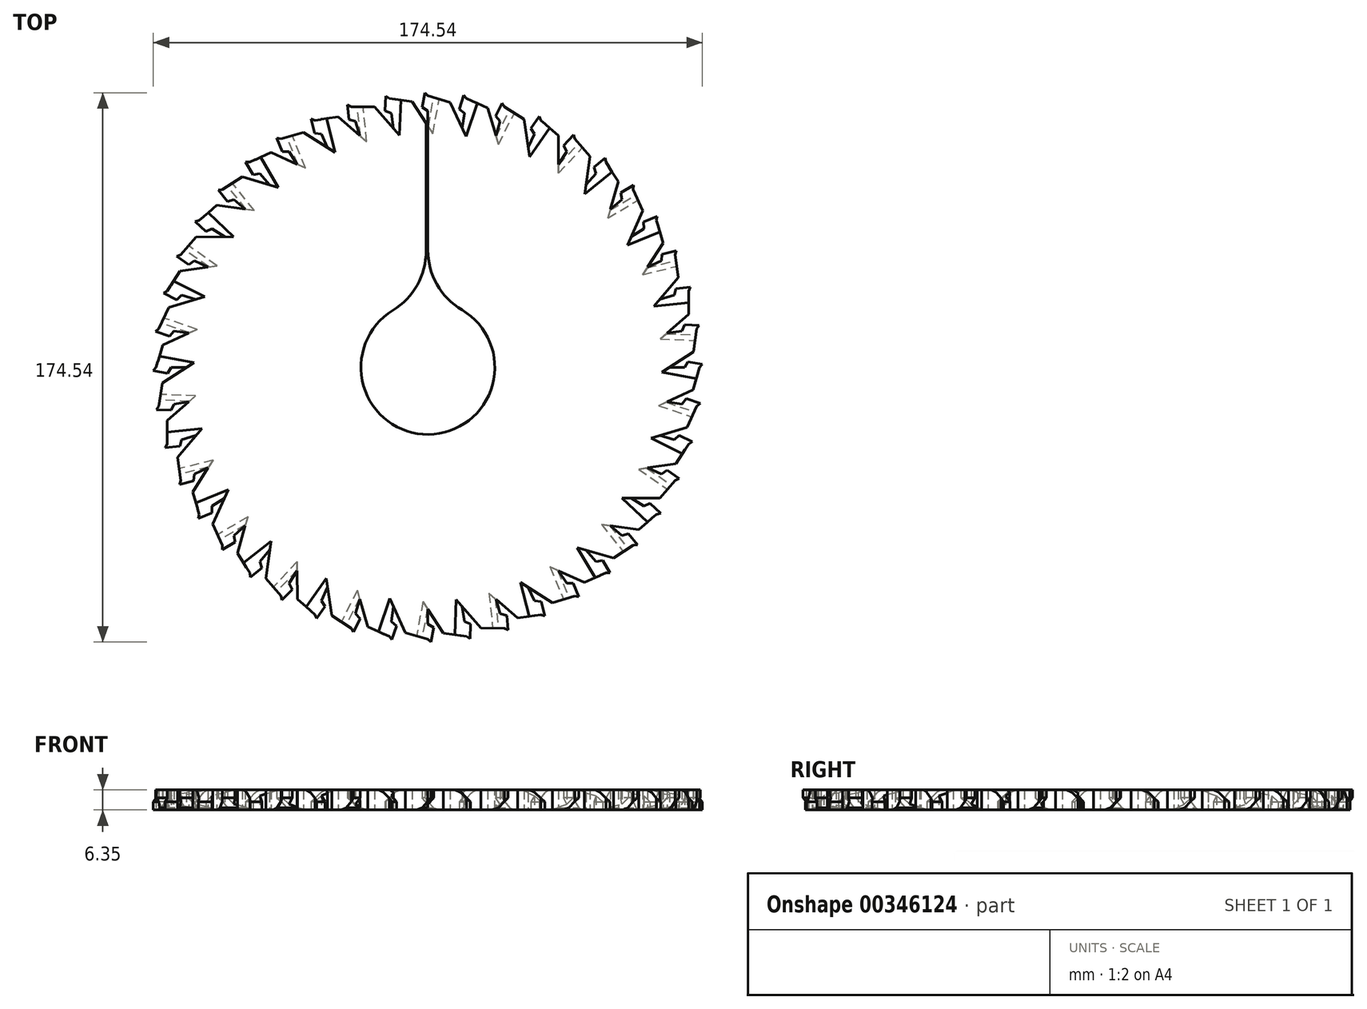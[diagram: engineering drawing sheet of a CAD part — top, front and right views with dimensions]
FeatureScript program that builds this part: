
annotation { "Feature Type Name" : "Feature", "Feature Type Description" : "" }
export const myFeature = defineFeature(function(context is Context, id is Id, definition is map)
    precondition{}
    {
        {
            var Q0;
            Q0=qCreatedBy(makeId("Top.planeOp"),FACE);
            var sketch = newSketch(context, id + "F0", { "sketchPlane" : qUnion([Q0])});
            skCircle(sketch, "E0", {"center": v(0, 0) * mm, "radius": 76.78 * mm});
            skLineSegment(sketch, "E1", {"start": v(0, 76.78) * mm, "end": v(0, 81.57) * mm});
            skLineSegment(sketch, "E2", {"start": v(0, 86.36) * mm, "end": v(7.12, 84.26) * mm});
            skLineSegment(sketch, "E3", {"start": v(7.12, 84.26) * mm, "end": v(10.93, 76) * mm});
            skLineSegment(sketch, "E4", {"start": v(0, 86.36) * mm, "end": v(-1, 87.27) * mm});
            skLineSegment(sketch, "E5", {"start": v(-1, 87.27) * mm, "end": v(-1.84, 82.68) * mm});
            skLineSegment(sketch, "E6", {"start": v(-1.84, 82.68) * mm, "end": v(0, 81.57) * mm});
            skLineSegment(sketch, "E7.1.0", {"start": v(-13.4, 86.24) * mm, "end": v(-13.59, 81.58) * mm});
            skLineSegment(sketch, "E7.1.1", {"start": v(-4.95, 84.41) * mm, "end": v(0, 76.78) * mm});
            skLineSegment(sketch, "E7.1.2", {"start": v(-12.3, 85.48) * mm, "end": v(-4.95, 84.41) * mm});
            skLineSegment(sketch, "E7.1.3", {"start": v(-10.93, 76) * mm, "end": v(-11.6, 80.74) * mm});
            skLineSegment(sketch, "E7.1.4", {"start": v(-13.59, 81.58) * mm, "end": v(-11.6, 80.74) * mm});
            skLineSegment(sketch, "E7.1.5", {"start": v(-12.3, 85.48) * mm, "end": v(-13.4, 86.24) * mm});
            skLineSegment(sketch, "E7.2.0", {"start": v(-25.54, 83.45) * mm, "end": v(-25.06, 78.81) * mm});
            skLineSegment(sketch, "E7.2.1", {"start": v(-16.91, 82.85) * mm, "end": v(-10.93, 76) * mm});
            skLineSegment(sketch, "E7.2.2", {"start": v(-24.33, 82.86) * mm, "end": v(-16.91, 82.85) * mm});
            skLineSegment(sketch, "E7.2.3", {"start": v(-21.63, 73.67) * mm, "end": v(-24.33, 82.86) * mm});
            skLineSegment(sketch, "E7.2.4", {"start": v(-25.06, 78.81) * mm, "end": v(-22.98, 78.27) * mm});
            skLineSegment(sketch, "E7.2.5", {"start": v(-24.33, 82.86) * mm, "end": v(-25.54, 83.45) * mm});
            skLineSegment(sketch, "E7.3.0", {"start": v(-37.15, 78.97) * mm, "end": v(-36.02, 74.45) * mm});
            skLineSegment(sketch, "E7.3.1", {"start": v(-28.53, 79.6) * mm, "end": v(-21.63, 73.67) * mm});
            skLineSegment(sketch, "E7.3.2", {"start": v(-35.88, 78.56) * mm, "end": v(-28.53, 79.6) * mm});
            skLineSegment(sketch, "E7.3.3", {"start": v(-31.9, 69.84) * mm, "end": v(-35.88, 78.56) * mm});
            skLineSegment(sketch, "E7.3.4", {"start": v(-36.02, 74.45) * mm, "end": v(-33.89, 74.2) * mm});
            skLineSegment(sketch, "E7.3.5", {"start": v(-35.88, 78.56) * mm, "end": v(-37.15, 78.97) * mm});
            skLineSegment(sketch, "E7.4.0", {"start": v(-48.01, 72.88) * mm, "end": v(-46.25, 68.56) * mm});
            skLineSegment(sketch, "E7.4.1", {"start": v(-39.57, 74.73) * mm, "end": v(-31.9, 69.84) * mm});
            skLineSegment(sketch, "E7.4.2", {"start": v(-46.7, 72.65) * mm, "end": v(-39.57, 74.73) * mm});
            skLineSegment(sketch, "E7.4.3", {"start": v(-41.51, 64.6) * mm, "end": v(-46.7, 72.65) * mm});
            skLineSegment(sketch, "E7.4.4", {"start": v(-46.25, 68.56) * mm, "end": v(-44.1, 68.62) * mm});
            skLineSegment(sketch, "E7.4.5", {"start": v(-46.7, 72.65) * mm, "end": v(-48.01, 72.88) * mm});
            skLineSegment(sketch, "E7.5.0", {"start": v(-57.9, 65.3) * mm, "end": v(-55.53, 61.28) * mm});
            skLineSegment(sketch, "E7.5.1", {"start": v(-49.8, 68.34) * mm, "end": v(-41.51, 64.6) * mm});
            skLineSegment(sketch, "E7.5.2", {"start": v(-56.55, 65.27) * mm, "end": v(-49.8, 68.34) * mm});
            skLineSegment(sketch, "E7.5.3", {"start": v(-50.28, 58.03) * mm, "end": v(-56.55, 65.27) * mm});
            skLineSegment(sketch, "E7.5.4", {"start": v(-55.53, 61.28) * mm, "end": v(-53.42, 61.65) * mm});
            skLineSegment(sketch, "E7.5.5", {"start": v(-56.55, 65.27) * mm, "end": v(-57.9, 65.3) * mm});
            skLineSegment(sketch, "E7.6.0", {"start": v(-66.6, 56.4) * mm, "end": v(-63.69, 52.76) * mm});
            skLineSegment(sketch, "E7.6.1", {"start": v(-59.02, 60.55) * mm, "end": v(-50.28, 58.03) * mm});
            skLineSegment(sketch, "E7.6.2", {"start": v(-65.27, 56.55) * mm, "end": v(-59.02, 60.55) * mm});
            skLineSegment(sketch, "E7.6.3", {"start": v(-58.03, 50.28) * mm, "end": v(-65.27, 56.55) * mm});
            skLineSegment(sketch, "E7.6.4", {"start": v(-63.69, 52.76) * mm, "end": v(-61.65, 53.42) * mm});
            skLineSegment(sketch, "E7.6.5", {"start": v(-65.27, 56.55) * mm, "end": v(-66.6, 56.4) * mm});
            skLineSegment(sketch, "E7.7.0", {"start": v(-73.95, 46.35) * mm, "end": v(-70.55, 43.16) * mm});
            skLineSegment(sketch, "E7.7.1", {"start": v(-67.04, 51.54) * mm, "end": v(-58.03, 50.28) * mm});
            skLineSegment(sketch, "E7.7.2", {"start": v(-72.65, 46.7) * mm, "end": v(-67.04, 51.54) * mm});
            skLineSegment(sketch, "E7.7.3", {"start": v(-64.6, 41.51) * mm, "end": v(-72.65, 46.7) * mm});
            skLineSegment(sketch, "E7.7.4", {"start": v(-70.55, 43.16) * mm, "end": v(-68.62, 44.1) * mm});
            skLineSegment(sketch, "E7.7.5", {"start": v(-72.65, 46.7) * mm, "end": v(-73.95, 46.35) * mm});
            skLineSegment(sketch, "E7.8.0", {"start": v(-79.8, 35.35) * mm, "end": v(-75.97, 32.68) * mm});
            skLineSegment(sketch, "E7.8.1", {"start": v(-73.69, 41.47) * mm, "end": v(-64.6, 41.51) * mm});
            skLineSegment(sketch, "E7.8.2", {"start": v(-78.56, 35.88) * mm, "end": v(-73.69, 41.47) * mm});
            skLineSegment(sketch, "E7.8.3", {"start": v(-69.84, 31.9) * mm, "end": v(-78.56, 35.88) * mm});
            skLineSegment(sketch, "E7.8.4", {"start": v(-75.97, 32.68) * mm, "end": v(-74.2, 33.89) * mm});
            skLineSegment(sketch, "E7.8.5", {"start": v(-78.56, 35.88) * mm, "end": v(-79.8, 35.35) * mm});
            skLineSegment(sketch, "E7.9.0", {"start": v(-84.01, 23.64) * mm, "end": v(-79.85, 21.53) * mm});
            skLineSegment(sketch, "E7.9.1", {"start": v(-78.84, 30.57) * mm, "end": v(-69.84, 31.9) * mm});
            skLineSegment(sketch, "E7.9.2", {"start": v(-82.86, 24.33) * mm, "end": v(-78.84, 30.57) * mm});
            skLineSegment(sketch, "E7.9.3", {"start": v(-73.67, 21.63) * mm, "end": v(-82.86, 24.33) * mm});
            skLineSegment(sketch, "E7.9.4", {"start": v(-79.85, 21.53) * mm, "end": v(-78.27, 22.98) * mm});
            skLineSegment(sketch, "E7.9.5", {"start": v(-82.86, 24.33) * mm, "end": v(-84.01, 23.64) * mm});
            skLineSegment(sketch, "E7.10.0", {"start": v(-86.52, 11.44) * mm, "end": v(-82.1, 9.95) * mm});
            skLineSegment(sketch, "E7.10.1", {"start": v(-82.39, 19.03) * mm, "end": v(-73.67, 21.63) * mm});
            skLineSegment(sketch, "E7.10.2", {"start": v(-85.48, 12.3) * mm, "end": v(-82.39, 19.03) * mm});
            skLineSegment(sketch, "E7.10.3", {"start": v(-76, 10.93) * mm, "end": v(-85.48, 12.3) * mm});
            skLineSegment(sketch, "E7.10.4", {"start": v(-82.1, 9.95) * mm, "end": v(-80.74, 11.6) * mm});
            skLineSegment(sketch, "E7.10.5", {"start": v(-85.48, 12.3) * mm, "end": v(-86.52, 11.44) * mm});
            skLineSegment(sketch, "E7.11.0", {"start": v(-87.27, -1) * mm, "end": v(-82.68, -1.84) * mm});
            skLineSegment(sketch, "E7.11.1", {"start": v(-84.26, 7.12) * mm, "end": v(-76, 10.93) * mm});
            skLineSegment(sketch, "E7.11.2", {"start": v(-86.36, 0) * mm, "end": v(-84.26, 7.12) * mm});
            skLineSegment(sketch, "E7.11.3", {"start": v(-76.78, 0) * mm, "end": v(-86.36, 0) * mm});
            skLineSegment(sketch, "E7.11.4", {"start": v(-82.68, -1.84) * mm, "end": v(-81.57, 0) * mm});
            skLineSegment(sketch, "E7.11.5", {"start": v(-86.36, 0) * mm, "end": v(-87.27, -1) * mm});
            skLineSegment(sketch, "E7.12.0", {"start": v(-86.24, -13.4) * mm, "end": v(-81.58, -13.59) * mm});
            skLineSegment(sketch, "E7.12.1", {"start": v(-84.41, -4.95) * mm, "end": v(-76.78, 0) * mm});
            skLineSegment(sketch, "E7.12.2", {"start": v(-85.48, -12.3) * mm, "end": v(-84.41, -4.95) * mm});
            skLineSegment(sketch, "E7.12.3", {"start": v(-76, -10.93) * mm, "end": v(-85.48, -12.3) * mm});
            skLineSegment(sketch, "E7.12.4", {"start": v(-81.58, -13.59) * mm, "end": v(-80.74, -11.6) * mm});
            skLineSegment(sketch, "E7.12.5", {"start": v(-85.48, -12.3) * mm, "end": v(-86.24, -13.4) * mm});
            skLineSegment(sketch, "E7.13.0", {"start": v(-83.45, -25.54) * mm, "end": v(-78.81, -25.06) * mm});
            skLineSegment(sketch, "E7.13.1", {"start": v(-82.85, -16.91) * mm, "end": v(-76, -10.93) * mm});
            skLineSegment(sketch, "E7.13.2", {"start": v(-82.86, -24.33) * mm, "end": v(-82.85, -16.91) * mm});
            skLineSegment(sketch, "E7.13.3", {"start": v(-73.67, -21.63) * mm, "end": v(-82.86, -24.33) * mm});
            skLineSegment(sketch, "E7.13.4", {"start": v(-78.81, -25.06) * mm, "end": v(-78.27, -22.98) * mm});
            skLineSegment(sketch, "E7.13.5", {"start": v(-82.86, -24.33) * mm, "end": v(-83.45, -25.54) * mm});
            skLineSegment(sketch, "E7.14.0", {"start": v(-78.97, -37.15) * mm, "end": v(-74.45, -36.02) * mm});
            skLineSegment(sketch, "E7.14.1", {"start": v(-79.6, -28.53) * mm, "end": v(-73.67, -21.63) * mm});
            skLineSegment(sketch, "E7.14.2", {"start": v(-78.56, -35.88) * mm, "end": v(-79.6, -28.53) * mm});
            skLineSegment(sketch, "E7.14.3", {"start": v(-69.84, -31.9) * mm, "end": v(-78.56, -35.88) * mm});
            skLineSegment(sketch, "E7.14.4", {"start": v(-74.45, -36.02) * mm, "end": v(-74.2, -33.89) * mm});
            skLineSegment(sketch, "E7.14.5", {"start": v(-78.56, -35.88) * mm, "end": v(-78.97, -37.15) * mm});
            skLineSegment(sketch, "E7.15.0", {"start": v(-72.88, -48.01) * mm, "end": v(-68.56, -46.25) * mm});
            skLineSegment(sketch, "E7.15.1", {"start": v(-74.73, -39.57) * mm, "end": v(-69.84, -31.9) * mm});
            skLineSegment(sketch, "E7.15.2", {"start": v(-72.65, -46.7) * mm, "end": v(-74.73, -39.57) * mm});
            skLineSegment(sketch, "E7.15.3", {"start": v(-64.6, -41.51) * mm, "end": v(-72.65, -46.7) * mm});
            skLineSegment(sketch, "E7.15.4", {"start": v(-68.56, -46.25) * mm, "end": v(-68.62, -44.1) * mm});
            skLineSegment(sketch, "E7.15.5", {"start": v(-72.65, -46.7) * mm, "end": v(-72.88, -48.01) * mm});
            skLineSegment(sketch, "E7.16.0", {"start": v(-65.3, -57.9) * mm, "end": v(-61.28, -55.53) * mm});
            skLineSegment(sketch, "E7.16.1", {"start": v(-68.34, -49.8) * mm, "end": v(-64.6, -41.51) * mm});
            skLineSegment(sketch, "E7.16.2", {"start": v(-65.27, -56.55) * mm, "end": v(-68.34, -49.8) * mm});
            skLineSegment(sketch, "E7.16.3", {"start": v(-58.03, -50.28) * mm, "end": v(-65.27, -56.55) * mm});
            skLineSegment(sketch, "E7.16.4", {"start": v(-61.28, -55.53) * mm, "end": v(-61.65, -53.42) * mm});
            skLineSegment(sketch, "E7.16.5", {"start": v(-65.27, -56.55) * mm, "end": v(-65.3, -57.9) * mm});
            skLineSegment(sketch, "E7.17.0", {"start": v(-56.4, -66.6) * mm, "end": v(-52.76, -63.69) * mm});
            skLineSegment(sketch, "E7.17.1", {"start": v(-60.55, -59.02) * mm, "end": v(-58.03, -50.28) * mm});
            skLineSegment(sketch, "E7.17.2", {"start": v(-56.55, -65.27) * mm, "end": v(-60.55, -59.02) * mm});
            skLineSegment(sketch, "E7.17.3", {"start": v(-50.28, -58.03) * mm, "end": v(-56.55, -65.27) * mm});
            skLineSegment(sketch, "E7.17.4", {"start": v(-52.76, -63.69) * mm, "end": v(-53.42, -61.65) * mm});
            skLineSegment(sketch, "E7.17.5", {"start": v(-56.55, -65.27) * mm, "end": v(-56.4, -66.6) * mm});
            skLineSegment(sketch, "E7.18.0", {"start": v(-46.35, -73.95) * mm, "end": v(-43.16, -70.55) * mm});
            skLineSegment(sketch, "E7.18.1", {"start": v(-51.54, -67.04) * mm, "end": v(-50.28, -58.03) * mm});
            skLineSegment(sketch, "E7.18.2", {"start": v(-46.7, -72.65) * mm, "end": v(-51.54, -67.04) * mm});
            skLineSegment(sketch, "E7.18.3", {"start": v(-41.51, -64.6) * mm, "end": v(-46.7, -72.65) * mm});
            skLineSegment(sketch, "E7.18.4", {"start": v(-43.16, -70.55) * mm, "end": v(-44.1, -68.62) * mm});
            skLineSegment(sketch, "E7.18.5", {"start": v(-46.7, -72.65) * mm, "end": v(-46.35, -73.95) * mm});
            skLineSegment(sketch, "E7.19.0", {"start": v(-35.35, -79.8) * mm, "end": v(-32.68, -75.97) * mm});
            skLineSegment(sketch, "E7.19.1", {"start": v(-41.47, -73.69) * mm, "end": v(-41.51, -64.6) * mm});
            skLineSegment(sketch, "E7.19.2", {"start": v(-35.88, -78.56) * mm, "end": v(-41.47, -73.69) * mm});
            skLineSegment(sketch, "E7.19.3", {"start": v(-31.9, -69.84) * mm, "end": v(-35.88, -78.56) * mm});
            skLineSegment(sketch, "E7.19.4", {"start": v(-32.68, -75.97) * mm, "end": v(-33.89, -74.2) * mm});
            skLineSegment(sketch, "E7.19.5", {"start": v(-35.88, -78.56) * mm, "end": v(-35.35, -79.8) * mm});
            skLineSegment(sketch, "E7.20.0", {"start": v(-23.64, -84.01) * mm, "end": v(-21.53, -79.85) * mm});
            skLineSegment(sketch, "E7.20.1", {"start": v(-30.57, -78.84) * mm, "end": v(-31.9, -69.84) * mm});
            skLineSegment(sketch, "E7.20.2", {"start": v(-24.33, -82.86) * mm, "end": v(-30.57, -78.84) * mm});
            skLineSegment(sketch, "E7.20.3", {"start": v(-21.63, -73.67) * mm, "end": v(-24.33, -82.86) * mm});
            skLineSegment(sketch, "E7.20.4", {"start": v(-21.53, -79.85) * mm, "end": v(-22.98, -78.27) * mm});
            skLineSegment(sketch, "E7.20.5", {"start": v(-24.33, -82.86) * mm, "end": v(-23.64, -84.01) * mm});
            skLineSegment(sketch, "E7.21.0", {"start": v(-11.44, -86.52) * mm, "end": v(-9.95, -82.1) * mm});
            skLineSegment(sketch, "E7.21.1", {"start": v(-19.03, -82.39) * mm, "end": v(-21.63, -73.67) * mm});
            skLineSegment(sketch, "E7.21.2", {"start": v(-12.3, -85.48) * mm, "end": v(-19.03, -82.39) * mm});
            skLineSegment(sketch, "E7.21.3", {"start": v(-10.93, -76) * mm, "end": v(-12.3, -85.48) * mm});
            skLineSegment(sketch, "E7.21.4", {"start": v(-9.95, -82.1) * mm, "end": v(-11.6, -80.74) * mm});
            skLineSegment(sketch, "E7.21.5", {"start": v(-12.3, -85.48) * mm, "end": v(-11.44, -86.52) * mm});
            skLineSegment(sketch, "E7.22.0", {"start": v(1, -87.27) * mm, "end": v(1.84, -82.68) * mm});
            skLineSegment(sketch, "E7.22.1", {"start": v(-7.12, -84.26) * mm, "end": v(-10.93, -76) * mm});
            skLineSegment(sketch, "E7.22.2", {"start": v(0, -86.36) * mm, "end": v(-7.12, -84.26) * mm});
            skLineSegment(sketch, "E7.22.3", {"start": v(0, -76.78) * mm, "end": v(0, -86.36) * mm});
            skLineSegment(sketch, "E7.22.4", {"start": v(1.84, -82.68) * mm, "end": v(0, -81.57) * mm});
            skLineSegment(sketch, "E7.22.5", {"start": v(0, -86.36) * mm, "end": v(1, -87.27) * mm});
            skLineSegment(sketch, "E7.23.0", {"start": v(13.4, -86.24) * mm, "end": v(13.59, -81.58) * mm});
            skLineSegment(sketch, "E7.23.1", {"start": v(4.95, -84.41) * mm, "end": v(0, -76.78) * mm});
            skLineSegment(sketch, "E7.23.2", {"start": v(12.3, -85.48) * mm, "end": v(4.95, -84.41) * mm});
            skLineSegment(sketch, "E7.23.3", {"start": v(10.93, -76) * mm, "end": v(12.3, -85.48) * mm});
            skLineSegment(sketch, "E7.23.4", {"start": v(13.59, -81.58) * mm, "end": v(11.6, -80.74) * mm});
            skLineSegment(sketch, "E7.23.5", {"start": v(12.3, -85.48) * mm, "end": v(13.4, -86.24) * mm});
            skLineSegment(sketch, "E7.24.0", {"start": v(25.54, -83.45) * mm, "end": v(25.06, -78.81) * mm});
            skLineSegment(sketch, "E7.24.1", {"start": v(16.91, -82.85) * mm, "end": v(10.93, -76) * mm});
            skLineSegment(sketch, "E7.24.2", {"start": v(24.33, -82.86) * mm, "end": v(16.91, -82.85) * mm});
            skLineSegment(sketch, "E7.24.3", {"start": v(21.63, -73.67) * mm, "end": v(24.33, -82.86) * mm});
            skLineSegment(sketch, "E7.24.4", {"start": v(25.06, -78.81) * mm, "end": v(22.98, -78.27) * mm});
            skLineSegment(sketch, "E7.24.5", {"start": v(24.33, -82.86) * mm, "end": v(25.54, -83.45) * mm});
            skLineSegment(sketch, "E7.25.0", {"start": v(37.15, -78.97) * mm, "end": v(36.02, -74.45) * mm});
            skLineSegment(sketch, "E7.25.1", {"start": v(28.53, -79.6) * mm, "end": v(21.63, -73.67) * mm});
            skLineSegment(sketch, "E7.25.2", {"start": v(35.88, -78.56) * mm, "end": v(28.53, -79.6) * mm});
            skLineSegment(sketch, "E7.25.3", {"start": v(31.9, -69.84) * mm, "end": v(35.88, -78.56) * mm});
            skLineSegment(sketch, "E7.25.4", {"start": v(36.02, -74.45) * mm, "end": v(33.89, -74.2) * mm});
            skLineSegment(sketch, "E7.25.5", {"start": v(35.88, -78.56) * mm, "end": v(37.15, -78.97) * mm});
            skLineSegment(sketch, "E7.26.0", {"start": v(48.01, -72.88) * mm, "end": v(46.25, -68.56) * mm});
            skLineSegment(sketch, "E7.26.1", {"start": v(39.57, -74.73) * mm, "end": v(31.9, -69.84) * mm});
            skLineSegment(sketch, "E7.26.2", {"start": v(46.7, -72.65) * mm, "end": v(39.57, -74.73) * mm});
            skLineSegment(sketch, "E7.26.3", {"start": v(41.51, -64.6) * mm, "end": v(46.7, -72.65) * mm});
            skLineSegment(sketch, "E7.26.4", {"start": v(46.25, -68.56) * mm, "end": v(44.1, -68.62) * mm});
            skLineSegment(sketch, "E7.26.5", {"start": v(46.7, -72.65) * mm, "end": v(48.01, -72.88) * mm});
            skLineSegment(sketch, "E7.27.0", {"start": v(57.9, -65.3) * mm, "end": v(55.53, -61.28) * mm});
            skLineSegment(sketch, "E7.27.1", {"start": v(49.8, -68.34) * mm, "end": v(41.51, -64.6) * mm});
            skLineSegment(sketch, "E7.27.2", {"start": v(56.55, -65.27) * mm, "end": v(49.8, -68.34) * mm});
            skLineSegment(sketch, "E7.27.3", {"start": v(50.28, -58.03) * mm, "end": v(56.55, -65.27) * mm});
            skLineSegment(sketch, "E7.27.4", {"start": v(55.53, -61.28) * mm, "end": v(53.42, -61.65) * mm});
            skLineSegment(sketch, "E7.27.5", {"start": v(56.55, -65.27) * mm, "end": v(57.9, -65.3) * mm});
            skLineSegment(sketch, "E7.28.0", {"start": v(66.6, -56.4) * mm, "end": v(63.69, -52.76) * mm});
            skLineSegment(sketch, "E7.28.1", {"start": v(59.02, -60.55) * mm, "end": v(50.28, -58.03) * mm});
            skLineSegment(sketch, "E7.28.2", {"start": v(65.27, -56.55) * mm, "end": v(59.02, -60.55) * mm});
            skLineSegment(sketch, "E7.28.3", {"start": v(58.03, -50.28) * mm, "end": v(65.27, -56.55) * mm});
            skLineSegment(sketch, "E7.28.4", {"start": v(63.69, -52.76) * mm, "end": v(61.65, -53.42) * mm});
            skLineSegment(sketch, "E7.28.5", {"start": v(65.27, -56.55) * mm, "end": v(66.6, -56.4) * mm});
            skLineSegment(sketch, "E7.29.0", {"start": v(73.95, -46.35) * mm, "end": v(70.55, -43.16) * mm});
            skLineSegment(sketch, "E7.29.1", {"start": v(67.04, -51.54) * mm, "end": v(58.03, -50.28) * mm});
            skLineSegment(sketch, "E7.29.2", {"start": v(72.65, -46.7) * mm, "end": v(67.04, -51.54) * mm});
            skLineSegment(sketch, "E7.29.3", {"start": v(64.6, -41.51) * mm, "end": v(72.65, -46.7) * mm});
            skLineSegment(sketch, "E7.29.4", {"start": v(70.55, -43.16) * mm, "end": v(68.62, -44.1) * mm});
            skLineSegment(sketch, "E7.29.5", {"start": v(72.65, -46.7) * mm, "end": v(73.95, -46.35) * mm});
            skLineSegment(sketch, "E7.30.0", {"start": v(79.8, -35.35) * mm, "end": v(75.97, -32.68) * mm});
            skLineSegment(sketch, "E7.30.1", {"start": v(73.69, -41.47) * mm, "end": v(64.6, -41.51) * mm});
            skLineSegment(sketch, "E7.30.2", {"start": v(78.56, -35.88) * mm, "end": v(73.69, -41.47) * mm});
            skLineSegment(sketch, "E7.30.3", {"start": v(69.84, -31.9) * mm, "end": v(78.56, -35.88) * mm});
            skLineSegment(sketch, "E7.30.4", {"start": v(75.97, -32.68) * mm, "end": v(74.2, -33.89) * mm});
            skLineSegment(sketch, "E7.30.5", {"start": v(78.56, -35.88) * mm, "end": v(79.8, -35.35) * mm});
            skLineSegment(sketch, "E7.31.0", {"start": v(84.01, -23.64) * mm, "end": v(79.85, -21.53) * mm});
            skLineSegment(sketch, "E7.31.1", {"start": v(78.84, -30.57) * mm, "end": v(69.84, -31.9) * mm});
            skLineSegment(sketch, "E7.31.2", {"start": v(82.86, -24.33) * mm, "end": v(78.84, -30.57) * mm});
            skLineSegment(sketch, "E7.31.3", {"start": v(73.67, -21.63) * mm, "end": v(82.86, -24.33) * mm});
            skLineSegment(sketch, "E7.31.4", {"start": v(79.85, -21.53) * mm, "end": v(78.27, -22.98) * mm});
            skLineSegment(sketch, "E7.31.5", {"start": v(82.86, -24.33) * mm, "end": v(84.01, -23.64) * mm});
            skLineSegment(sketch, "E7.32.0", {"start": v(86.52, -11.44) * mm, "end": v(82.1, -9.95) * mm});
            skLineSegment(sketch, "E7.32.1", {"start": v(82.39, -19.03) * mm, "end": v(73.67, -21.63) * mm});
            skLineSegment(sketch, "E7.32.2", {"start": v(85.48, -12.3) * mm, "end": v(82.39, -19.03) * mm});
            skLineSegment(sketch, "E7.32.3", {"start": v(76, -10.93) * mm, "end": v(85.48, -12.3) * mm});
            skLineSegment(sketch, "E7.32.4", {"start": v(82.1, -9.95) * mm, "end": v(80.74, -11.6) * mm});
            skLineSegment(sketch, "E7.32.5", {"start": v(85.48, -12.3) * mm, "end": v(86.52, -11.44) * mm});
            skLineSegment(sketch, "E7.33.0", {"start": v(87.27, 1) * mm, "end": v(82.68, 1.84) * mm});
            skLineSegment(sketch, "E7.33.1", {"start": v(84.26, -7.12) * mm, "end": v(76, -10.93) * mm});
            skLineSegment(sketch, "E7.33.2", {"start": v(86.36, 0) * mm, "end": v(84.26, -7.12) * mm});
            skLineSegment(sketch, "E7.33.3", {"start": v(76.78, 0) * mm, "end": v(86.36, 0) * mm});
            skLineSegment(sketch, "E7.33.4", {"start": v(82.68, 1.84) * mm, "end": v(81.57, 0) * mm});
            skLineSegment(sketch, "E7.33.5", {"start": v(86.36, 0) * mm, "end": v(87.27, 1) * mm});
            skLineSegment(sketch, "E7.34.0", {"start": v(86.24, 13.4) * mm, "end": v(81.58, 13.59) * mm});
            skLineSegment(sketch, "E7.34.1", {"start": v(84.41, 4.95) * mm, "end": v(76.78, 0) * mm});
            skLineSegment(sketch, "E7.34.2", {"start": v(85.48, 12.3) * mm, "end": v(84.41, 4.95) * mm});
            skLineSegment(sketch, "E7.34.3", {"start": v(76, 10.93) * mm, "end": v(85.48, 12.3) * mm});
            skLineSegment(sketch, "E7.34.4", {"start": v(81.58, 13.59) * mm, "end": v(80.74, 11.6) * mm});
            skLineSegment(sketch, "E7.34.5", {"start": v(85.48, 12.3) * mm, "end": v(86.24, 13.4) * mm});
            skLineSegment(sketch, "E7.35.0", {"start": v(83.45, 25.54) * mm, "end": v(78.81, 25.06) * mm});
            skLineSegment(sketch, "E7.35.1", {"start": v(82.85, 16.91) * mm, "end": v(76, 10.93) * mm});
            skLineSegment(sketch, "E7.35.2", {"start": v(82.86, 24.33) * mm, "end": v(82.85, 16.91) * mm});
            skLineSegment(sketch, "E7.35.3", {"start": v(73.67, 21.63) * mm, "end": v(82.86, 24.33) * mm});
            skLineSegment(sketch, "E7.35.4", {"start": v(78.81, 25.06) * mm, "end": v(78.27, 22.98) * mm});
            skLineSegment(sketch, "E7.35.5", {"start": v(82.86, 24.33) * mm, "end": v(83.45, 25.54) * mm});
            skLineSegment(sketch, "E7.36.0", {"start": v(78.97, 37.15) * mm, "end": v(74.45, 36.02) * mm});
            skLineSegment(sketch, "E7.36.1", {"start": v(79.6, 28.53) * mm, "end": v(73.67, 21.63) * mm});
            skLineSegment(sketch, "E7.36.2", {"start": v(78.56, 35.88) * mm, "end": v(79.6, 28.53) * mm});
            skLineSegment(sketch, "E7.36.3", {"start": v(69.84, 31.9) * mm, "end": v(78.56, 35.88) * mm});
            skLineSegment(sketch, "E7.36.4", {"start": v(74.45, 36.02) * mm, "end": v(74.2, 33.89) * mm});
            skLineSegment(sketch, "E7.36.5", {"start": v(78.56, 35.88) * mm, "end": v(78.97, 37.15) * mm});
            skLineSegment(sketch, "E7.37.0", {"start": v(72.88, 48.01) * mm, "end": v(68.56, 46.25) * mm});
            skLineSegment(sketch, "E7.37.1", {"start": v(74.73, 39.57) * mm, "end": v(69.84, 31.9) * mm});
            skLineSegment(sketch, "E7.37.2", {"start": v(72.65, 46.7) * mm, "end": v(74.73, 39.57) * mm});
            skLineSegment(sketch, "E7.37.3", {"start": v(64.6, 41.51) * mm, "end": v(72.65, 46.7) * mm});
            skLineSegment(sketch, "E7.37.4", {"start": v(68.56, 46.25) * mm, "end": v(68.62, 44.1) * mm});
            skLineSegment(sketch, "E7.37.5", {"start": v(72.65, 46.7) * mm, "end": v(72.88, 48.01) * mm});
            skLineSegment(sketch, "E7.38.0", {"start": v(65.3, 57.9) * mm, "end": v(61.28, 55.53) * mm});
            skLineSegment(sketch, "E7.38.1", {"start": v(68.34, 49.8) * mm, "end": v(64.6, 41.51) * mm});
            skLineSegment(sketch, "E7.38.2", {"start": v(65.27, 56.55) * mm, "end": v(68.34, 49.8) * mm});
            skLineSegment(sketch, "E7.38.3", {"start": v(58.03, 50.28) * mm, "end": v(65.27, 56.55) * mm});
            skLineSegment(sketch, "E7.38.4", {"start": v(61.28, 55.53) * mm, "end": v(61.65, 53.42) * mm});
            skLineSegment(sketch, "E7.38.5", {"start": v(65.27, 56.55) * mm, "end": v(65.3, 57.9) * mm});
            skLineSegment(sketch, "E7.39.0", {"start": v(56.4, 66.6) * mm, "end": v(52.76, 63.69) * mm});
            skLineSegment(sketch, "E7.39.1", {"start": v(60.55, 59.02) * mm, "end": v(58.03, 50.28) * mm});
            skLineSegment(sketch, "E7.39.2", {"start": v(56.55, 65.27) * mm, "end": v(60.55, 59.02) * mm});
            skLineSegment(sketch, "E7.39.3", {"start": v(50.28, 58.03) * mm, "end": v(56.55, 65.27) * mm});
            skLineSegment(sketch, "E7.39.4", {"start": v(52.76, 63.69) * mm, "end": v(53.42, 61.65) * mm});
            skLineSegment(sketch, "E7.39.5", {"start": v(56.55, 65.27) * mm, "end": v(56.4, 66.6) * mm});
            skLineSegment(sketch, "E7.40.0", {"start": v(46.35, 73.95) * mm, "end": v(43.16, 70.55) * mm});
            skLineSegment(sketch, "E7.40.1", {"start": v(51.54, 67.04) * mm, "end": v(50.28, 58.03) * mm});
            skLineSegment(sketch, "E7.40.2", {"start": v(46.7, 72.65) * mm, "end": v(51.54, 67.04) * mm});
            skLineSegment(sketch, "E7.40.3", {"start": v(41.51, 64.6) * mm, "end": v(46.7, 72.65) * mm});
            skLineSegment(sketch, "E7.40.4", {"start": v(43.16, 70.55) * mm, "end": v(44.1, 68.62) * mm});
            skLineSegment(sketch, "E7.40.5", {"start": v(46.7, 72.65) * mm, "end": v(46.35, 73.95) * mm});
            skLineSegment(sketch, "E7.41.0", {"start": v(35.35, 79.8) * mm, "end": v(32.68, 75.97) * mm});
            skLineSegment(sketch, "E7.41.1", {"start": v(41.47, 73.69) * mm, "end": v(41.51, 64.6) * mm});
            skLineSegment(sketch, "E7.41.2", {"start": v(35.88, 78.56) * mm, "end": v(41.47, 73.69) * mm});
            skLineSegment(sketch, "E7.41.3", {"start": v(31.9, 69.84) * mm, "end": v(35.88, 78.56) * mm});
            skLineSegment(sketch, "E7.41.4", {"start": v(32.68, 75.97) * mm, "end": v(33.89, 74.2) * mm});
            skLineSegment(sketch, "E7.41.5", {"start": v(35.88, 78.56) * mm, "end": v(35.35, 79.8) * mm});
            skLineSegment(sketch, "E7.42.0", {"start": v(23.64, 84.01) * mm, "end": v(21.53, 79.85) * mm});
            skLineSegment(sketch, "E7.42.1", {"start": v(30.57, 78.84) * mm, "end": v(31.9, 69.84) * mm});
            skLineSegment(sketch, "E7.42.2", {"start": v(24.33, 82.86) * mm, "end": v(30.57, 78.84) * mm});
            skLineSegment(sketch, "E7.42.3", {"start": v(21.63, 73.67) * mm, "end": v(24.33, 82.86) * mm});
            skLineSegment(sketch, "E7.42.4", {"start": v(21.53, 79.85) * mm, "end": v(22.98, 78.27) * mm});
            skLineSegment(sketch, "E7.42.5", {"start": v(24.33, 82.86) * mm, "end": v(23.64, 84.01) * mm});
            skLineSegment(sketch, "E7.43.0", {"start": v(11.44, 86.52) * mm, "end": v(9.95, 82.1) * mm});
            skLineSegment(sketch, "E7.43.1", {"start": v(19.03, 82.39) * mm, "end": v(21.63, 73.67) * mm});
            skLineSegment(sketch, "E7.43.2", {"start": v(12.3, 85.48) * mm, "end": v(19.03, 82.39) * mm});
            skLineSegment(sketch, "E7.43.3", {"start": v(10.93, 76) * mm, "end": v(12.3, 85.48) * mm});
            skLineSegment(sketch, "E7.43.4", {"start": v(9.95, 82.1) * mm, "end": v(11.6, 80.74) * mm});
            skLineSegment(sketch, "E7.43.5", {"start": v(12.3, 85.48) * mm, "end": v(11.44, 86.52) * mm});
            skSolve(sketch);
        }
        {
            var Q0;
            Q0 = qSketchRegion(id + "F0", true);
            extrude(context, id + "F1", {"entities" : qUnion([Q0]), "depth" : 6.35 * mm});
        }
        {
            var Q0;
            Q0=makeQuery(id+"F1.opExtrude","CAP_EDGE",EDGE,{"disambiguationData":[OSD([sQuery(id+"F0.wireOp",EDGE,"E7.39.0")])],"isStart":false});
            var Q1;
            Q1=makeQuery(id+"F1.opExtrude","CAP_EDGE",EDGE,{"disambiguationData":[OSD([sQuery(id+"F0.wireOp",EDGE,"E7.41.0")])],"isStart":false});
            var Q2;
            Q2=makeQuery(id+"F1.opExtrude","CAP_EDGE",EDGE,{"disambiguationData":[OSD([sQuery(id+"F0.wireOp",EDGE,"E7.43.0")])],"isStart":false});
            var Q3;
            Q3=makeQuery(id+"F1.opExtrude","CAP_EDGE",EDGE,{"disambiguationData":[OSD([sQuery(id+"F0.wireOp",EDGE,"E7.1.0")])],"isStart":false});
            var Q4;
            Q4=makeQuery(id+"F1.opExtrude","CAP_EDGE",EDGE,{"disambiguationData":[OSD([sQuery(id+"F0.wireOp",EDGE,"E7.3.0")])],"isStart":false});
            var Q5;
            Q5=makeQuery(id+"F1.opExtrude","CAP_EDGE",EDGE,{"disambiguationData":[OSD([sQuery(id+"F0.wireOp",EDGE,"E7.5.0")])],"isStart":false});
            var Q6;
            Q6=makeQuery(id+"F1.opExtrude","CAP_EDGE",EDGE,{"disambiguationData":[OSD([sQuery(id+"F0.wireOp",EDGE,"E7.7.0")])],"isStart":false});
            var Q7;
            Q7=makeQuery(id+"F1.opExtrude","CAP_EDGE",EDGE,{"disambiguationData":[OSD([sQuery(id+"F0.wireOp",EDGE,"E7.9.0")])],"isStart":false});
            var Q8;
            Q8=makeQuery(id+"F1.opExtrude","CAP_EDGE",EDGE,{"disambiguationData":[OSD([sQuery(id+"F0.wireOp",EDGE,"E7.11.0")])],"isStart":false});
            var Q9;
            Q9=makeQuery(id+"F1.opExtrude","CAP_EDGE",EDGE,{"disambiguationData":[OSD([sQuery(id+"F0.wireOp",EDGE,"E7.13.0")])],"isStart":false});
            var Q10;
            Q10=makeQuery(id+"F1.opExtrude","CAP_EDGE",EDGE,{"disambiguationData":[OSD([sQuery(id+"F0.wireOp",EDGE,"E7.15.0")])],"isStart":false});
            var Q11;
            Q11=makeQuery(id+"F1.opExtrude","CAP_EDGE",EDGE,{"disambiguationData":[OSD([sQuery(id+"F0.wireOp",EDGE,"E7.17.0")])],"isStart":false});
            var Q12;
            Q12=makeQuery(id+"F1.opExtrude","CAP_EDGE",EDGE,{"disambiguationData":[OSD([sQuery(id+"F0.wireOp",EDGE,"E7.19.0")])],"isStart":false});
            var Q13;
            Q13=makeQuery(id+"F1.opExtrude","CAP_EDGE",EDGE,{"disambiguationData":[OSD([sQuery(id+"F0.wireOp",EDGE,"E7.21.0")])],"isStart":false});
            var Q14;
            Q14=makeQuery(id+"F1.opExtrude","CAP_EDGE",EDGE,{"disambiguationData":[OSD([sQuery(id+"F0.wireOp",EDGE,"E7.23.0")])],"isStart":false});
            var Q15;
            Q15=makeQuery(id+"F1.opExtrude","CAP_EDGE",EDGE,{"disambiguationData":[OSD([sQuery(id+"F0.wireOp",EDGE,"E7.25.0")])],"isStart":false});
            var Q16;
            Q16=makeQuery(id+"F1.opExtrude","CAP_EDGE",EDGE,{"disambiguationData":[OSD([sQuery(id+"F0.wireOp",EDGE,"E7.27.0")])],"isStart":false});
            var Q17;
            Q17=makeQuery(id+"F1.opExtrude","CAP_EDGE",EDGE,{"disambiguationData":[OSD([sQuery(id+"F0.wireOp",EDGE,"E7.29.0")])],"isStart":false});
            var Q18;
            Q18=makeQuery(id+"F1.opExtrude","CAP_EDGE",EDGE,{"disambiguationData":[OSD([sQuery(id+"F0.wireOp",EDGE,"E7.31.0")])],"isStart":false});
            var Q19;
            Q19=makeQuery(id+"F1.opExtrude","CAP_EDGE",EDGE,{"disambiguationData":[OSD([sQuery(id+"F0.wireOp",EDGE,"E7.33.0")])],"isStart":false});
            var Q20;
            Q20=makeQuery(id+"F1.opExtrude","CAP_EDGE",EDGE,{"disambiguationData":[OSD([sQuery(id+"F0.wireOp",EDGE,"E7.35.0")])],"isStart":false});
            var Q21;
            Q21=makeQuery(id+"F1.opExtrude","CAP_EDGE",EDGE,{"disambiguationData":[OSD([sQuery(id+"F0.wireOp",EDGE,"E7.37.0")])],"isStart":false});
            var Q22;
            Q22=makeQuery(id+"F1.opExtrude","CAP_EDGE",EDGE,{"disambiguationData":[OSD([sQuery(id+"F0.wireOp",EDGE,"E7.22.0")])],"isStart":true});
            var Q23;
            Q23=makeQuery(id+"F1.opExtrude","CAP_EDGE",EDGE,{"disambiguationData":[OSD([sQuery(id+"F0.wireOp",EDGE,"E7.20.0")])],"isStart":true});
            var Q24;
            Q24=makeQuery(id+"F1.opExtrude","CAP_EDGE",EDGE,{"disambiguationData":[OSD([sQuery(id+"F0.wireOp",EDGE,"E7.18.0")])],"isStart":true});
            var Q25;
            Q25=makeQuery(id+"F1.opExtrude","CAP_EDGE",EDGE,{"disambiguationData":[OSD([sQuery(id+"F0.wireOp",EDGE,"E7.16.0")])],"isStart":true});
            var Q26;
            Q26=makeQuery(id+"F1.opExtrude","CAP_EDGE",EDGE,{"disambiguationData":[OSD([sQuery(id+"F0.wireOp",EDGE,"E7.14.0")])],"isStart":true});
            var Q27;
            Q27=makeQuery(id+"F1.opExtrude","CAP_EDGE",EDGE,{"disambiguationData":[OSD([sQuery(id+"F0.wireOp",EDGE,"E7.12.0")])],"isStart":true});
            var Q28;
            Q28=makeQuery(id+"F1.opExtrude","CAP_EDGE",EDGE,{"disambiguationData":[OSD([sQuery(id+"F0.wireOp",EDGE,"E7.10.0")])],"isStart":true});
            var Q29;
            Q29=makeQuery(id+"F1.opExtrude","CAP_EDGE",EDGE,{"disambiguationData":[OSD([sQuery(id+"F0.wireOp",EDGE,"E7.8.0")])],"isStart":true});
            var Q30;
            Q30=makeQuery(id+"F1.opExtrude","CAP_EDGE",EDGE,{"disambiguationData":[OSD([sQuery(id+"F0.wireOp",EDGE,"E7.6.0")])],"isStart":true});
            var Q31;
            Q31=makeQuery(id+"F1.opExtrude","CAP_EDGE",EDGE,{"disambiguationData":[OSD([sQuery(id+"F0.wireOp",EDGE,"E7.4.0")])],"isStart":true});
            var Q32;
            Q32=makeQuery(id+"F1.opExtrude","CAP_EDGE",EDGE,{"disambiguationData":[OSD([sQuery(id+"F0.wireOp",EDGE,"E7.2.0")])],"isStart":true});
            var Q33;
            Q33=makeQuery(id+"F1.opExtrude","CAP_EDGE",EDGE,{"disambiguationData":[OSD([sQuery(id+"F0.wireOp",EDGE,"E5")])],"isStart":true});
            var Q34;
            Q34=makeQuery(id+"F1.opExtrude","CAP_EDGE",EDGE,{"disambiguationData":[OSD([sQuery(id+"F0.wireOp",EDGE,"E7.42.0")])],"isStart":true});
            var Q35;
            Q35=makeQuery(id+"F1.opExtrude","CAP_EDGE",EDGE,{"disambiguationData":[OSD([sQuery(id+"F0.wireOp",EDGE,"E7.40.0")])],"isStart":true});
            var Q36;
            Q36=makeQuery(id+"F1.opExtrude","CAP_EDGE",EDGE,{"disambiguationData":[OSD([sQuery(id+"F0.wireOp",EDGE,"E7.38.0")])],"isStart":true});
            var Q37;
            Q37=makeQuery(id+"F1.opExtrude","CAP_EDGE",EDGE,{"disambiguationData":[OSD([sQuery(id+"F0.wireOp",EDGE,"E7.36.0")])],"isStart":true});
            var Q38;
            Q38=makeQuery(id+"F1.opExtrude","CAP_EDGE",EDGE,{"disambiguationData":[OSD([sQuery(id+"F0.wireOp",EDGE,"E7.34.0")])],"isStart":true});
            var Q39;
            Q39=makeQuery(id+"F1.opExtrude","CAP_EDGE",EDGE,{"disambiguationData":[OSD([sQuery(id+"F0.wireOp",EDGE,"E7.32.0")])],"isStart":true});
            var Q40;
            Q40=makeQuery(id+"F1.opExtrude","CAP_EDGE",EDGE,{"disambiguationData":[OSD([sQuery(id+"F0.wireOp",EDGE,"E7.30.0")])],"isStart":true});
            var Q41;
            Q41=makeQuery(id+"F1.opExtrude","CAP_EDGE",EDGE,{"disambiguationData":[OSD([sQuery(id+"F0.wireOp",EDGE,"E7.28.0")])],"isStart":true});
            var Q42;
            Q42=makeQuery(id+"F1.opExtrude","CAP_EDGE",EDGE,{"disambiguationData":[OSD([sQuery(id+"F0.wireOp",EDGE,"E7.26.0")])],"isStart":true});
            var Q43;
            Q43=makeQuery(id+"F1.opExtrude","CAP_EDGE",EDGE,{"disambiguationData":[OSD([sQuery(id+"F0.wireOp",EDGE,"E7.24.0")])],"isStart":true});
            chamfer(context, id + "F2", {"entities" : qUnion([Q0, Q1, Q2, Q3, Q4, Q5, Q6, Q7, Q8, Q9, Q10, Q11, Q12, Q13, Q14, Q15, Q16, Q17, Q18, Q19, Q20, Q21, Q22, Q23, Q24, Q25, Q26, Q27, Q28, Q29, Q30, Q31, Q32, Q33, Q34, Q35, Q36, Q37, Q38, Q39, Q40, Q41, Q42, Q43]), "width" : 3.8 * mm, "tangentPropagation" : true});
        }
        {
            var Q0;
            Q0=makeQuery(id+"F1.opExtrude","CAP_FACE",FACE,{"disambiguationData":[OSD([sQuery(id+"F0.wireOp",EDGE,"E1"),sQuery(id+"F0.wireOp",EDGE,"E2"),sQuery(id+"F0.wireOp",EDGE,"E3"),sQuery(id+"F0.wireOp",EDGE,"E4"),sQuery(id+"F0.wireOp",EDGE,"E5"),sQuery(id+"F0.wireOp",EDGE,"E6"),sQuery(id+"F0.wireOp",EDGE,"E7.1.0"),sQuery(id+"F0.wireOp",EDGE,"E7.1.1"),sQuery(id+"F0.wireOp",EDGE,"E7.1.2"),sQuery(id+"F0.wireOp",EDGE,"E7.1.3"),sQuery(id+"F0.wireOp",EDGE,"E7.1.4"),sQuery(id+"F0.wireOp",EDGE,"E7.1.5"),sQuery(id+"F0.wireOp",EDGE,"E7.2.0"),sQuery(id+"F0.wireOp",EDGE,"E7.2.1"),sQuery(id+"F0.wireOp",EDGE,"E7.2.2"),sQuery(id+"F0.wireOp",EDGE,"E7.2.3"),sQuery(id+"F0.wireOp",EDGE,"E7.2.4"),sQuery(id+"F0.wireOp",EDGE,"E7.2.5"),sQuery(id+"F0.wireOp",EDGE,"E7.3.0"),sQuery(id+"F0.wireOp",EDGE,"E7.3.1"),sQuery(id+"F0.wireOp",EDGE,"E7.3.2"),sQuery(id+"F0.wireOp",EDGE,"E7.3.3"),sQuery(id+"F0.wireOp",EDGE,"E7.3.4"),sQuery(id+"F0.wireOp",EDGE,"E7.3.5"),sQuery(id+"F0.wireOp",EDGE,"E7.4.0"),sQuery(id+"F0.wireOp",EDGE,"E7.4.1"),sQuery(id+"F0.wireOp",EDGE,"E7.4.2"),sQuery(id+"F0.wireOp",EDGE,"E7.4.3"),sQuery(id+"F0.wireOp",EDGE,"E7.4.4"),sQuery(id+"F0.wireOp",EDGE,"E7.4.5"),sQuery(id+"F0.wireOp",EDGE,"E7.5.0"),sQuery(id+"F0.wireOp",EDGE,"E7.5.1"),sQuery(id+"F0.wireOp",EDGE,"E7.5.2"),sQuery(id+"F0.wireOp",EDGE,"E7.5.3"),sQuery(id+"F0.wireOp",EDGE,"E7.5.4"),sQuery(id+"F0.wireOp",EDGE,"E7.5.5"),sQuery(id+"F0.wireOp",EDGE,"E7.6.0"),sQuery(id+"F0.wireOp",EDGE,"E7.6.1"),sQuery(id+"F0.wireOp",EDGE,"E7.6.2"),sQuery(id+"F0.wireOp",EDGE,"E7.6.3"),sQuery(id+"F0.wireOp",EDGE,"E7.6.4"),sQuery(id+"F0.wireOp",EDGE,"E7.6.5"),sQuery(id+"F0.wireOp",EDGE,"E7.7.0"),sQuery(id+"F0.wireOp",EDGE,"E7.7.1"),sQuery(id+"F0.wireOp",EDGE,"E7.7.2"),sQuery(id+"F0.wireOp",EDGE,"E7.7.3"),sQuery(id+"F0.wireOp",EDGE,"E7.7.4"),sQuery(id+"F0.wireOp",EDGE,"E7.7.5"),sQuery(id+"F0.wireOp",EDGE,"E7.8.0"),sQuery(id+"F0.wireOp",EDGE,"E7.8.1"),sQuery(id+"F0.wireOp",EDGE,"E7.8.2"),sQuery(id+"F0.wireOp",EDGE,"E7.8.3"),sQuery(id+"F0.wireOp",EDGE,"E7.8.4"),sQuery(id+"F0.wireOp",EDGE,"E7.8.5"),sQuery(id+"F0.wireOp",EDGE,"E7.9.0"),sQuery(id+"F0.wireOp",EDGE,"E7.9.1"),sQuery(id+"F0.wireOp",EDGE,"E7.9.2"),sQuery(id+"F0.wireOp",EDGE,"E7.9.3"),sQuery(id+"F0.wireOp",EDGE,"E7.9.4"),sQuery(id+"F0.wireOp",EDGE,"E7.9.5"),sQuery(id+"F0.wireOp",EDGE,"E7.10.0"),sQuery(id+"F0.wireOp",EDGE,"E7.10.1"),sQuery(id+"F0.wireOp",EDGE,"E7.10.2"),sQuery(id+"F0.wireOp",EDGE,"E7.10.3"),sQuery(id+"F0.wireOp",EDGE,"E7.10.4"),sQuery(id+"F0.wireOp",EDGE,"E7.10.5"),sQuery(id+"F0.wireOp",EDGE,"E7.11.0"),sQuery(id+"F0.wireOp",EDGE,"E7.11.1"),sQuery(id+"F0.wireOp",EDGE,"E7.11.2"),sQuery(id+"F0.wireOp",EDGE,"E7.11.3"),sQuery(id+"F0.wireOp",EDGE,"E7.11.4"),sQuery(id+"F0.wireOp",EDGE,"E7.11.5"),sQuery(id+"F0.wireOp",EDGE,"E7.12.0"),sQuery(id+"F0.wireOp",EDGE,"E7.12.1"),sQuery(id+"F0.wireOp",EDGE,"E7.12.2"),sQuery(id+"F0.wireOp",EDGE,"E7.12.3"),sQuery(id+"F0.wireOp",EDGE,"E7.12.4"),sQuery(id+"F0.wireOp",EDGE,"E7.12.5"),sQuery(id+"F0.wireOp",EDGE,"E7.13.0"),sQuery(id+"F0.wireOp",EDGE,"E7.13.1"),sQuery(id+"F0.wireOp",EDGE,"E7.13.2"),sQuery(id+"F0.wireOp",EDGE,"E7.13.3"),sQuery(id+"F0.wireOp",EDGE,"E7.13.4"),sQuery(id+"F0.wireOp",EDGE,"E7.13.5"),sQuery(id+"F0.wireOp",EDGE,"E7.14.0"),sQuery(id+"F0.wireOp",EDGE,"E7.14.1"),sQuery(id+"F0.wireOp",EDGE,"E7.14.2"),sQuery(id+"F0.wireOp",EDGE,"E7.14.3"),sQuery(id+"F0.wireOp",EDGE,"E7.14.4"),sQuery(id+"F0.wireOp",EDGE,"E7.14.5"),sQuery(id+"F0.wireOp",EDGE,"E7.15.0"),sQuery(id+"F0.wireOp",EDGE,"E7.15.1"),sQuery(id+"F0.wireOp",EDGE,"E7.15.2"),sQuery(id+"F0.wireOp",EDGE,"E7.15.3"),sQuery(id+"F0.wireOp",EDGE,"E7.15.4"),sQuery(id+"F0.wireOp",EDGE,"E7.15.5"),sQuery(id+"F0.wireOp",EDGE,"E7.16.0"),sQuery(id+"F0.wireOp",EDGE,"E7.16.1"),sQuery(id+"F0.wireOp",EDGE,"E7.16.2"),sQuery(id+"F0.wireOp",EDGE,"E7.16.3"),sQuery(id+"F0.wireOp",EDGE,"E7.16.4"),sQuery(id+"F0.wireOp",EDGE,"E7.16.5"),sQuery(id+"F0.wireOp",EDGE,"E7.17.0"),sQuery(id+"F0.wireOp",EDGE,"E7.17.1"),sQuery(id+"F0.wireOp",EDGE,"E7.17.2"),sQuery(id+"F0.wireOp",EDGE,"E7.17.3"),sQuery(id+"F0.wireOp",EDGE,"E7.17.4"),sQuery(id+"F0.wireOp",EDGE,"E7.17.5"),sQuery(id+"F0.wireOp",EDGE,"E7.18.0"),sQuery(id+"F0.wireOp",EDGE,"E7.18.1"),sQuery(id+"F0.wireOp",EDGE,"E7.18.2"),sQuery(id+"F0.wireOp",EDGE,"E7.18.3"),sQuery(id+"F0.wireOp",EDGE,"E7.18.4"),sQuery(id+"F0.wireOp",EDGE,"E7.18.5"),sQuery(id+"F0.wireOp",EDGE,"E7.19.0"),sQuery(id+"F0.wireOp",EDGE,"E7.19.1"),sQuery(id+"F0.wireOp",EDGE,"E7.19.2"),sQuery(id+"F0.wireOp",EDGE,"E7.19.3"),sQuery(id+"F0.wireOp",EDGE,"E7.19.4"),sQuery(id+"F0.wireOp",EDGE,"E7.19.5"),sQuery(id+"F0.wireOp",EDGE,"E7.20.0"),sQuery(id+"F0.wireOp",EDGE,"E7.20.1"),sQuery(id+"F0.wireOp",EDGE,"E7.20.2"),sQuery(id+"F0.wireOp",EDGE,"E7.20.3"),sQuery(id+"F0.wireOp",EDGE,"E7.20.4"),sQuery(id+"F0.wireOp",EDGE,"E7.20.5"),sQuery(id+"F0.wireOp",EDGE,"E7.21.0"),sQuery(id+"F0.wireOp",EDGE,"E7.21.1"),sQuery(id+"F0.wireOp",EDGE,"E7.21.2"),sQuery(id+"F0.wireOp",EDGE,"E7.21.3"),sQuery(id+"F0.wireOp",EDGE,"E7.21.4"),sQuery(id+"F0.wireOp",EDGE,"E7.21.5"),sQuery(id+"F0.wireOp",EDGE,"E7.22.0"),sQuery(id+"F0.wireOp",EDGE,"E7.22.1"),sQuery(id+"F0.wireOp",EDGE,"E7.22.2"),sQuery(id+"F0.wireOp",EDGE,"E7.22.3"),sQuery(id+"F0.wireOp",EDGE,"E7.22.4"),sQuery(id+"F0.wireOp",EDGE,"E7.22.5"),sQuery(id+"F0.wireOp",EDGE,"E7.23.0"),sQuery(id+"F0.wireOp",EDGE,"E7.23.1"),sQuery(id+"F0.wireOp",EDGE,"E7.23.2"),sQuery(id+"F0.wireOp",EDGE,"E7.23.3"),sQuery(id+"F0.wireOp",EDGE,"E7.23.4"),sQuery(id+"F0.wireOp",EDGE,"E7.23.5"),sQuery(id+"F0.wireOp",EDGE,"E7.24.0"),sQuery(id+"F0.wireOp",EDGE,"E7.24.1"),sQuery(id+"F0.wireOp",EDGE,"E7.24.2"),sQuery(id+"F0.wireOp",EDGE,"E7.24.3"),sQuery(id+"F0.wireOp",EDGE,"E7.24.4"),sQuery(id+"F0.wireOp",EDGE,"E7.24.5"),sQuery(id+"F0.wireOp",EDGE,"E7.25.0"),sQuery(id+"F0.wireOp",EDGE,"E7.25.1"),sQuery(id+"F0.wireOp",EDGE,"E7.25.2"),sQuery(id+"F0.wireOp",EDGE,"E7.25.3"),sQuery(id+"F0.wireOp",EDGE,"E7.25.4"),sQuery(id+"F0.wireOp",EDGE,"E7.25.5"),sQuery(id+"F0.wireOp",EDGE,"E7.26.0"),sQuery(id+"F0.wireOp",EDGE,"E7.26.1"),sQuery(id+"F0.wireOp",EDGE,"E7.26.2"),sQuery(id+"F0.wireOp",EDGE,"E7.26.3"),sQuery(id+"F0.wireOp",EDGE,"E7.26.4"),sQuery(id+"F0.wireOp",EDGE,"E7.26.5"),sQuery(id+"F0.wireOp",EDGE,"E7.27.0"),sQuery(id+"F0.wireOp",EDGE,"E7.27.1"),sQuery(id+"F0.wireOp",EDGE,"E7.27.2"),sQuery(id+"F0.wireOp",EDGE,"E7.27.3"),sQuery(id+"F0.wireOp",EDGE,"E7.27.4"),sQuery(id+"F0.wireOp",EDGE,"E7.27.5"),sQuery(id+"F0.wireOp",EDGE,"E7.28.0"),sQuery(id+"F0.wireOp",EDGE,"E7.28.1"),sQuery(id+"F0.wireOp",EDGE,"E7.28.2"),sQuery(id+"F0.wireOp",EDGE,"E7.28.3"),sQuery(id+"F0.wireOp",EDGE,"E7.28.4"),sQuery(id+"F0.wireOp",EDGE,"E7.28.5"),sQuery(id+"F0.wireOp",EDGE,"E7.29.0"),sQuery(id+"F0.wireOp",EDGE,"E7.29.1"),sQuery(id+"F0.wireOp",EDGE,"E7.29.2"),sQuery(id+"F0.wireOp",EDGE,"E7.29.3"),sQuery(id+"F0.wireOp",EDGE,"E7.29.4"),sQuery(id+"F0.wireOp",EDGE,"E7.29.5"),sQuery(id+"F0.wireOp",EDGE,"E7.30.0"),sQuery(id+"F0.wireOp",EDGE,"E7.30.1"),sQuery(id+"F0.wireOp",EDGE,"E7.30.2"),sQuery(id+"F0.wireOp",EDGE,"E7.30.3"),sQuery(id+"F0.wireOp",EDGE,"E7.30.4"),sQuery(id+"F0.wireOp",EDGE,"E7.30.5"),sQuery(id+"F0.wireOp",EDGE,"E7.31.0"),sQuery(id+"F0.wireOp",EDGE,"E7.31.1"),sQuery(id+"F0.wireOp",EDGE,"E7.31.2"),sQuery(id+"F0.wireOp",EDGE,"E7.31.3"),sQuery(id+"F0.wireOp",EDGE,"E7.31.4"),sQuery(id+"F0.wireOp",EDGE,"E7.31.5"),sQuery(id+"F0.wireOp",EDGE,"E7.32.0"),sQuery(id+"F0.wireOp",EDGE,"E7.32.1"),sQuery(id+"F0.wireOp",EDGE,"E7.32.2"),sQuery(id+"F0.wireOp",EDGE,"E7.32.3"),sQuery(id+"F0.wireOp",EDGE,"E7.32.4"),sQuery(id+"F0.wireOp",EDGE,"E7.32.5"),sQuery(id+"F0.wireOp",EDGE,"E7.33.0"),sQuery(id+"F0.wireOp",EDGE,"E7.33.1"),sQuery(id+"F0.wireOp",EDGE,"E7.33.2"),sQuery(id+"F0.wireOp",EDGE,"E7.33.3"),sQuery(id+"F0.wireOp",EDGE,"E7.33.4"),sQuery(id+"F0.wireOp",EDGE,"E7.33.5"),sQuery(id+"F0.wireOp",EDGE,"E7.34.0"),sQuery(id+"F0.wireOp",EDGE,"E7.34.1"),sQuery(id+"F0.wireOp",EDGE,"E7.34.2"),sQuery(id+"F0.wireOp",EDGE,"E7.34.3"),sQuery(id+"F0.wireOp",EDGE,"E7.34.4"),sQuery(id+"F0.wireOp",EDGE,"E7.34.5"),sQuery(id+"F0.wireOp",EDGE,"E7.35.0"),sQuery(id+"F0.wireOp",EDGE,"E7.35.1"),sQuery(id+"F0.wireOp",EDGE,"E7.35.2"),sQuery(id+"F0.wireOp",EDGE,"E7.35.3"),sQuery(id+"F0.wireOp",EDGE,"E7.35.4"),sQuery(id+"F0.wireOp",EDGE,"E7.35.5"),sQuery(id+"F0.wireOp",EDGE,"E7.36.0"),sQuery(id+"F0.wireOp",EDGE,"E7.36.1"),sQuery(id+"F0.wireOp",EDGE,"E7.36.2"),sQuery(id+"F0.wireOp",EDGE,"E7.36.3"),sQuery(id+"F0.wireOp",EDGE,"E7.36.4"),sQuery(id+"F0.wireOp",EDGE,"E7.36.5"),sQuery(id+"F0.wireOp",EDGE,"E7.37.0"),sQuery(id+"F0.wireOp",EDGE,"E7.37.1"),sQuery(id+"F0.wireOp",EDGE,"E7.37.2"),sQuery(id+"F0.wireOp",EDGE,"E7.37.3"),sQuery(id+"F0.wireOp",EDGE,"E7.37.4"),sQuery(id+"F0.wireOp",EDGE,"E7.37.5"),sQuery(id+"F0.wireOp",EDGE,"E7.38.0"),sQuery(id+"F0.wireOp",EDGE,"E7.38.1"),sQuery(id+"F0.wireOp",EDGE,"E7.38.2"),sQuery(id+"F0.wireOp",EDGE,"E7.38.3"),sQuery(id+"F0.wireOp",EDGE,"E7.38.4"),sQuery(id+"F0.wireOp",EDGE,"E7.38.5"),sQuery(id+"F0.wireOp",EDGE,"E7.39.0"),sQuery(id+"F0.wireOp",EDGE,"E7.39.1"),sQuery(id+"F0.wireOp",EDGE,"E7.39.2"),sQuery(id+"F0.wireOp",EDGE,"E7.39.3"),sQuery(id+"F0.wireOp",EDGE,"E7.39.4"),sQuery(id+"F0.wireOp",EDGE,"E7.39.5"),sQuery(id+"F0.wireOp",EDGE,"E7.40.0"),sQuery(id+"F0.wireOp",EDGE,"E7.40.1"),sQuery(id+"F0.wireOp",EDGE,"E7.40.2"),sQuery(id+"F0.wireOp",EDGE,"E7.40.3"),sQuery(id+"F0.wireOp",EDGE,"E7.40.4"),sQuery(id+"F0.wireOp",EDGE,"E7.40.5"),sQuery(id+"F0.wireOp",EDGE,"E7.41.0"),sQuery(id+"F0.wireOp",EDGE,"E7.41.1"),sQuery(id+"F0.wireOp",EDGE,"E7.41.2"),sQuery(id+"F0.wireOp",EDGE,"E7.41.3"),sQuery(id+"F0.wireOp",EDGE,"E7.41.4"),sQuery(id+"F0.wireOp",EDGE,"E7.41.5"),sQuery(id+"F0.wireOp",EDGE,"E7.42.0"),sQuery(id+"F0.wireOp",EDGE,"E7.42.1"),sQuery(id+"F0.wireOp",EDGE,"E7.42.2"),sQuery(id+"F0.wireOp",EDGE,"E7.42.3"),sQuery(id+"F0.wireOp",EDGE,"E7.42.4"),sQuery(id+"F0.wireOp",EDGE,"E7.42.5"),sQuery(id+"F0.wireOp",EDGE,"E7.43.0"),sQuery(id+"F0.wireOp",EDGE,"E7.43.1"),sQuery(id+"F0.wireOp",EDGE,"E7.43.2"),sQuery(id+"F0.wireOp",EDGE,"E7.43.3"),sQuery(id+"F0.wireOp",EDGE,"E7.43.4"),sQuery(id+"F0.wireOp",EDGE,"E7.43.5")])],"isStart":false});
            var sketch = newSketch(context, id + "F3", { "sketchPlane" : qUnion([Q0])});
            skCircle(sketch, "E8", {"center": v(0, 0) * mm, "radius": 21.28 * mm});
            skSolve(sketch);
        }
        {
            var Q0;
            Q0 = qSketchRegion(id + "F3", true);
            var Q1;
            Q1=makeQuery(id+"F3.imprint","IMPRINT",FACE,{"disambiguationData":[TD([[makeQuery(id+"F3.imprint","IMPRINT",EDGE,{"derivedFrom":sQuery(id+"F3.wireOp",EDGE,"E8")}),1.0]])]});
            extrude(context, id + "F4", {"entities" : qUnion([Q0, Q1]), "operationType" : NewBodyOperationType.REMOVE, "oppositeDirection" : true, "depth" : 25.4 * mm});
        }
        {
            var Q0;
            Q0=makeQuery(id+"F1.opExtrude","CAP_FACE",FACE,{"disambiguationData":[OSD([sQuery(id+"F0.wireOp",EDGE,"E1"),sQuery(id+"F0.wireOp",EDGE,"E2"),sQuery(id+"F0.wireOp",EDGE,"E3"),sQuery(id+"F0.wireOp",EDGE,"E4"),sQuery(id+"F0.wireOp",EDGE,"E5"),sQuery(id+"F0.wireOp",EDGE,"E6"),sQuery(id+"F0.wireOp",EDGE,"E7.1.0"),sQuery(id+"F0.wireOp",EDGE,"E7.1.1"),sQuery(id+"F0.wireOp",EDGE,"E7.1.2"),sQuery(id+"F0.wireOp",EDGE,"E7.1.3"),sQuery(id+"F0.wireOp",EDGE,"E7.1.4"),sQuery(id+"F0.wireOp",EDGE,"E7.1.5"),sQuery(id+"F0.wireOp",EDGE,"E7.2.0"),sQuery(id+"F0.wireOp",EDGE,"E7.2.1"),sQuery(id+"F0.wireOp",EDGE,"E7.2.2"),sQuery(id+"F0.wireOp",EDGE,"E7.2.3"),sQuery(id+"F0.wireOp",EDGE,"E7.2.4"),sQuery(id+"F0.wireOp",EDGE,"E7.2.5"),sQuery(id+"F0.wireOp",EDGE,"E7.3.0"),sQuery(id+"F0.wireOp",EDGE,"E7.3.1"),sQuery(id+"F0.wireOp",EDGE,"E7.3.2"),sQuery(id+"F0.wireOp",EDGE,"E7.3.3"),sQuery(id+"F0.wireOp",EDGE,"E7.3.4"),sQuery(id+"F0.wireOp",EDGE,"E7.3.5"),sQuery(id+"F0.wireOp",EDGE,"E7.4.0"),sQuery(id+"F0.wireOp",EDGE,"E7.4.1"),sQuery(id+"F0.wireOp",EDGE,"E7.4.2"),sQuery(id+"F0.wireOp",EDGE,"E7.4.3"),sQuery(id+"F0.wireOp",EDGE,"E7.4.4"),sQuery(id+"F0.wireOp",EDGE,"E7.4.5"),sQuery(id+"F0.wireOp",EDGE,"E7.5.0"),sQuery(id+"F0.wireOp",EDGE,"E7.5.1"),sQuery(id+"F0.wireOp",EDGE,"E7.5.2"),sQuery(id+"F0.wireOp",EDGE,"E7.5.3"),sQuery(id+"F0.wireOp",EDGE,"E7.5.4"),sQuery(id+"F0.wireOp",EDGE,"E7.5.5"),sQuery(id+"F0.wireOp",EDGE,"E7.6.0"),sQuery(id+"F0.wireOp",EDGE,"E7.6.1"),sQuery(id+"F0.wireOp",EDGE,"E7.6.2"),sQuery(id+"F0.wireOp",EDGE,"E7.6.3"),sQuery(id+"F0.wireOp",EDGE,"E7.6.4"),sQuery(id+"F0.wireOp",EDGE,"E7.6.5"),sQuery(id+"F0.wireOp",EDGE,"E7.7.0"),sQuery(id+"F0.wireOp",EDGE,"E7.7.1"),sQuery(id+"F0.wireOp",EDGE,"E7.7.2"),sQuery(id+"F0.wireOp",EDGE,"E7.7.3"),sQuery(id+"F0.wireOp",EDGE,"E7.7.4"),sQuery(id+"F0.wireOp",EDGE,"E7.7.5"),sQuery(id+"F0.wireOp",EDGE,"E7.8.0"),sQuery(id+"F0.wireOp",EDGE,"E7.8.1"),sQuery(id+"F0.wireOp",EDGE,"E7.8.2"),sQuery(id+"F0.wireOp",EDGE,"E7.8.3"),sQuery(id+"F0.wireOp",EDGE,"E7.8.4"),sQuery(id+"F0.wireOp",EDGE,"E7.8.5"),sQuery(id+"F0.wireOp",EDGE,"E7.9.0"),sQuery(id+"F0.wireOp",EDGE,"E7.9.1"),sQuery(id+"F0.wireOp",EDGE,"E7.9.2"),sQuery(id+"F0.wireOp",EDGE,"E7.9.3"),sQuery(id+"F0.wireOp",EDGE,"E7.9.4"),sQuery(id+"F0.wireOp",EDGE,"E7.9.5"),sQuery(id+"F0.wireOp",EDGE,"E7.10.0"),sQuery(id+"F0.wireOp",EDGE,"E7.10.1"),sQuery(id+"F0.wireOp",EDGE,"E7.10.2"),sQuery(id+"F0.wireOp",EDGE,"E7.10.3"),sQuery(id+"F0.wireOp",EDGE,"E7.10.4"),sQuery(id+"F0.wireOp",EDGE,"E7.10.5"),sQuery(id+"F0.wireOp",EDGE,"E7.11.0"),sQuery(id+"F0.wireOp",EDGE,"E7.11.1"),sQuery(id+"F0.wireOp",EDGE,"E7.11.2"),sQuery(id+"F0.wireOp",EDGE,"E7.11.3"),sQuery(id+"F0.wireOp",EDGE,"E7.11.4"),sQuery(id+"F0.wireOp",EDGE,"E7.11.5"),sQuery(id+"F0.wireOp",EDGE,"E7.12.0"),sQuery(id+"F0.wireOp",EDGE,"E7.12.1"),sQuery(id+"F0.wireOp",EDGE,"E7.12.2"),sQuery(id+"F0.wireOp",EDGE,"E7.12.3"),sQuery(id+"F0.wireOp",EDGE,"E7.12.4"),sQuery(id+"F0.wireOp",EDGE,"E7.12.5"),sQuery(id+"F0.wireOp",EDGE,"E7.13.0"),sQuery(id+"F0.wireOp",EDGE,"E7.13.1"),sQuery(id+"F0.wireOp",EDGE,"E7.13.2"),sQuery(id+"F0.wireOp",EDGE,"E7.13.3"),sQuery(id+"F0.wireOp",EDGE,"E7.13.4"),sQuery(id+"F0.wireOp",EDGE,"E7.13.5"),sQuery(id+"F0.wireOp",EDGE,"E7.14.0"),sQuery(id+"F0.wireOp",EDGE,"E7.14.1"),sQuery(id+"F0.wireOp",EDGE,"E7.14.2"),sQuery(id+"F0.wireOp",EDGE,"E7.14.3"),sQuery(id+"F0.wireOp",EDGE,"E7.14.4"),sQuery(id+"F0.wireOp",EDGE,"E7.14.5"),sQuery(id+"F0.wireOp",EDGE,"E7.15.0"),sQuery(id+"F0.wireOp",EDGE,"E7.15.1"),sQuery(id+"F0.wireOp",EDGE,"E7.15.2"),sQuery(id+"F0.wireOp",EDGE,"E7.15.3"),sQuery(id+"F0.wireOp",EDGE,"E7.15.4"),sQuery(id+"F0.wireOp",EDGE,"E7.15.5"),sQuery(id+"F0.wireOp",EDGE,"E7.16.0"),sQuery(id+"F0.wireOp",EDGE,"E7.16.1"),sQuery(id+"F0.wireOp",EDGE,"E7.16.2"),sQuery(id+"F0.wireOp",EDGE,"E7.16.3"),sQuery(id+"F0.wireOp",EDGE,"E7.16.4"),sQuery(id+"F0.wireOp",EDGE,"E7.16.5"),sQuery(id+"F0.wireOp",EDGE,"E7.17.0"),sQuery(id+"F0.wireOp",EDGE,"E7.17.1"),sQuery(id+"F0.wireOp",EDGE,"E7.17.2"),sQuery(id+"F0.wireOp",EDGE,"E7.17.3"),sQuery(id+"F0.wireOp",EDGE,"E7.17.4"),sQuery(id+"F0.wireOp",EDGE,"E7.17.5"),sQuery(id+"F0.wireOp",EDGE,"E7.18.0"),sQuery(id+"F0.wireOp",EDGE,"E7.18.1"),sQuery(id+"F0.wireOp",EDGE,"E7.18.2"),sQuery(id+"F0.wireOp",EDGE,"E7.18.3"),sQuery(id+"F0.wireOp",EDGE,"E7.18.4"),sQuery(id+"F0.wireOp",EDGE,"E7.18.5"),sQuery(id+"F0.wireOp",EDGE,"E7.19.0"),sQuery(id+"F0.wireOp",EDGE,"E7.19.1"),sQuery(id+"F0.wireOp",EDGE,"E7.19.2"),sQuery(id+"F0.wireOp",EDGE,"E7.19.3"),sQuery(id+"F0.wireOp",EDGE,"E7.19.4"),sQuery(id+"F0.wireOp",EDGE,"E7.19.5"),sQuery(id+"F0.wireOp",EDGE,"E7.20.0"),sQuery(id+"F0.wireOp",EDGE,"E7.20.1"),sQuery(id+"F0.wireOp",EDGE,"E7.20.2"),sQuery(id+"F0.wireOp",EDGE,"E7.20.3"),sQuery(id+"F0.wireOp",EDGE,"E7.20.4"),sQuery(id+"F0.wireOp",EDGE,"E7.20.5"),sQuery(id+"F0.wireOp",EDGE,"E7.21.0"),sQuery(id+"F0.wireOp",EDGE,"E7.21.1"),sQuery(id+"F0.wireOp",EDGE,"E7.21.2"),sQuery(id+"F0.wireOp",EDGE,"E7.21.3"),sQuery(id+"F0.wireOp",EDGE,"E7.21.4"),sQuery(id+"F0.wireOp",EDGE,"E7.21.5"),sQuery(id+"F0.wireOp",EDGE,"E7.22.0"),sQuery(id+"F0.wireOp",EDGE,"E7.22.1"),sQuery(id+"F0.wireOp",EDGE,"E7.22.2"),sQuery(id+"F0.wireOp",EDGE,"E7.22.3"),sQuery(id+"F0.wireOp",EDGE,"E7.22.4"),sQuery(id+"F0.wireOp",EDGE,"E7.22.5"),sQuery(id+"F0.wireOp",EDGE,"E7.23.0"),sQuery(id+"F0.wireOp",EDGE,"E7.23.1"),sQuery(id+"F0.wireOp",EDGE,"E7.23.2"),sQuery(id+"F0.wireOp",EDGE,"E7.23.3"),sQuery(id+"F0.wireOp",EDGE,"E7.23.4"),sQuery(id+"F0.wireOp",EDGE,"E7.23.5"),sQuery(id+"F0.wireOp",EDGE,"E7.24.0"),sQuery(id+"F0.wireOp",EDGE,"E7.24.1"),sQuery(id+"F0.wireOp",EDGE,"E7.24.2"),sQuery(id+"F0.wireOp",EDGE,"E7.24.3"),sQuery(id+"F0.wireOp",EDGE,"E7.24.4"),sQuery(id+"F0.wireOp",EDGE,"E7.24.5"),sQuery(id+"F0.wireOp",EDGE,"E7.25.0"),sQuery(id+"F0.wireOp",EDGE,"E7.25.1"),sQuery(id+"F0.wireOp",EDGE,"E7.25.2"),sQuery(id+"F0.wireOp",EDGE,"E7.25.3"),sQuery(id+"F0.wireOp",EDGE,"E7.25.4"),sQuery(id+"F0.wireOp",EDGE,"E7.25.5"),sQuery(id+"F0.wireOp",EDGE,"E7.26.0"),sQuery(id+"F0.wireOp",EDGE,"E7.26.1"),sQuery(id+"F0.wireOp",EDGE,"E7.26.2"),sQuery(id+"F0.wireOp",EDGE,"E7.26.3"),sQuery(id+"F0.wireOp",EDGE,"E7.26.4"),sQuery(id+"F0.wireOp",EDGE,"E7.26.5"),sQuery(id+"F0.wireOp",EDGE,"E7.27.0"),sQuery(id+"F0.wireOp",EDGE,"E7.27.1"),sQuery(id+"F0.wireOp",EDGE,"E7.27.2"),sQuery(id+"F0.wireOp",EDGE,"E7.27.3"),sQuery(id+"F0.wireOp",EDGE,"E7.27.4"),sQuery(id+"F0.wireOp",EDGE,"E7.27.5"),sQuery(id+"F0.wireOp",EDGE,"E7.28.0"),sQuery(id+"F0.wireOp",EDGE,"E7.28.1"),sQuery(id+"F0.wireOp",EDGE,"E7.28.2"),sQuery(id+"F0.wireOp",EDGE,"E7.28.3"),sQuery(id+"F0.wireOp",EDGE,"E7.28.4"),sQuery(id+"F0.wireOp",EDGE,"E7.28.5"),sQuery(id+"F0.wireOp",EDGE,"E7.29.0"),sQuery(id+"F0.wireOp",EDGE,"E7.29.1"),sQuery(id+"F0.wireOp",EDGE,"E7.29.2"),sQuery(id+"F0.wireOp",EDGE,"E7.29.3"),sQuery(id+"F0.wireOp",EDGE,"E7.29.4"),sQuery(id+"F0.wireOp",EDGE,"E7.29.5"),sQuery(id+"F0.wireOp",EDGE,"E7.30.0"),sQuery(id+"F0.wireOp",EDGE,"E7.30.1"),sQuery(id+"F0.wireOp",EDGE,"E7.30.2"),sQuery(id+"F0.wireOp",EDGE,"E7.30.3"),sQuery(id+"F0.wireOp",EDGE,"E7.30.4"),sQuery(id+"F0.wireOp",EDGE,"E7.30.5"),sQuery(id+"F0.wireOp",EDGE,"E7.31.0"),sQuery(id+"F0.wireOp",EDGE,"E7.31.1"),sQuery(id+"F0.wireOp",EDGE,"E7.31.2"),sQuery(id+"F0.wireOp",EDGE,"E7.31.3"),sQuery(id+"F0.wireOp",EDGE,"E7.31.4"),sQuery(id+"F0.wireOp",EDGE,"E7.31.5"),sQuery(id+"F0.wireOp",EDGE,"E7.32.0"),sQuery(id+"F0.wireOp",EDGE,"E7.32.1"),sQuery(id+"F0.wireOp",EDGE,"E7.32.2"),sQuery(id+"F0.wireOp",EDGE,"E7.32.3"),sQuery(id+"F0.wireOp",EDGE,"E7.32.4"),sQuery(id+"F0.wireOp",EDGE,"E7.32.5"),sQuery(id+"F0.wireOp",EDGE,"E7.33.0"),sQuery(id+"F0.wireOp",EDGE,"E7.33.1"),sQuery(id+"F0.wireOp",EDGE,"E7.33.2"),sQuery(id+"F0.wireOp",EDGE,"E7.33.3"),sQuery(id+"F0.wireOp",EDGE,"E7.33.4"),sQuery(id+"F0.wireOp",EDGE,"E7.33.5"),sQuery(id+"F0.wireOp",EDGE,"E7.34.0"),sQuery(id+"F0.wireOp",EDGE,"E7.34.1"),sQuery(id+"F0.wireOp",EDGE,"E7.34.2"),sQuery(id+"F0.wireOp",EDGE,"E7.34.3"),sQuery(id+"F0.wireOp",EDGE,"E7.34.4"),sQuery(id+"F0.wireOp",EDGE,"E7.34.5"),sQuery(id+"F0.wireOp",EDGE,"E7.35.0"),sQuery(id+"F0.wireOp",EDGE,"E7.35.1"),sQuery(id+"F0.wireOp",EDGE,"E7.35.2"),sQuery(id+"F0.wireOp",EDGE,"E7.35.3"),sQuery(id+"F0.wireOp",EDGE,"E7.35.4"),sQuery(id+"F0.wireOp",EDGE,"E7.35.5"),sQuery(id+"F0.wireOp",EDGE,"E7.36.0"),sQuery(id+"F0.wireOp",EDGE,"E7.36.1"),sQuery(id+"F0.wireOp",EDGE,"E7.36.2"),sQuery(id+"F0.wireOp",EDGE,"E7.36.3"),sQuery(id+"F0.wireOp",EDGE,"E7.36.4"),sQuery(id+"F0.wireOp",EDGE,"E7.36.5"),sQuery(id+"F0.wireOp",EDGE,"E7.37.0"),sQuery(id+"F0.wireOp",EDGE,"E7.37.1"),sQuery(id+"F0.wireOp",EDGE,"E7.37.2"),sQuery(id+"F0.wireOp",EDGE,"E7.37.3"),sQuery(id+"F0.wireOp",EDGE,"E7.37.4"),sQuery(id+"F0.wireOp",EDGE,"E7.37.5"),sQuery(id+"F0.wireOp",EDGE,"E7.38.0"),sQuery(id+"F0.wireOp",EDGE,"E7.38.1"),sQuery(id+"F0.wireOp",EDGE,"E7.38.2"),sQuery(id+"F0.wireOp",EDGE,"E7.38.3"),sQuery(id+"F0.wireOp",EDGE,"E7.38.4"),sQuery(id+"F0.wireOp",EDGE,"E7.38.5"),sQuery(id+"F0.wireOp",EDGE,"E7.39.0"),sQuery(id+"F0.wireOp",EDGE,"E7.39.1"),sQuery(id+"F0.wireOp",EDGE,"E7.39.2"),sQuery(id+"F0.wireOp",EDGE,"E7.39.3"),sQuery(id+"F0.wireOp",EDGE,"E7.39.4"),sQuery(id+"F0.wireOp",EDGE,"E7.39.5"),sQuery(id+"F0.wireOp",EDGE,"E7.40.0"),sQuery(id+"F0.wireOp",EDGE,"E7.40.1"),sQuery(id+"F0.wireOp",EDGE,"E7.40.2"),sQuery(id+"F0.wireOp",EDGE,"E7.40.3"),sQuery(id+"F0.wireOp",EDGE,"E7.40.4"),sQuery(id+"F0.wireOp",EDGE,"E7.40.5"),sQuery(id+"F0.wireOp",EDGE,"E7.41.0"),sQuery(id+"F0.wireOp",EDGE,"E7.41.1"),sQuery(id+"F0.wireOp",EDGE,"E7.41.2"),sQuery(id+"F0.wireOp",EDGE,"E7.41.3"),sQuery(id+"F0.wireOp",EDGE,"E7.41.4"),sQuery(id+"F0.wireOp",EDGE,"E7.41.5"),sQuery(id+"F0.wireOp",EDGE,"E7.42.0"),sQuery(id+"F0.wireOp",EDGE,"E7.42.1"),sQuery(id+"F0.wireOp",EDGE,"E7.42.2"),sQuery(id+"F0.wireOp",EDGE,"E7.42.3"),sQuery(id+"F0.wireOp",EDGE,"E7.42.4"),sQuery(id+"F0.wireOp",EDGE,"E7.42.5"),sQuery(id+"F0.wireOp",EDGE,"E7.43.0"),sQuery(id+"F0.wireOp",EDGE,"E7.43.1"),sQuery(id+"F0.wireOp",EDGE,"E7.43.2"),sQuery(id+"F0.wireOp",EDGE,"E7.43.3"),sQuery(id+"F0.wireOp",EDGE,"E7.43.4"),sQuery(id+"F0.wireOp",EDGE,"E7.43.5")])],"isStart":false});
            var sketch = newSketch(context, id + "F5", { "sketchPlane" : qUnion([Q0])});
            skLineSegment(sketch, "E9", {"start": v(0, 79.18) * mm, "end": v(-0.56, 79.18) * mm});
            skLineSegment(sketch, "E10", {"start": v(-0.56, 79.18) * mm, "end": v(-0.56, 0) * mm});
            skLineSegment(sketch, "E11", {"start": v(-0.56, 0) * mm, "end": v(0, 0) * mm});
            skLineSegment(sketch, "E12", {"start": v(0, 0) * mm, "end": v(0, 79.18) * mm});
            skSolve(sketch);
        }
        {
            var Q0;
            Q0 = qSketchRegion(id + "F5", true);
            extrude(context, id + "F6", {"entities" : qUnion([Q0]), "operationType" : NewBodyOperationType.REMOVE, "oppositeDirection" : true, "depth" : 25.4 * mm});
        }
        {
            var Q0;
            Q0=makeQuery(id+"F6.boolean.opBoolean","INTERSECT",EDGE,{"derivedFrom":[makeQuery(id+"F4.boolean.opBoolean","COPY",FACE,{"derivedFrom":makeQuery(id+"F4.opExtrude","SWEPT_FACE",FACE,{"disambiguationData":[OSD([sQuery(id+"F3.wireOp",EDGE,"E8")])]})}),makeQuery(id+"F6.opExtrude","SWEPT_FACE",FACE,{"disambiguationData":[OSD([sQuery(id+"F5.wireOp",EDGE,"E10")])]})]});
            var Q1;
            Q1=makeQuery(id+"F6.boolean.opBoolean","INTERSECT",EDGE,{"derivedFrom":[makeQuery(id+"F4.boolean.opBoolean","COPY",FACE,{"derivedFrom":makeQuery(id+"F4.opExtrude","SWEPT_FACE",FACE,{"disambiguationData":[OSD([sQuery(id+"F3.wireOp",EDGE,"E8")])]})}),makeQuery(id+"F6.opExtrude","SWEPT_FACE",FACE,{"disambiguationData":[OSD([sQuery(id+"F5.wireOp",EDGE,"E12")])]})]});
            fillet(context, id + "F7", {"entities" : qUnion([Q0, Q1]), "radius" : 22.08 * mm, "tangentPropagation" : true, "allowEdgeOverflow" : false});
        }
        {
            var Q0;
            {var subQ0=sQuery(id+"F0.wireOp",EDGE,"E7.43.0");Q0=makeQuery(id+"F2.opChamfer","BLEND_EDGE",EDGE,{"blendedFrom":[makeQuery(id+"F1.opExtrude","CAP_EDGE",EDGE,{"disambiguationData":[OSD([subQ0])],"isStart":false}),makeQuery(id+"F1.opExtrude","CAP_FACE",FACE,{"disambiguationData":[OSD([sQuery(id+"F0.wireOp",EDGE,"E1"),sQuery(id+"F0.wireOp",EDGE,"E2"),sQuery(id+"F0.wireOp",EDGE,"E3"),sQuery(id+"F0.wireOp",EDGE,"E4"),sQuery(id+"F0.wireOp",EDGE,"E5"),sQuery(id+"F0.wireOp",EDGE,"E6"),sQuery(id+"F0.wireOp",EDGE,"E7.1.0"),sQuery(id+"F0.wireOp",EDGE,"E7.1.1"),sQuery(id+"F0.wireOp",EDGE,"E7.1.2"),sQuery(id+"F0.wireOp",EDGE,"E7.1.3"),sQuery(id+"F0.wireOp",EDGE,"E7.1.4"),sQuery(id+"F0.wireOp",EDGE,"E7.1.5"),sQuery(id+"F0.wireOp",EDGE,"E7.2.0"),sQuery(id+"F0.wireOp",EDGE,"E7.2.1"),sQuery(id+"F0.wireOp",EDGE,"E7.2.2"),sQuery(id+"F0.wireOp",EDGE,"E7.2.3"),sQuery(id+"F0.wireOp",EDGE,"E7.2.4"),sQuery(id+"F0.wireOp",EDGE,"E7.2.5"),sQuery(id+"F0.wireOp",EDGE,"E7.3.0"),sQuery(id+"F0.wireOp",EDGE,"E7.3.1"),sQuery(id+"F0.wireOp",EDGE,"E7.3.2"),sQuery(id+"F0.wireOp",EDGE,"E7.3.3"),sQuery(id+"F0.wireOp",EDGE,"E7.3.4"),sQuery(id+"F0.wireOp",EDGE,"E7.3.5"),sQuery(id+"F0.wireOp",EDGE,"E7.4.0"),sQuery(id+"F0.wireOp",EDGE,"E7.4.1"),sQuery(id+"F0.wireOp",EDGE,"E7.4.2"),sQuery(id+"F0.wireOp",EDGE,"E7.4.3"),sQuery(id+"F0.wireOp",EDGE,"E7.4.4"),sQuery(id+"F0.wireOp",EDGE,"E7.4.5"),sQuery(id+"F0.wireOp",EDGE,"E7.5.0"),sQuery(id+"F0.wireOp",EDGE,"E7.5.1"),sQuery(id+"F0.wireOp",EDGE,"E7.5.2"),sQuery(id+"F0.wireOp",EDGE,"E7.5.3"),sQuery(id+"F0.wireOp",EDGE,"E7.5.4"),sQuery(id+"F0.wireOp",EDGE,"E7.5.5"),sQuery(id+"F0.wireOp",EDGE,"E7.6.0"),sQuery(id+"F0.wireOp",EDGE,"E7.6.1"),sQuery(id+"F0.wireOp",EDGE,"E7.6.2"),sQuery(id+"F0.wireOp",EDGE,"E7.6.3"),sQuery(id+"F0.wireOp",EDGE,"E7.6.4"),sQuery(id+"F0.wireOp",EDGE,"E7.6.5"),sQuery(id+"F0.wireOp",EDGE,"E7.7.0"),sQuery(id+"F0.wireOp",EDGE,"E7.7.1"),sQuery(id+"F0.wireOp",EDGE,"E7.7.2"),sQuery(id+"F0.wireOp",EDGE,"E7.7.3"),sQuery(id+"F0.wireOp",EDGE,"E7.7.4"),sQuery(id+"F0.wireOp",EDGE,"E7.7.5"),sQuery(id+"F0.wireOp",EDGE,"E7.8.0"),sQuery(id+"F0.wireOp",EDGE,"E7.8.1"),sQuery(id+"F0.wireOp",EDGE,"E7.8.2"),sQuery(id+"F0.wireOp",EDGE,"E7.8.3"),sQuery(id+"F0.wireOp",EDGE,"E7.8.4"),sQuery(id+"F0.wireOp",EDGE,"E7.8.5"),sQuery(id+"F0.wireOp",EDGE,"E7.9.0"),sQuery(id+"F0.wireOp",EDGE,"E7.9.1"),sQuery(id+"F0.wireOp",EDGE,"E7.9.2"),sQuery(id+"F0.wireOp",EDGE,"E7.9.3"),sQuery(id+"F0.wireOp",EDGE,"E7.9.4"),sQuery(id+"F0.wireOp",EDGE,"E7.9.5"),sQuery(id+"F0.wireOp",EDGE,"E7.10.0"),sQuery(id+"F0.wireOp",EDGE,"E7.10.1"),sQuery(id+"F0.wireOp",EDGE,"E7.10.2"),sQuery(id+"F0.wireOp",EDGE,"E7.10.3"),sQuery(id+"F0.wireOp",EDGE,"E7.10.4"),sQuery(id+"F0.wireOp",EDGE,"E7.10.5"),sQuery(id+"F0.wireOp",EDGE,"E7.11.0"),sQuery(id+"F0.wireOp",EDGE,"E7.11.1"),sQuery(id+"F0.wireOp",EDGE,"E7.11.2"),sQuery(id+"F0.wireOp",EDGE,"E7.11.3"),sQuery(id+"F0.wireOp",EDGE,"E7.11.4"),sQuery(id+"F0.wireOp",EDGE,"E7.11.5"),sQuery(id+"F0.wireOp",EDGE,"E7.12.0"),sQuery(id+"F0.wireOp",EDGE,"E7.12.1"),sQuery(id+"F0.wireOp",EDGE,"E7.12.2"),sQuery(id+"F0.wireOp",EDGE,"E7.12.3"),sQuery(id+"F0.wireOp",EDGE,"E7.12.4"),sQuery(id+"F0.wireOp",EDGE,"E7.12.5"),sQuery(id+"F0.wireOp",EDGE,"E7.13.0"),sQuery(id+"F0.wireOp",EDGE,"E7.13.1"),sQuery(id+"F0.wireOp",EDGE,"E7.13.2"),sQuery(id+"F0.wireOp",EDGE,"E7.13.3"),sQuery(id+"F0.wireOp",EDGE,"E7.13.4"),sQuery(id+"F0.wireOp",EDGE,"E7.13.5"),sQuery(id+"F0.wireOp",EDGE,"E7.14.0"),sQuery(id+"F0.wireOp",EDGE,"E7.14.1"),sQuery(id+"F0.wireOp",EDGE,"E7.14.2"),sQuery(id+"F0.wireOp",EDGE,"E7.14.3"),sQuery(id+"F0.wireOp",EDGE,"E7.14.4"),sQuery(id+"F0.wireOp",EDGE,"E7.14.5"),sQuery(id+"F0.wireOp",EDGE,"E7.15.0"),sQuery(id+"F0.wireOp",EDGE,"E7.15.1"),sQuery(id+"F0.wireOp",EDGE,"E7.15.2"),sQuery(id+"F0.wireOp",EDGE,"E7.15.3"),sQuery(id+"F0.wireOp",EDGE,"E7.15.4"),sQuery(id+"F0.wireOp",EDGE,"E7.15.5"),sQuery(id+"F0.wireOp",EDGE,"E7.16.0"),sQuery(id+"F0.wireOp",EDGE,"E7.16.1"),sQuery(id+"F0.wireOp",EDGE,"E7.16.2"),sQuery(id+"F0.wireOp",EDGE,"E7.16.3"),sQuery(id+"F0.wireOp",EDGE,"E7.16.4"),sQuery(id+"F0.wireOp",EDGE,"E7.16.5"),sQuery(id+"F0.wireOp",EDGE,"E7.17.0"),sQuery(id+"F0.wireOp",EDGE,"E7.17.1"),sQuery(id+"F0.wireOp",EDGE,"E7.17.2"),sQuery(id+"F0.wireOp",EDGE,"E7.17.3"),sQuery(id+"F0.wireOp",EDGE,"E7.17.4"),sQuery(id+"F0.wireOp",EDGE,"E7.17.5"),sQuery(id+"F0.wireOp",EDGE,"E7.18.0"),sQuery(id+"F0.wireOp",EDGE,"E7.18.1"),sQuery(id+"F0.wireOp",EDGE,"E7.18.2"),sQuery(id+"F0.wireOp",EDGE,"E7.18.3"),sQuery(id+"F0.wireOp",EDGE,"E7.18.4"),sQuery(id+"F0.wireOp",EDGE,"E7.18.5"),sQuery(id+"F0.wireOp",EDGE,"E7.19.0"),sQuery(id+"F0.wireOp",EDGE,"E7.19.1"),sQuery(id+"F0.wireOp",EDGE,"E7.19.2"),sQuery(id+"F0.wireOp",EDGE,"E7.19.3"),sQuery(id+"F0.wireOp",EDGE,"E7.19.4"),sQuery(id+"F0.wireOp",EDGE,"E7.19.5"),sQuery(id+"F0.wireOp",EDGE,"E7.20.0"),sQuery(id+"F0.wireOp",EDGE,"E7.20.1"),sQuery(id+"F0.wireOp",EDGE,"E7.20.2"),sQuery(id+"F0.wireOp",EDGE,"E7.20.3"),sQuery(id+"F0.wireOp",EDGE,"E7.20.4"),sQuery(id+"F0.wireOp",EDGE,"E7.20.5"),sQuery(id+"F0.wireOp",EDGE,"E7.21.0"),sQuery(id+"F0.wireOp",EDGE,"E7.21.1"),sQuery(id+"F0.wireOp",EDGE,"E7.21.2"),sQuery(id+"F0.wireOp",EDGE,"E7.21.3"),sQuery(id+"F0.wireOp",EDGE,"E7.21.4"),sQuery(id+"F0.wireOp",EDGE,"E7.21.5"),sQuery(id+"F0.wireOp",EDGE,"E7.22.0"),sQuery(id+"F0.wireOp",EDGE,"E7.22.1"),sQuery(id+"F0.wireOp",EDGE,"E7.22.2"),sQuery(id+"F0.wireOp",EDGE,"E7.22.3"),sQuery(id+"F0.wireOp",EDGE,"E7.22.4"),sQuery(id+"F0.wireOp",EDGE,"E7.22.5"),sQuery(id+"F0.wireOp",EDGE,"E7.23.0"),sQuery(id+"F0.wireOp",EDGE,"E7.23.1"),sQuery(id+"F0.wireOp",EDGE,"E7.23.2"),sQuery(id+"F0.wireOp",EDGE,"E7.23.3"),sQuery(id+"F0.wireOp",EDGE,"E7.23.4"),sQuery(id+"F0.wireOp",EDGE,"E7.23.5"),sQuery(id+"F0.wireOp",EDGE,"E7.24.0"),sQuery(id+"F0.wireOp",EDGE,"E7.24.1"),sQuery(id+"F0.wireOp",EDGE,"E7.24.2"),sQuery(id+"F0.wireOp",EDGE,"E7.24.3"),sQuery(id+"F0.wireOp",EDGE,"E7.24.4"),sQuery(id+"F0.wireOp",EDGE,"E7.24.5"),sQuery(id+"F0.wireOp",EDGE,"E7.25.0"),sQuery(id+"F0.wireOp",EDGE,"E7.25.1"),sQuery(id+"F0.wireOp",EDGE,"E7.25.2"),sQuery(id+"F0.wireOp",EDGE,"E7.25.3"),sQuery(id+"F0.wireOp",EDGE,"E7.25.4"),sQuery(id+"F0.wireOp",EDGE,"E7.25.5"),sQuery(id+"F0.wireOp",EDGE,"E7.26.0"),sQuery(id+"F0.wireOp",EDGE,"E7.26.1"),sQuery(id+"F0.wireOp",EDGE,"E7.26.2"),sQuery(id+"F0.wireOp",EDGE,"E7.26.3"),sQuery(id+"F0.wireOp",EDGE,"E7.26.4"),sQuery(id+"F0.wireOp",EDGE,"E7.26.5"),sQuery(id+"F0.wireOp",EDGE,"E7.27.0"),sQuery(id+"F0.wireOp",EDGE,"E7.27.1"),sQuery(id+"F0.wireOp",EDGE,"E7.27.2"),sQuery(id+"F0.wireOp",EDGE,"E7.27.3"),sQuery(id+"F0.wireOp",EDGE,"E7.27.4"),sQuery(id+"F0.wireOp",EDGE,"E7.27.5"),sQuery(id+"F0.wireOp",EDGE,"E7.28.0"),sQuery(id+"F0.wireOp",EDGE,"E7.28.1"),sQuery(id+"F0.wireOp",EDGE,"E7.28.2"),sQuery(id+"F0.wireOp",EDGE,"E7.28.3"),sQuery(id+"F0.wireOp",EDGE,"E7.28.4"),sQuery(id+"F0.wireOp",EDGE,"E7.28.5"),sQuery(id+"F0.wireOp",EDGE,"E7.29.0"),sQuery(id+"F0.wireOp",EDGE,"E7.29.1"),sQuery(id+"F0.wireOp",EDGE,"E7.29.2"),sQuery(id+"F0.wireOp",EDGE,"E7.29.3"),sQuery(id+"F0.wireOp",EDGE,"E7.29.4"),sQuery(id+"F0.wireOp",EDGE,"E7.29.5"),sQuery(id+"F0.wireOp",EDGE,"E7.30.0"),sQuery(id+"F0.wireOp",EDGE,"E7.30.1"),sQuery(id+"F0.wireOp",EDGE,"E7.30.2"),sQuery(id+"F0.wireOp",EDGE,"E7.30.3"),sQuery(id+"F0.wireOp",EDGE,"E7.30.4"),sQuery(id+"F0.wireOp",EDGE,"E7.30.5"),sQuery(id+"F0.wireOp",EDGE,"E7.31.0"),sQuery(id+"F0.wireOp",EDGE,"E7.31.1"),sQuery(id+"F0.wireOp",EDGE,"E7.31.2"),sQuery(id+"F0.wireOp",EDGE,"E7.31.3"),sQuery(id+"F0.wireOp",EDGE,"E7.31.4"),sQuery(id+"F0.wireOp",EDGE,"E7.31.5"),sQuery(id+"F0.wireOp",EDGE,"E7.32.0"),sQuery(id+"F0.wireOp",EDGE,"E7.32.1"),sQuery(id+"F0.wireOp",EDGE,"E7.32.2"),sQuery(id+"F0.wireOp",EDGE,"E7.32.3"),sQuery(id+"F0.wireOp",EDGE,"E7.32.4"),sQuery(id+"F0.wireOp",EDGE,"E7.32.5"),sQuery(id+"F0.wireOp",EDGE,"E7.33.0"),sQuery(id+"F0.wireOp",EDGE,"E7.33.1"),sQuery(id+"F0.wireOp",EDGE,"E7.33.2"),sQuery(id+"F0.wireOp",EDGE,"E7.33.3"),sQuery(id+"F0.wireOp",EDGE,"E7.33.4"),sQuery(id+"F0.wireOp",EDGE,"E7.33.5"),sQuery(id+"F0.wireOp",EDGE,"E7.34.0"),sQuery(id+"F0.wireOp",EDGE,"E7.34.1"),sQuery(id+"F0.wireOp",EDGE,"E7.34.2"),sQuery(id+"F0.wireOp",EDGE,"E7.34.3"),sQuery(id+"F0.wireOp",EDGE,"E7.34.4"),sQuery(id+"F0.wireOp",EDGE,"E7.34.5"),sQuery(id+"F0.wireOp",EDGE,"E7.35.0"),sQuery(id+"F0.wireOp",EDGE,"E7.35.1"),sQuery(id+"F0.wireOp",EDGE,"E7.35.2"),sQuery(id+"F0.wireOp",EDGE,"E7.35.3"),sQuery(id+"F0.wireOp",EDGE,"E7.35.4"),sQuery(id+"F0.wireOp",EDGE,"E7.35.5"),sQuery(id+"F0.wireOp",EDGE,"E7.36.0"),sQuery(id+"F0.wireOp",EDGE,"E7.36.1"),sQuery(id+"F0.wireOp",EDGE,"E7.36.2"),sQuery(id+"F0.wireOp",EDGE,"E7.36.3"),sQuery(id+"F0.wireOp",EDGE,"E7.36.4"),sQuery(id+"F0.wireOp",EDGE,"E7.36.5"),sQuery(id+"F0.wireOp",EDGE,"E7.37.0"),sQuery(id+"F0.wireOp",EDGE,"E7.37.1"),sQuery(id+"F0.wireOp",EDGE,"E7.37.2"),sQuery(id+"F0.wireOp",EDGE,"E7.37.3"),sQuery(id+"F0.wireOp",EDGE,"E7.37.4"),sQuery(id+"F0.wireOp",EDGE,"E7.37.5"),sQuery(id+"F0.wireOp",EDGE,"E7.38.0"),sQuery(id+"F0.wireOp",EDGE,"E7.38.1"),sQuery(id+"F0.wireOp",EDGE,"E7.38.2"),sQuery(id+"F0.wireOp",EDGE,"E7.38.3"),sQuery(id+"F0.wireOp",EDGE,"E7.38.4"),sQuery(id+"F0.wireOp",EDGE,"E7.38.5"),sQuery(id+"F0.wireOp",EDGE,"E7.39.0"),sQuery(id+"F0.wireOp",EDGE,"E7.39.1"),sQuery(id+"F0.wireOp",EDGE,"E7.39.2"),sQuery(id+"F0.wireOp",EDGE,"E7.39.3"),sQuery(id+"F0.wireOp",EDGE,"E7.39.4"),sQuery(id+"F0.wireOp",EDGE,"E7.39.5"),sQuery(id+"F0.wireOp",EDGE,"E7.40.0"),sQuery(id+"F0.wireOp",EDGE,"E7.40.1"),sQuery(id+"F0.wireOp",EDGE,"E7.40.2"),sQuery(id+"F0.wireOp",EDGE,"E7.40.3"),sQuery(id+"F0.wireOp",EDGE,"E7.40.4"),sQuery(id+"F0.wireOp",EDGE,"E7.40.5"),sQuery(id+"F0.wireOp",EDGE,"E7.41.0"),sQuery(id+"F0.wireOp",EDGE,"E7.41.1"),sQuery(id+"F0.wireOp",EDGE,"E7.41.2"),sQuery(id+"F0.wireOp",EDGE,"E7.41.3"),sQuery(id+"F0.wireOp",EDGE,"E7.41.4"),sQuery(id+"F0.wireOp",EDGE,"E7.41.5"),sQuery(id+"F0.wireOp",EDGE,"E7.42.0"),sQuery(id+"F0.wireOp",EDGE,"E7.42.1"),sQuery(id+"F0.wireOp",EDGE,"E7.42.2"),sQuery(id+"F0.wireOp",EDGE,"E7.42.3"),sQuery(id+"F0.wireOp",EDGE,"E7.42.4"),sQuery(id+"F0.wireOp",EDGE,"E7.42.5"),subQ0,sQuery(id+"F0.wireOp",EDGE,"E7.43.1"),sQuery(id+"F0.wireOp",EDGE,"E7.43.2"),sQuery(id+"F0.wireOp",EDGE,"E7.43.3"),sQuery(id+"F0.wireOp",EDGE,"E7.43.4"),sQuery(id+"F0.wireOp",EDGE,"E7.43.5")])],"isStart":false})],"blendedInto":[makeQuery(id+"F1.opExtrude","CAP_FACE",FACE,{"disambiguationData":[OSD([sQuery(id+"F0.wireOp",EDGE,"E1"),sQuery(id+"F0.wireOp",EDGE,"E2"),sQuery(id+"F0.wireOp",EDGE,"E3"),sQuery(id+"F0.wireOp",EDGE,"E4"),sQuery(id+"F0.wireOp",EDGE,"E5"),sQuery(id+"F0.wireOp",EDGE,"E6"),sQuery(id+"F0.wireOp",EDGE,"E7.1.0"),sQuery(id+"F0.wireOp",EDGE,"E7.1.1"),sQuery(id+"F0.wireOp",EDGE,"E7.1.2"),sQuery(id+"F0.wireOp",EDGE,"E7.1.3"),sQuery(id+"F0.wireOp",EDGE,"E7.1.4"),sQuery(id+"F0.wireOp",EDGE,"E7.1.5"),sQuery(id+"F0.wireOp",EDGE,"E7.2.0"),sQuery(id+"F0.wireOp",EDGE,"E7.2.1"),sQuery(id+"F0.wireOp",EDGE,"E7.2.2"),sQuery(id+"F0.wireOp",EDGE,"E7.2.3"),sQuery(id+"F0.wireOp",EDGE,"E7.2.4"),sQuery(id+"F0.wireOp",EDGE,"E7.2.5"),sQuery(id+"F0.wireOp",EDGE,"E7.3.0"),sQuery(id+"F0.wireOp",EDGE,"E7.3.1"),sQuery(id+"F0.wireOp",EDGE,"E7.3.2"),sQuery(id+"F0.wireOp",EDGE,"E7.3.3"),sQuery(id+"F0.wireOp",EDGE,"E7.3.4"),sQuery(id+"F0.wireOp",EDGE,"E7.3.5"),sQuery(id+"F0.wireOp",EDGE,"E7.4.0"),sQuery(id+"F0.wireOp",EDGE,"E7.4.1"),sQuery(id+"F0.wireOp",EDGE,"E7.4.2"),sQuery(id+"F0.wireOp",EDGE,"E7.4.3"),sQuery(id+"F0.wireOp",EDGE,"E7.4.4"),sQuery(id+"F0.wireOp",EDGE,"E7.4.5"),sQuery(id+"F0.wireOp",EDGE,"E7.5.0"),sQuery(id+"F0.wireOp",EDGE,"E7.5.1"),sQuery(id+"F0.wireOp",EDGE,"E7.5.2"),sQuery(id+"F0.wireOp",EDGE,"E7.5.3"),sQuery(id+"F0.wireOp",EDGE,"E7.5.4"),sQuery(id+"F0.wireOp",EDGE,"E7.5.5"),sQuery(id+"F0.wireOp",EDGE,"E7.6.0"),sQuery(id+"F0.wireOp",EDGE,"E7.6.1"),sQuery(id+"F0.wireOp",EDGE,"E7.6.2"),sQuery(id+"F0.wireOp",EDGE,"E7.6.3"),sQuery(id+"F0.wireOp",EDGE,"E7.6.4"),sQuery(id+"F0.wireOp",EDGE,"E7.6.5"),sQuery(id+"F0.wireOp",EDGE,"E7.7.0"),sQuery(id+"F0.wireOp",EDGE,"E7.7.1"),sQuery(id+"F0.wireOp",EDGE,"E7.7.2"),sQuery(id+"F0.wireOp",EDGE,"E7.7.3"),sQuery(id+"F0.wireOp",EDGE,"E7.7.4"),sQuery(id+"F0.wireOp",EDGE,"E7.7.5"),sQuery(id+"F0.wireOp",EDGE,"E7.8.0"),sQuery(id+"F0.wireOp",EDGE,"E7.8.1"),sQuery(id+"F0.wireOp",EDGE,"E7.8.2"),sQuery(id+"F0.wireOp",EDGE,"E7.8.3"),sQuery(id+"F0.wireOp",EDGE,"E7.8.4"),sQuery(id+"F0.wireOp",EDGE,"E7.8.5"),sQuery(id+"F0.wireOp",EDGE,"E7.9.0"),sQuery(id+"F0.wireOp",EDGE,"E7.9.1"),sQuery(id+"F0.wireOp",EDGE,"E7.9.2"),sQuery(id+"F0.wireOp",EDGE,"E7.9.3"),sQuery(id+"F0.wireOp",EDGE,"E7.9.4"),sQuery(id+"F0.wireOp",EDGE,"E7.9.5"),sQuery(id+"F0.wireOp",EDGE,"E7.10.0"),sQuery(id+"F0.wireOp",EDGE,"E7.10.1"),sQuery(id+"F0.wireOp",EDGE,"E7.10.2"),sQuery(id+"F0.wireOp",EDGE,"E7.10.3"),sQuery(id+"F0.wireOp",EDGE,"E7.10.4"),sQuery(id+"F0.wireOp",EDGE,"E7.10.5"),sQuery(id+"F0.wireOp",EDGE,"E7.11.0"),sQuery(id+"F0.wireOp",EDGE,"E7.11.1"),sQuery(id+"F0.wireOp",EDGE,"E7.11.2"),sQuery(id+"F0.wireOp",EDGE,"E7.11.3"),sQuery(id+"F0.wireOp",EDGE,"E7.11.4"),sQuery(id+"F0.wireOp",EDGE,"E7.11.5"),sQuery(id+"F0.wireOp",EDGE,"E7.12.0"),sQuery(id+"F0.wireOp",EDGE,"E7.12.1"),sQuery(id+"F0.wireOp",EDGE,"E7.12.2"),sQuery(id+"F0.wireOp",EDGE,"E7.12.3"),sQuery(id+"F0.wireOp",EDGE,"E7.12.4"),sQuery(id+"F0.wireOp",EDGE,"E7.12.5"),sQuery(id+"F0.wireOp",EDGE,"E7.13.0"),sQuery(id+"F0.wireOp",EDGE,"E7.13.1"),sQuery(id+"F0.wireOp",EDGE,"E7.13.2"),sQuery(id+"F0.wireOp",EDGE,"E7.13.3"),sQuery(id+"F0.wireOp",EDGE,"E7.13.4"),sQuery(id+"F0.wireOp",EDGE,"E7.13.5"),sQuery(id+"F0.wireOp",EDGE,"E7.14.0"),sQuery(id+"F0.wireOp",EDGE,"E7.14.1"),sQuery(id+"F0.wireOp",EDGE,"E7.14.2"),sQuery(id+"F0.wireOp",EDGE,"E7.14.3"),sQuery(id+"F0.wireOp",EDGE,"E7.14.4"),sQuery(id+"F0.wireOp",EDGE,"E7.14.5"),sQuery(id+"F0.wireOp",EDGE,"E7.15.0"),sQuery(id+"F0.wireOp",EDGE,"E7.15.1"),sQuery(id+"F0.wireOp",EDGE,"E7.15.2"),sQuery(id+"F0.wireOp",EDGE,"E7.15.3"),sQuery(id+"F0.wireOp",EDGE,"E7.15.4"),sQuery(id+"F0.wireOp",EDGE,"E7.15.5"),sQuery(id+"F0.wireOp",EDGE,"E7.16.0"),sQuery(id+"F0.wireOp",EDGE,"E7.16.1"),sQuery(id+"F0.wireOp",EDGE,"E7.16.2"),sQuery(id+"F0.wireOp",EDGE,"E7.16.3"),sQuery(id+"F0.wireOp",EDGE,"E7.16.4"),sQuery(id+"F0.wireOp",EDGE,"E7.16.5"),sQuery(id+"F0.wireOp",EDGE,"E7.17.0"),sQuery(id+"F0.wireOp",EDGE,"E7.17.1"),sQuery(id+"F0.wireOp",EDGE,"E7.17.2"),sQuery(id+"F0.wireOp",EDGE,"E7.17.3"),sQuery(id+"F0.wireOp",EDGE,"E7.17.4"),sQuery(id+"F0.wireOp",EDGE,"E7.17.5"),sQuery(id+"F0.wireOp",EDGE,"E7.18.0"),sQuery(id+"F0.wireOp",EDGE,"E7.18.1"),sQuery(id+"F0.wireOp",EDGE,"E7.18.2"),sQuery(id+"F0.wireOp",EDGE,"E7.18.3"),sQuery(id+"F0.wireOp",EDGE,"E7.18.4"),sQuery(id+"F0.wireOp",EDGE,"E7.18.5"),sQuery(id+"F0.wireOp",EDGE,"E7.19.0"),sQuery(id+"F0.wireOp",EDGE,"E7.19.1"),sQuery(id+"F0.wireOp",EDGE,"E7.19.2"),sQuery(id+"F0.wireOp",EDGE,"E7.19.3"),sQuery(id+"F0.wireOp",EDGE,"E7.19.4"),sQuery(id+"F0.wireOp",EDGE,"E7.19.5"),sQuery(id+"F0.wireOp",EDGE,"E7.20.0"),sQuery(id+"F0.wireOp",EDGE,"E7.20.1"),sQuery(id+"F0.wireOp",EDGE,"E7.20.2"),sQuery(id+"F0.wireOp",EDGE,"E7.20.3"),sQuery(id+"F0.wireOp",EDGE,"E7.20.4"),sQuery(id+"F0.wireOp",EDGE,"E7.20.5"),sQuery(id+"F0.wireOp",EDGE,"E7.21.0"),sQuery(id+"F0.wireOp",EDGE,"E7.21.1"),sQuery(id+"F0.wireOp",EDGE,"E7.21.2"),sQuery(id+"F0.wireOp",EDGE,"E7.21.3"),sQuery(id+"F0.wireOp",EDGE,"E7.21.4"),sQuery(id+"F0.wireOp",EDGE,"E7.21.5"),sQuery(id+"F0.wireOp",EDGE,"E7.22.0"),sQuery(id+"F0.wireOp",EDGE,"E7.22.1"),sQuery(id+"F0.wireOp",EDGE,"E7.22.2"),sQuery(id+"F0.wireOp",EDGE,"E7.22.3"),sQuery(id+"F0.wireOp",EDGE,"E7.22.4"),sQuery(id+"F0.wireOp",EDGE,"E7.22.5"),sQuery(id+"F0.wireOp",EDGE,"E7.23.0"),sQuery(id+"F0.wireOp",EDGE,"E7.23.1"),sQuery(id+"F0.wireOp",EDGE,"E7.23.2"),sQuery(id+"F0.wireOp",EDGE,"E7.23.3"),sQuery(id+"F0.wireOp",EDGE,"E7.23.4"),sQuery(id+"F0.wireOp",EDGE,"E7.23.5"),sQuery(id+"F0.wireOp",EDGE,"E7.24.0"),sQuery(id+"F0.wireOp",EDGE,"E7.24.1"),sQuery(id+"F0.wireOp",EDGE,"E7.24.2"),sQuery(id+"F0.wireOp",EDGE,"E7.24.3"),sQuery(id+"F0.wireOp",EDGE,"E7.24.4"),sQuery(id+"F0.wireOp",EDGE,"E7.24.5"),sQuery(id+"F0.wireOp",EDGE,"E7.25.0"),sQuery(id+"F0.wireOp",EDGE,"E7.25.1"),sQuery(id+"F0.wireOp",EDGE,"E7.25.2"),sQuery(id+"F0.wireOp",EDGE,"E7.25.3"),sQuery(id+"F0.wireOp",EDGE,"E7.25.4"),sQuery(id+"F0.wireOp",EDGE,"E7.25.5"),sQuery(id+"F0.wireOp",EDGE,"E7.26.0"),sQuery(id+"F0.wireOp",EDGE,"E7.26.1"),sQuery(id+"F0.wireOp",EDGE,"E7.26.2"),sQuery(id+"F0.wireOp",EDGE,"E7.26.3"),sQuery(id+"F0.wireOp",EDGE,"E7.26.4"),sQuery(id+"F0.wireOp",EDGE,"E7.26.5"),sQuery(id+"F0.wireOp",EDGE,"E7.27.0"),sQuery(id+"F0.wireOp",EDGE,"E7.27.1"),sQuery(id+"F0.wireOp",EDGE,"E7.27.2"),sQuery(id+"F0.wireOp",EDGE,"E7.27.3"),sQuery(id+"F0.wireOp",EDGE,"E7.27.4"),sQuery(id+"F0.wireOp",EDGE,"E7.27.5"),sQuery(id+"F0.wireOp",EDGE,"E7.28.0"),sQuery(id+"F0.wireOp",EDGE,"E7.28.1"),sQuery(id+"F0.wireOp",EDGE,"E7.28.2"),sQuery(id+"F0.wireOp",EDGE,"E7.28.3"),sQuery(id+"F0.wireOp",EDGE,"E7.28.4"),sQuery(id+"F0.wireOp",EDGE,"E7.28.5"),sQuery(id+"F0.wireOp",EDGE,"E7.29.0"),sQuery(id+"F0.wireOp",EDGE,"E7.29.1"),sQuery(id+"F0.wireOp",EDGE,"E7.29.2"),sQuery(id+"F0.wireOp",EDGE,"E7.29.3"),sQuery(id+"F0.wireOp",EDGE,"E7.29.4"),sQuery(id+"F0.wireOp",EDGE,"E7.29.5"),sQuery(id+"F0.wireOp",EDGE,"E7.30.0"),sQuery(id+"F0.wireOp",EDGE,"E7.30.1"),sQuery(id+"F0.wireOp",EDGE,"E7.30.2"),sQuery(id+"F0.wireOp",EDGE,"E7.30.3"),sQuery(id+"F0.wireOp",EDGE,"E7.30.4"),sQuery(id+"F0.wireOp",EDGE,"E7.30.5"),sQuery(id+"F0.wireOp",EDGE,"E7.31.0"),sQuery(id+"F0.wireOp",EDGE,"E7.31.1"),sQuery(id+"F0.wireOp",EDGE,"E7.31.2"),sQuery(id+"F0.wireOp",EDGE,"E7.31.3"),sQuery(id+"F0.wireOp",EDGE,"E7.31.4"),sQuery(id+"F0.wireOp",EDGE,"E7.31.5"),sQuery(id+"F0.wireOp",EDGE,"E7.32.0"),sQuery(id+"F0.wireOp",EDGE,"E7.32.1"),sQuery(id+"F0.wireOp",EDGE,"E7.32.2"),sQuery(id+"F0.wireOp",EDGE,"E7.32.3"),sQuery(id+"F0.wireOp",EDGE,"E7.32.4"),sQuery(id+"F0.wireOp",EDGE,"E7.32.5"),sQuery(id+"F0.wireOp",EDGE,"E7.33.0"),sQuery(id+"F0.wireOp",EDGE,"E7.33.1"),sQuery(id+"F0.wireOp",EDGE,"E7.33.2"),sQuery(id+"F0.wireOp",EDGE,"E7.33.3"),sQuery(id+"F0.wireOp",EDGE,"E7.33.4"),sQuery(id+"F0.wireOp",EDGE,"E7.33.5"),sQuery(id+"F0.wireOp",EDGE,"E7.34.0"),sQuery(id+"F0.wireOp",EDGE,"E7.34.1"),sQuery(id+"F0.wireOp",EDGE,"E7.34.2"),sQuery(id+"F0.wireOp",EDGE,"E7.34.3"),sQuery(id+"F0.wireOp",EDGE,"E7.34.4"),sQuery(id+"F0.wireOp",EDGE,"E7.34.5"),sQuery(id+"F0.wireOp",EDGE,"E7.35.0"),sQuery(id+"F0.wireOp",EDGE,"E7.35.1"),sQuery(id+"F0.wireOp",EDGE,"E7.35.2"),sQuery(id+"F0.wireOp",EDGE,"E7.35.3"),sQuery(id+"F0.wireOp",EDGE,"E7.35.4"),sQuery(id+"F0.wireOp",EDGE,"E7.35.5"),sQuery(id+"F0.wireOp",EDGE,"E7.36.0"),sQuery(id+"F0.wireOp",EDGE,"E7.36.1"),sQuery(id+"F0.wireOp",EDGE,"E7.36.2"),sQuery(id+"F0.wireOp",EDGE,"E7.36.3"),sQuery(id+"F0.wireOp",EDGE,"E7.36.4"),sQuery(id+"F0.wireOp",EDGE,"E7.36.5"),sQuery(id+"F0.wireOp",EDGE,"E7.37.0"),sQuery(id+"F0.wireOp",EDGE,"E7.37.1"),sQuery(id+"F0.wireOp",EDGE,"E7.37.2"),sQuery(id+"F0.wireOp",EDGE,"E7.37.3"),sQuery(id+"F0.wireOp",EDGE,"E7.37.4"),sQuery(id+"F0.wireOp",EDGE,"E7.37.5"),sQuery(id+"F0.wireOp",EDGE,"E7.38.0"),sQuery(id+"F0.wireOp",EDGE,"E7.38.1"),sQuery(id+"F0.wireOp",EDGE,"E7.38.2"),sQuery(id+"F0.wireOp",EDGE,"E7.38.3"),sQuery(id+"F0.wireOp",EDGE,"E7.38.4"),sQuery(id+"F0.wireOp",EDGE,"E7.38.5"),sQuery(id+"F0.wireOp",EDGE,"E7.39.0"),sQuery(id+"F0.wireOp",EDGE,"E7.39.1"),sQuery(id+"F0.wireOp",EDGE,"E7.39.2"),sQuery(id+"F0.wireOp",EDGE,"E7.39.3"),sQuery(id+"F0.wireOp",EDGE,"E7.39.4"),sQuery(id+"F0.wireOp",EDGE,"E7.39.5"),sQuery(id+"F0.wireOp",EDGE,"E7.40.0"),sQuery(id+"F0.wireOp",EDGE,"E7.40.1"),sQuery(id+"F0.wireOp",EDGE,"E7.40.2"),sQuery(id+"F0.wireOp",EDGE,"E7.40.3"),sQuery(id+"F0.wireOp",EDGE,"E7.40.4"),sQuery(id+"F0.wireOp",EDGE,"E7.40.5"),sQuery(id+"F0.wireOp",EDGE,"E7.41.0"),sQuery(id+"F0.wireOp",EDGE,"E7.41.1"),sQuery(id+"F0.wireOp",EDGE,"E7.41.2"),sQuery(id+"F0.wireOp",EDGE,"E7.41.3"),sQuery(id+"F0.wireOp",EDGE,"E7.41.4"),sQuery(id+"F0.wireOp",EDGE,"E7.41.5"),sQuery(id+"F0.wireOp",EDGE,"E7.42.0"),sQuery(id+"F0.wireOp",EDGE,"E7.42.1"),sQuery(id+"F0.wireOp",EDGE,"E7.42.2"),sQuery(id+"F0.wireOp",EDGE,"E7.42.3"),sQuery(id+"F0.wireOp",EDGE,"E7.42.4"),sQuery(id+"F0.wireOp",EDGE,"E7.42.5"),subQ0,sQuery(id+"F0.wireOp",EDGE,"E7.43.1"),sQuery(id+"F0.wireOp",EDGE,"E7.43.2"),sQuery(id+"F0.wireOp",EDGE,"E7.43.3"),sQuery(id+"F0.wireOp",EDGE,"E7.43.4"),sQuery(id+"F0.wireOp",EDGE,"E7.43.5")])],"isStart":false})]});}
            var Q1;
            {var subQ0=sQuery(id+"F0.wireOp",EDGE,"E7.41.0");Q1=makeQuery(id+"F2.opChamfer","BLEND_EDGE",EDGE,{"blendedFrom":[makeQuery(id+"F1.opExtrude","CAP_EDGE",EDGE,{"disambiguationData":[OSD([subQ0])],"isStart":false}),makeQuery(id+"F1.opExtrude","CAP_FACE",FACE,{"disambiguationData":[OSD([sQuery(id+"F0.wireOp",EDGE,"E1"),sQuery(id+"F0.wireOp",EDGE,"E2"),sQuery(id+"F0.wireOp",EDGE,"E3"),sQuery(id+"F0.wireOp",EDGE,"E4"),sQuery(id+"F0.wireOp",EDGE,"E5"),sQuery(id+"F0.wireOp",EDGE,"E6"),sQuery(id+"F0.wireOp",EDGE,"E7.1.0"),sQuery(id+"F0.wireOp",EDGE,"E7.1.1"),sQuery(id+"F0.wireOp",EDGE,"E7.1.2"),sQuery(id+"F0.wireOp",EDGE,"E7.1.3"),sQuery(id+"F0.wireOp",EDGE,"E7.1.4"),sQuery(id+"F0.wireOp",EDGE,"E7.1.5"),sQuery(id+"F0.wireOp",EDGE,"E7.2.0"),sQuery(id+"F0.wireOp",EDGE,"E7.2.1"),sQuery(id+"F0.wireOp",EDGE,"E7.2.2"),sQuery(id+"F0.wireOp",EDGE,"E7.2.3"),sQuery(id+"F0.wireOp",EDGE,"E7.2.4"),sQuery(id+"F0.wireOp",EDGE,"E7.2.5"),sQuery(id+"F0.wireOp",EDGE,"E7.3.0"),sQuery(id+"F0.wireOp",EDGE,"E7.3.1"),sQuery(id+"F0.wireOp",EDGE,"E7.3.2"),sQuery(id+"F0.wireOp",EDGE,"E7.3.3"),sQuery(id+"F0.wireOp",EDGE,"E7.3.4"),sQuery(id+"F0.wireOp",EDGE,"E7.3.5"),sQuery(id+"F0.wireOp",EDGE,"E7.4.0"),sQuery(id+"F0.wireOp",EDGE,"E7.4.1"),sQuery(id+"F0.wireOp",EDGE,"E7.4.2"),sQuery(id+"F0.wireOp",EDGE,"E7.4.3"),sQuery(id+"F0.wireOp",EDGE,"E7.4.4"),sQuery(id+"F0.wireOp",EDGE,"E7.4.5"),sQuery(id+"F0.wireOp",EDGE,"E7.5.0"),sQuery(id+"F0.wireOp",EDGE,"E7.5.1"),sQuery(id+"F0.wireOp",EDGE,"E7.5.2"),sQuery(id+"F0.wireOp",EDGE,"E7.5.3"),sQuery(id+"F0.wireOp",EDGE,"E7.5.4"),sQuery(id+"F0.wireOp",EDGE,"E7.5.5"),sQuery(id+"F0.wireOp",EDGE,"E7.6.0"),sQuery(id+"F0.wireOp",EDGE,"E7.6.1"),sQuery(id+"F0.wireOp",EDGE,"E7.6.2"),sQuery(id+"F0.wireOp",EDGE,"E7.6.3"),sQuery(id+"F0.wireOp",EDGE,"E7.6.4"),sQuery(id+"F0.wireOp",EDGE,"E7.6.5"),sQuery(id+"F0.wireOp",EDGE,"E7.7.0"),sQuery(id+"F0.wireOp",EDGE,"E7.7.1"),sQuery(id+"F0.wireOp",EDGE,"E7.7.2"),sQuery(id+"F0.wireOp",EDGE,"E7.7.3"),sQuery(id+"F0.wireOp",EDGE,"E7.7.4"),sQuery(id+"F0.wireOp",EDGE,"E7.7.5"),sQuery(id+"F0.wireOp",EDGE,"E7.8.0"),sQuery(id+"F0.wireOp",EDGE,"E7.8.1"),sQuery(id+"F0.wireOp",EDGE,"E7.8.2"),sQuery(id+"F0.wireOp",EDGE,"E7.8.3"),sQuery(id+"F0.wireOp",EDGE,"E7.8.4"),sQuery(id+"F0.wireOp",EDGE,"E7.8.5"),sQuery(id+"F0.wireOp",EDGE,"E7.9.0"),sQuery(id+"F0.wireOp",EDGE,"E7.9.1"),sQuery(id+"F0.wireOp",EDGE,"E7.9.2"),sQuery(id+"F0.wireOp",EDGE,"E7.9.3"),sQuery(id+"F0.wireOp",EDGE,"E7.9.4"),sQuery(id+"F0.wireOp",EDGE,"E7.9.5"),sQuery(id+"F0.wireOp",EDGE,"E7.10.0"),sQuery(id+"F0.wireOp",EDGE,"E7.10.1"),sQuery(id+"F0.wireOp",EDGE,"E7.10.2"),sQuery(id+"F0.wireOp",EDGE,"E7.10.3"),sQuery(id+"F0.wireOp",EDGE,"E7.10.4"),sQuery(id+"F0.wireOp",EDGE,"E7.10.5"),sQuery(id+"F0.wireOp",EDGE,"E7.11.0"),sQuery(id+"F0.wireOp",EDGE,"E7.11.1"),sQuery(id+"F0.wireOp",EDGE,"E7.11.2"),sQuery(id+"F0.wireOp",EDGE,"E7.11.3"),sQuery(id+"F0.wireOp",EDGE,"E7.11.4"),sQuery(id+"F0.wireOp",EDGE,"E7.11.5"),sQuery(id+"F0.wireOp",EDGE,"E7.12.0"),sQuery(id+"F0.wireOp",EDGE,"E7.12.1"),sQuery(id+"F0.wireOp",EDGE,"E7.12.2"),sQuery(id+"F0.wireOp",EDGE,"E7.12.3"),sQuery(id+"F0.wireOp",EDGE,"E7.12.4"),sQuery(id+"F0.wireOp",EDGE,"E7.12.5"),sQuery(id+"F0.wireOp",EDGE,"E7.13.0"),sQuery(id+"F0.wireOp",EDGE,"E7.13.1"),sQuery(id+"F0.wireOp",EDGE,"E7.13.2"),sQuery(id+"F0.wireOp",EDGE,"E7.13.3"),sQuery(id+"F0.wireOp",EDGE,"E7.13.4"),sQuery(id+"F0.wireOp",EDGE,"E7.13.5"),sQuery(id+"F0.wireOp",EDGE,"E7.14.0"),sQuery(id+"F0.wireOp",EDGE,"E7.14.1"),sQuery(id+"F0.wireOp",EDGE,"E7.14.2"),sQuery(id+"F0.wireOp",EDGE,"E7.14.3"),sQuery(id+"F0.wireOp",EDGE,"E7.14.4"),sQuery(id+"F0.wireOp",EDGE,"E7.14.5"),sQuery(id+"F0.wireOp",EDGE,"E7.15.0"),sQuery(id+"F0.wireOp",EDGE,"E7.15.1"),sQuery(id+"F0.wireOp",EDGE,"E7.15.2"),sQuery(id+"F0.wireOp",EDGE,"E7.15.3"),sQuery(id+"F0.wireOp",EDGE,"E7.15.4"),sQuery(id+"F0.wireOp",EDGE,"E7.15.5"),sQuery(id+"F0.wireOp",EDGE,"E7.16.0"),sQuery(id+"F0.wireOp",EDGE,"E7.16.1"),sQuery(id+"F0.wireOp",EDGE,"E7.16.2"),sQuery(id+"F0.wireOp",EDGE,"E7.16.3"),sQuery(id+"F0.wireOp",EDGE,"E7.16.4"),sQuery(id+"F0.wireOp",EDGE,"E7.16.5"),sQuery(id+"F0.wireOp",EDGE,"E7.17.0"),sQuery(id+"F0.wireOp",EDGE,"E7.17.1"),sQuery(id+"F0.wireOp",EDGE,"E7.17.2"),sQuery(id+"F0.wireOp",EDGE,"E7.17.3"),sQuery(id+"F0.wireOp",EDGE,"E7.17.4"),sQuery(id+"F0.wireOp",EDGE,"E7.17.5"),sQuery(id+"F0.wireOp",EDGE,"E7.18.0"),sQuery(id+"F0.wireOp",EDGE,"E7.18.1"),sQuery(id+"F0.wireOp",EDGE,"E7.18.2"),sQuery(id+"F0.wireOp",EDGE,"E7.18.3"),sQuery(id+"F0.wireOp",EDGE,"E7.18.4"),sQuery(id+"F0.wireOp",EDGE,"E7.18.5"),sQuery(id+"F0.wireOp",EDGE,"E7.19.0"),sQuery(id+"F0.wireOp",EDGE,"E7.19.1"),sQuery(id+"F0.wireOp",EDGE,"E7.19.2"),sQuery(id+"F0.wireOp",EDGE,"E7.19.3"),sQuery(id+"F0.wireOp",EDGE,"E7.19.4"),sQuery(id+"F0.wireOp",EDGE,"E7.19.5"),sQuery(id+"F0.wireOp",EDGE,"E7.20.0"),sQuery(id+"F0.wireOp",EDGE,"E7.20.1"),sQuery(id+"F0.wireOp",EDGE,"E7.20.2"),sQuery(id+"F0.wireOp",EDGE,"E7.20.3"),sQuery(id+"F0.wireOp",EDGE,"E7.20.4"),sQuery(id+"F0.wireOp",EDGE,"E7.20.5"),sQuery(id+"F0.wireOp",EDGE,"E7.21.0"),sQuery(id+"F0.wireOp",EDGE,"E7.21.1"),sQuery(id+"F0.wireOp",EDGE,"E7.21.2"),sQuery(id+"F0.wireOp",EDGE,"E7.21.3"),sQuery(id+"F0.wireOp",EDGE,"E7.21.4"),sQuery(id+"F0.wireOp",EDGE,"E7.21.5"),sQuery(id+"F0.wireOp",EDGE,"E7.22.0"),sQuery(id+"F0.wireOp",EDGE,"E7.22.1"),sQuery(id+"F0.wireOp",EDGE,"E7.22.2"),sQuery(id+"F0.wireOp",EDGE,"E7.22.3"),sQuery(id+"F0.wireOp",EDGE,"E7.22.4"),sQuery(id+"F0.wireOp",EDGE,"E7.22.5"),sQuery(id+"F0.wireOp",EDGE,"E7.23.0"),sQuery(id+"F0.wireOp",EDGE,"E7.23.1"),sQuery(id+"F0.wireOp",EDGE,"E7.23.2"),sQuery(id+"F0.wireOp",EDGE,"E7.23.3"),sQuery(id+"F0.wireOp",EDGE,"E7.23.4"),sQuery(id+"F0.wireOp",EDGE,"E7.23.5"),sQuery(id+"F0.wireOp",EDGE,"E7.24.0"),sQuery(id+"F0.wireOp",EDGE,"E7.24.1"),sQuery(id+"F0.wireOp",EDGE,"E7.24.2"),sQuery(id+"F0.wireOp",EDGE,"E7.24.3"),sQuery(id+"F0.wireOp",EDGE,"E7.24.4"),sQuery(id+"F0.wireOp",EDGE,"E7.24.5"),sQuery(id+"F0.wireOp",EDGE,"E7.25.0"),sQuery(id+"F0.wireOp",EDGE,"E7.25.1"),sQuery(id+"F0.wireOp",EDGE,"E7.25.2"),sQuery(id+"F0.wireOp",EDGE,"E7.25.3"),sQuery(id+"F0.wireOp",EDGE,"E7.25.4"),sQuery(id+"F0.wireOp",EDGE,"E7.25.5"),sQuery(id+"F0.wireOp",EDGE,"E7.26.0"),sQuery(id+"F0.wireOp",EDGE,"E7.26.1"),sQuery(id+"F0.wireOp",EDGE,"E7.26.2"),sQuery(id+"F0.wireOp",EDGE,"E7.26.3"),sQuery(id+"F0.wireOp",EDGE,"E7.26.4"),sQuery(id+"F0.wireOp",EDGE,"E7.26.5"),sQuery(id+"F0.wireOp",EDGE,"E7.27.0"),sQuery(id+"F0.wireOp",EDGE,"E7.27.1"),sQuery(id+"F0.wireOp",EDGE,"E7.27.2"),sQuery(id+"F0.wireOp",EDGE,"E7.27.3"),sQuery(id+"F0.wireOp",EDGE,"E7.27.4"),sQuery(id+"F0.wireOp",EDGE,"E7.27.5"),sQuery(id+"F0.wireOp",EDGE,"E7.28.0"),sQuery(id+"F0.wireOp",EDGE,"E7.28.1"),sQuery(id+"F0.wireOp",EDGE,"E7.28.2"),sQuery(id+"F0.wireOp",EDGE,"E7.28.3"),sQuery(id+"F0.wireOp",EDGE,"E7.28.4"),sQuery(id+"F0.wireOp",EDGE,"E7.28.5"),sQuery(id+"F0.wireOp",EDGE,"E7.29.0"),sQuery(id+"F0.wireOp",EDGE,"E7.29.1"),sQuery(id+"F0.wireOp",EDGE,"E7.29.2"),sQuery(id+"F0.wireOp",EDGE,"E7.29.3"),sQuery(id+"F0.wireOp",EDGE,"E7.29.4"),sQuery(id+"F0.wireOp",EDGE,"E7.29.5"),sQuery(id+"F0.wireOp",EDGE,"E7.30.0"),sQuery(id+"F0.wireOp",EDGE,"E7.30.1"),sQuery(id+"F0.wireOp",EDGE,"E7.30.2"),sQuery(id+"F0.wireOp",EDGE,"E7.30.3"),sQuery(id+"F0.wireOp",EDGE,"E7.30.4"),sQuery(id+"F0.wireOp",EDGE,"E7.30.5"),sQuery(id+"F0.wireOp",EDGE,"E7.31.0"),sQuery(id+"F0.wireOp",EDGE,"E7.31.1"),sQuery(id+"F0.wireOp",EDGE,"E7.31.2"),sQuery(id+"F0.wireOp",EDGE,"E7.31.3"),sQuery(id+"F0.wireOp",EDGE,"E7.31.4"),sQuery(id+"F0.wireOp",EDGE,"E7.31.5"),sQuery(id+"F0.wireOp",EDGE,"E7.32.0"),sQuery(id+"F0.wireOp",EDGE,"E7.32.1"),sQuery(id+"F0.wireOp",EDGE,"E7.32.2"),sQuery(id+"F0.wireOp",EDGE,"E7.32.3"),sQuery(id+"F0.wireOp",EDGE,"E7.32.4"),sQuery(id+"F0.wireOp",EDGE,"E7.32.5"),sQuery(id+"F0.wireOp",EDGE,"E7.33.0"),sQuery(id+"F0.wireOp",EDGE,"E7.33.1"),sQuery(id+"F0.wireOp",EDGE,"E7.33.2"),sQuery(id+"F0.wireOp",EDGE,"E7.33.3"),sQuery(id+"F0.wireOp",EDGE,"E7.33.4"),sQuery(id+"F0.wireOp",EDGE,"E7.33.5"),sQuery(id+"F0.wireOp",EDGE,"E7.34.0"),sQuery(id+"F0.wireOp",EDGE,"E7.34.1"),sQuery(id+"F0.wireOp",EDGE,"E7.34.2"),sQuery(id+"F0.wireOp",EDGE,"E7.34.3"),sQuery(id+"F0.wireOp",EDGE,"E7.34.4"),sQuery(id+"F0.wireOp",EDGE,"E7.34.5"),sQuery(id+"F0.wireOp",EDGE,"E7.35.0"),sQuery(id+"F0.wireOp",EDGE,"E7.35.1"),sQuery(id+"F0.wireOp",EDGE,"E7.35.2"),sQuery(id+"F0.wireOp",EDGE,"E7.35.3"),sQuery(id+"F0.wireOp",EDGE,"E7.35.4"),sQuery(id+"F0.wireOp",EDGE,"E7.35.5"),sQuery(id+"F0.wireOp",EDGE,"E7.36.0"),sQuery(id+"F0.wireOp",EDGE,"E7.36.1"),sQuery(id+"F0.wireOp",EDGE,"E7.36.2"),sQuery(id+"F0.wireOp",EDGE,"E7.36.3"),sQuery(id+"F0.wireOp",EDGE,"E7.36.4"),sQuery(id+"F0.wireOp",EDGE,"E7.36.5"),sQuery(id+"F0.wireOp",EDGE,"E7.37.0"),sQuery(id+"F0.wireOp",EDGE,"E7.37.1"),sQuery(id+"F0.wireOp",EDGE,"E7.37.2"),sQuery(id+"F0.wireOp",EDGE,"E7.37.3"),sQuery(id+"F0.wireOp",EDGE,"E7.37.4"),sQuery(id+"F0.wireOp",EDGE,"E7.37.5"),sQuery(id+"F0.wireOp",EDGE,"E7.38.0"),sQuery(id+"F0.wireOp",EDGE,"E7.38.1"),sQuery(id+"F0.wireOp",EDGE,"E7.38.2"),sQuery(id+"F0.wireOp",EDGE,"E7.38.3"),sQuery(id+"F0.wireOp",EDGE,"E7.38.4"),sQuery(id+"F0.wireOp",EDGE,"E7.38.5"),sQuery(id+"F0.wireOp",EDGE,"E7.39.0"),sQuery(id+"F0.wireOp",EDGE,"E7.39.1"),sQuery(id+"F0.wireOp",EDGE,"E7.39.2"),sQuery(id+"F0.wireOp",EDGE,"E7.39.3"),sQuery(id+"F0.wireOp",EDGE,"E7.39.4"),sQuery(id+"F0.wireOp",EDGE,"E7.39.5"),sQuery(id+"F0.wireOp",EDGE,"E7.40.0"),sQuery(id+"F0.wireOp",EDGE,"E7.40.1"),sQuery(id+"F0.wireOp",EDGE,"E7.40.2"),sQuery(id+"F0.wireOp",EDGE,"E7.40.3"),sQuery(id+"F0.wireOp",EDGE,"E7.40.4"),sQuery(id+"F0.wireOp",EDGE,"E7.40.5"),subQ0,sQuery(id+"F0.wireOp",EDGE,"E7.41.1"),sQuery(id+"F0.wireOp",EDGE,"E7.41.2"),sQuery(id+"F0.wireOp",EDGE,"E7.41.3"),sQuery(id+"F0.wireOp",EDGE,"E7.41.4"),sQuery(id+"F0.wireOp",EDGE,"E7.41.5"),sQuery(id+"F0.wireOp",EDGE,"E7.42.0"),sQuery(id+"F0.wireOp",EDGE,"E7.42.1"),sQuery(id+"F0.wireOp",EDGE,"E7.42.2"),sQuery(id+"F0.wireOp",EDGE,"E7.42.3"),sQuery(id+"F0.wireOp",EDGE,"E7.42.4"),sQuery(id+"F0.wireOp",EDGE,"E7.42.5"),sQuery(id+"F0.wireOp",EDGE,"E7.43.0"),sQuery(id+"F0.wireOp",EDGE,"E7.43.1"),sQuery(id+"F0.wireOp",EDGE,"E7.43.2"),sQuery(id+"F0.wireOp",EDGE,"E7.43.3"),sQuery(id+"F0.wireOp",EDGE,"E7.43.4"),sQuery(id+"F0.wireOp",EDGE,"E7.43.5")])],"isStart":false})],"blendedInto":[makeQuery(id+"F1.opExtrude","CAP_FACE",FACE,{"disambiguationData":[OSD([sQuery(id+"F0.wireOp",EDGE,"E1"),sQuery(id+"F0.wireOp",EDGE,"E2"),sQuery(id+"F0.wireOp",EDGE,"E3"),sQuery(id+"F0.wireOp",EDGE,"E4"),sQuery(id+"F0.wireOp",EDGE,"E5"),sQuery(id+"F0.wireOp",EDGE,"E6"),sQuery(id+"F0.wireOp",EDGE,"E7.1.0"),sQuery(id+"F0.wireOp",EDGE,"E7.1.1"),sQuery(id+"F0.wireOp",EDGE,"E7.1.2"),sQuery(id+"F0.wireOp",EDGE,"E7.1.3"),sQuery(id+"F0.wireOp",EDGE,"E7.1.4"),sQuery(id+"F0.wireOp",EDGE,"E7.1.5"),sQuery(id+"F0.wireOp",EDGE,"E7.2.0"),sQuery(id+"F0.wireOp",EDGE,"E7.2.1"),sQuery(id+"F0.wireOp",EDGE,"E7.2.2"),sQuery(id+"F0.wireOp",EDGE,"E7.2.3"),sQuery(id+"F0.wireOp",EDGE,"E7.2.4"),sQuery(id+"F0.wireOp",EDGE,"E7.2.5"),sQuery(id+"F0.wireOp",EDGE,"E7.3.0"),sQuery(id+"F0.wireOp",EDGE,"E7.3.1"),sQuery(id+"F0.wireOp",EDGE,"E7.3.2"),sQuery(id+"F0.wireOp",EDGE,"E7.3.3"),sQuery(id+"F0.wireOp",EDGE,"E7.3.4"),sQuery(id+"F0.wireOp",EDGE,"E7.3.5"),sQuery(id+"F0.wireOp",EDGE,"E7.4.0"),sQuery(id+"F0.wireOp",EDGE,"E7.4.1"),sQuery(id+"F0.wireOp",EDGE,"E7.4.2"),sQuery(id+"F0.wireOp",EDGE,"E7.4.3"),sQuery(id+"F0.wireOp",EDGE,"E7.4.4"),sQuery(id+"F0.wireOp",EDGE,"E7.4.5"),sQuery(id+"F0.wireOp",EDGE,"E7.5.0"),sQuery(id+"F0.wireOp",EDGE,"E7.5.1"),sQuery(id+"F0.wireOp",EDGE,"E7.5.2"),sQuery(id+"F0.wireOp",EDGE,"E7.5.3"),sQuery(id+"F0.wireOp",EDGE,"E7.5.4"),sQuery(id+"F0.wireOp",EDGE,"E7.5.5"),sQuery(id+"F0.wireOp",EDGE,"E7.6.0"),sQuery(id+"F0.wireOp",EDGE,"E7.6.1"),sQuery(id+"F0.wireOp",EDGE,"E7.6.2"),sQuery(id+"F0.wireOp",EDGE,"E7.6.3"),sQuery(id+"F0.wireOp",EDGE,"E7.6.4"),sQuery(id+"F0.wireOp",EDGE,"E7.6.5"),sQuery(id+"F0.wireOp",EDGE,"E7.7.0"),sQuery(id+"F0.wireOp",EDGE,"E7.7.1"),sQuery(id+"F0.wireOp",EDGE,"E7.7.2"),sQuery(id+"F0.wireOp",EDGE,"E7.7.3"),sQuery(id+"F0.wireOp",EDGE,"E7.7.4"),sQuery(id+"F0.wireOp",EDGE,"E7.7.5"),sQuery(id+"F0.wireOp",EDGE,"E7.8.0"),sQuery(id+"F0.wireOp",EDGE,"E7.8.1"),sQuery(id+"F0.wireOp",EDGE,"E7.8.2"),sQuery(id+"F0.wireOp",EDGE,"E7.8.3"),sQuery(id+"F0.wireOp",EDGE,"E7.8.4"),sQuery(id+"F0.wireOp",EDGE,"E7.8.5"),sQuery(id+"F0.wireOp",EDGE,"E7.9.0"),sQuery(id+"F0.wireOp",EDGE,"E7.9.1"),sQuery(id+"F0.wireOp",EDGE,"E7.9.2"),sQuery(id+"F0.wireOp",EDGE,"E7.9.3"),sQuery(id+"F0.wireOp",EDGE,"E7.9.4"),sQuery(id+"F0.wireOp",EDGE,"E7.9.5"),sQuery(id+"F0.wireOp",EDGE,"E7.10.0"),sQuery(id+"F0.wireOp",EDGE,"E7.10.1"),sQuery(id+"F0.wireOp",EDGE,"E7.10.2"),sQuery(id+"F0.wireOp",EDGE,"E7.10.3"),sQuery(id+"F0.wireOp",EDGE,"E7.10.4"),sQuery(id+"F0.wireOp",EDGE,"E7.10.5"),sQuery(id+"F0.wireOp",EDGE,"E7.11.0"),sQuery(id+"F0.wireOp",EDGE,"E7.11.1"),sQuery(id+"F0.wireOp",EDGE,"E7.11.2"),sQuery(id+"F0.wireOp",EDGE,"E7.11.3"),sQuery(id+"F0.wireOp",EDGE,"E7.11.4"),sQuery(id+"F0.wireOp",EDGE,"E7.11.5"),sQuery(id+"F0.wireOp",EDGE,"E7.12.0"),sQuery(id+"F0.wireOp",EDGE,"E7.12.1"),sQuery(id+"F0.wireOp",EDGE,"E7.12.2"),sQuery(id+"F0.wireOp",EDGE,"E7.12.3"),sQuery(id+"F0.wireOp",EDGE,"E7.12.4"),sQuery(id+"F0.wireOp",EDGE,"E7.12.5"),sQuery(id+"F0.wireOp",EDGE,"E7.13.0"),sQuery(id+"F0.wireOp",EDGE,"E7.13.1"),sQuery(id+"F0.wireOp",EDGE,"E7.13.2"),sQuery(id+"F0.wireOp",EDGE,"E7.13.3"),sQuery(id+"F0.wireOp",EDGE,"E7.13.4"),sQuery(id+"F0.wireOp",EDGE,"E7.13.5"),sQuery(id+"F0.wireOp",EDGE,"E7.14.0"),sQuery(id+"F0.wireOp",EDGE,"E7.14.1"),sQuery(id+"F0.wireOp",EDGE,"E7.14.2"),sQuery(id+"F0.wireOp",EDGE,"E7.14.3"),sQuery(id+"F0.wireOp",EDGE,"E7.14.4"),sQuery(id+"F0.wireOp",EDGE,"E7.14.5"),sQuery(id+"F0.wireOp",EDGE,"E7.15.0"),sQuery(id+"F0.wireOp",EDGE,"E7.15.1"),sQuery(id+"F0.wireOp",EDGE,"E7.15.2"),sQuery(id+"F0.wireOp",EDGE,"E7.15.3"),sQuery(id+"F0.wireOp",EDGE,"E7.15.4"),sQuery(id+"F0.wireOp",EDGE,"E7.15.5"),sQuery(id+"F0.wireOp",EDGE,"E7.16.0"),sQuery(id+"F0.wireOp",EDGE,"E7.16.1"),sQuery(id+"F0.wireOp",EDGE,"E7.16.2"),sQuery(id+"F0.wireOp",EDGE,"E7.16.3"),sQuery(id+"F0.wireOp",EDGE,"E7.16.4"),sQuery(id+"F0.wireOp",EDGE,"E7.16.5"),sQuery(id+"F0.wireOp",EDGE,"E7.17.0"),sQuery(id+"F0.wireOp",EDGE,"E7.17.1"),sQuery(id+"F0.wireOp",EDGE,"E7.17.2"),sQuery(id+"F0.wireOp",EDGE,"E7.17.3"),sQuery(id+"F0.wireOp",EDGE,"E7.17.4"),sQuery(id+"F0.wireOp",EDGE,"E7.17.5"),sQuery(id+"F0.wireOp",EDGE,"E7.18.0"),sQuery(id+"F0.wireOp",EDGE,"E7.18.1"),sQuery(id+"F0.wireOp",EDGE,"E7.18.2"),sQuery(id+"F0.wireOp",EDGE,"E7.18.3"),sQuery(id+"F0.wireOp",EDGE,"E7.18.4"),sQuery(id+"F0.wireOp",EDGE,"E7.18.5"),sQuery(id+"F0.wireOp",EDGE,"E7.19.0"),sQuery(id+"F0.wireOp",EDGE,"E7.19.1"),sQuery(id+"F0.wireOp",EDGE,"E7.19.2"),sQuery(id+"F0.wireOp",EDGE,"E7.19.3"),sQuery(id+"F0.wireOp",EDGE,"E7.19.4"),sQuery(id+"F0.wireOp",EDGE,"E7.19.5"),sQuery(id+"F0.wireOp",EDGE,"E7.20.0"),sQuery(id+"F0.wireOp",EDGE,"E7.20.1"),sQuery(id+"F0.wireOp",EDGE,"E7.20.2"),sQuery(id+"F0.wireOp",EDGE,"E7.20.3"),sQuery(id+"F0.wireOp",EDGE,"E7.20.4"),sQuery(id+"F0.wireOp",EDGE,"E7.20.5"),sQuery(id+"F0.wireOp",EDGE,"E7.21.0"),sQuery(id+"F0.wireOp",EDGE,"E7.21.1"),sQuery(id+"F0.wireOp",EDGE,"E7.21.2"),sQuery(id+"F0.wireOp",EDGE,"E7.21.3"),sQuery(id+"F0.wireOp",EDGE,"E7.21.4"),sQuery(id+"F0.wireOp",EDGE,"E7.21.5"),sQuery(id+"F0.wireOp",EDGE,"E7.22.0"),sQuery(id+"F0.wireOp",EDGE,"E7.22.1"),sQuery(id+"F0.wireOp",EDGE,"E7.22.2"),sQuery(id+"F0.wireOp",EDGE,"E7.22.3"),sQuery(id+"F0.wireOp",EDGE,"E7.22.4"),sQuery(id+"F0.wireOp",EDGE,"E7.22.5"),sQuery(id+"F0.wireOp",EDGE,"E7.23.0"),sQuery(id+"F0.wireOp",EDGE,"E7.23.1"),sQuery(id+"F0.wireOp",EDGE,"E7.23.2"),sQuery(id+"F0.wireOp",EDGE,"E7.23.3"),sQuery(id+"F0.wireOp",EDGE,"E7.23.4"),sQuery(id+"F0.wireOp",EDGE,"E7.23.5"),sQuery(id+"F0.wireOp",EDGE,"E7.24.0"),sQuery(id+"F0.wireOp",EDGE,"E7.24.1"),sQuery(id+"F0.wireOp",EDGE,"E7.24.2"),sQuery(id+"F0.wireOp",EDGE,"E7.24.3"),sQuery(id+"F0.wireOp",EDGE,"E7.24.4"),sQuery(id+"F0.wireOp",EDGE,"E7.24.5"),sQuery(id+"F0.wireOp",EDGE,"E7.25.0"),sQuery(id+"F0.wireOp",EDGE,"E7.25.1"),sQuery(id+"F0.wireOp",EDGE,"E7.25.2"),sQuery(id+"F0.wireOp",EDGE,"E7.25.3"),sQuery(id+"F0.wireOp",EDGE,"E7.25.4"),sQuery(id+"F0.wireOp",EDGE,"E7.25.5"),sQuery(id+"F0.wireOp",EDGE,"E7.26.0"),sQuery(id+"F0.wireOp",EDGE,"E7.26.1"),sQuery(id+"F0.wireOp",EDGE,"E7.26.2"),sQuery(id+"F0.wireOp",EDGE,"E7.26.3"),sQuery(id+"F0.wireOp",EDGE,"E7.26.4"),sQuery(id+"F0.wireOp",EDGE,"E7.26.5"),sQuery(id+"F0.wireOp",EDGE,"E7.27.0"),sQuery(id+"F0.wireOp",EDGE,"E7.27.1"),sQuery(id+"F0.wireOp",EDGE,"E7.27.2"),sQuery(id+"F0.wireOp",EDGE,"E7.27.3"),sQuery(id+"F0.wireOp",EDGE,"E7.27.4"),sQuery(id+"F0.wireOp",EDGE,"E7.27.5"),sQuery(id+"F0.wireOp",EDGE,"E7.28.0"),sQuery(id+"F0.wireOp",EDGE,"E7.28.1"),sQuery(id+"F0.wireOp",EDGE,"E7.28.2"),sQuery(id+"F0.wireOp",EDGE,"E7.28.3"),sQuery(id+"F0.wireOp",EDGE,"E7.28.4"),sQuery(id+"F0.wireOp",EDGE,"E7.28.5"),sQuery(id+"F0.wireOp",EDGE,"E7.29.0"),sQuery(id+"F0.wireOp",EDGE,"E7.29.1"),sQuery(id+"F0.wireOp",EDGE,"E7.29.2"),sQuery(id+"F0.wireOp",EDGE,"E7.29.3"),sQuery(id+"F0.wireOp",EDGE,"E7.29.4"),sQuery(id+"F0.wireOp",EDGE,"E7.29.5"),sQuery(id+"F0.wireOp",EDGE,"E7.30.0"),sQuery(id+"F0.wireOp",EDGE,"E7.30.1"),sQuery(id+"F0.wireOp",EDGE,"E7.30.2"),sQuery(id+"F0.wireOp",EDGE,"E7.30.3"),sQuery(id+"F0.wireOp",EDGE,"E7.30.4"),sQuery(id+"F0.wireOp",EDGE,"E7.30.5"),sQuery(id+"F0.wireOp",EDGE,"E7.31.0"),sQuery(id+"F0.wireOp",EDGE,"E7.31.1"),sQuery(id+"F0.wireOp",EDGE,"E7.31.2"),sQuery(id+"F0.wireOp",EDGE,"E7.31.3"),sQuery(id+"F0.wireOp",EDGE,"E7.31.4"),sQuery(id+"F0.wireOp",EDGE,"E7.31.5"),sQuery(id+"F0.wireOp",EDGE,"E7.32.0"),sQuery(id+"F0.wireOp",EDGE,"E7.32.1"),sQuery(id+"F0.wireOp",EDGE,"E7.32.2"),sQuery(id+"F0.wireOp",EDGE,"E7.32.3"),sQuery(id+"F0.wireOp",EDGE,"E7.32.4"),sQuery(id+"F0.wireOp",EDGE,"E7.32.5"),sQuery(id+"F0.wireOp",EDGE,"E7.33.0"),sQuery(id+"F0.wireOp",EDGE,"E7.33.1"),sQuery(id+"F0.wireOp",EDGE,"E7.33.2"),sQuery(id+"F0.wireOp",EDGE,"E7.33.3"),sQuery(id+"F0.wireOp",EDGE,"E7.33.4"),sQuery(id+"F0.wireOp",EDGE,"E7.33.5"),sQuery(id+"F0.wireOp",EDGE,"E7.34.0"),sQuery(id+"F0.wireOp",EDGE,"E7.34.1"),sQuery(id+"F0.wireOp",EDGE,"E7.34.2"),sQuery(id+"F0.wireOp",EDGE,"E7.34.3"),sQuery(id+"F0.wireOp",EDGE,"E7.34.4"),sQuery(id+"F0.wireOp",EDGE,"E7.34.5"),sQuery(id+"F0.wireOp",EDGE,"E7.35.0"),sQuery(id+"F0.wireOp",EDGE,"E7.35.1"),sQuery(id+"F0.wireOp",EDGE,"E7.35.2"),sQuery(id+"F0.wireOp",EDGE,"E7.35.3"),sQuery(id+"F0.wireOp",EDGE,"E7.35.4"),sQuery(id+"F0.wireOp",EDGE,"E7.35.5"),sQuery(id+"F0.wireOp",EDGE,"E7.36.0"),sQuery(id+"F0.wireOp",EDGE,"E7.36.1"),sQuery(id+"F0.wireOp",EDGE,"E7.36.2"),sQuery(id+"F0.wireOp",EDGE,"E7.36.3"),sQuery(id+"F0.wireOp",EDGE,"E7.36.4"),sQuery(id+"F0.wireOp",EDGE,"E7.36.5"),sQuery(id+"F0.wireOp",EDGE,"E7.37.0"),sQuery(id+"F0.wireOp",EDGE,"E7.37.1"),sQuery(id+"F0.wireOp",EDGE,"E7.37.2"),sQuery(id+"F0.wireOp",EDGE,"E7.37.3"),sQuery(id+"F0.wireOp",EDGE,"E7.37.4"),sQuery(id+"F0.wireOp",EDGE,"E7.37.5"),sQuery(id+"F0.wireOp",EDGE,"E7.38.0"),sQuery(id+"F0.wireOp",EDGE,"E7.38.1"),sQuery(id+"F0.wireOp",EDGE,"E7.38.2"),sQuery(id+"F0.wireOp",EDGE,"E7.38.3"),sQuery(id+"F0.wireOp",EDGE,"E7.38.4"),sQuery(id+"F0.wireOp",EDGE,"E7.38.5"),sQuery(id+"F0.wireOp",EDGE,"E7.39.0"),sQuery(id+"F0.wireOp",EDGE,"E7.39.1"),sQuery(id+"F0.wireOp",EDGE,"E7.39.2"),sQuery(id+"F0.wireOp",EDGE,"E7.39.3"),sQuery(id+"F0.wireOp",EDGE,"E7.39.4"),sQuery(id+"F0.wireOp",EDGE,"E7.39.5"),sQuery(id+"F0.wireOp",EDGE,"E7.40.0"),sQuery(id+"F0.wireOp",EDGE,"E7.40.1"),sQuery(id+"F0.wireOp",EDGE,"E7.40.2"),sQuery(id+"F0.wireOp",EDGE,"E7.40.3"),sQuery(id+"F0.wireOp",EDGE,"E7.40.4"),sQuery(id+"F0.wireOp",EDGE,"E7.40.5"),subQ0,sQuery(id+"F0.wireOp",EDGE,"E7.41.1"),sQuery(id+"F0.wireOp",EDGE,"E7.41.2"),sQuery(id+"F0.wireOp",EDGE,"E7.41.3"),sQuery(id+"F0.wireOp",EDGE,"E7.41.4"),sQuery(id+"F0.wireOp",EDGE,"E7.41.5"),sQuery(id+"F0.wireOp",EDGE,"E7.42.0"),sQuery(id+"F0.wireOp",EDGE,"E7.42.1"),sQuery(id+"F0.wireOp",EDGE,"E7.42.2"),sQuery(id+"F0.wireOp",EDGE,"E7.42.3"),sQuery(id+"F0.wireOp",EDGE,"E7.42.4"),sQuery(id+"F0.wireOp",EDGE,"E7.42.5"),sQuery(id+"F0.wireOp",EDGE,"E7.43.0"),sQuery(id+"F0.wireOp",EDGE,"E7.43.1"),sQuery(id+"F0.wireOp",EDGE,"E7.43.2"),sQuery(id+"F0.wireOp",EDGE,"E7.43.3"),sQuery(id+"F0.wireOp",EDGE,"E7.43.4"),sQuery(id+"F0.wireOp",EDGE,"E7.43.5")])],"isStart":false})]});}
            var Q2;
            {var subQ0=sQuery(id+"F0.wireOp",EDGE,"E7.39.0");Q2=makeQuery(id+"F2.opChamfer","BLEND_EDGE",EDGE,{"blendedFrom":[makeQuery(id+"F1.opExtrude","CAP_EDGE",EDGE,{"disambiguationData":[OSD([subQ0])],"isStart":false}),makeQuery(id+"F1.opExtrude","CAP_FACE",FACE,{"disambiguationData":[OSD([sQuery(id+"F0.wireOp",EDGE,"E1"),sQuery(id+"F0.wireOp",EDGE,"E2"),sQuery(id+"F0.wireOp",EDGE,"E3"),sQuery(id+"F0.wireOp",EDGE,"E4"),sQuery(id+"F0.wireOp",EDGE,"E5"),sQuery(id+"F0.wireOp",EDGE,"E6"),sQuery(id+"F0.wireOp",EDGE,"E7.1.0"),sQuery(id+"F0.wireOp",EDGE,"E7.1.1"),sQuery(id+"F0.wireOp",EDGE,"E7.1.2"),sQuery(id+"F0.wireOp",EDGE,"E7.1.3"),sQuery(id+"F0.wireOp",EDGE,"E7.1.4"),sQuery(id+"F0.wireOp",EDGE,"E7.1.5"),sQuery(id+"F0.wireOp",EDGE,"E7.2.0"),sQuery(id+"F0.wireOp",EDGE,"E7.2.1"),sQuery(id+"F0.wireOp",EDGE,"E7.2.2"),sQuery(id+"F0.wireOp",EDGE,"E7.2.3"),sQuery(id+"F0.wireOp",EDGE,"E7.2.4"),sQuery(id+"F0.wireOp",EDGE,"E7.2.5"),sQuery(id+"F0.wireOp",EDGE,"E7.3.0"),sQuery(id+"F0.wireOp",EDGE,"E7.3.1"),sQuery(id+"F0.wireOp",EDGE,"E7.3.2"),sQuery(id+"F0.wireOp",EDGE,"E7.3.3"),sQuery(id+"F0.wireOp",EDGE,"E7.3.4"),sQuery(id+"F0.wireOp",EDGE,"E7.3.5"),sQuery(id+"F0.wireOp",EDGE,"E7.4.0"),sQuery(id+"F0.wireOp",EDGE,"E7.4.1"),sQuery(id+"F0.wireOp",EDGE,"E7.4.2"),sQuery(id+"F0.wireOp",EDGE,"E7.4.3"),sQuery(id+"F0.wireOp",EDGE,"E7.4.4"),sQuery(id+"F0.wireOp",EDGE,"E7.4.5"),sQuery(id+"F0.wireOp",EDGE,"E7.5.0"),sQuery(id+"F0.wireOp",EDGE,"E7.5.1"),sQuery(id+"F0.wireOp",EDGE,"E7.5.2"),sQuery(id+"F0.wireOp",EDGE,"E7.5.3"),sQuery(id+"F0.wireOp",EDGE,"E7.5.4"),sQuery(id+"F0.wireOp",EDGE,"E7.5.5"),sQuery(id+"F0.wireOp",EDGE,"E7.6.0"),sQuery(id+"F0.wireOp",EDGE,"E7.6.1"),sQuery(id+"F0.wireOp",EDGE,"E7.6.2"),sQuery(id+"F0.wireOp",EDGE,"E7.6.3"),sQuery(id+"F0.wireOp",EDGE,"E7.6.4"),sQuery(id+"F0.wireOp",EDGE,"E7.6.5"),sQuery(id+"F0.wireOp",EDGE,"E7.7.0"),sQuery(id+"F0.wireOp",EDGE,"E7.7.1"),sQuery(id+"F0.wireOp",EDGE,"E7.7.2"),sQuery(id+"F0.wireOp",EDGE,"E7.7.3"),sQuery(id+"F0.wireOp",EDGE,"E7.7.4"),sQuery(id+"F0.wireOp",EDGE,"E7.7.5"),sQuery(id+"F0.wireOp",EDGE,"E7.8.0"),sQuery(id+"F0.wireOp",EDGE,"E7.8.1"),sQuery(id+"F0.wireOp",EDGE,"E7.8.2"),sQuery(id+"F0.wireOp",EDGE,"E7.8.3"),sQuery(id+"F0.wireOp",EDGE,"E7.8.4"),sQuery(id+"F0.wireOp",EDGE,"E7.8.5"),sQuery(id+"F0.wireOp",EDGE,"E7.9.0"),sQuery(id+"F0.wireOp",EDGE,"E7.9.1"),sQuery(id+"F0.wireOp",EDGE,"E7.9.2"),sQuery(id+"F0.wireOp",EDGE,"E7.9.3"),sQuery(id+"F0.wireOp",EDGE,"E7.9.4"),sQuery(id+"F0.wireOp",EDGE,"E7.9.5"),sQuery(id+"F0.wireOp",EDGE,"E7.10.0"),sQuery(id+"F0.wireOp",EDGE,"E7.10.1"),sQuery(id+"F0.wireOp",EDGE,"E7.10.2"),sQuery(id+"F0.wireOp",EDGE,"E7.10.3"),sQuery(id+"F0.wireOp",EDGE,"E7.10.4"),sQuery(id+"F0.wireOp",EDGE,"E7.10.5"),sQuery(id+"F0.wireOp",EDGE,"E7.11.0"),sQuery(id+"F0.wireOp",EDGE,"E7.11.1"),sQuery(id+"F0.wireOp",EDGE,"E7.11.2"),sQuery(id+"F0.wireOp",EDGE,"E7.11.3"),sQuery(id+"F0.wireOp",EDGE,"E7.11.4"),sQuery(id+"F0.wireOp",EDGE,"E7.11.5"),sQuery(id+"F0.wireOp",EDGE,"E7.12.0"),sQuery(id+"F0.wireOp",EDGE,"E7.12.1"),sQuery(id+"F0.wireOp",EDGE,"E7.12.2"),sQuery(id+"F0.wireOp",EDGE,"E7.12.3"),sQuery(id+"F0.wireOp",EDGE,"E7.12.4"),sQuery(id+"F0.wireOp",EDGE,"E7.12.5"),sQuery(id+"F0.wireOp",EDGE,"E7.13.0"),sQuery(id+"F0.wireOp",EDGE,"E7.13.1"),sQuery(id+"F0.wireOp",EDGE,"E7.13.2"),sQuery(id+"F0.wireOp",EDGE,"E7.13.3"),sQuery(id+"F0.wireOp",EDGE,"E7.13.4"),sQuery(id+"F0.wireOp",EDGE,"E7.13.5"),sQuery(id+"F0.wireOp",EDGE,"E7.14.0"),sQuery(id+"F0.wireOp",EDGE,"E7.14.1"),sQuery(id+"F0.wireOp",EDGE,"E7.14.2"),sQuery(id+"F0.wireOp",EDGE,"E7.14.3"),sQuery(id+"F0.wireOp",EDGE,"E7.14.4"),sQuery(id+"F0.wireOp",EDGE,"E7.14.5"),sQuery(id+"F0.wireOp",EDGE,"E7.15.0"),sQuery(id+"F0.wireOp",EDGE,"E7.15.1"),sQuery(id+"F0.wireOp",EDGE,"E7.15.2"),sQuery(id+"F0.wireOp",EDGE,"E7.15.3"),sQuery(id+"F0.wireOp",EDGE,"E7.15.4"),sQuery(id+"F0.wireOp",EDGE,"E7.15.5"),sQuery(id+"F0.wireOp",EDGE,"E7.16.0"),sQuery(id+"F0.wireOp",EDGE,"E7.16.1"),sQuery(id+"F0.wireOp",EDGE,"E7.16.2"),sQuery(id+"F0.wireOp",EDGE,"E7.16.3"),sQuery(id+"F0.wireOp",EDGE,"E7.16.4"),sQuery(id+"F0.wireOp",EDGE,"E7.16.5"),sQuery(id+"F0.wireOp",EDGE,"E7.17.0"),sQuery(id+"F0.wireOp",EDGE,"E7.17.1"),sQuery(id+"F0.wireOp",EDGE,"E7.17.2"),sQuery(id+"F0.wireOp",EDGE,"E7.17.3"),sQuery(id+"F0.wireOp",EDGE,"E7.17.4"),sQuery(id+"F0.wireOp",EDGE,"E7.17.5"),sQuery(id+"F0.wireOp",EDGE,"E7.18.0"),sQuery(id+"F0.wireOp",EDGE,"E7.18.1"),sQuery(id+"F0.wireOp",EDGE,"E7.18.2"),sQuery(id+"F0.wireOp",EDGE,"E7.18.3"),sQuery(id+"F0.wireOp",EDGE,"E7.18.4"),sQuery(id+"F0.wireOp",EDGE,"E7.18.5"),sQuery(id+"F0.wireOp",EDGE,"E7.19.0"),sQuery(id+"F0.wireOp",EDGE,"E7.19.1"),sQuery(id+"F0.wireOp",EDGE,"E7.19.2"),sQuery(id+"F0.wireOp",EDGE,"E7.19.3"),sQuery(id+"F0.wireOp",EDGE,"E7.19.4"),sQuery(id+"F0.wireOp",EDGE,"E7.19.5"),sQuery(id+"F0.wireOp",EDGE,"E7.20.0"),sQuery(id+"F0.wireOp",EDGE,"E7.20.1"),sQuery(id+"F0.wireOp",EDGE,"E7.20.2"),sQuery(id+"F0.wireOp",EDGE,"E7.20.3"),sQuery(id+"F0.wireOp",EDGE,"E7.20.4"),sQuery(id+"F0.wireOp",EDGE,"E7.20.5"),sQuery(id+"F0.wireOp",EDGE,"E7.21.0"),sQuery(id+"F0.wireOp",EDGE,"E7.21.1"),sQuery(id+"F0.wireOp",EDGE,"E7.21.2"),sQuery(id+"F0.wireOp",EDGE,"E7.21.3"),sQuery(id+"F0.wireOp",EDGE,"E7.21.4"),sQuery(id+"F0.wireOp",EDGE,"E7.21.5"),sQuery(id+"F0.wireOp",EDGE,"E7.22.0"),sQuery(id+"F0.wireOp",EDGE,"E7.22.1"),sQuery(id+"F0.wireOp",EDGE,"E7.22.2"),sQuery(id+"F0.wireOp",EDGE,"E7.22.3"),sQuery(id+"F0.wireOp",EDGE,"E7.22.4"),sQuery(id+"F0.wireOp",EDGE,"E7.22.5"),sQuery(id+"F0.wireOp",EDGE,"E7.23.0"),sQuery(id+"F0.wireOp",EDGE,"E7.23.1"),sQuery(id+"F0.wireOp",EDGE,"E7.23.2"),sQuery(id+"F0.wireOp",EDGE,"E7.23.3"),sQuery(id+"F0.wireOp",EDGE,"E7.23.4"),sQuery(id+"F0.wireOp",EDGE,"E7.23.5"),sQuery(id+"F0.wireOp",EDGE,"E7.24.0"),sQuery(id+"F0.wireOp",EDGE,"E7.24.1"),sQuery(id+"F0.wireOp",EDGE,"E7.24.2"),sQuery(id+"F0.wireOp",EDGE,"E7.24.3"),sQuery(id+"F0.wireOp",EDGE,"E7.24.4"),sQuery(id+"F0.wireOp",EDGE,"E7.24.5"),sQuery(id+"F0.wireOp",EDGE,"E7.25.0"),sQuery(id+"F0.wireOp",EDGE,"E7.25.1"),sQuery(id+"F0.wireOp",EDGE,"E7.25.2"),sQuery(id+"F0.wireOp",EDGE,"E7.25.3"),sQuery(id+"F0.wireOp",EDGE,"E7.25.4"),sQuery(id+"F0.wireOp",EDGE,"E7.25.5"),sQuery(id+"F0.wireOp",EDGE,"E7.26.0"),sQuery(id+"F0.wireOp",EDGE,"E7.26.1"),sQuery(id+"F0.wireOp",EDGE,"E7.26.2"),sQuery(id+"F0.wireOp",EDGE,"E7.26.3"),sQuery(id+"F0.wireOp",EDGE,"E7.26.4"),sQuery(id+"F0.wireOp",EDGE,"E7.26.5"),sQuery(id+"F0.wireOp",EDGE,"E7.27.0"),sQuery(id+"F0.wireOp",EDGE,"E7.27.1"),sQuery(id+"F0.wireOp",EDGE,"E7.27.2"),sQuery(id+"F0.wireOp",EDGE,"E7.27.3"),sQuery(id+"F0.wireOp",EDGE,"E7.27.4"),sQuery(id+"F0.wireOp",EDGE,"E7.27.5"),sQuery(id+"F0.wireOp",EDGE,"E7.28.0"),sQuery(id+"F0.wireOp",EDGE,"E7.28.1"),sQuery(id+"F0.wireOp",EDGE,"E7.28.2"),sQuery(id+"F0.wireOp",EDGE,"E7.28.3"),sQuery(id+"F0.wireOp",EDGE,"E7.28.4"),sQuery(id+"F0.wireOp",EDGE,"E7.28.5"),sQuery(id+"F0.wireOp",EDGE,"E7.29.0"),sQuery(id+"F0.wireOp",EDGE,"E7.29.1"),sQuery(id+"F0.wireOp",EDGE,"E7.29.2"),sQuery(id+"F0.wireOp",EDGE,"E7.29.3"),sQuery(id+"F0.wireOp",EDGE,"E7.29.4"),sQuery(id+"F0.wireOp",EDGE,"E7.29.5"),sQuery(id+"F0.wireOp",EDGE,"E7.30.0"),sQuery(id+"F0.wireOp",EDGE,"E7.30.1"),sQuery(id+"F0.wireOp",EDGE,"E7.30.2"),sQuery(id+"F0.wireOp",EDGE,"E7.30.3"),sQuery(id+"F0.wireOp",EDGE,"E7.30.4"),sQuery(id+"F0.wireOp",EDGE,"E7.30.5"),sQuery(id+"F0.wireOp",EDGE,"E7.31.0"),sQuery(id+"F0.wireOp",EDGE,"E7.31.1"),sQuery(id+"F0.wireOp",EDGE,"E7.31.2"),sQuery(id+"F0.wireOp",EDGE,"E7.31.3"),sQuery(id+"F0.wireOp",EDGE,"E7.31.4"),sQuery(id+"F0.wireOp",EDGE,"E7.31.5"),sQuery(id+"F0.wireOp",EDGE,"E7.32.0"),sQuery(id+"F0.wireOp",EDGE,"E7.32.1"),sQuery(id+"F0.wireOp",EDGE,"E7.32.2"),sQuery(id+"F0.wireOp",EDGE,"E7.32.3"),sQuery(id+"F0.wireOp",EDGE,"E7.32.4"),sQuery(id+"F0.wireOp",EDGE,"E7.32.5"),sQuery(id+"F0.wireOp",EDGE,"E7.33.0"),sQuery(id+"F0.wireOp",EDGE,"E7.33.1"),sQuery(id+"F0.wireOp",EDGE,"E7.33.2"),sQuery(id+"F0.wireOp",EDGE,"E7.33.3"),sQuery(id+"F0.wireOp",EDGE,"E7.33.4"),sQuery(id+"F0.wireOp",EDGE,"E7.33.5"),sQuery(id+"F0.wireOp",EDGE,"E7.34.0"),sQuery(id+"F0.wireOp",EDGE,"E7.34.1"),sQuery(id+"F0.wireOp",EDGE,"E7.34.2"),sQuery(id+"F0.wireOp",EDGE,"E7.34.3"),sQuery(id+"F0.wireOp",EDGE,"E7.34.4"),sQuery(id+"F0.wireOp",EDGE,"E7.34.5"),sQuery(id+"F0.wireOp",EDGE,"E7.35.0"),sQuery(id+"F0.wireOp",EDGE,"E7.35.1"),sQuery(id+"F0.wireOp",EDGE,"E7.35.2"),sQuery(id+"F0.wireOp",EDGE,"E7.35.3"),sQuery(id+"F0.wireOp",EDGE,"E7.35.4"),sQuery(id+"F0.wireOp",EDGE,"E7.35.5"),sQuery(id+"F0.wireOp",EDGE,"E7.36.0"),sQuery(id+"F0.wireOp",EDGE,"E7.36.1"),sQuery(id+"F0.wireOp",EDGE,"E7.36.2"),sQuery(id+"F0.wireOp",EDGE,"E7.36.3"),sQuery(id+"F0.wireOp",EDGE,"E7.36.4"),sQuery(id+"F0.wireOp",EDGE,"E7.36.5"),sQuery(id+"F0.wireOp",EDGE,"E7.37.0"),sQuery(id+"F0.wireOp",EDGE,"E7.37.1"),sQuery(id+"F0.wireOp",EDGE,"E7.37.2"),sQuery(id+"F0.wireOp",EDGE,"E7.37.3"),sQuery(id+"F0.wireOp",EDGE,"E7.37.4"),sQuery(id+"F0.wireOp",EDGE,"E7.37.5"),sQuery(id+"F0.wireOp",EDGE,"E7.38.0"),sQuery(id+"F0.wireOp",EDGE,"E7.38.1"),sQuery(id+"F0.wireOp",EDGE,"E7.38.2"),sQuery(id+"F0.wireOp",EDGE,"E7.38.3"),sQuery(id+"F0.wireOp",EDGE,"E7.38.4"),sQuery(id+"F0.wireOp",EDGE,"E7.38.5"),subQ0,sQuery(id+"F0.wireOp",EDGE,"E7.39.1"),sQuery(id+"F0.wireOp",EDGE,"E7.39.2"),sQuery(id+"F0.wireOp",EDGE,"E7.39.3"),sQuery(id+"F0.wireOp",EDGE,"E7.39.4"),sQuery(id+"F0.wireOp",EDGE,"E7.39.5"),sQuery(id+"F0.wireOp",EDGE,"E7.40.0"),sQuery(id+"F0.wireOp",EDGE,"E7.40.1"),sQuery(id+"F0.wireOp",EDGE,"E7.40.2"),sQuery(id+"F0.wireOp",EDGE,"E7.40.3"),sQuery(id+"F0.wireOp",EDGE,"E7.40.4"),sQuery(id+"F0.wireOp",EDGE,"E7.40.5"),sQuery(id+"F0.wireOp",EDGE,"E7.41.0"),sQuery(id+"F0.wireOp",EDGE,"E7.41.1"),sQuery(id+"F0.wireOp",EDGE,"E7.41.2"),sQuery(id+"F0.wireOp",EDGE,"E7.41.3"),sQuery(id+"F0.wireOp",EDGE,"E7.41.4"),sQuery(id+"F0.wireOp",EDGE,"E7.41.5"),sQuery(id+"F0.wireOp",EDGE,"E7.42.0"),sQuery(id+"F0.wireOp",EDGE,"E7.42.1"),sQuery(id+"F0.wireOp",EDGE,"E7.42.2"),sQuery(id+"F0.wireOp",EDGE,"E7.42.3"),sQuery(id+"F0.wireOp",EDGE,"E7.42.4"),sQuery(id+"F0.wireOp",EDGE,"E7.42.5"),sQuery(id+"F0.wireOp",EDGE,"E7.43.0"),sQuery(id+"F0.wireOp",EDGE,"E7.43.1"),sQuery(id+"F0.wireOp",EDGE,"E7.43.2"),sQuery(id+"F0.wireOp",EDGE,"E7.43.3"),sQuery(id+"F0.wireOp",EDGE,"E7.43.4"),sQuery(id+"F0.wireOp",EDGE,"E7.43.5")])],"isStart":false})],"blendedInto":[makeQuery(id+"F1.opExtrude","CAP_FACE",FACE,{"disambiguationData":[OSD([sQuery(id+"F0.wireOp",EDGE,"E1"),sQuery(id+"F0.wireOp",EDGE,"E2"),sQuery(id+"F0.wireOp",EDGE,"E3"),sQuery(id+"F0.wireOp",EDGE,"E4"),sQuery(id+"F0.wireOp",EDGE,"E5"),sQuery(id+"F0.wireOp",EDGE,"E6"),sQuery(id+"F0.wireOp",EDGE,"E7.1.0"),sQuery(id+"F0.wireOp",EDGE,"E7.1.1"),sQuery(id+"F0.wireOp",EDGE,"E7.1.2"),sQuery(id+"F0.wireOp",EDGE,"E7.1.3"),sQuery(id+"F0.wireOp",EDGE,"E7.1.4"),sQuery(id+"F0.wireOp",EDGE,"E7.1.5"),sQuery(id+"F0.wireOp",EDGE,"E7.2.0"),sQuery(id+"F0.wireOp",EDGE,"E7.2.1"),sQuery(id+"F0.wireOp",EDGE,"E7.2.2"),sQuery(id+"F0.wireOp",EDGE,"E7.2.3"),sQuery(id+"F0.wireOp",EDGE,"E7.2.4"),sQuery(id+"F0.wireOp",EDGE,"E7.2.5"),sQuery(id+"F0.wireOp",EDGE,"E7.3.0"),sQuery(id+"F0.wireOp",EDGE,"E7.3.1"),sQuery(id+"F0.wireOp",EDGE,"E7.3.2"),sQuery(id+"F0.wireOp",EDGE,"E7.3.3"),sQuery(id+"F0.wireOp",EDGE,"E7.3.4"),sQuery(id+"F0.wireOp",EDGE,"E7.3.5"),sQuery(id+"F0.wireOp",EDGE,"E7.4.0"),sQuery(id+"F0.wireOp",EDGE,"E7.4.1"),sQuery(id+"F0.wireOp",EDGE,"E7.4.2"),sQuery(id+"F0.wireOp",EDGE,"E7.4.3"),sQuery(id+"F0.wireOp",EDGE,"E7.4.4"),sQuery(id+"F0.wireOp",EDGE,"E7.4.5"),sQuery(id+"F0.wireOp",EDGE,"E7.5.0"),sQuery(id+"F0.wireOp",EDGE,"E7.5.1"),sQuery(id+"F0.wireOp",EDGE,"E7.5.2"),sQuery(id+"F0.wireOp",EDGE,"E7.5.3"),sQuery(id+"F0.wireOp",EDGE,"E7.5.4"),sQuery(id+"F0.wireOp",EDGE,"E7.5.5"),sQuery(id+"F0.wireOp",EDGE,"E7.6.0"),sQuery(id+"F0.wireOp",EDGE,"E7.6.1"),sQuery(id+"F0.wireOp",EDGE,"E7.6.2"),sQuery(id+"F0.wireOp",EDGE,"E7.6.3"),sQuery(id+"F0.wireOp",EDGE,"E7.6.4"),sQuery(id+"F0.wireOp",EDGE,"E7.6.5"),sQuery(id+"F0.wireOp",EDGE,"E7.7.0"),sQuery(id+"F0.wireOp",EDGE,"E7.7.1"),sQuery(id+"F0.wireOp",EDGE,"E7.7.2"),sQuery(id+"F0.wireOp",EDGE,"E7.7.3"),sQuery(id+"F0.wireOp",EDGE,"E7.7.4"),sQuery(id+"F0.wireOp",EDGE,"E7.7.5"),sQuery(id+"F0.wireOp",EDGE,"E7.8.0"),sQuery(id+"F0.wireOp",EDGE,"E7.8.1"),sQuery(id+"F0.wireOp",EDGE,"E7.8.2"),sQuery(id+"F0.wireOp",EDGE,"E7.8.3"),sQuery(id+"F0.wireOp",EDGE,"E7.8.4"),sQuery(id+"F0.wireOp",EDGE,"E7.8.5"),sQuery(id+"F0.wireOp",EDGE,"E7.9.0"),sQuery(id+"F0.wireOp",EDGE,"E7.9.1"),sQuery(id+"F0.wireOp",EDGE,"E7.9.2"),sQuery(id+"F0.wireOp",EDGE,"E7.9.3"),sQuery(id+"F0.wireOp",EDGE,"E7.9.4"),sQuery(id+"F0.wireOp",EDGE,"E7.9.5"),sQuery(id+"F0.wireOp",EDGE,"E7.10.0"),sQuery(id+"F0.wireOp",EDGE,"E7.10.1"),sQuery(id+"F0.wireOp",EDGE,"E7.10.2"),sQuery(id+"F0.wireOp",EDGE,"E7.10.3"),sQuery(id+"F0.wireOp",EDGE,"E7.10.4"),sQuery(id+"F0.wireOp",EDGE,"E7.10.5"),sQuery(id+"F0.wireOp",EDGE,"E7.11.0"),sQuery(id+"F0.wireOp",EDGE,"E7.11.1"),sQuery(id+"F0.wireOp",EDGE,"E7.11.2"),sQuery(id+"F0.wireOp",EDGE,"E7.11.3"),sQuery(id+"F0.wireOp",EDGE,"E7.11.4"),sQuery(id+"F0.wireOp",EDGE,"E7.11.5"),sQuery(id+"F0.wireOp",EDGE,"E7.12.0"),sQuery(id+"F0.wireOp",EDGE,"E7.12.1"),sQuery(id+"F0.wireOp",EDGE,"E7.12.2"),sQuery(id+"F0.wireOp",EDGE,"E7.12.3"),sQuery(id+"F0.wireOp",EDGE,"E7.12.4"),sQuery(id+"F0.wireOp",EDGE,"E7.12.5"),sQuery(id+"F0.wireOp",EDGE,"E7.13.0"),sQuery(id+"F0.wireOp",EDGE,"E7.13.1"),sQuery(id+"F0.wireOp",EDGE,"E7.13.2"),sQuery(id+"F0.wireOp",EDGE,"E7.13.3"),sQuery(id+"F0.wireOp",EDGE,"E7.13.4"),sQuery(id+"F0.wireOp",EDGE,"E7.13.5"),sQuery(id+"F0.wireOp",EDGE,"E7.14.0"),sQuery(id+"F0.wireOp",EDGE,"E7.14.1"),sQuery(id+"F0.wireOp",EDGE,"E7.14.2"),sQuery(id+"F0.wireOp",EDGE,"E7.14.3"),sQuery(id+"F0.wireOp",EDGE,"E7.14.4"),sQuery(id+"F0.wireOp",EDGE,"E7.14.5"),sQuery(id+"F0.wireOp",EDGE,"E7.15.0"),sQuery(id+"F0.wireOp",EDGE,"E7.15.1"),sQuery(id+"F0.wireOp",EDGE,"E7.15.2"),sQuery(id+"F0.wireOp",EDGE,"E7.15.3"),sQuery(id+"F0.wireOp",EDGE,"E7.15.4"),sQuery(id+"F0.wireOp",EDGE,"E7.15.5"),sQuery(id+"F0.wireOp",EDGE,"E7.16.0"),sQuery(id+"F0.wireOp",EDGE,"E7.16.1"),sQuery(id+"F0.wireOp",EDGE,"E7.16.2"),sQuery(id+"F0.wireOp",EDGE,"E7.16.3"),sQuery(id+"F0.wireOp",EDGE,"E7.16.4"),sQuery(id+"F0.wireOp",EDGE,"E7.16.5"),sQuery(id+"F0.wireOp",EDGE,"E7.17.0"),sQuery(id+"F0.wireOp",EDGE,"E7.17.1"),sQuery(id+"F0.wireOp",EDGE,"E7.17.2"),sQuery(id+"F0.wireOp",EDGE,"E7.17.3"),sQuery(id+"F0.wireOp",EDGE,"E7.17.4"),sQuery(id+"F0.wireOp",EDGE,"E7.17.5"),sQuery(id+"F0.wireOp",EDGE,"E7.18.0"),sQuery(id+"F0.wireOp",EDGE,"E7.18.1"),sQuery(id+"F0.wireOp",EDGE,"E7.18.2"),sQuery(id+"F0.wireOp",EDGE,"E7.18.3"),sQuery(id+"F0.wireOp",EDGE,"E7.18.4"),sQuery(id+"F0.wireOp",EDGE,"E7.18.5"),sQuery(id+"F0.wireOp",EDGE,"E7.19.0"),sQuery(id+"F0.wireOp",EDGE,"E7.19.1"),sQuery(id+"F0.wireOp",EDGE,"E7.19.2"),sQuery(id+"F0.wireOp",EDGE,"E7.19.3"),sQuery(id+"F0.wireOp",EDGE,"E7.19.4"),sQuery(id+"F0.wireOp",EDGE,"E7.19.5"),sQuery(id+"F0.wireOp",EDGE,"E7.20.0"),sQuery(id+"F0.wireOp",EDGE,"E7.20.1"),sQuery(id+"F0.wireOp",EDGE,"E7.20.2"),sQuery(id+"F0.wireOp",EDGE,"E7.20.3"),sQuery(id+"F0.wireOp",EDGE,"E7.20.4"),sQuery(id+"F0.wireOp",EDGE,"E7.20.5"),sQuery(id+"F0.wireOp",EDGE,"E7.21.0"),sQuery(id+"F0.wireOp",EDGE,"E7.21.1"),sQuery(id+"F0.wireOp",EDGE,"E7.21.2"),sQuery(id+"F0.wireOp",EDGE,"E7.21.3"),sQuery(id+"F0.wireOp",EDGE,"E7.21.4"),sQuery(id+"F0.wireOp",EDGE,"E7.21.5"),sQuery(id+"F0.wireOp",EDGE,"E7.22.0"),sQuery(id+"F0.wireOp",EDGE,"E7.22.1"),sQuery(id+"F0.wireOp",EDGE,"E7.22.2"),sQuery(id+"F0.wireOp",EDGE,"E7.22.3"),sQuery(id+"F0.wireOp",EDGE,"E7.22.4"),sQuery(id+"F0.wireOp",EDGE,"E7.22.5"),sQuery(id+"F0.wireOp",EDGE,"E7.23.0"),sQuery(id+"F0.wireOp",EDGE,"E7.23.1"),sQuery(id+"F0.wireOp",EDGE,"E7.23.2"),sQuery(id+"F0.wireOp",EDGE,"E7.23.3"),sQuery(id+"F0.wireOp",EDGE,"E7.23.4"),sQuery(id+"F0.wireOp",EDGE,"E7.23.5"),sQuery(id+"F0.wireOp",EDGE,"E7.24.0"),sQuery(id+"F0.wireOp",EDGE,"E7.24.1"),sQuery(id+"F0.wireOp",EDGE,"E7.24.2"),sQuery(id+"F0.wireOp",EDGE,"E7.24.3"),sQuery(id+"F0.wireOp",EDGE,"E7.24.4"),sQuery(id+"F0.wireOp",EDGE,"E7.24.5"),sQuery(id+"F0.wireOp",EDGE,"E7.25.0"),sQuery(id+"F0.wireOp",EDGE,"E7.25.1"),sQuery(id+"F0.wireOp",EDGE,"E7.25.2"),sQuery(id+"F0.wireOp",EDGE,"E7.25.3"),sQuery(id+"F0.wireOp",EDGE,"E7.25.4"),sQuery(id+"F0.wireOp",EDGE,"E7.25.5"),sQuery(id+"F0.wireOp",EDGE,"E7.26.0"),sQuery(id+"F0.wireOp",EDGE,"E7.26.1"),sQuery(id+"F0.wireOp",EDGE,"E7.26.2"),sQuery(id+"F0.wireOp",EDGE,"E7.26.3"),sQuery(id+"F0.wireOp",EDGE,"E7.26.4"),sQuery(id+"F0.wireOp",EDGE,"E7.26.5"),sQuery(id+"F0.wireOp",EDGE,"E7.27.0"),sQuery(id+"F0.wireOp",EDGE,"E7.27.1"),sQuery(id+"F0.wireOp",EDGE,"E7.27.2"),sQuery(id+"F0.wireOp",EDGE,"E7.27.3"),sQuery(id+"F0.wireOp",EDGE,"E7.27.4"),sQuery(id+"F0.wireOp",EDGE,"E7.27.5"),sQuery(id+"F0.wireOp",EDGE,"E7.28.0"),sQuery(id+"F0.wireOp",EDGE,"E7.28.1"),sQuery(id+"F0.wireOp",EDGE,"E7.28.2"),sQuery(id+"F0.wireOp",EDGE,"E7.28.3"),sQuery(id+"F0.wireOp",EDGE,"E7.28.4"),sQuery(id+"F0.wireOp",EDGE,"E7.28.5"),sQuery(id+"F0.wireOp",EDGE,"E7.29.0"),sQuery(id+"F0.wireOp",EDGE,"E7.29.1"),sQuery(id+"F0.wireOp",EDGE,"E7.29.2"),sQuery(id+"F0.wireOp",EDGE,"E7.29.3"),sQuery(id+"F0.wireOp",EDGE,"E7.29.4"),sQuery(id+"F0.wireOp",EDGE,"E7.29.5"),sQuery(id+"F0.wireOp",EDGE,"E7.30.0"),sQuery(id+"F0.wireOp",EDGE,"E7.30.1"),sQuery(id+"F0.wireOp",EDGE,"E7.30.2"),sQuery(id+"F0.wireOp",EDGE,"E7.30.3"),sQuery(id+"F0.wireOp",EDGE,"E7.30.4"),sQuery(id+"F0.wireOp",EDGE,"E7.30.5"),sQuery(id+"F0.wireOp",EDGE,"E7.31.0"),sQuery(id+"F0.wireOp",EDGE,"E7.31.1"),sQuery(id+"F0.wireOp",EDGE,"E7.31.2"),sQuery(id+"F0.wireOp",EDGE,"E7.31.3"),sQuery(id+"F0.wireOp",EDGE,"E7.31.4"),sQuery(id+"F0.wireOp",EDGE,"E7.31.5"),sQuery(id+"F0.wireOp",EDGE,"E7.32.0"),sQuery(id+"F0.wireOp",EDGE,"E7.32.1"),sQuery(id+"F0.wireOp",EDGE,"E7.32.2"),sQuery(id+"F0.wireOp",EDGE,"E7.32.3"),sQuery(id+"F0.wireOp",EDGE,"E7.32.4"),sQuery(id+"F0.wireOp",EDGE,"E7.32.5"),sQuery(id+"F0.wireOp",EDGE,"E7.33.0"),sQuery(id+"F0.wireOp",EDGE,"E7.33.1"),sQuery(id+"F0.wireOp",EDGE,"E7.33.2"),sQuery(id+"F0.wireOp",EDGE,"E7.33.3"),sQuery(id+"F0.wireOp",EDGE,"E7.33.4"),sQuery(id+"F0.wireOp",EDGE,"E7.33.5"),sQuery(id+"F0.wireOp",EDGE,"E7.34.0"),sQuery(id+"F0.wireOp",EDGE,"E7.34.1"),sQuery(id+"F0.wireOp",EDGE,"E7.34.2"),sQuery(id+"F0.wireOp",EDGE,"E7.34.3"),sQuery(id+"F0.wireOp",EDGE,"E7.34.4"),sQuery(id+"F0.wireOp",EDGE,"E7.34.5"),sQuery(id+"F0.wireOp",EDGE,"E7.35.0"),sQuery(id+"F0.wireOp",EDGE,"E7.35.1"),sQuery(id+"F0.wireOp",EDGE,"E7.35.2"),sQuery(id+"F0.wireOp",EDGE,"E7.35.3"),sQuery(id+"F0.wireOp",EDGE,"E7.35.4"),sQuery(id+"F0.wireOp",EDGE,"E7.35.5"),sQuery(id+"F0.wireOp",EDGE,"E7.36.0"),sQuery(id+"F0.wireOp",EDGE,"E7.36.1"),sQuery(id+"F0.wireOp",EDGE,"E7.36.2"),sQuery(id+"F0.wireOp",EDGE,"E7.36.3"),sQuery(id+"F0.wireOp",EDGE,"E7.36.4"),sQuery(id+"F0.wireOp",EDGE,"E7.36.5"),sQuery(id+"F0.wireOp",EDGE,"E7.37.0"),sQuery(id+"F0.wireOp",EDGE,"E7.37.1"),sQuery(id+"F0.wireOp",EDGE,"E7.37.2"),sQuery(id+"F0.wireOp",EDGE,"E7.37.3"),sQuery(id+"F0.wireOp",EDGE,"E7.37.4"),sQuery(id+"F0.wireOp",EDGE,"E7.37.5"),sQuery(id+"F0.wireOp",EDGE,"E7.38.0"),sQuery(id+"F0.wireOp",EDGE,"E7.38.1"),sQuery(id+"F0.wireOp",EDGE,"E7.38.2"),sQuery(id+"F0.wireOp",EDGE,"E7.38.3"),sQuery(id+"F0.wireOp",EDGE,"E7.38.4"),sQuery(id+"F0.wireOp",EDGE,"E7.38.5"),subQ0,sQuery(id+"F0.wireOp",EDGE,"E7.39.1"),sQuery(id+"F0.wireOp",EDGE,"E7.39.2"),sQuery(id+"F0.wireOp",EDGE,"E7.39.3"),sQuery(id+"F0.wireOp",EDGE,"E7.39.4"),sQuery(id+"F0.wireOp",EDGE,"E7.39.5"),sQuery(id+"F0.wireOp",EDGE,"E7.40.0"),sQuery(id+"F0.wireOp",EDGE,"E7.40.1"),sQuery(id+"F0.wireOp",EDGE,"E7.40.2"),sQuery(id+"F0.wireOp",EDGE,"E7.40.3"),sQuery(id+"F0.wireOp",EDGE,"E7.40.4"),sQuery(id+"F0.wireOp",EDGE,"E7.40.5"),sQuery(id+"F0.wireOp",EDGE,"E7.41.0"),sQuery(id+"F0.wireOp",EDGE,"E7.41.1"),sQuery(id+"F0.wireOp",EDGE,"E7.41.2"),sQuery(id+"F0.wireOp",EDGE,"E7.41.3"),sQuery(id+"F0.wireOp",EDGE,"E7.41.4"),sQuery(id+"F0.wireOp",EDGE,"E7.41.5"),sQuery(id+"F0.wireOp",EDGE,"E7.42.0"),sQuery(id+"F0.wireOp",EDGE,"E7.42.1"),sQuery(id+"F0.wireOp",EDGE,"E7.42.2"),sQuery(id+"F0.wireOp",EDGE,"E7.42.3"),sQuery(id+"F0.wireOp",EDGE,"E7.42.4"),sQuery(id+"F0.wireOp",EDGE,"E7.42.5"),sQuery(id+"F0.wireOp",EDGE,"E7.43.0"),sQuery(id+"F0.wireOp",EDGE,"E7.43.1"),sQuery(id+"F0.wireOp",EDGE,"E7.43.2"),sQuery(id+"F0.wireOp",EDGE,"E7.43.3"),sQuery(id+"F0.wireOp",EDGE,"E7.43.4"),sQuery(id+"F0.wireOp",EDGE,"E7.43.5")])],"isStart":false})]});}
            var Q3;
            {var subQ0=sQuery(id+"F0.wireOp",EDGE,"E7.37.0");Q3=makeQuery(id+"F2.opChamfer","BLEND_EDGE",EDGE,{"blendedFrom":[makeQuery(id+"F1.opExtrude","CAP_EDGE",EDGE,{"disambiguationData":[OSD([subQ0])],"isStart":false}),makeQuery(id+"F1.opExtrude","CAP_FACE",FACE,{"disambiguationData":[OSD([sQuery(id+"F0.wireOp",EDGE,"E1"),sQuery(id+"F0.wireOp",EDGE,"E2"),sQuery(id+"F0.wireOp",EDGE,"E3"),sQuery(id+"F0.wireOp",EDGE,"E4"),sQuery(id+"F0.wireOp",EDGE,"E5"),sQuery(id+"F0.wireOp",EDGE,"E6"),sQuery(id+"F0.wireOp",EDGE,"E7.1.0"),sQuery(id+"F0.wireOp",EDGE,"E7.1.1"),sQuery(id+"F0.wireOp",EDGE,"E7.1.2"),sQuery(id+"F0.wireOp",EDGE,"E7.1.3"),sQuery(id+"F0.wireOp",EDGE,"E7.1.4"),sQuery(id+"F0.wireOp",EDGE,"E7.1.5"),sQuery(id+"F0.wireOp",EDGE,"E7.2.0"),sQuery(id+"F0.wireOp",EDGE,"E7.2.1"),sQuery(id+"F0.wireOp",EDGE,"E7.2.2"),sQuery(id+"F0.wireOp",EDGE,"E7.2.3"),sQuery(id+"F0.wireOp",EDGE,"E7.2.4"),sQuery(id+"F0.wireOp",EDGE,"E7.2.5"),sQuery(id+"F0.wireOp",EDGE,"E7.3.0"),sQuery(id+"F0.wireOp",EDGE,"E7.3.1"),sQuery(id+"F0.wireOp",EDGE,"E7.3.2"),sQuery(id+"F0.wireOp",EDGE,"E7.3.3"),sQuery(id+"F0.wireOp",EDGE,"E7.3.4"),sQuery(id+"F0.wireOp",EDGE,"E7.3.5"),sQuery(id+"F0.wireOp",EDGE,"E7.4.0"),sQuery(id+"F0.wireOp",EDGE,"E7.4.1"),sQuery(id+"F0.wireOp",EDGE,"E7.4.2"),sQuery(id+"F0.wireOp",EDGE,"E7.4.3"),sQuery(id+"F0.wireOp",EDGE,"E7.4.4"),sQuery(id+"F0.wireOp",EDGE,"E7.4.5"),sQuery(id+"F0.wireOp",EDGE,"E7.5.0"),sQuery(id+"F0.wireOp",EDGE,"E7.5.1"),sQuery(id+"F0.wireOp",EDGE,"E7.5.2"),sQuery(id+"F0.wireOp",EDGE,"E7.5.3"),sQuery(id+"F0.wireOp",EDGE,"E7.5.4"),sQuery(id+"F0.wireOp",EDGE,"E7.5.5"),sQuery(id+"F0.wireOp",EDGE,"E7.6.0"),sQuery(id+"F0.wireOp",EDGE,"E7.6.1"),sQuery(id+"F0.wireOp",EDGE,"E7.6.2"),sQuery(id+"F0.wireOp",EDGE,"E7.6.3"),sQuery(id+"F0.wireOp",EDGE,"E7.6.4"),sQuery(id+"F0.wireOp",EDGE,"E7.6.5"),sQuery(id+"F0.wireOp",EDGE,"E7.7.0"),sQuery(id+"F0.wireOp",EDGE,"E7.7.1"),sQuery(id+"F0.wireOp",EDGE,"E7.7.2"),sQuery(id+"F0.wireOp",EDGE,"E7.7.3"),sQuery(id+"F0.wireOp",EDGE,"E7.7.4"),sQuery(id+"F0.wireOp",EDGE,"E7.7.5"),sQuery(id+"F0.wireOp",EDGE,"E7.8.0"),sQuery(id+"F0.wireOp",EDGE,"E7.8.1"),sQuery(id+"F0.wireOp",EDGE,"E7.8.2"),sQuery(id+"F0.wireOp",EDGE,"E7.8.3"),sQuery(id+"F0.wireOp",EDGE,"E7.8.4"),sQuery(id+"F0.wireOp",EDGE,"E7.8.5"),sQuery(id+"F0.wireOp",EDGE,"E7.9.0"),sQuery(id+"F0.wireOp",EDGE,"E7.9.1"),sQuery(id+"F0.wireOp",EDGE,"E7.9.2"),sQuery(id+"F0.wireOp",EDGE,"E7.9.3"),sQuery(id+"F0.wireOp",EDGE,"E7.9.4"),sQuery(id+"F0.wireOp",EDGE,"E7.9.5"),sQuery(id+"F0.wireOp",EDGE,"E7.10.0"),sQuery(id+"F0.wireOp",EDGE,"E7.10.1"),sQuery(id+"F0.wireOp",EDGE,"E7.10.2"),sQuery(id+"F0.wireOp",EDGE,"E7.10.3"),sQuery(id+"F0.wireOp",EDGE,"E7.10.4"),sQuery(id+"F0.wireOp",EDGE,"E7.10.5"),sQuery(id+"F0.wireOp",EDGE,"E7.11.0"),sQuery(id+"F0.wireOp",EDGE,"E7.11.1"),sQuery(id+"F0.wireOp",EDGE,"E7.11.2"),sQuery(id+"F0.wireOp",EDGE,"E7.11.3"),sQuery(id+"F0.wireOp",EDGE,"E7.11.4"),sQuery(id+"F0.wireOp",EDGE,"E7.11.5"),sQuery(id+"F0.wireOp",EDGE,"E7.12.0"),sQuery(id+"F0.wireOp",EDGE,"E7.12.1"),sQuery(id+"F0.wireOp",EDGE,"E7.12.2"),sQuery(id+"F0.wireOp",EDGE,"E7.12.3"),sQuery(id+"F0.wireOp",EDGE,"E7.12.4"),sQuery(id+"F0.wireOp",EDGE,"E7.12.5"),sQuery(id+"F0.wireOp",EDGE,"E7.13.0"),sQuery(id+"F0.wireOp",EDGE,"E7.13.1"),sQuery(id+"F0.wireOp",EDGE,"E7.13.2"),sQuery(id+"F0.wireOp",EDGE,"E7.13.3"),sQuery(id+"F0.wireOp",EDGE,"E7.13.4"),sQuery(id+"F0.wireOp",EDGE,"E7.13.5"),sQuery(id+"F0.wireOp",EDGE,"E7.14.0"),sQuery(id+"F0.wireOp",EDGE,"E7.14.1"),sQuery(id+"F0.wireOp",EDGE,"E7.14.2"),sQuery(id+"F0.wireOp",EDGE,"E7.14.3"),sQuery(id+"F0.wireOp",EDGE,"E7.14.4"),sQuery(id+"F0.wireOp",EDGE,"E7.14.5"),sQuery(id+"F0.wireOp",EDGE,"E7.15.0"),sQuery(id+"F0.wireOp",EDGE,"E7.15.1"),sQuery(id+"F0.wireOp",EDGE,"E7.15.2"),sQuery(id+"F0.wireOp",EDGE,"E7.15.3"),sQuery(id+"F0.wireOp",EDGE,"E7.15.4"),sQuery(id+"F0.wireOp",EDGE,"E7.15.5"),sQuery(id+"F0.wireOp",EDGE,"E7.16.0"),sQuery(id+"F0.wireOp",EDGE,"E7.16.1"),sQuery(id+"F0.wireOp",EDGE,"E7.16.2"),sQuery(id+"F0.wireOp",EDGE,"E7.16.3"),sQuery(id+"F0.wireOp",EDGE,"E7.16.4"),sQuery(id+"F0.wireOp",EDGE,"E7.16.5"),sQuery(id+"F0.wireOp",EDGE,"E7.17.0"),sQuery(id+"F0.wireOp",EDGE,"E7.17.1"),sQuery(id+"F0.wireOp",EDGE,"E7.17.2"),sQuery(id+"F0.wireOp",EDGE,"E7.17.3"),sQuery(id+"F0.wireOp",EDGE,"E7.17.4"),sQuery(id+"F0.wireOp",EDGE,"E7.17.5"),sQuery(id+"F0.wireOp",EDGE,"E7.18.0"),sQuery(id+"F0.wireOp",EDGE,"E7.18.1"),sQuery(id+"F0.wireOp",EDGE,"E7.18.2"),sQuery(id+"F0.wireOp",EDGE,"E7.18.3"),sQuery(id+"F0.wireOp",EDGE,"E7.18.4"),sQuery(id+"F0.wireOp",EDGE,"E7.18.5"),sQuery(id+"F0.wireOp",EDGE,"E7.19.0"),sQuery(id+"F0.wireOp",EDGE,"E7.19.1"),sQuery(id+"F0.wireOp",EDGE,"E7.19.2"),sQuery(id+"F0.wireOp",EDGE,"E7.19.3"),sQuery(id+"F0.wireOp",EDGE,"E7.19.4"),sQuery(id+"F0.wireOp",EDGE,"E7.19.5"),sQuery(id+"F0.wireOp",EDGE,"E7.20.0"),sQuery(id+"F0.wireOp",EDGE,"E7.20.1"),sQuery(id+"F0.wireOp",EDGE,"E7.20.2"),sQuery(id+"F0.wireOp",EDGE,"E7.20.3"),sQuery(id+"F0.wireOp",EDGE,"E7.20.4"),sQuery(id+"F0.wireOp",EDGE,"E7.20.5"),sQuery(id+"F0.wireOp",EDGE,"E7.21.0"),sQuery(id+"F0.wireOp",EDGE,"E7.21.1"),sQuery(id+"F0.wireOp",EDGE,"E7.21.2"),sQuery(id+"F0.wireOp",EDGE,"E7.21.3"),sQuery(id+"F0.wireOp",EDGE,"E7.21.4"),sQuery(id+"F0.wireOp",EDGE,"E7.21.5"),sQuery(id+"F0.wireOp",EDGE,"E7.22.0"),sQuery(id+"F0.wireOp",EDGE,"E7.22.1"),sQuery(id+"F0.wireOp",EDGE,"E7.22.2"),sQuery(id+"F0.wireOp",EDGE,"E7.22.3"),sQuery(id+"F0.wireOp",EDGE,"E7.22.4"),sQuery(id+"F0.wireOp",EDGE,"E7.22.5"),sQuery(id+"F0.wireOp",EDGE,"E7.23.0"),sQuery(id+"F0.wireOp",EDGE,"E7.23.1"),sQuery(id+"F0.wireOp",EDGE,"E7.23.2"),sQuery(id+"F0.wireOp",EDGE,"E7.23.3"),sQuery(id+"F0.wireOp",EDGE,"E7.23.4"),sQuery(id+"F0.wireOp",EDGE,"E7.23.5"),sQuery(id+"F0.wireOp",EDGE,"E7.24.0"),sQuery(id+"F0.wireOp",EDGE,"E7.24.1"),sQuery(id+"F0.wireOp",EDGE,"E7.24.2"),sQuery(id+"F0.wireOp",EDGE,"E7.24.3"),sQuery(id+"F0.wireOp",EDGE,"E7.24.4"),sQuery(id+"F0.wireOp",EDGE,"E7.24.5"),sQuery(id+"F0.wireOp",EDGE,"E7.25.0"),sQuery(id+"F0.wireOp",EDGE,"E7.25.1"),sQuery(id+"F0.wireOp",EDGE,"E7.25.2"),sQuery(id+"F0.wireOp",EDGE,"E7.25.3"),sQuery(id+"F0.wireOp",EDGE,"E7.25.4"),sQuery(id+"F0.wireOp",EDGE,"E7.25.5"),sQuery(id+"F0.wireOp",EDGE,"E7.26.0"),sQuery(id+"F0.wireOp",EDGE,"E7.26.1"),sQuery(id+"F0.wireOp",EDGE,"E7.26.2"),sQuery(id+"F0.wireOp",EDGE,"E7.26.3"),sQuery(id+"F0.wireOp",EDGE,"E7.26.4"),sQuery(id+"F0.wireOp",EDGE,"E7.26.5"),sQuery(id+"F0.wireOp",EDGE,"E7.27.0"),sQuery(id+"F0.wireOp",EDGE,"E7.27.1"),sQuery(id+"F0.wireOp",EDGE,"E7.27.2"),sQuery(id+"F0.wireOp",EDGE,"E7.27.3"),sQuery(id+"F0.wireOp",EDGE,"E7.27.4"),sQuery(id+"F0.wireOp",EDGE,"E7.27.5"),sQuery(id+"F0.wireOp",EDGE,"E7.28.0"),sQuery(id+"F0.wireOp",EDGE,"E7.28.1"),sQuery(id+"F0.wireOp",EDGE,"E7.28.2"),sQuery(id+"F0.wireOp",EDGE,"E7.28.3"),sQuery(id+"F0.wireOp",EDGE,"E7.28.4"),sQuery(id+"F0.wireOp",EDGE,"E7.28.5"),sQuery(id+"F0.wireOp",EDGE,"E7.29.0"),sQuery(id+"F0.wireOp",EDGE,"E7.29.1"),sQuery(id+"F0.wireOp",EDGE,"E7.29.2"),sQuery(id+"F0.wireOp",EDGE,"E7.29.3"),sQuery(id+"F0.wireOp",EDGE,"E7.29.4"),sQuery(id+"F0.wireOp",EDGE,"E7.29.5"),sQuery(id+"F0.wireOp",EDGE,"E7.30.0"),sQuery(id+"F0.wireOp",EDGE,"E7.30.1"),sQuery(id+"F0.wireOp",EDGE,"E7.30.2"),sQuery(id+"F0.wireOp",EDGE,"E7.30.3"),sQuery(id+"F0.wireOp",EDGE,"E7.30.4"),sQuery(id+"F0.wireOp",EDGE,"E7.30.5"),sQuery(id+"F0.wireOp",EDGE,"E7.31.0"),sQuery(id+"F0.wireOp",EDGE,"E7.31.1"),sQuery(id+"F0.wireOp",EDGE,"E7.31.2"),sQuery(id+"F0.wireOp",EDGE,"E7.31.3"),sQuery(id+"F0.wireOp",EDGE,"E7.31.4"),sQuery(id+"F0.wireOp",EDGE,"E7.31.5"),sQuery(id+"F0.wireOp",EDGE,"E7.32.0"),sQuery(id+"F0.wireOp",EDGE,"E7.32.1"),sQuery(id+"F0.wireOp",EDGE,"E7.32.2"),sQuery(id+"F0.wireOp",EDGE,"E7.32.3"),sQuery(id+"F0.wireOp",EDGE,"E7.32.4"),sQuery(id+"F0.wireOp",EDGE,"E7.32.5"),sQuery(id+"F0.wireOp",EDGE,"E7.33.0"),sQuery(id+"F0.wireOp",EDGE,"E7.33.1"),sQuery(id+"F0.wireOp",EDGE,"E7.33.2"),sQuery(id+"F0.wireOp",EDGE,"E7.33.3"),sQuery(id+"F0.wireOp",EDGE,"E7.33.4"),sQuery(id+"F0.wireOp",EDGE,"E7.33.5"),sQuery(id+"F0.wireOp",EDGE,"E7.34.0"),sQuery(id+"F0.wireOp",EDGE,"E7.34.1"),sQuery(id+"F0.wireOp",EDGE,"E7.34.2"),sQuery(id+"F0.wireOp",EDGE,"E7.34.3"),sQuery(id+"F0.wireOp",EDGE,"E7.34.4"),sQuery(id+"F0.wireOp",EDGE,"E7.34.5"),sQuery(id+"F0.wireOp",EDGE,"E7.35.0"),sQuery(id+"F0.wireOp",EDGE,"E7.35.1"),sQuery(id+"F0.wireOp",EDGE,"E7.35.2"),sQuery(id+"F0.wireOp",EDGE,"E7.35.3"),sQuery(id+"F0.wireOp",EDGE,"E7.35.4"),sQuery(id+"F0.wireOp",EDGE,"E7.35.5"),sQuery(id+"F0.wireOp",EDGE,"E7.36.0"),sQuery(id+"F0.wireOp",EDGE,"E7.36.1"),sQuery(id+"F0.wireOp",EDGE,"E7.36.2"),sQuery(id+"F0.wireOp",EDGE,"E7.36.3"),sQuery(id+"F0.wireOp",EDGE,"E7.36.4"),sQuery(id+"F0.wireOp",EDGE,"E7.36.5"),subQ0,sQuery(id+"F0.wireOp",EDGE,"E7.37.1"),sQuery(id+"F0.wireOp",EDGE,"E7.37.2"),sQuery(id+"F0.wireOp",EDGE,"E7.37.3"),sQuery(id+"F0.wireOp",EDGE,"E7.37.4"),sQuery(id+"F0.wireOp",EDGE,"E7.37.5"),sQuery(id+"F0.wireOp",EDGE,"E7.38.0"),sQuery(id+"F0.wireOp",EDGE,"E7.38.1"),sQuery(id+"F0.wireOp",EDGE,"E7.38.2"),sQuery(id+"F0.wireOp",EDGE,"E7.38.3"),sQuery(id+"F0.wireOp",EDGE,"E7.38.4"),sQuery(id+"F0.wireOp",EDGE,"E7.38.5"),sQuery(id+"F0.wireOp",EDGE,"E7.39.0"),sQuery(id+"F0.wireOp",EDGE,"E7.39.1"),sQuery(id+"F0.wireOp",EDGE,"E7.39.2"),sQuery(id+"F0.wireOp",EDGE,"E7.39.3"),sQuery(id+"F0.wireOp",EDGE,"E7.39.4"),sQuery(id+"F0.wireOp",EDGE,"E7.39.5"),sQuery(id+"F0.wireOp",EDGE,"E7.40.0"),sQuery(id+"F0.wireOp",EDGE,"E7.40.1"),sQuery(id+"F0.wireOp",EDGE,"E7.40.2"),sQuery(id+"F0.wireOp",EDGE,"E7.40.3"),sQuery(id+"F0.wireOp",EDGE,"E7.40.4"),sQuery(id+"F0.wireOp",EDGE,"E7.40.5"),sQuery(id+"F0.wireOp",EDGE,"E7.41.0"),sQuery(id+"F0.wireOp",EDGE,"E7.41.1"),sQuery(id+"F0.wireOp",EDGE,"E7.41.2"),sQuery(id+"F0.wireOp",EDGE,"E7.41.3"),sQuery(id+"F0.wireOp",EDGE,"E7.41.4"),sQuery(id+"F0.wireOp",EDGE,"E7.41.5"),sQuery(id+"F0.wireOp",EDGE,"E7.42.0"),sQuery(id+"F0.wireOp",EDGE,"E7.42.1"),sQuery(id+"F0.wireOp",EDGE,"E7.42.2"),sQuery(id+"F0.wireOp",EDGE,"E7.42.3"),sQuery(id+"F0.wireOp",EDGE,"E7.42.4"),sQuery(id+"F0.wireOp",EDGE,"E7.42.5"),sQuery(id+"F0.wireOp",EDGE,"E7.43.0"),sQuery(id+"F0.wireOp",EDGE,"E7.43.1"),sQuery(id+"F0.wireOp",EDGE,"E7.43.2"),sQuery(id+"F0.wireOp",EDGE,"E7.43.3"),sQuery(id+"F0.wireOp",EDGE,"E7.43.4"),sQuery(id+"F0.wireOp",EDGE,"E7.43.5")])],"isStart":false})],"blendedInto":[makeQuery(id+"F1.opExtrude","CAP_FACE",FACE,{"disambiguationData":[OSD([sQuery(id+"F0.wireOp",EDGE,"E1"),sQuery(id+"F0.wireOp",EDGE,"E2"),sQuery(id+"F0.wireOp",EDGE,"E3"),sQuery(id+"F0.wireOp",EDGE,"E4"),sQuery(id+"F0.wireOp",EDGE,"E5"),sQuery(id+"F0.wireOp",EDGE,"E6"),sQuery(id+"F0.wireOp",EDGE,"E7.1.0"),sQuery(id+"F0.wireOp",EDGE,"E7.1.1"),sQuery(id+"F0.wireOp",EDGE,"E7.1.2"),sQuery(id+"F0.wireOp",EDGE,"E7.1.3"),sQuery(id+"F0.wireOp",EDGE,"E7.1.4"),sQuery(id+"F0.wireOp",EDGE,"E7.1.5"),sQuery(id+"F0.wireOp",EDGE,"E7.2.0"),sQuery(id+"F0.wireOp",EDGE,"E7.2.1"),sQuery(id+"F0.wireOp",EDGE,"E7.2.2"),sQuery(id+"F0.wireOp",EDGE,"E7.2.3"),sQuery(id+"F0.wireOp",EDGE,"E7.2.4"),sQuery(id+"F0.wireOp",EDGE,"E7.2.5"),sQuery(id+"F0.wireOp",EDGE,"E7.3.0"),sQuery(id+"F0.wireOp",EDGE,"E7.3.1"),sQuery(id+"F0.wireOp",EDGE,"E7.3.2"),sQuery(id+"F0.wireOp",EDGE,"E7.3.3"),sQuery(id+"F0.wireOp",EDGE,"E7.3.4"),sQuery(id+"F0.wireOp",EDGE,"E7.3.5"),sQuery(id+"F0.wireOp",EDGE,"E7.4.0"),sQuery(id+"F0.wireOp",EDGE,"E7.4.1"),sQuery(id+"F0.wireOp",EDGE,"E7.4.2"),sQuery(id+"F0.wireOp",EDGE,"E7.4.3"),sQuery(id+"F0.wireOp",EDGE,"E7.4.4"),sQuery(id+"F0.wireOp",EDGE,"E7.4.5"),sQuery(id+"F0.wireOp",EDGE,"E7.5.0"),sQuery(id+"F0.wireOp",EDGE,"E7.5.1"),sQuery(id+"F0.wireOp",EDGE,"E7.5.2"),sQuery(id+"F0.wireOp",EDGE,"E7.5.3"),sQuery(id+"F0.wireOp",EDGE,"E7.5.4"),sQuery(id+"F0.wireOp",EDGE,"E7.5.5"),sQuery(id+"F0.wireOp",EDGE,"E7.6.0"),sQuery(id+"F0.wireOp",EDGE,"E7.6.1"),sQuery(id+"F0.wireOp",EDGE,"E7.6.2"),sQuery(id+"F0.wireOp",EDGE,"E7.6.3"),sQuery(id+"F0.wireOp",EDGE,"E7.6.4"),sQuery(id+"F0.wireOp",EDGE,"E7.6.5"),sQuery(id+"F0.wireOp",EDGE,"E7.7.0"),sQuery(id+"F0.wireOp",EDGE,"E7.7.1"),sQuery(id+"F0.wireOp",EDGE,"E7.7.2"),sQuery(id+"F0.wireOp",EDGE,"E7.7.3"),sQuery(id+"F0.wireOp",EDGE,"E7.7.4"),sQuery(id+"F0.wireOp",EDGE,"E7.7.5"),sQuery(id+"F0.wireOp",EDGE,"E7.8.0"),sQuery(id+"F0.wireOp",EDGE,"E7.8.1"),sQuery(id+"F0.wireOp",EDGE,"E7.8.2"),sQuery(id+"F0.wireOp",EDGE,"E7.8.3"),sQuery(id+"F0.wireOp",EDGE,"E7.8.4"),sQuery(id+"F0.wireOp",EDGE,"E7.8.5"),sQuery(id+"F0.wireOp",EDGE,"E7.9.0"),sQuery(id+"F0.wireOp",EDGE,"E7.9.1"),sQuery(id+"F0.wireOp",EDGE,"E7.9.2"),sQuery(id+"F0.wireOp",EDGE,"E7.9.3"),sQuery(id+"F0.wireOp",EDGE,"E7.9.4"),sQuery(id+"F0.wireOp",EDGE,"E7.9.5"),sQuery(id+"F0.wireOp",EDGE,"E7.10.0"),sQuery(id+"F0.wireOp",EDGE,"E7.10.1"),sQuery(id+"F0.wireOp",EDGE,"E7.10.2"),sQuery(id+"F0.wireOp",EDGE,"E7.10.3"),sQuery(id+"F0.wireOp",EDGE,"E7.10.4"),sQuery(id+"F0.wireOp",EDGE,"E7.10.5"),sQuery(id+"F0.wireOp",EDGE,"E7.11.0"),sQuery(id+"F0.wireOp",EDGE,"E7.11.1"),sQuery(id+"F0.wireOp",EDGE,"E7.11.2"),sQuery(id+"F0.wireOp",EDGE,"E7.11.3"),sQuery(id+"F0.wireOp",EDGE,"E7.11.4"),sQuery(id+"F0.wireOp",EDGE,"E7.11.5"),sQuery(id+"F0.wireOp",EDGE,"E7.12.0"),sQuery(id+"F0.wireOp",EDGE,"E7.12.1"),sQuery(id+"F0.wireOp",EDGE,"E7.12.2"),sQuery(id+"F0.wireOp",EDGE,"E7.12.3"),sQuery(id+"F0.wireOp",EDGE,"E7.12.4"),sQuery(id+"F0.wireOp",EDGE,"E7.12.5"),sQuery(id+"F0.wireOp",EDGE,"E7.13.0"),sQuery(id+"F0.wireOp",EDGE,"E7.13.1"),sQuery(id+"F0.wireOp",EDGE,"E7.13.2"),sQuery(id+"F0.wireOp",EDGE,"E7.13.3"),sQuery(id+"F0.wireOp",EDGE,"E7.13.4"),sQuery(id+"F0.wireOp",EDGE,"E7.13.5"),sQuery(id+"F0.wireOp",EDGE,"E7.14.0"),sQuery(id+"F0.wireOp",EDGE,"E7.14.1"),sQuery(id+"F0.wireOp",EDGE,"E7.14.2"),sQuery(id+"F0.wireOp",EDGE,"E7.14.3"),sQuery(id+"F0.wireOp",EDGE,"E7.14.4"),sQuery(id+"F0.wireOp",EDGE,"E7.14.5"),sQuery(id+"F0.wireOp",EDGE,"E7.15.0"),sQuery(id+"F0.wireOp",EDGE,"E7.15.1"),sQuery(id+"F0.wireOp",EDGE,"E7.15.2"),sQuery(id+"F0.wireOp",EDGE,"E7.15.3"),sQuery(id+"F0.wireOp",EDGE,"E7.15.4"),sQuery(id+"F0.wireOp",EDGE,"E7.15.5"),sQuery(id+"F0.wireOp",EDGE,"E7.16.0"),sQuery(id+"F0.wireOp",EDGE,"E7.16.1"),sQuery(id+"F0.wireOp",EDGE,"E7.16.2"),sQuery(id+"F0.wireOp",EDGE,"E7.16.3"),sQuery(id+"F0.wireOp",EDGE,"E7.16.4"),sQuery(id+"F0.wireOp",EDGE,"E7.16.5"),sQuery(id+"F0.wireOp",EDGE,"E7.17.0"),sQuery(id+"F0.wireOp",EDGE,"E7.17.1"),sQuery(id+"F0.wireOp",EDGE,"E7.17.2"),sQuery(id+"F0.wireOp",EDGE,"E7.17.3"),sQuery(id+"F0.wireOp",EDGE,"E7.17.4"),sQuery(id+"F0.wireOp",EDGE,"E7.17.5"),sQuery(id+"F0.wireOp",EDGE,"E7.18.0"),sQuery(id+"F0.wireOp",EDGE,"E7.18.1"),sQuery(id+"F0.wireOp",EDGE,"E7.18.2"),sQuery(id+"F0.wireOp",EDGE,"E7.18.3"),sQuery(id+"F0.wireOp",EDGE,"E7.18.4"),sQuery(id+"F0.wireOp",EDGE,"E7.18.5"),sQuery(id+"F0.wireOp",EDGE,"E7.19.0"),sQuery(id+"F0.wireOp",EDGE,"E7.19.1"),sQuery(id+"F0.wireOp",EDGE,"E7.19.2"),sQuery(id+"F0.wireOp",EDGE,"E7.19.3"),sQuery(id+"F0.wireOp",EDGE,"E7.19.4"),sQuery(id+"F0.wireOp",EDGE,"E7.19.5"),sQuery(id+"F0.wireOp",EDGE,"E7.20.0"),sQuery(id+"F0.wireOp",EDGE,"E7.20.1"),sQuery(id+"F0.wireOp",EDGE,"E7.20.2"),sQuery(id+"F0.wireOp",EDGE,"E7.20.3"),sQuery(id+"F0.wireOp",EDGE,"E7.20.4"),sQuery(id+"F0.wireOp",EDGE,"E7.20.5"),sQuery(id+"F0.wireOp",EDGE,"E7.21.0"),sQuery(id+"F0.wireOp",EDGE,"E7.21.1"),sQuery(id+"F0.wireOp",EDGE,"E7.21.2"),sQuery(id+"F0.wireOp",EDGE,"E7.21.3"),sQuery(id+"F0.wireOp",EDGE,"E7.21.4"),sQuery(id+"F0.wireOp",EDGE,"E7.21.5"),sQuery(id+"F0.wireOp",EDGE,"E7.22.0"),sQuery(id+"F0.wireOp",EDGE,"E7.22.1"),sQuery(id+"F0.wireOp",EDGE,"E7.22.2"),sQuery(id+"F0.wireOp",EDGE,"E7.22.3"),sQuery(id+"F0.wireOp",EDGE,"E7.22.4"),sQuery(id+"F0.wireOp",EDGE,"E7.22.5"),sQuery(id+"F0.wireOp",EDGE,"E7.23.0"),sQuery(id+"F0.wireOp",EDGE,"E7.23.1"),sQuery(id+"F0.wireOp",EDGE,"E7.23.2"),sQuery(id+"F0.wireOp",EDGE,"E7.23.3"),sQuery(id+"F0.wireOp",EDGE,"E7.23.4"),sQuery(id+"F0.wireOp",EDGE,"E7.23.5"),sQuery(id+"F0.wireOp",EDGE,"E7.24.0"),sQuery(id+"F0.wireOp",EDGE,"E7.24.1"),sQuery(id+"F0.wireOp",EDGE,"E7.24.2"),sQuery(id+"F0.wireOp",EDGE,"E7.24.3"),sQuery(id+"F0.wireOp",EDGE,"E7.24.4"),sQuery(id+"F0.wireOp",EDGE,"E7.24.5"),sQuery(id+"F0.wireOp",EDGE,"E7.25.0"),sQuery(id+"F0.wireOp",EDGE,"E7.25.1"),sQuery(id+"F0.wireOp",EDGE,"E7.25.2"),sQuery(id+"F0.wireOp",EDGE,"E7.25.3"),sQuery(id+"F0.wireOp",EDGE,"E7.25.4"),sQuery(id+"F0.wireOp",EDGE,"E7.25.5"),sQuery(id+"F0.wireOp",EDGE,"E7.26.0"),sQuery(id+"F0.wireOp",EDGE,"E7.26.1"),sQuery(id+"F0.wireOp",EDGE,"E7.26.2"),sQuery(id+"F0.wireOp",EDGE,"E7.26.3"),sQuery(id+"F0.wireOp",EDGE,"E7.26.4"),sQuery(id+"F0.wireOp",EDGE,"E7.26.5"),sQuery(id+"F0.wireOp",EDGE,"E7.27.0"),sQuery(id+"F0.wireOp",EDGE,"E7.27.1"),sQuery(id+"F0.wireOp",EDGE,"E7.27.2"),sQuery(id+"F0.wireOp",EDGE,"E7.27.3"),sQuery(id+"F0.wireOp",EDGE,"E7.27.4"),sQuery(id+"F0.wireOp",EDGE,"E7.27.5"),sQuery(id+"F0.wireOp",EDGE,"E7.28.0"),sQuery(id+"F0.wireOp",EDGE,"E7.28.1"),sQuery(id+"F0.wireOp",EDGE,"E7.28.2"),sQuery(id+"F0.wireOp",EDGE,"E7.28.3"),sQuery(id+"F0.wireOp",EDGE,"E7.28.4"),sQuery(id+"F0.wireOp",EDGE,"E7.28.5"),sQuery(id+"F0.wireOp",EDGE,"E7.29.0"),sQuery(id+"F0.wireOp",EDGE,"E7.29.1"),sQuery(id+"F0.wireOp",EDGE,"E7.29.2"),sQuery(id+"F0.wireOp",EDGE,"E7.29.3"),sQuery(id+"F0.wireOp",EDGE,"E7.29.4"),sQuery(id+"F0.wireOp",EDGE,"E7.29.5"),sQuery(id+"F0.wireOp",EDGE,"E7.30.0"),sQuery(id+"F0.wireOp",EDGE,"E7.30.1"),sQuery(id+"F0.wireOp",EDGE,"E7.30.2"),sQuery(id+"F0.wireOp",EDGE,"E7.30.3"),sQuery(id+"F0.wireOp",EDGE,"E7.30.4"),sQuery(id+"F0.wireOp",EDGE,"E7.30.5"),sQuery(id+"F0.wireOp",EDGE,"E7.31.0"),sQuery(id+"F0.wireOp",EDGE,"E7.31.1"),sQuery(id+"F0.wireOp",EDGE,"E7.31.2"),sQuery(id+"F0.wireOp",EDGE,"E7.31.3"),sQuery(id+"F0.wireOp",EDGE,"E7.31.4"),sQuery(id+"F0.wireOp",EDGE,"E7.31.5"),sQuery(id+"F0.wireOp",EDGE,"E7.32.0"),sQuery(id+"F0.wireOp",EDGE,"E7.32.1"),sQuery(id+"F0.wireOp",EDGE,"E7.32.2"),sQuery(id+"F0.wireOp",EDGE,"E7.32.3"),sQuery(id+"F0.wireOp",EDGE,"E7.32.4"),sQuery(id+"F0.wireOp",EDGE,"E7.32.5"),sQuery(id+"F0.wireOp",EDGE,"E7.33.0"),sQuery(id+"F0.wireOp",EDGE,"E7.33.1"),sQuery(id+"F0.wireOp",EDGE,"E7.33.2"),sQuery(id+"F0.wireOp",EDGE,"E7.33.3"),sQuery(id+"F0.wireOp",EDGE,"E7.33.4"),sQuery(id+"F0.wireOp",EDGE,"E7.33.5"),sQuery(id+"F0.wireOp",EDGE,"E7.34.0"),sQuery(id+"F0.wireOp",EDGE,"E7.34.1"),sQuery(id+"F0.wireOp",EDGE,"E7.34.2"),sQuery(id+"F0.wireOp",EDGE,"E7.34.3"),sQuery(id+"F0.wireOp",EDGE,"E7.34.4"),sQuery(id+"F0.wireOp",EDGE,"E7.34.5"),sQuery(id+"F0.wireOp",EDGE,"E7.35.0"),sQuery(id+"F0.wireOp",EDGE,"E7.35.1"),sQuery(id+"F0.wireOp",EDGE,"E7.35.2"),sQuery(id+"F0.wireOp",EDGE,"E7.35.3"),sQuery(id+"F0.wireOp",EDGE,"E7.35.4"),sQuery(id+"F0.wireOp",EDGE,"E7.35.5"),sQuery(id+"F0.wireOp",EDGE,"E7.36.0"),sQuery(id+"F0.wireOp",EDGE,"E7.36.1"),sQuery(id+"F0.wireOp",EDGE,"E7.36.2"),sQuery(id+"F0.wireOp",EDGE,"E7.36.3"),sQuery(id+"F0.wireOp",EDGE,"E7.36.4"),sQuery(id+"F0.wireOp",EDGE,"E7.36.5"),subQ0,sQuery(id+"F0.wireOp",EDGE,"E7.37.1"),sQuery(id+"F0.wireOp",EDGE,"E7.37.2"),sQuery(id+"F0.wireOp",EDGE,"E7.37.3"),sQuery(id+"F0.wireOp",EDGE,"E7.37.4"),sQuery(id+"F0.wireOp",EDGE,"E7.37.5"),sQuery(id+"F0.wireOp",EDGE,"E7.38.0"),sQuery(id+"F0.wireOp",EDGE,"E7.38.1"),sQuery(id+"F0.wireOp",EDGE,"E7.38.2"),sQuery(id+"F0.wireOp",EDGE,"E7.38.3"),sQuery(id+"F0.wireOp",EDGE,"E7.38.4"),sQuery(id+"F0.wireOp",EDGE,"E7.38.5"),sQuery(id+"F0.wireOp",EDGE,"E7.39.0"),sQuery(id+"F0.wireOp",EDGE,"E7.39.1"),sQuery(id+"F0.wireOp",EDGE,"E7.39.2"),sQuery(id+"F0.wireOp",EDGE,"E7.39.3"),sQuery(id+"F0.wireOp",EDGE,"E7.39.4"),sQuery(id+"F0.wireOp",EDGE,"E7.39.5"),sQuery(id+"F0.wireOp",EDGE,"E7.40.0"),sQuery(id+"F0.wireOp",EDGE,"E7.40.1"),sQuery(id+"F0.wireOp",EDGE,"E7.40.2"),sQuery(id+"F0.wireOp",EDGE,"E7.40.3"),sQuery(id+"F0.wireOp",EDGE,"E7.40.4"),sQuery(id+"F0.wireOp",EDGE,"E7.40.5"),sQuery(id+"F0.wireOp",EDGE,"E7.41.0"),sQuery(id+"F0.wireOp",EDGE,"E7.41.1"),sQuery(id+"F0.wireOp",EDGE,"E7.41.2"),sQuery(id+"F0.wireOp",EDGE,"E7.41.3"),sQuery(id+"F0.wireOp",EDGE,"E7.41.4"),sQuery(id+"F0.wireOp",EDGE,"E7.41.5"),sQuery(id+"F0.wireOp",EDGE,"E7.42.0"),sQuery(id+"F0.wireOp",EDGE,"E7.42.1"),sQuery(id+"F0.wireOp",EDGE,"E7.42.2"),sQuery(id+"F0.wireOp",EDGE,"E7.42.3"),sQuery(id+"F0.wireOp",EDGE,"E7.42.4"),sQuery(id+"F0.wireOp",EDGE,"E7.42.5"),sQuery(id+"F0.wireOp",EDGE,"E7.43.0"),sQuery(id+"F0.wireOp",EDGE,"E7.43.1"),sQuery(id+"F0.wireOp",EDGE,"E7.43.2"),sQuery(id+"F0.wireOp",EDGE,"E7.43.3"),sQuery(id+"F0.wireOp",EDGE,"E7.43.4"),sQuery(id+"F0.wireOp",EDGE,"E7.43.5")])],"isStart":false})]});}
            var Q4;
            {var subQ0=sQuery(id+"F0.wireOp",EDGE,"E7.35.0");Q4=makeQuery(id+"F2.opChamfer","BLEND_EDGE",EDGE,{"blendedFrom":[makeQuery(id+"F1.opExtrude","CAP_EDGE",EDGE,{"disambiguationData":[OSD([subQ0])],"isStart":false}),makeQuery(id+"F1.opExtrude","CAP_FACE",FACE,{"disambiguationData":[OSD([sQuery(id+"F0.wireOp",EDGE,"E1"),sQuery(id+"F0.wireOp",EDGE,"E2"),sQuery(id+"F0.wireOp",EDGE,"E3"),sQuery(id+"F0.wireOp",EDGE,"E4"),sQuery(id+"F0.wireOp",EDGE,"E5"),sQuery(id+"F0.wireOp",EDGE,"E6"),sQuery(id+"F0.wireOp",EDGE,"E7.1.0"),sQuery(id+"F0.wireOp",EDGE,"E7.1.1"),sQuery(id+"F0.wireOp",EDGE,"E7.1.2"),sQuery(id+"F0.wireOp",EDGE,"E7.1.3"),sQuery(id+"F0.wireOp",EDGE,"E7.1.4"),sQuery(id+"F0.wireOp",EDGE,"E7.1.5"),sQuery(id+"F0.wireOp",EDGE,"E7.2.0"),sQuery(id+"F0.wireOp",EDGE,"E7.2.1"),sQuery(id+"F0.wireOp",EDGE,"E7.2.2"),sQuery(id+"F0.wireOp",EDGE,"E7.2.3"),sQuery(id+"F0.wireOp",EDGE,"E7.2.4"),sQuery(id+"F0.wireOp",EDGE,"E7.2.5"),sQuery(id+"F0.wireOp",EDGE,"E7.3.0"),sQuery(id+"F0.wireOp",EDGE,"E7.3.1"),sQuery(id+"F0.wireOp",EDGE,"E7.3.2"),sQuery(id+"F0.wireOp",EDGE,"E7.3.3"),sQuery(id+"F0.wireOp",EDGE,"E7.3.4"),sQuery(id+"F0.wireOp",EDGE,"E7.3.5"),sQuery(id+"F0.wireOp",EDGE,"E7.4.0"),sQuery(id+"F0.wireOp",EDGE,"E7.4.1"),sQuery(id+"F0.wireOp",EDGE,"E7.4.2"),sQuery(id+"F0.wireOp",EDGE,"E7.4.3"),sQuery(id+"F0.wireOp",EDGE,"E7.4.4"),sQuery(id+"F0.wireOp",EDGE,"E7.4.5"),sQuery(id+"F0.wireOp",EDGE,"E7.5.0"),sQuery(id+"F0.wireOp",EDGE,"E7.5.1"),sQuery(id+"F0.wireOp",EDGE,"E7.5.2"),sQuery(id+"F0.wireOp",EDGE,"E7.5.3"),sQuery(id+"F0.wireOp",EDGE,"E7.5.4"),sQuery(id+"F0.wireOp",EDGE,"E7.5.5"),sQuery(id+"F0.wireOp",EDGE,"E7.6.0"),sQuery(id+"F0.wireOp",EDGE,"E7.6.1"),sQuery(id+"F0.wireOp",EDGE,"E7.6.2"),sQuery(id+"F0.wireOp",EDGE,"E7.6.3"),sQuery(id+"F0.wireOp",EDGE,"E7.6.4"),sQuery(id+"F0.wireOp",EDGE,"E7.6.5"),sQuery(id+"F0.wireOp",EDGE,"E7.7.0"),sQuery(id+"F0.wireOp",EDGE,"E7.7.1"),sQuery(id+"F0.wireOp",EDGE,"E7.7.2"),sQuery(id+"F0.wireOp",EDGE,"E7.7.3"),sQuery(id+"F0.wireOp",EDGE,"E7.7.4"),sQuery(id+"F0.wireOp",EDGE,"E7.7.5"),sQuery(id+"F0.wireOp",EDGE,"E7.8.0"),sQuery(id+"F0.wireOp",EDGE,"E7.8.1"),sQuery(id+"F0.wireOp",EDGE,"E7.8.2"),sQuery(id+"F0.wireOp",EDGE,"E7.8.3"),sQuery(id+"F0.wireOp",EDGE,"E7.8.4"),sQuery(id+"F0.wireOp",EDGE,"E7.8.5"),sQuery(id+"F0.wireOp",EDGE,"E7.9.0"),sQuery(id+"F0.wireOp",EDGE,"E7.9.1"),sQuery(id+"F0.wireOp",EDGE,"E7.9.2"),sQuery(id+"F0.wireOp",EDGE,"E7.9.3"),sQuery(id+"F0.wireOp",EDGE,"E7.9.4"),sQuery(id+"F0.wireOp",EDGE,"E7.9.5"),sQuery(id+"F0.wireOp",EDGE,"E7.10.0"),sQuery(id+"F0.wireOp",EDGE,"E7.10.1"),sQuery(id+"F0.wireOp",EDGE,"E7.10.2"),sQuery(id+"F0.wireOp",EDGE,"E7.10.3"),sQuery(id+"F0.wireOp",EDGE,"E7.10.4"),sQuery(id+"F0.wireOp",EDGE,"E7.10.5"),sQuery(id+"F0.wireOp",EDGE,"E7.11.0"),sQuery(id+"F0.wireOp",EDGE,"E7.11.1"),sQuery(id+"F0.wireOp",EDGE,"E7.11.2"),sQuery(id+"F0.wireOp",EDGE,"E7.11.3"),sQuery(id+"F0.wireOp",EDGE,"E7.11.4"),sQuery(id+"F0.wireOp",EDGE,"E7.11.5"),sQuery(id+"F0.wireOp",EDGE,"E7.12.0"),sQuery(id+"F0.wireOp",EDGE,"E7.12.1"),sQuery(id+"F0.wireOp",EDGE,"E7.12.2"),sQuery(id+"F0.wireOp",EDGE,"E7.12.3"),sQuery(id+"F0.wireOp",EDGE,"E7.12.4"),sQuery(id+"F0.wireOp",EDGE,"E7.12.5"),sQuery(id+"F0.wireOp",EDGE,"E7.13.0"),sQuery(id+"F0.wireOp",EDGE,"E7.13.1"),sQuery(id+"F0.wireOp",EDGE,"E7.13.2"),sQuery(id+"F0.wireOp",EDGE,"E7.13.3"),sQuery(id+"F0.wireOp",EDGE,"E7.13.4"),sQuery(id+"F0.wireOp",EDGE,"E7.13.5"),sQuery(id+"F0.wireOp",EDGE,"E7.14.0"),sQuery(id+"F0.wireOp",EDGE,"E7.14.1"),sQuery(id+"F0.wireOp",EDGE,"E7.14.2"),sQuery(id+"F0.wireOp",EDGE,"E7.14.3"),sQuery(id+"F0.wireOp",EDGE,"E7.14.4"),sQuery(id+"F0.wireOp",EDGE,"E7.14.5"),sQuery(id+"F0.wireOp",EDGE,"E7.15.0"),sQuery(id+"F0.wireOp",EDGE,"E7.15.1"),sQuery(id+"F0.wireOp",EDGE,"E7.15.2"),sQuery(id+"F0.wireOp",EDGE,"E7.15.3"),sQuery(id+"F0.wireOp",EDGE,"E7.15.4"),sQuery(id+"F0.wireOp",EDGE,"E7.15.5"),sQuery(id+"F0.wireOp",EDGE,"E7.16.0"),sQuery(id+"F0.wireOp",EDGE,"E7.16.1"),sQuery(id+"F0.wireOp",EDGE,"E7.16.2"),sQuery(id+"F0.wireOp",EDGE,"E7.16.3"),sQuery(id+"F0.wireOp",EDGE,"E7.16.4"),sQuery(id+"F0.wireOp",EDGE,"E7.16.5"),sQuery(id+"F0.wireOp",EDGE,"E7.17.0"),sQuery(id+"F0.wireOp",EDGE,"E7.17.1"),sQuery(id+"F0.wireOp",EDGE,"E7.17.2"),sQuery(id+"F0.wireOp",EDGE,"E7.17.3"),sQuery(id+"F0.wireOp",EDGE,"E7.17.4"),sQuery(id+"F0.wireOp",EDGE,"E7.17.5"),sQuery(id+"F0.wireOp",EDGE,"E7.18.0"),sQuery(id+"F0.wireOp",EDGE,"E7.18.1"),sQuery(id+"F0.wireOp",EDGE,"E7.18.2"),sQuery(id+"F0.wireOp",EDGE,"E7.18.3"),sQuery(id+"F0.wireOp",EDGE,"E7.18.4"),sQuery(id+"F0.wireOp",EDGE,"E7.18.5"),sQuery(id+"F0.wireOp",EDGE,"E7.19.0"),sQuery(id+"F0.wireOp",EDGE,"E7.19.1"),sQuery(id+"F0.wireOp",EDGE,"E7.19.2"),sQuery(id+"F0.wireOp",EDGE,"E7.19.3"),sQuery(id+"F0.wireOp",EDGE,"E7.19.4"),sQuery(id+"F0.wireOp",EDGE,"E7.19.5"),sQuery(id+"F0.wireOp",EDGE,"E7.20.0"),sQuery(id+"F0.wireOp",EDGE,"E7.20.1"),sQuery(id+"F0.wireOp",EDGE,"E7.20.2"),sQuery(id+"F0.wireOp",EDGE,"E7.20.3"),sQuery(id+"F0.wireOp",EDGE,"E7.20.4"),sQuery(id+"F0.wireOp",EDGE,"E7.20.5"),sQuery(id+"F0.wireOp",EDGE,"E7.21.0"),sQuery(id+"F0.wireOp",EDGE,"E7.21.1"),sQuery(id+"F0.wireOp",EDGE,"E7.21.2"),sQuery(id+"F0.wireOp",EDGE,"E7.21.3"),sQuery(id+"F0.wireOp",EDGE,"E7.21.4"),sQuery(id+"F0.wireOp",EDGE,"E7.21.5"),sQuery(id+"F0.wireOp",EDGE,"E7.22.0"),sQuery(id+"F0.wireOp",EDGE,"E7.22.1"),sQuery(id+"F0.wireOp",EDGE,"E7.22.2"),sQuery(id+"F0.wireOp",EDGE,"E7.22.3"),sQuery(id+"F0.wireOp",EDGE,"E7.22.4"),sQuery(id+"F0.wireOp",EDGE,"E7.22.5"),sQuery(id+"F0.wireOp",EDGE,"E7.23.0"),sQuery(id+"F0.wireOp",EDGE,"E7.23.1"),sQuery(id+"F0.wireOp",EDGE,"E7.23.2"),sQuery(id+"F0.wireOp",EDGE,"E7.23.3"),sQuery(id+"F0.wireOp",EDGE,"E7.23.4"),sQuery(id+"F0.wireOp",EDGE,"E7.23.5"),sQuery(id+"F0.wireOp",EDGE,"E7.24.0"),sQuery(id+"F0.wireOp",EDGE,"E7.24.1"),sQuery(id+"F0.wireOp",EDGE,"E7.24.2"),sQuery(id+"F0.wireOp",EDGE,"E7.24.3"),sQuery(id+"F0.wireOp",EDGE,"E7.24.4"),sQuery(id+"F0.wireOp",EDGE,"E7.24.5"),sQuery(id+"F0.wireOp",EDGE,"E7.25.0"),sQuery(id+"F0.wireOp",EDGE,"E7.25.1"),sQuery(id+"F0.wireOp",EDGE,"E7.25.2"),sQuery(id+"F0.wireOp",EDGE,"E7.25.3"),sQuery(id+"F0.wireOp",EDGE,"E7.25.4"),sQuery(id+"F0.wireOp",EDGE,"E7.25.5"),sQuery(id+"F0.wireOp",EDGE,"E7.26.0"),sQuery(id+"F0.wireOp",EDGE,"E7.26.1"),sQuery(id+"F0.wireOp",EDGE,"E7.26.2"),sQuery(id+"F0.wireOp",EDGE,"E7.26.3"),sQuery(id+"F0.wireOp",EDGE,"E7.26.4"),sQuery(id+"F0.wireOp",EDGE,"E7.26.5"),sQuery(id+"F0.wireOp",EDGE,"E7.27.0"),sQuery(id+"F0.wireOp",EDGE,"E7.27.1"),sQuery(id+"F0.wireOp",EDGE,"E7.27.2"),sQuery(id+"F0.wireOp",EDGE,"E7.27.3"),sQuery(id+"F0.wireOp",EDGE,"E7.27.4"),sQuery(id+"F0.wireOp",EDGE,"E7.27.5"),sQuery(id+"F0.wireOp",EDGE,"E7.28.0"),sQuery(id+"F0.wireOp",EDGE,"E7.28.1"),sQuery(id+"F0.wireOp",EDGE,"E7.28.2"),sQuery(id+"F0.wireOp",EDGE,"E7.28.3"),sQuery(id+"F0.wireOp",EDGE,"E7.28.4"),sQuery(id+"F0.wireOp",EDGE,"E7.28.5"),sQuery(id+"F0.wireOp",EDGE,"E7.29.0"),sQuery(id+"F0.wireOp",EDGE,"E7.29.1"),sQuery(id+"F0.wireOp",EDGE,"E7.29.2"),sQuery(id+"F0.wireOp",EDGE,"E7.29.3"),sQuery(id+"F0.wireOp",EDGE,"E7.29.4"),sQuery(id+"F0.wireOp",EDGE,"E7.29.5"),sQuery(id+"F0.wireOp",EDGE,"E7.30.0"),sQuery(id+"F0.wireOp",EDGE,"E7.30.1"),sQuery(id+"F0.wireOp",EDGE,"E7.30.2"),sQuery(id+"F0.wireOp",EDGE,"E7.30.3"),sQuery(id+"F0.wireOp",EDGE,"E7.30.4"),sQuery(id+"F0.wireOp",EDGE,"E7.30.5"),sQuery(id+"F0.wireOp",EDGE,"E7.31.0"),sQuery(id+"F0.wireOp",EDGE,"E7.31.1"),sQuery(id+"F0.wireOp",EDGE,"E7.31.2"),sQuery(id+"F0.wireOp",EDGE,"E7.31.3"),sQuery(id+"F0.wireOp",EDGE,"E7.31.4"),sQuery(id+"F0.wireOp",EDGE,"E7.31.5"),sQuery(id+"F0.wireOp",EDGE,"E7.32.0"),sQuery(id+"F0.wireOp",EDGE,"E7.32.1"),sQuery(id+"F0.wireOp",EDGE,"E7.32.2"),sQuery(id+"F0.wireOp",EDGE,"E7.32.3"),sQuery(id+"F0.wireOp",EDGE,"E7.32.4"),sQuery(id+"F0.wireOp",EDGE,"E7.32.5"),sQuery(id+"F0.wireOp",EDGE,"E7.33.0"),sQuery(id+"F0.wireOp",EDGE,"E7.33.1"),sQuery(id+"F0.wireOp",EDGE,"E7.33.2"),sQuery(id+"F0.wireOp",EDGE,"E7.33.3"),sQuery(id+"F0.wireOp",EDGE,"E7.33.4"),sQuery(id+"F0.wireOp",EDGE,"E7.33.5"),sQuery(id+"F0.wireOp",EDGE,"E7.34.0"),sQuery(id+"F0.wireOp",EDGE,"E7.34.1"),sQuery(id+"F0.wireOp",EDGE,"E7.34.2"),sQuery(id+"F0.wireOp",EDGE,"E7.34.3"),sQuery(id+"F0.wireOp",EDGE,"E7.34.4"),sQuery(id+"F0.wireOp",EDGE,"E7.34.5"),subQ0,sQuery(id+"F0.wireOp",EDGE,"E7.35.1"),sQuery(id+"F0.wireOp",EDGE,"E7.35.2"),sQuery(id+"F0.wireOp",EDGE,"E7.35.3"),sQuery(id+"F0.wireOp",EDGE,"E7.35.4"),sQuery(id+"F0.wireOp",EDGE,"E7.35.5"),sQuery(id+"F0.wireOp",EDGE,"E7.36.0"),sQuery(id+"F0.wireOp",EDGE,"E7.36.1"),sQuery(id+"F0.wireOp",EDGE,"E7.36.2"),sQuery(id+"F0.wireOp",EDGE,"E7.36.3"),sQuery(id+"F0.wireOp",EDGE,"E7.36.4"),sQuery(id+"F0.wireOp",EDGE,"E7.36.5"),sQuery(id+"F0.wireOp",EDGE,"E7.37.0"),sQuery(id+"F0.wireOp",EDGE,"E7.37.1"),sQuery(id+"F0.wireOp",EDGE,"E7.37.2"),sQuery(id+"F0.wireOp",EDGE,"E7.37.3"),sQuery(id+"F0.wireOp",EDGE,"E7.37.4"),sQuery(id+"F0.wireOp",EDGE,"E7.37.5"),sQuery(id+"F0.wireOp",EDGE,"E7.38.0"),sQuery(id+"F0.wireOp",EDGE,"E7.38.1"),sQuery(id+"F0.wireOp",EDGE,"E7.38.2"),sQuery(id+"F0.wireOp",EDGE,"E7.38.3"),sQuery(id+"F0.wireOp",EDGE,"E7.38.4"),sQuery(id+"F0.wireOp",EDGE,"E7.38.5"),sQuery(id+"F0.wireOp",EDGE,"E7.39.0"),sQuery(id+"F0.wireOp",EDGE,"E7.39.1"),sQuery(id+"F0.wireOp",EDGE,"E7.39.2"),sQuery(id+"F0.wireOp",EDGE,"E7.39.3"),sQuery(id+"F0.wireOp",EDGE,"E7.39.4"),sQuery(id+"F0.wireOp",EDGE,"E7.39.5"),sQuery(id+"F0.wireOp",EDGE,"E7.40.0"),sQuery(id+"F0.wireOp",EDGE,"E7.40.1"),sQuery(id+"F0.wireOp",EDGE,"E7.40.2"),sQuery(id+"F0.wireOp",EDGE,"E7.40.3"),sQuery(id+"F0.wireOp",EDGE,"E7.40.4"),sQuery(id+"F0.wireOp",EDGE,"E7.40.5"),sQuery(id+"F0.wireOp",EDGE,"E7.41.0"),sQuery(id+"F0.wireOp",EDGE,"E7.41.1"),sQuery(id+"F0.wireOp",EDGE,"E7.41.2"),sQuery(id+"F0.wireOp",EDGE,"E7.41.3"),sQuery(id+"F0.wireOp",EDGE,"E7.41.4"),sQuery(id+"F0.wireOp",EDGE,"E7.41.5"),sQuery(id+"F0.wireOp",EDGE,"E7.42.0"),sQuery(id+"F0.wireOp",EDGE,"E7.42.1"),sQuery(id+"F0.wireOp",EDGE,"E7.42.2"),sQuery(id+"F0.wireOp",EDGE,"E7.42.3"),sQuery(id+"F0.wireOp",EDGE,"E7.42.4"),sQuery(id+"F0.wireOp",EDGE,"E7.42.5"),sQuery(id+"F0.wireOp",EDGE,"E7.43.0"),sQuery(id+"F0.wireOp",EDGE,"E7.43.1"),sQuery(id+"F0.wireOp",EDGE,"E7.43.2"),sQuery(id+"F0.wireOp",EDGE,"E7.43.3"),sQuery(id+"F0.wireOp",EDGE,"E7.43.4"),sQuery(id+"F0.wireOp",EDGE,"E7.43.5")])],"isStart":false})],"blendedInto":[makeQuery(id+"F1.opExtrude","CAP_FACE",FACE,{"disambiguationData":[OSD([sQuery(id+"F0.wireOp",EDGE,"E1"),sQuery(id+"F0.wireOp",EDGE,"E2"),sQuery(id+"F0.wireOp",EDGE,"E3"),sQuery(id+"F0.wireOp",EDGE,"E4"),sQuery(id+"F0.wireOp",EDGE,"E5"),sQuery(id+"F0.wireOp",EDGE,"E6"),sQuery(id+"F0.wireOp",EDGE,"E7.1.0"),sQuery(id+"F0.wireOp",EDGE,"E7.1.1"),sQuery(id+"F0.wireOp",EDGE,"E7.1.2"),sQuery(id+"F0.wireOp",EDGE,"E7.1.3"),sQuery(id+"F0.wireOp",EDGE,"E7.1.4"),sQuery(id+"F0.wireOp",EDGE,"E7.1.5"),sQuery(id+"F0.wireOp",EDGE,"E7.2.0"),sQuery(id+"F0.wireOp",EDGE,"E7.2.1"),sQuery(id+"F0.wireOp",EDGE,"E7.2.2"),sQuery(id+"F0.wireOp",EDGE,"E7.2.3"),sQuery(id+"F0.wireOp",EDGE,"E7.2.4"),sQuery(id+"F0.wireOp",EDGE,"E7.2.5"),sQuery(id+"F0.wireOp",EDGE,"E7.3.0"),sQuery(id+"F0.wireOp",EDGE,"E7.3.1"),sQuery(id+"F0.wireOp",EDGE,"E7.3.2"),sQuery(id+"F0.wireOp",EDGE,"E7.3.3"),sQuery(id+"F0.wireOp",EDGE,"E7.3.4"),sQuery(id+"F0.wireOp",EDGE,"E7.3.5"),sQuery(id+"F0.wireOp",EDGE,"E7.4.0"),sQuery(id+"F0.wireOp",EDGE,"E7.4.1"),sQuery(id+"F0.wireOp",EDGE,"E7.4.2"),sQuery(id+"F0.wireOp",EDGE,"E7.4.3"),sQuery(id+"F0.wireOp",EDGE,"E7.4.4"),sQuery(id+"F0.wireOp",EDGE,"E7.4.5"),sQuery(id+"F0.wireOp",EDGE,"E7.5.0"),sQuery(id+"F0.wireOp",EDGE,"E7.5.1"),sQuery(id+"F0.wireOp",EDGE,"E7.5.2"),sQuery(id+"F0.wireOp",EDGE,"E7.5.3"),sQuery(id+"F0.wireOp",EDGE,"E7.5.4"),sQuery(id+"F0.wireOp",EDGE,"E7.5.5"),sQuery(id+"F0.wireOp",EDGE,"E7.6.0"),sQuery(id+"F0.wireOp",EDGE,"E7.6.1"),sQuery(id+"F0.wireOp",EDGE,"E7.6.2"),sQuery(id+"F0.wireOp",EDGE,"E7.6.3"),sQuery(id+"F0.wireOp",EDGE,"E7.6.4"),sQuery(id+"F0.wireOp",EDGE,"E7.6.5"),sQuery(id+"F0.wireOp",EDGE,"E7.7.0"),sQuery(id+"F0.wireOp",EDGE,"E7.7.1"),sQuery(id+"F0.wireOp",EDGE,"E7.7.2"),sQuery(id+"F0.wireOp",EDGE,"E7.7.3"),sQuery(id+"F0.wireOp",EDGE,"E7.7.4"),sQuery(id+"F0.wireOp",EDGE,"E7.7.5"),sQuery(id+"F0.wireOp",EDGE,"E7.8.0"),sQuery(id+"F0.wireOp",EDGE,"E7.8.1"),sQuery(id+"F0.wireOp",EDGE,"E7.8.2"),sQuery(id+"F0.wireOp",EDGE,"E7.8.3"),sQuery(id+"F0.wireOp",EDGE,"E7.8.4"),sQuery(id+"F0.wireOp",EDGE,"E7.8.5"),sQuery(id+"F0.wireOp",EDGE,"E7.9.0"),sQuery(id+"F0.wireOp",EDGE,"E7.9.1"),sQuery(id+"F0.wireOp",EDGE,"E7.9.2"),sQuery(id+"F0.wireOp",EDGE,"E7.9.3"),sQuery(id+"F0.wireOp",EDGE,"E7.9.4"),sQuery(id+"F0.wireOp",EDGE,"E7.9.5"),sQuery(id+"F0.wireOp",EDGE,"E7.10.0"),sQuery(id+"F0.wireOp",EDGE,"E7.10.1"),sQuery(id+"F0.wireOp",EDGE,"E7.10.2"),sQuery(id+"F0.wireOp",EDGE,"E7.10.3"),sQuery(id+"F0.wireOp",EDGE,"E7.10.4"),sQuery(id+"F0.wireOp",EDGE,"E7.10.5"),sQuery(id+"F0.wireOp",EDGE,"E7.11.0"),sQuery(id+"F0.wireOp",EDGE,"E7.11.1"),sQuery(id+"F0.wireOp",EDGE,"E7.11.2"),sQuery(id+"F0.wireOp",EDGE,"E7.11.3"),sQuery(id+"F0.wireOp",EDGE,"E7.11.4"),sQuery(id+"F0.wireOp",EDGE,"E7.11.5"),sQuery(id+"F0.wireOp",EDGE,"E7.12.0"),sQuery(id+"F0.wireOp",EDGE,"E7.12.1"),sQuery(id+"F0.wireOp",EDGE,"E7.12.2"),sQuery(id+"F0.wireOp",EDGE,"E7.12.3"),sQuery(id+"F0.wireOp",EDGE,"E7.12.4"),sQuery(id+"F0.wireOp",EDGE,"E7.12.5"),sQuery(id+"F0.wireOp",EDGE,"E7.13.0"),sQuery(id+"F0.wireOp",EDGE,"E7.13.1"),sQuery(id+"F0.wireOp",EDGE,"E7.13.2"),sQuery(id+"F0.wireOp",EDGE,"E7.13.3"),sQuery(id+"F0.wireOp",EDGE,"E7.13.4"),sQuery(id+"F0.wireOp",EDGE,"E7.13.5"),sQuery(id+"F0.wireOp",EDGE,"E7.14.0"),sQuery(id+"F0.wireOp",EDGE,"E7.14.1"),sQuery(id+"F0.wireOp",EDGE,"E7.14.2"),sQuery(id+"F0.wireOp",EDGE,"E7.14.3"),sQuery(id+"F0.wireOp",EDGE,"E7.14.4"),sQuery(id+"F0.wireOp",EDGE,"E7.14.5"),sQuery(id+"F0.wireOp",EDGE,"E7.15.0"),sQuery(id+"F0.wireOp",EDGE,"E7.15.1"),sQuery(id+"F0.wireOp",EDGE,"E7.15.2"),sQuery(id+"F0.wireOp",EDGE,"E7.15.3"),sQuery(id+"F0.wireOp",EDGE,"E7.15.4"),sQuery(id+"F0.wireOp",EDGE,"E7.15.5"),sQuery(id+"F0.wireOp",EDGE,"E7.16.0"),sQuery(id+"F0.wireOp",EDGE,"E7.16.1"),sQuery(id+"F0.wireOp",EDGE,"E7.16.2"),sQuery(id+"F0.wireOp",EDGE,"E7.16.3"),sQuery(id+"F0.wireOp",EDGE,"E7.16.4"),sQuery(id+"F0.wireOp",EDGE,"E7.16.5"),sQuery(id+"F0.wireOp",EDGE,"E7.17.0"),sQuery(id+"F0.wireOp",EDGE,"E7.17.1"),sQuery(id+"F0.wireOp",EDGE,"E7.17.2"),sQuery(id+"F0.wireOp",EDGE,"E7.17.3"),sQuery(id+"F0.wireOp",EDGE,"E7.17.4"),sQuery(id+"F0.wireOp",EDGE,"E7.17.5"),sQuery(id+"F0.wireOp",EDGE,"E7.18.0"),sQuery(id+"F0.wireOp",EDGE,"E7.18.1"),sQuery(id+"F0.wireOp",EDGE,"E7.18.2"),sQuery(id+"F0.wireOp",EDGE,"E7.18.3"),sQuery(id+"F0.wireOp",EDGE,"E7.18.4"),sQuery(id+"F0.wireOp",EDGE,"E7.18.5"),sQuery(id+"F0.wireOp",EDGE,"E7.19.0"),sQuery(id+"F0.wireOp",EDGE,"E7.19.1"),sQuery(id+"F0.wireOp",EDGE,"E7.19.2"),sQuery(id+"F0.wireOp",EDGE,"E7.19.3"),sQuery(id+"F0.wireOp",EDGE,"E7.19.4"),sQuery(id+"F0.wireOp",EDGE,"E7.19.5"),sQuery(id+"F0.wireOp",EDGE,"E7.20.0"),sQuery(id+"F0.wireOp",EDGE,"E7.20.1"),sQuery(id+"F0.wireOp",EDGE,"E7.20.2"),sQuery(id+"F0.wireOp",EDGE,"E7.20.3"),sQuery(id+"F0.wireOp",EDGE,"E7.20.4"),sQuery(id+"F0.wireOp",EDGE,"E7.20.5"),sQuery(id+"F0.wireOp",EDGE,"E7.21.0"),sQuery(id+"F0.wireOp",EDGE,"E7.21.1"),sQuery(id+"F0.wireOp",EDGE,"E7.21.2"),sQuery(id+"F0.wireOp",EDGE,"E7.21.3"),sQuery(id+"F0.wireOp",EDGE,"E7.21.4"),sQuery(id+"F0.wireOp",EDGE,"E7.21.5"),sQuery(id+"F0.wireOp",EDGE,"E7.22.0"),sQuery(id+"F0.wireOp",EDGE,"E7.22.1"),sQuery(id+"F0.wireOp",EDGE,"E7.22.2"),sQuery(id+"F0.wireOp",EDGE,"E7.22.3"),sQuery(id+"F0.wireOp",EDGE,"E7.22.4"),sQuery(id+"F0.wireOp",EDGE,"E7.22.5"),sQuery(id+"F0.wireOp",EDGE,"E7.23.0"),sQuery(id+"F0.wireOp",EDGE,"E7.23.1"),sQuery(id+"F0.wireOp",EDGE,"E7.23.2"),sQuery(id+"F0.wireOp",EDGE,"E7.23.3"),sQuery(id+"F0.wireOp",EDGE,"E7.23.4"),sQuery(id+"F0.wireOp",EDGE,"E7.23.5"),sQuery(id+"F0.wireOp",EDGE,"E7.24.0"),sQuery(id+"F0.wireOp",EDGE,"E7.24.1"),sQuery(id+"F0.wireOp",EDGE,"E7.24.2"),sQuery(id+"F0.wireOp",EDGE,"E7.24.3"),sQuery(id+"F0.wireOp",EDGE,"E7.24.4"),sQuery(id+"F0.wireOp",EDGE,"E7.24.5"),sQuery(id+"F0.wireOp",EDGE,"E7.25.0"),sQuery(id+"F0.wireOp",EDGE,"E7.25.1"),sQuery(id+"F0.wireOp",EDGE,"E7.25.2"),sQuery(id+"F0.wireOp",EDGE,"E7.25.3"),sQuery(id+"F0.wireOp",EDGE,"E7.25.4"),sQuery(id+"F0.wireOp",EDGE,"E7.25.5"),sQuery(id+"F0.wireOp",EDGE,"E7.26.0"),sQuery(id+"F0.wireOp",EDGE,"E7.26.1"),sQuery(id+"F0.wireOp",EDGE,"E7.26.2"),sQuery(id+"F0.wireOp",EDGE,"E7.26.3"),sQuery(id+"F0.wireOp",EDGE,"E7.26.4"),sQuery(id+"F0.wireOp",EDGE,"E7.26.5"),sQuery(id+"F0.wireOp",EDGE,"E7.27.0"),sQuery(id+"F0.wireOp",EDGE,"E7.27.1"),sQuery(id+"F0.wireOp",EDGE,"E7.27.2"),sQuery(id+"F0.wireOp",EDGE,"E7.27.3"),sQuery(id+"F0.wireOp",EDGE,"E7.27.4"),sQuery(id+"F0.wireOp",EDGE,"E7.27.5"),sQuery(id+"F0.wireOp",EDGE,"E7.28.0"),sQuery(id+"F0.wireOp",EDGE,"E7.28.1"),sQuery(id+"F0.wireOp",EDGE,"E7.28.2"),sQuery(id+"F0.wireOp",EDGE,"E7.28.3"),sQuery(id+"F0.wireOp",EDGE,"E7.28.4"),sQuery(id+"F0.wireOp",EDGE,"E7.28.5"),sQuery(id+"F0.wireOp",EDGE,"E7.29.0"),sQuery(id+"F0.wireOp",EDGE,"E7.29.1"),sQuery(id+"F0.wireOp",EDGE,"E7.29.2"),sQuery(id+"F0.wireOp",EDGE,"E7.29.3"),sQuery(id+"F0.wireOp",EDGE,"E7.29.4"),sQuery(id+"F0.wireOp",EDGE,"E7.29.5"),sQuery(id+"F0.wireOp",EDGE,"E7.30.0"),sQuery(id+"F0.wireOp",EDGE,"E7.30.1"),sQuery(id+"F0.wireOp",EDGE,"E7.30.2"),sQuery(id+"F0.wireOp",EDGE,"E7.30.3"),sQuery(id+"F0.wireOp",EDGE,"E7.30.4"),sQuery(id+"F0.wireOp",EDGE,"E7.30.5"),sQuery(id+"F0.wireOp",EDGE,"E7.31.0"),sQuery(id+"F0.wireOp",EDGE,"E7.31.1"),sQuery(id+"F0.wireOp",EDGE,"E7.31.2"),sQuery(id+"F0.wireOp",EDGE,"E7.31.3"),sQuery(id+"F0.wireOp",EDGE,"E7.31.4"),sQuery(id+"F0.wireOp",EDGE,"E7.31.5"),sQuery(id+"F0.wireOp",EDGE,"E7.32.0"),sQuery(id+"F0.wireOp",EDGE,"E7.32.1"),sQuery(id+"F0.wireOp",EDGE,"E7.32.2"),sQuery(id+"F0.wireOp",EDGE,"E7.32.3"),sQuery(id+"F0.wireOp",EDGE,"E7.32.4"),sQuery(id+"F0.wireOp",EDGE,"E7.32.5"),sQuery(id+"F0.wireOp",EDGE,"E7.33.0"),sQuery(id+"F0.wireOp",EDGE,"E7.33.1"),sQuery(id+"F0.wireOp",EDGE,"E7.33.2"),sQuery(id+"F0.wireOp",EDGE,"E7.33.3"),sQuery(id+"F0.wireOp",EDGE,"E7.33.4"),sQuery(id+"F0.wireOp",EDGE,"E7.33.5"),sQuery(id+"F0.wireOp",EDGE,"E7.34.0"),sQuery(id+"F0.wireOp",EDGE,"E7.34.1"),sQuery(id+"F0.wireOp",EDGE,"E7.34.2"),sQuery(id+"F0.wireOp",EDGE,"E7.34.3"),sQuery(id+"F0.wireOp",EDGE,"E7.34.4"),sQuery(id+"F0.wireOp",EDGE,"E7.34.5"),subQ0,sQuery(id+"F0.wireOp",EDGE,"E7.35.1"),sQuery(id+"F0.wireOp",EDGE,"E7.35.2"),sQuery(id+"F0.wireOp",EDGE,"E7.35.3"),sQuery(id+"F0.wireOp",EDGE,"E7.35.4"),sQuery(id+"F0.wireOp",EDGE,"E7.35.5"),sQuery(id+"F0.wireOp",EDGE,"E7.36.0"),sQuery(id+"F0.wireOp",EDGE,"E7.36.1"),sQuery(id+"F0.wireOp",EDGE,"E7.36.2"),sQuery(id+"F0.wireOp",EDGE,"E7.36.3"),sQuery(id+"F0.wireOp",EDGE,"E7.36.4"),sQuery(id+"F0.wireOp",EDGE,"E7.36.5"),sQuery(id+"F0.wireOp",EDGE,"E7.37.0"),sQuery(id+"F0.wireOp",EDGE,"E7.37.1"),sQuery(id+"F0.wireOp",EDGE,"E7.37.2"),sQuery(id+"F0.wireOp",EDGE,"E7.37.3"),sQuery(id+"F0.wireOp",EDGE,"E7.37.4"),sQuery(id+"F0.wireOp",EDGE,"E7.37.5"),sQuery(id+"F0.wireOp",EDGE,"E7.38.0"),sQuery(id+"F0.wireOp",EDGE,"E7.38.1"),sQuery(id+"F0.wireOp",EDGE,"E7.38.2"),sQuery(id+"F0.wireOp",EDGE,"E7.38.3"),sQuery(id+"F0.wireOp",EDGE,"E7.38.4"),sQuery(id+"F0.wireOp",EDGE,"E7.38.5"),sQuery(id+"F0.wireOp",EDGE,"E7.39.0"),sQuery(id+"F0.wireOp",EDGE,"E7.39.1"),sQuery(id+"F0.wireOp",EDGE,"E7.39.2"),sQuery(id+"F0.wireOp",EDGE,"E7.39.3"),sQuery(id+"F0.wireOp",EDGE,"E7.39.4"),sQuery(id+"F0.wireOp",EDGE,"E7.39.5"),sQuery(id+"F0.wireOp",EDGE,"E7.40.0"),sQuery(id+"F0.wireOp",EDGE,"E7.40.1"),sQuery(id+"F0.wireOp",EDGE,"E7.40.2"),sQuery(id+"F0.wireOp",EDGE,"E7.40.3"),sQuery(id+"F0.wireOp",EDGE,"E7.40.4"),sQuery(id+"F0.wireOp",EDGE,"E7.40.5"),sQuery(id+"F0.wireOp",EDGE,"E7.41.0"),sQuery(id+"F0.wireOp",EDGE,"E7.41.1"),sQuery(id+"F0.wireOp",EDGE,"E7.41.2"),sQuery(id+"F0.wireOp",EDGE,"E7.41.3"),sQuery(id+"F0.wireOp",EDGE,"E7.41.4"),sQuery(id+"F0.wireOp",EDGE,"E7.41.5"),sQuery(id+"F0.wireOp",EDGE,"E7.42.0"),sQuery(id+"F0.wireOp",EDGE,"E7.42.1"),sQuery(id+"F0.wireOp",EDGE,"E7.42.2"),sQuery(id+"F0.wireOp",EDGE,"E7.42.3"),sQuery(id+"F0.wireOp",EDGE,"E7.42.4"),sQuery(id+"F0.wireOp",EDGE,"E7.42.5"),sQuery(id+"F0.wireOp",EDGE,"E7.43.0"),sQuery(id+"F0.wireOp",EDGE,"E7.43.1"),sQuery(id+"F0.wireOp",EDGE,"E7.43.2"),sQuery(id+"F0.wireOp",EDGE,"E7.43.3"),sQuery(id+"F0.wireOp",EDGE,"E7.43.4"),sQuery(id+"F0.wireOp",EDGE,"E7.43.5")])],"isStart":false})]});}
            var Q5;
            {var subQ0=sQuery(id+"F0.wireOp",EDGE,"E7.33.0");Q5=makeQuery(id+"F2.opChamfer","BLEND_EDGE",EDGE,{"blendedFrom":[makeQuery(id+"F1.opExtrude","CAP_EDGE",EDGE,{"disambiguationData":[OSD([subQ0])],"isStart":false}),makeQuery(id+"F1.opExtrude","CAP_FACE",FACE,{"disambiguationData":[OSD([sQuery(id+"F0.wireOp",EDGE,"E1"),sQuery(id+"F0.wireOp",EDGE,"E2"),sQuery(id+"F0.wireOp",EDGE,"E3"),sQuery(id+"F0.wireOp",EDGE,"E4"),sQuery(id+"F0.wireOp",EDGE,"E5"),sQuery(id+"F0.wireOp",EDGE,"E6"),sQuery(id+"F0.wireOp",EDGE,"E7.1.0"),sQuery(id+"F0.wireOp",EDGE,"E7.1.1"),sQuery(id+"F0.wireOp",EDGE,"E7.1.2"),sQuery(id+"F0.wireOp",EDGE,"E7.1.3"),sQuery(id+"F0.wireOp",EDGE,"E7.1.4"),sQuery(id+"F0.wireOp",EDGE,"E7.1.5"),sQuery(id+"F0.wireOp",EDGE,"E7.2.0"),sQuery(id+"F0.wireOp",EDGE,"E7.2.1"),sQuery(id+"F0.wireOp",EDGE,"E7.2.2"),sQuery(id+"F0.wireOp",EDGE,"E7.2.3"),sQuery(id+"F0.wireOp",EDGE,"E7.2.4"),sQuery(id+"F0.wireOp",EDGE,"E7.2.5"),sQuery(id+"F0.wireOp",EDGE,"E7.3.0"),sQuery(id+"F0.wireOp",EDGE,"E7.3.1"),sQuery(id+"F0.wireOp",EDGE,"E7.3.2"),sQuery(id+"F0.wireOp",EDGE,"E7.3.3"),sQuery(id+"F0.wireOp",EDGE,"E7.3.4"),sQuery(id+"F0.wireOp",EDGE,"E7.3.5"),sQuery(id+"F0.wireOp",EDGE,"E7.4.0"),sQuery(id+"F0.wireOp",EDGE,"E7.4.1"),sQuery(id+"F0.wireOp",EDGE,"E7.4.2"),sQuery(id+"F0.wireOp",EDGE,"E7.4.3"),sQuery(id+"F0.wireOp",EDGE,"E7.4.4"),sQuery(id+"F0.wireOp",EDGE,"E7.4.5"),sQuery(id+"F0.wireOp",EDGE,"E7.5.0"),sQuery(id+"F0.wireOp",EDGE,"E7.5.1"),sQuery(id+"F0.wireOp",EDGE,"E7.5.2"),sQuery(id+"F0.wireOp",EDGE,"E7.5.3"),sQuery(id+"F0.wireOp",EDGE,"E7.5.4"),sQuery(id+"F0.wireOp",EDGE,"E7.5.5"),sQuery(id+"F0.wireOp",EDGE,"E7.6.0"),sQuery(id+"F0.wireOp",EDGE,"E7.6.1"),sQuery(id+"F0.wireOp",EDGE,"E7.6.2"),sQuery(id+"F0.wireOp",EDGE,"E7.6.3"),sQuery(id+"F0.wireOp",EDGE,"E7.6.4"),sQuery(id+"F0.wireOp",EDGE,"E7.6.5"),sQuery(id+"F0.wireOp",EDGE,"E7.7.0"),sQuery(id+"F0.wireOp",EDGE,"E7.7.1"),sQuery(id+"F0.wireOp",EDGE,"E7.7.2"),sQuery(id+"F0.wireOp",EDGE,"E7.7.3"),sQuery(id+"F0.wireOp",EDGE,"E7.7.4"),sQuery(id+"F0.wireOp",EDGE,"E7.7.5"),sQuery(id+"F0.wireOp",EDGE,"E7.8.0"),sQuery(id+"F0.wireOp",EDGE,"E7.8.1"),sQuery(id+"F0.wireOp",EDGE,"E7.8.2"),sQuery(id+"F0.wireOp",EDGE,"E7.8.3"),sQuery(id+"F0.wireOp",EDGE,"E7.8.4"),sQuery(id+"F0.wireOp",EDGE,"E7.8.5"),sQuery(id+"F0.wireOp",EDGE,"E7.9.0"),sQuery(id+"F0.wireOp",EDGE,"E7.9.1"),sQuery(id+"F0.wireOp",EDGE,"E7.9.2"),sQuery(id+"F0.wireOp",EDGE,"E7.9.3"),sQuery(id+"F0.wireOp",EDGE,"E7.9.4"),sQuery(id+"F0.wireOp",EDGE,"E7.9.5"),sQuery(id+"F0.wireOp",EDGE,"E7.10.0"),sQuery(id+"F0.wireOp",EDGE,"E7.10.1"),sQuery(id+"F0.wireOp",EDGE,"E7.10.2"),sQuery(id+"F0.wireOp",EDGE,"E7.10.3"),sQuery(id+"F0.wireOp",EDGE,"E7.10.4"),sQuery(id+"F0.wireOp",EDGE,"E7.10.5"),sQuery(id+"F0.wireOp",EDGE,"E7.11.0"),sQuery(id+"F0.wireOp",EDGE,"E7.11.1"),sQuery(id+"F0.wireOp",EDGE,"E7.11.2"),sQuery(id+"F0.wireOp",EDGE,"E7.11.3"),sQuery(id+"F0.wireOp",EDGE,"E7.11.4"),sQuery(id+"F0.wireOp",EDGE,"E7.11.5"),sQuery(id+"F0.wireOp",EDGE,"E7.12.0"),sQuery(id+"F0.wireOp",EDGE,"E7.12.1"),sQuery(id+"F0.wireOp",EDGE,"E7.12.2"),sQuery(id+"F0.wireOp",EDGE,"E7.12.3"),sQuery(id+"F0.wireOp",EDGE,"E7.12.4"),sQuery(id+"F0.wireOp",EDGE,"E7.12.5"),sQuery(id+"F0.wireOp",EDGE,"E7.13.0"),sQuery(id+"F0.wireOp",EDGE,"E7.13.1"),sQuery(id+"F0.wireOp",EDGE,"E7.13.2"),sQuery(id+"F0.wireOp",EDGE,"E7.13.3"),sQuery(id+"F0.wireOp",EDGE,"E7.13.4"),sQuery(id+"F0.wireOp",EDGE,"E7.13.5"),sQuery(id+"F0.wireOp",EDGE,"E7.14.0"),sQuery(id+"F0.wireOp",EDGE,"E7.14.1"),sQuery(id+"F0.wireOp",EDGE,"E7.14.2"),sQuery(id+"F0.wireOp",EDGE,"E7.14.3"),sQuery(id+"F0.wireOp",EDGE,"E7.14.4"),sQuery(id+"F0.wireOp",EDGE,"E7.14.5"),sQuery(id+"F0.wireOp",EDGE,"E7.15.0"),sQuery(id+"F0.wireOp",EDGE,"E7.15.1"),sQuery(id+"F0.wireOp",EDGE,"E7.15.2"),sQuery(id+"F0.wireOp",EDGE,"E7.15.3"),sQuery(id+"F0.wireOp",EDGE,"E7.15.4"),sQuery(id+"F0.wireOp",EDGE,"E7.15.5"),sQuery(id+"F0.wireOp",EDGE,"E7.16.0"),sQuery(id+"F0.wireOp",EDGE,"E7.16.1"),sQuery(id+"F0.wireOp",EDGE,"E7.16.2"),sQuery(id+"F0.wireOp",EDGE,"E7.16.3"),sQuery(id+"F0.wireOp",EDGE,"E7.16.4"),sQuery(id+"F0.wireOp",EDGE,"E7.16.5"),sQuery(id+"F0.wireOp",EDGE,"E7.17.0"),sQuery(id+"F0.wireOp",EDGE,"E7.17.1"),sQuery(id+"F0.wireOp",EDGE,"E7.17.2"),sQuery(id+"F0.wireOp",EDGE,"E7.17.3"),sQuery(id+"F0.wireOp",EDGE,"E7.17.4"),sQuery(id+"F0.wireOp",EDGE,"E7.17.5"),sQuery(id+"F0.wireOp",EDGE,"E7.18.0"),sQuery(id+"F0.wireOp",EDGE,"E7.18.1"),sQuery(id+"F0.wireOp",EDGE,"E7.18.2"),sQuery(id+"F0.wireOp",EDGE,"E7.18.3"),sQuery(id+"F0.wireOp",EDGE,"E7.18.4"),sQuery(id+"F0.wireOp",EDGE,"E7.18.5"),sQuery(id+"F0.wireOp",EDGE,"E7.19.0"),sQuery(id+"F0.wireOp",EDGE,"E7.19.1"),sQuery(id+"F0.wireOp",EDGE,"E7.19.2"),sQuery(id+"F0.wireOp",EDGE,"E7.19.3"),sQuery(id+"F0.wireOp",EDGE,"E7.19.4"),sQuery(id+"F0.wireOp",EDGE,"E7.19.5"),sQuery(id+"F0.wireOp",EDGE,"E7.20.0"),sQuery(id+"F0.wireOp",EDGE,"E7.20.1"),sQuery(id+"F0.wireOp",EDGE,"E7.20.2"),sQuery(id+"F0.wireOp",EDGE,"E7.20.3"),sQuery(id+"F0.wireOp",EDGE,"E7.20.4"),sQuery(id+"F0.wireOp",EDGE,"E7.20.5"),sQuery(id+"F0.wireOp",EDGE,"E7.21.0"),sQuery(id+"F0.wireOp",EDGE,"E7.21.1"),sQuery(id+"F0.wireOp",EDGE,"E7.21.2"),sQuery(id+"F0.wireOp",EDGE,"E7.21.3"),sQuery(id+"F0.wireOp",EDGE,"E7.21.4"),sQuery(id+"F0.wireOp",EDGE,"E7.21.5"),sQuery(id+"F0.wireOp",EDGE,"E7.22.0"),sQuery(id+"F0.wireOp",EDGE,"E7.22.1"),sQuery(id+"F0.wireOp",EDGE,"E7.22.2"),sQuery(id+"F0.wireOp",EDGE,"E7.22.3"),sQuery(id+"F0.wireOp",EDGE,"E7.22.4"),sQuery(id+"F0.wireOp",EDGE,"E7.22.5"),sQuery(id+"F0.wireOp",EDGE,"E7.23.0"),sQuery(id+"F0.wireOp",EDGE,"E7.23.1"),sQuery(id+"F0.wireOp",EDGE,"E7.23.2"),sQuery(id+"F0.wireOp",EDGE,"E7.23.3"),sQuery(id+"F0.wireOp",EDGE,"E7.23.4"),sQuery(id+"F0.wireOp",EDGE,"E7.23.5"),sQuery(id+"F0.wireOp",EDGE,"E7.24.0"),sQuery(id+"F0.wireOp",EDGE,"E7.24.1"),sQuery(id+"F0.wireOp",EDGE,"E7.24.2"),sQuery(id+"F0.wireOp",EDGE,"E7.24.3"),sQuery(id+"F0.wireOp",EDGE,"E7.24.4"),sQuery(id+"F0.wireOp",EDGE,"E7.24.5"),sQuery(id+"F0.wireOp",EDGE,"E7.25.0"),sQuery(id+"F0.wireOp",EDGE,"E7.25.1"),sQuery(id+"F0.wireOp",EDGE,"E7.25.2"),sQuery(id+"F0.wireOp",EDGE,"E7.25.3"),sQuery(id+"F0.wireOp",EDGE,"E7.25.4"),sQuery(id+"F0.wireOp",EDGE,"E7.25.5"),sQuery(id+"F0.wireOp",EDGE,"E7.26.0"),sQuery(id+"F0.wireOp",EDGE,"E7.26.1"),sQuery(id+"F0.wireOp",EDGE,"E7.26.2"),sQuery(id+"F0.wireOp",EDGE,"E7.26.3"),sQuery(id+"F0.wireOp",EDGE,"E7.26.4"),sQuery(id+"F0.wireOp",EDGE,"E7.26.5"),sQuery(id+"F0.wireOp",EDGE,"E7.27.0"),sQuery(id+"F0.wireOp",EDGE,"E7.27.1"),sQuery(id+"F0.wireOp",EDGE,"E7.27.2"),sQuery(id+"F0.wireOp",EDGE,"E7.27.3"),sQuery(id+"F0.wireOp",EDGE,"E7.27.4"),sQuery(id+"F0.wireOp",EDGE,"E7.27.5"),sQuery(id+"F0.wireOp",EDGE,"E7.28.0"),sQuery(id+"F0.wireOp",EDGE,"E7.28.1"),sQuery(id+"F0.wireOp",EDGE,"E7.28.2"),sQuery(id+"F0.wireOp",EDGE,"E7.28.3"),sQuery(id+"F0.wireOp",EDGE,"E7.28.4"),sQuery(id+"F0.wireOp",EDGE,"E7.28.5"),sQuery(id+"F0.wireOp",EDGE,"E7.29.0"),sQuery(id+"F0.wireOp",EDGE,"E7.29.1"),sQuery(id+"F0.wireOp",EDGE,"E7.29.2"),sQuery(id+"F0.wireOp",EDGE,"E7.29.3"),sQuery(id+"F0.wireOp",EDGE,"E7.29.4"),sQuery(id+"F0.wireOp",EDGE,"E7.29.5"),sQuery(id+"F0.wireOp",EDGE,"E7.30.0"),sQuery(id+"F0.wireOp",EDGE,"E7.30.1"),sQuery(id+"F0.wireOp",EDGE,"E7.30.2"),sQuery(id+"F0.wireOp",EDGE,"E7.30.3"),sQuery(id+"F0.wireOp",EDGE,"E7.30.4"),sQuery(id+"F0.wireOp",EDGE,"E7.30.5"),sQuery(id+"F0.wireOp",EDGE,"E7.31.0"),sQuery(id+"F0.wireOp",EDGE,"E7.31.1"),sQuery(id+"F0.wireOp",EDGE,"E7.31.2"),sQuery(id+"F0.wireOp",EDGE,"E7.31.3"),sQuery(id+"F0.wireOp",EDGE,"E7.31.4"),sQuery(id+"F0.wireOp",EDGE,"E7.31.5"),sQuery(id+"F0.wireOp",EDGE,"E7.32.0"),sQuery(id+"F0.wireOp",EDGE,"E7.32.1"),sQuery(id+"F0.wireOp",EDGE,"E7.32.2"),sQuery(id+"F0.wireOp",EDGE,"E7.32.3"),sQuery(id+"F0.wireOp",EDGE,"E7.32.4"),sQuery(id+"F0.wireOp",EDGE,"E7.32.5"),subQ0,sQuery(id+"F0.wireOp",EDGE,"E7.33.1"),sQuery(id+"F0.wireOp",EDGE,"E7.33.2"),sQuery(id+"F0.wireOp",EDGE,"E7.33.3"),sQuery(id+"F0.wireOp",EDGE,"E7.33.4"),sQuery(id+"F0.wireOp",EDGE,"E7.33.5"),sQuery(id+"F0.wireOp",EDGE,"E7.34.0"),sQuery(id+"F0.wireOp",EDGE,"E7.34.1"),sQuery(id+"F0.wireOp",EDGE,"E7.34.2"),sQuery(id+"F0.wireOp",EDGE,"E7.34.3"),sQuery(id+"F0.wireOp",EDGE,"E7.34.4"),sQuery(id+"F0.wireOp",EDGE,"E7.34.5"),sQuery(id+"F0.wireOp",EDGE,"E7.35.0"),sQuery(id+"F0.wireOp",EDGE,"E7.35.1"),sQuery(id+"F0.wireOp",EDGE,"E7.35.2"),sQuery(id+"F0.wireOp",EDGE,"E7.35.3"),sQuery(id+"F0.wireOp",EDGE,"E7.35.4"),sQuery(id+"F0.wireOp",EDGE,"E7.35.5"),sQuery(id+"F0.wireOp",EDGE,"E7.36.0"),sQuery(id+"F0.wireOp",EDGE,"E7.36.1"),sQuery(id+"F0.wireOp",EDGE,"E7.36.2"),sQuery(id+"F0.wireOp",EDGE,"E7.36.3"),sQuery(id+"F0.wireOp",EDGE,"E7.36.4"),sQuery(id+"F0.wireOp",EDGE,"E7.36.5"),sQuery(id+"F0.wireOp",EDGE,"E7.37.0"),sQuery(id+"F0.wireOp",EDGE,"E7.37.1"),sQuery(id+"F0.wireOp",EDGE,"E7.37.2"),sQuery(id+"F0.wireOp",EDGE,"E7.37.3"),sQuery(id+"F0.wireOp",EDGE,"E7.37.4"),sQuery(id+"F0.wireOp",EDGE,"E7.37.5"),sQuery(id+"F0.wireOp",EDGE,"E7.38.0"),sQuery(id+"F0.wireOp",EDGE,"E7.38.1"),sQuery(id+"F0.wireOp",EDGE,"E7.38.2"),sQuery(id+"F0.wireOp",EDGE,"E7.38.3"),sQuery(id+"F0.wireOp",EDGE,"E7.38.4"),sQuery(id+"F0.wireOp",EDGE,"E7.38.5"),sQuery(id+"F0.wireOp",EDGE,"E7.39.0"),sQuery(id+"F0.wireOp",EDGE,"E7.39.1"),sQuery(id+"F0.wireOp",EDGE,"E7.39.2"),sQuery(id+"F0.wireOp",EDGE,"E7.39.3"),sQuery(id+"F0.wireOp",EDGE,"E7.39.4"),sQuery(id+"F0.wireOp",EDGE,"E7.39.5"),sQuery(id+"F0.wireOp",EDGE,"E7.40.0"),sQuery(id+"F0.wireOp",EDGE,"E7.40.1"),sQuery(id+"F0.wireOp",EDGE,"E7.40.2"),sQuery(id+"F0.wireOp",EDGE,"E7.40.3"),sQuery(id+"F0.wireOp",EDGE,"E7.40.4"),sQuery(id+"F0.wireOp",EDGE,"E7.40.5"),sQuery(id+"F0.wireOp",EDGE,"E7.41.0"),sQuery(id+"F0.wireOp",EDGE,"E7.41.1"),sQuery(id+"F0.wireOp",EDGE,"E7.41.2"),sQuery(id+"F0.wireOp",EDGE,"E7.41.3"),sQuery(id+"F0.wireOp",EDGE,"E7.41.4"),sQuery(id+"F0.wireOp",EDGE,"E7.41.5"),sQuery(id+"F0.wireOp",EDGE,"E7.42.0"),sQuery(id+"F0.wireOp",EDGE,"E7.42.1"),sQuery(id+"F0.wireOp",EDGE,"E7.42.2"),sQuery(id+"F0.wireOp",EDGE,"E7.42.3"),sQuery(id+"F0.wireOp",EDGE,"E7.42.4"),sQuery(id+"F0.wireOp",EDGE,"E7.42.5"),sQuery(id+"F0.wireOp",EDGE,"E7.43.0"),sQuery(id+"F0.wireOp",EDGE,"E7.43.1"),sQuery(id+"F0.wireOp",EDGE,"E7.43.2"),sQuery(id+"F0.wireOp",EDGE,"E7.43.3"),sQuery(id+"F0.wireOp",EDGE,"E7.43.4"),sQuery(id+"F0.wireOp",EDGE,"E7.43.5")])],"isStart":false})],"blendedInto":[makeQuery(id+"F1.opExtrude","CAP_FACE",FACE,{"disambiguationData":[OSD([sQuery(id+"F0.wireOp",EDGE,"E1"),sQuery(id+"F0.wireOp",EDGE,"E2"),sQuery(id+"F0.wireOp",EDGE,"E3"),sQuery(id+"F0.wireOp",EDGE,"E4"),sQuery(id+"F0.wireOp",EDGE,"E5"),sQuery(id+"F0.wireOp",EDGE,"E6"),sQuery(id+"F0.wireOp",EDGE,"E7.1.0"),sQuery(id+"F0.wireOp",EDGE,"E7.1.1"),sQuery(id+"F0.wireOp",EDGE,"E7.1.2"),sQuery(id+"F0.wireOp",EDGE,"E7.1.3"),sQuery(id+"F0.wireOp",EDGE,"E7.1.4"),sQuery(id+"F0.wireOp",EDGE,"E7.1.5"),sQuery(id+"F0.wireOp",EDGE,"E7.2.0"),sQuery(id+"F0.wireOp",EDGE,"E7.2.1"),sQuery(id+"F0.wireOp",EDGE,"E7.2.2"),sQuery(id+"F0.wireOp",EDGE,"E7.2.3"),sQuery(id+"F0.wireOp",EDGE,"E7.2.4"),sQuery(id+"F0.wireOp",EDGE,"E7.2.5"),sQuery(id+"F0.wireOp",EDGE,"E7.3.0"),sQuery(id+"F0.wireOp",EDGE,"E7.3.1"),sQuery(id+"F0.wireOp",EDGE,"E7.3.2"),sQuery(id+"F0.wireOp",EDGE,"E7.3.3"),sQuery(id+"F0.wireOp",EDGE,"E7.3.4"),sQuery(id+"F0.wireOp",EDGE,"E7.3.5"),sQuery(id+"F0.wireOp",EDGE,"E7.4.0"),sQuery(id+"F0.wireOp",EDGE,"E7.4.1"),sQuery(id+"F0.wireOp",EDGE,"E7.4.2"),sQuery(id+"F0.wireOp",EDGE,"E7.4.3"),sQuery(id+"F0.wireOp",EDGE,"E7.4.4"),sQuery(id+"F0.wireOp",EDGE,"E7.4.5"),sQuery(id+"F0.wireOp",EDGE,"E7.5.0"),sQuery(id+"F0.wireOp",EDGE,"E7.5.1"),sQuery(id+"F0.wireOp",EDGE,"E7.5.2"),sQuery(id+"F0.wireOp",EDGE,"E7.5.3"),sQuery(id+"F0.wireOp",EDGE,"E7.5.4"),sQuery(id+"F0.wireOp",EDGE,"E7.5.5"),sQuery(id+"F0.wireOp",EDGE,"E7.6.0"),sQuery(id+"F0.wireOp",EDGE,"E7.6.1"),sQuery(id+"F0.wireOp",EDGE,"E7.6.2"),sQuery(id+"F0.wireOp",EDGE,"E7.6.3"),sQuery(id+"F0.wireOp",EDGE,"E7.6.4"),sQuery(id+"F0.wireOp",EDGE,"E7.6.5"),sQuery(id+"F0.wireOp",EDGE,"E7.7.0"),sQuery(id+"F0.wireOp",EDGE,"E7.7.1"),sQuery(id+"F0.wireOp",EDGE,"E7.7.2"),sQuery(id+"F0.wireOp",EDGE,"E7.7.3"),sQuery(id+"F0.wireOp",EDGE,"E7.7.4"),sQuery(id+"F0.wireOp",EDGE,"E7.7.5"),sQuery(id+"F0.wireOp",EDGE,"E7.8.0"),sQuery(id+"F0.wireOp",EDGE,"E7.8.1"),sQuery(id+"F0.wireOp",EDGE,"E7.8.2"),sQuery(id+"F0.wireOp",EDGE,"E7.8.3"),sQuery(id+"F0.wireOp",EDGE,"E7.8.4"),sQuery(id+"F0.wireOp",EDGE,"E7.8.5"),sQuery(id+"F0.wireOp",EDGE,"E7.9.0"),sQuery(id+"F0.wireOp",EDGE,"E7.9.1"),sQuery(id+"F0.wireOp",EDGE,"E7.9.2"),sQuery(id+"F0.wireOp",EDGE,"E7.9.3"),sQuery(id+"F0.wireOp",EDGE,"E7.9.4"),sQuery(id+"F0.wireOp",EDGE,"E7.9.5"),sQuery(id+"F0.wireOp",EDGE,"E7.10.0"),sQuery(id+"F0.wireOp",EDGE,"E7.10.1"),sQuery(id+"F0.wireOp",EDGE,"E7.10.2"),sQuery(id+"F0.wireOp",EDGE,"E7.10.3"),sQuery(id+"F0.wireOp",EDGE,"E7.10.4"),sQuery(id+"F0.wireOp",EDGE,"E7.10.5"),sQuery(id+"F0.wireOp",EDGE,"E7.11.0"),sQuery(id+"F0.wireOp",EDGE,"E7.11.1"),sQuery(id+"F0.wireOp",EDGE,"E7.11.2"),sQuery(id+"F0.wireOp",EDGE,"E7.11.3"),sQuery(id+"F0.wireOp",EDGE,"E7.11.4"),sQuery(id+"F0.wireOp",EDGE,"E7.11.5"),sQuery(id+"F0.wireOp",EDGE,"E7.12.0"),sQuery(id+"F0.wireOp",EDGE,"E7.12.1"),sQuery(id+"F0.wireOp",EDGE,"E7.12.2"),sQuery(id+"F0.wireOp",EDGE,"E7.12.3"),sQuery(id+"F0.wireOp",EDGE,"E7.12.4"),sQuery(id+"F0.wireOp",EDGE,"E7.12.5"),sQuery(id+"F0.wireOp",EDGE,"E7.13.0"),sQuery(id+"F0.wireOp",EDGE,"E7.13.1"),sQuery(id+"F0.wireOp",EDGE,"E7.13.2"),sQuery(id+"F0.wireOp",EDGE,"E7.13.3"),sQuery(id+"F0.wireOp",EDGE,"E7.13.4"),sQuery(id+"F0.wireOp",EDGE,"E7.13.5"),sQuery(id+"F0.wireOp",EDGE,"E7.14.0"),sQuery(id+"F0.wireOp",EDGE,"E7.14.1"),sQuery(id+"F0.wireOp",EDGE,"E7.14.2"),sQuery(id+"F0.wireOp",EDGE,"E7.14.3"),sQuery(id+"F0.wireOp",EDGE,"E7.14.4"),sQuery(id+"F0.wireOp",EDGE,"E7.14.5"),sQuery(id+"F0.wireOp",EDGE,"E7.15.0"),sQuery(id+"F0.wireOp",EDGE,"E7.15.1"),sQuery(id+"F0.wireOp",EDGE,"E7.15.2"),sQuery(id+"F0.wireOp",EDGE,"E7.15.3"),sQuery(id+"F0.wireOp",EDGE,"E7.15.4"),sQuery(id+"F0.wireOp",EDGE,"E7.15.5"),sQuery(id+"F0.wireOp",EDGE,"E7.16.0"),sQuery(id+"F0.wireOp",EDGE,"E7.16.1"),sQuery(id+"F0.wireOp",EDGE,"E7.16.2"),sQuery(id+"F0.wireOp",EDGE,"E7.16.3"),sQuery(id+"F0.wireOp",EDGE,"E7.16.4"),sQuery(id+"F0.wireOp",EDGE,"E7.16.5"),sQuery(id+"F0.wireOp",EDGE,"E7.17.0"),sQuery(id+"F0.wireOp",EDGE,"E7.17.1"),sQuery(id+"F0.wireOp",EDGE,"E7.17.2"),sQuery(id+"F0.wireOp",EDGE,"E7.17.3"),sQuery(id+"F0.wireOp",EDGE,"E7.17.4"),sQuery(id+"F0.wireOp",EDGE,"E7.17.5"),sQuery(id+"F0.wireOp",EDGE,"E7.18.0"),sQuery(id+"F0.wireOp",EDGE,"E7.18.1"),sQuery(id+"F0.wireOp",EDGE,"E7.18.2"),sQuery(id+"F0.wireOp",EDGE,"E7.18.3"),sQuery(id+"F0.wireOp",EDGE,"E7.18.4"),sQuery(id+"F0.wireOp",EDGE,"E7.18.5"),sQuery(id+"F0.wireOp",EDGE,"E7.19.0"),sQuery(id+"F0.wireOp",EDGE,"E7.19.1"),sQuery(id+"F0.wireOp",EDGE,"E7.19.2"),sQuery(id+"F0.wireOp",EDGE,"E7.19.3"),sQuery(id+"F0.wireOp",EDGE,"E7.19.4"),sQuery(id+"F0.wireOp",EDGE,"E7.19.5"),sQuery(id+"F0.wireOp",EDGE,"E7.20.0"),sQuery(id+"F0.wireOp",EDGE,"E7.20.1"),sQuery(id+"F0.wireOp",EDGE,"E7.20.2"),sQuery(id+"F0.wireOp",EDGE,"E7.20.3"),sQuery(id+"F0.wireOp",EDGE,"E7.20.4"),sQuery(id+"F0.wireOp",EDGE,"E7.20.5"),sQuery(id+"F0.wireOp",EDGE,"E7.21.0"),sQuery(id+"F0.wireOp",EDGE,"E7.21.1"),sQuery(id+"F0.wireOp",EDGE,"E7.21.2"),sQuery(id+"F0.wireOp",EDGE,"E7.21.3"),sQuery(id+"F0.wireOp",EDGE,"E7.21.4"),sQuery(id+"F0.wireOp",EDGE,"E7.21.5"),sQuery(id+"F0.wireOp",EDGE,"E7.22.0"),sQuery(id+"F0.wireOp",EDGE,"E7.22.1"),sQuery(id+"F0.wireOp",EDGE,"E7.22.2"),sQuery(id+"F0.wireOp",EDGE,"E7.22.3"),sQuery(id+"F0.wireOp",EDGE,"E7.22.4"),sQuery(id+"F0.wireOp",EDGE,"E7.22.5"),sQuery(id+"F0.wireOp",EDGE,"E7.23.0"),sQuery(id+"F0.wireOp",EDGE,"E7.23.1"),sQuery(id+"F0.wireOp",EDGE,"E7.23.2"),sQuery(id+"F0.wireOp",EDGE,"E7.23.3"),sQuery(id+"F0.wireOp",EDGE,"E7.23.4"),sQuery(id+"F0.wireOp",EDGE,"E7.23.5"),sQuery(id+"F0.wireOp",EDGE,"E7.24.0"),sQuery(id+"F0.wireOp",EDGE,"E7.24.1"),sQuery(id+"F0.wireOp",EDGE,"E7.24.2"),sQuery(id+"F0.wireOp",EDGE,"E7.24.3"),sQuery(id+"F0.wireOp",EDGE,"E7.24.4"),sQuery(id+"F0.wireOp",EDGE,"E7.24.5"),sQuery(id+"F0.wireOp",EDGE,"E7.25.0"),sQuery(id+"F0.wireOp",EDGE,"E7.25.1"),sQuery(id+"F0.wireOp",EDGE,"E7.25.2"),sQuery(id+"F0.wireOp",EDGE,"E7.25.3"),sQuery(id+"F0.wireOp",EDGE,"E7.25.4"),sQuery(id+"F0.wireOp",EDGE,"E7.25.5"),sQuery(id+"F0.wireOp",EDGE,"E7.26.0"),sQuery(id+"F0.wireOp",EDGE,"E7.26.1"),sQuery(id+"F0.wireOp",EDGE,"E7.26.2"),sQuery(id+"F0.wireOp",EDGE,"E7.26.3"),sQuery(id+"F0.wireOp",EDGE,"E7.26.4"),sQuery(id+"F0.wireOp",EDGE,"E7.26.5"),sQuery(id+"F0.wireOp",EDGE,"E7.27.0"),sQuery(id+"F0.wireOp",EDGE,"E7.27.1"),sQuery(id+"F0.wireOp",EDGE,"E7.27.2"),sQuery(id+"F0.wireOp",EDGE,"E7.27.3"),sQuery(id+"F0.wireOp",EDGE,"E7.27.4"),sQuery(id+"F0.wireOp",EDGE,"E7.27.5"),sQuery(id+"F0.wireOp",EDGE,"E7.28.0"),sQuery(id+"F0.wireOp",EDGE,"E7.28.1"),sQuery(id+"F0.wireOp",EDGE,"E7.28.2"),sQuery(id+"F0.wireOp",EDGE,"E7.28.3"),sQuery(id+"F0.wireOp",EDGE,"E7.28.4"),sQuery(id+"F0.wireOp",EDGE,"E7.28.5"),sQuery(id+"F0.wireOp",EDGE,"E7.29.0"),sQuery(id+"F0.wireOp",EDGE,"E7.29.1"),sQuery(id+"F0.wireOp",EDGE,"E7.29.2"),sQuery(id+"F0.wireOp",EDGE,"E7.29.3"),sQuery(id+"F0.wireOp",EDGE,"E7.29.4"),sQuery(id+"F0.wireOp",EDGE,"E7.29.5"),sQuery(id+"F0.wireOp",EDGE,"E7.30.0"),sQuery(id+"F0.wireOp",EDGE,"E7.30.1"),sQuery(id+"F0.wireOp",EDGE,"E7.30.2"),sQuery(id+"F0.wireOp",EDGE,"E7.30.3"),sQuery(id+"F0.wireOp",EDGE,"E7.30.4"),sQuery(id+"F0.wireOp",EDGE,"E7.30.5"),sQuery(id+"F0.wireOp",EDGE,"E7.31.0"),sQuery(id+"F0.wireOp",EDGE,"E7.31.1"),sQuery(id+"F0.wireOp",EDGE,"E7.31.2"),sQuery(id+"F0.wireOp",EDGE,"E7.31.3"),sQuery(id+"F0.wireOp",EDGE,"E7.31.4"),sQuery(id+"F0.wireOp",EDGE,"E7.31.5"),sQuery(id+"F0.wireOp",EDGE,"E7.32.0"),sQuery(id+"F0.wireOp",EDGE,"E7.32.1"),sQuery(id+"F0.wireOp",EDGE,"E7.32.2"),sQuery(id+"F0.wireOp",EDGE,"E7.32.3"),sQuery(id+"F0.wireOp",EDGE,"E7.32.4"),sQuery(id+"F0.wireOp",EDGE,"E7.32.5"),subQ0,sQuery(id+"F0.wireOp",EDGE,"E7.33.1"),sQuery(id+"F0.wireOp",EDGE,"E7.33.2"),sQuery(id+"F0.wireOp",EDGE,"E7.33.3"),sQuery(id+"F0.wireOp",EDGE,"E7.33.4"),sQuery(id+"F0.wireOp",EDGE,"E7.33.5"),sQuery(id+"F0.wireOp",EDGE,"E7.34.0"),sQuery(id+"F0.wireOp",EDGE,"E7.34.1"),sQuery(id+"F0.wireOp",EDGE,"E7.34.2"),sQuery(id+"F0.wireOp",EDGE,"E7.34.3"),sQuery(id+"F0.wireOp",EDGE,"E7.34.4"),sQuery(id+"F0.wireOp",EDGE,"E7.34.5"),sQuery(id+"F0.wireOp",EDGE,"E7.35.0"),sQuery(id+"F0.wireOp",EDGE,"E7.35.1"),sQuery(id+"F0.wireOp",EDGE,"E7.35.2"),sQuery(id+"F0.wireOp",EDGE,"E7.35.3"),sQuery(id+"F0.wireOp",EDGE,"E7.35.4"),sQuery(id+"F0.wireOp",EDGE,"E7.35.5"),sQuery(id+"F0.wireOp",EDGE,"E7.36.0"),sQuery(id+"F0.wireOp",EDGE,"E7.36.1"),sQuery(id+"F0.wireOp",EDGE,"E7.36.2"),sQuery(id+"F0.wireOp",EDGE,"E7.36.3"),sQuery(id+"F0.wireOp",EDGE,"E7.36.4"),sQuery(id+"F0.wireOp",EDGE,"E7.36.5"),sQuery(id+"F0.wireOp",EDGE,"E7.37.0"),sQuery(id+"F0.wireOp",EDGE,"E7.37.1"),sQuery(id+"F0.wireOp",EDGE,"E7.37.2"),sQuery(id+"F0.wireOp",EDGE,"E7.37.3"),sQuery(id+"F0.wireOp",EDGE,"E7.37.4"),sQuery(id+"F0.wireOp",EDGE,"E7.37.5"),sQuery(id+"F0.wireOp",EDGE,"E7.38.0"),sQuery(id+"F0.wireOp",EDGE,"E7.38.1"),sQuery(id+"F0.wireOp",EDGE,"E7.38.2"),sQuery(id+"F0.wireOp",EDGE,"E7.38.3"),sQuery(id+"F0.wireOp",EDGE,"E7.38.4"),sQuery(id+"F0.wireOp",EDGE,"E7.38.5"),sQuery(id+"F0.wireOp",EDGE,"E7.39.0"),sQuery(id+"F0.wireOp",EDGE,"E7.39.1"),sQuery(id+"F0.wireOp",EDGE,"E7.39.2"),sQuery(id+"F0.wireOp",EDGE,"E7.39.3"),sQuery(id+"F0.wireOp",EDGE,"E7.39.4"),sQuery(id+"F0.wireOp",EDGE,"E7.39.5"),sQuery(id+"F0.wireOp",EDGE,"E7.40.0"),sQuery(id+"F0.wireOp",EDGE,"E7.40.1"),sQuery(id+"F0.wireOp",EDGE,"E7.40.2"),sQuery(id+"F0.wireOp",EDGE,"E7.40.3"),sQuery(id+"F0.wireOp",EDGE,"E7.40.4"),sQuery(id+"F0.wireOp",EDGE,"E7.40.5"),sQuery(id+"F0.wireOp",EDGE,"E7.41.0"),sQuery(id+"F0.wireOp",EDGE,"E7.41.1"),sQuery(id+"F0.wireOp",EDGE,"E7.41.2"),sQuery(id+"F0.wireOp",EDGE,"E7.41.3"),sQuery(id+"F0.wireOp",EDGE,"E7.41.4"),sQuery(id+"F0.wireOp",EDGE,"E7.41.5"),sQuery(id+"F0.wireOp",EDGE,"E7.42.0"),sQuery(id+"F0.wireOp",EDGE,"E7.42.1"),sQuery(id+"F0.wireOp",EDGE,"E7.42.2"),sQuery(id+"F0.wireOp",EDGE,"E7.42.3"),sQuery(id+"F0.wireOp",EDGE,"E7.42.4"),sQuery(id+"F0.wireOp",EDGE,"E7.42.5"),sQuery(id+"F0.wireOp",EDGE,"E7.43.0"),sQuery(id+"F0.wireOp",EDGE,"E7.43.1"),sQuery(id+"F0.wireOp",EDGE,"E7.43.2"),sQuery(id+"F0.wireOp",EDGE,"E7.43.3"),sQuery(id+"F0.wireOp",EDGE,"E7.43.4"),sQuery(id+"F0.wireOp",EDGE,"E7.43.5")])],"isStart":false})]});}
            var Q6;
            {var subQ0=sQuery(id+"F0.wireOp",EDGE,"E7.31.0");Q6=makeQuery(id+"F2.opChamfer","BLEND_EDGE",EDGE,{"blendedFrom":[makeQuery(id+"F1.opExtrude","CAP_EDGE",EDGE,{"disambiguationData":[OSD([subQ0])],"isStart":false}),makeQuery(id+"F1.opExtrude","CAP_FACE",FACE,{"disambiguationData":[OSD([sQuery(id+"F0.wireOp",EDGE,"E1"),sQuery(id+"F0.wireOp",EDGE,"E2"),sQuery(id+"F0.wireOp",EDGE,"E3"),sQuery(id+"F0.wireOp",EDGE,"E4"),sQuery(id+"F0.wireOp",EDGE,"E5"),sQuery(id+"F0.wireOp",EDGE,"E6"),sQuery(id+"F0.wireOp",EDGE,"E7.1.0"),sQuery(id+"F0.wireOp",EDGE,"E7.1.1"),sQuery(id+"F0.wireOp",EDGE,"E7.1.2"),sQuery(id+"F0.wireOp",EDGE,"E7.1.3"),sQuery(id+"F0.wireOp",EDGE,"E7.1.4"),sQuery(id+"F0.wireOp",EDGE,"E7.1.5"),sQuery(id+"F0.wireOp",EDGE,"E7.2.0"),sQuery(id+"F0.wireOp",EDGE,"E7.2.1"),sQuery(id+"F0.wireOp",EDGE,"E7.2.2"),sQuery(id+"F0.wireOp",EDGE,"E7.2.3"),sQuery(id+"F0.wireOp",EDGE,"E7.2.4"),sQuery(id+"F0.wireOp",EDGE,"E7.2.5"),sQuery(id+"F0.wireOp",EDGE,"E7.3.0"),sQuery(id+"F0.wireOp",EDGE,"E7.3.1"),sQuery(id+"F0.wireOp",EDGE,"E7.3.2"),sQuery(id+"F0.wireOp",EDGE,"E7.3.3"),sQuery(id+"F0.wireOp",EDGE,"E7.3.4"),sQuery(id+"F0.wireOp",EDGE,"E7.3.5"),sQuery(id+"F0.wireOp",EDGE,"E7.4.0"),sQuery(id+"F0.wireOp",EDGE,"E7.4.1"),sQuery(id+"F0.wireOp",EDGE,"E7.4.2"),sQuery(id+"F0.wireOp",EDGE,"E7.4.3"),sQuery(id+"F0.wireOp",EDGE,"E7.4.4"),sQuery(id+"F0.wireOp",EDGE,"E7.4.5"),sQuery(id+"F0.wireOp",EDGE,"E7.5.0"),sQuery(id+"F0.wireOp",EDGE,"E7.5.1"),sQuery(id+"F0.wireOp",EDGE,"E7.5.2"),sQuery(id+"F0.wireOp",EDGE,"E7.5.3"),sQuery(id+"F0.wireOp",EDGE,"E7.5.4"),sQuery(id+"F0.wireOp",EDGE,"E7.5.5"),sQuery(id+"F0.wireOp",EDGE,"E7.6.0"),sQuery(id+"F0.wireOp",EDGE,"E7.6.1"),sQuery(id+"F0.wireOp",EDGE,"E7.6.2"),sQuery(id+"F0.wireOp",EDGE,"E7.6.3"),sQuery(id+"F0.wireOp",EDGE,"E7.6.4"),sQuery(id+"F0.wireOp",EDGE,"E7.6.5"),sQuery(id+"F0.wireOp",EDGE,"E7.7.0"),sQuery(id+"F0.wireOp",EDGE,"E7.7.1"),sQuery(id+"F0.wireOp",EDGE,"E7.7.2"),sQuery(id+"F0.wireOp",EDGE,"E7.7.3"),sQuery(id+"F0.wireOp",EDGE,"E7.7.4"),sQuery(id+"F0.wireOp",EDGE,"E7.7.5"),sQuery(id+"F0.wireOp",EDGE,"E7.8.0"),sQuery(id+"F0.wireOp",EDGE,"E7.8.1"),sQuery(id+"F0.wireOp",EDGE,"E7.8.2"),sQuery(id+"F0.wireOp",EDGE,"E7.8.3"),sQuery(id+"F0.wireOp",EDGE,"E7.8.4"),sQuery(id+"F0.wireOp",EDGE,"E7.8.5"),sQuery(id+"F0.wireOp",EDGE,"E7.9.0"),sQuery(id+"F0.wireOp",EDGE,"E7.9.1"),sQuery(id+"F0.wireOp",EDGE,"E7.9.2"),sQuery(id+"F0.wireOp",EDGE,"E7.9.3"),sQuery(id+"F0.wireOp",EDGE,"E7.9.4"),sQuery(id+"F0.wireOp",EDGE,"E7.9.5"),sQuery(id+"F0.wireOp",EDGE,"E7.10.0"),sQuery(id+"F0.wireOp",EDGE,"E7.10.1"),sQuery(id+"F0.wireOp",EDGE,"E7.10.2"),sQuery(id+"F0.wireOp",EDGE,"E7.10.3"),sQuery(id+"F0.wireOp",EDGE,"E7.10.4"),sQuery(id+"F0.wireOp",EDGE,"E7.10.5"),sQuery(id+"F0.wireOp",EDGE,"E7.11.0"),sQuery(id+"F0.wireOp",EDGE,"E7.11.1"),sQuery(id+"F0.wireOp",EDGE,"E7.11.2"),sQuery(id+"F0.wireOp",EDGE,"E7.11.3"),sQuery(id+"F0.wireOp",EDGE,"E7.11.4"),sQuery(id+"F0.wireOp",EDGE,"E7.11.5"),sQuery(id+"F0.wireOp",EDGE,"E7.12.0"),sQuery(id+"F0.wireOp",EDGE,"E7.12.1"),sQuery(id+"F0.wireOp",EDGE,"E7.12.2"),sQuery(id+"F0.wireOp",EDGE,"E7.12.3"),sQuery(id+"F0.wireOp",EDGE,"E7.12.4"),sQuery(id+"F0.wireOp",EDGE,"E7.12.5"),sQuery(id+"F0.wireOp",EDGE,"E7.13.0"),sQuery(id+"F0.wireOp",EDGE,"E7.13.1"),sQuery(id+"F0.wireOp",EDGE,"E7.13.2"),sQuery(id+"F0.wireOp",EDGE,"E7.13.3"),sQuery(id+"F0.wireOp",EDGE,"E7.13.4"),sQuery(id+"F0.wireOp",EDGE,"E7.13.5"),sQuery(id+"F0.wireOp",EDGE,"E7.14.0"),sQuery(id+"F0.wireOp",EDGE,"E7.14.1"),sQuery(id+"F0.wireOp",EDGE,"E7.14.2"),sQuery(id+"F0.wireOp",EDGE,"E7.14.3"),sQuery(id+"F0.wireOp",EDGE,"E7.14.4"),sQuery(id+"F0.wireOp",EDGE,"E7.14.5"),sQuery(id+"F0.wireOp",EDGE,"E7.15.0"),sQuery(id+"F0.wireOp",EDGE,"E7.15.1"),sQuery(id+"F0.wireOp",EDGE,"E7.15.2"),sQuery(id+"F0.wireOp",EDGE,"E7.15.3"),sQuery(id+"F0.wireOp",EDGE,"E7.15.4"),sQuery(id+"F0.wireOp",EDGE,"E7.15.5"),sQuery(id+"F0.wireOp",EDGE,"E7.16.0"),sQuery(id+"F0.wireOp",EDGE,"E7.16.1"),sQuery(id+"F0.wireOp",EDGE,"E7.16.2"),sQuery(id+"F0.wireOp",EDGE,"E7.16.3"),sQuery(id+"F0.wireOp",EDGE,"E7.16.4"),sQuery(id+"F0.wireOp",EDGE,"E7.16.5"),sQuery(id+"F0.wireOp",EDGE,"E7.17.0"),sQuery(id+"F0.wireOp",EDGE,"E7.17.1"),sQuery(id+"F0.wireOp",EDGE,"E7.17.2"),sQuery(id+"F0.wireOp",EDGE,"E7.17.3"),sQuery(id+"F0.wireOp",EDGE,"E7.17.4"),sQuery(id+"F0.wireOp",EDGE,"E7.17.5"),sQuery(id+"F0.wireOp",EDGE,"E7.18.0"),sQuery(id+"F0.wireOp",EDGE,"E7.18.1"),sQuery(id+"F0.wireOp",EDGE,"E7.18.2"),sQuery(id+"F0.wireOp",EDGE,"E7.18.3"),sQuery(id+"F0.wireOp",EDGE,"E7.18.4"),sQuery(id+"F0.wireOp",EDGE,"E7.18.5"),sQuery(id+"F0.wireOp",EDGE,"E7.19.0"),sQuery(id+"F0.wireOp",EDGE,"E7.19.1"),sQuery(id+"F0.wireOp",EDGE,"E7.19.2"),sQuery(id+"F0.wireOp",EDGE,"E7.19.3"),sQuery(id+"F0.wireOp",EDGE,"E7.19.4"),sQuery(id+"F0.wireOp",EDGE,"E7.19.5"),sQuery(id+"F0.wireOp",EDGE,"E7.20.0"),sQuery(id+"F0.wireOp",EDGE,"E7.20.1"),sQuery(id+"F0.wireOp",EDGE,"E7.20.2"),sQuery(id+"F0.wireOp",EDGE,"E7.20.3"),sQuery(id+"F0.wireOp",EDGE,"E7.20.4"),sQuery(id+"F0.wireOp",EDGE,"E7.20.5"),sQuery(id+"F0.wireOp",EDGE,"E7.21.0"),sQuery(id+"F0.wireOp",EDGE,"E7.21.1"),sQuery(id+"F0.wireOp",EDGE,"E7.21.2"),sQuery(id+"F0.wireOp",EDGE,"E7.21.3"),sQuery(id+"F0.wireOp",EDGE,"E7.21.4"),sQuery(id+"F0.wireOp",EDGE,"E7.21.5"),sQuery(id+"F0.wireOp",EDGE,"E7.22.0"),sQuery(id+"F0.wireOp",EDGE,"E7.22.1"),sQuery(id+"F0.wireOp",EDGE,"E7.22.2"),sQuery(id+"F0.wireOp",EDGE,"E7.22.3"),sQuery(id+"F0.wireOp",EDGE,"E7.22.4"),sQuery(id+"F0.wireOp",EDGE,"E7.22.5"),sQuery(id+"F0.wireOp",EDGE,"E7.23.0"),sQuery(id+"F0.wireOp",EDGE,"E7.23.1"),sQuery(id+"F0.wireOp",EDGE,"E7.23.2"),sQuery(id+"F0.wireOp",EDGE,"E7.23.3"),sQuery(id+"F0.wireOp",EDGE,"E7.23.4"),sQuery(id+"F0.wireOp",EDGE,"E7.23.5"),sQuery(id+"F0.wireOp",EDGE,"E7.24.0"),sQuery(id+"F0.wireOp",EDGE,"E7.24.1"),sQuery(id+"F0.wireOp",EDGE,"E7.24.2"),sQuery(id+"F0.wireOp",EDGE,"E7.24.3"),sQuery(id+"F0.wireOp",EDGE,"E7.24.4"),sQuery(id+"F0.wireOp",EDGE,"E7.24.5"),sQuery(id+"F0.wireOp",EDGE,"E7.25.0"),sQuery(id+"F0.wireOp",EDGE,"E7.25.1"),sQuery(id+"F0.wireOp",EDGE,"E7.25.2"),sQuery(id+"F0.wireOp",EDGE,"E7.25.3"),sQuery(id+"F0.wireOp",EDGE,"E7.25.4"),sQuery(id+"F0.wireOp",EDGE,"E7.25.5"),sQuery(id+"F0.wireOp",EDGE,"E7.26.0"),sQuery(id+"F0.wireOp",EDGE,"E7.26.1"),sQuery(id+"F0.wireOp",EDGE,"E7.26.2"),sQuery(id+"F0.wireOp",EDGE,"E7.26.3"),sQuery(id+"F0.wireOp",EDGE,"E7.26.4"),sQuery(id+"F0.wireOp",EDGE,"E7.26.5"),sQuery(id+"F0.wireOp",EDGE,"E7.27.0"),sQuery(id+"F0.wireOp",EDGE,"E7.27.1"),sQuery(id+"F0.wireOp",EDGE,"E7.27.2"),sQuery(id+"F0.wireOp",EDGE,"E7.27.3"),sQuery(id+"F0.wireOp",EDGE,"E7.27.4"),sQuery(id+"F0.wireOp",EDGE,"E7.27.5"),sQuery(id+"F0.wireOp",EDGE,"E7.28.0"),sQuery(id+"F0.wireOp",EDGE,"E7.28.1"),sQuery(id+"F0.wireOp",EDGE,"E7.28.2"),sQuery(id+"F0.wireOp",EDGE,"E7.28.3"),sQuery(id+"F0.wireOp",EDGE,"E7.28.4"),sQuery(id+"F0.wireOp",EDGE,"E7.28.5"),sQuery(id+"F0.wireOp",EDGE,"E7.29.0"),sQuery(id+"F0.wireOp",EDGE,"E7.29.1"),sQuery(id+"F0.wireOp",EDGE,"E7.29.2"),sQuery(id+"F0.wireOp",EDGE,"E7.29.3"),sQuery(id+"F0.wireOp",EDGE,"E7.29.4"),sQuery(id+"F0.wireOp",EDGE,"E7.29.5"),sQuery(id+"F0.wireOp",EDGE,"E7.30.0"),sQuery(id+"F0.wireOp",EDGE,"E7.30.1"),sQuery(id+"F0.wireOp",EDGE,"E7.30.2"),sQuery(id+"F0.wireOp",EDGE,"E7.30.3"),sQuery(id+"F0.wireOp",EDGE,"E7.30.4"),sQuery(id+"F0.wireOp",EDGE,"E7.30.5"),subQ0,sQuery(id+"F0.wireOp",EDGE,"E7.31.1"),sQuery(id+"F0.wireOp",EDGE,"E7.31.2"),sQuery(id+"F0.wireOp",EDGE,"E7.31.3"),sQuery(id+"F0.wireOp",EDGE,"E7.31.4"),sQuery(id+"F0.wireOp",EDGE,"E7.31.5"),sQuery(id+"F0.wireOp",EDGE,"E7.32.0"),sQuery(id+"F0.wireOp",EDGE,"E7.32.1"),sQuery(id+"F0.wireOp",EDGE,"E7.32.2"),sQuery(id+"F0.wireOp",EDGE,"E7.32.3"),sQuery(id+"F0.wireOp",EDGE,"E7.32.4"),sQuery(id+"F0.wireOp",EDGE,"E7.32.5"),sQuery(id+"F0.wireOp",EDGE,"E7.33.0"),sQuery(id+"F0.wireOp",EDGE,"E7.33.1"),sQuery(id+"F0.wireOp",EDGE,"E7.33.2"),sQuery(id+"F0.wireOp",EDGE,"E7.33.3"),sQuery(id+"F0.wireOp",EDGE,"E7.33.4"),sQuery(id+"F0.wireOp",EDGE,"E7.33.5"),sQuery(id+"F0.wireOp",EDGE,"E7.34.0"),sQuery(id+"F0.wireOp",EDGE,"E7.34.1"),sQuery(id+"F0.wireOp",EDGE,"E7.34.2"),sQuery(id+"F0.wireOp",EDGE,"E7.34.3"),sQuery(id+"F0.wireOp",EDGE,"E7.34.4"),sQuery(id+"F0.wireOp",EDGE,"E7.34.5"),sQuery(id+"F0.wireOp",EDGE,"E7.35.0"),sQuery(id+"F0.wireOp",EDGE,"E7.35.1"),sQuery(id+"F0.wireOp",EDGE,"E7.35.2"),sQuery(id+"F0.wireOp",EDGE,"E7.35.3"),sQuery(id+"F0.wireOp",EDGE,"E7.35.4"),sQuery(id+"F0.wireOp",EDGE,"E7.35.5"),sQuery(id+"F0.wireOp",EDGE,"E7.36.0"),sQuery(id+"F0.wireOp",EDGE,"E7.36.1"),sQuery(id+"F0.wireOp",EDGE,"E7.36.2"),sQuery(id+"F0.wireOp",EDGE,"E7.36.3"),sQuery(id+"F0.wireOp",EDGE,"E7.36.4"),sQuery(id+"F0.wireOp",EDGE,"E7.36.5"),sQuery(id+"F0.wireOp",EDGE,"E7.37.0"),sQuery(id+"F0.wireOp",EDGE,"E7.37.1"),sQuery(id+"F0.wireOp",EDGE,"E7.37.2"),sQuery(id+"F0.wireOp",EDGE,"E7.37.3"),sQuery(id+"F0.wireOp",EDGE,"E7.37.4"),sQuery(id+"F0.wireOp",EDGE,"E7.37.5"),sQuery(id+"F0.wireOp",EDGE,"E7.38.0"),sQuery(id+"F0.wireOp",EDGE,"E7.38.1"),sQuery(id+"F0.wireOp",EDGE,"E7.38.2"),sQuery(id+"F0.wireOp",EDGE,"E7.38.3"),sQuery(id+"F0.wireOp",EDGE,"E7.38.4"),sQuery(id+"F0.wireOp",EDGE,"E7.38.5"),sQuery(id+"F0.wireOp",EDGE,"E7.39.0"),sQuery(id+"F0.wireOp",EDGE,"E7.39.1"),sQuery(id+"F0.wireOp",EDGE,"E7.39.2"),sQuery(id+"F0.wireOp",EDGE,"E7.39.3"),sQuery(id+"F0.wireOp",EDGE,"E7.39.4"),sQuery(id+"F0.wireOp",EDGE,"E7.39.5"),sQuery(id+"F0.wireOp",EDGE,"E7.40.0"),sQuery(id+"F0.wireOp",EDGE,"E7.40.1"),sQuery(id+"F0.wireOp",EDGE,"E7.40.2"),sQuery(id+"F0.wireOp",EDGE,"E7.40.3"),sQuery(id+"F0.wireOp",EDGE,"E7.40.4"),sQuery(id+"F0.wireOp",EDGE,"E7.40.5"),sQuery(id+"F0.wireOp",EDGE,"E7.41.0"),sQuery(id+"F0.wireOp",EDGE,"E7.41.1"),sQuery(id+"F0.wireOp",EDGE,"E7.41.2"),sQuery(id+"F0.wireOp",EDGE,"E7.41.3"),sQuery(id+"F0.wireOp",EDGE,"E7.41.4"),sQuery(id+"F0.wireOp",EDGE,"E7.41.5"),sQuery(id+"F0.wireOp",EDGE,"E7.42.0"),sQuery(id+"F0.wireOp",EDGE,"E7.42.1"),sQuery(id+"F0.wireOp",EDGE,"E7.42.2"),sQuery(id+"F0.wireOp",EDGE,"E7.42.3"),sQuery(id+"F0.wireOp",EDGE,"E7.42.4"),sQuery(id+"F0.wireOp",EDGE,"E7.42.5"),sQuery(id+"F0.wireOp",EDGE,"E7.43.0"),sQuery(id+"F0.wireOp",EDGE,"E7.43.1"),sQuery(id+"F0.wireOp",EDGE,"E7.43.2"),sQuery(id+"F0.wireOp",EDGE,"E7.43.3"),sQuery(id+"F0.wireOp",EDGE,"E7.43.4"),sQuery(id+"F0.wireOp",EDGE,"E7.43.5")])],"isStart":false})],"blendedInto":[makeQuery(id+"F1.opExtrude","CAP_FACE",FACE,{"disambiguationData":[OSD([sQuery(id+"F0.wireOp",EDGE,"E1"),sQuery(id+"F0.wireOp",EDGE,"E2"),sQuery(id+"F0.wireOp",EDGE,"E3"),sQuery(id+"F0.wireOp",EDGE,"E4"),sQuery(id+"F0.wireOp",EDGE,"E5"),sQuery(id+"F0.wireOp",EDGE,"E6"),sQuery(id+"F0.wireOp",EDGE,"E7.1.0"),sQuery(id+"F0.wireOp",EDGE,"E7.1.1"),sQuery(id+"F0.wireOp",EDGE,"E7.1.2"),sQuery(id+"F0.wireOp",EDGE,"E7.1.3"),sQuery(id+"F0.wireOp",EDGE,"E7.1.4"),sQuery(id+"F0.wireOp",EDGE,"E7.1.5"),sQuery(id+"F0.wireOp",EDGE,"E7.2.0"),sQuery(id+"F0.wireOp",EDGE,"E7.2.1"),sQuery(id+"F0.wireOp",EDGE,"E7.2.2"),sQuery(id+"F0.wireOp",EDGE,"E7.2.3"),sQuery(id+"F0.wireOp",EDGE,"E7.2.4"),sQuery(id+"F0.wireOp",EDGE,"E7.2.5"),sQuery(id+"F0.wireOp",EDGE,"E7.3.0"),sQuery(id+"F0.wireOp",EDGE,"E7.3.1"),sQuery(id+"F0.wireOp",EDGE,"E7.3.2"),sQuery(id+"F0.wireOp",EDGE,"E7.3.3"),sQuery(id+"F0.wireOp",EDGE,"E7.3.4"),sQuery(id+"F0.wireOp",EDGE,"E7.3.5"),sQuery(id+"F0.wireOp",EDGE,"E7.4.0"),sQuery(id+"F0.wireOp",EDGE,"E7.4.1"),sQuery(id+"F0.wireOp",EDGE,"E7.4.2"),sQuery(id+"F0.wireOp",EDGE,"E7.4.3"),sQuery(id+"F0.wireOp",EDGE,"E7.4.4"),sQuery(id+"F0.wireOp",EDGE,"E7.4.5"),sQuery(id+"F0.wireOp",EDGE,"E7.5.0"),sQuery(id+"F0.wireOp",EDGE,"E7.5.1"),sQuery(id+"F0.wireOp",EDGE,"E7.5.2"),sQuery(id+"F0.wireOp",EDGE,"E7.5.3"),sQuery(id+"F0.wireOp",EDGE,"E7.5.4"),sQuery(id+"F0.wireOp",EDGE,"E7.5.5"),sQuery(id+"F0.wireOp",EDGE,"E7.6.0"),sQuery(id+"F0.wireOp",EDGE,"E7.6.1"),sQuery(id+"F0.wireOp",EDGE,"E7.6.2"),sQuery(id+"F0.wireOp",EDGE,"E7.6.3"),sQuery(id+"F0.wireOp",EDGE,"E7.6.4"),sQuery(id+"F0.wireOp",EDGE,"E7.6.5"),sQuery(id+"F0.wireOp",EDGE,"E7.7.0"),sQuery(id+"F0.wireOp",EDGE,"E7.7.1"),sQuery(id+"F0.wireOp",EDGE,"E7.7.2"),sQuery(id+"F0.wireOp",EDGE,"E7.7.3"),sQuery(id+"F0.wireOp",EDGE,"E7.7.4"),sQuery(id+"F0.wireOp",EDGE,"E7.7.5"),sQuery(id+"F0.wireOp",EDGE,"E7.8.0"),sQuery(id+"F0.wireOp",EDGE,"E7.8.1"),sQuery(id+"F0.wireOp",EDGE,"E7.8.2"),sQuery(id+"F0.wireOp",EDGE,"E7.8.3"),sQuery(id+"F0.wireOp",EDGE,"E7.8.4"),sQuery(id+"F0.wireOp",EDGE,"E7.8.5"),sQuery(id+"F0.wireOp",EDGE,"E7.9.0"),sQuery(id+"F0.wireOp",EDGE,"E7.9.1"),sQuery(id+"F0.wireOp",EDGE,"E7.9.2"),sQuery(id+"F0.wireOp",EDGE,"E7.9.3"),sQuery(id+"F0.wireOp",EDGE,"E7.9.4"),sQuery(id+"F0.wireOp",EDGE,"E7.9.5"),sQuery(id+"F0.wireOp",EDGE,"E7.10.0"),sQuery(id+"F0.wireOp",EDGE,"E7.10.1"),sQuery(id+"F0.wireOp",EDGE,"E7.10.2"),sQuery(id+"F0.wireOp",EDGE,"E7.10.3"),sQuery(id+"F0.wireOp",EDGE,"E7.10.4"),sQuery(id+"F0.wireOp",EDGE,"E7.10.5"),sQuery(id+"F0.wireOp",EDGE,"E7.11.0"),sQuery(id+"F0.wireOp",EDGE,"E7.11.1"),sQuery(id+"F0.wireOp",EDGE,"E7.11.2"),sQuery(id+"F0.wireOp",EDGE,"E7.11.3"),sQuery(id+"F0.wireOp",EDGE,"E7.11.4"),sQuery(id+"F0.wireOp",EDGE,"E7.11.5"),sQuery(id+"F0.wireOp",EDGE,"E7.12.0"),sQuery(id+"F0.wireOp",EDGE,"E7.12.1"),sQuery(id+"F0.wireOp",EDGE,"E7.12.2"),sQuery(id+"F0.wireOp",EDGE,"E7.12.3"),sQuery(id+"F0.wireOp",EDGE,"E7.12.4"),sQuery(id+"F0.wireOp",EDGE,"E7.12.5"),sQuery(id+"F0.wireOp",EDGE,"E7.13.0"),sQuery(id+"F0.wireOp",EDGE,"E7.13.1"),sQuery(id+"F0.wireOp",EDGE,"E7.13.2"),sQuery(id+"F0.wireOp",EDGE,"E7.13.3"),sQuery(id+"F0.wireOp",EDGE,"E7.13.4"),sQuery(id+"F0.wireOp",EDGE,"E7.13.5"),sQuery(id+"F0.wireOp",EDGE,"E7.14.0"),sQuery(id+"F0.wireOp",EDGE,"E7.14.1"),sQuery(id+"F0.wireOp",EDGE,"E7.14.2"),sQuery(id+"F0.wireOp",EDGE,"E7.14.3"),sQuery(id+"F0.wireOp",EDGE,"E7.14.4"),sQuery(id+"F0.wireOp",EDGE,"E7.14.5"),sQuery(id+"F0.wireOp",EDGE,"E7.15.0"),sQuery(id+"F0.wireOp",EDGE,"E7.15.1"),sQuery(id+"F0.wireOp",EDGE,"E7.15.2"),sQuery(id+"F0.wireOp",EDGE,"E7.15.3"),sQuery(id+"F0.wireOp",EDGE,"E7.15.4"),sQuery(id+"F0.wireOp",EDGE,"E7.15.5"),sQuery(id+"F0.wireOp",EDGE,"E7.16.0"),sQuery(id+"F0.wireOp",EDGE,"E7.16.1"),sQuery(id+"F0.wireOp",EDGE,"E7.16.2"),sQuery(id+"F0.wireOp",EDGE,"E7.16.3"),sQuery(id+"F0.wireOp",EDGE,"E7.16.4"),sQuery(id+"F0.wireOp",EDGE,"E7.16.5"),sQuery(id+"F0.wireOp",EDGE,"E7.17.0"),sQuery(id+"F0.wireOp",EDGE,"E7.17.1"),sQuery(id+"F0.wireOp",EDGE,"E7.17.2"),sQuery(id+"F0.wireOp",EDGE,"E7.17.3"),sQuery(id+"F0.wireOp",EDGE,"E7.17.4"),sQuery(id+"F0.wireOp",EDGE,"E7.17.5"),sQuery(id+"F0.wireOp",EDGE,"E7.18.0"),sQuery(id+"F0.wireOp",EDGE,"E7.18.1"),sQuery(id+"F0.wireOp",EDGE,"E7.18.2"),sQuery(id+"F0.wireOp",EDGE,"E7.18.3"),sQuery(id+"F0.wireOp",EDGE,"E7.18.4"),sQuery(id+"F0.wireOp",EDGE,"E7.18.5"),sQuery(id+"F0.wireOp",EDGE,"E7.19.0"),sQuery(id+"F0.wireOp",EDGE,"E7.19.1"),sQuery(id+"F0.wireOp",EDGE,"E7.19.2"),sQuery(id+"F0.wireOp",EDGE,"E7.19.3"),sQuery(id+"F0.wireOp",EDGE,"E7.19.4"),sQuery(id+"F0.wireOp",EDGE,"E7.19.5"),sQuery(id+"F0.wireOp",EDGE,"E7.20.0"),sQuery(id+"F0.wireOp",EDGE,"E7.20.1"),sQuery(id+"F0.wireOp",EDGE,"E7.20.2"),sQuery(id+"F0.wireOp",EDGE,"E7.20.3"),sQuery(id+"F0.wireOp",EDGE,"E7.20.4"),sQuery(id+"F0.wireOp",EDGE,"E7.20.5"),sQuery(id+"F0.wireOp",EDGE,"E7.21.0"),sQuery(id+"F0.wireOp",EDGE,"E7.21.1"),sQuery(id+"F0.wireOp",EDGE,"E7.21.2"),sQuery(id+"F0.wireOp",EDGE,"E7.21.3"),sQuery(id+"F0.wireOp",EDGE,"E7.21.4"),sQuery(id+"F0.wireOp",EDGE,"E7.21.5"),sQuery(id+"F0.wireOp",EDGE,"E7.22.0"),sQuery(id+"F0.wireOp",EDGE,"E7.22.1"),sQuery(id+"F0.wireOp",EDGE,"E7.22.2"),sQuery(id+"F0.wireOp",EDGE,"E7.22.3"),sQuery(id+"F0.wireOp",EDGE,"E7.22.4"),sQuery(id+"F0.wireOp",EDGE,"E7.22.5"),sQuery(id+"F0.wireOp",EDGE,"E7.23.0"),sQuery(id+"F0.wireOp",EDGE,"E7.23.1"),sQuery(id+"F0.wireOp",EDGE,"E7.23.2"),sQuery(id+"F0.wireOp",EDGE,"E7.23.3"),sQuery(id+"F0.wireOp",EDGE,"E7.23.4"),sQuery(id+"F0.wireOp",EDGE,"E7.23.5"),sQuery(id+"F0.wireOp",EDGE,"E7.24.0"),sQuery(id+"F0.wireOp",EDGE,"E7.24.1"),sQuery(id+"F0.wireOp",EDGE,"E7.24.2"),sQuery(id+"F0.wireOp",EDGE,"E7.24.3"),sQuery(id+"F0.wireOp",EDGE,"E7.24.4"),sQuery(id+"F0.wireOp",EDGE,"E7.24.5"),sQuery(id+"F0.wireOp",EDGE,"E7.25.0"),sQuery(id+"F0.wireOp",EDGE,"E7.25.1"),sQuery(id+"F0.wireOp",EDGE,"E7.25.2"),sQuery(id+"F0.wireOp",EDGE,"E7.25.3"),sQuery(id+"F0.wireOp",EDGE,"E7.25.4"),sQuery(id+"F0.wireOp",EDGE,"E7.25.5"),sQuery(id+"F0.wireOp",EDGE,"E7.26.0"),sQuery(id+"F0.wireOp",EDGE,"E7.26.1"),sQuery(id+"F0.wireOp",EDGE,"E7.26.2"),sQuery(id+"F0.wireOp",EDGE,"E7.26.3"),sQuery(id+"F0.wireOp",EDGE,"E7.26.4"),sQuery(id+"F0.wireOp",EDGE,"E7.26.5"),sQuery(id+"F0.wireOp",EDGE,"E7.27.0"),sQuery(id+"F0.wireOp",EDGE,"E7.27.1"),sQuery(id+"F0.wireOp",EDGE,"E7.27.2"),sQuery(id+"F0.wireOp",EDGE,"E7.27.3"),sQuery(id+"F0.wireOp",EDGE,"E7.27.4"),sQuery(id+"F0.wireOp",EDGE,"E7.27.5"),sQuery(id+"F0.wireOp",EDGE,"E7.28.0"),sQuery(id+"F0.wireOp",EDGE,"E7.28.1"),sQuery(id+"F0.wireOp",EDGE,"E7.28.2"),sQuery(id+"F0.wireOp",EDGE,"E7.28.3"),sQuery(id+"F0.wireOp",EDGE,"E7.28.4"),sQuery(id+"F0.wireOp",EDGE,"E7.28.5"),sQuery(id+"F0.wireOp",EDGE,"E7.29.0"),sQuery(id+"F0.wireOp",EDGE,"E7.29.1"),sQuery(id+"F0.wireOp",EDGE,"E7.29.2"),sQuery(id+"F0.wireOp",EDGE,"E7.29.3"),sQuery(id+"F0.wireOp",EDGE,"E7.29.4"),sQuery(id+"F0.wireOp",EDGE,"E7.29.5"),sQuery(id+"F0.wireOp",EDGE,"E7.30.0"),sQuery(id+"F0.wireOp",EDGE,"E7.30.1"),sQuery(id+"F0.wireOp",EDGE,"E7.30.2"),sQuery(id+"F0.wireOp",EDGE,"E7.30.3"),sQuery(id+"F0.wireOp",EDGE,"E7.30.4"),sQuery(id+"F0.wireOp",EDGE,"E7.30.5"),subQ0,sQuery(id+"F0.wireOp",EDGE,"E7.31.1"),sQuery(id+"F0.wireOp",EDGE,"E7.31.2"),sQuery(id+"F0.wireOp",EDGE,"E7.31.3"),sQuery(id+"F0.wireOp",EDGE,"E7.31.4"),sQuery(id+"F0.wireOp",EDGE,"E7.31.5"),sQuery(id+"F0.wireOp",EDGE,"E7.32.0"),sQuery(id+"F0.wireOp",EDGE,"E7.32.1"),sQuery(id+"F0.wireOp",EDGE,"E7.32.2"),sQuery(id+"F0.wireOp",EDGE,"E7.32.3"),sQuery(id+"F0.wireOp",EDGE,"E7.32.4"),sQuery(id+"F0.wireOp",EDGE,"E7.32.5"),sQuery(id+"F0.wireOp",EDGE,"E7.33.0"),sQuery(id+"F0.wireOp",EDGE,"E7.33.1"),sQuery(id+"F0.wireOp",EDGE,"E7.33.2"),sQuery(id+"F0.wireOp",EDGE,"E7.33.3"),sQuery(id+"F0.wireOp",EDGE,"E7.33.4"),sQuery(id+"F0.wireOp",EDGE,"E7.33.5"),sQuery(id+"F0.wireOp",EDGE,"E7.34.0"),sQuery(id+"F0.wireOp",EDGE,"E7.34.1"),sQuery(id+"F0.wireOp",EDGE,"E7.34.2"),sQuery(id+"F0.wireOp",EDGE,"E7.34.3"),sQuery(id+"F0.wireOp",EDGE,"E7.34.4"),sQuery(id+"F0.wireOp",EDGE,"E7.34.5"),sQuery(id+"F0.wireOp",EDGE,"E7.35.0"),sQuery(id+"F0.wireOp",EDGE,"E7.35.1"),sQuery(id+"F0.wireOp",EDGE,"E7.35.2"),sQuery(id+"F0.wireOp",EDGE,"E7.35.3"),sQuery(id+"F0.wireOp",EDGE,"E7.35.4"),sQuery(id+"F0.wireOp",EDGE,"E7.35.5"),sQuery(id+"F0.wireOp",EDGE,"E7.36.0"),sQuery(id+"F0.wireOp",EDGE,"E7.36.1"),sQuery(id+"F0.wireOp",EDGE,"E7.36.2"),sQuery(id+"F0.wireOp",EDGE,"E7.36.3"),sQuery(id+"F0.wireOp",EDGE,"E7.36.4"),sQuery(id+"F0.wireOp",EDGE,"E7.36.5"),sQuery(id+"F0.wireOp",EDGE,"E7.37.0"),sQuery(id+"F0.wireOp",EDGE,"E7.37.1"),sQuery(id+"F0.wireOp",EDGE,"E7.37.2"),sQuery(id+"F0.wireOp",EDGE,"E7.37.3"),sQuery(id+"F0.wireOp",EDGE,"E7.37.4"),sQuery(id+"F0.wireOp",EDGE,"E7.37.5"),sQuery(id+"F0.wireOp",EDGE,"E7.38.0"),sQuery(id+"F0.wireOp",EDGE,"E7.38.1"),sQuery(id+"F0.wireOp",EDGE,"E7.38.2"),sQuery(id+"F0.wireOp",EDGE,"E7.38.3"),sQuery(id+"F0.wireOp",EDGE,"E7.38.4"),sQuery(id+"F0.wireOp",EDGE,"E7.38.5"),sQuery(id+"F0.wireOp",EDGE,"E7.39.0"),sQuery(id+"F0.wireOp",EDGE,"E7.39.1"),sQuery(id+"F0.wireOp",EDGE,"E7.39.2"),sQuery(id+"F0.wireOp",EDGE,"E7.39.3"),sQuery(id+"F0.wireOp",EDGE,"E7.39.4"),sQuery(id+"F0.wireOp",EDGE,"E7.39.5"),sQuery(id+"F0.wireOp",EDGE,"E7.40.0"),sQuery(id+"F0.wireOp",EDGE,"E7.40.1"),sQuery(id+"F0.wireOp",EDGE,"E7.40.2"),sQuery(id+"F0.wireOp",EDGE,"E7.40.3"),sQuery(id+"F0.wireOp",EDGE,"E7.40.4"),sQuery(id+"F0.wireOp",EDGE,"E7.40.5"),sQuery(id+"F0.wireOp",EDGE,"E7.41.0"),sQuery(id+"F0.wireOp",EDGE,"E7.41.1"),sQuery(id+"F0.wireOp",EDGE,"E7.41.2"),sQuery(id+"F0.wireOp",EDGE,"E7.41.3"),sQuery(id+"F0.wireOp",EDGE,"E7.41.4"),sQuery(id+"F0.wireOp",EDGE,"E7.41.5"),sQuery(id+"F0.wireOp",EDGE,"E7.42.0"),sQuery(id+"F0.wireOp",EDGE,"E7.42.1"),sQuery(id+"F0.wireOp",EDGE,"E7.42.2"),sQuery(id+"F0.wireOp",EDGE,"E7.42.3"),sQuery(id+"F0.wireOp",EDGE,"E7.42.4"),sQuery(id+"F0.wireOp",EDGE,"E7.42.5"),sQuery(id+"F0.wireOp",EDGE,"E7.43.0"),sQuery(id+"F0.wireOp",EDGE,"E7.43.1"),sQuery(id+"F0.wireOp",EDGE,"E7.43.2"),sQuery(id+"F0.wireOp",EDGE,"E7.43.3"),sQuery(id+"F0.wireOp",EDGE,"E7.43.4"),sQuery(id+"F0.wireOp",EDGE,"E7.43.5")])],"isStart":false})]});}
            var Q7;
            {var subQ0=sQuery(id+"F0.wireOp",EDGE,"E7.29.0");Q7=makeQuery(id+"F2.opChamfer","BLEND_EDGE",EDGE,{"blendedFrom":[makeQuery(id+"F1.opExtrude","CAP_EDGE",EDGE,{"disambiguationData":[OSD([subQ0])],"isStart":false}),makeQuery(id+"F1.opExtrude","CAP_FACE",FACE,{"disambiguationData":[OSD([sQuery(id+"F0.wireOp",EDGE,"E1"),sQuery(id+"F0.wireOp",EDGE,"E2"),sQuery(id+"F0.wireOp",EDGE,"E3"),sQuery(id+"F0.wireOp",EDGE,"E4"),sQuery(id+"F0.wireOp",EDGE,"E5"),sQuery(id+"F0.wireOp",EDGE,"E6"),sQuery(id+"F0.wireOp",EDGE,"E7.1.0"),sQuery(id+"F0.wireOp",EDGE,"E7.1.1"),sQuery(id+"F0.wireOp",EDGE,"E7.1.2"),sQuery(id+"F0.wireOp",EDGE,"E7.1.3"),sQuery(id+"F0.wireOp",EDGE,"E7.1.4"),sQuery(id+"F0.wireOp",EDGE,"E7.1.5"),sQuery(id+"F0.wireOp",EDGE,"E7.2.0"),sQuery(id+"F0.wireOp",EDGE,"E7.2.1"),sQuery(id+"F0.wireOp",EDGE,"E7.2.2"),sQuery(id+"F0.wireOp",EDGE,"E7.2.3"),sQuery(id+"F0.wireOp",EDGE,"E7.2.4"),sQuery(id+"F0.wireOp",EDGE,"E7.2.5"),sQuery(id+"F0.wireOp",EDGE,"E7.3.0"),sQuery(id+"F0.wireOp",EDGE,"E7.3.1"),sQuery(id+"F0.wireOp",EDGE,"E7.3.2"),sQuery(id+"F0.wireOp",EDGE,"E7.3.3"),sQuery(id+"F0.wireOp",EDGE,"E7.3.4"),sQuery(id+"F0.wireOp",EDGE,"E7.3.5"),sQuery(id+"F0.wireOp",EDGE,"E7.4.0"),sQuery(id+"F0.wireOp",EDGE,"E7.4.1"),sQuery(id+"F0.wireOp",EDGE,"E7.4.2"),sQuery(id+"F0.wireOp",EDGE,"E7.4.3"),sQuery(id+"F0.wireOp",EDGE,"E7.4.4"),sQuery(id+"F0.wireOp",EDGE,"E7.4.5"),sQuery(id+"F0.wireOp",EDGE,"E7.5.0"),sQuery(id+"F0.wireOp",EDGE,"E7.5.1"),sQuery(id+"F0.wireOp",EDGE,"E7.5.2"),sQuery(id+"F0.wireOp",EDGE,"E7.5.3"),sQuery(id+"F0.wireOp",EDGE,"E7.5.4"),sQuery(id+"F0.wireOp",EDGE,"E7.5.5"),sQuery(id+"F0.wireOp",EDGE,"E7.6.0"),sQuery(id+"F0.wireOp",EDGE,"E7.6.1"),sQuery(id+"F0.wireOp",EDGE,"E7.6.2"),sQuery(id+"F0.wireOp",EDGE,"E7.6.3"),sQuery(id+"F0.wireOp",EDGE,"E7.6.4"),sQuery(id+"F0.wireOp",EDGE,"E7.6.5"),sQuery(id+"F0.wireOp",EDGE,"E7.7.0"),sQuery(id+"F0.wireOp",EDGE,"E7.7.1"),sQuery(id+"F0.wireOp",EDGE,"E7.7.2"),sQuery(id+"F0.wireOp",EDGE,"E7.7.3"),sQuery(id+"F0.wireOp",EDGE,"E7.7.4"),sQuery(id+"F0.wireOp",EDGE,"E7.7.5"),sQuery(id+"F0.wireOp",EDGE,"E7.8.0"),sQuery(id+"F0.wireOp",EDGE,"E7.8.1"),sQuery(id+"F0.wireOp",EDGE,"E7.8.2"),sQuery(id+"F0.wireOp",EDGE,"E7.8.3"),sQuery(id+"F0.wireOp",EDGE,"E7.8.4"),sQuery(id+"F0.wireOp",EDGE,"E7.8.5"),sQuery(id+"F0.wireOp",EDGE,"E7.9.0"),sQuery(id+"F0.wireOp",EDGE,"E7.9.1"),sQuery(id+"F0.wireOp",EDGE,"E7.9.2"),sQuery(id+"F0.wireOp",EDGE,"E7.9.3"),sQuery(id+"F0.wireOp",EDGE,"E7.9.4"),sQuery(id+"F0.wireOp",EDGE,"E7.9.5"),sQuery(id+"F0.wireOp",EDGE,"E7.10.0"),sQuery(id+"F0.wireOp",EDGE,"E7.10.1"),sQuery(id+"F0.wireOp",EDGE,"E7.10.2"),sQuery(id+"F0.wireOp",EDGE,"E7.10.3"),sQuery(id+"F0.wireOp",EDGE,"E7.10.4"),sQuery(id+"F0.wireOp",EDGE,"E7.10.5"),sQuery(id+"F0.wireOp",EDGE,"E7.11.0"),sQuery(id+"F0.wireOp",EDGE,"E7.11.1"),sQuery(id+"F0.wireOp",EDGE,"E7.11.2"),sQuery(id+"F0.wireOp",EDGE,"E7.11.3"),sQuery(id+"F0.wireOp",EDGE,"E7.11.4"),sQuery(id+"F0.wireOp",EDGE,"E7.11.5"),sQuery(id+"F0.wireOp",EDGE,"E7.12.0"),sQuery(id+"F0.wireOp",EDGE,"E7.12.1"),sQuery(id+"F0.wireOp",EDGE,"E7.12.2"),sQuery(id+"F0.wireOp",EDGE,"E7.12.3"),sQuery(id+"F0.wireOp",EDGE,"E7.12.4"),sQuery(id+"F0.wireOp",EDGE,"E7.12.5"),sQuery(id+"F0.wireOp",EDGE,"E7.13.0"),sQuery(id+"F0.wireOp",EDGE,"E7.13.1"),sQuery(id+"F0.wireOp",EDGE,"E7.13.2"),sQuery(id+"F0.wireOp",EDGE,"E7.13.3"),sQuery(id+"F0.wireOp",EDGE,"E7.13.4"),sQuery(id+"F0.wireOp",EDGE,"E7.13.5"),sQuery(id+"F0.wireOp",EDGE,"E7.14.0"),sQuery(id+"F0.wireOp",EDGE,"E7.14.1"),sQuery(id+"F0.wireOp",EDGE,"E7.14.2"),sQuery(id+"F0.wireOp",EDGE,"E7.14.3"),sQuery(id+"F0.wireOp",EDGE,"E7.14.4"),sQuery(id+"F0.wireOp",EDGE,"E7.14.5"),sQuery(id+"F0.wireOp",EDGE,"E7.15.0"),sQuery(id+"F0.wireOp",EDGE,"E7.15.1"),sQuery(id+"F0.wireOp",EDGE,"E7.15.2"),sQuery(id+"F0.wireOp",EDGE,"E7.15.3"),sQuery(id+"F0.wireOp",EDGE,"E7.15.4"),sQuery(id+"F0.wireOp",EDGE,"E7.15.5"),sQuery(id+"F0.wireOp",EDGE,"E7.16.0"),sQuery(id+"F0.wireOp",EDGE,"E7.16.1"),sQuery(id+"F0.wireOp",EDGE,"E7.16.2"),sQuery(id+"F0.wireOp",EDGE,"E7.16.3"),sQuery(id+"F0.wireOp",EDGE,"E7.16.4"),sQuery(id+"F0.wireOp",EDGE,"E7.16.5"),sQuery(id+"F0.wireOp",EDGE,"E7.17.0"),sQuery(id+"F0.wireOp",EDGE,"E7.17.1"),sQuery(id+"F0.wireOp",EDGE,"E7.17.2"),sQuery(id+"F0.wireOp",EDGE,"E7.17.3"),sQuery(id+"F0.wireOp",EDGE,"E7.17.4"),sQuery(id+"F0.wireOp",EDGE,"E7.17.5"),sQuery(id+"F0.wireOp",EDGE,"E7.18.0"),sQuery(id+"F0.wireOp",EDGE,"E7.18.1"),sQuery(id+"F0.wireOp",EDGE,"E7.18.2"),sQuery(id+"F0.wireOp",EDGE,"E7.18.3"),sQuery(id+"F0.wireOp",EDGE,"E7.18.4"),sQuery(id+"F0.wireOp",EDGE,"E7.18.5"),sQuery(id+"F0.wireOp",EDGE,"E7.19.0"),sQuery(id+"F0.wireOp",EDGE,"E7.19.1"),sQuery(id+"F0.wireOp",EDGE,"E7.19.2"),sQuery(id+"F0.wireOp",EDGE,"E7.19.3"),sQuery(id+"F0.wireOp",EDGE,"E7.19.4"),sQuery(id+"F0.wireOp",EDGE,"E7.19.5"),sQuery(id+"F0.wireOp",EDGE,"E7.20.0"),sQuery(id+"F0.wireOp",EDGE,"E7.20.1"),sQuery(id+"F0.wireOp",EDGE,"E7.20.2"),sQuery(id+"F0.wireOp",EDGE,"E7.20.3"),sQuery(id+"F0.wireOp",EDGE,"E7.20.4"),sQuery(id+"F0.wireOp",EDGE,"E7.20.5"),sQuery(id+"F0.wireOp",EDGE,"E7.21.0"),sQuery(id+"F0.wireOp",EDGE,"E7.21.1"),sQuery(id+"F0.wireOp",EDGE,"E7.21.2"),sQuery(id+"F0.wireOp",EDGE,"E7.21.3"),sQuery(id+"F0.wireOp",EDGE,"E7.21.4"),sQuery(id+"F0.wireOp",EDGE,"E7.21.5"),sQuery(id+"F0.wireOp",EDGE,"E7.22.0"),sQuery(id+"F0.wireOp",EDGE,"E7.22.1"),sQuery(id+"F0.wireOp",EDGE,"E7.22.2"),sQuery(id+"F0.wireOp",EDGE,"E7.22.3"),sQuery(id+"F0.wireOp",EDGE,"E7.22.4"),sQuery(id+"F0.wireOp",EDGE,"E7.22.5"),sQuery(id+"F0.wireOp",EDGE,"E7.23.0"),sQuery(id+"F0.wireOp",EDGE,"E7.23.1"),sQuery(id+"F0.wireOp",EDGE,"E7.23.2"),sQuery(id+"F0.wireOp",EDGE,"E7.23.3"),sQuery(id+"F0.wireOp",EDGE,"E7.23.4"),sQuery(id+"F0.wireOp",EDGE,"E7.23.5"),sQuery(id+"F0.wireOp",EDGE,"E7.24.0"),sQuery(id+"F0.wireOp",EDGE,"E7.24.1"),sQuery(id+"F0.wireOp",EDGE,"E7.24.2"),sQuery(id+"F0.wireOp",EDGE,"E7.24.3"),sQuery(id+"F0.wireOp",EDGE,"E7.24.4"),sQuery(id+"F0.wireOp",EDGE,"E7.24.5"),sQuery(id+"F0.wireOp",EDGE,"E7.25.0"),sQuery(id+"F0.wireOp",EDGE,"E7.25.1"),sQuery(id+"F0.wireOp",EDGE,"E7.25.2"),sQuery(id+"F0.wireOp",EDGE,"E7.25.3"),sQuery(id+"F0.wireOp",EDGE,"E7.25.4"),sQuery(id+"F0.wireOp",EDGE,"E7.25.5"),sQuery(id+"F0.wireOp",EDGE,"E7.26.0"),sQuery(id+"F0.wireOp",EDGE,"E7.26.1"),sQuery(id+"F0.wireOp",EDGE,"E7.26.2"),sQuery(id+"F0.wireOp",EDGE,"E7.26.3"),sQuery(id+"F0.wireOp",EDGE,"E7.26.4"),sQuery(id+"F0.wireOp",EDGE,"E7.26.5"),sQuery(id+"F0.wireOp",EDGE,"E7.27.0"),sQuery(id+"F0.wireOp",EDGE,"E7.27.1"),sQuery(id+"F0.wireOp",EDGE,"E7.27.2"),sQuery(id+"F0.wireOp",EDGE,"E7.27.3"),sQuery(id+"F0.wireOp",EDGE,"E7.27.4"),sQuery(id+"F0.wireOp",EDGE,"E7.27.5"),sQuery(id+"F0.wireOp",EDGE,"E7.28.0"),sQuery(id+"F0.wireOp",EDGE,"E7.28.1"),sQuery(id+"F0.wireOp",EDGE,"E7.28.2"),sQuery(id+"F0.wireOp",EDGE,"E7.28.3"),sQuery(id+"F0.wireOp",EDGE,"E7.28.4"),sQuery(id+"F0.wireOp",EDGE,"E7.28.5"),subQ0,sQuery(id+"F0.wireOp",EDGE,"E7.29.1"),sQuery(id+"F0.wireOp",EDGE,"E7.29.2"),sQuery(id+"F0.wireOp",EDGE,"E7.29.3"),sQuery(id+"F0.wireOp",EDGE,"E7.29.4"),sQuery(id+"F0.wireOp",EDGE,"E7.29.5"),sQuery(id+"F0.wireOp",EDGE,"E7.30.0"),sQuery(id+"F0.wireOp",EDGE,"E7.30.1"),sQuery(id+"F0.wireOp",EDGE,"E7.30.2"),sQuery(id+"F0.wireOp",EDGE,"E7.30.3"),sQuery(id+"F0.wireOp",EDGE,"E7.30.4"),sQuery(id+"F0.wireOp",EDGE,"E7.30.5"),sQuery(id+"F0.wireOp",EDGE,"E7.31.0"),sQuery(id+"F0.wireOp",EDGE,"E7.31.1"),sQuery(id+"F0.wireOp",EDGE,"E7.31.2"),sQuery(id+"F0.wireOp",EDGE,"E7.31.3"),sQuery(id+"F0.wireOp",EDGE,"E7.31.4"),sQuery(id+"F0.wireOp",EDGE,"E7.31.5"),sQuery(id+"F0.wireOp",EDGE,"E7.32.0"),sQuery(id+"F0.wireOp",EDGE,"E7.32.1"),sQuery(id+"F0.wireOp",EDGE,"E7.32.2"),sQuery(id+"F0.wireOp",EDGE,"E7.32.3"),sQuery(id+"F0.wireOp",EDGE,"E7.32.4"),sQuery(id+"F0.wireOp",EDGE,"E7.32.5"),sQuery(id+"F0.wireOp",EDGE,"E7.33.0"),sQuery(id+"F0.wireOp",EDGE,"E7.33.1"),sQuery(id+"F0.wireOp",EDGE,"E7.33.2"),sQuery(id+"F0.wireOp",EDGE,"E7.33.3"),sQuery(id+"F0.wireOp",EDGE,"E7.33.4"),sQuery(id+"F0.wireOp",EDGE,"E7.33.5"),sQuery(id+"F0.wireOp",EDGE,"E7.34.0"),sQuery(id+"F0.wireOp",EDGE,"E7.34.1"),sQuery(id+"F0.wireOp",EDGE,"E7.34.2"),sQuery(id+"F0.wireOp",EDGE,"E7.34.3"),sQuery(id+"F0.wireOp",EDGE,"E7.34.4"),sQuery(id+"F0.wireOp",EDGE,"E7.34.5"),sQuery(id+"F0.wireOp",EDGE,"E7.35.0"),sQuery(id+"F0.wireOp",EDGE,"E7.35.1"),sQuery(id+"F0.wireOp",EDGE,"E7.35.2"),sQuery(id+"F0.wireOp",EDGE,"E7.35.3"),sQuery(id+"F0.wireOp",EDGE,"E7.35.4"),sQuery(id+"F0.wireOp",EDGE,"E7.35.5"),sQuery(id+"F0.wireOp",EDGE,"E7.36.0"),sQuery(id+"F0.wireOp",EDGE,"E7.36.1"),sQuery(id+"F0.wireOp",EDGE,"E7.36.2"),sQuery(id+"F0.wireOp",EDGE,"E7.36.3"),sQuery(id+"F0.wireOp",EDGE,"E7.36.4"),sQuery(id+"F0.wireOp",EDGE,"E7.36.5"),sQuery(id+"F0.wireOp",EDGE,"E7.37.0"),sQuery(id+"F0.wireOp",EDGE,"E7.37.1"),sQuery(id+"F0.wireOp",EDGE,"E7.37.2"),sQuery(id+"F0.wireOp",EDGE,"E7.37.3"),sQuery(id+"F0.wireOp",EDGE,"E7.37.4"),sQuery(id+"F0.wireOp",EDGE,"E7.37.5"),sQuery(id+"F0.wireOp",EDGE,"E7.38.0"),sQuery(id+"F0.wireOp",EDGE,"E7.38.1"),sQuery(id+"F0.wireOp",EDGE,"E7.38.2"),sQuery(id+"F0.wireOp",EDGE,"E7.38.3"),sQuery(id+"F0.wireOp",EDGE,"E7.38.4"),sQuery(id+"F0.wireOp",EDGE,"E7.38.5"),sQuery(id+"F0.wireOp",EDGE,"E7.39.0"),sQuery(id+"F0.wireOp",EDGE,"E7.39.1"),sQuery(id+"F0.wireOp",EDGE,"E7.39.2"),sQuery(id+"F0.wireOp",EDGE,"E7.39.3"),sQuery(id+"F0.wireOp",EDGE,"E7.39.4"),sQuery(id+"F0.wireOp",EDGE,"E7.39.5"),sQuery(id+"F0.wireOp",EDGE,"E7.40.0"),sQuery(id+"F0.wireOp",EDGE,"E7.40.1"),sQuery(id+"F0.wireOp",EDGE,"E7.40.2"),sQuery(id+"F0.wireOp",EDGE,"E7.40.3"),sQuery(id+"F0.wireOp",EDGE,"E7.40.4"),sQuery(id+"F0.wireOp",EDGE,"E7.40.5"),sQuery(id+"F0.wireOp",EDGE,"E7.41.0"),sQuery(id+"F0.wireOp",EDGE,"E7.41.1"),sQuery(id+"F0.wireOp",EDGE,"E7.41.2"),sQuery(id+"F0.wireOp",EDGE,"E7.41.3"),sQuery(id+"F0.wireOp",EDGE,"E7.41.4"),sQuery(id+"F0.wireOp",EDGE,"E7.41.5"),sQuery(id+"F0.wireOp",EDGE,"E7.42.0"),sQuery(id+"F0.wireOp",EDGE,"E7.42.1"),sQuery(id+"F0.wireOp",EDGE,"E7.42.2"),sQuery(id+"F0.wireOp",EDGE,"E7.42.3"),sQuery(id+"F0.wireOp",EDGE,"E7.42.4"),sQuery(id+"F0.wireOp",EDGE,"E7.42.5"),sQuery(id+"F0.wireOp",EDGE,"E7.43.0"),sQuery(id+"F0.wireOp",EDGE,"E7.43.1"),sQuery(id+"F0.wireOp",EDGE,"E7.43.2"),sQuery(id+"F0.wireOp",EDGE,"E7.43.3"),sQuery(id+"F0.wireOp",EDGE,"E7.43.4"),sQuery(id+"F0.wireOp",EDGE,"E7.43.5")])],"isStart":false})],"blendedInto":[makeQuery(id+"F1.opExtrude","CAP_FACE",FACE,{"disambiguationData":[OSD([sQuery(id+"F0.wireOp",EDGE,"E1"),sQuery(id+"F0.wireOp",EDGE,"E2"),sQuery(id+"F0.wireOp",EDGE,"E3"),sQuery(id+"F0.wireOp",EDGE,"E4"),sQuery(id+"F0.wireOp",EDGE,"E5"),sQuery(id+"F0.wireOp",EDGE,"E6"),sQuery(id+"F0.wireOp",EDGE,"E7.1.0"),sQuery(id+"F0.wireOp",EDGE,"E7.1.1"),sQuery(id+"F0.wireOp",EDGE,"E7.1.2"),sQuery(id+"F0.wireOp",EDGE,"E7.1.3"),sQuery(id+"F0.wireOp",EDGE,"E7.1.4"),sQuery(id+"F0.wireOp",EDGE,"E7.1.5"),sQuery(id+"F0.wireOp",EDGE,"E7.2.0"),sQuery(id+"F0.wireOp",EDGE,"E7.2.1"),sQuery(id+"F0.wireOp",EDGE,"E7.2.2"),sQuery(id+"F0.wireOp",EDGE,"E7.2.3"),sQuery(id+"F0.wireOp",EDGE,"E7.2.4"),sQuery(id+"F0.wireOp",EDGE,"E7.2.5"),sQuery(id+"F0.wireOp",EDGE,"E7.3.0"),sQuery(id+"F0.wireOp",EDGE,"E7.3.1"),sQuery(id+"F0.wireOp",EDGE,"E7.3.2"),sQuery(id+"F0.wireOp",EDGE,"E7.3.3"),sQuery(id+"F0.wireOp",EDGE,"E7.3.4"),sQuery(id+"F0.wireOp",EDGE,"E7.3.5"),sQuery(id+"F0.wireOp",EDGE,"E7.4.0"),sQuery(id+"F0.wireOp",EDGE,"E7.4.1"),sQuery(id+"F0.wireOp",EDGE,"E7.4.2"),sQuery(id+"F0.wireOp",EDGE,"E7.4.3"),sQuery(id+"F0.wireOp",EDGE,"E7.4.4"),sQuery(id+"F0.wireOp",EDGE,"E7.4.5"),sQuery(id+"F0.wireOp",EDGE,"E7.5.0"),sQuery(id+"F0.wireOp",EDGE,"E7.5.1"),sQuery(id+"F0.wireOp",EDGE,"E7.5.2"),sQuery(id+"F0.wireOp",EDGE,"E7.5.3"),sQuery(id+"F0.wireOp",EDGE,"E7.5.4"),sQuery(id+"F0.wireOp",EDGE,"E7.5.5"),sQuery(id+"F0.wireOp",EDGE,"E7.6.0"),sQuery(id+"F0.wireOp",EDGE,"E7.6.1"),sQuery(id+"F0.wireOp",EDGE,"E7.6.2"),sQuery(id+"F0.wireOp",EDGE,"E7.6.3"),sQuery(id+"F0.wireOp",EDGE,"E7.6.4"),sQuery(id+"F0.wireOp",EDGE,"E7.6.5"),sQuery(id+"F0.wireOp",EDGE,"E7.7.0"),sQuery(id+"F0.wireOp",EDGE,"E7.7.1"),sQuery(id+"F0.wireOp",EDGE,"E7.7.2"),sQuery(id+"F0.wireOp",EDGE,"E7.7.3"),sQuery(id+"F0.wireOp",EDGE,"E7.7.4"),sQuery(id+"F0.wireOp",EDGE,"E7.7.5"),sQuery(id+"F0.wireOp",EDGE,"E7.8.0"),sQuery(id+"F0.wireOp",EDGE,"E7.8.1"),sQuery(id+"F0.wireOp",EDGE,"E7.8.2"),sQuery(id+"F0.wireOp",EDGE,"E7.8.3"),sQuery(id+"F0.wireOp",EDGE,"E7.8.4"),sQuery(id+"F0.wireOp",EDGE,"E7.8.5"),sQuery(id+"F0.wireOp",EDGE,"E7.9.0"),sQuery(id+"F0.wireOp",EDGE,"E7.9.1"),sQuery(id+"F0.wireOp",EDGE,"E7.9.2"),sQuery(id+"F0.wireOp",EDGE,"E7.9.3"),sQuery(id+"F0.wireOp",EDGE,"E7.9.4"),sQuery(id+"F0.wireOp",EDGE,"E7.9.5"),sQuery(id+"F0.wireOp",EDGE,"E7.10.0"),sQuery(id+"F0.wireOp",EDGE,"E7.10.1"),sQuery(id+"F0.wireOp",EDGE,"E7.10.2"),sQuery(id+"F0.wireOp",EDGE,"E7.10.3"),sQuery(id+"F0.wireOp",EDGE,"E7.10.4"),sQuery(id+"F0.wireOp",EDGE,"E7.10.5"),sQuery(id+"F0.wireOp",EDGE,"E7.11.0"),sQuery(id+"F0.wireOp",EDGE,"E7.11.1"),sQuery(id+"F0.wireOp",EDGE,"E7.11.2"),sQuery(id+"F0.wireOp",EDGE,"E7.11.3"),sQuery(id+"F0.wireOp",EDGE,"E7.11.4"),sQuery(id+"F0.wireOp",EDGE,"E7.11.5"),sQuery(id+"F0.wireOp",EDGE,"E7.12.0"),sQuery(id+"F0.wireOp",EDGE,"E7.12.1"),sQuery(id+"F0.wireOp",EDGE,"E7.12.2"),sQuery(id+"F0.wireOp",EDGE,"E7.12.3"),sQuery(id+"F0.wireOp",EDGE,"E7.12.4"),sQuery(id+"F0.wireOp",EDGE,"E7.12.5"),sQuery(id+"F0.wireOp",EDGE,"E7.13.0"),sQuery(id+"F0.wireOp",EDGE,"E7.13.1"),sQuery(id+"F0.wireOp",EDGE,"E7.13.2"),sQuery(id+"F0.wireOp",EDGE,"E7.13.3"),sQuery(id+"F0.wireOp",EDGE,"E7.13.4"),sQuery(id+"F0.wireOp",EDGE,"E7.13.5"),sQuery(id+"F0.wireOp",EDGE,"E7.14.0"),sQuery(id+"F0.wireOp",EDGE,"E7.14.1"),sQuery(id+"F0.wireOp",EDGE,"E7.14.2"),sQuery(id+"F0.wireOp",EDGE,"E7.14.3"),sQuery(id+"F0.wireOp",EDGE,"E7.14.4"),sQuery(id+"F0.wireOp",EDGE,"E7.14.5"),sQuery(id+"F0.wireOp",EDGE,"E7.15.0"),sQuery(id+"F0.wireOp",EDGE,"E7.15.1"),sQuery(id+"F0.wireOp",EDGE,"E7.15.2"),sQuery(id+"F0.wireOp",EDGE,"E7.15.3"),sQuery(id+"F0.wireOp",EDGE,"E7.15.4"),sQuery(id+"F0.wireOp",EDGE,"E7.15.5"),sQuery(id+"F0.wireOp",EDGE,"E7.16.0"),sQuery(id+"F0.wireOp",EDGE,"E7.16.1"),sQuery(id+"F0.wireOp",EDGE,"E7.16.2"),sQuery(id+"F0.wireOp",EDGE,"E7.16.3"),sQuery(id+"F0.wireOp",EDGE,"E7.16.4"),sQuery(id+"F0.wireOp",EDGE,"E7.16.5"),sQuery(id+"F0.wireOp",EDGE,"E7.17.0"),sQuery(id+"F0.wireOp",EDGE,"E7.17.1"),sQuery(id+"F0.wireOp",EDGE,"E7.17.2"),sQuery(id+"F0.wireOp",EDGE,"E7.17.3"),sQuery(id+"F0.wireOp",EDGE,"E7.17.4"),sQuery(id+"F0.wireOp",EDGE,"E7.17.5"),sQuery(id+"F0.wireOp",EDGE,"E7.18.0"),sQuery(id+"F0.wireOp",EDGE,"E7.18.1"),sQuery(id+"F0.wireOp",EDGE,"E7.18.2"),sQuery(id+"F0.wireOp",EDGE,"E7.18.3"),sQuery(id+"F0.wireOp",EDGE,"E7.18.4"),sQuery(id+"F0.wireOp",EDGE,"E7.18.5"),sQuery(id+"F0.wireOp",EDGE,"E7.19.0"),sQuery(id+"F0.wireOp",EDGE,"E7.19.1"),sQuery(id+"F0.wireOp",EDGE,"E7.19.2"),sQuery(id+"F0.wireOp",EDGE,"E7.19.3"),sQuery(id+"F0.wireOp",EDGE,"E7.19.4"),sQuery(id+"F0.wireOp",EDGE,"E7.19.5"),sQuery(id+"F0.wireOp",EDGE,"E7.20.0"),sQuery(id+"F0.wireOp",EDGE,"E7.20.1"),sQuery(id+"F0.wireOp",EDGE,"E7.20.2"),sQuery(id+"F0.wireOp",EDGE,"E7.20.3"),sQuery(id+"F0.wireOp",EDGE,"E7.20.4"),sQuery(id+"F0.wireOp",EDGE,"E7.20.5"),sQuery(id+"F0.wireOp",EDGE,"E7.21.0"),sQuery(id+"F0.wireOp",EDGE,"E7.21.1"),sQuery(id+"F0.wireOp",EDGE,"E7.21.2"),sQuery(id+"F0.wireOp",EDGE,"E7.21.3"),sQuery(id+"F0.wireOp",EDGE,"E7.21.4"),sQuery(id+"F0.wireOp",EDGE,"E7.21.5"),sQuery(id+"F0.wireOp",EDGE,"E7.22.0"),sQuery(id+"F0.wireOp",EDGE,"E7.22.1"),sQuery(id+"F0.wireOp",EDGE,"E7.22.2"),sQuery(id+"F0.wireOp",EDGE,"E7.22.3"),sQuery(id+"F0.wireOp",EDGE,"E7.22.4"),sQuery(id+"F0.wireOp",EDGE,"E7.22.5"),sQuery(id+"F0.wireOp",EDGE,"E7.23.0"),sQuery(id+"F0.wireOp",EDGE,"E7.23.1"),sQuery(id+"F0.wireOp",EDGE,"E7.23.2"),sQuery(id+"F0.wireOp",EDGE,"E7.23.3"),sQuery(id+"F0.wireOp",EDGE,"E7.23.4"),sQuery(id+"F0.wireOp",EDGE,"E7.23.5"),sQuery(id+"F0.wireOp",EDGE,"E7.24.0"),sQuery(id+"F0.wireOp",EDGE,"E7.24.1"),sQuery(id+"F0.wireOp",EDGE,"E7.24.2"),sQuery(id+"F0.wireOp",EDGE,"E7.24.3"),sQuery(id+"F0.wireOp",EDGE,"E7.24.4"),sQuery(id+"F0.wireOp",EDGE,"E7.24.5"),sQuery(id+"F0.wireOp",EDGE,"E7.25.0"),sQuery(id+"F0.wireOp",EDGE,"E7.25.1"),sQuery(id+"F0.wireOp",EDGE,"E7.25.2"),sQuery(id+"F0.wireOp",EDGE,"E7.25.3"),sQuery(id+"F0.wireOp",EDGE,"E7.25.4"),sQuery(id+"F0.wireOp",EDGE,"E7.25.5"),sQuery(id+"F0.wireOp",EDGE,"E7.26.0"),sQuery(id+"F0.wireOp",EDGE,"E7.26.1"),sQuery(id+"F0.wireOp",EDGE,"E7.26.2"),sQuery(id+"F0.wireOp",EDGE,"E7.26.3"),sQuery(id+"F0.wireOp",EDGE,"E7.26.4"),sQuery(id+"F0.wireOp",EDGE,"E7.26.5"),sQuery(id+"F0.wireOp",EDGE,"E7.27.0"),sQuery(id+"F0.wireOp",EDGE,"E7.27.1"),sQuery(id+"F0.wireOp",EDGE,"E7.27.2"),sQuery(id+"F0.wireOp",EDGE,"E7.27.3"),sQuery(id+"F0.wireOp",EDGE,"E7.27.4"),sQuery(id+"F0.wireOp",EDGE,"E7.27.5"),sQuery(id+"F0.wireOp",EDGE,"E7.28.0"),sQuery(id+"F0.wireOp",EDGE,"E7.28.1"),sQuery(id+"F0.wireOp",EDGE,"E7.28.2"),sQuery(id+"F0.wireOp",EDGE,"E7.28.3"),sQuery(id+"F0.wireOp",EDGE,"E7.28.4"),sQuery(id+"F0.wireOp",EDGE,"E7.28.5"),subQ0,sQuery(id+"F0.wireOp",EDGE,"E7.29.1"),sQuery(id+"F0.wireOp",EDGE,"E7.29.2"),sQuery(id+"F0.wireOp",EDGE,"E7.29.3"),sQuery(id+"F0.wireOp",EDGE,"E7.29.4"),sQuery(id+"F0.wireOp",EDGE,"E7.29.5"),sQuery(id+"F0.wireOp",EDGE,"E7.30.0"),sQuery(id+"F0.wireOp",EDGE,"E7.30.1"),sQuery(id+"F0.wireOp",EDGE,"E7.30.2"),sQuery(id+"F0.wireOp",EDGE,"E7.30.3"),sQuery(id+"F0.wireOp",EDGE,"E7.30.4"),sQuery(id+"F0.wireOp",EDGE,"E7.30.5"),sQuery(id+"F0.wireOp",EDGE,"E7.31.0"),sQuery(id+"F0.wireOp",EDGE,"E7.31.1"),sQuery(id+"F0.wireOp",EDGE,"E7.31.2"),sQuery(id+"F0.wireOp",EDGE,"E7.31.3"),sQuery(id+"F0.wireOp",EDGE,"E7.31.4"),sQuery(id+"F0.wireOp",EDGE,"E7.31.5"),sQuery(id+"F0.wireOp",EDGE,"E7.32.0"),sQuery(id+"F0.wireOp",EDGE,"E7.32.1"),sQuery(id+"F0.wireOp",EDGE,"E7.32.2"),sQuery(id+"F0.wireOp",EDGE,"E7.32.3"),sQuery(id+"F0.wireOp",EDGE,"E7.32.4"),sQuery(id+"F0.wireOp",EDGE,"E7.32.5"),sQuery(id+"F0.wireOp",EDGE,"E7.33.0"),sQuery(id+"F0.wireOp",EDGE,"E7.33.1"),sQuery(id+"F0.wireOp",EDGE,"E7.33.2"),sQuery(id+"F0.wireOp",EDGE,"E7.33.3"),sQuery(id+"F0.wireOp",EDGE,"E7.33.4"),sQuery(id+"F0.wireOp",EDGE,"E7.33.5"),sQuery(id+"F0.wireOp",EDGE,"E7.34.0"),sQuery(id+"F0.wireOp",EDGE,"E7.34.1"),sQuery(id+"F0.wireOp",EDGE,"E7.34.2"),sQuery(id+"F0.wireOp",EDGE,"E7.34.3"),sQuery(id+"F0.wireOp",EDGE,"E7.34.4"),sQuery(id+"F0.wireOp",EDGE,"E7.34.5"),sQuery(id+"F0.wireOp",EDGE,"E7.35.0"),sQuery(id+"F0.wireOp",EDGE,"E7.35.1"),sQuery(id+"F0.wireOp",EDGE,"E7.35.2"),sQuery(id+"F0.wireOp",EDGE,"E7.35.3"),sQuery(id+"F0.wireOp",EDGE,"E7.35.4"),sQuery(id+"F0.wireOp",EDGE,"E7.35.5"),sQuery(id+"F0.wireOp",EDGE,"E7.36.0"),sQuery(id+"F0.wireOp",EDGE,"E7.36.1"),sQuery(id+"F0.wireOp",EDGE,"E7.36.2"),sQuery(id+"F0.wireOp",EDGE,"E7.36.3"),sQuery(id+"F0.wireOp",EDGE,"E7.36.4"),sQuery(id+"F0.wireOp",EDGE,"E7.36.5"),sQuery(id+"F0.wireOp",EDGE,"E7.37.0"),sQuery(id+"F0.wireOp",EDGE,"E7.37.1"),sQuery(id+"F0.wireOp",EDGE,"E7.37.2"),sQuery(id+"F0.wireOp",EDGE,"E7.37.3"),sQuery(id+"F0.wireOp",EDGE,"E7.37.4"),sQuery(id+"F0.wireOp",EDGE,"E7.37.5"),sQuery(id+"F0.wireOp",EDGE,"E7.38.0"),sQuery(id+"F0.wireOp",EDGE,"E7.38.1"),sQuery(id+"F0.wireOp",EDGE,"E7.38.2"),sQuery(id+"F0.wireOp",EDGE,"E7.38.3"),sQuery(id+"F0.wireOp",EDGE,"E7.38.4"),sQuery(id+"F0.wireOp",EDGE,"E7.38.5"),sQuery(id+"F0.wireOp",EDGE,"E7.39.0"),sQuery(id+"F0.wireOp",EDGE,"E7.39.1"),sQuery(id+"F0.wireOp",EDGE,"E7.39.2"),sQuery(id+"F0.wireOp",EDGE,"E7.39.3"),sQuery(id+"F0.wireOp",EDGE,"E7.39.4"),sQuery(id+"F0.wireOp",EDGE,"E7.39.5"),sQuery(id+"F0.wireOp",EDGE,"E7.40.0"),sQuery(id+"F0.wireOp",EDGE,"E7.40.1"),sQuery(id+"F0.wireOp",EDGE,"E7.40.2"),sQuery(id+"F0.wireOp",EDGE,"E7.40.3"),sQuery(id+"F0.wireOp",EDGE,"E7.40.4"),sQuery(id+"F0.wireOp",EDGE,"E7.40.5"),sQuery(id+"F0.wireOp",EDGE,"E7.41.0"),sQuery(id+"F0.wireOp",EDGE,"E7.41.1"),sQuery(id+"F0.wireOp",EDGE,"E7.41.2"),sQuery(id+"F0.wireOp",EDGE,"E7.41.3"),sQuery(id+"F0.wireOp",EDGE,"E7.41.4"),sQuery(id+"F0.wireOp",EDGE,"E7.41.5"),sQuery(id+"F0.wireOp",EDGE,"E7.42.0"),sQuery(id+"F0.wireOp",EDGE,"E7.42.1"),sQuery(id+"F0.wireOp",EDGE,"E7.42.2"),sQuery(id+"F0.wireOp",EDGE,"E7.42.3"),sQuery(id+"F0.wireOp",EDGE,"E7.42.4"),sQuery(id+"F0.wireOp",EDGE,"E7.42.5"),sQuery(id+"F0.wireOp",EDGE,"E7.43.0"),sQuery(id+"F0.wireOp",EDGE,"E7.43.1"),sQuery(id+"F0.wireOp",EDGE,"E7.43.2"),sQuery(id+"F0.wireOp",EDGE,"E7.43.3"),sQuery(id+"F0.wireOp",EDGE,"E7.43.4"),sQuery(id+"F0.wireOp",EDGE,"E7.43.5")])],"isStart":false})]});}
            var Q8;
            {var subQ0=sQuery(id+"F0.wireOp",EDGE,"E7.27.0");Q8=makeQuery(id+"F2.opChamfer","BLEND_EDGE",EDGE,{"blendedFrom":[makeQuery(id+"F1.opExtrude","CAP_EDGE",EDGE,{"disambiguationData":[OSD([subQ0])],"isStart":false}),makeQuery(id+"F1.opExtrude","CAP_FACE",FACE,{"disambiguationData":[OSD([sQuery(id+"F0.wireOp",EDGE,"E1"),sQuery(id+"F0.wireOp",EDGE,"E2"),sQuery(id+"F0.wireOp",EDGE,"E3"),sQuery(id+"F0.wireOp",EDGE,"E4"),sQuery(id+"F0.wireOp",EDGE,"E5"),sQuery(id+"F0.wireOp",EDGE,"E6"),sQuery(id+"F0.wireOp",EDGE,"E7.1.0"),sQuery(id+"F0.wireOp",EDGE,"E7.1.1"),sQuery(id+"F0.wireOp",EDGE,"E7.1.2"),sQuery(id+"F0.wireOp",EDGE,"E7.1.3"),sQuery(id+"F0.wireOp",EDGE,"E7.1.4"),sQuery(id+"F0.wireOp",EDGE,"E7.1.5"),sQuery(id+"F0.wireOp",EDGE,"E7.2.0"),sQuery(id+"F0.wireOp",EDGE,"E7.2.1"),sQuery(id+"F0.wireOp",EDGE,"E7.2.2"),sQuery(id+"F0.wireOp",EDGE,"E7.2.3"),sQuery(id+"F0.wireOp",EDGE,"E7.2.4"),sQuery(id+"F0.wireOp",EDGE,"E7.2.5"),sQuery(id+"F0.wireOp",EDGE,"E7.3.0"),sQuery(id+"F0.wireOp",EDGE,"E7.3.1"),sQuery(id+"F0.wireOp",EDGE,"E7.3.2"),sQuery(id+"F0.wireOp",EDGE,"E7.3.3"),sQuery(id+"F0.wireOp",EDGE,"E7.3.4"),sQuery(id+"F0.wireOp",EDGE,"E7.3.5"),sQuery(id+"F0.wireOp",EDGE,"E7.4.0"),sQuery(id+"F0.wireOp",EDGE,"E7.4.1"),sQuery(id+"F0.wireOp",EDGE,"E7.4.2"),sQuery(id+"F0.wireOp",EDGE,"E7.4.3"),sQuery(id+"F0.wireOp",EDGE,"E7.4.4"),sQuery(id+"F0.wireOp",EDGE,"E7.4.5"),sQuery(id+"F0.wireOp",EDGE,"E7.5.0"),sQuery(id+"F0.wireOp",EDGE,"E7.5.1"),sQuery(id+"F0.wireOp",EDGE,"E7.5.2"),sQuery(id+"F0.wireOp",EDGE,"E7.5.3"),sQuery(id+"F0.wireOp",EDGE,"E7.5.4"),sQuery(id+"F0.wireOp",EDGE,"E7.5.5"),sQuery(id+"F0.wireOp",EDGE,"E7.6.0"),sQuery(id+"F0.wireOp",EDGE,"E7.6.1"),sQuery(id+"F0.wireOp",EDGE,"E7.6.2"),sQuery(id+"F0.wireOp",EDGE,"E7.6.3"),sQuery(id+"F0.wireOp",EDGE,"E7.6.4"),sQuery(id+"F0.wireOp",EDGE,"E7.6.5"),sQuery(id+"F0.wireOp",EDGE,"E7.7.0"),sQuery(id+"F0.wireOp",EDGE,"E7.7.1"),sQuery(id+"F0.wireOp",EDGE,"E7.7.2"),sQuery(id+"F0.wireOp",EDGE,"E7.7.3"),sQuery(id+"F0.wireOp",EDGE,"E7.7.4"),sQuery(id+"F0.wireOp",EDGE,"E7.7.5"),sQuery(id+"F0.wireOp",EDGE,"E7.8.0"),sQuery(id+"F0.wireOp",EDGE,"E7.8.1"),sQuery(id+"F0.wireOp",EDGE,"E7.8.2"),sQuery(id+"F0.wireOp",EDGE,"E7.8.3"),sQuery(id+"F0.wireOp",EDGE,"E7.8.4"),sQuery(id+"F0.wireOp",EDGE,"E7.8.5"),sQuery(id+"F0.wireOp",EDGE,"E7.9.0"),sQuery(id+"F0.wireOp",EDGE,"E7.9.1"),sQuery(id+"F0.wireOp",EDGE,"E7.9.2"),sQuery(id+"F0.wireOp",EDGE,"E7.9.3"),sQuery(id+"F0.wireOp",EDGE,"E7.9.4"),sQuery(id+"F0.wireOp",EDGE,"E7.9.5"),sQuery(id+"F0.wireOp",EDGE,"E7.10.0"),sQuery(id+"F0.wireOp",EDGE,"E7.10.1"),sQuery(id+"F0.wireOp",EDGE,"E7.10.2"),sQuery(id+"F0.wireOp",EDGE,"E7.10.3"),sQuery(id+"F0.wireOp",EDGE,"E7.10.4"),sQuery(id+"F0.wireOp",EDGE,"E7.10.5"),sQuery(id+"F0.wireOp",EDGE,"E7.11.0"),sQuery(id+"F0.wireOp",EDGE,"E7.11.1"),sQuery(id+"F0.wireOp",EDGE,"E7.11.2"),sQuery(id+"F0.wireOp",EDGE,"E7.11.3"),sQuery(id+"F0.wireOp",EDGE,"E7.11.4"),sQuery(id+"F0.wireOp",EDGE,"E7.11.5"),sQuery(id+"F0.wireOp",EDGE,"E7.12.0"),sQuery(id+"F0.wireOp",EDGE,"E7.12.1"),sQuery(id+"F0.wireOp",EDGE,"E7.12.2"),sQuery(id+"F0.wireOp",EDGE,"E7.12.3"),sQuery(id+"F0.wireOp",EDGE,"E7.12.4"),sQuery(id+"F0.wireOp",EDGE,"E7.12.5"),sQuery(id+"F0.wireOp",EDGE,"E7.13.0"),sQuery(id+"F0.wireOp",EDGE,"E7.13.1"),sQuery(id+"F0.wireOp",EDGE,"E7.13.2"),sQuery(id+"F0.wireOp",EDGE,"E7.13.3"),sQuery(id+"F0.wireOp",EDGE,"E7.13.4"),sQuery(id+"F0.wireOp",EDGE,"E7.13.5"),sQuery(id+"F0.wireOp",EDGE,"E7.14.0"),sQuery(id+"F0.wireOp",EDGE,"E7.14.1"),sQuery(id+"F0.wireOp",EDGE,"E7.14.2"),sQuery(id+"F0.wireOp",EDGE,"E7.14.3"),sQuery(id+"F0.wireOp",EDGE,"E7.14.4"),sQuery(id+"F0.wireOp",EDGE,"E7.14.5"),sQuery(id+"F0.wireOp",EDGE,"E7.15.0"),sQuery(id+"F0.wireOp",EDGE,"E7.15.1"),sQuery(id+"F0.wireOp",EDGE,"E7.15.2"),sQuery(id+"F0.wireOp",EDGE,"E7.15.3"),sQuery(id+"F0.wireOp",EDGE,"E7.15.4"),sQuery(id+"F0.wireOp",EDGE,"E7.15.5"),sQuery(id+"F0.wireOp",EDGE,"E7.16.0"),sQuery(id+"F0.wireOp",EDGE,"E7.16.1"),sQuery(id+"F0.wireOp",EDGE,"E7.16.2"),sQuery(id+"F0.wireOp",EDGE,"E7.16.3"),sQuery(id+"F0.wireOp",EDGE,"E7.16.4"),sQuery(id+"F0.wireOp",EDGE,"E7.16.5"),sQuery(id+"F0.wireOp",EDGE,"E7.17.0"),sQuery(id+"F0.wireOp",EDGE,"E7.17.1"),sQuery(id+"F0.wireOp",EDGE,"E7.17.2"),sQuery(id+"F0.wireOp",EDGE,"E7.17.3"),sQuery(id+"F0.wireOp",EDGE,"E7.17.4"),sQuery(id+"F0.wireOp",EDGE,"E7.17.5"),sQuery(id+"F0.wireOp",EDGE,"E7.18.0"),sQuery(id+"F0.wireOp",EDGE,"E7.18.1"),sQuery(id+"F0.wireOp",EDGE,"E7.18.2"),sQuery(id+"F0.wireOp",EDGE,"E7.18.3"),sQuery(id+"F0.wireOp",EDGE,"E7.18.4"),sQuery(id+"F0.wireOp",EDGE,"E7.18.5"),sQuery(id+"F0.wireOp",EDGE,"E7.19.0"),sQuery(id+"F0.wireOp",EDGE,"E7.19.1"),sQuery(id+"F0.wireOp",EDGE,"E7.19.2"),sQuery(id+"F0.wireOp",EDGE,"E7.19.3"),sQuery(id+"F0.wireOp",EDGE,"E7.19.4"),sQuery(id+"F0.wireOp",EDGE,"E7.19.5"),sQuery(id+"F0.wireOp",EDGE,"E7.20.0"),sQuery(id+"F0.wireOp",EDGE,"E7.20.1"),sQuery(id+"F0.wireOp",EDGE,"E7.20.2"),sQuery(id+"F0.wireOp",EDGE,"E7.20.3"),sQuery(id+"F0.wireOp",EDGE,"E7.20.4"),sQuery(id+"F0.wireOp",EDGE,"E7.20.5"),sQuery(id+"F0.wireOp",EDGE,"E7.21.0"),sQuery(id+"F0.wireOp",EDGE,"E7.21.1"),sQuery(id+"F0.wireOp",EDGE,"E7.21.2"),sQuery(id+"F0.wireOp",EDGE,"E7.21.3"),sQuery(id+"F0.wireOp",EDGE,"E7.21.4"),sQuery(id+"F0.wireOp",EDGE,"E7.21.5"),sQuery(id+"F0.wireOp",EDGE,"E7.22.0"),sQuery(id+"F0.wireOp",EDGE,"E7.22.1"),sQuery(id+"F0.wireOp",EDGE,"E7.22.2"),sQuery(id+"F0.wireOp",EDGE,"E7.22.3"),sQuery(id+"F0.wireOp",EDGE,"E7.22.4"),sQuery(id+"F0.wireOp",EDGE,"E7.22.5"),sQuery(id+"F0.wireOp",EDGE,"E7.23.0"),sQuery(id+"F0.wireOp",EDGE,"E7.23.1"),sQuery(id+"F0.wireOp",EDGE,"E7.23.2"),sQuery(id+"F0.wireOp",EDGE,"E7.23.3"),sQuery(id+"F0.wireOp",EDGE,"E7.23.4"),sQuery(id+"F0.wireOp",EDGE,"E7.23.5"),sQuery(id+"F0.wireOp",EDGE,"E7.24.0"),sQuery(id+"F0.wireOp",EDGE,"E7.24.1"),sQuery(id+"F0.wireOp",EDGE,"E7.24.2"),sQuery(id+"F0.wireOp",EDGE,"E7.24.3"),sQuery(id+"F0.wireOp",EDGE,"E7.24.4"),sQuery(id+"F0.wireOp",EDGE,"E7.24.5"),sQuery(id+"F0.wireOp",EDGE,"E7.25.0"),sQuery(id+"F0.wireOp",EDGE,"E7.25.1"),sQuery(id+"F0.wireOp",EDGE,"E7.25.2"),sQuery(id+"F0.wireOp",EDGE,"E7.25.3"),sQuery(id+"F0.wireOp",EDGE,"E7.25.4"),sQuery(id+"F0.wireOp",EDGE,"E7.25.5"),sQuery(id+"F0.wireOp",EDGE,"E7.26.0"),sQuery(id+"F0.wireOp",EDGE,"E7.26.1"),sQuery(id+"F0.wireOp",EDGE,"E7.26.2"),sQuery(id+"F0.wireOp",EDGE,"E7.26.3"),sQuery(id+"F0.wireOp",EDGE,"E7.26.4"),sQuery(id+"F0.wireOp",EDGE,"E7.26.5"),subQ0,sQuery(id+"F0.wireOp",EDGE,"E7.27.1"),sQuery(id+"F0.wireOp",EDGE,"E7.27.2"),sQuery(id+"F0.wireOp",EDGE,"E7.27.3"),sQuery(id+"F0.wireOp",EDGE,"E7.27.4"),sQuery(id+"F0.wireOp",EDGE,"E7.27.5"),sQuery(id+"F0.wireOp",EDGE,"E7.28.0"),sQuery(id+"F0.wireOp",EDGE,"E7.28.1"),sQuery(id+"F0.wireOp",EDGE,"E7.28.2"),sQuery(id+"F0.wireOp",EDGE,"E7.28.3"),sQuery(id+"F0.wireOp",EDGE,"E7.28.4"),sQuery(id+"F0.wireOp",EDGE,"E7.28.5"),sQuery(id+"F0.wireOp",EDGE,"E7.29.0"),sQuery(id+"F0.wireOp",EDGE,"E7.29.1"),sQuery(id+"F0.wireOp",EDGE,"E7.29.2"),sQuery(id+"F0.wireOp",EDGE,"E7.29.3"),sQuery(id+"F0.wireOp",EDGE,"E7.29.4"),sQuery(id+"F0.wireOp",EDGE,"E7.29.5"),sQuery(id+"F0.wireOp",EDGE,"E7.30.0"),sQuery(id+"F0.wireOp",EDGE,"E7.30.1"),sQuery(id+"F0.wireOp",EDGE,"E7.30.2"),sQuery(id+"F0.wireOp",EDGE,"E7.30.3"),sQuery(id+"F0.wireOp",EDGE,"E7.30.4"),sQuery(id+"F0.wireOp",EDGE,"E7.30.5"),sQuery(id+"F0.wireOp",EDGE,"E7.31.0"),sQuery(id+"F0.wireOp",EDGE,"E7.31.1"),sQuery(id+"F0.wireOp",EDGE,"E7.31.2"),sQuery(id+"F0.wireOp",EDGE,"E7.31.3"),sQuery(id+"F0.wireOp",EDGE,"E7.31.4"),sQuery(id+"F0.wireOp",EDGE,"E7.31.5"),sQuery(id+"F0.wireOp",EDGE,"E7.32.0"),sQuery(id+"F0.wireOp",EDGE,"E7.32.1"),sQuery(id+"F0.wireOp",EDGE,"E7.32.2"),sQuery(id+"F0.wireOp",EDGE,"E7.32.3"),sQuery(id+"F0.wireOp",EDGE,"E7.32.4"),sQuery(id+"F0.wireOp",EDGE,"E7.32.5"),sQuery(id+"F0.wireOp",EDGE,"E7.33.0"),sQuery(id+"F0.wireOp",EDGE,"E7.33.1"),sQuery(id+"F0.wireOp",EDGE,"E7.33.2"),sQuery(id+"F0.wireOp",EDGE,"E7.33.3"),sQuery(id+"F0.wireOp",EDGE,"E7.33.4"),sQuery(id+"F0.wireOp",EDGE,"E7.33.5"),sQuery(id+"F0.wireOp",EDGE,"E7.34.0"),sQuery(id+"F0.wireOp",EDGE,"E7.34.1"),sQuery(id+"F0.wireOp",EDGE,"E7.34.2"),sQuery(id+"F0.wireOp",EDGE,"E7.34.3"),sQuery(id+"F0.wireOp",EDGE,"E7.34.4"),sQuery(id+"F0.wireOp",EDGE,"E7.34.5"),sQuery(id+"F0.wireOp",EDGE,"E7.35.0"),sQuery(id+"F0.wireOp",EDGE,"E7.35.1"),sQuery(id+"F0.wireOp",EDGE,"E7.35.2"),sQuery(id+"F0.wireOp",EDGE,"E7.35.3"),sQuery(id+"F0.wireOp",EDGE,"E7.35.4"),sQuery(id+"F0.wireOp",EDGE,"E7.35.5"),sQuery(id+"F0.wireOp",EDGE,"E7.36.0"),sQuery(id+"F0.wireOp",EDGE,"E7.36.1"),sQuery(id+"F0.wireOp",EDGE,"E7.36.2"),sQuery(id+"F0.wireOp",EDGE,"E7.36.3"),sQuery(id+"F0.wireOp",EDGE,"E7.36.4"),sQuery(id+"F0.wireOp",EDGE,"E7.36.5"),sQuery(id+"F0.wireOp",EDGE,"E7.37.0"),sQuery(id+"F0.wireOp",EDGE,"E7.37.1"),sQuery(id+"F0.wireOp",EDGE,"E7.37.2"),sQuery(id+"F0.wireOp",EDGE,"E7.37.3"),sQuery(id+"F0.wireOp",EDGE,"E7.37.4"),sQuery(id+"F0.wireOp",EDGE,"E7.37.5"),sQuery(id+"F0.wireOp",EDGE,"E7.38.0"),sQuery(id+"F0.wireOp",EDGE,"E7.38.1"),sQuery(id+"F0.wireOp",EDGE,"E7.38.2"),sQuery(id+"F0.wireOp",EDGE,"E7.38.3"),sQuery(id+"F0.wireOp",EDGE,"E7.38.4"),sQuery(id+"F0.wireOp",EDGE,"E7.38.5"),sQuery(id+"F0.wireOp",EDGE,"E7.39.0"),sQuery(id+"F0.wireOp",EDGE,"E7.39.1"),sQuery(id+"F0.wireOp",EDGE,"E7.39.2"),sQuery(id+"F0.wireOp",EDGE,"E7.39.3"),sQuery(id+"F0.wireOp",EDGE,"E7.39.4"),sQuery(id+"F0.wireOp",EDGE,"E7.39.5"),sQuery(id+"F0.wireOp",EDGE,"E7.40.0"),sQuery(id+"F0.wireOp",EDGE,"E7.40.1"),sQuery(id+"F0.wireOp",EDGE,"E7.40.2"),sQuery(id+"F0.wireOp",EDGE,"E7.40.3"),sQuery(id+"F0.wireOp",EDGE,"E7.40.4"),sQuery(id+"F0.wireOp",EDGE,"E7.40.5"),sQuery(id+"F0.wireOp",EDGE,"E7.41.0"),sQuery(id+"F0.wireOp",EDGE,"E7.41.1"),sQuery(id+"F0.wireOp",EDGE,"E7.41.2"),sQuery(id+"F0.wireOp",EDGE,"E7.41.3"),sQuery(id+"F0.wireOp",EDGE,"E7.41.4"),sQuery(id+"F0.wireOp",EDGE,"E7.41.5"),sQuery(id+"F0.wireOp",EDGE,"E7.42.0"),sQuery(id+"F0.wireOp",EDGE,"E7.42.1"),sQuery(id+"F0.wireOp",EDGE,"E7.42.2"),sQuery(id+"F0.wireOp",EDGE,"E7.42.3"),sQuery(id+"F0.wireOp",EDGE,"E7.42.4"),sQuery(id+"F0.wireOp",EDGE,"E7.42.5"),sQuery(id+"F0.wireOp",EDGE,"E7.43.0"),sQuery(id+"F0.wireOp",EDGE,"E7.43.1"),sQuery(id+"F0.wireOp",EDGE,"E7.43.2"),sQuery(id+"F0.wireOp",EDGE,"E7.43.3"),sQuery(id+"F0.wireOp",EDGE,"E7.43.4"),sQuery(id+"F0.wireOp",EDGE,"E7.43.5")])],"isStart":false})],"blendedInto":[makeQuery(id+"F1.opExtrude","CAP_FACE",FACE,{"disambiguationData":[OSD([sQuery(id+"F0.wireOp",EDGE,"E1"),sQuery(id+"F0.wireOp",EDGE,"E2"),sQuery(id+"F0.wireOp",EDGE,"E3"),sQuery(id+"F0.wireOp",EDGE,"E4"),sQuery(id+"F0.wireOp",EDGE,"E5"),sQuery(id+"F0.wireOp",EDGE,"E6"),sQuery(id+"F0.wireOp",EDGE,"E7.1.0"),sQuery(id+"F0.wireOp",EDGE,"E7.1.1"),sQuery(id+"F0.wireOp",EDGE,"E7.1.2"),sQuery(id+"F0.wireOp",EDGE,"E7.1.3"),sQuery(id+"F0.wireOp",EDGE,"E7.1.4"),sQuery(id+"F0.wireOp",EDGE,"E7.1.5"),sQuery(id+"F0.wireOp",EDGE,"E7.2.0"),sQuery(id+"F0.wireOp",EDGE,"E7.2.1"),sQuery(id+"F0.wireOp",EDGE,"E7.2.2"),sQuery(id+"F0.wireOp",EDGE,"E7.2.3"),sQuery(id+"F0.wireOp",EDGE,"E7.2.4"),sQuery(id+"F0.wireOp",EDGE,"E7.2.5"),sQuery(id+"F0.wireOp",EDGE,"E7.3.0"),sQuery(id+"F0.wireOp",EDGE,"E7.3.1"),sQuery(id+"F0.wireOp",EDGE,"E7.3.2"),sQuery(id+"F0.wireOp",EDGE,"E7.3.3"),sQuery(id+"F0.wireOp",EDGE,"E7.3.4"),sQuery(id+"F0.wireOp",EDGE,"E7.3.5"),sQuery(id+"F0.wireOp",EDGE,"E7.4.0"),sQuery(id+"F0.wireOp",EDGE,"E7.4.1"),sQuery(id+"F0.wireOp",EDGE,"E7.4.2"),sQuery(id+"F0.wireOp",EDGE,"E7.4.3"),sQuery(id+"F0.wireOp",EDGE,"E7.4.4"),sQuery(id+"F0.wireOp",EDGE,"E7.4.5"),sQuery(id+"F0.wireOp",EDGE,"E7.5.0"),sQuery(id+"F0.wireOp",EDGE,"E7.5.1"),sQuery(id+"F0.wireOp",EDGE,"E7.5.2"),sQuery(id+"F0.wireOp",EDGE,"E7.5.3"),sQuery(id+"F0.wireOp",EDGE,"E7.5.4"),sQuery(id+"F0.wireOp",EDGE,"E7.5.5"),sQuery(id+"F0.wireOp",EDGE,"E7.6.0"),sQuery(id+"F0.wireOp",EDGE,"E7.6.1"),sQuery(id+"F0.wireOp",EDGE,"E7.6.2"),sQuery(id+"F0.wireOp",EDGE,"E7.6.3"),sQuery(id+"F0.wireOp",EDGE,"E7.6.4"),sQuery(id+"F0.wireOp",EDGE,"E7.6.5"),sQuery(id+"F0.wireOp",EDGE,"E7.7.0"),sQuery(id+"F0.wireOp",EDGE,"E7.7.1"),sQuery(id+"F0.wireOp",EDGE,"E7.7.2"),sQuery(id+"F0.wireOp",EDGE,"E7.7.3"),sQuery(id+"F0.wireOp",EDGE,"E7.7.4"),sQuery(id+"F0.wireOp",EDGE,"E7.7.5"),sQuery(id+"F0.wireOp",EDGE,"E7.8.0"),sQuery(id+"F0.wireOp",EDGE,"E7.8.1"),sQuery(id+"F0.wireOp",EDGE,"E7.8.2"),sQuery(id+"F0.wireOp",EDGE,"E7.8.3"),sQuery(id+"F0.wireOp",EDGE,"E7.8.4"),sQuery(id+"F0.wireOp",EDGE,"E7.8.5"),sQuery(id+"F0.wireOp",EDGE,"E7.9.0"),sQuery(id+"F0.wireOp",EDGE,"E7.9.1"),sQuery(id+"F0.wireOp",EDGE,"E7.9.2"),sQuery(id+"F0.wireOp",EDGE,"E7.9.3"),sQuery(id+"F0.wireOp",EDGE,"E7.9.4"),sQuery(id+"F0.wireOp",EDGE,"E7.9.5"),sQuery(id+"F0.wireOp",EDGE,"E7.10.0"),sQuery(id+"F0.wireOp",EDGE,"E7.10.1"),sQuery(id+"F0.wireOp",EDGE,"E7.10.2"),sQuery(id+"F0.wireOp",EDGE,"E7.10.3"),sQuery(id+"F0.wireOp",EDGE,"E7.10.4"),sQuery(id+"F0.wireOp",EDGE,"E7.10.5"),sQuery(id+"F0.wireOp",EDGE,"E7.11.0"),sQuery(id+"F0.wireOp",EDGE,"E7.11.1"),sQuery(id+"F0.wireOp",EDGE,"E7.11.2"),sQuery(id+"F0.wireOp",EDGE,"E7.11.3"),sQuery(id+"F0.wireOp",EDGE,"E7.11.4"),sQuery(id+"F0.wireOp",EDGE,"E7.11.5"),sQuery(id+"F0.wireOp",EDGE,"E7.12.0"),sQuery(id+"F0.wireOp",EDGE,"E7.12.1"),sQuery(id+"F0.wireOp",EDGE,"E7.12.2"),sQuery(id+"F0.wireOp",EDGE,"E7.12.3"),sQuery(id+"F0.wireOp",EDGE,"E7.12.4"),sQuery(id+"F0.wireOp",EDGE,"E7.12.5"),sQuery(id+"F0.wireOp",EDGE,"E7.13.0"),sQuery(id+"F0.wireOp",EDGE,"E7.13.1"),sQuery(id+"F0.wireOp",EDGE,"E7.13.2"),sQuery(id+"F0.wireOp",EDGE,"E7.13.3"),sQuery(id+"F0.wireOp",EDGE,"E7.13.4"),sQuery(id+"F0.wireOp",EDGE,"E7.13.5"),sQuery(id+"F0.wireOp",EDGE,"E7.14.0"),sQuery(id+"F0.wireOp",EDGE,"E7.14.1"),sQuery(id+"F0.wireOp",EDGE,"E7.14.2"),sQuery(id+"F0.wireOp",EDGE,"E7.14.3"),sQuery(id+"F0.wireOp",EDGE,"E7.14.4"),sQuery(id+"F0.wireOp",EDGE,"E7.14.5"),sQuery(id+"F0.wireOp",EDGE,"E7.15.0"),sQuery(id+"F0.wireOp",EDGE,"E7.15.1"),sQuery(id+"F0.wireOp",EDGE,"E7.15.2"),sQuery(id+"F0.wireOp",EDGE,"E7.15.3"),sQuery(id+"F0.wireOp",EDGE,"E7.15.4"),sQuery(id+"F0.wireOp",EDGE,"E7.15.5"),sQuery(id+"F0.wireOp",EDGE,"E7.16.0"),sQuery(id+"F0.wireOp",EDGE,"E7.16.1"),sQuery(id+"F0.wireOp",EDGE,"E7.16.2"),sQuery(id+"F0.wireOp",EDGE,"E7.16.3"),sQuery(id+"F0.wireOp",EDGE,"E7.16.4"),sQuery(id+"F0.wireOp",EDGE,"E7.16.5"),sQuery(id+"F0.wireOp",EDGE,"E7.17.0"),sQuery(id+"F0.wireOp",EDGE,"E7.17.1"),sQuery(id+"F0.wireOp",EDGE,"E7.17.2"),sQuery(id+"F0.wireOp",EDGE,"E7.17.3"),sQuery(id+"F0.wireOp",EDGE,"E7.17.4"),sQuery(id+"F0.wireOp",EDGE,"E7.17.5"),sQuery(id+"F0.wireOp",EDGE,"E7.18.0"),sQuery(id+"F0.wireOp",EDGE,"E7.18.1"),sQuery(id+"F0.wireOp",EDGE,"E7.18.2"),sQuery(id+"F0.wireOp",EDGE,"E7.18.3"),sQuery(id+"F0.wireOp",EDGE,"E7.18.4"),sQuery(id+"F0.wireOp",EDGE,"E7.18.5"),sQuery(id+"F0.wireOp",EDGE,"E7.19.0"),sQuery(id+"F0.wireOp",EDGE,"E7.19.1"),sQuery(id+"F0.wireOp",EDGE,"E7.19.2"),sQuery(id+"F0.wireOp",EDGE,"E7.19.3"),sQuery(id+"F0.wireOp",EDGE,"E7.19.4"),sQuery(id+"F0.wireOp",EDGE,"E7.19.5"),sQuery(id+"F0.wireOp",EDGE,"E7.20.0"),sQuery(id+"F0.wireOp",EDGE,"E7.20.1"),sQuery(id+"F0.wireOp",EDGE,"E7.20.2"),sQuery(id+"F0.wireOp",EDGE,"E7.20.3"),sQuery(id+"F0.wireOp",EDGE,"E7.20.4"),sQuery(id+"F0.wireOp",EDGE,"E7.20.5"),sQuery(id+"F0.wireOp",EDGE,"E7.21.0"),sQuery(id+"F0.wireOp",EDGE,"E7.21.1"),sQuery(id+"F0.wireOp",EDGE,"E7.21.2"),sQuery(id+"F0.wireOp",EDGE,"E7.21.3"),sQuery(id+"F0.wireOp",EDGE,"E7.21.4"),sQuery(id+"F0.wireOp",EDGE,"E7.21.5"),sQuery(id+"F0.wireOp",EDGE,"E7.22.0"),sQuery(id+"F0.wireOp",EDGE,"E7.22.1"),sQuery(id+"F0.wireOp",EDGE,"E7.22.2"),sQuery(id+"F0.wireOp",EDGE,"E7.22.3"),sQuery(id+"F0.wireOp",EDGE,"E7.22.4"),sQuery(id+"F0.wireOp",EDGE,"E7.22.5"),sQuery(id+"F0.wireOp",EDGE,"E7.23.0"),sQuery(id+"F0.wireOp",EDGE,"E7.23.1"),sQuery(id+"F0.wireOp",EDGE,"E7.23.2"),sQuery(id+"F0.wireOp",EDGE,"E7.23.3"),sQuery(id+"F0.wireOp",EDGE,"E7.23.4"),sQuery(id+"F0.wireOp",EDGE,"E7.23.5"),sQuery(id+"F0.wireOp",EDGE,"E7.24.0"),sQuery(id+"F0.wireOp",EDGE,"E7.24.1"),sQuery(id+"F0.wireOp",EDGE,"E7.24.2"),sQuery(id+"F0.wireOp",EDGE,"E7.24.3"),sQuery(id+"F0.wireOp",EDGE,"E7.24.4"),sQuery(id+"F0.wireOp",EDGE,"E7.24.5"),sQuery(id+"F0.wireOp",EDGE,"E7.25.0"),sQuery(id+"F0.wireOp",EDGE,"E7.25.1"),sQuery(id+"F0.wireOp",EDGE,"E7.25.2"),sQuery(id+"F0.wireOp",EDGE,"E7.25.3"),sQuery(id+"F0.wireOp",EDGE,"E7.25.4"),sQuery(id+"F0.wireOp",EDGE,"E7.25.5"),sQuery(id+"F0.wireOp",EDGE,"E7.26.0"),sQuery(id+"F0.wireOp",EDGE,"E7.26.1"),sQuery(id+"F0.wireOp",EDGE,"E7.26.2"),sQuery(id+"F0.wireOp",EDGE,"E7.26.3"),sQuery(id+"F0.wireOp",EDGE,"E7.26.4"),sQuery(id+"F0.wireOp",EDGE,"E7.26.5"),subQ0,sQuery(id+"F0.wireOp",EDGE,"E7.27.1"),sQuery(id+"F0.wireOp",EDGE,"E7.27.2"),sQuery(id+"F0.wireOp",EDGE,"E7.27.3"),sQuery(id+"F0.wireOp",EDGE,"E7.27.4"),sQuery(id+"F0.wireOp",EDGE,"E7.27.5"),sQuery(id+"F0.wireOp",EDGE,"E7.28.0"),sQuery(id+"F0.wireOp",EDGE,"E7.28.1"),sQuery(id+"F0.wireOp",EDGE,"E7.28.2"),sQuery(id+"F0.wireOp",EDGE,"E7.28.3"),sQuery(id+"F0.wireOp",EDGE,"E7.28.4"),sQuery(id+"F0.wireOp",EDGE,"E7.28.5"),sQuery(id+"F0.wireOp",EDGE,"E7.29.0"),sQuery(id+"F0.wireOp",EDGE,"E7.29.1"),sQuery(id+"F0.wireOp",EDGE,"E7.29.2"),sQuery(id+"F0.wireOp",EDGE,"E7.29.3"),sQuery(id+"F0.wireOp",EDGE,"E7.29.4"),sQuery(id+"F0.wireOp",EDGE,"E7.29.5"),sQuery(id+"F0.wireOp",EDGE,"E7.30.0"),sQuery(id+"F0.wireOp",EDGE,"E7.30.1"),sQuery(id+"F0.wireOp",EDGE,"E7.30.2"),sQuery(id+"F0.wireOp",EDGE,"E7.30.3"),sQuery(id+"F0.wireOp",EDGE,"E7.30.4"),sQuery(id+"F0.wireOp",EDGE,"E7.30.5"),sQuery(id+"F0.wireOp",EDGE,"E7.31.0"),sQuery(id+"F0.wireOp",EDGE,"E7.31.1"),sQuery(id+"F0.wireOp",EDGE,"E7.31.2"),sQuery(id+"F0.wireOp",EDGE,"E7.31.3"),sQuery(id+"F0.wireOp",EDGE,"E7.31.4"),sQuery(id+"F0.wireOp",EDGE,"E7.31.5"),sQuery(id+"F0.wireOp",EDGE,"E7.32.0"),sQuery(id+"F0.wireOp",EDGE,"E7.32.1"),sQuery(id+"F0.wireOp",EDGE,"E7.32.2"),sQuery(id+"F0.wireOp",EDGE,"E7.32.3"),sQuery(id+"F0.wireOp",EDGE,"E7.32.4"),sQuery(id+"F0.wireOp",EDGE,"E7.32.5"),sQuery(id+"F0.wireOp",EDGE,"E7.33.0"),sQuery(id+"F0.wireOp",EDGE,"E7.33.1"),sQuery(id+"F0.wireOp",EDGE,"E7.33.2"),sQuery(id+"F0.wireOp",EDGE,"E7.33.3"),sQuery(id+"F0.wireOp",EDGE,"E7.33.4"),sQuery(id+"F0.wireOp",EDGE,"E7.33.5"),sQuery(id+"F0.wireOp",EDGE,"E7.34.0"),sQuery(id+"F0.wireOp",EDGE,"E7.34.1"),sQuery(id+"F0.wireOp",EDGE,"E7.34.2"),sQuery(id+"F0.wireOp",EDGE,"E7.34.3"),sQuery(id+"F0.wireOp",EDGE,"E7.34.4"),sQuery(id+"F0.wireOp",EDGE,"E7.34.5"),sQuery(id+"F0.wireOp",EDGE,"E7.35.0"),sQuery(id+"F0.wireOp",EDGE,"E7.35.1"),sQuery(id+"F0.wireOp",EDGE,"E7.35.2"),sQuery(id+"F0.wireOp",EDGE,"E7.35.3"),sQuery(id+"F0.wireOp",EDGE,"E7.35.4"),sQuery(id+"F0.wireOp",EDGE,"E7.35.5"),sQuery(id+"F0.wireOp",EDGE,"E7.36.0"),sQuery(id+"F0.wireOp",EDGE,"E7.36.1"),sQuery(id+"F0.wireOp",EDGE,"E7.36.2"),sQuery(id+"F0.wireOp",EDGE,"E7.36.3"),sQuery(id+"F0.wireOp",EDGE,"E7.36.4"),sQuery(id+"F0.wireOp",EDGE,"E7.36.5"),sQuery(id+"F0.wireOp",EDGE,"E7.37.0"),sQuery(id+"F0.wireOp",EDGE,"E7.37.1"),sQuery(id+"F0.wireOp",EDGE,"E7.37.2"),sQuery(id+"F0.wireOp",EDGE,"E7.37.3"),sQuery(id+"F0.wireOp",EDGE,"E7.37.4"),sQuery(id+"F0.wireOp",EDGE,"E7.37.5"),sQuery(id+"F0.wireOp",EDGE,"E7.38.0"),sQuery(id+"F0.wireOp",EDGE,"E7.38.1"),sQuery(id+"F0.wireOp",EDGE,"E7.38.2"),sQuery(id+"F0.wireOp",EDGE,"E7.38.3"),sQuery(id+"F0.wireOp",EDGE,"E7.38.4"),sQuery(id+"F0.wireOp",EDGE,"E7.38.5"),sQuery(id+"F0.wireOp",EDGE,"E7.39.0"),sQuery(id+"F0.wireOp",EDGE,"E7.39.1"),sQuery(id+"F0.wireOp",EDGE,"E7.39.2"),sQuery(id+"F0.wireOp",EDGE,"E7.39.3"),sQuery(id+"F0.wireOp",EDGE,"E7.39.4"),sQuery(id+"F0.wireOp",EDGE,"E7.39.5"),sQuery(id+"F0.wireOp",EDGE,"E7.40.0"),sQuery(id+"F0.wireOp",EDGE,"E7.40.1"),sQuery(id+"F0.wireOp",EDGE,"E7.40.2"),sQuery(id+"F0.wireOp",EDGE,"E7.40.3"),sQuery(id+"F0.wireOp",EDGE,"E7.40.4"),sQuery(id+"F0.wireOp",EDGE,"E7.40.5"),sQuery(id+"F0.wireOp",EDGE,"E7.41.0"),sQuery(id+"F0.wireOp",EDGE,"E7.41.1"),sQuery(id+"F0.wireOp",EDGE,"E7.41.2"),sQuery(id+"F0.wireOp",EDGE,"E7.41.3"),sQuery(id+"F0.wireOp",EDGE,"E7.41.4"),sQuery(id+"F0.wireOp",EDGE,"E7.41.5"),sQuery(id+"F0.wireOp",EDGE,"E7.42.0"),sQuery(id+"F0.wireOp",EDGE,"E7.42.1"),sQuery(id+"F0.wireOp",EDGE,"E7.42.2"),sQuery(id+"F0.wireOp",EDGE,"E7.42.3"),sQuery(id+"F0.wireOp",EDGE,"E7.42.4"),sQuery(id+"F0.wireOp",EDGE,"E7.42.5"),sQuery(id+"F0.wireOp",EDGE,"E7.43.0"),sQuery(id+"F0.wireOp",EDGE,"E7.43.1"),sQuery(id+"F0.wireOp",EDGE,"E7.43.2"),sQuery(id+"F0.wireOp",EDGE,"E7.43.3"),sQuery(id+"F0.wireOp",EDGE,"E7.43.4"),sQuery(id+"F0.wireOp",EDGE,"E7.43.5")])],"isStart":false})]});}
            var Q9;
            {var subQ0=sQuery(id+"F0.wireOp",EDGE,"E7.25.0");Q9=makeQuery(id+"F2.opChamfer","BLEND_EDGE",EDGE,{"blendedFrom":[makeQuery(id+"F1.opExtrude","CAP_EDGE",EDGE,{"disambiguationData":[OSD([subQ0])],"isStart":false}),makeQuery(id+"F1.opExtrude","CAP_FACE",FACE,{"disambiguationData":[OSD([sQuery(id+"F0.wireOp",EDGE,"E1"),sQuery(id+"F0.wireOp",EDGE,"E2"),sQuery(id+"F0.wireOp",EDGE,"E3"),sQuery(id+"F0.wireOp",EDGE,"E4"),sQuery(id+"F0.wireOp",EDGE,"E5"),sQuery(id+"F0.wireOp",EDGE,"E6"),sQuery(id+"F0.wireOp",EDGE,"E7.1.0"),sQuery(id+"F0.wireOp",EDGE,"E7.1.1"),sQuery(id+"F0.wireOp",EDGE,"E7.1.2"),sQuery(id+"F0.wireOp",EDGE,"E7.1.3"),sQuery(id+"F0.wireOp",EDGE,"E7.1.4"),sQuery(id+"F0.wireOp",EDGE,"E7.1.5"),sQuery(id+"F0.wireOp",EDGE,"E7.2.0"),sQuery(id+"F0.wireOp",EDGE,"E7.2.1"),sQuery(id+"F0.wireOp",EDGE,"E7.2.2"),sQuery(id+"F0.wireOp",EDGE,"E7.2.3"),sQuery(id+"F0.wireOp",EDGE,"E7.2.4"),sQuery(id+"F0.wireOp",EDGE,"E7.2.5"),sQuery(id+"F0.wireOp",EDGE,"E7.3.0"),sQuery(id+"F0.wireOp",EDGE,"E7.3.1"),sQuery(id+"F0.wireOp",EDGE,"E7.3.2"),sQuery(id+"F0.wireOp",EDGE,"E7.3.3"),sQuery(id+"F0.wireOp",EDGE,"E7.3.4"),sQuery(id+"F0.wireOp",EDGE,"E7.3.5"),sQuery(id+"F0.wireOp",EDGE,"E7.4.0"),sQuery(id+"F0.wireOp",EDGE,"E7.4.1"),sQuery(id+"F0.wireOp",EDGE,"E7.4.2"),sQuery(id+"F0.wireOp",EDGE,"E7.4.3"),sQuery(id+"F0.wireOp",EDGE,"E7.4.4"),sQuery(id+"F0.wireOp",EDGE,"E7.4.5"),sQuery(id+"F0.wireOp",EDGE,"E7.5.0"),sQuery(id+"F0.wireOp",EDGE,"E7.5.1"),sQuery(id+"F0.wireOp",EDGE,"E7.5.2"),sQuery(id+"F0.wireOp",EDGE,"E7.5.3"),sQuery(id+"F0.wireOp",EDGE,"E7.5.4"),sQuery(id+"F0.wireOp",EDGE,"E7.5.5"),sQuery(id+"F0.wireOp",EDGE,"E7.6.0"),sQuery(id+"F0.wireOp",EDGE,"E7.6.1"),sQuery(id+"F0.wireOp",EDGE,"E7.6.2"),sQuery(id+"F0.wireOp",EDGE,"E7.6.3"),sQuery(id+"F0.wireOp",EDGE,"E7.6.4"),sQuery(id+"F0.wireOp",EDGE,"E7.6.5"),sQuery(id+"F0.wireOp",EDGE,"E7.7.0"),sQuery(id+"F0.wireOp",EDGE,"E7.7.1"),sQuery(id+"F0.wireOp",EDGE,"E7.7.2"),sQuery(id+"F0.wireOp",EDGE,"E7.7.3"),sQuery(id+"F0.wireOp",EDGE,"E7.7.4"),sQuery(id+"F0.wireOp",EDGE,"E7.7.5"),sQuery(id+"F0.wireOp",EDGE,"E7.8.0"),sQuery(id+"F0.wireOp",EDGE,"E7.8.1"),sQuery(id+"F0.wireOp",EDGE,"E7.8.2"),sQuery(id+"F0.wireOp",EDGE,"E7.8.3"),sQuery(id+"F0.wireOp",EDGE,"E7.8.4"),sQuery(id+"F0.wireOp",EDGE,"E7.8.5"),sQuery(id+"F0.wireOp",EDGE,"E7.9.0"),sQuery(id+"F0.wireOp",EDGE,"E7.9.1"),sQuery(id+"F0.wireOp",EDGE,"E7.9.2"),sQuery(id+"F0.wireOp",EDGE,"E7.9.3"),sQuery(id+"F0.wireOp",EDGE,"E7.9.4"),sQuery(id+"F0.wireOp",EDGE,"E7.9.5"),sQuery(id+"F0.wireOp",EDGE,"E7.10.0"),sQuery(id+"F0.wireOp",EDGE,"E7.10.1"),sQuery(id+"F0.wireOp",EDGE,"E7.10.2"),sQuery(id+"F0.wireOp",EDGE,"E7.10.3"),sQuery(id+"F0.wireOp",EDGE,"E7.10.4"),sQuery(id+"F0.wireOp",EDGE,"E7.10.5"),sQuery(id+"F0.wireOp",EDGE,"E7.11.0"),sQuery(id+"F0.wireOp",EDGE,"E7.11.1"),sQuery(id+"F0.wireOp",EDGE,"E7.11.2"),sQuery(id+"F0.wireOp",EDGE,"E7.11.3"),sQuery(id+"F0.wireOp",EDGE,"E7.11.4"),sQuery(id+"F0.wireOp",EDGE,"E7.11.5"),sQuery(id+"F0.wireOp",EDGE,"E7.12.0"),sQuery(id+"F0.wireOp",EDGE,"E7.12.1"),sQuery(id+"F0.wireOp",EDGE,"E7.12.2"),sQuery(id+"F0.wireOp",EDGE,"E7.12.3"),sQuery(id+"F0.wireOp",EDGE,"E7.12.4"),sQuery(id+"F0.wireOp",EDGE,"E7.12.5"),sQuery(id+"F0.wireOp",EDGE,"E7.13.0"),sQuery(id+"F0.wireOp",EDGE,"E7.13.1"),sQuery(id+"F0.wireOp",EDGE,"E7.13.2"),sQuery(id+"F0.wireOp",EDGE,"E7.13.3"),sQuery(id+"F0.wireOp",EDGE,"E7.13.4"),sQuery(id+"F0.wireOp",EDGE,"E7.13.5"),sQuery(id+"F0.wireOp",EDGE,"E7.14.0"),sQuery(id+"F0.wireOp",EDGE,"E7.14.1"),sQuery(id+"F0.wireOp",EDGE,"E7.14.2"),sQuery(id+"F0.wireOp",EDGE,"E7.14.3"),sQuery(id+"F0.wireOp",EDGE,"E7.14.4"),sQuery(id+"F0.wireOp",EDGE,"E7.14.5"),sQuery(id+"F0.wireOp",EDGE,"E7.15.0"),sQuery(id+"F0.wireOp",EDGE,"E7.15.1"),sQuery(id+"F0.wireOp",EDGE,"E7.15.2"),sQuery(id+"F0.wireOp",EDGE,"E7.15.3"),sQuery(id+"F0.wireOp",EDGE,"E7.15.4"),sQuery(id+"F0.wireOp",EDGE,"E7.15.5"),sQuery(id+"F0.wireOp",EDGE,"E7.16.0"),sQuery(id+"F0.wireOp",EDGE,"E7.16.1"),sQuery(id+"F0.wireOp",EDGE,"E7.16.2"),sQuery(id+"F0.wireOp",EDGE,"E7.16.3"),sQuery(id+"F0.wireOp",EDGE,"E7.16.4"),sQuery(id+"F0.wireOp",EDGE,"E7.16.5"),sQuery(id+"F0.wireOp",EDGE,"E7.17.0"),sQuery(id+"F0.wireOp",EDGE,"E7.17.1"),sQuery(id+"F0.wireOp",EDGE,"E7.17.2"),sQuery(id+"F0.wireOp",EDGE,"E7.17.3"),sQuery(id+"F0.wireOp",EDGE,"E7.17.4"),sQuery(id+"F0.wireOp",EDGE,"E7.17.5"),sQuery(id+"F0.wireOp",EDGE,"E7.18.0"),sQuery(id+"F0.wireOp",EDGE,"E7.18.1"),sQuery(id+"F0.wireOp",EDGE,"E7.18.2"),sQuery(id+"F0.wireOp",EDGE,"E7.18.3"),sQuery(id+"F0.wireOp",EDGE,"E7.18.4"),sQuery(id+"F0.wireOp",EDGE,"E7.18.5"),sQuery(id+"F0.wireOp",EDGE,"E7.19.0"),sQuery(id+"F0.wireOp",EDGE,"E7.19.1"),sQuery(id+"F0.wireOp",EDGE,"E7.19.2"),sQuery(id+"F0.wireOp",EDGE,"E7.19.3"),sQuery(id+"F0.wireOp",EDGE,"E7.19.4"),sQuery(id+"F0.wireOp",EDGE,"E7.19.5"),sQuery(id+"F0.wireOp",EDGE,"E7.20.0"),sQuery(id+"F0.wireOp",EDGE,"E7.20.1"),sQuery(id+"F0.wireOp",EDGE,"E7.20.2"),sQuery(id+"F0.wireOp",EDGE,"E7.20.3"),sQuery(id+"F0.wireOp",EDGE,"E7.20.4"),sQuery(id+"F0.wireOp",EDGE,"E7.20.5"),sQuery(id+"F0.wireOp",EDGE,"E7.21.0"),sQuery(id+"F0.wireOp",EDGE,"E7.21.1"),sQuery(id+"F0.wireOp",EDGE,"E7.21.2"),sQuery(id+"F0.wireOp",EDGE,"E7.21.3"),sQuery(id+"F0.wireOp",EDGE,"E7.21.4"),sQuery(id+"F0.wireOp",EDGE,"E7.21.5"),sQuery(id+"F0.wireOp",EDGE,"E7.22.0"),sQuery(id+"F0.wireOp",EDGE,"E7.22.1"),sQuery(id+"F0.wireOp",EDGE,"E7.22.2"),sQuery(id+"F0.wireOp",EDGE,"E7.22.3"),sQuery(id+"F0.wireOp",EDGE,"E7.22.4"),sQuery(id+"F0.wireOp",EDGE,"E7.22.5"),sQuery(id+"F0.wireOp",EDGE,"E7.23.0"),sQuery(id+"F0.wireOp",EDGE,"E7.23.1"),sQuery(id+"F0.wireOp",EDGE,"E7.23.2"),sQuery(id+"F0.wireOp",EDGE,"E7.23.3"),sQuery(id+"F0.wireOp",EDGE,"E7.23.4"),sQuery(id+"F0.wireOp",EDGE,"E7.23.5"),sQuery(id+"F0.wireOp",EDGE,"E7.24.0"),sQuery(id+"F0.wireOp",EDGE,"E7.24.1"),sQuery(id+"F0.wireOp",EDGE,"E7.24.2"),sQuery(id+"F0.wireOp",EDGE,"E7.24.3"),sQuery(id+"F0.wireOp",EDGE,"E7.24.4"),sQuery(id+"F0.wireOp",EDGE,"E7.24.5"),subQ0,sQuery(id+"F0.wireOp",EDGE,"E7.25.1"),sQuery(id+"F0.wireOp",EDGE,"E7.25.2"),sQuery(id+"F0.wireOp",EDGE,"E7.25.3"),sQuery(id+"F0.wireOp",EDGE,"E7.25.4"),sQuery(id+"F0.wireOp",EDGE,"E7.25.5"),sQuery(id+"F0.wireOp",EDGE,"E7.26.0"),sQuery(id+"F0.wireOp",EDGE,"E7.26.1"),sQuery(id+"F0.wireOp",EDGE,"E7.26.2"),sQuery(id+"F0.wireOp",EDGE,"E7.26.3"),sQuery(id+"F0.wireOp",EDGE,"E7.26.4"),sQuery(id+"F0.wireOp",EDGE,"E7.26.5"),sQuery(id+"F0.wireOp",EDGE,"E7.27.0"),sQuery(id+"F0.wireOp",EDGE,"E7.27.1"),sQuery(id+"F0.wireOp",EDGE,"E7.27.2"),sQuery(id+"F0.wireOp",EDGE,"E7.27.3"),sQuery(id+"F0.wireOp",EDGE,"E7.27.4"),sQuery(id+"F0.wireOp",EDGE,"E7.27.5"),sQuery(id+"F0.wireOp",EDGE,"E7.28.0"),sQuery(id+"F0.wireOp",EDGE,"E7.28.1"),sQuery(id+"F0.wireOp",EDGE,"E7.28.2"),sQuery(id+"F0.wireOp",EDGE,"E7.28.3"),sQuery(id+"F0.wireOp",EDGE,"E7.28.4"),sQuery(id+"F0.wireOp",EDGE,"E7.28.5"),sQuery(id+"F0.wireOp",EDGE,"E7.29.0"),sQuery(id+"F0.wireOp",EDGE,"E7.29.1"),sQuery(id+"F0.wireOp",EDGE,"E7.29.2"),sQuery(id+"F0.wireOp",EDGE,"E7.29.3"),sQuery(id+"F0.wireOp",EDGE,"E7.29.4"),sQuery(id+"F0.wireOp",EDGE,"E7.29.5"),sQuery(id+"F0.wireOp",EDGE,"E7.30.0"),sQuery(id+"F0.wireOp",EDGE,"E7.30.1"),sQuery(id+"F0.wireOp",EDGE,"E7.30.2"),sQuery(id+"F0.wireOp",EDGE,"E7.30.3"),sQuery(id+"F0.wireOp",EDGE,"E7.30.4"),sQuery(id+"F0.wireOp",EDGE,"E7.30.5"),sQuery(id+"F0.wireOp",EDGE,"E7.31.0"),sQuery(id+"F0.wireOp",EDGE,"E7.31.1"),sQuery(id+"F0.wireOp",EDGE,"E7.31.2"),sQuery(id+"F0.wireOp",EDGE,"E7.31.3"),sQuery(id+"F0.wireOp",EDGE,"E7.31.4"),sQuery(id+"F0.wireOp",EDGE,"E7.31.5"),sQuery(id+"F0.wireOp",EDGE,"E7.32.0"),sQuery(id+"F0.wireOp",EDGE,"E7.32.1"),sQuery(id+"F0.wireOp",EDGE,"E7.32.2"),sQuery(id+"F0.wireOp",EDGE,"E7.32.3"),sQuery(id+"F0.wireOp",EDGE,"E7.32.4"),sQuery(id+"F0.wireOp",EDGE,"E7.32.5"),sQuery(id+"F0.wireOp",EDGE,"E7.33.0"),sQuery(id+"F0.wireOp",EDGE,"E7.33.1"),sQuery(id+"F0.wireOp",EDGE,"E7.33.2"),sQuery(id+"F0.wireOp",EDGE,"E7.33.3"),sQuery(id+"F0.wireOp",EDGE,"E7.33.4"),sQuery(id+"F0.wireOp",EDGE,"E7.33.5"),sQuery(id+"F0.wireOp",EDGE,"E7.34.0"),sQuery(id+"F0.wireOp",EDGE,"E7.34.1"),sQuery(id+"F0.wireOp",EDGE,"E7.34.2"),sQuery(id+"F0.wireOp",EDGE,"E7.34.3"),sQuery(id+"F0.wireOp",EDGE,"E7.34.4"),sQuery(id+"F0.wireOp",EDGE,"E7.34.5"),sQuery(id+"F0.wireOp",EDGE,"E7.35.0"),sQuery(id+"F0.wireOp",EDGE,"E7.35.1"),sQuery(id+"F0.wireOp",EDGE,"E7.35.2"),sQuery(id+"F0.wireOp",EDGE,"E7.35.3"),sQuery(id+"F0.wireOp",EDGE,"E7.35.4"),sQuery(id+"F0.wireOp",EDGE,"E7.35.5"),sQuery(id+"F0.wireOp",EDGE,"E7.36.0"),sQuery(id+"F0.wireOp",EDGE,"E7.36.1"),sQuery(id+"F0.wireOp",EDGE,"E7.36.2"),sQuery(id+"F0.wireOp",EDGE,"E7.36.3"),sQuery(id+"F0.wireOp",EDGE,"E7.36.4"),sQuery(id+"F0.wireOp",EDGE,"E7.36.5"),sQuery(id+"F0.wireOp",EDGE,"E7.37.0"),sQuery(id+"F0.wireOp",EDGE,"E7.37.1"),sQuery(id+"F0.wireOp",EDGE,"E7.37.2"),sQuery(id+"F0.wireOp",EDGE,"E7.37.3"),sQuery(id+"F0.wireOp",EDGE,"E7.37.4"),sQuery(id+"F0.wireOp",EDGE,"E7.37.5"),sQuery(id+"F0.wireOp",EDGE,"E7.38.0"),sQuery(id+"F0.wireOp",EDGE,"E7.38.1"),sQuery(id+"F0.wireOp",EDGE,"E7.38.2"),sQuery(id+"F0.wireOp",EDGE,"E7.38.3"),sQuery(id+"F0.wireOp",EDGE,"E7.38.4"),sQuery(id+"F0.wireOp",EDGE,"E7.38.5"),sQuery(id+"F0.wireOp",EDGE,"E7.39.0"),sQuery(id+"F0.wireOp",EDGE,"E7.39.1"),sQuery(id+"F0.wireOp",EDGE,"E7.39.2"),sQuery(id+"F0.wireOp",EDGE,"E7.39.3"),sQuery(id+"F0.wireOp",EDGE,"E7.39.4"),sQuery(id+"F0.wireOp",EDGE,"E7.39.5"),sQuery(id+"F0.wireOp",EDGE,"E7.40.0"),sQuery(id+"F0.wireOp",EDGE,"E7.40.1"),sQuery(id+"F0.wireOp",EDGE,"E7.40.2"),sQuery(id+"F0.wireOp",EDGE,"E7.40.3"),sQuery(id+"F0.wireOp",EDGE,"E7.40.4"),sQuery(id+"F0.wireOp",EDGE,"E7.40.5"),sQuery(id+"F0.wireOp",EDGE,"E7.41.0"),sQuery(id+"F0.wireOp",EDGE,"E7.41.1"),sQuery(id+"F0.wireOp",EDGE,"E7.41.2"),sQuery(id+"F0.wireOp",EDGE,"E7.41.3"),sQuery(id+"F0.wireOp",EDGE,"E7.41.4"),sQuery(id+"F0.wireOp",EDGE,"E7.41.5"),sQuery(id+"F0.wireOp",EDGE,"E7.42.0"),sQuery(id+"F0.wireOp",EDGE,"E7.42.1"),sQuery(id+"F0.wireOp",EDGE,"E7.42.2"),sQuery(id+"F0.wireOp",EDGE,"E7.42.3"),sQuery(id+"F0.wireOp",EDGE,"E7.42.4"),sQuery(id+"F0.wireOp",EDGE,"E7.42.5"),sQuery(id+"F0.wireOp",EDGE,"E7.43.0"),sQuery(id+"F0.wireOp",EDGE,"E7.43.1"),sQuery(id+"F0.wireOp",EDGE,"E7.43.2"),sQuery(id+"F0.wireOp",EDGE,"E7.43.3"),sQuery(id+"F0.wireOp",EDGE,"E7.43.4"),sQuery(id+"F0.wireOp",EDGE,"E7.43.5")])],"isStart":false})],"blendedInto":[makeQuery(id+"F1.opExtrude","CAP_FACE",FACE,{"disambiguationData":[OSD([sQuery(id+"F0.wireOp",EDGE,"E1"),sQuery(id+"F0.wireOp",EDGE,"E2"),sQuery(id+"F0.wireOp",EDGE,"E3"),sQuery(id+"F0.wireOp",EDGE,"E4"),sQuery(id+"F0.wireOp",EDGE,"E5"),sQuery(id+"F0.wireOp",EDGE,"E6"),sQuery(id+"F0.wireOp",EDGE,"E7.1.0"),sQuery(id+"F0.wireOp",EDGE,"E7.1.1"),sQuery(id+"F0.wireOp",EDGE,"E7.1.2"),sQuery(id+"F0.wireOp",EDGE,"E7.1.3"),sQuery(id+"F0.wireOp",EDGE,"E7.1.4"),sQuery(id+"F0.wireOp",EDGE,"E7.1.5"),sQuery(id+"F0.wireOp",EDGE,"E7.2.0"),sQuery(id+"F0.wireOp",EDGE,"E7.2.1"),sQuery(id+"F0.wireOp",EDGE,"E7.2.2"),sQuery(id+"F0.wireOp",EDGE,"E7.2.3"),sQuery(id+"F0.wireOp",EDGE,"E7.2.4"),sQuery(id+"F0.wireOp",EDGE,"E7.2.5"),sQuery(id+"F0.wireOp",EDGE,"E7.3.0"),sQuery(id+"F0.wireOp",EDGE,"E7.3.1"),sQuery(id+"F0.wireOp",EDGE,"E7.3.2"),sQuery(id+"F0.wireOp",EDGE,"E7.3.3"),sQuery(id+"F0.wireOp",EDGE,"E7.3.4"),sQuery(id+"F0.wireOp",EDGE,"E7.3.5"),sQuery(id+"F0.wireOp",EDGE,"E7.4.0"),sQuery(id+"F0.wireOp",EDGE,"E7.4.1"),sQuery(id+"F0.wireOp",EDGE,"E7.4.2"),sQuery(id+"F0.wireOp",EDGE,"E7.4.3"),sQuery(id+"F0.wireOp",EDGE,"E7.4.4"),sQuery(id+"F0.wireOp",EDGE,"E7.4.5"),sQuery(id+"F0.wireOp",EDGE,"E7.5.0"),sQuery(id+"F0.wireOp",EDGE,"E7.5.1"),sQuery(id+"F0.wireOp",EDGE,"E7.5.2"),sQuery(id+"F0.wireOp",EDGE,"E7.5.3"),sQuery(id+"F0.wireOp",EDGE,"E7.5.4"),sQuery(id+"F0.wireOp",EDGE,"E7.5.5"),sQuery(id+"F0.wireOp",EDGE,"E7.6.0"),sQuery(id+"F0.wireOp",EDGE,"E7.6.1"),sQuery(id+"F0.wireOp",EDGE,"E7.6.2"),sQuery(id+"F0.wireOp",EDGE,"E7.6.3"),sQuery(id+"F0.wireOp",EDGE,"E7.6.4"),sQuery(id+"F0.wireOp",EDGE,"E7.6.5"),sQuery(id+"F0.wireOp",EDGE,"E7.7.0"),sQuery(id+"F0.wireOp",EDGE,"E7.7.1"),sQuery(id+"F0.wireOp",EDGE,"E7.7.2"),sQuery(id+"F0.wireOp",EDGE,"E7.7.3"),sQuery(id+"F0.wireOp",EDGE,"E7.7.4"),sQuery(id+"F0.wireOp",EDGE,"E7.7.5"),sQuery(id+"F0.wireOp",EDGE,"E7.8.0"),sQuery(id+"F0.wireOp",EDGE,"E7.8.1"),sQuery(id+"F0.wireOp",EDGE,"E7.8.2"),sQuery(id+"F0.wireOp",EDGE,"E7.8.3"),sQuery(id+"F0.wireOp",EDGE,"E7.8.4"),sQuery(id+"F0.wireOp",EDGE,"E7.8.5"),sQuery(id+"F0.wireOp",EDGE,"E7.9.0"),sQuery(id+"F0.wireOp",EDGE,"E7.9.1"),sQuery(id+"F0.wireOp",EDGE,"E7.9.2"),sQuery(id+"F0.wireOp",EDGE,"E7.9.3"),sQuery(id+"F0.wireOp",EDGE,"E7.9.4"),sQuery(id+"F0.wireOp",EDGE,"E7.9.5"),sQuery(id+"F0.wireOp",EDGE,"E7.10.0"),sQuery(id+"F0.wireOp",EDGE,"E7.10.1"),sQuery(id+"F0.wireOp",EDGE,"E7.10.2"),sQuery(id+"F0.wireOp",EDGE,"E7.10.3"),sQuery(id+"F0.wireOp",EDGE,"E7.10.4"),sQuery(id+"F0.wireOp",EDGE,"E7.10.5"),sQuery(id+"F0.wireOp",EDGE,"E7.11.0"),sQuery(id+"F0.wireOp",EDGE,"E7.11.1"),sQuery(id+"F0.wireOp",EDGE,"E7.11.2"),sQuery(id+"F0.wireOp",EDGE,"E7.11.3"),sQuery(id+"F0.wireOp",EDGE,"E7.11.4"),sQuery(id+"F0.wireOp",EDGE,"E7.11.5"),sQuery(id+"F0.wireOp",EDGE,"E7.12.0"),sQuery(id+"F0.wireOp",EDGE,"E7.12.1"),sQuery(id+"F0.wireOp",EDGE,"E7.12.2"),sQuery(id+"F0.wireOp",EDGE,"E7.12.3"),sQuery(id+"F0.wireOp",EDGE,"E7.12.4"),sQuery(id+"F0.wireOp",EDGE,"E7.12.5"),sQuery(id+"F0.wireOp",EDGE,"E7.13.0"),sQuery(id+"F0.wireOp",EDGE,"E7.13.1"),sQuery(id+"F0.wireOp",EDGE,"E7.13.2"),sQuery(id+"F0.wireOp",EDGE,"E7.13.3"),sQuery(id+"F0.wireOp",EDGE,"E7.13.4"),sQuery(id+"F0.wireOp",EDGE,"E7.13.5"),sQuery(id+"F0.wireOp",EDGE,"E7.14.0"),sQuery(id+"F0.wireOp",EDGE,"E7.14.1"),sQuery(id+"F0.wireOp",EDGE,"E7.14.2"),sQuery(id+"F0.wireOp",EDGE,"E7.14.3"),sQuery(id+"F0.wireOp",EDGE,"E7.14.4"),sQuery(id+"F0.wireOp",EDGE,"E7.14.5"),sQuery(id+"F0.wireOp",EDGE,"E7.15.0"),sQuery(id+"F0.wireOp",EDGE,"E7.15.1"),sQuery(id+"F0.wireOp",EDGE,"E7.15.2"),sQuery(id+"F0.wireOp",EDGE,"E7.15.3"),sQuery(id+"F0.wireOp",EDGE,"E7.15.4"),sQuery(id+"F0.wireOp",EDGE,"E7.15.5"),sQuery(id+"F0.wireOp",EDGE,"E7.16.0"),sQuery(id+"F0.wireOp",EDGE,"E7.16.1"),sQuery(id+"F0.wireOp",EDGE,"E7.16.2"),sQuery(id+"F0.wireOp",EDGE,"E7.16.3"),sQuery(id+"F0.wireOp",EDGE,"E7.16.4"),sQuery(id+"F0.wireOp",EDGE,"E7.16.5"),sQuery(id+"F0.wireOp",EDGE,"E7.17.0"),sQuery(id+"F0.wireOp",EDGE,"E7.17.1"),sQuery(id+"F0.wireOp",EDGE,"E7.17.2"),sQuery(id+"F0.wireOp",EDGE,"E7.17.3"),sQuery(id+"F0.wireOp",EDGE,"E7.17.4"),sQuery(id+"F0.wireOp",EDGE,"E7.17.5"),sQuery(id+"F0.wireOp",EDGE,"E7.18.0"),sQuery(id+"F0.wireOp",EDGE,"E7.18.1"),sQuery(id+"F0.wireOp",EDGE,"E7.18.2"),sQuery(id+"F0.wireOp",EDGE,"E7.18.3"),sQuery(id+"F0.wireOp",EDGE,"E7.18.4"),sQuery(id+"F0.wireOp",EDGE,"E7.18.5"),sQuery(id+"F0.wireOp",EDGE,"E7.19.0"),sQuery(id+"F0.wireOp",EDGE,"E7.19.1"),sQuery(id+"F0.wireOp",EDGE,"E7.19.2"),sQuery(id+"F0.wireOp",EDGE,"E7.19.3"),sQuery(id+"F0.wireOp",EDGE,"E7.19.4"),sQuery(id+"F0.wireOp",EDGE,"E7.19.5"),sQuery(id+"F0.wireOp",EDGE,"E7.20.0"),sQuery(id+"F0.wireOp",EDGE,"E7.20.1"),sQuery(id+"F0.wireOp",EDGE,"E7.20.2"),sQuery(id+"F0.wireOp",EDGE,"E7.20.3"),sQuery(id+"F0.wireOp",EDGE,"E7.20.4"),sQuery(id+"F0.wireOp",EDGE,"E7.20.5"),sQuery(id+"F0.wireOp",EDGE,"E7.21.0"),sQuery(id+"F0.wireOp",EDGE,"E7.21.1"),sQuery(id+"F0.wireOp",EDGE,"E7.21.2"),sQuery(id+"F0.wireOp",EDGE,"E7.21.3"),sQuery(id+"F0.wireOp",EDGE,"E7.21.4"),sQuery(id+"F0.wireOp",EDGE,"E7.21.5"),sQuery(id+"F0.wireOp",EDGE,"E7.22.0"),sQuery(id+"F0.wireOp",EDGE,"E7.22.1"),sQuery(id+"F0.wireOp",EDGE,"E7.22.2"),sQuery(id+"F0.wireOp",EDGE,"E7.22.3"),sQuery(id+"F0.wireOp",EDGE,"E7.22.4"),sQuery(id+"F0.wireOp",EDGE,"E7.22.5"),sQuery(id+"F0.wireOp",EDGE,"E7.23.0"),sQuery(id+"F0.wireOp",EDGE,"E7.23.1"),sQuery(id+"F0.wireOp",EDGE,"E7.23.2"),sQuery(id+"F0.wireOp",EDGE,"E7.23.3"),sQuery(id+"F0.wireOp",EDGE,"E7.23.4"),sQuery(id+"F0.wireOp",EDGE,"E7.23.5"),sQuery(id+"F0.wireOp",EDGE,"E7.24.0"),sQuery(id+"F0.wireOp",EDGE,"E7.24.1"),sQuery(id+"F0.wireOp",EDGE,"E7.24.2"),sQuery(id+"F0.wireOp",EDGE,"E7.24.3"),sQuery(id+"F0.wireOp",EDGE,"E7.24.4"),sQuery(id+"F0.wireOp",EDGE,"E7.24.5"),subQ0,sQuery(id+"F0.wireOp",EDGE,"E7.25.1"),sQuery(id+"F0.wireOp",EDGE,"E7.25.2"),sQuery(id+"F0.wireOp",EDGE,"E7.25.3"),sQuery(id+"F0.wireOp",EDGE,"E7.25.4"),sQuery(id+"F0.wireOp",EDGE,"E7.25.5"),sQuery(id+"F0.wireOp",EDGE,"E7.26.0"),sQuery(id+"F0.wireOp",EDGE,"E7.26.1"),sQuery(id+"F0.wireOp",EDGE,"E7.26.2"),sQuery(id+"F0.wireOp",EDGE,"E7.26.3"),sQuery(id+"F0.wireOp",EDGE,"E7.26.4"),sQuery(id+"F0.wireOp",EDGE,"E7.26.5"),sQuery(id+"F0.wireOp",EDGE,"E7.27.0"),sQuery(id+"F0.wireOp",EDGE,"E7.27.1"),sQuery(id+"F0.wireOp",EDGE,"E7.27.2"),sQuery(id+"F0.wireOp",EDGE,"E7.27.3"),sQuery(id+"F0.wireOp",EDGE,"E7.27.4"),sQuery(id+"F0.wireOp",EDGE,"E7.27.5"),sQuery(id+"F0.wireOp",EDGE,"E7.28.0"),sQuery(id+"F0.wireOp",EDGE,"E7.28.1"),sQuery(id+"F0.wireOp",EDGE,"E7.28.2"),sQuery(id+"F0.wireOp",EDGE,"E7.28.3"),sQuery(id+"F0.wireOp",EDGE,"E7.28.4"),sQuery(id+"F0.wireOp",EDGE,"E7.28.5"),sQuery(id+"F0.wireOp",EDGE,"E7.29.0"),sQuery(id+"F0.wireOp",EDGE,"E7.29.1"),sQuery(id+"F0.wireOp",EDGE,"E7.29.2"),sQuery(id+"F0.wireOp",EDGE,"E7.29.3"),sQuery(id+"F0.wireOp",EDGE,"E7.29.4"),sQuery(id+"F0.wireOp",EDGE,"E7.29.5"),sQuery(id+"F0.wireOp",EDGE,"E7.30.0"),sQuery(id+"F0.wireOp",EDGE,"E7.30.1"),sQuery(id+"F0.wireOp",EDGE,"E7.30.2"),sQuery(id+"F0.wireOp",EDGE,"E7.30.3"),sQuery(id+"F0.wireOp",EDGE,"E7.30.4"),sQuery(id+"F0.wireOp",EDGE,"E7.30.5"),sQuery(id+"F0.wireOp",EDGE,"E7.31.0"),sQuery(id+"F0.wireOp",EDGE,"E7.31.1"),sQuery(id+"F0.wireOp",EDGE,"E7.31.2"),sQuery(id+"F0.wireOp",EDGE,"E7.31.3"),sQuery(id+"F0.wireOp",EDGE,"E7.31.4"),sQuery(id+"F0.wireOp",EDGE,"E7.31.5"),sQuery(id+"F0.wireOp",EDGE,"E7.32.0"),sQuery(id+"F0.wireOp",EDGE,"E7.32.1"),sQuery(id+"F0.wireOp",EDGE,"E7.32.2"),sQuery(id+"F0.wireOp",EDGE,"E7.32.3"),sQuery(id+"F0.wireOp",EDGE,"E7.32.4"),sQuery(id+"F0.wireOp",EDGE,"E7.32.5"),sQuery(id+"F0.wireOp",EDGE,"E7.33.0"),sQuery(id+"F0.wireOp",EDGE,"E7.33.1"),sQuery(id+"F0.wireOp",EDGE,"E7.33.2"),sQuery(id+"F0.wireOp",EDGE,"E7.33.3"),sQuery(id+"F0.wireOp",EDGE,"E7.33.4"),sQuery(id+"F0.wireOp",EDGE,"E7.33.5"),sQuery(id+"F0.wireOp",EDGE,"E7.34.0"),sQuery(id+"F0.wireOp",EDGE,"E7.34.1"),sQuery(id+"F0.wireOp",EDGE,"E7.34.2"),sQuery(id+"F0.wireOp",EDGE,"E7.34.3"),sQuery(id+"F0.wireOp",EDGE,"E7.34.4"),sQuery(id+"F0.wireOp",EDGE,"E7.34.5"),sQuery(id+"F0.wireOp",EDGE,"E7.35.0"),sQuery(id+"F0.wireOp",EDGE,"E7.35.1"),sQuery(id+"F0.wireOp",EDGE,"E7.35.2"),sQuery(id+"F0.wireOp",EDGE,"E7.35.3"),sQuery(id+"F0.wireOp",EDGE,"E7.35.4"),sQuery(id+"F0.wireOp",EDGE,"E7.35.5"),sQuery(id+"F0.wireOp",EDGE,"E7.36.0"),sQuery(id+"F0.wireOp",EDGE,"E7.36.1"),sQuery(id+"F0.wireOp",EDGE,"E7.36.2"),sQuery(id+"F0.wireOp",EDGE,"E7.36.3"),sQuery(id+"F0.wireOp",EDGE,"E7.36.4"),sQuery(id+"F0.wireOp",EDGE,"E7.36.5"),sQuery(id+"F0.wireOp",EDGE,"E7.37.0"),sQuery(id+"F0.wireOp",EDGE,"E7.37.1"),sQuery(id+"F0.wireOp",EDGE,"E7.37.2"),sQuery(id+"F0.wireOp",EDGE,"E7.37.3"),sQuery(id+"F0.wireOp",EDGE,"E7.37.4"),sQuery(id+"F0.wireOp",EDGE,"E7.37.5"),sQuery(id+"F0.wireOp",EDGE,"E7.38.0"),sQuery(id+"F0.wireOp",EDGE,"E7.38.1"),sQuery(id+"F0.wireOp",EDGE,"E7.38.2"),sQuery(id+"F0.wireOp",EDGE,"E7.38.3"),sQuery(id+"F0.wireOp",EDGE,"E7.38.4"),sQuery(id+"F0.wireOp",EDGE,"E7.38.5"),sQuery(id+"F0.wireOp",EDGE,"E7.39.0"),sQuery(id+"F0.wireOp",EDGE,"E7.39.1"),sQuery(id+"F0.wireOp",EDGE,"E7.39.2"),sQuery(id+"F0.wireOp",EDGE,"E7.39.3"),sQuery(id+"F0.wireOp",EDGE,"E7.39.4"),sQuery(id+"F0.wireOp",EDGE,"E7.39.5"),sQuery(id+"F0.wireOp",EDGE,"E7.40.0"),sQuery(id+"F0.wireOp",EDGE,"E7.40.1"),sQuery(id+"F0.wireOp",EDGE,"E7.40.2"),sQuery(id+"F0.wireOp",EDGE,"E7.40.3"),sQuery(id+"F0.wireOp",EDGE,"E7.40.4"),sQuery(id+"F0.wireOp",EDGE,"E7.40.5"),sQuery(id+"F0.wireOp",EDGE,"E7.41.0"),sQuery(id+"F0.wireOp",EDGE,"E7.41.1"),sQuery(id+"F0.wireOp",EDGE,"E7.41.2"),sQuery(id+"F0.wireOp",EDGE,"E7.41.3"),sQuery(id+"F0.wireOp",EDGE,"E7.41.4"),sQuery(id+"F0.wireOp",EDGE,"E7.41.5"),sQuery(id+"F0.wireOp",EDGE,"E7.42.0"),sQuery(id+"F0.wireOp",EDGE,"E7.42.1"),sQuery(id+"F0.wireOp",EDGE,"E7.42.2"),sQuery(id+"F0.wireOp",EDGE,"E7.42.3"),sQuery(id+"F0.wireOp",EDGE,"E7.42.4"),sQuery(id+"F0.wireOp",EDGE,"E7.42.5"),sQuery(id+"F0.wireOp",EDGE,"E7.43.0"),sQuery(id+"F0.wireOp",EDGE,"E7.43.1"),sQuery(id+"F0.wireOp",EDGE,"E7.43.2"),sQuery(id+"F0.wireOp",EDGE,"E7.43.3"),sQuery(id+"F0.wireOp",EDGE,"E7.43.4"),sQuery(id+"F0.wireOp",EDGE,"E7.43.5")])],"isStart":false})]});}
            var Q10;
            {var subQ0=sQuery(id+"F0.wireOp",EDGE,"E7.23.0");Q10=makeQuery(id+"F2.opChamfer","BLEND_EDGE",EDGE,{"blendedFrom":[makeQuery(id+"F1.opExtrude","CAP_EDGE",EDGE,{"disambiguationData":[OSD([subQ0])],"isStart":false}),makeQuery(id+"F1.opExtrude","CAP_FACE",FACE,{"disambiguationData":[OSD([sQuery(id+"F0.wireOp",EDGE,"E1"),sQuery(id+"F0.wireOp",EDGE,"E2"),sQuery(id+"F0.wireOp",EDGE,"E3"),sQuery(id+"F0.wireOp",EDGE,"E4"),sQuery(id+"F0.wireOp",EDGE,"E5"),sQuery(id+"F0.wireOp",EDGE,"E6"),sQuery(id+"F0.wireOp",EDGE,"E7.1.0"),sQuery(id+"F0.wireOp",EDGE,"E7.1.1"),sQuery(id+"F0.wireOp",EDGE,"E7.1.2"),sQuery(id+"F0.wireOp",EDGE,"E7.1.3"),sQuery(id+"F0.wireOp",EDGE,"E7.1.4"),sQuery(id+"F0.wireOp",EDGE,"E7.1.5"),sQuery(id+"F0.wireOp",EDGE,"E7.2.0"),sQuery(id+"F0.wireOp",EDGE,"E7.2.1"),sQuery(id+"F0.wireOp",EDGE,"E7.2.2"),sQuery(id+"F0.wireOp",EDGE,"E7.2.3"),sQuery(id+"F0.wireOp",EDGE,"E7.2.4"),sQuery(id+"F0.wireOp",EDGE,"E7.2.5"),sQuery(id+"F0.wireOp",EDGE,"E7.3.0"),sQuery(id+"F0.wireOp",EDGE,"E7.3.1"),sQuery(id+"F0.wireOp",EDGE,"E7.3.2"),sQuery(id+"F0.wireOp",EDGE,"E7.3.3"),sQuery(id+"F0.wireOp",EDGE,"E7.3.4"),sQuery(id+"F0.wireOp",EDGE,"E7.3.5"),sQuery(id+"F0.wireOp",EDGE,"E7.4.0"),sQuery(id+"F0.wireOp",EDGE,"E7.4.1"),sQuery(id+"F0.wireOp",EDGE,"E7.4.2"),sQuery(id+"F0.wireOp",EDGE,"E7.4.3"),sQuery(id+"F0.wireOp",EDGE,"E7.4.4"),sQuery(id+"F0.wireOp",EDGE,"E7.4.5"),sQuery(id+"F0.wireOp",EDGE,"E7.5.0"),sQuery(id+"F0.wireOp",EDGE,"E7.5.1"),sQuery(id+"F0.wireOp",EDGE,"E7.5.2"),sQuery(id+"F0.wireOp",EDGE,"E7.5.3"),sQuery(id+"F0.wireOp",EDGE,"E7.5.4"),sQuery(id+"F0.wireOp",EDGE,"E7.5.5"),sQuery(id+"F0.wireOp",EDGE,"E7.6.0"),sQuery(id+"F0.wireOp",EDGE,"E7.6.1"),sQuery(id+"F0.wireOp",EDGE,"E7.6.2"),sQuery(id+"F0.wireOp",EDGE,"E7.6.3"),sQuery(id+"F0.wireOp",EDGE,"E7.6.4"),sQuery(id+"F0.wireOp",EDGE,"E7.6.5"),sQuery(id+"F0.wireOp",EDGE,"E7.7.0"),sQuery(id+"F0.wireOp",EDGE,"E7.7.1"),sQuery(id+"F0.wireOp",EDGE,"E7.7.2"),sQuery(id+"F0.wireOp",EDGE,"E7.7.3"),sQuery(id+"F0.wireOp",EDGE,"E7.7.4"),sQuery(id+"F0.wireOp",EDGE,"E7.7.5"),sQuery(id+"F0.wireOp",EDGE,"E7.8.0"),sQuery(id+"F0.wireOp",EDGE,"E7.8.1"),sQuery(id+"F0.wireOp",EDGE,"E7.8.2"),sQuery(id+"F0.wireOp",EDGE,"E7.8.3"),sQuery(id+"F0.wireOp",EDGE,"E7.8.4"),sQuery(id+"F0.wireOp",EDGE,"E7.8.5"),sQuery(id+"F0.wireOp",EDGE,"E7.9.0"),sQuery(id+"F0.wireOp",EDGE,"E7.9.1"),sQuery(id+"F0.wireOp",EDGE,"E7.9.2"),sQuery(id+"F0.wireOp",EDGE,"E7.9.3"),sQuery(id+"F0.wireOp",EDGE,"E7.9.4"),sQuery(id+"F0.wireOp",EDGE,"E7.9.5"),sQuery(id+"F0.wireOp",EDGE,"E7.10.0"),sQuery(id+"F0.wireOp",EDGE,"E7.10.1"),sQuery(id+"F0.wireOp",EDGE,"E7.10.2"),sQuery(id+"F0.wireOp",EDGE,"E7.10.3"),sQuery(id+"F0.wireOp",EDGE,"E7.10.4"),sQuery(id+"F0.wireOp",EDGE,"E7.10.5"),sQuery(id+"F0.wireOp",EDGE,"E7.11.0"),sQuery(id+"F0.wireOp",EDGE,"E7.11.1"),sQuery(id+"F0.wireOp",EDGE,"E7.11.2"),sQuery(id+"F0.wireOp",EDGE,"E7.11.3"),sQuery(id+"F0.wireOp",EDGE,"E7.11.4"),sQuery(id+"F0.wireOp",EDGE,"E7.11.5"),sQuery(id+"F0.wireOp",EDGE,"E7.12.0"),sQuery(id+"F0.wireOp",EDGE,"E7.12.1"),sQuery(id+"F0.wireOp",EDGE,"E7.12.2"),sQuery(id+"F0.wireOp",EDGE,"E7.12.3"),sQuery(id+"F0.wireOp",EDGE,"E7.12.4"),sQuery(id+"F0.wireOp",EDGE,"E7.12.5"),sQuery(id+"F0.wireOp",EDGE,"E7.13.0"),sQuery(id+"F0.wireOp",EDGE,"E7.13.1"),sQuery(id+"F0.wireOp",EDGE,"E7.13.2"),sQuery(id+"F0.wireOp",EDGE,"E7.13.3"),sQuery(id+"F0.wireOp",EDGE,"E7.13.4"),sQuery(id+"F0.wireOp",EDGE,"E7.13.5"),sQuery(id+"F0.wireOp",EDGE,"E7.14.0"),sQuery(id+"F0.wireOp",EDGE,"E7.14.1"),sQuery(id+"F0.wireOp",EDGE,"E7.14.2"),sQuery(id+"F0.wireOp",EDGE,"E7.14.3"),sQuery(id+"F0.wireOp",EDGE,"E7.14.4"),sQuery(id+"F0.wireOp",EDGE,"E7.14.5"),sQuery(id+"F0.wireOp",EDGE,"E7.15.0"),sQuery(id+"F0.wireOp",EDGE,"E7.15.1"),sQuery(id+"F0.wireOp",EDGE,"E7.15.2"),sQuery(id+"F0.wireOp",EDGE,"E7.15.3"),sQuery(id+"F0.wireOp",EDGE,"E7.15.4"),sQuery(id+"F0.wireOp",EDGE,"E7.15.5"),sQuery(id+"F0.wireOp",EDGE,"E7.16.0"),sQuery(id+"F0.wireOp",EDGE,"E7.16.1"),sQuery(id+"F0.wireOp",EDGE,"E7.16.2"),sQuery(id+"F0.wireOp",EDGE,"E7.16.3"),sQuery(id+"F0.wireOp",EDGE,"E7.16.4"),sQuery(id+"F0.wireOp",EDGE,"E7.16.5"),sQuery(id+"F0.wireOp",EDGE,"E7.17.0"),sQuery(id+"F0.wireOp",EDGE,"E7.17.1"),sQuery(id+"F0.wireOp",EDGE,"E7.17.2"),sQuery(id+"F0.wireOp",EDGE,"E7.17.3"),sQuery(id+"F0.wireOp",EDGE,"E7.17.4"),sQuery(id+"F0.wireOp",EDGE,"E7.17.5"),sQuery(id+"F0.wireOp",EDGE,"E7.18.0"),sQuery(id+"F0.wireOp",EDGE,"E7.18.1"),sQuery(id+"F0.wireOp",EDGE,"E7.18.2"),sQuery(id+"F0.wireOp",EDGE,"E7.18.3"),sQuery(id+"F0.wireOp",EDGE,"E7.18.4"),sQuery(id+"F0.wireOp",EDGE,"E7.18.5"),sQuery(id+"F0.wireOp",EDGE,"E7.19.0"),sQuery(id+"F0.wireOp",EDGE,"E7.19.1"),sQuery(id+"F0.wireOp",EDGE,"E7.19.2"),sQuery(id+"F0.wireOp",EDGE,"E7.19.3"),sQuery(id+"F0.wireOp",EDGE,"E7.19.4"),sQuery(id+"F0.wireOp",EDGE,"E7.19.5"),sQuery(id+"F0.wireOp",EDGE,"E7.20.0"),sQuery(id+"F0.wireOp",EDGE,"E7.20.1"),sQuery(id+"F0.wireOp",EDGE,"E7.20.2"),sQuery(id+"F0.wireOp",EDGE,"E7.20.3"),sQuery(id+"F0.wireOp",EDGE,"E7.20.4"),sQuery(id+"F0.wireOp",EDGE,"E7.20.5"),sQuery(id+"F0.wireOp",EDGE,"E7.21.0"),sQuery(id+"F0.wireOp",EDGE,"E7.21.1"),sQuery(id+"F0.wireOp",EDGE,"E7.21.2"),sQuery(id+"F0.wireOp",EDGE,"E7.21.3"),sQuery(id+"F0.wireOp",EDGE,"E7.21.4"),sQuery(id+"F0.wireOp",EDGE,"E7.21.5"),sQuery(id+"F0.wireOp",EDGE,"E7.22.0"),sQuery(id+"F0.wireOp",EDGE,"E7.22.1"),sQuery(id+"F0.wireOp",EDGE,"E7.22.2"),sQuery(id+"F0.wireOp",EDGE,"E7.22.3"),sQuery(id+"F0.wireOp",EDGE,"E7.22.4"),sQuery(id+"F0.wireOp",EDGE,"E7.22.5"),subQ0,sQuery(id+"F0.wireOp",EDGE,"E7.23.1"),sQuery(id+"F0.wireOp",EDGE,"E7.23.2"),sQuery(id+"F0.wireOp",EDGE,"E7.23.3"),sQuery(id+"F0.wireOp",EDGE,"E7.23.4"),sQuery(id+"F0.wireOp",EDGE,"E7.23.5"),sQuery(id+"F0.wireOp",EDGE,"E7.24.0"),sQuery(id+"F0.wireOp",EDGE,"E7.24.1"),sQuery(id+"F0.wireOp",EDGE,"E7.24.2"),sQuery(id+"F0.wireOp",EDGE,"E7.24.3"),sQuery(id+"F0.wireOp",EDGE,"E7.24.4"),sQuery(id+"F0.wireOp",EDGE,"E7.24.5"),sQuery(id+"F0.wireOp",EDGE,"E7.25.0"),sQuery(id+"F0.wireOp",EDGE,"E7.25.1"),sQuery(id+"F0.wireOp",EDGE,"E7.25.2"),sQuery(id+"F0.wireOp",EDGE,"E7.25.3"),sQuery(id+"F0.wireOp",EDGE,"E7.25.4"),sQuery(id+"F0.wireOp",EDGE,"E7.25.5"),sQuery(id+"F0.wireOp",EDGE,"E7.26.0"),sQuery(id+"F0.wireOp",EDGE,"E7.26.1"),sQuery(id+"F0.wireOp",EDGE,"E7.26.2"),sQuery(id+"F0.wireOp",EDGE,"E7.26.3"),sQuery(id+"F0.wireOp",EDGE,"E7.26.4"),sQuery(id+"F0.wireOp",EDGE,"E7.26.5"),sQuery(id+"F0.wireOp",EDGE,"E7.27.0"),sQuery(id+"F0.wireOp",EDGE,"E7.27.1"),sQuery(id+"F0.wireOp",EDGE,"E7.27.2"),sQuery(id+"F0.wireOp",EDGE,"E7.27.3"),sQuery(id+"F0.wireOp",EDGE,"E7.27.4"),sQuery(id+"F0.wireOp",EDGE,"E7.27.5"),sQuery(id+"F0.wireOp",EDGE,"E7.28.0"),sQuery(id+"F0.wireOp",EDGE,"E7.28.1"),sQuery(id+"F0.wireOp",EDGE,"E7.28.2"),sQuery(id+"F0.wireOp",EDGE,"E7.28.3"),sQuery(id+"F0.wireOp",EDGE,"E7.28.4"),sQuery(id+"F0.wireOp",EDGE,"E7.28.5"),sQuery(id+"F0.wireOp",EDGE,"E7.29.0"),sQuery(id+"F0.wireOp",EDGE,"E7.29.1"),sQuery(id+"F0.wireOp",EDGE,"E7.29.2"),sQuery(id+"F0.wireOp",EDGE,"E7.29.3"),sQuery(id+"F0.wireOp",EDGE,"E7.29.4"),sQuery(id+"F0.wireOp",EDGE,"E7.29.5"),sQuery(id+"F0.wireOp",EDGE,"E7.30.0"),sQuery(id+"F0.wireOp",EDGE,"E7.30.1"),sQuery(id+"F0.wireOp",EDGE,"E7.30.2"),sQuery(id+"F0.wireOp",EDGE,"E7.30.3"),sQuery(id+"F0.wireOp",EDGE,"E7.30.4"),sQuery(id+"F0.wireOp",EDGE,"E7.30.5"),sQuery(id+"F0.wireOp",EDGE,"E7.31.0"),sQuery(id+"F0.wireOp",EDGE,"E7.31.1"),sQuery(id+"F0.wireOp",EDGE,"E7.31.2"),sQuery(id+"F0.wireOp",EDGE,"E7.31.3"),sQuery(id+"F0.wireOp",EDGE,"E7.31.4"),sQuery(id+"F0.wireOp",EDGE,"E7.31.5"),sQuery(id+"F0.wireOp",EDGE,"E7.32.0"),sQuery(id+"F0.wireOp",EDGE,"E7.32.1"),sQuery(id+"F0.wireOp",EDGE,"E7.32.2"),sQuery(id+"F0.wireOp",EDGE,"E7.32.3"),sQuery(id+"F0.wireOp",EDGE,"E7.32.4"),sQuery(id+"F0.wireOp",EDGE,"E7.32.5"),sQuery(id+"F0.wireOp",EDGE,"E7.33.0"),sQuery(id+"F0.wireOp",EDGE,"E7.33.1"),sQuery(id+"F0.wireOp",EDGE,"E7.33.2"),sQuery(id+"F0.wireOp",EDGE,"E7.33.3"),sQuery(id+"F0.wireOp",EDGE,"E7.33.4"),sQuery(id+"F0.wireOp",EDGE,"E7.33.5"),sQuery(id+"F0.wireOp",EDGE,"E7.34.0"),sQuery(id+"F0.wireOp",EDGE,"E7.34.1"),sQuery(id+"F0.wireOp",EDGE,"E7.34.2"),sQuery(id+"F0.wireOp",EDGE,"E7.34.3"),sQuery(id+"F0.wireOp",EDGE,"E7.34.4"),sQuery(id+"F0.wireOp",EDGE,"E7.34.5"),sQuery(id+"F0.wireOp",EDGE,"E7.35.0"),sQuery(id+"F0.wireOp",EDGE,"E7.35.1"),sQuery(id+"F0.wireOp",EDGE,"E7.35.2"),sQuery(id+"F0.wireOp",EDGE,"E7.35.3"),sQuery(id+"F0.wireOp",EDGE,"E7.35.4"),sQuery(id+"F0.wireOp",EDGE,"E7.35.5"),sQuery(id+"F0.wireOp",EDGE,"E7.36.0"),sQuery(id+"F0.wireOp",EDGE,"E7.36.1"),sQuery(id+"F0.wireOp",EDGE,"E7.36.2"),sQuery(id+"F0.wireOp",EDGE,"E7.36.3"),sQuery(id+"F0.wireOp",EDGE,"E7.36.4"),sQuery(id+"F0.wireOp",EDGE,"E7.36.5"),sQuery(id+"F0.wireOp",EDGE,"E7.37.0"),sQuery(id+"F0.wireOp",EDGE,"E7.37.1"),sQuery(id+"F0.wireOp",EDGE,"E7.37.2"),sQuery(id+"F0.wireOp",EDGE,"E7.37.3"),sQuery(id+"F0.wireOp",EDGE,"E7.37.4"),sQuery(id+"F0.wireOp",EDGE,"E7.37.5"),sQuery(id+"F0.wireOp",EDGE,"E7.38.0"),sQuery(id+"F0.wireOp",EDGE,"E7.38.1"),sQuery(id+"F0.wireOp",EDGE,"E7.38.2"),sQuery(id+"F0.wireOp",EDGE,"E7.38.3"),sQuery(id+"F0.wireOp",EDGE,"E7.38.4"),sQuery(id+"F0.wireOp",EDGE,"E7.38.5"),sQuery(id+"F0.wireOp",EDGE,"E7.39.0"),sQuery(id+"F0.wireOp",EDGE,"E7.39.1"),sQuery(id+"F0.wireOp",EDGE,"E7.39.2"),sQuery(id+"F0.wireOp",EDGE,"E7.39.3"),sQuery(id+"F0.wireOp",EDGE,"E7.39.4"),sQuery(id+"F0.wireOp",EDGE,"E7.39.5"),sQuery(id+"F0.wireOp",EDGE,"E7.40.0"),sQuery(id+"F0.wireOp",EDGE,"E7.40.1"),sQuery(id+"F0.wireOp",EDGE,"E7.40.2"),sQuery(id+"F0.wireOp",EDGE,"E7.40.3"),sQuery(id+"F0.wireOp",EDGE,"E7.40.4"),sQuery(id+"F0.wireOp",EDGE,"E7.40.5"),sQuery(id+"F0.wireOp",EDGE,"E7.41.0"),sQuery(id+"F0.wireOp",EDGE,"E7.41.1"),sQuery(id+"F0.wireOp",EDGE,"E7.41.2"),sQuery(id+"F0.wireOp",EDGE,"E7.41.3"),sQuery(id+"F0.wireOp",EDGE,"E7.41.4"),sQuery(id+"F0.wireOp",EDGE,"E7.41.5"),sQuery(id+"F0.wireOp",EDGE,"E7.42.0"),sQuery(id+"F0.wireOp",EDGE,"E7.42.1"),sQuery(id+"F0.wireOp",EDGE,"E7.42.2"),sQuery(id+"F0.wireOp",EDGE,"E7.42.3"),sQuery(id+"F0.wireOp",EDGE,"E7.42.4"),sQuery(id+"F0.wireOp",EDGE,"E7.42.5"),sQuery(id+"F0.wireOp",EDGE,"E7.43.0"),sQuery(id+"F0.wireOp",EDGE,"E7.43.1"),sQuery(id+"F0.wireOp",EDGE,"E7.43.2"),sQuery(id+"F0.wireOp",EDGE,"E7.43.3"),sQuery(id+"F0.wireOp",EDGE,"E7.43.4"),sQuery(id+"F0.wireOp",EDGE,"E7.43.5")])],"isStart":false})],"blendedInto":[makeQuery(id+"F1.opExtrude","CAP_FACE",FACE,{"disambiguationData":[OSD([sQuery(id+"F0.wireOp",EDGE,"E1"),sQuery(id+"F0.wireOp",EDGE,"E2"),sQuery(id+"F0.wireOp",EDGE,"E3"),sQuery(id+"F0.wireOp",EDGE,"E4"),sQuery(id+"F0.wireOp",EDGE,"E5"),sQuery(id+"F0.wireOp",EDGE,"E6"),sQuery(id+"F0.wireOp",EDGE,"E7.1.0"),sQuery(id+"F0.wireOp",EDGE,"E7.1.1"),sQuery(id+"F0.wireOp",EDGE,"E7.1.2"),sQuery(id+"F0.wireOp",EDGE,"E7.1.3"),sQuery(id+"F0.wireOp",EDGE,"E7.1.4"),sQuery(id+"F0.wireOp",EDGE,"E7.1.5"),sQuery(id+"F0.wireOp",EDGE,"E7.2.0"),sQuery(id+"F0.wireOp",EDGE,"E7.2.1"),sQuery(id+"F0.wireOp",EDGE,"E7.2.2"),sQuery(id+"F0.wireOp",EDGE,"E7.2.3"),sQuery(id+"F0.wireOp",EDGE,"E7.2.4"),sQuery(id+"F0.wireOp",EDGE,"E7.2.5"),sQuery(id+"F0.wireOp",EDGE,"E7.3.0"),sQuery(id+"F0.wireOp",EDGE,"E7.3.1"),sQuery(id+"F0.wireOp",EDGE,"E7.3.2"),sQuery(id+"F0.wireOp",EDGE,"E7.3.3"),sQuery(id+"F0.wireOp",EDGE,"E7.3.4"),sQuery(id+"F0.wireOp",EDGE,"E7.3.5"),sQuery(id+"F0.wireOp",EDGE,"E7.4.0"),sQuery(id+"F0.wireOp",EDGE,"E7.4.1"),sQuery(id+"F0.wireOp",EDGE,"E7.4.2"),sQuery(id+"F0.wireOp",EDGE,"E7.4.3"),sQuery(id+"F0.wireOp",EDGE,"E7.4.4"),sQuery(id+"F0.wireOp",EDGE,"E7.4.5"),sQuery(id+"F0.wireOp",EDGE,"E7.5.0"),sQuery(id+"F0.wireOp",EDGE,"E7.5.1"),sQuery(id+"F0.wireOp",EDGE,"E7.5.2"),sQuery(id+"F0.wireOp",EDGE,"E7.5.3"),sQuery(id+"F0.wireOp",EDGE,"E7.5.4"),sQuery(id+"F0.wireOp",EDGE,"E7.5.5"),sQuery(id+"F0.wireOp",EDGE,"E7.6.0"),sQuery(id+"F0.wireOp",EDGE,"E7.6.1"),sQuery(id+"F0.wireOp",EDGE,"E7.6.2"),sQuery(id+"F0.wireOp",EDGE,"E7.6.3"),sQuery(id+"F0.wireOp",EDGE,"E7.6.4"),sQuery(id+"F0.wireOp",EDGE,"E7.6.5"),sQuery(id+"F0.wireOp",EDGE,"E7.7.0"),sQuery(id+"F0.wireOp",EDGE,"E7.7.1"),sQuery(id+"F0.wireOp",EDGE,"E7.7.2"),sQuery(id+"F0.wireOp",EDGE,"E7.7.3"),sQuery(id+"F0.wireOp",EDGE,"E7.7.4"),sQuery(id+"F0.wireOp",EDGE,"E7.7.5"),sQuery(id+"F0.wireOp",EDGE,"E7.8.0"),sQuery(id+"F0.wireOp",EDGE,"E7.8.1"),sQuery(id+"F0.wireOp",EDGE,"E7.8.2"),sQuery(id+"F0.wireOp",EDGE,"E7.8.3"),sQuery(id+"F0.wireOp",EDGE,"E7.8.4"),sQuery(id+"F0.wireOp",EDGE,"E7.8.5"),sQuery(id+"F0.wireOp",EDGE,"E7.9.0"),sQuery(id+"F0.wireOp",EDGE,"E7.9.1"),sQuery(id+"F0.wireOp",EDGE,"E7.9.2"),sQuery(id+"F0.wireOp",EDGE,"E7.9.3"),sQuery(id+"F0.wireOp",EDGE,"E7.9.4"),sQuery(id+"F0.wireOp",EDGE,"E7.9.5"),sQuery(id+"F0.wireOp",EDGE,"E7.10.0"),sQuery(id+"F0.wireOp",EDGE,"E7.10.1"),sQuery(id+"F0.wireOp",EDGE,"E7.10.2"),sQuery(id+"F0.wireOp",EDGE,"E7.10.3"),sQuery(id+"F0.wireOp",EDGE,"E7.10.4"),sQuery(id+"F0.wireOp",EDGE,"E7.10.5"),sQuery(id+"F0.wireOp",EDGE,"E7.11.0"),sQuery(id+"F0.wireOp",EDGE,"E7.11.1"),sQuery(id+"F0.wireOp",EDGE,"E7.11.2"),sQuery(id+"F0.wireOp",EDGE,"E7.11.3"),sQuery(id+"F0.wireOp",EDGE,"E7.11.4"),sQuery(id+"F0.wireOp",EDGE,"E7.11.5"),sQuery(id+"F0.wireOp",EDGE,"E7.12.0"),sQuery(id+"F0.wireOp",EDGE,"E7.12.1"),sQuery(id+"F0.wireOp",EDGE,"E7.12.2"),sQuery(id+"F0.wireOp",EDGE,"E7.12.3"),sQuery(id+"F0.wireOp",EDGE,"E7.12.4"),sQuery(id+"F0.wireOp",EDGE,"E7.12.5"),sQuery(id+"F0.wireOp",EDGE,"E7.13.0"),sQuery(id+"F0.wireOp",EDGE,"E7.13.1"),sQuery(id+"F0.wireOp",EDGE,"E7.13.2"),sQuery(id+"F0.wireOp",EDGE,"E7.13.3"),sQuery(id+"F0.wireOp",EDGE,"E7.13.4"),sQuery(id+"F0.wireOp",EDGE,"E7.13.5"),sQuery(id+"F0.wireOp",EDGE,"E7.14.0"),sQuery(id+"F0.wireOp",EDGE,"E7.14.1"),sQuery(id+"F0.wireOp",EDGE,"E7.14.2"),sQuery(id+"F0.wireOp",EDGE,"E7.14.3"),sQuery(id+"F0.wireOp",EDGE,"E7.14.4"),sQuery(id+"F0.wireOp",EDGE,"E7.14.5"),sQuery(id+"F0.wireOp",EDGE,"E7.15.0"),sQuery(id+"F0.wireOp",EDGE,"E7.15.1"),sQuery(id+"F0.wireOp",EDGE,"E7.15.2"),sQuery(id+"F0.wireOp",EDGE,"E7.15.3"),sQuery(id+"F0.wireOp",EDGE,"E7.15.4"),sQuery(id+"F0.wireOp",EDGE,"E7.15.5"),sQuery(id+"F0.wireOp",EDGE,"E7.16.0"),sQuery(id+"F0.wireOp",EDGE,"E7.16.1"),sQuery(id+"F0.wireOp",EDGE,"E7.16.2"),sQuery(id+"F0.wireOp",EDGE,"E7.16.3"),sQuery(id+"F0.wireOp",EDGE,"E7.16.4"),sQuery(id+"F0.wireOp",EDGE,"E7.16.5"),sQuery(id+"F0.wireOp",EDGE,"E7.17.0"),sQuery(id+"F0.wireOp",EDGE,"E7.17.1"),sQuery(id+"F0.wireOp",EDGE,"E7.17.2"),sQuery(id+"F0.wireOp",EDGE,"E7.17.3"),sQuery(id+"F0.wireOp",EDGE,"E7.17.4"),sQuery(id+"F0.wireOp",EDGE,"E7.17.5"),sQuery(id+"F0.wireOp",EDGE,"E7.18.0"),sQuery(id+"F0.wireOp",EDGE,"E7.18.1"),sQuery(id+"F0.wireOp",EDGE,"E7.18.2"),sQuery(id+"F0.wireOp",EDGE,"E7.18.3"),sQuery(id+"F0.wireOp",EDGE,"E7.18.4"),sQuery(id+"F0.wireOp",EDGE,"E7.18.5"),sQuery(id+"F0.wireOp",EDGE,"E7.19.0"),sQuery(id+"F0.wireOp",EDGE,"E7.19.1"),sQuery(id+"F0.wireOp",EDGE,"E7.19.2"),sQuery(id+"F0.wireOp",EDGE,"E7.19.3"),sQuery(id+"F0.wireOp",EDGE,"E7.19.4"),sQuery(id+"F0.wireOp",EDGE,"E7.19.5"),sQuery(id+"F0.wireOp",EDGE,"E7.20.0"),sQuery(id+"F0.wireOp",EDGE,"E7.20.1"),sQuery(id+"F0.wireOp",EDGE,"E7.20.2"),sQuery(id+"F0.wireOp",EDGE,"E7.20.3"),sQuery(id+"F0.wireOp",EDGE,"E7.20.4"),sQuery(id+"F0.wireOp",EDGE,"E7.20.5"),sQuery(id+"F0.wireOp",EDGE,"E7.21.0"),sQuery(id+"F0.wireOp",EDGE,"E7.21.1"),sQuery(id+"F0.wireOp",EDGE,"E7.21.2"),sQuery(id+"F0.wireOp",EDGE,"E7.21.3"),sQuery(id+"F0.wireOp",EDGE,"E7.21.4"),sQuery(id+"F0.wireOp",EDGE,"E7.21.5"),sQuery(id+"F0.wireOp",EDGE,"E7.22.0"),sQuery(id+"F0.wireOp",EDGE,"E7.22.1"),sQuery(id+"F0.wireOp",EDGE,"E7.22.2"),sQuery(id+"F0.wireOp",EDGE,"E7.22.3"),sQuery(id+"F0.wireOp",EDGE,"E7.22.4"),sQuery(id+"F0.wireOp",EDGE,"E7.22.5"),subQ0,sQuery(id+"F0.wireOp",EDGE,"E7.23.1"),sQuery(id+"F0.wireOp",EDGE,"E7.23.2"),sQuery(id+"F0.wireOp",EDGE,"E7.23.3"),sQuery(id+"F0.wireOp",EDGE,"E7.23.4"),sQuery(id+"F0.wireOp",EDGE,"E7.23.5"),sQuery(id+"F0.wireOp",EDGE,"E7.24.0"),sQuery(id+"F0.wireOp",EDGE,"E7.24.1"),sQuery(id+"F0.wireOp",EDGE,"E7.24.2"),sQuery(id+"F0.wireOp",EDGE,"E7.24.3"),sQuery(id+"F0.wireOp",EDGE,"E7.24.4"),sQuery(id+"F0.wireOp",EDGE,"E7.24.5"),sQuery(id+"F0.wireOp",EDGE,"E7.25.0"),sQuery(id+"F0.wireOp",EDGE,"E7.25.1"),sQuery(id+"F0.wireOp",EDGE,"E7.25.2"),sQuery(id+"F0.wireOp",EDGE,"E7.25.3"),sQuery(id+"F0.wireOp",EDGE,"E7.25.4"),sQuery(id+"F0.wireOp",EDGE,"E7.25.5"),sQuery(id+"F0.wireOp",EDGE,"E7.26.0"),sQuery(id+"F0.wireOp",EDGE,"E7.26.1"),sQuery(id+"F0.wireOp",EDGE,"E7.26.2"),sQuery(id+"F0.wireOp",EDGE,"E7.26.3"),sQuery(id+"F0.wireOp",EDGE,"E7.26.4"),sQuery(id+"F0.wireOp",EDGE,"E7.26.5"),sQuery(id+"F0.wireOp",EDGE,"E7.27.0"),sQuery(id+"F0.wireOp",EDGE,"E7.27.1"),sQuery(id+"F0.wireOp",EDGE,"E7.27.2"),sQuery(id+"F0.wireOp",EDGE,"E7.27.3"),sQuery(id+"F0.wireOp",EDGE,"E7.27.4"),sQuery(id+"F0.wireOp",EDGE,"E7.27.5"),sQuery(id+"F0.wireOp",EDGE,"E7.28.0"),sQuery(id+"F0.wireOp",EDGE,"E7.28.1"),sQuery(id+"F0.wireOp",EDGE,"E7.28.2"),sQuery(id+"F0.wireOp",EDGE,"E7.28.3"),sQuery(id+"F0.wireOp",EDGE,"E7.28.4"),sQuery(id+"F0.wireOp",EDGE,"E7.28.5"),sQuery(id+"F0.wireOp",EDGE,"E7.29.0"),sQuery(id+"F0.wireOp",EDGE,"E7.29.1"),sQuery(id+"F0.wireOp",EDGE,"E7.29.2"),sQuery(id+"F0.wireOp",EDGE,"E7.29.3"),sQuery(id+"F0.wireOp",EDGE,"E7.29.4"),sQuery(id+"F0.wireOp",EDGE,"E7.29.5"),sQuery(id+"F0.wireOp",EDGE,"E7.30.0"),sQuery(id+"F0.wireOp",EDGE,"E7.30.1"),sQuery(id+"F0.wireOp",EDGE,"E7.30.2"),sQuery(id+"F0.wireOp",EDGE,"E7.30.3"),sQuery(id+"F0.wireOp",EDGE,"E7.30.4"),sQuery(id+"F0.wireOp",EDGE,"E7.30.5"),sQuery(id+"F0.wireOp",EDGE,"E7.31.0"),sQuery(id+"F0.wireOp",EDGE,"E7.31.1"),sQuery(id+"F0.wireOp",EDGE,"E7.31.2"),sQuery(id+"F0.wireOp",EDGE,"E7.31.3"),sQuery(id+"F0.wireOp",EDGE,"E7.31.4"),sQuery(id+"F0.wireOp",EDGE,"E7.31.5"),sQuery(id+"F0.wireOp",EDGE,"E7.32.0"),sQuery(id+"F0.wireOp",EDGE,"E7.32.1"),sQuery(id+"F0.wireOp",EDGE,"E7.32.2"),sQuery(id+"F0.wireOp",EDGE,"E7.32.3"),sQuery(id+"F0.wireOp",EDGE,"E7.32.4"),sQuery(id+"F0.wireOp",EDGE,"E7.32.5"),sQuery(id+"F0.wireOp",EDGE,"E7.33.0"),sQuery(id+"F0.wireOp",EDGE,"E7.33.1"),sQuery(id+"F0.wireOp",EDGE,"E7.33.2"),sQuery(id+"F0.wireOp",EDGE,"E7.33.3"),sQuery(id+"F0.wireOp",EDGE,"E7.33.4"),sQuery(id+"F0.wireOp",EDGE,"E7.33.5"),sQuery(id+"F0.wireOp",EDGE,"E7.34.0"),sQuery(id+"F0.wireOp",EDGE,"E7.34.1"),sQuery(id+"F0.wireOp",EDGE,"E7.34.2"),sQuery(id+"F0.wireOp",EDGE,"E7.34.3"),sQuery(id+"F0.wireOp",EDGE,"E7.34.4"),sQuery(id+"F0.wireOp",EDGE,"E7.34.5"),sQuery(id+"F0.wireOp",EDGE,"E7.35.0"),sQuery(id+"F0.wireOp",EDGE,"E7.35.1"),sQuery(id+"F0.wireOp",EDGE,"E7.35.2"),sQuery(id+"F0.wireOp",EDGE,"E7.35.3"),sQuery(id+"F0.wireOp",EDGE,"E7.35.4"),sQuery(id+"F0.wireOp",EDGE,"E7.35.5"),sQuery(id+"F0.wireOp",EDGE,"E7.36.0"),sQuery(id+"F0.wireOp",EDGE,"E7.36.1"),sQuery(id+"F0.wireOp",EDGE,"E7.36.2"),sQuery(id+"F0.wireOp",EDGE,"E7.36.3"),sQuery(id+"F0.wireOp",EDGE,"E7.36.4"),sQuery(id+"F0.wireOp",EDGE,"E7.36.5"),sQuery(id+"F0.wireOp",EDGE,"E7.37.0"),sQuery(id+"F0.wireOp",EDGE,"E7.37.1"),sQuery(id+"F0.wireOp",EDGE,"E7.37.2"),sQuery(id+"F0.wireOp",EDGE,"E7.37.3"),sQuery(id+"F0.wireOp",EDGE,"E7.37.4"),sQuery(id+"F0.wireOp",EDGE,"E7.37.5"),sQuery(id+"F0.wireOp",EDGE,"E7.38.0"),sQuery(id+"F0.wireOp",EDGE,"E7.38.1"),sQuery(id+"F0.wireOp",EDGE,"E7.38.2"),sQuery(id+"F0.wireOp",EDGE,"E7.38.3"),sQuery(id+"F0.wireOp",EDGE,"E7.38.4"),sQuery(id+"F0.wireOp",EDGE,"E7.38.5"),sQuery(id+"F0.wireOp",EDGE,"E7.39.0"),sQuery(id+"F0.wireOp",EDGE,"E7.39.1"),sQuery(id+"F0.wireOp",EDGE,"E7.39.2"),sQuery(id+"F0.wireOp",EDGE,"E7.39.3"),sQuery(id+"F0.wireOp",EDGE,"E7.39.4"),sQuery(id+"F0.wireOp",EDGE,"E7.39.5"),sQuery(id+"F0.wireOp",EDGE,"E7.40.0"),sQuery(id+"F0.wireOp",EDGE,"E7.40.1"),sQuery(id+"F0.wireOp",EDGE,"E7.40.2"),sQuery(id+"F0.wireOp",EDGE,"E7.40.3"),sQuery(id+"F0.wireOp",EDGE,"E7.40.4"),sQuery(id+"F0.wireOp",EDGE,"E7.40.5"),sQuery(id+"F0.wireOp",EDGE,"E7.41.0"),sQuery(id+"F0.wireOp",EDGE,"E7.41.1"),sQuery(id+"F0.wireOp",EDGE,"E7.41.2"),sQuery(id+"F0.wireOp",EDGE,"E7.41.3"),sQuery(id+"F0.wireOp",EDGE,"E7.41.4"),sQuery(id+"F0.wireOp",EDGE,"E7.41.5"),sQuery(id+"F0.wireOp",EDGE,"E7.42.0"),sQuery(id+"F0.wireOp",EDGE,"E7.42.1"),sQuery(id+"F0.wireOp",EDGE,"E7.42.2"),sQuery(id+"F0.wireOp",EDGE,"E7.42.3"),sQuery(id+"F0.wireOp",EDGE,"E7.42.4"),sQuery(id+"F0.wireOp",EDGE,"E7.42.5"),sQuery(id+"F0.wireOp",EDGE,"E7.43.0"),sQuery(id+"F0.wireOp",EDGE,"E7.43.1"),sQuery(id+"F0.wireOp",EDGE,"E7.43.2"),sQuery(id+"F0.wireOp",EDGE,"E7.43.3"),sQuery(id+"F0.wireOp",EDGE,"E7.43.4"),sQuery(id+"F0.wireOp",EDGE,"E7.43.5")])],"isStart":false})]});}
            var Q11;
            {var subQ0=sQuery(id+"F0.wireOp",EDGE,"E7.21.0");Q11=makeQuery(id+"F2.opChamfer","BLEND_EDGE",EDGE,{"blendedFrom":[makeQuery(id+"F1.opExtrude","CAP_EDGE",EDGE,{"disambiguationData":[OSD([subQ0])],"isStart":false}),makeQuery(id+"F1.opExtrude","CAP_FACE",FACE,{"disambiguationData":[OSD([sQuery(id+"F0.wireOp",EDGE,"E1"),sQuery(id+"F0.wireOp",EDGE,"E2"),sQuery(id+"F0.wireOp",EDGE,"E3"),sQuery(id+"F0.wireOp",EDGE,"E4"),sQuery(id+"F0.wireOp",EDGE,"E5"),sQuery(id+"F0.wireOp",EDGE,"E6"),sQuery(id+"F0.wireOp",EDGE,"E7.1.0"),sQuery(id+"F0.wireOp",EDGE,"E7.1.1"),sQuery(id+"F0.wireOp",EDGE,"E7.1.2"),sQuery(id+"F0.wireOp",EDGE,"E7.1.3"),sQuery(id+"F0.wireOp",EDGE,"E7.1.4"),sQuery(id+"F0.wireOp",EDGE,"E7.1.5"),sQuery(id+"F0.wireOp",EDGE,"E7.2.0"),sQuery(id+"F0.wireOp",EDGE,"E7.2.1"),sQuery(id+"F0.wireOp",EDGE,"E7.2.2"),sQuery(id+"F0.wireOp",EDGE,"E7.2.3"),sQuery(id+"F0.wireOp",EDGE,"E7.2.4"),sQuery(id+"F0.wireOp",EDGE,"E7.2.5"),sQuery(id+"F0.wireOp",EDGE,"E7.3.0"),sQuery(id+"F0.wireOp",EDGE,"E7.3.1"),sQuery(id+"F0.wireOp",EDGE,"E7.3.2"),sQuery(id+"F0.wireOp",EDGE,"E7.3.3"),sQuery(id+"F0.wireOp",EDGE,"E7.3.4"),sQuery(id+"F0.wireOp",EDGE,"E7.3.5"),sQuery(id+"F0.wireOp",EDGE,"E7.4.0"),sQuery(id+"F0.wireOp",EDGE,"E7.4.1"),sQuery(id+"F0.wireOp",EDGE,"E7.4.2"),sQuery(id+"F0.wireOp",EDGE,"E7.4.3"),sQuery(id+"F0.wireOp",EDGE,"E7.4.4"),sQuery(id+"F0.wireOp",EDGE,"E7.4.5"),sQuery(id+"F0.wireOp",EDGE,"E7.5.0"),sQuery(id+"F0.wireOp",EDGE,"E7.5.1"),sQuery(id+"F0.wireOp",EDGE,"E7.5.2"),sQuery(id+"F0.wireOp",EDGE,"E7.5.3"),sQuery(id+"F0.wireOp",EDGE,"E7.5.4"),sQuery(id+"F0.wireOp",EDGE,"E7.5.5"),sQuery(id+"F0.wireOp",EDGE,"E7.6.0"),sQuery(id+"F0.wireOp",EDGE,"E7.6.1"),sQuery(id+"F0.wireOp",EDGE,"E7.6.2"),sQuery(id+"F0.wireOp",EDGE,"E7.6.3"),sQuery(id+"F0.wireOp",EDGE,"E7.6.4"),sQuery(id+"F0.wireOp",EDGE,"E7.6.5"),sQuery(id+"F0.wireOp",EDGE,"E7.7.0"),sQuery(id+"F0.wireOp",EDGE,"E7.7.1"),sQuery(id+"F0.wireOp",EDGE,"E7.7.2"),sQuery(id+"F0.wireOp",EDGE,"E7.7.3"),sQuery(id+"F0.wireOp",EDGE,"E7.7.4"),sQuery(id+"F0.wireOp",EDGE,"E7.7.5"),sQuery(id+"F0.wireOp",EDGE,"E7.8.0"),sQuery(id+"F0.wireOp",EDGE,"E7.8.1"),sQuery(id+"F0.wireOp",EDGE,"E7.8.2"),sQuery(id+"F0.wireOp",EDGE,"E7.8.3"),sQuery(id+"F0.wireOp",EDGE,"E7.8.4"),sQuery(id+"F0.wireOp",EDGE,"E7.8.5"),sQuery(id+"F0.wireOp",EDGE,"E7.9.0"),sQuery(id+"F0.wireOp",EDGE,"E7.9.1"),sQuery(id+"F0.wireOp",EDGE,"E7.9.2"),sQuery(id+"F0.wireOp",EDGE,"E7.9.3"),sQuery(id+"F0.wireOp",EDGE,"E7.9.4"),sQuery(id+"F0.wireOp",EDGE,"E7.9.5"),sQuery(id+"F0.wireOp",EDGE,"E7.10.0"),sQuery(id+"F0.wireOp",EDGE,"E7.10.1"),sQuery(id+"F0.wireOp",EDGE,"E7.10.2"),sQuery(id+"F0.wireOp",EDGE,"E7.10.3"),sQuery(id+"F0.wireOp",EDGE,"E7.10.4"),sQuery(id+"F0.wireOp",EDGE,"E7.10.5"),sQuery(id+"F0.wireOp",EDGE,"E7.11.0"),sQuery(id+"F0.wireOp",EDGE,"E7.11.1"),sQuery(id+"F0.wireOp",EDGE,"E7.11.2"),sQuery(id+"F0.wireOp",EDGE,"E7.11.3"),sQuery(id+"F0.wireOp",EDGE,"E7.11.4"),sQuery(id+"F0.wireOp",EDGE,"E7.11.5"),sQuery(id+"F0.wireOp",EDGE,"E7.12.0"),sQuery(id+"F0.wireOp",EDGE,"E7.12.1"),sQuery(id+"F0.wireOp",EDGE,"E7.12.2"),sQuery(id+"F0.wireOp",EDGE,"E7.12.3"),sQuery(id+"F0.wireOp",EDGE,"E7.12.4"),sQuery(id+"F0.wireOp",EDGE,"E7.12.5"),sQuery(id+"F0.wireOp",EDGE,"E7.13.0"),sQuery(id+"F0.wireOp",EDGE,"E7.13.1"),sQuery(id+"F0.wireOp",EDGE,"E7.13.2"),sQuery(id+"F0.wireOp",EDGE,"E7.13.3"),sQuery(id+"F0.wireOp",EDGE,"E7.13.4"),sQuery(id+"F0.wireOp",EDGE,"E7.13.5"),sQuery(id+"F0.wireOp",EDGE,"E7.14.0"),sQuery(id+"F0.wireOp",EDGE,"E7.14.1"),sQuery(id+"F0.wireOp",EDGE,"E7.14.2"),sQuery(id+"F0.wireOp",EDGE,"E7.14.3"),sQuery(id+"F0.wireOp",EDGE,"E7.14.4"),sQuery(id+"F0.wireOp",EDGE,"E7.14.5"),sQuery(id+"F0.wireOp",EDGE,"E7.15.0"),sQuery(id+"F0.wireOp",EDGE,"E7.15.1"),sQuery(id+"F0.wireOp",EDGE,"E7.15.2"),sQuery(id+"F0.wireOp",EDGE,"E7.15.3"),sQuery(id+"F0.wireOp",EDGE,"E7.15.4"),sQuery(id+"F0.wireOp",EDGE,"E7.15.5"),sQuery(id+"F0.wireOp",EDGE,"E7.16.0"),sQuery(id+"F0.wireOp",EDGE,"E7.16.1"),sQuery(id+"F0.wireOp",EDGE,"E7.16.2"),sQuery(id+"F0.wireOp",EDGE,"E7.16.3"),sQuery(id+"F0.wireOp",EDGE,"E7.16.4"),sQuery(id+"F0.wireOp",EDGE,"E7.16.5"),sQuery(id+"F0.wireOp",EDGE,"E7.17.0"),sQuery(id+"F0.wireOp",EDGE,"E7.17.1"),sQuery(id+"F0.wireOp",EDGE,"E7.17.2"),sQuery(id+"F0.wireOp",EDGE,"E7.17.3"),sQuery(id+"F0.wireOp",EDGE,"E7.17.4"),sQuery(id+"F0.wireOp",EDGE,"E7.17.5"),sQuery(id+"F0.wireOp",EDGE,"E7.18.0"),sQuery(id+"F0.wireOp",EDGE,"E7.18.1"),sQuery(id+"F0.wireOp",EDGE,"E7.18.2"),sQuery(id+"F0.wireOp",EDGE,"E7.18.3"),sQuery(id+"F0.wireOp",EDGE,"E7.18.4"),sQuery(id+"F0.wireOp",EDGE,"E7.18.5"),sQuery(id+"F0.wireOp",EDGE,"E7.19.0"),sQuery(id+"F0.wireOp",EDGE,"E7.19.1"),sQuery(id+"F0.wireOp",EDGE,"E7.19.2"),sQuery(id+"F0.wireOp",EDGE,"E7.19.3"),sQuery(id+"F0.wireOp",EDGE,"E7.19.4"),sQuery(id+"F0.wireOp",EDGE,"E7.19.5"),sQuery(id+"F0.wireOp",EDGE,"E7.20.0"),sQuery(id+"F0.wireOp",EDGE,"E7.20.1"),sQuery(id+"F0.wireOp",EDGE,"E7.20.2"),sQuery(id+"F0.wireOp",EDGE,"E7.20.3"),sQuery(id+"F0.wireOp",EDGE,"E7.20.4"),sQuery(id+"F0.wireOp",EDGE,"E7.20.5"),subQ0,sQuery(id+"F0.wireOp",EDGE,"E7.21.1"),sQuery(id+"F0.wireOp",EDGE,"E7.21.2"),sQuery(id+"F0.wireOp",EDGE,"E7.21.3"),sQuery(id+"F0.wireOp",EDGE,"E7.21.4"),sQuery(id+"F0.wireOp",EDGE,"E7.21.5"),sQuery(id+"F0.wireOp",EDGE,"E7.22.0"),sQuery(id+"F0.wireOp",EDGE,"E7.22.1"),sQuery(id+"F0.wireOp",EDGE,"E7.22.2"),sQuery(id+"F0.wireOp",EDGE,"E7.22.3"),sQuery(id+"F0.wireOp",EDGE,"E7.22.4"),sQuery(id+"F0.wireOp",EDGE,"E7.22.5"),sQuery(id+"F0.wireOp",EDGE,"E7.23.0"),sQuery(id+"F0.wireOp",EDGE,"E7.23.1"),sQuery(id+"F0.wireOp",EDGE,"E7.23.2"),sQuery(id+"F0.wireOp",EDGE,"E7.23.3"),sQuery(id+"F0.wireOp",EDGE,"E7.23.4"),sQuery(id+"F0.wireOp",EDGE,"E7.23.5"),sQuery(id+"F0.wireOp",EDGE,"E7.24.0"),sQuery(id+"F0.wireOp",EDGE,"E7.24.1"),sQuery(id+"F0.wireOp",EDGE,"E7.24.2"),sQuery(id+"F0.wireOp",EDGE,"E7.24.3"),sQuery(id+"F0.wireOp",EDGE,"E7.24.4"),sQuery(id+"F0.wireOp",EDGE,"E7.24.5"),sQuery(id+"F0.wireOp",EDGE,"E7.25.0"),sQuery(id+"F0.wireOp",EDGE,"E7.25.1"),sQuery(id+"F0.wireOp",EDGE,"E7.25.2"),sQuery(id+"F0.wireOp",EDGE,"E7.25.3"),sQuery(id+"F0.wireOp",EDGE,"E7.25.4"),sQuery(id+"F0.wireOp",EDGE,"E7.25.5"),sQuery(id+"F0.wireOp",EDGE,"E7.26.0"),sQuery(id+"F0.wireOp",EDGE,"E7.26.1"),sQuery(id+"F0.wireOp",EDGE,"E7.26.2"),sQuery(id+"F0.wireOp",EDGE,"E7.26.3"),sQuery(id+"F0.wireOp",EDGE,"E7.26.4"),sQuery(id+"F0.wireOp",EDGE,"E7.26.5"),sQuery(id+"F0.wireOp",EDGE,"E7.27.0"),sQuery(id+"F0.wireOp",EDGE,"E7.27.1"),sQuery(id+"F0.wireOp",EDGE,"E7.27.2"),sQuery(id+"F0.wireOp",EDGE,"E7.27.3"),sQuery(id+"F0.wireOp",EDGE,"E7.27.4"),sQuery(id+"F0.wireOp",EDGE,"E7.27.5"),sQuery(id+"F0.wireOp",EDGE,"E7.28.0"),sQuery(id+"F0.wireOp",EDGE,"E7.28.1"),sQuery(id+"F0.wireOp",EDGE,"E7.28.2"),sQuery(id+"F0.wireOp",EDGE,"E7.28.3"),sQuery(id+"F0.wireOp",EDGE,"E7.28.4"),sQuery(id+"F0.wireOp",EDGE,"E7.28.5"),sQuery(id+"F0.wireOp",EDGE,"E7.29.0"),sQuery(id+"F0.wireOp",EDGE,"E7.29.1"),sQuery(id+"F0.wireOp",EDGE,"E7.29.2"),sQuery(id+"F0.wireOp",EDGE,"E7.29.3"),sQuery(id+"F0.wireOp",EDGE,"E7.29.4"),sQuery(id+"F0.wireOp",EDGE,"E7.29.5"),sQuery(id+"F0.wireOp",EDGE,"E7.30.0"),sQuery(id+"F0.wireOp",EDGE,"E7.30.1"),sQuery(id+"F0.wireOp",EDGE,"E7.30.2"),sQuery(id+"F0.wireOp",EDGE,"E7.30.3"),sQuery(id+"F0.wireOp",EDGE,"E7.30.4"),sQuery(id+"F0.wireOp",EDGE,"E7.30.5"),sQuery(id+"F0.wireOp",EDGE,"E7.31.0"),sQuery(id+"F0.wireOp",EDGE,"E7.31.1"),sQuery(id+"F0.wireOp",EDGE,"E7.31.2"),sQuery(id+"F0.wireOp",EDGE,"E7.31.3"),sQuery(id+"F0.wireOp",EDGE,"E7.31.4"),sQuery(id+"F0.wireOp",EDGE,"E7.31.5"),sQuery(id+"F0.wireOp",EDGE,"E7.32.0"),sQuery(id+"F0.wireOp",EDGE,"E7.32.1"),sQuery(id+"F0.wireOp",EDGE,"E7.32.2"),sQuery(id+"F0.wireOp",EDGE,"E7.32.3"),sQuery(id+"F0.wireOp",EDGE,"E7.32.4"),sQuery(id+"F0.wireOp",EDGE,"E7.32.5"),sQuery(id+"F0.wireOp",EDGE,"E7.33.0"),sQuery(id+"F0.wireOp",EDGE,"E7.33.1"),sQuery(id+"F0.wireOp",EDGE,"E7.33.2"),sQuery(id+"F0.wireOp",EDGE,"E7.33.3"),sQuery(id+"F0.wireOp",EDGE,"E7.33.4"),sQuery(id+"F0.wireOp",EDGE,"E7.33.5"),sQuery(id+"F0.wireOp",EDGE,"E7.34.0"),sQuery(id+"F0.wireOp",EDGE,"E7.34.1"),sQuery(id+"F0.wireOp",EDGE,"E7.34.2"),sQuery(id+"F0.wireOp",EDGE,"E7.34.3"),sQuery(id+"F0.wireOp",EDGE,"E7.34.4"),sQuery(id+"F0.wireOp",EDGE,"E7.34.5"),sQuery(id+"F0.wireOp",EDGE,"E7.35.0"),sQuery(id+"F0.wireOp",EDGE,"E7.35.1"),sQuery(id+"F0.wireOp",EDGE,"E7.35.2"),sQuery(id+"F0.wireOp",EDGE,"E7.35.3"),sQuery(id+"F0.wireOp",EDGE,"E7.35.4"),sQuery(id+"F0.wireOp",EDGE,"E7.35.5"),sQuery(id+"F0.wireOp",EDGE,"E7.36.0"),sQuery(id+"F0.wireOp",EDGE,"E7.36.1"),sQuery(id+"F0.wireOp",EDGE,"E7.36.2"),sQuery(id+"F0.wireOp",EDGE,"E7.36.3"),sQuery(id+"F0.wireOp",EDGE,"E7.36.4"),sQuery(id+"F0.wireOp",EDGE,"E7.36.5"),sQuery(id+"F0.wireOp",EDGE,"E7.37.0"),sQuery(id+"F0.wireOp",EDGE,"E7.37.1"),sQuery(id+"F0.wireOp",EDGE,"E7.37.2"),sQuery(id+"F0.wireOp",EDGE,"E7.37.3"),sQuery(id+"F0.wireOp",EDGE,"E7.37.4"),sQuery(id+"F0.wireOp",EDGE,"E7.37.5"),sQuery(id+"F0.wireOp",EDGE,"E7.38.0"),sQuery(id+"F0.wireOp",EDGE,"E7.38.1"),sQuery(id+"F0.wireOp",EDGE,"E7.38.2"),sQuery(id+"F0.wireOp",EDGE,"E7.38.3"),sQuery(id+"F0.wireOp",EDGE,"E7.38.4"),sQuery(id+"F0.wireOp",EDGE,"E7.38.5"),sQuery(id+"F0.wireOp",EDGE,"E7.39.0"),sQuery(id+"F0.wireOp",EDGE,"E7.39.1"),sQuery(id+"F0.wireOp",EDGE,"E7.39.2"),sQuery(id+"F0.wireOp",EDGE,"E7.39.3"),sQuery(id+"F0.wireOp",EDGE,"E7.39.4"),sQuery(id+"F0.wireOp",EDGE,"E7.39.5"),sQuery(id+"F0.wireOp",EDGE,"E7.40.0"),sQuery(id+"F0.wireOp",EDGE,"E7.40.1"),sQuery(id+"F0.wireOp",EDGE,"E7.40.2"),sQuery(id+"F0.wireOp",EDGE,"E7.40.3"),sQuery(id+"F0.wireOp",EDGE,"E7.40.4"),sQuery(id+"F0.wireOp",EDGE,"E7.40.5"),sQuery(id+"F0.wireOp",EDGE,"E7.41.0"),sQuery(id+"F0.wireOp",EDGE,"E7.41.1"),sQuery(id+"F0.wireOp",EDGE,"E7.41.2"),sQuery(id+"F0.wireOp",EDGE,"E7.41.3"),sQuery(id+"F0.wireOp",EDGE,"E7.41.4"),sQuery(id+"F0.wireOp",EDGE,"E7.41.5"),sQuery(id+"F0.wireOp",EDGE,"E7.42.0"),sQuery(id+"F0.wireOp",EDGE,"E7.42.1"),sQuery(id+"F0.wireOp",EDGE,"E7.42.2"),sQuery(id+"F0.wireOp",EDGE,"E7.42.3"),sQuery(id+"F0.wireOp",EDGE,"E7.42.4"),sQuery(id+"F0.wireOp",EDGE,"E7.42.5"),sQuery(id+"F0.wireOp",EDGE,"E7.43.0"),sQuery(id+"F0.wireOp",EDGE,"E7.43.1"),sQuery(id+"F0.wireOp",EDGE,"E7.43.2"),sQuery(id+"F0.wireOp",EDGE,"E7.43.3"),sQuery(id+"F0.wireOp",EDGE,"E7.43.4"),sQuery(id+"F0.wireOp",EDGE,"E7.43.5")])],"isStart":false})],"blendedInto":[makeQuery(id+"F1.opExtrude","CAP_FACE",FACE,{"disambiguationData":[OSD([sQuery(id+"F0.wireOp",EDGE,"E1"),sQuery(id+"F0.wireOp",EDGE,"E2"),sQuery(id+"F0.wireOp",EDGE,"E3"),sQuery(id+"F0.wireOp",EDGE,"E4"),sQuery(id+"F0.wireOp",EDGE,"E5"),sQuery(id+"F0.wireOp",EDGE,"E6"),sQuery(id+"F0.wireOp",EDGE,"E7.1.0"),sQuery(id+"F0.wireOp",EDGE,"E7.1.1"),sQuery(id+"F0.wireOp",EDGE,"E7.1.2"),sQuery(id+"F0.wireOp",EDGE,"E7.1.3"),sQuery(id+"F0.wireOp",EDGE,"E7.1.4"),sQuery(id+"F0.wireOp",EDGE,"E7.1.5"),sQuery(id+"F0.wireOp",EDGE,"E7.2.0"),sQuery(id+"F0.wireOp",EDGE,"E7.2.1"),sQuery(id+"F0.wireOp",EDGE,"E7.2.2"),sQuery(id+"F0.wireOp",EDGE,"E7.2.3"),sQuery(id+"F0.wireOp",EDGE,"E7.2.4"),sQuery(id+"F0.wireOp",EDGE,"E7.2.5"),sQuery(id+"F0.wireOp",EDGE,"E7.3.0"),sQuery(id+"F0.wireOp",EDGE,"E7.3.1"),sQuery(id+"F0.wireOp",EDGE,"E7.3.2"),sQuery(id+"F0.wireOp",EDGE,"E7.3.3"),sQuery(id+"F0.wireOp",EDGE,"E7.3.4"),sQuery(id+"F0.wireOp",EDGE,"E7.3.5"),sQuery(id+"F0.wireOp",EDGE,"E7.4.0"),sQuery(id+"F0.wireOp",EDGE,"E7.4.1"),sQuery(id+"F0.wireOp",EDGE,"E7.4.2"),sQuery(id+"F0.wireOp",EDGE,"E7.4.3"),sQuery(id+"F0.wireOp",EDGE,"E7.4.4"),sQuery(id+"F0.wireOp",EDGE,"E7.4.5"),sQuery(id+"F0.wireOp",EDGE,"E7.5.0"),sQuery(id+"F0.wireOp",EDGE,"E7.5.1"),sQuery(id+"F0.wireOp",EDGE,"E7.5.2"),sQuery(id+"F0.wireOp",EDGE,"E7.5.3"),sQuery(id+"F0.wireOp",EDGE,"E7.5.4"),sQuery(id+"F0.wireOp",EDGE,"E7.5.5"),sQuery(id+"F0.wireOp",EDGE,"E7.6.0"),sQuery(id+"F0.wireOp",EDGE,"E7.6.1"),sQuery(id+"F0.wireOp",EDGE,"E7.6.2"),sQuery(id+"F0.wireOp",EDGE,"E7.6.3"),sQuery(id+"F0.wireOp",EDGE,"E7.6.4"),sQuery(id+"F0.wireOp",EDGE,"E7.6.5"),sQuery(id+"F0.wireOp",EDGE,"E7.7.0"),sQuery(id+"F0.wireOp",EDGE,"E7.7.1"),sQuery(id+"F0.wireOp",EDGE,"E7.7.2"),sQuery(id+"F0.wireOp",EDGE,"E7.7.3"),sQuery(id+"F0.wireOp",EDGE,"E7.7.4"),sQuery(id+"F0.wireOp",EDGE,"E7.7.5"),sQuery(id+"F0.wireOp",EDGE,"E7.8.0"),sQuery(id+"F0.wireOp",EDGE,"E7.8.1"),sQuery(id+"F0.wireOp",EDGE,"E7.8.2"),sQuery(id+"F0.wireOp",EDGE,"E7.8.3"),sQuery(id+"F0.wireOp",EDGE,"E7.8.4"),sQuery(id+"F0.wireOp",EDGE,"E7.8.5"),sQuery(id+"F0.wireOp",EDGE,"E7.9.0"),sQuery(id+"F0.wireOp",EDGE,"E7.9.1"),sQuery(id+"F0.wireOp",EDGE,"E7.9.2"),sQuery(id+"F0.wireOp",EDGE,"E7.9.3"),sQuery(id+"F0.wireOp",EDGE,"E7.9.4"),sQuery(id+"F0.wireOp",EDGE,"E7.9.5"),sQuery(id+"F0.wireOp",EDGE,"E7.10.0"),sQuery(id+"F0.wireOp",EDGE,"E7.10.1"),sQuery(id+"F0.wireOp",EDGE,"E7.10.2"),sQuery(id+"F0.wireOp",EDGE,"E7.10.3"),sQuery(id+"F0.wireOp",EDGE,"E7.10.4"),sQuery(id+"F0.wireOp",EDGE,"E7.10.5"),sQuery(id+"F0.wireOp",EDGE,"E7.11.0"),sQuery(id+"F0.wireOp",EDGE,"E7.11.1"),sQuery(id+"F0.wireOp",EDGE,"E7.11.2"),sQuery(id+"F0.wireOp",EDGE,"E7.11.3"),sQuery(id+"F0.wireOp",EDGE,"E7.11.4"),sQuery(id+"F0.wireOp",EDGE,"E7.11.5"),sQuery(id+"F0.wireOp",EDGE,"E7.12.0"),sQuery(id+"F0.wireOp",EDGE,"E7.12.1"),sQuery(id+"F0.wireOp",EDGE,"E7.12.2"),sQuery(id+"F0.wireOp",EDGE,"E7.12.3"),sQuery(id+"F0.wireOp",EDGE,"E7.12.4"),sQuery(id+"F0.wireOp",EDGE,"E7.12.5"),sQuery(id+"F0.wireOp",EDGE,"E7.13.0"),sQuery(id+"F0.wireOp",EDGE,"E7.13.1"),sQuery(id+"F0.wireOp",EDGE,"E7.13.2"),sQuery(id+"F0.wireOp",EDGE,"E7.13.3"),sQuery(id+"F0.wireOp",EDGE,"E7.13.4"),sQuery(id+"F0.wireOp",EDGE,"E7.13.5"),sQuery(id+"F0.wireOp",EDGE,"E7.14.0"),sQuery(id+"F0.wireOp",EDGE,"E7.14.1"),sQuery(id+"F0.wireOp",EDGE,"E7.14.2"),sQuery(id+"F0.wireOp",EDGE,"E7.14.3"),sQuery(id+"F0.wireOp",EDGE,"E7.14.4"),sQuery(id+"F0.wireOp",EDGE,"E7.14.5"),sQuery(id+"F0.wireOp",EDGE,"E7.15.0"),sQuery(id+"F0.wireOp",EDGE,"E7.15.1"),sQuery(id+"F0.wireOp",EDGE,"E7.15.2"),sQuery(id+"F0.wireOp",EDGE,"E7.15.3"),sQuery(id+"F0.wireOp",EDGE,"E7.15.4"),sQuery(id+"F0.wireOp",EDGE,"E7.15.5"),sQuery(id+"F0.wireOp",EDGE,"E7.16.0"),sQuery(id+"F0.wireOp",EDGE,"E7.16.1"),sQuery(id+"F0.wireOp",EDGE,"E7.16.2"),sQuery(id+"F0.wireOp",EDGE,"E7.16.3"),sQuery(id+"F0.wireOp",EDGE,"E7.16.4"),sQuery(id+"F0.wireOp",EDGE,"E7.16.5"),sQuery(id+"F0.wireOp",EDGE,"E7.17.0"),sQuery(id+"F0.wireOp",EDGE,"E7.17.1"),sQuery(id+"F0.wireOp",EDGE,"E7.17.2"),sQuery(id+"F0.wireOp",EDGE,"E7.17.3"),sQuery(id+"F0.wireOp",EDGE,"E7.17.4"),sQuery(id+"F0.wireOp",EDGE,"E7.17.5"),sQuery(id+"F0.wireOp",EDGE,"E7.18.0"),sQuery(id+"F0.wireOp",EDGE,"E7.18.1"),sQuery(id+"F0.wireOp",EDGE,"E7.18.2"),sQuery(id+"F0.wireOp",EDGE,"E7.18.3"),sQuery(id+"F0.wireOp",EDGE,"E7.18.4"),sQuery(id+"F0.wireOp",EDGE,"E7.18.5"),sQuery(id+"F0.wireOp",EDGE,"E7.19.0"),sQuery(id+"F0.wireOp",EDGE,"E7.19.1"),sQuery(id+"F0.wireOp",EDGE,"E7.19.2"),sQuery(id+"F0.wireOp",EDGE,"E7.19.3"),sQuery(id+"F0.wireOp",EDGE,"E7.19.4"),sQuery(id+"F0.wireOp",EDGE,"E7.19.5"),sQuery(id+"F0.wireOp",EDGE,"E7.20.0"),sQuery(id+"F0.wireOp",EDGE,"E7.20.1"),sQuery(id+"F0.wireOp",EDGE,"E7.20.2"),sQuery(id+"F0.wireOp",EDGE,"E7.20.3"),sQuery(id+"F0.wireOp",EDGE,"E7.20.4"),sQuery(id+"F0.wireOp",EDGE,"E7.20.5"),subQ0,sQuery(id+"F0.wireOp",EDGE,"E7.21.1"),sQuery(id+"F0.wireOp",EDGE,"E7.21.2"),sQuery(id+"F0.wireOp",EDGE,"E7.21.3"),sQuery(id+"F0.wireOp",EDGE,"E7.21.4"),sQuery(id+"F0.wireOp",EDGE,"E7.21.5"),sQuery(id+"F0.wireOp",EDGE,"E7.22.0"),sQuery(id+"F0.wireOp",EDGE,"E7.22.1"),sQuery(id+"F0.wireOp",EDGE,"E7.22.2"),sQuery(id+"F0.wireOp",EDGE,"E7.22.3"),sQuery(id+"F0.wireOp",EDGE,"E7.22.4"),sQuery(id+"F0.wireOp",EDGE,"E7.22.5"),sQuery(id+"F0.wireOp",EDGE,"E7.23.0"),sQuery(id+"F0.wireOp",EDGE,"E7.23.1"),sQuery(id+"F0.wireOp",EDGE,"E7.23.2"),sQuery(id+"F0.wireOp",EDGE,"E7.23.3"),sQuery(id+"F0.wireOp",EDGE,"E7.23.4"),sQuery(id+"F0.wireOp",EDGE,"E7.23.5"),sQuery(id+"F0.wireOp",EDGE,"E7.24.0"),sQuery(id+"F0.wireOp",EDGE,"E7.24.1"),sQuery(id+"F0.wireOp",EDGE,"E7.24.2"),sQuery(id+"F0.wireOp",EDGE,"E7.24.3"),sQuery(id+"F0.wireOp",EDGE,"E7.24.4"),sQuery(id+"F0.wireOp",EDGE,"E7.24.5"),sQuery(id+"F0.wireOp",EDGE,"E7.25.0"),sQuery(id+"F0.wireOp",EDGE,"E7.25.1"),sQuery(id+"F0.wireOp",EDGE,"E7.25.2"),sQuery(id+"F0.wireOp",EDGE,"E7.25.3"),sQuery(id+"F0.wireOp",EDGE,"E7.25.4"),sQuery(id+"F0.wireOp",EDGE,"E7.25.5"),sQuery(id+"F0.wireOp",EDGE,"E7.26.0"),sQuery(id+"F0.wireOp",EDGE,"E7.26.1"),sQuery(id+"F0.wireOp",EDGE,"E7.26.2"),sQuery(id+"F0.wireOp",EDGE,"E7.26.3"),sQuery(id+"F0.wireOp",EDGE,"E7.26.4"),sQuery(id+"F0.wireOp",EDGE,"E7.26.5"),sQuery(id+"F0.wireOp",EDGE,"E7.27.0"),sQuery(id+"F0.wireOp",EDGE,"E7.27.1"),sQuery(id+"F0.wireOp",EDGE,"E7.27.2"),sQuery(id+"F0.wireOp",EDGE,"E7.27.3"),sQuery(id+"F0.wireOp",EDGE,"E7.27.4"),sQuery(id+"F0.wireOp",EDGE,"E7.27.5"),sQuery(id+"F0.wireOp",EDGE,"E7.28.0"),sQuery(id+"F0.wireOp",EDGE,"E7.28.1"),sQuery(id+"F0.wireOp",EDGE,"E7.28.2"),sQuery(id+"F0.wireOp",EDGE,"E7.28.3"),sQuery(id+"F0.wireOp",EDGE,"E7.28.4"),sQuery(id+"F0.wireOp",EDGE,"E7.28.5"),sQuery(id+"F0.wireOp",EDGE,"E7.29.0"),sQuery(id+"F0.wireOp",EDGE,"E7.29.1"),sQuery(id+"F0.wireOp",EDGE,"E7.29.2"),sQuery(id+"F0.wireOp",EDGE,"E7.29.3"),sQuery(id+"F0.wireOp",EDGE,"E7.29.4"),sQuery(id+"F0.wireOp",EDGE,"E7.29.5"),sQuery(id+"F0.wireOp",EDGE,"E7.30.0"),sQuery(id+"F0.wireOp",EDGE,"E7.30.1"),sQuery(id+"F0.wireOp",EDGE,"E7.30.2"),sQuery(id+"F0.wireOp",EDGE,"E7.30.3"),sQuery(id+"F0.wireOp",EDGE,"E7.30.4"),sQuery(id+"F0.wireOp",EDGE,"E7.30.5"),sQuery(id+"F0.wireOp",EDGE,"E7.31.0"),sQuery(id+"F0.wireOp",EDGE,"E7.31.1"),sQuery(id+"F0.wireOp",EDGE,"E7.31.2"),sQuery(id+"F0.wireOp",EDGE,"E7.31.3"),sQuery(id+"F0.wireOp",EDGE,"E7.31.4"),sQuery(id+"F0.wireOp",EDGE,"E7.31.5"),sQuery(id+"F0.wireOp",EDGE,"E7.32.0"),sQuery(id+"F0.wireOp",EDGE,"E7.32.1"),sQuery(id+"F0.wireOp",EDGE,"E7.32.2"),sQuery(id+"F0.wireOp",EDGE,"E7.32.3"),sQuery(id+"F0.wireOp",EDGE,"E7.32.4"),sQuery(id+"F0.wireOp",EDGE,"E7.32.5"),sQuery(id+"F0.wireOp",EDGE,"E7.33.0"),sQuery(id+"F0.wireOp",EDGE,"E7.33.1"),sQuery(id+"F0.wireOp",EDGE,"E7.33.2"),sQuery(id+"F0.wireOp",EDGE,"E7.33.3"),sQuery(id+"F0.wireOp",EDGE,"E7.33.4"),sQuery(id+"F0.wireOp",EDGE,"E7.33.5"),sQuery(id+"F0.wireOp",EDGE,"E7.34.0"),sQuery(id+"F0.wireOp",EDGE,"E7.34.1"),sQuery(id+"F0.wireOp",EDGE,"E7.34.2"),sQuery(id+"F0.wireOp",EDGE,"E7.34.3"),sQuery(id+"F0.wireOp",EDGE,"E7.34.4"),sQuery(id+"F0.wireOp",EDGE,"E7.34.5"),sQuery(id+"F0.wireOp",EDGE,"E7.35.0"),sQuery(id+"F0.wireOp",EDGE,"E7.35.1"),sQuery(id+"F0.wireOp",EDGE,"E7.35.2"),sQuery(id+"F0.wireOp",EDGE,"E7.35.3"),sQuery(id+"F0.wireOp",EDGE,"E7.35.4"),sQuery(id+"F0.wireOp",EDGE,"E7.35.5"),sQuery(id+"F0.wireOp",EDGE,"E7.36.0"),sQuery(id+"F0.wireOp",EDGE,"E7.36.1"),sQuery(id+"F0.wireOp",EDGE,"E7.36.2"),sQuery(id+"F0.wireOp",EDGE,"E7.36.3"),sQuery(id+"F0.wireOp",EDGE,"E7.36.4"),sQuery(id+"F0.wireOp",EDGE,"E7.36.5"),sQuery(id+"F0.wireOp",EDGE,"E7.37.0"),sQuery(id+"F0.wireOp",EDGE,"E7.37.1"),sQuery(id+"F0.wireOp",EDGE,"E7.37.2"),sQuery(id+"F0.wireOp",EDGE,"E7.37.3"),sQuery(id+"F0.wireOp",EDGE,"E7.37.4"),sQuery(id+"F0.wireOp",EDGE,"E7.37.5"),sQuery(id+"F0.wireOp",EDGE,"E7.38.0"),sQuery(id+"F0.wireOp",EDGE,"E7.38.1"),sQuery(id+"F0.wireOp",EDGE,"E7.38.2"),sQuery(id+"F0.wireOp",EDGE,"E7.38.3"),sQuery(id+"F0.wireOp",EDGE,"E7.38.4"),sQuery(id+"F0.wireOp",EDGE,"E7.38.5"),sQuery(id+"F0.wireOp",EDGE,"E7.39.0"),sQuery(id+"F0.wireOp",EDGE,"E7.39.1"),sQuery(id+"F0.wireOp",EDGE,"E7.39.2"),sQuery(id+"F0.wireOp",EDGE,"E7.39.3"),sQuery(id+"F0.wireOp",EDGE,"E7.39.4"),sQuery(id+"F0.wireOp",EDGE,"E7.39.5"),sQuery(id+"F0.wireOp",EDGE,"E7.40.0"),sQuery(id+"F0.wireOp",EDGE,"E7.40.1"),sQuery(id+"F0.wireOp",EDGE,"E7.40.2"),sQuery(id+"F0.wireOp",EDGE,"E7.40.3"),sQuery(id+"F0.wireOp",EDGE,"E7.40.4"),sQuery(id+"F0.wireOp",EDGE,"E7.40.5"),sQuery(id+"F0.wireOp",EDGE,"E7.41.0"),sQuery(id+"F0.wireOp",EDGE,"E7.41.1"),sQuery(id+"F0.wireOp",EDGE,"E7.41.2"),sQuery(id+"F0.wireOp",EDGE,"E7.41.3"),sQuery(id+"F0.wireOp",EDGE,"E7.41.4"),sQuery(id+"F0.wireOp",EDGE,"E7.41.5"),sQuery(id+"F0.wireOp",EDGE,"E7.42.0"),sQuery(id+"F0.wireOp",EDGE,"E7.42.1"),sQuery(id+"F0.wireOp",EDGE,"E7.42.2"),sQuery(id+"F0.wireOp",EDGE,"E7.42.3"),sQuery(id+"F0.wireOp",EDGE,"E7.42.4"),sQuery(id+"F0.wireOp",EDGE,"E7.42.5"),sQuery(id+"F0.wireOp",EDGE,"E7.43.0"),sQuery(id+"F0.wireOp",EDGE,"E7.43.1"),sQuery(id+"F0.wireOp",EDGE,"E7.43.2"),sQuery(id+"F0.wireOp",EDGE,"E7.43.3"),sQuery(id+"F0.wireOp",EDGE,"E7.43.4"),sQuery(id+"F0.wireOp",EDGE,"E7.43.5")])],"isStart":false})]});}
            var Q12;
            {var subQ0=sQuery(id+"F0.wireOp",EDGE,"E7.19.0");Q12=makeQuery(id+"F2.opChamfer","BLEND_EDGE",EDGE,{"blendedFrom":[makeQuery(id+"F1.opExtrude","CAP_EDGE",EDGE,{"disambiguationData":[OSD([subQ0])],"isStart":false}),makeQuery(id+"F1.opExtrude","CAP_FACE",FACE,{"disambiguationData":[OSD([sQuery(id+"F0.wireOp",EDGE,"E1"),sQuery(id+"F0.wireOp",EDGE,"E2"),sQuery(id+"F0.wireOp",EDGE,"E3"),sQuery(id+"F0.wireOp",EDGE,"E4"),sQuery(id+"F0.wireOp",EDGE,"E5"),sQuery(id+"F0.wireOp",EDGE,"E6"),sQuery(id+"F0.wireOp",EDGE,"E7.1.0"),sQuery(id+"F0.wireOp",EDGE,"E7.1.1"),sQuery(id+"F0.wireOp",EDGE,"E7.1.2"),sQuery(id+"F0.wireOp",EDGE,"E7.1.3"),sQuery(id+"F0.wireOp",EDGE,"E7.1.4"),sQuery(id+"F0.wireOp",EDGE,"E7.1.5"),sQuery(id+"F0.wireOp",EDGE,"E7.2.0"),sQuery(id+"F0.wireOp",EDGE,"E7.2.1"),sQuery(id+"F0.wireOp",EDGE,"E7.2.2"),sQuery(id+"F0.wireOp",EDGE,"E7.2.3"),sQuery(id+"F0.wireOp",EDGE,"E7.2.4"),sQuery(id+"F0.wireOp",EDGE,"E7.2.5"),sQuery(id+"F0.wireOp",EDGE,"E7.3.0"),sQuery(id+"F0.wireOp",EDGE,"E7.3.1"),sQuery(id+"F0.wireOp",EDGE,"E7.3.2"),sQuery(id+"F0.wireOp",EDGE,"E7.3.3"),sQuery(id+"F0.wireOp",EDGE,"E7.3.4"),sQuery(id+"F0.wireOp",EDGE,"E7.3.5"),sQuery(id+"F0.wireOp",EDGE,"E7.4.0"),sQuery(id+"F0.wireOp",EDGE,"E7.4.1"),sQuery(id+"F0.wireOp",EDGE,"E7.4.2"),sQuery(id+"F0.wireOp",EDGE,"E7.4.3"),sQuery(id+"F0.wireOp",EDGE,"E7.4.4"),sQuery(id+"F0.wireOp",EDGE,"E7.4.5"),sQuery(id+"F0.wireOp",EDGE,"E7.5.0"),sQuery(id+"F0.wireOp",EDGE,"E7.5.1"),sQuery(id+"F0.wireOp",EDGE,"E7.5.2"),sQuery(id+"F0.wireOp",EDGE,"E7.5.3"),sQuery(id+"F0.wireOp",EDGE,"E7.5.4"),sQuery(id+"F0.wireOp",EDGE,"E7.5.5"),sQuery(id+"F0.wireOp",EDGE,"E7.6.0"),sQuery(id+"F0.wireOp",EDGE,"E7.6.1"),sQuery(id+"F0.wireOp",EDGE,"E7.6.2"),sQuery(id+"F0.wireOp",EDGE,"E7.6.3"),sQuery(id+"F0.wireOp",EDGE,"E7.6.4"),sQuery(id+"F0.wireOp",EDGE,"E7.6.5"),sQuery(id+"F0.wireOp",EDGE,"E7.7.0"),sQuery(id+"F0.wireOp",EDGE,"E7.7.1"),sQuery(id+"F0.wireOp",EDGE,"E7.7.2"),sQuery(id+"F0.wireOp",EDGE,"E7.7.3"),sQuery(id+"F0.wireOp",EDGE,"E7.7.4"),sQuery(id+"F0.wireOp",EDGE,"E7.7.5"),sQuery(id+"F0.wireOp",EDGE,"E7.8.0"),sQuery(id+"F0.wireOp",EDGE,"E7.8.1"),sQuery(id+"F0.wireOp",EDGE,"E7.8.2"),sQuery(id+"F0.wireOp",EDGE,"E7.8.3"),sQuery(id+"F0.wireOp",EDGE,"E7.8.4"),sQuery(id+"F0.wireOp",EDGE,"E7.8.5"),sQuery(id+"F0.wireOp",EDGE,"E7.9.0"),sQuery(id+"F0.wireOp",EDGE,"E7.9.1"),sQuery(id+"F0.wireOp",EDGE,"E7.9.2"),sQuery(id+"F0.wireOp",EDGE,"E7.9.3"),sQuery(id+"F0.wireOp",EDGE,"E7.9.4"),sQuery(id+"F0.wireOp",EDGE,"E7.9.5"),sQuery(id+"F0.wireOp",EDGE,"E7.10.0"),sQuery(id+"F0.wireOp",EDGE,"E7.10.1"),sQuery(id+"F0.wireOp",EDGE,"E7.10.2"),sQuery(id+"F0.wireOp",EDGE,"E7.10.3"),sQuery(id+"F0.wireOp",EDGE,"E7.10.4"),sQuery(id+"F0.wireOp",EDGE,"E7.10.5"),sQuery(id+"F0.wireOp",EDGE,"E7.11.0"),sQuery(id+"F0.wireOp",EDGE,"E7.11.1"),sQuery(id+"F0.wireOp",EDGE,"E7.11.2"),sQuery(id+"F0.wireOp",EDGE,"E7.11.3"),sQuery(id+"F0.wireOp",EDGE,"E7.11.4"),sQuery(id+"F0.wireOp",EDGE,"E7.11.5"),sQuery(id+"F0.wireOp",EDGE,"E7.12.0"),sQuery(id+"F0.wireOp",EDGE,"E7.12.1"),sQuery(id+"F0.wireOp",EDGE,"E7.12.2"),sQuery(id+"F0.wireOp",EDGE,"E7.12.3"),sQuery(id+"F0.wireOp",EDGE,"E7.12.4"),sQuery(id+"F0.wireOp",EDGE,"E7.12.5"),sQuery(id+"F0.wireOp",EDGE,"E7.13.0"),sQuery(id+"F0.wireOp",EDGE,"E7.13.1"),sQuery(id+"F0.wireOp",EDGE,"E7.13.2"),sQuery(id+"F0.wireOp",EDGE,"E7.13.3"),sQuery(id+"F0.wireOp",EDGE,"E7.13.4"),sQuery(id+"F0.wireOp",EDGE,"E7.13.5"),sQuery(id+"F0.wireOp",EDGE,"E7.14.0"),sQuery(id+"F0.wireOp",EDGE,"E7.14.1"),sQuery(id+"F0.wireOp",EDGE,"E7.14.2"),sQuery(id+"F0.wireOp",EDGE,"E7.14.3"),sQuery(id+"F0.wireOp",EDGE,"E7.14.4"),sQuery(id+"F0.wireOp",EDGE,"E7.14.5"),sQuery(id+"F0.wireOp",EDGE,"E7.15.0"),sQuery(id+"F0.wireOp",EDGE,"E7.15.1"),sQuery(id+"F0.wireOp",EDGE,"E7.15.2"),sQuery(id+"F0.wireOp",EDGE,"E7.15.3"),sQuery(id+"F0.wireOp",EDGE,"E7.15.4"),sQuery(id+"F0.wireOp",EDGE,"E7.15.5"),sQuery(id+"F0.wireOp",EDGE,"E7.16.0"),sQuery(id+"F0.wireOp",EDGE,"E7.16.1"),sQuery(id+"F0.wireOp",EDGE,"E7.16.2"),sQuery(id+"F0.wireOp",EDGE,"E7.16.3"),sQuery(id+"F0.wireOp",EDGE,"E7.16.4"),sQuery(id+"F0.wireOp",EDGE,"E7.16.5"),sQuery(id+"F0.wireOp",EDGE,"E7.17.0"),sQuery(id+"F0.wireOp",EDGE,"E7.17.1"),sQuery(id+"F0.wireOp",EDGE,"E7.17.2"),sQuery(id+"F0.wireOp",EDGE,"E7.17.3"),sQuery(id+"F0.wireOp",EDGE,"E7.17.4"),sQuery(id+"F0.wireOp",EDGE,"E7.17.5"),sQuery(id+"F0.wireOp",EDGE,"E7.18.0"),sQuery(id+"F0.wireOp",EDGE,"E7.18.1"),sQuery(id+"F0.wireOp",EDGE,"E7.18.2"),sQuery(id+"F0.wireOp",EDGE,"E7.18.3"),sQuery(id+"F0.wireOp",EDGE,"E7.18.4"),sQuery(id+"F0.wireOp",EDGE,"E7.18.5"),subQ0,sQuery(id+"F0.wireOp",EDGE,"E7.19.1"),sQuery(id+"F0.wireOp",EDGE,"E7.19.2"),sQuery(id+"F0.wireOp",EDGE,"E7.19.3"),sQuery(id+"F0.wireOp",EDGE,"E7.19.4"),sQuery(id+"F0.wireOp",EDGE,"E7.19.5"),sQuery(id+"F0.wireOp",EDGE,"E7.20.0"),sQuery(id+"F0.wireOp",EDGE,"E7.20.1"),sQuery(id+"F0.wireOp",EDGE,"E7.20.2"),sQuery(id+"F0.wireOp",EDGE,"E7.20.3"),sQuery(id+"F0.wireOp",EDGE,"E7.20.4"),sQuery(id+"F0.wireOp",EDGE,"E7.20.5"),sQuery(id+"F0.wireOp",EDGE,"E7.21.0"),sQuery(id+"F0.wireOp",EDGE,"E7.21.1"),sQuery(id+"F0.wireOp",EDGE,"E7.21.2"),sQuery(id+"F0.wireOp",EDGE,"E7.21.3"),sQuery(id+"F0.wireOp",EDGE,"E7.21.4"),sQuery(id+"F0.wireOp",EDGE,"E7.21.5"),sQuery(id+"F0.wireOp",EDGE,"E7.22.0"),sQuery(id+"F0.wireOp",EDGE,"E7.22.1"),sQuery(id+"F0.wireOp",EDGE,"E7.22.2"),sQuery(id+"F0.wireOp",EDGE,"E7.22.3"),sQuery(id+"F0.wireOp",EDGE,"E7.22.4"),sQuery(id+"F0.wireOp",EDGE,"E7.22.5"),sQuery(id+"F0.wireOp",EDGE,"E7.23.0"),sQuery(id+"F0.wireOp",EDGE,"E7.23.1"),sQuery(id+"F0.wireOp",EDGE,"E7.23.2"),sQuery(id+"F0.wireOp",EDGE,"E7.23.3"),sQuery(id+"F0.wireOp",EDGE,"E7.23.4"),sQuery(id+"F0.wireOp",EDGE,"E7.23.5"),sQuery(id+"F0.wireOp",EDGE,"E7.24.0"),sQuery(id+"F0.wireOp",EDGE,"E7.24.1"),sQuery(id+"F0.wireOp",EDGE,"E7.24.2"),sQuery(id+"F0.wireOp",EDGE,"E7.24.3"),sQuery(id+"F0.wireOp",EDGE,"E7.24.4"),sQuery(id+"F0.wireOp",EDGE,"E7.24.5"),sQuery(id+"F0.wireOp",EDGE,"E7.25.0"),sQuery(id+"F0.wireOp",EDGE,"E7.25.1"),sQuery(id+"F0.wireOp",EDGE,"E7.25.2"),sQuery(id+"F0.wireOp",EDGE,"E7.25.3"),sQuery(id+"F0.wireOp",EDGE,"E7.25.4"),sQuery(id+"F0.wireOp",EDGE,"E7.25.5"),sQuery(id+"F0.wireOp",EDGE,"E7.26.0"),sQuery(id+"F0.wireOp",EDGE,"E7.26.1"),sQuery(id+"F0.wireOp",EDGE,"E7.26.2"),sQuery(id+"F0.wireOp",EDGE,"E7.26.3"),sQuery(id+"F0.wireOp",EDGE,"E7.26.4"),sQuery(id+"F0.wireOp",EDGE,"E7.26.5"),sQuery(id+"F0.wireOp",EDGE,"E7.27.0"),sQuery(id+"F0.wireOp",EDGE,"E7.27.1"),sQuery(id+"F0.wireOp",EDGE,"E7.27.2"),sQuery(id+"F0.wireOp",EDGE,"E7.27.3"),sQuery(id+"F0.wireOp",EDGE,"E7.27.4"),sQuery(id+"F0.wireOp",EDGE,"E7.27.5"),sQuery(id+"F0.wireOp",EDGE,"E7.28.0"),sQuery(id+"F0.wireOp",EDGE,"E7.28.1"),sQuery(id+"F0.wireOp",EDGE,"E7.28.2"),sQuery(id+"F0.wireOp",EDGE,"E7.28.3"),sQuery(id+"F0.wireOp",EDGE,"E7.28.4"),sQuery(id+"F0.wireOp",EDGE,"E7.28.5"),sQuery(id+"F0.wireOp",EDGE,"E7.29.0"),sQuery(id+"F0.wireOp",EDGE,"E7.29.1"),sQuery(id+"F0.wireOp",EDGE,"E7.29.2"),sQuery(id+"F0.wireOp",EDGE,"E7.29.3"),sQuery(id+"F0.wireOp",EDGE,"E7.29.4"),sQuery(id+"F0.wireOp",EDGE,"E7.29.5"),sQuery(id+"F0.wireOp",EDGE,"E7.30.0"),sQuery(id+"F0.wireOp",EDGE,"E7.30.1"),sQuery(id+"F0.wireOp",EDGE,"E7.30.2"),sQuery(id+"F0.wireOp",EDGE,"E7.30.3"),sQuery(id+"F0.wireOp",EDGE,"E7.30.4"),sQuery(id+"F0.wireOp",EDGE,"E7.30.5"),sQuery(id+"F0.wireOp",EDGE,"E7.31.0"),sQuery(id+"F0.wireOp",EDGE,"E7.31.1"),sQuery(id+"F0.wireOp",EDGE,"E7.31.2"),sQuery(id+"F0.wireOp",EDGE,"E7.31.3"),sQuery(id+"F0.wireOp",EDGE,"E7.31.4"),sQuery(id+"F0.wireOp",EDGE,"E7.31.5"),sQuery(id+"F0.wireOp",EDGE,"E7.32.0"),sQuery(id+"F0.wireOp",EDGE,"E7.32.1"),sQuery(id+"F0.wireOp",EDGE,"E7.32.2"),sQuery(id+"F0.wireOp",EDGE,"E7.32.3"),sQuery(id+"F0.wireOp",EDGE,"E7.32.4"),sQuery(id+"F0.wireOp",EDGE,"E7.32.5"),sQuery(id+"F0.wireOp",EDGE,"E7.33.0"),sQuery(id+"F0.wireOp",EDGE,"E7.33.1"),sQuery(id+"F0.wireOp",EDGE,"E7.33.2"),sQuery(id+"F0.wireOp",EDGE,"E7.33.3"),sQuery(id+"F0.wireOp",EDGE,"E7.33.4"),sQuery(id+"F0.wireOp",EDGE,"E7.33.5"),sQuery(id+"F0.wireOp",EDGE,"E7.34.0"),sQuery(id+"F0.wireOp",EDGE,"E7.34.1"),sQuery(id+"F0.wireOp",EDGE,"E7.34.2"),sQuery(id+"F0.wireOp",EDGE,"E7.34.3"),sQuery(id+"F0.wireOp",EDGE,"E7.34.4"),sQuery(id+"F0.wireOp",EDGE,"E7.34.5"),sQuery(id+"F0.wireOp",EDGE,"E7.35.0"),sQuery(id+"F0.wireOp",EDGE,"E7.35.1"),sQuery(id+"F0.wireOp",EDGE,"E7.35.2"),sQuery(id+"F0.wireOp",EDGE,"E7.35.3"),sQuery(id+"F0.wireOp",EDGE,"E7.35.4"),sQuery(id+"F0.wireOp",EDGE,"E7.35.5"),sQuery(id+"F0.wireOp",EDGE,"E7.36.0"),sQuery(id+"F0.wireOp",EDGE,"E7.36.1"),sQuery(id+"F0.wireOp",EDGE,"E7.36.2"),sQuery(id+"F0.wireOp",EDGE,"E7.36.3"),sQuery(id+"F0.wireOp",EDGE,"E7.36.4"),sQuery(id+"F0.wireOp",EDGE,"E7.36.5"),sQuery(id+"F0.wireOp",EDGE,"E7.37.0"),sQuery(id+"F0.wireOp",EDGE,"E7.37.1"),sQuery(id+"F0.wireOp",EDGE,"E7.37.2"),sQuery(id+"F0.wireOp",EDGE,"E7.37.3"),sQuery(id+"F0.wireOp",EDGE,"E7.37.4"),sQuery(id+"F0.wireOp",EDGE,"E7.37.5"),sQuery(id+"F0.wireOp",EDGE,"E7.38.0"),sQuery(id+"F0.wireOp",EDGE,"E7.38.1"),sQuery(id+"F0.wireOp",EDGE,"E7.38.2"),sQuery(id+"F0.wireOp",EDGE,"E7.38.3"),sQuery(id+"F0.wireOp",EDGE,"E7.38.4"),sQuery(id+"F0.wireOp",EDGE,"E7.38.5"),sQuery(id+"F0.wireOp",EDGE,"E7.39.0"),sQuery(id+"F0.wireOp",EDGE,"E7.39.1"),sQuery(id+"F0.wireOp",EDGE,"E7.39.2"),sQuery(id+"F0.wireOp",EDGE,"E7.39.3"),sQuery(id+"F0.wireOp",EDGE,"E7.39.4"),sQuery(id+"F0.wireOp",EDGE,"E7.39.5"),sQuery(id+"F0.wireOp",EDGE,"E7.40.0"),sQuery(id+"F0.wireOp",EDGE,"E7.40.1"),sQuery(id+"F0.wireOp",EDGE,"E7.40.2"),sQuery(id+"F0.wireOp",EDGE,"E7.40.3"),sQuery(id+"F0.wireOp",EDGE,"E7.40.4"),sQuery(id+"F0.wireOp",EDGE,"E7.40.5"),sQuery(id+"F0.wireOp",EDGE,"E7.41.0"),sQuery(id+"F0.wireOp",EDGE,"E7.41.1"),sQuery(id+"F0.wireOp",EDGE,"E7.41.2"),sQuery(id+"F0.wireOp",EDGE,"E7.41.3"),sQuery(id+"F0.wireOp",EDGE,"E7.41.4"),sQuery(id+"F0.wireOp",EDGE,"E7.41.5"),sQuery(id+"F0.wireOp",EDGE,"E7.42.0"),sQuery(id+"F0.wireOp",EDGE,"E7.42.1"),sQuery(id+"F0.wireOp",EDGE,"E7.42.2"),sQuery(id+"F0.wireOp",EDGE,"E7.42.3"),sQuery(id+"F0.wireOp",EDGE,"E7.42.4"),sQuery(id+"F0.wireOp",EDGE,"E7.42.5"),sQuery(id+"F0.wireOp",EDGE,"E7.43.0"),sQuery(id+"F0.wireOp",EDGE,"E7.43.1"),sQuery(id+"F0.wireOp",EDGE,"E7.43.2"),sQuery(id+"F0.wireOp",EDGE,"E7.43.3"),sQuery(id+"F0.wireOp",EDGE,"E7.43.4"),sQuery(id+"F0.wireOp",EDGE,"E7.43.5")])],"isStart":false})],"blendedInto":[makeQuery(id+"F1.opExtrude","CAP_FACE",FACE,{"disambiguationData":[OSD([sQuery(id+"F0.wireOp",EDGE,"E1"),sQuery(id+"F0.wireOp",EDGE,"E2"),sQuery(id+"F0.wireOp",EDGE,"E3"),sQuery(id+"F0.wireOp",EDGE,"E4"),sQuery(id+"F0.wireOp",EDGE,"E5"),sQuery(id+"F0.wireOp",EDGE,"E6"),sQuery(id+"F0.wireOp",EDGE,"E7.1.0"),sQuery(id+"F0.wireOp",EDGE,"E7.1.1"),sQuery(id+"F0.wireOp",EDGE,"E7.1.2"),sQuery(id+"F0.wireOp",EDGE,"E7.1.3"),sQuery(id+"F0.wireOp",EDGE,"E7.1.4"),sQuery(id+"F0.wireOp",EDGE,"E7.1.5"),sQuery(id+"F0.wireOp",EDGE,"E7.2.0"),sQuery(id+"F0.wireOp",EDGE,"E7.2.1"),sQuery(id+"F0.wireOp",EDGE,"E7.2.2"),sQuery(id+"F0.wireOp",EDGE,"E7.2.3"),sQuery(id+"F0.wireOp",EDGE,"E7.2.4"),sQuery(id+"F0.wireOp",EDGE,"E7.2.5"),sQuery(id+"F0.wireOp",EDGE,"E7.3.0"),sQuery(id+"F0.wireOp",EDGE,"E7.3.1"),sQuery(id+"F0.wireOp",EDGE,"E7.3.2"),sQuery(id+"F0.wireOp",EDGE,"E7.3.3"),sQuery(id+"F0.wireOp",EDGE,"E7.3.4"),sQuery(id+"F0.wireOp",EDGE,"E7.3.5"),sQuery(id+"F0.wireOp",EDGE,"E7.4.0"),sQuery(id+"F0.wireOp",EDGE,"E7.4.1"),sQuery(id+"F0.wireOp",EDGE,"E7.4.2"),sQuery(id+"F0.wireOp",EDGE,"E7.4.3"),sQuery(id+"F0.wireOp",EDGE,"E7.4.4"),sQuery(id+"F0.wireOp",EDGE,"E7.4.5"),sQuery(id+"F0.wireOp",EDGE,"E7.5.0"),sQuery(id+"F0.wireOp",EDGE,"E7.5.1"),sQuery(id+"F0.wireOp",EDGE,"E7.5.2"),sQuery(id+"F0.wireOp",EDGE,"E7.5.3"),sQuery(id+"F0.wireOp",EDGE,"E7.5.4"),sQuery(id+"F0.wireOp",EDGE,"E7.5.5"),sQuery(id+"F0.wireOp",EDGE,"E7.6.0"),sQuery(id+"F0.wireOp",EDGE,"E7.6.1"),sQuery(id+"F0.wireOp",EDGE,"E7.6.2"),sQuery(id+"F0.wireOp",EDGE,"E7.6.3"),sQuery(id+"F0.wireOp",EDGE,"E7.6.4"),sQuery(id+"F0.wireOp",EDGE,"E7.6.5"),sQuery(id+"F0.wireOp",EDGE,"E7.7.0"),sQuery(id+"F0.wireOp",EDGE,"E7.7.1"),sQuery(id+"F0.wireOp",EDGE,"E7.7.2"),sQuery(id+"F0.wireOp",EDGE,"E7.7.3"),sQuery(id+"F0.wireOp",EDGE,"E7.7.4"),sQuery(id+"F0.wireOp",EDGE,"E7.7.5"),sQuery(id+"F0.wireOp",EDGE,"E7.8.0"),sQuery(id+"F0.wireOp",EDGE,"E7.8.1"),sQuery(id+"F0.wireOp",EDGE,"E7.8.2"),sQuery(id+"F0.wireOp",EDGE,"E7.8.3"),sQuery(id+"F0.wireOp",EDGE,"E7.8.4"),sQuery(id+"F0.wireOp",EDGE,"E7.8.5"),sQuery(id+"F0.wireOp",EDGE,"E7.9.0"),sQuery(id+"F0.wireOp",EDGE,"E7.9.1"),sQuery(id+"F0.wireOp",EDGE,"E7.9.2"),sQuery(id+"F0.wireOp",EDGE,"E7.9.3"),sQuery(id+"F0.wireOp",EDGE,"E7.9.4"),sQuery(id+"F0.wireOp",EDGE,"E7.9.5"),sQuery(id+"F0.wireOp",EDGE,"E7.10.0"),sQuery(id+"F0.wireOp",EDGE,"E7.10.1"),sQuery(id+"F0.wireOp",EDGE,"E7.10.2"),sQuery(id+"F0.wireOp",EDGE,"E7.10.3"),sQuery(id+"F0.wireOp",EDGE,"E7.10.4"),sQuery(id+"F0.wireOp",EDGE,"E7.10.5"),sQuery(id+"F0.wireOp",EDGE,"E7.11.0"),sQuery(id+"F0.wireOp",EDGE,"E7.11.1"),sQuery(id+"F0.wireOp",EDGE,"E7.11.2"),sQuery(id+"F0.wireOp",EDGE,"E7.11.3"),sQuery(id+"F0.wireOp",EDGE,"E7.11.4"),sQuery(id+"F0.wireOp",EDGE,"E7.11.5"),sQuery(id+"F0.wireOp",EDGE,"E7.12.0"),sQuery(id+"F0.wireOp",EDGE,"E7.12.1"),sQuery(id+"F0.wireOp",EDGE,"E7.12.2"),sQuery(id+"F0.wireOp",EDGE,"E7.12.3"),sQuery(id+"F0.wireOp",EDGE,"E7.12.4"),sQuery(id+"F0.wireOp",EDGE,"E7.12.5"),sQuery(id+"F0.wireOp",EDGE,"E7.13.0"),sQuery(id+"F0.wireOp",EDGE,"E7.13.1"),sQuery(id+"F0.wireOp",EDGE,"E7.13.2"),sQuery(id+"F0.wireOp",EDGE,"E7.13.3"),sQuery(id+"F0.wireOp",EDGE,"E7.13.4"),sQuery(id+"F0.wireOp",EDGE,"E7.13.5"),sQuery(id+"F0.wireOp",EDGE,"E7.14.0"),sQuery(id+"F0.wireOp",EDGE,"E7.14.1"),sQuery(id+"F0.wireOp",EDGE,"E7.14.2"),sQuery(id+"F0.wireOp",EDGE,"E7.14.3"),sQuery(id+"F0.wireOp",EDGE,"E7.14.4"),sQuery(id+"F0.wireOp",EDGE,"E7.14.5"),sQuery(id+"F0.wireOp",EDGE,"E7.15.0"),sQuery(id+"F0.wireOp",EDGE,"E7.15.1"),sQuery(id+"F0.wireOp",EDGE,"E7.15.2"),sQuery(id+"F0.wireOp",EDGE,"E7.15.3"),sQuery(id+"F0.wireOp",EDGE,"E7.15.4"),sQuery(id+"F0.wireOp",EDGE,"E7.15.5"),sQuery(id+"F0.wireOp",EDGE,"E7.16.0"),sQuery(id+"F0.wireOp",EDGE,"E7.16.1"),sQuery(id+"F0.wireOp",EDGE,"E7.16.2"),sQuery(id+"F0.wireOp",EDGE,"E7.16.3"),sQuery(id+"F0.wireOp",EDGE,"E7.16.4"),sQuery(id+"F0.wireOp",EDGE,"E7.16.5"),sQuery(id+"F0.wireOp",EDGE,"E7.17.0"),sQuery(id+"F0.wireOp",EDGE,"E7.17.1"),sQuery(id+"F0.wireOp",EDGE,"E7.17.2"),sQuery(id+"F0.wireOp",EDGE,"E7.17.3"),sQuery(id+"F0.wireOp",EDGE,"E7.17.4"),sQuery(id+"F0.wireOp",EDGE,"E7.17.5"),sQuery(id+"F0.wireOp",EDGE,"E7.18.0"),sQuery(id+"F0.wireOp",EDGE,"E7.18.1"),sQuery(id+"F0.wireOp",EDGE,"E7.18.2"),sQuery(id+"F0.wireOp",EDGE,"E7.18.3"),sQuery(id+"F0.wireOp",EDGE,"E7.18.4"),sQuery(id+"F0.wireOp",EDGE,"E7.18.5"),subQ0,sQuery(id+"F0.wireOp",EDGE,"E7.19.1"),sQuery(id+"F0.wireOp",EDGE,"E7.19.2"),sQuery(id+"F0.wireOp",EDGE,"E7.19.3"),sQuery(id+"F0.wireOp",EDGE,"E7.19.4"),sQuery(id+"F0.wireOp",EDGE,"E7.19.5"),sQuery(id+"F0.wireOp",EDGE,"E7.20.0"),sQuery(id+"F0.wireOp",EDGE,"E7.20.1"),sQuery(id+"F0.wireOp",EDGE,"E7.20.2"),sQuery(id+"F0.wireOp",EDGE,"E7.20.3"),sQuery(id+"F0.wireOp",EDGE,"E7.20.4"),sQuery(id+"F0.wireOp",EDGE,"E7.20.5"),sQuery(id+"F0.wireOp",EDGE,"E7.21.0"),sQuery(id+"F0.wireOp",EDGE,"E7.21.1"),sQuery(id+"F0.wireOp",EDGE,"E7.21.2"),sQuery(id+"F0.wireOp",EDGE,"E7.21.3"),sQuery(id+"F0.wireOp",EDGE,"E7.21.4"),sQuery(id+"F0.wireOp",EDGE,"E7.21.5"),sQuery(id+"F0.wireOp",EDGE,"E7.22.0"),sQuery(id+"F0.wireOp",EDGE,"E7.22.1"),sQuery(id+"F0.wireOp",EDGE,"E7.22.2"),sQuery(id+"F0.wireOp",EDGE,"E7.22.3"),sQuery(id+"F0.wireOp",EDGE,"E7.22.4"),sQuery(id+"F0.wireOp",EDGE,"E7.22.5"),sQuery(id+"F0.wireOp",EDGE,"E7.23.0"),sQuery(id+"F0.wireOp",EDGE,"E7.23.1"),sQuery(id+"F0.wireOp",EDGE,"E7.23.2"),sQuery(id+"F0.wireOp",EDGE,"E7.23.3"),sQuery(id+"F0.wireOp",EDGE,"E7.23.4"),sQuery(id+"F0.wireOp",EDGE,"E7.23.5"),sQuery(id+"F0.wireOp",EDGE,"E7.24.0"),sQuery(id+"F0.wireOp",EDGE,"E7.24.1"),sQuery(id+"F0.wireOp",EDGE,"E7.24.2"),sQuery(id+"F0.wireOp",EDGE,"E7.24.3"),sQuery(id+"F0.wireOp",EDGE,"E7.24.4"),sQuery(id+"F0.wireOp",EDGE,"E7.24.5"),sQuery(id+"F0.wireOp",EDGE,"E7.25.0"),sQuery(id+"F0.wireOp",EDGE,"E7.25.1"),sQuery(id+"F0.wireOp",EDGE,"E7.25.2"),sQuery(id+"F0.wireOp",EDGE,"E7.25.3"),sQuery(id+"F0.wireOp",EDGE,"E7.25.4"),sQuery(id+"F0.wireOp",EDGE,"E7.25.5"),sQuery(id+"F0.wireOp",EDGE,"E7.26.0"),sQuery(id+"F0.wireOp",EDGE,"E7.26.1"),sQuery(id+"F0.wireOp",EDGE,"E7.26.2"),sQuery(id+"F0.wireOp",EDGE,"E7.26.3"),sQuery(id+"F0.wireOp",EDGE,"E7.26.4"),sQuery(id+"F0.wireOp",EDGE,"E7.26.5"),sQuery(id+"F0.wireOp",EDGE,"E7.27.0"),sQuery(id+"F0.wireOp",EDGE,"E7.27.1"),sQuery(id+"F0.wireOp",EDGE,"E7.27.2"),sQuery(id+"F0.wireOp",EDGE,"E7.27.3"),sQuery(id+"F0.wireOp",EDGE,"E7.27.4"),sQuery(id+"F0.wireOp",EDGE,"E7.27.5"),sQuery(id+"F0.wireOp",EDGE,"E7.28.0"),sQuery(id+"F0.wireOp",EDGE,"E7.28.1"),sQuery(id+"F0.wireOp",EDGE,"E7.28.2"),sQuery(id+"F0.wireOp",EDGE,"E7.28.3"),sQuery(id+"F0.wireOp",EDGE,"E7.28.4"),sQuery(id+"F0.wireOp",EDGE,"E7.28.5"),sQuery(id+"F0.wireOp",EDGE,"E7.29.0"),sQuery(id+"F0.wireOp",EDGE,"E7.29.1"),sQuery(id+"F0.wireOp",EDGE,"E7.29.2"),sQuery(id+"F0.wireOp",EDGE,"E7.29.3"),sQuery(id+"F0.wireOp",EDGE,"E7.29.4"),sQuery(id+"F0.wireOp",EDGE,"E7.29.5"),sQuery(id+"F0.wireOp",EDGE,"E7.30.0"),sQuery(id+"F0.wireOp",EDGE,"E7.30.1"),sQuery(id+"F0.wireOp",EDGE,"E7.30.2"),sQuery(id+"F0.wireOp",EDGE,"E7.30.3"),sQuery(id+"F0.wireOp",EDGE,"E7.30.4"),sQuery(id+"F0.wireOp",EDGE,"E7.30.5"),sQuery(id+"F0.wireOp",EDGE,"E7.31.0"),sQuery(id+"F0.wireOp",EDGE,"E7.31.1"),sQuery(id+"F0.wireOp",EDGE,"E7.31.2"),sQuery(id+"F0.wireOp",EDGE,"E7.31.3"),sQuery(id+"F0.wireOp",EDGE,"E7.31.4"),sQuery(id+"F0.wireOp",EDGE,"E7.31.5"),sQuery(id+"F0.wireOp",EDGE,"E7.32.0"),sQuery(id+"F0.wireOp",EDGE,"E7.32.1"),sQuery(id+"F0.wireOp",EDGE,"E7.32.2"),sQuery(id+"F0.wireOp",EDGE,"E7.32.3"),sQuery(id+"F0.wireOp",EDGE,"E7.32.4"),sQuery(id+"F0.wireOp",EDGE,"E7.32.5"),sQuery(id+"F0.wireOp",EDGE,"E7.33.0"),sQuery(id+"F0.wireOp",EDGE,"E7.33.1"),sQuery(id+"F0.wireOp",EDGE,"E7.33.2"),sQuery(id+"F0.wireOp",EDGE,"E7.33.3"),sQuery(id+"F0.wireOp",EDGE,"E7.33.4"),sQuery(id+"F0.wireOp",EDGE,"E7.33.5"),sQuery(id+"F0.wireOp",EDGE,"E7.34.0"),sQuery(id+"F0.wireOp",EDGE,"E7.34.1"),sQuery(id+"F0.wireOp",EDGE,"E7.34.2"),sQuery(id+"F0.wireOp",EDGE,"E7.34.3"),sQuery(id+"F0.wireOp",EDGE,"E7.34.4"),sQuery(id+"F0.wireOp",EDGE,"E7.34.5"),sQuery(id+"F0.wireOp",EDGE,"E7.35.0"),sQuery(id+"F0.wireOp",EDGE,"E7.35.1"),sQuery(id+"F0.wireOp",EDGE,"E7.35.2"),sQuery(id+"F0.wireOp",EDGE,"E7.35.3"),sQuery(id+"F0.wireOp",EDGE,"E7.35.4"),sQuery(id+"F0.wireOp",EDGE,"E7.35.5"),sQuery(id+"F0.wireOp",EDGE,"E7.36.0"),sQuery(id+"F0.wireOp",EDGE,"E7.36.1"),sQuery(id+"F0.wireOp",EDGE,"E7.36.2"),sQuery(id+"F0.wireOp",EDGE,"E7.36.3"),sQuery(id+"F0.wireOp",EDGE,"E7.36.4"),sQuery(id+"F0.wireOp",EDGE,"E7.36.5"),sQuery(id+"F0.wireOp",EDGE,"E7.37.0"),sQuery(id+"F0.wireOp",EDGE,"E7.37.1"),sQuery(id+"F0.wireOp",EDGE,"E7.37.2"),sQuery(id+"F0.wireOp",EDGE,"E7.37.3"),sQuery(id+"F0.wireOp",EDGE,"E7.37.4"),sQuery(id+"F0.wireOp",EDGE,"E7.37.5"),sQuery(id+"F0.wireOp",EDGE,"E7.38.0"),sQuery(id+"F0.wireOp",EDGE,"E7.38.1"),sQuery(id+"F0.wireOp",EDGE,"E7.38.2"),sQuery(id+"F0.wireOp",EDGE,"E7.38.3"),sQuery(id+"F0.wireOp",EDGE,"E7.38.4"),sQuery(id+"F0.wireOp",EDGE,"E7.38.5"),sQuery(id+"F0.wireOp",EDGE,"E7.39.0"),sQuery(id+"F0.wireOp",EDGE,"E7.39.1"),sQuery(id+"F0.wireOp",EDGE,"E7.39.2"),sQuery(id+"F0.wireOp",EDGE,"E7.39.3"),sQuery(id+"F0.wireOp",EDGE,"E7.39.4"),sQuery(id+"F0.wireOp",EDGE,"E7.39.5"),sQuery(id+"F0.wireOp",EDGE,"E7.40.0"),sQuery(id+"F0.wireOp",EDGE,"E7.40.1"),sQuery(id+"F0.wireOp",EDGE,"E7.40.2"),sQuery(id+"F0.wireOp",EDGE,"E7.40.3"),sQuery(id+"F0.wireOp",EDGE,"E7.40.4"),sQuery(id+"F0.wireOp",EDGE,"E7.40.5"),sQuery(id+"F0.wireOp",EDGE,"E7.41.0"),sQuery(id+"F0.wireOp",EDGE,"E7.41.1"),sQuery(id+"F0.wireOp",EDGE,"E7.41.2"),sQuery(id+"F0.wireOp",EDGE,"E7.41.3"),sQuery(id+"F0.wireOp",EDGE,"E7.41.4"),sQuery(id+"F0.wireOp",EDGE,"E7.41.5"),sQuery(id+"F0.wireOp",EDGE,"E7.42.0"),sQuery(id+"F0.wireOp",EDGE,"E7.42.1"),sQuery(id+"F0.wireOp",EDGE,"E7.42.2"),sQuery(id+"F0.wireOp",EDGE,"E7.42.3"),sQuery(id+"F0.wireOp",EDGE,"E7.42.4"),sQuery(id+"F0.wireOp",EDGE,"E7.42.5"),sQuery(id+"F0.wireOp",EDGE,"E7.43.0"),sQuery(id+"F0.wireOp",EDGE,"E7.43.1"),sQuery(id+"F0.wireOp",EDGE,"E7.43.2"),sQuery(id+"F0.wireOp",EDGE,"E7.43.3"),sQuery(id+"F0.wireOp",EDGE,"E7.43.4"),sQuery(id+"F0.wireOp",EDGE,"E7.43.5")])],"isStart":false})]});}
            var Q13;
            {var subQ0=sQuery(id+"F0.wireOp",EDGE,"E7.17.0");Q13=makeQuery(id+"F2.opChamfer","BLEND_EDGE",EDGE,{"blendedFrom":[makeQuery(id+"F1.opExtrude","CAP_EDGE",EDGE,{"disambiguationData":[OSD([subQ0])],"isStart":false}),makeQuery(id+"F1.opExtrude","CAP_FACE",FACE,{"disambiguationData":[OSD([sQuery(id+"F0.wireOp",EDGE,"E1"),sQuery(id+"F0.wireOp",EDGE,"E2"),sQuery(id+"F0.wireOp",EDGE,"E3"),sQuery(id+"F0.wireOp",EDGE,"E4"),sQuery(id+"F0.wireOp",EDGE,"E5"),sQuery(id+"F0.wireOp",EDGE,"E6"),sQuery(id+"F0.wireOp",EDGE,"E7.1.0"),sQuery(id+"F0.wireOp",EDGE,"E7.1.1"),sQuery(id+"F0.wireOp",EDGE,"E7.1.2"),sQuery(id+"F0.wireOp",EDGE,"E7.1.3"),sQuery(id+"F0.wireOp",EDGE,"E7.1.4"),sQuery(id+"F0.wireOp",EDGE,"E7.1.5"),sQuery(id+"F0.wireOp",EDGE,"E7.2.0"),sQuery(id+"F0.wireOp",EDGE,"E7.2.1"),sQuery(id+"F0.wireOp",EDGE,"E7.2.2"),sQuery(id+"F0.wireOp",EDGE,"E7.2.3"),sQuery(id+"F0.wireOp",EDGE,"E7.2.4"),sQuery(id+"F0.wireOp",EDGE,"E7.2.5"),sQuery(id+"F0.wireOp",EDGE,"E7.3.0"),sQuery(id+"F0.wireOp",EDGE,"E7.3.1"),sQuery(id+"F0.wireOp",EDGE,"E7.3.2"),sQuery(id+"F0.wireOp",EDGE,"E7.3.3"),sQuery(id+"F0.wireOp",EDGE,"E7.3.4"),sQuery(id+"F0.wireOp",EDGE,"E7.3.5"),sQuery(id+"F0.wireOp",EDGE,"E7.4.0"),sQuery(id+"F0.wireOp",EDGE,"E7.4.1"),sQuery(id+"F0.wireOp",EDGE,"E7.4.2"),sQuery(id+"F0.wireOp",EDGE,"E7.4.3"),sQuery(id+"F0.wireOp",EDGE,"E7.4.4"),sQuery(id+"F0.wireOp",EDGE,"E7.4.5"),sQuery(id+"F0.wireOp",EDGE,"E7.5.0"),sQuery(id+"F0.wireOp",EDGE,"E7.5.1"),sQuery(id+"F0.wireOp",EDGE,"E7.5.2"),sQuery(id+"F0.wireOp",EDGE,"E7.5.3"),sQuery(id+"F0.wireOp",EDGE,"E7.5.4"),sQuery(id+"F0.wireOp",EDGE,"E7.5.5"),sQuery(id+"F0.wireOp",EDGE,"E7.6.0"),sQuery(id+"F0.wireOp",EDGE,"E7.6.1"),sQuery(id+"F0.wireOp",EDGE,"E7.6.2"),sQuery(id+"F0.wireOp",EDGE,"E7.6.3"),sQuery(id+"F0.wireOp",EDGE,"E7.6.4"),sQuery(id+"F0.wireOp",EDGE,"E7.6.5"),sQuery(id+"F0.wireOp",EDGE,"E7.7.0"),sQuery(id+"F0.wireOp",EDGE,"E7.7.1"),sQuery(id+"F0.wireOp",EDGE,"E7.7.2"),sQuery(id+"F0.wireOp",EDGE,"E7.7.3"),sQuery(id+"F0.wireOp",EDGE,"E7.7.4"),sQuery(id+"F0.wireOp",EDGE,"E7.7.5"),sQuery(id+"F0.wireOp",EDGE,"E7.8.0"),sQuery(id+"F0.wireOp",EDGE,"E7.8.1"),sQuery(id+"F0.wireOp",EDGE,"E7.8.2"),sQuery(id+"F0.wireOp",EDGE,"E7.8.3"),sQuery(id+"F0.wireOp",EDGE,"E7.8.4"),sQuery(id+"F0.wireOp",EDGE,"E7.8.5"),sQuery(id+"F0.wireOp",EDGE,"E7.9.0"),sQuery(id+"F0.wireOp",EDGE,"E7.9.1"),sQuery(id+"F0.wireOp",EDGE,"E7.9.2"),sQuery(id+"F0.wireOp",EDGE,"E7.9.3"),sQuery(id+"F0.wireOp",EDGE,"E7.9.4"),sQuery(id+"F0.wireOp",EDGE,"E7.9.5"),sQuery(id+"F0.wireOp",EDGE,"E7.10.0"),sQuery(id+"F0.wireOp",EDGE,"E7.10.1"),sQuery(id+"F0.wireOp",EDGE,"E7.10.2"),sQuery(id+"F0.wireOp",EDGE,"E7.10.3"),sQuery(id+"F0.wireOp",EDGE,"E7.10.4"),sQuery(id+"F0.wireOp",EDGE,"E7.10.5"),sQuery(id+"F0.wireOp",EDGE,"E7.11.0"),sQuery(id+"F0.wireOp",EDGE,"E7.11.1"),sQuery(id+"F0.wireOp",EDGE,"E7.11.2"),sQuery(id+"F0.wireOp",EDGE,"E7.11.3"),sQuery(id+"F0.wireOp",EDGE,"E7.11.4"),sQuery(id+"F0.wireOp",EDGE,"E7.11.5"),sQuery(id+"F0.wireOp",EDGE,"E7.12.0"),sQuery(id+"F0.wireOp",EDGE,"E7.12.1"),sQuery(id+"F0.wireOp",EDGE,"E7.12.2"),sQuery(id+"F0.wireOp",EDGE,"E7.12.3"),sQuery(id+"F0.wireOp",EDGE,"E7.12.4"),sQuery(id+"F0.wireOp",EDGE,"E7.12.5"),sQuery(id+"F0.wireOp",EDGE,"E7.13.0"),sQuery(id+"F0.wireOp",EDGE,"E7.13.1"),sQuery(id+"F0.wireOp",EDGE,"E7.13.2"),sQuery(id+"F0.wireOp",EDGE,"E7.13.3"),sQuery(id+"F0.wireOp",EDGE,"E7.13.4"),sQuery(id+"F0.wireOp",EDGE,"E7.13.5"),sQuery(id+"F0.wireOp",EDGE,"E7.14.0"),sQuery(id+"F0.wireOp",EDGE,"E7.14.1"),sQuery(id+"F0.wireOp",EDGE,"E7.14.2"),sQuery(id+"F0.wireOp",EDGE,"E7.14.3"),sQuery(id+"F0.wireOp",EDGE,"E7.14.4"),sQuery(id+"F0.wireOp",EDGE,"E7.14.5"),sQuery(id+"F0.wireOp",EDGE,"E7.15.0"),sQuery(id+"F0.wireOp",EDGE,"E7.15.1"),sQuery(id+"F0.wireOp",EDGE,"E7.15.2"),sQuery(id+"F0.wireOp",EDGE,"E7.15.3"),sQuery(id+"F0.wireOp",EDGE,"E7.15.4"),sQuery(id+"F0.wireOp",EDGE,"E7.15.5"),sQuery(id+"F0.wireOp",EDGE,"E7.16.0"),sQuery(id+"F0.wireOp",EDGE,"E7.16.1"),sQuery(id+"F0.wireOp",EDGE,"E7.16.2"),sQuery(id+"F0.wireOp",EDGE,"E7.16.3"),sQuery(id+"F0.wireOp",EDGE,"E7.16.4"),sQuery(id+"F0.wireOp",EDGE,"E7.16.5"),subQ0,sQuery(id+"F0.wireOp",EDGE,"E7.17.1"),sQuery(id+"F0.wireOp",EDGE,"E7.17.2"),sQuery(id+"F0.wireOp",EDGE,"E7.17.3"),sQuery(id+"F0.wireOp",EDGE,"E7.17.4"),sQuery(id+"F0.wireOp",EDGE,"E7.17.5"),sQuery(id+"F0.wireOp",EDGE,"E7.18.0"),sQuery(id+"F0.wireOp",EDGE,"E7.18.1"),sQuery(id+"F0.wireOp",EDGE,"E7.18.2"),sQuery(id+"F0.wireOp",EDGE,"E7.18.3"),sQuery(id+"F0.wireOp",EDGE,"E7.18.4"),sQuery(id+"F0.wireOp",EDGE,"E7.18.5"),sQuery(id+"F0.wireOp",EDGE,"E7.19.0"),sQuery(id+"F0.wireOp",EDGE,"E7.19.1"),sQuery(id+"F0.wireOp",EDGE,"E7.19.2"),sQuery(id+"F0.wireOp",EDGE,"E7.19.3"),sQuery(id+"F0.wireOp",EDGE,"E7.19.4"),sQuery(id+"F0.wireOp",EDGE,"E7.19.5"),sQuery(id+"F0.wireOp",EDGE,"E7.20.0"),sQuery(id+"F0.wireOp",EDGE,"E7.20.1"),sQuery(id+"F0.wireOp",EDGE,"E7.20.2"),sQuery(id+"F0.wireOp",EDGE,"E7.20.3"),sQuery(id+"F0.wireOp",EDGE,"E7.20.4"),sQuery(id+"F0.wireOp",EDGE,"E7.20.5"),sQuery(id+"F0.wireOp",EDGE,"E7.21.0"),sQuery(id+"F0.wireOp",EDGE,"E7.21.1"),sQuery(id+"F0.wireOp",EDGE,"E7.21.2"),sQuery(id+"F0.wireOp",EDGE,"E7.21.3"),sQuery(id+"F0.wireOp",EDGE,"E7.21.4"),sQuery(id+"F0.wireOp",EDGE,"E7.21.5"),sQuery(id+"F0.wireOp",EDGE,"E7.22.0"),sQuery(id+"F0.wireOp",EDGE,"E7.22.1"),sQuery(id+"F0.wireOp",EDGE,"E7.22.2"),sQuery(id+"F0.wireOp",EDGE,"E7.22.3"),sQuery(id+"F0.wireOp",EDGE,"E7.22.4"),sQuery(id+"F0.wireOp",EDGE,"E7.22.5"),sQuery(id+"F0.wireOp",EDGE,"E7.23.0"),sQuery(id+"F0.wireOp",EDGE,"E7.23.1"),sQuery(id+"F0.wireOp",EDGE,"E7.23.2"),sQuery(id+"F0.wireOp",EDGE,"E7.23.3"),sQuery(id+"F0.wireOp",EDGE,"E7.23.4"),sQuery(id+"F0.wireOp",EDGE,"E7.23.5"),sQuery(id+"F0.wireOp",EDGE,"E7.24.0"),sQuery(id+"F0.wireOp",EDGE,"E7.24.1"),sQuery(id+"F0.wireOp",EDGE,"E7.24.2"),sQuery(id+"F0.wireOp",EDGE,"E7.24.3"),sQuery(id+"F0.wireOp",EDGE,"E7.24.4"),sQuery(id+"F0.wireOp",EDGE,"E7.24.5"),sQuery(id+"F0.wireOp",EDGE,"E7.25.0"),sQuery(id+"F0.wireOp",EDGE,"E7.25.1"),sQuery(id+"F0.wireOp",EDGE,"E7.25.2"),sQuery(id+"F0.wireOp",EDGE,"E7.25.3"),sQuery(id+"F0.wireOp",EDGE,"E7.25.4"),sQuery(id+"F0.wireOp",EDGE,"E7.25.5"),sQuery(id+"F0.wireOp",EDGE,"E7.26.0"),sQuery(id+"F0.wireOp",EDGE,"E7.26.1"),sQuery(id+"F0.wireOp",EDGE,"E7.26.2"),sQuery(id+"F0.wireOp",EDGE,"E7.26.3"),sQuery(id+"F0.wireOp",EDGE,"E7.26.4"),sQuery(id+"F0.wireOp",EDGE,"E7.26.5"),sQuery(id+"F0.wireOp",EDGE,"E7.27.0"),sQuery(id+"F0.wireOp",EDGE,"E7.27.1"),sQuery(id+"F0.wireOp",EDGE,"E7.27.2"),sQuery(id+"F0.wireOp",EDGE,"E7.27.3"),sQuery(id+"F0.wireOp",EDGE,"E7.27.4"),sQuery(id+"F0.wireOp",EDGE,"E7.27.5"),sQuery(id+"F0.wireOp",EDGE,"E7.28.0"),sQuery(id+"F0.wireOp",EDGE,"E7.28.1"),sQuery(id+"F0.wireOp",EDGE,"E7.28.2"),sQuery(id+"F0.wireOp",EDGE,"E7.28.3"),sQuery(id+"F0.wireOp",EDGE,"E7.28.4"),sQuery(id+"F0.wireOp",EDGE,"E7.28.5"),sQuery(id+"F0.wireOp",EDGE,"E7.29.0"),sQuery(id+"F0.wireOp",EDGE,"E7.29.1"),sQuery(id+"F0.wireOp",EDGE,"E7.29.2"),sQuery(id+"F0.wireOp",EDGE,"E7.29.3"),sQuery(id+"F0.wireOp",EDGE,"E7.29.4"),sQuery(id+"F0.wireOp",EDGE,"E7.29.5"),sQuery(id+"F0.wireOp",EDGE,"E7.30.0"),sQuery(id+"F0.wireOp",EDGE,"E7.30.1"),sQuery(id+"F0.wireOp",EDGE,"E7.30.2"),sQuery(id+"F0.wireOp",EDGE,"E7.30.3"),sQuery(id+"F0.wireOp",EDGE,"E7.30.4"),sQuery(id+"F0.wireOp",EDGE,"E7.30.5"),sQuery(id+"F0.wireOp",EDGE,"E7.31.0"),sQuery(id+"F0.wireOp",EDGE,"E7.31.1"),sQuery(id+"F0.wireOp",EDGE,"E7.31.2"),sQuery(id+"F0.wireOp",EDGE,"E7.31.3"),sQuery(id+"F0.wireOp",EDGE,"E7.31.4"),sQuery(id+"F0.wireOp",EDGE,"E7.31.5"),sQuery(id+"F0.wireOp",EDGE,"E7.32.0"),sQuery(id+"F0.wireOp",EDGE,"E7.32.1"),sQuery(id+"F0.wireOp",EDGE,"E7.32.2"),sQuery(id+"F0.wireOp",EDGE,"E7.32.3"),sQuery(id+"F0.wireOp",EDGE,"E7.32.4"),sQuery(id+"F0.wireOp",EDGE,"E7.32.5"),sQuery(id+"F0.wireOp",EDGE,"E7.33.0"),sQuery(id+"F0.wireOp",EDGE,"E7.33.1"),sQuery(id+"F0.wireOp",EDGE,"E7.33.2"),sQuery(id+"F0.wireOp",EDGE,"E7.33.3"),sQuery(id+"F0.wireOp",EDGE,"E7.33.4"),sQuery(id+"F0.wireOp",EDGE,"E7.33.5"),sQuery(id+"F0.wireOp",EDGE,"E7.34.0"),sQuery(id+"F0.wireOp",EDGE,"E7.34.1"),sQuery(id+"F0.wireOp",EDGE,"E7.34.2"),sQuery(id+"F0.wireOp",EDGE,"E7.34.3"),sQuery(id+"F0.wireOp",EDGE,"E7.34.4"),sQuery(id+"F0.wireOp",EDGE,"E7.34.5"),sQuery(id+"F0.wireOp",EDGE,"E7.35.0"),sQuery(id+"F0.wireOp",EDGE,"E7.35.1"),sQuery(id+"F0.wireOp",EDGE,"E7.35.2"),sQuery(id+"F0.wireOp",EDGE,"E7.35.3"),sQuery(id+"F0.wireOp",EDGE,"E7.35.4"),sQuery(id+"F0.wireOp",EDGE,"E7.35.5"),sQuery(id+"F0.wireOp",EDGE,"E7.36.0"),sQuery(id+"F0.wireOp",EDGE,"E7.36.1"),sQuery(id+"F0.wireOp",EDGE,"E7.36.2"),sQuery(id+"F0.wireOp",EDGE,"E7.36.3"),sQuery(id+"F0.wireOp",EDGE,"E7.36.4"),sQuery(id+"F0.wireOp",EDGE,"E7.36.5"),sQuery(id+"F0.wireOp",EDGE,"E7.37.0"),sQuery(id+"F0.wireOp",EDGE,"E7.37.1"),sQuery(id+"F0.wireOp",EDGE,"E7.37.2"),sQuery(id+"F0.wireOp",EDGE,"E7.37.3"),sQuery(id+"F0.wireOp",EDGE,"E7.37.4"),sQuery(id+"F0.wireOp",EDGE,"E7.37.5"),sQuery(id+"F0.wireOp",EDGE,"E7.38.0"),sQuery(id+"F0.wireOp",EDGE,"E7.38.1"),sQuery(id+"F0.wireOp",EDGE,"E7.38.2"),sQuery(id+"F0.wireOp",EDGE,"E7.38.3"),sQuery(id+"F0.wireOp",EDGE,"E7.38.4"),sQuery(id+"F0.wireOp",EDGE,"E7.38.5"),sQuery(id+"F0.wireOp",EDGE,"E7.39.0"),sQuery(id+"F0.wireOp",EDGE,"E7.39.1"),sQuery(id+"F0.wireOp",EDGE,"E7.39.2"),sQuery(id+"F0.wireOp",EDGE,"E7.39.3"),sQuery(id+"F0.wireOp",EDGE,"E7.39.4"),sQuery(id+"F0.wireOp",EDGE,"E7.39.5"),sQuery(id+"F0.wireOp",EDGE,"E7.40.0"),sQuery(id+"F0.wireOp",EDGE,"E7.40.1"),sQuery(id+"F0.wireOp",EDGE,"E7.40.2"),sQuery(id+"F0.wireOp",EDGE,"E7.40.3"),sQuery(id+"F0.wireOp",EDGE,"E7.40.4"),sQuery(id+"F0.wireOp",EDGE,"E7.40.5"),sQuery(id+"F0.wireOp",EDGE,"E7.41.0"),sQuery(id+"F0.wireOp",EDGE,"E7.41.1"),sQuery(id+"F0.wireOp",EDGE,"E7.41.2"),sQuery(id+"F0.wireOp",EDGE,"E7.41.3"),sQuery(id+"F0.wireOp",EDGE,"E7.41.4"),sQuery(id+"F0.wireOp",EDGE,"E7.41.5"),sQuery(id+"F0.wireOp",EDGE,"E7.42.0"),sQuery(id+"F0.wireOp",EDGE,"E7.42.1"),sQuery(id+"F0.wireOp",EDGE,"E7.42.2"),sQuery(id+"F0.wireOp",EDGE,"E7.42.3"),sQuery(id+"F0.wireOp",EDGE,"E7.42.4"),sQuery(id+"F0.wireOp",EDGE,"E7.42.5"),sQuery(id+"F0.wireOp",EDGE,"E7.43.0"),sQuery(id+"F0.wireOp",EDGE,"E7.43.1"),sQuery(id+"F0.wireOp",EDGE,"E7.43.2"),sQuery(id+"F0.wireOp",EDGE,"E7.43.3"),sQuery(id+"F0.wireOp",EDGE,"E7.43.4"),sQuery(id+"F0.wireOp",EDGE,"E7.43.5")])],"isStart":false})],"blendedInto":[makeQuery(id+"F1.opExtrude","CAP_FACE",FACE,{"disambiguationData":[OSD([sQuery(id+"F0.wireOp",EDGE,"E1"),sQuery(id+"F0.wireOp",EDGE,"E2"),sQuery(id+"F0.wireOp",EDGE,"E3"),sQuery(id+"F0.wireOp",EDGE,"E4"),sQuery(id+"F0.wireOp",EDGE,"E5"),sQuery(id+"F0.wireOp",EDGE,"E6"),sQuery(id+"F0.wireOp",EDGE,"E7.1.0"),sQuery(id+"F0.wireOp",EDGE,"E7.1.1"),sQuery(id+"F0.wireOp",EDGE,"E7.1.2"),sQuery(id+"F0.wireOp",EDGE,"E7.1.3"),sQuery(id+"F0.wireOp",EDGE,"E7.1.4"),sQuery(id+"F0.wireOp",EDGE,"E7.1.5"),sQuery(id+"F0.wireOp",EDGE,"E7.2.0"),sQuery(id+"F0.wireOp",EDGE,"E7.2.1"),sQuery(id+"F0.wireOp",EDGE,"E7.2.2"),sQuery(id+"F0.wireOp",EDGE,"E7.2.3"),sQuery(id+"F0.wireOp",EDGE,"E7.2.4"),sQuery(id+"F0.wireOp",EDGE,"E7.2.5"),sQuery(id+"F0.wireOp",EDGE,"E7.3.0"),sQuery(id+"F0.wireOp",EDGE,"E7.3.1"),sQuery(id+"F0.wireOp",EDGE,"E7.3.2"),sQuery(id+"F0.wireOp",EDGE,"E7.3.3"),sQuery(id+"F0.wireOp",EDGE,"E7.3.4"),sQuery(id+"F0.wireOp",EDGE,"E7.3.5"),sQuery(id+"F0.wireOp",EDGE,"E7.4.0"),sQuery(id+"F0.wireOp",EDGE,"E7.4.1"),sQuery(id+"F0.wireOp",EDGE,"E7.4.2"),sQuery(id+"F0.wireOp",EDGE,"E7.4.3"),sQuery(id+"F0.wireOp",EDGE,"E7.4.4"),sQuery(id+"F0.wireOp",EDGE,"E7.4.5"),sQuery(id+"F0.wireOp",EDGE,"E7.5.0"),sQuery(id+"F0.wireOp",EDGE,"E7.5.1"),sQuery(id+"F0.wireOp",EDGE,"E7.5.2"),sQuery(id+"F0.wireOp",EDGE,"E7.5.3"),sQuery(id+"F0.wireOp",EDGE,"E7.5.4"),sQuery(id+"F0.wireOp",EDGE,"E7.5.5"),sQuery(id+"F0.wireOp",EDGE,"E7.6.0"),sQuery(id+"F0.wireOp",EDGE,"E7.6.1"),sQuery(id+"F0.wireOp",EDGE,"E7.6.2"),sQuery(id+"F0.wireOp",EDGE,"E7.6.3"),sQuery(id+"F0.wireOp",EDGE,"E7.6.4"),sQuery(id+"F0.wireOp",EDGE,"E7.6.5"),sQuery(id+"F0.wireOp",EDGE,"E7.7.0"),sQuery(id+"F0.wireOp",EDGE,"E7.7.1"),sQuery(id+"F0.wireOp",EDGE,"E7.7.2"),sQuery(id+"F0.wireOp",EDGE,"E7.7.3"),sQuery(id+"F0.wireOp",EDGE,"E7.7.4"),sQuery(id+"F0.wireOp",EDGE,"E7.7.5"),sQuery(id+"F0.wireOp",EDGE,"E7.8.0"),sQuery(id+"F0.wireOp",EDGE,"E7.8.1"),sQuery(id+"F0.wireOp",EDGE,"E7.8.2"),sQuery(id+"F0.wireOp",EDGE,"E7.8.3"),sQuery(id+"F0.wireOp",EDGE,"E7.8.4"),sQuery(id+"F0.wireOp",EDGE,"E7.8.5"),sQuery(id+"F0.wireOp",EDGE,"E7.9.0"),sQuery(id+"F0.wireOp",EDGE,"E7.9.1"),sQuery(id+"F0.wireOp",EDGE,"E7.9.2"),sQuery(id+"F0.wireOp",EDGE,"E7.9.3"),sQuery(id+"F0.wireOp",EDGE,"E7.9.4"),sQuery(id+"F0.wireOp",EDGE,"E7.9.5"),sQuery(id+"F0.wireOp",EDGE,"E7.10.0"),sQuery(id+"F0.wireOp",EDGE,"E7.10.1"),sQuery(id+"F0.wireOp",EDGE,"E7.10.2"),sQuery(id+"F0.wireOp",EDGE,"E7.10.3"),sQuery(id+"F0.wireOp",EDGE,"E7.10.4"),sQuery(id+"F0.wireOp",EDGE,"E7.10.5"),sQuery(id+"F0.wireOp",EDGE,"E7.11.0"),sQuery(id+"F0.wireOp",EDGE,"E7.11.1"),sQuery(id+"F0.wireOp",EDGE,"E7.11.2"),sQuery(id+"F0.wireOp",EDGE,"E7.11.3"),sQuery(id+"F0.wireOp",EDGE,"E7.11.4"),sQuery(id+"F0.wireOp",EDGE,"E7.11.5"),sQuery(id+"F0.wireOp",EDGE,"E7.12.0"),sQuery(id+"F0.wireOp",EDGE,"E7.12.1"),sQuery(id+"F0.wireOp",EDGE,"E7.12.2"),sQuery(id+"F0.wireOp",EDGE,"E7.12.3"),sQuery(id+"F0.wireOp",EDGE,"E7.12.4"),sQuery(id+"F0.wireOp",EDGE,"E7.12.5"),sQuery(id+"F0.wireOp",EDGE,"E7.13.0"),sQuery(id+"F0.wireOp",EDGE,"E7.13.1"),sQuery(id+"F0.wireOp",EDGE,"E7.13.2"),sQuery(id+"F0.wireOp",EDGE,"E7.13.3"),sQuery(id+"F0.wireOp",EDGE,"E7.13.4"),sQuery(id+"F0.wireOp",EDGE,"E7.13.5"),sQuery(id+"F0.wireOp",EDGE,"E7.14.0"),sQuery(id+"F0.wireOp",EDGE,"E7.14.1"),sQuery(id+"F0.wireOp",EDGE,"E7.14.2"),sQuery(id+"F0.wireOp",EDGE,"E7.14.3"),sQuery(id+"F0.wireOp",EDGE,"E7.14.4"),sQuery(id+"F0.wireOp",EDGE,"E7.14.5"),sQuery(id+"F0.wireOp",EDGE,"E7.15.0"),sQuery(id+"F0.wireOp",EDGE,"E7.15.1"),sQuery(id+"F0.wireOp",EDGE,"E7.15.2"),sQuery(id+"F0.wireOp",EDGE,"E7.15.3"),sQuery(id+"F0.wireOp",EDGE,"E7.15.4"),sQuery(id+"F0.wireOp",EDGE,"E7.15.5"),sQuery(id+"F0.wireOp",EDGE,"E7.16.0"),sQuery(id+"F0.wireOp",EDGE,"E7.16.1"),sQuery(id+"F0.wireOp",EDGE,"E7.16.2"),sQuery(id+"F0.wireOp",EDGE,"E7.16.3"),sQuery(id+"F0.wireOp",EDGE,"E7.16.4"),sQuery(id+"F0.wireOp",EDGE,"E7.16.5"),subQ0,sQuery(id+"F0.wireOp",EDGE,"E7.17.1"),sQuery(id+"F0.wireOp",EDGE,"E7.17.2"),sQuery(id+"F0.wireOp",EDGE,"E7.17.3"),sQuery(id+"F0.wireOp",EDGE,"E7.17.4"),sQuery(id+"F0.wireOp",EDGE,"E7.17.5"),sQuery(id+"F0.wireOp",EDGE,"E7.18.0"),sQuery(id+"F0.wireOp",EDGE,"E7.18.1"),sQuery(id+"F0.wireOp",EDGE,"E7.18.2"),sQuery(id+"F0.wireOp",EDGE,"E7.18.3"),sQuery(id+"F0.wireOp",EDGE,"E7.18.4"),sQuery(id+"F0.wireOp",EDGE,"E7.18.5"),sQuery(id+"F0.wireOp",EDGE,"E7.19.0"),sQuery(id+"F0.wireOp",EDGE,"E7.19.1"),sQuery(id+"F0.wireOp",EDGE,"E7.19.2"),sQuery(id+"F0.wireOp",EDGE,"E7.19.3"),sQuery(id+"F0.wireOp",EDGE,"E7.19.4"),sQuery(id+"F0.wireOp",EDGE,"E7.19.5"),sQuery(id+"F0.wireOp",EDGE,"E7.20.0"),sQuery(id+"F0.wireOp",EDGE,"E7.20.1"),sQuery(id+"F0.wireOp",EDGE,"E7.20.2"),sQuery(id+"F0.wireOp",EDGE,"E7.20.3"),sQuery(id+"F0.wireOp",EDGE,"E7.20.4"),sQuery(id+"F0.wireOp",EDGE,"E7.20.5"),sQuery(id+"F0.wireOp",EDGE,"E7.21.0"),sQuery(id+"F0.wireOp",EDGE,"E7.21.1"),sQuery(id+"F0.wireOp",EDGE,"E7.21.2"),sQuery(id+"F0.wireOp",EDGE,"E7.21.3"),sQuery(id+"F0.wireOp",EDGE,"E7.21.4"),sQuery(id+"F0.wireOp",EDGE,"E7.21.5"),sQuery(id+"F0.wireOp",EDGE,"E7.22.0"),sQuery(id+"F0.wireOp",EDGE,"E7.22.1"),sQuery(id+"F0.wireOp",EDGE,"E7.22.2"),sQuery(id+"F0.wireOp",EDGE,"E7.22.3"),sQuery(id+"F0.wireOp",EDGE,"E7.22.4"),sQuery(id+"F0.wireOp",EDGE,"E7.22.5"),sQuery(id+"F0.wireOp",EDGE,"E7.23.0"),sQuery(id+"F0.wireOp",EDGE,"E7.23.1"),sQuery(id+"F0.wireOp",EDGE,"E7.23.2"),sQuery(id+"F0.wireOp",EDGE,"E7.23.3"),sQuery(id+"F0.wireOp",EDGE,"E7.23.4"),sQuery(id+"F0.wireOp",EDGE,"E7.23.5"),sQuery(id+"F0.wireOp",EDGE,"E7.24.0"),sQuery(id+"F0.wireOp",EDGE,"E7.24.1"),sQuery(id+"F0.wireOp",EDGE,"E7.24.2"),sQuery(id+"F0.wireOp",EDGE,"E7.24.3"),sQuery(id+"F0.wireOp",EDGE,"E7.24.4"),sQuery(id+"F0.wireOp",EDGE,"E7.24.5"),sQuery(id+"F0.wireOp",EDGE,"E7.25.0"),sQuery(id+"F0.wireOp",EDGE,"E7.25.1"),sQuery(id+"F0.wireOp",EDGE,"E7.25.2"),sQuery(id+"F0.wireOp",EDGE,"E7.25.3"),sQuery(id+"F0.wireOp",EDGE,"E7.25.4"),sQuery(id+"F0.wireOp",EDGE,"E7.25.5"),sQuery(id+"F0.wireOp",EDGE,"E7.26.0"),sQuery(id+"F0.wireOp",EDGE,"E7.26.1"),sQuery(id+"F0.wireOp",EDGE,"E7.26.2"),sQuery(id+"F0.wireOp",EDGE,"E7.26.3"),sQuery(id+"F0.wireOp",EDGE,"E7.26.4"),sQuery(id+"F0.wireOp",EDGE,"E7.26.5"),sQuery(id+"F0.wireOp",EDGE,"E7.27.0"),sQuery(id+"F0.wireOp",EDGE,"E7.27.1"),sQuery(id+"F0.wireOp",EDGE,"E7.27.2"),sQuery(id+"F0.wireOp",EDGE,"E7.27.3"),sQuery(id+"F0.wireOp",EDGE,"E7.27.4"),sQuery(id+"F0.wireOp",EDGE,"E7.27.5"),sQuery(id+"F0.wireOp",EDGE,"E7.28.0"),sQuery(id+"F0.wireOp",EDGE,"E7.28.1"),sQuery(id+"F0.wireOp",EDGE,"E7.28.2"),sQuery(id+"F0.wireOp",EDGE,"E7.28.3"),sQuery(id+"F0.wireOp",EDGE,"E7.28.4"),sQuery(id+"F0.wireOp",EDGE,"E7.28.5"),sQuery(id+"F0.wireOp",EDGE,"E7.29.0"),sQuery(id+"F0.wireOp",EDGE,"E7.29.1"),sQuery(id+"F0.wireOp",EDGE,"E7.29.2"),sQuery(id+"F0.wireOp",EDGE,"E7.29.3"),sQuery(id+"F0.wireOp",EDGE,"E7.29.4"),sQuery(id+"F0.wireOp",EDGE,"E7.29.5"),sQuery(id+"F0.wireOp",EDGE,"E7.30.0"),sQuery(id+"F0.wireOp",EDGE,"E7.30.1"),sQuery(id+"F0.wireOp",EDGE,"E7.30.2"),sQuery(id+"F0.wireOp",EDGE,"E7.30.3"),sQuery(id+"F0.wireOp",EDGE,"E7.30.4"),sQuery(id+"F0.wireOp",EDGE,"E7.30.5"),sQuery(id+"F0.wireOp",EDGE,"E7.31.0"),sQuery(id+"F0.wireOp",EDGE,"E7.31.1"),sQuery(id+"F0.wireOp",EDGE,"E7.31.2"),sQuery(id+"F0.wireOp",EDGE,"E7.31.3"),sQuery(id+"F0.wireOp",EDGE,"E7.31.4"),sQuery(id+"F0.wireOp",EDGE,"E7.31.5"),sQuery(id+"F0.wireOp",EDGE,"E7.32.0"),sQuery(id+"F0.wireOp",EDGE,"E7.32.1"),sQuery(id+"F0.wireOp",EDGE,"E7.32.2"),sQuery(id+"F0.wireOp",EDGE,"E7.32.3"),sQuery(id+"F0.wireOp",EDGE,"E7.32.4"),sQuery(id+"F0.wireOp",EDGE,"E7.32.5"),sQuery(id+"F0.wireOp",EDGE,"E7.33.0"),sQuery(id+"F0.wireOp",EDGE,"E7.33.1"),sQuery(id+"F0.wireOp",EDGE,"E7.33.2"),sQuery(id+"F0.wireOp",EDGE,"E7.33.3"),sQuery(id+"F0.wireOp",EDGE,"E7.33.4"),sQuery(id+"F0.wireOp",EDGE,"E7.33.5"),sQuery(id+"F0.wireOp",EDGE,"E7.34.0"),sQuery(id+"F0.wireOp",EDGE,"E7.34.1"),sQuery(id+"F0.wireOp",EDGE,"E7.34.2"),sQuery(id+"F0.wireOp",EDGE,"E7.34.3"),sQuery(id+"F0.wireOp",EDGE,"E7.34.4"),sQuery(id+"F0.wireOp",EDGE,"E7.34.5"),sQuery(id+"F0.wireOp",EDGE,"E7.35.0"),sQuery(id+"F0.wireOp",EDGE,"E7.35.1"),sQuery(id+"F0.wireOp",EDGE,"E7.35.2"),sQuery(id+"F0.wireOp",EDGE,"E7.35.3"),sQuery(id+"F0.wireOp",EDGE,"E7.35.4"),sQuery(id+"F0.wireOp",EDGE,"E7.35.5"),sQuery(id+"F0.wireOp",EDGE,"E7.36.0"),sQuery(id+"F0.wireOp",EDGE,"E7.36.1"),sQuery(id+"F0.wireOp",EDGE,"E7.36.2"),sQuery(id+"F0.wireOp",EDGE,"E7.36.3"),sQuery(id+"F0.wireOp",EDGE,"E7.36.4"),sQuery(id+"F0.wireOp",EDGE,"E7.36.5"),sQuery(id+"F0.wireOp",EDGE,"E7.37.0"),sQuery(id+"F0.wireOp",EDGE,"E7.37.1"),sQuery(id+"F0.wireOp",EDGE,"E7.37.2"),sQuery(id+"F0.wireOp",EDGE,"E7.37.3"),sQuery(id+"F0.wireOp",EDGE,"E7.37.4"),sQuery(id+"F0.wireOp",EDGE,"E7.37.5"),sQuery(id+"F0.wireOp",EDGE,"E7.38.0"),sQuery(id+"F0.wireOp",EDGE,"E7.38.1"),sQuery(id+"F0.wireOp",EDGE,"E7.38.2"),sQuery(id+"F0.wireOp",EDGE,"E7.38.3"),sQuery(id+"F0.wireOp",EDGE,"E7.38.4"),sQuery(id+"F0.wireOp",EDGE,"E7.38.5"),sQuery(id+"F0.wireOp",EDGE,"E7.39.0"),sQuery(id+"F0.wireOp",EDGE,"E7.39.1"),sQuery(id+"F0.wireOp",EDGE,"E7.39.2"),sQuery(id+"F0.wireOp",EDGE,"E7.39.3"),sQuery(id+"F0.wireOp",EDGE,"E7.39.4"),sQuery(id+"F0.wireOp",EDGE,"E7.39.5"),sQuery(id+"F0.wireOp",EDGE,"E7.40.0"),sQuery(id+"F0.wireOp",EDGE,"E7.40.1"),sQuery(id+"F0.wireOp",EDGE,"E7.40.2"),sQuery(id+"F0.wireOp",EDGE,"E7.40.3"),sQuery(id+"F0.wireOp",EDGE,"E7.40.4"),sQuery(id+"F0.wireOp",EDGE,"E7.40.5"),sQuery(id+"F0.wireOp",EDGE,"E7.41.0"),sQuery(id+"F0.wireOp",EDGE,"E7.41.1"),sQuery(id+"F0.wireOp",EDGE,"E7.41.2"),sQuery(id+"F0.wireOp",EDGE,"E7.41.3"),sQuery(id+"F0.wireOp",EDGE,"E7.41.4"),sQuery(id+"F0.wireOp",EDGE,"E7.41.5"),sQuery(id+"F0.wireOp",EDGE,"E7.42.0"),sQuery(id+"F0.wireOp",EDGE,"E7.42.1"),sQuery(id+"F0.wireOp",EDGE,"E7.42.2"),sQuery(id+"F0.wireOp",EDGE,"E7.42.3"),sQuery(id+"F0.wireOp",EDGE,"E7.42.4"),sQuery(id+"F0.wireOp",EDGE,"E7.42.5"),sQuery(id+"F0.wireOp",EDGE,"E7.43.0"),sQuery(id+"F0.wireOp",EDGE,"E7.43.1"),sQuery(id+"F0.wireOp",EDGE,"E7.43.2"),sQuery(id+"F0.wireOp",EDGE,"E7.43.3"),sQuery(id+"F0.wireOp",EDGE,"E7.43.4"),sQuery(id+"F0.wireOp",EDGE,"E7.43.5")])],"isStart":false})]});}
            var Q14;
            {var subQ0=sQuery(id+"F0.wireOp",EDGE,"E7.15.0");Q14=makeQuery(id+"F2.opChamfer","BLEND_EDGE",EDGE,{"blendedFrom":[makeQuery(id+"F1.opExtrude","CAP_EDGE",EDGE,{"disambiguationData":[OSD([subQ0])],"isStart":false}),makeQuery(id+"F1.opExtrude","CAP_FACE",FACE,{"disambiguationData":[OSD([sQuery(id+"F0.wireOp",EDGE,"E1"),sQuery(id+"F0.wireOp",EDGE,"E2"),sQuery(id+"F0.wireOp",EDGE,"E3"),sQuery(id+"F0.wireOp",EDGE,"E4"),sQuery(id+"F0.wireOp",EDGE,"E5"),sQuery(id+"F0.wireOp",EDGE,"E6"),sQuery(id+"F0.wireOp",EDGE,"E7.1.0"),sQuery(id+"F0.wireOp",EDGE,"E7.1.1"),sQuery(id+"F0.wireOp",EDGE,"E7.1.2"),sQuery(id+"F0.wireOp",EDGE,"E7.1.3"),sQuery(id+"F0.wireOp",EDGE,"E7.1.4"),sQuery(id+"F0.wireOp",EDGE,"E7.1.5"),sQuery(id+"F0.wireOp",EDGE,"E7.2.0"),sQuery(id+"F0.wireOp",EDGE,"E7.2.1"),sQuery(id+"F0.wireOp",EDGE,"E7.2.2"),sQuery(id+"F0.wireOp",EDGE,"E7.2.3"),sQuery(id+"F0.wireOp",EDGE,"E7.2.4"),sQuery(id+"F0.wireOp",EDGE,"E7.2.5"),sQuery(id+"F0.wireOp",EDGE,"E7.3.0"),sQuery(id+"F0.wireOp",EDGE,"E7.3.1"),sQuery(id+"F0.wireOp",EDGE,"E7.3.2"),sQuery(id+"F0.wireOp",EDGE,"E7.3.3"),sQuery(id+"F0.wireOp",EDGE,"E7.3.4"),sQuery(id+"F0.wireOp",EDGE,"E7.3.5"),sQuery(id+"F0.wireOp",EDGE,"E7.4.0"),sQuery(id+"F0.wireOp",EDGE,"E7.4.1"),sQuery(id+"F0.wireOp",EDGE,"E7.4.2"),sQuery(id+"F0.wireOp",EDGE,"E7.4.3"),sQuery(id+"F0.wireOp",EDGE,"E7.4.4"),sQuery(id+"F0.wireOp",EDGE,"E7.4.5"),sQuery(id+"F0.wireOp",EDGE,"E7.5.0"),sQuery(id+"F0.wireOp",EDGE,"E7.5.1"),sQuery(id+"F0.wireOp",EDGE,"E7.5.2"),sQuery(id+"F0.wireOp",EDGE,"E7.5.3"),sQuery(id+"F0.wireOp",EDGE,"E7.5.4"),sQuery(id+"F0.wireOp",EDGE,"E7.5.5"),sQuery(id+"F0.wireOp",EDGE,"E7.6.0"),sQuery(id+"F0.wireOp",EDGE,"E7.6.1"),sQuery(id+"F0.wireOp",EDGE,"E7.6.2"),sQuery(id+"F0.wireOp",EDGE,"E7.6.3"),sQuery(id+"F0.wireOp",EDGE,"E7.6.4"),sQuery(id+"F0.wireOp",EDGE,"E7.6.5"),sQuery(id+"F0.wireOp",EDGE,"E7.7.0"),sQuery(id+"F0.wireOp",EDGE,"E7.7.1"),sQuery(id+"F0.wireOp",EDGE,"E7.7.2"),sQuery(id+"F0.wireOp",EDGE,"E7.7.3"),sQuery(id+"F0.wireOp",EDGE,"E7.7.4"),sQuery(id+"F0.wireOp",EDGE,"E7.7.5"),sQuery(id+"F0.wireOp",EDGE,"E7.8.0"),sQuery(id+"F0.wireOp",EDGE,"E7.8.1"),sQuery(id+"F0.wireOp",EDGE,"E7.8.2"),sQuery(id+"F0.wireOp",EDGE,"E7.8.3"),sQuery(id+"F0.wireOp",EDGE,"E7.8.4"),sQuery(id+"F0.wireOp",EDGE,"E7.8.5"),sQuery(id+"F0.wireOp",EDGE,"E7.9.0"),sQuery(id+"F0.wireOp",EDGE,"E7.9.1"),sQuery(id+"F0.wireOp",EDGE,"E7.9.2"),sQuery(id+"F0.wireOp",EDGE,"E7.9.3"),sQuery(id+"F0.wireOp",EDGE,"E7.9.4"),sQuery(id+"F0.wireOp",EDGE,"E7.9.5"),sQuery(id+"F0.wireOp",EDGE,"E7.10.0"),sQuery(id+"F0.wireOp",EDGE,"E7.10.1"),sQuery(id+"F0.wireOp",EDGE,"E7.10.2"),sQuery(id+"F0.wireOp",EDGE,"E7.10.3"),sQuery(id+"F0.wireOp",EDGE,"E7.10.4"),sQuery(id+"F0.wireOp",EDGE,"E7.10.5"),sQuery(id+"F0.wireOp",EDGE,"E7.11.0"),sQuery(id+"F0.wireOp",EDGE,"E7.11.1"),sQuery(id+"F0.wireOp",EDGE,"E7.11.2"),sQuery(id+"F0.wireOp",EDGE,"E7.11.3"),sQuery(id+"F0.wireOp",EDGE,"E7.11.4"),sQuery(id+"F0.wireOp",EDGE,"E7.11.5"),sQuery(id+"F0.wireOp",EDGE,"E7.12.0"),sQuery(id+"F0.wireOp",EDGE,"E7.12.1"),sQuery(id+"F0.wireOp",EDGE,"E7.12.2"),sQuery(id+"F0.wireOp",EDGE,"E7.12.3"),sQuery(id+"F0.wireOp",EDGE,"E7.12.4"),sQuery(id+"F0.wireOp",EDGE,"E7.12.5"),sQuery(id+"F0.wireOp",EDGE,"E7.13.0"),sQuery(id+"F0.wireOp",EDGE,"E7.13.1"),sQuery(id+"F0.wireOp",EDGE,"E7.13.2"),sQuery(id+"F0.wireOp",EDGE,"E7.13.3"),sQuery(id+"F0.wireOp",EDGE,"E7.13.4"),sQuery(id+"F0.wireOp",EDGE,"E7.13.5"),sQuery(id+"F0.wireOp",EDGE,"E7.14.0"),sQuery(id+"F0.wireOp",EDGE,"E7.14.1"),sQuery(id+"F0.wireOp",EDGE,"E7.14.2"),sQuery(id+"F0.wireOp",EDGE,"E7.14.3"),sQuery(id+"F0.wireOp",EDGE,"E7.14.4"),sQuery(id+"F0.wireOp",EDGE,"E7.14.5"),subQ0,sQuery(id+"F0.wireOp",EDGE,"E7.15.1"),sQuery(id+"F0.wireOp",EDGE,"E7.15.2"),sQuery(id+"F0.wireOp",EDGE,"E7.15.3"),sQuery(id+"F0.wireOp",EDGE,"E7.15.4"),sQuery(id+"F0.wireOp",EDGE,"E7.15.5"),sQuery(id+"F0.wireOp",EDGE,"E7.16.0"),sQuery(id+"F0.wireOp",EDGE,"E7.16.1"),sQuery(id+"F0.wireOp",EDGE,"E7.16.2"),sQuery(id+"F0.wireOp",EDGE,"E7.16.3"),sQuery(id+"F0.wireOp",EDGE,"E7.16.4"),sQuery(id+"F0.wireOp",EDGE,"E7.16.5"),sQuery(id+"F0.wireOp",EDGE,"E7.17.0"),sQuery(id+"F0.wireOp",EDGE,"E7.17.1"),sQuery(id+"F0.wireOp",EDGE,"E7.17.2"),sQuery(id+"F0.wireOp",EDGE,"E7.17.3"),sQuery(id+"F0.wireOp",EDGE,"E7.17.4"),sQuery(id+"F0.wireOp",EDGE,"E7.17.5"),sQuery(id+"F0.wireOp",EDGE,"E7.18.0"),sQuery(id+"F0.wireOp",EDGE,"E7.18.1"),sQuery(id+"F0.wireOp",EDGE,"E7.18.2"),sQuery(id+"F0.wireOp",EDGE,"E7.18.3"),sQuery(id+"F0.wireOp",EDGE,"E7.18.4"),sQuery(id+"F0.wireOp",EDGE,"E7.18.5"),sQuery(id+"F0.wireOp",EDGE,"E7.19.0"),sQuery(id+"F0.wireOp",EDGE,"E7.19.1"),sQuery(id+"F0.wireOp",EDGE,"E7.19.2"),sQuery(id+"F0.wireOp",EDGE,"E7.19.3"),sQuery(id+"F0.wireOp",EDGE,"E7.19.4"),sQuery(id+"F0.wireOp",EDGE,"E7.19.5"),sQuery(id+"F0.wireOp",EDGE,"E7.20.0"),sQuery(id+"F0.wireOp",EDGE,"E7.20.1"),sQuery(id+"F0.wireOp",EDGE,"E7.20.2"),sQuery(id+"F0.wireOp",EDGE,"E7.20.3"),sQuery(id+"F0.wireOp",EDGE,"E7.20.4"),sQuery(id+"F0.wireOp",EDGE,"E7.20.5"),sQuery(id+"F0.wireOp",EDGE,"E7.21.0"),sQuery(id+"F0.wireOp",EDGE,"E7.21.1"),sQuery(id+"F0.wireOp",EDGE,"E7.21.2"),sQuery(id+"F0.wireOp",EDGE,"E7.21.3"),sQuery(id+"F0.wireOp",EDGE,"E7.21.4"),sQuery(id+"F0.wireOp",EDGE,"E7.21.5"),sQuery(id+"F0.wireOp",EDGE,"E7.22.0"),sQuery(id+"F0.wireOp",EDGE,"E7.22.1"),sQuery(id+"F0.wireOp",EDGE,"E7.22.2"),sQuery(id+"F0.wireOp",EDGE,"E7.22.3"),sQuery(id+"F0.wireOp",EDGE,"E7.22.4"),sQuery(id+"F0.wireOp",EDGE,"E7.22.5"),sQuery(id+"F0.wireOp",EDGE,"E7.23.0"),sQuery(id+"F0.wireOp",EDGE,"E7.23.1"),sQuery(id+"F0.wireOp",EDGE,"E7.23.2"),sQuery(id+"F0.wireOp",EDGE,"E7.23.3"),sQuery(id+"F0.wireOp",EDGE,"E7.23.4"),sQuery(id+"F0.wireOp",EDGE,"E7.23.5"),sQuery(id+"F0.wireOp",EDGE,"E7.24.0"),sQuery(id+"F0.wireOp",EDGE,"E7.24.1"),sQuery(id+"F0.wireOp",EDGE,"E7.24.2"),sQuery(id+"F0.wireOp",EDGE,"E7.24.3"),sQuery(id+"F0.wireOp",EDGE,"E7.24.4"),sQuery(id+"F0.wireOp",EDGE,"E7.24.5"),sQuery(id+"F0.wireOp",EDGE,"E7.25.0"),sQuery(id+"F0.wireOp",EDGE,"E7.25.1"),sQuery(id+"F0.wireOp",EDGE,"E7.25.2"),sQuery(id+"F0.wireOp",EDGE,"E7.25.3"),sQuery(id+"F0.wireOp",EDGE,"E7.25.4"),sQuery(id+"F0.wireOp",EDGE,"E7.25.5"),sQuery(id+"F0.wireOp",EDGE,"E7.26.0"),sQuery(id+"F0.wireOp",EDGE,"E7.26.1"),sQuery(id+"F0.wireOp",EDGE,"E7.26.2"),sQuery(id+"F0.wireOp",EDGE,"E7.26.3"),sQuery(id+"F0.wireOp",EDGE,"E7.26.4"),sQuery(id+"F0.wireOp",EDGE,"E7.26.5"),sQuery(id+"F0.wireOp",EDGE,"E7.27.0"),sQuery(id+"F0.wireOp",EDGE,"E7.27.1"),sQuery(id+"F0.wireOp",EDGE,"E7.27.2"),sQuery(id+"F0.wireOp",EDGE,"E7.27.3"),sQuery(id+"F0.wireOp",EDGE,"E7.27.4"),sQuery(id+"F0.wireOp",EDGE,"E7.27.5"),sQuery(id+"F0.wireOp",EDGE,"E7.28.0"),sQuery(id+"F0.wireOp",EDGE,"E7.28.1"),sQuery(id+"F0.wireOp",EDGE,"E7.28.2"),sQuery(id+"F0.wireOp",EDGE,"E7.28.3"),sQuery(id+"F0.wireOp",EDGE,"E7.28.4"),sQuery(id+"F0.wireOp",EDGE,"E7.28.5"),sQuery(id+"F0.wireOp",EDGE,"E7.29.0"),sQuery(id+"F0.wireOp",EDGE,"E7.29.1"),sQuery(id+"F0.wireOp",EDGE,"E7.29.2"),sQuery(id+"F0.wireOp",EDGE,"E7.29.3"),sQuery(id+"F0.wireOp",EDGE,"E7.29.4"),sQuery(id+"F0.wireOp",EDGE,"E7.29.5"),sQuery(id+"F0.wireOp",EDGE,"E7.30.0"),sQuery(id+"F0.wireOp",EDGE,"E7.30.1"),sQuery(id+"F0.wireOp",EDGE,"E7.30.2"),sQuery(id+"F0.wireOp",EDGE,"E7.30.3"),sQuery(id+"F0.wireOp",EDGE,"E7.30.4"),sQuery(id+"F0.wireOp",EDGE,"E7.30.5"),sQuery(id+"F0.wireOp",EDGE,"E7.31.0"),sQuery(id+"F0.wireOp",EDGE,"E7.31.1"),sQuery(id+"F0.wireOp",EDGE,"E7.31.2"),sQuery(id+"F0.wireOp",EDGE,"E7.31.3"),sQuery(id+"F0.wireOp",EDGE,"E7.31.4"),sQuery(id+"F0.wireOp",EDGE,"E7.31.5"),sQuery(id+"F0.wireOp",EDGE,"E7.32.0"),sQuery(id+"F0.wireOp",EDGE,"E7.32.1"),sQuery(id+"F0.wireOp",EDGE,"E7.32.2"),sQuery(id+"F0.wireOp",EDGE,"E7.32.3"),sQuery(id+"F0.wireOp",EDGE,"E7.32.4"),sQuery(id+"F0.wireOp",EDGE,"E7.32.5"),sQuery(id+"F0.wireOp",EDGE,"E7.33.0"),sQuery(id+"F0.wireOp",EDGE,"E7.33.1"),sQuery(id+"F0.wireOp",EDGE,"E7.33.2"),sQuery(id+"F0.wireOp",EDGE,"E7.33.3"),sQuery(id+"F0.wireOp",EDGE,"E7.33.4"),sQuery(id+"F0.wireOp",EDGE,"E7.33.5"),sQuery(id+"F0.wireOp",EDGE,"E7.34.0"),sQuery(id+"F0.wireOp",EDGE,"E7.34.1"),sQuery(id+"F0.wireOp",EDGE,"E7.34.2"),sQuery(id+"F0.wireOp",EDGE,"E7.34.3"),sQuery(id+"F0.wireOp",EDGE,"E7.34.4"),sQuery(id+"F0.wireOp",EDGE,"E7.34.5"),sQuery(id+"F0.wireOp",EDGE,"E7.35.0"),sQuery(id+"F0.wireOp",EDGE,"E7.35.1"),sQuery(id+"F0.wireOp",EDGE,"E7.35.2"),sQuery(id+"F0.wireOp",EDGE,"E7.35.3"),sQuery(id+"F0.wireOp",EDGE,"E7.35.4"),sQuery(id+"F0.wireOp",EDGE,"E7.35.5"),sQuery(id+"F0.wireOp",EDGE,"E7.36.0"),sQuery(id+"F0.wireOp",EDGE,"E7.36.1"),sQuery(id+"F0.wireOp",EDGE,"E7.36.2"),sQuery(id+"F0.wireOp",EDGE,"E7.36.3"),sQuery(id+"F0.wireOp",EDGE,"E7.36.4"),sQuery(id+"F0.wireOp",EDGE,"E7.36.5"),sQuery(id+"F0.wireOp",EDGE,"E7.37.0"),sQuery(id+"F0.wireOp",EDGE,"E7.37.1"),sQuery(id+"F0.wireOp",EDGE,"E7.37.2"),sQuery(id+"F0.wireOp",EDGE,"E7.37.3"),sQuery(id+"F0.wireOp",EDGE,"E7.37.4"),sQuery(id+"F0.wireOp",EDGE,"E7.37.5"),sQuery(id+"F0.wireOp",EDGE,"E7.38.0"),sQuery(id+"F0.wireOp",EDGE,"E7.38.1"),sQuery(id+"F0.wireOp",EDGE,"E7.38.2"),sQuery(id+"F0.wireOp",EDGE,"E7.38.3"),sQuery(id+"F0.wireOp",EDGE,"E7.38.4"),sQuery(id+"F0.wireOp",EDGE,"E7.38.5"),sQuery(id+"F0.wireOp",EDGE,"E7.39.0"),sQuery(id+"F0.wireOp",EDGE,"E7.39.1"),sQuery(id+"F0.wireOp",EDGE,"E7.39.2"),sQuery(id+"F0.wireOp",EDGE,"E7.39.3"),sQuery(id+"F0.wireOp",EDGE,"E7.39.4"),sQuery(id+"F0.wireOp",EDGE,"E7.39.5"),sQuery(id+"F0.wireOp",EDGE,"E7.40.0"),sQuery(id+"F0.wireOp",EDGE,"E7.40.1"),sQuery(id+"F0.wireOp",EDGE,"E7.40.2"),sQuery(id+"F0.wireOp",EDGE,"E7.40.3"),sQuery(id+"F0.wireOp",EDGE,"E7.40.4"),sQuery(id+"F0.wireOp",EDGE,"E7.40.5"),sQuery(id+"F0.wireOp",EDGE,"E7.41.0"),sQuery(id+"F0.wireOp",EDGE,"E7.41.1"),sQuery(id+"F0.wireOp",EDGE,"E7.41.2"),sQuery(id+"F0.wireOp",EDGE,"E7.41.3"),sQuery(id+"F0.wireOp",EDGE,"E7.41.4"),sQuery(id+"F0.wireOp",EDGE,"E7.41.5"),sQuery(id+"F0.wireOp",EDGE,"E7.42.0"),sQuery(id+"F0.wireOp",EDGE,"E7.42.1"),sQuery(id+"F0.wireOp",EDGE,"E7.42.2"),sQuery(id+"F0.wireOp",EDGE,"E7.42.3"),sQuery(id+"F0.wireOp",EDGE,"E7.42.4"),sQuery(id+"F0.wireOp",EDGE,"E7.42.5"),sQuery(id+"F0.wireOp",EDGE,"E7.43.0"),sQuery(id+"F0.wireOp",EDGE,"E7.43.1"),sQuery(id+"F0.wireOp",EDGE,"E7.43.2"),sQuery(id+"F0.wireOp",EDGE,"E7.43.3"),sQuery(id+"F0.wireOp",EDGE,"E7.43.4"),sQuery(id+"F0.wireOp",EDGE,"E7.43.5")])],"isStart":false})],"blendedInto":[makeQuery(id+"F1.opExtrude","CAP_FACE",FACE,{"disambiguationData":[OSD([sQuery(id+"F0.wireOp",EDGE,"E1"),sQuery(id+"F0.wireOp",EDGE,"E2"),sQuery(id+"F0.wireOp",EDGE,"E3"),sQuery(id+"F0.wireOp",EDGE,"E4"),sQuery(id+"F0.wireOp",EDGE,"E5"),sQuery(id+"F0.wireOp",EDGE,"E6"),sQuery(id+"F0.wireOp",EDGE,"E7.1.0"),sQuery(id+"F0.wireOp",EDGE,"E7.1.1"),sQuery(id+"F0.wireOp",EDGE,"E7.1.2"),sQuery(id+"F0.wireOp",EDGE,"E7.1.3"),sQuery(id+"F0.wireOp",EDGE,"E7.1.4"),sQuery(id+"F0.wireOp",EDGE,"E7.1.5"),sQuery(id+"F0.wireOp",EDGE,"E7.2.0"),sQuery(id+"F0.wireOp",EDGE,"E7.2.1"),sQuery(id+"F0.wireOp",EDGE,"E7.2.2"),sQuery(id+"F0.wireOp",EDGE,"E7.2.3"),sQuery(id+"F0.wireOp",EDGE,"E7.2.4"),sQuery(id+"F0.wireOp",EDGE,"E7.2.5"),sQuery(id+"F0.wireOp",EDGE,"E7.3.0"),sQuery(id+"F0.wireOp",EDGE,"E7.3.1"),sQuery(id+"F0.wireOp",EDGE,"E7.3.2"),sQuery(id+"F0.wireOp",EDGE,"E7.3.3"),sQuery(id+"F0.wireOp",EDGE,"E7.3.4"),sQuery(id+"F0.wireOp",EDGE,"E7.3.5"),sQuery(id+"F0.wireOp",EDGE,"E7.4.0"),sQuery(id+"F0.wireOp",EDGE,"E7.4.1"),sQuery(id+"F0.wireOp",EDGE,"E7.4.2"),sQuery(id+"F0.wireOp",EDGE,"E7.4.3"),sQuery(id+"F0.wireOp",EDGE,"E7.4.4"),sQuery(id+"F0.wireOp",EDGE,"E7.4.5"),sQuery(id+"F0.wireOp",EDGE,"E7.5.0"),sQuery(id+"F0.wireOp",EDGE,"E7.5.1"),sQuery(id+"F0.wireOp",EDGE,"E7.5.2"),sQuery(id+"F0.wireOp",EDGE,"E7.5.3"),sQuery(id+"F0.wireOp",EDGE,"E7.5.4"),sQuery(id+"F0.wireOp",EDGE,"E7.5.5"),sQuery(id+"F0.wireOp",EDGE,"E7.6.0"),sQuery(id+"F0.wireOp",EDGE,"E7.6.1"),sQuery(id+"F0.wireOp",EDGE,"E7.6.2"),sQuery(id+"F0.wireOp",EDGE,"E7.6.3"),sQuery(id+"F0.wireOp",EDGE,"E7.6.4"),sQuery(id+"F0.wireOp",EDGE,"E7.6.5"),sQuery(id+"F0.wireOp",EDGE,"E7.7.0"),sQuery(id+"F0.wireOp",EDGE,"E7.7.1"),sQuery(id+"F0.wireOp",EDGE,"E7.7.2"),sQuery(id+"F0.wireOp",EDGE,"E7.7.3"),sQuery(id+"F0.wireOp",EDGE,"E7.7.4"),sQuery(id+"F0.wireOp",EDGE,"E7.7.5"),sQuery(id+"F0.wireOp",EDGE,"E7.8.0"),sQuery(id+"F0.wireOp",EDGE,"E7.8.1"),sQuery(id+"F0.wireOp",EDGE,"E7.8.2"),sQuery(id+"F0.wireOp",EDGE,"E7.8.3"),sQuery(id+"F0.wireOp",EDGE,"E7.8.4"),sQuery(id+"F0.wireOp",EDGE,"E7.8.5"),sQuery(id+"F0.wireOp",EDGE,"E7.9.0"),sQuery(id+"F0.wireOp",EDGE,"E7.9.1"),sQuery(id+"F0.wireOp",EDGE,"E7.9.2"),sQuery(id+"F0.wireOp",EDGE,"E7.9.3"),sQuery(id+"F0.wireOp",EDGE,"E7.9.4"),sQuery(id+"F0.wireOp",EDGE,"E7.9.5"),sQuery(id+"F0.wireOp",EDGE,"E7.10.0"),sQuery(id+"F0.wireOp",EDGE,"E7.10.1"),sQuery(id+"F0.wireOp",EDGE,"E7.10.2"),sQuery(id+"F0.wireOp",EDGE,"E7.10.3"),sQuery(id+"F0.wireOp",EDGE,"E7.10.4"),sQuery(id+"F0.wireOp",EDGE,"E7.10.5"),sQuery(id+"F0.wireOp",EDGE,"E7.11.0"),sQuery(id+"F0.wireOp",EDGE,"E7.11.1"),sQuery(id+"F0.wireOp",EDGE,"E7.11.2"),sQuery(id+"F0.wireOp",EDGE,"E7.11.3"),sQuery(id+"F0.wireOp",EDGE,"E7.11.4"),sQuery(id+"F0.wireOp",EDGE,"E7.11.5"),sQuery(id+"F0.wireOp",EDGE,"E7.12.0"),sQuery(id+"F0.wireOp",EDGE,"E7.12.1"),sQuery(id+"F0.wireOp",EDGE,"E7.12.2"),sQuery(id+"F0.wireOp",EDGE,"E7.12.3"),sQuery(id+"F0.wireOp",EDGE,"E7.12.4"),sQuery(id+"F0.wireOp",EDGE,"E7.12.5"),sQuery(id+"F0.wireOp",EDGE,"E7.13.0"),sQuery(id+"F0.wireOp",EDGE,"E7.13.1"),sQuery(id+"F0.wireOp",EDGE,"E7.13.2"),sQuery(id+"F0.wireOp",EDGE,"E7.13.3"),sQuery(id+"F0.wireOp",EDGE,"E7.13.4"),sQuery(id+"F0.wireOp",EDGE,"E7.13.5"),sQuery(id+"F0.wireOp",EDGE,"E7.14.0"),sQuery(id+"F0.wireOp",EDGE,"E7.14.1"),sQuery(id+"F0.wireOp",EDGE,"E7.14.2"),sQuery(id+"F0.wireOp",EDGE,"E7.14.3"),sQuery(id+"F0.wireOp",EDGE,"E7.14.4"),sQuery(id+"F0.wireOp",EDGE,"E7.14.5"),subQ0,sQuery(id+"F0.wireOp",EDGE,"E7.15.1"),sQuery(id+"F0.wireOp",EDGE,"E7.15.2"),sQuery(id+"F0.wireOp",EDGE,"E7.15.3"),sQuery(id+"F0.wireOp",EDGE,"E7.15.4"),sQuery(id+"F0.wireOp",EDGE,"E7.15.5"),sQuery(id+"F0.wireOp",EDGE,"E7.16.0"),sQuery(id+"F0.wireOp",EDGE,"E7.16.1"),sQuery(id+"F0.wireOp",EDGE,"E7.16.2"),sQuery(id+"F0.wireOp",EDGE,"E7.16.3"),sQuery(id+"F0.wireOp",EDGE,"E7.16.4"),sQuery(id+"F0.wireOp",EDGE,"E7.16.5"),sQuery(id+"F0.wireOp",EDGE,"E7.17.0"),sQuery(id+"F0.wireOp",EDGE,"E7.17.1"),sQuery(id+"F0.wireOp",EDGE,"E7.17.2"),sQuery(id+"F0.wireOp",EDGE,"E7.17.3"),sQuery(id+"F0.wireOp",EDGE,"E7.17.4"),sQuery(id+"F0.wireOp",EDGE,"E7.17.5"),sQuery(id+"F0.wireOp",EDGE,"E7.18.0"),sQuery(id+"F0.wireOp",EDGE,"E7.18.1"),sQuery(id+"F0.wireOp",EDGE,"E7.18.2"),sQuery(id+"F0.wireOp",EDGE,"E7.18.3"),sQuery(id+"F0.wireOp",EDGE,"E7.18.4"),sQuery(id+"F0.wireOp",EDGE,"E7.18.5"),sQuery(id+"F0.wireOp",EDGE,"E7.19.0"),sQuery(id+"F0.wireOp",EDGE,"E7.19.1"),sQuery(id+"F0.wireOp",EDGE,"E7.19.2"),sQuery(id+"F0.wireOp",EDGE,"E7.19.3"),sQuery(id+"F0.wireOp",EDGE,"E7.19.4"),sQuery(id+"F0.wireOp",EDGE,"E7.19.5"),sQuery(id+"F0.wireOp",EDGE,"E7.20.0"),sQuery(id+"F0.wireOp",EDGE,"E7.20.1"),sQuery(id+"F0.wireOp",EDGE,"E7.20.2"),sQuery(id+"F0.wireOp",EDGE,"E7.20.3"),sQuery(id+"F0.wireOp",EDGE,"E7.20.4"),sQuery(id+"F0.wireOp",EDGE,"E7.20.5"),sQuery(id+"F0.wireOp",EDGE,"E7.21.0"),sQuery(id+"F0.wireOp",EDGE,"E7.21.1"),sQuery(id+"F0.wireOp",EDGE,"E7.21.2"),sQuery(id+"F0.wireOp",EDGE,"E7.21.3"),sQuery(id+"F0.wireOp",EDGE,"E7.21.4"),sQuery(id+"F0.wireOp",EDGE,"E7.21.5"),sQuery(id+"F0.wireOp",EDGE,"E7.22.0"),sQuery(id+"F0.wireOp",EDGE,"E7.22.1"),sQuery(id+"F0.wireOp",EDGE,"E7.22.2"),sQuery(id+"F0.wireOp",EDGE,"E7.22.3"),sQuery(id+"F0.wireOp",EDGE,"E7.22.4"),sQuery(id+"F0.wireOp",EDGE,"E7.22.5"),sQuery(id+"F0.wireOp",EDGE,"E7.23.0"),sQuery(id+"F0.wireOp",EDGE,"E7.23.1"),sQuery(id+"F0.wireOp",EDGE,"E7.23.2"),sQuery(id+"F0.wireOp",EDGE,"E7.23.3"),sQuery(id+"F0.wireOp",EDGE,"E7.23.4"),sQuery(id+"F0.wireOp",EDGE,"E7.23.5"),sQuery(id+"F0.wireOp",EDGE,"E7.24.0"),sQuery(id+"F0.wireOp",EDGE,"E7.24.1"),sQuery(id+"F0.wireOp",EDGE,"E7.24.2"),sQuery(id+"F0.wireOp",EDGE,"E7.24.3"),sQuery(id+"F0.wireOp",EDGE,"E7.24.4"),sQuery(id+"F0.wireOp",EDGE,"E7.24.5"),sQuery(id+"F0.wireOp",EDGE,"E7.25.0"),sQuery(id+"F0.wireOp",EDGE,"E7.25.1"),sQuery(id+"F0.wireOp",EDGE,"E7.25.2"),sQuery(id+"F0.wireOp",EDGE,"E7.25.3"),sQuery(id+"F0.wireOp",EDGE,"E7.25.4"),sQuery(id+"F0.wireOp",EDGE,"E7.25.5"),sQuery(id+"F0.wireOp",EDGE,"E7.26.0"),sQuery(id+"F0.wireOp",EDGE,"E7.26.1"),sQuery(id+"F0.wireOp",EDGE,"E7.26.2"),sQuery(id+"F0.wireOp",EDGE,"E7.26.3"),sQuery(id+"F0.wireOp",EDGE,"E7.26.4"),sQuery(id+"F0.wireOp",EDGE,"E7.26.5"),sQuery(id+"F0.wireOp",EDGE,"E7.27.0"),sQuery(id+"F0.wireOp",EDGE,"E7.27.1"),sQuery(id+"F0.wireOp",EDGE,"E7.27.2"),sQuery(id+"F0.wireOp",EDGE,"E7.27.3"),sQuery(id+"F0.wireOp",EDGE,"E7.27.4"),sQuery(id+"F0.wireOp",EDGE,"E7.27.5"),sQuery(id+"F0.wireOp",EDGE,"E7.28.0"),sQuery(id+"F0.wireOp",EDGE,"E7.28.1"),sQuery(id+"F0.wireOp",EDGE,"E7.28.2"),sQuery(id+"F0.wireOp",EDGE,"E7.28.3"),sQuery(id+"F0.wireOp",EDGE,"E7.28.4"),sQuery(id+"F0.wireOp",EDGE,"E7.28.5"),sQuery(id+"F0.wireOp",EDGE,"E7.29.0"),sQuery(id+"F0.wireOp",EDGE,"E7.29.1"),sQuery(id+"F0.wireOp",EDGE,"E7.29.2"),sQuery(id+"F0.wireOp",EDGE,"E7.29.3"),sQuery(id+"F0.wireOp",EDGE,"E7.29.4"),sQuery(id+"F0.wireOp",EDGE,"E7.29.5"),sQuery(id+"F0.wireOp",EDGE,"E7.30.0"),sQuery(id+"F0.wireOp",EDGE,"E7.30.1"),sQuery(id+"F0.wireOp",EDGE,"E7.30.2"),sQuery(id+"F0.wireOp",EDGE,"E7.30.3"),sQuery(id+"F0.wireOp",EDGE,"E7.30.4"),sQuery(id+"F0.wireOp",EDGE,"E7.30.5"),sQuery(id+"F0.wireOp",EDGE,"E7.31.0"),sQuery(id+"F0.wireOp",EDGE,"E7.31.1"),sQuery(id+"F0.wireOp",EDGE,"E7.31.2"),sQuery(id+"F0.wireOp",EDGE,"E7.31.3"),sQuery(id+"F0.wireOp",EDGE,"E7.31.4"),sQuery(id+"F0.wireOp",EDGE,"E7.31.5"),sQuery(id+"F0.wireOp",EDGE,"E7.32.0"),sQuery(id+"F0.wireOp",EDGE,"E7.32.1"),sQuery(id+"F0.wireOp",EDGE,"E7.32.2"),sQuery(id+"F0.wireOp",EDGE,"E7.32.3"),sQuery(id+"F0.wireOp",EDGE,"E7.32.4"),sQuery(id+"F0.wireOp",EDGE,"E7.32.5"),sQuery(id+"F0.wireOp",EDGE,"E7.33.0"),sQuery(id+"F0.wireOp",EDGE,"E7.33.1"),sQuery(id+"F0.wireOp",EDGE,"E7.33.2"),sQuery(id+"F0.wireOp",EDGE,"E7.33.3"),sQuery(id+"F0.wireOp",EDGE,"E7.33.4"),sQuery(id+"F0.wireOp",EDGE,"E7.33.5"),sQuery(id+"F0.wireOp",EDGE,"E7.34.0"),sQuery(id+"F0.wireOp",EDGE,"E7.34.1"),sQuery(id+"F0.wireOp",EDGE,"E7.34.2"),sQuery(id+"F0.wireOp",EDGE,"E7.34.3"),sQuery(id+"F0.wireOp",EDGE,"E7.34.4"),sQuery(id+"F0.wireOp",EDGE,"E7.34.5"),sQuery(id+"F0.wireOp",EDGE,"E7.35.0"),sQuery(id+"F0.wireOp",EDGE,"E7.35.1"),sQuery(id+"F0.wireOp",EDGE,"E7.35.2"),sQuery(id+"F0.wireOp",EDGE,"E7.35.3"),sQuery(id+"F0.wireOp",EDGE,"E7.35.4"),sQuery(id+"F0.wireOp",EDGE,"E7.35.5"),sQuery(id+"F0.wireOp",EDGE,"E7.36.0"),sQuery(id+"F0.wireOp",EDGE,"E7.36.1"),sQuery(id+"F0.wireOp",EDGE,"E7.36.2"),sQuery(id+"F0.wireOp",EDGE,"E7.36.3"),sQuery(id+"F0.wireOp",EDGE,"E7.36.4"),sQuery(id+"F0.wireOp",EDGE,"E7.36.5"),sQuery(id+"F0.wireOp",EDGE,"E7.37.0"),sQuery(id+"F0.wireOp",EDGE,"E7.37.1"),sQuery(id+"F0.wireOp",EDGE,"E7.37.2"),sQuery(id+"F0.wireOp",EDGE,"E7.37.3"),sQuery(id+"F0.wireOp",EDGE,"E7.37.4"),sQuery(id+"F0.wireOp",EDGE,"E7.37.5"),sQuery(id+"F0.wireOp",EDGE,"E7.38.0"),sQuery(id+"F0.wireOp",EDGE,"E7.38.1"),sQuery(id+"F0.wireOp",EDGE,"E7.38.2"),sQuery(id+"F0.wireOp",EDGE,"E7.38.3"),sQuery(id+"F0.wireOp",EDGE,"E7.38.4"),sQuery(id+"F0.wireOp",EDGE,"E7.38.5"),sQuery(id+"F0.wireOp",EDGE,"E7.39.0"),sQuery(id+"F0.wireOp",EDGE,"E7.39.1"),sQuery(id+"F0.wireOp",EDGE,"E7.39.2"),sQuery(id+"F0.wireOp",EDGE,"E7.39.3"),sQuery(id+"F0.wireOp",EDGE,"E7.39.4"),sQuery(id+"F0.wireOp",EDGE,"E7.39.5"),sQuery(id+"F0.wireOp",EDGE,"E7.40.0"),sQuery(id+"F0.wireOp",EDGE,"E7.40.1"),sQuery(id+"F0.wireOp",EDGE,"E7.40.2"),sQuery(id+"F0.wireOp",EDGE,"E7.40.3"),sQuery(id+"F0.wireOp",EDGE,"E7.40.4"),sQuery(id+"F0.wireOp",EDGE,"E7.40.5"),sQuery(id+"F0.wireOp",EDGE,"E7.41.0"),sQuery(id+"F0.wireOp",EDGE,"E7.41.1"),sQuery(id+"F0.wireOp",EDGE,"E7.41.2"),sQuery(id+"F0.wireOp",EDGE,"E7.41.3"),sQuery(id+"F0.wireOp",EDGE,"E7.41.4"),sQuery(id+"F0.wireOp",EDGE,"E7.41.5"),sQuery(id+"F0.wireOp",EDGE,"E7.42.0"),sQuery(id+"F0.wireOp",EDGE,"E7.42.1"),sQuery(id+"F0.wireOp",EDGE,"E7.42.2"),sQuery(id+"F0.wireOp",EDGE,"E7.42.3"),sQuery(id+"F0.wireOp",EDGE,"E7.42.4"),sQuery(id+"F0.wireOp",EDGE,"E7.42.5"),sQuery(id+"F0.wireOp",EDGE,"E7.43.0"),sQuery(id+"F0.wireOp",EDGE,"E7.43.1"),sQuery(id+"F0.wireOp",EDGE,"E7.43.2"),sQuery(id+"F0.wireOp",EDGE,"E7.43.3"),sQuery(id+"F0.wireOp",EDGE,"E7.43.4"),sQuery(id+"F0.wireOp",EDGE,"E7.43.5")])],"isStart":false})]});}
            var Q15;
            {var subQ0=sQuery(id+"F0.wireOp",EDGE,"E7.13.0");Q15=makeQuery(id+"F2.opChamfer","BLEND_EDGE",EDGE,{"blendedFrom":[makeQuery(id+"F1.opExtrude","CAP_EDGE",EDGE,{"disambiguationData":[OSD([subQ0])],"isStart":false}),makeQuery(id+"F1.opExtrude","CAP_FACE",FACE,{"disambiguationData":[OSD([sQuery(id+"F0.wireOp",EDGE,"E1"),sQuery(id+"F0.wireOp",EDGE,"E2"),sQuery(id+"F0.wireOp",EDGE,"E3"),sQuery(id+"F0.wireOp",EDGE,"E4"),sQuery(id+"F0.wireOp",EDGE,"E5"),sQuery(id+"F0.wireOp",EDGE,"E6"),sQuery(id+"F0.wireOp",EDGE,"E7.1.0"),sQuery(id+"F0.wireOp",EDGE,"E7.1.1"),sQuery(id+"F0.wireOp",EDGE,"E7.1.2"),sQuery(id+"F0.wireOp",EDGE,"E7.1.3"),sQuery(id+"F0.wireOp",EDGE,"E7.1.4"),sQuery(id+"F0.wireOp",EDGE,"E7.1.5"),sQuery(id+"F0.wireOp",EDGE,"E7.2.0"),sQuery(id+"F0.wireOp",EDGE,"E7.2.1"),sQuery(id+"F0.wireOp",EDGE,"E7.2.2"),sQuery(id+"F0.wireOp",EDGE,"E7.2.3"),sQuery(id+"F0.wireOp",EDGE,"E7.2.4"),sQuery(id+"F0.wireOp",EDGE,"E7.2.5"),sQuery(id+"F0.wireOp",EDGE,"E7.3.0"),sQuery(id+"F0.wireOp",EDGE,"E7.3.1"),sQuery(id+"F0.wireOp",EDGE,"E7.3.2"),sQuery(id+"F0.wireOp",EDGE,"E7.3.3"),sQuery(id+"F0.wireOp",EDGE,"E7.3.4"),sQuery(id+"F0.wireOp",EDGE,"E7.3.5"),sQuery(id+"F0.wireOp",EDGE,"E7.4.0"),sQuery(id+"F0.wireOp",EDGE,"E7.4.1"),sQuery(id+"F0.wireOp",EDGE,"E7.4.2"),sQuery(id+"F0.wireOp",EDGE,"E7.4.3"),sQuery(id+"F0.wireOp",EDGE,"E7.4.4"),sQuery(id+"F0.wireOp",EDGE,"E7.4.5"),sQuery(id+"F0.wireOp",EDGE,"E7.5.0"),sQuery(id+"F0.wireOp",EDGE,"E7.5.1"),sQuery(id+"F0.wireOp",EDGE,"E7.5.2"),sQuery(id+"F0.wireOp",EDGE,"E7.5.3"),sQuery(id+"F0.wireOp",EDGE,"E7.5.4"),sQuery(id+"F0.wireOp",EDGE,"E7.5.5"),sQuery(id+"F0.wireOp",EDGE,"E7.6.0"),sQuery(id+"F0.wireOp",EDGE,"E7.6.1"),sQuery(id+"F0.wireOp",EDGE,"E7.6.2"),sQuery(id+"F0.wireOp",EDGE,"E7.6.3"),sQuery(id+"F0.wireOp",EDGE,"E7.6.4"),sQuery(id+"F0.wireOp",EDGE,"E7.6.5"),sQuery(id+"F0.wireOp",EDGE,"E7.7.0"),sQuery(id+"F0.wireOp",EDGE,"E7.7.1"),sQuery(id+"F0.wireOp",EDGE,"E7.7.2"),sQuery(id+"F0.wireOp",EDGE,"E7.7.3"),sQuery(id+"F0.wireOp",EDGE,"E7.7.4"),sQuery(id+"F0.wireOp",EDGE,"E7.7.5"),sQuery(id+"F0.wireOp",EDGE,"E7.8.0"),sQuery(id+"F0.wireOp",EDGE,"E7.8.1"),sQuery(id+"F0.wireOp",EDGE,"E7.8.2"),sQuery(id+"F0.wireOp",EDGE,"E7.8.3"),sQuery(id+"F0.wireOp",EDGE,"E7.8.4"),sQuery(id+"F0.wireOp",EDGE,"E7.8.5"),sQuery(id+"F0.wireOp",EDGE,"E7.9.0"),sQuery(id+"F0.wireOp",EDGE,"E7.9.1"),sQuery(id+"F0.wireOp",EDGE,"E7.9.2"),sQuery(id+"F0.wireOp",EDGE,"E7.9.3"),sQuery(id+"F0.wireOp",EDGE,"E7.9.4"),sQuery(id+"F0.wireOp",EDGE,"E7.9.5"),sQuery(id+"F0.wireOp",EDGE,"E7.10.0"),sQuery(id+"F0.wireOp",EDGE,"E7.10.1"),sQuery(id+"F0.wireOp",EDGE,"E7.10.2"),sQuery(id+"F0.wireOp",EDGE,"E7.10.3"),sQuery(id+"F0.wireOp",EDGE,"E7.10.4"),sQuery(id+"F0.wireOp",EDGE,"E7.10.5"),sQuery(id+"F0.wireOp",EDGE,"E7.11.0"),sQuery(id+"F0.wireOp",EDGE,"E7.11.1"),sQuery(id+"F0.wireOp",EDGE,"E7.11.2"),sQuery(id+"F0.wireOp",EDGE,"E7.11.3"),sQuery(id+"F0.wireOp",EDGE,"E7.11.4"),sQuery(id+"F0.wireOp",EDGE,"E7.11.5"),sQuery(id+"F0.wireOp",EDGE,"E7.12.0"),sQuery(id+"F0.wireOp",EDGE,"E7.12.1"),sQuery(id+"F0.wireOp",EDGE,"E7.12.2"),sQuery(id+"F0.wireOp",EDGE,"E7.12.3"),sQuery(id+"F0.wireOp",EDGE,"E7.12.4"),sQuery(id+"F0.wireOp",EDGE,"E7.12.5"),subQ0,sQuery(id+"F0.wireOp",EDGE,"E7.13.1"),sQuery(id+"F0.wireOp",EDGE,"E7.13.2"),sQuery(id+"F0.wireOp",EDGE,"E7.13.3"),sQuery(id+"F0.wireOp",EDGE,"E7.13.4"),sQuery(id+"F0.wireOp",EDGE,"E7.13.5"),sQuery(id+"F0.wireOp",EDGE,"E7.14.0"),sQuery(id+"F0.wireOp",EDGE,"E7.14.1"),sQuery(id+"F0.wireOp",EDGE,"E7.14.2"),sQuery(id+"F0.wireOp",EDGE,"E7.14.3"),sQuery(id+"F0.wireOp",EDGE,"E7.14.4"),sQuery(id+"F0.wireOp",EDGE,"E7.14.5"),sQuery(id+"F0.wireOp",EDGE,"E7.15.0"),sQuery(id+"F0.wireOp",EDGE,"E7.15.1"),sQuery(id+"F0.wireOp",EDGE,"E7.15.2"),sQuery(id+"F0.wireOp",EDGE,"E7.15.3"),sQuery(id+"F0.wireOp",EDGE,"E7.15.4"),sQuery(id+"F0.wireOp",EDGE,"E7.15.5"),sQuery(id+"F0.wireOp",EDGE,"E7.16.0"),sQuery(id+"F0.wireOp",EDGE,"E7.16.1"),sQuery(id+"F0.wireOp",EDGE,"E7.16.2"),sQuery(id+"F0.wireOp",EDGE,"E7.16.3"),sQuery(id+"F0.wireOp",EDGE,"E7.16.4"),sQuery(id+"F0.wireOp",EDGE,"E7.16.5"),sQuery(id+"F0.wireOp",EDGE,"E7.17.0"),sQuery(id+"F0.wireOp",EDGE,"E7.17.1"),sQuery(id+"F0.wireOp",EDGE,"E7.17.2"),sQuery(id+"F0.wireOp",EDGE,"E7.17.3"),sQuery(id+"F0.wireOp",EDGE,"E7.17.4"),sQuery(id+"F0.wireOp",EDGE,"E7.17.5"),sQuery(id+"F0.wireOp",EDGE,"E7.18.0"),sQuery(id+"F0.wireOp",EDGE,"E7.18.1"),sQuery(id+"F0.wireOp",EDGE,"E7.18.2"),sQuery(id+"F0.wireOp",EDGE,"E7.18.3"),sQuery(id+"F0.wireOp",EDGE,"E7.18.4"),sQuery(id+"F0.wireOp",EDGE,"E7.18.5"),sQuery(id+"F0.wireOp",EDGE,"E7.19.0"),sQuery(id+"F0.wireOp",EDGE,"E7.19.1"),sQuery(id+"F0.wireOp",EDGE,"E7.19.2"),sQuery(id+"F0.wireOp",EDGE,"E7.19.3"),sQuery(id+"F0.wireOp",EDGE,"E7.19.4"),sQuery(id+"F0.wireOp",EDGE,"E7.19.5"),sQuery(id+"F0.wireOp",EDGE,"E7.20.0"),sQuery(id+"F0.wireOp",EDGE,"E7.20.1"),sQuery(id+"F0.wireOp",EDGE,"E7.20.2"),sQuery(id+"F0.wireOp",EDGE,"E7.20.3"),sQuery(id+"F0.wireOp",EDGE,"E7.20.4"),sQuery(id+"F0.wireOp",EDGE,"E7.20.5"),sQuery(id+"F0.wireOp",EDGE,"E7.21.0"),sQuery(id+"F0.wireOp",EDGE,"E7.21.1"),sQuery(id+"F0.wireOp",EDGE,"E7.21.2"),sQuery(id+"F0.wireOp",EDGE,"E7.21.3"),sQuery(id+"F0.wireOp",EDGE,"E7.21.4"),sQuery(id+"F0.wireOp",EDGE,"E7.21.5"),sQuery(id+"F0.wireOp",EDGE,"E7.22.0"),sQuery(id+"F0.wireOp",EDGE,"E7.22.1"),sQuery(id+"F0.wireOp",EDGE,"E7.22.2"),sQuery(id+"F0.wireOp",EDGE,"E7.22.3"),sQuery(id+"F0.wireOp",EDGE,"E7.22.4"),sQuery(id+"F0.wireOp",EDGE,"E7.22.5"),sQuery(id+"F0.wireOp",EDGE,"E7.23.0"),sQuery(id+"F0.wireOp",EDGE,"E7.23.1"),sQuery(id+"F0.wireOp",EDGE,"E7.23.2"),sQuery(id+"F0.wireOp",EDGE,"E7.23.3"),sQuery(id+"F0.wireOp",EDGE,"E7.23.4"),sQuery(id+"F0.wireOp",EDGE,"E7.23.5"),sQuery(id+"F0.wireOp",EDGE,"E7.24.0"),sQuery(id+"F0.wireOp",EDGE,"E7.24.1"),sQuery(id+"F0.wireOp",EDGE,"E7.24.2"),sQuery(id+"F0.wireOp",EDGE,"E7.24.3"),sQuery(id+"F0.wireOp",EDGE,"E7.24.4"),sQuery(id+"F0.wireOp",EDGE,"E7.24.5"),sQuery(id+"F0.wireOp",EDGE,"E7.25.0"),sQuery(id+"F0.wireOp",EDGE,"E7.25.1"),sQuery(id+"F0.wireOp",EDGE,"E7.25.2"),sQuery(id+"F0.wireOp",EDGE,"E7.25.3"),sQuery(id+"F0.wireOp",EDGE,"E7.25.4"),sQuery(id+"F0.wireOp",EDGE,"E7.25.5"),sQuery(id+"F0.wireOp",EDGE,"E7.26.0"),sQuery(id+"F0.wireOp",EDGE,"E7.26.1"),sQuery(id+"F0.wireOp",EDGE,"E7.26.2"),sQuery(id+"F0.wireOp",EDGE,"E7.26.3"),sQuery(id+"F0.wireOp",EDGE,"E7.26.4"),sQuery(id+"F0.wireOp",EDGE,"E7.26.5"),sQuery(id+"F0.wireOp",EDGE,"E7.27.0"),sQuery(id+"F0.wireOp",EDGE,"E7.27.1"),sQuery(id+"F0.wireOp",EDGE,"E7.27.2"),sQuery(id+"F0.wireOp",EDGE,"E7.27.3"),sQuery(id+"F0.wireOp",EDGE,"E7.27.4"),sQuery(id+"F0.wireOp",EDGE,"E7.27.5"),sQuery(id+"F0.wireOp",EDGE,"E7.28.0"),sQuery(id+"F0.wireOp",EDGE,"E7.28.1"),sQuery(id+"F0.wireOp",EDGE,"E7.28.2"),sQuery(id+"F0.wireOp",EDGE,"E7.28.3"),sQuery(id+"F0.wireOp",EDGE,"E7.28.4"),sQuery(id+"F0.wireOp",EDGE,"E7.28.5"),sQuery(id+"F0.wireOp",EDGE,"E7.29.0"),sQuery(id+"F0.wireOp",EDGE,"E7.29.1"),sQuery(id+"F0.wireOp",EDGE,"E7.29.2"),sQuery(id+"F0.wireOp",EDGE,"E7.29.3"),sQuery(id+"F0.wireOp",EDGE,"E7.29.4"),sQuery(id+"F0.wireOp",EDGE,"E7.29.5"),sQuery(id+"F0.wireOp",EDGE,"E7.30.0"),sQuery(id+"F0.wireOp",EDGE,"E7.30.1"),sQuery(id+"F0.wireOp",EDGE,"E7.30.2"),sQuery(id+"F0.wireOp",EDGE,"E7.30.3"),sQuery(id+"F0.wireOp",EDGE,"E7.30.4"),sQuery(id+"F0.wireOp",EDGE,"E7.30.5"),sQuery(id+"F0.wireOp",EDGE,"E7.31.0"),sQuery(id+"F0.wireOp",EDGE,"E7.31.1"),sQuery(id+"F0.wireOp",EDGE,"E7.31.2"),sQuery(id+"F0.wireOp",EDGE,"E7.31.3"),sQuery(id+"F0.wireOp",EDGE,"E7.31.4"),sQuery(id+"F0.wireOp",EDGE,"E7.31.5"),sQuery(id+"F0.wireOp",EDGE,"E7.32.0"),sQuery(id+"F0.wireOp",EDGE,"E7.32.1"),sQuery(id+"F0.wireOp",EDGE,"E7.32.2"),sQuery(id+"F0.wireOp",EDGE,"E7.32.3"),sQuery(id+"F0.wireOp",EDGE,"E7.32.4"),sQuery(id+"F0.wireOp",EDGE,"E7.32.5"),sQuery(id+"F0.wireOp",EDGE,"E7.33.0"),sQuery(id+"F0.wireOp",EDGE,"E7.33.1"),sQuery(id+"F0.wireOp",EDGE,"E7.33.2"),sQuery(id+"F0.wireOp",EDGE,"E7.33.3"),sQuery(id+"F0.wireOp",EDGE,"E7.33.4"),sQuery(id+"F0.wireOp",EDGE,"E7.33.5"),sQuery(id+"F0.wireOp",EDGE,"E7.34.0"),sQuery(id+"F0.wireOp",EDGE,"E7.34.1"),sQuery(id+"F0.wireOp",EDGE,"E7.34.2"),sQuery(id+"F0.wireOp",EDGE,"E7.34.3"),sQuery(id+"F0.wireOp",EDGE,"E7.34.4"),sQuery(id+"F0.wireOp",EDGE,"E7.34.5"),sQuery(id+"F0.wireOp",EDGE,"E7.35.0"),sQuery(id+"F0.wireOp",EDGE,"E7.35.1"),sQuery(id+"F0.wireOp",EDGE,"E7.35.2"),sQuery(id+"F0.wireOp",EDGE,"E7.35.3"),sQuery(id+"F0.wireOp",EDGE,"E7.35.4"),sQuery(id+"F0.wireOp",EDGE,"E7.35.5"),sQuery(id+"F0.wireOp",EDGE,"E7.36.0"),sQuery(id+"F0.wireOp",EDGE,"E7.36.1"),sQuery(id+"F0.wireOp",EDGE,"E7.36.2"),sQuery(id+"F0.wireOp",EDGE,"E7.36.3"),sQuery(id+"F0.wireOp",EDGE,"E7.36.4"),sQuery(id+"F0.wireOp",EDGE,"E7.36.5"),sQuery(id+"F0.wireOp",EDGE,"E7.37.0"),sQuery(id+"F0.wireOp",EDGE,"E7.37.1"),sQuery(id+"F0.wireOp",EDGE,"E7.37.2"),sQuery(id+"F0.wireOp",EDGE,"E7.37.3"),sQuery(id+"F0.wireOp",EDGE,"E7.37.4"),sQuery(id+"F0.wireOp",EDGE,"E7.37.5"),sQuery(id+"F0.wireOp",EDGE,"E7.38.0"),sQuery(id+"F0.wireOp",EDGE,"E7.38.1"),sQuery(id+"F0.wireOp",EDGE,"E7.38.2"),sQuery(id+"F0.wireOp",EDGE,"E7.38.3"),sQuery(id+"F0.wireOp",EDGE,"E7.38.4"),sQuery(id+"F0.wireOp",EDGE,"E7.38.5"),sQuery(id+"F0.wireOp",EDGE,"E7.39.0"),sQuery(id+"F0.wireOp",EDGE,"E7.39.1"),sQuery(id+"F0.wireOp",EDGE,"E7.39.2"),sQuery(id+"F0.wireOp",EDGE,"E7.39.3"),sQuery(id+"F0.wireOp",EDGE,"E7.39.4"),sQuery(id+"F0.wireOp",EDGE,"E7.39.5"),sQuery(id+"F0.wireOp",EDGE,"E7.40.0"),sQuery(id+"F0.wireOp",EDGE,"E7.40.1"),sQuery(id+"F0.wireOp",EDGE,"E7.40.2"),sQuery(id+"F0.wireOp",EDGE,"E7.40.3"),sQuery(id+"F0.wireOp",EDGE,"E7.40.4"),sQuery(id+"F0.wireOp",EDGE,"E7.40.5"),sQuery(id+"F0.wireOp",EDGE,"E7.41.0"),sQuery(id+"F0.wireOp",EDGE,"E7.41.1"),sQuery(id+"F0.wireOp",EDGE,"E7.41.2"),sQuery(id+"F0.wireOp",EDGE,"E7.41.3"),sQuery(id+"F0.wireOp",EDGE,"E7.41.4"),sQuery(id+"F0.wireOp",EDGE,"E7.41.5"),sQuery(id+"F0.wireOp",EDGE,"E7.42.0"),sQuery(id+"F0.wireOp",EDGE,"E7.42.1"),sQuery(id+"F0.wireOp",EDGE,"E7.42.2"),sQuery(id+"F0.wireOp",EDGE,"E7.42.3"),sQuery(id+"F0.wireOp",EDGE,"E7.42.4"),sQuery(id+"F0.wireOp",EDGE,"E7.42.5"),sQuery(id+"F0.wireOp",EDGE,"E7.43.0"),sQuery(id+"F0.wireOp",EDGE,"E7.43.1"),sQuery(id+"F0.wireOp",EDGE,"E7.43.2"),sQuery(id+"F0.wireOp",EDGE,"E7.43.3"),sQuery(id+"F0.wireOp",EDGE,"E7.43.4"),sQuery(id+"F0.wireOp",EDGE,"E7.43.5")])],"isStart":false})],"blendedInto":[makeQuery(id+"F1.opExtrude","CAP_FACE",FACE,{"disambiguationData":[OSD([sQuery(id+"F0.wireOp",EDGE,"E1"),sQuery(id+"F0.wireOp",EDGE,"E2"),sQuery(id+"F0.wireOp",EDGE,"E3"),sQuery(id+"F0.wireOp",EDGE,"E4"),sQuery(id+"F0.wireOp",EDGE,"E5"),sQuery(id+"F0.wireOp",EDGE,"E6"),sQuery(id+"F0.wireOp",EDGE,"E7.1.0"),sQuery(id+"F0.wireOp",EDGE,"E7.1.1"),sQuery(id+"F0.wireOp",EDGE,"E7.1.2"),sQuery(id+"F0.wireOp",EDGE,"E7.1.3"),sQuery(id+"F0.wireOp",EDGE,"E7.1.4"),sQuery(id+"F0.wireOp",EDGE,"E7.1.5"),sQuery(id+"F0.wireOp",EDGE,"E7.2.0"),sQuery(id+"F0.wireOp",EDGE,"E7.2.1"),sQuery(id+"F0.wireOp",EDGE,"E7.2.2"),sQuery(id+"F0.wireOp",EDGE,"E7.2.3"),sQuery(id+"F0.wireOp",EDGE,"E7.2.4"),sQuery(id+"F0.wireOp",EDGE,"E7.2.5"),sQuery(id+"F0.wireOp",EDGE,"E7.3.0"),sQuery(id+"F0.wireOp",EDGE,"E7.3.1"),sQuery(id+"F0.wireOp",EDGE,"E7.3.2"),sQuery(id+"F0.wireOp",EDGE,"E7.3.3"),sQuery(id+"F0.wireOp",EDGE,"E7.3.4"),sQuery(id+"F0.wireOp",EDGE,"E7.3.5"),sQuery(id+"F0.wireOp",EDGE,"E7.4.0"),sQuery(id+"F0.wireOp",EDGE,"E7.4.1"),sQuery(id+"F0.wireOp",EDGE,"E7.4.2"),sQuery(id+"F0.wireOp",EDGE,"E7.4.3"),sQuery(id+"F0.wireOp",EDGE,"E7.4.4"),sQuery(id+"F0.wireOp",EDGE,"E7.4.5"),sQuery(id+"F0.wireOp",EDGE,"E7.5.0"),sQuery(id+"F0.wireOp",EDGE,"E7.5.1"),sQuery(id+"F0.wireOp",EDGE,"E7.5.2"),sQuery(id+"F0.wireOp",EDGE,"E7.5.3"),sQuery(id+"F0.wireOp",EDGE,"E7.5.4"),sQuery(id+"F0.wireOp",EDGE,"E7.5.5"),sQuery(id+"F0.wireOp",EDGE,"E7.6.0"),sQuery(id+"F0.wireOp",EDGE,"E7.6.1"),sQuery(id+"F0.wireOp",EDGE,"E7.6.2"),sQuery(id+"F0.wireOp",EDGE,"E7.6.3"),sQuery(id+"F0.wireOp",EDGE,"E7.6.4"),sQuery(id+"F0.wireOp",EDGE,"E7.6.5"),sQuery(id+"F0.wireOp",EDGE,"E7.7.0"),sQuery(id+"F0.wireOp",EDGE,"E7.7.1"),sQuery(id+"F0.wireOp",EDGE,"E7.7.2"),sQuery(id+"F0.wireOp",EDGE,"E7.7.3"),sQuery(id+"F0.wireOp",EDGE,"E7.7.4"),sQuery(id+"F0.wireOp",EDGE,"E7.7.5"),sQuery(id+"F0.wireOp",EDGE,"E7.8.0"),sQuery(id+"F0.wireOp",EDGE,"E7.8.1"),sQuery(id+"F0.wireOp",EDGE,"E7.8.2"),sQuery(id+"F0.wireOp",EDGE,"E7.8.3"),sQuery(id+"F0.wireOp",EDGE,"E7.8.4"),sQuery(id+"F0.wireOp",EDGE,"E7.8.5"),sQuery(id+"F0.wireOp",EDGE,"E7.9.0"),sQuery(id+"F0.wireOp",EDGE,"E7.9.1"),sQuery(id+"F0.wireOp",EDGE,"E7.9.2"),sQuery(id+"F0.wireOp",EDGE,"E7.9.3"),sQuery(id+"F0.wireOp",EDGE,"E7.9.4"),sQuery(id+"F0.wireOp",EDGE,"E7.9.5"),sQuery(id+"F0.wireOp",EDGE,"E7.10.0"),sQuery(id+"F0.wireOp",EDGE,"E7.10.1"),sQuery(id+"F0.wireOp",EDGE,"E7.10.2"),sQuery(id+"F0.wireOp",EDGE,"E7.10.3"),sQuery(id+"F0.wireOp",EDGE,"E7.10.4"),sQuery(id+"F0.wireOp",EDGE,"E7.10.5"),sQuery(id+"F0.wireOp",EDGE,"E7.11.0"),sQuery(id+"F0.wireOp",EDGE,"E7.11.1"),sQuery(id+"F0.wireOp",EDGE,"E7.11.2"),sQuery(id+"F0.wireOp",EDGE,"E7.11.3"),sQuery(id+"F0.wireOp",EDGE,"E7.11.4"),sQuery(id+"F0.wireOp",EDGE,"E7.11.5"),sQuery(id+"F0.wireOp",EDGE,"E7.12.0"),sQuery(id+"F0.wireOp",EDGE,"E7.12.1"),sQuery(id+"F0.wireOp",EDGE,"E7.12.2"),sQuery(id+"F0.wireOp",EDGE,"E7.12.3"),sQuery(id+"F0.wireOp",EDGE,"E7.12.4"),sQuery(id+"F0.wireOp",EDGE,"E7.12.5"),subQ0,sQuery(id+"F0.wireOp",EDGE,"E7.13.1"),sQuery(id+"F0.wireOp",EDGE,"E7.13.2"),sQuery(id+"F0.wireOp",EDGE,"E7.13.3"),sQuery(id+"F0.wireOp",EDGE,"E7.13.4"),sQuery(id+"F0.wireOp",EDGE,"E7.13.5"),sQuery(id+"F0.wireOp",EDGE,"E7.14.0"),sQuery(id+"F0.wireOp",EDGE,"E7.14.1"),sQuery(id+"F0.wireOp",EDGE,"E7.14.2"),sQuery(id+"F0.wireOp",EDGE,"E7.14.3"),sQuery(id+"F0.wireOp",EDGE,"E7.14.4"),sQuery(id+"F0.wireOp",EDGE,"E7.14.5"),sQuery(id+"F0.wireOp",EDGE,"E7.15.0"),sQuery(id+"F0.wireOp",EDGE,"E7.15.1"),sQuery(id+"F0.wireOp",EDGE,"E7.15.2"),sQuery(id+"F0.wireOp",EDGE,"E7.15.3"),sQuery(id+"F0.wireOp",EDGE,"E7.15.4"),sQuery(id+"F0.wireOp",EDGE,"E7.15.5"),sQuery(id+"F0.wireOp",EDGE,"E7.16.0"),sQuery(id+"F0.wireOp",EDGE,"E7.16.1"),sQuery(id+"F0.wireOp",EDGE,"E7.16.2"),sQuery(id+"F0.wireOp",EDGE,"E7.16.3"),sQuery(id+"F0.wireOp",EDGE,"E7.16.4"),sQuery(id+"F0.wireOp",EDGE,"E7.16.5"),sQuery(id+"F0.wireOp",EDGE,"E7.17.0"),sQuery(id+"F0.wireOp",EDGE,"E7.17.1"),sQuery(id+"F0.wireOp",EDGE,"E7.17.2"),sQuery(id+"F0.wireOp",EDGE,"E7.17.3"),sQuery(id+"F0.wireOp",EDGE,"E7.17.4"),sQuery(id+"F0.wireOp",EDGE,"E7.17.5"),sQuery(id+"F0.wireOp",EDGE,"E7.18.0"),sQuery(id+"F0.wireOp",EDGE,"E7.18.1"),sQuery(id+"F0.wireOp",EDGE,"E7.18.2"),sQuery(id+"F0.wireOp",EDGE,"E7.18.3"),sQuery(id+"F0.wireOp",EDGE,"E7.18.4"),sQuery(id+"F0.wireOp",EDGE,"E7.18.5"),sQuery(id+"F0.wireOp",EDGE,"E7.19.0"),sQuery(id+"F0.wireOp",EDGE,"E7.19.1"),sQuery(id+"F0.wireOp",EDGE,"E7.19.2"),sQuery(id+"F0.wireOp",EDGE,"E7.19.3"),sQuery(id+"F0.wireOp",EDGE,"E7.19.4"),sQuery(id+"F0.wireOp",EDGE,"E7.19.5"),sQuery(id+"F0.wireOp",EDGE,"E7.20.0"),sQuery(id+"F0.wireOp",EDGE,"E7.20.1"),sQuery(id+"F0.wireOp",EDGE,"E7.20.2"),sQuery(id+"F0.wireOp",EDGE,"E7.20.3"),sQuery(id+"F0.wireOp",EDGE,"E7.20.4"),sQuery(id+"F0.wireOp",EDGE,"E7.20.5"),sQuery(id+"F0.wireOp",EDGE,"E7.21.0"),sQuery(id+"F0.wireOp",EDGE,"E7.21.1"),sQuery(id+"F0.wireOp",EDGE,"E7.21.2"),sQuery(id+"F0.wireOp",EDGE,"E7.21.3"),sQuery(id+"F0.wireOp",EDGE,"E7.21.4"),sQuery(id+"F0.wireOp",EDGE,"E7.21.5"),sQuery(id+"F0.wireOp",EDGE,"E7.22.0"),sQuery(id+"F0.wireOp",EDGE,"E7.22.1"),sQuery(id+"F0.wireOp",EDGE,"E7.22.2"),sQuery(id+"F0.wireOp",EDGE,"E7.22.3"),sQuery(id+"F0.wireOp",EDGE,"E7.22.4"),sQuery(id+"F0.wireOp",EDGE,"E7.22.5"),sQuery(id+"F0.wireOp",EDGE,"E7.23.0"),sQuery(id+"F0.wireOp",EDGE,"E7.23.1"),sQuery(id+"F0.wireOp",EDGE,"E7.23.2"),sQuery(id+"F0.wireOp",EDGE,"E7.23.3"),sQuery(id+"F0.wireOp",EDGE,"E7.23.4"),sQuery(id+"F0.wireOp",EDGE,"E7.23.5"),sQuery(id+"F0.wireOp",EDGE,"E7.24.0"),sQuery(id+"F0.wireOp",EDGE,"E7.24.1"),sQuery(id+"F0.wireOp",EDGE,"E7.24.2"),sQuery(id+"F0.wireOp",EDGE,"E7.24.3"),sQuery(id+"F0.wireOp",EDGE,"E7.24.4"),sQuery(id+"F0.wireOp",EDGE,"E7.24.5"),sQuery(id+"F0.wireOp",EDGE,"E7.25.0"),sQuery(id+"F0.wireOp",EDGE,"E7.25.1"),sQuery(id+"F0.wireOp",EDGE,"E7.25.2"),sQuery(id+"F0.wireOp",EDGE,"E7.25.3"),sQuery(id+"F0.wireOp",EDGE,"E7.25.4"),sQuery(id+"F0.wireOp",EDGE,"E7.25.5"),sQuery(id+"F0.wireOp",EDGE,"E7.26.0"),sQuery(id+"F0.wireOp",EDGE,"E7.26.1"),sQuery(id+"F0.wireOp",EDGE,"E7.26.2"),sQuery(id+"F0.wireOp",EDGE,"E7.26.3"),sQuery(id+"F0.wireOp",EDGE,"E7.26.4"),sQuery(id+"F0.wireOp",EDGE,"E7.26.5"),sQuery(id+"F0.wireOp",EDGE,"E7.27.0"),sQuery(id+"F0.wireOp",EDGE,"E7.27.1"),sQuery(id+"F0.wireOp",EDGE,"E7.27.2"),sQuery(id+"F0.wireOp",EDGE,"E7.27.3"),sQuery(id+"F0.wireOp",EDGE,"E7.27.4"),sQuery(id+"F0.wireOp",EDGE,"E7.27.5"),sQuery(id+"F0.wireOp",EDGE,"E7.28.0"),sQuery(id+"F0.wireOp",EDGE,"E7.28.1"),sQuery(id+"F0.wireOp",EDGE,"E7.28.2"),sQuery(id+"F0.wireOp",EDGE,"E7.28.3"),sQuery(id+"F0.wireOp",EDGE,"E7.28.4"),sQuery(id+"F0.wireOp",EDGE,"E7.28.5"),sQuery(id+"F0.wireOp",EDGE,"E7.29.0"),sQuery(id+"F0.wireOp",EDGE,"E7.29.1"),sQuery(id+"F0.wireOp",EDGE,"E7.29.2"),sQuery(id+"F0.wireOp",EDGE,"E7.29.3"),sQuery(id+"F0.wireOp",EDGE,"E7.29.4"),sQuery(id+"F0.wireOp",EDGE,"E7.29.5"),sQuery(id+"F0.wireOp",EDGE,"E7.30.0"),sQuery(id+"F0.wireOp",EDGE,"E7.30.1"),sQuery(id+"F0.wireOp",EDGE,"E7.30.2"),sQuery(id+"F0.wireOp",EDGE,"E7.30.3"),sQuery(id+"F0.wireOp",EDGE,"E7.30.4"),sQuery(id+"F0.wireOp",EDGE,"E7.30.5"),sQuery(id+"F0.wireOp",EDGE,"E7.31.0"),sQuery(id+"F0.wireOp",EDGE,"E7.31.1"),sQuery(id+"F0.wireOp",EDGE,"E7.31.2"),sQuery(id+"F0.wireOp",EDGE,"E7.31.3"),sQuery(id+"F0.wireOp",EDGE,"E7.31.4"),sQuery(id+"F0.wireOp",EDGE,"E7.31.5"),sQuery(id+"F0.wireOp",EDGE,"E7.32.0"),sQuery(id+"F0.wireOp",EDGE,"E7.32.1"),sQuery(id+"F0.wireOp",EDGE,"E7.32.2"),sQuery(id+"F0.wireOp",EDGE,"E7.32.3"),sQuery(id+"F0.wireOp",EDGE,"E7.32.4"),sQuery(id+"F0.wireOp",EDGE,"E7.32.5"),sQuery(id+"F0.wireOp",EDGE,"E7.33.0"),sQuery(id+"F0.wireOp",EDGE,"E7.33.1"),sQuery(id+"F0.wireOp",EDGE,"E7.33.2"),sQuery(id+"F0.wireOp",EDGE,"E7.33.3"),sQuery(id+"F0.wireOp",EDGE,"E7.33.4"),sQuery(id+"F0.wireOp",EDGE,"E7.33.5"),sQuery(id+"F0.wireOp",EDGE,"E7.34.0"),sQuery(id+"F0.wireOp",EDGE,"E7.34.1"),sQuery(id+"F0.wireOp",EDGE,"E7.34.2"),sQuery(id+"F0.wireOp",EDGE,"E7.34.3"),sQuery(id+"F0.wireOp",EDGE,"E7.34.4"),sQuery(id+"F0.wireOp",EDGE,"E7.34.5"),sQuery(id+"F0.wireOp",EDGE,"E7.35.0"),sQuery(id+"F0.wireOp",EDGE,"E7.35.1"),sQuery(id+"F0.wireOp",EDGE,"E7.35.2"),sQuery(id+"F0.wireOp",EDGE,"E7.35.3"),sQuery(id+"F0.wireOp",EDGE,"E7.35.4"),sQuery(id+"F0.wireOp",EDGE,"E7.35.5"),sQuery(id+"F0.wireOp",EDGE,"E7.36.0"),sQuery(id+"F0.wireOp",EDGE,"E7.36.1"),sQuery(id+"F0.wireOp",EDGE,"E7.36.2"),sQuery(id+"F0.wireOp",EDGE,"E7.36.3"),sQuery(id+"F0.wireOp",EDGE,"E7.36.4"),sQuery(id+"F0.wireOp",EDGE,"E7.36.5"),sQuery(id+"F0.wireOp",EDGE,"E7.37.0"),sQuery(id+"F0.wireOp",EDGE,"E7.37.1"),sQuery(id+"F0.wireOp",EDGE,"E7.37.2"),sQuery(id+"F0.wireOp",EDGE,"E7.37.3"),sQuery(id+"F0.wireOp",EDGE,"E7.37.4"),sQuery(id+"F0.wireOp",EDGE,"E7.37.5"),sQuery(id+"F0.wireOp",EDGE,"E7.38.0"),sQuery(id+"F0.wireOp",EDGE,"E7.38.1"),sQuery(id+"F0.wireOp",EDGE,"E7.38.2"),sQuery(id+"F0.wireOp",EDGE,"E7.38.3"),sQuery(id+"F0.wireOp",EDGE,"E7.38.4"),sQuery(id+"F0.wireOp",EDGE,"E7.38.5"),sQuery(id+"F0.wireOp",EDGE,"E7.39.0"),sQuery(id+"F0.wireOp",EDGE,"E7.39.1"),sQuery(id+"F0.wireOp",EDGE,"E7.39.2"),sQuery(id+"F0.wireOp",EDGE,"E7.39.3"),sQuery(id+"F0.wireOp",EDGE,"E7.39.4"),sQuery(id+"F0.wireOp",EDGE,"E7.39.5"),sQuery(id+"F0.wireOp",EDGE,"E7.40.0"),sQuery(id+"F0.wireOp",EDGE,"E7.40.1"),sQuery(id+"F0.wireOp",EDGE,"E7.40.2"),sQuery(id+"F0.wireOp",EDGE,"E7.40.3"),sQuery(id+"F0.wireOp",EDGE,"E7.40.4"),sQuery(id+"F0.wireOp",EDGE,"E7.40.5"),sQuery(id+"F0.wireOp",EDGE,"E7.41.0"),sQuery(id+"F0.wireOp",EDGE,"E7.41.1"),sQuery(id+"F0.wireOp",EDGE,"E7.41.2"),sQuery(id+"F0.wireOp",EDGE,"E7.41.3"),sQuery(id+"F0.wireOp",EDGE,"E7.41.4"),sQuery(id+"F0.wireOp",EDGE,"E7.41.5"),sQuery(id+"F0.wireOp",EDGE,"E7.42.0"),sQuery(id+"F0.wireOp",EDGE,"E7.42.1"),sQuery(id+"F0.wireOp",EDGE,"E7.42.2"),sQuery(id+"F0.wireOp",EDGE,"E7.42.3"),sQuery(id+"F0.wireOp",EDGE,"E7.42.4"),sQuery(id+"F0.wireOp",EDGE,"E7.42.5"),sQuery(id+"F0.wireOp",EDGE,"E7.43.0"),sQuery(id+"F0.wireOp",EDGE,"E7.43.1"),sQuery(id+"F0.wireOp",EDGE,"E7.43.2"),sQuery(id+"F0.wireOp",EDGE,"E7.43.3"),sQuery(id+"F0.wireOp",EDGE,"E7.43.4"),sQuery(id+"F0.wireOp",EDGE,"E7.43.5")])],"isStart":false})]});}
            var Q16;
            {var subQ0=sQuery(id+"F0.wireOp",EDGE,"E7.11.0");Q16=makeQuery(id+"F2.opChamfer","BLEND_EDGE",EDGE,{"blendedFrom":[makeQuery(id+"F1.opExtrude","CAP_EDGE",EDGE,{"disambiguationData":[OSD([subQ0])],"isStart":false}),makeQuery(id+"F1.opExtrude","CAP_FACE",FACE,{"disambiguationData":[OSD([sQuery(id+"F0.wireOp",EDGE,"E1"),sQuery(id+"F0.wireOp",EDGE,"E2"),sQuery(id+"F0.wireOp",EDGE,"E3"),sQuery(id+"F0.wireOp",EDGE,"E4"),sQuery(id+"F0.wireOp",EDGE,"E5"),sQuery(id+"F0.wireOp",EDGE,"E6"),sQuery(id+"F0.wireOp",EDGE,"E7.1.0"),sQuery(id+"F0.wireOp",EDGE,"E7.1.1"),sQuery(id+"F0.wireOp",EDGE,"E7.1.2"),sQuery(id+"F0.wireOp",EDGE,"E7.1.3"),sQuery(id+"F0.wireOp",EDGE,"E7.1.4"),sQuery(id+"F0.wireOp",EDGE,"E7.1.5"),sQuery(id+"F0.wireOp",EDGE,"E7.2.0"),sQuery(id+"F0.wireOp",EDGE,"E7.2.1"),sQuery(id+"F0.wireOp",EDGE,"E7.2.2"),sQuery(id+"F0.wireOp",EDGE,"E7.2.3"),sQuery(id+"F0.wireOp",EDGE,"E7.2.4"),sQuery(id+"F0.wireOp",EDGE,"E7.2.5"),sQuery(id+"F0.wireOp",EDGE,"E7.3.0"),sQuery(id+"F0.wireOp",EDGE,"E7.3.1"),sQuery(id+"F0.wireOp",EDGE,"E7.3.2"),sQuery(id+"F0.wireOp",EDGE,"E7.3.3"),sQuery(id+"F0.wireOp",EDGE,"E7.3.4"),sQuery(id+"F0.wireOp",EDGE,"E7.3.5"),sQuery(id+"F0.wireOp",EDGE,"E7.4.0"),sQuery(id+"F0.wireOp",EDGE,"E7.4.1"),sQuery(id+"F0.wireOp",EDGE,"E7.4.2"),sQuery(id+"F0.wireOp",EDGE,"E7.4.3"),sQuery(id+"F0.wireOp",EDGE,"E7.4.4"),sQuery(id+"F0.wireOp",EDGE,"E7.4.5"),sQuery(id+"F0.wireOp",EDGE,"E7.5.0"),sQuery(id+"F0.wireOp",EDGE,"E7.5.1"),sQuery(id+"F0.wireOp",EDGE,"E7.5.2"),sQuery(id+"F0.wireOp",EDGE,"E7.5.3"),sQuery(id+"F0.wireOp",EDGE,"E7.5.4"),sQuery(id+"F0.wireOp",EDGE,"E7.5.5"),sQuery(id+"F0.wireOp",EDGE,"E7.6.0"),sQuery(id+"F0.wireOp",EDGE,"E7.6.1"),sQuery(id+"F0.wireOp",EDGE,"E7.6.2"),sQuery(id+"F0.wireOp",EDGE,"E7.6.3"),sQuery(id+"F0.wireOp",EDGE,"E7.6.4"),sQuery(id+"F0.wireOp",EDGE,"E7.6.5"),sQuery(id+"F0.wireOp",EDGE,"E7.7.0"),sQuery(id+"F0.wireOp",EDGE,"E7.7.1"),sQuery(id+"F0.wireOp",EDGE,"E7.7.2"),sQuery(id+"F0.wireOp",EDGE,"E7.7.3"),sQuery(id+"F0.wireOp",EDGE,"E7.7.4"),sQuery(id+"F0.wireOp",EDGE,"E7.7.5"),sQuery(id+"F0.wireOp",EDGE,"E7.8.0"),sQuery(id+"F0.wireOp",EDGE,"E7.8.1"),sQuery(id+"F0.wireOp",EDGE,"E7.8.2"),sQuery(id+"F0.wireOp",EDGE,"E7.8.3"),sQuery(id+"F0.wireOp",EDGE,"E7.8.4"),sQuery(id+"F0.wireOp",EDGE,"E7.8.5"),sQuery(id+"F0.wireOp",EDGE,"E7.9.0"),sQuery(id+"F0.wireOp",EDGE,"E7.9.1"),sQuery(id+"F0.wireOp",EDGE,"E7.9.2"),sQuery(id+"F0.wireOp",EDGE,"E7.9.3"),sQuery(id+"F0.wireOp",EDGE,"E7.9.4"),sQuery(id+"F0.wireOp",EDGE,"E7.9.5"),sQuery(id+"F0.wireOp",EDGE,"E7.10.0"),sQuery(id+"F0.wireOp",EDGE,"E7.10.1"),sQuery(id+"F0.wireOp",EDGE,"E7.10.2"),sQuery(id+"F0.wireOp",EDGE,"E7.10.3"),sQuery(id+"F0.wireOp",EDGE,"E7.10.4"),sQuery(id+"F0.wireOp",EDGE,"E7.10.5"),subQ0,sQuery(id+"F0.wireOp",EDGE,"E7.11.1"),sQuery(id+"F0.wireOp",EDGE,"E7.11.2"),sQuery(id+"F0.wireOp",EDGE,"E7.11.3"),sQuery(id+"F0.wireOp",EDGE,"E7.11.4"),sQuery(id+"F0.wireOp",EDGE,"E7.11.5"),sQuery(id+"F0.wireOp",EDGE,"E7.12.0"),sQuery(id+"F0.wireOp",EDGE,"E7.12.1"),sQuery(id+"F0.wireOp",EDGE,"E7.12.2"),sQuery(id+"F0.wireOp",EDGE,"E7.12.3"),sQuery(id+"F0.wireOp",EDGE,"E7.12.4"),sQuery(id+"F0.wireOp",EDGE,"E7.12.5"),sQuery(id+"F0.wireOp",EDGE,"E7.13.0"),sQuery(id+"F0.wireOp",EDGE,"E7.13.1"),sQuery(id+"F0.wireOp",EDGE,"E7.13.2"),sQuery(id+"F0.wireOp",EDGE,"E7.13.3"),sQuery(id+"F0.wireOp",EDGE,"E7.13.4"),sQuery(id+"F0.wireOp",EDGE,"E7.13.5"),sQuery(id+"F0.wireOp",EDGE,"E7.14.0"),sQuery(id+"F0.wireOp",EDGE,"E7.14.1"),sQuery(id+"F0.wireOp",EDGE,"E7.14.2"),sQuery(id+"F0.wireOp",EDGE,"E7.14.3"),sQuery(id+"F0.wireOp",EDGE,"E7.14.4"),sQuery(id+"F0.wireOp",EDGE,"E7.14.5"),sQuery(id+"F0.wireOp",EDGE,"E7.15.0"),sQuery(id+"F0.wireOp",EDGE,"E7.15.1"),sQuery(id+"F0.wireOp",EDGE,"E7.15.2"),sQuery(id+"F0.wireOp",EDGE,"E7.15.3"),sQuery(id+"F0.wireOp",EDGE,"E7.15.4"),sQuery(id+"F0.wireOp",EDGE,"E7.15.5"),sQuery(id+"F0.wireOp",EDGE,"E7.16.0"),sQuery(id+"F0.wireOp",EDGE,"E7.16.1"),sQuery(id+"F0.wireOp",EDGE,"E7.16.2"),sQuery(id+"F0.wireOp",EDGE,"E7.16.3"),sQuery(id+"F0.wireOp",EDGE,"E7.16.4"),sQuery(id+"F0.wireOp",EDGE,"E7.16.5"),sQuery(id+"F0.wireOp",EDGE,"E7.17.0"),sQuery(id+"F0.wireOp",EDGE,"E7.17.1"),sQuery(id+"F0.wireOp",EDGE,"E7.17.2"),sQuery(id+"F0.wireOp",EDGE,"E7.17.3"),sQuery(id+"F0.wireOp",EDGE,"E7.17.4"),sQuery(id+"F0.wireOp",EDGE,"E7.17.5"),sQuery(id+"F0.wireOp",EDGE,"E7.18.0"),sQuery(id+"F0.wireOp",EDGE,"E7.18.1"),sQuery(id+"F0.wireOp",EDGE,"E7.18.2"),sQuery(id+"F0.wireOp",EDGE,"E7.18.3"),sQuery(id+"F0.wireOp",EDGE,"E7.18.4"),sQuery(id+"F0.wireOp",EDGE,"E7.18.5"),sQuery(id+"F0.wireOp",EDGE,"E7.19.0"),sQuery(id+"F0.wireOp",EDGE,"E7.19.1"),sQuery(id+"F0.wireOp",EDGE,"E7.19.2"),sQuery(id+"F0.wireOp",EDGE,"E7.19.3"),sQuery(id+"F0.wireOp",EDGE,"E7.19.4"),sQuery(id+"F0.wireOp",EDGE,"E7.19.5"),sQuery(id+"F0.wireOp",EDGE,"E7.20.0"),sQuery(id+"F0.wireOp",EDGE,"E7.20.1"),sQuery(id+"F0.wireOp",EDGE,"E7.20.2"),sQuery(id+"F0.wireOp",EDGE,"E7.20.3"),sQuery(id+"F0.wireOp",EDGE,"E7.20.4"),sQuery(id+"F0.wireOp",EDGE,"E7.20.5"),sQuery(id+"F0.wireOp",EDGE,"E7.21.0"),sQuery(id+"F0.wireOp",EDGE,"E7.21.1"),sQuery(id+"F0.wireOp",EDGE,"E7.21.2"),sQuery(id+"F0.wireOp",EDGE,"E7.21.3"),sQuery(id+"F0.wireOp",EDGE,"E7.21.4"),sQuery(id+"F0.wireOp",EDGE,"E7.21.5"),sQuery(id+"F0.wireOp",EDGE,"E7.22.0"),sQuery(id+"F0.wireOp",EDGE,"E7.22.1"),sQuery(id+"F0.wireOp",EDGE,"E7.22.2"),sQuery(id+"F0.wireOp",EDGE,"E7.22.3"),sQuery(id+"F0.wireOp",EDGE,"E7.22.4"),sQuery(id+"F0.wireOp",EDGE,"E7.22.5"),sQuery(id+"F0.wireOp",EDGE,"E7.23.0"),sQuery(id+"F0.wireOp",EDGE,"E7.23.1"),sQuery(id+"F0.wireOp",EDGE,"E7.23.2"),sQuery(id+"F0.wireOp",EDGE,"E7.23.3"),sQuery(id+"F0.wireOp",EDGE,"E7.23.4"),sQuery(id+"F0.wireOp",EDGE,"E7.23.5"),sQuery(id+"F0.wireOp",EDGE,"E7.24.0"),sQuery(id+"F0.wireOp",EDGE,"E7.24.1"),sQuery(id+"F0.wireOp",EDGE,"E7.24.2"),sQuery(id+"F0.wireOp",EDGE,"E7.24.3"),sQuery(id+"F0.wireOp",EDGE,"E7.24.4"),sQuery(id+"F0.wireOp",EDGE,"E7.24.5"),sQuery(id+"F0.wireOp",EDGE,"E7.25.0"),sQuery(id+"F0.wireOp",EDGE,"E7.25.1"),sQuery(id+"F0.wireOp",EDGE,"E7.25.2"),sQuery(id+"F0.wireOp",EDGE,"E7.25.3"),sQuery(id+"F0.wireOp",EDGE,"E7.25.4"),sQuery(id+"F0.wireOp",EDGE,"E7.25.5"),sQuery(id+"F0.wireOp",EDGE,"E7.26.0"),sQuery(id+"F0.wireOp",EDGE,"E7.26.1"),sQuery(id+"F0.wireOp",EDGE,"E7.26.2"),sQuery(id+"F0.wireOp",EDGE,"E7.26.3"),sQuery(id+"F0.wireOp",EDGE,"E7.26.4"),sQuery(id+"F0.wireOp",EDGE,"E7.26.5"),sQuery(id+"F0.wireOp",EDGE,"E7.27.0"),sQuery(id+"F0.wireOp",EDGE,"E7.27.1"),sQuery(id+"F0.wireOp",EDGE,"E7.27.2"),sQuery(id+"F0.wireOp",EDGE,"E7.27.3"),sQuery(id+"F0.wireOp",EDGE,"E7.27.4"),sQuery(id+"F0.wireOp",EDGE,"E7.27.5"),sQuery(id+"F0.wireOp",EDGE,"E7.28.0"),sQuery(id+"F0.wireOp",EDGE,"E7.28.1"),sQuery(id+"F0.wireOp",EDGE,"E7.28.2"),sQuery(id+"F0.wireOp",EDGE,"E7.28.3"),sQuery(id+"F0.wireOp",EDGE,"E7.28.4"),sQuery(id+"F0.wireOp",EDGE,"E7.28.5"),sQuery(id+"F0.wireOp",EDGE,"E7.29.0"),sQuery(id+"F0.wireOp",EDGE,"E7.29.1"),sQuery(id+"F0.wireOp",EDGE,"E7.29.2"),sQuery(id+"F0.wireOp",EDGE,"E7.29.3"),sQuery(id+"F0.wireOp",EDGE,"E7.29.4"),sQuery(id+"F0.wireOp",EDGE,"E7.29.5"),sQuery(id+"F0.wireOp",EDGE,"E7.30.0"),sQuery(id+"F0.wireOp",EDGE,"E7.30.1"),sQuery(id+"F0.wireOp",EDGE,"E7.30.2"),sQuery(id+"F0.wireOp",EDGE,"E7.30.3"),sQuery(id+"F0.wireOp",EDGE,"E7.30.4"),sQuery(id+"F0.wireOp",EDGE,"E7.30.5"),sQuery(id+"F0.wireOp",EDGE,"E7.31.0"),sQuery(id+"F0.wireOp",EDGE,"E7.31.1"),sQuery(id+"F0.wireOp",EDGE,"E7.31.2"),sQuery(id+"F0.wireOp",EDGE,"E7.31.3"),sQuery(id+"F0.wireOp",EDGE,"E7.31.4"),sQuery(id+"F0.wireOp",EDGE,"E7.31.5"),sQuery(id+"F0.wireOp",EDGE,"E7.32.0"),sQuery(id+"F0.wireOp",EDGE,"E7.32.1"),sQuery(id+"F0.wireOp",EDGE,"E7.32.2"),sQuery(id+"F0.wireOp",EDGE,"E7.32.3"),sQuery(id+"F0.wireOp",EDGE,"E7.32.4"),sQuery(id+"F0.wireOp",EDGE,"E7.32.5"),sQuery(id+"F0.wireOp",EDGE,"E7.33.0"),sQuery(id+"F0.wireOp",EDGE,"E7.33.1"),sQuery(id+"F0.wireOp",EDGE,"E7.33.2"),sQuery(id+"F0.wireOp",EDGE,"E7.33.3"),sQuery(id+"F0.wireOp",EDGE,"E7.33.4"),sQuery(id+"F0.wireOp",EDGE,"E7.33.5"),sQuery(id+"F0.wireOp",EDGE,"E7.34.0"),sQuery(id+"F0.wireOp",EDGE,"E7.34.1"),sQuery(id+"F0.wireOp",EDGE,"E7.34.2"),sQuery(id+"F0.wireOp",EDGE,"E7.34.3"),sQuery(id+"F0.wireOp",EDGE,"E7.34.4"),sQuery(id+"F0.wireOp",EDGE,"E7.34.5"),sQuery(id+"F0.wireOp",EDGE,"E7.35.0"),sQuery(id+"F0.wireOp",EDGE,"E7.35.1"),sQuery(id+"F0.wireOp",EDGE,"E7.35.2"),sQuery(id+"F0.wireOp",EDGE,"E7.35.3"),sQuery(id+"F0.wireOp",EDGE,"E7.35.4"),sQuery(id+"F0.wireOp",EDGE,"E7.35.5"),sQuery(id+"F0.wireOp",EDGE,"E7.36.0"),sQuery(id+"F0.wireOp",EDGE,"E7.36.1"),sQuery(id+"F0.wireOp",EDGE,"E7.36.2"),sQuery(id+"F0.wireOp",EDGE,"E7.36.3"),sQuery(id+"F0.wireOp",EDGE,"E7.36.4"),sQuery(id+"F0.wireOp",EDGE,"E7.36.5"),sQuery(id+"F0.wireOp",EDGE,"E7.37.0"),sQuery(id+"F0.wireOp",EDGE,"E7.37.1"),sQuery(id+"F0.wireOp",EDGE,"E7.37.2"),sQuery(id+"F0.wireOp",EDGE,"E7.37.3"),sQuery(id+"F0.wireOp",EDGE,"E7.37.4"),sQuery(id+"F0.wireOp",EDGE,"E7.37.5"),sQuery(id+"F0.wireOp",EDGE,"E7.38.0"),sQuery(id+"F0.wireOp",EDGE,"E7.38.1"),sQuery(id+"F0.wireOp",EDGE,"E7.38.2"),sQuery(id+"F0.wireOp",EDGE,"E7.38.3"),sQuery(id+"F0.wireOp",EDGE,"E7.38.4"),sQuery(id+"F0.wireOp",EDGE,"E7.38.5"),sQuery(id+"F0.wireOp",EDGE,"E7.39.0"),sQuery(id+"F0.wireOp",EDGE,"E7.39.1"),sQuery(id+"F0.wireOp",EDGE,"E7.39.2"),sQuery(id+"F0.wireOp",EDGE,"E7.39.3"),sQuery(id+"F0.wireOp",EDGE,"E7.39.4"),sQuery(id+"F0.wireOp",EDGE,"E7.39.5"),sQuery(id+"F0.wireOp",EDGE,"E7.40.0"),sQuery(id+"F0.wireOp",EDGE,"E7.40.1"),sQuery(id+"F0.wireOp",EDGE,"E7.40.2"),sQuery(id+"F0.wireOp",EDGE,"E7.40.3"),sQuery(id+"F0.wireOp",EDGE,"E7.40.4"),sQuery(id+"F0.wireOp",EDGE,"E7.40.5"),sQuery(id+"F0.wireOp",EDGE,"E7.41.0"),sQuery(id+"F0.wireOp",EDGE,"E7.41.1"),sQuery(id+"F0.wireOp",EDGE,"E7.41.2"),sQuery(id+"F0.wireOp",EDGE,"E7.41.3"),sQuery(id+"F0.wireOp",EDGE,"E7.41.4"),sQuery(id+"F0.wireOp",EDGE,"E7.41.5"),sQuery(id+"F0.wireOp",EDGE,"E7.42.0"),sQuery(id+"F0.wireOp",EDGE,"E7.42.1"),sQuery(id+"F0.wireOp",EDGE,"E7.42.2"),sQuery(id+"F0.wireOp",EDGE,"E7.42.3"),sQuery(id+"F0.wireOp",EDGE,"E7.42.4"),sQuery(id+"F0.wireOp",EDGE,"E7.42.5"),sQuery(id+"F0.wireOp",EDGE,"E7.43.0"),sQuery(id+"F0.wireOp",EDGE,"E7.43.1"),sQuery(id+"F0.wireOp",EDGE,"E7.43.2"),sQuery(id+"F0.wireOp",EDGE,"E7.43.3"),sQuery(id+"F0.wireOp",EDGE,"E7.43.4"),sQuery(id+"F0.wireOp",EDGE,"E7.43.5")])],"isStart":false})],"blendedInto":[makeQuery(id+"F1.opExtrude","CAP_FACE",FACE,{"disambiguationData":[OSD([sQuery(id+"F0.wireOp",EDGE,"E1"),sQuery(id+"F0.wireOp",EDGE,"E2"),sQuery(id+"F0.wireOp",EDGE,"E3"),sQuery(id+"F0.wireOp",EDGE,"E4"),sQuery(id+"F0.wireOp",EDGE,"E5"),sQuery(id+"F0.wireOp",EDGE,"E6"),sQuery(id+"F0.wireOp",EDGE,"E7.1.0"),sQuery(id+"F0.wireOp",EDGE,"E7.1.1"),sQuery(id+"F0.wireOp",EDGE,"E7.1.2"),sQuery(id+"F0.wireOp",EDGE,"E7.1.3"),sQuery(id+"F0.wireOp",EDGE,"E7.1.4"),sQuery(id+"F0.wireOp",EDGE,"E7.1.5"),sQuery(id+"F0.wireOp",EDGE,"E7.2.0"),sQuery(id+"F0.wireOp",EDGE,"E7.2.1"),sQuery(id+"F0.wireOp",EDGE,"E7.2.2"),sQuery(id+"F0.wireOp",EDGE,"E7.2.3"),sQuery(id+"F0.wireOp",EDGE,"E7.2.4"),sQuery(id+"F0.wireOp",EDGE,"E7.2.5"),sQuery(id+"F0.wireOp",EDGE,"E7.3.0"),sQuery(id+"F0.wireOp",EDGE,"E7.3.1"),sQuery(id+"F0.wireOp",EDGE,"E7.3.2"),sQuery(id+"F0.wireOp",EDGE,"E7.3.3"),sQuery(id+"F0.wireOp",EDGE,"E7.3.4"),sQuery(id+"F0.wireOp",EDGE,"E7.3.5"),sQuery(id+"F0.wireOp",EDGE,"E7.4.0"),sQuery(id+"F0.wireOp",EDGE,"E7.4.1"),sQuery(id+"F0.wireOp",EDGE,"E7.4.2"),sQuery(id+"F0.wireOp",EDGE,"E7.4.3"),sQuery(id+"F0.wireOp",EDGE,"E7.4.4"),sQuery(id+"F0.wireOp",EDGE,"E7.4.5"),sQuery(id+"F0.wireOp",EDGE,"E7.5.0"),sQuery(id+"F0.wireOp",EDGE,"E7.5.1"),sQuery(id+"F0.wireOp",EDGE,"E7.5.2"),sQuery(id+"F0.wireOp",EDGE,"E7.5.3"),sQuery(id+"F0.wireOp",EDGE,"E7.5.4"),sQuery(id+"F0.wireOp",EDGE,"E7.5.5"),sQuery(id+"F0.wireOp",EDGE,"E7.6.0"),sQuery(id+"F0.wireOp",EDGE,"E7.6.1"),sQuery(id+"F0.wireOp",EDGE,"E7.6.2"),sQuery(id+"F0.wireOp",EDGE,"E7.6.3"),sQuery(id+"F0.wireOp",EDGE,"E7.6.4"),sQuery(id+"F0.wireOp",EDGE,"E7.6.5"),sQuery(id+"F0.wireOp",EDGE,"E7.7.0"),sQuery(id+"F0.wireOp",EDGE,"E7.7.1"),sQuery(id+"F0.wireOp",EDGE,"E7.7.2"),sQuery(id+"F0.wireOp",EDGE,"E7.7.3"),sQuery(id+"F0.wireOp",EDGE,"E7.7.4"),sQuery(id+"F0.wireOp",EDGE,"E7.7.5"),sQuery(id+"F0.wireOp",EDGE,"E7.8.0"),sQuery(id+"F0.wireOp",EDGE,"E7.8.1"),sQuery(id+"F0.wireOp",EDGE,"E7.8.2"),sQuery(id+"F0.wireOp",EDGE,"E7.8.3"),sQuery(id+"F0.wireOp",EDGE,"E7.8.4"),sQuery(id+"F0.wireOp",EDGE,"E7.8.5"),sQuery(id+"F0.wireOp",EDGE,"E7.9.0"),sQuery(id+"F0.wireOp",EDGE,"E7.9.1"),sQuery(id+"F0.wireOp",EDGE,"E7.9.2"),sQuery(id+"F0.wireOp",EDGE,"E7.9.3"),sQuery(id+"F0.wireOp",EDGE,"E7.9.4"),sQuery(id+"F0.wireOp",EDGE,"E7.9.5"),sQuery(id+"F0.wireOp",EDGE,"E7.10.0"),sQuery(id+"F0.wireOp",EDGE,"E7.10.1"),sQuery(id+"F0.wireOp",EDGE,"E7.10.2"),sQuery(id+"F0.wireOp",EDGE,"E7.10.3"),sQuery(id+"F0.wireOp",EDGE,"E7.10.4"),sQuery(id+"F0.wireOp",EDGE,"E7.10.5"),subQ0,sQuery(id+"F0.wireOp",EDGE,"E7.11.1"),sQuery(id+"F0.wireOp",EDGE,"E7.11.2"),sQuery(id+"F0.wireOp",EDGE,"E7.11.3"),sQuery(id+"F0.wireOp",EDGE,"E7.11.4"),sQuery(id+"F0.wireOp",EDGE,"E7.11.5"),sQuery(id+"F0.wireOp",EDGE,"E7.12.0"),sQuery(id+"F0.wireOp",EDGE,"E7.12.1"),sQuery(id+"F0.wireOp",EDGE,"E7.12.2"),sQuery(id+"F0.wireOp",EDGE,"E7.12.3"),sQuery(id+"F0.wireOp",EDGE,"E7.12.4"),sQuery(id+"F0.wireOp",EDGE,"E7.12.5"),sQuery(id+"F0.wireOp",EDGE,"E7.13.0"),sQuery(id+"F0.wireOp",EDGE,"E7.13.1"),sQuery(id+"F0.wireOp",EDGE,"E7.13.2"),sQuery(id+"F0.wireOp",EDGE,"E7.13.3"),sQuery(id+"F0.wireOp",EDGE,"E7.13.4"),sQuery(id+"F0.wireOp",EDGE,"E7.13.5"),sQuery(id+"F0.wireOp",EDGE,"E7.14.0"),sQuery(id+"F0.wireOp",EDGE,"E7.14.1"),sQuery(id+"F0.wireOp",EDGE,"E7.14.2"),sQuery(id+"F0.wireOp",EDGE,"E7.14.3"),sQuery(id+"F0.wireOp",EDGE,"E7.14.4"),sQuery(id+"F0.wireOp",EDGE,"E7.14.5"),sQuery(id+"F0.wireOp",EDGE,"E7.15.0"),sQuery(id+"F0.wireOp",EDGE,"E7.15.1"),sQuery(id+"F0.wireOp",EDGE,"E7.15.2"),sQuery(id+"F0.wireOp",EDGE,"E7.15.3"),sQuery(id+"F0.wireOp",EDGE,"E7.15.4"),sQuery(id+"F0.wireOp",EDGE,"E7.15.5"),sQuery(id+"F0.wireOp",EDGE,"E7.16.0"),sQuery(id+"F0.wireOp",EDGE,"E7.16.1"),sQuery(id+"F0.wireOp",EDGE,"E7.16.2"),sQuery(id+"F0.wireOp",EDGE,"E7.16.3"),sQuery(id+"F0.wireOp",EDGE,"E7.16.4"),sQuery(id+"F0.wireOp",EDGE,"E7.16.5"),sQuery(id+"F0.wireOp",EDGE,"E7.17.0"),sQuery(id+"F0.wireOp",EDGE,"E7.17.1"),sQuery(id+"F0.wireOp",EDGE,"E7.17.2"),sQuery(id+"F0.wireOp",EDGE,"E7.17.3"),sQuery(id+"F0.wireOp",EDGE,"E7.17.4"),sQuery(id+"F0.wireOp",EDGE,"E7.17.5"),sQuery(id+"F0.wireOp",EDGE,"E7.18.0"),sQuery(id+"F0.wireOp",EDGE,"E7.18.1"),sQuery(id+"F0.wireOp",EDGE,"E7.18.2"),sQuery(id+"F0.wireOp",EDGE,"E7.18.3"),sQuery(id+"F0.wireOp",EDGE,"E7.18.4"),sQuery(id+"F0.wireOp",EDGE,"E7.18.5"),sQuery(id+"F0.wireOp",EDGE,"E7.19.0"),sQuery(id+"F0.wireOp",EDGE,"E7.19.1"),sQuery(id+"F0.wireOp",EDGE,"E7.19.2"),sQuery(id+"F0.wireOp",EDGE,"E7.19.3"),sQuery(id+"F0.wireOp",EDGE,"E7.19.4"),sQuery(id+"F0.wireOp",EDGE,"E7.19.5"),sQuery(id+"F0.wireOp",EDGE,"E7.20.0"),sQuery(id+"F0.wireOp",EDGE,"E7.20.1"),sQuery(id+"F0.wireOp",EDGE,"E7.20.2"),sQuery(id+"F0.wireOp",EDGE,"E7.20.3"),sQuery(id+"F0.wireOp",EDGE,"E7.20.4"),sQuery(id+"F0.wireOp",EDGE,"E7.20.5"),sQuery(id+"F0.wireOp",EDGE,"E7.21.0"),sQuery(id+"F0.wireOp",EDGE,"E7.21.1"),sQuery(id+"F0.wireOp",EDGE,"E7.21.2"),sQuery(id+"F0.wireOp",EDGE,"E7.21.3"),sQuery(id+"F0.wireOp",EDGE,"E7.21.4"),sQuery(id+"F0.wireOp",EDGE,"E7.21.5"),sQuery(id+"F0.wireOp",EDGE,"E7.22.0"),sQuery(id+"F0.wireOp",EDGE,"E7.22.1"),sQuery(id+"F0.wireOp",EDGE,"E7.22.2"),sQuery(id+"F0.wireOp",EDGE,"E7.22.3"),sQuery(id+"F0.wireOp",EDGE,"E7.22.4"),sQuery(id+"F0.wireOp",EDGE,"E7.22.5"),sQuery(id+"F0.wireOp",EDGE,"E7.23.0"),sQuery(id+"F0.wireOp",EDGE,"E7.23.1"),sQuery(id+"F0.wireOp",EDGE,"E7.23.2"),sQuery(id+"F0.wireOp",EDGE,"E7.23.3"),sQuery(id+"F0.wireOp",EDGE,"E7.23.4"),sQuery(id+"F0.wireOp",EDGE,"E7.23.5"),sQuery(id+"F0.wireOp",EDGE,"E7.24.0"),sQuery(id+"F0.wireOp",EDGE,"E7.24.1"),sQuery(id+"F0.wireOp",EDGE,"E7.24.2"),sQuery(id+"F0.wireOp",EDGE,"E7.24.3"),sQuery(id+"F0.wireOp",EDGE,"E7.24.4"),sQuery(id+"F0.wireOp",EDGE,"E7.24.5"),sQuery(id+"F0.wireOp",EDGE,"E7.25.0"),sQuery(id+"F0.wireOp",EDGE,"E7.25.1"),sQuery(id+"F0.wireOp",EDGE,"E7.25.2"),sQuery(id+"F0.wireOp",EDGE,"E7.25.3"),sQuery(id+"F0.wireOp",EDGE,"E7.25.4"),sQuery(id+"F0.wireOp",EDGE,"E7.25.5"),sQuery(id+"F0.wireOp",EDGE,"E7.26.0"),sQuery(id+"F0.wireOp",EDGE,"E7.26.1"),sQuery(id+"F0.wireOp",EDGE,"E7.26.2"),sQuery(id+"F0.wireOp",EDGE,"E7.26.3"),sQuery(id+"F0.wireOp",EDGE,"E7.26.4"),sQuery(id+"F0.wireOp",EDGE,"E7.26.5"),sQuery(id+"F0.wireOp",EDGE,"E7.27.0"),sQuery(id+"F0.wireOp",EDGE,"E7.27.1"),sQuery(id+"F0.wireOp",EDGE,"E7.27.2"),sQuery(id+"F0.wireOp",EDGE,"E7.27.3"),sQuery(id+"F0.wireOp",EDGE,"E7.27.4"),sQuery(id+"F0.wireOp",EDGE,"E7.27.5"),sQuery(id+"F0.wireOp",EDGE,"E7.28.0"),sQuery(id+"F0.wireOp",EDGE,"E7.28.1"),sQuery(id+"F0.wireOp",EDGE,"E7.28.2"),sQuery(id+"F0.wireOp",EDGE,"E7.28.3"),sQuery(id+"F0.wireOp",EDGE,"E7.28.4"),sQuery(id+"F0.wireOp",EDGE,"E7.28.5"),sQuery(id+"F0.wireOp",EDGE,"E7.29.0"),sQuery(id+"F0.wireOp",EDGE,"E7.29.1"),sQuery(id+"F0.wireOp",EDGE,"E7.29.2"),sQuery(id+"F0.wireOp",EDGE,"E7.29.3"),sQuery(id+"F0.wireOp",EDGE,"E7.29.4"),sQuery(id+"F0.wireOp",EDGE,"E7.29.5"),sQuery(id+"F0.wireOp",EDGE,"E7.30.0"),sQuery(id+"F0.wireOp",EDGE,"E7.30.1"),sQuery(id+"F0.wireOp",EDGE,"E7.30.2"),sQuery(id+"F0.wireOp",EDGE,"E7.30.3"),sQuery(id+"F0.wireOp",EDGE,"E7.30.4"),sQuery(id+"F0.wireOp",EDGE,"E7.30.5"),sQuery(id+"F0.wireOp",EDGE,"E7.31.0"),sQuery(id+"F0.wireOp",EDGE,"E7.31.1"),sQuery(id+"F0.wireOp",EDGE,"E7.31.2"),sQuery(id+"F0.wireOp",EDGE,"E7.31.3"),sQuery(id+"F0.wireOp",EDGE,"E7.31.4"),sQuery(id+"F0.wireOp",EDGE,"E7.31.5"),sQuery(id+"F0.wireOp",EDGE,"E7.32.0"),sQuery(id+"F0.wireOp",EDGE,"E7.32.1"),sQuery(id+"F0.wireOp",EDGE,"E7.32.2"),sQuery(id+"F0.wireOp",EDGE,"E7.32.3"),sQuery(id+"F0.wireOp",EDGE,"E7.32.4"),sQuery(id+"F0.wireOp",EDGE,"E7.32.5"),sQuery(id+"F0.wireOp",EDGE,"E7.33.0"),sQuery(id+"F0.wireOp",EDGE,"E7.33.1"),sQuery(id+"F0.wireOp",EDGE,"E7.33.2"),sQuery(id+"F0.wireOp",EDGE,"E7.33.3"),sQuery(id+"F0.wireOp",EDGE,"E7.33.4"),sQuery(id+"F0.wireOp",EDGE,"E7.33.5"),sQuery(id+"F0.wireOp",EDGE,"E7.34.0"),sQuery(id+"F0.wireOp",EDGE,"E7.34.1"),sQuery(id+"F0.wireOp",EDGE,"E7.34.2"),sQuery(id+"F0.wireOp",EDGE,"E7.34.3"),sQuery(id+"F0.wireOp",EDGE,"E7.34.4"),sQuery(id+"F0.wireOp",EDGE,"E7.34.5"),sQuery(id+"F0.wireOp",EDGE,"E7.35.0"),sQuery(id+"F0.wireOp",EDGE,"E7.35.1"),sQuery(id+"F0.wireOp",EDGE,"E7.35.2"),sQuery(id+"F0.wireOp",EDGE,"E7.35.3"),sQuery(id+"F0.wireOp",EDGE,"E7.35.4"),sQuery(id+"F0.wireOp",EDGE,"E7.35.5"),sQuery(id+"F0.wireOp",EDGE,"E7.36.0"),sQuery(id+"F0.wireOp",EDGE,"E7.36.1"),sQuery(id+"F0.wireOp",EDGE,"E7.36.2"),sQuery(id+"F0.wireOp",EDGE,"E7.36.3"),sQuery(id+"F0.wireOp",EDGE,"E7.36.4"),sQuery(id+"F0.wireOp",EDGE,"E7.36.5"),sQuery(id+"F0.wireOp",EDGE,"E7.37.0"),sQuery(id+"F0.wireOp",EDGE,"E7.37.1"),sQuery(id+"F0.wireOp",EDGE,"E7.37.2"),sQuery(id+"F0.wireOp",EDGE,"E7.37.3"),sQuery(id+"F0.wireOp",EDGE,"E7.37.4"),sQuery(id+"F0.wireOp",EDGE,"E7.37.5"),sQuery(id+"F0.wireOp",EDGE,"E7.38.0"),sQuery(id+"F0.wireOp",EDGE,"E7.38.1"),sQuery(id+"F0.wireOp",EDGE,"E7.38.2"),sQuery(id+"F0.wireOp",EDGE,"E7.38.3"),sQuery(id+"F0.wireOp",EDGE,"E7.38.4"),sQuery(id+"F0.wireOp",EDGE,"E7.38.5"),sQuery(id+"F0.wireOp",EDGE,"E7.39.0"),sQuery(id+"F0.wireOp",EDGE,"E7.39.1"),sQuery(id+"F0.wireOp",EDGE,"E7.39.2"),sQuery(id+"F0.wireOp",EDGE,"E7.39.3"),sQuery(id+"F0.wireOp",EDGE,"E7.39.4"),sQuery(id+"F0.wireOp",EDGE,"E7.39.5"),sQuery(id+"F0.wireOp",EDGE,"E7.40.0"),sQuery(id+"F0.wireOp",EDGE,"E7.40.1"),sQuery(id+"F0.wireOp",EDGE,"E7.40.2"),sQuery(id+"F0.wireOp",EDGE,"E7.40.3"),sQuery(id+"F0.wireOp",EDGE,"E7.40.4"),sQuery(id+"F0.wireOp",EDGE,"E7.40.5"),sQuery(id+"F0.wireOp",EDGE,"E7.41.0"),sQuery(id+"F0.wireOp",EDGE,"E7.41.1"),sQuery(id+"F0.wireOp",EDGE,"E7.41.2"),sQuery(id+"F0.wireOp",EDGE,"E7.41.3"),sQuery(id+"F0.wireOp",EDGE,"E7.41.4"),sQuery(id+"F0.wireOp",EDGE,"E7.41.5"),sQuery(id+"F0.wireOp",EDGE,"E7.42.0"),sQuery(id+"F0.wireOp",EDGE,"E7.42.1"),sQuery(id+"F0.wireOp",EDGE,"E7.42.2"),sQuery(id+"F0.wireOp",EDGE,"E7.42.3"),sQuery(id+"F0.wireOp",EDGE,"E7.42.4"),sQuery(id+"F0.wireOp",EDGE,"E7.42.5"),sQuery(id+"F0.wireOp",EDGE,"E7.43.0"),sQuery(id+"F0.wireOp",EDGE,"E7.43.1"),sQuery(id+"F0.wireOp",EDGE,"E7.43.2"),sQuery(id+"F0.wireOp",EDGE,"E7.43.3"),sQuery(id+"F0.wireOp",EDGE,"E7.43.4"),sQuery(id+"F0.wireOp",EDGE,"E7.43.5")])],"isStart":false})]});}
            var Q17;
            {var subQ0=sQuery(id+"F0.wireOp",EDGE,"E7.9.0");Q17=makeQuery(id+"F2.opChamfer","BLEND_EDGE",EDGE,{"blendedFrom":[makeQuery(id+"F1.opExtrude","CAP_EDGE",EDGE,{"disambiguationData":[OSD([subQ0])],"isStart":false}),makeQuery(id+"F1.opExtrude","CAP_FACE",FACE,{"disambiguationData":[OSD([sQuery(id+"F0.wireOp",EDGE,"E1"),sQuery(id+"F0.wireOp",EDGE,"E2"),sQuery(id+"F0.wireOp",EDGE,"E3"),sQuery(id+"F0.wireOp",EDGE,"E4"),sQuery(id+"F0.wireOp",EDGE,"E5"),sQuery(id+"F0.wireOp",EDGE,"E6"),sQuery(id+"F0.wireOp",EDGE,"E7.1.0"),sQuery(id+"F0.wireOp",EDGE,"E7.1.1"),sQuery(id+"F0.wireOp",EDGE,"E7.1.2"),sQuery(id+"F0.wireOp",EDGE,"E7.1.3"),sQuery(id+"F0.wireOp",EDGE,"E7.1.4"),sQuery(id+"F0.wireOp",EDGE,"E7.1.5"),sQuery(id+"F0.wireOp",EDGE,"E7.2.0"),sQuery(id+"F0.wireOp",EDGE,"E7.2.1"),sQuery(id+"F0.wireOp",EDGE,"E7.2.2"),sQuery(id+"F0.wireOp",EDGE,"E7.2.3"),sQuery(id+"F0.wireOp",EDGE,"E7.2.4"),sQuery(id+"F0.wireOp",EDGE,"E7.2.5"),sQuery(id+"F0.wireOp",EDGE,"E7.3.0"),sQuery(id+"F0.wireOp",EDGE,"E7.3.1"),sQuery(id+"F0.wireOp",EDGE,"E7.3.2"),sQuery(id+"F0.wireOp",EDGE,"E7.3.3"),sQuery(id+"F0.wireOp",EDGE,"E7.3.4"),sQuery(id+"F0.wireOp",EDGE,"E7.3.5"),sQuery(id+"F0.wireOp",EDGE,"E7.4.0"),sQuery(id+"F0.wireOp",EDGE,"E7.4.1"),sQuery(id+"F0.wireOp",EDGE,"E7.4.2"),sQuery(id+"F0.wireOp",EDGE,"E7.4.3"),sQuery(id+"F0.wireOp",EDGE,"E7.4.4"),sQuery(id+"F0.wireOp",EDGE,"E7.4.5"),sQuery(id+"F0.wireOp",EDGE,"E7.5.0"),sQuery(id+"F0.wireOp",EDGE,"E7.5.1"),sQuery(id+"F0.wireOp",EDGE,"E7.5.2"),sQuery(id+"F0.wireOp",EDGE,"E7.5.3"),sQuery(id+"F0.wireOp",EDGE,"E7.5.4"),sQuery(id+"F0.wireOp",EDGE,"E7.5.5"),sQuery(id+"F0.wireOp",EDGE,"E7.6.0"),sQuery(id+"F0.wireOp",EDGE,"E7.6.1"),sQuery(id+"F0.wireOp",EDGE,"E7.6.2"),sQuery(id+"F0.wireOp",EDGE,"E7.6.3"),sQuery(id+"F0.wireOp",EDGE,"E7.6.4"),sQuery(id+"F0.wireOp",EDGE,"E7.6.5"),sQuery(id+"F0.wireOp",EDGE,"E7.7.0"),sQuery(id+"F0.wireOp",EDGE,"E7.7.1"),sQuery(id+"F0.wireOp",EDGE,"E7.7.2"),sQuery(id+"F0.wireOp",EDGE,"E7.7.3"),sQuery(id+"F0.wireOp",EDGE,"E7.7.4"),sQuery(id+"F0.wireOp",EDGE,"E7.7.5"),sQuery(id+"F0.wireOp",EDGE,"E7.8.0"),sQuery(id+"F0.wireOp",EDGE,"E7.8.1"),sQuery(id+"F0.wireOp",EDGE,"E7.8.2"),sQuery(id+"F0.wireOp",EDGE,"E7.8.3"),sQuery(id+"F0.wireOp",EDGE,"E7.8.4"),sQuery(id+"F0.wireOp",EDGE,"E7.8.5"),subQ0,sQuery(id+"F0.wireOp",EDGE,"E7.9.1"),sQuery(id+"F0.wireOp",EDGE,"E7.9.2"),sQuery(id+"F0.wireOp",EDGE,"E7.9.3"),sQuery(id+"F0.wireOp",EDGE,"E7.9.4"),sQuery(id+"F0.wireOp",EDGE,"E7.9.5"),sQuery(id+"F0.wireOp",EDGE,"E7.10.0"),sQuery(id+"F0.wireOp",EDGE,"E7.10.1"),sQuery(id+"F0.wireOp",EDGE,"E7.10.2"),sQuery(id+"F0.wireOp",EDGE,"E7.10.3"),sQuery(id+"F0.wireOp",EDGE,"E7.10.4"),sQuery(id+"F0.wireOp",EDGE,"E7.10.5"),sQuery(id+"F0.wireOp",EDGE,"E7.11.0"),sQuery(id+"F0.wireOp",EDGE,"E7.11.1"),sQuery(id+"F0.wireOp",EDGE,"E7.11.2"),sQuery(id+"F0.wireOp",EDGE,"E7.11.3"),sQuery(id+"F0.wireOp",EDGE,"E7.11.4"),sQuery(id+"F0.wireOp",EDGE,"E7.11.5"),sQuery(id+"F0.wireOp",EDGE,"E7.12.0"),sQuery(id+"F0.wireOp",EDGE,"E7.12.1"),sQuery(id+"F0.wireOp",EDGE,"E7.12.2"),sQuery(id+"F0.wireOp",EDGE,"E7.12.3"),sQuery(id+"F0.wireOp",EDGE,"E7.12.4"),sQuery(id+"F0.wireOp",EDGE,"E7.12.5"),sQuery(id+"F0.wireOp",EDGE,"E7.13.0"),sQuery(id+"F0.wireOp",EDGE,"E7.13.1"),sQuery(id+"F0.wireOp",EDGE,"E7.13.2"),sQuery(id+"F0.wireOp",EDGE,"E7.13.3"),sQuery(id+"F0.wireOp",EDGE,"E7.13.4"),sQuery(id+"F0.wireOp",EDGE,"E7.13.5"),sQuery(id+"F0.wireOp",EDGE,"E7.14.0"),sQuery(id+"F0.wireOp",EDGE,"E7.14.1"),sQuery(id+"F0.wireOp",EDGE,"E7.14.2"),sQuery(id+"F0.wireOp",EDGE,"E7.14.3"),sQuery(id+"F0.wireOp",EDGE,"E7.14.4"),sQuery(id+"F0.wireOp",EDGE,"E7.14.5"),sQuery(id+"F0.wireOp",EDGE,"E7.15.0"),sQuery(id+"F0.wireOp",EDGE,"E7.15.1"),sQuery(id+"F0.wireOp",EDGE,"E7.15.2"),sQuery(id+"F0.wireOp",EDGE,"E7.15.3"),sQuery(id+"F0.wireOp",EDGE,"E7.15.4"),sQuery(id+"F0.wireOp",EDGE,"E7.15.5"),sQuery(id+"F0.wireOp",EDGE,"E7.16.0"),sQuery(id+"F0.wireOp",EDGE,"E7.16.1"),sQuery(id+"F0.wireOp",EDGE,"E7.16.2"),sQuery(id+"F0.wireOp",EDGE,"E7.16.3"),sQuery(id+"F0.wireOp",EDGE,"E7.16.4"),sQuery(id+"F0.wireOp",EDGE,"E7.16.5"),sQuery(id+"F0.wireOp",EDGE,"E7.17.0"),sQuery(id+"F0.wireOp",EDGE,"E7.17.1"),sQuery(id+"F0.wireOp",EDGE,"E7.17.2"),sQuery(id+"F0.wireOp",EDGE,"E7.17.3"),sQuery(id+"F0.wireOp",EDGE,"E7.17.4"),sQuery(id+"F0.wireOp",EDGE,"E7.17.5"),sQuery(id+"F0.wireOp",EDGE,"E7.18.0"),sQuery(id+"F0.wireOp",EDGE,"E7.18.1"),sQuery(id+"F0.wireOp",EDGE,"E7.18.2"),sQuery(id+"F0.wireOp",EDGE,"E7.18.3"),sQuery(id+"F0.wireOp",EDGE,"E7.18.4"),sQuery(id+"F0.wireOp",EDGE,"E7.18.5"),sQuery(id+"F0.wireOp",EDGE,"E7.19.0"),sQuery(id+"F0.wireOp",EDGE,"E7.19.1"),sQuery(id+"F0.wireOp",EDGE,"E7.19.2"),sQuery(id+"F0.wireOp",EDGE,"E7.19.3"),sQuery(id+"F0.wireOp",EDGE,"E7.19.4"),sQuery(id+"F0.wireOp",EDGE,"E7.19.5"),sQuery(id+"F0.wireOp",EDGE,"E7.20.0"),sQuery(id+"F0.wireOp",EDGE,"E7.20.1"),sQuery(id+"F0.wireOp",EDGE,"E7.20.2"),sQuery(id+"F0.wireOp",EDGE,"E7.20.3"),sQuery(id+"F0.wireOp",EDGE,"E7.20.4"),sQuery(id+"F0.wireOp",EDGE,"E7.20.5"),sQuery(id+"F0.wireOp",EDGE,"E7.21.0"),sQuery(id+"F0.wireOp",EDGE,"E7.21.1"),sQuery(id+"F0.wireOp",EDGE,"E7.21.2"),sQuery(id+"F0.wireOp",EDGE,"E7.21.3"),sQuery(id+"F0.wireOp",EDGE,"E7.21.4"),sQuery(id+"F0.wireOp",EDGE,"E7.21.5"),sQuery(id+"F0.wireOp",EDGE,"E7.22.0"),sQuery(id+"F0.wireOp",EDGE,"E7.22.1"),sQuery(id+"F0.wireOp",EDGE,"E7.22.2"),sQuery(id+"F0.wireOp",EDGE,"E7.22.3"),sQuery(id+"F0.wireOp",EDGE,"E7.22.4"),sQuery(id+"F0.wireOp",EDGE,"E7.22.5"),sQuery(id+"F0.wireOp",EDGE,"E7.23.0"),sQuery(id+"F0.wireOp",EDGE,"E7.23.1"),sQuery(id+"F0.wireOp",EDGE,"E7.23.2"),sQuery(id+"F0.wireOp",EDGE,"E7.23.3"),sQuery(id+"F0.wireOp",EDGE,"E7.23.4"),sQuery(id+"F0.wireOp",EDGE,"E7.23.5"),sQuery(id+"F0.wireOp",EDGE,"E7.24.0"),sQuery(id+"F0.wireOp",EDGE,"E7.24.1"),sQuery(id+"F0.wireOp",EDGE,"E7.24.2"),sQuery(id+"F0.wireOp",EDGE,"E7.24.3"),sQuery(id+"F0.wireOp",EDGE,"E7.24.4"),sQuery(id+"F0.wireOp",EDGE,"E7.24.5"),sQuery(id+"F0.wireOp",EDGE,"E7.25.0"),sQuery(id+"F0.wireOp",EDGE,"E7.25.1"),sQuery(id+"F0.wireOp",EDGE,"E7.25.2"),sQuery(id+"F0.wireOp",EDGE,"E7.25.3"),sQuery(id+"F0.wireOp",EDGE,"E7.25.4"),sQuery(id+"F0.wireOp",EDGE,"E7.25.5"),sQuery(id+"F0.wireOp",EDGE,"E7.26.0"),sQuery(id+"F0.wireOp",EDGE,"E7.26.1"),sQuery(id+"F0.wireOp",EDGE,"E7.26.2"),sQuery(id+"F0.wireOp",EDGE,"E7.26.3"),sQuery(id+"F0.wireOp",EDGE,"E7.26.4"),sQuery(id+"F0.wireOp",EDGE,"E7.26.5"),sQuery(id+"F0.wireOp",EDGE,"E7.27.0"),sQuery(id+"F0.wireOp",EDGE,"E7.27.1"),sQuery(id+"F0.wireOp",EDGE,"E7.27.2"),sQuery(id+"F0.wireOp",EDGE,"E7.27.3"),sQuery(id+"F0.wireOp",EDGE,"E7.27.4"),sQuery(id+"F0.wireOp",EDGE,"E7.27.5"),sQuery(id+"F0.wireOp",EDGE,"E7.28.0"),sQuery(id+"F0.wireOp",EDGE,"E7.28.1"),sQuery(id+"F0.wireOp",EDGE,"E7.28.2"),sQuery(id+"F0.wireOp",EDGE,"E7.28.3"),sQuery(id+"F0.wireOp",EDGE,"E7.28.4"),sQuery(id+"F0.wireOp",EDGE,"E7.28.5"),sQuery(id+"F0.wireOp",EDGE,"E7.29.0"),sQuery(id+"F0.wireOp",EDGE,"E7.29.1"),sQuery(id+"F0.wireOp",EDGE,"E7.29.2"),sQuery(id+"F0.wireOp",EDGE,"E7.29.3"),sQuery(id+"F0.wireOp",EDGE,"E7.29.4"),sQuery(id+"F0.wireOp",EDGE,"E7.29.5"),sQuery(id+"F0.wireOp",EDGE,"E7.30.0"),sQuery(id+"F0.wireOp",EDGE,"E7.30.1"),sQuery(id+"F0.wireOp",EDGE,"E7.30.2"),sQuery(id+"F0.wireOp",EDGE,"E7.30.3"),sQuery(id+"F0.wireOp",EDGE,"E7.30.4"),sQuery(id+"F0.wireOp",EDGE,"E7.30.5"),sQuery(id+"F0.wireOp",EDGE,"E7.31.0"),sQuery(id+"F0.wireOp",EDGE,"E7.31.1"),sQuery(id+"F0.wireOp",EDGE,"E7.31.2"),sQuery(id+"F0.wireOp",EDGE,"E7.31.3"),sQuery(id+"F0.wireOp",EDGE,"E7.31.4"),sQuery(id+"F0.wireOp",EDGE,"E7.31.5"),sQuery(id+"F0.wireOp",EDGE,"E7.32.0"),sQuery(id+"F0.wireOp",EDGE,"E7.32.1"),sQuery(id+"F0.wireOp",EDGE,"E7.32.2"),sQuery(id+"F0.wireOp",EDGE,"E7.32.3"),sQuery(id+"F0.wireOp",EDGE,"E7.32.4"),sQuery(id+"F0.wireOp",EDGE,"E7.32.5"),sQuery(id+"F0.wireOp",EDGE,"E7.33.0"),sQuery(id+"F0.wireOp",EDGE,"E7.33.1"),sQuery(id+"F0.wireOp",EDGE,"E7.33.2"),sQuery(id+"F0.wireOp",EDGE,"E7.33.3"),sQuery(id+"F0.wireOp",EDGE,"E7.33.4"),sQuery(id+"F0.wireOp",EDGE,"E7.33.5"),sQuery(id+"F0.wireOp",EDGE,"E7.34.0"),sQuery(id+"F0.wireOp",EDGE,"E7.34.1"),sQuery(id+"F0.wireOp",EDGE,"E7.34.2"),sQuery(id+"F0.wireOp",EDGE,"E7.34.3"),sQuery(id+"F0.wireOp",EDGE,"E7.34.4"),sQuery(id+"F0.wireOp",EDGE,"E7.34.5"),sQuery(id+"F0.wireOp",EDGE,"E7.35.0"),sQuery(id+"F0.wireOp",EDGE,"E7.35.1"),sQuery(id+"F0.wireOp",EDGE,"E7.35.2"),sQuery(id+"F0.wireOp",EDGE,"E7.35.3"),sQuery(id+"F0.wireOp",EDGE,"E7.35.4"),sQuery(id+"F0.wireOp",EDGE,"E7.35.5"),sQuery(id+"F0.wireOp",EDGE,"E7.36.0"),sQuery(id+"F0.wireOp",EDGE,"E7.36.1"),sQuery(id+"F0.wireOp",EDGE,"E7.36.2"),sQuery(id+"F0.wireOp",EDGE,"E7.36.3"),sQuery(id+"F0.wireOp",EDGE,"E7.36.4"),sQuery(id+"F0.wireOp",EDGE,"E7.36.5"),sQuery(id+"F0.wireOp",EDGE,"E7.37.0"),sQuery(id+"F0.wireOp",EDGE,"E7.37.1"),sQuery(id+"F0.wireOp",EDGE,"E7.37.2"),sQuery(id+"F0.wireOp",EDGE,"E7.37.3"),sQuery(id+"F0.wireOp",EDGE,"E7.37.4"),sQuery(id+"F0.wireOp",EDGE,"E7.37.5"),sQuery(id+"F0.wireOp",EDGE,"E7.38.0"),sQuery(id+"F0.wireOp",EDGE,"E7.38.1"),sQuery(id+"F0.wireOp",EDGE,"E7.38.2"),sQuery(id+"F0.wireOp",EDGE,"E7.38.3"),sQuery(id+"F0.wireOp",EDGE,"E7.38.4"),sQuery(id+"F0.wireOp",EDGE,"E7.38.5"),sQuery(id+"F0.wireOp",EDGE,"E7.39.0"),sQuery(id+"F0.wireOp",EDGE,"E7.39.1"),sQuery(id+"F0.wireOp",EDGE,"E7.39.2"),sQuery(id+"F0.wireOp",EDGE,"E7.39.3"),sQuery(id+"F0.wireOp",EDGE,"E7.39.4"),sQuery(id+"F0.wireOp",EDGE,"E7.39.5"),sQuery(id+"F0.wireOp",EDGE,"E7.40.0"),sQuery(id+"F0.wireOp",EDGE,"E7.40.1"),sQuery(id+"F0.wireOp",EDGE,"E7.40.2"),sQuery(id+"F0.wireOp",EDGE,"E7.40.3"),sQuery(id+"F0.wireOp",EDGE,"E7.40.4"),sQuery(id+"F0.wireOp",EDGE,"E7.40.5"),sQuery(id+"F0.wireOp",EDGE,"E7.41.0"),sQuery(id+"F0.wireOp",EDGE,"E7.41.1"),sQuery(id+"F0.wireOp",EDGE,"E7.41.2"),sQuery(id+"F0.wireOp",EDGE,"E7.41.3"),sQuery(id+"F0.wireOp",EDGE,"E7.41.4"),sQuery(id+"F0.wireOp",EDGE,"E7.41.5"),sQuery(id+"F0.wireOp",EDGE,"E7.42.0"),sQuery(id+"F0.wireOp",EDGE,"E7.42.1"),sQuery(id+"F0.wireOp",EDGE,"E7.42.2"),sQuery(id+"F0.wireOp",EDGE,"E7.42.3"),sQuery(id+"F0.wireOp",EDGE,"E7.42.4"),sQuery(id+"F0.wireOp",EDGE,"E7.42.5"),sQuery(id+"F0.wireOp",EDGE,"E7.43.0"),sQuery(id+"F0.wireOp",EDGE,"E7.43.1"),sQuery(id+"F0.wireOp",EDGE,"E7.43.2"),sQuery(id+"F0.wireOp",EDGE,"E7.43.3"),sQuery(id+"F0.wireOp",EDGE,"E7.43.4"),sQuery(id+"F0.wireOp",EDGE,"E7.43.5")])],"isStart":false})],"blendedInto":[makeQuery(id+"F1.opExtrude","CAP_FACE",FACE,{"disambiguationData":[OSD([sQuery(id+"F0.wireOp",EDGE,"E1"),sQuery(id+"F0.wireOp",EDGE,"E2"),sQuery(id+"F0.wireOp",EDGE,"E3"),sQuery(id+"F0.wireOp",EDGE,"E4"),sQuery(id+"F0.wireOp",EDGE,"E5"),sQuery(id+"F0.wireOp",EDGE,"E6"),sQuery(id+"F0.wireOp",EDGE,"E7.1.0"),sQuery(id+"F0.wireOp",EDGE,"E7.1.1"),sQuery(id+"F0.wireOp",EDGE,"E7.1.2"),sQuery(id+"F0.wireOp",EDGE,"E7.1.3"),sQuery(id+"F0.wireOp",EDGE,"E7.1.4"),sQuery(id+"F0.wireOp",EDGE,"E7.1.5"),sQuery(id+"F0.wireOp",EDGE,"E7.2.0"),sQuery(id+"F0.wireOp",EDGE,"E7.2.1"),sQuery(id+"F0.wireOp",EDGE,"E7.2.2"),sQuery(id+"F0.wireOp",EDGE,"E7.2.3"),sQuery(id+"F0.wireOp",EDGE,"E7.2.4"),sQuery(id+"F0.wireOp",EDGE,"E7.2.5"),sQuery(id+"F0.wireOp",EDGE,"E7.3.0"),sQuery(id+"F0.wireOp",EDGE,"E7.3.1"),sQuery(id+"F0.wireOp",EDGE,"E7.3.2"),sQuery(id+"F0.wireOp",EDGE,"E7.3.3"),sQuery(id+"F0.wireOp",EDGE,"E7.3.4"),sQuery(id+"F0.wireOp",EDGE,"E7.3.5"),sQuery(id+"F0.wireOp",EDGE,"E7.4.0"),sQuery(id+"F0.wireOp",EDGE,"E7.4.1"),sQuery(id+"F0.wireOp",EDGE,"E7.4.2"),sQuery(id+"F0.wireOp",EDGE,"E7.4.3"),sQuery(id+"F0.wireOp",EDGE,"E7.4.4"),sQuery(id+"F0.wireOp",EDGE,"E7.4.5"),sQuery(id+"F0.wireOp",EDGE,"E7.5.0"),sQuery(id+"F0.wireOp",EDGE,"E7.5.1"),sQuery(id+"F0.wireOp",EDGE,"E7.5.2"),sQuery(id+"F0.wireOp",EDGE,"E7.5.3"),sQuery(id+"F0.wireOp",EDGE,"E7.5.4"),sQuery(id+"F0.wireOp",EDGE,"E7.5.5"),sQuery(id+"F0.wireOp",EDGE,"E7.6.0"),sQuery(id+"F0.wireOp",EDGE,"E7.6.1"),sQuery(id+"F0.wireOp",EDGE,"E7.6.2"),sQuery(id+"F0.wireOp",EDGE,"E7.6.3"),sQuery(id+"F0.wireOp",EDGE,"E7.6.4"),sQuery(id+"F0.wireOp",EDGE,"E7.6.5"),sQuery(id+"F0.wireOp",EDGE,"E7.7.0"),sQuery(id+"F0.wireOp",EDGE,"E7.7.1"),sQuery(id+"F0.wireOp",EDGE,"E7.7.2"),sQuery(id+"F0.wireOp",EDGE,"E7.7.3"),sQuery(id+"F0.wireOp",EDGE,"E7.7.4"),sQuery(id+"F0.wireOp",EDGE,"E7.7.5"),sQuery(id+"F0.wireOp",EDGE,"E7.8.0"),sQuery(id+"F0.wireOp",EDGE,"E7.8.1"),sQuery(id+"F0.wireOp",EDGE,"E7.8.2"),sQuery(id+"F0.wireOp",EDGE,"E7.8.3"),sQuery(id+"F0.wireOp",EDGE,"E7.8.4"),sQuery(id+"F0.wireOp",EDGE,"E7.8.5"),subQ0,sQuery(id+"F0.wireOp",EDGE,"E7.9.1"),sQuery(id+"F0.wireOp",EDGE,"E7.9.2"),sQuery(id+"F0.wireOp",EDGE,"E7.9.3"),sQuery(id+"F0.wireOp",EDGE,"E7.9.4"),sQuery(id+"F0.wireOp",EDGE,"E7.9.5"),sQuery(id+"F0.wireOp",EDGE,"E7.10.0"),sQuery(id+"F0.wireOp",EDGE,"E7.10.1"),sQuery(id+"F0.wireOp",EDGE,"E7.10.2"),sQuery(id+"F0.wireOp",EDGE,"E7.10.3"),sQuery(id+"F0.wireOp",EDGE,"E7.10.4"),sQuery(id+"F0.wireOp",EDGE,"E7.10.5"),sQuery(id+"F0.wireOp",EDGE,"E7.11.0"),sQuery(id+"F0.wireOp",EDGE,"E7.11.1"),sQuery(id+"F0.wireOp",EDGE,"E7.11.2"),sQuery(id+"F0.wireOp",EDGE,"E7.11.3"),sQuery(id+"F0.wireOp",EDGE,"E7.11.4"),sQuery(id+"F0.wireOp",EDGE,"E7.11.5"),sQuery(id+"F0.wireOp",EDGE,"E7.12.0"),sQuery(id+"F0.wireOp",EDGE,"E7.12.1"),sQuery(id+"F0.wireOp",EDGE,"E7.12.2"),sQuery(id+"F0.wireOp",EDGE,"E7.12.3"),sQuery(id+"F0.wireOp",EDGE,"E7.12.4"),sQuery(id+"F0.wireOp",EDGE,"E7.12.5"),sQuery(id+"F0.wireOp",EDGE,"E7.13.0"),sQuery(id+"F0.wireOp",EDGE,"E7.13.1"),sQuery(id+"F0.wireOp",EDGE,"E7.13.2"),sQuery(id+"F0.wireOp",EDGE,"E7.13.3"),sQuery(id+"F0.wireOp",EDGE,"E7.13.4"),sQuery(id+"F0.wireOp",EDGE,"E7.13.5"),sQuery(id+"F0.wireOp",EDGE,"E7.14.0"),sQuery(id+"F0.wireOp",EDGE,"E7.14.1"),sQuery(id+"F0.wireOp",EDGE,"E7.14.2"),sQuery(id+"F0.wireOp",EDGE,"E7.14.3"),sQuery(id+"F0.wireOp",EDGE,"E7.14.4"),sQuery(id+"F0.wireOp",EDGE,"E7.14.5"),sQuery(id+"F0.wireOp",EDGE,"E7.15.0"),sQuery(id+"F0.wireOp",EDGE,"E7.15.1"),sQuery(id+"F0.wireOp",EDGE,"E7.15.2"),sQuery(id+"F0.wireOp",EDGE,"E7.15.3"),sQuery(id+"F0.wireOp",EDGE,"E7.15.4"),sQuery(id+"F0.wireOp",EDGE,"E7.15.5"),sQuery(id+"F0.wireOp",EDGE,"E7.16.0"),sQuery(id+"F0.wireOp",EDGE,"E7.16.1"),sQuery(id+"F0.wireOp",EDGE,"E7.16.2"),sQuery(id+"F0.wireOp",EDGE,"E7.16.3"),sQuery(id+"F0.wireOp",EDGE,"E7.16.4"),sQuery(id+"F0.wireOp",EDGE,"E7.16.5"),sQuery(id+"F0.wireOp",EDGE,"E7.17.0"),sQuery(id+"F0.wireOp",EDGE,"E7.17.1"),sQuery(id+"F0.wireOp",EDGE,"E7.17.2"),sQuery(id+"F0.wireOp",EDGE,"E7.17.3"),sQuery(id+"F0.wireOp",EDGE,"E7.17.4"),sQuery(id+"F0.wireOp",EDGE,"E7.17.5"),sQuery(id+"F0.wireOp",EDGE,"E7.18.0"),sQuery(id+"F0.wireOp",EDGE,"E7.18.1"),sQuery(id+"F0.wireOp",EDGE,"E7.18.2"),sQuery(id+"F0.wireOp",EDGE,"E7.18.3"),sQuery(id+"F0.wireOp",EDGE,"E7.18.4"),sQuery(id+"F0.wireOp",EDGE,"E7.18.5"),sQuery(id+"F0.wireOp",EDGE,"E7.19.0"),sQuery(id+"F0.wireOp",EDGE,"E7.19.1"),sQuery(id+"F0.wireOp",EDGE,"E7.19.2"),sQuery(id+"F0.wireOp",EDGE,"E7.19.3"),sQuery(id+"F0.wireOp",EDGE,"E7.19.4"),sQuery(id+"F0.wireOp",EDGE,"E7.19.5"),sQuery(id+"F0.wireOp",EDGE,"E7.20.0"),sQuery(id+"F0.wireOp",EDGE,"E7.20.1"),sQuery(id+"F0.wireOp",EDGE,"E7.20.2"),sQuery(id+"F0.wireOp",EDGE,"E7.20.3"),sQuery(id+"F0.wireOp",EDGE,"E7.20.4"),sQuery(id+"F0.wireOp",EDGE,"E7.20.5"),sQuery(id+"F0.wireOp",EDGE,"E7.21.0"),sQuery(id+"F0.wireOp",EDGE,"E7.21.1"),sQuery(id+"F0.wireOp",EDGE,"E7.21.2"),sQuery(id+"F0.wireOp",EDGE,"E7.21.3"),sQuery(id+"F0.wireOp",EDGE,"E7.21.4"),sQuery(id+"F0.wireOp",EDGE,"E7.21.5"),sQuery(id+"F0.wireOp",EDGE,"E7.22.0"),sQuery(id+"F0.wireOp",EDGE,"E7.22.1"),sQuery(id+"F0.wireOp",EDGE,"E7.22.2"),sQuery(id+"F0.wireOp",EDGE,"E7.22.3"),sQuery(id+"F0.wireOp",EDGE,"E7.22.4"),sQuery(id+"F0.wireOp",EDGE,"E7.22.5"),sQuery(id+"F0.wireOp",EDGE,"E7.23.0"),sQuery(id+"F0.wireOp",EDGE,"E7.23.1"),sQuery(id+"F0.wireOp",EDGE,"E7.23.2"),sQuery(id+"F0.wireOp",EDGE,"E7.23.3"),sQuery(id+"F0.wireOp",EDGE,"E7.23.4"),sQuery(id+"F0.wireOp",EDGE,"E7.23.5"),sQuery(id+"F0.wireOp",EDGE,"E7.24.0"),sQuery(id+"F0.wireOp",EDGE,"E7.24.1"),sQuery(id+"F0.wireOp",EDGE,"E7.24.2"),sQuery(id+"F0.wireOp",EDGE,"E7.24.3"),sQuery(id+"F0.wireOp",EDGE,"E7.24.4"),sQuery(id+"F0.wireOp",EDGE,"E7.24.5"),sQuery(id+"F0.wireOp",EDGE,"E7.25.0"),sQuery(id+"F0.wireOp",EDGE,"E7.25.1"),sQuery(id+"F0.wireOp",EDGE,"E7.25.2"),sQuery(id+"F0.wireOp",EDGE,"E7.25.3"),sQuery(id+"F0.wireOp",EDGE,"E7.25.4"),sQuery(id+"F0.wireOp",EDGE,"E7.25.5"),sQuery(id+"F0.wireOp",EDGE,"E7.26.0"),sQuery(id+"F0.wireOp",EDGE,"E7.26.1"),sQuery(id+"F0.wireOp",EDGE,"E7.26.2"),sQuery(id+"F0.wireOp",EDGE,"E7.26.3"),sQuery(id+"F0.wireOp",EDGE,"E7.26.4"),sQuery(id+"F0.wireOp",EDGE,"E7.26.5"),sQuery(id+"F0.wireOp",EDGE,"E7.27.0"),sQuery(id+"F0.wireOp",EDGE,"E7.27.1"),sQuery(id+"F0.wireOp",EDGE,"E7.27.2"),sQuery(id+"F0.wireOp",EDGE,"E7.27.3"),sQuery(id+"F0.wireOp",EDGE,"E7.27.4"),sQuery(id+"F0.wireOp",EDGE,"E7.27.5"),sQuery(id+"F0.wireOp",EDGE,"E7.28.0"),sQuery(id+"F0.wireOp",EDGE,"E7.28.1"),sQuery(id+"F0.wireOp",EDGE,"E7.28.2"),sQuery(id+"F0.wireOp",EDGE,"E7.28.3"),sQuery(id+"F0.wireOp",EDGE,"E7.28.4"),sQuery(id+"F0.wireOp",EDGE,"E7.28.5"),sQuery(id+"F0.wireOp",EDGE,"E7.29.0"),sQuery(id+"F0.wireOp",EDGE,"E7.29.1"),sQuery(id+"F0.wireOp",EDGE,"E7.29.2"),sQuery(id+"F0.wireOp",EDGE,"E7.29.3"),sQuery(id+"F0.wireOp",EDGE,"E7.29.4"),sQuery(id+"F0.wireOp",EDGE,"E7.29.5"),sQuery(id+"F0.wireOp",EDGE,"E7.30.0"),sQuery(id+"F0.wireOp",EDGE,"E7.30.1"),sQuery(id+"F0.wireOp",EDGE,"E7.30.2"),sQuery(id+"F0.wireOp",EDGE,"E7.30.3"),sQuery(id+"F0.wireOp",EDGE,"E7.30.4"),sQuery(id+"F0.wireOp",EDGE,"E7.30.5"),sQuery(id+"F0.wireOp",EDGE,"E7.31.0"),sQuery(id+"F0.wireOp",EDGE,"E7.31.1"),sQuery(id+"F0.wireOp",EDGE,"E7.31.2"),sQuery(id+"F0.wireOp",EDGE,"E7.31.3"),sQuery(id+"F0.wireOp",EDGE,"E7.31.4"),sQuery(id+"F0.wireOp",EDGE,"E7.31.5"),sQuery(id+"F0.wireOp",EDGE,"E7.32.0"),sQuery(id+"F0.wireOp",EDGE,"E7.32.1"),sQuery(id+"F0.wireOp",EDGE,"E7.32.2"),sQuery(id+"F0.wireOp",EDGE,"E7.32.3"),sQuery(id+"F0.wireOp",EDGE,"E7.32.4"),sQuery(id+"F0.wireOp",EDGE,"E7.32.5"),sQuery(id+"F0.wireOp",EDGE,"E7.33.0"),sQuery(id+"F0.wireOp",EDGE,"E7.33.1"),sQuery(id+"F0.wireOp",EDGE,"E7.33.2"),sQuery(id+"F0.wireOp",EDGE,"E7.33.3"),sQuery(id+"F0.wireOp",EDGE,"E7.33.4"),sQuery(id+"F0.wireOp",EDGE,"E7.33.5"),sQuery(id+"F0.wireOp",EDGE,"E7.34.0"),sQuery(id+"F0.wireOp",EDGE,"E7.34.1"),sQuery(id+"F0.wireOp",EDGE,"E7.34.2"),sQuery(id+"F0.wireOp",EDGE,"E7.34.3"),sQuery(id+"F0.wireOp",EDGE,"E7.34.4"),sQuery(id+"F0.wireOp",EDGE,"E7.34.5"),sQuery(id+"F0.wireOp",EDGE,"E7.35.0"),sQuery(id+"F0.wireOp",EDGE,"E7.35.1"),sQuery(id+"F0.wireOp",EDGE,"E7.35.2"),sQuery(id+"F0.wireOp",EDGE,"E7.35.3"),sQuery(id+"F0.wireOp",EDGE,"E7.35.4"),sQuery(id+"F0.wireOp",EDGE,"E7.35.5"),sQuery(id+"F0.wireOp",EDGE,"E7.36.0"),sQuery(id+"F0.wireOp",EDGE,"E7.36.1"),sQuery(id+"F0.wireOp",EDGE,"E7.36.2"),sQuery(id+"F0.wireOp",EDGE,"E7.36.3"),sQuery(id+"F0.wireOp",EDGE,"E7.36.4"),sQuery(id+"F0.wireOp",EDGE,"E7.36.5"),sQuery(id+"F0.wireOp",EDGE,"E7.37.0"),sQuery(id+"F0.wireOp",EDGE,"E7.37.1"),sQuery(id+"F0.wireOp",EDGE,"E7.37.2"),sQuery(id+"F0.wireOp",EDGE,"E7.37.3"),sQuery(id+"F0.wireOp",EDGE,"E7.37.4"),sQuery(id+"F0.wireOp",EDGE,"E7.37.5"),sQuery(id+"F0.wireOp",EDGE,"E7.38.0"),sQuery(id+"F0.wireOp",EDGE,"E7.38.1"),sQuery(id+"F0.wireOp",EDGE,"E7.38.2"),sQuery(id+"F0.wireOp",EDGE,"E7.38.3"),sQuery(id+"F0.wireOp",EDGE,"E7.38.4"),sQuery(id+"F0.wireOp",EDGE,"E7.38.5"),sQuery(id+"F0.wireOp",EDGE,"E7.39.0"),sQuery(id+"F0.wireOp",EDGE,"E7.39.1"),sQuery(id+"F0.wireOp",EDGE,"E7.39.2"),sQuery(id+"F0.wireOp",EDGE,"E7.39.3"),sQuery(id+"F0.wireOp",EDGE,"E7.39.4"),sQuery(id+"F0.wireOp",EDGE,"E7.39.5"),sQuery(id+"F0.wireOp",EDGE,"E7.40.0"),sQuery(id+"F0.wireOp",EDGE,"E7.40.1"),sQuery(id+"F0.wireOp",EDGE,"E7.40.2"),sQuery(id+"F0.wireOp",EDGE,"E7.40.3"),sQuery(id+"F0.wireOp",EDGE,"E7.40.4"),sQuery(id+"F0.wireOp",EDGE,"E7.40.5"),sQuery(id+"F0.wireOp",EDGE,"E7.41.0"),sQuery(id+"F0.wireOp",EDGE,"E7.41.1"),sQuery(id+"F0.wireOp",EDGE,"E7.41.2"),sQuery(id+"F0.wireOp",EDGE,"E7.41.3"),sQuery(id+"F0.wireOp",EDGE,"E7.41.4"),sQuery(id+"F0.wireOp",EDGE,"E7.41.5"),sQuery(id+"F0.wireOp",EDGE,"E7.42.0"),sQuery(id+"F0.wireOp",EDGE,"E7.42.1"),sQuery(id+"F0.wireOp",EDGE,"E7.42.2"),sQuery(id+"F0.wireOp",EDGE,"E7.42.3"),sQuery(id+"F0.wireOp",EDGE,"E7.42.4"),sQuery(id+"F0.wireOp",EDGE,"E7.42.5"),sQuery(id+"F0.wireOp",EDGE,"E7.43.0"),sQuery(id+"F0.wireOp",EDGE,"E7.43.1"),sQuery(id+"F0.wireOp",EDGE,"E7.43.2"),sQuery(id+"F0.wireOp",EDGE,"E7.43.3"),sQuery(id+"F0.wireOp",EDGE,"E7.43.4"),sQuery(id+"F0.wireOp",EDGE,"E7.43.5")])],"isStart":false})]});}
            var Q18;
            {var subQ0=sQuery(id+"F0.wireOp",EDGE,"E7.7.0");Q18=makeQuery(id+"F2.opChamfer","BLEND_EDGE",EDGE,{"blendedFrom":[makeQuery(id+"F1.opExtrude","CAP_EDGE",EDGE,{"disambiguationData":[OSD([subQ0])],"isStart":false}),makeQuery(id+"F1.opExtrude","CAP_FACE",FACE,{"disambiguationData":[OSD([sQuery(id+"F0.wireOp",EDGE,"E1"),sQuery(id+"F0.wireOp",EDGE,"E2"),sQuery(id+"F0.wireOp",EDGE,"E3"),sQuery(id+"F0.wireOp",EDGE,"E4"),sQuery(id+"F0.wireOp",EDGE,"E5"),sQuery(id+"F0.wireOp",EDGE,"E6"),sQuery(id+"F0.wireOp",EDGE,"E7.1.0"),sQuery(id+"F0.wireOp",EDGE,"E7.1.1"),sQuery(id+"F0.wireOp",EDGE,"E7.1.2"),sQuery(id+"F0.wireOp",EDGE,"E7.1.3"),sQuery(id+"F0.wireOp",EDGE,"E7.1.4"),sQuery(id+"F0.wireOp",EDGE,"E7.1.5"),sQuery(id+"F0.wireOp",EDGE,"E7.2.0"),sQuery(id+"F0.wireOp",EDGE,"E7.2.1"),sQuery(id+"F0.wireOp",EDGE,"E7.2.2"),sQuery(id+"F0.wireOp",EDGE,"E7.2.3"),sQuery(id+"F0.wireOp",EDGE,"E7.2.4"),sQuery(id+"F0.wireOp",EDGE,"E7.2.5"),sQuery(id+"F0.wireOp",EDGE,"E7.3.0"),sQuery(id+"F0.wireOp",EDGE,"E7.3.1"),sQuery(id+"F0.wireOp",EDGE,"E7.3.2"),sQuery(id+"F0.wireOp",EDGE,"E7.3.3"),sQuery(id+"F0.wireOp",EDGE,"E7.3.4"),sQuery(id+"F0.wireOp",EDGE,"E7.3.5"),sQuery(id+"F0.wireOp",EDGE,"E7.4.0"),sQuery(id+"F0.wireOp",EDGE,"E7.4.1"),sQuery(id+"F0.wireOp",EDGE,"E7.4.2"),sQuery(id+"F0.wireOp",EDGE,"E7.4.3"),sQuery(id+"F0.wireOp",EDGE,"E7.4.4"),sQuery(id+"F0.wireOp",EDGE,"E7.4.5"),sQuery(id+"F0.wireOp",EDGE,"E7.5.0"),sQuery(id+"F0.wireOp",EDGE,"E7.5.1"),sQuery(id+"F0.wireOp",EDGE,"E7.5.2"),sQuery(id+"F0.wireOp",EDGE,"E7.5.3"),sQuery(id+"F0.wireOp",EDGE,"E7.5.4"),sQuery(id+"F0.wireOp",EDGE,"E7.5.5"),sQuery(id+"F0.wireOp",EDGE,"E7.6.0"),sQuery(id+"F0.wireOp",EDGE,"E7.6.1"),sQuery(id+"F0.wireOp",EDGE,"E7.6.2"),sQuery(id+"F0.wireOp",EDGE,"E7.6.3"),sQuery(id+"F0.wireOp",EDGE,"E7.6.4"),sQuery(id+"F0.wireOp",EDGE,"E7.6.5"),subQ0,sQuery(id+"F0.wireOp",EDGE,"E7.7.1"),sQuery(id+"F0.wireOp",EDGE,"E7.7.2"),sQuery(id+"F0.wireOp",EDGE,"E7.7.3"),sQuery(id+"F0.wireOp",EDGE,"E7.7.4"),sQuery(id+"F0.wireOp",EDGE,"E7.7.5"),sQuery(id+"F0.wireOp",EDGE,"E7.8.0"),sQuery(id+"F0.wireOp",EDGE,"E7.8.1"),sQuery(id+"F0.wireOp",EDGE,"E7.8.2"),sQuery(id+"F0.wireOp",EDGE,"E7.8.3"),sQuery(id+"F0.wireOp",EDGE,"E7.8.4"),sQuery(id+"F0.wireOp",EDGE,"E7.8.5"),sQuery(id+"F0.wireOp",EDGE,"E7.9.0"),sQuery(id+"F0.wireOp",EDGE,"E7.9.1"),sQuery(id+"F0.wireOp",EDGE,"E7.9.2"),sQuery(id+"F0.wireOp",EDGE,"E7.9.3"),sQuery(id+"F0.wireOp",EDGE,"E7.9.4"),sQuery(id+"F0.wireOp",EDGE,"E7.9.5"),sQuery(id+"F0.wireOp",EDGE,"E7.10.0"),sQuery(id+"F0.wireOp",EDGE,"E7.10.1"),sQuery(id+"F0.wireOp",EDGE,"E7.10.2"),sQuery(id+"F0.wireOp",EDGE,"E7.10.3"),sQuery(id+"F0.wireOp",EDGE,"E7.10.4"),sQuery(id+"F0.wireOp",EDGE,"E7.10.5"),sQuery(id+"F0.wireOp",EDGE,"E7.11.0"),sQuery(id+"F0.wireOp",EDGE,"E7.11.1"),sQuery(id+"F0.wireOp",EDGE,"E7.11.2"),sQuery(id+"F0.wireOp",EDGE,"E7.11.3"),sQuery(id+"F0.wireOp",EDGE,"E7.11.4"),sQuery(id+"F0.wireOp",EDGE,"E7.11.5"),sQuery(id+"F0.wireOp",EDGE,"E7.12.0"),sQuery(id+"F0.wireOp",EDGE,"E7.12.1"),sQuery(id+"F0.wireOp",EDGE,"E7.12.2"),sQuery(id+"F0.wireOp",EDGE,"E7.12.3"),sQuery(id+"F0.wireOp",EDGE,"E7.12.4"),sQuery(id+"F0.wireOp",EDGE,"E7.12.5"),sQuery(id+"F0.wireOp",EDGE,"E7.13.0"),sQuery(id+"F0.wireOp",EDGE,"E7.13.1"),sQuery(id+"F0.wireOp",EDGE,"E7.13.2"),sQuery(id+"F0.wireOp",EDGE,"E7.13.3"),sQuery(id+"F0.wireOp",EDGE,"E7.13.4"),sQuery(id+"F0.wireOp",EDGE,"E7.13.5"),sQuery(id+"F0.wireOp",EDGE,"E7.14.0"),sQuery(id+"F0.wireOp",EDGE,"E7.14.1"),sQuery(id+"F0.wireOp",EDGE,"E7.14.2"),sQuery(id+"F0.wireOp",EDGE,"E7.14.3"),sQuery(id+"F0.wireOp",EDGE,"E7.14.4"),sQuery(id+"F0.wireOp",EDGE,"E7.14.5"),sQuery(id+"F0.wireOp",EDGE,"E7.15.0"),sQuery(id+"F0.wireOp",EDGE,"E7.15.1"),sQuery(id+"F0.wireOp",EDGE,"E7.15.2"),sQuery(id+"F0.wireOp",EDGE,"E7.15.3"),sQuery(id+"F0.wireOp",EDGE,"E7.15.4"),sQuery(id+"F0.wireOp",EDGE,"E7.15.5"),sQuery(id+"F0.wireOp",EDGE,"E7.16.0"),sQuery(id+"F0.wireOp",EDGE,"E7.16.1"),sQuery(id+"F0.wireOp",EDGE,"E7.16.2"),sQuery(id+"F0.wireOp",EDGE,"E7.16.3"),sQuery(id+"F0.wireOp",EDGE,"E7.16.4"),sQuery(id+"F0.wireOp",EDGE,"E7.16.5"),sQuery(id+"F0.wireOp",EDGE,"E7.17.0"),sQuery(id+"F0.wireOp",EDGE,"E7.17.1"),sQuery(id+"F0.wireOp",EDGE,"E7.17.2"),sQuery(id+"F0.wireOp",EDGE,"E7.17.3"),sQuery(id+"F0.wireOp",EDGE,"E7.17.4"),sQuery(id+"F0.wireOp",EDGE,"E7.17.5"),sQuery(id+"F0.wireOp",EDGE,"E7.18.0"),sQuery(id+"F0.wireOp",EDGE,"E7.18.1"),sQuery(id+"F0.wireOp",EDGE,"E7.18.2"),sQuery(id+"F0.wireOp",EDGE,"E7.18.3"),sQuery(id+"F0.wireOp",EDGE,"E7.18.4"),sQuery(id+"F0.wireOp",EDGE,"E7.18.5"),sQuery(id+"F0.wireOp",EDGE,"E7.19.0"),sQuery(id+"F0.wireOp",EDGE,"E7.19.1"),sQuery(id+"F0.wireOp",EDGE,"E7.19.2"),sQuery(id+"F0.wireOp",EDGE,"E7.19.3"),sQuery(id+"F0.wireOp",EDGE,"E7.19.4"),sQuery(id+"F0.wireOp",EDGE,"E7.19.5"),sQuery(id+"F0.wireOp",EDGE,"E7.20.0"),sQuery(id+"F0.wireOp",EDGE,"E7.20.1"),sQuery(id+"F0.wireOp",EDGE,"E7.20.2"),sQuery(id+"F0.wireOp",EDGE,"E7.20.3"),sQuery(id+"F0.wireOp",EDGE,"E7.20.4"),sQuery(id+"F0.wireOp",EDGE,"E7.20.5"),sQuery(id+"F0.wireOp",EDGE,"E7.21.0"),sQuery(id+"F0.wireOp",EDGE,"E7.21.1"),sQuery(id+"F0.wireOp",EDGE,"E7.21.2"),sQuery(id+"F0.wireOp",EDGE,"E7.21.3"),sQuery(id+"F0.wireOp",EDGE,"E7.21.4"),sQuery(id+"F0.wireOp",EDGE,"E7.21.5"),sQuery(id+"F0.wireOp",EDGE,"E7.22.0"),sQuery(id+"F0.wireOp",EDGE,"E7.22.1"),sQuery(id+"F0.wireOp",EDGE,"E7.22.2"),sQuery(id+"F0.wireOp",EDGE,"E7.22.3"),sQuery(id+"F0.wireOp",EDGE,"E7.22.4"),sQuery(id+"F0.wireOp",EDGE,"E7.22.5"),sQuery(id+"F0.wireOp",EDGE,"E7.23.0"),sQuery(id+"F0.wireOp",EDGE,"E7.23.1"),sQuery(id+"F0.wireOp",EDGE,"E7.23.2"),sQuery(id+"F0.wireOp",EDGE,"E7.23.3"),sQuery(id+"F0.wireOp",EDGE,"E7.23.4"),sQuery(id+"F0.wireOp",EDGE,"E7.23.5"),sQuery(id+"F0.wireOp",EDGE,"E7.24.0"),sQuery(id+"F0.wireOp",EDGE,"E7.24.1"),sQuery(id+"F0.wireOp",EDGE,"E7.24.2"),sQuery(id+"F0.wireOp",EDGE,"E7.24.3"),sQuery(id+"F0.wireOp",EDGE,"E7.24.4"),sQuery(id+"F0.wireOp",EDGE,"E7.24.5"),sQuery(id+"F0.wireOp",EDGE,"E7.25.0"),sQuery(id+"F0.wireOp",EDGE,"E7.25.1"),sQuery(id+"F0.wireOp",EDGE,"E7.25.2"),sQuery(id+"F0.wireOp",EDGE,"E7.25.3"),sQuery(id+"F0.wireOp",EDGE,"E7.25.4"),sQuery(id+"F0.wireOp",EDGE,"E7.25.5"),sQuery(id+"F0.wireOp",EDGE,"E7.26.0"),sQuery(id+"F0.wireOp",EDGE,"E7.26.1"),sQuery(id+"F0.wireOp",EDGE,"E7.26.2"),sQuery(id+"F0.wireOp",EDGE,"E7.26.3"),sQuery(id+"F0.wireOp",EDGE,"E7.26.4"),sQuery(id+"F0.wireOp",EDGE,"E7.26.5"),sQuery(id+"F0.wireOp",EDGE,"E7.27.0"),sQuery(id+"F0.wireOp",EDGE,"E7.27.1"),sQuery(id+"F0.wireOp",EDGE,"E7.27.2"),sQuery(id+"F0.wireOp",EDGE,"E7.27.3"),sQuery(id+"F0.wireOp",EDGE,"E7.27.4"),sQuery(id+"F0.wireOp",EDGE,"E7.27.5"),sQuery(id+"F0.wireOp",EDGE,"E7.28.0"),sQuery(id+"F0.wireOp",EDGE,"E7.28.1"),sQuery(id+"F0.wireOp",EDGE,"E7.28.2"),sQuery(id+"F0.wireOp",EDGE,"E7.28.3"),sQuery(id+"F0.wireOp",EDGE,"E7.28.4"),sQuery(id+"F0.wireOp",EDGE,"E7.28.5"),sQuery(id+"F0.wireOp",EDGE,"E7.29.0"),sQuery(id+"F0.wireOp",EDGE,"E7.29.1"),sQuery(id+"F0.wireOp",EDGE,"E7.29.2"),sQuery(id+"F0.wireOp",EDGE,"E7.29.3"),sQuery(id+"F0.wireOp",EDGE,"E7.29.4"),sQuery(id+"F0.wireOp",EDGE,"E7.29.5"),sQuery(id+"F0.wireOp",EDGE,"E7.30.0"),sQuery(id+"F0.wireOp",EDGE,"E7.30.1"),sQuery(id+"F0.wireOp",EDGE,"E7.30.2"),sQuery(id+"F0.wireOp",EDGE,"E7.30.3"),sQuery(id+"F0.wireOp",EDGE,"E7.30.4"),sQuery(id+"F0.wireOp",EDGE,"E7.30.5"),sQuery(id+"F0.wireOp",EDGE,"E7.31.0"),sQuery(id+"F0.wireOp",EDGE,"E7.31.1"),sQuery(id+"F0.wireOp",EDGE,"E7.31.2"),sQuery(id+"F0.wireOp",EDGE,"E7.31.3"),sQuery(id+"F0.wireOp",EDGE,"E7.31.4"),sQuery(id+"F0.wireOp",EDGE,"E7.31.5"),sQuery(id+"F0.wireOp",EDGE,"E7.32.0"),sQuery(id+"F0.wireOp",EDGE,"E7.32.1"),sQuery(id+"F0.wireOp",EDGE,"E7.32.2"),sQuery(id+"F0.wireOp",EDGE,"E7.32.3"),sQuery(id+"F0.wireOp",EDGE,"E7.32.4"),sQuery(id+"F0.wireOp",EDGE,"E7.32.5"),sQuery(id+"F0.wireOp",EDGE,"E7.33.0"),sQuery(id+"F0.wireOp",EDGE,"E7.33.1"),sQuery(id+"F0.wireOp",EDGE,"E7.33.2"),sQuery(id+"F0.wireOp",EDGE,"E7.33.3"),sQuery(id+"F0.wireOp",EDGE,"E7.33.4"),sQuery(id+"F0.wireOp",EDGE,"E7.33.5"),sQuery(id+"F0.wireOp",EDGE,"E7.34.0"),sQuery(id+"F0.wireOp",EDGE,"E7.34.1"),sQuery(id+"F0.wireOp",EDGE,"E7.34.2"),sQuery(id+"F0.wireOp",EDGE,"E7.34.3"),sQuery(id+"F0.wireOp",EDGE,"E7.34.4"),sQuery(id+"F0.wireOp",EDGE,"E7.34.5"),sQuery(id+"F0.wireOp",EDGE,"E7.35.0"),sQuery(id+"F0.wireOp",EDGE,"E7.35.1"),sQuery(id+"F0.wireOp",EDGE,"E7.35.2"),sQuery(id+"F0.wireOp",EDGE,"E7.35.3"),sQuery(id+"F0.wireOp",EDGE,"E7.35.4"),sQuery(id+"F0.wireOp",EDGE,"E7.35.5"),sQuery(id+"F0.wireOp",EDGE,"E7.36.0"),sQuery(id+"F0.wireOp",EDGE,"E7.36.1"),sQuery(id+"F0.wireOp",EDGE,"E7.36.2"),sQuery(id+"F0.wireOp",EDGE,"E7.36.3"),sQuery(id+"F0.wireOp",EDGE,"E7.36.4"),sQuery(id+"F0.wireOp",EDGE,"E7.36.5"),sQuery(id+"F0.wireOp",EDGE,"E7.37.0"),sQuery(id+"F0.wireOp",EDGE,"E7.37.1"),sQuery(id+"F0.wireOp",EDGE,"E7.37.2"),sQuery(id+"F0.wireOp",EDGE,"E7.37.3"),sQuery(id+"F0.wireOp",EDGE,"E7.37.4"),sQuery(id+"F0.wireOp",EDGE,"E7.37.5"),sQuery(id+"F0.wireOp",EDGE,"E7.38.0"),sQuery(id+"F0.wireOp",EDGE,"E7.38.1"),sQuery(id+"F0.wireOp",EDGE,"E7.38.2"),sQuery(id+"F0.wireOp",EDGE,"E7.38.3"),sQuery(id+"F0.wireOp",EDGE,"E7.38.4"),sQuery(id+"F0.wireOp",EDGE,"E7.38.5"),sQuery(id+"F0.wireOp",EDGE,"E7.39.0"),sQuery(id+"F0.wireOp",EDGE,"E7.39.1"),sQuery(id+"F0.wireOp",EDGE,"E7.39.2"),sQuery(id+"F0.wireOp",EDGE,"E7.39.3"),sQuery(id+"F0.wireOp",EDGE,"E7.39.4"),sQuery(id+"F0.wireOp",EDGE,"E7.39.5"),sQuery(id+"F0.wireOp",EDGE,"E7.40.0"),sQuery(id+"F0.wireOp",EDGE,"E7.40.1"),sQuery(id+"F0.wireOp",EDGE,"E7.40.2"),sQuery(id+"F0.wireOp",EDGE,"E7.40.3"),sQuery(id+"F0.wireOp",EDGE,"E7.40.4"),sQuery(id+"F0.wireOp",EDGE,"E7.40.5"),sQuery(id+"F0.wireOp",EDGE,"E7.41.0"),sQuery(id+"F0.wireOp",EDGE,"E7.41.1"),sQuery(id+"F0.wireOp",EDGE,"E7.41.2"),sQuery(id+"F0.wireOp",EDGE,"E7.41.3"),sQuery(id+"F0.wireOp",EDGE,"E7.41.4"),sQuery(id+"F0.wireOp",EDGE,"E7.41.5"),sQuery(id+"F0.wireOp",EDGE,"E7.42.0"),sQuery(id+"F0.wireOp",EDGE,"E7.42.1"),sQuery(id+"F0.wireOp",EDGE,"E7.42.2"),sQuery(id+"F0.wireOp",EDGE,"E7.42.3"),sQuery(id+"F0.wireOp",EDGE,"E7.42.4"),sQuery(id+"F0.wireOp",EDGE,"E7.42.5"),sQuery(id+"F0.wireOp",EDGE,"E7.43.0"),sQuery(id+"F0.wireOp",EDGE,"E7.43.1"),sQuery(id+"F0.wireOp",EDGE,"E7.43.2"),sQuery(id+"F0.wireOp",EDGE,"E7.43.3"),sQuery(id+"F0.wireOp",EDGE,"E7.43.4"),sQuery(id+"F0.wireOp",EDGE,"E7.43.5")])],"isStart":false})],"blendedInto":[makeQuery(id+"F1.opExtrude","CAP_FACE",FACE,{"disambiguationData":[OSD([sQuery(id+"F0.wireOp",EDGE,"E1"),sQuery(id+"F0.wireOp",EDGE,"E2"),sQuery(id+"F0.wireOp",EDGE,"E3"),sQuery(id+"F0.wireOp",EDGE,"E4"),sQuery(id+"F0.wireOp",EDGE,"E5"),sQuery(id+"F0.wireOp",EDGE,"E6"),sQuery(id+"F0.wireOp",EDGE,"E7.1.0"),sQuery(id+"F0.wireOp",EDGE,"E7.1.1"),sQuery(id+"F0.wireOp",EDGE,"E7.1.2"),sQuery(id+"F0.wireOp",EDGE,"E7.1.3"),sQuery(id+"F0.wireOp",EDGE,"E7.1.4"),sQuery(id+"F0.wireOp",EDGE,"E7.1.5"),sQuery(id+"F0.wireOp",EDGE,"E7.2.0"),sQuery(id+"F0.wireOp",EDGE,"E7.2.1"),sQuery(id+"F0.wireOp",EDGE,"E7.2.2"),sQuery(id+"F0.wireOp",EDGE,"E7.2.3"),sQuery(id+"F0.wireOp",EDGE,"E7.2.4"),sQuery(id+"F0.wireOp",EDGE,"E7.2.5"),sQuery(id+"F0.wireOp",EDGE,"E7.3.0"),sQuery(id+"F0.wireOp",EDGE,"E7.3.1"),sQuery(id+"F0.wireOp",EDGE,"E7.3.2"),sQuery(id+"F0.wireOp",EDGE,"E7.3.3"),sQuery(id+"F0.wireOp",EDGE,"E7.3.4"),sQuery(id+"F0.wireOp",EDGE,"E7.3.5"),sQuery(id+"F0.wireOp",EDGE,"E7.4.0"),sQuery(id+"F0.wireOp",EDGE,"E7.4.1"),sQuery(id+"F0.wireOp",EDGE,"E7.4.2"),sQuery(id+"F0.wireOp",EDGE,"E7.4.3"),sQuery(id+"F0.wireOp",EDGE,"E7.4.4"),sQuery(id+"F0.wireOp",EDGE,"E7.4.5"),sQuery(id+"F0.wireOp",EDGE,"E7.5.0"),sQuery(id+"F0.wireOp",EDGE,"E7.5.1"),sQuery(id+"F0.wireOp",EDGE,"E7.5.2"),sQuery(id+"F0.wireOp",EDGE,"E7.5.3"),sQuery(id+"F0.wireOp",EDGE,"E7.5.4"),sQuery(id+"F0.wireOp",EDGE,"E7.5.5"),sQuery(id+"F0.wireOp",EDGE,"E7.6.0"),sQuery(id+"F0.wireOp",EDGE,"E7.6.1"),sQuery(id+"F0.wireOp",EDGE,"E7.6.2"),sQuery(id+"F0.wireOp",EDGE,"E7.6.3"),sQuery(id+"F0.wireOp",EDGE,"E7.6.4"),sQuery(id+"F0.wireOp",EDGE,"E7.6.5"),subQ0,sQuery(id+"F0.wireOp",EDGE,"E7.7.1"),sQuery(id+"F0.wireOp",EDGE,"E7.7.2"),sQuery(id+"F0.wireOp",EDGE,"E7.7.3"),sQuery(id+"F0.wireOp",EDGE,"E7.7.4"),sQuery(id+"F0.wireOp",EDGE,"E7.7.5"),sQuery(id+"F0.wireOp",EDGE,"E7.8.0"),sQuery(id+"F0.wireOp",EDGE,"E7.8.1"),sQuery(id+"F0.wireOp",EDGE,"E7.8.2"),sQuery(id+"F0.wireOp",EDGE,"E7.8.3"),sQuery(id+"F0.wireOp",EDGE,"E7.8.4"),sQuery(id+"F0.wireOp",EDGE,"E7.8.5"),sQuery(id+"F0.wireOp",EDGE,"E7.9.0"),sQuery(id+"F0.wireOp",EDGE,"E7.9.1"),sQuery(id+"F0.wireOp",EDGE,"E7.9.2"),sQuery(id+"F0.wireOp",EDGE,"E7.9.3"),sQuery(id+"F0.wireOp",EDGE,"E7.9.4"),sQuery(id+"F0.wireOp",EDGE,"E7.9.5"),sQuery(id+"F0.wireOp",EDGE,"E7.10.0"),sQuery(id+"F0.wireOp",EDGE,"E7.10.1"),sQuery(id+"F0.wireOp",EDGE,"E7.10.2"),sQuery(id+"F0.wireOp",EDGE,"E7.10.3"),sQuery(id+"F0.wireOp",EDGE,"E7.10.4"),sQuery(id+"F0.wireOp",EDGE,"E7.10.5"),sQuery(id+"F0.wireOp",EDGE,"E7.11.0"),sQuery(id+"F0.wireOp",EDGE,"E7.11.1"),sQuery(id+"F0.wireOp",EDGE,"E7.11.2"),sQuery(id+"F0.wireOp",EDGE,"E7.11.3"),sQuery(id+"F0.wireOp",EDGE,"E7.11.4"),sQuery(id+"F0.wireOp",EDGE,"E7.11.5"),sQuery(id+"F0.wireOp",EDGE,"E7.12.0"),sQuery(id+"F0.wireOp",EDGE,"E7.12.1"),sQuery(id+"F0.wireOp",EDGE,"E7.12.2"),sQuery(id+"F0.wireOp",EDGE,"E7.12.3"),sQuery(id+"F0.wireOp",EDGE,"E7.12.4"),sQuery(id+"F0.wireOp",EDGE,"E7.12.5"),sQuery(id+"F0.wireOp",EDGE,"E7.13.0"),sQuery(id+"F0.wireOp",EDGE,"E7.13.1"),sQuery(id+"F0.wireOp",EDGE,"E7.13.2"),sQuery(id+"F0.wireOp",EDGE,"E7.13.3"),sQuery(id+"F0.wireOp",EDGE,"E7.13.4"),sQuery(id+"F0.wireOp",EDGE,"E7.13.5"),sQuery(id+"F0.wireOp",EDGE,"E7.14.0"),sQuery(id+"F0.wireOp",EDGE,"E7.14.1"),sQuery(id+"F0.wireOp",EDGE,"E7.14.2"),sQuery(id+"F0.wireOp",EDGE,"E7.14.3"),sQuery(id+"F0.wireOp",EDGE,"E7.14.4"),sQuery(id+"F0.wireOp",EDGE,"E7.14.5"),sQuery(id+"F0.wireOp",EDGE,"E7.15.0"),sQuery(id+"F0.wireOp",EDGE,"E7.15.1"),sQuery(id+"F0.wireOp",EDGE,"E7.15.2"),sQuery(id+"F0.wireOp",EDGE,"E7.15.3"),sQuery(id+"F0.wireOp",EDGE,"E7.15.4"),sQuery(id+"F0.wireOp",EDGE,"E7.15.5"),sQuery(id+"F0.wireOp",EDGE,"E7.16.0"),sQuery(id+"F0.wireOp",EDGE,"E7.16.1"),sQuery(id+"F0.wireOp",EDGE,"E7.16.2"),sQuery(id+"F0.wireOp",EDGE,"E7.16.3"),sQuery(id+"F0.wireOp",EDGE,"E7.16.4"),sQuery(id+"F0.wireOp",EDGE,"E7.16.5"),sQuery(id+"F0.wireOp",EDGE,"E7.17.0"),sQuery(id+"F0.wireOp",EDGE,"E7.17.1"),sQuery(id+"F0.wireOp",EDGE,"E7.17.2"),sQuery(id+"F0.wireOp",EDGE,"E7.17.3"),sQuery(id+"F0.wireOp",EDGE,"E7.17.4"),sQuery(id+"F0.wireOp",EDGE,"E7.17.5"),sQuery(id+"F0.wireOp",EDGE,"E7.18.0"),sQuery(id+"F0.wireOp",EDGE,"E7.18.1"),sQuery(id+"F0.wireOp",EDGE,"E7.18.2"),sQuery(id+"F0.wireOp",EDGE,"E7.18.3"),sQuery(id+"F0.wireOp",EDGE,"E7.18.4"),sQuery(id+"F0.wireOp",EDGE,"E7.18.5"),sQuery(id+"F0.wireOp",EDGE,"E7.19.0"),sQuery(id+"F0.wireOp",EDGE,"E7.19.1"),sQuery(id+"F0.wireOp",EDGE,"E7.19.2"),sQuery(id+"F0.wireOp",EDGE,"E7.19.3"),sQuery(id+"F0.wireOp",EDGE,"E7.19.4"),sQuery(id+"F0.wireOp",EDGE,"E7.19.5"),sQuery(id+"F0.wireOp",EDGE,"E7.20.0"),sQuery(id+"F0.wireOp",EDGE,"E7.20.1"),sQuery(id+"F0.wireOp",EDGE,"E7.20.2"),sQuery(id+"F0.wireOp",EDGE,"E7.20.3"),sQuery(id+"F0.wireOp",EDGE,"E7.20.4"),sQuery(id+"F0.wireOp",EDGE,"E7.20.5"),sQuery(id+"F0.wireOp",EDGE,"E7.21.0"),sQuery(id+"F0.wireOp",EDGE,"E7.21.1"),sQuery(id+"F0.wireOp",EDGE,"E7.21.2"),sQuery(id+"F0.wireOp",EDGE,"E7.21.3"),sQuery(id+"F0.wireOp",EDGE,"E7.21.4"),sQuery(id+"F0.wireOp",EDGE,"E7.21.5"),sQuery(id+"F0.wireOp",EDGE,"E7.22.0"),sQuery(id+"F0.wireOp",EDGE,"E7.22.1"),sQuery(id+"F0.wireOp",EDGE,"E7.22.2"),sQuery(id+"F0.wireOp",EDGE,"E7.22.3"),sQuery(id+"F0.wireOp",EDGE,"E7.22.4"),sQuery(id+"F0.wireOp",EDGE,"E7.22.5"),sQuery(id+"F0.wireOp",EDGE,"E7.23.0"),sQuery(id+"F0.wireOp",EDGE,"E7.23.1"),sQuery(id+"F0.wireOp",EDGE,"E7.23.2"),sQuery(id+"F0.wireOp",EDGE,"E7.23.3"),sQuery(id+"F0.wireOp",EDGE,"E7.23.4"),sQuery(id+"F0.wireOp",EDGE,"E7.23.5"),sQuery(id+"F0.wireOp",EDGE,"E7.24.0"),sQuery(id+"F0.wireOp",EDGE,"E7.24.1"),sQuery(id+"F0.wireOp",EDGE,"E7.24.2"),sQuery(id+"F0.wireOp",EDGE,"E7.24.3"),sQuery(id+"F0.wireOp",EDGE,"E7.24.4"),sQuery(id+"F0.wireOp",EDGE,"E7.24.5"),sQuery(id+"F0.wireOp",EDGE,"E7.25.0"),sQuery(id+"F0.wireOp",EDGE,"E7.25.1"),sQuery(id+"F0.wireOp",EDGE,"E7.25.2"),sQuery(id+"F0.wireOp",EDGE,"E7.25.3"),sQuery(id+"F0.wireOp",EDGE,"E7.25.4"),sQuery(id+"F0.wireOp",EDGE,"E7.25.5"),sQuery(id+"F0.wireOp",EDGE,"E7.26.0"),sQuery(id+"F0.wireOp",EDGE,"E7.26.1"),sQuery(id+"F0.wireOp",EDGE,"E7.26.2"),sQuery(id+"F0.wireOp",EDGE,"E7.26.3"),sQuery(id+"F0.wireOp",EDGE,"E7.26.4"),sQuery(id+"F0.wireOp",EDGE,"E7.26.5"),sQuery(id+"F0.wireOp",EDGE,"E7.27.0"),sQuery(id+"F0.wireOp",EDGE,"E7.27.1"),sQuery(id+"F0.wireOp",EDGE,"E7.27.2"),sQuery(id+"F0.wireOp",EDGE,"E7.27.3"),sQuery(id+"F0.wireOp",EDGE,"E7.27.4"),sQuery(id+"F0.wireOp",EDGE,"E7.27.5"),sQuery(id+"F0.wireOp",EDGE,"E7.28.0"),sQuery(id+"F0.wireOp",EDGE,"E7.28.1"),sQuery(id+"F0.wireOp",EDGE,"E7.28.2"),sQuery(id+"F0.wireOp",EDGE,"E7.28.3"),sQuery(id+"F0.wireOp",EDGE,"E7.28.4"),sQuery(id+"F0.wireOp",EDGE,"E7.28.5"),sQuery(id+"F0.wireOp",EDGE,"E7.29.0"),sQuery(id+"F0.wireOp",EDGE,"E7.29.1"),sQuery(id+"F0.wireOp",EDGE,"E7.29.2"),sQuery(id+"F0.wireOp",EDGE,"E7.29.3"),sQuery(id+"F0.wireOp",EDGE,"E7.29.4"),sQuery(id+"F0.wireOp",EDGE,"E7.29.5"),sQuery(id+"F0.wireOp",EDGE,"E7.30.0"),sQuery(id+"F0.wireOp",EDGE,"E7.30.1"),sQuery(id+"F0.wireOp",EDGE,"E7.30.2"),sQuery(id+"F0.wireOp",EDGE,"E7.30.3"),sQuery(id+"F0.wireOp",EDGE,"E7.30.4"),sQuery(id+"F0.wireOp",EDGE,"E7.30.5"),sQuery(id+"F0.wireOp",EDGE,"E7.31.0"),sQuery(id+"F0.wireOp",EDGE,"E7.31.1"),sQuery(id+"F0.wireOp",EDGE,"E7.31.2"),sQuery(id+"F0.wireOp",EDGE,"E7.31.3"),sQuery(id+"F0.wireOp",EDGE,"E7.31.4"),sQuery(id+"F0.wireOp",EDGE,"E7.31.5"),sQuery(id+"F0.wireOp",EDGE,"E7.32.0"),sQuery(id+"F0.wireOp",EDGE,"E7.32.1"),sQuery(id+"F0.wireOp",EDGE,"E7.32.2"),sQuery(id+"F0.wireOp",EDGE,"E7.32.3"),sQuery(id+"F0.wireOp",EDGE,"E7.32.4"),sQuery(id+"F0.wireOp",EDGE,"E7.32.5"),sQuery(id+"F0.wireOp",EDGE,"E7.33.0"),sQuery(id+"F0.wireOp",EDGE,"E7.33.1"),sQuery(id+"F0.wireOp",EDGE,"E7.33.2"),sQuery(id+"F0.wireOp",EDGE,"E7.33.3"),sQuery(id+"F0.wireOp",EDGE,"E7.33.4"),sQuery(id+"F0.wireOp",EDGE,"E7.33.5"),sQuery(id+"F0.wireOp",EDGE,"E7.34.0"),sQuery(id+"F0.wireOp",EDGE,"E7.34.1"),sQuery(id+"F0.wireOp",EDGE,"E7.34.2"),sQuery(id+"F0.wireOp",EDGE,"E7.34.3"),sQuery(id+"F0.wireOp",EDGE,"E7.34.4"),sQuery(id+"F0.wireOp",EDGE,"E7.34.5"),sQuery(id+"F0.wireOp",EDGE,"E7.35.0"),sQuery(id+"F0.wireOp",EDGE,"E7.35.1"),sQuery(id+"F0.wireOp",EDGE,"E7.35.2"),sQuery(id+"F0.wireOp",EDGE,"E7.35.3"),sQuery(id+"F0.wireOp",EDGE,"E7.35.4"),sQuery(id+"F0.wireOp",EDGE,"E7.35.5"),sQuery(id+"F0.wireOp",EDGE,"E7.36.0"),sQuery(id+"F0.wireOp",EDGE,"E7.36.1"),sQuery(id+"F0.wireOp",EDGE,"E7.36.2"),sQuery(id+"F0.wireOp",EDGE,"E7.36.3"),sQuery(id+"F0.wireOp",EDGE,"E7.36.4"),sQuery(id+"F0.wireOp",EDGE,"E7.36.5"),sQuery(id+"F0.wireOp",EDGE,"E7.37.0"),sQuery(id+"F0.wireOp",EDGE,"E7.37.1"),sQuery(id+"F0.wireOp",EDGE,"E7.37.2"),sQuery(id+"F0.wireOp",EDGE,"E7.37.3"),sQuery(id+"F0.wireOp",EDGE,"E7.37.4"),sQuery(id+"F0.wireOp",EDGE,"E7.37.5"),sQuery(id+"F0.wireOp",EDGE,"E7.38.0"),sQuery(id+"F0.wireOp",EDGE,"E7.38.1"),sQuery(id+"F0.wireOp",EDGE,"E7.38.2"),sQuery(id+"F0.wireOp",EDGE,"E7.38.3"),sQuery(id+"F0.wireOp",EDGE,"E7.38.4"),sQuery(id+"F0.wireOp",EDGE,"E7.38.5"),sQuery(id+"F0.wireOp",EDGE,"E7.39.0"),sQuery(id+"F0.wireOp",EDGE,"E7.39.1"),sQuery(id+"F0.wireOp",EDGE,"E7.39.2"),sQuery(id+"F0.wireOp",EDGE,"E7.39.3"),sQuery(id+"F0.wireOp",EDGE,"E7.39.4"),sQuery(id+"F0.wireOp",EDGE,"E7.39.5"),sQuery(id+"F0.wireOp",EDGE,"E7.40.0"),sQuery(id+"F0.wireOp",EDGE,"E7.40.1"),sQuery(id+"F0.wireOp",EDGE,"E7.40.2"),sQuery(id+"F0.wireOp",EDGE,"E7.40.3"),sQuery(id+"F0.wireOp",EDGE,"E7.40.4"),sQuery(id+"F0.wireOp",EDGE,"E7.40.5"),sQuery(id+"F0.wireOp",EDGE,"E7.41.0"),sQuery(id+"F0.wireOp",EDGE,"E7.41.1"),sQuery(id+"F0.wireOp",EDGE,"E7.41.2"),sQuery(id+"F0.wireOp",EDGE,"E7.41.3"),sQuery(id+"F0.wireOp",EDGE,"E7.41.4"),sQuery(id+"F0.wireOp",EDGE,"E7.41.5"),sQuery(id+"F0.wireOp",EDGE,"E7.42.0"),sQuery(id+"F0.wireOp",EDGE,"E7.42.1"),sQuery(id+"F0.wireOp",EDGE,"E7.42.2"),sQuery(id+"F0.wireOp",EDGE,"E7.42.3"),sQuery(id+"F0.wireOp",EDGE,"E7.42.4"),sQuery(id+"F0.wireOp",EDGE,"E7.42.5"),sQuery(id+"F0.wireOp",EDGE,"E7.43.0"),sQuery(id+"F0.wireOp",EDGE,"E7.43.1"),sQuery(id+"F0.wireOp",EDGE,"E7.43.2"),sQuery(id+"F0.wireOp",EDGE,"E7.43.3"),sQuery(id+"F0.wireOp",EDGE,"E7.43.4"),sQuery(id+"F0.wireOp",EDGE,"E7.43.5")])],"isStart":false})]});}
            var Q19;
            {var subQ0=sQuery(id+"F0.wireOp",EDGE,"E7.5.0");Q19=makeQuery(id+"F2.opChamfer","BLEND_EDGE",EDGE,{"blendedFrom":[makeQuery(id+"F1.opExtrude","CAP_EDGE",EDGE,{"disambiguationData":[OSD([subQ0])],"isStart":false}),makeQuery(id+"F1.opExtrude","CAP_FACE",FACE,{"disambiguationData":[OSD([sQuery(id+"F0.wireOp",EDGE,"E1"),sQuery(id+"F0.wireOp",EDGE,"E2"),sQuery(id+"F0.wireOp",EDGE,"E3"),sQuery(id+"F0.wireOp",EDGE,"E4"),sQuery(id+"F0.wireOp",EDGE,"E5"),sQuery(id+"F0.wireOp",EDGE,"E6"),sQuery(id+"F0.wireOp",EDGE,"E7.1.0"),sQuery(id+"F0.wireOp",EDGE,"E7.1.1"),sQuery(id+"F0.wireOp",EDGE,"E7.1.2"),sQuery(id+"F0.wireOp",EDGE,"E7.1.3"),sQuery(id+"F0.wireOp",EDGE,"E7.1.4"),sQuery(id+"F0.wireOp",EDGE,"E7.1.5"),sQuery(id+"F0.wireOp",EDGE,"E7.2.0"),sQuery(id+"F0.wireOp",EDGE,"E7.2.1"),sQuery(id+"F0.wireOp",EDGE,"E7.2.2"),sQuery(id+"F0.wireOp",EDGE,"E7.2.3"),sQuery(id+"F0.wireOp",EDGE,"E7.2.4"),sQuery(id+"F0.wireOp",EDGE,"E7.2.5"),sQuery(id+"F0.wireOp",EDGE,"E7.3.0"),sQuery(id+"F0.wireOp",EDGE,"E7.3.1"),sQuery(id+"F0.wireOp",EDGE,"E7.3.2"),sQuery(id+"F0.wireOp",EDGE,"E7.3.3"),sQuery(id+"F0.wireOp",EDGE,"E7.3.4"),sQuery(id+"F0.wireOp",EDGE,"E7.3.5"),sQuery(id+"F0.wireOp",EDGE,"E7.4.0"),sQuery(id+"F0.wireOp",EDGE,"E7.4.1"),sQuery(id+"F0.wireOp",EDGE,"E7.4.2"),sQuery(id+"F0.wireOp",EDGE,"E7.4.3"),sQuery(id+"F0.wireOp",EDGE,"E7.4.4"),sQuery(id+"F0.wireOp",EDGE,"E7.4.5"),subQ0,sQuery(id+"F0.wireOp",EDGE,"E7.5.1"),sQuery(id+"F0.wireOp",EDGE,"E7.5.2"),sQuery(id+"F0.wireOp",EDGE,"E7.5.3"),sQuery(id+"F0.wireOp",EDGE,"E7.5.4"),sQuery(id+"F0.wireOp",EDGE,"E7.5.5"),sQuery(id+"F0.wireOp",EDGE,"E7.6.0"),sQuery(id+"F0.wireOp",EDGE,"E7.6.1"),sQuery(id+"F0.wireOp",EDGE,"E7.6.2"),sQuery(id+"F0.wireOp",EDGE,"E7.6.3"),sQuery(id+"F0.wireOp",EDGE,"E7.6.4"),sQuery(id+"F0.wireOp",EDGE,"E7.6.5"),sQuery(id+"F0.wireOp",EDGE,"E7.7.0"),sQuery(id+"F0.wireOp",EDGE,"E7.7.1"),sQuery(id+"F0.wireOp",EDGE,"E7.7.2"),sQuery(id+"F0.wireOp",EDGE,"E7.7.3"),sQuery(id+"F0.wireOp",EDGE,"E7.7.4"),sQuery(id+"F0.wireOp",EDGE,"E7.7.5"),sQuery(id+"F0.wireOp",EDGE,"E7.8.0"),sQuery(id+"F0.wireOp",EDGE,"E7.8.1"),sQuery(id+"F0.wireOp",EDGE,"E7.8.2"),sQuery(id+"F0.wireOp",EDGE,"E7.8.3"),sQuery(id+"F0.wireOp",EDGE,"E7.8.4"),sQuery(id+"F0.wireOp",EDGE,"E7.8.5"),sQuery(id+"F0.wireOp",EDGE,"E7.9.0"),sQuery(id+"F0.wireOp",EDGE,"E7.9.1"),sQuery(id+"F0.wireOp",EDGE,"E7.9.2"),sQuery(id+"F0.wireOp",EDGE,"E7.9.3"),sQuery(id+"F0.wireOp",EDGE,"E7.9.4"),sQuery(id+"F0.wireOp",EDGE,"E7.9.5"),sQuery(id+"F0.wireOp",EDGE,"E7.10.0"),sQuery(id+"F0.wireOp",EDGE,"E7.10.1"),sQuery(id+"F0.wireOp",EDGE,"E7.10.2"),sQuery(id+"F0.wireOp",EDGE,"E7.10.3"),sQuery(id+"F0.wireOp",EDGE,"E7.10.4"),sQuery(id+"F0.wireOp",EDGE,"E7.10.5"),sQuery(id+"F0.wireOp",EDGE,"E7.11.0"),sQuery(id+"F0.wireOp",EDGE,"E7.11.1"),sQuery(id+"F0.wireOp",EDGE,"E7.11.2"),sQuery(id+"F0.wireOp",EDGE,"E7.11.3"),sQuery(id+"F0.wireOp",EDGE,"E7.11.4"),sQuery(id+"F0.wireOp",EDGE,"E7.11.5"),sQuery(id+"F0.wireOp",EDGE,"E7.12.0"),sQuery(id+"F0.wireOp",EDGE,"E7.12.1"),sQuery(id+"F0.wireOp",EDGE,"E7.12.2"),sQuery(id+"F0.wireOp",EDGE,"E7.12.3"),sQuery(id+"F0.wireOp",EDGE,"E7.12.4"),sQuery(id+"F0.wireOp",EDGE,"E7.12.5"),sQuery(id+"F0.wireOp",EDGE,"E7.13.0"),sQuery(id+"F0.wireOp",EDGE,"E7.13.1"),sQuery(id+"F0.wireOp",EDGE,"E7.13.2"),sQuery(id+"F0.wireOp",EDGE,"E7.13.3"),sQuery(id+"F0.wireOp",EDGE,"E7.13.4"),sQuery(id+"F0.wireOp",EDGE,"E7.13.5"),sQuery(id+"F0.wireOp",EDGE,"E7.14.0"),sQuery(id+"F0.wireOp",EDGE,"E7.14.1"),sQuery(id+"F0.wireOp",EDGE,"E7.14.2"),sQuery(id+"F0.wireOp",EDGE,"E7.14.3"),sQuery(id+"F0.wireOp",EDGE,"E7.14.4"),sQuery(id+"F0.wireOp",EDGE,"E7.14.5"),sQuery(id+"F0.wireOp",EDGE,"E7.15.0"),sQuery(id+"F0.wireOp",EDGE,"E7.15.1"),sQuery(id+"F0.wireOp",EDGE,"E7.15.2"),sQuery(id+"F0.wireOp",EDGE,"E7.15.3"),sQuery(id+"F0.wireOp",EDGE,"E7.15.4"),sQuery(id+"F0.wireOp",EDGE,"E7.15.5"),sQuery(id+"F0.wireOp",EDGE,"E7.16.0"),sQuery(id+"F0.wireOp",EDGE,"E7.16.1"),sQuery(id+"F0.wireOp",EDGE,"E7.16.2"),sQuery(id+"F0.wireOp",EDGE,"E7.16.3"),sQuery(id+"F0.wireOp",EDGE,"E7.16.4"),sQuery(id+"F0.wireOp",EDGE,"E7.16.5"),sQuery(id+"F0.wireOp",EDGE,"E7.17.0"),sQuery(id+"F0.wireOp",EDGE,"E7.17.1"),sQuery(id+"F0.wireOp",EDGE,"E7.17.2"),sQuery(id+"F0.wireOp",EDGE,"E7.17.3"),sQuery(id+"F0.wireOp",EDGE,"E7.17.4"),sQuery(id+"F0.wireOp",EDGE,"E7.17.5"),sQuery(id+"F0.wireOp",EDGE,"E7.18.0"),sQuery(id+"F0.wireOp",EDGE,"E7.18.1"),sQuery(id+"F0.wireOp",EDGE,"E7.18.2"),sQuery(id+"F0.wireOp",EDGE,"E7.18.3"),sQuery(id+"F0.wireOp",EDGE,"E7.18.4"),sQuery(id+"F0.wireOp",EDGE,"E7.18.5"),sQuery(id+"F0.wireOp",EDGE,"E7.19.0"),sQuery(id+"F0.wireOp",EDGE,"E7.19.1"),sQuery(id+"F0.wireOp",EDGE,"E7.19.2"),sQuery(id+"F0.wireOp",EDGE,"E7.19.3"),sQuery(id+"F0.wireOp",EDGE,"E7.19.4"),sQuery(id+"F0.wireOp",EDGE,"E7.19.5"),sQuery(id+"F0.wireOp",EDGE,"E7.20.0"),sQuery(id+"F0.wireOp",EDGE,"E7.20.1"),sQuery(id+"F0.wireOp",EDGE,"E7.20.2"),sQuery(id+"F0.wireOp",EDGE,"E7.20.3"),sQuery(id+"F0.wireOp",EDGE,"E7.20.4"),sQuery(id+"F0.wireOp",EDGE,"E7.20.5"),sQuery(id+"F0.wireOp",EDGE,"E7.21.0"),sQuery(id+"F0.wireOp",EDGE,"E7.21.1"),sQuery(id+"F0.wireOp",EDGE,"E7.21.2"),sQuery(id+"F0.wireOp",EDGE,"E7.21.3"),sQuery(id+"F0.wireOp",EDGE,"E7.21.4"),sQuery(id+"F0.wireOp",EDGE,"E7.21.5"),sQuery(id+"F0.wireOp",EDGE,"E7.22.0"),sQuery(id+"F0.wireOp",EDGE,"E7.22.1"),sQuery(id+"F0.wireOp",EDGE,"E7.22.2"),sQuery(id+"F0.wireOp",EDGE,"E7.22.3"),sQuery(id+"F0.wireOp",EDGE,"E7.22.4"),sQuery(id+"F0.wireOp",EDGE,"E7.22.5"),sQuery(id+"F0.wireOp",EDGE,"E7.23.0"),sQuery(id+"F0.wireOp",EDGE,"E7.23.1"),sQuery(id+"F0.wireOp",EDGE,"E7.23.2"),sQuery(id+"F0.wireOp",EDGE,"E7.23.3"),sQuery(id+"F0.wireOp",EDGE,"E7.23.4"),sQuery(id+"F0.wireOp",EDGE,"E7.23.5"),sQuery(id+"F0.wireOp",EDGE,"E7.24.0"),sQuery(id+"F0.wireOp",EDGE,"E7.24.1"),sQuery(id+"F0.wireOp",EDGE,"E7.24.2"),sQuery(id+"F0.wireOp",EDGE,"E7.24.3"),sQuery(id+"F0.wireOp",EDGE,"E7.24.4"),sQuery(id+"F0.wireOp",EDGE,"E7.24.5"),sQuery(id+"F0.wireOp",EDGE,"E7.25.0"),sQuery(id+"F0.wireOp",EDGE,"E7.25.1"),sQuery(id+"F0.wireOp",EDGE,"E7.25.2"),sQuery(id+"F0.wireOp",EDGE,"E7.25.3"),sQuery(id+"F0.wireOp",EDGE,"E7.25.4"),sQuery(id+"F0.wireOp",EDGE,"E7.25.5"),sQuery(id+"F0.wireOp",EDGE,"E7.26.0"),sQuery(id+"F0.wireOp",EDGE,"E7.26.1"),sQuery(id+"F0.wireOp",EDGE,"E7.26.2"),sQuery(id+"F0.wireOp",EDGE,"E7.26.3"),sQuery(id+"F0.wireOp",EDGE,"E7.26.4"),sQuery(id+"F0.wireOp",EDGE,"E7.26.5"),sQuery(id+"F0.wireOp",EDGE,"E7.27.0"),sQuery(id+"F0.wireOp",EDGE,"E7.27.1"),sQuery(id+"F0.wireOp",EDGE,"E7.27.2"),sQuery(id+"F0.wireOp",EDGE,"E7.27.3"),sQuery(id+"F0.wireOp",EDGE,"E7.27.4"),sQuery(id+"F0.wireOp",EDGE,"E7.27.5"),sQuery(id+"F0.wireOp",EDGE,"E7.28.0"),sQuery(id+"F0.wireOp",EDGE,"E7.28.1"),sQuery(id+"F0.wireOp",EDGE,"E7.28.2"),sQuery(id+"F0.wireOp",EDGE,"E7.28.3"),sQuery(id+"F0.wireOp",EDGE,"E7.28.4"),sQuery(id+"F0.wireOp",EDGE,"E7.28.5"),sQuery(id+"F0.wireOp",EDGE,"E7.29.0"),sQuery(id+"F0.wireOp",EDGE,"E7.29.1"),sQuery(id+"F0.wireOp",EDGE,"E7.29.2"),sQuery(id+"F0.wireOp",EDGE,"E7.29.3"),sQuery(id+"F0.wireOp",EDGE,"E7.29.4"),sQuery(id+"F0.wireOp",EDGE,"E7.29.5"),sQuery(id+"F0.wireOp",EDGE,"E7.30.0"),sQuery(id+"F0.wireOp",EDGE,"E7.30.1"),sQuery(id+"F0.wireOp",EDGE,"E7.30.2"),sQuery(id+"F0.wireOp",EDGE,"E7.30.3"),sQuery(id+"F0.wireOp",EDGE,"E7.30.4"),sQuery(id+"F0.wireOp",EDGE,"E7.30.5"),sQuery(id+"F0.wireOp",EDGE,"E7.31.0"),sQuery(id+"F0.wireOp",EDGE,"E7.31.1"),sQuery(id+"F0.wireOp",EDGE,"E7.31.2"),sQuery(id+"F0.wireOp",EDGE,"E7.31.3"),sQuery(id+"F0.wireOp",EDGE,"E7.31.4"),sQuery(id+"F0.wireOp",EDGE,"E7.31.5"),sQuery(id+"F0.wireOp",EDGE,"E7.32.0"),sQuery(id+"F0.wireOp",EDGE,"E7.32.1"),sQuery(id+"F0.wireOp",EDGE,"E7.32.2"),sQuery(id+"F0.wireOp",EDGE,"E7.32.3"),sQuery(id+"F0.wireOp",EDGE,"E7.32.4"),sQuery(id+"F0.wireOp",EDGE,"E7.32.5"),sQuery(id+"F0.wireOp",EDGE,"E7.33.0"),sQuery(id+"F0.wireOp",EDGE,"E7.33.1"),sQuery(id+"F0.wireOp",EDGE,"E7.33.2"),sQuery(id+"F0.wireOp",EDGE,"E7.33.3"),sQuery(id+"F0.wireOp",EDGE,"E7.33.4"),sQuery(id+"F0.wireOp",EDGE,"E7.33.5"),sQuery(id+"F0.wireOp",EDGE,"E7.34.0"),sQuery(id+"F0.wireOp",EDGE,"E7.34.1"),sQuery(id+"F0.wireOp",EDGE,"E7.34.2"),sQuery(id+"F0.wireOp",EDGE,"E7.34.3"),sQuery(id+"F0.wireOp",EDGE,"E7.34.4"),sQuery(id+"F0.wireOp",EDGE,"E7.34.5"),sQuery(id+"F0.wireOp",EDGE,"E7.35.0"),sQuery(id+"F0.wireOp",EDGE,"E7.35.1"),sQuery(id+"F0.wireOp",EDGE,"E7.35.2"),sQuery(id+"F0.wireOp",EDGE,"E7.35.3"),sQuery(id+"F0.wireOp",EDGE,"E7.35.4"),sQuery(id+"F0.wireOp",EDGE,"E7.35.5"),sQuery(id+"F0.wireOp",EDGE,"E7.36.0"),sQuery(id+"F0.wireOp",EDGE,"E7.36.1"),sQuery(id+"F0.wireOp",EDGE,"E7.36.2"),sQuery(id+"F0.wireOp",EDGE,"E7.36.3"),sQuery(id+"F0.wireOp",EDGE,"E7.36.4"),sQuery(id+"F0.wireOp",EDGE,"E7.36.5"),sQuery(id+"F0.wireOp",EDGE,"E7.37.0"),sQuery(id+"F0.wireOp",EDGE,"E7.37.1"),sQuery(id+"F0.wireOp",EDGE,"E7.37.2"),sQuery(id+"F0.wireOp",EDGE,"E7.37.3"),sQuery(id+"F0.wireOp",EDGE,"E7.37.4"),sQuery(id+"F0.wireOp",EDGE,"E7.37.5"),sQuery(id+"F0.wireOp",EDGE,"E7.38.0"),sQuery(id+"F0.wireOp",EDGE,"E7.38.1"),sQuery(id+"F0.wireOp",EDGE,"E7.38.2"),sQuery(id+"F0.wireOp",EDGE,"E7.38.3"),sQuery(id+"F0.wireOp",EDGE,"E7.38.4"),sQuery(id+"F0.wireOp",EDGE,"E7.38.5"),sQuery(id+"F0.wireOp",EDGE,"E7.39.0"),sQuery(id+"F0.wireOp",EDGE,"E7.39.1"),sQuery(id+"F0.wireOp",EDGE,"E7.39.2"),sQuery(id+"F0.wireOp",EDGE,"E7.39.3"),sQuery(id+"F0.wireOp",EDGE,"E7.39.4"),sQuery(id+"F0.wireOp",EDGE,"E7.39.5"),sQuery(id+"F0.wireOp",EDGE,"E7.40.0"),sQuery(id+"F0.wireOp",EDGE,"E7.40.1"),sQuery(id+"F0.wireOp",EDGE,"E7.40.2"),sQuery(id+"F0.wireOp",EDGE,"E7.40.3"),sQuery(id+"F0.wireOp",EDGE,"E7.40.4"),sQuery(id+"F0.wireOp",EDGE,"E7.40.5"),sQuery(id+"F0.wireOp",EDGE,"E7.41.0"),sQuery(id+"F0.wireOp",EDGE,"E7.41.1"),sQuery(id+"F0.wireOp",EDGE,"E7.41.2"),sQuery(id+"F0.wireOp",EDGE,"E7.41.3"),sQuery(id+"F0.wireOp",EDGE,"E7.41.4"),sQuery(id+"F0.wireOp",EDGE,"E7.41.5"),sQuery(id+"F0.wireOp",EDGE,"E7.42.0"),sQuery(id+"F0.wireOp",EDGE,"E7.42.1"),sQuery(id+"F0.wireOp",EDGE,"E7.42.2"),sQuery(id+"F0.wireOp",EDGE,"E7.42.3"),sQuery(id+"F0.wireOp",EDGE,"E7.42.4"),sQuery(id+"F0.wireOp",EDGE,"E7.42.5"),sQuery(id+"F0.wireOp",EDGE,"E7.43.0"),sQuery(id+"F0.wireOp",EDGE,"E7.43.1"),sQuery(id+"F0.wireOp",EDGE,"E7.43.2"),sQuery(id+"F0.wireOp",EDGE,"E7.43.3"),sQuery(id+"F0.wireOp",EDGE,"E7.43.4"),sQuery(id+"F0.wireOp",EDGE,"E7.43.5")])],"isStart":false})],"blendedInto":[makeQuery(id+"F1.opExtrude","CAP_FACE",FACE,{"disambiguationData":[OSD([sQuery(id+"F0.wireOp",EDGE,"E1"),sQuery(id+"F0.wireOp",EDGE,"E2"),sQuery(id+"F0.wireOp",EDGE,"E3"),sQuery(id+"F0.wireOp",EDGE,"E4"),sQuery(id+"F0.wireOp",EDGE,"E5"),sQuery(id+"F0.wireOp",EDGE,"E6"),sQuery(id+"F0.wireOp",EDGE,"E7.1.0"),sQuery(id+"F0.wireOp",EDGE,"E7.1.1"),sQuery(id+"F0.wireOp",EDGE,"E7.1.2"),sQuery(id+"F0.wireOp",EDGE,"E7.1.3"),sQuery(id+"F0.wireOp",EDGE,"E7.1.4"),sQuery(id+"F0.wireOp",EDGE,"E7.1.5"),sQuery(id+"F0.wireOp",EDGE,"E7.2.0"),sQuery(id+"F0.wireOp",EDGE,"E7.2.1"),sQuery(id+"F0.wireOp",EDGE,"E7.2.2"),sQuery(id+"F0.wireOp",EDGE,"E7.2.3"),sQuery(id+"F0.wireOp",EDGE,"E7.2.4"),sQuery(id+"F0.wireOp",EDGE,"E7.2.5"),sQuery(id+"F0.wireOp",EDGE,"E7.3.0"),sQuery(id+"F0.wireOp",EDGE,"E7.3.1"),sQuery(id+"F0.wireOp",EDGE,"E7.3.2"),sQuery(id+"F0.wireOp",EDGE,"E7.3.3"),sQuery(id+"F0.wireOp",EDGE,"E7.3.4"),sQuery(id+"F0.wireOp",EDGE,"E7.3.5"),sQuery(id+"F0.wireOp",EDGE,"E7.4.0"),sQuery(id+"F0.wireOp",EDGE,"E7.4.1"),sQuery(id+"F0.wireOp",EDGE,"E7.4.2"),sQuery(id+"F0.wireOp",EDGE,"E7.4.3"),sQuery(id+"F0.wireOp",EDGE,"E7.4.4"),sQuery(id+"F0.wireOp",EDGE,"E7.4.5"),subQ0,sQuery(id+"F0.wireOp",EDGE,"E7.5.1"),sQuery(id+"F0.wireOp",EDGE,"E7.5.2"),sQuery(id+"F0.wireOp",EDGE,"E7.5.3"),sQuery(id+"F0.wireOp",EDGE,"E7.5.4"),sQuery(id+"F0.wireOp",EDGE,"E7.5.5"),sQuery(id+"F0.wireOp",EDGE,"E7.6.0"),sQuery(id+"F0.wireOp",EDGE,"E7.6.1"),sQuery(id+"F0.wireOp",EDGE,"E7.6.2"),sQuery(id+"F0.wireOp",EDGE,"E7.6.3"),sQuery(id+"F0.wireOp",EDGE,"E7.6.4"),sQuery(id+"F0.wireOp",EDGE,"E7.6.5"),sQuery(id+"F0.wireOp",EDGE,"E7.7.0"),sQuery(id+"F0.wireOp",EDGE,"E7.7.1"),sQuery(id+"F0.wireOp",EDGE,"E7.7.2"),sQuery(id+"F0.wireOp",EDGE,"E7.7.3"),sQuery(id+"F0.wireOp",EDGE,"E7.7.4"),sQuery(id+"F0.wireOp",EDGE,"E7.7.5"),sQuery(id+"F0.wireOp",EDGE,"E7.8.0"),sQuery(id+"F0.wireOp",EDGE,"E7.8.1"),sQuery(id+"F0.wireOp",EDGE,"E7.8.2"),sQuery(id+"F0.wireOp",EDGE,"E7.8.3"),sQuery(id+"F0.wireOp",EDGE,"E7.8.4"),sQuery(id+"F0.wireOp",EDGE,"E7.8.5"),sQuery(id+"F0.wireOp",EDGE,"E7.9.0"),sQuery(id+"F0.wireOp",EDGE,"E7.9.1"),sQuery(id+"F0.wireOp",EDGE,"E7.9.2"),sQuery(id+"F0.wireOp",EDGE,"E7.9.3"),sQuery(id+"F0.wireOp",EDGE,"E7.9.4"),sQuery(id+"F0.wireOp",EDGE,"E7.9.5"),sQuery(id+"F0.wireOp",EDGE,"E7.10.0"),sQuery(id+"F0.wireOp",EDGE,"E7.10.1"),sQuery(id+"F0.wireOp",EDGE,"E7.10.2"),sQuery(id+"F0.wireOp",EDGE,"E7.10.3"),sQuery(id+"F0.wireOp",EDGE,"E7.10.4"),sQuery(id+"F0.wireOp",EDGE,"E7.10.5"),sQuery(id+"F0.wireOp",EDGE,"E7.11.0"),sQuery(id+"F0.wireOp",EDGE,"E7.11.1"),sQuery(id+"F0.wireOp",EDGE,"E7.11.2"),sQuery(id+"F0.wireOp",EDGE,"E7.11.3"),sQuery(id+"F0.wireOp",EDGE,"E7.11.4"),sQuery(id+"F0.wireOp",EDGE,"E7.11.5"),sQuery(id+"F0.wireOp",EDGE,"E7.12.0"),sQuery(id+"F0.wireOp",EDGE,"E7.12.1"),sQuery(id+"F0.wireOp",EDGE,"E7.12.2"),sQuery(id+"F0.wireOp",EDGE,"E7.12.3"),sQuery(id+"F0.wireOp",EDGE,"E7.12.4"),sQuery(id+"F0.wireOp",EDGE,"E7.12.5"),sQuery(id+"F0.wireOp",EDGE,"E7.13.0"),sQuery(id+"F0.wireOp",EDGE,"E7.13.1"),sQuery(id+"F0.wireOp",EDGE,"E7.13.2"),sQuery(id+"F0.wireOp",EDGE,"E7.13.3"),sQuery(id+"F0.wireOp",EDGE,"E7.13.4"),sQuery(id+"F0.wireOp",EDGE,"E7.13.5"),sQuery(id+"F0.wireOp",EDGE,"E7.14.0"),sQuery(id+"F0.wireOp",EDGE,"E7.14.1"),sQuery(id+"F0.wireOp",EDGE,"E7.14.2"),sQuery(id+"F0.wireOp",EDGE,"E7.14.3"),sQuery(id+"F0.wireOp",EDGE,"E7.14.4"),sQuery(id+"F0.wireOp",EDGE,"E7.14.5"),sQuery(id+"F0.wireOp",EDGE,"E7.15.0"),sQuery(id+"F0.wireOp",EDGE,"E7.15.1"),sQuery(id+"F0.wireOp",EDGE,"E7.15.2"),sQuery(id+"F0.wireOp",EDGE,"E7.15.3"),sQuery(id+"F0.wireOp",EDGE,"E7.15.4"),sQuery(id+"F0.wireOp",EDGE,"E7.15.5"),sQuery(id+"F0.wireOp",EDGE,"E7.16.0"),sQuery(id+"F0.wireOp",EDGE,"E7.16.1"),sQuery(id+"F0.wireOp",EDGE,"E7.16.2"),sQuery(id+"F0.wireOp",EDGE,"E7.16.3"),sQuery(id+"F0.wireOp",EDGE,"E7.16.4"),sQuery(id+"F0.wireOp",EDGE,"E7.16.5"),sQuery(id+"F0.wireOp",EDGE,"E7.17.0"),sQuery(id+"F0.wireOp",EDGE,"E7.17.1"),sQuery(id+"F0.wireOp",EDGE,"E7.17.2"),sQuery(id+"F0.wireOp",EDGE,"E7.17.3"),sQuery(id+"F0.wireOp",EDGE,"E7.17.4"),sQuery(id+"F0.wireOp",EDGE,"E7.17.5"),sQuery(id+"F0.wireOp",EDGE,"E7.18.0"),sQuery(id+"F0.wireOp",EDGE,"E7.18.1"),sQuery(id+"F0.wireOp",EDGE,"E7.18.2"),sQuery(id+"F0.wireOp",EDGE,"E7.18.3"),sQuery(id+"F0.wireOp",EDGE,"E7.18.4"),sQuery(id+"F0.wireOp",EDGE,"E7.18.5"),sQuery(id+"F0.wireOp",EDGE,"E7.19.0"),sQuery(id+"F0.wireOp",EDGE,"E7.19.1"),sQuery(id+"F0.wireOp",EDGE,"E7.19.2"),sQuery(id+"F0.wireOp",EDGE,"E7.19.3"),sQuery(id+"F0.wireOp",EDGE,"E7.19.4"),sQuery(id+"F0.wireOp",EDGE,"E7.19.5"),sQuery(id+"F0.wireOp",EDGE,"E7.20.0"),sQuery(id+"F0.wireOp",EDGE,"E7.20.1"),sQuery(id+"F0.wireOp",EDGE,"E7.20.2"),sQuery(id+"F0.wireOp",EDGE,"E7.20.3"),sQuery(id+"F0.wireOp",EDGE,"E7.20.4"),sQuery(id+"F0.wireOp",EDGE,"E7.20.5"),sQuery(id+"F0.wireOp",EDGE,"E7.21.0"),sQuery(id+"F0.wireOp",EDGE,"E7.21.1"),sQuery(id+"F0.wireOp",EDGE,"E7.21.2"),sQuery(id+"F0.wireOp",EDGE,"E7.21.3"),sQuery(id+"F0.wireOp",EDGE,"E7.21.4"),sQuery(id+"F0.wireOp",EDGE,"E7.21.5"),sQuery(id+"F0.wireOp",EDGE,"E7.22.0"),sQuery(id+"F0.wireOp",EDGE,"E7.22.1"),sQuery(id+"F0.wireOp",EDGE,"E7.22.2"),sQuery(id+"F0.wireOp",EDGE,"E7.22.3"),sQuery(id+"F0.wireOp",EDGE,"E7.22.4"),sQuery(id+"F0.wireOp",EDGE,"E7.22.5"),sQuery(id+"F0.wireOp",EDGE,"E7.23.0"),sQuery(id+"F0.wireOp",EDGE,"E7.23.1"),sQuery(id+"F0.wireOp",EDGE,"E7.23.2"),sQuery(id+"F0.wireOp",EDGE,"E7.23.3"),sQuery(id+"F0.wireOp",EDGE,"E7.23.4"),sQuery(id+"F0.wireOp",EDGE,"E7.23.5"),sQuery(id+"F0.wireOp",EDGE,"E7.24.0"),sQuery(id+"F0.wireOp",EDGE,"E7.24.1"),sQuery(id+"F0.wireOp",EDGE,"E7.24.2"),sQuery(id+"F0.wireOp",EDGE,"E7.24.3"),sQuery(id+"F0.wireOp",EDGE,"E7.24.4"),sQuery(id+"F0.wireOp",EDGE,"E7.24.5"),sQuery(id+"F0.wireOp",EDGE,"E7.25.0"),sQuery(id+"F0.wireOp",EDGE,"E7.25.1"),sQuery(id+"F0.wireOp",EDGE,"E7.25.2"),sQuery(id+"F0.wireOp",EDGE,"E7.25.3"),sQuery(id+"F0.wireOp",EDGE,"E7.25.4"),sQuery(id+"F0.wireOp",EDGE,"E7.25.5"),sQuery(id+"F0.wireOp",EDGE,"E7.26.0"),sQuery(id+"F0.wireOp",EDGE,"E7.26.1"),sQuery(id+"F0.wireOp",EDGE,"E7.26.2"),sQuery(id+"F0.wireOp",EDGE,"E7.26.3"),sQuery(id+"F0.wireOp",EDGE,"E7.26.4"),sQuery(id+"F0.wireOp",EDGE,"E7.26.5"),sQuery(id+"F0.wireOp",EDGE,"E7.27.0"),sQuery(id+"F0.wireOp",EDGE,"E7.27.1"),sQuery(id+"F0.wireOp",EDGE,"E7.27.2"),sQuery(id+"F0.wireOp",EDGE,"E7.27.3"),sQuery(id+"F0.wireOp",EDGE,"E7.27.4"),sQuery(id+"F0.wireOp",EDGE,"E7.27.5"),sQuery(id+"F0.wireOp",EDGE,"E7.28.0"),sQuery(id+"F0.wireOp",EDGE,"E7.28.1"),sQuery(id+"F0.wireOp",EDGE,"E7.28.2"),sQuery(id+"F0.wireOp",EDGE,"E7.28.3"),sQuery(id+"F0.wireOp",EDGE,"E7.28.4"),sQuery(id+"F0.wireOp",EDGE,"E7.28.5"),sQuery(id+"F0.wireOp",EDGE,"E7.29.0"),sQuery(id+"F0.wireOp",EDGE,"E7.29.1"),sQuery(id+"F0.wireOp",EDGE,"E7.29.2"),sQuery(id+"F0.wireOp",EDGE,"E7.29.3"),sQuery(id+"F0.wireOp",EDGE,"E7.29.4"),sQuery(id+"F0.wireOp",EDGE,"E7.29.5"),sQuery(id+"F0.wireOp",EDGE,"E7.30.0"),sQuery(id+"F0.wireOp",EDGE,"E7.30.1"),sQuery(id+"F0.wireOp",EDGE,"E7.30.2"),sQuery(id+"F0.wireOp",EDGE,"E7.30.3"),sQuery(id+"F0.wireOp",EDGE,"E7.30.4"),sQuery(id+"F0.wireOp",EDGE,"E7.30.5"),sQuery(id+"F0.wireOp",EDGE,"E7.31.0"),sQuery(id+"F0.wireOp",EDGE,"E7.31.1"),sQuery(id+"F0.wireOp",EDGE,"E7.31.2"),sQuery(id+"F0.wireOp",EDGE,"E7.31.3"),sQuery(id+"F0.wireOp",EDGE,"E7.31.4"),sQuery(id+"F0.wireOp",EDGE,"E7.31.5"),sQuery(id+"F0.wireOp",EDGE,"E7.32.0"),sQuery(id+"F0.wireOp",EDGE,"E7.32.1"),sQuery(id+"F0.wireOp",EDGE,"E7.32.2"),sQuery(id+"F0.wireOp",EDGE,"E7.32.3"),sQuery(id+"F0.wireOp",EDGE,"E7.32.4"),sQuery(id+"F0.wireOp",EDGE,"E7.32.5"),sQuery(id+"F0.wireOp",EDGE,"E7.33.0"),sQuery(id+"F0.wireOp",EDGE,"E7.33.1"),sQuery(id+"F0.wireOp",EDGE,"E7.33.2"),sQuery(id+"F0.wireOp",EDGE,"E7.33.3"),sQuery(id+"F0.wireOp",EDGE,"E7.33.4"),sQuery(id+"F0.wireOp",EDGE,"E7.33.5"),sQuery(id+"F0.wireOp",EDGE,"E7.34.0"),sQuery(id+"F0.wireOp",EDGE,"E7.34.1"),sQuery(id+"F0.wireOp",EDGE,"E7.34.2"),sQuery(id+"F0.wireOp",EDGE,"E7.34.3"),sQuery(id+"F0.wireOp",EDGE,"E7.34.4"),sQuery(id+"F0.wireOp",EDGE,"E7.34.5"),sQuery(id+"F0.wireOp",EDGE,"E7.35.0"),sQuery(id+"F0.wireOp",EDGE,"E7.35.1"),sQuery(id+"F0.wireOp",EDGE,"E7.35.2"),sQuery(id+"F0.wireOp",EDGE,"E7.35.3"),sQuery(id+"F0.wireOp",EDGE,"E7.35.4"),sQuery(id+"F0.wireOp",EDGE,"E7.35.5"),sQuery(id+"F0.wireOp",EDGE,"E7.36.0"),sQuery(id+"F0.wireOp",EDGE,"E7.36.1"),sQuery(id+"F0.wireOp",EDGE,"E7.36.2"),sQuery(id+"F0.wireOp",EDGE,"E7.36.3"),sQuery(id+"F0.wireOp",EDGE,"E7.36.4"),sQuery(id+"F0.wireOp",EDGE,"E7.36.5"),sQuery(id+"F0.wireOp",EDGE,"E7.37.0"),sQuery(id+"F0.wireOp",EDGE,"E7.37.1"),sQuery(id+"F0.wireOp",EDGE,"E7.37.2"),sQuery(id+"F0.wireOp",EDGE,"E7.37.3"),sQuery(id+"F0.wireOp",EDGE,"E7.37.4"),sQuery(id+"F0.wireOp",EDGE,"E7.37.5"),sQuery(id+"F0.wireOp",EDGE,"E7.38.0"),sQuery(id+"F0.wireOp",EDGE,"E7.38.1"),sQuery(id+"F0.wireOp",EDGE,"E7.38.2"),sQuery(id+"F0.wireOp",EDGE,"E7.38.3"),sQuery(id+"F0.wireOp",EDGE,"E7.38.4"),sQuery(id+"F0.wireOp",EDGE,"E7.38.5"),sQuery(id+"F0.wireOp",EDGE,"E7.39.0"),sQuery(id+"F0.wireOp",EDGE,"E7.39.1"),sQuery(id+"F0.wireOp",EDGE,"E7.39.2"),sQuery(id+"F0.wireOp",EDGE,"E7.39.3"),sQuery(id+"F0.wireOp",EDGE,"E7.39.4"),sQuery(id+"F0.wireOp",EDGE,"E7.39.5"),sQuery(id+"F0.wireOp",EDGE,"E7.40.0"),sQuery(id+"F0.wireOp",EDGE,"E7.40.1"),sQuery(id+"F0.wireOp",EDGE,"E7.40.2"),sQuery(id+"F0.wireOp",EDGE,"E7.40.3"),sQuery(id+"F0.wireOp",EDGE,"E7.40.4"),sQuery(id+"F0.wireOp",EDGE,"E7.40.5"),sQuery(id+"F0.wireOp",EDGE,"E7.41.0"),sQuery(id+"F0.wireOp",EDGE,"E7.41.1"),sQuery(id+"F0.wireOp",EDGE,"E7.41.2"),sQuery(id+"F0.wireOp",EDGE,"E7.41.3"),sQuery(id+"F0.wireOp",EDGE,"E7.41.4"),sQuery(id+"F0.wireOp",EDGE,"E7.41.5"),sQuery(id+"F0.wireOp",EDGE,"E7.42.0"),sQuery(id+"F0.wireOp",EDGE,"E7.42.1"),sQuery(id+"F0.wireOp",EDGE,"E7.42.2"),sQuery(id+"F0.wireOp",EDGE,"E7.42.3"),sQuery(id+"F0.wireOp",EDGE,"E7.42.4"),sQuery(id+"F0.wireOp",EDGE,"E7.42.5"),sQuery(id+"F0.wireOp",EDGE,"E7.43.0"),sQuery(id+"F0.wireOp",EDGE,"E7.43.1"),sQuery(id+"F0.wireOp",EDGE,"E7.43.2"),sQuery(id+"F0.wireOp",EDGE,"E7.43.3"),sQuery(id+"F0.wireOp",EDGE,"E7.43.4"),sQuery(id+"F0.wireOp",EDGE,"E7.43.5")])],"isStart":false})]});}
            var Q20;
            {var subQ0=sQuery(id+"F0.wireOp",EDGE,"E7.3.0");Q20=makeQuery(id+"F2.opChamfer","BLEND_EDGE",EDGE,{"blendedFrom":[makeQuery(id+"F1.opExtrude","CAP_EDGE",EDGE,{"disambiguationData":[OSD([subQ0])],"isStart":false}),makeQuery(id+"F1.opExtrude","CAP_FACE",FACE,{"disambiguationData":[OSD([sQuery(id+"F0.wireOp",EDGE,"E1"),sQuery(id+"F0.wireOp",EDGE,"E2"),sQuery(id+"F0.wireOp",EDGE,"E3"),sQuery(id+"F0.wireOp",EDGE,"E4"),sQuery(id+"F0.wireOp",EDGE,"E5"),sQuery(id+"F0.wireOp",EDGE,"E6"),sQuery(id+"F0.wireOp",EDGE,"E7.1.0"),sQuery(id+"F0.wireOp",EDGE,"E7.1.1"),sQuery(id+"F0.wireOp",EDGE,"E7.1.2"),sQuery(id+"F0.wireOp",EDGE,"E7.1.3"),sQuery(id+"F0.wireOp",EDGE,"E7.1.4"),sQuery(id+"F0.wireOp",EDGE,"E7.1.5"),sQuery(id+"F0.wireOp",EDGE,"E7.2.0"),sQuery(id+"F0.wireOp",EDGE,"E7.2.1"),sQuery(id+"F0.wireOp",EDGE,"E7.2.2"),sQuery(id+"F0.wireOp",EDGE,"E7.2.3"),sQuery(id+"F0.wireOp",EDGE,"E7.2.4"),sQuery(id+"F0.wireOp",EDGE,"E7.2.5"),subQ0,sQuery(id+"F0.wireOp",EDGE,"E7.3.1"),sQuery(id+"F0.wireOp",EDGE,"E7.3.2"),sQuery(id+"F0.wireOp",EDGE,"E7.3.3"),sQuery(id+"F0.wireOp",EDGE,"E7.3.4"),sQuery(id+"F0.wireOp",EDGE,"E7.3.5"),sQuery(id+"F0.wireOp",EDGE,"E7.4.0"),sQuery(id+"F0.wireOp",EDGE,"E7.4.1"),sQuery(id+"F0.wireOp",EDGE,"E7.4.2"),sQuery(id+"F0.wireOp",EDGE,"E7.4.3"),sQuery(id+"F0.wireOp",EDGE,"E7.4.4"),sQuery(id+"F0.wireOp",EDGE,"E7.4.5"),sQuery(id+"F0.wireOp",EDGE,"E7.5.0"),sQuery(id+"F0.wireOp",EDGE,"E7.5.1"),sQuery(id+"F0.wireOp",EDGE,"E7.5.2"),sQuery(id+"F0.wireOp",EDGE,"E7.5.3"),sQuery(id+"F0.wireOp",EDGE,"E7.5.4"),sQuery(id+"F0.wireOp",EDGE,"E7.5.5"),sQuery(id+"F0.wireOp",EDGE,"E7.6.0"),sQuery(id+"F0.wireOp",EDGE,"E7.6.1"),sQuery(id+"F0.wireOp",EDGE,"E7.6.2"),sQuery(id+"F0.wireOp",EDGE,"E7.6.3"),sQuery(id+"F0.wireOp",EDGE,"E7.6.4"),sQuery(id+"F0.wireOp",EDGE,"E7.6.5"),sQuery(id+"F0.wireOp",EDGE,"E7.7.0"),sQuery(id+"F0.wireOp",EDGE,"E7.7.1"),sQuery(id+"F0.wireOp",EDGE,"E7.7.2"),sQuery(id+"F0.wireOp",EDGE,"E7.7.3"),sQuery(id+"F0.wireOp",EDGE,"E7.7.4"),sQuery(id+"F0.wireOp",EDGE,"E7.7.5"),sQuery(id+"F0.wireOp",EDGE,"E7.8.0"),sQuery(id+"F0.wireOp",EDGE,"E7.8.1"),sQuery(id+"F0.wireOp",EDGE,"E7.8.2"),sQuery(id+"F0.wireOp",EDGE,"E7.8.3"),sQuery(id+"F0.wireOp",EDGE,"E7.8.4"),sQuery(id+"F0.wireOp",EDGE,"E7.8.5"),sQuery(id+"F0.wireOp",EDGE,"E7.9.0"),sQuery(id+"F0.wireOp",EDGE,"E7.9.1"),sQuery(id+"F0.wireOp",EDGE,"E7.9.2"),sQuery(id+"F0.wireOp",EDGE,"E7.9.3"),sQuery(id+"F0.wireOp",EDGE,"E7.9.4"),sQuery(id+"F0.wireOp",EDGE,"E7.9.5"),sQuery(id+"F0.wireOp",EDGE,"E7.10.0"),sQuery(id+"F0.wireOp",EDGE,"E7.10.1"),sQuery(id+"F0.wireOp",EDGE,"E7.10.2"),sQuery(id+"F0.wireOp",EDGE,"E7.10.3"),sQuery(id+"F0.wireOp",EDGE,"E7.10.4"),sQuery(id+"F0.wireOp",EDGE,"E7.10.5"),sQuery(id+"F0.wireOp",EDGE,"E7.11.0"),sQuery(id+"F0.wireOp",EDGE,"E7.11.1"),sQuery(id+"F0.wireOp",EDGE,"E7.11.2"),sQuery(id+"F0.wireOp",EDGE,"E7.11.3"),sQuery(id+"F0.wireOp",EDGE,"E7.11.4"),sQuery(id+"F0.wireOp",EDGE,"E7.11.5"),sQuery(id+"F0.wireOp",EDGE,"E7.12.0"),sQuery(id+"F0.wireOp",EDGE,"E7.12.1"),sQuery(id+"F0.wireOp",EDGE,"E7.12.2"),sQuery(id+"F0.wireOp",EDGE,"E7.12.3"),sQuery(id+"F0.wireOp",EDGE,"E7.12.4"),sQuery(id+"F0.wireOp",EDGE,"E7.12.5"),sQuery(id+"F0.wireOp",EDGE,"E7.13.0"),sQuery(id+"F0.wireOp",EDGE,"E7.13.1"),sQuery(id+"F0.wireOp",EDGE,"E7.13.2"),sQuery(id+"F0.wireOp",EDGE,"E7.13.3"),sQuery(id+"F0.wireOp",EDGE,"E7.13.4"),sQuery(id+"F0.wireOp",EDGE,"E7.13.5"),sQuery(id+"F0.wireOp",EDGE,"E7.14.0"),sQuery(id+"F0.wireOp",EDGE,"E7.14.1"),sQuery(id+"F0.wireOp",EDGE,"E7.14.2"),sQuery(id+"F0.wireOp",EDGE,"E7.14.3"),sQuery(id+"F0.wireOp",EDGE,"E7.14.4"),sQuery(id+"F0.wireOp",EDGE,"E7.14.5"),sQuery(id+"F0.wireOp",EDGE,"E7.15.0"),sQuery(id+"F0.wireOp",EDGE,"E7.15.1"),sQuery(id+"F0.wireOp",EDGE,"E7.15.2"),sQuery(id+"F0.wireOp",EDGE,"E7.15.3"),sQuery(id+"F0.wireOp",EDGE,"E7.15.4"),sQuery(id+"F0.wireOp",EDGE,"E7.15.5"),sQuery(id+"F0.wireOp",EDGE,"E7.16.0"),sQuery(id+"F0.wireOp",EDGE,"E7.16.1"),sQuery(id+"F0.wireOp",EDGE,"E7.16.2"),sQuery(id+"F0.wireOp",EDGE,"E7.16.3"),sQuery(id+"F0.wireOp",EDGE,"E7.16.4"),sQuery(id+"F0.wireOp",EDGE,"E7.16.5"),sQuery(id+"F0.wireOp",EDGE,"E7.17.0"),sQuery(id+"F0.wireOp",EDGE,"E7.17.1"),sQuery(id+"F0.wireOp",EDGE,"E7.17.2"),sQuery(id+"F0.wireOp",EDGE,"E7.17.3"),sQuery(id+"F0.wireOp",EDGE,"E7.17.4"),sQuery(id+"F0.wireOp",EDGE,"E7.17.5"),sQuery(id+"F0.wireOp",EDGE,"E7.18.0"),sQuery(id+"F0.wireOp",EDGE,"E7.18.1"),sQuery(id+"F0.wireOp",EDGE,"E7.18.2"),sQuery(id+"F0.wireOp",EDGE,"E7.18.3"),sQuery(id+"F0.wireOp",EDGE,"E7.18.4"),sQuery(id+"F0.wireOp",EDGE,"E7.18.5"),sQuery(id+"F0.wireOp",EDGE,"E7.19.0"),sQuery(id+"F0.wireOp",EDGE,"E7.19.1"),sQuery(id+"F0.wireOp",EDGE,"E7.19.2"),sQuery(id+"F0.wireOp",EDGE,"E7.19.3"),sQuery(id+"F0.wireOp",EDGE,"E7.19.4"),sQuery(id+"F0.wireOp",EDGE,"E7.19.5"),sQuery(id+"F0.wireOp",EDGE,"E7.20.0"),sQuery(id+"F0.wireOp",EDGE,"E7.20.1"),sQuery(id+"F0.wireOp",EDGE,"E7.20.2"),sQuery(id+"F0.wireOp",EDGE,"E7.20.3"),sQuery(id+"F0.wireOp",EDGE,"E7.20.4"),sQuery(id+"F0.wireOp",EDGE,"E7.20.5"),sQuery(id+"F0.wireOp",EDGE,"E7.21.0"),sQuery(id+"F0.wireOp",EDGE,"E7.21.1"),sQuery(id+"F0.wireOp",EDGE,"E7.21.2"),sQuery(id+"F0.wireOp",EDGE,"E7.21.3"),sQuery(id+"F0.wireOp",EDGE,"E7.21.4"),sQuery(id+"F0.wireOp",EDGE,"E7.21.5"),sQuery(id+"F0.wireOp",EDGE,"E7.22.0"),sQuery(id+"F0.wireOp",EDGE,"E7.22.1"),sQuery(id+"F0.wireOp",EDGE,"E7.22.2"),sQuery(id+"F0.wireOp",EDGE,"E7.22.3"),sQuery(id+"F0.wireOp",EDGE,"E7.22.4"),sQuery(id+"F0.wireOp",EDGE,"E7.22.5"),sQuery(id+"F0.wireOp",EDGE,"E7.23.0"),sQuery(id+"F0.wireOp",EDGE,"E7.23.1"),sQuery(id+"F0.wireOp",EDGE,"E7.23.2"),sQuery(id+"F0.wireOp",EDGE,"E7.23.3"),sQuery(id+"F0.wireOp",EDGE,"E7.23.4"),sQuery(id+"F0.wireOp",EDGE,"E7.23.5"),sQuery(id+"F0.wireOp",EDGE,"E7.24.0"),sQuery(id+"F0.wireOp",EDGE,"E7.24.1"),sQuery(id+"F0.wireOp",EDGE,"E7.24.2"),sQuery(id+"F0.wireOp",EDGE,"E7.24.3"),sQuery(id+"F0.wireOp",EDGE,"E7.24.4"),sQuery(id+"F0.wireOp",EDGE,"E7.24.5"),sQuery(id+"F0.wireOp",EDGE,"E7.25.0"),sQuery(id+"F0.wireOp",EDGE,"E7.25.1"),sQuery(id+"F0.wireOp",EDGE,"E7.25.2"),sQuery(id+"F0.wireOp",EDGE,"E7.25.3"),sQuery(id+"F0.wireOp",EDGE,"E7.25.4"),sQuery(id+"F0.wireOp",EDGE,"E7.25.5"),sQuery(id+"F0.wireOp",EDGE,"E7.26.0"),sQuery(id+"F0.wireOp",EDGE,"E7.26.1"),sQuery(id+"F0.wireOp",EDGE,"E7.26.2"),sQuery(id+"F0.wireOp",EDGE,"E7.26.3"),sQuery(id+"F0.wireOp",EDGE,"E7.26.4"),sQuery(id+"F0.wireOp",EDGE,"E7.26.5"),sQuery(id+"F0.wireOp",EDGE,"E7.27.0"),sQuery(id+"F0.wireOp",EDGE,"E7.27.1"),sQuery(id+"F0.wireOp",EDGE,"E7.27.2"),sQuery(id+"F0.wireOp",EDGE,"E7.27.3"),sQuery(id+"F0.wireOp",EDGE,"E7.27.4"),sQuery(id+"F0.wireOp",EDGE,"E7.27.5"),sQuery(id+"F0.wireOp",EDGE,"E7.28.0"),sQuery(id+"F0.wireOp",EDGE,"E7.28.1"),sQuery(id+"F0.wireOp",EDGE,"E7.28.2"),sQuery(id+"F0.wireOp",EDGE,"E7.28.3"),sQuery(id+"F0.wireOp",EDGE,"E7.28.4"),sQuery(id+"F0.wireOp",EDGE,"E7.28.5"),sQuery(id+"F0.wireOp",EDGE,"E7.29.0"),sQuery(id+"F0.wireOp",EDGE,"E7.29.1"),sQuery(id+"F0.wireOp",EDGE,"E7.29.2"),sQuery(id+"F0.wireOp",EDGE,"E7.29.3"),sQuery(id+"F0.wireOp",EDGE,"E7.29.4"),sQuery(id+"F0.wireOp",EDGE,"E7.29.5"),sQuery(id+"F0.wireOp",EDGE,"E7.30.0"),sQuery(id+"F0.wireOp",EDGE,"E7.30.1"),sQuery(id+"F0.wireOp",EDGE,"E7.30.2"),sQuery(id+"F0.wireOp",EDGE,"E7.30.3"),sQuery(id+"F0.wireOp",EDGE,"E7.30.4"),sQuery(id+"F0.wireOp",EDGE,"E7.30.5"),sQuery(id+"F0.wireOp",EDGE,"E7.31.0"),sQuery(id+"F0.wireOp",EDGE,"E7.31.1"),sQuery(id+"F0.wireOp",EDGE,"E7.31.2"),sQuery(id+"F0.wireOp",EDGE,"E7.31.3"),sQuery(id+"F0.wireOp",EDGE,"E7.31.4"),sQuery(id+"F0.wireOp",EDGE,"E7.31.5"),sQuery(id+"F0.wireOp",EDGE,"E7.32.0"),sQuery(id+"F0.wireOp",EDGE,"E7.32.1"),sQuery(id+"F0.wireOp",EDGE,"E7.32.2"),sQuery(id+"F0.wireOp",EDGE,"E7.32.3"),sQuery(id+"F0.wireOp",EDGE,"E7.32.4"),sQuery(id+"F0.wireOp",EDGE,"E7.32.5"),sQuery(id+"F0.wireOp",EDGE,"E7.33.0"),sQuery(id+"F0.wireOp",EDGE,"E7.33.1"),sQuery(id+"F0.wireOp",EDGE,"E7.33.2"),sQuery(id+"F0.wireOp",EDGE,"E7.33.3"),sQuery(id+"F0.wireOp",EDGE,"E7.33.4"),sQuery(id+"F0.wireOp",EDGE,"E7.33.5"),sQuery(id+"F0.wireOp",EDGE,"E7.34.0"),sQuery(id+"F0.wireOp",EDGE,"E7.34.1"),sQuery(id+"F0.wireOp",EDGE,"E7.34.2"),sQuery(id+"F0.wireOp",EDGE,"E7.34.3"),sQuery(id+"F0.wireOp",EDGE,"E7.34.4"),sQuery(id+"F0.wireOp",EDGE,"E7.34.5"),sQuery(id+"F0.wireOp",EDGE,"E7.35.0"),sQuery(id+"F0.wireOp",EDGE,"E7.35.1"),sQuery(id+"F0.wireOp",EDGE,"E7.35.2"),sQuery(id+"F0.wireOp",EDGE,"E7.35.3"),sQuery(id+"F0.wireOp",EDGE,"E7.35.4"),sQuery(id+"F0.wireOp",EDGE,"E7.35.5"),sQuery(id+"F0.wireOp",EDGE,"E7.36.0"),sQuery(id+"F0.wireOp",EDGE,"E7.36.1"),sQuery(id+"F0.wireOp",EDGE,"E7.36.2"),sQuery(id+"F0.wireOp",EDGE,"E7.36.3"),sQuery(id+"F0.wireOp",EDGE,"E7.36.4"),sQuery(id+"F0.wireOp",EDGE,"E7.36.5"),sQuery(id+"F0.wireOp",EDGE,"E7.37.0"),sQuery(id+"F0.wireOp",EDGE,"E7.37.1"),sQuery(id+"F0.wireOp",EDGE,"E7.37.2"),sQuery(id+"F0.wireOp",EDGE,"E7.37.3"),sQuery(id+"F0.wireOp",EDGE,"E7.37.4"),sQuery(id+"F0.wireOp",EDGE,"E7.37.5"),sQuery(id+"F0.wireOp",EDGE,"E7.38.0"),sQuery(id+"F0.wireOp",EDGE,"E7.38.1"),sQuery(id+"F0.wireOp",EDGE,"E7.38.2"),sQuery(id+"F0.wireOp",EDGE,"E7.38.3"),sQuery(id+"F0.wireOp",EDGE,"E7.38.4"),sQuery(id+"F0.wireOp",EDGE,"E7.38.5"),sQuery(id+"F0.wireOp",EDGE,"E7.39.0"),sQuery(id+"F0.wireOp",EDGE,"E7.39.1"),sQuery(id+"F0.wireOp",EDGE,"E7.39.2"),sQuery(id+"F0.wireOp",EDGE,"E7.39.3"),sQuery(id+"F0.wireOp",EDGE,"E7.39.4"),sQuery(id+"F0.wireOp",EDGE,"E7.39.5"),sQuery(id+"F0.wireOp",EDGE,"E7.40.0"),sQuery(id+"F0.wireOp",EDGE,"E7.40.1"),sQuery(id+"F0.wireOp",EDGE,"E7.40.2"),sQuery(id+"F0.wireOp",EDGE,"E7.40.3"),sQuery(id+"F0.wireOp",EDGE,"E7.40.4"),sQuery(id+"F0.wireOp",EDGE,"E7.40.5"),sQuery(id+"F0.wireOp",EDGE,"E7.41.0"),sQuery(id+"F0.wireOp",EDGE,"E7.41.1"),sQuery(id+"F0.wireOp",EDGE,"E7.41.2"),sQuery(id+"F0.wireOp",EDGE,"E7.41.3"),sQuery(id+"F0.wireOp",EDGE,"E7.41.4"),sQuery(id+"F0.wireOp",EDGE,"E7.41.5"),sQuery(id+"F0.wireOp",EDGE,"E7.42.0"),sQuery(id+"F0.wireOp",EDGE,"E7.42.1"),sQuery(id+"F0.wireOp",EDGE,"E7.42.2"),sQuery(id+"F0.wireOp",EDGE,"E7.42.3"),sQuery(id+"F0.wireOp",EDGE,"E7.42.4"),sQuery(id+"F0.wireOp",EDGE,"E7.42.5"),sQuery(id+"F0.wireOp",EDGE,"E7.43.0"),sQuery(id+"F0.wireOp",EDGE,"E7.43.1"),sQuery(id+"F0.wireOp",EDGE,"E7.43.2"),sQuery(id+"F0.wireOp",EDGE,"E7.43.3"),sQuery(id+"F0.wireOp",EDGE,"E7.43.4"),sQuery(id+"F0.wireOp",EDGE,"E7.43.5")])],"isStart":false})],"blendedInto":[makeQuery(id+"F1.opExtrude","CAP_FACE",FACE,{"disambiguationData":[OSD([sQuery(id+"F0.wireOp",EDGE,"E1"),sQuery(id+"F0.wireOp",EDGE,"E2"),sQuery(id+"F0.wireOp",EDGE,"E3"),sQuery(id+"F0.wireOp",EDGE,"E4"),sQuery(id+"F0.wireOp",EDGE,"E5"),sQuery(id+"F0.wireOp",EDGE,"E6"),sQuery(id+"F0.wireOp",EDGE,"E7.1.0"),sQuery(id+"F0.wireOp",EDGE,"E7.1.1"),sQuery(id+"F0.wireOp",EDGE,"E7.1.2"),sQuery(id+"F0.wireOp",EDGE,"E7.1.3"),sQuery(id+"F0.wireOp",EDGE,"E7.1.4"),sQuery(id+"F0.wireOp",EDGE,"E7.1.5"),sQuery(id+"F0.wireOp",EDGE,"E7.2.0"),sQuery(id+"F0.wireOp",EDGE,"E7.2.1"),sQuery(id+"F0.wireOp",EDGE,"E7.2.2"),sQuery(id+"F0.wireOp",EDGE,"E7.2.3"),sQuery(id+"F0.wireOp",EDGE,"E7.2.4"),sQuery(id+"F0.wireOp",EDGE,"E7.2.5"),subQ0,sQuery(id+"F0.wireOp",EDGE,"E7.3.1"),sQuery(id+"F0.wireOp",EDGE,"E7.3.2"),sQuery(id+"F0.wireOp",EDGE,"E7.3.3"),sQuery(id+"F0.wireOp",EDGE,"E7.3.4"),sQuery(id+"F0.wireOp",EDGE,"E7.3.5"),sQuery(id+"F0.wireOp",EDGE,"E7.4.0"),sQuery(id+"F0.wireOp",EDGE,"E7.4.1"),sQuery(id+"F0.wireOp",EDGE,"E7.4.2"),sQuery(id+"F0.wireOp",EDGE,"E7.4.3"),sQuery(id+"F0.wireOp",EDGE,"E7.4.4"),sQuery(id+"F0.wireOp",EDGE,"E7.4.5"),sQuery(id+"F0.wireOp",EDGE,"E7.5.0"),sQuery(id+"F0.wireOp",EDGE,"E7.5.1"),sQuery(id+"F0.wireOp",EDGE,"E7.5.2"),sQuery(id+"F0.wireOp",EDGE,"E7.5.3"),sQuery(id+"F0.wireOp",EDGE,"E7.5.4"),sQuery(id+"F0.wireOp",EDGE,"E7.5.5"),sQuery(id+"F0.wireOp",EDGE,"E7.6.0"),sQuery(id+"F0.wireOp",EDGE,"E7.6.1"),sQuery(id+"F0.wireOp",EDGE,"E7.6.2"),sQuery(id+"F0.wireOp",EDGE,"E7.6.3"),sQuery(id+"F0.wireOp",EDGE,"E7.6.4"),sQuery(id+"F0.wireOp",EDGE,"E7.6.5"),sQuery(id+"F0.wireOp",EDGE,"E7.7.0"),sQuery(id+"F0.wireOp",EDGE,"E7.7.1"),sQuery(id+"F0.wireOp",EDGE,"E7.7.2"),sQuery(id+"F0.wireOp",EDGE,"E7.7.3"),sQuery(id+"F0.wireOp",EDGE,"E7.7.4"),sQuery(id+"F0.wireOp",EDGE,"E7.7.5"),sQuery(id+"F0.wireOp",EDGE,"E7.8.0"),sQuery(id+"F0.wireOp",EDGE,"E7.8.1"),sQuery(id+"F0.wireOp",EDGE,"E7.8.2"),sQuery(id+"F0.wireOp",EDGE,"E7.8.3"),sQuery(id+"F0.wireOp",EDGE,"E7.8.4"),sQuery(id+"F0.wireOp",EDGE,"E7.8.5"),sQuery(id+"F0.wireOp",EDGE,"E7.9.0"),sQuery(id+"F0.wireOp",EDGE,"E7.9.1"),sQuery(id+"F0.wireOp",EDGE,"E7.9.2"),sQuery(id+"F0.wireOp",EDGE,"E7.9.3"),sQuery(id+"F0.wireOp",EDGE,"E7.9.4"),sQuery(id+"F0.wireOp",EDGE,"E7.9.5"),sQuery(id+"F0.wireOp",EDGE,"E7.10.0"),sQuery(id+"F0.wireOp",EDGE,"E7.10.1"),sQuery(id+"F0.wireOp",EDGE,"E7.10.2"),sQuery(id+"F0.wireOp",EDGE,"E7.10.3"),sQuery(id+"F0.wireOp",EDGE,"E7.10.4"),sQuery(id+"F0.wireOp",EDGE,"E7.10.5"),sQuery(id+"F0.wireOp",EDGE,"E7.11.0"),sQuery(id+"F0.wireOp",EDGE,"E7.11.1"),sQuery(id+"F0.wireOp",EDGE,"E7.11.2"),sQuery(id+"F0.wireOp",EDGE,"E7.11.3"),sQuery(id+"F0.wireOp",EDGE,"E7.11.4"),sQuery(id+"F0.wireOp",EDGE,"E7.11.5"),sQuery(id+"F0.wireOp",EDGE,"E7.12.0"),sQuery(id+"F0.wireOp",EDGE,"E7.12.1"),sQuery(id+"F0.wireOp",EDGE,"E7.12.2"),sQuery(id+"F0.wireOp",EDGE,"E7.12.3"),sQuery(id+"F0.wireOp",EDGE,"E7.12.4"),sQuery(id+"F0.wireOp",EDGE,"E7.12.5"),sQuery(id+"F0.wireOp",EDGE,"E7.13.0"),sQuery(id+"F0.wireOp",EDGE,"E7.13.1"),sQuery(id+"F0.wireOp",EDGE,"E7.13.2"),sQuery(id+"F0.wireOp",EDGE,"E7.13.3"),sQuery(id+"F0.wireOp",EDGE,"E7.13.4"),sQuery(id+"F0.wireOp",EDGE,"E7.13.5"),sQuery(id+"F0.wireOp",EDGE,"E7.14.0"),sQuery(id+"F0.wireOp",EDGE,"E7.14.1"),sQuery(id+"F0.wireOp",EDGE,"E7.14.2"),sQuery(id+"F0.wireOp",EDGE,"E7.14.3"),sQuery(id+"F0.wireOp",EDGE,"E7.14.4"),sQuery(id+"F0.wireOp",EDGE,"E7.14.5"),sQuery(id+"F0.wireOp",EDGE,"E7.15.0"),sQuery(id+"F0.wireOp",EDGE,"E7.15.1"),sQuery(id+"F0.wireOp",EDGE,"E7.15.2"),sQuery(id+"F0.wireOp",EDGE,"E7.15.3"),sQuery(id+"F0.wireOp",EDGE,"E7.15.4"),sQuery(id+"F0.wireOp",EDGE,"E7.15.5"),sQuery(id+"F0.wireOp",EDGE,"E7.16.0"),sQuery(id+"F0.wireOp",EDGE,"E7.16.1"),sQuery(id+"F0.wireOp",EDGE,"E7.16.2"),sQuery(id+"F0.wireOp",EDGE,"E7.16.3"),sQuery(id+"F0.wireOp",EDGE,"E7.16.4"),sQuery(id+"F0.wireOp",EDGE,"E7.16.5"),sQuery(id+"F0.wireOp",EDGE,"E7.17.0"),sQuery(id+"F0.wireOp",EDGE,"E7.17.1"),sQuery(id+"F0.wireOp",EDGE,"E7.17.2"),sQuery(id+"F0.wireOp",EDGE,"E7.17.3"),sQuery(id+"F0.wireOp",EDGE,"E7.17.4"),sQuery(id+"F0.wireOp",EDGE,"E7.17.5"),sQuery(id+"F0.wireOp",EDGE,"E7.18.0"),sQuery(id+"F0.wireOp",EDGE,"E7.18.1"),sQuery(id+"F0.wireOp",EDGE,"E7.18.2"),sQuery(id+"F0.wireOp",EDGE,"E7.18.3"),sQuery(id+"F0.wireOp",EDGE,"E7.18.4"),sQuery(id+"F0.wireOp",EDGE,"E7.18.5"),sQuery(id+"F0.wireOp",EDGE,"E7.19.0"),sQuery(id+"F0.wireOp",EDGE,"E7.19.1"),sQuery(id+"F0.wireOp",EDGE,"E7.19.2"),sQuery(id+"F0.wireOp",EDGE,"E7.19.3"),sQuery(id+"F0.wireOp",EDGE,"E7.19.4"),sQuery(id+"F0.wireOp",EDGE,"E7.19.5"),sQuery(id+"F0.wireOp",EDGE,"E7.20.0"),sQuery(id+"F0.wireOp",EDGE,"E7.20.1"),sQuery(id+"F0.wireOp",EDGE,"E7.20.2"),sQuery(id+"F0.wireOp",EDGE,"E7.20.3"),sQuery(id+"F0.wireOp",EDGE,"E7.20.4"),sQuery(id+"F0.wireOp",EDGE,"E7.20.5"),sQuery(id+"F0.wireOp",EDGE,"E7.21.0"),sQuery(id+"F0.wireOp",EDGE,"E7.21.1"),sQuery(id+"F0.wireOp",EDGE,"E7.21.2"),sQuery(id+"F0.wireOp",EDGE,"E7.21.3"),sQuery(id+"F0.wireOp",EDGE,"E7.21.4"),sQuery(id+"F0.wireOp",EDGE,"E7.21.5"),sQuery(id+"F0.wireOp",EDGE,"E7.22.0"),sQuery(id+"F0.wireOp",EDGE,"E7.22.1"),sQuery(id+"F0.wireOp",EDGE,"E7.22.2"),sQuery(id+"F0.wireOp",EDGE,"E7.22.3"),sQuery(id+"F0.wireOp",EDGE,"E7.22.4"),sQuery(id+"F0.wireOp",EDGE,"E7.22.5"),sQuery(id+"F0.wireOp",EDGE,"E7.23.0"),sQuery(id+"F0.wireOp",EDGE,"E7.23.1"),sQuery(id+"F0.wireOp",EDGE,"E7.23.2"),sQuery(id+"F0.wireOp",EDGE,"E7.23.3"),sQuery(id+"F0.wireOp",EDGE,"E7.23.4"),sQuery(id+"F0.wireOp",EDGE,"E7.23.5"),sQuery(id+"F0.wireOp",EDGE,"E7.24.0"),sQuery(id+"F0.wireOp",EDGE,"E7.24.1"),sQuery(id+"F0.wireOp",EDGE,"E7.24.2"),sQuery(id+"F0.wireOp",EDGE,"E7.24.3"),sQuery(id+"F0.wireOp",EDGE,"E7.24.4"),sQuery(id+"F0.wireOp",EDGE,"E7.24.5"),sQuery(id+"F0.wireOp",EDGE,"E7.25.0"),sQuery(id+"F0.wireOp",EDGE,"E7.25.1"),sQuery(id+"F0.wireOp",EDGE,"E7.25.2"),sQuery(id+"F0.wireOp",EDGE,"E7.25.3"),sQuery(id+"F0.wireOp",EDGE,"E7.25.4"),sQuery(id+"F0.wireOp",EDGE,"E7.25.5"),sQuery(id+"F0.wireOp",EDGE,"E7.26.0"),sQuery(id+"F0.wireOp",EDGE,"E7.26.1"),sQuery(id+"F0.wireOp",EDGE,"E7.26.2"),sQuery(id+"F0.wireOp",EDGE,"E7.26.3"),sQuery(id+"F0.wireOp",EDGE,"E7.26.4"),sQuery(id+"F0.wireOp",EDGE,"E7.26.5"),sQuery(id+"F0.wireOp",EDGE,"E7.27.0"),sQuery(id+"F0.wireOp",EDGE,"E7.27.1"),sQuery(id+"F0.wireOp",EDGE,"E7.27.2"),sQuery(id+"F0.wireOp",EDGE,"E7.27.3"),sQuery(id+"F0.wireOp",EDGE,"E7.27.4"),sQuery(id+"F0.wireOp",EDGE,"E7.27.5"),sQuery(id+"F0.wireOp",EDGE,"E7.28.0"),sQuery(id+"F0.wireOp",EDGE,"E7.28.1"),sQuery(id+"F0.wireOp",EDGE,"E7.28.2"),sQuery(id+"F0.wireOp",EDGE,"E7.28.3"),sQuery(id+"F0.wireOp",EDGE,"E7.28.4"),sQuery(id+"F0.wireOp",EDGE,"E7.28.5"),sQuery(id+"F0.wireOp",EDGE,"E7.29.0"),sQuery(id+"F0.wireOp",EDGE,"E7.29.1"),sQuery(id+"F0.wireOp",EDGE,"E7.29.2"),sQuery(id+"F0.wireOp",EDGE,"E7.29.3"),sQuery(id+"F0.wireOp",EDGE,"E7.29.4"),sQuery(id+"F0.wireOp",EDGE,"E7.29.5"),sQuery(id+"F0.wireOp",EDGE,"E7.30.0"),sQuery(id+"F0.wireOp",EDGE,"E7.30.1"),sQuery(id+"F0.wireOp",EDGE,"E7.30.2"),sQuery(id+"F0.wireOp",EDGE,"E7.30.3"),sQuery(id+"F0.wireOp",EDGE,"E7.30.4"),sQuery(id+"F0.wireOp",EDGE,"E7.30.5"),sQuery(id+"F0.wireOp",EDGE,"E7.31.0"),sQuery(id+"F0.wireOp",EDGE,"E7.31.1"),sQuery(id+"F0.wireOp",EDGE,"E7.31.2"),sQuery(id+"F0.wireOp",EDGE,"E7.31.3"),sQuery(id+"F0.wireOp",EDGE,"E7.31.4"),sQuery(id+"F0.wireOp",EDGE,"E7.31.5"),sQuery(id+"F0.wireOp",EDGE,"E7.32.0"),sQuery(id+"F0.wireOp",EDGE,"E7.32.1"),sQuery(id+"F0.wireOp",EDGE,"E7.32.2"),sQuery(id+"F0.wireOp",EDGE,"E7.32.3"),sQuery(id+"F0.wireOp",EDGE,"E7.32.4"),sQuery(id+"F0.wireOp",EDGE,"E7.32.5"),sQuery(id+"F0.wireOp",EDGE,"E7.33.0"),sQuery(id+"F0.wireOp",EDGE,"E7.33.1"),sQuery(id+"F0.wireOp",EDGE,"E7.33.2"),sQuery(id+"F0.wireOp",EDGE,"E7.33.3"),sQuery(id+"F0.wireOp",EDGE,"E7.33.4"),sQuery(id+"F0.wireOp",EDGE,"E7.33.5"),sQuery(id+"F0.wireOp",EDGE,"E7.34.0"),sQuery(id+"F0.wireOp",EDGE,"E7.34.1"),sQuery(id+"F0.wireOp",EDGE,"E7.34.2"),sQuery(id+"F0.wireOp",EDGE,"E7.34.3"),sQuery(id+"F0.wireOp",EDGE,"E7.34.4"),sQuery(id+"F0.wireOp",EDGE,"E7.34.5"),sQuery(id+"F0.wireOp",EDGE,"E7.35.0"),sQuery(id+"F0.wireOp",EDGE,"E7.35.1"),sQuery(id+"F0.wireOp",EDGE,"E7.35.2"),sQuery(id+"F0.wireOp",EDGE,"E7.35.3"),sQuery(id+"F0.wireOp",EDGE,"E7.35.4"),sQuery(id+"F0.wireOp",EDGE,"E7.35.5"),sQuery(id+"F0.wireOp",EDGE,"E7.36.0"),sQuery(id+"F0.wireOp",EDGE,"E7.36.1"),sQuery(id+"F0.wireOp",EDGE,"E7.36.2"),sQuery(id+"F0.wireOp",EDGE,"E7.36.3"),sQuery(id+"F0.wireOp",EDGE,"E7.36.4"),sQuery(id+"F0.wireOp",EDGE,"E7.36.5"),sQuery(id+"F0.wireOp",EDGE,"E7.37.0"),sQuery(id+"F0.wireOp",EDGE,"E7.37.1"),sQuery(id+"F0.wireOp",EDGE,"E7.37.2"),sQuery(id+"F0.wireOp",EDGE,"E7.37.3"),sQuery(id+"F0.wireOp",EDGE,"E7.37.4"),sQuery(id+"F0.wireOp",EDGE,"E7.37.5"),sQuery(id+"F0.wireOp",EDGE,"E7.38.0"),sQuery(id+"F0.wireOp",EDGE,"E7.38.1"),sQuery(id+"F0.wireOp",EDGE,"E7.38.2"),sQuery(id+"F0.wireOp",EDGE,"E7.38.3"),sQuery(id+"F0.wireOp",EDGE,"E7.38.4"),sQuery(id+"F0.wireOp",EDGE,"E7.38.5"),sQuery(id+"F0.wireOp",EDGE,"E7.39.0"),sQuery(id+"F0.wireOp",EDGE,"E7.39.1"),sQuery(id+"F0.wireOp",EDGE,"E7.39.2"),sQuery(id+"F0.wireOp",EDGE,"E7.39.3"),sQuery(id+"F0.wireOp",EDGE,"E7.39.4"),sQuery(id+"F0.wireOp",EDGE,"E7.39.5"),sQuery(id+"F0.wireOp",EDGE,"E7.40.0"),sQuery(id+"F0.wireOp",EDGE,"E7.40.1"),sQuery(id+"F0.wireOp",EDGE,"E7.40.2"),sQuery(id+"F0.wireOp",EDGE,"E7.40.3"),sQuery(id+"F0.wireOp",EDGE,"E7.40.4"),sQuery(id+"F0.wireOp",EDGE,"E7.40.5"),sQuery(id+"F0.wireOp",EDGE,"E7.41.0"),sQuery(id+"F0.wireOp",EDGE,"E7.41.1"),sQuery(id+"F0.wireOp",EDGE,"E7.41.2"),sQuery(id+"F0.wireOp",EDGE,"E7.41.3"),sQuery(id+"F0.wireOp",EDGE,"E7.41.4"),sQuery(id+"F0.wireOp",EDGE,"E7.41.5"),sQuery(id+"F0.wireOp",EDGE,"E7.42.0"),sQuery(id+"F0.wireOp",EDGE,"E7.42.1"),sQuery(id+"F0.wireOp",EDGE,"E7.42.2"),sQuery(id+"F0.wireOp",EDGE,"E7.42.3"),sQuery(id+"F0.wireOp",EDGE,"E7.42.4"),sQuery(id+"F0.wireOp",EDGE,"E7.42.5"),sQuery(id+"F0.wireOp",EDGE,"E7.43.0"),sQuery(id+"F0.wireOp",EDGE,"E7.43.1"),sQuery(id+"F0.wireOp",EDGE,"E7.43.2"),sQuery(id+"F0.wireOp",EDGE,"E7.43.3"),sQuery(id+"F0.wireOp",EDGE,"E7.43.4"),sQuery(id+"F0.wireOp",EDGE,"E7.43.5")])],"isStart":false})]});}
            var Q21;
            {var subQ0=sQuery(id+"F0.wireOp",EDGE,"E7.1.0");Q21=makeQuery(id+"F2.opChamfer","BLEND_EDGE",EDGE,{"blendedFrom":[makeQuery(id+"F1.opExtrude","CAP_EDGE",EDGE,{"disambiguationData":[OSD([subQ0])],"isStart":false}),makeQuery(id+"F1.opExtrude","CAP_FACE",FACE,{"disambiguationData":[OSD([sQuery(id+"F0.wireOp",EDGE,"E1"),sQuery(id+"F0.wireOp",EDGE,"E2"),sQuery(id+"F0.wireOp",EDGE,"E3"),sQuery(id+"F0.wireOp",EDGE,"E4"),sQuery(id+"F0.wireOp",EDGE,"E5"),sQuery(id+"F0.wireOp",EDGE,"E6"),subQ0,sQuery(id+"F0.wireOp",EDGE,"E7.1.1"),sQuery(id+"F0.wireOp",EDGE,"E7.1.2"),sQuery(id+"F0.wireOp",EDGE,"E7.1.3"),sQuery(id+"F0.wireOp",EDGE,"E7.1.4"),sQuery(id+"F0.wireOp",EDGE,"E7.1.5"),sQuery(id+"F0.wireOp",EDGE,"E7.2.0"),sQuery(id+"F0.wireOp",EDGE,"E7.2.1"),sQuery(id+"F0.wireOp",EDGE,"E7.2.2"),sQuery(id+"F0.wireOp",EDGE,"E7.2.3"),sQuery(id+"F0.wireOp",EDGE,"E7.2.4"),sQuery(id+"F0.wireOp",EDGE,"E7.2.5"),sQuery(id+"F0.wireOp",EDGE,"E7.3.0"),sQuery(id+"F0.wireOp",EDGE,"E7.3.1"),sQuery(id+"F0.wireOp",EDGE,"E7.3.2"),sQuery(id+"F0.wireOp",EDGE,"E7.3.3"),sQuery(id+"F0.wireOp",EDGE,"E7.3.4"),sQuery(id+"F0.wireOp",EDGE,"E7.3.5"),sQuery(id+"F0.wireOp",EDGE,"E7.4.0"),sQuery(id+"F0.wireOp",EDGE,"E7.4.1"),sQuery(id+"F0.wireOp",EDGE,"E7.4.2"),sQuery(id+"F0.wireOp",EDGE,"E7.4.3"),sQuery(id+"F0.wireOp",EDGE,"E7.4.4"),sQuery(id+"F0.wireOp",EDGE,"E7.4.5"),sQuery(id+"F0.wireOp",EDGE,"E7.5.0"),sQuery(id+"F0.wireOp",EDGE,"E7.5.1"),sQuery(id+"F0.wireOp",EDGE,"E7.5.2"),sQuery(id+"F0.wireOp",EDGE,"E7.5.3"),sQuery(id+"F0.wireOp",EDGE,"E7.5.4"),sQuery(id+"F0.wireOp",EDGE,"E7.5.5"),sQuery(id+"F0.wireOp",EDGE,"E7.6.0"),sQuery(id+"F0.wireOp",EDGE,"E7.6.1"),sQuery(id+"F0.wireOp",EDGE,"E7.6.2"),sQuery(id+"F0.wireOp",EDGE,"E7.6.3"),sQuery(id+"F0.wireOp",EDGE,"E7.6.4"),sQuery(id+"F0.wireOp",EDGE,"E7.6.5"),sQuery(id+"F0.wireOp",EDGE,"E7.7.0"),sQuery(id+"F0.wireOp",EDGE,"E7.7.1"),sQuery(id+"F0.wireOp",EDGE,"E7.7.2"),sQuery(id+"F0.wireOp",EDGE,"E7.7.3"),sQuery(id+"F0.wireOp",EDGE,"E7.7.4"),sQuery(id+"F0.wireOp",EDGE,"E7.7.5"),sQuery(id+"F0.wireOp",EDGE,"E7.8.0"),sQuery(id+"F0.wireOp",EDGE,"E7.8.1"),sQuery(id+"F0.wireOp",EDGE,"E7.8.2"),sQuery(id+"F0.wireOp",EDGE,"E7.8.3"),sQuery(id+"F0.wireOp",EDGE,"E7.8.4"),sQuery(id+"F0.wireOp",EDGE,"E7.8.5"),sQuery(id+"F0.wireOp",EDGE,"E7.9.0"),sQuery(id+"F0.wireOp",EDGE,"E7.9.1"),sQuery(id+"F0.wireOp",EDGE,"E7.9.2"),sQuery(id+"F0.wireOp",EDGE,"E7.9.3"),sQuery(id+"F0.wireOp",EDGE,"E7.9.4"),sQuery(id+"F0.wireOp",EDGE,"E7.9.5"),sQuery(id+"F0.wireOp",EDGE,"E7.10.0"),sQuery(id+"F0.wireOp",EDGE,"E7.10.1"),sQuery(id+"F0.wireOp",EDGE,"E7.10.2"),sQuery(id+"F0.wireOp",EDGE,"E7.10.3"),sQuery(id+"F0.wireOp",EDGE,"E7.10.4"),sQuery(id+"F0.wireOp",EDGE,"E7.10.5"),sQuery(id+"F0.wireOp",EDGE,"E7.11.0"),sQuery(id+"F0.wireOp",EDGE,"E7.11.1"),sQuery(id+"F0.wireOp",EDGE,"E7.11.2"),sQuery(id+"F0.wireOp",EDGE,"E7.11.3"),sQuery(id+"F0.wireOp",EDGE,"E7.11.4"),sQuery(id+"F0.wireOp",EDGE,"E7.11.5"),sQuery(id+"F0.wireOp",EDGE,"E7.12.0"),sQuery(id+"F0.wireOp",EDGE,"E7.12.1"),sQuery(id+"F0.wireOp",EDGE,"E7.12.2"),sQuery(id+"F0.wireOp",EDGE,"E7.12.3"),sQuery(id+"F0.wireOp",EDGE,"E7.12.4"),sQuery(id+"F0.wireOp",EDGE,"E7.12.5"),sQuery(id+"F0.wireOp",EDGE,"E7.13.0"),sQuery(id+"F0.wireOp",EDGE,"E7.13.1"),sQuery(id+"F0.wireOp",EDGE,"E7.13.2"),sQuery(id+"F0.wireOp",EDGE,"E7.13.3"),sQuery(id+"F0.wireOp",EDGE,"E7.13.4"),sQuery(id+"F0.wireOp",EDGE,"E7.13.5"),sQuery(id+"F0.wireOp",EDGE,"E7.14.0"),sQuery(id+"F0.wireOp",EDGE,"E7.14.1"),sQuery(id+"F0.wireOp",EDGE,"E7.14.2"),sQuery(id+"F0.wireOp",EDGE,"E7.14.3"),sQuery(id+"F0.wireOp",EDGE,"E7.14.4"),sQuery(id+"F0.wireOp",EDGE,"E7.14.5"),sQuery(id+"F0.wireOp",EDGE,"E7.15.0"),sQuery(id+"F0.wireOp",EDGE,"E7.15.1"),sQuery(id+"F0.wireOp",EDGE,"E7.15.2"),sQuery(id+"F0.wireOp",EDGE,"E7.15.3"),sQuery(id+"F0.wireOp",EDGE,"E7.15.4"),sQuery(id+"F0.wireOp",EDGE,"E7.15.5"),sQuery(id+"F0.wireOp",EDGE,"E7.16.0"),sQuery(id+"F0.wireOp",EDGE,"E7.16.1"),sQuery(id+"F0.wireOp",EDGE,"E7.16.2"),sQuery(id+"F0.wireOp",EDGE,"E7.16.3"),sQuery(id+"F0.wireOp",EDGE,"E7.16.4"),sQuery(id+"F0.wireOp",EDGE,"E7.16.5"),sQuery(id+"F0.wireOp",EDGE,"E7.17.0"),sQuery(id+"F0.wireOp",EDGE,"E7.17.1"),sQuery(id+"F0.wireOp",EDGE,"E7.17.2"),sQuery(id+"F0.wireOp",EDGE,"E7.17.3"),sQuery(id+"F0.wireOp",EDGE,"E7.17.4"),sQuery(id+"F0.wireOp",EDGE,"E7.17.5"),sQuery(id+"F0.wireOp",EDGE,"E7.18.0"),sQuery(id+"F0.wireOp",EDGE,"E7.18.1"),sQuery(id+"F0.wireOp",EDGE,"E7.18.2"),sQuery(id+"F0.wireOp",EDGE,"E7.18.3"),sQuery(id+"F0.wireOp",EDGE,"E7.18.4"),sQuery(id+"F0.wireOp",EDGE,"E7.18.5"),sQuery(id+"F0.wireOp",EDGE,"E7.19.0"),sQuery(id+"F0.wireOp",EDGE,"E7.19.1"),sQuery(id+"F0.wireOp",EDGE,"E7.19.2"),sQuery(id+"F0.wireOp",EDGE,"E7.19.3"),sQuery(id+"F0.wireOp",EDGE,"E7.19.4"),sQuery(id+"F0.wireOp",EDGE,"E7.19.5"),sQuery(id+"F0.wireOp",EDGE,"E7.20.0"),sQuery(id+"F0.wireOp",EDGE,"E7.20.1"),sQuery(id+"F0.wireOp",EDGE,"E7.20.2"),sQuery(id+"F0.wireOp",EDGE,"E7.20.3"),sQuery(id+"F0.wireOp",EDGE,"E7.20.4"),sQuery(id+"F0.wireOp",EDGE,"E7.20.5"),sQuery(id+"F0.wireOp",EDGE,"E7.21.0"),sQuery(id+"F0.wireOp",EDGE,"E7.21.1"),sQuery(id+"F0.wireOp",EDGE,"E7.21.2"),sQuery(id+"F0.wireOp",EDGE,"E7.21.3"),sQuery(id+"F0.wireOp",EDGE,"E7.21.4"),sQuery(id+"F0.wireOp",EDGE,"E7.21.5"),sQuery(id+"F0.wireOp",EDGE,"E7.22.0"),sQuery(id+"F0.wireOp",EDGE,"E7.22.1"),sQuery(id+"F0.wireOp",EDGE,"E7.22.2"),sQuery(id+"F0.wireOp",EDGE,"E7.22.3"),sQuery(id+"F0.wireOp",EDGE,"E7.22.4"),sQuery(id+"F0.wireOp",EDGE,"E7.22.5"),sQuery(id+"F0.wireOp",EDGE,"E7.23.0"),sQuery(id+"F0.wireOp",EDGE,"E7.23.1"),sQuery(id+"F0.wireOp",EDGE,"E7.23.2"),sQuery(id+"F0.wireOp",EDGE,"E7.23.3"),sQuery(id+"F0.wireOp",EDGE,"E7.23.4"),sQuery(id+"F0.wireOp",EDGE,"E7.23.5"),sQuery(id+"F0.wireOp",EDGE,"E7.24.0"),sQuery(id+"F0.wireOp",EDGE,"E7.24.1"),sQuery(id+"F0.wireOp",EDGE,"E7.24.2"),sQuery(id+"F0.wireOp",EDGE,"E7.24.3"),sQuery(id+"F0.wireOp",EDGE,"E7.24.4"),sQuery(id+"F0.wireOp",EDGE,"E7.24.5"),sQuery(id+"F0.wireOp",EDGE,"E7.25.0"),sQuery(id+"F0.wireOp",EDGE,"E7.25.1"),sQuery(id+"F0.wireOp",EDGE,"E7.25.2"),sQuery(id+"F0.wireOp",EDGE,"E7.25.3"),sQuery(id+"F0.wireOp",EDGE,"E7.25.4"),sQuery(id+"F0.wireOp",EDGE,"E7.25.5"),sQuery(id+"F0.wireOp",EDGE,"E7.26.0"),sQuery(id+"F0.wireOp",EDGE,"E7.26.1"),sQuery(id+"F0.wireOp",EDGE,"E7.26.2"),sQuery(id+"F0.wireOp",EDGE,"E7.26.3"),sQuery(id+"F0.wireOp",EDGE,"E7.26.4"),sQuery(id+"F0.wireOp",EDGE,"E7.26.5"),sQuery(id+"F0.wireOp",EDGE,"E7.27.0"),sQuery(id+"F0.wireOp",EDGE,"E7.27.1"),sQuery(id+"F0.wireOp",EDGE,"E7.27.2"),sQuery(id+"F0.wireOp",EDGE,"E7.27.3"),sQuery(id+"F0.wireOp",EDGE,"E7.27.4"),sQuery(id+"F0.wireOp",EDGE,"E7.27.5"),sQuery(id+"F0.wireOp",EDGE,"E7.28.0"),sQuery(id+"F0.wireOp",EDGE,"E7.28.1"),sQuery(id+"F0.wireOp",EDGE,"E7.28.2"),sQuery(id+"F0.wireOp",EDGE,"E7.28.3"),sQuery(id+"F0.wireOp",EDGE,"E7.28.4"),sQuery(id+"F0.wireOp",EDGE,"E7.28.5"),sQuery(id+"F0.wireOp",EDGE,"E7.29.0"),sQuery(id+"F0.wireOp",EDGE,"E7.29.1"),sQuery(id+"F0.wireOp",EDGE,"E7.29.2"),sQuery(id+"F0.wireOp",EDGE,"E7.29.3"),sQuery(id+"F0.wireOp",EDGE,"E7.29.4"),sQuery(id+"F0.wireOp",EDGE,"E7.29.5"),sQuery(id+"F0.wireOp",EDGE,"E7.30.0"),sQuery(id+"F0.wireOp",EDGE,"E7.30.1"),sQuery(id+"F0.wireOp",EDGE,"E7.30.2"),sQuery(id+"F0.wireOp",EDGE,"E7.30.3"),sQuery(id+"F0.wireOp",EDGE,"E7.30.4"),sQuery(id+"F0.wireOp",EDGE,"E7.30.5"),sQuery(id+"F0.wireOp",EDGE,"E7.31.0"),sQuery(id+"F0.wireOp",EDGE,"E7.31.1"),sQuery(id+"F0.wireOp",EDGE,"E7.31.2"),sQuery(id+"F0.wireOp",EDGE,"E7.31.3"),sQuery(id+"F0.wireOp",EDGE,"E7.31.4"),sQuery(id+"F0.wireOp",EDGE,"E7.31.5"),sQuery(id+"F0.wireOp",EDGE,"E7.32.0"),sQuery(id+"F0.wireOp",EDGE,"E7.32.1"),sQuery(id+"F0.wireOp",EDGE,"E7.32.2"),sQuery(id+"F0.wireOp",EDGE,"E7.32.3"),sQuery(id+"F0.wireOp",EDGE,"E7.32.4"),sQuery(id+"F0.wireOp",EDGE,"E7.32.5"),sQuery(id+"F0.wireOp",EDGE,"E7.33.0"),sQuery(id+"F0.wireOp",EDGE,"E7.33.1"),sQuery(id+"F0.wireOp",EDGE,"E7.33.2"),sQuery(id+"F0.wireOp",EDGE,"E7.33.3"),sQuery(id+"F0.wireOp",EDGE,"E7.33.4"),sQuery(id+"F0.wireOp",EDGE,"E7.33.5"),sQuery(id+"F0.wireOp",EDGE,"E7.34.0"),sQuery(id+"F0.wireOp",EDGE,"E7.34.1"),sQuery(id+"F0.wireOp",EDGE,"E7.34.2"),sQuery(id+"F0.wireOp",EDGE,"E7.34.3"),sQuery(id+"F0.wireOp",EDGE,"E7.34.4"),sQuery(id+"F0.wireOp",EDGE,"E7.34.5"),sQuery(id+"F0.wireOp",EDGE,"E7.35.0"),sQuery(id+"F0.wireOp",EDGE,"E7.35.1"),sQuery(id+"F0.wireOp",EDGE,"E7.35.2"),sQuery(id+"F0.wireOp",EDGE,"E7.35.3"),sQuery(id+"F0.wireOp",EDGE,"E7.35.4"),sQuery(id+"F0.wireOp",EDGE,"E7.35.5"),sQuery(id+"F0.wireOp",EDGE,"E7.36.0"),sQuery(id+"F0.wireOp",EDGE,"E7.36.1"),sQuery(id+"F0.wireOp",EDGE,"E7.36.2"),sQuery(id+"F0.wireOp",EDGE,"E7.36.3"),sQuery(id+"F0.wireOp",EDGE,"E7.36.4"),sQuery(id+"F0.wireOp",EDGE,"E7.36.5"),sQuery(id+"F0.wireOp",EDGE,"E7.37.0"),sQuery(id+"F0.wireOp",EDGE,"E7.37.1"),sQuery(id+"F0.wireOp",EDGE,"E7.37.2"),sQuery(id+"F0.wireOp",EDGE,"E7.37.3"),sQuery(id+"F0.wireOp",EDGE,"E7.37.4"),sQuery(id+"F0.wireOp",EDGE,"E7.37.5"),sQuery(id+"F0.wireOp",EDGE,"E7.38.0"),sQuery(id+"F0.wireOp",EDGE,"E7.38.1"),sQuery(id+"F0.wireOp",EDGE,"E7.38.2"),sQuery(id+"F0.wireOp",EDGE,"E7.38.3"),sQuery(id+"F0.wireOp",EDGE,"E7.38.4"),sQuery(id+"F0.wireOp",EDGE,"E7.38.5"),sQuery(id+"F0.wireOp",EDGE,"E7.39.0"),sQuery(id+"F0.wireOp",EDGE,"E7.39.1"),sQuery(id+"F0.wireOp",EDGE,"E7.39.2"),sQuery(id+"F0.wireOp",EDGE,"E7.39.3"),sQuery(id+"F0.wireOp",EDGE,"E7.39.4"),sQuery(id+"F0.wireOp",EDGE,"E7.39.5"),sQuery(id+"F0.wireOp",EDGE,"E7.40.0"),sQuery(id+"F0.wireOp",EDGE,"E7.40.1"),sQuery(id+"F0.wireOp",EDGE,"E7.40.2"),sQuery(id+"F0.wireOp",EDGE,"E7.40.3"),sQuery(id+"F0.wireOp",EDGE,"E7.40.4"),sQuery(id+"F0.wireOp",EDGE,"E7.40.5"),sQuery(id+"F0.wireOp",EDGE,"E7.41.0"),sQuery(id+"F0.wireOp",EDGE,"E7.41.1"),sQuery(id+"F0.wireOp",EDGE,"E7.41.2"),sQuery(id+"F0.wireOp",EDGE,"E7.41.3"),sQuery(id+"F0.wireOp",EDGE,"E7.41.4"),sQuery(id+"F0.wireOp",EDGE,"E7.41.5"),sQuery(id+"F0.wireOp",EDGE,"E7.42.0"),sQuery(id+"F0.wireOp",EDGE,"E7.42.1"),sQuery(id+"F0.wireOp",EDGE,"E7.42.2"),sQuery(id+"F0.wireOp",EDGE,"E7.42.3"),sQuery(id+"F0.wireOp",EDGE,"E7.42.4"),sQuery(id+"F0.wireOp",EDGE,"E7.42.5"),sQuery(id+"F0.wireOp",EDGE,"E7.43.0"),sQuery(id+"F0.wireOp",EDGE,"E7.43.1"),sQuery(id+"F0.wireOp",EDGE,"E7.43.2"),sQuery(id+"F0.wireOp",EDGE,"E7.43.3"),sQuery(id+"F0.wireOp",EDGE,"E7.43.4"),sQuery(id+"F0.wireOp",EDGE,"E7.43.5")])],"isStart":false})],"blendedInto":[makeQuery(id+"F1.opExtrude","CAP_FACE",FACE,{"disambiguationData":[OSD([sQuery(id+"F0.wireOp",EDGE,"E1"),sQuery(id+"F0.wireOp",EDGE,"E2"),sQuery(id+"F0.wireOp",EDGE,"E3"),sQuery(id+"F0.wireOp",EDGE,"E4"),sQuery(id+"F0.wireOp",EDGE,"E5"),sQuery(id+"F0.wireOp",EDGE,"E6"),subQ0,sQuery(id+"F0.wireOp",EDGE,"E7.1.1"),sQuery(id+"F0.wireOp",EDGE,"E7.1.2"),sQuery(id+"F0.wireOp",EDGE,"E7.1.3"),sQuery(id+"F0.wireOp",EDGE,"E7.1.4"),sQuery(id+"F0.wireOp",EDGE,"E7.1.5"),sQuery(id+"F0.wireOp",EDGE,"E7.2.0"),sQuery(id+"F0.wireOp",EDGE,"E7.2.1"),sQuery(id+"F0.wireOp",EDGE,"E7.2.2"),sQuery(id+"F0.wireOp",EDGE,"E7.2.3"),sQuery(id+"F0.wireOp",EDGE,"E7.2.4"),sQuery(id+"F0.wireOp",EDGE,"E7.2.5"),sQuery(id+"F0.wireOp",EDGE,"E7.3.0"),sQuery(id+"F0.wireOp",EDGE,"E7.3.1"),sQuery(id+"F0.wireOp",EDGE,"E7.3.2"),sQuery(id+"F0.wireOp",EDGE,"E7.3.3"),sQuery(id+"F0.wireOp",EDGE,"E7.3.4"),sQuery(id+"F0.wireOp",EDGE,"E7.3.5"),sQuery(id+"F0.wireOp",EDGE,"E7.4.0"),sQuery(id+"F0.wireOp",EDGE,"E7.4.1"),sQuery(id+"F0.wireOp",EDGE,"E7.4.2"),sQuery(id+"F0.wireOp",EDGE,"E7.4.3"),sQuery(id+"F0.wireOp",EDGE,"E7.4.4"),sQuery(id+"F0.wireOp",EDGE,"E7.4.5"),sQuery(id+"F0.wireOp",EDGE,"E7.5.0"),sQuery(id+"F0.wireOp",EDGE,"E7.5.1"),sQuery(id+"F0.wireOp",EDGE,"E7.5.2"),sQuery(id+"F0.wireOp",EDGE,"E7.5.3"),sQuery(id+"F0.wireOp",EDGE,"E7.5.4"),sQuery(id+"F0.wireOp",EDGE,"E7.5.5"),sQuery(id+"F0.wireOp",EDGE,"E7.6.0"),sQuery(id+"F0.wireOp",EDGE,"E7.6.1"),sQuery(id+"F0.wireOp",EDGE,"E7.6.2"),sQuery(id+"F0.wireOp",EDGE,"E7.6.3"),sQuery(id+"F0.wireOp",EDGE,"E7.6.4"),sQuery(id+"F0.wireOp",EDGE,"E7.6.5"),sQuery(id+"F0.wireOp",EDGE,"E7.7.0"),sQuery(id+"F0.wireOp",EDGE,"E7.7.1"),sQuery(id+"F0.wireOp",EDGE,"E7.7.2"),sQuery(id+"F0.wireOp",EDGE,"E7.7.3"),sQuery(id+"F0.wireOp",EDGE,"E7.7.4"),sQuery(id+"F0.wireOp",EDGE,"E7.7.5"),sQuery(id+"F0.wireOp",EDGE,"E7.8.0"),sQuery(id+"F0.wireOp",EDGE,"E7.8.1"),sQuery(id+"F0.wireOp",EDGE,"E7.8.2"),sQuery(id+"F0.wireOp",EDGE,"E7.8.3"),sQuery(id+"F0.wireOp",EDGE,"E7.8.4"),sQuery(id+"F0.wireOp",EDGE,"E7.8.5"),sQuery(id+"F0.wireOp",EDGE,"E7.9.0"),sQuery(id+"F0.wireOp",EDGE,"E7.9.1"),sQuery(id+"F0.wireOp",EDGE,"E7.9.2"),sQuery(id+"F0.wireOp",EDGE,"E7.9.3"),sQuery(id+"F0.wireOp",EDGE,"E7.9.4"),sQuery(id+"F0.wireOp",EDGE,"E7.9.5"),sQuery(id+"F0.wireOp",EDGE,"E7.10.0"),sQuery(id+"F0.wireOp",EDGE,"E7.10.1"),sQuery(id+"F0.wireOp",EDGE,"E7.10.2"),sQuery(id+"F0.wireOp",EDGE,"E7.10.3"),sQuery(id+"F0.wireOp",EDGE,"E7.10.4"),sQuery(id+"F0.wireOp",EDGE,"E7.10.5"),sQuery(id+"F0.wireOp",EDGE,"E7.11.0"),sQuery(id+"F0.wireOp",EDGE,"E7.11.1"),sQuery(id+"F0.wireOp",EDGE,"E7.11.2"),sQuery(id+"F0.wireOp",EDGE,"E7.11.3"),sQuery(id+"F0.wireOp",EDGE,"E7.11.4"),sQuery(id+"F0.wireOp",EDGE,"E7.11.5"),sQuery(id+"F0.wireOp",EDGE,"E7.12.0"),sQuery(id+"F0.wireOp",EDGE,"E7.12.1"),sQuery(id+"F0.wireOp",EDGE,"E7.12.2"),sQuery(id+"F0.wireOp",EDGE,"E7.12.3"),sQuery(id+"F0.wireOp",EDGE,"E7.12.4"),sQuery(id+"F0.wireOp",EDGE,"E7.12.5"),sQuery(id+"F0.wireOp",EDGE,"E7.13.0"),sQuery(id+"F0.wireOp",EDGE,"E7.13.1"),sQuery(id+"F0.wireOp",EDGE,"E7.13.2"),sQuery(id+"F0.wireOp",EDGE,"E7.13.3"),sQuery(id+"F0.wireOp",EDGE,"E7.13.4"),sQuery(id+"F0.wireOp",EDGE,"E7.13.5"),sQuery(id+"F0.wireOp",EDGE,"E7.14.0"),sQuery(id+"F0.wireOp",EDGE,"E7.14.1"),sQuery(id+"F0.wireOp",EDGE,"E7.14.2"),sQuery(id+"F0.wireOp",EDGE,"E7.14.3"),sQuery(id+"F0.wireOp",EDGE,"E7.14.4"),sQuery(id+"F0.wireOp",EDGE,"E7.14.5"),sQuery(id+"F0.wireOp",EDGE,"E7.15.0"),sQuery(id+"F0.wireOp",EDGE,"E7.15.1"),sQuery(id+"F0.wireOp",EDGE,"E7.15.2"),sQuery(id+"F0.wireOp",EDGE,"E7.15.3"),sQuery(id+"F0.wireOp",EDGE,"E7.15.4"),sQuery(id+"F0.wireOp",EDGE,"E7.15.5"),sQuery(id+"F0.wireOp",EDGE,"E7.16.0"),sQuery(id+"F0.wireOp",EDGE,"E7.16.1"),sQuery(id+"F0.wireOp",EDGE,"E7.16.2"),sQuery(id+"F0.wireOp",EDGE,"E7.16.3"),sQuery(id+"F0.wireOp",EDGE,"E7.16.4"),sQuery(id+"F0.wireOp",EDGE,"E7.16.5"),sQuery(id+"F0.wireOp",EDGE,"E7.17.0"),sQuery(id+"F0.wireOp",EDGE,"E7.17.1"),sQuery(id+"F0.wireOp",EDGE,"E7.17.2"),sQuery(id+"F0.wireOp",EDGE,"E7.17.3"),sQuery(id+"F0.wireOp",EDGE,"E7.17.4"),sQuery(id+"F0.wireOp",EDGE,"E7.17.5"),sQuery(id+"F0.wireOp",EDGE,"E7.18.0"),sQuery(id+"F0.wireOp",EDGE,"E7.18.1"),sQuery(id+"F0.wireOp",EDGE,"E7.18.2"),sQuery(id+"F0.wireOp",EDGE,"E7.18.3"),sQuery(id+"F0.wireOp",EDGE,"E7.18.4"),sQuery(id+"F0.wireOp",EDGE,"E7.18.5"),sQuery(id+"F0.wireOp",EDGE,"E7.19.0"),sQuery(id+"F0.wireOp",EDGE,"E7.19.1"),sQuery(id+"F0.wireOp",EDGE,"E7.19.2"),sQuery(id+"F0.wireOp",EDGE,"E7.19.3"),sQuery(id+"F0.wireOp",EDGE,"E7.19.4"),sQuery(id+"F0.wireOp",EDGE,"E7.19.5"),sQuery(id+"F0.wireOp",EDGE,"E7.20.0"),sQuery(id+"F0.wireOp",EDGE,"E7.20.1"),sQuery(id+"F0.wireOp",EDGE,"E7.20.2"),sQuery(id+"F0.wireOp",EDGE,"E7.20.3"),sQuery(id+"F0.wireOp",EDGE,"E7.20.4"),sQuery(id+"F0.wireOp",EDGE,"E7.20.5"),sQuery(id+"F0.wireOp",EDGE,"E7.21.0"),sQuery(id+"F0.wireOp",EDGE,"E7.21.1"),sQuery(id+"F0.wireOp",EDGE,"E7.21.2"),sQuery(id+"F0.wireOp",EDGE,"E7.21.3"),sQuery(id+"F0.wireOp",EDGE,"E7.21.4"),sQuery(id+"F0.wireOp",EDGE,"E7.21.5"),sQuery(id+"F0.wireOp",EDGE,"E7.22.0"),sQuery(id+"F0.wireOp",EDGE,"E7.22.1"),sQuery(id+"F0.wireOp",EDGE,"E7.22.2"),sQuery(id+"F0.wireOp",EDGE,"E7.22.3"),sQuery(id+"F0.wireOp",EDGE,"E7.22.4"),sQuery(id+"F0.wireOp",EDGE,"E7.22.5"),sQuery(id+"F0.wireOp",EDGE,"E7.23.0"),sQuery(id+"F0.wireOp",EDGE,"E7.23.1"),sQuery(id+"F0.wireOp",EDGE,"E7.23.2"),sQuery(id+"F0.wireOp",EDGE,"E7.23.3"),sQuery(id+"F0.wireOp",EDGE,"E7.23.4"),sQuery(id+"F0.wireOp",EDGE,"E7.23.5"),sQuery(id+"F0.wireOp",EDGE,"E7.24.0"),sQuery(id+"F0.wireOp",EDGE,"E7.24.1"),sQuery(id+"F0.wireOp",EDGE,"E7.24.2"),sQuery(id+"F0.wireOp",EDGE,"E7.24.3"),sQuery(id+"F0.wireOp",EDGE,"E7.24.4"),sQuery(id+"F0.wireOp",EDGE,"E7.24.5"),sQuery(id+"F0.wireOp",EDGE,"E7.25.0"),sQuery(id+"F0.wireOp",EDGE,"E7.25.1"),sQuery(id+"F0.wireOp",EDGE,"E7.25.2"),sQuery(id+"F0.wireOp",EDGE,"E7.25.3"),sQuery(id+"F0.wireOp",EDGE,"E7.25.4"),sQuery(id+"F0.wireOp",EDGE,"E7.25.5"),sQuery(id+"F0.wireOp",EDGE,"E7.26.0"),sQuery(id+"F0.wireOp",EDGE,"E7.26.1"),sQuery(id+"F0.wireOp",EDGE,"E7.26.2"),sQuery(id+"F0.wireOp",EDGE,"E7.26.3"),sQuery(id+"F0.wireOp",EDGE,"E7.26.4"),sQuery(id+"F0.wireOp",EDGE,"E7.26.5"),sQuery(id+"F0.wireOp",EDGE,"E7.27.0"),sQuery(id+"F0.wireOp",EDGE,"E7.27.1"),sQuery(id+"F0.wireOp",EDGE,"E7.27.2"),sQuery(id+"F0.wireOp",EDGE,"E7.27.3"),sQuery(id+"F0.wireOp",EDGE,"E7.27.4"),sQuery(id+"F0.wireOp",EDGE,"E7.27.5"),sQuery(id+"F0.wireOp",EDGE,"E7.28.0"),sQuery(id+"F0.wireOp",EDGE,"E7.28.1"),sQuery(id+"F0.wireOp",EDGE,"E7.28.2"),sQuery(id+"F0.wireOp",EDGE,"E7.28.3"),sQuery(id+"F0.wireOp",EDGE,"E7.28.4"),sQuery(id+"F0.wireOp",EDGE,"E7.28.5"),sQuery(id+"F0.wireOp",EDGE,"E7.29.0"),sQuery(id+"F0.wireOp",EDGE,"E7.29.1"),sQuery(id+"F0.wireOp",EDGE,"E7.29.2"),sQuery(id+"F0.wireOp",EDGE,"E7.29.3"),sQuery(id+"F0.wireOp",EDGE,"E7.29.4"),sQuery(id+"F0.wireOp",EDGE,"E7.29.5"),sQuery(id+"F0.wireOp",EDGE,"E7.30.0"),sQuery(id+"F0.wireOp",EDGE,"E7.30.1"),sQuery(id+"F0.wireOp",EDGE,"E7.30.2"),sQuery(id+"F0.wireOp",EDGE,"E7.30.3"),sQuery(id+"F0.wireOp",EDGE,"E7.30.4"),sQuery(id+"F0.wireOp",EDGE,"E7.30.5"),sQuery(id+"F0.wireOp",EDGE,"E7.31.0"),sQuery(id+"F0.wireOp",EDGE,"E7.31.1"),sQuery(id+"F0.wireOp",EDGE,"E7.31.2"),sQuery(id+"F0.wireOp",EDGE,"E7.31.3"),sQuery(id+"F0.wireOp",EDGE,"E7.31.4"),sQuery(id+"F0.wireOp",EDGE,"E7.31.5"),sQuery(id+"F0.wireOp",EDGE,"E7.32.0"),sQuery(id+"F0.wireOp",EDGE,"E7.32.1"),sQuery(id+"F0.wireOp",EDGE,"E7.32.2"),sQuery(id+"F0.wireOp",EDGE,"E7.32.3"),sQuery(id+"F0.wireOp",EDGE,"E7.32.4"),sQuery(id+"F0.wireOp",EDGE,"E7.32.5"),sQuery(id+"F0.wireOp",EDGE,"E7.33.0"),sQuery(id+"F0.wireOp",EDGE,"E7.33.1"),sQuery(id+"F0.wireOp",EDGE,"E7.33.2"),sQuery(id+"F0.wireOp",EDGE,"E7.33.3"),sQuery(id+"F0.wireOp",EDGE,"E7.33.4"),sQuery(id+"F0.wireOp",EDGE,"E7.33.5"),sQuery(id+"F0.wireOp",EDGE,"E7.34.0"),sQuery(id+"F0.wireOp",EDGE,"E7.34.1"),sQuery(id+"F0.wireOp",EDGE,"E7.34.2"),sQuery(id+"F0.wireOp",EDGE,"E7.34.3"),sQuery(id+"F0.wireOp",EDGE,"E7.34.4"),sQuery(id+"F0.wireOp",EDGE,"E7.34.5"),sQuery(id+"F0.wireOp",EDGE,"E7.35.0"),sQuery(id+"F0.wireOp",EDGE,"E7.35.1"),sQuery(id+"F0.wireOp",EDGE,"E7.35.2"),sQuery(id+"F0.wireOp",EDGE,"E7.35.3"),sQuery(id+"F0.wireOp",EDGE,"E7.35.4"),sQuery(id+"F0.wireOp",EDGE,"E7.35.5"),sQuery(id+"F0.wireOp",EDGE,"E7.36.0"),sQuery(id+"F0.wireOp",EDGE,"E7.36.1"),sQuery(id+"F0.wireOp",EDGE,"E7.36.2"),sQuery(id+"F0.wireOp",EDGE,"E7.36.3"),sQuery(id+"F0.wireOp",EDGE,"E7.36.4"),sQuery(id+"F0.wireOp",EDGE,"E7.36.5"),sQuery(id+"F0.wireOp",EDGE,"E7.37.0"),sQuery(id+"F0.wireOp",EDGE,"E7.37.1"),sQuery(id+"F0.wireOp",EDGE,"E7.37.2"),sQuery(id+"F0.wireOp",EDGE,"E7.37.3"),sQuery(id+"F0.wireOp",EDGE,"E7.37.4"),sQuery(id+"F0.wireOp",EDGE,"E7.37.5"),sQuery(id+"F0.wireOp",EDGE,"E7.38.0"),sQuery(id+"F0.wireOp",EDGE,"E7.38.1"),sQuery(id+"F0.wireOp",EDGE,"E7.38.2"),sQuery(id+"F0.wireOp",EDGE,"E7.38.3"),sQuery(id+"F0.wireOp",EDGE,"E7.38.4"),sQuery(id+"F0.wireOp",EDGE,"E7.38.5"),sQuery(id+"F0.wireOp",EDGE,"E7.39.0"),sQuery(id+"F0.wireOp",EDGE,"E7.39.1"),sQuery(id+"F0.wireOp",EDGE,"E7.39.2"),sQuery(id+"F0.wireOp",EDGE,"E7.39.3"),sQuery(id+"F0.wireOp",EDGE,"E7.39.4"),sQuery(id+"F0.wireOp",EDGE,"E7.39.5"),sQuery(id+"F0.wireOp",EDGE,"E7.40.0"),sQuery(id+"F0.wireOp",EDGE,"E7.40.1"),sQuery(id+"F0.wireOp",EDGE,"E7.40.2"),sQuery(id+"F0.wireOp",EDGE,"E7.40.3"),sQuery(id+"F0.wireOp",EDGE,"E7.40.4"),sQuery(id+"F0.wireOp",EDGE,"E7.40.5"),sQuery(id+"F0.wireOp",EDGE,"E7.41.0"),sQuery(id+"F0.wireOp",EDGE,"E7.41.1"),sQuery(id+"F0.wireOp",EDGE,"E7.41.2"),sQuery(id+"F0.wireOp",EDGE,"E7.41.3"),sQuery(id+"F0.wireOp",EDGE,"E7.41.4"),sQuery(id+"F0.wireOp",EDGE,"E7.41.5"),sQuery(id+"F0.wireOp",EDGE,"E7.42.0"),sQuery(id+"F0.wireOp",EDGE,"E7.42.1"),sQuery(id+"F0.wireOp",EDGE,"E7.42.2"),sQuery(id+"F0.wireOp",EDGE,"E7.42.3"),sQuery(id+"F0.wireOp",EDGE,"E7.42.4"),sQuery(id+"F0.wireOp",EDGE,"E7.42.5"),sQuery(id+"F0.wireOp",EDGE,"E7.43.0"),sQuery(id+"F0.wireOp",EDGE,"E7.43.1"),sQuery(id+"F0.wireOp",EDGE,"E7.43.2"),sQuery(id+"F0.wireOp",EDGE,"E7.43.3"),sQuery(id+"F0.wireOp",EDGE,"E7.43.4"),sQuery(id+"F0.wireOp",EDGE,"E7.43.5")])],"isStart":false})]});}
            var Q22;
            {var subQ0=sQuery(id+"F0.wireOp",EDGE,"E7.2.0");Q22=makeQuery(id+"F2.opChamfer","BLEND_EDGE",EDGE,{"blendedFrom":[makeQuery(id+"F1.opExtrude","CAP_EDGE",EDGE,{"disambiguationData":[OSD([subQ0])],"isStart":true}),makeQuery(id+"F1.opExtrude","CAP_FACE",FACE,{"disambiguationData":[OSD([sQuery(id+"F0.wireOp",EDGE,"E1"),sQuery(id+"F0.wireOp",EDGE,"E2"),sQuery(id+"F0.wireOp",EDGE,"E3"),sQuery(id+"F0.wireOp",EDGE,"E4"),sQuery(id+"F0.wireOp",EDGE,"E5"),sQuery(id+"F0.wireOp",EDGE,"E6"),sQuery(id+"F0.wireOp",EDGE,"E7.1.0"),sQuery(id+"F0.wireOp",EDGE,"E7.1.1"),sQuery(id+"F0.wireOp",EDGE,"E7.1.2"),sQuery(id+"F0.wireOp",EDGE,"E7.1.3"),sQuery(id+"F0.wireOp",EDGE,"E7.1.4"),sQuery(id+"F0.wireOp",EDGE,"E7.1.5"),subQ0,sQuery(id+"F0.wireOp",EDGE,"E7.2.1"),sQuery(id+"F0.wireOp",EDGE,"E7.2.2"),sQuery(id+"F0.wireOp",EDGE,"E7.2.3"),sQuery(id+"F0.wireOp",EDGE,"E7.2.4"),sQuery(id+"F0.wireOp",EDGE,"E7.2.5"),sQuery(id+"F0.wireOp",EDGE,"E7.3.0"),sQuery(id+"F0.wireOp",EDGE,"E7.3.1"),sQuery(id+"F0.wireOp",EDGE,"E7.3.2"),sQuery(id+"F0.wireOp",EDGE,"E7.3.3"),sQuery(id+"F0.wireOp",EDGE,"E7.3.4"),sQuery(id+"F0.wireOp",EDGE,"E7.3.5"),sQuery(id+"F0.wireOp",EDGE,"E7.4.0"),sQuery(id+"F0.wireOp",EDGE,"E7.4.1"),sQuery(id+"F0.wireOp",EDGE,"E7.4.2"),sQuery(id+"F0.wireOp",EDGE,"E7.4.3"),sQuery(id+"F0.wireOp",EDGE,"E7.4.4"),sQuery(id+"F0.wireOp",EDGE,"E7.4.5"),sQuery(id+"F0.wireOp",EDGE,"E7.5.0"),sQuery(id+"F0.wireOp",EDGE,"E7.5.1"),sQuery(id+"F0.wireOp",EDGE,"E7.5.2"),sQuery(id+"F0.wireOp",EDGE,"E7.5.3"),sQuery(id+"F0.wireOp",EDGE,"E7.5.4"),sQuery(id+"F0.wireOp",EDGE,"E7.5.5"),sQuery(id+"F0.wireOp",EDGE,"E7.6.0"),sQuery(id+"F0.wireOp",EDGE,"E7.6.1"),sQuery(id+"F0.wireOp",EDGE,"E7.6.2"),sQuery(id+"F0.wireOp",EDGE,"E7.6.3"),sQuery(id+"F0.wireOp",EDGE,"E7.6.4"),sQuery(id+"F0.wireOp",EDGE,"E7.6.5"),sQuery(id+"F0.wireOp",EDGE,"E7.7.0"),sQuery(id+"F0.wireOp",EDGE,"E7.7.1"),sQuery(id+"F0.wireOp",EDGE,"E7.7.2"),sQuery(id+"F0.wireOp",EDGE,"E7.7.3"),sQuery(id+"F0.wireOp",EDGE,"E7.7.4"),sQuery(id+"F0.wireOp",EDGE,"E7.7.5"),sQuery(id+"F0.wireOp",EDGE,"E7.8.0"),sQuery(id+"F0.wireOp",EDGE,"E7.8.1"),sQuery(id+"F0.wireOp",EDGE,"E7.8.2"),sQuery(id+"F0.wireOp",EDGE,"E7.8.3"),sQuery(id+"F0.wireOp",EDGE,"E7.8.4"),sQuery(id+"F0.wireOp",EDGE,"E7.8.5"),sQuery(id+"F0.wireOp",EDGE,"E7.9.0"),sQuery(id+"F0.wireOp",EDGE,"E7.9.1"),sQuery(id+"F0.wireOp",EDGE,"E7.9.2"),sQuery(id+"F0.wireOp",EDGE,"E7.9.3"),sQuery(id+"F0.wireOp",EDGE,"E7.9.4"),sQuery(id+"F0.wireOp",EDGE,"E7.9.5"),sQuery(id+"F0.wireOp",EDGE,"E7.10.0"),sQuery(id+"F0.wireOp",EDGE,"E7.10.1"),sQuery(id+"F0.wireOp",EDGE,"E7.10.2"),sQuery(id+"F0.wireOp",EDGE,"E7.10.3"),sQuery(id+"F0.wireOp",EDGE,"E7.10.4"),sQuery(id+"F0.wireOp",EDGE,"E7.10.5"),sQuery(id+"F0.wireOp",EDGE,"E7.11.0"),sQuery(id+"F0.wireOp",EDGE,"E7.11.1"),sQuery(id+"F0.wireOp",EDGE,"E7.11.2"),sQuery(id+"F0.wireOp",EDGE,"E7.11.3"),sQuery(id+"F0.wireOp",EDGE,"E7.11.4"),sQuery(id+"F0.wireOp",EDGE,"E7.11.5"),sQuery(id+"F0.wireOp",EDGE,"E7.12.0"),sQuery(id+"F0.wireOp",EDGE,"E7.12.1"),sQuery(id+"F0.wireOp",EDGE,"E7.12.2"),sQuery(id+"F0.wireOp",EDGE,"E7.12.3"),sQuery(id+"F0.wireOp",EDGE,"E7.12.4"),sQuery(id+"F0.wireOp",EDGE,"E7.12.5"),sQuery(id+"F0.wireOp",EDGE,"E7.13.0"),sQuery(id+"F0.wireOp",EDGE,"E7.13.1"),sQuery(id+"F0.wireOp",EDGE,"E7.13.2"),sQuery(id+"F0.wireOp",EDGE,"E7.13.3"),sQuery(id+"F0.wireOp",EDGE,"E7.13.4"),sQuery(id+"F0.wireOp",EDGE,"E7.13.5"),sQuery(id+"F0.wireOp",EDGE,"E7.14.0"),sQuery(id+"F0.wireOp",EDGE,"E7.14.1"),sQuery(id+"F0.wireOp",EDGE,"E7.14.2"),sQuery(id+"F0.wireOp",EDGE,"E7.14.3"),sQuery(id+"F0.wireOp",EDGE,"E7.14.4"),sQuery(id+"F0.wireOp",EDGE,"E7.14.5"),sQuery(id+"F0.wireOp",EDGE,"E7.15.0"),sQuery(id+"F0.wireOp",EDGE,"E7.15.1"),sQuery(id+"F0.wireOp",EDGE,"E7.15.2"),sQuery(id+"F0.wireOp",EDGE,"E7.15.3"),sQuery(id+"F0.wireOp",EDGE,"E7.15.4"),sQuery(id+"F0.wireOp",EDGE,"E7.15.5"),sQuery(id+"F0.wireOp",EDGE,"E7.16.0"),sQuery(id+"F0.wireOp",EDGE,"E7.16.1"),sQuery(id+"F0.wireOp",EDGE,"E7.16.2"),sQuery(id+"F0.wireOp",EDGE,"E7.16.3"),sQuery(id+"F0.wireOp",EDGE,"E7.16.4"),sQuery(id+"F0.wireOp",EDGE,"E7.16.5"),sQuery(id+"F0.wireOp",EDGE,"E7.17.0"),sQuery(id+"F0.wireOp",EDGE,"E7.17.1"),sQuery(id+"F0.wireOp",EDGE,"E7.17.2"),sQuery(id+"F0.wireOp",EDGE,"E7.17.3"),sQuery(id+"F0.wireOp",EDGE,"E7.17.4"),sQuery(id+"F0.wireOp",EDGE,"E7.17.5"),sQuery(id+"F0.wireOp",EDGE,"E7.18.0"),sQuery(id+"F0.wireOp",EDGE,"E7.18.1"),sQuery(id+"F0.wireOp",EDGE,"E7.18.2"),sQuery(id+"F0.wireOp",EDGE,"E7.18.3"),sQuery(id+"F0.wireOp",EDGE,"E7.18.4"),sQuery(id+"F0.wireOp",EDGE,"E7.18.5"),sQuery(id+"F0.wireOp",EDGE,"E7.19.0"),sQuery(id+"F0.wireOp",EDGE,"E7.19.1"),sQuery(id+"F0.wireOp",EDGE,"E7.19.2"),sQuery(id+"F0.wireOp",EDGE,"E7.19.3"),sQuery(id+"F0.wireOp",EDGE,"E7.19.4"),sQuery(id+"F0.wireOp",EDGE,"E7.19.5"),sQuery(id+"F0.wireOp",EDGE,"E7.20.0"),sQuery(id+"F0.wireOp",EDGE,"E7.20.1"),sQuery(id+"F0.wireOp",EDGE,"E7.20.2"),sQuery(id+"F0.wireOp",EDGE,"E7.20.3"),sQuery(id+"F0.wireOp",EDGE,"E7.20.4"),sQuery(id+"F0.wireOp",EDGE,"E7.20.5"),sQuery(id+"F0.wireOp",EDGE,"E7.21.0"),sQuery(id+"F0.wireOp",EDGE,"E7.21.1"),sQuery(id+"F0.wireOp",EDGE,"E7.21.2"),sQuery(id+"F0.wireOp",EDGE,"E7.21.3"),sQuery(id+"F0.wireOp",EDGE,"E7.21.4"),sQuery(id+"F0.wireOp",EDGE,"E7.21.5"),sQuery(id+"F0.wireOp",EDGE,"E7.22.0"),sQuery(id+"F0.wireOp",EDGE,"E7.22.1"),sQuery(id+"F0.wireOp",EDGE,"E7.22.2"),sQuery(id+"F0.wireOp",EDGE,"E7.22.3"),sQuery(id+"F0.wireOp",EDGE,"E7.22.4"),sQuery(id+"F0.wireOp",EDGE,"E7.22.5"),sQuery(id+"F0.wireOp",EDGE,"E7.23.0"),sQuery(id+"F0.wireOp",EDGE,"E7.23.1"),sQuery(id+"F0.wireOp",EDGE,"E7.23.2"),sQuery(id+"F0.wireOp",EDGE,"E7.23.3"),sQuery(id+"F0.wireOp",EDGE,"E7.23.4"),sQuery(id+"F0.wireOp",EDGE,"E7.23.5"),sQuery(id+"F0.wireOp",EDGE,"E7.24.0"),sQuery(id+"F0.wireOp",EDGE,"E7.24.1"),sQuery(id+"F0.wireOp",EDGE,"E7.24.2"),sQuery(id+"F0.wireOp",EDGE,"E7.24.3"),sQuery(id+"F0.wireOp",EDGE,"E7.24.4"),sQuery(id+"F0.wireOp",EDGE,"E7.24.5"),sQuery(id+"F0.wireOp",EDGE,"E7.25.0"),sQuery(id+"F0.wireOp",EDGE,"E7.25.1"),sQuery(id+"F0.wireOp",EDGE,"E7.25.2"),sQuery(id+"F0.wireOp",EDGE,"E7.25.3"),sQuery(id+"F0.wireOp",EDGE,"E7.25.4"),sQuery(id+"F0.wireOp",EDGE,"E7.25.5"),sQuery(id+"F0.wireOp",EDGE,"E7.26.0"),sQuery(id+"F0.wireOp",EDGE,"E7.26.1"),sQuery(id+"F0.wireOp",EDGE,"E7.26.2"),sQuery(id+"F0.wireOp",EDGE,"E7.26.3"),sQuery(id+"F0.wireOp",EDGE,"E7.26.4"),sQuery(id+"F0.wireOp",EDGE,"E7.26.5"),sQuery(id+"F0.wireOp",EDGE,"E7.27.0"),sQuery(id+"F0.wireOp",EDGE,"E7.27.1"),sQuery(id+"F0.wireOp",EDGE,"E7.27.2"),sQuery(id+"F0.wireOp",EDGE,"E7.27.3"),sQuery(id+"F0.wireOp",EDGE,"E7.27.4"),sQuery(id+"F0.wireOp",EDGE,"E7.27.5"),sQuery(id+"F0.wireOp",EDGE,"E7.28.0"),sQuery(id+"F0.wireOp",EDGE,"E7.28.1"),sQuery(id+"F0.wireOp",EDGE,"E7.28.2"),sQuery(id+"F0.wireOp",EDGE,"E7.28.3"),sQuery(id+"F0.wireOp",EDGE,"E7.28.4"),sQuery(id+"F0.wireOp",EDGE,"E7.28.5"),sQuery(id+"F0.wireOp",EDGE,"E7.29.0"),sQuery(id+"F0.wireOp",EDGE,"E7.29.1"),sQuery(id+"F0.wireOp",EDGE,"E7.29.2"),sQuery(id+"F0.wireOp",EDGE,"E7.29.3"),sQuery(id+"F0.wireOp",EDGE,"E7.29.4"),sQuery(id+"F0.wireOp",EDGE,"E7.29.5"),sQuery(id+"F0.wireOp",EDGE,"E7.30.0"),sQuery(id+"F0.wireOp",EDGE,"E7.30.1"),sQuery(id+"F0.wireOp",EDGE,"E7.30.2"),sQuery(id+"F0.wireOp",EDGE,"E7.30.3"),sQuery(id+"F0.wireOp",EDGE,"E7.30.4"),sQuery(id+"F0.wireOp",EDGE,"E7.30.5"),sQuery(id+"F0.wireOp",EDGE,"E7.31.0"),sQuery(id+"F0.wireOp",EDGE,"E7.31.1"),sQuery(id+"F0.wireOp",EDGE,"E7.31.2"),sQuery(id+"F0.wireOp",EDGE,"E7.31.3"),sQuery(id+"F0.wireOp",EDGE,"E7.31.4"),sQuery(id+"F0.wireOp",EDGE,"E7.31.5"),sQuery(id+"F0.wireOp",EDGE,"E7.32.0"),sQuery(id+"F0.wireOp",EDGE,"E7.32.1"),sQuery(id+"F0.wireOp",EDGE,"E7.32.2"),sQuery(id+"F0.wireOp",EDGE,"E7.32.3"),sQuery(id+"F0.wireOp",EDGE,"E7.32.4"),sQuery(id+"F0.wireOp",EDGE,"E7.32.5"),sQuery(id+"F0.wireOp",EDGE,"E7.33.0"),sQuery(id+"F0.wireOp",EDGE,"E7.33.1"),sQuery(id+"F0.wireOp",EDGE,"E7.33.2"),sQuery(id+"F0.wireOp",EDGE,"E7.33.3"),sQuery(id+"F0.wireOp",EDGE,"E7.33.4"),sQuery(id+"F0.wireOp",EDGE,"E7.33.5"),sQuery(id+"F0.wireOp",EDGE,"E7.34.0"),sQuery(id+"F0.wireOp",EDGE,"E7.34.1"),sQuery(id+"F0.wireOp",EDGE,"E7.34.2"),sQuery(id+"F0.wireOp",EDGE,"E7.34.3"),sQuery(id+"F0.wireOp",EDGE,"E7.34.4"),sQuery(id+"F0.wireOp",EDGE,"E7.34.5"),sQuery(id+"F0.wireOp",EDGE,"E7.35.0"),sQuery(id+"F0.wireOp",EDGE,"E7.35.1"),sQuery(id+"F0.wireOp",EDGE,"E7.35.2"),sQuery(id+"F0.wireOp",EDGE,"E7.35.3"),sQuery(id+"F0.wireOp",EDGE,"E7.35.4"),sQuery(id+"F0.wireOp",EDGE,"E7.35.5"),sQuery(id+"F0.wireOp",EDGE,"E7.36.0"),sQuery(id+"F0.wireOp",EDGE,"E7.36.1"),sQuery(id+"F0.wireOp",EDGE,"E7.36.2"),sQuery(id+"F0.wireOp",EDGE,"E7.36.3"),sQuery(id+"F0.wireOp",EDGE,"E7.36.4"),sQuery(id+"F0.wireOp",EDGE,"E7.36.5"),sQuery(id+"F0.wireOp",EDGE,"E7.37.0"),sQuery(id+"F0.wireOp",EDGE,"E7.37.1"),sQuery(id+"F0.wireOp",EDGE,"E7.37.2"),sQuery(id+"F0.wireOp",EDGE,"E7.37.3"),sQuery(id+"F0.wireOp",EDGE,"E7.37.4"),sQuery(id+"F0.wireOp",EDGE,"E7.37.5"),sQuery(id+"F0.wireOp",EDGE,"E7.38.0"),sQuery(id+"F0.wireOp",EDGE,"E7.38.1"),sQuery(id+"F0.wireOp",EDGE,"E7.38.2"),sQuery(id+"F0.wireOp",EDGE,"E7.38.3"),sQuery(id+"F0.wireOp",EDGE,"E7.38.4"),sQuery(id+"F0.wireOp",EDGE,"E7.38.5"),sQuery(id+"F0.wireOp",EDGE,"E7.39.0"),sQuery(id+"F0.wireOp",EDGE,"E7.39.1"),sQuery(id+"F0.wireOp",EDGE,"E7.39.2"),sQuery(id+"F0.wireOp",EDGE,"E7.39.3"),sQuery(id+"F0.wireOp",EDGE,"E7.39.4"),sQuery(id+"F0.wireOp",EDGE,"E7.39.5"),sQuery(id+"F0.wireOp",EDGE,"E7.40.0"),sQuery(id+"F0.wireOp",EDGE,"E7.40.1"),sQuery(id+"F0.wireOp",EDGE,"E7.40.2"),sQuery(id+"F0.wireOp",EDGE,"E7.40.3"),sQuery(id+"F0.wireOp",EDGE,"E7.40.4"),sQuery(id+"F0.wireOp",EDGE,"E7.40.5"),sQuery(id+"F0.wireOp",EDGE,"E7.41.0"),sQuery(id+"F0.wireOp",EDGE,"E7.41.1"),sQuery(id+"F0.wireOp",EDGE,"E7.41.2"),sQuery(id+"F0.wireOp",EDGE,"E7.41.3"),sQuery(id+"F0.wireOp",EDGE,"E7.41.4"),sQuery(id+"F0.wireOp",EDGE,"E7.41.5"),sQuery(id+"F0.wireOp",EDGE,"E7.42.0"),sQuery(id+"F0.wireOp",EDGE,"E7.42.1"),sQuery(id+"F0.wireOp",EDGE,"E7.42.2"),sQuery(id+"F0.wireOp",EDGE,"E7.42.3"),sQuery(id+"F0.wireOp",EDGE,"E7.42.4"),sQuery(id+"F0.wireOp",EDGE,"E7.42.5"),sQuery(id+"F0.wireOp",EDGE,"E7.43.0"),sQuery(id+"F0.wireOp",EDGE,"E7.43.1"),sQuery(id+"F0.wireOp",EDGE,"E7.43.2"),sQuery(id+"F0.wireOp",EDGE,"E7.43.3"),sQuery(id+"F0.wireOp",EDGE,"E7.43.4"),sQuery(id+"F0.wireOp",EDGE,"E7.43.5")])],"isStart":true})],"blendedInto":[makeQuery(id+"F1.opExtrude","CAP_FACE",FACE,{"disambiguationData":[OSD([sQuery(id+"F0.wireOp",EDGE,"E1"),sQuery(id+"F0.wireOp",EDGE,"E2"),sQuery(id+"F0.wireOp",EDGE,"E3"),sQuery(id+"F0.wireOp",EDGE,"E4"),sQuery(id+"F0.wireOp",EDGE,"E5"),sQuery(id+"F0.wireOp",EDGE,"E6"),sQuery(id+"F0.wireOp",EDGE,"E7.1.0"),sQuery(id+"F0.wireOp",EDGE,"E7.1.1"),sQuery(id+"F0.wireOp",EDGE,"E7.1.2"),sQuery(id+"F0.wireOp",EDGE,"E7.1.3"),sQuery(id+"F0.wireOp",EDGE,"E7.1.4"),sQuery(id+"F0.wireOp",EDGE,"E7.1.5"),subQ0,sQuery(id+"F0.wireOp",EDGE,"E7.2.1"),sQuery(id+"F0.wireOp",EDGE,"E7.2.2"),sQuery(id+"F0.wireOp",EDGE,"E7.2.3"),sQuery(id+"F0.wireOp",EDGE,"E7.2.4"),sQuery(id+"F0.wireOp",EDGE,"E7.2.5"),sQuery(id+"F0.wireOp",EDGE,"E7.3.0"),sQuery(id+"F0.wireOp",EDGE,"E7.3.1"),sQuery(id+"F0.wireOp",EDGE,"E7.3.2"),sQuery(id+"F0.wireOp",EDGE,"E7.3.3"),sQuery(id+"F0.wireOp",EDGE,"E7.3.4"),sQuery(id+"F0.wireOp",EDGE,"E7.3.5"),sQuery(id+"F0.wireOp",EDGE,"E7.4.0"),sQuery(id+"F0.wireOp",EDGE,"E7.4.1"),sQuery(id+"F0.wireOp",EDGE,"E7.4.2"),sQuery(id+"F0.wireOp",EDGE,"E7.4.3"),sQuery(id+"F0.wireOp",EDGE,"E7.4.4"),sQuery(id+"F0.wireOp",EDGE,"E7.4.5"),sQuery(id+"F0.wireOp",EDGE,"E7.5.0"),sQuery(id+"F0.wireOp",EDGE,"E7.5.1"),sQuery(id+"F0.wireOp",EDGE,"E7.5.2"),sQuery(id+"F0.wireOp",EDGE,"E7.5.3"),sQuery(id+"F0.wireOp",EDGE,"E7.5.4"),sQuery(id+"F0.wireOp",EDGE,"E7.5.5"),sQuery(id+"F0.wireOp",EDGE,"E7.6.0"),sQuery(id+"F0.wireOp",EDGE,"E7.6.1"),sQuery(id+"F0.wireOp",EDGE,"E7.6.2"),sQuery(id+"F0.wireOp",EDGE,"E7.6.3"),sQuery(id+"F0.wireOp",EDGE,"E7.6.4"),sQuery(id+"F0.wireOp",EDGE,"E7.6.5"),sQuery(id+"F0.wireOp",EDGE,"E7.7.0"),sQuery(id+"F0.wireOp",EDGE,"E7.7.1"),sQuery(id+"F0.wireOp",EDGE,"E7.7.2"),sQuery(id+"F0.wireOp",EDGE,"E7.7.3"),sQuery(id+"F0.wireOp",EDGE,"E7.7.4"),sQuery(id+"F0.wireOp",EDGE,"E7.7.5"),sQuery(id+"F0.wireOp",EDGE,"E7.8.0"),sQuery(id+"F0.wireOp",EDGE,"E7.8.1"),sQuery(id+"F0.wireOp",EDGE,"E7.8.2"),sQuery(id+"F0.wireOp",EDGE,"E7.8.3"),sQuery(id+"F0.wireOp",EDGE,"E7.8.4"),sQuery(id+"F0.wireOp",EDGE,"E7.8.5"),sQuery(id+"F0.wireOp",EDGE,"E7.9.0"),sQuery(id+"F0.wireOp",EDGE,"E7.9.1"),sQuery(id+"F0.wireOp",EDGE,"E7.9.2"),sQuery(id+"F0.wireOp",EDGE,"E7.9.3"),sQuery(id+"F0.wireOp",EDGE,"E7.9.4"),sQuery(id+"F0.wireOp",EDGE,"E7.9.5"),sQuery(id+"F0.wireOp",EDGE,"E7.10.0"),sQuery(id+"F0.wireOp",EDGE,"E7.10.1"),sQuery(id+"F0.wireOp",EDGE,"E7.10.2"),sQuery(id+"F0.wireOp",EDGE,"E7.10.3"),sQuery(id+"F0.wireOp",EDGE,"E7.10.4"),sQuery(id+"F0.wireOp",EDGE,"E7.10.5"),sQuery(id+"F0.wireOp",EDGE,"E7.11.0"),sQuery(id+"F0.wireOp",EDGE,"E7.11.1"),sQuery(id+"F0.wireOp",EDGE,"E7.11.2"),sQuery(id+"F0.wireOp",EDGE,"E7.11.3"),sQuery(id+"F0.wireOp",EDGE,"E7.11.4"),sQuery(id+"F0.wireOp",EDGE,"E7.11.5"),sQuery(id+"F0.wireOp",EDGE,"E7.12.0"),sQuery(id+"F0.wireOp",EDGE,"E7.12.1"),sQuery(id+"F0.wireOp",EDGE,"E7.12.2"),sQuery(id+"F0.wireOp",EDGE,"E7.12.3"),sQuery(id+"F0.wireOp",EDGE,"E7.12.4"),sQuery(id+"F0.wireOp",EDGE,"E7.12.5"),sQuery(id+"F0.wireOp",EDGE,"E7.13.0"),sQuery(id+"F0.wireOp",EDGE,"E7.13.1"),sQuery(id+"F0.wireOp",EDGE,"E7.13.2"),sQuery(id+"F0.wireOp",EDGE,"E7.13.3"),sQuery(id+"F0.wireOp",EDGE,"E7.13.4"),sQuery(id+"F0.wireOp",EDGE,"E7.13.5"),sQuery(id+"F0.wireOp",EDGE,"E7.14.0"),sQuery(id+"F0.wireOp",EDGE,"E7.14.1"),sQuery(id+"F0.wireOp",EDGE,"E7.14.2"),sQuery(id+"F0.wireOp",EDGE,"E7.14.3"),sQuery(id+"F0.wireOp",EDGE,"E7.14.4"),sQuery(id+"F0.wireOp",EDGE,"E7.14.5"),sQuery(id+"F0.wireOp",EDGE,"E7.15.0"),sQuery(id+"F0.wireOp",EDGE,"E7.15.1"),sQuery(id+"F0.wireOp",EDGE,"E7.15.2"),sQuery(id+"F0.wireOp",EDGE,"E7.15.3"),sQuery(id+"F0.wireOp",EDGE,"E7.15.4"),sQuery(id+"F0.wireOp",EDGE,"E7.15.5"),sQuery(id+"F0.wireOp",EDGE,"E7.16.0"),sQuery(id+"F0.wireOp",EDGE,"E7.16.1"),sQuery(id+"F0.wireOp",EDGE,"E7.16.2"),sQuery(id+"F0.wireOp",EDGE,"E7.16.3"),sQuery(id+"F0.wireOp",EDGE,"E7.16.4"),sQuery(id+"F0.wireOp",EDGE,"E7.16.5"),sQuery(id+"F0.wireOp",EDGE,"E7.17.0"),sQuery(id+"F0.wireOp",EDGE,"E7.17.1"),sQuery(id+"F0.wireOp",EDGE,"E7.17.2"),sQuery(id+"F0.wireOp",EDGE,"E7.17.3"),sQuery(id+"F0.wireOp",EDGE,"E7.17.4"),sQuery(id+"F0.wireOp",EDGE,"E7.17.5"),sQuery(id+"F0.wireOp",EDGE,"E7.18.0"),sQuery(id+"F0.wireOp",EDGE,"E7.18.1"),sQuery(id+"F0.wireOp",EDGE,"E7.18.2"),sQuery(id+"F0.wireOp",EDGE,"E7.18.3"),sQuery(id+"F0.wireOp",EDGE,"E7.18.4"),sQuery(id+"F0.wireOp",EDGE,"E7.18.5"),sQuery(id+"F0.wireOp",EDGE,"E7.19.0"),sQuery(id+"F0.wireOp",EDGE,"E7.19.1"),sQuery(id+"F0.wireOp",EDGE,"E7.19.2"),sQuery(id+"F0.wireOp",EDGE,"E7.19.3"),sQuery(id+"F0.wireOp",EDGE,"E7.19.4"),sQuery(id+"F0.wireOp",EDGE,"E7.19.5"),sQuery(id+"F0.wireOp",EDGE,"E7.20.0"),sQuery(id+"F0.wireOp",EDGE,"E7.20.1"),sQuery(id+"F0.wireOp",EDGE,"E7.20.2"),sQuery(id+"F0.wireOp",EDGE,"E7.20.3"),sQuery(id+"F0.wireOp",EDGE,"E7.20.4"),sQuery(id+"F0.wireOp",EDGE,"E7.20.5"),sQuery(id+"F0.wireOp",EDGE,"E7.21.0"),sQuery(id+"F0.wireOp",EDGE,"E7.21.1"),sQuery(id+"F0.wireOp",EDGE,"E7.21.2"),sQuery(id+"F0.wireOp",EDGE,"E7.21.3"),sQuery(id+"F0.wireOp",EDGE,"E7.21.4"),sQuery(id+"F0.wireOp",EDGE,"E7.21.5"),sQuery(id+"F0.wireOp",EDGE,"E7.22.0"),sQuery(id+"F0.wireOp",EDGE,"E7.22.1"),sQuery(id+"F0.wireOp",EDGE,"E7.22.2"),sQuery(id+"F0.wireOp",EDGE,"E7.22.3"),sQuery(id+"F0.wireOp",EDGE,"E7.22.4"),sQuery(id+"F0.wireOp",EDGE,"E7.22.5"),sQuery(id+"F0.wireOp",EDGE,"E7.23.0"),sQuery(id+"F0.wireOp",EDGE,"E7.23.1"),sQuery(id+"F0.wireOp",EDGE,"E7.23.2"),sQuery(id+"F0.wireOp",EDGE,"E7.23.3"),sQuery(id+"F0.wireOp",EDGE,"E7.23.4"),sQuery(id+"F0.wireOp",EDGE,"E7.23.5"),sQuery(id+"F0.wireOp",EDGE,"E7.24.0"),sQuery(id+"F0.wireOp",EDGE,"E7.24.1"),sQuery(id+"F0.wireOp",EDGE,"E7.24.2"),sQuery(id+"F0.wireOp",EDGE,"E7.24.3"),sQuery(id+"F0.wireOp",EDGE,"E7.24.4"),sQuery(id+"F0.wireOp",EDGE,"E7.24.5"),sQuery(id+"F0.wireOp",EDGE,"E7.25.0"),sQuery(id+"F0.wireOp",EDGE,"E7.25.1"),sQuery(id+"F0.wireOp",EDGE,"E7.25.2"),sQuery(id+"F0.wireOp",EDGE,"E7.25.3"),sQuery(id+"F0.wireOp",EDGE,"E7.25.4"),sQuery(id+"F0.wireOp",EDGE,"E7.25.5"),sQuery(id+"F0.wireOp",EDGE,"E7.26.0"),sQuery(id+"F0.wireOp",EDGE,"E7.26.1"),sQuery(id+"F0.wireOp",EDGE,"E7.26.2"),sQuery(id+"F0.wireOp",EDGE,"E7.26.3"),sQuery(id+"F0.wireOp",EDGE,"E7.26.4"),sQuery(id+"F0.wireOp",EDGE,"E7.26.5"),sQuery(id+"F0.wireOp",EDGE,"E7.27.0"),sQuery(id+"F0.wireOp",EDGE,"E7.27.1"),sQuery(id+"F0.wireOp",EDGE,"E7.27.2"),sQuery(id+"F0.wireOp",EDGE,"E7.27.3"),sQuery(id+"F0.wireOp",EDGE,"E7.27.4"),sQuery(id+"F0.wireOp",EDGE,"E7.27.5"),sQuery(id+"F0.wireOp",EDGE,"E7.28.0"),sQuery(id+"F0.wireOp",EDGE,"E7.28.1"),sQuery(id+"F0.wireOp",EDGE,"E7.28.2"),sQuery(id+"F0.wireOp",EDGE,"E7.28.3"),sQuery(id+"F0.wireOp",EDGE,"E7.28.4"),sQuery(id+"F0.wireOp",EDGE,"E7.28.5"),sQuery(id+"F0.wireOp",EDGE,"E7.29.0"),sQuery(id+"F0.wireOp",EDGE,"E7.29.1"),sQuery(id+"F0.wireOp",EDGE,"E7.29.2"),sQuery(id+"F0.wireOp",EDGE,"E7.29.3"),sQuery(id+"F0.wireOp",EDGE,"E7.29.4"),sQuery(id+"F0.wireOp",EDGE,"E7.29.5"),sQuery(id+"F0.wireOp",EDGE,"E7.30.0"),sQuery(id+"F0.wireOp",EDGE,"E7.30.1"),sQuery(id+"F0.wireOp",EDGE,"E7.30.2"),sQuery(id+"F0.wireOp",EDGE,"E7.30.3"),sQuery(id+"F0.wireOp",EDGE,"E7.30.4"),sQuery(id+"F0.wireOp",EDGE,"E7.30.5"),sQuery(id+"F0.wireOp",EDGE,"E7.31.0"),sQuery(id+"F0.wireOp",EDGE,"E7.31.1"),sQuery(id+"F0.wireOp",EDGE,"E7.31.2"),sQuery(id+"F0.wireOp",EDGE,"E7.31.3"),sQuery(id+"F0.wireOp",EDGE,"E7.31.4"),sQuery(id+"F0.wireOp",EDGE,"E7.31.5"),sQuery(id+"F0.wireOp",EDGE,"E7.32.0"),sQuery(id+"F0.wireOp",EDGE,"E7.32.1"),sQuery(id+"F0.wireOp",EDGE,"E7.32.2"),sQuery(id+"F0.wireOp",EDGE,"E7.32.3"),sQuery(id+"F0.wireOp",EDGE,"E7.32.4"),sQuery(id+"F0.wireOp",EDGE,"E7.32.5"),sQuery(id+"F0.wireOp",EDGE,"E7.33.0"),sQuery(id+"F0.wireOp",EDGE,"E7.33.1"),sQuery(id+"F0.wireOp",EDGE,"E7.33.2"),sQuery(id+"F0.wireOp",EDGE,"E7.33.3"),sQuery(id+"F0.wireOp",EDGE,"E7.33.4"),sQuery(id+"F0.wireOp",EDGE,"E7.33.5"),sQuery(id+"F0.wireOp",EDGE,"E7.34.0"),sQuery(id+"F0.wireOp",EDGE,"E7.34.1"),sQuery(id+"F0.wireOp",EDGE,"E7.34.2"),sQuery(id+"F0.wireOp",EDGE,"E7.34.3"),sQuery(id+"F0.wireOp",EDGE,"E7.34.4"),sQuery(id+"F0.wireOp",EDGE,"E7.34.5"),sQuery(id+"F0.wireOp",EDGE,"E7.35.0"),sQuery(id+"F0.wireOp",EDGE,"E7.35.1"),sQuery(id+"F0.wireOp",EDGE,"E7.35.2"),sQuery(id+"F0.wireOp",EDGE,"E7.35.3"),sQuery(id+"F0.wireOp",EDGE,"E7.35.4"),sQuery(id+"F0.wireOp",EDGE,"E7.35.5"),sQuery(id+"F0.wireOp",EDGE,"E7.36.0"),sQuery(id+"F0.wireOp",EDGE,"E7.36.1"),sQuery(id+"F0.wireOp",EDGE,"E7.36.2"),sQuery(id+"F0.wireOp",EDGE,"E7.36.3"),sQuery(id+"F0.wireOp",EDGE,"E7.36.4"),sQuery(id+"F0.wireOp",EDGE,"E7.36.5"),sQuery(id+"F0.wireOp",EDGE,"E7.37.0"),sQuery(id+"F0.wireOp",EDGE,"E7.37.1"),sQuery(id+"F0.wireOp",EDGE,"E7.37.2"),sQuery(id+"F0.wireOp",EDGE,"E7.37.3"),sQuery(id+"F0.wireOp",EDGE,"E7.37.4"),sQuery(id+"F0.wireOp",EDGE,"E7.37.5"),sQuery(id+"F0.wireOp",EDGE,"E7.38.0"),sQuery(id+"F0.wireOp",EDGE,"E7.38.1"),sQuery(id+"F0.wireOp",EDGE,"E7.38.2"),sQuery(id+"F0.wireOp",EDGE,"E7.38.3"),sQuery(id+"F0.wireOp",EDGE,"E7.38.4"),sQuery(id+"F0.wireOp",EDGE,"E7.38.5"),sQuery(id+"F0.wireOp",EDGE,"E7.39.0"),sQuery(id+"F0.wireOp",EDGE,"E7.39.1"),sQuery(id+"F0.wireOp",EDGE,"E7.39.2"),sQuery(id+"F0.wireOp",EDGE,"E7.39.3"),sQuery(id+"F0.wireOp",EDGE,"E7.39.4"),sQuery(id+"F0.wireOp",EDGE,"E7.39.5"),sQuery(id+"F0.wireOp",EDGE,"E7.40.0"),sQuery(id+"F0.wireOp",EDGE,"E7.40.1"),sQuery(id+"F0.wireOp",EDGE,"E7.40.2"),sQuery(id+"F0.wireOp",EDGE,"E7.40.3"),sQuery(id+"F0.wireOp",EDGE,"E7.40.4"),sQuery(id+"F0.wireOp",EDGE,"E7.40.5"),sQuery(id+"F0.wireOp",EDGE,"E7.41.0"),sQuery(id+"F0.wireOp",EDGE,"E7.41.1"),sQuery(id+"F0.wireOp",EDGE,"E7.41.2"),sQuery(id+"F0.wireOp",EDGE,"E7.41.3"),sQuery(id+"F0.wireOp",EDGE,"E7.41.4"),sQuery(id+"F0.wireOp",EDGE,"E7.41.5"),sQuery(id+"F0.wireOp",EDGE,"E7.42.0"),sQuery(id+"F0.wireOp",EDGE,"E7.42.1"),sQuery(id+"F0.wireOp",EDGE,"E7.42.2"),sQuery(id+"F0.wireOp",EDGE,"E7.42.3"),sQuery(id+"F0.wireOp",EDGE,"E7.42.4"),sQuery(id+"F0.wireOp",EDGE,"E7.42.5"),sQuery(id+"F0.wireOp",EDGE,"E7.43.0"),sQuery(id+"F0.wireOp",EDGE,"E7.43.1"),sQuery(id+"F0.wireOp",EDGE,"E7.43.2"),sQuery(id+"F0.wireOp",EDGE,"E7.43.3"),sQuery(id+"F0.wireOp",EDGE,"E7.43.4"),sQuery(id+"F0.wireOp",EDGE,"E7.43.5")])],"isStart":true})]});}
            var Q23;
            {var subQ0=sQuery(id+"F0.wireOp",EDGE,"E7.4.0");Q23=makeQuery(id+"F2.opChamfer","BLEND_EDGE",EDGE,{"blendedFrom":[makeQuery(id+"F1.opExtrude","CAP_EDGE",EDGE,{"disambiguationData":[OSD([subQ0])],"isStart":true}),makeQuery(id+"F1.opExtrude","CAP_FACE",FACE,{"disambiguationData":[OSD([sQuery(id+"F0.wireOp",EDGE,"E1"),sQuery(id+"F0.wireOp",EDGE,"E2"),sQuery(id+"F0.wireOp",EDGE,"E3"),sQuery(id+"F0.wireOp",EDGE,"E4"),sQuery(id+"F0.wireOp",EDGE,"E5"),sQuery(id+"F0.wireOp",EDGE,"E6"),sQuery(id+"F0.wireOp",EDGE,"E7.1.0"),sQuery(id+"F0.wireOp",EDGE,"E7.1.1"),sQuery(id+"F0.wireOp",EDGE,"E7.1.2"),sQuery(id+"F0.wireOp",EDGE,"E7.1.3"),sQuery(id+"F0.wireOp",EDGE,"E7.1.4"),sQuery(id+"F0.wireOp",EDGE,"E7.1.5"),sQuery(id+"F0.wireOp",EDGE,"E7.2.0"),sQuery(id+"F0.wireOp",EDGE,"E7.2.1"),sQuery(id+"F0.wireOp",EDGE,"E7.2.2"),sQuery(id+"F0.wireOp",EDGE,"E7.2.3"),sQuery(id+"F0.wireOp",EDGE,"E7.2.4"),sQuery(id+"F0.wireOp",EDGE,"E7.2.5"),sQuery(id+"F0.wireOp",EDGE,"E7.3.0"),sQuery(id+"F0.wireOp",EDGE,"E7.3.1"),sQuery(id+"F0.wireOp",EDGE,"E7.3.2"),sQuery(id+"F0.wireOp",EDGE,"E7.3.3"),sQuery(id+"F0.wireOp",EDGE,"E7.3.4"),sQuery(id+"F0.wireOp",EDGE,"E7.3.5"),subQ0,sQuery(id+"F0.wireOp",EDGE,"E7.4.1"),sQuery(id+"F0.wireOp",EDGE,"E7.4.2"),sQuery(id+"F0.wireOp",EDGE,"E7.4.3"),sQuery(id+"F0.wireOp",EDGE,"E7.4.4"),sQuery(id+"F0.wireOp",EDGE,"E7.4.5"),sQuery(id+"F0.wireOp",EDGE,"E7.5.0"),sQuery(id+"F0.wireOp",EDGE,"E7.5.1"),sQuery(id+"F0.wireOp",EDGE,"E7.5.2"),sQuery(id+"F0.wireOp",EDGE,"E7.5.3"),sQuery(id+"F0.wireOp",EDGE,"E7.5.4"),sQuery(id+"F0.wireOp",EDGE,"E7.5.5"),sQuery(id+"F0.wireOp",EDGE,"E7.6.0"),sQuery(id+"F0.wireOp",EDGE,"E7.6.1"),sQuery(id+"F0.wireOp",EDGE,"E7.6.2"),sQuery(id+"F0.wireOp",EDGE,"E7.6.3"),sQuery(id+"F0.wireOp",EDGE,"E7.6.4"),sQuery(id+"F0.wireOp",EDGE,"E7.6.5"),sQuery(id+"F0.wireOp",EDGE,"E7.7.0"),sQuery(id+"F0.wireOp",EDGE,"E7.7.1"),sQuery(id+"F0.wireOp",EDGE,"E7.7.2"),sQuery(id+"F0.wireOp",EDGE,"E7.7.3"),sQuery(id+"F0.wireOp",EDGE,"E7.7.4"),sQuery(id+"F0.wireOp",EDGE,"E7.7.5"),sQuery(id+"F0.wireOp",EDGE,"E7.8.0"),sQuery(id+"F0.wireOp",EDGE,"E7.8.1"),sQuery(id+"F0.wireOp",EDGE,"E7.8.2"),sQuery(id+"F0.wireOp",EDGE,"E7.8.3"),sQuery(id+"F0.wireOp",EDGE,"E7.8.4"),sQuery(id+"F0.wireOp",EDGE,"E7.8.5"),sQuery(id+"F0.wireOp",EDGE,"E7.9.0"),sQuery(id+"F0.wireOp",EDGE,"E7.9.1"),sQuery(id+"F0.wireOp",EDGE,"E7.9.2"),sQuery(id+"F0.wireOp",EDGE,"E7.9.3"),sQuery(id+"F0.wireOp",EDGE,"E7.9.4"),sQuery(id+"F0.wireOp",EDGE,"E7.9.5"),sQuery(id+"F0.wireOp",EDGE,"E7.10.0"),sQuery(id+"F0.wireOp",EDGE,"E7.10.1"),sQuery(id+"F0.wireOp",EDGE,"E7.10.2"),sQuery(id+"F0.wireOp",EDGE,"E7.10.3"),sQuery(id+"F0.wireOp",EDGE,"E7.10.4"),sQuery(id+"F0.wireOp",EDGE,"E7.10.5"),sQuery(id+"F0.wireOp",EDGE,"E7.11.0"),sQuery(id+"F0.wireOp",EDGE,"E7.11.1"),sQuery(id+"F0.wireOp",EDGE,"E7.11.2"),sQuery(id+"F0.wireOp",EDGE,"E7.11.3"),sQuery(id+"F0.wireOp",EDGE,"E7.11.4"),sQuery(id+"F0.wireOp",EDGE,"E7.11.5"),sQuery(id+"F0.wireOp",EDGE,"E7.12.0"),sQuery(id+"F0.wireOp",EDGE,"E7.12.1"),sQuery(id+"F0.wireOp",EDGE,"E7.12.2"),sQuery(id+"F0.wireOp",EDGE,"E7.12.3"),sQuery(id+"F0.wireOp",EDGE,"E7.12.4"),sQuery(id+"F0.wireOp",EDGE,"E7.12.5"),sQuery(id+"F0.wireOp",EDGE,"E7.13.0"),sQuery(id+"F0.wireOp",EDGE,"E7.13.1"),sQuery(id+"F0.wireOp",EDGE,"E7.13.2"),sQuery(id+"F0.wireOp",EDGE,"E7.13.3"),sQuery(id+"F0.wireOp",EDGE,"E7.13.4"),sQuery(id+"F0.wireOp",EDGE,"E7.13.5"),sQuery(id+"F0.wireOp",EDGE,"E7.14.0"),sQuery(id+"F0.wireOp",EDGE,"E7.14.1"),sQuery(id+"F0.wireOp",EDGE,"E7.14.2"),sQuery(id+"F0.wireOp",EDGE,"E7.14.3"),sQuery(id+"F0.wireOp",EDGE,"E7.14.4"),sQuery(id+"F0.wireOp",EDGE,"E7.14.5"),sQuery(id+"F0.wireOp",EDGE,"E7.15.0"),sQuery(id+"F0.wireOp",EDGE,"E7.15.1"),sQuery(id+"F0.wireOp",EDGE,"E7.15.2"),sQuery(id+"F0.wireOp",EDGE,"E7.15.3"),sQuery(id+"F0.wireOp",EDGE,"E7.15.4"),sQuery(id+"F0.wireOp",EDGE,"E7.15.5"),sQuery(id+"F0.wireOp",EDGE,"E7.16.0"),sQuery(id+"F0.wireOp",EDGE,"E7.16.1"),sQuery(id+"F0.wireOp",EDGE,"E7.16.2"),sQuery(id+"F0.wireOp",EDGE,"E7.16.3"),sQuery(id+"F0.wireOp",EDGE,"E7.16.4"),sQuery(id+"F0.wireOp",EDGE,"E7.16.5"),sQuery(id+"F0.wireOp",EDGE,"E7.17.0"),sQuery(id+"F0.wireOp",EDGE,"E7.17.1"),sQuery(id+"F0.wireOp",EDGE,"E7.17.2"),sQuery(id+"F0.wireOp",EDGE,"E7.17.3"),sQuery(id+"F0.wireOp",EDGE,"E7.17.4"),sQuery(id+"F0.wireOp",EDGE,"E7.17.5"),sQuery(id+"F0.wireOp",EDGE,"E7.18.0"),sQuery(id+"F0.wireOp",EDGE,"E7.18.1"),sQuery(id+"F0.wireOp",EDGE,"E7.18.2"),sQuery(id+"F0.wireOp",EDGE,"E7.18.3"),sQuery(id+"F0.wireOp",EDGE,"E7.18.4"),sQuery(id+"F0.wireOp",EDGE,"E7.18.5"),sQuery(id+"F0.wireOp",EDGE,"E7.19.0"),sQuery(id+"F0.wireOp",EDGE,"E7.19.1"),sQuery(id+"F0.wireOp",EDGE,"E7.19.2"),sQuery(id+"F0.wireOp",EDGE,"E7.19.3"),sQuery(id+"F0.wireOp",EDGE,"E7.19.4"),sQuery(id+"F0.wireOp",EDGE,"E7.19.5"),sQuery(id+"F0.wireOp",EDGE,"E7.20.0"),sQuery(id+"F0.wireOp",EDGE,"E7.20.1"),sQuery(id+"F0.wireOp",EDGE,"E7.20.2"),sQuery(id+"F0.wireOp",EDGE,"E7.20.3"),sQuery(id+"F0.wireOp",EDGE,"E7.20.4"),sQuery(id+"F0.wireOp",EDGE,"E7.20.5"),sQuery(id+"F0.wireOp",EDGE,"E7.21.0"),sQuery(id+"F0.wireOp",EDGE,"E7.21.1"),sQuery(id+"F0.wireOp",EDGE,"E7.21.2"),sQuery(id+"F0.wireOp",EDGE,"E7.21.3"),sQuery(id+"F0.wireOp",EDGE,"E7.21.4"),sQuery(id+"F0.wireOp",EDGE,"E7.21.5"),sQuery(id+"F0.wireOp",EDGE,"E7.22.0"),sQuery(id+"F0.wireOp",EDGE,"E7.22.1"),sQuery(id+"F0.wireOp",EDGE,"E7.22.2"),sQuery(id+"F0.wireOp",EDGE,"E7.22.3"),sQuery(id+"F0.wireOp",EDGE,"E7.22.4"),sQuery(id+"F0.wireOp",EDGE,"E7.22.5"),sQuery(id+"F0.wireOp",EDGE,"E7.23.0"),sQuery(id+"F0.wireOp",EDGE,"E7.23.1"),sQuery(id+"F0.wireOp",EDGE,"E7.23.2"),sQuery(id+"F0.wireOp",EDGE,"E7.23.3"),sQuery(id+"F0.wireOp",EDGE,"E7.23.4"),sQuery(id+"F0.wireOp",EDGE,"E7.23.5"),sQuery(id+"F0.wireOp",EDGE,"E7.24.0"),sQuery(id+"F0.wireOp",EDGE,"E7.24.1"),sQuery(id+"F0.wireOp",EDGE,"E7.24.2"),sQuery(id+"F0.wireOp",EDGE,"E7.24.3"),sQuery(id+"F0.wireOp",EDGE,"E7.24.4"),sQuery(id+"F0.wireOp",EDGE,"E7.24.5"),sQuery(id+"F0.wireOp",EDGE,"E7.25.0"),sQuery(id+"F0.wireOp",EDGE,"E7.25.1"),sQuery(id+"F0.wireOp",EDGE,"E7.25.2"),sQuery(id+"F0.wireOp",EDGE,"E7.25.3"),sQuery(id+"F0.wireOp",EDGE,"E7.25.4"),sQuery(id+"F0.wireOp",EDGE,"E7.25.5"),sQuery(id+"F0.wireOp",EDGE,"E7.26.0"),sQuery(id+"F0.wireOp",EDGE,"E7.26.1"),sQuery(id+"F0.wireOp",EDGE,"E7.26.2"),sQuery(id+"F0.wireOp",EDGE,"E7.26.3"),sQuery(id+"F0.wireOp",EDGE,"E7.26.4"),sQuery(id+"F0.wireOp",EDGE,"E7.26.5"),sQuery(id+"F0.wireOp",EDGE,"E7.27.0"),sQuery(id+"F0.wireOp",EDGE,"E7.27.1"),sQuery(id+"F0.wireOp",EDGE,"E7.27.2"),sQuery(id+"F0.wireOp",EDGE,"E7.27.3"),sQuery(id+"F0.wireOp",EDGE,"E7.27.4"),sQuery(id+"F0.wireOp",EDGE,"E7.27.5"),sQuery(id+"F0.wireOp",EDGE,"E7.28.0"),sQuery(id+"F0.wireOp",EDGE,"E7.28.1"),sQuery(id+"F0.wireOp",EDGE,"E7.28.2"),sQuery(id+"F0.wireOp",EDGE,"E7.28.3"),sQuery(id+"F0.wireOp",EDGE,"E7.28.4"),sQuery(id+"F0.wireOp",EDGE,"E7.28.5"),sQuery(id+"F0.wireOp",EDGE,"E7.29.0"),sQuery(id+"F0.wireOp",EDGE,"E7.29.1"),sQuery(id+"F0.wireOp",EDGE,"E7.29.2"),sQuery(id+"F0.wireOp",EDGE,"E7.29.3"),sQuery(id+"F0.wireOp",EDGE,"E7.29.4"),sQuery(id+"F0.wireOp",EDGE,"E7.29.5"),sQuery(id+"F0.wireOp",EDGE,"E7.30.0"),sQuery(id+"F0.wireOp",EDGE,"E7.30.1"),sQuery(id+"F0.wireOp",EDGE,"E7.30.2"),sQuery(id+"F0.wireOp",EDGE,"E7.30.3"),sQuery(id+"F0.wireOp",EDGE,"E7.30.4"),sQuery(id+"F0.wireOp",EDGE,"E7.30.5"),sQuery(id+"F0.wireOp",EDGE,"E7.31.0"),sQuery(id+"F0.wireOp",EDGE,"E7.31.1"),sQuery(id+"F0.wireOp",EDGE,"E7.31.2"),sQuery(id+"F0.wireOp",EDGE,"E7.31.3"),sQuery(id+"F0.wireOp",EDGE,"E7.31.4"),sQuery(id+"F0.wireOp",EDGE,"E7.31.5"),sQuery(id+"F0.wireOp",EDGE,"E7.32.0"),sQuery(id+"F0.wireOp",EDGE,"E7.32.1"),sQuery(id+"F0.wireOp",EDGE,"E7.32.2"),sQuery(id+"F0.wireOp",EDGE,"E7.32.3"),sQuery(id+"F0.wireOp",EDGE,"E7.32.4"),sQuery(id+"F0.wireOp",EDGE,"E7.32.5"),sQuery(id+"F0.wireOp",EDGE,"E7.33.0"),sQuery(id+"F0.wireOp",EDGE,"E7.33.1"),sQuery(id+"F0.wireOp",EDGE,"E7.33.2"),sQuery(id+"F0.wireOp",EDGE,"E7.33.3"),sQuery(id+"F0.wireOp",EDGE,"E7.33.4"),sQuery(id+"F0.wireOp",EDGE,"E7.33.5"),sQuery(id+"F0.wireOp",EDGE,"E7.34.0"),sQuery(id+"F0.wireOp",EDGE,"E7.34.1"),sQuery(id+"F0.wireOp",EDGE,"E7.34.2"),sQuery(id+"F0.wireOp",EDGE,"E7.34.3"),sQuery(id+"F0.wireOp",EDGE,"E7.34.4"),sQuery(id+"F0.wireOp",EDGE,"E7.34.5"),sQuery(id+"F0.wireOp",EDGE,"E7.35.0"),sQuery(id+"F0.wireOp",EDGE,"E7.35.1"),sQuery(id+"F0.wireOp",EDGE,"E7.35.2"),sQuery(id+"F0.wireOp",EDGE,"E7.35.3"),sQuery(id+"F0.wireOp",EDGE,"E7.35.4"),sQuery(id+"F0.wireOp",EDGE,"E7.35.5"),sQuery(id+"F0.wireOp",EDGE,"E7.36.0"),sQuery(id+"F0.wireOp",EDGE,"E7.36.1"),sQuery(id+"F0.wireOp",EDGE,"E7.36.2"),sQuery(id+"F0.wireOp",EDGE,"E7.36.3"),sQuery(id+"F0.wireOp",EDGE,"E7.36.4"),sQuery(id+"F0.wireOp",EDGE,"E7.36.5"),sQuery(id+"F0.wireOp",EDGE,"E7.37.0"),sQuery(id+"F0.wireOp",EDGE,"E7.37.1"),sQuery(id+"F0.wireOp",EDGE,"E7.37.2"),sQuery(id+"F0.wireOp",EDGE,"E7.37.3"),sQuery(id+"F0.wireOp",EDGE,"E7.37.4"),sQuery(id+"F0.wireOp",EDGE,"E7.37.5"),sQuery(id+"F0.wireOp",EDGE,"E7.38.0"),sQuery(id+"F0.wireOp",EDGE,"E7.38.1"),sQuery(id+"F0.wireOp",EDGE,"E7.38.2"),sQuery(id+"F0.wireOp",EDGE,"E7.38.3"),sQuery(id+"F0.wireOp",EDGE,"E7.38.4"),sQuery(id+"F0.wireOp",EDGE,"E7.38.5"),sQuery(id+"F0.wireOp",EDGE,"E7.39.0"),sQuery(id+"F0.wireOp",EDGE,"E7.39.1"),sQuery(id+"F0.wireOp",EDGE,"E7.39.2"),sQuery(id+"F0.wireOp",EDGE,"E7.39.3"),sQuery(id+"F0.wireOp",EDGE,"E7.39.4"),sQuery(id+"F0.wireOp",EDGE,"E7.39.5"),sQuery(id+"F0.wireOp",EDGE,"E7.40.0"),sQuery(id+"F0.wireOp",EDGE,"E7.40.1"),sQuery(id+"F0.wireOp",EDGE,"E7.40.2"),sQuery(id+"F0.wireOp",EDGE,"E7.40.3"),sQuery(id+"F0.wireOp",EDGE,"E7.40.4"),sQuery(id+"F0.wireOp",EDGE,"E7.40.5"),sQuery(id+"F0.wireOp",EDGE,"E7.41.0"),sQuery(id+"F0.wireOp",EDGE,"E7.41.1"),sQuery(id+"F0.wireOp",EDGE,"E7.41.2"),sQuery(id+"F0.wireOp",EDGE,"E7.41.3"),sQuery(id+"F0.wireOp",EDGE,"E7.41.4"),sQuery(id+"F0.wireOp",EDGE,"E7.41.5"),sQuery(id+"F0.wireOp",EDGE,"E7.42.0"),sQuery(id+"F0.wireOp",EDGE,"E7.42.1"),sQuery(id+"F0.wireOp",EDGE,"E7.42.2"),sQuery(id+"F0.wireOp",EDGE,"E7.42.3"),sQuery(id+"F0.wireOp",EDGE,"E7.42.4"),sQuery(id+"F0.wireOp",EDGE,"E7.42.5"),sQuery(id+"F0.wireOp",EDGE,"E7.43.0"),sQuery(id+"F0.wireOp",EDGE,"E7.43.1"),sQuery(id+"F0.wireOp",EDGE,"E7.43.2"),sQuery(id+"F0.wireOp",EDGE,"E7.43.3"),sQuery(id+"F0.wireOp",EDGE,"E7.43.4"),sQuery(id+"F0.wireOp",EDGE,"E7.43.5")])],"isStart":true})],"blendedInto":[makeQuery(id+"F1.opExtrude","CAP_FACE",FACE,{"disambiguationData":[OSD([sQuery(id+"F0.wireOp",EDGE,"E1"),sQuery(id+"F0.wireOp",EDGE,"E2"),sQuery(id+"F0.wireOp",EDGE,"E3"),sQuery(id+"F0.wireOp",EDGE,"E4"),sQuery(id+"F0.wireOp",EDGE,"E5"),sQuery(id+"F0.wireOp",EDGE,"E6"),sQuery(id+"F0.wireOp",EDGE,"E7.1.0"),sQuery(id+"F0.wireOp",EDGE,"E7.1.1"),sQuery(id+"F0.wireOp",EDGE,"E7.1.2"),sQuery(id+"F0.wireOp",EDGE,"E7.1.3"),sQuery(id+"F0.wireOp",EDGE,"E7.1.4"),sQuery(id+"F0.wireOp",EDGE,"E7.1.5"),sQuery(id+"F0.wireOp",EDGE,"E7.2.0"),sQuery(id+"F0.wireOp",EDGE,"E7.2.1"),sQuery(id+"F0.wireOp",EDGE,"E7.2.2"),sQuery(id+"F0.wireOp",EDGE,"E7.2.3"),sQuery(id+"F0.wireOp",EDGE,"E7.2.4"),sQuery(id+"F0.wireOp",EDGE,"E7.2.5"),sQuery(id+"F0.wireOp",EDGE,"E7.3.0"),sQuery(id+"F0.wireOp",EDGE,"E7.3.1"),sQuery(id+"F0.wireOp",EDGE,"E7.3.2"),sQuery(id+"F0.wireOp",EDGE,"E7.3.3"),sQuery(id+"F0.wireOp",EDGE,"E7.3.4"),sQuery(id+"F0.wireOp",EDGE,"E7.3.5"),subQ0,sQuery(id+"F0.wireOp",EDGE,"E7.4.1"),sQuery(id+"F0.wireOp",EDGE,"E7.4.2"),sQuery(id+"F0.wireOp",EDGE,"E7.4.3"),sQuery(id+"F0.wireOp",EDGE,"E7.4.4"),sQuery(id+"F0.wireOp",EDGE,"E7.4.5"),sQuery(id+"F0.wireOp",EDGE,"E7.5.0"),sQuery(id+"F0.wireOp",EDGE,"E7.5.1"),sQuery(id+"F0.wireOp",EDGE,"E7.5.2"),sQuery(id+"F0.wireOp",EDGE,"E7.5.3"),sQuery(id+"F0.wireOp",EDGE,"E7.5.4"),sQuery(id+"F0.wireOp",EDGE,"E7.5.5"),sQuery(id+"F0.wireOp",EDGE,"E7.6.0"),sQuery(id+"F0.wireOp",EDGE,"E7.6.1"),sQuery(id+"F0.wireOp",EDGE,"E7.6.2"),sQuery(id+"F0.wireOp",EDGE,"E7.6.3"),sQuery(id+"F0.wireOp",EDGE,"E7.6.4"),sQuery(id+"F0.wireOp",EDGE,"E7.6.5"),sQuery(id+"F0.wireOp",EDGE,"E7.7.0"),sQuery(id+"F0.wireOp",EDGE,"E7.7.1"),sQuery(id+"F0.wireOp",EDGE,"E7.7.2"),sQuery(id+"F0.wireOp",EDGE,"E7.7.3"),sQuery(id+"F0.wireOp",EDGE,"E7.7.4"),sQuery(id+"F0.wireOp",EDGE,"E7.7.5"),sQuery(id+"F0.wireOp",EDGE,"E7.8.0"),sQuery(id+"F0.wireOp",EDGE,"E7.8.1"),sQuery(id+"F0.wireOp",EDGE,"E7.8.2"),sQuery(id+"F0.wireOp",EDGE,"E7.8.3"),sQuery(id+"F0.wireOp",EDGE,"E7.8.4"),sQuery(id+"F0.wireOp",EDGE,"E7.8.5"),sQuery(id+"F0.wireOp",EDGE,"E7.9.0"),sQuery(id+"F0.wireOp",EDGE,"E7.9.1"),sQuery(id+"F0.wireOp",EDGE,"E7.9.2"),sQuery(id+"F0.wireOp",EDGE,"E7.9.3"),sQuery(id+"F0.wireOp",EDGE,"E7.9.4"),sQuery(id+"F0.wireOp",EDGE,"E7.9.5"),sQuery(id+"F0.wireOp",EDGE,"E7.10.0"),sQuery(id+"F0.wireOp",EDGE,"E7.10.1"),sQuery(id+"F0.wireOp",EDGE,"E7.10.2"),sQuery(id+"F0.wireOp",EDGE,"E7.10.3"),sQuery(id+"F0.wireOp",EDGE,"E7.10.4"),sQuery(id+"F0.wireOp",EDGE,"E7.10.5"),sQuery(id+"F0.wireOp",EDGE,"E7.11.0"),sQuery(id+"F0.wireOp",EDGE,"E7.11.1"),sQuery(id+"F0.wireOp",EDGE,"E7.11.2"),sQuery(id+"F0.wireOp",EDGE,"E7.11.3"),sQuery(id+"F0.wireOp",EDGE,"E7.11.4"),sQuery(id+"F0.wireOp",EDGE,"E7.11.5"),sQuery(id+"F0.wireOp",EDGE,"E7.12.0"),sQuery(id+"F0.wireOp",EDGE,"E7.12.1"),sQuery(id+"F0.wireOp",EDGE,"E7.12.2"),sQuery(id+"F0.wireOp",EDGE,"E7.12.3"),sQuery(id+"F0.wireOp",EDGE,"E7.12.4"),sQuery(id+"F0.wireOp",EDGE,"E7.12.5"),sQuery(id+"F0.wireOp",EDGE,"E7.13.0"),sQuery(id+"F0.wireOp",EDGE,"E7.13.1"),sQuery(id+"F0.wireOp",EDGE,"E7.13.2"),sQuery(id+"F0.wireOp",EDGE,"E7.13.3"),sQuery(id+"F0.wireOp",EDGE,"E7.13.4"),sQuery(id+"F0.wireOp",EDGE,"E7.13.5"),sQuery(id+"F0.wireOp",EDGE,"E7.14.0"),sQuery(id+"F0.wireOp",EDGE,"E7.14.1"),sQuery(id+"F0.wireOp",EDGE,"E7.14.2"),sQuery(id+"F0.wireOp",EDGE,"E7.14.3"),sQuery(id+"F0.wireOp",EDGE,"E7.14.4"),sQuery(id+"F0.wireOp",EDGE,"E7.14.5"),sQuery(id+"F0.wireOp",EDGE,"E7.15.0"),sQuery(id+"F0.wireOp",EDGE,"E7.15.1"),sQuery(id+"F0.wireOp",EDGE,"E7.15.2"),sQuery(id+"F0.wireOp",EDGE,"E7.15.3"),sQuery(id+"F0.wireOp",EDGE,"E7.15.4"),sQuery(id+"F0.wireOp",EDGE,"E7.15.5"),sQuery(id+"F0.wireOp",EDGE,"E7.16.0"),sQuery(id+"F0.wireOp",EDGE,"E7.16.1"),sQuery(id+"F0.wireOp",EDGE,"E7.16.2"),sQuery(id+"F0.wireOp",EDGE,"E7.16.3"),sQuery(id+"F0.wireOp",EDGE,"E7.16.4"),sQuery(id+"F0.wireOp",EDGE,"E7.16.5"),sQuery(id+"F0.wireOp",EDGE,"E7.17.0"),sQuery(id+"F0.wireOp",EDGE,"E7.17.1"),sQuery(id+"F0.wireOp",EDGE,"E7.17.2"),sQuery(id+"F0.wireOp",EDGE,"E7.17.3"),sQuery(id+"F0.wireOp",EDGE,"E7.17.4"),sQuery(id+"F0.wireOp",EDGE,"E7.17.5"),sQuery(id+"F0.wireOp",EDGE,"E7.18.0"),sQuery(id+"F0.wireOp",EDGE,"E7.18.1"),sQuery(id+"F0.wireOp",EDGE,"E7.18.2"),sQuery(id+"F0.wireOp",EDGE,"E7.18.3"),sQuery(id+"F0.wireOp",EDGE,"E7.18.4"),sQuery(id+"F0.wireOp",EDGE,"E7.18.5"),sQuery(id+"F0.wireOp",EDGE,"E7.19.0"),sQuery(id+"F0.wireOp",EDGE,"E7.19.1"),sQuery(id+"F0.wireOp",EDGE,"E7.19.2"),sQuery(id+"F0.wireOp",EDGE,"E7.19.3"),sQuery(id+"F0.wireOp",EDGE,"E7.19.4"),sQuery(id+"F0.wireOp",EDGE,"E7.19.5"),sQuery(id+"F0.wireOp",EDGE,"E7.20.0"),sQuery(id+"F0.wireOp",EDGE,"E7.20.1"),sQuery(id+"F0.wireOp",EDGE,"E7.20.2"),sQuery(id+"F0.wireOp",EDGE,"E7.20.3"),sQuery(id+"F0.wireOp",EDGE,"E7.20.4"),sQuery(id+"F0.wireOp",EDGE,"E7.20.5"),sQuery(id+"F0.wireOp",EDGE,"E7.21.0"),sQuery(id+"F0.wireOp",EDGE,"E7.21.1"),sQuery(id+"F0.wireOp",EDGE,"E7.21.2"),sQuery(id+"F0.wireOp",EDGE,"E7.21.3"),sQuery(id+"F0.wireOp",EDGE,"E7.21.4"),sQuery(id+"F0.wireOp",EDGE,"E7.21.5"),sQuery(id+"F0.wireOp",EDGE,"E7.22.0"),sQuery(id+"F0.wireOp",EDGE,"E7.22.1"),sQuery(id+"F0.wireOp",EDGE,"E7.22.2"),sQuery(id+"F0.wireOp",EDGE,"E7.22.3"),sQuery(id+"F0.wireOp",EDGE,"E7.22.4"),sQuery(id+"F0.wireOp",EDGE,"E7.22.5"),sQuery(id+"F0.wireOp",EDGE,"E7.23.0"),sQuery(id+"F0.wireOp",EDGE,"E7.23.1"),sQuery(id+"F0.wireOp",EDGE,"E7.23.2"),sQuery(id+"F0.wireOp",EDGE,"E7.23.3"),sQuery(id+"F0.wireOp",EDGE,"E7.23.4"),sQuery(id+"F0.wireOp",EDGE,"E7.23.5"),sQuery(id+"F0.wireOp",EDGE,"E7.24.0"),sQuery(id+"F0.wireOp",EDGE,"E7.24.1"),sQuery(id+"F0.wireOp",EDGE,"E7.24.2"),sQuery(id+"F0.wireOp",EDGE,"E7.24.3"),sQuery(id+"F0.wireOp",EDGE,"E7.24.4"),sQuery(id+"F0.wireOp",EDGE,"E7.24.5"),sQuery(id+"F0.wireOp",EDGE,"E7.25.0"),sQuery(id+"F0.wireOp",EDGE,"E7.25.1"),sQuery(id+"F0.wireOp",EDGE,"E7.25.2"),sQuery(id+"F0.wireOp",EDGE,"E7.25.3"),sQuery(id+"F0.wireOp",EDGE,"E7.25.4"),sQuery(id+"F0.wireOp",EDGE,"E7.25.5"),sQuery(id+"F0.wireOp",EDGE,"E7.26.0"),sQuery(id+"F0.wireOp",EDGE,"E7.26.1"),sQuery(id+"F0.wireOp",EDGE,"E7.26.2"),sQuery(id+"F0.wireOp",EDGE,"E7.26.3"),sQuery(id+"F0.wireOp",EDGE,"E7.26.4"),sQuery(id+"F0.wireOp",EDGE,"E7.26.5"),sQuery(id+"F0.wireOp",EDGE,"E7.27.0"),sQuery(id+"F0.wireOp",EDGE,"E7.27.1"),sQuery(id+"F0.wireOp",EDGE,"E7.27.2"),sQuery(id+"F0.wireOp",EDGE,"E7.27.3"),sQuery(id+"F0.wireOp",EDGE,"E7.27.4"),sQuery(id+"F0.wireOp",EDGE,"E7.27.5"),sQuery(id+"F0.wireOp",EDGE,"E7.28.0"),sQuery(id+"F0.wireOp",EDGE,"E7.28.1"),sQuery(id+"F0.wireOp",EDGE,"E7.28.2"),sQuery(id+"F0.wireOp",EDGE,"E7.28.3"),sQuery(id+"F0.wireOp",EDGE,"E7.28.4"),sQuery(id+"F0.wireOp",EDGE,"E7.28.5"),sQuery(id+"F0.wireOp",EDGE,"E7.29.0"),sQuery(id+"F0.wireOp",EDGE,"E7.29.1"),sQuery(id+"F0.wireOp",EDGE,"E7.29.2"),sQuery(id+"F0.wireOp",EDGE,"E7.29.3"),sQuery(id+"F0.wireOp",EDGE,"E7.29.4"),sQuery(id+"F0.wireOp",EDGE,"E7.29.5"),sQuery(id+"F0.wireOp",EDGE,"E7.30.0"),sQuery(id+"F0.wireOp",EDGE,"E7.30.1"),sQuery(id+"F0.wireOp",EDGE,"E7.30.2"),sQuery(id+"F0.wireOp",EDGE,"E7.30.3"),sQuery(id+"F0.wireOp",EDGE,"E7.30.4"),sQuery(id+"F0.wireOp",EDGE,"E7.30.5"),sQuery(id+"F0.wireOp",EDGE,"E7.31.0"),sQuery(id+"F0.wireOp",EDGE,"E7.31.1"),sQuery(id+"F0.wireOp",EDGE,"E7.31.2"),sQuery(id+"F0.wireOp",EDGE,"E7.31.3"),sQuery(id+"F0.wireOp",EDGE,"E7.31.4"),sQuery(id+"F0.wireOp",EDGE,"E7.31.5"),sQuery(id+"F0.wireOp",EDGE,"E7.32.0"),sQuery(id+"F0.wireOp",EDGE,"E7.32.1"),sQuery(id+"F0.wireOp",EDGE,"E7.32.2"),sQuery(id+"F0.wireOp",EDGE,"E7.32.3"),sQuery(id+"F0.wireOp",EDGE,"E7.32.4"),sQuery(id+"F0.wireOp",EDGE,"E7.32.5"),sQuery(id+"F0.wireOp",EDGE,"E7.33.0"),sQuery(id+"F0.wireOp",EDGE,"E7.33.1"),sQuery(id+"F0.wireOp",EDGE,"E7.33.2"),sQuery(id+"F0.wireOp",EDGE,"E7.33.3"),sQuery(id+"F0.wireOp",EDGE,"E7.33.4"),sQuery(id+"F0.wireOp",EDGE,"E7.33.5"),sQuery(id+"F0.wireOp",EDGE,"E7.34.0"),sQuery(id+"F0.wireOp",EDGE,"E7.34.1"),sQuery(id+"F0.wireOp",EDGE,"E7.34.2"),sQuery(id+"F0.wireOp",EDGE,"E7.34.3"),sQuery(id+"F0.wireOp",EDGE,"E7.34.4"),sQuery(id+"F0.wireOp",EDGE,"E7.34.5"),sQuery(id+"F0.wireOp",EDGE,"E7.35.0"),sQuery(id+"F0.wireOp",EDGE,"E7.35.1"),sQuery(id+"F0.wireOp",EDGE,"E7.35.2"),sQuery(id+"F0.wireOp",EDGE,"E7.35.3"),sQuery(id+"F0.wireOp",EDGE,"E7.35.4"),sQuery(id+"F0.wireOp",EDGE,"E7.35.5"),sQuery(id+"F0.wireOp",EDGE,"E7.36.0"),sQuery(id+"F0.wireOp",EDGE,"E7.36.1"),sQuery(id+"F0.wireOp",EDGE,"E7.36.2"),sQuery(id+"F0.wireOp",EDGE,"E7.36.3"),sQuery(id+"F0.wireOp",EDGE,"E7.36.4"),sQuery(id+"F0.wireOp",EDGE,"E7.36.5"),sQuery(id+"F0.wireOp",EDGE,"E7.37.0"),sQuery(id+"F0.wireOp",EDGE,"E7.37.1"),sQuery(id+"F0.wireOp",EDGE,"E7.37.2"),sQuery(id+"F0.wireOp",EDGE,"E7.37.3"),sQuery(id+"F0.wireOp",EDGE,"E7.37.4"),sQuery(id+"F0.wireOp",EDGE,"E7.37.5"),sQuery(id+"F0.wireOp",EDGE,"E7.38.0"),sQuery(id+"F0.wireOp",EDGE,"E7.38.1"),sQuery(id+"F0.wireOp",EDGE,"E7.38.2"),sQuery(id+"F0.wireOp",EDGE,"E7.38.3"),sQuery(id+"F0.wireOp",EDGE,"E7.38.4"),sQuery(id+"F0.wireOp",EDGE,"E7.38.5"),sQuery(id+"F0.wireOp",EDGE,"E7.39.0"),sQuery(id+"F0.wireOp",EDGE,"E7.39.1"),sQuery(id+"F0.wireOp",EDGE,"E7.39.2"),sQuery(id+"F0.wireOp",EDGE,"E7.39.3"),sQuery(id+"F0.wireOp",EDGE,"E7.39.4"),sQuery(id+"F0.wireOp",EDGE,"E7.39.5"),sQuery(id+"F0.wireOp",EDGE,"E7.40.0"),sQuery(id+"F0.wireOp",EDGE,"E7.40.1"),sQuery(id+"F0.wireOp",EDGE,"E7.40.2"),sQuery(id+"F0.wireOp",EDGE,"E7.40.3"),sQuery(id+"F0.wireOp",EDGE,"E7.40.4"),sQuery(id+"F0.wireOp",EDGE,"E7.40.5"),sQuery(id+"F0.wireOp",EDGE,"E7.41.0"),sQuery(id+"F0.wireOp",EDGE,"E7.41.1"),sQuery(id+"F0.wireOp",EDGE,"E7.41.2"),sQuery(id+"F0.wireOp",EDGE,"E7.41.3"),sQuery(id+"F0.wireOp",EDGE,"E7.41.4"),sQuery(id+"F0.wireOp",EDGE,"E7.41.5"),sQuery(id+"F0.wireOp",EDGE,"E7.42.0"),sQuery(id+"F0.wireOp",EDGE,"E7.42.1"),sQuery(id+"F0.wireOp",EDGE,"E7.42.2"),sQuery(id+"F0.wireOp",EDGE,"E7.42.3"),sQuery(id+"F0.wireOp",EDGE,"E7.42.4"),sQuery(id+"F0.wireOp",EDGE,"E7.42.5"),sQuery(id+"F0.wireOp",EDGE,"E7.43.0"),sQuery(id+"F0.wireOp",EDGE,"E7.43.1"),sQuery(id+"F0.wireOp",EDGE,"E7.43.2"),sQuery(id+"F0.wireOp",EDGE,"E7.43.3"),sQuery(id+"F0.wireOp",EDGE,"E7.43.4"),sQuery(id+"F0.wireOp",EDGE,"E7.43.5")])],"isStart":true})]});}
            var Q24;
            {var subQ0=sQuery(id+"F0.wireOp",EDGE,"E7.6.0");Q24=makeQuery(id+"F2.opChamfer","BLEND_EDGE",EDGE,{"blendedFrom":[makeQuery(id+"F1.opExtrude","CAP_EDGE",EDGE,{"disambiguationData":[OSD([subQ0])],"isStart":true}),makeQuery(id+"F1.opExtrude","CAP_FACE",FACE,{"disambiguationData":[OSD([sQuery(id+"F0.wireOp",EDGE,"E1"),sQuery(id+"F0.wireOp",EDGE,"E2"),sQuery(id+"F0.wireOp",EDGE,"E3"),sQuery(id+"F0.wireOp",EDGE,"E4"),sQuery(id+"F0.wireOp",EDGE,"E5"),sQuery(id+"F0.wireOp",EDGE,"E6"),sQuery(id+"F0.wireOp",EDGE,"E7.1.0"),sQuery(id+"F0.wireOp",EDGE,"E7.1.1"),sQuery(id+"F0.wireOp",EDGE,"E7.1.2"),sQuery(id+"F0.wireOp",EDGE,"E7.1.3"),sQuery(id+"F0.wireOp",EDGE,"E7.1.4"),sQuery(id+"F0.wireOp",EDGE,"E7.1.5"),sQuery(id+"F0.wireOp",EDGE,"E7.2.0"),sQuery(id+"F0.wireOp",EDGE,"E7.2.1"),sQuery(id+"F0.wireOp",EDGE,"E7.2.2"),sQuery(id+"F0.wireOp",EDGE,"E7.2.3"),sQuery(id+"F0.wireOp",EDGE,"E7.2.4"),sQuery(id+"F0.wireOp",EDGE,"E7.2.5"),sQuery(id+"F0.wireOp",EDGE,"E7.3.0"),sQuery(id+"F0.wireOp",EDGE,"E7.3.1"),sQuery(id+"F0.wireOp",EDGE,"E7.3.2"),sQuery(id+"F0.wireOp",EDGE,"E7.3.3"),sQuery(id+"F0.wireOp",EDGE,"E7.3.4"),sQuery(id+"F0.wireOp",EDGE,"E7.3.5"),sQuery(id+"F0.wireOp",EDGE,"E7.4.0"),sQuery(id+"F0.wireOp",EDGE,"E7.4.1"),sQuery(id+"F0.wireOp",EDGE,"E7.4.2"),sQuery(id+"F0.wireOp",EDGE,"E7.4.3"),sQuery(id+"F0.wireOp",EDGE,"E7.4.4"),sQuery(id+"F0.wireOp",EDGE,"E7.4.5"),sQuery(id+"F0.wireOp",EDGE,"E7.5.0"),sQuery(id+"F0.wireOp",EDGE,"E7.5.1"),sQuery(id+"F0.wireOp",EDGE,"E7.5.2"),sQuery(id+"F0.wireOp",EDGE,"E7.5.3"),sQuery(id+"F0.wireOp",EDGE,"E7.5.4"),sQuery(id+"F0.wireOp",EDGE,"E7.5.5"),subQ0,sQuery(id+"F0.wireOp",EDGE,"E7.6.1"),sQuery(id+"F0.wireOp",EDGE,"E7.6.2"),sQuery(id+"F0.wireOp",EDGE,"E7.6.3"),sQuery(id+"F0.wireOp",EDGE,"E7.6.4"),sQuery(id+"F0.wireOp",EDGE,"E7.6.5"),sQuery(id+"F0.wireOp",EDGE,"E7.7.0"),sQuery(id+"F0.wireOp",EDGE,"E7.7.1"),sQuery(id+"F0.wireOp",EDGE,"E7.7.2"),sQuery(id+"F0.wireOp",EDGE,"E7.7.3"),sQuery(id+"F0.wireOp",EDGE,"E7.7.4"),sQuery(id+"F0.wireOp",EDGE,"E7.7.5"),sQuery(id+"F0.wireOp",EDGE,"E7.8.0"),sQuery(id+"F0.wireOp",EDGE,"E7.8.1"),sQuery(id+"F0.wireOp",EDGE,"E7.8.2"),sQuery(id+"F0.wireOp",EDGE,"E7.8.3"),sQuery(id+"F0.wireOp",EDGE,"E7.8.4"),sQuery(id+"F0.wireOp",EDGE,"E7.8.5"),sQuery(id+"F0.wireOp",EDGE,"E7.9.0"),sQuery(id+"F0.wireOp",EDGE,"E7.9.1"),sQuery(id+"F0.wireOp",EDGE,"E7.9.2"),sQuery(id+"F0.wireOp",EDGE,"E7.9.3"),sQuery(id+"F0.wireOp",EDGE,"E7.9.4"),sQuery(id+"F0.wireOp",EDGE,"E7.9.5"),sQuery(id+"F0.wireOp",EDGE,"E7.10.0"),sQuery(id+"F0.wireOp",EDGE,"E7.10.1"),sQuery(id+"F0.wireOp",EDGE,"E7.10.2"),sQuery(id+"F0.wireOp",EDGE,"E7.10.3"),sQuery(id+"F0.wireOp",EDGE,"E7.10.4"),sQuery(id+"F0.wireOp",EDGE,"E7.10.5"),sQuery(id+"F0.wireOp",EDGE,"E7.11.0"),sQuery(id+"F0.wireOp",EDGE,"E7.11.1"),sQuery(id+"F0.wireOp",EDGE,"E7.11.2"),sQuery(id+"F0.wireOp",EDGE,"E7.11.3"),sQuery(id+"F0.wireOp",EDGE,"E7.11.4"),sQuery(id+"F0.wireOp",EDGE,"E7.11.5"),sQuery(id+"F0.wireOp",EDGE,"E7.12.0"),sQuery(id+"F0.wireOp",EDGE,"E7.12.1"),sQuery(id+"F0.wireOp",EDGE,"E7.12.2"),sQuery(id+"F0.wireOp",EDGE,"E7.12.3"),sQuery(id+"F0.wireOp",EDGE,"E7.12.4"),sQuery(id+"F0.wireOp",EDGE,"E7.12.5"),sQuery(id+"F0.wireOp",EDGE,"E7.13.0"),sQuery(id+"F0.wireOp",EDGE,"E7.13.1"),sQuery(id+"F0.wireOp",EDGE,"E7.13.2"),sQuery(id+"F0.wireOp",EDGE,"E7.13.3"),sQuery(id+"F0.wireOp",EDGE,"E7.13.4"),sQuery(id+"F0.wireOp",EDGE,"E7.13.5"),sQuery(id+"F0.wireOp",EDGE,"E7.14.0"),sQuery(id+"F0.wireOp",EDGE,"E7.14.1"),sQuery(id+"F0.wireOp",EDGE,"E7.14.2"),sQuery(id+"F0.wireOp",EDGE,"E7.14.3"),sQuery(id+"F0.wireOp",EDGE,"E7.14.4"),sQuery(id+"F0.wireOp",EDGE,"E7.14.5"),sQuery(id+"F0.wireOp",EDGE,"E7.15.0"),sQuery(id+"F0.wireOp",EDGE,"E7.15.1"),sQuery(id+"F0.wireOp",EDGE,"E7.15.2"),sQuery(id+"F0.wireOp",EDGE,"E7.15.3"),sQuery(id+"F0.wireOp",EDGE,"E7.15.4"),sQuery(id+"F0.wireOp",EDGE,"E7.15.5"),sQuery(id+"F0.wireOp",EDGE,"E7.16.0"),sQuery(id+"F0.wireOp",EDGE,"E7.16.1"),sQuery(id+"F0.wireOp",EDGE,"E7.16.2"),sQuery(id+"F0.wireOp",EDGE,"E7.16.3"),sQuery(id+"F0.wireOp",EDGE,"E7.16.4"),sQuery(id+"F0.wireOp",EDGE,"E7.16.5"),sQuery(id+"F0.wireOp",EDGE,"E7.17.0"),sQuery(id+"F0.wireOp",EDGE,"E7.17.1"),sQuery(id+"F0.wireOp",EDGE,"E7.17.2"),sQuery(id+"F0.wireOp",EDGE,"E7.17.3"),sQuery(id+"F0.wireOp",EDGE,"E7.17.4"),sQuery(id+"F0.wireOp",EDGE,"E7.17.5"),sQuery(id+"F0.wireOp",EDGE,"E7.18.0"),sQuery(id+"F0.wireOp",EDGE,"E7.18.1"),sQuery(id+"F0.wireOp",EDGE,"E7.18.2"),sQuery(id+"F0.wireOp",EDGE,"E7.18.3"),sQuery(id+"F0.wireOp",EDGE,"E7.18.4"),sQuery(id+"F0.wireOp",EDGE,"E7.18.5"),sQuery(id+"F0.wireOp",EDGE,"E7.19.0"),sQuery(id+"F0.wireOp",EDGE,"E7.19.1"),sQuery(id+"F0.wireOp",EDGE,"E7.19.2"),sQuery(id+"F0.wireOp",EDGE,"E7.19.3"),sQuery(id+"F0.wireOp",EDGE,"E7.19.4"),sQuery(id+"F0.wireOp",EDGE,"E7.19.5"),sQuery(id+"F0.wireOp",EDGE,"E7.20.0"),sQuery(id+"F0.wireOp",EDGE,"E7.20.1"),sQuery(id+"F0.wireOp",EDGE,"E7.20.2"),sQuery(id+"F0.wireOp",EDGE,"E7.20.3"),sQuery(id+"F0.wireOp",EDGE,"E7.20.4"),sQuery(id+"F0.wireOp",EDGE,"E7.20.5"),sQuery(id+"F0.wireOp",EDGE,"E7.21.0"),sQuery(id+"F0.wireOp",EDGE,"E7.21.1"),sQuery(id+"F0.wireOp",EDGE,"E7.21.2"),sQuery(id+"F0.wireOp",EDGE,"E7.21.3"),sQuery(id+"F0.wireOp",EDGE,"E7.21.4"),sQuery(id+"F0.wireOp",EDGE,"E7.21.5"),sQuery(id+"F0.wireOp",EDGE,"E7.22.0"),sQuery(id+"F0.wireOp",EDGE,"E7.22.1"),sQuery(id+"F0.wireOp",EDGE,"E7.22.2"),sQuery(id+"F0.wireOp",EDGE,"E7.22.3"),sQuery(id+"F0.wireOp",EDGE,"E7.22.4"),sQuery(id+"F0.wireOp",EDGE,"E7.22.5"),sQuery(id+"F0.wireOp",EDGE,"E7.23.0"),sQuery(id+"F0.wireOp",EDGE,"E7.23.1"),sQuery(id+"F0.wireOp",EDGE,"E7.23.2"),sQuery(id+"F0.wireOp",EDGE,"E7.23.3"),sQuery(id+"F0.wireOp",EDGE,"E7.23.4"),sQuery(id+"F0.wireOp",EDGE,"E7.23.5"),sQuery(id+"F0.wireOp",EDGE,"E7.24.0"),sQuery(id+"F0.wireOp",EDGE,"E7.24.1"),sQuery(id+"F0.wireOp",EDGE,"E7.24.2"),sQuery(id+"F0.wireOp",EDGE,"E7.24.3"),sQuery(id+"F0.wireOp",EDGE,"E7.24.4"),sQuery(id+"F0.wireOp",EDGE,"E7.24.5"),sQuery(id+"F0.wireOp",EDGE,"E7.25.0"),sQuery(id+"F0.wireOp",EDGE,"E7.25.1"),sQuery(id+"F0.wireOp",EDGE,"E7.25.2"),sQuery(id+"F0.wireOp",EDGE,"E7.25.3"),sQuery(id+"F0.wireOp",EDGE,"E7.25.4"),sQuery(id+"F0.wireOp",EDGE,"E7.25.5"),sQuery(id+"F0.wireOp",EDGE,"E7.26.0"),sQuery(id+"F0.wireOp",EDGE,"E7.26.1"),sQuery(id+"F0.wireOp",EDGE,"E7.26.2"),sQuery(id+"F0.wireOp",EDGE,"E7.26.3"),sQuery(id+"F0.wireOp",EDGE,"E7.26.4"),sQuery(id+"F0.wireOp",EDGE,"E7.26.5"),sQuery(id+"F0.wireOp",EDGE,"E7.27.0"),sQuery(id+"F0.wireOp",EDGE,"E7.27.1"),sQuery(id+"F0.wireOp",EDGE,"E7.27.2"),sQuery(id+"F0.wireOp",EDGE,"E7.27.3"),sQuery(id+"F0.wireOp",EDGE,"E7.27.4"),sQuery(id+"F0.wireOp",EDGE,"E7.27.5"),sQuery(id+"F0.wireOp",EDGE,"E7.28.0"),sQuery(id+"F0.wireOp",EDGE,"E7.28.1"),sQuery(id+"F0.wireOp",EDGE,"E7.28.2"),sQuery(id+"F0.wireOp",EDGE,"E7.28.3"),sQuery(id+"F0.wireOp",EDGE,"E7.28.4"),sQuery(id+"F0.wireOp",EDGE,"E7.28.5"),sQuery(id+"F0.wireOp",EDGE,"E7.29.0"),sQuery(id+"F0.wireOp",EDGE,"E7.29.1"),sQuery(id+"F0.wireOp",EDGE,"E7.29.2"),sQuery(id+"F0.wireOp",EDGE,"E7.29.3"),sQuery(id+"F0.wireOp",EDGE,"E7.29.4"),sQuery(id+"F0.wireOp",EDGE,"E7.29.5"),sQuery(id+"F0.wireOp",EDGE,"E7.30.0"),sQuery(id+"F0.wireOp",EDGE,"E7.30.1"),sQuery(id+"F0.wireOp",EDGE,"E7.30.2"),sQuery(id+"F0.wireOp",EDGE,"E7.30.3"),sQuery(id+"F0.wireOp",EDGE,"E7.30.4"),sQuery(id+"F0.wireOp",EDGE,"E7.30.5"),sQuery(id+"F0.wireOp",EDGE,"E7.31.0"),sQuery(id+"F0.wireOp",EDGE,"E7.31.1"),sQuery(id+"F0.wireOp",EDGE,"E7.31.2"),sQuery(id+"F0.wireOp",EDGE,"E7.31.3"),sQuery(id+"F0.wireOp",EDGE,"E7.31.4"),sQuery(id+"F0.wireOp",EDGE,"E7.31.5"),sQuery(id+"F0.wireOp",EDGE,"E7.32.0"),sQuery(id+"F0.wireOp",EDGE,"E7.32.1"),sQuery(id+"F0.wireOp",EDGE,"E7.32.2"),sQuery(id+"F0.wireOp",EDGE,"E7.32.3"),sQuery(id+"F0.wireOp",EDGE,"E7.32.4"),sQuery(id+"F0.wireOp",EDGE,"E7.32.5"),sQuery(id+"F0.wireOp",EDGE,"E7.33.0"),sQuery(id+"F0.wireOp",EDGE,"E7.33.1"),sQuery(id+"F0.wireOp",EDGE,"E7.33.2"),sQuery(id+"F0.wireOp",EDGE,"E7.33.3"),sQuery(id+"F0.wireOp",EDGE,"E7.33.4"),sQuery(id+"F0.wireOp",EDGE,"E7.33.5"),sQuery(id+"F0.wireOp",EDGE,"E7.34.0"),sQuery(id+"F0.wireOp",EDGE,"E7.34.1"),sQuery(id+"F0.wireOp",EDGE,"E7.34.2"),sQuery(id+"F0.wireOp",EDGE,"E7.34.3"),sQuery(id+"F0.wireOp",EDGE,"E7.34.4"),sQuery(id+"F0.wireOp",EDGE,"E7.34.5"),sQuery(id+"F0.wireOp",EDGE,"E7.35.0"),sQuery(id+"F0.wireOp",EDGE,"E7.35.1"),sQuery(id+"F0.wireOp",EDGE,"E7.35.2"),sQuery(id+"F0.wireOp",EDGE,"E7.35.3"),sQuery(id+"F0.wireOp",EDGE,"E7.35.4"),sQuery(id+"F0.wireOp",EDGE,"E7.35.5"),sQuery(id+"F0.wireOp",EDGE,"E7.36.0"),sQuery(id+"F0.wireOp",EDGE,"E7.36.1"),sQuery(id+"F0.wireOp",EDGE,"E7.36.2"),sQuery(id+"F0.wireOp",EDGE,"E7.36.3"),sQuery(id+"F0.wireOp",EDGE,"E7.36.4"),sQuery(id+"F0.wireOp",EDGE,"E7.36.5"),sQuery(id+"F0.wireOp",EDGE,"E7.37.0"),sQuery(id+"F0.wireOp",EDGE,"E7.37.1"),sQuery(id+"F0.wireOp",EDGE,"E7.37.2"),sQuery(id+"F0.wireOp",EDGE,"E7.37.3"),sQuery(id+"F0.wireOp",EDGE,"E7.37.4"),sQuery(id+"F0.wireOp",EDGE,"E7.37.5"),sQuery(id+"F0.wireOp",EDGE,"E7.38.0"),sQuery(id+"F0.wireOp",EDGE,"E7.38.1"),sQuery(id+"F0.wireOp",EDGE,"E7.38.2"),sQuery(id+"F0.wireOp",EDGE,"E7.38.3"),sQuery(id+"F0.wireOp",EDGE,"E7.38.4"),sQuery(id+"F0.wireOp",EDGE,"E7.38.5"),sQuery(id+"F0.wireOp",EDGE,"E7.39.0"),sQuery(id+"F0.wireOp",EDGE,"E7.39.1"),sQuery(id+"F0.wireOp",EDGE,"E7.39.2"),sQuery(id+"F0.wireOp",EDGE,"E7.39.3"),sQuery(id+"F0.wireOp",EDGE,"E7.39.4"),sQuery(id+"F0.wireOp",EDGE,"E7.39.5"),sQuery(id+"F0.wireOp",EDGE,"E7.40.0"),sQuery(id+"F0.wireOp",EDGE,"E7.40.1"),sQuery(id+"F0.wireOp",EDGE,"E7.40.2"),sQuery(id+"F0.wireOp",EDGE,"E7.40.3"),sQuery(id+"F0.wireOp",EDGE,"E7.40.4"),sQuery(id+"F0.wireOp",EDGE,"E7.40.5"),sQuery(id+"F0.wireOp",EDGE,"E7.41.0"),sQuery(id+"F0.wireOp",EDGE,"E7.41.1"),sQuery(id+"F0.wireOp",EDGE,"E7.41.2"),sQuery(id+"F0.wireOp",EDGE,"E7.41.3"),sQuery(id+"F0.wireOp",EDGE,"E7.41.4"),sQuery(id+"F0.wireOp",EDGE,"E7.41.5"),sQuery(id+"F0.wireOp",EDGE,"E7.42.0"),sQuery(id+"F0.wireOp",EDGE,"E7.42.1"),sQuery(id+"F0.wireOp",EDGE,"E7.42.2"),sQuery(id+"F0.wireOp",EDGE,"E7.42.3"),sQuery(id+"F0.wireOp",EDGE,"E7.42.4"),sQuery(id+"F0.wireOp",EDGE,"E7.42.5"),sQuery(id+"F0.wireOp",EDGE,"E7.43.0"),sQuery(id+"F0.wireOp",EDGE,"E7.43.1"),sQuery(id+"F0.wireOp",EDGE,"E7.43.2"),sQuery(id+"F0.wireOp",EDGE,"E7.43.3"),sQuery(id+"F0.wireOp",EDGE,"E7.43.4"),sQuery(id+"F0.wireOp",EDGE,"E7.43.5")])],"isStart":true})],"blendedInto":[makeQuery(id+"F1.opExtrude","CAP_FACE",FACE,{"disambiguationData":[OSD([sQuery(id+"F0.wireOp",EDGE,"E1"),sQuery(id+"F0.wireOp",EDGE,"E2"),sQuery(id+"F0.wireOp",EDGE,"E3"),sQuery(id+"F0.wireOp",EDGE,"E4"),sQuery(id+"F0.wireOp",EDGE,"E5"),sQuery(id+"F0.wireOp",EDGE,"E6"),sQuery(id+"F0.wireOp",EDGE,"E7.1.0"),sQuery(id+"F0.wireOp",EDGE,"E7.1.1"),sQuery(id+"F0.wireOp",EDGE,"E7.1.2"),sQuery(id+"F0.wireOp",EDGE,"E7.1.3"),sQuery(id+"F0.wireOp",EDGE,"E7.1.4"),sQuery(id+"F0.wireOp",EDGE,"E7.1.5"),sQuery(id+"F0.wireOp",EDGE,"E7.2.0"),sQuery(id+"F0.wireOp",EDGE,"E7.2.1"),sQuery(id+"F0.wireOp",EDGE,"E7.2.2"),sQuery(id+"F0.wireOp",EDGE,"E7.2.3"),sQuery(id+"F0.wireOp",EDGE,"E7.2.4"),sQuery(id+"F0.wireOp",EDGE,"E7.2.5"),sQuery(id+"F0.wireOp",EDGE,"E7.3.0"),sQuery(id+"F0.wireOp",EDGE,"E7.3.1"),sQuery(id+"F0.wireOp",EDGE,"E7.3.2"),sQuery(id+"F0.wireOp",EDGE,"E7.3.3"),sQuery(id+"F0.wireOp",EDGE,"E7.3.4"),sQuery(id+"F0.wireOp",EDGE,"E7.3.5"),sQuery(id+"F0.wireOp",EDGE,"E7.4.0"),sQuery(id+"F0.wireOp",EDGE,"E7.4.1"),sQuery(id+"F0.wireOp",EDGE,"E7.4.2"),sQuery(id+"F0.wireOp",EDGE,"E7.4.3"),sQuery(id+"F0.wireOp",EDGE,"E7.4.4"),sQuery(id+"F0.wireOp",EDGE,"E7.4.5"),sQuery(id+"F0.wireOp",EDGE,"E7.5.0"),sQuery(id+"F0.wireOp",EDGE,"E7.5.1"),sQuery(id+"F0.wireOp",EDGE,"E7.5.2"),sQuery(id+"F0.wireOp",EDGE,"E7.5.3"),sQuery(id+"F0.wireOp",EDGE,"E7.5.4"),sQuery(id+"F0.wireOp",EDGE,"E7.5.5"),subQ0,sQuery(id+"F0.wireOp",EDGE,"E7.6.1"),sQuery(id+"F0.wireOp",EDGE,"E7.6.2"),sQuery(id+"F0.wireOp",EDGE,"E7.6.3"),sQuery(id+"F0.wireOp",EDGE,"E7.6.4"),sQuery(id+"F0.wireOp",EDGE,"E7.6.5"),sQuery(id+"F0.wireOp",EDGE,"E7.7.0"),sQuery(id+"F0.wireOp",EDGE,"E7.7.1"),sQuery(id+"F0.wireOp",EDGE,"E7.7.2"),sQuery(id+"F0.wireOp",EDGE,"E7.7.3"),sQuery(id+"F0.wireOp",EDGE,"E7.7.4"),sQuery(id+"F0.wireOp",EDGE,"E7.7.5"),sQuery(id+"F0.wireOp",EDGE,"E7.8.0"),sQuery(id+"F0.wireOp",EDGE,"E7.8.1"),sQuery(id+"F0.wireOp",EDGE,"E7.8.2"),sQuery(id+"F0.wireOp",EDGE,"E7.8.3"),sQuery(id+"F0.wireOp",EDGE,"E7.8.4"),sQuery(id+"F0.wireOp",EDGE,"E7.8.5"),sQuery(id+"F0.wireOp",EDGE,"E7.9.0"),sQuery(id+"F0.wireOp",EDGE,"E7.9.1"),sQuery(id+"F0.wireOp",EDGE,"E7.9.2"),sQuery(id+"F0.wireOp",EDGE,"E7.9.3"),sQuery(id+"F0.wireOp",EDGE,"E7.9.4"),sQuery(id+"F0.wireOp",EDGE,"E7.9.5"),sQuery(id+"F0.wireOp",EDGE,"E7.10.0"),sQuery(id+"F0.wireOp",EDGE,"E7.10.1"),sQuery(id+"F0.wireOp",EDGE,"E7.10.2"),sQuery(id+"F0.wireOp",EDGE,"E7.10.3"),sQuery(id+"F0.wireOp",EDGE,"E7.10.4"),sQuery(id+"F0.wireOp",EDGE,"E7.10.5"),sQuery(id+"F0.wireOp",EDGE,"E7.11.0"),sQuery(id+"F0.wireOp",EDGE,"E7.11.1"),sQuery(id+"F0.wireOp",EDGE,"E7.11.2"),sQuery(id+"F0.wireOp",EDGE,"E7.11.3"),sQuery(id+"F0.wireOp",EDGE,"E7.11.4"),sQuery(id+"F0.wireOp",EDGE,"E7.11.5"),sQuery(id+"F0.wireOp",EDGE,"E7.12.0"),sQuery(id+"F0.wireOp",EDGE,"E7.12.1"),sQuery(id+"F0.wireOp",EDGE,"E7.12.2"),sQuery(id+"F0.wireOp",EDGE,"E7.12.3"),sQuery(id+"F0.wireOp",EDGE,"E7.12.4"),sQuery(id+"F0.wireOp",EDGE,"E7.12.5"),sQuery(id+"F0.wireOp",EDGE,"E7.13.0"),sQuery(id+"F0.wireOp",EDGE,"E7.13.1"),sQuery(id+"F0.wireOp",EDGE,"E7.13.2"),sQuery(id+"F0.wireOp",EDGE,"E7.13.3"),sQuery(id+"F0.wireOp",EDGE,"E7.13.4"),sQuery(id+"F0.wireOp",EDGE,"E7.13.5"),sQuery(id+"F0.wireOp",EDGE,"E7.14.0"),sQuery(id+"F0.wireOp",EDGE,"E7.14.1"),sQuery(id+"F0.wireOp",EDGE,"E7.14.2"),sQuery(id+"F0.wireOp",EDGE,"E7.14.3"),sQuery(id+"F0.wireOp",EDGE,"E7.14.4"),sQuery(id+"F0.wireOp",EDGE,"E7.14.5"),sQuery(id+"F0.wireOp",EDGE,"E7.15.0"),sQuery(id+"F0.wireOp",EDGE,"E7.15.1"),sQuery(id+"F0.wireOp",EDGE,"E7.15.2"),sQuery(id+"F0.wireOp",EDGE,"E7.15.3"),sQuery(id+"F0.wireOp",EDGE,"E7.15.4"),sQuery(id+"F0.wireOp",EDGE,"E7.15.5"),sQuery(id+"F0.wireOp",EDGE,"E7.16.0"),sQuery(id+"F0.wireOp",EDGE,"E7.16.1"),sQuery(id+"F0.wireOp",EDGE,"E7.16.2"),sQuery(id+"F0.wireOp",EDGE,"E7.16.3"),sQuery(id+"F0.wireOp",EDGE,"E7.16.4"),sQuery(id+"F0.wireOp",EDGE,"E7.16.5"),sQuery(id+"F0.wireOp",EDGE,"E7.17.0"),sQuery(id+"F0.wireOp",EDGE,"E7.17.1"),sQuery(id+"F0.wireOp",EDGE,"E7.17.2"),sQuery(id+"F0.wireOp",EDGE,"E7.17.3"),sQuery(id+"F0.wireOp",EDGE,"E7.17.4"),sQuery(id+"F0.wireOp",EDGE,"E7.17.5"),sQuery(id+"F0.wireOp",EDGE,"E7.18.0"),sQuery(id+"F0.wireOp",EDGE,"E7.18.1"),sQuery(id+"F0.wireOp",EDGE,"E7.18.2"),sQuery(id+"F0.wireOp",EDGE,"E7.18.3"),sQuery(id+"F0.wireOp",EDGE,"E7.18.4"),sQuery(id+"F0.wireOp",EDGE,"E7.18.5"),sQuery(id+"F0.wireOp",EDGE,"E7.19.0"),sQuery(id+"F0.wireOp",EDGE,"E7.19.1"),sQuery(id+"F0.wireOp",EDGE,"E7.19.2"),sQuery(id+"F0.wireOp",EDGE,"E7.19.3"),sQuery(id+"F0.wireOp",EDGE,"E7.19.4"),sQuery(id+"F0.wireOp",EDGE,"E7.19.5"),sQuery(id+"F0.wireOp",EDGE,"E7.20.0"),sQuery(id+"F0.wireOp",EDGE,"E7.20.1"),sQuery(id+"F0.wireOp",EDGE,"E7.20.2"),sQuery(id+"F0.wireOp",EDGE,"E7.20.3"),sQuery(id+"F0.wireOp",EDGE,"E7.20.4"),sQuery(id+"F0.wireOp",EDGE,"E7.20.5"),sQuery(id+"F0.wireOp",EDGE,"E7.21.0"),sQuery(id+"F0.wireOp",EDGE,"E7.21.1"),sQuery(id+"F0.wireOp",EDGE,"E7.21.2"),sQuery(id+"F0.wireOp",EDGE,"E7.21.3"),sQuery(id+"F0.wireOp",EDGE,"E7.21.4"),sQuery(id+"F0.wireOp",EDGE,"E7.21.5"),sQuery(id+"F0.wireOp",EDGE,"E7.22.0"),sQuery(id+"F0.wireOp",EDGE,"E7.22.1"),sQuery(id+"F0.wireOp",EDGE,"E7.22.2"),sQuery(id+"F0.wireOp",EDGE,"E7.22.3"),sQuery(id+"F0.wireOp",EDGE,"E7.22.4"),sQuery(id+"F0.wireOp",EDGE,"E7.22.5"),sQuery(id+"F0.wireOp",EDGE,"E7.23.0"),sQuery(id+"F0.wireOp",EDGE,"E7.23.1"),sQuery(id+"F0.wireOp",EDGE,"E7.23.2"),sQuery(id+"F0.wireOp",EDGE,"E7.23.3"),sQuery(id+"F0.wireOp",EDGE,"E7.23.4"),sQuery(id+"F0.wireOp",EDGE,"E7.23.5"),sQuery(id+"F0.wireOp",EDGE,"E7.24.0"),sQuery(id+"F0.wireOp",EDGE,"E7.24.1"),sQuery(id+"F0.wireOp",EDGE,"E7.24.2"),sQuery(id+"F0.wireOp",EDGE,"E7.24.3"),sQuery(id+"F0.wireOp",EDGE,"E7.24.4"),sQuery(id+"F0.wireOp",EDGE,"E7.24.5"),sQuery(id+"F0.wireOp",EDGE,"E7.25.0"),sQuery(id+"F0.wireOp",EDGE,"E7.25.1"),sQuery(id+"F0.wireOp",EDGE,"E7.25.2"),sQuery(id+"F0.wireOp",EDGE,"E7.25.3"),sQuery(id+"F0.wireOp",EDGE,"E7.25.4"),sQuery(id+"F0.wireOp",EDGE,"E7.25.5"),sQuery(id+"F0.wireOp",EDGE,"E7.26.0"),sQuery(id+"F0.wireOp",EDGE,"E7.26.1"),sQuery(id+"F0.wireOp",EDGE,"E7.26.2"),sQuery(id+"F0.wireOp",EDGE,"E7.26.3"),sQuery(id+"F0.wireOp",EDGE,"E7.26.4"),sQuery(id+"F0.wireOp",EDGE,"E7.26.5"),sQuery(id+"F0.wireOp",EDGE,"E7.27.0"),sQuery(id+"F0.wireOp",EDGE,"E7.27.1"),sQuery(id+"F0.wireOp",EDGE,"E7.27.2"),sQuery(id+"F0.wireOp",EDGE,"E7.27.3"),sQuery(id+"F0.wireOp",EDGE,"E7.27.4"),sQuery(id+"F0.wireOp",EDGE,"E7.27.5"),sQuery(id+"F0.wireOp",EDGE,"E7.28.0"),sQuery(id+"F0.wireOp",EDGE,"E7.28.1"),sQuery(id+"F0.wireOp",EDGE,"E7.28.2"),sQuery(id+"F0.wireOp",EDGE,"E7.28.3"),sQuery(id+"F0.wireOp",EDGE,"E7.28.4"),sQuery(id+"F0.wireOp",EDGE,"E7.28.5"),sQuery(id+"F0.wireOp",EDGE,"E7.29.0"),sQuery(id+"F0.wireOp",EDGE,"E7.29.1"),sQuery(id+"F0.wireOp",EDGE,"E7.29.2"),sQuery(id+"F0.wireOp",EDGE,"E7.29.3"),sQuery(id+"F0.wireOp",EDGE,"E7.29.4"),sQuery(id+"F0.wireOp",EDGE,"E7.29.5"),sQuery(id+"F0.wireOp",EDGE,"E7.30.0"),sQuery(id+"F0.wireOp",EDGE,"E7.30.1"),sQuery(id+"F0.wireOp",EDGE,"E7.30.2"),sQuery(id+"F0.wireOp",EDGE,"E7.30.3"),sQuery(id+"F0.wireOp",EDGE,"E7.30.4"),sQuery(id+"F0.wireOp",EDGE,"E7.30.5"),sQuery(id+"F0.wireOp",EDGE,"E7.31.0"),sQuery(id+"F0.wireOp",EDGE,"E7.31.1"),sQuery(id+"F0.wireOp",EDGE,"E7.31.2"),sQuery(id+"F0.wireOp",EDGE,"E7.31.3"),sQuery(id+"F0.wireOp",EDGE,"E7.31.4"),sQuery(id+"F0.wireOp",EDGE,"E7.31.5"),sQuery(id+"F0.wireOp",EDGE,"E7.32.0"),sQuery(id+"F0.wireOp",EDGE,"E7.32.1"),sQuery(id+"F0.wireOp",EDGE,"E7.32.2"),sQuery(id+"F0.wireOp",EDGE,"E7.32.3"),sQuery(id+"F0.wireOp",EDGE,"E7.32.4"),sQuery(id+"F0.wireOp",EDGE,"E7.32.5"),sQuery(id+"F0.wireOp",EDGE,"E7.33.0"),sQuery(id+"F0.wireOp",EDGE,"E7.33.1"),sQuery(id+"F0.wireOp",EDGE,"E7.33.2"),sQuery(id+"F0.wireOp",EDGE,"E7.33.3"),sQuery(id+"F0.wireOp",EDGE,"E7.33.4"),sQuery(id+"F0.wireOp",EDGE,"E7.33.5"),sQuery(id+"F0.wireOp",EDGE,"E7.34.0"),sQuery(id+"F0.wireOp",EDGE,"E7.34.1"),sQuery(id+"F0.wireOp",EDGE,"E7.34.2"),sQuery(id+"F0.wireOp",EDGE,"E7.34.3"),sQuery(id+"F0.wireOp",EDGE,"E7.34.4"),sQuery(id+"F0.wireOp",EDGE,"E7.34.5"),sQuery(id+"F0.wireOp",EDGE,"E7.35.0"),sQuery(id+"F0.wireOp",EDGE,"E7.35.1"),sQuery(id+"F0.wireOp",EDGE,"E7.35.2"),sQuery(id+"F0.wireOp",EDGE,"E7.35.3"),sQuery(id+"F0.wireOp",EDGE,"E7.35.4"),sQuery(id+"F0.wireOp",EDGE,"E7.35.5"),sQuery(id+"F0.wireOp",EDGE,"E7.36.0"),sQuery(id+"F0.wireOp",EDGE,"E7.36.1"),sQuery(id+"F0.wireOp",EDGE,"E7.36.2"),sQuery(id+"F0.wireOp",EDGE,"E7.36.3"),sQuery(id+"F0.wireOp",EDGE,"E7.36.4"),sQuery(id+"F0.wireOp",EDGE,"E7.36.5"),sQuery(id+"F0.wireOp",EDGE,"E7.37.0"),sQuery(id+"F0.wireOp",EDGE,"E7.37.1"),sQuery(id+"F0.wireOp",EDGE,"E7.37.2"),sQuery(id+"F0.wireOp",EDGE,"E7.37.3"),sQuery(id+"F0.wireOp",EDGE,"E7.37.4"),sQuery(id+"F0.wireOp",EDGE,"E7.37.5"),sQuery(id+"F0.wireOp",EDGE,"E7.38.0"),sQuery(id+"F0.wireOp",EDGE,"E7.38.1"),sQuery(id+"F0.wireOp",EDGE,"E7.38.2"),sQuery(id+"F0.wireOp",EDGE,"E7.38.3"),sQuery(id+"F0.wireOp",EDGE,"E7.38.4"),sQuery(id+"F0.wireOp",EDGE,"E7.38.5"),sQuery(id+"F0.wireOp",EDGE,"E7.39.0"),sQuery(id+"F0.wireOp",EDGE,"E7.39.1"),sQuery(id+"F0.wireOp",EDGE,"E7.39.2"),sQuery(id+"F0.wireOp",EDGE,"E7.39.3"),sQuery(id+"F0.wireOp",EDGE,"E7.39.4"),sQuery(id+"F0.wireOp",EDGE,"E7.39.5"),sQuery(id+"F0.wireOp",EDGE,"E7.40.0"),sQuery(id+"F0.wireOp",EDGE,"E7.40.1"),sQuery(id+"F0.wireOp",EDGE,"E7.40.2"),sQuery(id+"F0.wireOp",EDGE,"E7.40.3"),sQuery(id+"F0.wireOp",EDGE,"E7.40.4"),sQuery(id+"F0.wireOp",EDGE,"E7.40.5"),sQuery(id+"F0.wireOp",EDGE,"E7.41.0"),sQuery(id+"F0.wireOp",EDGE,"E7.41.1"),sQuery(id+"F0.wireOp",EDGE,"E7.41.2"),sQuery(id+"F0.wireOp",EDGE,"E7.41.3"),sQuery(id+"F0.wireOp",EDGE,"E7.41.4"),sQuery(id+"F0.wireOp",EDGE,"E7.41.5"),sQuery(id+"F0.wireOp",EDGE,"E7.42.0"),sQuery(id+"F0.wireOp",EDGE,"E7.42.1"),sQuery(id+"F0.wireOp",EDGE,"E7.42.2"),sQuery(id+"F0.wireOp",EDGE,"E7.42.3"),sQuery(id+"F0.wireOp",EDGE,"E7.42.4"),sQuery(id+"F0.wireOp",EDGE,"E7.42.5"),sQuery(id+"F0.wireOp",EDGE,"E7.43.0"),sQuery(id+"F0.wireOp",EDGE,"E7.43.1"),sQuery(id+"F0.wireOp",EDGE,"E7.43.2"),sQuery(id+"F0.wireOp",EDGE,"E7.43.3"),sQuery(id+"F0.wireOp",EDGE,"E7.43.4"),sQuery(id+"F0.wireOp",EDGE,"E7.43.5")])],"isStart":true})]});}
            var Q25;
            {var subQ0=sQuery(id+"F0.wireOp",EDGE,"E7.8.0");Q25=makeQuery(id+"F2.opChamfer","BLEND_EDGE",EDGE,{"blendedFrom":[makeQuery(id+"F1.opExtrude","CAP_EDGE",EDGE,{"disambiguationData":[OSD([subQ0])],"isStart":true}),makeQuery(id+"F1.opExtrude","CAP_FACE",FACE,{"disambiguationData":[OSD([sQuery(id+"F0.wireOp",EDGE,"E1"),sQuery(id+"F0.wireOp",EDGE,"E2"),sQuery(id+"F0.wireOp",EDGE,"E3"),sQuery(id+"F0.wireOp",EDGE,"E4"),sQuery(id+"F0.wireOp",EDGE,"E5"),sQuery(id+"F0.wireOp",EDGE,"E6"),sQuery(id+"F0.wireOp",EDGE,"E7.1.0"),sQuery(id+"F0.wireOp",EDGE,"E7.1.1"),sQuery(id+"F0.wireOp",EDGE,"E7.1.2"),sQuery(id+"F0.wireOp",EDGE,"E7.1.3"),sQuery(id+"F0.wireOp",EDGE,"E7.1.4"),sQuery(id+"F0.wireOp",EDGE,"E7.1.5"),sQuery(id+"F0.wireOp",EDGE,"E7.2.0"),sQuery(id+"F0.wireOp",EDGE,"E7.2.1"),sQuery(id+"F0.wireOp",EDGE,"E7.2.2"),sQuery(id+"F0.wireOp",EDGE,"E7.2.3"),sQuery(id+"F0.wireOp",EDGE,"E7.2.4"),sQuery(id+"F0.wireOp",EDGE,"E7.2.5"),sQuery(id+"F0.wireOp",EDGE,"E7.3.0"),sQuery(id+"F0.wireOp",EDGE,"E7.3.1"),sQuery(id+"F0.wireOp",EDGE,"E7.3.2"),sQuery(id+"F0.wireOp",EDGE,"E7.3.3"),sQuery(id+"F0.wireOp",EDGE,"E7.3.4"),sQuery(id+"F0.wireOp",EDGE,"E7.3.5"),sQuery(id+"F0.wireOp",EDGE,"E7.4.0"),sQuery(id+"F0.wireOp",EDGE,"E7.4.1"),sQuery(id+"F0.wireOp",EDGE,"E7.4.2"),sQuery(id+"F0.wireOp",EDGE,"E7.4.3"),sQuery(id+"F0.wireOp",EDGE,"E7.4.4"),sQuery(id+"F0.wireOp",EDGE,"E7.4.5"),sQuery(id+"F0.wireOp",EDGE,"E7.5.0"),sQuery(id+"F0.wireOp",EDGE,"E7.5.1"),sQuery(id+"F0.wireOp",EDGE,"E7.5.2"),sQuery(id+"F0.wireOp",EDGE,"E7.5.3"),sQuery(id+"F0.wireOp",EDGE,"E7.5.4"),sQuery(id+"F0.wireOp",EDGE,"E7.5.5"),sQuery(id+"F0.wireOp",EDGE,"E7.6.0"),sQuery(id+"F0.wireOp",EDGE,"E7.6.1"),sQuery(id+"F0.wireOp",EDGE,"E7.6.2"),sQuery(id+"F0.wireOp",EDGE,"E7.6.3"),sQuery(id+"F0.wireOp",EDGE,"E7.6.4"),sQuery(id+"F0.wireOp",EDGE,"E7.6.5"),sQuery(id+"F0.wireOp",EDGE,"E7.7.0"),sQuery(id+"F0.wireOp",EDGE,"E7.7.1"),sQuery(id+"F0.wireOp",EDGE,"E7.7.2"),sQuery(id+"F0.wireOp",EDGE,"E7.7.3"),sQuery(id+"F0.wireOp",EDGE,"E7.7.4"),sQuery(id+"F0.wireOp",EDGE,"E7.7.5"),subQ0,sQuery(id+"F0.wireOp",EDGE,"E7.8.1"),sQuery(id+"F0.wireOp",EDGE,"E7.8.2"),sQuery(id+"F0.wireOp",EDGE,"E7.8.3"),sQuery(id+"F0.wireOp",EDGE,"E7.8.4"),sQuery(id+"F0.wireOp",EDGE,"E7.8.5"),sQuery(id+"F0.wireOp",EDGE,"E7.9.0"),sQuery(id+"F0.wireOp",EDGE,"E7.9.1"),sQuery(id+"F0.wireOp",EDGE,"E7.9.2"),sQuery(id+"F0.wireOp",EDGE,"E7.9.3"),sQuery(id+"F0.wireOp",EDGE,"E7.9.4"),sQuery(id+"F0.wireOp",EDGE,"E7.9.5"),sQuery(id+"F0.wireOp",EDGE,"E7.10.0"),sQuery(id+"F0.wireOp",EDGE,"E7.10.1"),sQuery(id+"F0.wireOp",EDGE,"E7.10.2"),sQuery(id+"F0.wireOp",EDGE,"E7.10.3"),sQuery(id+"F0.wireOp",EDGE,"E7.10.4"),sQuery(id+"F0.wireOp",EDGE,"E7.10.5"),sQuery(id+"F0.wireOp",EDGE,"E7.11.0"),sQuery(id+"F0.wireOp",EDGE,"E7.11.1"),sQuery(id+"F0.wireOp",EDGE,"E7.11.2"),sQuery(id+"F0.wireOp",EDGE,"E7.11.3"),sQuery(id+"F0.wireOp",EDGE,"E7.11.4"),sQuery(id+"F0.wireOp",EDGE,"E7.11.5"),sQuery(id+"F0.wireOp",EDGE,"E7.12.0"),sQuery(id+"F0.wireOp",EDGE,"E7.12.1"),sQuery(id+"F0.wireOp",EDGE,"E7.12.2"),sQuery(id+"F0.wireOp",EDGE,"E7.12.3"),sQuery(id+"F0.wireOp",EDGE,"E7.12.4"),sQuery(id+"F0.wireOp",EDGE,"E7.12.5"),sQuery(id+"F0.wireOp",EDGE,"E7.13.0"),sQuery(id+"F0.wireOp",EDGE,"E7.13.1"),sQuery(id+"F0.wireOp",EDGE,"E7.13.2"),sQuery(id+"F0.wireOp",EDGE,"E7.13.3"),sQuery(id+"F0.wireOp",EDGE,"E7.13.4"),sQuery(id+"F0.wireOp",EDGE,"E7.13.5"),sQuery(id+"F0.wireOp",EDGE,"E7.14.0"),sQuery(id+"F0.wireOp",EDGE,"E7.14.1"),sQuery(id+"F0.wireOp",EDGE,"E7.14.2"),sQuery(id+"F0.wireOp",EDGE,"E7.14.3"),sQuery(id+"F0.wireOp",EDGE,"E7.14.4"),sQuery(id+"F0.wireOp",EDGE,"E7.14.5"),sQuery(id+"F0.wireOp",EDGE,"E7.15.0"),sQuery(id+"F0.wireOp",EDGE,"E7.15.1"),sQuery(id+"F0.wireOp",EDGE,"E7.15.2"),sQuery(id+"F0.wireOp",EDGE,"E7.15.3"),sQuery(id+"F0.wireOp",EDGE,"E7.15.4"),sQuery(id+"F0.wireOp",EDGE,"E7.15.5"),sQuery(id+"F0.wireOp",EDGE,"E7.16.0"),sQuery(id+"F0.wireOp",EDGE,"E7.16.1"),sQuery(id+"F0.wireOp",EDGE,"E7.16.2"),sQuery(id+"F0.wireOp",EDGE,"E7.16.3"),sQuery(id+"F0.wireOp",EDGE,"E7.16.4"),sQuery(id+"F0.wireOp",EDGE,"E7.16.5"),sQuery(id+"F0.wireOp",EDGE,"E7.17.0"),sQuery(id+"F0.wireOp",EDGE,"E7.17.1"),sQuery(id+"F0.wireOp",EDGE,"E7.17.2"),sQuery(id+"F0.wireOp",EDGE,"E7.17.3"),sQuery(id+"F0.wireOp",EDGE,"E7.17.4"),sQuery(id+"F0.wireOp",EDGE,"E7.17.5"),sQuery(id+"F0.wireOp",EDGE,"E7.18.0"),sQuery(id+"F0.wireOp",EDGE,"E7.18.1"),sQuery(id+"F0.wireOp",EDGE,"E7.18.2"),sQuery(id+"F0.wireOp",EDGE,"E7.18.3"),sQuery(id+"F0.wireOp",EDGE,"E7.18.4"),sQuery(id+"F0.wireOp",EDGE,"E7.18.5"),sQuery(id+"F0.wireOp",EDGE,"E7.19.0"),sQuery(id+"F0.wireOp",EDGE,"E7.19.1"),sQuery(id+"F0.wireOp",EDGE,"E7.19.2"),sQuery(id+"F0.wireOp",EDGE,"E7.19.3"),sQuery(id+"F0.wireOp",EDGE,"E7.19.4"),sQuery(id+"F0.wireOp",EDGE,"E7.19.5"),sQuery(id+"F0.wireOp",EDGE,"E7.20.0"),sQuery(id+"F0.wireOp",EDGE,"E7.20.1"),sQuery(id+"F0.wireOp",EDGE,"E7.20.2"),sQuery(id+"F0.wireOp",EDGE,"E7.20.3"),sQuery(id+"F0.wireOp",EDGE,"E7.20.4"),sQuery(id+"F0.wireOp",EDGE,"E7.20.5"),sQuery(id+"F0.wireOp",EDGE,"E7.21.0"),sQuery(id+"F0.wireOp",EDGE,"E7.21.1"),sQuery(id+"F0.wireOp",EDGE,"E7.21.2"),sQuery(id+"F0.wireOp",EDGE,"E7.21.3"),sQuery(id+"F0.wireOp",EDGE,"E7.21.4"),sQuery(id+"F0.wireOp",EDGE,"E7.21.5"),sQuery(id+"F0.wireOp",EDGE,"E7.22.0"),sQuery(id+"F0.wireOp",EDGE,"E7.22.1"),sQuery(id+"F0.wireOp",EDGE,"E7.22.2"),sQuery(id+"F0.wireOp",EDGE,"E7.22.3"),sQuery(id+"F0.wireOp",EDGE,"E7.22.4"),sQuery(id+"F0.wireOp",EDGE,"E7.22.5"),sQuery(id+"F0.wireOp",EDGE,"E7.23.0"),sQuery(id+"F0.wireOp",EDGE,"E7.23.1"),sQuery(id+"F0.wireOp",EDGE,"E7.23.2"),sQuery(id+"F0.wireOp",EDGE,"E7.23.3"),sQuery(id+"F0.wireOp",EDGE,"E7.23.4"),sQuery(id+"F0.wireOp",EDGE,"E7.23.5"),sQuery(id+"F0.wireOp",EDGE,"E7.24.0"),sQuery(id+"F0.wireOp",EDGE,"E7.24.1"),sQuery(id+"F0.wireOp",EDGE,"E7.24.2"),sQuery(id+"F0.wireOp",EDGE,"E7.24.3"),sQuery(id+"F0.wireOp",EDGE,"E7.24.4"),sQuery(id+"F0.wireOp",EDGE,"E7.24.5"),sQuery(id+"F0.wireOp",EDGE,"E7.25.0"),sQuery(id+"F0.wireOp",EDGE,"E7.25.1"),sQuery(id+"F0.wireOp",EDGE,"E7.25.2"),sQuery(id+"F0.wireOp",EDGE,"E7.25.3"),sQuery(id+"F0.wireOp",EDGE,"E7.25.4"),sQuery(id+"F0.wireOp",EDGE,"E7.25.5"),sQuery(id+"F0.wireOp",EDGE,"E7.26.0"),sQuery(id+"F0.wireOp",EDGE,"E7.26.1"),sQuery(id+"F0.wireOp",EDGE,"E7.26.2"),sQuery(id+"F0.wireOp",EDGE,"E7.26.3"),sQuery(id+"F0.wireOp",EDGE,"E7.26.4"),sQuery(id+"F0.wireOp",EDGE,"E7.26.5"),sQuery(id+"F0.wireOp",EDGE,"E7.27.0"),sQuery(id+"F0.wireOp",EDGE,"E7.27.1"),sQuery(id+"F0.wireOp",EDGE,"E7.27.2"),sQuery(id+"F0.wireOp",EDGE,"E7.27.3"),sQuery(id+"F0.wireOp",EDGE,"E7.27.4"),sQuery(id+"F0.wireOp",EDGE,"E7.27.5"),sQuery(id+"F0.wireOp",EDGE,"E7.28.0"),sQuery(id+"F0.wireOp",EDGE,"E7.28.1"),sQuery(id+"F0.wireOp",EDGE,"E7.28.2"),sQuery(id+"F0.wireOp",EDGE,"E7.28.3"),sQuery(id+"F0.wireOp",EDGE,"E7.28.4"),sQuery(id+"F0.wireOp",EDGE,"E7.28.5"),sQuery(id+"F0.wireOp",EDGE,"E7.29.0"),sQuery(id+"F0.wireOp",EDGE,"E7.29.1"),sQuery(id+"F0.wireOp",EDGE,"E7.29.2"),sQuery(id+"F0.wireOp",EDGE,"E7.29.3"),sQuery(id+"F0.wireOp",EDGE,"E7.29.4"),sQuery(id+"F0.wireOp",EDGE,"E7.29.5"),sQuery(id+"F0.wireOp",EDGE,"E7.30.0"),sQuery(id+"F0.wireOp",EDGE,"E7.30.1"),sQuery(id+"F0.wireOp",EDGE,"E7.30.2"),sQuery(id+"F0.wireOp",EDGE,"E7.30.3"),sQuery(id+"F0.wireOp",EDGE,"E7.30.4"),sQuery(id+"F0.wireOp",EDGE,"E7.30.5"),sQuery(id+"F0.wireOp",EDGE,"E7.31.0"),sQuery(id+"F0.wireOp",EDGE,"E7.31.1"),sQuery(id+"F0.wireOp",EDGE,"E7.31.2"),sQuery(id+"F0.wireOp",EDGE,"E7.31.3"),sQuery(id+"F0.wireOp",EDGE,"E7.31.4"),sQuery(id+"F0.wireOp",EDGE,"E7.31.5"),sQuery(id+"F0.wireOp",EDGE,"E7.32.0"),sQuery(id+"F0.wireOp",EDGE,"E7.32.1"),sQuery(id+"F0.wireOp",EDGE,"E7.32.2"),sQuery(id+"F0.wireOp",EDGE,"E7.32.3"),sQuery(id+"F0.wireOp",EDGE,"E7.32.4"),sQuery(id+"F0.wireOp",EDGE,"E7.32.5"),sQuery(id+"F0.wireOp",EDGE,"E7.33.0"),sQuery(id+"F0.wireOp",EDGE,"E7.33.1"),sQuery(id+"F0.wireOp",EDGE,"E7.33.2"),sQuery(id+"F0.wireOp",EDGE,"E7.33.3"),sQuery(id+"F0.wireOp",EDGE,"E7.33.4"),sQuery(id+"F0.wireOp",EDGE,"E7.33.5"),sQuery(id+"F0.wireOp",EDGE,"E7.34.0"),sQuery(id+"F0.wireOp",EDGE,"E7.34.1"),sQuery(id+"F0.wireOp",EDGE,"E7.34.2"),sQuery(id+"F0.wireOp",EDGE,"E7.34.3"),sQuery(id+"F0.wireOp",EDGE,"E7.34.4"),sQuery(id+"F0.wireOp",EDGE,"E7.34.5"),sQuery(id+"F0.wireOp",EDGE,"E7.35.0"),sQuery(id+"F0.wireOp",EDGE,"E7.35.1"),sQuery(id+"F0.wireOp",EDGE,"E7.35.2"),sQuery(id+"F0.wireOp",EDGE,"E7.35.3"),sQuery(id+"F0.wireOp",EDGE,"E7.35.4"),sQuery(id+"F0.wireOp",EDGE,"E7.35.5"),sQuery(id+"F0.wireOp",EDGE,"E7.36.0"),sQuery(id+"F0.wireOp",EDGE,"E7.36.1"),sQuery(id+"F0.wireOp",EDGE,"E7.36.2"),sQuery(id+"F0.wireOp",EDGE,"E7.36.3"),sQuery(id+"F0.wireOp",EDGE,"E7.36.4"),sQuery(id+"F0.wireOp",EDGE,"E7.36.5"),sQuery(id+"F0.wireOp",EDGE,"E7.37.0"),sQuery(id+"F0.wireOp",EDGE,"E7.37.1"),sQuery(id+"F0.wireOp",EDGE,"E7.37.2"),sQuery(id+"F0.wireOp",EDGE,"E7.37.3"),sQuery(id+"F0.wireOp",EDGE,"E7.37.4"),sQuery(id+"F0.wireOp",EDGE,"E7.37.5"),sQuery(id+"F0.wireOp",EDGE,"E7.38.0"),sQuery(id+"F0.wireOp",EDGE,"E7.38.1"),sQuery(id+"F0.wireOp",EDGE,"E7.38.2"),sQuery(id+"F0.wireOp",EDGE,"E7.38.3"),sQuery(id+"F0.wireOp",EDGE,"E7.38.4"),sQuery(id+"F0.wireOp",EDGE,"E7.38.5"),sQuery(id+"F0.wireOp",EDGE,"E7.39.0"),sQuery(id+"F0.wireOp",EDGE,"E7.39.1"),sQuery(id+"F0.wireOp",EDGE,"E7.39.2"),sQuery(id+"F0.wireOp",EDGE,"E7.39.3"),sQuery(id+"F0.wireOp",EDGE,"E7.39.4"),sQuery(id+"F0.wireOp",EDGE,"E7.39.5"),sQuery(id+"F0.wireOp",EDGE,"E7.40.0"),sQuery(id+"F0.wireOp",EDGE,"E7.40.1"),sQuery(id+"F0.wireOp",EDGE,"E7.40.2"),sQuery(id+"F0.wireOp",EDGE,"E7.40.3"),sQuery(id+"F0.wireOp",EDGE,"E7.40.4"),sQuery(id+"F0.wireOp",EDGE,"E7.40.5"),sQuery(id+"F0.wireOp",EDGE,"E7.41.0"),sQuery(id+"F0.wireOp",EDGE,"E7.41.1"),sQuery(id+"F0.wireOp",EDGE,"E7.41.2"),sQuery(id+"F0.wireOp",EDGE,"E7.41.3"),sQuery(id+"F0.wireOp",EDGE,"E7.41.4"),sQuery(id+"F0.wireOp",EDGE,"E7.41.5"),sQuery(id+"F0.wireOp",EDGE,"E7.42.0"),sQuery(id+"F0.wireOp",EDGE,"E7.42.1"),sQuery(id+"F0.wireOp",EDGE,"E7.42.2"),sQuery(id+"F0.wireOp",EDGE,"E7.42.3"),sQuery(id+"F0.wireOp",EDGE,"E7.42.4"),sQuery(id+"F0.wireOp",EDGE,"E7.42.5"),sQuery(id+"F0.wireOp",EDGE,"E7.43.0"),sQuery(id+"F0.wireOp",EDGE,"E7.43.1"),sQuery(id+"F0.wireOp",EDGE,"E7.43.2"),sQuery(id+"F0.wireOp",EDGE,"E7.43.3"),sQuery(id+"F0.wireOp",EDGE,"E7.43.4"),sQuery(id+"F0.wireOp",EDGE,"E7.43.5")])],"isStart":true})],"blendedInto":[makeQuery(id+"F1.opExtrude","CAP_FACE",FACE,{"disambiguationData":[OSD([sQuery(id+"F0.wireOp",EDGE,"E1"),sQuery(id+"F0.wireOp",EDGE,"E2"),sQuery(id+"F0.wireOp",EDGE,"E3"),sQuery(id+"F0.wireOp",EDGE,"E4"),sQuery(id+"F0.wireOp",EDGE,"E5"),sQuery(id+"F0.wireOp",EDGE,"E6"),sQuery(id+"F0.wireOp",EDGE,"E7.1.0"),sQuery(id+"F0.wireOp",EDGE,"E7.1.1"),sQuery(id+"F0.wireOp",EDGE,"E7.1.2"),sQuery(id+"F0.wireOp",EDGE,"E7.1.3"),sQuery(id+"F0.wireOp",EDGE,"E7.1.4"),sQuery(id+"F0.wireOp",EDGE,"E7.1.5"),sQuery(id+"F0.wireOp",EDGE,"E7.2.0"),sQuery(id+"F0.wireOp",EDGE,"E7.2.1"),sQuery(id+"F0.wireOp",EDGE,"E7.2.2"),sQuery(id+"F0.wireOp",EDGE,"E7.2.3"),sQuery(id+"F0.wireOp",EDGE,"E7.2.4"),sQuery(id+"F0.wireOp",EDGE,"E7.2.5"),sQuery(id+"F0.wireOp",EDGE,"E7.3.0"),sQuery(id+"F0.wireOp",EDGE,"E7.3.1"),sQuery(id+"F0.wireOp",EDGE,"E7.3.2"),sQuery(id+"F0.wireOp",EDGE,"E7.3.3"),sQuery(id+"F0.wireOp",EDGE,"E7.3.4"),sQuery(id+"F0.wireOp",EDGE,"E7.3.5"),sQuery(id+"F0.wireOp",EDGE,"E7.4.0"),sQuery(id+"F0.wireOp",EDGE,"E7.4.1"),sQuery(id+"F0.wireOp",EDGE,"E7.4.2"),sQuery(id+"F0.wireOp",EDGE,"E7.4.3"),sQuery(id+"F0.wireOp",EDGE,"E7.4.4"),sQuery(id+"F0.wireOp",EDGE,"E7.4.5"),sQuery(id+"F0.wireOp",EDGE,"E7.5.0"),sQuery(id+"F0.wireOp",EDGE,"E7.5.1"),sQuery(id+"F0.wireOp",EDGE,"E7.5.2"),sQuery(id+"F0.wireOp",EDGE,"E7.5.3"),sQuery(id+"F0.wireOp",EDGE,"E7.5.4"),sQuery(id+"F0.wireOp",EDGE,"E7.5.5"),sQuery(id+"F0.wireOp",EDGE,"E7.6.0"),sQuery(id+"F0.wireOp",EDGE,"E7.6.1"),sQuery(id+"F0.wireOp",EDGE,"E7.6.2"),sQuery(id+"F0.wireOp",EDGE,"E7.6.3"),sQuery(id+"F0.wireOp",EDGE,"E7.6.4"),sQuery(id+"F0.wireOp",EDGE,"E7.6.5"),sQuery(id+"F0.wireOp",EDGE,"E7.7.0"),sQuery(id+"F0.wireOp",EDGE,"E7.7.1"),sQuery(id+"F0.wireOp",EDGE,"E7.7.2"),sQuery(id+"F0.wireOp",EDGE,"E7.7.3"),sQuery(id+"F0.wireOp",EDGE,"E7.7.4"),sQuery(id+"F0.wireOp",EDGE,"E7.7.5"),subQ0,sQuery(id+"F0.wireOp",EDGE,"E7.8.1"),sQuery(id+"F0.wireOp",EDGE,"E7.8.2"),sQuery(id+"F0.wireOp",EDGE,"E7.8.3"),sQuery(id+"F0.wireOp",EDGE,"E7.8.4"),sQuery(id+"F0.wireOp",EDGE,"E7.8.5"),sQuery(id+"F0.wireOp",EDGE,"E7.9.0"),sQuery(id+"F0.wireOp",EDGE,"E7.9.1"),sQuery(id+"F0.wireOp",EDGE,"E7.9.2"),sQuery(id+"F0.wireOp",EDGE,"E7.9.3"),sQuery(id+"F0.wireOp",EDGE,"E7.9.4"),sQuery(id+"F0.wireOp",EDGE,"E7.9.5"),sQuery(id+"F0.wireOp",EDGE,"E7.10.0"),sQuery(id+"F0.wireOp",EDGE,"E7.10.1"),sQuery(id+"F0.wireOp",EDGE,"E7.10.2"),sQuery(id+"F0.wireOp",EDGE,"E7.10.3"),sQuery(id+"F0.wireOp",EDGE,"E7.10.4"),sQuery(id+"F0.wireOp",EDGE,"E7.10.5"),sQuery(id+"F0.wireOp",EDGE,"E7.11.0"),sQuery(id+"F0.wireOp",EDGE,"E7.11.1"),sQuery(id+"F0.wireOp",EDGE,"E7.11.2"),sQuery(id+"F0.wireOp",EDGE,"E7.11.3"),sQuery(id+"F0.wireOp",EDGE,"E7.11.4"),sQuery(id+"F0.wireOp",EDGE,"E7.11.5"),sQuery(id+"F0.wireOp",EDGE,"E7.12.0"),sQuery(id+"F0.wireOp",EDGE,"E7.12.1"),sQuery(id+"F0.wireOp",EDGE,"E7.12.2"),sQuery(id+"F0.wireOp",EDGE,"E7.12.3"),sQuery(id+"F0.wireOp",EDGE,"E7.12.4"),sQuery(id+"F0.wireOp",EDGE,"E7.12.5"),sQuery(id+"F0.wireOp",EDGE,"E7.13.0"),sQuery(id+"F0.wireOp",EDGE,"E7.13.1"),sQuery(id+"F0.wireOp",EDGE,"E7.13.2"),sQuery(id+"F0.wireOp",EDGE,"E7.13.3"),sQuery(id+"F0.wireOp",EDGE,"E7.13.4"),sQuery(id+"F0.wireOp",EDGE,"E7.13.5"),sQuery(id+"F0.wireOp",EDGE,"E7.14.0"),sQuery(id+"F0.wireOp",EDGE,"E7.14.1"),sQuery(id+"F0.wireOp",EDGE,"E7.14.2"),sQuery(id+"F0.wireOp",EDGE,"E7.14.3"),sQuery(id+"F0.wireOp",EDGE,"E7.14.4"),sQuery(id+"F0.wireOp",EDGE,"E7.14.5"),sQuery(id+"F0.wireOp",EDGE,"E7.15.0"),sQuery(id+"F0.wireOp",EDGE,"E7.15.1"),sQuery(id+"F0.wireOp",EDGE,"E7.15.2"),sQuery(id+"F0.wireOp",EDGE,"E7.15.3"),sQuery(id+"F0.wireOp",EDGE,"E7.15.4"),sQuery(id+"F0.wireOp",EDGE,"E7.15.5"),sQuery(id+"F0.wireOp",EDGE,"E7.16.0"),sQuery(id+"F0.wireOp",EDGE,"E7.16.1"),sQuery(id+"F0.wireOp",EDGE,"E7.16.2"),sQuery(id+"F0.wireOp",EDGE,"E7.16.3"),sQuery(id+"F0.wireOp",EDGE,"E7.16.4"),sQuery(id+"F0.wireOp",EDGE,"E7.16.5"),sQuery(id+"F0.wireOp",EDGE,"E7.17.0"),sQuery(id+"F0.wireOp",EDGE,"E7.17.1"),sQuery(id+"F0.wireOp",EDGE,"E7.17.2"),sQuery(id+"F0.wireOp",EDGE,"E7.17.3"),sQuery(id+"F0.wireOp",EDGE,"E7.17.4"),sQuery(id+"F0.wireOp",EDGE,"E7.17.5"),sQuery(id+"F0.wireOp",EDGE,"E7.18.0"),sQuery(id+"F0.wireOp",EDGE,"E7.18.1"),sQuery(id+"F0.wireOp",EDGE,"E7.18.2"),sQuery(id+"F0.wireOp",EDGE,"E7.18.3"),sQuery(id+"F0.wireOp",EDGE,"E7.18.4"),sQuery(id+"F0.wireOp",EDGE,"E7.18.5"),sQuery(id+"F0.wireOp",EDGE,"E7.19.0"),sQuery(id+"F0.wireOp",EDGE,"E7.19.1"),sQuery(id+"F0.wireOp",EDGE,"E7.19.2"),sQuery(id+"F0.wireOp",EDGE,"E7.19.3"),sQuery(id+"F0.wireOp",EDGE,"E7.19.4"),sQuery(id+"F0.wireOp",EDGE,"E7.19.5"),sQuery(id+"F0.wireOp",EDGE,"E7.20.0"),sQuery(id+"F0.wireOp",EDGE,"E7.20.1"),sQuery(id+"F0.wireOp",EDGE,"E7.20.2"),sQuery(id+"F0.wireOp",EDGE,"E7.20.3"),sQuery(id+"F0.wireOp",EDGE,"E7.20.4"),sQuery(id+"F0.wireOp",EDGE,"E7.20.5"),sQuery(id+"F0.wireOp",EDGE,"E7.21.0"),sQuery(id+"F0.wireOp",EDGE,"E7.21.1"),sQuery(id+"F0.wireOp",EDGE,"E7.21.2"),sQuery(id+"F0.wireOp",EDGE,"E7.21.3"),sQuery(id+"F0.wireOp",EDGE,"E7.21.4"),sQuery(id+"F0.wireOp",EDGE,"E7.21.5"),sQuery(id+"F0.wireOp",EDGE,"E7.22.0"),sQuery(id+"F0.wireOp",EDGE,"E7.22.1"),sQuery(id+"F0.wireOp",EDGE,"E7.22.2"),sQuery(id+"F0.wireOp",EDGE,"E7.22.3"),sQuery(id+"F0.wireOp",EDGE,"E7.22.4"),sQuery(id+"F0.wireOp",EDGE,"E7.22.5"),sQuery(id+"F0.wireOp",EDGE,"E7.23.0"),sQuery(id+"F0.wireOp",EDGE,"E7.23.1"),sQuery(id+"F0.wireOp",EDGE,"E7.23.2"),sQuery(id+"F0.wireOp",EDGE,"E7.23.3"),sQuery(id+"F0.wireOp",EDGE,"E7.23.4"),sQuery(id+"F0.wireOp",EDGE,"E7.23.5"),sQuery(id+"F0.wireOp",EDGE,"E7.24.0"),sQuery(id+"F0.wireOp",EDGE,"E7.24.1"),sQuery(id+"F0.wireOp",EDGE,"E7.24.2"),sQuery(id+"F0.wireOp",EDGE,"E7.24.3"),sQuery(id+"F0.wireOp",EDGE,"E7.24.4"),sQuery(id+"F0.wireOp",EDGE,"E7.24.5"),sQuery(id+"F0.wireOp",EDGE,"E7.25.0"),sQuery(id+"F0.wireOp",EDGE,"E7.25.1"),sQuery(id+"F0.wireOp",EDGE,"E7.25.2"),sQuery(id+"F0.wireOp",EDGE,"E7.25.3"),sQuery(id+"F0.wireOp",EDGE,"E7.25.4"),sQuery(id+"F0.wireOp",EDGE,"E7.25.5"),sQuery(id+"F0.wireOp",EDGE,"E7.26.0"),sQuery(id+"F0.wireOp",EDGE,"E7.26.1"),sQuery(id+"F0.wireOp",EDGE,"E7.26.2"),sQuery(id+"F0.wireOp",EDGE,"E7.26.3"),sQuery(id+"F0.wireOp",EDGE,"E7.26.4"),sQuery(id+"F0.wireOp",EDGE,"E7.26.5"),sQuery(id+"F0.wireOp",EDGE,"E7.27.0"),sQuery(id+"F0.wireOp",EDGE,"E7.27.1"),sQuery(id+"F0.wireOp",EDGE,"E7.27.2"),sQuery(id+"F0.wireOp",EDGE,"E7.27.3"),sQuery(id+"F0.wireOp",EDGE,"E7.27.4"),sQuery(id+"F0.wireOp",EDGE,"E7.27.5"),sQuery(id+"F0.wireOp",EDGE,"E7.28.0"),sQuery(id+"F0.wireOp",EDGE,"E7.28.1"),sQuery(id+"F0.wireOp",EDGE,"E7.28.2"),sQuery(id+"F0.wireOp",EDGE,"E7.28.3"),sQuery(id+"F0.wireOp",EDGE,"E7.28.4"),sQuery(id+"F0.wireOp",EDGE,"E7.28.5"),sQuery(id+"F0.wireOp",EDGE,"E7.29.0"),sQuery(id+"F0.wireOp",EDGE,"E7.29.1"),sQuery(id+"F0.wireOp",EDGE,"E7.29.2"),sQuery(id+"F0.wireOp",EDGE,"E7.29.3"),sQuery(id+"F0.wireOp",EDGE,"E7.29.4"),sQuery(id+"F0.wireOp",EDGE,"E7.29.5"),sQuery(id+"F0.wireOp",EDGE,"E7.30.0"),sQuery(id+"F0.wireOp",EDGE,"E7.30.1"),sQuery(id+"F0.wireOp",EDGE,"E7.30.2"),sQuery(id+"F0.wireOp",EDGE,"E7.30.3"),sQuery(id+"F0.wireOp",EDGE,"E7.30.4"),sQuery(id+"F0.wireOp",EDGE,"E7.30.5"),sQuery(id+"F0.wireOp",EDGE,"E7.31.0"),sQuery(id+"F0.wireOp",EDGE,"E7.31.1"),sQuery(id+"F0.wireOp",EDGE,"E7.31.2"),sQuery(id+"F0.wireOp",EDGE,"E7.31.3"),sQuery(id+"F0.wireOp",EDGE,"E7.31.4"),sQuery(id+"F0.wireOp",EDGE,"E7.31.5"),sQuery(id+"F0.wireOp",EDGE,"E7.32.0"),sQuery(id+"F0.wireOp",EDGE,"E7.32.1"),sQuery(id+"F0.wireOp",EDGE,"E7.32.2"),sQuery(id+"F0.wireOp",EDGE,"E7.32.3"),sQuery(id+"F0.wireOp",EDGE,"E7.32.4"),sQuery(id+"F0.wireOp",EDGE,"E7.32.5"),sQuery(id+"F0.wireOp",EDGE,"E7.33.0"),sQuery(id+"F0.wireOp",EDGE,"E7.33.1"),sQuery(id+"F0.wireOp",EDGE,"E7.33.2"),sQuery(id+"F0.wireOp",EDGE,"E7.33.3"),sQuery(id+"F0.wireOp",EDGE,"E7.33.4"),sQuery(id+"F0.wireOp",EDGE,"E7.33.5"),sQuery(id+"F0.wireOp",EDGE,"E7.34.0"),sQuery(id+"F0.wireOp",EDGE,"E7.34.1"),sQuery(id+"F0.wireOp",EDGE,"E7.34.2"),sQuery(id+"F0.wireOp",EDGE,"E7.34.3"),sQuery(id+"F0.wireOp",EDGE,"E7.34.4"),sQuery(id+"F0.wireOp",EDGE,"E7.34.5"),sQuery(id+"F0.wireOp",EDGE,"E7.35.0"),sQuery(id+"F0.wireOp",EDGE,"E7.35.1"),sQuery(id+"F0.wireOp",EDGE,"E7.35.2"),sQuery(id+"F0.wireOp",EDGE,"E7.35.3"),sQuery(id+"F0.wireOp",EDGE,"E7.35.4"),sQuery(id+"F0.wireOp",EDGE,"E7.35.5"),sQuery(id+"F0.wireOp",EDGE,"E7.36.0"),sQuery(id+"F0.wireOp",EDGE,"E7.36.1"),sQuery(id+"F0.wireOp",EDGE,"E7.36.2"),sQuery(id+"F0.wireOp",EDGE,"E7.36.3"),sQuery(id+"F0.wireOp",EDGE,"E7.36.4"),sQuery(id+"F0.wireOp",EDGE,"E7.36.5"),sQuery(id+"F0.wireOp",EDGE,"E7.37.0"),sQuery(id+"F0.wireOp",EDGE,"E7.37.1"),sQuery(id+"F0.wireOp",EDGE,"E7.37.2"),sQuery(id+"F0.wireOp",EDGE,"E7.37.3"),sQuery(id+"F0.wireOp",EDGE,"E7.37.4"),sQuery(id+"F0.wireOp",EDGE,"E7.37.5"),sQuery(id+"F0.wireOp",EDGE,"E7.38.0"),sQuery(id+"F0.wireOp",EDGE,"E7.38.1"),sQuery(id+"F0.wireOp",EDGE,"E7.38.2"),sQuery(id+"F0.wireOp",EDGE,"E7.38.3"),sQuery(id+"F0.wireOp",EDGE,"E7.38.4"),sQuery(id+"F0.wireOp",EDGE,"E7.38.5"),sQuery(id+"F0.wireOp",EDGE,"E7.39.0"),sQuery(id+"F0.wireOp",EDGE,"E7.39.1"),sQuery(id+"F0.wireOp",EDGE,"E7.39.2"),sQuery(id+"F0.wireOp",EDGE,"E7.39.3"),sQuery(id+"F0.wireOp",EDGE,"E7.39.4"),sQuery(id+"F0.wireOp",EDGE,"E7.39.5"),sQuery(id+"F0.wireOp",EDGE,"E7.40.0"),sQuery(id+"F0.wireOp",EDGE,"E7.40.1"),sQuery(id+"F0.wireOp",EDGE,"E7.40.2"),sQuery(id+"F0.wireOp",EDGE,"E7.40.3"),sQuery(id+"F0.wireOp",EDGE,"E7.40.4"),sQuery(id+"F0.wireOp",EDGE,"E7.40.5"),sQuery(id+"F0.wireOp",EDGE,"E7.41.0"),sQuery(id+"F0.wireOp",EDGE,"E7.41.1"),sQuery(id+"F0.wireOp",EDGE,"E7.41.2"),sQuery(id+"F0.wireOp",EDGE,"E7.41.3"),sQuery(id+"F0.wireOp",EDGE,"E7.41.4"),sQuery(id+"F0.wireOp",EDGE,"E7.41.5"),sQuery(id+"F0.wireOp",EDGE,"E7.42.0"),sQuery(id+"F0.wireOp",EDGE,"E7.42.1"),sQuery(id+"F0.wireOp",EDGE,"E7.42.2"),sQuery(id+"F0.wireOp",EDGE,"E7.42.3"),sQuery(id+"F0.wireOp",EDGE,"E7.42.4"),sQuery(id+"F0.wireOp",EDGE,"E7.42.5"),sQuery(id+"F0.wireOp",EDGE,"E7.43.0"),sQuery(id+"F0.wireOp",EDGE,"E7.43.1"),sQuery(id+"F0.wireOp",EDGE,"E7.43.2"),sQuery(id+"F0.wireOp",EDGE,"E7.43.3"),sQuery(id+"F0.wireOp",EDGE,"E7.43.4"),sQuery(id+"F0.wireOp",EDGE,"E7.43.5")])],"isStart":true})]});}
            var Q26;
            {var subQ0=sQuery(id+"F0.wireOp",EDGE,"E7.10.0");Q26=makeQuery(id+"F2.opChamfer","BLEND_EDGE",EDGE,{"blendedFrom":[makeQuery(id+"F1.opExtrude","CAP_EDGE",EDGE,{"disambiguationData":[OSD([subQ0])],"isStart":true}),makeQuery(id+"F1.opExtrude","CAP_FACE",FACE,{"disambiguationData":[OSD([sQuery(id+"F0.wireOp",EDGE,"E1"),sQuery(id+"F0.wireOp",EDGE,"E2"),sQuery(id+"F0.wireOp",EDGE,"E3"),sQuery(id+"F0.wireOp",EDGE,"E4"),sQuery(id+"F0.wireOp",EDGE,"E5"),sQuery(id+"F0.wireOp",EDGE,"E6"),sQuery(id+"F0.wireOp",EDGE,"E7.1.0"),sQuery(id+"F0.wireOp",EDGE,"E7.1.1"),sQuery(id+"F0.wireOp",EDGE,"E7.1.2"),sQuery(id+"F0.wireOp",EDGE,"E7.1.3"),sQuery(id+"F0.wireOp",EDGE,"E7.1.4"),sQuery(id+"F0.wireOp",EDGE,"E7.1.5"),sQuery(id+"F0.wireOp",EDGE,"E7.2.0"),sQuery(id+"F0.wireOp",EDGE,"E7.2.1"),sQuery(id+"F0.wireOp",EDGE,"E7.2.2"),sQuery(id+"F0.wireOp",EDGE,"E7.2.3"),sQuery(id+"F0.wireOp",EDGE,"E7.2.4"),sQuery(id+"F0.wireOp",EDGE,"E7.2.5"),sQuery(id+"F0.wireOp",EDGE,"E7.3.0"),sQuery(id+"F0.wireOp",EDGE,"E7.3.1"),sQuery(id+"F0.wireOp",EDGE,"E7.3.2"),sQuery(id+"F0.wireOp",EDGE,"E7.3.3"),sQuery(id+"F0.wireOp",EDGE,"E7.3.4"),sQuery(id+"F0.wireOp",EDGE,"E7.3.5"),sQuery(id+"F0.wireOp",EDGE,"E7.4.0"),sQuery(id+"F0.wireOp",EDGE,"E7.4.1"),sQuery(id+"F0.wireOp",EDGE,"E7.4.2"),sQuery(id+"F0.wireOp",EDGE,"E7.4.3"),sQuery(id+"F0.wireOp",EDGE,"E7.4.4"),sQuery(id+"F0.wireOp",EDGE,"E7.4.5"),sQuery(id+"F0.wireOp",EDGE,"E7.5.0"),sQuery(id+"F0.wireOp",EDGE,"E7.5.1"),sQuery(id+"F0.wireOp",EDGE,"E7.5.2"),sQuery(id+"F0.wireOp",EDGE,"E7.5.3"),sQuery(id+"F0.wireOp",EDGE,"E7.5.4"),sQuery(id+"F0.wireOp",EDGE,"E7.5.5"),sQuery(id+"F0.wireOp",EDGE,"E7.6.0"),sQuery(id+"F0.wireOp",EDGE,"E7.6.1"),sQuery(id+"F0.wireOp",EDGE,"E7.6.2"),sQuery(id+"F0.wireOp",EDGE,"E7.6.3"),sQuery(id+"F0.wireOp",EDGE,"E7.6.4"),sQuery(id+"F0.wireOp",EDGE,"E7.6.5"),sQuery(id+"F0.wireOp",EDGE,"E7.7.0"),sQuery(id+"F0.wireOp",EDGE,"E7.7.1"),sQuery(id+"F0.wireOp",EDGE,"E7.7.2"),sQuery(id+"F0.wireOp",EDGE,"E7.7.3"),sQuery(id+"F0.wireOp",EDGE,"E7.7.4"),sQuery(id+"F0.wireOp",EDGE,"E7.7.5"),sQuery(id+"F0.wireOp",EDGE,"E7.8.0"),sQuery(id+"F0.wireOp",EDGE,"E7.8.1"),sQuery(id+"F0.wireOp",EDGE,"E7.8.2"),sQuery(id+"F0.wireOp",EDGE,"E7.8.3"),sQuery(id+"F0.wireOp",EDGE,"E7.8.4"),sQuery(id+"F0.wireOp",EDGE,"E7.8.5"),sQuery(id+"F0.wireOp",EDGE,"E7.9.0"),sQuery(id+"F0.wireOp",EDGE,"E7.9.1"),sQuery(id+"F0.wireOp",EDGE,"E7.9.2"),sQuery(id+"F0.wireOp",EDGE,"E7.9.3"),sQuery(id+"F0.wireOp",EDGE,"E7.9.4"),sQuery(id+"F0.wireOp",EDGE,"E7.9.5"),subQ0,sQuery(id+"F0.wireOp",EDGE,"E7.10.1"),sQuery(id+"F0.wireOp",EDGE,"E7.10.2"),sQuery(id+"F0.wireOp",EDGE,"E7.10.3"),sQuery(id+"F0.wireOp",EDGE,"E7.10.4"),sQuery(id+"F0.wireOp",EDGE,"E7.10.5"),sQuery(id+"F0.wireOp",EDGE,"E7.11.0"),sQuery(id+"F0.wireOp",EDGE,"E7.11.1"),sQuery(id+"F0.wireOp",EDGE,"E7.11.2"),sQuery(id+"F0.wireOp",EDGE,"E7.11.3"),sQuery(id+"F0.wireOp",EDGE,"E7.11.4"),sQuery(id+"F0.wireOp",EDGE,"E7.11.5"),sQuery(id+"F0.wireOp",EDGE,"E7.12.0"),sQuery(id+"F0.wireOp",EDGE,"E7.12.1"),sQuery(id+"F0.wireOp",EDGE,"E7.12.2"),sQuery(id+"F0.wireOp",EDGE,"E7.12.3"),sQuery(id+"F0.wireOp",EDGE,"E7.12.4"),sQuery(id+"F0.wireOp",EDGE,"E7.12.5"),sQuery(id+"F0.wireOp",EDGE,"E7.13.0"),sQuery(id+"F0.wireOp",EDGE,"E7.13.1"),sQuery(id+"F0.wireOp",EDGE,"E7.13.2"),sQuery(id+"F0.wireOp",EDGE,"E7.13.3"),sQuery(id+"F0.wireOp",EDGE,"E7.13.4"),sQuery(id+"F0.wireOp",EDGE,"E7.13.5"),sQuery(id+"F0.wireOp",EDGE,"E7.14.0"),sQuery(id+"F0.wireOp",EDGE,"E7.14.1"),sQuery(id+"F0.wireOp",EDGE,"E7.14.2"),sQuery(id+"F0.wireOp",EDGE,"E7.14.3"),sQuery(id+"F0.wireOp",EDGE,"E7.14.4"),sQuery(id+"F0.wireOp",EDGE,"E7.14.5"),sQuery(id+"F0.wireOp",EDGE,"E7.15.0"),sQuery(id+"F0.wireOp",EDGE,"E7.15.1"),sQuery(id+"F0.wireOp",EDGE,"E7.15.2"),sQuery(id+"F0.wireOp",EDGE,"E7.15.3"),sQuery(id+"F0.wireOp",EDGE,"E7.15.4"),sQuery(id+"F0.wireOp",EDGE,"E7.15.5"),sQuery(id+"F0.wireOp",EDGE,"E7.16.0"),sQuery(id+"F0.wireOp",EDGE,"E7.16.1"),sQuery(id+"F0.wireOp",EDGE,"E7.16.2"),sQuery(id+"F0.wireOp",EDGE,"E7.16.3"),sQuery(id+"F0.wireOp",EDGE,"E7.16.4"),sQuery(id+"F0.wireOp",EDGE,"E7.16.5"),sQuery(id+"F0.wireOp",EDGE,"E7.17.0"),sQuery(id+"F0.wireOp",EDGE,"E7.17.1"),sQuery(id+"F0.wireOp",EDGE,"E7.17.2"),sQuery(id+"F0.wireOp",EDGE,"E7.17.3"),sQuery(id+"F0.wireOp",EDGE,"E7.17.4"),sQuery(id+"F0.wireOp",EDGE,"E7.17.5"),sQuery(id+"F0.wireOp",EDGE,"E7.18.0"),sQuery(id+"F0.wireOp",EDGE,"E7.18.1"),sQuery(id+"F0.wireOp",EDGE,"E7.18.2"),sQuery(id+"F0.wireOp",EDGE,"E7.18.3"),sQuery(id+"F0.wireOp",EDGE,"E7.18.4"),sQuery(id+"F0.wireOp",EDGE,"E7.18.5"),sQuery(id+"F0.wireOp",EDGE,"E7.19.0"),sQuery(id+"F0.wireOp",EDGE,"E7.19.1"),sQuery(id+"F0.wireOp",EDGE,"E7.19.2"),sQuery(id+"F0.wireOp",EDGE,"E7.19.3"),sQuery(id+"F0.wireOp",EDGE,"E7.19.4"),sQuery(id+"F0.wireOp",EDGE,"E7.19.5"),sQuery(id+"F0.wireOp",EDGE,"E7.20.0"),sQuery(id+"F0.wireOp",EDGE,"E7.20.1"),sQuery(id+"F0.wireOp",EDGE,"E7.20.2"),sQuery(id+"F0.wireOp",EDGE,"E7.20.3"),sQuery(id+"F0.wireOp",EDGE,"E7.20.4"),sQuery(id+"F0.wireOp",EDGE,"E7.20.5"),sQuery(id+"F0.wireOp",EDGE,"E7.21.0"),sQuery(id+"F0.wireOp",EDGE,"E7.21.1"),sQuery(id+"F0.wireOp",EDGE,"E7.21.2"),sQuery(id+"F0.wireOp",EDGE,"E7.21.3"),sQuery(id+"F0.wireOp",EDGE,"E7.21.4"),sQuery(id+"F0.wireOp",EDGE,"E7.21.5"),sQuery(id+"F0.wireOp",EDGE,"E7.22.0"),sQuery(id+"F0.wireOp",EDGE,"E7.22.1"),sQuery(id+"F0.wireOp",EDGE,"E7.22.2"),sQuery(id+"F0.wireOp",EDGE,"E7.22.3"),sQuery(id+"F0.wireOp",EDGE,"E7.22.4"),sQuery(id+"F0.wireOp",EDGE,"E7.22.5"),sQuery(id+"F0.wireOp",EDGE,"E7.23.0"),sQuery(id+"F0.wireOp",EDGE,"E7.23.1"),sQuery(id+"F0.wireOp",EDGE,"E7.23.2"),sQuery(id+"F0.wireOp",EDGE,"E7.23.3"),sQuery(id+"F0.wireOp",EDGE,"E7.23.4"),sQuery(id+"F0.wireOp",EDGE,"E7.23.5"),sQuery(id+"F0.wireOp",EDGE,"E7.24.0"),sQuery(id+"F0.wireOp",EDGE,"E7.24.1"),sQuery(id+"F0.wireOp",EDGE,"E7.24.2"),sQuery(id+"F0.wireOp",EDGE,"E7.24.3"),sQuery(id+"F0.wireOp",EDGE,"E7.24.4"),sQuery(id+"F0.wireOp",EDGE,"E7.24.5"),sQuery(id+"F0.wireOp",EDGE,"E7.25.0"),sQuery(id+"F0.wireOp",EDGE,"E7.25.1"),sQuery(id+"F0.wireOp",EDGE,"E7.25.2"),sQuery(id+"F0.wireOp",EDGE,"E7.25.3"),sQuery(id+"F0.wireOp",EDGE,"E7.25.4"),sQuery(id+"F0.wireOp",EDGE,"E7.25.5"),sQuery(id+"F0.wireOp",EDGE,"E7.26.0"),sQuery(id+"F0.wireOp",EDGE,"E7.26.1"),sQuery(id+"F0.wireOp",EDGE,"E7.26.2"),sQuery(id+"F0.wireOp",EDGE,"E7.26.3"),sQuery(id+"F0.wireOp",EDGE,"E7.26.4"),sQuery(id+"F0.wireOp",EDGE,"E7.26.5"),sQuery(id+"F0.wireOp",EDGE,"E7.27.0"),sQuery(id+"F0.wireOp",EDGE,"E7.27.1"),sQuery(id+"F0.wireOp",EDGE,"E7.27.2"),sQuery(id+"F0.wireOp",EDGE,"E7.27.3"),sQuery(id+"F0.wireOp",EDGE,"E7.27.4"),sQuery(id+"F0.wireOp",EDGE,"E7.27.5"),sQuery(id+"F0.wireOp",EDGE,"E7.28.0"),sQuery(id+"F0.wireOp",EDGE,"E7.28.1"),sQuery(id+"F0.wireOp",EDGE,"E7.28.2"),sQuery(id+"F0.wireOp",EDGE,"E7.28.3"),sQuery(id+"F0.wireOp",EDGE,"E7.28.4"),sQuery(id+"F0.wireOp",EDGE,"E7.28.5"),sQuery(id+"F0.wireOp",EDGE,"E7.29.0"),sQuery(id+"F0.wireOp",EDGE,"E7.29.1"),sQuery(id+"F0.wireOp",EDGE,"E7.29.2"),sQuery(id+"F0.wireOp",EDGE,"E7.29.3"),sQuery(id+"F0.wireOp",EDGE,"E7.29.4"),sQuery(id+"F0.wireOp",EDGE,"E7.29.5"),sQuery(id+"F0.wireOp",EDGE,"E7.30.0"),sQuery(id+"F0.wireOp",EDGE,"E7.30.1"),sQuery(id+"F0.wireOp",EDGE,"E7.30.2"),sQuery(id+"F0.wireOp",EDGE,"E7.30.3"),sQuery(id+"F0.wireOp",EDGE,"E7.30.4"),sQuery(id+"F0.wireOp",EDGE,"E7.30.5"),sQuery(id+"F0.wireOp",EDGE,"E7.31.0"),sQuery(id+"F0.wireOp",EDGE,"E7.31.1"),sQuery(id+"F0.wireOp",EDGE,"E7.31.2"),sQuery(id+"F0.wireOp",EDGE,"E7.31.3"),sQuery(id+"F0.wireOp",EDGE,"E7.31.4"),sQuery(id+"F0.wireOp",EDGE,"E7.31.5"),sQuery(id+"F0.wireOp",EDGE,"E7.32.0"),sQuery(id+"F0.wireOp",EDGE,"E7.32.1"),sQuery(id+"F0.wireOp",EDGE,"E7.32.2"),sQuery(id+"F0.wireOp",EDGE,"E7.32.3"),sQuery(id+"F0.wireOp",EDGE,"E7.32.4"),sQuery(id+"F0.wireOp",EDGE,"E7.32.5"),sQuery(id+"F0.wireOp",EDGE,"E7.33.0"),sQuery(id+"F0.wireOp",EDGE,"E7.33.1"),sQuery(id+"F0.wireOp",EDGE,"E7.33.2"),sQuery(id+"F0.wireOp",EDGE,"E7.33.3"),sQuery(id+"F0.wireOp",EDGE,"E7.33.4"),sQuery(id+"F0.wireOp",EDGE,"E7.33.5"),sQuery(id+"F0.wireOp",EDGE,"E7.34.0"),sQuery(id+"F0.wireOp",EDGE,"E7.34.1"),sQuery(id+"F0.wireOp",EDGE,"E7.34.2"),sQuery(id+"F0.wireOp",EDGE,"E7.34.3"),sQuery(id+"F0.wireOp",EDGE,"E7.34.4"),sQuery(id+"F0.wireOp",EDGE,"E7.34.5"),sQuery(id+"F0.wireOp",EDGE,"E7.35.0"),sQuery(id+"F0.wireOp",EDGE,"E7.35.1"),sQuery(id+"F0.wireOp",EDGE,"E7.35.2"),sQuery(id+"F0.wireOp",EDGE,"E7.35.3"),sQuery(id+"F0.wireOp",EDGE,"E7.35.4"),sQuery(id+"F0.wireOp",EDGE,"E7.35.5"),sQuery(id+"F0.wireOp",EDGE,"E7.36.0"),sQuery(id+"F0.wireOp",EDGE,"E7.36.1"),sQuery(id+"F0.wireOp",EDGE,"E7.36.2"),sQuery(id+"F0.wireOp",EDGE,"E7.36.3"),sQuery(id+"F0.wireOp",EDGE,"E7.36.4"),sQuery(id+"F0.wireOp",EDGE,"E7.36.5"),sQuery(id+"F0.wireOp",EDGE,"E7.37.0"),sQuery(id+"F0.wireOp",EDGE,"E7.37.1"),sQuery(id+"F0.wireOp",EDGE,"E7.37.2"),sQuery(id+"F0.wireOp",EDGE,"E7.37.3"),sQuery(id+"F0.wireOp",EDGE,"E7.37.4"),sQuery(id+"F0.wireOp",EDGE,"E7.37.5"),sQuery(id+"F0.wireOp",EDGE,"E7.38.0"),sQuery(id+"F0.wireOp",EDGE,"E7.38.1"),sQuery(id+"F0.wireOp",EDGE,"E7.38.2"),sQuery(id+"F0.wireOp",EDGE,"E7.38.3"),sQuery(id+"F0.wireOp",EDGE,"E7.38.4"),sQuery(id+"F0.wireOp",EDGE,"E7.38.5"),sQuery(id+"F0.wireOp",EDGE,"E7.39.0"),sQuery(id+"F0.wireOp",EDGE,"E7.39.1"),sQuery(id+"F0.wireOp",EDGE,"E7.39.2"),sQuery(id+"F0.wireOp",EDGE,"E7.39.3"),sQuery(id+"F0.wireOp",EDGE,"E7.39.4"),sQuery(id+"F0.wireOp",EDGE,"E7.39.5"),sQuery(id+"F0.wireOp",EDGE,"E7.40.0"),sQuery(id+"F0.wireOp",EDGE,"E7.40.1"),sQuery(id+"F0.wireOp",EDGE,"E7.40.2"),sQuery(id+"F0.wireOp",EDGE,"E7.40.3"),sQuery(id+"F0.wireOp",EDGE,"E7.40.4"),sQuery(id+"F0.wireOp",EDGE,"E7.40.5"),sQuery(id+"F0.wireOp",EDGE,"E7.41.0"),sQuery(id+"F0.wireOp",EDGE,"E7.41.1"),sQuery(id+"F0.wireOp",EDGE,"E7.41.2"),sQuery(id+"F0.wireOp",EDGE,"E7.41.3"),sQuery(id+"F0.wireOp",EDGE,"E7.41.4"),sQuery(id+"F0.wireOp",EDGE,"E7.41.5"),sQuery(id+"F0.wireOp",EDGE,"E7.42.0"),sQuery(id+"F0.wireOp",EDGE,"E7.42.1"),sQuery(id+"F0.wireOp",EDGE,"E7.42.2"),sQuery(id+"F0.wireOp",EDGE,"E7.42.3"),sQuery(id+"F0.wireOp",EDGE,"E7.42.4"),sQuery(id+"F0.wireOp",EDGE,"E7.42.5"),sQuery(id+"F0.wireOp",EDGE,"E7.43.0"),sQuery(id+"F0.wireOp",EDGE,"E7.43.1"),sQuery(id+"F0.wireOp",EDGE,"E7.43.2"),sQuery(id+"F0.wireOp",EDGE,"E7.43.3"),sQuery(id+"F0.wireOp",EDGE,"E7.43.4"),sQuery(id+"F0.wireOp",EDGE,"E7.43.5")])],"isStart":true})],"blendedInto":[makeQuery(id+"F1.opExtrude","CAP_FACE",FACE,{"disambiguationData":[OSD([sQuery(id+"F0.wireOp",EDGE,"E1"),sQuery(id+"F0.wireOp",EDGE,"E2"),sQuery(id+"F0.wireOp",EDGE,"E3"),sQuery(id+"F0.wireOp",EDGE,"E4"),sQuery(id+"F0.wireOp",EDGE,"E5"),sQuery(id+"F0.wireOp",EDGE,"E6"),sQuery(id+"F0.wireOp",EDGE,"E7.1.0"),sQuery(id+"F0.wireOp",EDGE,"E7.1.1"),sQuery(id+"F0.wireOp",EDGE,"E7.1.2"),sQuery(id+"F0.wireOp",EDGE,"E7.1.3"),sQuery(id+"F0.wireOp",EDGE,"E7.1.4"),sQuery(id+"F0.wireOp",EDGE,"E7.1.5"),sQuery(id+"F0.wireOp",EDGE,"E7.2.0"),sQuery(id+"F0.wireOp",EDGE,"E7.2.1"),sQuery(id+"F0.wireOp",EDGE,"E7.2.2"),sQuery(id+"F0.wireOp",EDGE,"E7.2.3"),sQuery(id+"F0.wireOp",EDGE,"E7.2.4"),sQuery(id+"F0.wireOp",EDGE,"E7.2.5"),sQuery(id+"F0.wireOp",EDGE,"E7.3.0"),sQuery(id+"F0.wireOp",EDGE,"E7.3.1"),sQuery(id+"F0.wireOp",EDGE,"E7.3.2"),sQuery(id+"F0.wireOp",EDGE,"E7.3.3"),sQuery(id+"F0.wireOp",EDGE,"E7.3.4"),sQuery(id+"F0.wireOp",EDGE,"E7.3.5"),sQuery(id+"F0.wireOp",EDGE,"E7.4.0"),sQuery(id+"F0.wireOp",EDGE,"E7.4.1"),sQuery(id+"F0.wireOp",EDGE,"E7.4.2"),sQuery(id+"F0.wireOp",EDGE,"E7.4.3"),sQuery(id+"F0.wireOp",EDGE,"E7.4.4"),sQuery(id+"F0.wireOp",EDGE,"E7.4.5"),sQuery(id+"F0.wireOp",EDGE,"E7.5.0"),sQuery(id+"F0.wireOp",EDGE,"E7.5.1"),sQuery(id+"F0.wireOp",EDGE,"E7.5.2"),sQuery(id+"F0.wireOp",EDGE,"E7.5.3"),sQuery(id+"F0.wireOp",EDGE,"E7.5.4"),sQuery(id+"F0.wireOp",EDGE,"E7.5.5"),sQuery(id+"F0.wireOp",EDGE,"E7.6.0"),sQuery(id+"F0.wireOp",EDGE,"E7.6.1"),sQuery(id+"F0.wireOp",EDGE,"E7.6.2"),sQuery(id+"F0.wireOp",EDGE,"E7.6.3"),sQuery(id+"F0.wireOp",EDGE,"E7.6.4"),sQuery(id+"F0.wireOp",EDGE,"E7.6.5"),sQuery(id+"F0.wireOp",EDGE,"E7.7.0"),sQuery(id+"F0.wireOp",EDGE,"E7.7.1"),sQuery(id+"F0.wireOp",EDGE,"E7.7.2"),sQuery(id+"F0.wireOp",EDGE,"E7.7.3"),sQuery(id+"F0.wireOp",EDGE,"E7.7.4"),sQuery(id+"F0.wireOp",EDGE,"E7.7.5"),sQuery(id+"F0.wireOp",EDGE,"E7.8.0"),sQuery(id+"F0.wireOp",EDGE,"E7.8.1"),sQuery(id+"F0.wireOp",EDGE,"E7.8.2"),sQuery(id+"F0.wireOp",EDGE,"E7.8.3"),sQuery(id+"F0.wireOp",EDGE,"E7.8.4"),sQuery(id+"F0.wireOp",EDGE,"E7.8.5"),sQuery(id+"F0.wireOp",EDGE,"E7.9.0"),sQuery(id+"F0.wireOp",EDGE,"E7.9.1"),sQuery(id+"F0.wireOp",EDGE,"E7.9.2"),sQuery(id+"F0.wireOp",EDGE,"E7.9.3"),sQuery(id+"F0.wireOp",EDGE,"E7.9.4"),sQuery(id+"F0.wireOp",EDGE,"E7.9.5"),subQ0,sQuery(id+"F0.wireOp",EDGE,"E7.10.1"),sQuery(id+"F0.wireOp",EDGE,"E7.10.2"),sQuery(id+"F0.wireOp",EDGE,"E7.10.3"),sQuery(id+"F0.wireOp",EDGE,"E7.10.4"),sQuery(id+"F0.wireOp",EDGE,"E7.10.5"),sQuery(id+"F0.wireOp",EDGE,"E7.11.0"),sQuery(id+"F0.wireOp",EDGE,"E7.11.1"),sQuery(id+"F0.wireOp",EDGE,"E7.11.2"),sQuery(id+"F0.wireOp",EDGE,"E7.11.3"),sQuery(id+"F0.wireOp",EDGE,"E7.11.4"),sQuery(id+"F0.wireOp",EDGE,"E7.11.5"),sQuery(id+"F0.wireOp",EDGE,"E7.12.0"),sQuery(id+"F0.wireOp",EDGE,"E7.12.1"),sQuery(id+"F0.wireOp",EDGE,"E7.12.2"),sQuery(id+"F0.wireOp",EDGE,"E7.12.3"),sQuery(id+"F0.wireOp",EDGE,"E7.12.4"),sQuery(id+"F0.wireOp",EDGE,"E7.12.5"),sQuery(id+"F0.wireOp",EDGE,"E7.13.0"),sQuery(id+"F0.wireOp",EDGE,"E7.13.1"),sQuery(id+"F0.wireOp",EDGE,"E7.13.2"),sQuery(id+"F0.wireOp",EDGE,"E7.13.3"),sQuery(id+"F0.wireOp",EDGE,"E7.13.4"),sQuery(id+"F0.wireOp",EDGE,"E7.13.5"),sQuery(id+"F0.wireOp",EDGE,"E7.14.0"),sQuery(id+"F0.wireOp",EDGE,"E7.14.1"),sQuery(id+"F0.wireOp",EDGE,"E7.14.2"),sQuery(id+"F0.wireOp",EDGE,"E7.14.3"),sQuery(id+"F0.wireOp",EDGE,"E7.14.4"),sQuery(id+"F0.wireOp",EDGE,"E7.14.5"),sQuery(id+"F0.wireOp",EDGE,"E7.15.0"),sQuery(id+"F0.wireOp",EDGE,"E7.15.1"),sQuery(id+"F0.wireOp",EDGE,"E7.15.2"),sQuery(id+"F0.wireOp",EDGE,"E7.15.3"),sQuery(id+"F0.wireOp",EDGE,"E7.15.4"),sQuery(id+"F0.wireOp",EDGE,"E7.15.5"),sQuery(id+"F0.wireOp",EDGE,"E7.16.0"),sQuery(id+"F0.wireOp",EDGE,"E7.16.1"),sQuery(id+"F0.wireOp",EDGE,"E7.16.2"),sQuery(id+"F0.wireOp",EDGE,"E7.16.3"),sQuery(id+"F0.wireOp",EDGE,"E7.16.4"),sQuery(id+"F0.wireOp",EDGE,"E7.16.5"),sQuery(id+"F0.wireOp",EDGE,"E7.17.0"),sQuery(id+"F0.wireOp",EDGE,"E7.17.1"),sQuery(id+"F0.wireOp",EDGE,"E7.17.2"),sQuery(id+"F0.wireOp",EDGE,"E7.17.3"),sQuery(id+"F0.wireOp",EDGE,"E7.17.4"),sQuery(id+"F0.wireOp",EDGE,"E7.17.5"),sQuery(id+"F0.wireOp",EDGE,"E7.18.0"),sQuery(id+"F0.wireOp",EDGE,"E7.18.1"),sQuery(id+"F0.wireOp",EDGE,"E7.18.2"),sQuery(id+"F0.wireOp",EDGE,"E7.18.3"),sQuery(id+"F0.wireOp",EDGE,"E7.18.4"),sQuery(id+"F0.wireOp",EDGE,"E7.18.5"),sQuery(id+"F0.wireOp",EDGE,"E7.19.0"),sQuery(id+"F0.wireOp",EDGE,"E7.19.1"),sQuery(id+"F0.wireOp",EDGE,"E7.19.2"),sQuery(id+"F0.wireOp",EDGE,"E7.19.3"),sQuery(id+"F0.wireOp",EDGE,"E7.19.4"),sQuery(id+"F0.wireOp",EDGE,"E7.19.5"),sQuery(id+"F0.wireOp",EDGE,"E7.20.0"),sQuery(id+"F0.wireOp",EDGE,"E7.20.1"),sQuery(id+"F0.wireOp",EDGE,"E7.20.2"),sQuery(id+"F0.wireOp",EDGE,"E7.20.3"),sQuery(id+"F0.wireOp",EDGE,"E7.20.4"),sQuery(id+"F0.wireOp",EDGE,"E7.20.5"),sQuery(id+"F0.wireOp",EDGE,"E7.21.0"),sQuery(id+"F0.wireOp",EDGE,"E7.21.1"),sQuery(id+"F0.wireOp",EDGE,"E7.21.2"),sQuery(id+"F0.wireOp",EDGE,"E7.21.3"),sQuery(id+"F0.wireOp",EDGE,"E7.21.4"),sQuery(id+"F0.wireOp",EDGE,"E7.21.5"),sQuery(id+"F0.wireOp",EDGE,"E7.22.0"),sQuery(id+"F0.wireOp",EDGE,"E7.22.1"),sQuery(id+"F0.wireOp",EDGE,"E7.22.2"),sQuery(id+"F0.wireOp",EDGE,"E7.22.3"),sQuery(id+"F0.wireOp",EDGE,"E7.22.4"),sQuery(id+"F0.wireOp",EDGE,"E7.22.5"),sQuery(id+"F0.wireOp",EDGE,"E7.23.0"),sQuery(id+"F0.wireOp",EDGE,"E7.23.1"),sQuery(id+"F0.wireOp",EDGE,"E7.23.2"),sQuery(id+"F0.wireOp",EDGE,"E7.23.3"),sQuery(id+"F0.wireOp",EDGE,"E7.23.4"),sQuery(id+"F0.wireOp",EDGE,"E7.23.5"),sQuery(id+"F0.wireOp",EDGE,"E7.24.0"),sQuery(id+"F0.wireOp",EDGE,"E7.24.1"),sQuery(id+"F0.wireOp",EDGE,"E7.24.2"),sQuery(id+"F0.wireOp",EDGE,"E7.24.3"),sQuery(id+"F0.wireOp",EDGE,"E7.24.4"),sQuery(id+"F0.wireOp",EDGE,"E7.24.5"),sQuery(id+"F0.wireOp",EDGE,"E7.25.0"),sQuery(id+"F0.wireOp",EDGE,"E7.25.1"),sQuery(id+"F0.wireOp",EDGE,"E7.25.2"),sQuery(id+"F0.wireOp",EDGE,"E7.25.3"),sQuery(id+"F0.wireOp",EDGE,"E7.25.4"),sQuery(id+"F0.wireOp",EDGE,"E7.25.5"),sQuery(id+"F0.wireOp",EDGE,"E7.26.0"),sQuery(id+"F0.wireOp",EDGE,"E7.26.1"),sQuery(id+"F0.wireOp",EDGE,"E7.26.2"),sQuery(id+"F0.wireOp",EDGE,"E7.26.3"),sQuery(id+"F0.wireOp",EDGE,"E7.26.4"),sQuery(id+"F0.wireOp",EDGE,"E7.26.5"),sQuery(id+"F0.wireOp",EDGE,"E7.27.0"),sQuery(id+"F0.wireOp",EDGE,"E7.27.1"),sQuery(id+"F0.wireOp",EDGE,"E7.27.2"),sQuery(id+"F0.wireOp",EDGE,"E7.27.3"),sQuery(id+"F0.wireOp",EDGE,"E7.27.4"),sQuery(id+"F0.wireOp",EDGE,"E7.27.5"),sQuery(id+"F0.wireOp",EDGE,"E7.28.0"),sQuery(id+"F0.wireOp",EDGE,"E7.28.1"),sQuery(id+"F0.wireOp",EDGE,"E7.28.2"),sQuery(id+"F0.wireOp",EDGE,"E7.28.3"),sQuery(id+"F0.wireOp",EDGE,"E7.28.4"),sQuery(id+"F0.wireOp",EDGE,"E7.28.5"),sQuery(id+"F0.wireOp",EDGE,"E7.29.0"),sQuery(id+"F0.wireOp",EDGE,"E7.29.1"),sQuery(id+"F0.wireOp",EDGE,"E7.29.2"),sQuery(id+"F0.wireOp",EDGE,"E7.29.3"),sQuery(id+"F0.wireOp",EDGE,"E7.29.4"),sQuery(id+"F0.wireOp",EDGE,"E7.29.5"),sQuery(id+"F0.wireOp",EDGE,"E7.30.0"),sQuery(id+"F0.wireOp",EDGE,"E7.30.1"),sQuery(id+"F0.wireOp",EDGE,"E7.30.2"),sQuery(id+"F0.wireOp",EDGE,"E7.30.3"),sQuery(id+"F0.wireOp",EDGE,"E7.30.4"),sQuery(id+"F0.wireOp",EDGE,"E7.30.5"),sQuery(id+"F0.wireOp",EDGE,"E7.31.0"),sQuery(id+"F0.wireOp",EDGE,"E7.31.1"),sQuery(id+"F0.wireOp",EDGE,"E7.31.2"),sQuery(id+"F0.wireOp",EDGE,"E7.31.3"),sQuery(id+"F0.wireOp",EDGE,"E7.31.4"),sQuery(id+"F0.wireOp",EDGE,"E7.31.5"),sQuery(id+"F0.wireOp",EDGE,"E7.32.0"),sQuery(id+"F0.wireOp",EDGE,"E7.32.1"),sQuery(id+"F0.wireOp",EDGE,"E7.32.2"),sQuery(id+"F0.wireOp",EDGE,"E7.32.3"),sQuery(id+"F0.wireOp",EDGE,"E7.32.4"),sQuery(id+"F0.wireOp",EDGE,"E7.32.5"),sQuery(id+"F0.wireOp",EDGE,"E7.33.0"),sQuery(id+"F0.wireOp",EDGE,"E7.33.1"),sQuery(id+"F0.wireOp",EDGE,"E7.33.2"),sQuery(id+"F0.wireOp",EDGE,"E7.33.3"),sQuery(id+"F0.wireOp",EDGE,"E7.33.4"),sQuery(id+"F0.wireOp",EDGE,"E7.33.5"),sQuery(id+"F0.wireOp",EDGE,"E7.34.0"),sQuery(id+"F0.wireOp",EDGE,"E7.34.1"),sQuery(id+"F0.wireOp",EDGE,"E7.34.2"),sQuery(id+"F0.wireOp",EDGE,"E7.34.3"),sQuery(id+"F0.wireOp",EDGE,"E7.34.4"),sQuery(id+"F0.wireOp",EDGE,"E7.34.5"),sQuery(id+"F0.wireOp",EDGE,"E7.35.0"),sQuery(id+"F0.wireOp",EDGE,"E7.35.1"),sQuery(id+"F0.wireOp",EDGE,"E7.35.2"),sQuery(id+"F0.wireOp",EDGE,"E7.35.3"),sQuery(id+"F0.wireOp",EDGE,"E7.35.4"),sQuery(id+"F0.wireOp",EDGE,"E7.35.5"),sQuery(id+"F0.wireOp",EDGE,"E7.36.0"),sQuery(id+"F0.wireOp",EDGE,"E7.36.1"),sQuery(id+"F0.wireOp",EDGE,"E7.36.2"),sQuery(id+"F0.wireOp",EDGE,"E7.36.3"),sQuery(id+"F0.wireOp",EDGE,"E7.36.4"),sQuery(id+"F0.wireOp",EDGE,"E7.36.5"),sQuery(id+"F0.wireOp",EDGE,"E7.37.0"),sQuery(id+"F0.wireOp",EDGE,"E7.37.1"),sQuery(id+"F0.wireOp",EDGE,"E7.37.2"),sQuery(id+"F0.wireOp",EDGE,"E7.37.3"),sQuery(id+"F0.wireOp",EDGE,"E7.37.4"),sQuery(id+"F0.wireOp",EDGE,"E7.37.5"),sQuery(id+"F0.wireOp",EDGE,"E7.38.0"),sQuery(id+"F0.wireOp",EDGE,"E7.38.1"),sQuery(id+"F0.wireOp",EDGE,"E7.38.2"),sQuery(id+"F0.wireOp",EDGE,"E7.38.3"),sQuery(id+"F0.wireOp",EDGE,"E7.38.4"),sQuery(id+"F0.wireOp",EDGE,"E7.38.5"),sQuery(id+"F0.wireOp",EDGE,"E7.39.0"),sQuery(id+"F0.wireOp",EDGE,"E7.39.1"),sQuery(id+"F0.wireOp",EDGE,"E7.39.2"),sQuery(id+"F0.wireOp",EDGE,"E7.39.3"),sQuery(id+"F0.wireOp",EDGE,"E7.39.4"),sQuery(id+"F0.wireOp",EDGE,"E7.39.5"),sQuery(id+"F0.wireOp",EDGE,"E7.40.0"),sQuery(id+"F0.wireOp",EDGE,"E7.40.1"),sQuery(id+"F0.wireOp",EDGE,"E7.40.2"),sQuery(id+"F0.wireOp",EDGE,"E7.40.3"),sQuery(id+"F0.wireOp",EDGE,"E7.40.4"),sQuery(id+"F0.wireOp",EDGE,"E7.40.5"),sQuery(id+"F0.wireOp",EDGE,"E7.41.0"),sQuery(id+"F0.wireOp",EDGE,"E7.41.1"),sQuery(id+"F0.wireOp",EDGE,"E7.41.2"),sQuery(id+"F0.wireOp",EDGE,"E7.41.3"),sQuery(id+"F0.wireOp",EDGE,"E7.41.4"),sQuery(id+"F0.wireOp",EDGE,"E7.41.5"),sQuery(id+"F0.wireOp",EDGE,"E7.42.0"),sQuery(id+"F0.wireOp",EDGE,"E7.42.1"),sQuery(id+"F0.wireOp",EDGE,"E7.42.2"),sQuery(id+"F0.wireOp",EDGE,"E7.42.3"),sQuery(id+"F0.wireOp",EDGE,"E7.42.4"),sQuery(id+"F0.wireOp",EDGE,"E7.42.5"),sQuery(id+"F0.wireOp",EDGE,"E7.43.0"),sQuery(id+"F0.wireOp",EDGE,"E7.43.1"),sQuery(id+"F0.wireOp",EDGE,"E7.43.2"),sQuery(id+"F0.wireOp",EDGE,"E7.43.3"),sQuery(id+"F0.wireOp",EDGE,"E7.43.4"),sQuery(id+"F0.wireOp",EDGE,"E7.43.5")])],"isStart":true})]});}
            var Q27;
            {var subQ0=sQuery(id+"F0.wireOp",EDGE,"E7.12.0");Q27=makeQuery(id+"F2.opChamfer","BLEND_EDGE",EDGE,{"blendedFrom":[makeQuery(id+"F1.opExtrude","CAP_EDGE",EDGE,{"disambiguationData":[OSD([subQ0])],"isStart":true}),makeQuery(id+"F1.opExtrude","CAP_FACE",FACE,{"disambiguationData":[OSD([sQuery(id+"F0.wireOp",EDGE,"E1"),sQuery(id+"F0.wireOp",EDGE,"E2"),sQuery(id+"F0.wireOp",EDGE,"E3"),sQuery(id+"F0.wireOp",EDGE,"E4"),sQuery(id+"F0.wireOp",EDGE,"E5"),sQuery(id+"F0.wireOp",EDGE,"E6"),sQuery(id+"F0.wireOp",EDGE,"E7.1.0"),sQuery(id+"F0.wireOp",EDGE,"E7.1.1"),sQuery(id+"F0.wireOp",EDGE,"E7.1.2"),sQuery(id+"F0.wireOp",EDGE,"E7.1.3"),sQuery(id+"F0.wireOp",EDGE,"E7.1.4"),sQuery(id+"F0.wireOp",EDGE,"E7.1.5"),sQuery(id+"F0.wireOp",EDGE,"E7.2.0"),sQuery(id+"F0.wireOp",EDGE,"E7.2.1"),sQuery(id+"F0.wireOp",EDGE,"E7.2.2"),sQuery(id+"F0.wireOp",EDGE,"E7.2.3"),sQuery(id+"F0.wireOp",EDGE,"E7.2.4"),sQuery(id+"F0.wireOp",EDGE,"E7.2.5"),sQuery(id+"F0.wireOp",EDGE,"E7.3.0"),sQuery(id+"F0.wireOp",EDGE,"E7.3.1"),sQuery(id+"F0.wireOp",EDGE,"E7.3.2"),sQuery(id+"F0.wireOp",EDGE,"E7.3.3"),sQuery(id+"F0.wireOp",EDGE,"E7.3.4"),sQuery(id+"F0.wireOp",EDGE,"E7.3.5"),sQuery(id+"F0.wireOp",EDGE,"E7.4.0"),sQuery(id+"F0.wireOp",EDGE,"E7.4.1"),sQuery(id+"F0.wireOp",EDGE,"E7.4.2"),sQuery(id+"F0.wireOp",EDGE,"E7.4.3"),sQuery(id+"F0.wireOp",EDGE,"E7.4.4"),sQuery(id+"F0.wireOp",EDGE,"E7.4.5"),sQuery(id+"F0.wireOp",EDGE,"E7.5.0"),sQuery(id+"F0.wireOp",EDGE,"E7.5.1"),sQuery(id+"F0.wireOp",EDGE,"E7.5.2"),sQuery(id+"F0.wireOp",EDGE,"E7.5.3"),sQuery(id+"F0.wireOp",EDGE,"E7.5.4"),sQuery(id+"F0.wireOp",EDGE,"E7.5.5"),sQuery(id+"F0.wireOp",EDGE,"E7.6.0"),sQuery(id+"F0.wireOp",EDGE,"E7.6.1"),sQuery(id+"F0.wireOp",EDGE,"E7.6.2"),sQuery(id+"F0.wireOp",EDGE,"E7.6.3"),sQuery(id+"F0.wireOp",EDGE,"E7.6.4"),sQuery(id+"F0.wireOp",EDGE,"E7.6.5"),sQuery(id+"F0.wireOp",EDGE,"E7.7.0"),sQuery(id+"F0.wireOp",EDGE,"E7.7.1"),sQuery(id+"F0.wireOp",EDGE,"E7.7.2"),sQuery(id+"F0.wireOp",EDGE,"E7.7.3"),sQuery(id+"F0.wireOp",EDGE,"E7.7.4"),sQuery(id+"F0.wireOp",EDGE,"E7.7.5"),sQuery(id+"F0.wireOp",EDGE,"E7.8.0"),sQuery(id+"F0.wireOp",EDGE,"E7.8.1"),sQuery(id+"F0.wireOp",EDGE,"E7.8.2"),sQuery(id+"F0.wireOp",EDGE,"E7.8.3"),sQuery(id+"F0.wireOp",EDGE,"E7.8.4"),sQuery(id+"F0.wireOp",EDGE,"E7.8.5"),sQuery(id+"F0.wireOp",EDGE,"E7.9.0"),sQuery(id+"F0.wireOp",EDGE,"E7.9.1"),sQuery(id+"F0.wireOp",EDGE,"E7.9.2"),sQuery(id+"F0.wireOp",EDGE,"E7.9.3"),sQuery(id+"F0.wireOp",EDGE,"E7.9.4"),sQuery(id+"F0.wireOp",EDGE,"E7.9.5"),sQuery(id+"F0.wireOp",EDGE,"E7.10.0"),sQuery(id+"F0.wireOp",EDGE,"E7.10.1"),sQuery(id+"F0.wireOp",EDGE,"E7.10.2"),sQuery(id+"F0.wireOp",EDGE,"E7.10.3"),sQuery(id+"F0.wireOp",EDGE,"E7.10.4"),sQuery(id+"F0.wireOp",EDGE,"E7.10.5"),sQuery(id+"F0.wireOp",EDGE,"E7.11.0"),sQuery(id+"F0.wireOp",EDGE,"E7.11.1"),sQuery(id+"F0.wireOp",EDGE,"E7.11.2"),sQuery(id+"F0.wireOp",EDGE,"E7.11.3"),sQuery(id+"F0.wireOp",EDGE,"E7.11.4"),sQuery(id+"F0.wireOp",EDGE,"E7.11.5"),subQ0,sQuery(id+"F0.wireOp",EDGE,"E7.12.1"),sQuery(id+"F0.wireOp",EDGE,"E7.12.2"),sQuery(id+"F0.wireOp",EDGE,"E7.12.3"),sQuery(id+"F0.wireOp",EDGE,"E7.12.4"),sQuery(id+"F0.wireOp",EDGE,"E7.12.5"),sQuery(id+"F0.wireOp",EDGE,"E7.13.0"),sQuery(id+"F0.wireOp",EDGE,"E7.13.1"),sQuery(id+"F0.wireOp",EDGE,"E7.13.2"),sQuery(id+"F0.wireOp",EDGE,"E7.13.3"),sQuery(id+"F0.wireOp",EDGE,"E7.13.4"),sQuery(id+"F0.wireOp",EDGE,"E7.13.5"),sQuery(id+"F0.wireOp",EDGE,"E7.14.0"),sQuery(id+"F0.wireOp",EDGE,"E7.14.1"),sQuery(id+"F0.wireOp",EDGE,"E7.14.2"),sQuery(id+"F0.wireOp",EDGE,"E7.14.3"),sQuery(id+"F0.wireOp",EDGE,"E7.14.4"),sQuery(id+"F0.wireOp",EDGE,"E7.14.5"),sQuery(id+"F0.wireOp",EDGE,"E7.15.0"),sQuery(id+"F0.wireOp",EDGE,"E7.15.1"),sQuery(id+"F0.wireOp",EDGE,"E7.15.2"),sQuery(id+"F0.wireOp",EDGE,"E7.15.3"),sQuery(id+"F0.wireOp",EDGE,"E7.15.4"),sQuery(id+"F0.wireOp",EDGE,"E7.15.5"),sQuery(id+"F0.wireOp",EDGE,"E7.16.0"),sQuery(id+"F0.wireOp",EDGE,"E7.16.1"),sQuery(id+"F0.wireOp",EDGE,"E7.16.2"),sQuery(id+"F0.wireOp",EDGE,"E7.16.3"),sQuery(id+"F0.wireOp",EDGE,"E7.16.4"),sQuery(id+"F0.wireOp",EDGE,"E7.16.5"),sQuery(id+"F0.wireOp",EDGE,"E7.17.0"),sQuery(id+"F0.wireOp",EDGE,"E7.17.1"),sQuery(id+"F0.wireOp",EDGE,"E7.17.2"),sQuery(id+"F0.wireOp",EDGE,"E7.17.3"),sQuery(id+"F0.wireOp",EDGE,"E7.17.4"),sQuery(id+"F0.wireOp",EDGE,"E7.17.5"),sQuery(id+"F0.wireOp",EDGE,"E7.18.0"),sQuery(id+"F0.wireOp",EDGE,"E7.18.1"),sQuery(id+"F0.wireOp",EDGE,"E7.18.2"),sQuery(id+"F0.wireOp",EDGE,"E7.18.3"),sQuery(id+"F0.wireOp",EDGE,"E7.18.4"),sQuery(id+"F0.wireOp",EDGE,"E7.18.5"),sQuery(id+"F0.wireOp",EDGE,"E7.19.0"),sQuery(id+"F0.wireOp",EDGE,"E7.19.1"),sQuery(id+"F0.wireOp",EDGE,"E7.19.2"),sQuery(id+"F0.wireOp",EDGE,"E7.19.3"),sQuery(id+"F0.wireOp",EDGE,"E7.19.4"),sQuery(id+"F0.wireOp",EDGE,"E7.19.5"),sQuery(id+"F0.wireOp",EDGE,"E7.20.0"),sQuery(id+"F0.wireOp",EDGE,"E7.20.1"),sQuery(id+"F0.wireOp",EDGE,"E7.20.2"),sQuery(id+"F0.wireOp",EDGE,"E7.20.3"),sQuery(id+"F0.wireOp",EDGE,"E7.20.4"),sQuery(id+"F0.wireOp",EDGE,"E7.20.5"),sQuery(id+"F0.wireOp",EDGE,"E7.21.0"),sQuery(id+"F0.wireOp",EDGE,"E7.21.1"),sQuery(id+"F0.wireOp",EDGE,"E7.21.2"),sQuery(id+"F0.wireOp",EDGE,"E7.21.3"),sQuery(id+"F0.wireOp",EDGE,"E7.21.4"),sQuery(id+"F0.wireOp",EDGE,"E7.21.5"),sQuery(id+"F0.wireOp",EDGE,"E7.22.0"),sQuery(id+"F0.wireOp",EDGE,"E7.22.1"),sQuery(id+"F0.wireOp",EDGE,"E7.22.2"),sQuery(id+"F0.wireOp",EDGE,"E7.22.3"),sQuery(id+"F0.wireOp",EDGE,"E7.22.4"),sQuery(id+"F0.wireOp",EDGE,"E7.22.5"),sQuery(id+"F0.wireOp",EDGE,"E7.23.0"),sQuery(id+"F0.wireOp",EDGE,"E7.23.1"),sQuery(id+"F0.wireOp",EDGE,"E7.23.2"),sQuery(id+"F0.wireOp",EDGE,"E7.23.3"),sQuery(id+"F0.wireOp",EDGE,"E7.23.4"),sQuery(id+"F0.wireOp",EDGE,"E7.23.5"),sQuery(id+"F0.wireOp",EDGE,"E7.24.0"),sQuery(id+"F0.wireOp",EDGE,"E7.24.1"),sQuery(id+"F0.wireOp",EDGE,"E7.24.2"),sQuery(id+"F0.wireOp",EDGE,"E7.24.3"),sQuery(id+"F0.wireOp",EDGE,"E7.24.4"),sQuery(id+"F0.wireOp",EDGE,"E7.24.5"),sQuery(id+"F0.wireOp",EDGE,"E7.25.0"),sQuery(id+"F0.wireOp",EDGE,"E7.25.1"),sQuery(id+"F0.wireOp",EDGE,"E7.25.2"),sQuery(id+"F0.wireOp",EDGE,"E7.25.3"),sQuery(id+"F0.wireOp",EDGE,"E7.25.4"),sQuery(id+"F0.wireOp",EDGE,"E7.25.5"),sQuery(id+"F0.wireOp",EDGE,"E7.26.0"),sQuery(id+"F0.wireOp",EDGE,"E7.26.1"),sQuery(id+"F0.wireOp",EDGE,"E7.26.2"),sQuery(id+"F0.wireOp",EDGE,"E7.26.3"),sQuery(id+"F0.wireOp",EDGE,"E7.26.4"),sQuery(id+"F0.wireOp",EDGE,"E7.26.5"),sQuery(id+"F0.wireOp",EDGE,"E7.27.0"),sQuery(id+"F0.wireOp",EDGE,"E7.27.1"),sQuery(id+"F0.wireOp",EDGE,"E7.27.2"),sQuery(id+"F0.wireOp",EDGE,"E7.27.3"),sQuery(id+"F0.wireOp",EDGE,"E7.27.4"),sQuery(id+"F0.wireOp",EDGE,"E7.27.5"),sQuery(id+"F0.wireOp",EDGE,"E7.28.0"),sQuery(id+"F0.wireOp",EDGE,"E7.28.1"),sQuery(id+"F0.wireOp",EDGE,"E7.28.2"),sQuery(id+"F0.wireOp",EDGE,"E7.28.3"),sQuery(id+"F0.wireOp",EDGE,"E7.28.4"),sQuery(id+"F0.wireOp",EDGE,"E7.28.5"),sQuery(id+"F0.wireOp",EDGE,"E7.29.0"),sQuery(id+"F0.wireOp",EDGE,"E7.29.1"),sQuery(id+"F0.wireOp",EDGE,"E7.29.2"),sQuery(id+"F0.wireOp",EDGE,"E7.29.3"),sQuery(id+"F0.wireOp",EDGE,"E7.29.4"),sQuery(id+"F0.wireOp",EDGE,"E7.29.5"),sQuery(id+"F0.wireOp",EDGE,"E7.30.0"),sQuery(id+"F0.wireOp",EDGE,"E7.30.1"),sQuery(id+"F0.wireOp",EDGE,"E7.30.2"),sQuery(id+"F0.wireOp",EDGE,"E7.30.3"),sQuery(id+"F0.wireOp",EDGE,"E7.30.4"),sQuery(id+"F0.wireOp",EDGE,"E7.30.5"),sQuery(id+"F0.wireOp",EDGE,"E7.31.0"),sQuery(id+"F0.wireOp",EDGE,"E7.31.1"),sQuery(id+"F0.wireOp",EDGE,"E7.31.2"),sQuery(id+"F0.wireOp",EDGE,"E7.31.3"),sQuery(id+"F0.wireOp",EDGE,"E7.31.4"),sQuery(id+"F0.wireOp",EDGE,"E7.31.5"),sQuery(id+"F0.wireOp",EDGE,"E7.32.0"),sQuery(id+"F0.wireOp",EDGE,"E7.32.1"),sQuery(id+"F0.wireOp",EDGE,"E7.32.2"),sQuery(id+"F0.wireOp",EDGE,"E7.32.3"),sQuery(id+"F0.wireOp",EDGE,"E7.32.4"),sQuery(id+"F0.wireOp",EDGE,"E7.32.5"),sQuery(id+"F0.wireOp",EDGE,"E7.33.0"),sQuery(id+"F0.wireOp",EDGE,"E7.33.1"),sQuery(id+"F0.wireOp",EDGE,"E7.33.2"),sQuery(id+"F0.wireOp",EDGE,"E7.33.3"),sQuery(id+"F0.wireOp",EDGE,"E7.33.4"),sQuery(id+"F0.wireOp",EDGE,"E7.33.5"),sQuery(id+"F0.wireOp",EDGE,"E7.34.0"),sQuery(id+"F0.wireOp",EDGE,"E7.34.1"),sQuery(id+"F0.wireOp",EDGE,"E7.34.2"),sQuery(id+"F0.wireOp",EDGE,"E7.34.3"),sQuery(id+"F0.wireOp",EDGE,"E7.34.4"),sQuery(id+"F0.wireOp",EDGE,"E7.34.5"),sQuery(id+"F0.wireOp",EDGE,"E7.35.0"),sQuery(id+"F0.wireOp",EDGE,"E7.35.1"),sQuery(id+"F0.wireOp",EDGE,"E7.35.2"),sQuery(id+"F0.wireOp",EDGE,"E7.35.3"),sQuery(id+"F0.wireOp",EDGE,"E7.35.4"),sQuery(id+"F0.wireOp",EDGE,"E7.35.5"),sQuery(id+"F0.wireOp",EDGE,"E7.36.0"),sQuery(id+"F0.wireOp",EDGE,"E7.36.1"),sQuery(id+"F0.wireOp",EDGE,"E7.36.2"),sQuery(id+"F0.wireOp",EDGE,"E7.36.3"),sQuery(id+"F0.wireOp",EDGE,"E7.36.4"),sQuery(id+"F0.wireOp",EDGE,"E7.36.5"),sQuery(id+"F0.wireOp",EDGE,"E7.37.0"),sQuery(id+"F0.wireOp",EDGE,"E7.37.1"),sQuery(id+"F0.wireOp",EDGE,"E7.37.2"),sQuery(id+"F0.wireOp",EDGE,"E7.37.3"),sQuery(id+"F0.wireOp",EDGE,"E7.37.4"),sQuery(id+"F0.wireOp",EDGE,"E7.37.5"),sQuery(id+"F0.wireOp",EDGE,"E7.38.0"),sQuery(id+"F0.wireOp",EDGE,"E7.38.1"),sQuery(id+"F0.wireOp",EDGE,"E7.38.2"),sQuery(id+"F0.wireOp",EDGE,"E7.38.3"),sQuery(id+"F0.wireOp",EDGE,"E7.38.4"),sQuery(id+"F0.wireOp",EDGE,"E7.38.5"),sQuery(id+"F0.wireOp",EDGE,"E7.39.0"),sQuery(id+"F0.wireOp",EDGE,"E7.39.1"),sQuery(id+"F0.wireOp",EDGE,"E7.39.2"),sQuery(id+"F0.wireOp",EDGE,"E7.39.3"),sQuery(id+"F0.wireOp",EDGE,"E7.39.4"),sQuery(id+"F0.wireOp",EDGE,"E7.39.5"),sQuery(id+"F0.wireOp",EDGE,"E7.40.0"),sQuery(id+"F0.wireOp",EDGE,"E7.40.1"),sQuery(id+"F0.wireOp",EDGE,"E7.40.2"),sQuery(id+"F0.wireOp",EDGE,"E7.40.3"),sQuery(id+"F0.wireOp",EDGE,"E7.40.4"),sQuery(id+"F0.wireOp",EDGE,"E7.40.5"),sQuery(id+"F0.wireOp",EDGE,"E7.41.0"),sQuery(id+"F0.wireOp",EDGE,"E7.41.1"),sQuery(id+"F0.wireOp",EDGE,"E7.41.2"),sQuery(id+"F0.wireOp",EDGE,"E7.41.3"),sQuery(id+"F0.wireOp",EDGE,"E7.41.4"),sQuery(id+"F0.wireOp",EDGE,"E7.41.5"),sQuery(id+"F0.wireOp",EDGE,"E7.42.0"),sQuery(id+"F0.wireOp",EDGE,"E7.42.1"),sQuery(id+"F0.wireOp",EDGE,"E7.42.2"),sQuery(id+"F0.wireOp",EDGE,"E7.42.3"),sQuery(id+"F0.wireOp",EDGE,"E7.42.4"),sQuery(id+"F0.wireOp",EDGE,"E7.42.5"),sQuery(id+"F0.wireOp",EDGE,"E7.43.0"),sQuery(id+"F0.wireOp",EDGE,"E7.43.1"),sQuery(id+"F0.wireOp",EDGE,"E7.43.2"),sQuery(id+"F0.wireOp",EDGE,"E7.43.3"),sQuery(id+"F0.wireOp",EDGE,"E7.43.4"),sQuery(id+"F0.wireOp",EDGE,"E7.43.5")])],"isStart":true})],"blendedInto":[makeQuery(id+"F1.opExtrude","CAP_FACE",FACE,{"disambiguationData":[OSD([sQuery(id+"F0.wireOp",EDGE,"E1"),sQuery(id+"F0.wireOp",EDGE,"E2"),sQuery(id+"F0.wireOp",EDGE,"E3"),sQuery(id+"F0.wireOp",EDGE,"E4"),sQuery(id+"F0.wireOp",EDGE,"E5"),sQuery(id+"F0.wireOp",EDGE,"E6"),sQuery(id+"F0.wireOp",EDGE,"E7.1.0"),sQuery(id+"F0.wireOp",EDGE,"E7.1.1"),sQuery(id+"F0.wireOp",EDGE,"E7.1.2"),sQuery(id+"F0.wireOp",EDGE,"E7.1.3"),sQuery(id+"F0.wireOp",EDGE,"E7.1.4"),sQuery(id+"F0.wireOp",EDGE,"E7.1.5"),sQuery(id+"F0.wireOp",EDGE,"E7.2.0"),sQuery(id+"F0.wireOp",EDGE,"E7.2.1"),sQuery(id+"F0.wireOp",EDGE,"E7.2.2"),sQuery(id+"F0.wireOp",EDGE,"E7.2.3"),sQuery(id+"F0.wireOp",EDGE,"E7.2.4"),sQuery(id+"F0.wireOp",EDGE,"E7.2.5"),sQuery(id+"F0.wireOp",EDGE,"E7.3.0"),sQuery(id+"F0.wireOp",EDGE,"E7.3.1"),sQuery(id+"F0.wireOp",EDGE,"E7.3.2"),sQuery(id+"F0.wireOp",EDGE,"E7.3.3"),sQuery(id+"F0.wireOp",EDGE,"E7.3.4"),sQuery(id+"F0.wireOp",EDGE,"E7.3.5"),sQuery(id+"F0.wireOp",EDGE,"E7.4.0"),sQuery(id+"F0.wireOp",EDGE,"E7.4.1"),sQuery(id+"F0.wireOp",EDGE,"E7.4.2"),sQuery(id+"F0.wireOp",EDGE,"E7.4.3"),sQuery(id+"F0.wireOp",EDGE,"E7.4.4"),sQuery(id+"F0.wireOp",EDGE,"E7.4.5"),sQuery(id+"F0.wireOp",EDGE,"E7.5.0"),sQuery(id+"F0.wireOp",EDGE,"E7.5.1"),sQuery(id+"F0.wireOp",EDGE,"E7.5.2"),sQuery(id+"F0.wireOp",EDGE,"E7.5.3"),sQuery(id+"F0.wireOp",EDGE,"E7.5.4"),sQuery(id+"F0.wireOp",EDGE,"E7.5.5"),sQuery(id+"F0.wireOp",EDGE,"E7.6.0"),sQuery(id+"F0.wireOp",EDGE,"E7.6.1"),sQuery(id+"F0.wireOp",EDGE,"E7.6.2"),sQuery(id+"F0.wireOp",EDGE,"E7.6.3"),sQuery(id+"F0.wireOp",EDGE,"E7.6.4"),sQuery(id+"F0.wireOp",EDGE,"E7.6.5"),sQuery(id+"F0.wireOp",EDGE,"E7.7.0"),sQuery(id+"F0.wireOp",EDGE,"E7.7.1"),sQuery(id+"F0.wireOp",EDGE,"E7.7.2"),sQuery(id+"F0.wireOp",EDGE,"E7.7.3"),sQuery(id+"F0.wireOp",EDGE,"E7.7.4"),sQuery(id+"F0.wireOp",EDGE,"E7.7.5"),sQuery(id+"F0.wireOp",EDGE,"E7.8.0"),sQuery(id+"F0.wireOp",EDGE,"E7.8.1"),sQuery(id+"F0.wireOp",EDGE,"E7.8.2"),sQuery(id+"F0.wireOp",EDGE,"E7.8.3"),sQuery(id+"F0.wireOp",EDGE,"E7.8.4"),sQuery(id+"F0.wireOp",EDGE,"E7.8.5"),sQuery(id+"F0.wireOp",EDGE,"E7.9.0"),sQuery(id+"F0.wireOp",EDGE,"E7.9.1"),sQuery(id+"F0.wireOp",EDGE,"E7.9.2"),sQuery(id+"F0.wireOp",EDGE,"E7.9.3"),sQuery(id+"F0.wireOp",EDGE,"E7.9.4"),sQuery(id+"F0.wireOp",EDGE,"E7.9.5"),sQuery(id+"F0.wireOp",EDGE,"E7.10.0"),sQuery(id+"F0.wireOp",EDGE,"E7.10.1"),sQuery(id+"F0.wireOp",EDGE,"E7.10.2"),sQuery(id+"F0.wireOp",EDGE,"E7.10.3"),sQuery(id+"F0.wireOp",EDGE,"E7.10.4"),sQuery(id+"F0.wireOp",EDGE,"E7.10.5"),sQuery(id+"F0.wireOp",EDGE,"E7.11.0"),sQuery(id+"F0.wireOp",EDGE,"E7.11.1"),sQuery(id+"F0.wireOp",EDGE,"E7.11.2"),sQuery(id+"F0.wireOp",EDGE,"E7.11.3"),sQuery(id+"F0.wireOp",EDGE,"E7.11.4"),sQuery(id+"F0.wireOp",EDGE,"E7.11.5"),subQ0,sQuery(id+"F0.wireOp",EDGE,"E7.12.1"),sQuery(id+"F0.wireOp",EDGE,"E7.12.2"),sQuery(id+"F0.wireOp",EDGE,"E7.12.3"),sQuery(id+"F0.wireOp",EDGE,"E7.12.4"),sQuery(id+"F0.wireOp",EDGE,"E7.12.5"),sQuery(id+"F0.wireOp",EDGE,"E7.13.0"),sQuery(id+"F0.wireOp",EDGE,"E7.13.1"),sQuery(id+"F0.wireOp",EDGE,"E7.13.2"),sQuery(id+"F0.wireOp",EDGE,"E7.13.3"),sQuery(id+"F0.wireOp",EDGE,"E7.13.4"),sQuery(id+"F0.wireOp",EDGE,"E7.13.5"),sQuery(id+"F0.wireOp",EDGE,"E7.14.0"),sQuery(id+"F0.wireOp",EDGE,"E7.14.1"),sQuery(id+"F0.wireOp",EDGE,"E7.14.2"),sQuery(id+"F0.wireOp",EDGE,"E7.14.3"),sQuery(id+"F0.wireOp",EDGE,"E7.14.4"),sQuery(id+"F0.wireOp",EDGE,"E7.14.5"),sQuery(id+"F0.wireOp",EDGE,"E7.15.0"),sQuery(id+"F0.wireOp",EDGE,"E7.15.1"),sQuery(id+"F0.wireOp",EDGE,"E7.15.2"),sQuery(id+"F0.wireOp",EDGE,"E7.15.3"),sQuery(id+"F0.wireOp",EDGE,"E7.15.4"),sQuery(id+"F0.wireOp",EDGE,"E7.15.5"),sQuery(id+"F0.wireOp",EDGE,"E7.16.0"),sQuery(id+"F0.wireOp",EDGE,"E7.16.1"),sQuery(id+"F0.wireOp",EDGE,"E7.16.2"),sQuery(id+"F0.wireOp",EDGE,"E7.16.3"),sQuery(id+"F0.wireOp",EDGE,"E7.16.4"),sQuery(id+"F0.wireOp",EDGE,"E7.16.5"),sQuery(id+"F0.wireOp",EDGE,"E7.17.0"),sQuery(id+"F0.wireOp",EDGE,"E7.17.1"),sQuery(id+"F0.wireOp",EDGE,"E7.17.2"),sQuery(id+"F0.wireOp",EDGE,"E7.17.3"),sQuery(id+"F0.wireOp",EDGE,"E7.17.4"),sQuery(id+"F0.wireOp",EDGE,"E7.17.5"),sQuery(id+"F0.wireOp",EDGE,"E7.18.0"),sQuery(id+"F0.wireOp",EDGE,"E7.18.1"),sQuery(id+"F0.wireOp",EDGE,"E7.18.2"),sQuery(id+"F0.wireOp",EDGE,"E7.18.3"),sQuery(id+"F0.wireOp",EDGE,"E7.18.4"),sQuery(id+"F0.wireOp",EDGE,"E7.18.5"),sQuery(id+"F0.wireOp",EDGE,"E7.19.0"),sQuery(id+"F0.wireOp",EDGE,"E7.19.1"),sQuery(id+"F0.wireOp",EDGE,"E7.19.2"),sQuery(id+"F0.wireOp",EDGE,"E7.19.3"),sQuery(id+"F0.wireOp",EDGE,"E7.19.4"),sQuery(id+"F0.wireOp",EDGE,"E7.19.5"),sQuery(id+"F0.wireOp",EDGE,"E7.20.0"),sQuery(id+"F0.wireOp",EDGE,"E7.20.1"),sQuery(id+"F0.wireOp",EDGE,"E7.20.2"),sQuery(id+"F0.wireOp",EDGE,"E7.20.3"),sQuery(id+"F0.wireOp",EDGE,"E7.20.4"),sQuery(id+"F0.wireOp",EDGE,"E7.20.5"),sQuery(id+"F0.wireOp",EDGE,"E7.21.0"),sQuery(id+"F0.wireOp",EDGE,"E7.21.1"),sQuery(id+"F0.wireOp",EDGE,"E7.21.2"),sQuery(id+"F0.wireOp",EDGE,"E7.21.3"),sQuery(id+"F0.wireOp",EDGE,"E7.21.4"),sQuery(id+"F0.wireOp",EDGE,"E7.21.5"),sQuery(id+"F0.wireOp",EDGE,"E7.22.0"),sQuery(id+"F0.wireOp",EDGE,"E7.22.1"),sQuery(id+"F0.wireOp",EDGE,"E7.22.2"),sQuery(id+"F0.wireOp",EDGE,"E7.22.3"),sQuery(id+"F0.wireOp",EDGE,"E7.22.4"),sQuery(id+"F0.wireOp",EDGE,"E7.22.5"),sQuery(id+"F0.wireOp",EDGE,"E7.23.0"),sQuery(id+"F0.wireOp",EDGE,"E7.23.1"),sQuery(id+"F0.wireOp",EDGE,"E7.23.2"),sQuery(id+"F0.wireOp",EDGE,"E7.23.3"),sQuery(id+"F0.wireOp",EDGE,"E7.23.4"),sQuery(id+"F0.wireOp",EDGE,"E7.23.5"),sQuery(id+"F0.wireOp",EDGE,"E7.24.0"),sQuery(id+"F0.wireOp",EDGE,"E7.24.1"),sQuery(id+"F0.wireOp",EDGE,"E7.24.2"),sQuery(id+"F0.wireOp",EDGE,"E7.24.3"),sQuery(id+"F0.wireOp",EDGE,"E7.24.4"),sQuery(id+"F0.wireOp",EDGE,"E7.24.5"),sQuery(id+"F0.wireOp",EDGE,"E7.25.0"),sQuery(id+"F0.wireOp",EDGE,"E7.25.1"),sQuery(id+"F0.wireOp",EDGE,"E7.25.2"),sQuery(id+"F0.wireOp",EDGE,"E7.25.3"),sQuery(id+"F0.wireOp",EDGE,"E7.25.4"),sQuery(id+"F0.wireOp",EDGE,"E7.25.5"),sQuery(id+"F0.wireOp",EDGE,"E7.26.0"),sQuery(id+"F0.wireOp",EDGE,"E7.26.1"),sQuery(id+"F0.wireOp",EDGE,"E7.26.2"),sQuery(id+"F0.wireOp",EDGE,"E7.26.3"),sQuery(id+"F0.wireOp",EDGE,"E7.26.4"),sQuery(id+"F0.wireOp",EDGE,"E7.26.5"),sQuery(id+"F0.wireOp",EDGE,"E7.27.0"),sQuery(id+"F0.wireOp",EDGE,"E7.27.1"),sQuery(id+"F0.wireOp",EDGE,"E7.27.2"),sQuery(id+"F0.wireOp",EDGE,"E7.27.3"),sQuery(id+"F0.wireOp",EDGE,"E7.27.4"),sQuery(id+"F0.wireOp",EDGE,"E7.27.5"),sQuery(id+"F0.wireOp",EDGE,"E7.28.0"),sQuery(id+"F0.wireOp",EDGE,"E7.28.1"),sQuery(id+"F0.wireOp",EDGE,"E7.28.2"),sQuery(id+"F0.wireOp",EDGE,"E7.28.3"),sQuery(id+"F0.wireOp",EDGE,"E7.28.4"),sQuery(id+"F0.wireOp",EDGE,"E7.28.5"),sQuery(id+"F0.wireOp",EDGE,"E7.29.0"),sQuery(id+"F0.wireOp",EDGE,"E7.29.1"),sQuery(id+"F0.wireOp",EDGE,"E7.29.2"),sQuery(id+"F0.wireOp",EDGE,"E7.29.3"),sQuery(id+"F0.wireOp",EDGE,"E7.29.4"),sQuery(id+"F0.wireOp",EDGE,"E7.29.5"),sQuery(id+"F0.wireOp",EDGE,"E7.30.0"),sQuery(id+"F0.wireOp",EDGE,"E7.30.1"),sQuery(id+"F0.wireOp",EDGE,"E7.30.2"),sQuery(id+"F0.wireOp",EDGE,"E7.30.3"),sQuery(id+"F0.wireOp",EDGE,"E7.30.4"),sQuery(id+"F0.wireOp",EDGE,"E7.30.5"),sQuery(id+"F0.wireOp",EDGE,"E7.31.0"),sQuery(id+"F0.wireOp",EDGE,"E7.31.1"),sQuery(id+"F0.wireOp",EDGE,"E7.31.2"),sQuery(id+"F0.wireOp",EDGE,"E7.31.3"),sQuery(id+"F0.wireOp",EDGE,"E7.31.4"),sQuery(id+"F0.wireOp",EDGE,"E7.31.5"),sQuery(id+"F0.wireOp",EDGE,"E7.32.0"),sQuery(id+"F0.wireOp",EDGE,"E7.32.1"),sQuery(id+"F0.wireOp",EDGE,"E7.32.2"),sQuery(id+"F0.wireOp",EDGE,"E7.32.3"),sQuery(id+"F0.wireOp",EDGE,"E7.32.4"),sQuery(id+"F0.wireOp",EDGE,"E7.32.5"),sQuery(id+"F0.wireOp",EDGE,"E7.33.0"),sQuery(id+"F0.wireOp",EDGE,"E7.33.1"),sQuery(id+"F0.wireOp",EDGE,"E7.33.2"),sQuery(id+"F0.wireOp",EDGE,"E7.33.3"),sQuery(id+"F0.wireOp",EDGE,"E7.33.4"),sQuery(id+"F0.wireOp",EDGE,"E7.33.5"),sQuery(id+"F0.wireOp",EDGE,"E7.34.0"),sQuery(id+"F0.wireOp",EDGE,"E7.34.1"),sQuery(id+"F0.wireOp",EDGE,"E7.34.2"),sQuery(id+"F0.wireOp",EDGE,"E7.34.3"),sQuery(id+"F0.wireOp",EDGE,"E7.34.4"),sQuery(id+"F0.wireOp",EDGE,"E7.34.5"),sQuery(id+"F0.wireOp",EDGE,"E7.35.0"),sQuery(id+"F0.wireOp",EDGE,"E7.35.1"),sQuery(id+"F0.wireOp",EDGE,"E7.35.2"),sQuery(id+"F0.wireOp",EDGE,"E7.35.3"),sQuery(id+"F0.wireOp",EDGE,"E7.35.4"),sQuery(id+"F0.wireOp",EDGE,"E7.35.5"),sQuery(id+"F0.wireOp",EDGE,"E7.36.0"),sQuery(id+"F0.wireOp",EDGE,"E7.36.1"),sQuery(id+"F0.wireOp",EDGE,"E7.36.2"),sQuery(id+"F0.wireOp",EDGE,"E7.36.3"),sQuery(id+"F0.wireOp",EDGE,"E7.36.4"),sQuery(id+"F0.wireOp",EDGE,"E7.36.5"),sQuery(id+"F0.wireOp",EDGE,"E7.37.0"),sQuery(id+"F0.wireOp",EDGE,"E7.37.1"),sQuery(id+"F0.wireOp",EDGE,"E7.37.2"),sQuery(id+"F0.wireOp",EDGE,"E7.37.3"),sQuery(id+"F0.wireOp",EDGE,"E7.37.4"),sQuery(id+"F0.wireOp",EDGE,"E7.37.5"),sQuery(id+"F0.wireOp",EDGE,"E7.38.0"),sQuery(id+"F0.wireOp",EDGE,"E7.38.1"),sQuery(id+"F0.wireOp",EDGE,"E7.38.2"),sQuery(id+"F0.wireOp",EDGE,"E7.38.3"),sQuery(id+"F0.wireOp",EDGE,"E7.38.4"),sQuery(id+"F0.wireOp",EDGE,"E7.38.5"),sQuery(id+"F0.wireOp",EDGE,"E7.39.0"),sQuery(id+"F0.wireOp",EDGE,"E7.39.1"),sQuery(id+"F0.wireOp",EDGE,"E7.39.2"),sQuery(id+"F0.wireOp",EDGE,"E7.39.3"),sQuery(id+"F0.wireOp",EDGE,"E7.39.4"),sQuery(id+"F0.wireOp",EDGE,"E7.39.5"),sQuery(id+"F0.wireOp",EDGE,"E7.40.0"),sQuery(id+"F0.wireOp",EDGE,"E7.40.1"),sQuery(id+"F0.wireOp",EDGE,"E7.40.2"),sQuery(id+"F0.wireOp",EDGE,"E7.40.3"),sQuery(id+"F0.wireOp",EDGE,"E7.40.4"),sQuery(id+"F0.wireOp",EDGE,"E7.40.5"),sQuery(id+"F0.wireOp",EDGE,"E7.41.0"),sQuery(id+"F0.wireOp",EDGE,"E7.41.1"),sQuery(id+"F0.wireOp",EDGE,"E7.41.2"),sQuery(id+"F0.wireOp",EDGE,"E7.41.3"),sQuery(id+"F0.wireOp",EDGE,"E7.41.4"),sQuery(id+"F0.wireOp",EDGE,"E7.41.5"),sQuery(id+"F0.wireOp",EDGE,"E7.42.0"),sQuery(id+"F0.wireOp",EDGE,"E7.42.1"),sQuery(id+"F0.wireOp",EDGE,"E7.42.2"),sQuery(id+"F0.wireOp",EDGE,"E7.42.3"),sQuery(id+"F0.wireOp",EDGE,"E7.42.4"),sQuery(id+"F0.wireOp",EDGE,"E7.42.5"),sQuery(id+"F0.wireOp",EDGE,"E7.43.0"),sQuery(id+"F0.wireOp",EDGE,"E7.43.1"),sQuery(id+"F0.wireOp",EDGE,"E7.43.2"),sQuery(id+"F0.wireOp",EDGE,"E7.43.3"),sQuery(id+"F0.wireOp",EDGE,"E7.43.4"),sQuery(id+"F0.wireOp",EDGE,"E7.43.5")])],"isStart":true})]});}
            var Q28;
            {var subQ0=sQuery(id+"F0.wireOp",EDGE,"E7.14.0");Q28=makeQuery(id+"F2.opChamfer","BLEND_EDGE",EDGE,{"blendedFrom":[makeQuery(id+"F1.opExtrude","CAP_EDGE",EDGE,{"disambiguationData":[OSD([subQ0])],"isStart":true}),makeQuery(id+"F1.opExtrude","CAP_FACE",FACE,{"disambiguationData":[OSD([sQuery(id+"F0.wireOp",EDGE,"E1"),sQuery(id+"F0.wireOp",EDGE,"E2"),sQuery(id+"F0.wireOp",EDGE,"E3"),sQuery(id+"F0.wireOp",EDGE,"E4"),sQuery(id+"F0.wireOp",EDGE,"E5"),sQuery(id+"F0.wireOp",EDGE,"E6"),sQuery(id+"F0.wireOp",EDGE,"E7.1.0"),sQuery(id+"F0.wireOp",EDGE,"E7.1.1"),sQuery(id+"F0.wireOp",EDGE,"E7.1.2"),sQuery(id+"F0.wireOp",EDGE,"E7.1.3"),sQuery(id+"F0.wireOp",EDGE,"E7.1.4"),sQuery(id+"F0.wireOp",EDGE,"E7.1.5"),sQuery(id+"F0.wireOp",EDGE,"E7.2.0"),sQuery(id+"F0.wireOp",EDGE,"E7.2.1"),sQuery(id+"F0.wireOp",EDGE,"E7.2.2"),sQuery(id+"F0.wireOp",EDGE,"E7.2.3"),sQuery(id+"F0.wireOp",EDGE,"E7.2.4"),sQuery(id+"F0.wireOp",EDGE,"E7.2.5"),sQuery(id+"F0.wireOp",EDGE,"E7.3.0"),sQuery(id+"F0.wireOp",EDGE,"E7.3.1"),sQuery(id+"F0.wireOp",EDGE,"E7.3.2"),sQuery(id+"F0.wireOp",EDGE,"E7.3.3"),sQuery(id+"F0.wireOp",EDGE,"E7.3.4"),sQuery(id+"F0.wireOp",EDGE,"E7.3.5"),sQuery(id+"F0.wireOp",EDGE,"E7.4.0"),sQuery(id+"F0.wireOp",EDGE,"E7.4.1"),sQuery(id+"F0.wireOp",EDGE,"E7.4.2"),sQuery(id+"F0.wireOp",EDGE,"E7.4.3"),sQuery(id+"F0.wireOp",EDGE,"E7.4.4"),sQuery(id+"F0.wireOp",EDGE,"E7.4.5"),sQuery(id+"F0.wireOp",EDGE,"E7.5.0"),sQuery(id+"F0.wireOp",EDGE,"E7.5.1"),sQuery(id+"F0.wireOp",EDGE,"E7.5.2"),sQuery(id+"F0.wireOp",EDGE,"E7.5.3"),sQuery(id+"F0.wireOp",EDGE,"E7.5.4"),sQuery(id+"F0.wireOp",EDGE,"E7.5.5"),sQuery(id+"F0.wireOp",EDGE,"E7.6.0"),sQuery(id+"F0.wireOp",EDGE,"E7.6.1"),sQuery(id+"F0.wireOp",EDGE,"E7.6.2"),sQuery(id+"F0.wireOp",EDGE,"E7.6.3"),sQuery(id+"F0.wireOp",EDGE,"E7.6.4"),sQuery(id+"F0.wireOp",EDGE,"E7.6.5"),sQuery(id+"F0.wireOp",EDGE,"E7.7.0"),sQuery(id+"F0.wireOp",EDGE,"E7.7.1"),sQuery(id+"F0.wireOp",EDGE,"E7.7.2"),sQuery(id+"F0.wireOp",EDGE,"E7.7.3"),sQuery(id+"F0.wireOp",EDGE,"E7.7.4"),sQuery(id+"F0.wireOp",EDGE,"E7.7.5"),sQuery(id+"F0.wireOp",EDGE,"E7.8.0"),sQuery(id+"F0.wireOp",EDGE,"E7.8.1"),sQuery(id+"F0.wireOp",EDGE,"E7.8.2"),sQuery(id+"F0.wireOp",EDGE,"E7.8.3"),sQuery(id+"F0.wireOp",EDGE,"E7.8.4"),sQuery(id+"F0.wireOp",EDGE,"E7.8.5"),sQuery(id+"F0.wireOp",EDGE,"E7.9.0"),sQuery(id+"F0.wireOp",EDGE,"E7.9.1"),sQuery(id+"F0.wireOp",EDGE,"E7.9.2"),sQuery(id+"F0.wireOp",EDGE,"E7.9.3"),sQuery(id+"F0.wireOp",EDGE,"E7.9.4"),sQuery(id+"F0.wireOp",EDGE,"E7.9.5"),sQuery(id+"F0.wireOp",EDGE,"E7.10.0"),sQuery(id+"F0.wireOp",EDGE,"E7.10.1"),sQuery(id+"F0.wireOp",EDGE,"E7.10.2"),sQuery(id+"F0.wireOp",EDGE,"E7.10.3"),sQuery(id+"F0.wireOp",EDGE,"E7.10.4"),sQuery(id+"F0.wireOp",EDGE,"E7.10.5"),sQuery(id+"F0.wireOp",EDGE,"E7.11.0"),sQuery(id+"F0.wireOp",EDGE,"E7.11.1"),sQuery(id+"F0.wireOp",EDGE,"E7.11.2"),sQuery(id+"F0.wireOp",EDGE,"E7.11.3"),sQuery(id+"F0.wireOp",EDGE,"E7.11.4"),sQuery(id+"F0.wireOp",EDGE,"E7.11.5"),sQuery(id+"F0.wireOp",EDGE,"E7.12.0"),sQuery(id+"F0.wireOp",EDGE,"E7.12.1"),sQuery(id+"F0.wireOp",EDGE,"E7.12.2"),sQuery(id+"F0.wireOp",EDGE,"E7.12.3"),sQuery(id+"F0.wireOp",EDGE,"E7.12.4"),sQuery(id+"F0.wireOp",EDGE,"E7.12.5"),sQuery(id+"F0.wireOp",EDGE,"E7.13.0"),sQuery(id+"F0.wireOp",EDGE,"E7.13.1"),sQuery(id+"F0.wireOp",EDGE,"E7.13.2"),sQuery(id+"F0.wireOp",EDGE,"E7.13.3"),sQuery(id+"F0.wireOp",EDGE,"E7.13.4"),sQuery(id+"F0.wireOp",EDGE,"E7.13.5"),subQ0,sQuery(id+"F0.wireOp",EDGE,"E7.14.1"),sQuery(id+"F0.wireOp",EDGE,"E7.14.2"),sQuery(id+"F0.wireOp",EDGE,"E7.14.3"),sQuery(id+"F0.wireOp",EDGE,"E7.14.4"),sQuery(id+"F0.wireOp",EDGE,"E7.14.5"),sQuery(id+"F0.wireOp",EDGE,"E7.15.0"),sQuery(id+"F0.wireOp",EDGE,"E7.15.1"),sQuery(id+"F0.wireOp",EDGE,"E7.15.2"),sQuery(id+"F0.wireOp",EDGE,"E7.15.3"),sQuery(id+"F0.wireOp",EDGE,"E7.15.4"),sQuery(id+"F0.wireOp",EDGE,"E7.15.5"),sQuery(id+"F0.wireOp",EDGE,"E7.16.0"),sQuery(id+"F0.wireOp",EDGE,"E7.16.1"),sQuery(id+"F0.wireOp",EDGE,"E7.16.2"),sQuery(id+"F0.wireOp",EDGE,"E7.16.3"),sQuery(id+"F0.wireOp",EDGE,"E7.16.4"),sQuery(id+"F0.wireOp",EDGE,"E7.16.5"),sQuery(id+"F0.wireOp",EDGE,"E7.17.0"),sQuery(id+"F0.wireOp",EDGE,"E7.17.1"),sQuery(id+"F0.wireOp",EDGE,"E7.17.2"),sQuery(id+"F0.wireOp",EDGE,"E7.17.3"),sQuery(id+"F0.wireOp",EDGE,"E7.17.4"),sQuery(id+"F0.wireOp",EDGE,"E7.17.5"),sQuery(id+"F0.wireOp",EDGE,"E7.18.0"),sQuery(id+"F0.wireOp",EDGE,"E7.18.1"),sQuery(id+"F0.wireOp",EDGE,"E7.18.2"),sQuery(id+"F0.wireOp",EDGE,"E7.18.3"),sQuery(id+"F0.wireOp",EDGE,"E7.18.4"),sQuery(id+"F0.wireOp",EDGE,"E7.18.5"),sQuery(id+"F0.wireOp",EDGE,"E7.19.0"),sQuery(id+"F0.wireOp",EDGE,"E7.19.1"),sQuery(id+"F0.wireOp",EDGE,"E7.19.2"),sQuery(id+"F0.wireOp",EDGE,"E7.19.3"),sQuery(id+"F0.wireOp",EDGE,"E7.19.4"),sQuery(id+"F0.wireOp",EDGE,"E7.19.5"),sQuery(id+"F0.wireOp",EDGE,"E7.20.0"),sQuery(id+"F0.wireOp",EDGE,"E7.20.1"),sQuery(id+"F0.wireOp",EDGE,"E7.20.2"),sQuery(id+"F0.wireOp",EDGE,"E7.20.3"),sQuery(id+"F0.wireOp",EDGE,"E7.20.4"),sQuery(id+"F0.wireOp",EDGE,"E7.20.5"),sQuery(id+"F0.wireOp",EDGE,"E7.21.0"),sQuery(id+"F0.wireOp",EDGE,"E7.21.1"),sQuery(id+"F0.wireOp",EDGE,"E7.21.2"),sQuery(id+"F0.wireOp",EDGE,"E7.21.3"),sQuery(id+"F0.wireOp",EDGE,"E7.21.4"),sQuery(id+"F0.wireOp",EDGE,"E7.21.5"),sQuery(id+"F0.wireOp",EDGE,"E7.22.0"),sQuery(id+"F0.wireOp",EDGE,"E7.22.1"),sQuery(id+"F0.wireOp",EDGE,"E7.22.2"),sQuery(id+"F0.wireOp",EDGE,"E7.22.3"),sQuery(id+"F0.wireOp",EDGE,"E7.22.4"),sQuery(id+"F0.wireOp",EDGE,"E7.22.5"),sQuery(id+"F0.wireOp",EDGE,"E7.23.0"),sQuery(id+"F0.wireOp",EDGE,"E7.23.1"),sQuery(id+"F0.wireOp",EDGE,"E7.23.2"),sQuery(id+"F0.wireOp",EDGE,"E7.23.3"),sQuery(id+"F0.wireOp",EDGE,"E7.23.4"),sQuery(id+"F0.wireOp",EDGE,"E7.23.5"),sQuery(id+"F0.wireOp",EDGE,"E7.24.0"),sQuery(id+"F0.wireOp",EDGE,"E7.24.1"),sQuery(id+"F0.wireOp",EDGE,"E7.24.2"),sQuery(id+"F0.wireOp",EDGE,"E7.24.3"),sQuery(id+"F0.wireOp",EDGE,"E7.24.4"),sQuery(id+"F0.wireOp",EDGE,"E7.24.5"),sQuery(id+"F0.wireOp",EDGE,"E7.25.0"),sQuery(id+"F0.wireOp",EDGE,"E7.25.1"),sQuery(id+"F0.wireOp",EDGE,"E7.25.2"),sQuery(id+"F0.wireOp",EDGE,"E7.25.3"),sQuery(id+"F0.wireOp",EDGE,"E7.25.4"),sQuery(id+"F0.wireOp",EDGE,"E7.25.5"),sQuery(id+"F0.wireOp",EDGE,"E7.26.0"),sQuery(id+"F0.wireOp",EDGE,"E7.26.1"),sQuery(id+"F0.wireOp",EDGE,"E7.26.2"),sQuery(id+"F0.wireOp",EDGE,"E7.26.3"),sQuery(id+"F0.wireOp",EDGE,"E7.26.4"),sQuery(id+"F0.wireOp",EDGE,"E7.26.5"),sQuery(id+"F0.wireOp",EDGE,"E7.27.0"),sQuery(id+"F0.wireOp",EDGE,"E7.27.1"),sQuery(id+"F0.wireOp",EDGE,"E7.27.2"),sQuery(id+"F0.wireOp",EDGE,"E7.27.3"),sQuery(id+"F0.wireOp",EDGE,"E7.27.4"),sQuery(id+"F0.wireOp",EDGE,"E7.27.5"),sQuery(id+"F0.wireOp",EDGE,"E7.28.0"),sQuery(id+"F0.wireOp",EDGE,"E7.28.1"),sQuery(id+"F0.wireOp",EDGE,"E7.28.2"),sQuery(id+"F0.wireOp",EDGE,"E7.28.3"),sQuery(id+"F0.wireOp",EDGE,"E7.28.4"),sQuery(id+"F0.wireOp",EDGE,"E7.28.5"),sQuery(id+"F0.wireOp",EDGE,"E7.29.0"),sQuery(id+"F0.wireOp",EDGE,"E7.29.1"),sQuery(id+"F0.wireOp",EDGE,"E7.29.2"),sQuery(id+"F0.wireOp",EDGE,"E7.29.3"),sQuery(id+"F0.wireOp",EDGE,"E7.29.4"),sQuery(id+"F0.wireOp",EDGE,"E7.29.5"),sQuery(id+"F0.wireOp",EDGE,"E7.30.0"),sQuery(id+"F0.wireOp",EDGE,"E7.30.1"),sQuery(id+"F0.wireOp",EDGE,"E7.30.2"),sQuery(id+"F0.wireOp",EDGE,"E7.30.3"),sQuery(id+"F0.wireOp",EDGE,"E7.30.4"),sQuery(id+"F0.wireOp",EDGE,"E7.30.5"),sQuery(id+"F0.wireOp",EDGE,"E7.31.0"),sQuery(id+"F0.wireOp",EDGE,"E7.31.1"),sQuery(id+"F0.wireOp",EDGE,"E7.31.2"),sQuery(id+"F0.wireOp",EDGE,"E7.31.3"),sQuery(id+"F0.wireOp",EDGE,"E7.31.4"),sQuery(id+"F0.wireOp",EDGE,"E7.31.5"),sQuery(id+"F0.wireOp",EDGE,"E7.32.0"),sQuery(id+"F0.wireOp",EDGE,"E7.32.1"),sQuery(id+"F0.wireOp",EDGE,"E7.32.2"),sQuery(id+"F0.wireOp",EDGE,"E7.32.3"),sQuery(id+"F0.wireOp",EDGE,"E7.32.4"),sQuery(id+"F0.wireOp",EDGE,"E7.32.5"),sQuery(id+"F0.wireOp",EDGE,"E7.33.0"),sQuery(id+"F0.wireOp",EDGE,"E7.33.1"),sQuery(id+"F0.wireOp",EDGE,"E7.33.2"),sQuery(id+"F0.wireOp",EDGE,"E7.33.3"),sQuery(id+"F0.wireOp",EDGE,"E7.33.4"),sQuery(id+"F0.wireOp",EDGE,"E7.33.5"),sQuery(id+"F0.wireOp",EDGE,"E7.34.0"),sQuery(id+"F0.wireOp",EDGE,"E7.34.1"),sQuery(id+"F0.wireOp",EDGE,"E7.34.2"),sQuery(id+"F0.wireOp",EDGE,"E7.34.3"),sQuery(id+"F0.wireOp",EDGE,"E7.34.4"),sQuery(id+"F0.wireOp",EDGE,"E7.34.5"),sQuery(id+"F0.wireOp",EDGE,"E7.35.0"),sQuery(id+"F0.wireOp",EDGE,"E7.35.1"),sQuery(id+"F0.wireOp",EDGE,"E7.35.2"),sQuery(id+"F0.wireOp",EDGE,"E7.35.3"),sQuery(id+"F0.wireOp",EDGE,"E7.35.4"),sQuery(id+"F0.wireOp",EDGE,"E7.35.5"),sQuery(id+"F0.wireOp",EDGE,"E7.36.0"),sQuery(id+"F0.wireOp",EDGE,"E7.36.1"),sQuery(id+"F0.wireOp",EDGE,"E7.36.2"),sQuery(id+"F0.wireOp",EDGE,"E7.36.3"),sQuery(id+"F0.wireOp",EDGE,"E7.36.4"),sQuery(id+"F0.wireOp",EDGE,"E7.36.5"),sQuery(id+"F0.wireOp",EDGE,"E7.37.0"),sQuery(id+"F0.wireOp",EDGE,"E7.37.1"),sQuery(id+"F0.wireOp",EDGE,"E7.37.2"),sQuery(id+"F0.wireOp",EDGE,"E7.37.3"),sQuery(id+"F0.wireOp",EDGE,"E7.37.4"),sQuery(id+"F0.wireOp",EDGE,"E7.37.5"),sQuery(id+"F0.wireOp",EDGE,"E7.38.0"),sQuery(id+"F0.wireOp",EDGE,"E7.38.1"),sQuery(id+"F0.wireOp",EDGE,"E7.38.2"),sQuery(id+"F0.wireOp",EDGE,"E7.38.3"),sQuery(id+"F0.wireOp",EDGE,"E7.38.4"),sQuery(id+"F0.wireOp",EDGE,"E7.38.5"),sQuery(id+"F0.wireOp",EDGE,"E7.39.0"),sQuery(id+"F0.wireOp",EDGE,"E7.39.1"),sQuery(id+"F0.wireOp",EDGE,"E7.39.2"),sQuery(id+"F0.wireOp",EDGE,"E7.39.3"),sQuery(id+"F0.wireOp",EDGE,"E7.39.4"),sQuery(id+"F0.wireOp",EDGE,"E7.39.5"),sQuery(id+"F0.wireOp",EDGE,"E7.40.0"),sQuery(id+"F0.wireOp",EDGE,"E7.40.1"),sQuery(id+"F0.wireOp",EDGE,"E7.40.2"),sQuery(id+"F0.wireOp",EDGE,"E7.40.3"),sQuery(id+"F0.wireOp",EDGE,"E7.40.4"),sQuery(id+"F0.wireOp",EDGE,"E7.40.5"),sQuery(id+"F0.wireOp",EDGE,"E7.41.0"),sQuery(id+"F0.wireOp",EDGE,"E7.41.1"),sQuery(id+"F0.wireOp",EDGE,"E7.41.2"),sQuery(id+"F0.wireOp",EDGE,"E7.41.3"),sQuery(id+"F0.wireOp",EDGE,"E7.41.4"),sQuery(id+"F0.wireOp",EDGE,"E7.41.5"),sQuery(id+"F0.wireOp",EDGE,"E7.42.0"),sQuery(id+"F0.wireOp",EDGE,"E7.42.1"),sQuery(id+"F0.wireOp",EDGE,"E7.42.2"),sQuery(id+"F0.wireOp",EDGE,"E7.42.3"),sQuery(id+"F0.wireOp",EDGE,"E7.42.4"),sQuery(id+"F0.wireOp",EDGE,"E7.42.5"),sQuery(id+"F0.wireOp",EDGE,"E7.43.0"),sQuery(id+"F0.wireOp",EDGE,"E7.43.1"),sQuery(id+"F0.wireOp",EDGE,"E7.43.2"),sQuery(id+"F0.wireOp",EDGE,"E7.43.3"),sQuery(id+"F0.wireOp",EDGE,"E7.43.4"),sQuery(id+"F0.wireOp",EDGE,"E7.43.5")])],"isStart":true})],"blendedInto":[makeQuery(id+"F1.opExtrude","CAP_FACE",FACE,{"disambiguationData":[OSD([sQuery(id+"F0.wireOp",EDGE,"E1"),sQuery(id+"F0.wireOp",EDGE,"E2"),sQuery(id+"F0.wireOp",EDGE,"E3"),sQuery(id+"F0.wireOp",EDGE,"E4"),sQuery(id+"F0.wireOp",EDGE,"E5"),sQuery(id+"F0.wireOp",EDGE,"E6"),sQuery(id+"F0.wireOp",EDGE,"E7.1.0"),sQuery(id+"F0.wireOp",EDGE,"E7.1.1"),sQuery(id+"F0.wireOp",EDGE,"E7.1.2"),sQuery(id+"F0.wireOp",EDGE,"E7.1.3"),sQuery(id+"F0.wireOp",EDGE,"E7.1.4"),sQuery(id+"F0.wireOp",EDGE,"E7.1.5"),sQuery(id+"F0.wireOp",EDGE,"E7.2.0"),sQuery(id+"F0.wireOp",EDGE,"E7.2.1"),sQuery(id+"F0.wireOp",EDGE,"E7.2.2"),sQuery(id+"F0.wireOp",EDGE,"E7.2.3"),sQuery(id+"F0.wireOp",EDGE,"E7.2.4"),sQuery(id+"F0.wireOp",EDGE,"E7.2.5"),sQuery(id+"F0.wireOp",EDGE,"E7.3.0"),sQuery(id+"F0.wireOp",EDGE,"E7.3.1"),sQuery(id+"F0.wireOp",EDGE,"E7.3.2"),sQuery(id+"F0.wireOp",EDGE,"E7.3.3"),sQuery(id+"F0.wireOp",EDGE,"E7.3.4"),sQuery(id+"F0.wireOp",EDGE,"E7.3.5"),sQuery(id+"F0.wireOp",EDGE,"E7.4.0"),sQuery(id+"F0.wireOp",EDGE,"E7.4.1"),sQuery(id+"F0.wireOp",EDGE,"E7.4.2"),sQuery(id+"F0.wireOp",EDGE,"E7.4.3"),sQuery(id+"F0.wireOp",EDGE,"E7.4.4"),sQuery(id+"F0.wireOp",EDGE,"E7.4.5"),sQuery(id+"F0.wireOp",EDGE,"E7.5.0"),sQuery(id+"F0.wireOp",EDGE,"E7.5.1"),sQuery(id+"F0.wireOp",EDGE,"E7.5.2"),sQuery(id+"F0.wireOp",EDGE,"E7.5.3"),sQuery(id+"F0.wireOp",EDGE,"E7.5.4"),sQuery(id+"F0.wireOp",EDGE,"E7.5.5"),sQuery(id+"F0.wireOp",EDGE,"E7.6.0"),sQuery(id+"F0.wireOp",EDGE,"E7.6.1"),sQuery(id+"F0.wireOp",EDGE,"E7.6.2"),sQuery(id+"F0.wireOp",EDGE,"E7.6.3"),sQuery(id+"F0.wireOp",EDGE,"E7.6.4"),sQuery(id+"F0.wireOp",EDGE,"E7.6.5"),sQuery(id+"F0.wireOp",EDGE,"E7.7.0"),sQuery(id+"F0.wireOp",EDGE,"E7.7.1"),sQuery(id+"F0.wireOp",EDGE,"E7.7.2"),sQuery(id+"F0.wireOp",EDGE,"E7.7.3"),sQuery(id+"F0.wireOp",EDGE,"E7.7.4"),sQuery(id+"F0.wireOp",EDGE,"E7.7.5"),sQuery(id+"F0.wireOp",EDGE,"E7.8.0"),sQuery(id+"F0.wireOp",EDGE,"E7.8.1"),sQuery(id+"F0.wireOp",EDGE,"E7.8.2"),sQuery(id+"F0.wireOp",EDGE,"E7.8.3"),sQuery(id+"F0.wireOp",EDGE,"E7.8.4"),sQuery(id+"F0.wireOp",EDGE,"E7.8.5"),sQuery(id+"F0.wireOp",EDGE,"E7.9.0"),sQuery(id+"F0.wireOp",EDGE,"E7.9.1"),sQuery(id+"F0.wireOp",EDGE,"E7.9.2"),sQuery(id+"F0.wireOp",EDGE,"E7.9.3"),sQuery(id+"F0.wireOp",EDGE,"E7.9.4"),sQuery(id+"F0.wireOp",EDGE,"E7.9.5"),sQuery(id+"F0.wireOp",EDGE,"E7.10.0"),sQuery(id+"F0.wireOp",EDGE,"E7.10.1"),sQuery(id+"F0.wireOp",EDGE,"E7.10.2"),sQuery(id+"F0.wireOp",EDGE,"E7.10.3"),sQuery(id+"F0.wireOp",EDGE,"E7.10.4"),sQuery(id+"F0.wireOp",EDGE,"E7.10.5"),sQuery(id+"F0.wireOp",EDGE,"E7.11.0"),sQuery(id+"F0.wireOp",EDGE,"E7.11.1"),sQuery(id+"F0.wireOp",EDGE,"E7.11.2"),sQuery(id+"F0.wireOp",EDGE,"E7.11.3"),sQuery(id+"F0.wireOp",EDGE,"E7.11.4"),sQuery(id+"F0.wireOp",EDGE,"E7.11.5"),sQuery(id+"F0.wireOp",EDGE,"E7.12.0"),sQuery(id+"F0.wireOp",EDGE,"E7.12.1"),sQuery(id+"F0.wireOp",EDGE,"E7.12.2"),sQuery(id+"F0.wireOp",EDGE,"E7.12.3"),sQuery(id+"F0.wireOp",EDGE,"E7.12.4"),sQuery(id+"F0.wireOp",EDGE,"E7.12.5"),sQuery(id+"F0.wireOp",EDGE,"E7.13.0"),sQuery(id+"F0.wireOp",EDGE,"E7.13.1"),sQuery(id+"F0.wireOp",EDGE,"E7.13.2"),sQuery(id+"F0.wireOp",EDGE,"E7.13.3"),sQuery(id+"F0.wireOp",EDGE,"E7.13.4"),sQuery(id+"F0.wireOp",EDGE,"E7.13.5"),subQ0,sQuery(id+"F0.wireOp",EDGE,"E7.14.1"),sQuery(id+"F0.wireOp",EDGE,"E7.14.2"),sQuery(id+"F0.wireOp",EDGE,"E7.14.3"),sQuery(id+"F0.wireOp",EDGE,"E7.14.4"),sQuery(id+"F0.wireOp",EDGE,"E7.14.5"),sQuery(id+"F0.wireOp",EDGE,"E7.15.0"),sQuery(id+"F0.wireOp",EDGE,"E7.15.1"),sQuery(id+"F0.wireOp",EDGE,"E7.15.2"),sQuery(id+"F0.wireOp",EDGE,"E7.15.3"),sQuery(id+"F0.wireOp",EDGE,"E7.15.4"),sQuery(id+"F0.wireOp",EDGE,"E7.15.5"),sQuery(id+"F0.wireOp",EDGE,"E7.16.0"),sQuery(id+"F0.wireOp",EDGE,"E7.16.1"),sQuery(id+"F0.wireOp",EDGE,"E7.16.2"),sQuery(id+"F0.wireOp",EDGE,"E7.16.3"),sQuery(id+"F0.wireOp",EDGE,"E7.16.4"),sQuery(id+"F0.wireOp",EDGE,"E7.16.5"),sQuery(id+"F0.wireOp",EDGE,"E7.17.0"),sQuery(id+"F0.wireOp",EDGE,"E7.17.1"),sQuery(id+"F0.wireOp",EDGE,"E7.17.2"),sQuery(id+"F0.wireOp",EDGE,"E7.17.3"),sQuery(id+"F0.wireOp",EDGE,"E7.17.4"),sQuery(id+"F0.wireOp",EDGE,"E7.17.5"),sQuery(id+"F0.wireOp",EDGE,"E7.18.0"),sQuery(id+"F0.wireOp",EDGE,"E7.18.1"),sQuery(id+"F0.wireOp",EDGE,"E7.18.2"),sQuery(id+"F0.wireOp",EDGE,"E7.18.3"),sQuery(id+"F0.wireOp",EDGE,"E7.18.4"),sQuery(id+"F0.wireOp",EDGE,"E7.18.5"),sQuery(id+"F0.wireOp",EDGE,"E7.19.0"),sQuery(id+"F0.wireOp",EDGE,"E7.19.1"),sQuery(id+"F0.wireOp",EDGE,"E7.19.2"),sQuery(id+"F0.wireOp",EDGE,"E7.19.3"),sQuery(id+"F0.wireOp",EDGE,"E7.19.4"),sQuery(id+"F0.wireOp",EDGE,"E7.19.5"),sQuery(id+"F0.wireOp",EDGE,"E7.20.0"),sQuery(id+"F0.wireOp",EDGE,"E7.20.1"),sQuery(id+"F0.wireOp",EDGE,"E7.20.2"),sQuery(id+"F0.wireOp",EDGE,"E7.20.3"),sQuery(id+"F0.wireOp",EDGE,"E7.20.4"),sQuery(id+"F0.wireOp",EDGE,"E7.20.5"),sQuery(id+"F0.wireOp",EDGE,"E7.21.0"),sQuery(id+"F0.wireOp",EDGE,"E7.21.1"),sQuery(id+"F0.wireOp",EDGE,"E7.21.2"),sQuery(id+"F0.wireOp",EDGE,"E7.21.3"),sQuery(id+"F0.wireOp",EDGE,"E7.21.4"),sQuery(id+"F0.wireOp",EDGE,"E7.21.5"),sQuery(id+"F0.wireOp",EDGE,"E7.22.0"),sQuery(id+"F0.wireOp",EDGE,"E7.22.1"),sQuery(id+"F0.wireOp",EDGE,"E7.22.2"),sQuery(id+"F0.wireOp",EDGE,"E7.22.3"),sQuery(id+"F0.wireOp",EDGE,"E7.22.4"),sQuery(id+"F0.wireOp",EDGE,"E7.22.5"),sQuery(id+"F0.wireOp",EDGE,"E7.23.0"),sQuery(id+"F0.wireOp",EDGE,"E7.23.1"),sQuery(id+"F0.wireOp",EDGE,"E7.23.2"),sQuery(id+"F0.wireOp",EDGE,"E7.23.3"),sQuery(id+"F0.wireOp",EDGE,"E7.23.4"),sQuery(id+"F0.wireOp",EDGE,"E7.23.5"),sQuery(id+"F0.wireOp",EDGE,"E7.24.0"),sQuery(id+"F0.wireOp",EDGE,"E7.24.1"),sQuery(id+"F0.wireOp",EDGE,"E7.24.2"),sQuery(id+"F0.wireOp",EDGE,"E7.24.3"),sQuery(id+"F0.wireOp",EDGE,"E7.24.4"),sQuery(id+"F0.wireOp",EDGE,"E7.24.5"),sQuery(id+"F0.wireOp",EDGE,"E7.25.0"),sQuery(id+"F0.wireOp",EDGE,"E7.25.1"),sQuery(id+"F0.wireOp",EDGE,"E7.25.2"),sQuery(id+"F0.wireOp",EDGE,"E7.25.3"),sQuery(id+"F0.wireOp",EDGE,"E7.25.4"),sQuery(id+"F0.wireOp",EDGE,"E7.25.5"),sQuery(id+"F0.wireOp",EDGE,"E7.26.0"),sQuery(id+"F0.wireOp",EDGE,"E7.26.1"),sQuery(id+"F0.wireOp",EDGE,"E7.26.2"),sQuery(id+"F0.wireOp",EDGE,"E7.26.3"),sQuery(id+"F0.wireOp",EDGE,"E7.26.4"),sQuery(id+"F0.wireOp",EDGE,"E7.26.5"),sQuery(id+"F0.wireOp",EDGE,"E7.27.0"),sQuery(id+"F0.wireOp",EDGE,"E7.27.1"),sQuery(id+"F0.wireOp",EDGE,"E7.27.2"),sQuery(id+"F0.wireOp",EDGE,"E7.27.3"),sQuery(id+"F0.wireOp",EDGE,"E7.27.4"),sQuery(id+"F0.wireOp",EDGE,"E7.27.5"),sQuery(id+"F0.wireOp",EDGE,"E7.28.0"),sQuery(id+"F0.wireOp",EDGE,"E7.28.1"),sQuery(id+"F0.wireOp",EDGE,"E7.28.2"),sQuery(id+"F0.wireOp",EDGE,"E7.28.3"),sQuery(id+"F0.wireOp",EDGE,"E7.28.4"),sQuery(id+"F0.wireOp",EDGE,"E7.28.5"),sQuery(id+"F0.wireOp",EDGE,"E7.29.0"),sQuery(id+"F0.wireOp",EDGE,"E7.29.1"),sQuery(id+"F0.wireOp",EDGE,"E7.29.2"),sQuery(id+"F0.wireOp",EDGE,"E7.29.3"),sQuery(id+"F0.wireOp",EDGE,"E7.29.4"),sQuery(id+"F0.wireOp",EDGE,"E7.29.5"),sQuery(id+"F0.wireOp",EDGE,"E7.30.0"),sQuery(id+"F0.wireOp",EDGE,"E7.30.1"),sQuery(id+"F0.wireOp",EDGE,"E7.30.2"),sQuery(id+"F0.wireOp",EDGE,"E7.30.3"),sQuery(id+"F0.wireOp",EDGE,"E7.30.4"),sQuery(id+"F0.wireOp",EDGE,"E7.30.5"),sQuery(id+"F0.wireOp",EDGE,"E7.31.0"),sQuery(id+"F0.wireOp",EDGE,"E7.31.1"),sQuery(id+"F0.wireOp",EDGE,"E7.31.2"),sQuery(id+"F0.wireOp",EDGE,"E7.31.3"),sQuery(id+"F0.wireOp",EDGE,"E7.31.4"),sQuery(id+"F0.wireOp",EDGE,"E7.31.5"),sQuery(id+"F0.wireOp",EDGE,"E7.32.0"),sQuery(id+"F0.wireOp",EDGE,"E7.32.1"),sQuery(id+"F0.wireOp",EDGE,"E7.32.2"),sQuery(id+"F0.wireOp",EDGE,"E7.32.3"),sQuery(id+"F0.wireOp",EDGE,"E7.32.4"),sQuery(id+"F0.wireOp",EDGE,"E7.32.5"),sQuery(id+"F0.wireOp",EDGE,"E7.33.0"),sQuery(id+"F0.wireOp",EDGE,"E7.33.1"),sQuery(id+"F0.wireOp",EDGE,"E7.33.2"),sQuery(id+"F0.wireOp",EDGE,"E7.33.3"),sQuery(id+"F0.wireOp",EDGE,"E7.33.4"),sQuery(id+"F0.wireOp",EDGE,"E7.33.5"),sQuery(id+"F0.wireOp",EDGE,"E7.34.0"),sQuery(id+"F0.wireOp",EDGE,"E7.34.1"),sQuery(id+"F0.wireOp",EDGE,"E7.34.2"),sQuery(id+"F0.wireOp",EDGE,"E7.34.3"),sQuery(id+"F0.wireOp",EDGE,"E7.34.4"),sQuery(id+"F0.wireOp",EDGE,"E7.34.5"),sQuery(id+"F0.wireOp",EDGE,"E7.35.0"),sQuery(id+"F0.wireOp",EDGE,"E7.35.1"),sQuery(id+"F0.wireOp",EDGE,"E7.35.2"),sQuery(id+"F0.wireOp",EDGE,"E7.35.3"),sQuery(id+"F0.wireOp",EDGE,"E7.35.4"),sQuery(id+"F0.wireOp",EDGE,"E7.35.5"),sQuery(id+"F0.wireOp",EDGE,"E7.36.0"),sQuery(id+"F0.wireOp",EDGE,"E7.36.1"),sQuery(id+"F0.wireOp",EDGE,"E7.36.2"),sQuery(id+"F0.wireOp",EDGE,"E7.36.3"),sQuery(id+"F0.wireOp",EDGE,"E7.36.4"),sQuery(id+"F0.wireOp",EDGE,"E7.36.5"),sQuery(id+"F0.wireOp",EDGE,"E7.37.0"),sQuery(id+"F0.wireOp",EDGE,"E7.37.1"),sQuery(id+"F0.wireOp",EDGE,"E7.37.2"),sQuery(id+"F0.wireOp",EDGE,"E7.37.3"),sQuery(id+"F0.wireOp",EDGE,"E7.37.4"),sQuery(id+"F0.wireOp",EDGE,"E7.37.5"),sQuery(id+"F0.wireOp",EDGE,"E7.38.0"),sQuery(id+"F0.wireOp",EDGE,"E7.38.1"),sQuery(id+"F0.wireOp",EDGE,"E7.38.2"),sQuery(id+"F0.wireOp",EDGE,"E7.38.3"),sQuery(id+"F0.wireOp",EDGE,"E7.38.4"),sQuery(id+"F0.wireOp",EDGE,"E7.38.5"),sQuery(id+"F0.wireOp",EDGE,"E7.39.0"),sQuery(id+"F0.wireOp",EDGE,"E7.39.1"),sQuery(id+"F0.wireOp",EDGE,"E7.39.2"),sQuery(id+"F0.wireOp",EDGE,"E7.39.3"),sQuery(id+"F0.wireOp",EDGE,"E7.39.4"),sQuery(id+"F0.wireOp",EDGE,"E7.39.5"),sQuery(id+"F0.wireOp",EDGE,"E7.40.0"),sQuery(id+"F0.wireOp",EDGE,"E7.40.1"),sQuery(id+"F0.wireOp",EDGE,"E7.40.2"),sQuery(id+"F0.wireOp",EDGE,"E7.40.3"),sQuery(id+"F0.wireOp",EDGE,"E7.40.4"),sQuery(id+"F0.wireOp",EDGE,"E7.40.5"),sQuery(id+"F0.wireOp",EDGE,"E7.41.0"),sQuery(id+"F0.wireOp",EDGE,"E7.41.1"),sQuery(id+"F0.wireOp",EDGE,"E7.41.2"),sQuery(id+"F0.wireOp",EDGE,"E7.41.3"),sQuery(id+"F0.wireOp",EDGE,"E7.41.4"),sQuery(id+"F0.wireOp",EDGE,"E7.41.5"),sQuery(id+"F0.wireOp",EDGE,"E7.42.0"),sQuery(id+"F0.wireOp",EDGE,"E7.42.1"),sQuery(id+"F0.wireOp",EDGE,"E7.42.2"),sQuery(id+"F0.wireOp",EDGE,"E7.42.3"),sQuery(id+"F0.wireOp",EDGE,"E7.42.4"),sQuery(id+"F0.wireOp",EDGE,"E7.42.5"),sQuery(id+"F0.wireOp",EDGE,"E7.43.0"),sQuery(id+"F0.wireOp",EDGE,"E7.43.1"),sQuery(id+"F0.wireOp",EDGE,"E7.43.2"),sQuery(id+"F0.wireOp",EDGE,"E7.43.3"),sQuery(id+"F0.wireOp",EDGE,"E7.43.4"),sQuery(id+"F0.wireOp",EDGE,"E7.43.5")])],"isStart":true})]});}
            var Q29;
            {var subQ0=sQuery(id+"F0.wireOp",EDGE,"E7.16.0");Q29=makeQuery(id+"F2.opChamfer","BLEND_EDGE",EDGE,{"blendedFrom":[makeQuery(id+"F1.opExtrude","CAP_EDGE",EDGE,{"disambiguationData":[OSD([subQ0])],"isStart":true}),makeQuery(id+"F1.opExtrude","CAP_FACE",FACE,{"disambiguationData":[OSD([sQuery(id+"F0.wireOp",EDGE,"E1"),sQuery(id+"F0.wireOp",EDGE,"E2"),sQuery(id+"F0.wireOp",EDGE,"E3"),sQuery(id+"F0.wireOp",EDGE,"E4"),sQuery(id+"F0.wireOp",EDGE,"E5"),sQuery(id+"F0.wireOp",EDGE,"E6"),sQuery(id+"F0.wireOp",EDGE,"E7.1.0"),sQuery(id+"F0.wireOp",EDGE,"E7.1.1"),sQuery(id+"F0.wireOp",EDGE,"E7.1.2"),sQuery(id+"F0.wireOp",EDGE,"E7.1.3"),sQuery(id+"F0.wireOp",EDGE,"E7.1.4"),sQuery(id+"F0.wireOp",EDGE,"E7.1.5"),sQuery(id+"F0.wireOp",EDGE,"E7.2.0"),sQuery(id+"F0.wireOp",EDGE,"E7.2.1"),sQuery(id+"F0.wireOp",EDGE,"E7.2.2"),sQuery(id+"F0.wireOp",EDGE,"E7.2.3"),sQuery(id+"F0.wireOp",EDGE,"E7.2.4"),sQuery(id+"F0.wireOp",EDGE,"E7.2.5"),sQuery(id+"F0.wireOp",EDGE,"E7.3.0"),sQuery(id+"F0.wireOp",EDGE,"E7.3.1"),sQuery(id+"F0.wireOp",EDGE,"E7.3.2"),sQuery(id+"F0.wireOp",EDGE,"E7.3.3"),sQuery(id+"F0.wireOp",EDGE,"E7.3.4"),sQuery(id+"F0.wireOp",EDGE,"E7.3.5"),sQuery(id+"F0.wireOp",EDGE,"E7.4.0"),sQuery(id+"F0.wireOp",EDGE,"E7.4.1"),sQuery(id+"F0.wireOp",EDGE,"E7.4.2"),sQuery(id+"F0.wireOp",EDGE,"E7.4.3"),sQuery(id+"F0.wireOp",EDGE,"E7.4.4"),sQuery(id+"F0.wireOp",EDGE,"E7.4.5"),sQuery(id+"F0.wireOp",EDGE,"E7.5.0"),sQuery(id+"F0.wireOp",EDGE,"E7.5.1"),sQuery(id+"F0.wireOp",EDGE,"E7.5.2"),sQuery(id+"F0.wireOp",EDGE,"E7.5.3"),sQuery(id+"F0.wireOp",EDGE,"E7.5.4"),sQuery(id+"F0.wireOp",EDGE,"E7.5.5"),sQuery(id+"F0.wireOp",EDGE,"E7.6.0"),sQuery(id+"F0.wireOp",EDGE,"E7.6.1"),sQuery(id+"F0.wireOp",EDGE,"E7.6.2"),sQuery(id+"F0.wireOp",EDGE,"E7.6.3"),sQuery(id+"F0.wireOp",EDGE,"E7.6.4"),sQuery(id+"F0.wireOp",EDGE,"E7.6.5"),sQuery(id+"F0.wireOp",EDGE,"E7.7.0"),sQuery(id+"F0.wireOp",EDGE,"E7.7.1"),sQuery(id+"F0.wireOp",EDGE,"E7.7.2"),sQuery(id+"F0.wireOp",EDGE,"E7.7.3"),sQuery(id+"F0.wireOp",EDGE,"E7.7.4"),sQuery(id+"F0.wireOp",EDGE,"E7.7.5"),sQuery(id+"F0.wireOp",EDGE,"E7.8.0"),sQuery(id+"F0.wireOp",EDGE,"E7.8.1"),sQuery(id+"F0.wireOp",EDGE,"E7.8.2"),sQuery(id+"F0.wireOp",EDGE,"E7.8.3"),sQuery(id+"F0.wireOp",EDGE,"E7.8.4"),sQuery(id+"F0.wireOp",EDGE,"E7.8.5"),sQuery(id+"F0.wireOp",EDGE,"E7.9.0"),sQuery(id+"F0.wireOp",EDGE,"E7.9.1"),sQuery(id+"F0.wireOp",EDGE,"E7.9.2"),sQuery(id+"F0.wireOp",EDGE,"E7.9.3"),sQuery(id+"F0.wireOp",EDGE,"E7.9.4"),sQuery(id+"F0.wireOp",EDGE,"E7.9.5"),sQuery(id+"F0.wireOp",EDGE,"E7.10.0"),sQuery(id+"F0.wireOp",EDGE,"E7.10.1"),sQuery(id+"F0.wireOp",EDGE,"E7.10.2"),sQuery(id+"F0.wireOp",EDGE,"E7.10.3"),sQuery(id+"F0.wireOp",EDGE,"E7.10.4"),sQuery(id+"F0.wireOp",EDGE,"E7.10.5"),sQuery(id+"F0.wireOp",EDGE,"E7.11.0"),sQuery(id+"F0.wireOp",EDGE,"E7.11.1"),sQuery(id+"F0.wireOp",EDGE,"E7.11.2"),sQuery(id+"F0.wireOp",EDGE,"E7.11.3"),sQuery(id+"F0.wireOp",EDGE,"E7.11.4"),sQuery(id+"F0.wireOp",EDGE,"E7.11.5"),sQuery(id+"F0.wireOp",EDGE,"E7.12.0"),sQuery(id+"F0.wireOp",EDGE,"E7.12.1"),sQuery(id+"F0.wireOp",EDGE,"E7.12.2"),sQuery(id+"F0.wireOp",EDGE,"E7.12.3"),sQuery(id+"F0.wireOp",EDGE,"E7.12.4"),sQuery(id+"F0.wireOp",EDGE,"E7.12.5"),sQuery(id+"F0.wireOp",EDGE,"E7.13.0"),sQuery(id+"F0.wireOp",EDGE,"E7.13.1"),sQuery(id+"F0.wireOp",EDGE,"E7.13.2"),sQuery(id+"F0.wireOp",EDGE,"E7.13.3"),sQuery(id+"F0.wireOp",EDGE,"E7.13.4"),sQuery(id+"F0.wireOp",EDGE,"E7.13.5"),sQuery(id+"F0.wireOp",EDGE,"E7.14.0"),sQuery(id+"F0.wireOp",EDGE,"E7.14.1"),sQuery(id+"F0.wireOp",EDGE,"E7.14.2"),sQuery(id+"F0.wireOp",EDGE,"E7.14.3"),sQuery(id+"F0.wireOp",EDGE,"E7.14.4"),sQuery(id+"F0.wireOp",EDGE,"E7.14.5"),sQuery(id+"F0.wireOp",EDGE,"E7.15.0"),sQuery(id+"F0.wireOp",EDGE,"E7.15.1"),sQuery(id+"F0.wireOp",EDGE,"E7.15.2"),sQuery(id+"F0.wireOp",EDGE,"E7.15.3"),sQuery(id+"F0.wireOp",EDGE,"E7.15.4"),sQuery(id+"F0.wireOp",EDGE,"E7.15.5"),subQ0,sQuery(id+"F0.wireOp",EDGE,"E7.16.1"),sQuery(id+"F0.wireOp",EDGE,"E7.16.2"),sQuery(id+"F0.wireOp",EDGE,"E7.16.3"),sQuery(id+"F0.wireOp",EDGE,"E7.16.4"),sQuery(id+"F0.wireOp",EDGE,"E7.16.5"),sQuery(id+"F0.wireOp",EDGE,"E7.17.0"),sQuery(id+"F0.wireOp",EDGE,"E7.17.1"),sQuery(id+"F0.wireOp",EDGE,"E7.17.2"),sQuery(id+"F0.wireOp",EDGE,"E7.17.3"),sQuery(id+"F0.wireOp",EDGE,"E7.17.4"),sQuery(id+"F0.wireOp",EDGE,"E7.17.5"),sQuery(id+"F0.wireOp",EDGE,"E7.18.0"),sQuery(id+"F0.wireOp",EDGE,"E7.18.1"),sQuery(id+"F0.wireOp",EDGE,"E7.18.2"),sQuery(id+"F0.wireOp",EDGE,"E7.18.3"),sQuery(id+"F0.wireOp",EDGE,"E7.18.4"),sQuery(id+"F0.wireOp",EDGE,"E7.18.5"),sQuery(id+"F0.wireOp",EDGE,"E7.19.0"),sQuery(id+"F0.wireOp",EDGE,"E7.19.1"),sQuery(id+"F0.wireOp",EDGE,"E7.19.2"),sQuery(id+"F0.wireOp",EDGE,"E7.19.3"),sQuery(id+"F0.wireOp",EDGE,"E7.19.4"),sQuery(id+"F0.wireOp",EDGE,"E7.19.5"),sQuery(id+"F0.wireOp",EDGE,"E7.20.0"),sQuery(id+"F0.wireOp",EDGE,"E7.20.1"),sQuery(id+"F0.wireOp",EDGE,"E7.20.2"),sQuery(id+"F0.wireOp",EDGE,"E7.20.3"),sQuery(id+"F0.wireOp",EDGE,"E7.20.4"),sQuery(id+"F0.wireOp",EDGE,"E7.20.5"),sQuery(id+"F0.wireOp",EDGE,"E7.21.0"),sQuery(id+"F0.wireOp",EDGE,"E7.21.1"),sQuery(id+"F0.wireOp",EDGE,"E7.21.2"),sQuery(id+"F0.wireOp",EDGE,"E7.21.3"),sQuery(id+"F0.wireOp",EDGE,"E7.21.4"),sQuery(id+"F0.wireOp",EDGE,"E7.21.5"),sQuery(id+"F0.wireOp",EDGE,"E7.22.0"),sQuery(id+"F0.wireOp",EDGE,"E7.22.1"),sQuery(id+"F0.wireOp",EDGE,"E7.22.2"),sQuery(id+"F0.wireOp",EDGE,"E7.22.3"),sQuery(id+"F0.wireOp",EDGE,"E7.22.4"),sQuery(id+"F0.wireOp",EDGE,"E7.22.5"),sQuery(id+"F0.wireOp",EDGE,"E7.23.0"),sQuery(id+"F0.wireOp",EDGE,"E7.23.1"),sQuery(id+"F0.wireOp",EDGE,"E7.23.2"),sQuery(id+"F0.wireOp",EDGE,"E7.23.3"),sQuery(id+"F0.wireOp",EDGE,"E7.23.4"),sQuery(id+"F0.wireOp",EDGE,"E7.23.5"),sQuery(id+"F0.wireOp",EDGE,"E7.24.0"),sQuery(id+"F0.wireOp",EDGE,"E7.24.1"),sQuery(id+"F0.wireOp",EDGE,"E7.24.2"),sQuery(id+"F0.wireOp",EDGE,"E7.24.3"),sQuery(id+"F0.wireOp",EDGE,"E7.24.4"),sQuery(id+"F0.wireOp",EDGE,"E7.24.5"),sQuery(id+"F0.wireOp",EDGE,"E7.25.0"),sQuery(id+"F0.wireOp",EDGE,"E7.25.1"),sQuery(id+"F0.wireOp",EDGE,"E7.25.2"),sQuery(id+"F0.wireOp",EDGE,"E7.25.3"),sQuery(id+"F0.wireOp",EDGE,"E7.25.4"),sQuery(id+"F0.wireOp",EDGE,"E7.25.5"),sQuery(id+"F0.wireOp",EDGE,"E7.26.0"),sQuery(id+"F0.wireOp",EDGE,"E7.26.1"),sQuery(id+"F0.wireOp",EDGE,"E7.26.2"),sQuery(id+"F0.wireOp",EDGE,"E7.26.3"),sQuery(id+"F0.wireOp",EDGE,"E7.26.4"),sQuery(id+"F0.wireOp",EDGE,"E7.26.5"),sQuery(id+"F0.wireOp",EDGE,"E7.27.0"),sQuery(id+"F0.wireOp",EDGE,"E7.27.1"),sQuery(id+"F0.wireOp",EDGE,"E7.27.2"),sQuery(id+"F0.wireOp",EDGE,"E7.27.3"),sQuery(id+"F0.wireOp",EDGE,"E7.27.4"),sQuery(id+"F0.wireOp",EDGE,"E7.27.5"),sQuery(id+"F0.wireOp",EDGE,"E7.28.0"),sQuery(id+"F0.wireOp",EDGE,"E7.28.1"),sQuery(id+"F0.wireOp",EDGE,"E7.28.2"),sQuery(id+"F0.wireOp",EDGE,"E7.28.3"),sQuery(id+"F0.wireOp",EDGE,"E7.28.4"),sQuery(id+"F0.wireOp",EDGE,"E7.28.5"),sQuery(id+"F0.wireOp",EDGE,"E7.29.0"),sQuery(id+"F0.wireOp",EDGE,"E7.29.1"),sQuery(id+"F0.wireOp",EDGE,"E7.29.2"),sQuery(id+"F0.wireOp",EDGE,"E7.29.3"),sQuery(id+"F0.wireOp",EDGE,"E7.29.4"),sQuery(id+"F0.wireOp",EDGE,"E7.29.5"),sQuery(id+"F0.wireOp",EDGE,"E7.30.0"),sQuery(id+"F0.wireOp",EDGE,"E7.30.1"),sQuery(id+"F0.wireOp",EDGE,"E7.30.2"),sQuery(id+"F0.wireOp",EDGE,"E7.30.3"),sQuery(id+"F0.wireOp",EDGE,"E7.30.4"),sQuery(id+"F0.wireOp",EDGE,"E7.30.5"),sQuery(id+"F0.wireOp",EDGE,"E7.31.0"),sQuery(id+"F0.wireOp",EDGE,"E7.31.1"),sQuery(id+"F0.wireOp",EDGE,"E7.31.2"),sQuery(id+"F0.wireOp",EDGE,"E7.31.3"),sQuery(id+"F0.wireOp",EDGE,"E7.31.4"),sQuery(id+"F0.wireOp",EDGE,"E7.31.5"),sQuery(id+"F0.wireOp",EDGE,"E7.32.0"),sQuery(id+"F0.wireOp",EDGE,"E7.32.1"),sQuery(id+"F0.wireOp",EDGE,"E7.32.2"),sQuery(id+"F0.wireOp",EDGE,"E7.32.3"),sQuery(id+"F0.wireOp",EDGE,"E7.32.4"),sQuery(id+"F0.wireOp",EDGE,"E7.32.5"),sQuery(id+"F0.wireOp",EDGE,"E7.33.0"),sQuery(id+"F0.wireOp",EDGE,"E7.33.1"),sQuery(id+"F0.wireOp",EDGE,"E7.33.2"),sQuery(id+"F0.wireOp",EDGE,"E7.33.3"),sQuery(id+"F0.wireOp",EDGE,"E7.33.4"),sQuery(id+"F0.wireOp",EDGE,"E7.33.5"),sQuery(id+"F0.wireOp",EDGE,"E7.34.0"),sQuery(id+"F0.wireOp",EDGE,"E7.34.1"),sQuery(id+"F0.wireOp",EDGE,"E7.34.2"),sQuery(id+"F0.wireOp",EDGE,"E7.34.3"),sQuery(id+"F0.wireOp",EDGE,"E7.34.4"),sQuery(id+"F0.wireOp",EDGE,"E7.34.5"),sQuery(id+"F0.wireOp",EDGE,"E7.35.0"),sQuery(id+"F0.wireOp",EDGE,"E7.35.1"),sQuery(id+"F0.wireOp",EDGE,"E7.35.2"),sQuery(id+"F0.wireOp",EDGE,"E7.35.3"),sQuery(id+"F0.wireOp",EDGE,"E7.35.4"),sQuery(id+"F0.wireOp",EDGE,"E7.35.5"),sQuery(id+"F0.wireOp",EDGE,"E7.36.0"),sQuery(id+"F0.wireOp",EDGE,"E7.36.1"),sQuery(id+"F0.wireOp",EDGE,"E7.36.2"),sQuery(id+"F0.wireOp",EDGE,"E7.36.3"),sQuery(id+"F0.wireOp",EDGE,"E7.36.4"),sQuery(id+"F0.wireOp",EDGE,"E7.36.5"),sQuery(id+"F0.wireOp",EDGE,"E7.37.0"),sQuery(id+"F0.wireOp",EDGE,"E7.37.1"),sQuery(id+"F0.wireOp",EDGE,"E7.37.2"),sQuery(id+"F0.wireOp",EDGE,"E7.37.3"),sQuery(id+"F0.wireOp",EDGE,"E7.37.4"),sQuery(id+"F0.wireOp",EDGE,"E7.37.5"),sQuery(id+"F0.wireOp",EDGE,"E7.38.0"),sQuery(id+"F0.wireOp",EDGE,"E7.38.1"),sQuery(id+"F0.wireOp",EDGE,"E7.38.2"),sQuery(id+"F0.wireOp",EDGE,"E7.38.3"),sQuery(id+"F0.wireOp",EDGE,"E7.38.4"),sQuery(id+"F0.wireOp",EDGE,"E7.38.5"),sQuery(id+"F0.wireOp",EDGE,"E7.39.0"),sQuery(id+"F0.wireOp",EDGE,"E7.39.1"),sQuery(id+"F0.wireOp",EDGE,"E7.39.2"),sQuery(id+"F0.wireOp",EDGE,"E7.39.3"),sQuery(id+"F0.wireOp",EDGE,"E7.39.4"),sQuery(id+"F0.wireOp",EDGE,"E7.39.5"),sQuery(id+"F0.wireOp",EDGE,"E7.40.0"),sQuery(id+"F0.wireOp",EDGE,"E7.40.1"),sQuery(id+"F0.wireOp",EDGE,"E7.40.2"),sQuery(id+"F0.wireOp",EDGE,"E7.40.3"),sQuery(id+"F0.wireOp",EDGE,"E7.40.4"),sQuery(id+"F0.wireOp",EDGE,"E7.40.5"),sQuery(id+"F0.wireOp",EDGE,"E7.41.0"),sQuery(id+"F0.wireOp",EDGE,"E7.41.1"),sQuery(id+"F0.wireOp",EDGE,"E7.41.2"),sQuery(id+"F0.wireOp",EDGE,"E7.41.3"),sQuery(id+"F0.wireOp",EDGE,"E7.41.4"),sQuery(id+"F0.wireOp",EDGE,"E7.41.5"),sQuery(id+"F0.wireOp",EDGE,"E7.42.0"),sQuery(id+"F0.wireOp",EDGE,"E7.42.1"),sQuery(id+"F0.wireOp",EDGE,"E7.42.2"),sQuery(id+"F0.wireOp",EDGE,"E7.42.3"),sQuery(id+"F0.wireOp",EDGE,"E7.42.4"),sQuery(id+"F0.wireOp",EDGE,"E7.42.5"),sQuery(id+"F0.wireOp",EDGE,"E7.43.0"),sQuery(id+"F0.wireOp",EDGE,"E7.43.1"),sQuery(id+"F0.wireOp",EDGE,"E7.43.2"),sQuery(id+"F0.wireOp",EDGE,"E7.43.3"),sQuery(id+"F0.wireOp",EDGE,"E7.43.4"),sQuery(id+"F0.wireOp",EDGE,"E7.43.5")])],"isStart":true})],"blendedInto":[makeQuery(id+"F1.opExtrude","CAP_FACE",FACE,{"disambiguationData":[OSD([sQuery(id+"F0.wireOp",EDGE,"E1"),sQuery(id+"F0.wireOp",EDGE,"E2"),sQuery(id+"F0.wireOp",EDGE,"E3"),sQuery(id+"F0.wireOp",EDGE,"E4"),sQuery(id+"F0.wireOp",EDGE,"E5"),sQuery(id+"F0.wireOp",EDGE,"E6"),sQuery(id+"F0.wireOp",EDGE,"E7.1.0"),sQuery(id+"F0.wireOp",EDGE,"E7.1.1"),sQuery(id+"F0.wireOp",EDGE,"E7.1.2"),sQuery(id+"F0.wireOp",EDGE,"E7.1.3"),sQuery(id+"F0.wireOp",EDGE,"E7.1.4"),sQuery(id+"F0.wireOp",EDGE,"E7.1.5"),sQuery(id+"F0.wireOp",EDGE,"E7.2.0"),sQuery(id+"F0.wireOp",EDGE,"E7.2.1"),sQuery(id+"F0.wireOp",EDGE,"E7.2.2"),sQuery(id+"F0.wireOp",EDGE,"E7.2.3"),sQuery(id+"F0.wireOp",EDGE,"E7.2.4"),sQuery(id+"F0.wireOp",EDGE,"E7.2.5"),sQuery(id+"F0.wireOp",EDGE,"E7.3.0"),sQuery(id+"F0.wireOp",EDGE,"E7.3.1"),sQuery(id+"F0.wireOp",EDGE,"E7.3.2"),sQuery(id+"F0.wireOp",EDGE,"E7.3.3"),sQuery(id+"F0.wireOp",EDGE,"E7.3.4"),sQuery(id+"F0.wireOp",EDGE,"E7.3.5"),sQuery(id+"F0.wireOp",EDGE,"E7.4.0"),sQuery(id+"F0.wireOp",EDGE,"E7.4.1"),sQuery(id+"F0.wireOp",EDGE,"E7.4.2"),sQuery(id+"F0.wireOp",EDGE,"E7.4.3"),sQuery(id+"F0.wireOp",EDGE,"E7.4.4"),sQuery(id+"F0.wireOp",EDGE,"E7.4.5"),sQuery(id+"F0.wireOp",EDGE,"E7.5.0"),sQuery(id+"F0.wireOp",EDGE,"E7.5.1"),sQuery(id+"F0.wireOp",EDGE,"E7.5.2"),sQuery(id+"F0.wireOp",EDGE,"E7.5.3"),sQuery(id+"F0.wireOp",EDGE,"E7.5.4"),sQuery(id+"F0.wireOp",EDGE,"E7.5.5"),sQuery(id+"F0.wireOp",EDGE,"E7.6.0"),sQuery(id+"F0.wireOp",EDGE,"E7.6.1"),sQuery(id+"F0.wireOp",EDGE,"E7.6.2"),sQuery(id+"F0.wireOp",EDGE,"E7.6.3"),sQuery(id+"F0.wireOp",EDGE,"E7.6.4"),sQuery(id+"F0.wireOp",EDGE,"E7.6.5"),sQuery(id+"F0.wireOp",EDGE,"E7.7.0"),sQuery(id+"F0.wireOp",EDGE,"E7.7.1"),sQuery(id+"F0.wireOp",EDGE,"E7.7.2"),sQuery(id+"F0.wireOp",EDGE,"E7.7.3"),sQuery(id+"F0.wireOp",EDGE,"E7.7.4"),sQuery(id+"F0.wireOp",EDGE,"E7.7.5"),sQuery(id+"F0.wireOp",EDGE,"E7.8.0"),sQuery(id+"F0.wireOp",EDGE,"E7.8.1"),sQuery(id+"F0.wireOp",EDGE,"E7.8.2"),sQuery(id+"F0.wireOp",EDGE,"E7.8.3"),sQuery(id+"F0.wireOp",EDGE,"E7.8.4"),sQuery(id+"F0.wireOp",EDGE,"E7.8.5"),sQuery(id+"F0.wireOp",EDGE,"E7.9.0"),sQuery(id+"F0.wireOp",EDGE,"E7.9.1"),sQuery(id+"F0.wireOp",EDGE,"E7.9.2"),sQuery(id+"F0.wireOp",EDGE,"E7.9.3"),sQuery(id+"F0.wireOp",EDGE,"E7.9.4"),sQuery(id+"F0.wireOp",EDGE,"E7.9.5"),sQuery(id+"F0.wireOp",EDGE,"E7.10.0"),sQuery(id+"F0.wireOp",EDGE,"E7.10.1"),sQuery(id+"F0.wireOp",EDGE,"E7.10.2"),sQuery(id+"F0.wireOp",EDGE,"E7.10.3"),sQuery(id+"F0.wireOp",EDGE,"E7.10.4"),sQuery(id+"F0.wireOp",EDGE,"E7.10.5"),sQuery(id+"F0.wireOp",EDGE,"E7.11.0"),sQuery(id+"F0.wireOp",EDGE,"E7.11.1"),sQuery(id+"F0.wireOp",EDGE,"E7.11.2"),sQuery(id+"F0.wireOp",EDGE,"E7.11.3"),sQuery(id+"F0.wireOp",EDGE,"E7.11.4"),sQuery(id+"F0.wireOp",EDGE,"E7.11.5"),sQuery(id+"F0.wireOp",EDGE,"E7.12.0"),sQuery(id+"F0.wireOp",EDGE,"E7.12.1"),sQuery(id+"F0.wireOp",EDGE,"E7.12.2"),sQuery(id+"F0.wireOp",EDGE,"E7.12.3"),sQuery(id+"F0.wireOp",EDGE,"E7.12.4"),sQuery(id+"F0.wireOp",EDGE,"E7.12.5"),sQuery(id+"F0.wireOp",EDGE,"E7.13.0"),sQuery(id+"F0.wireOp",EDGE,"E7.13.1"),sQuery(id+"F0.wireOp",EDGE,"E7.13.2"),sQuery(id+"F0.wireOp",EDGE,"E7.13.3"),sQuery(id+"F0.wireOp",EDGE,"E7.13.4"),sQuery(id+"F0.wireOp",EDGE,"E7.13.5"),sQuery(id+"F0.wireOp",EDGE,"E7.14.0"),sQuery(id+"F0.wireOp",EDGE,"E7.14.1"),sQuery(id+"F0.wireOp",EDGE,"E7.14.2"),sQuery(id+"F0.wireOp",EDGE,"E7.14.3"),sQuery(id+"F0.wireOp",EDGE,"E7.14.4"),sQuery(id+"F0.wireOp",EDGE,"E7.14.5"),sQuery(id+"F0.wireOp",EDGE,"E7.15.0"),sQuery(id+"F0.wireOp",EDGE,"E7.15.1"),sQuery(id+"F0.wireOp",EDGE,"E7.15.2"),sQuery(id+"F0.wireOp",EDGE,"E7.15.3"),sQuery(id+"F0.wireOp",EDGE,"E7.15.4"),sQuery(id+"F0.wireOp",EDGE,"E7.15.5"),subQ0,sQuery(id+"F0.wireOp",EDGE,"E7.16.1"),sQuery(id+"F0.wireOp",EDGE,"E7.16.2"),sQuery(id+"F0.wireOp",EDGE,"E7.16.3"),sQuery(id+"F0.wireOp",EDGE,"E7.16.4"),sQuery(id+"F0.wireOp",EDGE,"E7.16.5"),sQuery(id+"F0.wireOp",EDGE,"E7.17.0"),sQuery(id+"F0.wireOp",EDGE,"E7.17.1"),sQuery(id+"F0.wireOp",EDGE,"E7.17.2"),sQuery(id+"F0.wireOp",EDGE,"E7.17.3"),sQuery(id+"F0.wireOp",EDGE,"E7.17.4"),sQuery(id+"F0.wireOp",EDGE,"E7.17.5"),sQuery(id+"F0.wireOp",EDGE,"E7.18.0"),sQuery(id+"F0.wireOp",EDGE,"E7.18.1"),sQuery(id+"F0.wireOp",EDGE,"E7.18.2"),sQuery(id+"F0.wireOp",EDGE,"E7.18.3"),sQuery(id+"F0.wireOp",EDGE,"E7.18.4"),sQuery(id+"F0.wireOp",EDGE,"E7.18.5"),sQuery(id+"F0.wireOp",EDGE,"E7.19.0"),sQuery(id+"F0.wireOp",EDGE,"E7.19.1"),sQuery(id+"F0.wireOp",EDGE,"E7.19.2"),sQuery(id+"F0.wireOp",EDGE,"E7.19.3"),sQuery(id+"F0.wireOp",EDGE,"E7.19.4"),sQuery(id+"F0.wireOp",EDGE,"E7.19.5"),sQuery(id+"F0.wireOp",EDGE,"E7.20.0"),sQuery(id+"F0.wireOp",EDGE,"E7.20.1"),sQuery(id+"F0.wireOp",EDGE,"E7.20.2"),sQuery(id+"F0.wireOp",EDGE,"E7.20.3"),sQuery(id+"F0.wireOp",EDGE,"E7.20.4"),sQuery(id+"F0.wireOp",EDGE,"E7.20.5"),sQuery(id+"F0.wireOp",EDGE,"E7.21.0"),sQuery(id+"F0.wireOp",EDGE,"E7.21.1"),sQuery(id+"F0.wireOp",EDGE,"E7.21.2"),sQuery(id+"F0.wireOp",EDGE,"E7.21.3"),sQuery(id+"F0.wireOp",EDGE,"E7.21.4"),sQuery(id+"F0.wireOp",EDGE,"E7.21.5"),sQuery(id+"F0.wireOp",EDGE,"E7.22.0"),sQuery(id+"F0.wireOp",EDGE,"E7.22.1"),sQuery(id+"F0.wireOp",EDGE,"E7.22.2"),sQuery(id+"F0.wireOp",EDGE,"E7.22.3"),sQuery(id+"F0.wireOp",EDGE,"E7.22.4"),sQuery(id+"F0.wireOp",EDGE,"E7.22.5"),sQuery(id+"F0.wireOp",EDGE,"E7.23.0"),sQuery(id+"F0.wireOp",EDGE,"E7.23.1"),sQuery(id+"F0.wireOp",EDGE,"E7.23.2"),sQuery(id+"F0.wireOp",EDGE,"E7.23.3"),sQuery(id+"F0.wireOp",EDGE,"E7.23.4"),sQuery(id+"F0.wireOp",EDGE,"E7.23.5"),sQuery(id+"F0.wireOp",EDGE,"E7.24.0"),sQuery(id+"F0.wireOp",EDGE,"E7.24.1"),sQuery(id+"F0.wireOp",EDGE,"E7.24.2"),sQuery(id+"F0.wireOp",EDGE,"E7.24.3"),sQuery(id+"F0.wireOp",EDGE,"E7.24.4"),sQuery(id+"F0.wireOp",EDGE,"E7.24.5"),sQuery(id+"F0.wireOp",EDGE,"E7.25.0"),sQuery(id+"F0.wireOp",EDGE,"E7.25.1"),sQuery(id+"F0.wireOp",EDGE,"E7.25.2"),sQuery(id+"F0.wireOp",EDGE,"E7.25.3"),sQuery(id+"F0.wireOp",EDGE,"E7.25.4"),sQuery(id+"F0.wireOp",EDGE,"E7.25.5"),sQuery(id+"F0.wireOp",EDGE,"E7.26.0"),sQuery(id+"F0.wireOp",EDGE,"E7.26.1"),sQuery(id+"F0.wireOp",EDGE,"E7.26.2"),sQuery(id+"F0.wireOp",EDGE,"E7.26.3"),sQuery(id+"F0.wireOp",EDGE,"E7.26.4"),sQuery(id+"F0.wireOp",EDGE,"E7.26.5"),sQuery(id+"F0.wireOp",EDGE,"E7.27.0"),sQuery(id+"F0.wireOp",EDGE,"E7.27.1"),sQuery(id+"F0.wireOp",EDGE,"E7.27.2"),sQuery(id+"F0.wireOp",EDGE,"E7.27.3"),sQuery(id+"F0.wireOp",EDGE,"E7.27.4"),sQuery(id+"F0.wireOp",EDGE,"E7.27.5"),sQuery(id+"F0.wireOp",EDGE,"E7.28.0"),sQuery(id+"F0.wireOp",EDGE,"E7.28.1"),sQuery(id+"F0.wireOp",EDGE,"E7.28.2"),sQuery(id+"F0.wireOp",EDGE,"E7.28.3"),sQuery(id+"F0.wireOp",EDGE,"E7.28.4"),sQuery(id+"F0.wireOp",EDGE,"E7.28.5"),sQuery(id+"F0.wireOp",EDGE,"E7.29.0"),sQuery(id+"F0.wireOp",EDGE,"E7.29.1"),sQuery(id+"F0.wireOp",EDGE,"E7.29.2"),sQuery(id+"F0.wireOp",EDGE,"E7.29.3"),sQuery(id+"F0.wireOp",EDGE,"E7.29.4"),sQuery(id+"F0.wireOp",EDGE,"E7.29.5"),sQuery(id+"F0.wireOp",EDGE,"E7.30.0"),sQuery(id+"F0.wireOp",EDGE,"E7.30.1"),sQuery(id+"F0.wireOp",EDGE,"E7.30.2"),sQuery(id+"F0.wireOp",EDGE,"E7.30.3"),sQuery(id+"F0.wireOp",EDGE,"E7.30.4"),sQuery(id+"F0.wireOp",EDGE,"E7.30.5"),sQuery(id+"F0.wireOp",EDGE,"E7.31.0"),sQuery(id+"F0.wireOp",EDGE,"E7.31.1"),sQuery(id+"F0.wireOp",EDGE,"E7.31.2"),sQuery(id+"F0.wireOp",EDGE,"E7.31.3"),sQuery(id+"F0.wireOp",EDGE,"E7.31.4"),sQuery(id+"F0.wireOp",EDGE,"E7.31.5"),sQuery(id+"F0.wireOp",EDGE,"E7.32.0"),sQuery(id+"F0.wireOp",EDGE,"E7.32.1"),sQuery(id+"F0.wireOp",EDGE,"E7.32.2"),sQuery(id+"F0.wireOp",EDGE,"E7.32.3"),sQuery(id+"F0.wireOp",EDGE,"E7.32.4"),sQuery(id+"F0.wireOp",EDGE,"E7.32.5"),sQuery(id+"F0.wireOp",EDGE,"E7.33.0"),sQuery(id+"F0.wireOp",EDGE,"E7.33.1"),sQuery(id+"F0.wireOp",EDGE,"E7.33.2"),sQuery(id+"F0.wireOp",EDGE,"E7.33.3"),sQuery(id+"F0.wireOp",EDGE,"E7.33.4"),sQuery(id+"F0.wireOp",EDGE,"E7.33.5"),sQuery(id+"F0.wireOp",EDGE,"E7.34.0"),sQuery(id+"F0.wireOp",EDGE,"E7.34.1"),sQuery(id+"F0.wireOp",EDGE,"E7.34.2"),sQuery(id+"F0.wireOp",EDGE,"E7.34.3"),sQuery(id+"F0.wireOp",EDGE,"E7.34.4"),sQuery(id+"F0.wireOp",EDGE,"E7.34.5"),sQuery(id+"F0.wireOp",EDGE,"E7.35.0"),sQuery(id+"F0.wireOp",EDGE,"E7.35.1"),sQuery(id+"F0.wireOp",EDGE,"E7.35.2"),sQuery(id+"F0.wireOp",EDGE,"E7.35.3"),sQuery(id+"F0.wireOp",EDGE,"E7.35.4"),sQuery(id+"F0.wireOp",EDGE,"E7.35.5"),sQuery(id+"F0.wireOp",EDGE,"E7.36.0"),sQuery(id+"F0.wireOp",EDGE,"E7.36.1"),sQuery(id+"F0.wireOp",EDGE,"E7.36.2"),sQuery(id+"F0.wireOp",EDGE,"E7.36.3"),sQuery(id+"F0.wireOp",EDGE,"E7.36.4"),sQuery(id+"F0.wireOp",EDGE,"E7.36.5"),sQuery(id+"F0.wireOp",EDGE,"E7.37.0"),sQuery(id+"F0.wireOp",EDGE,"E7.37.1"),sQuery(id+"F0.wireOp",EDGE,"E7.37.2"),sQuery(id+"F0.wireOp",EDGE,"E7.37.3"),sQuery(id+"F0.wireOp",EDGE,"E7.37.4"),sQuery(id+"F0.wireOp",EDGE,"E7.37.5"),sQuery(id+"F0.wireOp",EDGE,"E7.38.0"),sQuery(id+"F0.wireOp",EDGE,"E7.38.1"),sQuery(id+"F0.wireOp",EDGE,"E7.38.2"),sQuery(id+"F0.wireOp",EDGE,"E7.38.3"),sQuery(id+"F0.wireOp",EDGE,"E7.38.4"),sQuery(id+"F0.wireOp",EDGE,"E7.38.5"),sQuery(id+"F0.wireOp",EDGE,"E7.39.0"),sQuery(id+"F0.wireOp",EDGE,"E7.39.1"),sQuery(id+"F0.wireOp",EDGE,"E7.39.2"),sQuery(id+"F0.wireOp",EDGE,"E7.39.3"),sQuery(id+"F0.wireOp",EDGE,"E7.39.4"),sQuery(id+"F0.wireOp",EDGE,"E7.39.5"),sQuery(id+"F0.wireOp",EDGE,"E7.40.0"),sQuery(id+"F0.wireOp",EDGE,"E7.40.1"),sQuery(id+"F0.wireOp",EDGE,"E7.40.2"),sQuery(id+"F0.wireOp",EDGE,"E7.40.3"),sQuery(id+"F0.wireOp",EDGE,"E7.40.4"),sQuery(id+"F0.wireOp",EDGE,"E7.40.5"),sQuery(id+"F0.wireOp",EDGE,"E7.41.0"),sQuery(id+"F0.wireOp",EDGE,"E7.41.1"),sQuery(id+"F0.wireOp",EDGE,"E7.41.2"),sQuery(id+"F0.wireOp",EDGE,"E7.41.3"),sQuery(id+"F0.wireOp",EDGE,"E7.41.4"),sQuery(id+"F0.wireOp",EDGE,"E7.41.5"),sQuery(id+"F0.wireOp",EDGE,"E7.42.0"),sQuery(id+"F0.wireOp",EDGE,"E7.42.1"),sQuery(id+"F0.wireOp",EDGE,"E7.42.2"),sQuery(id+"F0.wireOp",EDGE,"E7.42.3"),sQuery(id+"F0.wireOp",EDGE,"E7.42.4"),sQuery(id+"F0.wireOp",EDGE,"E7.42.5"),sQuery(id+"F0.wireOp",EDGE,"E7.43.0"),sQuery(id+"F0.wireOp",EDGE,"E7.43.1"),sQuery(id+"F0.wireOp",EDGE,"E7.43.2"),sQuery(id+"F0.wireOp",EDGE,"E7.43.3"),sQuery(id+"F0.wireOp",EDGE,"E7.43.4"),sQuery(id+"F0.wireOp",EDGE,"E7.43.5")])],"isStart":true})]});}
            var Q30;
            {var subQ0=sQuery(id+"F0.wireOp",EDGE,"E7.18.0");Q30=makeQuery(id+"F2.opChamfer","BLEND_EDGE",EDGE,{"blendedFrom":[makeQuery(id+"F1.opExtrude","CAP_EDGE",EDGE,{"disambiguationData":[OSD([subQ0])],"isStart":true}),makeQuery(id+"F1.opExtrude","CAP_FACE",FACE,{"disambiguationData":[OSD([sQuery(id+"F0.wireOp",EDGE,"E1"),sQuery(id+"F0.wireOp",EDGE,"E2"),sQuery(id+"F0.wireOp",EDGE,"E3"),sQuery(id+"F0.wireOp",EDGE,"E4"),sQuery(id+"F0.wireOp",EDGE,"E5"),sQuery(id+"F0.wireOp",EDGE,"E6"),sQuery(id+"F0.wireOp",EDGE,"E7.1.0"),sQuery(id+"F0.wireOp",EDGE,"E7.1.1"),sQuery(id+"F0.wireOp",EDGE,"E7.1.2"),sQuery(id+"F0.wireOp",EDGE,"E7.1.3"),sQuery(id+"F0.wireOp",EDGE,"E7.1.4"),sQuery(id+"F0.wireOp",EDGE,"E7.1.5"),sQuery(id+"F0.wireOp",EDGE,"E7.2.0"),sQuery(id+"F0.wireOp",EDGE,"E7.2.1"),sQuery(id+"F0.wireOp",EDGE,"E7.2.2"),sQuery(id+"F0.wireOp",EDGE,"E7.2.3"),sQuery(id+"F0.wireOp",EDGE,"E7.2.4"),sQuery(id+"F0.wireOp",EDGE,"E7.2.5"),sQuery(id+"F0.wireOp",EDGE,"E7.3.0"),sQuery(id+"F0.wireOp",EDGE,"E7.3.1"),sQuery(id+"F0.wireOp",EDGE,"E7.3.2"),sQuery(id+"F0.wireOp",EDGE,"E7.3.3"),sQuery(id+"F0.wireOp",EDGE,"E7.3.4"),sQuery(id+"F0.wireOp",EDGE,"E7.3.5"),sQuery(id+"F0.wireOp",EDGE,"E7.4.0"),sQuery(id+"F0.wireOp",EDGE,"E7.4.1"),sQuery(id+"F0.wireOp",EDGE,"E7.4.2"),sQuery(id+"F0.wireOp",EDGE,"E7.4.3"),sQuery(id+"F0.wireOp",EDGE,"E7.4.4"),sQuery(id+"F0.wireOp",EDGE,"E7.4.5"),sQuery(id+"F0.wireOp",EDGE,"E7.5.0"),sQuery(id+"F0.wireOp",EDGE,"E7.5.1"),sQuery(id+"F0.wireOp",EDGE,"E7.5.2"),sQuery(id+"F0.wireOp",EDGE,"E7.5.3"),sQuery(id+"F0.wireOp",EDGE,"E7.5.4"),sQuery(id+"F0.wireOp",EDGE,"E7.5.5"),sQuery(id+"F0.wireOp",EDGE,"E7.6.0"),sQuery(id+"F0.wireOp",EDGE,"E7.6.1"),sQuery(id+"F0.wireOp",EDGE,"E7.6.2"),sQuery(id+"F0.wireOp",EDGE,"E7.6.3"),sQuery(id+"F0.wireOp",EDGE,"E7.6.4"),sQuery(id+"F0.wireOp",EDGE,"E7.6.5"),sQuery(id+"F0.wireOp",EDGE,"E7.7.0"),sQuery(id+"F0.wireOp",EDGE,"E7.7.1"),sQuery(id+"F0.wireOp",EDGE,"E7.7.2"),sQuery(id+"F0.wireOp",EDGE,"E7.7.3"),sQuery(id+"F0.wireOp",EDGE,"E7.7.4"),sQuery(id+"F0.wireOp",EDGE,"E7.7.5"),sQuery(id+"F0.wireOp",EDGE,"E7.8.0"),sQuery(id+"F0.wireOp",EDGE,"E7.8.1"),sQuery(id+"F0.wireOp",EDGE,"E7.8.2"),sQuery(id+"F0.wireOp",EDGE,"E7.8.3"),sQuery(id+"F0.wireOp",EDGE,"E7.8.4"),sQuery(id+"F0.wireOp",EDGE,"E7.8.5"),sQuery(id+"F0.wireOp",EDGE,"E7.9.0"),sQuery(id+"F0.wireOp",EDGE,"E7.9.1"),sQuery(id+"F0.wireOp",EDGE,"E7.9.2"),sQuery(id+"F0.wireOp",EDGE,"E7.9.3"),sQuery(id+"F0.wireOp",EDGE,"E7.9.4"),sQuery(id+"F0.wireOp",EDGE,"E7.9.5"),sQuery(id+"F0.wireOp",EDGE,"E7.10.0"),sQuery(id+"F0.wireOp",EDGE,"E7.10.1"),sQuery(id+"F0.wireOp",EDGE,"E7.10.2"),sQuery(id+"F0.wireOp",EDGE,"E7.10.3"),sQuery(id+"F0.wireOp",EDGE,"E7.10.4"),sQuery(id+"F0.wireOp",EDGE,"E7.10.5"),sQuery(id+"F0.wireOp",EDGE,"E7.11.0"),sQuery(id+"F0.wireOp",EDGE,"E7.11.1"),sQuery(id+"F0.wireOp",EDGE,"E7.11.2"),sQuery(id+"F0.wireOp",EDGE,"E7.11.3"),sQuery(id+"F0.wireOp",EDGE,"E7.11.4"),sQuery(id+"F0.wireOp",EDGE,"E7.11.5"),sQuery(id+"F0.wireOp",EDGE,"E7.12.0"),sQuery(id+"F0.wireOp",EDGE,"E7.12.1"),sQuery(id+"F0.wireOp",EDGE,"E7.12.2"),sQuery(id+"F0.wireOp",EDGE,"E7.12.3"),sQuery(id+"F0.wireOp",EDGE,"E7.12.4"),sQuery(id+"F0.wireOp",EDGE,"E7.12.5"),sQuery(id+"F0.wireOp",EDGE,"E7.13.0"),sQuery(id+"F0.wireOp",EDGE,"E7.13.1"),sQuery(id+"F0.wireOp",EDGE,"E7.13.2"),sQuery(id+"F0.wireOp",EDGE,"E7.13.3"),sQuery(id+"F0.wireOp",EDGE,"E7.13.4"),sQuery(id+"F0.wireOp",EDGE,"E7.13.5"),sQuery(id+"F0.wireOp",EDGE,"E7.14.0"),sQuery(id+"F0.wireOp",EDGE,"E7.14.1"),sQuery(id+"F0.wireOp",EDGE,"E7.14.2"),sQuery(id+"F0.wireOp",EDGE,"E7.14.3"),sQuery(id+"F0.wireOp",EDGE,"E7.14.4"),sQuery(id+"F0.wireOp",EDGE,"E7.14.5"),sQuery(id+"F0.wireOp",EDGE,"E7.15.0"),sQuery(id+"F0.wireOp",EDGE,"E7.15.1"),sQuery(id+"F0.wireOp",EDGE,"E7.15.2"),sQuery(id+"F0.wireOp",EDGE,"E7.15.3"),sQuery(id+"F0.wireOp",EDGE,"E7.15.4"),sQuery(id+"F0.wireOp",EDGE,"E7.15.5"),sQuery(id+"F0.wireOp",EDGE,"E7.16.0"),sQuery(id+"F0.wireOp",EDGE,"E7.16.1"),sQuery(id+"F0.wireOp",EDGE,"E7.16.2"),sQuery(id+"F0.wireOp",EDGE,"E7.16.3"),sQuery(id+"F0.wireOp",EDGE,"E7.16.4"),sQuery(id+"F0.wireOp",EDGE,"E7.16.5"),sQuery(id+"F0.wireOp",EDGE,"E7.17.0"),sQuery(id+"F0.wireOp",EDGE,"E7.17.1"),sQuery(id+"F0.wireOp",EDGE,"E7.17.2"),sQuery(id+"F0.wireOp",EDGE,"E7.17.3"),sQuery(id+"F0.wireOp",EDGE,"E7.17.4"),sQuery(id+"F0.wireOp",EDGE,"E7.17.5"),subQ0,sQuery(id+"F0.wireOp",EDGE,"E7.18.1"),sQuery(id+"F0.wireOp",EDGE,"E7.18.2"),sQuery(id+"F0.wireOp",EDGE,"E7.18.3"),sQuery(id+"F0.wireOp",EDGE,"E7.18.4"),sQuery(id+"F0.wireOp",EDGE,"E7.18.5"),sQuery(id+"F0.wireOp",EDGE,"E7.19.0"),sQuery(id+"F0.wireOp",EDGE,"E7.19.1"),sQuery(id+"F0.wireOp",EDGE,"E7.19.2"),sQuery(id+"F0.wireOp",EDGE,"E7.19.3"),sQuery(id+"F0.wireOp",EDGE,"E7.19.4"),sQuery(id+"F0.wireOp",EDGE,"E7.19.5"),sQuery(id+"F0.wireOp",EDGE,"E7.20.0"),sQuery(id+"F0.wireOp",EDGE,"E7.20.1"),sQuery(id+"F0.wireOp",EDGE,"E7.20.2"),sQuery(id+"F0.wireOp",EDGE,"E7.20.3"),sQuery(id+"F0.wireOp",EDGE,"E7.20.4"),sQuery(id+"F0.wireOp",EDGE,"E7.20.5"),sQuery(id+"F0.wireOp",EDGE,"E7.21.0"),sQuery(id+"F0.wireOp",EDGE,"E7.21.1"),sQuery(id+"F0.wireOp",EDGE,"E7.21.2"),sQuery(id+"F0.wireOp",EDGE,"E7.21.3"),sQuery(id+"F0.wireOp",EDGE,"E7.21.4"),sQuery(id+"F0.wireOp",EDGE,"E7.21.5"),sQuery(id+"F0.wireOp",EDGE,"E7.22.0"),sQuery(id+"F0.wireOp",EDGE,"E7.22.1"),sQuery(id+"F0.wireOp",EDGE,"E7.22.2"),sQuery(id+"F0.wireOp",EDGE,"E7.22.3"),sQuery(id+"F0.wireOp",EDGE,"E7.22.4"),sQuery(id+"F0.wireOp",EDGE,"E7.22.5"),sQuery(id+"F0.wireOp",EDGE,"E7.23.0"),sQuery(id+"F0.wireOp",EDGE,"E7.23.1"),sQuery(id+"F0.wireOp",EDGE,"E7.23.2"),sQuery(id+"F0.wireOp",EDGE,"E7.23.3"),sQuery(id+"F0.wireOp",EDGE,"E7.23.4"),sQuery(id+"F0.wireOp",EDGE,"E7.23.5"),sQuery(id+"F0.wireOp",EDGE,"E7.24.0"),sQuery(id+"F0.wireOp",EDGE,"E7.24.1"),sQuery(id+"F0.wireOp",EDGE,"E7.24.2"),sQuery(id+"F0.wireOp",EDGE,"E7.24.3"),sQuery(id+"F0.wireOp",EDGE,"E7.24.4"),sQuery(id+"F0.wireOp",EDGE,"E7.24.5"),sQuery(id+"F0.wireOp",EDGE,"E7.25.0"),sQuery(id+"F0.wireOp",EDGE,"E7.25.1"),sQuery(id+"F0.wireOp",EDGE,"E7.25.2"),sQuery(id+"F0.wireOp",EDGE,"E7.25.3"),sQuery(id+"F0.wireOp",EDGE,"E7.25.4"),sQuery(id+"F0.wireOp",EDGE,"E7.25.5"),sQuery(id+"F0.wireOp",EDGE,"E7.26.0"),sQuery(id+"F0.wireOp",EDGE,"E7.26.1"),sQuery(id+"F0.wireOp",EDGE,"E7.26.2"),sQuery(id+"F0.wireOp",EDGE,"E7.26.3"),sQuery(id+"F0.wireOp",EDGE,"E7.26.4"),sQuery(id+"F0.wireOp",EDGE,"E7.26.5"),sQuery(id+"F0.wireOp",EDGE,"E7.27.0"),sQuery(id+"F0.wireOp",EDGE,"E7.27.1"),sQuery(id+"F0.wireOp",EDGE,"E7.27.2"),sQuery(id+"F0.wireOp",EDGE,"E7.27.3"),sQuery(id+"F0.wireOp",EDGE,"E7.27.4"),sQuery(id+"F0.wireOp",EDGE,"E7.27.5"),sQuery(id+"F0.wireOp",EDGE,"E7.28.0"),sQuery(id+"F0.wireOp",EDGE,"E7.28.1"),sQuery(id+"F0.wireOp",EDGE,"E7.28.2"),sQuery(id+"F0.wireOp",EDGE,"E7.28.3"),sQuery(id+"F0.wireOp",EDGE,"E7.28.4"),sQuery(id+"F0.wireOp",EDGE,"E7.28.5"),sQuery(id+"F0.wireOp",EDGE,"E7.29.0"),sQuery(id+"F0.wireOp",EDGE,"E7.29.1"),sQuery(id+"F0.wireOp",EDGE,"E7.29.2"),sQuery(id+"F0.wireOp",EDGE,"E7.29.3"),sQuery(id+"F0.wireOp",EDGE,"E7.29.4"),sQuery(id+"F0.wireOp",EDGE,"E7.29.5"),sQuery(id+"F0.wireOp",EDGE,"E7.30.0"),sQuery(id+"F0.wireOp",EDGE,"E7.30.1"),sQuery(id+"F0.wireOp",EDGE,"E7.30.2"),sQuery(id+"F0.wireOp",EDGE,"E7.30.3"),sQuery(id+"F0.wireOp",EDGE,"E7.30.4"),sQuery(id+"F0.wireOp",EDGE,"E7.30.5"),sQuery(id+"F0.wireOp",EDGE,"E7.31.0"),sQuery(id+"F0.wireOp",EDGE,"E7.31.1"),sQuery(id+"F0.wireOp",EDGE,"E7.31.2"),sQuery(id+"F0.wireOp",EDGE,"E7.31.3"),sQuery(id+"F0.wireOp",EDGE,"E7.31.4"),sQuery(id+"F0.wireOp",EDGE,"E7.31.5"),sQuery(id+"F0.wireOp",EDGE,"E7.32.0"),sQuery(id+"F0.wireOp",EDGE,"E7.32.1"),sQuery(id+"F0.wireOp",EDGE,"E7.32.2"),sQuery(id+"F0.wireOp",EDGE,"E7.32.3"),sQuery(id+"F0.wireOp",EDGE,"E7.32.4"),sQuery(id+"F0.wireOp",EDGE,"E7.32.5"),sQuery(id+"F0.wireOp",EDGE,"E7.33.0"),sQuery(id+"F0.wireOp",EDGE,"E7.33.1"),sQuery(id+"F0.wireOp",EDGE,"E7.33.2"),sQuery(id+"F0.wireOp",EDGE,"E7.33.3"),sQuery(id+"F0.wireOp",EDGE,"E7.33.4"),sQuery(id+"F0.wireOp",EDGE,"E7.33.5"),sQuery(id+"F0.wireOp",EDGE,"E7.34.0"),sQuery(id+"F0.wireOp",EDGE,"E7.34.1"),sQuery(id+"F0.wireOp",EDGE,"E7.34.2"),sQuery(id+"F0.wireOp",EDGE,"E7.34.3"),sQuery(id+"F0.wireOp",EDGE,"E7.34.4"),sQuery(id+"F0.wireOp",EDGE,"E7.34.5"),sQuery(id+"F0.wireOp",EDGE,"E7.35.0"),sQuery(id+"F0.wireOp",EDGE,"E7.35.1"),sQuery(id+"F0.wireOp",EDGE,"E7.35.2"),sQuery(id+"F0.wireOp",EDGE,"E7.35.3"),sQuery(id+"F0.wireOp",EDGE,"E7.35.4"),sQuery(id+"F0.wireOp",EDGE,"E7.35.5"),sQuery(id+"F0.wireOp",EDGE,"E7.36.0"),sQuery(id+"F0.wireOp",EDGE,"E7.36.1"),sQuery(id+"F0.wireOp",EDGE,"E7.36.2"),sQuery(id+"F0.wireOp",EDGE,"E7.36.3"),sQuery(id+"F0.wireOp",EDGE,"E7.36.4"),sQuery(id+"F0.wireOp",EDGE,"E7.36.5"),sQuery(id+"F0.wireOp",EDGE,"E7.37.0"),sQuery(id+"F0.wireOp",EDGE,"E7.37.1"),sQuery(id+"F0.wireOp",EDGE,"E7.37.2"),sQuery(id+"F0.wireOp",EDGE,"E7.37.3"),sQuery(id+"F0.wireOp",EDGE,"E7.37.4"),sQuery(id+"F0.wireOp",EDGE,"E7.37.5"),sQuery(id+"F0.wireOp",EDGE,"E7.38.0"),sQuery(id+"F0.wireOp",EDGE,"E7.38.1"),sQuery(id+"F0.wireOp",EDGE,"E7.38.2"),sQuery(id+"F0.wireOp",EDGE,"E7.38.3"),sQuery(id+"F0.wireOp",EDGE,"E7.38.4"),sQuery(id+"F0.wireOp",EDGE,"E7.38.5"),sQuery(id+"F0.wireOp",EDGE,"E7.39.0"),sQuery(id+"F0.wireOp",EDGE,"E7.39.1"),sQuery(id+"F0.wireOp",EDGE,"E7.39.2"),sQuery(id+"F0.wireOp",EDGE,"E7.39.3"),sQuery(id+"F0.wireOp",EDGE,"E7.39.4"),sQuery(id+"F0.wireOp",EDGE,"E7.39.5"),sQuery(id+"F0.wireOp",EDGE,"E7.40.0"),sQuery(id+"F0.wireOp",EDGE,"E7.40.1"),sQuery(id+"F0.wireOp",EDGE,"E7.40.2"),sQuery(id+"F0.wireOp",EDGE,"E7.40.3"),sQuery(id+"F0.wireOp",EDGE,"E7.40.4"),sQuery(id+"F0.wireOp",EDGE,"E7.40.5"),sQuery(id+"F0.wireOp",EDGE,"E7.41.0"),sQuery(id+"F0.wireOp",EDGE,"E7.41.1"),sQuery(id+"F0.wireOp",EDGE,"E7.41.2"),sQuery(id+"F0.wireOp",EDGE,"E7.41.3"),sQuery(id+"F0.wireOp",EDGE,"E7.41.4"),sQuery(id+"F0.wireOp",EDGE,"E7.41.5"),sQuery(id+"F0.wireOp",EDGE,"E7.42.0"),sQuery(id+"F0.wireOp",EDGE,"E7.42.1"),sQuery(id+"F0.wireOp",EDGE,"E7.42.2"),sQuery(id+"F0.wireOp",EDGE,"E7.42.3"),sQuery(id+"F0.wireOp",EDGE,"E7.42.4"),sQuery(id+"F0.wireOp",EDGE,"E7.42.5"),sQuery(id+"F0.wireOp",EDGE,"E7.43.0"),sQuery(id+"F0.wireOp",EDGE,"E7.43.1"),sQuery(id+"F0.wireOp",EDGE,"E7.43.2"),sQuery(id+"F0.wireOp",EDGE,"E7.43.3"),sQuery(id+"F0.wireOp",EDGE,"E7.43.4"),sQuery(id+"F0.wireOp",EDGE,"E7.43.5")])],"isStart":true})],"blendedInto":[makeQuery(id+"F1.opExtrude","CAP_FACE",FACE,{"disambiguationData":[OSD([sQuery(id+"F0.wireOp",EDGE,"E1"),sQuery(id+"F0.wireOp",EDGE,"E2"),sQuery(id+"F0.wireOp",EDGE,"E3"),sQuery(id+"F0.wireOp",EDGE,"E4"),sQuery(id+"F0.wireOp",EDGE,"E5"),sQuery(id+"F0.wireOp",EDGE,"E6"),sQuery(id+"F0.wireOp",EDGE,"E7.1.0"),sQuery(id+"F0.wireOp",EDGE,"E7.1.1"),sQuery(id+"F0.wireOp",EDGE,"E7.1.2"),sQuery(id+"F0.wireOp",EDGE,"E7.1.3"),sQuery(id+"F0.wireOp",EDGE,"E7.1.4"),sQuery(id+"F0.wireOp",EDGE,"E7.1.5"),sQuery(id+"F0.wireOp",EDGE,"E7.2.0"),sQuery(id+"F0.wireOp",EDGE,"E7.2.1"),sQuery(id+"F0.wireOp",EDGE,"E7.2.2"),sQuery(id+"F0.wireOp",EDGE,"E7.2.3"),sQuery(id+"F0.wireOp",EDGE,"E7.2.4"),sQuery(id+"F0.wireOp",EDGE,"E7.2.5"),sQuery(id+"F0.wireOp",EDGE,"E7.3.0"),sQuery(id+"F0.wireOp",EDGE,"E7.3.1"),sQuery(id+"F0.wireOp",EDGE,"E7.3.2"),sQuery(id+"F0.wireOp",EDGE,"E7.3.3"),sQuery(id+"F0.wireOp",EDGE,"E7.3.4"),sQuery(id+"F0.wireOp",EDGE,"E7.3.5"),sQuery(id+"F0.wireOp",EDGE,"E7.4.0"),sQuery(id+"F0.wireOp",EDGE,"E7.4.1"),sQuery(id+"F0.wireOp",EDGE,"E7.4.2"),sQuery(id+"F0.wireOp",EDGE,"E7.4.3"),sQuery(id+"F0.wireOp",EDGE,"E7.4.4"),sQuery(id+"F0.wireOp",EDGE,"E7.4.5"),sQuery(id+"F0.wireOp",EDGE,"E7.5.0"),sQuery(id+"F0.wireOp",EDGE,"E7.5.1"),sQuery(id+"F0.wireOp",EDGE,"E7.5.2"),sQuery(id+"F0.wireOp",EDGE,"E7.5.3"),sQuery(id+"F0.wireOp",EDGE,"E7.5.4"),sQuery(id+"F0.wireOp",EDGE,"E7.5.5"),sQuery(id+"F0.wireOp",EDGE,"E7.6.0"),sQuery(id+"F0.wireOp",EDGE,"E7.6.1"),sQuery(id+"F0.wireOp",EDGE,"E7.6.2"),sQuery(id+"F0.wireOp",EDGE,"E7.6.3"),sQuery(id+"F0.wireOp",EDGE,"E7.6.4"),sQuery(id+"F0.wireOp",EDGE,"E7.6.5"),sQuery(id+"F0.wireOp",EDGE,"E7.7.0"),sQuery(id+"F0.wireOp",EDGE,"E7.7.1"),sQuery(id+"F0.wireOp",EDGE,"E7.7.2"),sQuery(id+"F0.wireOp",EDGE,"E7.7.3"),sQuery(id+"F0.wireOp",EDGE,"E7.7.4"),sQuery(id+"F0.wireOp",EDGE,"E7.7.5"),sQuery(id+"F0.wireOp",EDGE,"E7.8.0"),sQuery(id+"F0.wireOp",EDGE,"E7.8.1"),sQuery(id+"F0.wireOp",EDGE,"E7.8.2"),sQuery(id+"F0.wireOp",EDGE,"E7.8.3"),sQuery(id+"F0.wireOp",EDGE,"E7.8.4"),sQuery(id+"F0.wireOp",EDGE,"E7.8.5"),sQuery(id+"F0.wireOp",EDGE,"E7.9.0"),sQuery(id+"F0.wireOp",EDGE,"E7.9.1"),sQuery(id+"F0.wireOp",EDGE,"E7.9.2"),sQuery(id+"F0.wireOp",EDGE,"E7.9.3"),sQuery(id+"F0.wireOp",EDGE,"E7.9.4"),sQuery(id+"F0.wireOp",EDGE,"E7.9.5"),sQuery(id+"F0.wireOp",EDGE,"E7.10.0"),sQuery(id+"F0.wireOp",EDGE,"E7.10.1"),sQuery(id+"F0.wireOp",EDGE,"E7.10.2"),sQuery(id+"F0.wireOp",EDGE,"E7.10.3"),sQuery(id+"F0.wireOp",EDGE,"E7.10.4"),sQuery(id+"F0.wireOp",EDGE,"E7.10.5"),sQuery(id+"F0.wireOp",EDGE,"E7.11.0"),sQuery(id+"F0.wireOp",EDGE,"E7.11.1"),sQuery(id+"F0.wireOp",EDGE,"E7.11.2"),sQuery(id+"F0.wireOp",EDGE,"E7.11.3"),sQuery(id+"F0.wireOp",EDGE,"E7.11.4"),sQuery(id+"F0.wireOp",EDGE,"E7.11.5"),sQuery(id+"F0.wireOp",EDGE,"E7.12.0"),sQuery(id+"F0.wireOp",EDGE,"E7.12.1"),sQuery(id+"F0.wireOp",EDGE,"E7.12.2"),sQuery(id+"F0.wireOp",EDGE,"E7.12.3"),sQuery(id+"F0.wireOp",EDGE,"E7.12.4"),sQuery(id+"F0.wireOp",EDGE,"E7.12.5"),sQuery(id+"F0.wireOp",EDGE,"E7.13.0"),sQuery(id+"F0.wireOp",EDGE,"E7.13.1"),sQuery(id+"F0.wireOp",EDGE,"E7.13.2"),sQuery(id+"F0.wireOp",EDGE,"E7.13.3"),sQuery(id+"F0.wireOp",EDGE,"E7.13.4"),sQuery(id+"F0.wireOp",EDGE,"E7.13.5"),sQuery(id+"F0.wireOp",EDGE,"E7.14.0"),sQuery(id+"F0.wireOp",EDGE,"E7.14.1"),sQuery(id+"F0.wireOp",EDGE,"E7.14.2"),sQuery(id+"F0.wireOp",EDGE,"E7.14.3"),sQuery(id+"F0.wireOp",EDGE,"E7.14.4"),sQuery(id+"F0.wireOp",EDGE,"E7.14.5"),sQuery(id+"F0.wireOp",EDGE,"E7.15.0"),sQuery(id+"F0.wireOp",EDGE,"E7.15.1"),sQuery(id+"F0.wireOp",EDGE,"E7.15.2"),sQuery(id+"F0.wireOp",EDGE,"E7.15.3"),sQuery(id+"F0.wireOp",EDGE,"E7.15.4"),sQuery(id+"F0.wireOp",EDGE,"E7.15.5"),sQuery(id+"F0.wireOp",EDGE,"E7.16.0"),sQuery(id+"F0.wireOp",EDGE,"E7.16.1"),sQuery(id+"F0.wireOp",EDGE,"E7.16.2"),sQuery(id+"F0.wireOp",EDGE,"E7.16.3"),sQuery(id+"F0.wireOp",EDGE,"E7.16.4"),sQuery(id+"F0.wireOp",EDGE,"E7.16.5"),sQuery(id+"F0.wireOp",EDGE,"E7.17.0"),sQuery(id+"F0.wireOp",EDGE,"E7.17.1"),sQuery(id+"F0.wireOp",EDGE,"E7.17.2"),sQuery(id+"F0.wireOp",EDGE,"E7.17.3"),sQuery(id+"F0.wireOp",EDGE,"E7.17.4"),sQuery(id+"F0.wireOp",EDGE,"E7.17.5"),subQ0,sQuery(id+"F0.wireOp",EDGE,"E7.18.1"),sQuery(id+"F0.wireOp",EDGE,"E7.18.2"),sQuery(id+"F0.wireOp",EDGE,"E7.18.3"),sQuery(id+"F0.wireOp",EDGE,"E7.18.4"),sQuery(id+"F0.wireOp",EDGE,"E7.18.5"),sQuery(id+"F0.wireOp",EDGE,"E7.19.0"),sQuery(id+"F0.wireOp",EDGE,"E7.19.1"),sQuery(id+"F0.wireOp",EDGE,"E7.19.2"),sQuery(id+"F0.wireOp",EDGE,"E7.19.3"),sQuery(id+"F0.wireOp",EDGE,"E7.19.4"),sQuery(id+"F0.wireOp",EDGE,"E7.19.5"),sQuery(id+"F0.wireOp",EDGE,"E7.20.0"),sQuery(id+"F0.wireOp",EDGE,"E7.20.1"),sQuery(id+"F0.wireOp",EDGE,"E7.20.2"),sQuery(id+"F0.wireOp",EDGE,"E7.20.3"),sQuery(id+"F0.wireOp",EDGE,"E7.20.4"),sQuery(id+"F0.wireOp",EDGE,"E7.20.5"),sQuery(id+"F0.wireOp",EDGE,"E7.21.0"),sQuery(id+"F0.wireOp",EDGE,"E7.21.1"),sQuery(id+"F0.wireOp",EDGE,"E7.21.2"),sQuery(id+"F0.wireOp",EDGE,"E7.21.3"),sQuery(id+"F0.wireOp",EDGE,"E7.21.4"),sQuery(id+"F0.wireOp",EDGE,"E7.21.5"),sQuery(id+"F0.wireOp",EDGE,"E7.22.0"),sQuery(id+"F0.wireOp",EDGE,"E7.22.1"),sQuery(id+"F0.wireOp",EDGE,"E7.22.2"),sQuery(id+"F0.wireOp",EDGE,"E7.22.3"),sQuery(id+"F0.wireOp",EDGE,"E7.22.4"),sQuery(id+"F0.wireOp",EDGE,"E7.22.5"),sQuery(id+"F0.wireOp",EDGE,"E7.23.0"),sQuery(id+"F0.wireOp",EDGE,"E7.23.1"),sQuery(id+"F0.wireOp",EDGE,"E7.23.2"),sQuery(id+"F0.wireOp",EDGE,"E7.23.3"),sQuery(id+"F0.wireOp",EDGE,"E7.23.4"),sQuery(id+"F0.wireOp",EDGE,"E7.23.5"),sQuery(id+"F0.wireOp",EDGE,"E7.24.0"),sQuery(id+"F0.wireOp",EDGE,"E7.24.1"),sQuery(id+"F0.wireOp",EDGE,"E7.24.2"),sQuery(id+"F0.wireOp",EDGE,"E7.24.3"),sQuery(id+"F0.wireOp",EDGE,"E7.24.4"),sQuery(id+"F0.wireOp",EDGE,"E7.24.5"),sQuery(id+"F0.wireOp",EDGE,"E7.25.0"),sQuery(id+"F0.wireOp",EDGE,"E7.25.1"),sQuery(id+"F0.wireOp",EDGE,"E7.25.2"),sQuery(id+"F0.wireOp",EDGE,"E7.25.3"),sQuery(id+"F0.wireOp",EDGE,"E7.25.4"),sQuery(id+"F0.wireOp",EDGE,"E7.25.5"),sQuery(id+"F0.wireOp",EDGE,"E7.26.0"),sQuery(id+"F0.wireOp",EDGE,"E7.26.1"),sQuery(id+"F0.wireOp",EDGE,"E7.26.2"),sQuery(id+"F0.wireOp",EDGE,"E7.26.3"),sQuery(id+"F0.wireOp",EDGE,"E7.26.4"),sQuery(id+"F0.wireOp",EDGE,"E7.26.5"),sQuery(id+"F0.wireOp",EDGE,"E7.27.0"),sQuery(id+"F0.wireOp",EDGE,"E7.27.1"),sQuery(id+"F0.wireOp",EDGE,"E7.27.2"),sQuery(id+"F0.wireOp",EDGE,"E7.27.3"),sQuery(id+"F0.wireOp",EDGE,"E7.27.4"),sQuery(id+"F0.wireOp",EDGE,"E7.27.5"),sQuery(id+"F0.wireOp",EDGE,"E7.28.0"),sQuery(id+"F0.wireOp",EDGE,"E7.28.1"),sQuery(id+"F0.wireOp",EDGE,"E7.28.2"),sQuery(id+"F0.wireOp",EDGE,"E7.28.3"),sQuery(id+"F0.wireOp",EDGE,"E7.28.4"),sQuery(id+"F0.wireOp",EDGE,"E7.28.5"),sQuery(id+"F0.wireOp",EDGE,"E7.29.0"),sQuery(id+"F0.wireOp",EDGE,"E7.29.1"),sQuery(id+"F0.wireOp",EDGE,"E7.29.2"),sQuery(id+"F0.wireOp",EDGE,"E7.29.3"),sQuery(id+"F0.wireOp",EDGE,"E7.29.4"),sQuery(id+"F0.wireOp",EDGE,"E7.29.5"),sQuery(id+"F0.wireOp",EDGE,"E7.30.0"),sQuery(id+"F0.wireOp",EDGE,"E7.30.1"),sQuery(id+"F0.wireOp",EDGE,"E7.30.2"),sQuery(id+"F0.wireOp",EDGE,"E7.30.3"),sQuery(id+"F0.wireOp",EDGE,"E7.30.4"),sQuery(id+"F0.wireOp",EDGE,"E7.30.5"),sQuery(id+"F0.wireOp",EDGE,"E7.31.0"),sQuery(id+"F0.wireOp",EDGE,"E7.31.1"),sQuery(id+"F0.wireOp",EDGE,"E7.31.2"),sQuery(id+"F0.wireOp",EDGE,"E7.31.3"),sQuery(id+"F0.wireOp",EDGE,"E7.31.4"),sQuery(id+"F0.wireOp",EDGE,"E7.31.5"),sQuery(id+"F0.wireOp",EDGE,"E7.32.0"),sQuery(id+"F0.wireOp",EDGE,"E7.32.1"),sQuery(id+"F0.wireOp",EDGE,"E7.32.2"),sQuery(id+"F0.wireOp",EDGE,"E7.32.3"),sQuery(id+"F0.wireOp",EDGE,"E7.32.4"),sQuery(id+"F0.wireOp",EDGE,"E7.32.5"),sQuery(id+"F0.wireOp",EDGE,"E7.33.0"),sQuery(id+"F0.wireOp",EDGE,"E7.33.1"),sQuery(id+"F0.wireOp",EDGE,"E7.33.2"),sQuery(id+"F0.wireOp",EDGE,"E7.33.3"),sQuery(id+"F0.wireOp",EDGE,"E7.33.4"),sQuery(id+"F0.wireOp",EDGE,"E7.33.5"),sQuery(id+"F0.wireOp",EDGE,"E7.34.0"),sQuery(id+"F0.wireOp",EDGE,"E7.34.1"),sQuery(id+"F0.wireOp",EDGE,"E7.34.2"),sQuery(id+"F0.wireOp",EDGE,"E7.34.3"),sQuery(id+"F0.wireOp",EDGE,"E7.34.4"),sQuery(id+"F0.wireOp",EDGE,"E7.34.5"),sQuery(id+"F0.wireOp",EDGE,"E7.35.0"),sQuery(id+"F0.wireOp",EDGE,"E7.35.1"),sQuery(id+"F0.wireOp",EDGE,"E7.35.2"),sQuery(id+"F0.wireOp",EDGE,"E7.35.3"),sQuery(id+"F0.wireOp",EDGE,"E7.35.4"),sQuery(id+"F0.wireOp",EDGE,"E7.35.5"),sQuery(id+"F0.wireOp",EDGE,"E7.36.0"),sQuery(id+"F0.wireOp",EDGE,"E7.36.1"),sQuery(id+"F0.wireOp",EDGE,"E7.36.2"),sQuery(id+"F0.wireOp",EDGE,"E7.36.3"),sQuery(id+"F0.wireOp",EDGE,"E7.36.4"),sQuery(id+"F0.wireOp",EDGE,"E7.36.5"),sQuery(id+"F0.wireOp",EDGE,"E7.37.0"),sQuery(id+"F0.wireOp",EDGE,"E7.37.1"),sQuery(id+"F0.wireOp",EDGE,"E7.37.2"),sQuery(id+"F0.wireOp",EDGE,"E7.37.3"),sQuery(id+"F0.wireOp",EDGE,"E7.37.4"),sQuery(id+"F0.wireOp",EDGE,"E7.37.5"),sQuery(id+"F0.wireOp",EDGE,"E7.38.0"),sQuery(id+"F0.wireOp",EDGE,"E7.38.1"),sQuery(id+"F0.wireOp",EDGE,"E7.38.2"),sQuery(id+"F0.wireOp",EDGE,"E7.38.3"),sQuery(id+"F0.wireOp",EDGE,"E7.38.4"),sQuery(id+"F0.wireOp",EDGE,"E7.38.5"),sQuery(id+"F0.wireOp",EDGE,"E7.39.0"),sQuery(id+"F0.wireOp",EDGE,"E7.39.1"),sQuery(id+"F0.wireOp",EDGE,"E7.39.2"),sQuery(id+"F0.wireOp",EDGE,"E7.39.3"),sQuery(id+"F0.wireOp",EDGE,"E7.39.4"),sQuery(id+"F0.wireOp",EDGE,"E7.39.5"),sQuery(id+"F0.wireOp",EDGE,"E7.40.0"),sQuery(id+"F0.wireOp",EDGE,"E7.40.1"),sQuery(id+"F0.wireOp",EDGE,"E7.40.2"),sQuery(id+"F0.wireOp",EDGE,"E7.40.3"),sQuery(id+"F0.wireOp",EDGE,"E7.40.4"),sQuery(id+"F0.wireOp",EDGE,"E7.40.5"),sQuery(id+"F0.wireOp",EDGE,"E7.41.0"),sQuery(id+"F0.wireOp",EDGE,"E7.41.1"),sQuery(id+"F0.wireOp",EDGE,"E7.41.2"),sQuery(id+"F0.wireOp",EDGE,"E7.41.3"),sQuery(id+"F0.wireOp",EDGE,"E7.41.4"),sQuery(id+"F0.wireOp",EDGE,"E7.41.5"),sQuery(id+"F0.wireOp",EDGE,"E7.42.0"),sQuery(id+"F0.wireOp",EDGE,"E7.42.1"),sQuery(id+"F0.wireOp",EDGE,"E7.42.2"),sQuery(id+"F0.wireOp",EDGE,"E7.42.3"),sQuery(id+"F0.wireOp",EDGE,"E7.42.4"),sQuery(id+"F0.wireOp",EDGE,"E7.42.5"),sQuery(id+"F0.wireOp",EDGE,"E7.43.0"),sQuery(id+"F0.wireOp",EDGE,"E7.43.1"),sQuery(id+"F0.wireOp",EDGE,"E7.43.2"),sQuery(id+"F0.wireOp",EDGE,"E7.43.3"),sQuery(id+"F0.wireOp",EDGE,"E7.43.4"),sQuery(id+"F0.wireOp",EDGE,"E7.43.5")])],"isStart":true})]});}
            var Q31;
            {var subQ0=sQuery(id+"F0.wireOp",EDGE,"E7.20.0");Q31=makeQuery(id+"F2.opChamfer","BLEND_EDGE",EDGE,{"blendedFrom":[makeQuery(id+"F1.opExtrude","CAP_EDGE",EDGE,{"disambiguationData":[OSD([subQ0])],"isStart":true}),makeQuery(id+"F1.opExtrude","CAP_FACE",FACE,{"disambiguationData":[OSD([sQuery(id+"F0.wireOp",EDGE,"E1"),sQuery(id+"F0.wireOp",EDGE,"E2"),sQuery(id+"F0.wireOp",EDGE,"E3"),sQuery(id+"F0.wireOp",EDGE,"E4"),sQuery(id+"F0.wireOp",EDGE,"E5"),sQuery(id+"F0.wireOp",EDGE,"E6"),sQuery(id+"F0.wireOp",EDGE,"E7.1.0"),sQuery(id+"F0.wireOp",EDGE,"E7.1.1"),sQuery(id+"F0.wireOp",EDGE,"E7.1.2"),sQuery(id+"F0.wireOp",EDGE,"E7.1.3"),sQuery(id+"F0.wireOp",EDGE,"E7.1.4"),sQuery(id+"F0.wireOp",EDGE,"E7.1.5"),sQuery(id+"F0.wireOp",EDGE,"E7.2.0"),sQuery(id+"F0.wireOp",EDGE,"E7.2.1"),sQuery(id+"F0.wireOp",EDGE,"E7.2.2"),sQuery(id+"F0.wireOp",EDGE,"E7.2.3"),sQuery(id+"F0.wireOp",EDGE,"E7.2.4"),sQuery(id+"F0.wireOp",EDGE,"E7.2.5"),sQuery(id+"F0.wireOp",EDGE,"E7.3.0"),sQuery(id+"F0.wireOp",EDGE,"E7.3.1"),sQuery(id+"F0.wireOp",EDGE,"E7.3.2"),sQuery(id+"F0.wireOp",EDGE,"E7.3.3"),sQuery(id+"F0.wireOp",EDGE,"E7.3.4"),sQuery(id+"F0.wireOp",EDGE,"E7.3.5"),sQuery(id+"F0.wireOp",EDGE,"E7.4.0"),sQuery(id+"F0.wireOp",EDGE,"E7.4.1"),sQuery(id+"F0.wireOp",EDGE,"E7.4.2"),sQuery(id+"F0.wireOp",EDGE,"E7.4.3"),sQuery(id+"F0.wireOp",EDGE,"E7.4.4"),sQuery(id+"F0.wireOp",EDGE,"E7.4.5"),sQuery(id+"F0.wireOp",EDGE,"E7.5.0"),sQuery(id+"F0.wireOp",EDGE,"E7.5.1"),sQuery(id+"F0.wireOp",EDGE,"E7.5.2"),sQuery(id+"F0.wireOp",EDGE,"E7.5.3"),sQuery(id+"F0.wireOp",EDGE,"E7.5.4"),sQuery(id+"F0.wireOp",EDGE,"E7.5.5"),sQuery(id+"F0.wireOp",EDGE,"E7.6.0"),sQuery(id+"F0.wireOp",EDGE,"E7.6.1"),sQuery(id+"F0.wireOp",EDGE,"E7.6.2"),sQuery(id+"F0.wireOp",EDGE,"E7.6.3"),sQuery(id+"F0.wireOp",EDGE,"E7.6.4"),sQuery(id+"F0.wireOp",EDGE,"E7.6.5"),sQuery(id+"F0.wireOp",EDGE,"E7.7.0"),sQuery(id+"F0.wireOp",EDGE,"E7.7.1"),sQuery(id+"F0.wireOp",EDGE,"E7.7.2"),sQuery(id+"F0.wireOp",EDGE,"E7.7.3"),sQuery(id+"F0.wireOp",EDGE,"E7.7.4"),sQuery(id+"F0.wireOp",EDGE,"E7.7.5"),sQuery(id+"F0.wireOp",EDGE,"E7.8.0"),sQuery(id+"F0.wireOp",EDGE,"E7.8.1"),sQuery(id+"F0.wireOp",EDGE,"E7.8.2"),sQuery(id+"F0.wireOp",EDGE,"E7.8.3"),sQuery(id+"F0.wireOp",EDGE,"E7.8.4"),sQuery(id+"F0.wireOp",EDGE,"E7.8.5"),sQuery(id+"F0.wireOp",EDGE,"E7.9.0"),sQuery(id+"F0.wireOp",EDGE,"E7.9.1"),sQuery(id+"F0.wireOp",EDGE,"E7.9.2"),sQuery(id+"F0.wireOp",EDGE,"E7.9.3"),sQuery(id+"F0.wireOp",EDGE,"E7.9.4"),sQuery(id+"F0.wireOp",EDGE,"E7.9.5"),sQuery(id+"F0.wireOp",EDGE,"E7.10.0"),sQuery(id+"F0.wireOp",EDGE,"E7.10.1"),sQuery(id+"F0.wireOp",EDGE,"E7.10.2"),sQuery(id+"F0.wireOp",EDGE,"E7.10.3"),sQuery(id+"F0.wireOp",EDGE,"E7.10.4"),sQuery(id+"F0.wireOp",EDGE,"E7.10.5"),sQuery(id+"F0.wireOp",EDGE,"E7.11.0"),sQuery(id+"F0.wireOp",EDGE,"E7.11.1"),sQuery(id+"F0.wireOp",EDGE,"E7.11.2"),sQuery(id+"F0.wireOp",EDGE,"E7.11.3"),sQuery(id+"F0.wireOp",EDGE,"E7.11.4"),sQuery(id+"F0.wireOp",EDGE,"E7.11.5"),sQuery(id+"F0.wireOp",EDGE,"E7.12.0"),sQuery(id+"F0.wireOp",EDGE,"E7.12.1"),sQuery(id+"F0.wireOp",EDGE,"E7.12.2"),sQuery(id+"F0.wireOp",EDGE,"E7.12.3"),sQuery(id+"F0.wireOp",EDGE,"E7.12.4"),sQuery(id+"F0.wireOp",EDGE,"E7.12.5"),sQuery(id+"F0.wireOp",EDGE,"E7.13.0"),sQuery(id+"F0.wireOp",EDGE,"E7.13.1"),sQuery(id+"F0.wireOp",EDGE,"E7.13.2"),sQuery(id+"F0.wireOp",EDGE,"E7.13.3"),sQuery(id+"F0.wireOp",EDGE,"E7.13.4"),sQuery(id+"F0.wireOp",EDGE,"E7.13.5"),sQuery(id+"F0.wireOp",EDGE,"E7.14.0"),sQuery(id+"F0.wireOp",EDGE,"E7.14.1"),sQuery(id+"F0.wireOp",EDGE,"E7.14.2"),sQuery(id+"F0.wireOp",EDGE,"E7.14.3"),sQuery(id+"F0.wireOp",EDGE,"E7.14.4"),sQuery(id+"F0.wireOp",EDGE,"E7.14.5"),sQuery(id+"F0.wireOp",EDGE,"E7.15.0"),sQuery(id+"F0.wireOp",EDGE,"E7.15.1"),sQuery(id+"F0.wireOp",EDGE,"E7.15.2"),sQuery(id+"F0.wireOp",EDGE,"E7.15.3"),sQuery(id+"F0.wireOp",EDGE,"E7.15.4"),sQuery(id+"F0.wireOp",EDGE,"E7.15.5"),sQuery(id+"F0.wireOp",EDGE,"E7.16.0"),sQuery(id+"F0.wireOp",EDGE,"E7.16.1"),sQuery(id+"F0.wireOp",EDGE,"E7.16.2"),sQuery(id+"F0.wireOp",EDGE,"E7.16.3"),sQuery(id+"F0.wireOp",EDGE,"E7.16.4"),sQuery(id+"F0.wireOp",EDGE,"E7.16.5"),sQuery(id+"F0.wireOp",EDGE,"E7.17.0"),sQuery(id+"F0.wireOp",EDGE,"E7.17.1"),sQuery(id+"F0.wireOp",EDGE,"E7.17.2"),sQuery(id+"F0.wireOp",EDGE,"E7.17.3"),sQuery(id+"F0.wireOp",EDGE,"E7.17.4"),sQuery(id+"F0.wireOp",EDGE,"E7.17.5"),sQuery(id+"F0.wireOp",EDGE,"E7.18.0"),sQuery(id+"F0.wireOp",EDGE,"E7.18.1"),sQuery(id+"F0.wireOp",EDGE,"E7.18.2"),sQuery(id+"F0.wireOp",EDGE,"E7.18.3"),sQuery(id+"F0.wireOp",EDGE,"E7.18.4"),sQuery(id+"F0.wireOp",EDGE,"E7.18.5"),sQuery(id+"F0.wireOp",EDGE,"E7.19.0"),sQuery(id+"F0.wireOp",EDGE,"E7.19.1"),sQuery(id+"F0.wireOp",EDGE,"E7.19.2"),sQuery(id+"F0.wireOp",EDGE,"E7.19.3"),sQuery(id+"F0.wireOp",EDGE,"E7.19.4"),sQuery(id+"F0.wireOp",EDGE,"E7.19.5"),subQ0,sQuery(id+"F0.wireOp",EDGE,"E7.20.1"),sQuery(id+"F0.wireOp",EDGE,"E7.20.2"),sQuery(id+"F0.wireOp",EDGE,"E7.20.3"),sQuery(id+"F0.wireOp",EDGE,"E7.20.4"),sQuery(id+"F0.wireOp",EDGE,"E7.20.5"),sQuery(id+"F0.wireOp",EDGE,"E7.21.0"),sQuery(id+"F0.wireOp",EDGE,"E7.21.1"),sQuery(id+"F0.wireOp",EDGE,"E7.21.2"),sQuery(id+"F0.wireOp",EDGE,"E7.21.3"),sQuery(id+"F0.wireOp",EDGE,"E7.21.4"),sQuery(id+"F0.wireOp",EDGE,"E7.21.5"),sQuery(id+"F0.wireOp",EDGE,"E7.22.0"),sQuery(id+"F0.wireOp",EDGE,"E7.22.1"),sQuery(id+"F0.wireOp",EDGE,"E7.22.2"),sQuery(id+"F0.wireOp",EDGE,"E7.22.3"),sQuery(id+"F0.wireOp",EDGE,"E7.22.4"),sQuery(id+"F0.wireOp",EDGE,"E7.22.5"),sQuery(id+"F0.wireOp",EDGE,"E7.23.0"),sQuery(id+"F0.wireOp",EDGE,"E7.23.1"),sQuery(id+"F0.wireOp",EDGE,"E7.23.2"),sQuery(id+"F0.wireOp",EDGE,"E7.23.3"),sQuery(id+"F0.wireOp",EDGE,"E7.23.4"),sQuery(id+"F0.wireOp",EDGE,"E7.23.5"),sQuery(id+"F0.wireOp",EDGE,"E7.24.0"),sQuery(id+"F0.wireOp",EDGE,"E7.24.1"),sQuery(id+"F0.wireOp",EDGE,"E7.24.2"),sQuery(id+"F0.wireOp",EDGE,"E7.24.3"),sQuery(id+"F0.wireOp",EDGE,"E7.24.4"),sQuery(id+"F0.wireOp",EDGE,"E7.24.5"),sQuery(id+"F0.wireOp",EDGE,"E7.25.0"),sQuery(id+"F0.wireOp",EDGE,"E7.25.1"),sQuery(id+"F0.wireOp",EDGE,"E7.25.2"),sQuery(id+"F0.wireOp",EDGE,"E7.25.3"),sQuery(id+"F0.wireOp",EDGE,"E7.25.4"),sQuery(id+"F0.wireOp",EDGE,"E7.25.5"),sQuery(id+"F0.wireOp",EDGE,"E7.26.0"),sQuery(id+"F0.wireOp",EDGE,"E7.26.1"),sQuery(id+"F0.wireOp",EDGE,"E7.26.2"),sQuery(id+"F0.wireOp",EDGE,"E7.26.3"),sQuery(id+"F0.wireOp",EDGE,"E7.26.4"),sQuery(id+"F0.wireOp",EDGE,"E7.26.5"),sQuery(id+"F0.wireOp",EDGE,"E7.27.0"),sQuery(id+"F0.wireOp",EDGE,"E7.27.1"),sQuery(id+"F0.wireOp",EDGE,"E7.27.2"),sQuery(id+"F0.wireOp",EDGE,"E7.27.3"),sQuery(id+"F0.wireOp",EDGE,"E7.27.4"),sQuery(id+"F0.wireOp",EDGE,"E7.27.5"),sQuery(id+"F0.wireOp",EDGE,"E7.28.0"),sQuery(id+"F0.wireOp",EDGE,"E7.28.1"),sQuery(id+"F0.wireOp",EDGE,"E7.28.2"),sQuery(id+"F0.wireOp",EDGE,"E7.28.3"),sQuery(id+"F0.wireOp",EDGE,"E7.28.4"),sQuery(id+"F0.wireOp",EDGE,"E7.28.5"),sQuery(id+"F0.wireOp",EDGE,"E7.29.0"),sQuery(id+"F0.wireOp",EDGE,"E7.29.1"),sQuery(id+"F0.wireOp",EDGE,"E7.29.2"),sQuery(id+"F0.wireOp",EDGE,"E7.29.3"),sQuery(id+"F0.wireOp",EDGE,"E7.29.4"),sQuery(id+"F0.wireOp",EDGE,"E7.29.5"),sQuery(id+"F0.wireOp",EDGE,"E7.30.0"),sQuery(id+"F0.wireOp",EDGE,"E7.30.1"),sQuery(id+"F0.wireOp",EDGE,"E7.30.2"),sQuery(id+"F0.wireOp",EDGE,"E7.30.3"),sQuery(id+"F0.wireOp",EDGE,"E7.30.4"),sQuery(id+"F0.wireOp",EDGE,"E7.30.5"),sQuery(id+"F0.wireOp",EDGE,"E7.31.0"),sQuery(id+"F0.wireOp",EDGE,"E7.31.1"),sQuery(id+"F0.wireOp",EDGE,"E7.31.2"),sQuery(id+"F0.wireOp",EDGE,"E7.31.3"),sQuery(id+"F0.wireOp",EDGE,"E7.31.4"),sQuery(id+"F0.wireOp",EDGE,"E7.31.5"),sQuery(id+"F0.wireOp",EDGE,"E7.32.0"),sQuery(id+"F0.wireOp",EDGE,"E7.32.1"),sQuery(id+"F0.wireOp",EDGE,"E7.32.2"),sQuery(id+"F0.wireOp",EDGE,"E7.32.3"),sQuery(id+"F0.wireOp",EDGE,"E7.32.4"),sQuery(id+"F0.wireOp",EDGE,"E7.32.5"),sQuery(id+"F0.wireOp",EDGE,"E7.33.0"),sQuery(id+"F0.wireOp",EDGE,"E7.33.1"),sQuery(id+"F0.wireOp",EDGE,"E7.33.2"),sQuery(id+"F0.wireOp",EDGE,"E7.33.3"),sQuery(id+"F0.wireOp",EDGE,"E7.33.4"),sQuery(id+"F0.wireOp",EDGE,"E7.33.5"),sQuery(id+"F0.wireOp",EDGE,"E7.34.0"),sQuery(id+"F0.wireOp",EDGE,"E7.34.1"),sQuery(id+"F0.wireOp",EDGE,"E7.34.2"),sQuery(id+"F0.wireOp",EDGE,"E7.34.3"),sQuery(id+"F0.wireOp",EDGE,"E7.34.4"),sQuery(id+"F0.wireOp",EDGE,"E7.34.5"),sQuery(id+"F0.wireOp",EDGE,"E7.35.0"),sQuery(id+"F0.wireOp",EDGE,"E7.35.1"),sQuery(id+"F0.wireOp",EDGE,"E7.35.2"),sQuery(id+"F0.wireOp",EDGE,"E7.35.3"),sQuery(id+"F0.wireOp",EDGE,"E7.35.4"),sQuery(id+"F0.wireOp",EDGE,"E7.35.5"),sQuery(id+"F0.wireOp",EDGE,"E7.36.0"),sQuery(id+"F0.wireOp",EDGE,"E7.36.1"),sQuery(id+"F0.wireOp",EDGE,"E7.36.2"),sQuery(id+"F0.wireOp",EDGE,"E7.36.3"),sQuery(id+"F0.wireOp",EDGE,"E7.36.4"),sQuery(id+"F0.wireOp",EDGE,"E7.36.5"),sQuery(id+"F0.wireOp",EDGE,"E7.37.0"),sQuery(id+"F0.wireOp",EDGE,"E7.37.1"),sQuery(id+"F0.wireOp",EDGE,"E7.37.2"),sQuery(id+"F0.wireOp",EDGE,"E7.37.3"),sQuery(id+"F0.wireOp",EDGE,"E7.37.4"),sQuery(id+"F0.wireOp",EDGE,"E7.37.5"),sQuery(id+"F0.wireOp",EDGE,"E7.38.0"),sQuery(id+"F0.wireOp",EDGE,"E7.38.1"),sQuery(id+"F0.wireOp",EDGE,"E7.38.2"),sQuery(id+"F0.wireOp",EDGE,"E7.38.3"),sQuery(id+"F0.wireOp",EDGE,"E7.38.4"),sQuery(id+"F0.wireOp",EDGE,"E7.38.5"),sQuery(id+"F0.wireOp",EDGE,"E7.39.0"),sQuery(id+"F0.wireOp",EDGE,"E7.39.1"),sQuery(id+"F0.wireOp",EDGE,"E7.39.2"),sQuery(id+"F0.wireOp",EDGE,"E7.39.3"),sQuery(id+"F0.wireOp",EDGE,"E7.39.4"),sQuery(id+"F0.wireOp",EDGE,"E7.39.5"),sQuery(id+"F0.wireOp",EDGE,"E7.40.0"),sQuery(id+"F0.wireOp",EDGE,"E7.40.1"),sQuery(id+"F0.wireOp",EDGE,"E7.40.2"),sQuery(id+"F0.wireOp",EDGE,"E7.40.3"),sQuery(id+"F0.wireOp",EDGE,"E7.40.4"),sQuery(id+"F0.wireOp",EDGE,"E7.40.5"),sQuery(id+"F0.wireOp",EDGE,"E7.41.0"),sQuery(id+"F0.wireOp",EDGE,"E7.41.1"),sQuery(id+"F0.wireOp",EDGE,"E7.41.2"),sQuery(id+"F0.wireOp",EDGE,"E7.41.3"),sQuery(id+"F0.wireOp",EDGE,"E7.41.4"),sQuery(id+"F0.wireOp",EDGE,"E7.41.5"),sQuery(id+"F0.wireOp",EDGE,"E7.42.0"),sQuery(id+"F0.wireOp",EDGE,"E7.42.1"),sQuery(id+"F0.wireOp",EDGE,"E7.42.2"),sQuery(id+"F0.wireOp",EDGE,"E7.42.3"),sQuery(id+"F0.wireOp",EDGE,"E7.42.4"),sQuery(id+"F0.wireOp",EDGE,"E7.42.5"),sQuery(id+"F0.wireOp",EDGE,"E7.43.0"),sQuery(id+"F0.wireOp",EDGE,"E7.43.1"),sQuery(id+"F0.wireOp",EDGE,"E7.43.2"),sQuery(id+"F0.wireOp",EDGE,"E7.43.3"),sQuery(id+"F0.wireOp",EDGE,"E7.43.4"),sQuery(id+"F0.wireOp",EDGE,"E7.43.5")])],"isStart":true})],"blendedInto":[makeQuery(id+"F1.opExtrude","CAP_FACE",FACE,{"disambiguationData":[OSD([sQuery(id+"F0.wireOp",EDGE,"E1"),sQuery(id+"F0.wireOp",EDGE,"E2"),sQuery(id+"F0.wireOp",EDGE,"E3"),sQuery(id+"F0.wireOp",EDGE,"E4"),sQuery(id+"F0.wireOp",EDGE,"E5"),sQuery(id+"F0.wireOp",EDGE,"E6"),sQuery(id+"F0.wireOp",EDGE,"E7.1.0"),sQuery(id+"F0.wireOp",EDGE,"E7.1.1"),sQuery(id+"F0.wireOp",EDGE,"E7.1.2"),sQuery(id+"F0.wireOp",EDGE,"E7.1.3"),sQuery(id+"F0.wireOp",EDGE,"E7.1.4"),sQuery(id+"F0.wireOp",EDGE,"E7.1.5"),sQuery(id+"F0.wireOp",EDGE,"E7.2.0"),sQuery(id+"F0.wireOp",EDGE,"E7.2.1"),sQuery(id+"F0.wireOp",EDGE,"E7.2.2"),sQuery(id+"F0.wireOp",EDGE,"E7.2.3"),sQuery(id+"F0.wireOp",EDGE,"E7.2.4"),sQuery(id+"F0.wireOp",EDGE,"E7.2.5"),sQuery(id+"F0.wireOp",EDGE,"E7.3.0"),sQuery(id+"F0.wireOp",EDGE,"E7.3.1"),sQuery(id+"F0.wireOp",EDGE,"E7.3.2"),sQuery(id+"F0.wireOp",EDGE,"E7.3.3"),sQuery(id+"F0.wireOp",EDGE,"E7.3.4"),sQuery(id+"F0.wireOp",EDGE,"E7.3.5"),sQuery(id+"F0.wireOp",EDGE,"E7.4.0"),sQuery(id+"F0.wireOp",EDGE,"E7.4.1"),sQuery(id+"F0.wireOp",EDGE,"E7.4.2"),sQuery(id+"F0.wireOp",EDGE,"E7.4.3"),sQuery(id+"F0.wireOp",EDGE,"E7.4.4"),sQuery(id+"F0.wireOp",EDGE,"E7.4.5"),sQuery(id+"F0.wireOp",EDGE,"E7.5.0"),sQuery(id+"F0.wireOp",EDGE,"E7.5.1"),sQuery(id+"F0.wireOp",EDGE,"E7.5.2"),sQuery(id+"F0.wireOp",EDGE,"E7.5.3"),sQuery(id+"F0.wireOp",EDGE,"E7.5.4"),sQuery(id+"F0.wireOp",EDGE,"E7.5.5"),sQuery(id+"F0.wireOp",EDGE,"E7.6.0"),sQuery(id+"F0.wireOp",EDGE,"E7.6.1"),sQuery(id+"F0.wireOp",EDGE,"E7.6.2"),sQuery(id+"F0.wireOp",EDGE,"E7.6.3"),sQuery(id+"F0.wireOp",EDGE,"E7.6.4"),sQuery(id+"F0.wireOp",EDGE,"E7.6.5"),sQuery(id+"F0.wireOp",EDGE,"E7.7.0"),sQuery(id+"F0.wireOp",EDGE,"E7.7.1"),sQuery(id+"F0.wireOp",EDGE,"E7.7.2"),sQuery(id+"F0.wireOp",EDGE,"E7.7.3"),sQuery(id+"F0.wireOp",EDGE,"E7.7.4"),sQuery(id+"F0.wireOp",EDGE,"E7.7.5"),sQuery(id+"F0.wireOp",EDGE,"E7.8.0"),sQuery(id+"F0.wireOp",EDGE,"E7.8.1"),sQuery(id+"F0.wireOp",EDGE,"E7.8.2"),sQuery(id+"F0.wireOp",EDGE,"E7.8.3"),sQuery(id+"F0.wireOp",EDGE,"E7.8.4"),sQuery(id+"F0.wireOp",EDGE,"E7.8.5"),sQuery(id+"F0.wireOp",EDGE,"E7.9.0"),sQuery(id+"F0.wireOp",EDGE,"E7.9.1"),sQuery(id+"F0.wireOp",EDGE,"E7.9.2"),sQuery(id+"F0.wireOp",EDGE,"E7.9.3"),sQuery(id+"F0.wireOp",EDGE,"E7.9.4"),sQuery(id+"F0.wireOp",EDGE,"E7.9.5"),sQuery(id+"F0.wireOp",EDGE,"E7.10.0"),sQuery(id+"F0.wireOp",EDGE,"E7.10.1"),sQuery(id+"F0.wireOp",EDGE,"E7.10.2"),sQuery(id+"F0.wireOp",EDGE,"E7.10.3"),sQuery(id+"F0.wireOp",EDGE,"E7.10.4"),sQuery(id+"F0.wireOp",EDGE,"E7.10.5"),sQuery(id+"F0.wireOp",EDGE,"E7.11.0"),sQuery(id+"F0.wireOp",EDGE,"E7.11.1"),sQuery(id+"F0.wireOp",EDGE,"E7.11.2"),sQuery(id+"F0.wireOp",EDGE,"E7.11.3"),sQuery(id+"F0.wireOp",EDGE,"E7.11.4"),sQuery(id+"F0.wireOp",EDGE,"E7.11.5"),sQuery(id+"F0.wireOp",EDGE,"E7.12.0"),sQuery(id+"F0.wireOp",EDGE,"E7.12.1"),sQuery(id+"F0.wireOp",EDGE,"E7.12.2"),sQuery(id+"F0.wireOp",EDGE,"E7.12.3"),sQuery(id+"F0.wireOp",EDGE,"E7.12.4"),sQuery(id+"F0.wireOp",EDGE,"E7.12.5"),sQuery(id+"F0.wireOp",EDGE,"E7.13.0"),sQuery(id+"F0.wireOp",EDGE,"E7.13.1"),sQuery(id+"F0.wireOp",EDGE,"E7.13.2"),sQuery(id+"F0.wireOp",EDGE,"E7.13.3"),sQuery(id+"F0.wireOp",EDGE,"E7.13.4"),sQuery(id+"F0.wireOp",EDGE,"E7.13.5"),sQuery(id+"F0.wireOp",EDGE,"E7.14.0"),sQuery(id+"F0.wireOp",EDGE,"E7.14.1"),sQuery(id+"F0.wireOp",EDGE,"E7.14.2"),sQuery(id+"F0.wireOp",EDGE,"E7.14.3"),sQuery(id+"F0.wireOp",EDGE,"E7.14.4"),sQuery(id+"F0.wireOp",EDGE,"E7.14.5"),sQuery(id+"F0.wireOp",EDGE,"E7.15.0"),sQuery(id+"F0.wireOp",EDGE,"E7.15.1"),sQuery(id+"F0.wireOp",EDGE,"E7.15.2"),sQuery(id+"F0.wireOp",EDGE,"E7.15.3"),sQuery(id+"F0.wireOp",EDGE,"E7.15.4"),sQuery(id+"F0.wireOp",EDGE,"E7.15.5"),sQuery(id+"F0.wireOp",EDGE,"E7.16.0"),sQuery(id+"F0.wireOp",EDGE,"E7.16.1"),sQuery(id+"F0.wireOp",EDGE,"E7.16.2"),sQuery(id+"F0.wireOp",EDGE,"E7.16.3"),sQuery(id+"F0.wireOp",EDGE,"E7.16.4"),sQuery(id+"F0.wireOp",EDGE,"E7.16.5"),sQuery(id+"F0.wireOp",EDGE,"E7.17.0"),sQuery(id+"F0.wireOp",EDGE,"E7.17.1"),sQuery(id+"F0.wireOp",EDGE,"E7.17.2"),sQuery(id+"F0.wireOp",EDGE,"E7.17.3"),sQuery(id+"F0.wireOp",EDGE,"E7.17.4"),sQuery(id+"F0.wireOp",EDGE,"E7.17.5"),sQuery(id+"F0.wireOp",EDGE,"E7.18.0"),sQuery(id+"F0.wireOp",EDGE,"E7.18.1"),sQuery(id+"F0.wireOp",EDGE,"E7.18.2"),sQuery(id+"F0.wireOp",EDGE,"E7.18.3"),sQuery(id+"F0.wireOp",EDGE,"E7.18.4"),sQuery(id+"F0.wireOp",EDGE,"E7.18.5"),sQuery(id+"F0.wireOp",EDGE,"E7.19.0"),sQuery(id+"F0.wireOp",EDGE,"E7.19.1"),sQuery(id+"F0.wireOp",EDGE,"E7.19.2"),sQuery(id+"F0.wireOp",EDGE,"E7.19.3"),sQuery(id+"F0.wireOp",EDGE,"E7.19.4"),sQuery(id+"F0.wireOp",EDGE,"E7.19.5"),subQ0,sQuery(id+"F0.wireOp",EDGE,"E7.20.1"),sQuery(id+"F0.wireOp",EDGE,"E7.20.2"),sQuery(id+"F0.wireOp",EDGE,"E7.20.3"),sQuery(id+"F0.wireOp",EDGE,"E7.20.4"),sQuery(id+"F0.wireOp",EDGE,"E7.20.5"),sQuery(id+"F0.wireOp",EDGE,"E7.21.0"),sQuery(id+"F0.wireOp",EDGE,"E7.21.1"),sQuery(id+"F0.wireOp",EDGE,"E7.21.2"),sQuery(id+"F0.wireOp",EDGE,"E7.21.3"),sQuery(id+"F0.wireOp",EDGE,"E7.21.4"),sQuery(id+"F0.wireOp",EDGE,"E7.21.5"),sQuery(id+"F0.wireOp",EDGE,"E7.22.0"),sQuery(id+"F0.wireOp",EDGE,"E7.22.1"),sQuery(id+"F0.wireOp",EDGE,"E7.22.2"),sQuery(id+"F0.wireOp",EDGE,"E7.22.3"),sQuery(id+"F0.wireOp",EDGE,"E7.22.4"),sQuery(id+"F0.wireOp",EDGE,"E7.22.5"),sQuery(id+"F0.wireOp",EDGE,"E7.23.0"),sQuery(id+"F0.wireOp",EDGE,"E7.23.1"),sQuery(id+"F0.wireOp",EDGE,"E7.23.2"),sQuery(id+"F0.wireOp",EDGE,"E7.23.3"),sQuery(id+"F0.wireOp",EDGE,"E7.23.4"),sQuery(id+"F0.wireOp",EDGE,"E7.23.5"),sQuery(id+"F0.wireOp",EDGE,"E7.24.0"),sQuery(id+"F0.wireOp",EDGE,"E7.24.1"),sQuery(id+"F0.wireOp",EDGE,"E7.24.2"),sQuery(id+"F0.wireOp",EDGE,"E7.24.3"),sQuery(id+"F0.wireOp",EDGE,"E7.24.4"),sQuery(id+"F0.wireOp",EDGE,"E7.24.5"),sQuery(id+"F0.wireOp",EDGE,"E7.25.0"),sQuery(id+"F0.wireOp",EDGE,"E7.25.1"),sQuery(id+"F0.wireOp",EDGE,"E7.25.2"),sQuery(id+"F0.wireOp",EDGE,"E7.25.3"),sQuery(id+"F0.wireOp",EDGE,"E7.25.4"),sQuery(id+"F0.wireOp",EDGE,"E7.25.5"),sQuery(id+"F0.wireOp",EDGE,"E7.26.0"),sQuery(id+"F0.wireOp",EDGE,"E7.26.1"),sQuery(id+"F0.wireOp",EDGE,"E7.26.2"),sQuery(id+"F0.wireOp",EDGE,"E7.26.3"),sQuery(id+"F0.wireOp",EDGE,"E7.26.4"),sQuery(id+"F0.wireOp",EDGE,"E7.26.5"),sQuery(id+"F0.wireOp",EDGE,"E7.27.0"),sQuery(id+"F0.wireOp",EDGE,"E7.27.1"),sQuery(id+"F0.wireOp",EDGE,"E7.27.2"),sQuery(id+"F0.wireOp",EDGE,"E7.27.3"),sQuery(id+"F0.wireOp",EDGE,"E7.27.4"),sQuery(id+"F0.wireOp",EDGE,"E7.27.5"),sQuery(id+"F0.wireOp",EDGE,"E7.28.0"),sQuery(id+"F0.wireOp",EDGE,"E7.28.1"),sQuery(id+"F0.wireOp",EDGE,"E7.28.2"),sQuery(id+"F0.wireOp",EDGE,"E7.28.3"),sQuery(id+"F0.wireOp",EDGE,"E7.28.4"),sQuery(id+"F0.wireOp",EDGE,"E7.28.5"),sQuery(id+"F0.wireOp",EDGE,"E7.29.0"),sQuery(id+"F0.wireOp",EDGE,"E7.29.1"),sQuery(id+"F0.wireOp",EDGE,"E7.29.2"),sQuery(id+"F0.wireOp",EDGE,"E7.29.3"),sQuery(id+"F0.wireOp",EDGE,"E7.29.4"),sQuery(id+"F0.wireOp",EDGE,"E7.29.5"),sQuery(id+"F0.wireOp",EDGE,"E7.30.0"),sQuery(id+"F0.wireOp",EDGE,"E7.30.1"),sQuery(id+"F0.wireOp",EDGE,"E7.30.2"),sQuery(id+"F0.wireOp",EDGE,"E7.30.3"),sQuery(id+"F0.wireOp",EDGE,"E7.30.4"),sQuery(id+"F0.wireOp",EDGE,"E7.30.5"),sQuery(id+"F0.wireOp",EDGE,"E7.31.0"),sQuery(id+"F0.wireOp",EDGE,"E7.31.1"),sQuery(id+"F0.wireOp",EDGE,"E7.31.2"),sQuery(id+"F0.wireOp",EDGE,"E7.31.3"),sQuery(id+"F0.wireOp",EDGE,"E7.31.4"),sQuery(id+"F0.wireOp",EDGE,"E7.31.5"),sQuery(id+"F0.wireOp",EDGE,"E7.32.0"),sQuery(id+"F0.wireOp",EDGE,"E7.32.1"),sQuery(id+"F0.wireOp",EDGE,"E7.32.2"),sQuery(id+"F0.wireOp",EDGE,"E7.32.3"),sQuery(id+"F0.wireOp",EDGE,"E7.32.4"),sQuery(id+"F0.wireOp",EDGE,"E7.32.5"),sQuery(id+"F0.wireOp",EDGE,"E7.33.0"),sQuery(id+"F0.wireOp",EDGE,"E7.33.1"),sQuery(id+"F0.wireOp",EDGE,"E7.33.2"),sQuery(id+"F0.wireOp",EDGE,"E7.33.3"),sQuery(id+"F0.wireOp",EDGE,"E7.33.4"),sQuery(id+"F0.wireOp",EDGE,"E7.33.5"),sQuery(id+"F0.wireOp",EDGE,"E7.34.0"),sQuery(id+"F0.wireOp",EDGE,"E7.34.1"),sQuery(id+"F0.wireOp",EDGE,"E7.34.2"),sQuery(id+"F0.wireOp",EDGE,"E7.34.3"),sQuery(id+"F0.wireOp",EDGE,"E7.34.4"),sQuery(id+"F0.wireOp",EDGE,"E7.34.5"),sQuery(id+"F0.wireOp",EDGE,"E7.35.0"),sQuery(id+"F0.wireOp",EDGE,"E7.35.1"),sQuery(id+"F0.wireOp",EDGE,"E7.35.2"),sQuery(id+"F0.wireOp",EDGE,"E7.35.3"),sQuery(id+"F0.wireOp",EDGE,"E7.35.4"),sQuery(id+"F0.wireOp",EDGE,"E7.35.5"),sQuery(id+"F0.wireOp",EDGE,"E7.36.0"),sQuery(id+"F0.wireOp",EDGE,"E7.36.1"),sQuery(id+"F0.wireOp",EDGE,"E7.36.2"),sQuery(id+"F0.wireOp",EDGE,"E7.36.3"),sQuery(id+"F0.wireOp",EDGE,"E7.36.4"),sQuery(id+"F0.wireOp",EDGE,"E7.36.5"),sQuery(id+"F0.wireOp",EDGE,"E7.37.0"),sQuery(id+"F0.wireOp",EDGE,"E7.37.1"),sQuery(id+"F0.wireOp",EDGE,"E7.37.2"),sQuery(id+"F0.wireOp",EDGE,"E7.37.3"),sQuery(id+"F0.wireOp",EDGE,"E7.37.4"),sQuery(id+"F0.wireOp",EDGE,"E7.37.5"),sQuery(id+"F0.wireOp",EDGE,"E7.38.0"),sQuery(id+"F0.wireOp",EDGE,"E7.38.1"),sQuery(id+"F0.wireOp",EDGE,"E7.38.2"),sQuery(id+"F0.wireOp",EDGE,"E7.38.3"),sQuery(id+"F0.wireOp",EDGE,"E7.38.4"),sQuery(id+"F0.wireOp",EDGE,"E7.38.5"),sQuery(id+"F0.wireOp",EDGE,"E7.39.0"),sQuery(id+"F0.wireOp",EDGE,"E7.39.1"),sQuery(id+"F0.wireOp",EDGE,"E7.39.2"),sQuery(id+"F0.wireOp",EDGE,"E7.39.3"),sQuery(id+"F0.wireOp",EDGE,"E7.39.4"),sQuery(id+"F0.wireOp",EDGE,"E7.39.5"),sQuery(id+"F0.wireOp",EDGE,"E7.40.0"),sQuery(id+"F0.wireOp",EDGE,"E7.40.1"),sQuery(id+"F0.wireOp",EDGE,"E7.40.2"),sQuery(id+"F0.wireOp",EDGE,"E7.40.3"),sQuery(id+"F0.wireOp",EDGE,"E7.40.4"),sQuery(id+"F0.wireOp",EDGE,"E7.40.5"),sQuery(id+"F0.wireOp",EDGE,"E7.41.0"),sQuery(id+"F0.wireOp",EDGE,"E7.41.1"),sQuery(id+"F0.wireOp",EDGE,"E7.41.2"),sQuery(id+"F0.wireOp",EDGE,"E7.41.3"),sQuery(id+"F0.wireOp",EDGE,"E7.41.4"),sQuery(id+"F0.wireOp",EDGE,"E7.41.5"),sQuery(id+"F0.wireOp",EDGE,"E7.42.0"),sQuery(id+"F0.wireOp",EDGE,"E7.42.1"),sQuery(id+"F0.wireOp",EDGE,"E7.42.2"),sQuery(id+"F0.wireOp",EDGE,"E7.42.3"),sQuery(id+"F0.wireOp",EDGE,"E7.42.4"),sQuery(id+"F0.wireOp",EDGE,"E7.42.5"),sQuery(id+"F0.wireOp",EDGE,"E7.43.0"),sQuery(id+"F0.wireOp",EDGE,"E7.43.1"),sQuery(id+"F0.wireOp",EDGE,"E7.43.2"),sQuery(id+"F0.wireOp",EDGE,"E7.43.3"),sQuery(id+"F0.wireOp",EDGE,"E7.43.4"),sQuery(id+"F0.wireOp",EDGE,"E7.43.5")])],"isStart":true})]});}
            var Q32;
            {var subQ0=sQuery(id+"F0.wireOp",EDGE,"E7.22.0");Q32=makeQuery(id+"F2.opChamfer","BLEND_EDGE",EDGE,{"blendedFrom":[makeQuery(id+"F1.opExtrude","CAP_EDGE",EDGE,{"disambiguationData":[OSD([subQ0])],"isStart":true}),makeQuery(id+"F1.opExtrude","CAP_FACE",FACE,{"disambiguationData":[OSD([sQuery(id+"F0.wireOp",EDGE,"E1"),sQuery(id+"F0.wireOp",EDGE,"E2"),sQuery(id+"F0.wireOp",EDGE,"E3"),sQuery(id+"F0.wireOp",EDGE,"E4"),sQuery(id+"F0.wireOp",EDGE,"E5"),sQuery(id+"F0.wireOp",EDGE,"E6"),sQuery(id+"F0.wireOp",EDGE,"E7.1.0"),sQuery(id+"F0.wireOp",EDGE,"E7.1.1"),sQuery(id+"F0.wireOp",EDGE,"E7.1.2"),sQuery(id+"F0.wireOp",EDGE,"E7.1.3"),sQuery(id+"F0.wireOp",EDGE,"E7.1.4"),sQuery(id+"F0.wireOp",EDGE,"E7.1.5"),sQuery(id+"F0.wireOp",EDGE,"E7.2.0"),sQuery(id+"F0.wireOp",EDGE,"E7.2.1"),sQuery(id+"F0.wireOp",EDGE,"E7.2.2"),sQuery(id+"F0.wireOp",EDGE,"E7.2.3"),sQuery(id+"F0.wireOp",EDGE,"E7.2.4"),sQuery(id+"F0.wireOp",EDGE,"E7.2.5"),sQuery(id+"F0.wireOp",EDGE,"E7.3.0"),sQuery(id+"F0.wireOp",EDGE,"E7.3.1"),sQuery(id+"F0.wireOp",EDGE,"E7.3.2"),sQuery(id+"F0.wireOp",EDGE,"E7.3.3"),sQuery(id+"F0.wireOp",EDGE,"E7.3.4"),sQuery(id+"F0.wireOp",EDGE,"E7.3.5"),sQuery(id+"F0.wireOp",EDGE,"E7.4.0"),sQuery(id+"F0.wireOp",EDGE,"E7.4.1"),sQuery(id+"F0.wireOp",EDGE,"E7.4.2"),sQuery(id+"F0.wireOp",EDGE,"E7.4.3"),sQuery(id+"F0.wireOp",EDGE,"E7.4.4"),sQuery(id+"F0.wireOp",EDGE,"E7.4.5"),sQuery(id+"F0.wireOp",EDGE,"E7.5.0"),sQuery(id+"F0.wireOp",EDGE,"E7.5.1"),sQuery(id+"F0.wireOp",EDGE,"E7.5.2"),sQuery(id+"F0.wireOp",EDGE,"E7.5.3"),sQuery(id+"F0.wireOp",EDGE,"E7.5.4"),sQuery(id+"F0.wireOp",EDGE,"E7.5.5"),sQuery(id+"F0.wireOp",EDGE,"E7.6.0"),sQuery(id+"F0.wireOp",EDGE,"E7.6.1"),sQuery(id+"F0.wireOp",EDGE,"E7.6.2"),sQuery(id+"F0.wireOp",EDGE,"E7.6.3"),sQuery(id+"F0.wireOp",EDGE,"E7.6.4"),sQuery(id+"F0.wireOp",EDGE,"E7.6.5"),sQuery(id+"F0.wireOp",EDGE,"E7.7.0"),sQuery(id+"F0.wireOp",EDGE,"E7.7.1"),sQuery(id+"F0.wireOp",EDGE,"E7.7.2"),sQuery(id+"F0.wireOp",EDGE,"E7.7.3"),sQuery(id+"F0.wireOp",EDGE,"E7.7.4"),sQuery(id+"F0.wireOp",EDGE,"E7.7.5"),sQuery(id+"F0.wireOp",EDGE,"E7.8.0"),sQuery(id+"F0.wireOp",EDGE,"E7.8.1"),sQuery(id+"F0.wireOp",EDGE,"E7.8.2"),sQuery(id+"F0.wireOp",EDGE,"E7.8.3"),sQuery(id+"F0.wireOp",EDGE,"E7.8.4"),sQuery(id+"F0.wireOp",EDGE,"E7.8.5"),sQuery(id+"F0.wireOp",EDGE,"E7.9.0"),sQuery(id+"F0.wireOp",EDGE,"E7.9.1"),sQuery(id+"F0.wireOp",EDGE,"E7.9.2"),sQuery(id+"F0.wireOp",EDGE,"E7.9.3"),sQuery(id+"F0.wireOp",EDGE,"E7.9.4"),sQuery(id+"F0.wireOp",EDGE,"E7.9.5"),sQuery(id+"F0.wireOp",EDGE,"E7.10.0"),sQuery(id+"F0.wireOp",EDGE,"E7.10.1"),sQuery(id+"F0.wireOp",EDGE,"E7.10.2"),sQuery(id+"F0.wireOp",EDGE,"E7.10.3"),sQuery(id+"F0.wireOp",EDGE,"E7.10.4"),sQuery(id+"F0.wireOp",EDGE,"E7.10.5"),sQuery(id+"F0.wireOp",EDGE,"E7.11.0"),sQuery(id+"F0.wireOp",EDGE,"E7.11.1"),sQuery(id+"F0.wireOp",EDGE,"E7.11.2"),sQuery(id+"F0.wireOp",EDGE,"E7.11.3"),sQuery(id+"F0.wireOp",EDGE,"E7.11.4"),sQuery(id+"F0.wireOp",EDGE,"E7.11.5"),sQuery(id+"F0.wireOp",EDGE,"E7.12.0"),sQuery(id+"F0.wireOp",EDGE,"E7.12.1"),sQuery(id+"F0.wireOp",EDGE,"E7.12.2"),sQuery(id+"F0.wireOp",EDGE,"E7.12.3"),sQuery(id+"F0.wireOp",EDGE,"E7.12.4"),sQuery(id+"F0.wireOp",EDGE,"E7.12.5"),sQuery(id+"F0.wireOp",EDGE,"E7.13.0"),sQuery(id+"F0.wireOp",EDGE,"E7.13.1"),sQuery(id+"F0.wireOp",EDGE,"E7.13.2"),sQuery(id+"F0.wireOp",EDGE,"E7.13.3"),sQuery(id+"F0.wireOp",EDGE,"E7.13.4"),sQuery(id+"F0.wireOp",EDGE,"E7.13.5"),sQuery(id+"F0.wireOp",EDGE,"E7.14.0"),sQuery(id+"F0.wireOp",EDGE,"E7.14.1"),sQuery(id+"F0.wireOp",EDGE,"E7.14.2"),sQuery(id+"F0.wireOp",EDGE,"E7.14.3"),sQuery(id+"F0.wireOp",EDGE,"E7.14.4"),sQuery(id+"F0.wireOp",EDGE,"E7.14.5"),sQuery(id+"F0.wireOp",EDGE,"E7.15.0"),sQuery(id+"F0.wireOp",EDGE,"E7.15.1"),sQuery(id+"F0.wireOp",EDGE,"E7.15.2"),sQuery(id+"F0.wireOp",EDGE,"E7.15.3"),sQuery(id+"F0.wireOp",EDGE,"E7.15.4"),sQuery(id+"F0.wireOp",EDGE,"E7.15.5"),sQuery(id+"F0.wireOp",EDGE,"E7.16.0"),sQuery(id+"F0.wireOp",EDGE,"E7.16.1"),sQuery(id+"F0.wireOp",EDGE,"E7.16.2"),sQuery(id+"F0.wireOp",EDGE,"E7.16.3"),sQuery(id+"F0.wireOp",EDGE,"E7.16.4"),sQuery(id+"F0.wireOp",EDGE,"E7.16.5"),sQuery(id+"F0.wireOp",EDGE,"E7.17.0"),sQuery(id+"F0.wireOp",EDGE,"E7.17.1"),sQuery(id+"F0.wireOp",EDGE,"E7.17.2"),sQuery(id+"F0.wireOp",EDGE,"E7.17.3"),sQuery(id+"F0.wireOp",EDGE,"E7.17.4"),sQuery(id+"F0.wireOp",EDGE,"E7.17.5"),sQuery(id+"F0.wireOp",EDGE,"E7.18.0"),sQuery(id+"F0.wireOp",EDGE,"E7.18.1"),sQuery(id+"F0.wireOp",EDGE,"E7.18.2"),sQuery(id+"F0.wireOp",EDGE,"E7.18.3"),sQuery(id+"F0.wireOp",EDGE,"E7.18.4"),sQuery(id+"F0.wireOp",EDGE,"E7.18.5"),sQuery(id+"F0.wireOp",EDGE,"E7.19.0"),sQuery(id+"F0.wireOp",EDGE,"E7.19.1"),sQuery(id+"F0.wireOp",EDGE,"E7.19.2"),sQuery(id+"F0.wireOp",EDGE,"E7.19.3"),sQuery(id+"F0.wireOp",EDGE,"E7.19.4"),sQuery(id+"F0.wireOp",EDGE,"E7.19.5"),sQuery(id+"F0.wireOp",EDGE,"E7.20.0"),sQuery(id+"F0.wireOp",EDGE,"E7.20.1"),sQuery(id+"F0.wireOp",EDGE,"E7.20.2"),sQuery(id+"F0.wireOp",EDGE,"E7.20.3"),sQuery(id+"F0.wireOp",EDGE,"E7.20.4"),sQuery(id+"F0.wireOp",EDGE,"E7.20.5"),sQuery(id+"F0.wireOp",EDGE,"E7.21.0"),sQuery(id+"F0.wireOp",EDGE,"E7.21.1"),sQuery(id+"F0.wireOp",EDGE,"E7.21.2"),sQuery(id+"F0.wireOp",EDGE,"E7.21.3"),sQuery(id+"F0.wireOp",EDGE,"E7.21.4"),sQuery(id+"F0.wireOp",EDGE,"E7.21.5"),subQ0,sQuery(id+"F0.wireOp",EDGE,"E7.22.1"),sQuery(id+"F0.wireOp",EDGE,"E7.22.2"),sQuery(id+"F0.wireOp",EDGE,"E7.22.3"),sQuery(id+"F0.wireOp",EDGE,"E7.22.4"),sQuery(id+"F0.wireOp",EDGE,"E7.22.5"),sQuery(id+"F0.wireOp",EDGE,"E7.23.0"),sQuery(id+"F0.wireOp",EDGE,"E7.23.1"),sQuery(id+"F0.wireOp",EDGE,"E7.23.2"),sQuery(id+"F0.wireOp",EDGE,"E7.23.3"),sQuery(id+"F0.wireOp",EDGE,"E7.23.4"),sQuery(id+"F0.wireOp",EDGE,"E7.23.5"),sQuery(id+"F0.wireOp",EDGE,"E7.24.0"),sQuery(id+"F0.wireOp",EDGE,"E7.24.1"),sQuery(id+"F0.wireOp",EDGE,"E7.24.2"),sQuery(id+"F0.wireOp",EDGE,"E7.24.3"),sQuery(id+"F0.wireOp",EDGE,"E7.24.4"),sQuery(id+"F0.wireOp",EDGE,"E7.24.5"),sQuery(id+"F0.wireOp",EDGE,"E7.25.0"),sQuery(id+"F0.wireOp",EDGE,"E7.25.1"),sQuery(id+"F0.wireOp",EDGE,"E7.25.2"),sQuery(id+"F0.wireOp",EDGE,"E7.25.3"),sQuery(id+"F0.wireOp",EDGE,"E7.25.4"),sQuery(id+"F0.wireOp",EDGE,"E7.25.5"),sQuery(id+"F0.wireOp",EDGE,"E7.26.0"),sQuery(id+"F0.wireOp",EDGE,"E7.26.1"),sQuery(id+"F0.wireOp",EDGE,"E7.26.2"),sQuery(id+"F0.wireOp",EDGE,"E7.26.3"),sQuery(id+"F0.wireOp",EDGE,"E7.26.4"),sQuery(id+"F0.wireOp",EDGE,"E7.26.5"),sQuery(id+"F0.wireOp",EDGE,"E7.27.0"),sQuery(id+"F0.wireOp",EDGE,"E7.27.1"),sQuery(id+"F0.wireOp",EDGE,"E7.27.2"),sQuery(id+"F0.wireOp",EDGE,"E7.27.3"),sQuery(id+"F0.wireOp",EDGE,"E7.27.4"),sQuery(id+"F0.wireOp",EDGE,"E7.27.5"),sQuery(id+"F0.wireOp",EDGE,"E7.28.0"),sQuery(id+"F0.wireOp",EDGE,"E7.28.1"),sQuery(id+"F0.wireOp",EDGE,"E7.28.2"),sQuery(id+"F0.wireOp",EDGE,"E7.28.3"),sQuery(id+"F0.wireOp",EDGE,"E7.28.4"),sQuery(id+"F0.wireOp",EDGE,"E7.28.5"),sQuery(id+"F0.wireOp",EDGE,"E7.29.0"),sQuery(id+"F0.wireOp",EDGE,"E7.29.1"),sQuery(id+"F0.wireOp",EDGE,"E7.29.2"),sQuery(id+"F0.wireOp",EDGE,"E7.29.3"),sQuery(id+"F0.wireOp",EDGE,"E7.29.4"),sQuery(id+"F0.wireOp",EDGE,"E7.29.5"),sQuery(id+"F0.wireOp",EDGE,"E7.30.0"),sQuery(id+"F0.wireOp",EDGE,"E7.30.1"),sQuery(id+"F0.wireOp",EDGE,"E7.30.2"),sQuery(id+"F0.wireOp",EDGE,"E7.30.3"),sQuery(id+"F0.wireOp",EDGE,"E7.30.4"),sQuery(id+"F0.wireOp",EDGE,"E7.30.5"),sQuery(id+"F0.wireOp",EDGE,"E7.31.0"),sQuery(id+"F0.wireOp",EDGE,"E7.31.1"),sQuery(id+"F0.wireOp",EDGE,"E7.31.2"),sQuery(id+"F0.wireOp",EDGE,"E7.31.3"),sQuery(id+"F0.wireOp",EDGE,"E7.31.4"),sQuery(id+"F0.wireOp",EDGE,"E7.31.5"),sQuery(id+"F0.wireOp",EDGE,"E7.32.0"),sQuery(id+"F0.wireOp",EDGE,"E7.32.1"),sQuery(id+"F0.wireOp",EDGE,"E7.32.2"),sQuery(id+"F0.wireOp",EDGE,"E7.32.3"),sQuery(id+"F0.wireOp",EDGE,"E7.32.4"),sQuery(id+"F0.wireOp",EDGE,"E7.32.5"),sQuery(id+"F0.wireOp",EDGE,"E7.33.0"),sQuery(id+"F0.wireOp",EDGE,"E7.33.1"),sQuery(id+"F0.wireOp",EDGE,"E7.33.2"),sQuery(id+"F0.wireOp",EDGE,"E7.33.3"),sQuery(id+"F0.wireOp",EDGE,"E7.33.4"),sQuery(id+"F0.wireOp",EDGE,"E7.33.5"),sQuery(id+"F0.wireOp",EDGE,"E7.34.0"),sQuery(id+"F0.wireOp",EDGE,"E7.34.1"),sQuery(id+"F0.wireOp",EDGE,"E7.34.2"),sQuery(id+"F0.wireOp",EDGE,"E7.34.3"),sQuery(id+"F0.wireOp",EDGE,"E7.34.4"),sQuery(id+"F0.wireOp",EDGE,"E7.34.5"),sQuery(id+"F0.wireOp",EDGE,"E7.35.0"),sQuery(id+"F0.wireOp",EDGE,"E7.35.1"),sQuery(id+"F0.wireOp",EDGE,"E7.35.2"),sQuery(id+"F0.wireOp",EDGE,"E7.35.3"),sQuery(id+"F0.wireOp",EDGE,"E7.35.4"),sQuery(id+"F0.wireOp",EDGE,"E7.35.5"),sQuery(id+"F0.wireOp",EDGE,"E7.36.0"),sQuery(id+"F0.wireOp",EDGE,"E7.36.1"),sQuery(id+"F0.wireOp",EDGE,"E7.36.2"),sQuery(id+"F0.wireOp",EDGE,"E7.36.3"),sQuery(id+"F0.wireOp",EDGE,"E7.36.4"),sQuery(id+"F0.wireOp",EDGE,"E7.36.5"),sQuery(id+"F0.wireOp",EDGE,"E7.37.0"),sQuery(id+"F0.wireOp",EDGE,"E7.37.1"),sQuery(id+"F0.wireOp",EDGE,"E7.37.2"),sQuery(id+"F0.wireOp",EDGE,"E7.37.3"),sQuery(id+"F0.wireOp",EDGE,"E7.37.4"),sQuery(id+"F0.wireOp",EDGE,"E7.37.5"),sQuery(id+"F0.wireOp",EDGE,"E7.38.0"),sQuery(id+"F0.wireOp",EDGE,"E7.38.1"),sQuery(id+"F0.wireOp",EDGE,"E7.38.2"),sQuery(id+"F0.wireOp",EDGE,"E7.38.3"),sQuery(id+"F0.wireOp",EDGE,"E7.38.4"),sQuery(id+"F0.wireOp",EDGE,"E7.38.5"),sQuery(id+"F0.wireOp",EDGE,"E7.39.0"),sQuery(id+"F0.wireOp",EDGE,"E7.39.1"),sQuery(id+"F0.wireOp",EDGE,"E7.39.2"),sQuery(id+"F0.wireOp",EDGE,"E7.39.3"),sQuery(id+"F0.wireOp",EDGE,"E7.39.4"),sQuery(id+"F0.wireOp",EDGE,"E7.39.5"),sQuery(id+"F0.wireOp",EDGE,"E7.40.0"),sQuery(id+"F0.wireOp",EDGE,"E7.40.1"),sQuery(id+"F0.wireOp",EDGE,"E7.40.2"),sQuery(id+"F0.wireOp",EDGE,"E7.40.3"),sQuery(id+"F0.wireOp",EDGE,"E7.40.4"),sQuery(id+"F0.wireOp",EDGE,"E7.40.5"),sQuery(id+"F0.wireOp",EDGE,"E7.41.0"),sQuery(id+"F0.wireOp",EDGE,"E7.41.1"),sQuery(id+"F0.wireOp",EDGE,"E7.41.2"),sQuery(id+"F0.wireOp",EDGE,"E7.41.3"),sQuery(id+"F0.wireOp",EDGE,"E7.41.4"),sQuery(id+"F0.wireOp",EDGE,"E7.41.5"),sQuery(id+"F0.wireOp",EDGE,"E7.42.0"),sQuery(id+"F0.wireOp",EDGE,"E7.42.1"),sQuery(id+"F0.wireOp",EDGE,"E7.42.2"),sQuery(id+"F0.wireOp",EDGE,"E7.42.3"),sQuery(id+"F0.wireOp",EDGE,"E7.42.4"),sQuery(id+"F0.wireOp",EDGE,"E7.42.5"),sQuery(id+"F0.wireOp",EDGE,"E7.43.0"),sQuery(id+"F0.wireOp",EDGE,"E7.43.1"),sQuery(id+"F0.wireOp",EDGE,"E7.43.2"),sQuery(id+"F0.wireOp",EDGE,"E7.43.3"),sQuery(id+"F0.wireOp",EDGE,"E7.43.4"),sQuery(id+"F0.wireOp",EDGE,"E7.43.5")])],"isStart":true})],"blendedInto":[makeQuery(id+"F1.opExtrude","CAP_FACE",FACE,{"disambiguationData":[OSD([sQuery(id+"F0.wireOp",EDGE,"E1"),sQuery(id+"F0.wireOp",EDGE,"E2"),sQuery(id+"F0.wireOp",EDGE,"E3"),sQuery(id+"F0.wireOp",EDGE,"E4"),sQuery(id+"F0.wireOp",EDGE,"E5"),sQuery(id+"F0.wireOp",EDGE,"E6"),sQuery(id+"F0.wireOp",EDGE,"E7.1.0"),sQuery(id+"F0.wireOp",EDGE,"E7.1.1"),sQuery(id+"F0.wireOp",EDGE,"E7.1.2"),sQuery(id+"F0.wireOp",EDGE,"E7.1.3"),sQuery(id+"F0.wireOp",EDGE,"E7.1.4"),sQuery(id+"F0.wireOp",EDGE,"E7.1.5"),sQuery(id+"F0.wireOp",EDGE,"E7.2.0"),sQuery(id+"F0.wireOp",EDGE,"E7.2.1"),sQuery(id+"F0.wireOp",EDGE,"E7.2.2"),sQuery(id+"F0.wireOp",EDGE,"E7.2.3"),sQuery(id+"F0.wireOp",EDGE,"E7.2.4"),sQuery(id+"F0.wireOp",EDGE,"E7.2.5"),sQuery(id+"F0.wireOp",EDGE,"E7.3.0"),sQuery(id+"F0.wireOp",EDGE,"E7.3.1"),sQuery(id+"F0.wireOp",EDGE,"E7.3.2"),sQuery(id+"F0.wireOp",EDGE,"E7.3.3"),sQuery(id+"F0.wireOp",EDGE,"E7.3.4"),sQuery(id+"F0.wireOp",EDGE,"E7.3.5"),sQuery(id+"F0.wireOp",EDGE,"E7.4.0"),sQuery(id+"F0.wireOp",EDGE,"E7.4.1"),sQuery(id+"F0.wireOp",EDGE,"E7.4.2"),sQuery(id+"F0.wireOp",EDGE,"E7.4.3"),sQuery(id+"F0.wireOp",EDGE,"E7.4.4"),sQuery(id+"F0.wireOp",EDGE,"E7.4.5"),sQuery(id+"F0.wireOp",EDGE,"E7.5.0"),sQuery(id+"F0.wireOp",EDGE,"E7.5.1"),sQuery(id+"F0.wireOp",EDGE,"E7.5.2"),sQuery(id+"F0.wireOp",EDGE,"E7.5.3"),sQuery(id+"F0.wireOp",EDGE,"E7.5.4"),sQuery(id+"F0.wireOp",EDGE,"E7.5.5"),sQuery(id+"F0.wireOp",EDGE,"E7.6.0"),sQuery(id+"F0.wireOp",EDGE,"E7.6.1"),sQuery(id+"F0.wireOp",EDGE,"E7.6.2"),sQuery(id+"F0.wireOp",EDGE,"E7.6.3"),sQuery(id+"F0.wireOp",EDGE,"E7.6.4"),sQuery(id+"F0.wireOp",EDGE,"E7.6.5"),sQuery(id+"F0.wireOp",EDGE,"E7.7.0"),sQuery(id+"F0.wireOp",EDGE,"E7.7.1"),sQuery(id+"F0.wireOp",EDGE,"E7.7.2"),sQuery(id+"F0.wireOp",EDGE,"E7.7.3"),sQuery(id+"F0.wireOp",EDGE,"E7.7.4"),sQuery(id+"F0.wireOp",EDGE,"E7.7.5"),sQuery(id+"F0.wireOp",EDGE,"E7.8.0"),sQuery(id+"F0.wireOp",EDGE,"E7.8.1"),sQuery(id+"F0.wireOp",EDGE,"E7.8.2"),sQuery(id+"F0.wireOp",EDGE,"E7.8.3"),sQuery(id+"F0.wireOp",EDGE,"E7.8.4"),sQuery(id+"F0.wireOp",EDGE,"E7.8.5"),sQuery(id+"F0.wireOp",EDGE,"E7.9.0"),sQuery(id+"F0.wireOp",EDGE,"E7.9.1"),sQuery(id+"F0.wireOp",EDGE,"E7.9.2"),sQuery(id+"F0.wireOp",EDGE,"E7.9.3"),sQuery(id+"F0.wireOp",EDGE,"E7.9.4"),sQuery(id+"F0.wireOp",EDGE,"E7.9.5"),sQuery(id+"F0.wireOp",EDGE,"E7.10.0"),sQuery(id+"F0.wireOp",EDGE,"E7.10.1"),sQuery(id+"F0.wireOp",EDGE,"E7.10.2"),sQuery(id+"F0.wireOp",EDGE,"E7.10.3"),sQuery(id+"F0.wireOp",EDGE,"E7.10.4"),sQuery(id+"F0.wireOp",EDGE,"E7.10.5"),sQuery(id+"F0.wireOp",EDGE,"E7.11.0"),sQuery(id+"F0.wireOp",EDGE,"E7.11.1"),sQuery(id+"F0.wireOp",EDGE,"E7.11.2"),sQuery(id+"F0.wireOp",EDGE,"E7.11.3"),sQuery(id+"F0.wireOp",EDGE,"E7.11.4"),sQuery(id+"F0.wireOp",EDGE,"E7.11.5"),sQuery(id+"F0.wireOp",EDGE,"E7.12.0"),sQuery(id+"F0.wireOp",EDGE,"E7.12.1"),sQuery(id+"F0.wireOp",EDGE,"E7.12.2"),sQuery(id+"F0.wireOp",EDGE,"E7.12.3"),sQuery(id+"F0.wireOp",EDGE,"E7.12.4"),sQuery(id+"F0.wireOp",EDGE,"E7.12.5"),sQuery(id+"F0.wireOp",EDGE,"E7.13.0"),sQuery(id+"F0.wireOp",EDGE,"E7.13.1"),sQuery(id+"F0.wireOp",EDGE,"E7.13.2"),sQuery(id+"F0.wireOp",EDGE,"E7.13.3"),sQuery(id+"F0.wireOp",EDGE,"E7.13.4"),sQuery(id+"F0.wireOp",EDGE,"E7.13.5"),sQuery(id+"F0.wireOp",EDGE,"E7.14.0"),sQuery(id+"F0.wireOp",EDGE,"E7.14.1"),sQuery(id+"F0.wireOp",EDGE,"E7.14.2"),sQuery(id+"F0.wireOp",EDGE,"E7.14.3"),sQuery(id+"F0.wireOp",EDGE,"E7.14.4"),sQuery(id+"F0.wireOp",EDGE,"E7.14.5"),sQuery(id+"F0.wireOp",EDGE,"E7.15.0"),sQuery(id+"F0.wireOp",EDGE,"E7.15.1"),sQuery(id+"F0.wireOp",EDGE,"E7.15.2"),sQuery(id+"F0.wireOp",EDGE,"E7.15.3"),sQuery(id+"F0.wireOp",EDGE,"E7.15.4"),sQuery(id+"F0.wireOp",EDGE,"E7.15.5"),sQuery(id+"F0.wireOp",EDGE,"E7.16.0"),sQuery(id+"F0.wireOp",EDGE,"E7.16.1"),sQuery(id+"F0.wireOp",EDGE,"E7.16.2"),sQuery(id+"F0.wireOp",EDGE,"E7.16.3"),sQuery(id+"F0.wireOp",EDGE,"E7.16.4"),sQuery(id+"F0.wireOp",EDGE,"E7.16.5"),sQuery(id+"F0.wireOp",EDGE,"E7.17.0"),sQuery(id+"F0.wireOp",EDGE,"E7.17.1"),sQuery(id+"F0.wireOp",EDGE,"E7.17.2"),sQuery(id+"F0.wireOp",EDGE,"E7.17.3"),sQuery(id+"F0.wireOp",EDGE,"E7.17.4"),sQuery(id+"F0.wireOp",EDGE,"E7.17.5"),sQuery(id+"F0.wireOp",EDGE,"E7.18.0"),sQuery(id+"F0.wireOp",EDGE,"E7.18.1"),sQuery(id+"F0.wireOp",EDGE,"E7.18.2"),sQuery(id+"F0.wireOp",EDGE,"E7.18.3"),sQuery(id+"F0.wireOp",EDGE,"E7.18.4"),sQuery(id+"F0.wireOp",EDGE,"E7.18.5"),sQuery(id+"F0.wireOp",EDGE,"E7.19.0"),sQuery(id+"F0.wireOp",EDGE,"E7.19.1"),sQuery(id+"F0.wireOp",EDGE,"E7.19.2"),sQuery(id+"F0.wireOp",EDGE,"E7.19.3"),sQuery(id+"F0.wireOp",EDGE,"E7.19.4"),sQuery(id+"F0.wireOp",EDGE,"E7.19.5"),sQuery(id+"F0.wireOp",EDGE,"E7.20.0"),sQuery(id+"F0.wireOp",EDGE,"E7.20.1"),sQuery(id+"F0.wireOp",EDGE,"E7.20.2"),sQuery(id+"F0.wireOp",EDGE,"E7.20.3"),sQuery(id+"F0.wireOp",EDGE,"E7.20.4"),sQuery(id+"F0.wireOp",EDGE,"E7.20.5"),sQuery(id+"F0.wireOp",EDGE,"E7.21.0"),sQuery(id+"F0.wireOp",EDGE,"E7.21.1"),sQuery(id+"F0.wireOp",EDGE,"E7.21.2"),sQuery(id+"F0.wireOp",EDGE,"E7.21.3"),sQuery(id+"F0.wireOp",EDGE,"E7.21.4"),sQuery(id+"F0.wireOp",EDGE,"E7.21.5"),subQ0,sQuery(id+"F0.wireOp",EDGE,"E7.22.1"),sQuery(id+"F0.wireOp",EDGE,"E7.22.2"),sQuery(id+"F0.wireOp",EDGE,"E7.22.3"),sQuery(id+"F0.wireOp",EDGE,"E7.22.4"),sQuery(id+"F0.wireOp",EDGE,"E7.22.5"),sQuery(id+"F0.wireOp",EDGE,"E7.23.0"),sQuery(id+"F0.wireOp",EDGE,"E7.23.1"),sQuery(id+"F0.wireOp",EDGE,"E7.23.2"),sQuery(id+"F0.wireOp",EDGE,"E7.23.3"),sQuery(id+"F0.wireOp",EDGE,"E7.23.4"),sQuery(id+"F0.wireOp",EDGE,"E7.23.5"),sQuery(id+"F0.wireOp",EDGE,"E7.24.0"),sQuery(id+"F0.wireOp",EDGE,"E7.24.1"),sQuery(id+"F0.wireOp",EDGE,"E7.24.2"),sQuery(id+"F0.wireOp",EDGE,"E7.24.3"),sQuery(id+"F0.wireOp",EDGE,"E7.24.4"),sQuery(id+"F0.wireOp",EDGE,"E7.24.5"),sQuery(id+"F0.wireOp",EDGE,"E7.25.0"),sQuery(id+"F0.wireOp",EDGE,"E7.25.1"),sQuery(id+"F0.wireOp",EDGE,"E7.25.2"),sQuery(id+"F0.wireOp",EDGE,"E7.25.3"),sQuery(id+"F0.wireOp",EDGE,"E7.25.4"),sQuery(id+"F0.wireOp",EDGE,"E7.25.5"),sQuery(id+"F0.wireOp",EDGE,"E7.26.0"),sQuery(id+"F0.wireOp",EDGE,"E7.26.1"),sQuery(id+"F0.wireOp",EDGE,"E7.26.2"),sQuery(id+"F0.wireOp",EDGE,"E7.26.3"),sQuery(id+"F0.wireOp",EDGE,"E7.26.4"),sQuery(id+"F0.wireOp",EDGE,"E7.26.5"),sQuery(id+"F0.wireOp",EDGE,"E7.27.0"),sQuery(id+"F0.wireOp",EDGE,"E7.27.1"),sQuery(id+"F0.wireOp",EDGE,"E7.27.2"),sQuery(id+"F0.wireOp",EDGE,"E7.27.3"),sQuery(id+"F0.wireOp",EDGE,"E7.27.4"),sQuery(id+"F0.wireOp",EDGE,"E7.27.5"),sQuery(id+"F0.wireOp",EDGE,"E7.28.0"),sQuery(id+"F0.wireOp",EDGE,"E7.28.1"),sQuery(id+"F0.wireOp",EDGE,"E7.28.2"),sQuery(id+"F0.wireOp",EDGE,"E7.28.3"),sQuery(id+"F0.wireOp",EDGE,"E7.28.4"),sQuery(id+"F0.wireOp",EDGE,"E7.28.5"),sQuery(id+"F0.wireOp",EDGE,"E7.29.0"),sQuery(id+"F0.wireOp",EDGE,"E7.29.1"),sQuery(id+"F0.wireOp",EDGE,"E7.29.2"),sQuery(id+"F0.wireOp",EDGE,"E7.29.3"),sQuery(id+"F0.wireOp",EDGE,"E7.29.4"),sQuery(id+"F0.wireOp",EDGE,"E7.29.5"),sQuery(id+"F0.wireOp",EDGE,"E7.30.0"),sQuery(id+"F0.wireOp",EDGE,"E7.30.1"),sQuery(id+"F0.wireOp",EDGE,"E7.30.2"),sQuery(id+"F0.wireOp",EDGE,"E7.30.3"),sQuery(id+"F0.wireOp",EDGE,"E7.30.4"),sQuery(id+"F0.wireOp",EDGE,"E7.30.5"),sQuery(id+"F0.wireOp",EDGE,"E7.31.0"),sQuery(id+"F0.wireOp",EDGE,"E7.31.1"),sQuery(id+"F0.wireOp",EDGE,"E7.31.2"),sQuery(id+"F0.wireOp",EDGE,"E7.31.3"),sQuery(id+"F0.wireOp",EDGE,"E7.31.4"),sQuery(id+"F0.wireOp",EDGE,"E7.31.5"),sQuery(id+"F0.wireOp",EDGE,"E7.32.0"),sQuery(id+"F0.wireOp",EDGE,"E7.32.1"),sQuery(id+"F0.wireOp",EDGE,"E7.32.2"),sQuery(id+"F0.wireOp",EDGE,"E7.32.3"),sQuery(id+"F0.wireOp",EDGE,"E7.32.4"),sQuery(id+"F0.wireOp",EDGE,"E7.32.5"),sQuery(id+"F0.wireOp",EDGE,"E7.33.0"),sQuery(id+"F0.wireOp",EDGE,"E7.33.1"),sQuery(id+"F0.wireOp",EDGE,"E7.33.2"),sQuery(id+"F0.wireOp",EDGE,"E7.33.3"),sQuery(id+"F0.wireOp",EDGE,"E7.33.4"),sQuery(id+"F0.wireOp",EDGE,"E7.33.5"),sQuery(id+"F0.wireOp",EDGE,"E7.34.0"),sQuery(id+"F0.wireOp",EDGE,"E7.34.1"),sQuery(id+"F0.wireOp",EDGE,"E7.34.2"),sQuery(id+"F0.wireOp",EDGE,"E7.34.3"),sQuery(id+"F0.wireOp",EDGE,"E7.34.4"),sQuery(id+"F0.wireOp",EDGE,"E7.34.5"),sQuery(id+"F0.wireOp",EDGE,"E7.35.0"),sQuery(id+"F0.wireOp",EDGE,"E7.35.1"),sQuery(id+"F0.wireOp",EDGE,"E7.35.2"),sQuery(id+"F0.wireOp",EDGE,"E7.35.3"),sQuery(id+"F0.wireOp",EDGE,"E7.35.4"),sQuery(id+"F0.wireOp",EDGE,"E7.35.5"),sQuery(id+"F0.wireOp",EDGE,"E7.36.0"),sQuery(id+"F0.wireOp",EDGE,"E7.36.1"),sQuery(id+"F0.wireOp",EDGE,"E7.36.2"),sQuery(id+"F0.wireOp",EDGE,"E7.36.3"),sQuery(id+"F0.wireOp",EDGE,"E7.36.4"),sQuery(id+"F0.wireOp",EDGE,"E7.36.5"),sQuery(id+"F0.wireOp",EDGE,"E7.37.0"),sQuery(id+"F0.wireOp",EDGE,"E7.37.1"),sQuery(id+"F0.wireOp",EDGE,"E7.37.2"),sQuery(id+"F0.wireOp",EDGE,"E7.37.3"),sQuery(id+"F0.wireOp",EDGE,"E7.37.4"),sQuery(id+"F0.wireOp",EDGE,"E7.37.5"),sQuery(id+"F0.wireOp",EDGE,"E7.38.0"),sQuery(id+"F0.wireOp",EDGE,"E7.38.1"),sQuery(id+"F0.wireOp",EDGE,"E7.38.2"),sQuery(id+"F0.wireOp",EDGE,"E7.38.3"),sQuery(id+"F0.wireOp",EDGE,"E7.38.4"),sQuery(id+"F0.wireOp",EDGE,"E7.38.5"),sQuery(id+"F0.wireOp",EDGE,"E7.39.0"),sQuery(id+"F0.wireOp",EDGE,"E7.39.1"),sQuery(id+"F0.wireOp",EDGE,"E7.39.2"),sQuery(id+"F0.wireOp",EDGE,"E7.39.3"),sQuery(id+"F0.wireOp",EDGE,"E7.39.4"),sQuery(id+"F0.wireOp",EDGE,"E7.39.5"),sQuery(id+"F0.wireOp",EDGE,"E7.40.0"),sQuery(id+"F0.wireOp",EDGE,"E7.40.1"),sQuery(id+"F0.wireOp",EDGE,"E7.40.2"),sQuery(id+"F0.wireOp",EDGE,"E7.40.3"),sQuery(id+"F0.wireOp",EDGE,"E7.40.4"),sQuery(id+"F0.wireOp",EDGE,"E7.40.5"),sQuery(id+"F0.wireOp",EDGE,"E7.41.0"),sQuery(id+"F0.wireOp",EDGE,"E7.41.1"),sQuery(id+"F0.wireOp",EDGE,"E7.41.2"),sQuery(id+"F0.wireOp",EDGE,"E7.41.3"),sQuery(id+"F0.wireOp",EDGE,"E7.41.4"),sQuery(id+"F0.wireOp",EDGE,"E7.41.5"),sQuery(id+"F0.wireOp",EDGE,"E7.42.0"),sQuery(id+"F0.wireOp",EDGE,"E7.42.1"),sQuery(id+"F0.wireOp",EDGE,"E7.42.2"),sQuery(id+"F0.wireOp",EDGE,"E7.42.3"),sQuery(id+"F0.wireOp",EDGE,"E7.42.4"),sQuery(id+"F0.wireOp",EDGE,"E7.42.5"),sQuery(id+"F0.wireOp",EDGE,"E7.43.0"),sQuery(id+"F0.wireOp",EDGE,"E7.43.1"),sQuery(id+"F0.wireOp",EDGE,"E7.43.2"),sQuery(id+"F0.wireOp",EDGE,"E7.43.3"),sQuery(id+"F0.wireOp",EDGE,"E7.43.4"),sQuery(id+"F0.wireOp",EDGE,"E7.43.5")])],"isStart":true})]});}
            var Q33;
            {var subQ0=sQuery(id+"F0.wireOp",EDGE,"E7.24.0");Q33=makeQuery(id+"F2.opChamfer","BLEND_EDGE",EDGE,{"blendedFrom":[makeQuery(id+"F1.opExtrude","CAP_EDGE",EDGE,{"disambiguationData":[OSD([subQ0])],"isStart":true}),makeQuery(id+"F1.opExtrude","CAP_FACE",FACE,{"disambiguationData":[OSD([sQuery(id+"F0.wireOp",EDGE,"E1"),sQuery(id+"F0.wireOp",EDGE,"E2"),sQuery(id+"F0.wireOp",EDGE,"E3"),sQuery(id+"F0.wireOp",EDGE,"E4"),sQuery(id+"F0.wireOp",EDGE,"E5"),sQuery(id+"F0.wireOp",EDGE,"E6"),sQuery(id+"F0.wireOp",EDGE,"E7.1.0"),sQuery(id+"F0.wireOp",EDGE,"E7.1.1"),sQuery(id+"F0.wireOp",EDGE,"E7.1.2"),sQuery(id+"F0.wireOp",EDGE,"E7.1.3"),sQuery(id+"F0.wireOp",EDGE,"E7.1.4"),sQuery(id+"F0.wireOp",EDGE,"E7.1.5"),sQuery(id+"F0.wireOp",EDGE,"E7.2.0"),sQuery(id+"F0.wireOp",EDGE,"E7.2.1"),sQuery(id+"F0.wireOp",EDGE,"E7.2.2"),sQuery(id+"F0.wireOp",EDGE,"E7.2.3"),sQuery(id+"F0.wireOp",EDGE,"E7.2.4"),sQuery(id+"F0.wireOp",EDGE,"E7.2.5"),sQuery(id+"F0.wireOp",EDGE,"E7.3.0"),sQuery(id+"F0.wireOp",EDGE,"E7.3.1"),sQuery(id+"F0.wireOp",EDGE,"E7.3.2"),sQuery(id+"F0.wireOp",EDGE,"E7.3.3"),sQuery(id+"F0.wireOp",EDGE,"E7.3.4"),sQuery(id+"F0.wireOp",EDGE,"E7.3.5"),sQuery(id+"F0.wireOp",EDGE,"E7.4.0"),sQuery(id+"F0.wireOp",EDGE,"E7.4.1"),sQuery(id+"F0.wireOp",EDGE,"E7.4.2"),sQuery(id+"F0.wireOp",EDGE,"E7.4.3"),sQuery(id+"F0.wireOp",EDGE,"E7.4.4"),sQuery(id+"F0.wireOp",EDGE,"E7.4.5"),sQuery(id+"F0.wireOp",EDGE,"E7.5.0"),sQuery(id+"F0.wireOp",EDGE,"E7.5.1"),sQuery(id+"F0.wireOp",EDGE,"E7.5.2"),sQuery(id+"F0.wireOp",EDGE,"E7.5.3"),sQuery(id+"F0.wireOp",EDGE,"E7.5.4"),sQuery(id+"F0.wireOp",EDGE,"E7.5.5"),sQuery(id+"F0.wireOp",EDGE,"E7.6.0"),sQuery(id+"F0.wireOp",EDGE,"E7.6.1"),sQuery(id+"F0.wireOp",EDGE,"E7.6.2"),sQuery(id+"F0.wireOp",EDGE,"E7.6.3"),sQuery(id+"F0.wireOp",EDGE,"E7.6.4"),sQuery(id+"F0.wireOp",EDGE,"E7.6.5"),sQuery(id+"F0.wireOp",EDGE,"E7.7.0"),sQuery(id+"F0.wireOp",EDGE,"E7.7.1"),sQuery(id+"F0.wireOp",EDGE,"E7.7.2"),sQuery(id+"F0.wireOp",EDGE,"E7.7.3"),sQuery(id+"F0.wireOp",EDGE,"E7.7.4"),sQuery(id+"F0.wireOp",EDGE,"E7.7.5"),sQuery(id+"F0.wireOp",EDGE,"E7.8.0"),sQuery(id+"F0.wireOp",EDGE,"E7.8.1"),sQuery(id+"F0.wireOp",EDGE,"E7.8.2"),sQuery(id+"F0.wireOp",EDGE,"E7.8.3"),sQuery(id+"F0.wireOp",EDGE,"E7.8.4"),sQuery(id+"F0.wireOp",EDGE,"E7.8.5"),sQuery(id+"F0.wireOp",EDGE,"E7.9.0"),sQuery(id+"F0.wireOp",EDGE,"E7.9.1"),sQuery(id+"F0.wireOp",EDGE,"E7.9.2"),sQuery(id+"F0.wireOp",EDGE,"E7.9.3"),sQuery(id+"F0.wireOp",EDGE,"E7.9.4"),sQuery(id+"F0.wireOp",EDGE,"E7.9.5"),sQuery(id+"F0.wireOp",EDGE,"E7.10.0"),sQuery(id+"F0.wireOp",EDGE,"E7.10.1"),sQuery(id+"F0.wireOp",EDGE,"E7.10.2"),sQuery(id+"F0.wireOp",EDGE,"E7.10.3"),sQuery(id+"F0.wireOp",EDGE,"E7.10.4"),sQuery(id+"F0.wireOp",EDGE,"E7.10.5"),sQuery(id+"F0.wireOp",EDGE,"E7.11.0"),sQuery(id+"F0.wireOp",EDGE,"E7.11.1"),sQuery(id+"F0.wireOp",EDGE,"E7.11.2"),sQuery(id+"F0.wireOp",EDGE,"E7.11.3"),sQuery(id+"F0.wireOp",EDGE,"E7.11.4"),sQuery(id+"F0.wireOp",EDGE,"E7.11.5"),sQuery(id+"F0.wireOp",EDGE,"E7.12.0"),sQuery(id+"F0.wireOp",EDGE,"E7.12.1"),sQuery(id+"F0.wireOp",EDGE,"E7.12.2"),sQuery(id+"F0.wireOp",EDGE,"E7.12.3"),sQuery(id+"F0.wireOp",EDGE,"E7.12.4"),sQuery(id+"F0.wireOp",EDGE,"E7.12.5"),sQuery(id+"F0.wireOp",EDGE,"E7.13.0"),sQuery(id+"F0.wireOp",EDGE,"E7.13.1"),sQuery(id+"F0.wireOp",EDGE,"E7.13.2"),sQuery(id+"F0.wireOp",EDGE,"E7.13.3"),sQuery(id+"F0.wireOp",EDGE,"E7.13.4"),sQuery(id+"F0.wireOp",EDGE,"E7.13.5"),sQuery(id+"F0.wireOp",EDGE,"E7.14.0"),sQuery(id+"F0.wireOp",EDGE,"E7.14.1"),sQuery(id+"F0.wireOp",EDGE,"E7.14.2"),sQuery(id+"F0.wireOp",EDGE,"E7.14.3"),sQuery(id+"F0.wireOp",EDGE,"E7.14.4"),sQuery(id+"F0.wireOp",EDGE,"E7.14.5"),sQuery(id+"F0.wireOp",EDGE,"E7.15.0"),sQuery(id+"F0.wireOp",EDGE,"E7.15.1"),sQuery(id+"F0.wireOp",EDGE,"E7.15.2"),sQuery(id+"F0.wireOp",EDGE,"E7.15.3"),sQuery(id+"F0.wireOp",EDGE,"E7.15.4"),sQuery(id+"F0.wireOp",EDGE,"E7.15.5"),sQuery(id+"F0.wireOp",EDGE,"E7.16.0"),sQuery(id+"F0.wireOp",EDGE,"E7.16.1"),sQuery(id+"F0.wireOp",EDGE,"E7.16.2"),sQuery(id+"F0.wireOp",EDGE,"E7.16.3"),sQuery(id+"F0.wireOp",EDGE,"E7.16.4"),sQuery(id+"F0.wireOp",EDGE,"E7.16.5"),sQuery(id+"F0.wireOp",EDGE,"E7.17.0"),sQuery(id+"F0.wireOp",EDGE,"E7.17.1"),sQuery(id+"F0.wireOp",EDGE,"E7.17.2"),sQuery(id+"F0.wireOp",EDGE,"E7.17.3"),sQuery(id+"F0.wireOp",EDGE,"E7.17.4"),sQuery(id+"F0.wireOp",EDGE,"E7.17.5"),sQuery(id+"F0.wireOp",EDGE,"E7.18.0"),sQuery(id+"F0.wireOp",EDGE,"E7.18.1"),sQuery(id+"F0.wireOp",EDGE,"E7.18.2"),sQuery(id+"F0.wireOp",EDGE,"E7.18.3"),sQuery(id+"F0.wireOp",EDGE,"E7.18.4"),sQuery(id+"F0.wireOp",EDGE,"E7.18.5"),sQuery(id+"F0.wireOp",EDGE,"E7.19.0"),sQuery(id+"F0.wireOp",EDGE,"E7.19.1"),sQuery(id+"F0.wireOp",EDGE,"E7.19.2"),sQuery(id+"F0.wireOp",EDGE,"E7.19.3"),sQuery(id+"F0.wireOp",EDGE,"E7.19.4"),sQuery(id+"F0.wireOp",EDGE,"E7.19.5"),sQuery(id+"F0.wireOp",EDGE,"E7.20.0"),sQuery(id+"F0.wireOp",EDGE,"E7.20.1"),sQuery(id+"F0.wireOp",EDGE,"E7.20.2"),sQuery(id+"F0.wireOp",EDGE,"E7.20.3"),sQuery(id+"F0.wireOp",EDGE,"E7.20.4"),sQuery(id+"F0.wireOp",EDGE,"E7.20.5"),sQuery(id+"F0.wireOp",EDGE,"E7.21.0"),sQuery(id+"F0.wireOp",EDGE,"E7.21.1"),sQuery(id+"F0.wireOp",EDGE,"E7.21.2"),sQuery(id+"F0.wireOp",EDGE,"E7.21.3"),sQuery(id+"F0.wireOp",EDGE,"E7.21.4"),sQuery(id+"F0.wireOp",EDGE,"E7.21.5"),sQuery(id+"F0.wireOp",EDGE,"E7.22.0"),sQuery(id+"F0.wireOp",EDGE,"E7.22.1"),sQuery(id+"F0.wireOp",EDGE,"E7.22.2"),sQuery(id+"F0.wireOp",EDGE,"E7.22.3"),sQuery(id+"F0.wireOp",EDGE,"E7.22.4"),sQuery(id+"F0.wireOp",EDGE,"E7.22.5"),sQuery(id+"F0.wireOp",EDGE,"E7.23.0"),sQuery(id+"F0.wireOp",EDGE,"E7.23.1"),sQuery(id+"F0.wireOp",EDGE,"E7.23.2"),sQuery(id+"F0.wireOp",EDGE,"E7.23.3"),sQuery(id+"F0.wireOp",EDGE,"E7.23.4"),sQuery(id+"F0.wireOp",EDGE,"E7.23.5"),subQ0,sQuery(id+"F0.wireOp",EDGE,"E7.24.1"),sQuery(id+"F0.wireOp",EDGE,"E7.24.2"),sQuery(id+"F0.wireOp",EDGE,"E7.24.3"),sQuery(id+"F0.wireOp",EDGE,"E7.24.4"),sQuery(id+"F0.wireOp",EDGE,"E7.24.5"),sQuery(id+"F0.wireOp",EDGE,"E7.25.0"),sQuery(id+"F0.wireOp",EDGE,"E7.25.1"),sQuery(id+"F0.wireOp",EDGE,"E7.25.2"),sQuery(id+"F0.wireOp",EDGE,"E7.25.3"),sQuery(id+"F0.wireOp",EDGE,"E7.25.4"),sQuery(id+"F0.wireOp",EDGE,"E7.25.5"),sQuery(id+"F0.wireOp",EDGE,"E7.26.0"),sQuery(id+"F0.wireOp",EDGE,"E7.26.1"),sQuery(id+"F0.wireOp",EDGE,"E7.26.2"),sQuery(id+"F0.wireOp",EDGE,"E7.26.3"),sQuery(id+"F0.wireOp",EDGE,"E7.26.4"),sQuery(id+"F0.wireOp",EDGE,"E7.26.5"),sQuery(id+"F0.wireOp",EDGE,"E7.27.0"),sQuery(id+"F0.wireOp",EDGE,"E7.27.1"),sQuery(id+"F0.wireOp",EDGE,"E7.27.2"),sQuery(id+"F0.wireOp",EDGE,"E7.27.3"),sQuery(id+"F0.wireOp",EDGE,"E7.27.4"),sQuery(id+"F0.wireOp",EDGE,"E7.27.5"),sQuery(id+"F0.wireOp",EDGE,"E7.28.0"),sQuery(id+"F0.wireOp",EDGE,"E7.28.1"),sQuery(id+"F0.wireOp",EDGE,"E7.28.2"),sQuery(id+"F0.wireOp",EDGE,"E7.28.3"),sQuery(id+"F0.wireOp",EDGE,"E7.28.4"),sQuery(id+"F0.wireOp",EDGE,"E7.28.5"),sQuery(id+"F0.wireOp",EDGE,"E7.29.0"),sQuery(id+"F0.wireOp",EDGE,"E7.29.1"),sQuery(id+"F0.wireOp",EDGE,"E7.29.2"),sQuery(id+"F0.wireOp",EDGE,"E7.29.3"),sQuery(id+"F0.wireOp",EDGE,"E7.29.4"),sQuery(id+"F0.wireOp",EDGE,"E7.29.5"),sQuery(id+"F0.wireOp",EDGE,"E7.30.0"),sQuery(id+"F0.wireOp",EDGE,"E7.30.1"),sQuery(id+"F0.wireOp",EDGE,"E7.30.2"),sQuery(id+"F0.wireOp",EDGE,"E7.30.3"),sQuery(id+"F0.wireOp",EDGE,"E7.30.4"),sQuery(id+"F0.wireOp",EDGE,"E7.30.5"),sQuery(id+"F0.wireOp",EDGE,"E7.31.0"),sQuery(id+"F0.wireOp",EDGE,"E7.31.1"),sQuery(id+"F0.wireOp",EDGE,"E7.31.2"),sQuery(id+"F0.wireOp",EDGE,"E7.31.3"),sQuery(id+"F0.wireOp",EDGE,"E7.31.4"),sQuery(id+"F0.wireOp",EDGE,"E7.31.5"),sQuery(id+"F0.wireOp",EDGE,"E7.32.0"),sQuery(id+"F0.wireOp",EDGE,"E7.32.1"),sQuery(id+"F0.wireOp",EDGE,"E7.32.2"),sQuery(id+"F0.wireOp",EDGE,"E7.32.3"),sQuery(id+"F0.wireOp",EDGE,"E7.32.4"),sQuery(id+"F0.wireOp",EDGE,"E7.32.5"),sQuery(id+"F0.wireOp",EDGE,"E7.33.0"),sQuery(id+"F0.wireOp",EDGE,"E7.33.1"),sQuery(id+"F0.wireOp",EDGE,"E7.33.2"),sQuery(id+"F0.wireOp",EDGE,"E7.33.3"),sQuery(id+"F0.wireOp",EDGE,"E7.33.4"),sQuery(id+"F0.wireOp",EDGE,"E7.33.5"),sQuery(id+"F0.wireOp",EDGE,"E7.34.0"),sQuery(id+"F0.wireOp",EDGE,"E7.34.1"),sQuery(id+"F0.wireOp",EDGE,"E7.34.2"),sQuery(id+"F0.wireOp",EDGE,"E7.34.3"),sQuery(id+"F0.wireOp",EDGE,"E7.34.4"),sQuery(id+"F0.wireOp",EDGE,"E7.34.5"),sQuery(id+"F0.wireOp",EDGE,"E7.35.0"),sQuery(id+"F0.wireOp",EDGE,"E7.35.1"),sQuery(id+"F0.wireOp",EDGE,"E7.35.2"),sQuery(id+"F0.wireOp",EDGE,"E7.35.3"),sQuery(id+"F0.wireOp",EDGE,"E7.35.4"),sQuery(id+"F0.wireOp",EDGE,"E7.35.5"),sQuery(id+"F0.wireOp",EDGE,"E7.36.0"),sQuery(id+"F0.wireOp",EDGE,"E7.36.1"),sQuery(id+"F0.wireOp",EDGE,"E7.36.2"),sQuery(id+"F0.wireOp",EDGE,"E7.36.3"),sQuery(id+"F0.wireOp",EDGE,"E7.36.4"),sQuery(id+"F0.wireOp",EDGE,"E7.36.5"),sQuery(id+"F0.wireOp",EDGE,"E7.37.0"),sQuery(id+"F0.wireOp",EDGE,"E7.37.1"),sQuery(id+"F0.wireOp",EDGE,"E7.37.2"),sQuery(id+"F0.wireOp",EDGE,"E7.37.3"),sQuery(id+"F0.wireOp",EDGE,"E7.37.4"),sQuery(id+"F0.wireOp",EDGE,"E7.37.5"),sQuery(id+"F0.wireOp",EDGE,"E7.38.0"),sQuery(id+"F0.wireOp",EDGE,"E7.38.1"),sQuery(id+"F0.wireOp",EDGE,"E7.38.2"),sQuery(id+"F0.wireOp",EDGE,"E7.38.3"),sQuery(id+"F0.wireOp",EDGE,"E7.38.4"),sQuery(id+"F0.wireOp",EDGE,"E7.38.5"),sQuery(id+"F0.wireOp",EDGE,"E7.39.0"),sQuery(id+"F0.wireOp",EDGE,"E7.39.1"),sQuery(id+"F0.wireOp",EDGE,"E7.39.2"),sQuery(id+"F0.wireOp",EDGE,"E7.39.3"),sQuery(id+"F0.wireOp",EDGE,"E7.39.4"),sQuery(id+"F0.wireOp",EDGE,"E7.39.5"),sQuery(id+"F0.wireOp",EDGE,"E7.40.0"),sQuery(id+"F0.wireOp",EDGE,"E7.40.1"),sQuery(id+"F0.wireOp",EDGE,"E7.40.2"),sQuery(id+"F0.wireOp",EDGE,"E7.40.3"),sQuery(id+"F0.wireOp",EDGE,"E7.40.4"),sQuery(id+"F0.wireOp",EDGE,"E7.40.5"),sQuery(id+"F0.wireOp",EDGE,"E7.41.0"),sQuery(id+"F0.wireOp",EDGE,"E7.41.1"),sQuery(id+"F0.wireOp",EDGE,"E7.41.2"),sQuery(id+"F0.wireOp",EDGE,"E7.41.3"),sQuery(id+"F0.wireOp",EDGE,"E7.41.4"),sQuery(id+"F0.wireOp",EDGE,"E7.41.5"),sQuery(id+"F0.wireOp",EDGE,"E7.42.0"),sQuery(id+"F0.wireOp",EDGE,"E7.42.1"),sQuery(id+"F0.wireOp",EDGE,"E7.42.2"),sQuery(id+"F0.wireOp",EDGE,"E7.42.3"),sQuery(id+"F0.wireOp",EDGE,"E7.42.4"),sQuery(id+"F0.wireOp",EDGE,"E7.42.5"),sQuery(id+"F0.wireOp",EDGE,"E7.43.0"),sQuery(id+"F0.wireOp",EDGE,"E7.43.1"),sQuery(id+"F0.wireOp",EDGE,"E7.43.2"),sQuery(id+"F0.wireOp",EDGE,"E7.43.3"),sQuery(id+"F0.wireOp",EDGE,"E7.43.4"),sQuery(id+"F0.wireOp",EDGE,"E7.43.5")])],"isStart":true})],"blendedInto":[makeQuery(id+"F1.opExtrude","CAP_FACE",FACE,{"disambiguationData":[OSD([sQuery(id+"F0.wireOp",EDGE,"E1"),sQuery(id+"F0.wireOp",EDGE,"E2"),sQuery(id+"F0.wireOp",EDGE,"E3"),sQuery(id+"F0.wireOp",EDGE,"E4"),sQuery(id+"F0.wireOp",EDGE,"E5"),sQuery(id+"F0.wireOp",EDGE,"E6"),sQuery(id+"F0.wireOp",EDGE,"E7.1.0"),sQuery(id+"F0.wireOp",EDGE,"E7.1.1"),sQuery(id+"F0.wireOp",EDGE,"E7.1.2"),sQuery(id+"F0.wireOp",EDGE,"E7.1.3"),sQuery(id+"F0.wireOp",EDGE,"E7.1.4"),sQuery(id+"F0.wireOp",EDGE,"E7.1.5"),sQuery(id+"F0.wireOp",EDGE,"E7.2.0"),sQuery(id+"F0.wireOp",EDGE,"E7.2.1"),sQuery(id+"F0.wireOp",EDGE,"E7.2.2"),sQuery(id+"F0.wireOp",EDGE,"E7.2.3"),sQuery(id+"F0.wireOp",EDGE,"E7.2.4"),sQuery(id+"F0.wireOp",EDGE,"E7.2.5"),sQuery(id+"F0.wireOp",EDGE,"E7.3.0"),sQuery(id+"F0.wireOp",EDGE,"E7.3.1"),sQuery(id+"F0.wireOp",EDGE,"E7.3.2"),sQuery(id+"F0.wireOp",EDGE,"E7.3.3"),sQuery(id+"F0.wireOp",EDGE,"E7.3.4"),sQuery(id+"F0.wireOp",EDGE,"E7.3.5"),sQuery(id+"F0.wireOp",EDGE,"E7.4.0"),sQuery(id+"F0.wireOp",EDGE,"E7.4.1"),sQuery(id+"F0.wireOp",EDGE,"E7.4.2"),sQuery(id+"F0.wireOp",EDGE,"E7.4.3"),sQuery(id+"F0.wireOp",EDGE,"E7.4.4"),sQuery(id+"F0.wireOp",EDGE,"E7.4.5"),sQuery(id+"F0.wireOp",EDGE,"E7.5.0"),sQuery(id+"F0.wireOp",EDGE,"E7.5.1"),sQuery(id+"F0.wireOp",EDGE,"E7.5.2"),sQuery(id+"F0.wireOp",EDGE,"E7.5.3"),sQuery(id+"F0.wireOp",EDGE,"E7.5.4"),sQuery(id+"F0.wireOp",EDGE,"E7.5.5"),sQuery(id+"F0.wireOp",EDGE,"E7.6.0"),sQuery(id+"F0.wireOp",EDGE,"E7.6.1"),sQuery(id+"F0.wireOp",EDGE,"E7.6.2"),sQuery(id+"F0.wireOp",EDGE,"E7.6.3"),sQuery(id+"F0.wireOp",EDGE,"E7.6.4"),sQuery(id+"F0.wireOp",EDGE,"E7.6.5"),sQuery(id+"F0.wireOp",EDGE,"E7.7.0"),sQuery(id+"F0.wireOp",EDGE,"E7.7.1"),sQuery(id+"F0.wireOp",EDGE,"E7.7.2"),sQuery(id+"F0.wireOp",EDGE,"E7.7.3"),sQuery(id+"F0.wireOp",EDGE,"E7.7.4"),sQuery(id+"F0.wireOp",EDGE,"E7.7.5"),sQuery(id+"F0.wireOp",EDGE,"E7.8.0"),sQuery(id+"F0.wireOp",EDGE,"E7.8.1"),sQuery(id+"F0.wireOp",EDGE,"E7.8.2"),sQuery(id+"F0.wireOp",EDGE,"E7.8.3"),sQuery(id+"F0.wireOp",EDGE,"E7.8.4"),sQuery(id+"F0.wireOp",EDGE,"E7.8.5"),sQuery(id+"F0.wireOp",EDGE,"E7.9.0"),sQuery(id+"F0.wireOp",EDGE,"E7.9.1"),sQuery(id+"F0.wireOp",EDGE,"E7.9.2"),sQuery(id+"F0.wireOp",EDGE,"E7.9.3"),sQuery(id+"F0.wireOp",EDGE,"E7.9.4"),sQuery(id+"F0.wireOp",EDGE,"E7.9.5"),sQuery(id+"F0.wireOp",EDGE,"E7.10.0"),sQuery(id+"F0.wireOp",EDGE,"E7.10.1"),sQuery(id+"F0.wireOp",EDGE,"E7.10.2"),sQuery(id+"F0.wireOp",EDGE,"E7.10.3"),sQuery(id+"F0.wireOp",EDGE,"E7.10.4"),sQuery(id+"F0.wireOp",EDGE,"E7.10.5"),sQuery(id+"F0.wireOp",EDGE,"E7.11.0"),sQuery(id+"F0.wireOp",EDGE,"E7.11.1"),sQuery(id+"F0.wireOp",EDGE,"E7.11.2"),sQuery(id+"F0.wireOp",EDGE,"E7.11.3"),sQuery(id+"F0.wireOp",EDGE,"E7.11.4"),sQuery(id+"F0.wireOp",EDGE,"E7.11.5"),sQuery(id+"F0.wireOp",EDGE,"E7.12.0"),sQuery(id+"F0.wireOp",EDGE,"E7.12.1"),sQuery(id+"F0.wireOp",EDGE,"E7.12.2"),sQuery(id+"F0.wireOp",EDGE,"E7.12.3"),sQuery(id+"F0.wireOp",EDGE,"E7.12.4"),sQuery(id+"F0.wireOp",EDGE,"E7.12.5"),sQuery(id+"F0.wireOp",EDGE,"E7.13.0"),sQuery(id+"F0.wireOp",EDGE,"E7.13.1"),sQuery(id+"F0.wireOp",EDGE,"E7.13.2"),sQuery(id+"F0.wireOp",EDGE,"E7.13.3"),sQuery(id+"F0.wireOp",EDGE,"E7.13.4"),sQuery(id+"F0.wireOp",EDGE,"E7.13.5"),sQuery(id+"F0.wireOp",EDGE,"E7.14.0"),sQuery(id+"F0.wireOp",EDGE,"E7.14.1"),sQuery(id+"F0.wireOp",EDGE,"E7.14.2"),sQuery(id+"F0.wireOp",EDGE,"E7.14.3"),sQuery(id+"F0.wireOp",EDGE,"E7.14.4"),sQuery(id+"F0.wireOp",EDGE,"E7.14.5"),sQuery(id+"F0.wireOp",EDGE,"E7.15.0"),sQuery(id+"F0.wireOp",EDGE,"E7.15.1"),sQuery(id+"F0.wireOp",EDGE,"E7.15.2"),sQuery(id+"F0.wireOp",EDGE,"E7.15.3"),sQuery(id+"F0.wireOp",EDGE,"E7.15.4"),sQuery(id+"F0.wireOp",EDGE,"E7.15.5"),sQuery(id+"F0.wireOp",EDGE,"E7.16.0"),sQuery(id+"F0.wireOp",EDGE,"E7.16.1"),sQuery(id+"F0.wireOp",EDGE,"E7.16.2"),sQuery(id+"F0.wireOp",EDGE,"E7.16.3"),sQuery(id+"F0.wireOp",EDGE,"E7.16.4"),sQuery(id+"F0.wireOp",EDGE,"E7.16.5"),sQuery(id+"F0.wireOp",EDGE,"E7.17.0"),sQuery(id+"F0.wireOp",EDGE,"E7.17.1"),sQuery(id+"F0.wireOp",EDGE,"E7.17.2"),sQuery(id+"F0.wireOp",EDGE,"E7.17.3"),sQuery(id+"F0.wireOp",EDGE,"E7.17.4"),sQuery(id+"F0.wireOp",EDGE,"E7.17.5"),sQuery(id+"F0.wireOp",EDGE,"E7.18.0"),sQuery(id+"F0.wireOp",EDGE,"E7.18.1"),sQuery(id+"F0.wireOp",EDGE,"E7.18.2"),sQuery(id+"F0.wireOp",EDGE,"E7.18.3"),sQuery(id+"F0.wireOp",EDGE,"E7.18.4"),sQuery(id+"F0.wireOp",EDGE,"E7.18.5"),sQuery(id+"F0.wireOp",EDGE,"E7.19.0"),sQuery(id+"F0.wireOp",EDGE,"E7.19.1"),sQuery(id+"F0.wireOp",EDGE,"E7.19.2"),sQuery(id+"F0.wireOp",EDGE,"E7.19.3"),sQuery(id+"F0.wireOp",EDGE,"E7.19.4"),sQuery(id+"F0.wireOp",EDGE,"E7.19.5"),sQuery(id+"F0.wireOp",EDGE,"E7.20.0"),sQuery(id+"F0.wireOp",EDGE,"E7.20.1"),sQuery(id+"F0.wireOp",EDGE,"E7.20.2"),sQuery(id+"F0.wireOp",EDGE,"E7.20.3"),sQuery(id+"F0.wireOp",EDGE,"E7.20.4"),sQuery(id+"F0.wireOp",EDGE,"E7.20.5"),sQuery(id+"F0.wireOp",EDGE,"E7.21.0"),sQuery(id+"F0.wireOp",EDGE,"E7.21.1"),sQuery(id+"F0.wireOp",EDGE,"E7.21.2"),sQuery(id+"F0.wireOp",EDGE,"E7.21.3"),sQuery(id+"F0.wireOp",EDGE,"E7.21.4"),sQuery(id+"F0.wireOp",EDGE,"E7.21.5"),sQuery(id+"F0.wireOp",EDGE,"E7.22.0"),sQuery(id+"F0.wireOp",EDGE,"E7.22.1"),sQuery(id+"F0.wireOp",EDGE,"E7.22.2"),sQuery(id+"F0.wireOp",EDGE,"E7.22.3"),sQuery(id+"F0.wireOp",EDGE,"E7.22.4"),sQuery(id+"F0.wireOp",EDGE,"E7.22.5"),sQuery(id+"F0.wireOp",EDGE,"E7.23.0"),sQuery(id+"F0.wireOp",EDGE,"E7.23.1"),sQuery(id+"F0.wireOp",EDGE,"E7.23.2"),sQuery(id+"F0.wireOp",EDGE,"E7.23.3"),sQuery(id+"F0.wireOp",EDGE,"E7.23.4"),sQuery(id+"F0.wireOp",EDGE,"E7.23.5"),subQ0,sQuery(id+"F0.wireOp",EDGE,"E7.24.1"),sQuery(id+"F0.wireOp",EDGE,"E7.24.2"),sQuery(id+"F0.wireOp",EDGE,"E7.24.3"),sQuery(id+"F0.wireOp",EDGE,"E7.24.4"),sQuery(id+"F0.wireOp",EDGE,"E7.24.5"),sQuery(id+"F0.wireOp",EDGE,"E7.25.0"),sQuery(id+"F0.wireOp",EDGE,"E7.25.1"),sQuery(id+"F0.wireOp",EDGE,"E7.25.2"),sQuery(id+"F0.wireOp",EDGE,"E7.25.3"),sQuery(id+"F0.wireOp",EDGE,"E7.25.4"),sQuery(id+"F0.wireOp",EDGE,"E7.25.5"),sQuery(id+"F0.wireOp",EDGE,"E7.26.0"),sQuery(id+"F0.wireOp",EDGE,"E7.26.1"),sQuery(id+"F0.wireOp",EDGE,"E7.26.2"),sQuery(id+"F0.wireOp",EDGE,"E7.26.3"),sQuery(id+"F0.wireOp",EDGE,"E7.26.4"),sQuery(id+"F0.wireOp",EDGE,"E7.26.5"),sQuery(id+"F0.wireOp",EDGE,"E7.27.0"),sQuery(id+"F0.wireOp",EDGE,"E7.27.1"),sQuery(id+"F0.wireOp",EDGE,"E7.27.2"),sQuery(id+"F0.wireOp",EDGE,"E7.27.3"),sQuery(id+"F0.wireOp",EDGE,"E7.27.4"),sQuery(id+"F0.wireOp",EDGE,"E7.27.5"),sQuery(id+"F0.wireOp",EDGE,"E7.28.0"),sQuery(id+"F0.wireOp",EDGE,"E7.28.1"),sQuery(id+"F0.wireOp",EDGE,"E7.28.2"),sQuery(id+"F0.wireOp",EDGE,"E7.28.3"),sQuery(id+"F0.wireOp",EDGE,"E7.28.4"),sQuery(id+"F0.wireOp",EDGE,"E7.28.5"),sQuery(id+"F0.wireOp",EDGE,"E7.29.0"),sQuery(id+"F0.wireOp",EDGE,"E7.29.1"),sQuery(id+"F0.wireOp",EDGE,"E7.29.2"),sQuery(id+"F0.wireOp",EDGE,"E7.29.3"),sQuery(id+"F0.wireOp",EDGE,"E7.29.4"),sQuery(id+"F0.wireOp",EDGE,"E7.29.5"),sQuery(id+"F0.wireOp",EDGE,"E7.30.0"),sQuery(id+"F0.wireOp",EDGE,"E7.30.1"),sQuery(id+"F0.wireOp",EDGE,"E7.30.2"),sQuery(id+"F0.wireOp",EDGE,"E7.30.3"),sQuery(id+"F0.wireOp",EDGE,"E7.30.4"),sQuery(id+"F0.wireOp",EDGE,"E7.30.5"),sQuery(id+"F0.wireOp",EDGE,"E7.31.0"),sQuery(id+"F0.wireOp",EDGE,"E7.31.1"),sQuery(id+"F0.wireOp",EDGE,"E7.31.2"),sQuery(id+"F0.wireOp",EDGE,"E7.31.3"),sQuery(id+"F0.wireOp",EDGE,"E7.31.4"),sQuery(id+"F0.wireOp",EDGE,"E7.31.5"),sQuery(id+"F0.wireOp",EDGE,"E7.32.0"),sQuery(id+"F0.wireOp",EDGE,"E7.32.1"),sQuery(id+"F0.wireOp",EDGE,"E7.32.2"),sQuery(id+"F0.wireOp",EDGE,"E7.32.3"),sQuery(id+"F0.wireOp",EDGE,"E7.32.4"),sQuery(id+"F0.wireOp",EDGE,"E7.32.5"),sQuery(id+"F0.wireOp",EDGE,"E7.33.0"),sQuery(id+"F0.wireOp",EDGE,"E7.33.1"),sQuery(id+"F0.wireOp",EDGE,"E7.33.2"),sQuery(id+"F0.wireOp",EDGE,"E7.33.3"),sQuery(id+"F0.wireOp",EDGE,"E7.33.4"),sQuery(id+"F0.wireOp",EDGE,"E7.33.5"),sQuery(id+"F0.wireOp",EDGE,"E7.34.0"),sQuery(id+"F0.wireOp",EDGE,"E7.34.1"),sQuery(id+"F0.wireOp",EDGE,"E7.34.2"),sQuery(id+"F0.wireOp",EDGE,"E7.34.3"),sQuery(id+"F0.wireOp",EDGE,"E7.34.4"),sQuery(id+"F0.wireOp",EDGE,"E7.34.5"),sQuery(id+"F0.wireOp",EDGE,"E7.35.0"),sQuery(id+"F0.wireOp",EDGE,"E7.35.1"),sQuery(id+"F0.wireOp",EDGE,"E7.35.2"),sQuery(id+"F0.wireOp",EDGE,"E7.35.3"),sQuery(id+"F0.wireOp",EDGE,"E7.35.4"),sQuery(id+"F0.wireOp",EDGE,"E7.35.5"),sQuery(id+"F0.wireOp",EDGE,"E7.36.0"),sQuery(id+"F0.wireOp",EDGE,"E7.36.1"),sQuery(id+"F0.wireOp",EDGE,"E7.36.2"),sQuery(id+"F0.wireOp",EDGE,"E7.36.3"),sQuery(id+"F0.wireOp",EDGE,"E7.36.4"),sQuery(id+"F0.wireOp",EDGE,"E7.36.5"),sQuery(id+"F0.wireOp",EDGE,"E7.37.0"),sQuery(id+"F0.wireOp",EDGE,"E7.37.1"),sQuery(id+"F0.wireOp",EDGE,"E7.37.2"),sQuery(id+"F0.wireOp",EDGE,"E7.37.3"),sQuery(id+"F0.wireOp",EDGE,"E7.37.4"),sQuery(id+"F0.wireOp",EDGE,"E7.37.5"),sQuery(id+"F0.wireOp",EDGE,"E7.38.0"),sQuery(id+"F0.wireOp",EDGE,"E7.38.1"),sQuery(id+"F0.wireOp",EDGE,"E7.38.2"),sQuery(id+"F0.wireOp",EDGE,"E7.38.3"),sQuery(id+"F0.wireOp",EDGE,"E7.38.4"),sQuery(id+"F0.wireOp",EDGE,"E7.38.5"),sQuery(id+"F0.wireOp",EDGE,"E7.39.0"),sQuery(id+"F0.wireOp",EDGE,"E7.39.1"),sQuery(id+"F0.wireOp",EDGE,"E7.39.2"),sQuery(id+"F0.wireOp",EDGE,"E7.39.3"),sQuery(id+"F0.wireOp",EDGE,"E7.39.4"),sQuery(id+"F0.wireOp",EDGE,"E7.39.5"),sQuery(id+"F0.wireOp",EDGE,"E7.40.0"),sQuery(id+"F0.wireOp",EDGE,"E7.40.1"),sQuery(id+"F0.wireOp",EDGE,"E7.40.2"),sQuery(id+"F0.wireOp",EDGE,"E7.40.3"),sQuery(id+"F0.wireOp",EDGE,"E7.40.4"),sQuery(id+"F0.wireOp",EDGE,"E7.40.5"),sQuery(id+"F0.wireOp",EDGE,"E7.41.0"),sQuery(id+"F0.wireOp",EDGE,"E7.41.1"),sQuery(id+"F0.wireOp",EDGE,"E7.41.2"),sQuery(id+"F0.wireOp",EDGE,"E7.41.3"),sQuery(id+"F0.wireOp",EDGE,"E7.41.4"),sQuery(id+"F0.wireOp",EDGE,"E7.41.5"),sQuery(id+"F0.wireOp",EDGE,"E7.42.0"),sQuery(id+"F0.wireOp",EDGE,"E7.42.1"),sQuery(id+"F0.wireOp",EDGE,"E7.42.2"),sQuery(id+"F0.wireOp",EDGE,"E7.42.3"),sQuery(id+"F0.wireOp",EDGE,"E7.42.4"),sQuery(id+"F0.wireOp",EDGE,"E7.42.5"),sQuery(id+"F0.wireOp",EDGE,"E7.43.0"),sQuery(id+"F0.wireOp",EDGE,"E7.43.1"),sQuery(id+"F0.wireOp",EDGE,"E7.43.2"),sQuery(id+"F0.wireOp",EDGE,"E7.43.3"),sQuery(id+"F0.wireOp",EDGE,"E7.43.4"),sQuery(id+"F0.wireOp",EDGE,"E7.43.5")])],"isStart":true})]});}
            var Q34;
            {var subQ0=sQuery(id+"F0.wireOp",EDGE,"E7.26.0");Q34=makeQuery(id+"F2.opChamfer","BLEND_EDGE",EDGE,{"blendedFrom":[makeQuery(id+"F1.opExtrude","CAP_EDGE",EDGE,{"disambiguationData":[OSD([subQ0])],"isStart":true}),makeQuery(id+"F1.opExtrude","CAP_FACE",FACE,{"disambiguationData":[OSD([sQuery(id+"F0.wireOp",EDGE,"E1"),sQuery(id+"F0.wireOp",EDGE,"E2"),sQuery(id+"F0.wireOp",EDGE,"E3"),sQuery(id+"F0.wireOp",EDGE,"E4"),sQuery(id+"F0.wireOp",EDGE,"E5"),sQuery(id+"F0.wireOp",EDGE,"E6"),sQuery(id+"F0.wireOp",EDGE,"E7.1.0"),sQuery(id+"F0.wireOp",EDGE,"E7.1.1"),sQuery(id+"F0.wireOp",EDGE,"E7.1.2"),sQuery(id+"F0.wireOp",EDGE,"E7.1.3"),sQuery(id+"F0.wireOp",EDGE,"E7.1.4"),sQuery(id+"F0.wireOp",EDGE,"E7.1.5"),sQuery(id+"F0.wireOp",EDGE,"E7.2.0"),sQuery(id+"F0.wireOp",EDGE,"E7.2.1"),sQuery(id+"F0.wireOp",EDGE,"E7.2.2"),sQuery(id+"F0.wireOp",EDGE,"E7.2.3"),sQuery(id+"F0.wireOp",EDGE,"E7.2.4"),sQuery(id+"F0.wireOp",EDGE,"E7.2.5"),sQuery(id+"F0.wireOp",EDGE,"E7.3.0"),sQuery(id+"F0.wireOp",EDGE,"E7.3.1"),sQuery(id+"F0.wireOp",EDGE,"E7.3.2"),sQuery(id+"F0.wireOp",EDGE,"E7.3.3"),sQuery(id+"F0.wireOp",EDGE,"E7.3.4"),sQuery(id+"F0.wireOp",EDGE,"E7.3.5"),sQuery(id+"F0.wireOp",EDGE,"E7.4.0"),sQuery(id+"F0.wireOp",EDGE,"E7.4.1"),sQuery(id+"F0.wireOp",EDGE,"E7.4.2"),sQuery(id+"F0.wireOp",EDGE,"E7.4.3"),sQuery(id+"F0.wireOp",EDGE,"E7.4.4"),sQuery(id+"F0.wireOp",EDGE,"E7.4.5"),sQuery(id+"F0.wireOp",EDGE,"E7.5.0"),sQuery(id+"F0.wireOp",EDGE,"E7.5.1"),sQuery(id+"F0.wireOp",EDGE,"E7.5.2"),sQuery(id+"F0.wireOp",EDGE,"E7.5.3"),sQuery(id+"F0.wireOp",EDGE,"E7.5.4"),sQuery(id+"F0.wireOp",EDGE,"E7.5.5"),sQuery(id+"F0.wireOp",EDGE,"E7.6.0"),sQuery(id+"F0.wireOp",EDGE,"E7.6.1"),sQuery(id+"F0.wireOp",EDGE,"E7.6.2"),sQuery(id+"F0.wireOp",EDGE,"E7.6.3"),sQuery(id+"F0.wireOp",EDGE,"E7.6.4"),sQuery(id+"F0.wireOp",EDGE,"E7.6.5"),sQuery(id+"F0.wireOp",EDGE,"E7.7.0"),sQuery(id+"F0.wireOp",EDGE,"E7.7.1"),sQuery(id+"F0.wireOp",EDGE,"E7.7.2"),sQuery(id+"F0.wireOp",EDGE,"E7.7.3"),sQuery(id+"F0.wireOp",EDGE,"E7.7.4"),sQuery(id+"F0.wireOp",EDGE,"E7.7.5"),sQuery(id+"F0.wireOp",EDGE,"E7.8.0"),sQuery(id+"F0.wireOp",EDGE,"E7.8.1"),sQuery(id+"F0.wireOp",EDGE,"E7.8.2"),sQuery(id+"F0.wireOp",EDGE,"E7.8.3"),sQuery(id+"F0.wireOp",EDGE,"E7.8.4"),sQuery(id+"F0.wireOp",EDGE,"E7.8.5"),sQuery(id+"F0.wireOp",EDGE,"E7.9.0"),sQuery(id+"F0.wireOp",EDGE,"E7.9.1"),sQuery(id+"F0.wireOp",EDGE,"E7.9.2"),sQuery(id+"F0.wireOp",EDGE,"E7.9.3"),sQuery(id+"F0.wireOp",EDGE,"E7.9.4"),sQuery(id+"F0.wireOp",EDGE,"E7.9.5"),sQuery(id+"F0.wireOp",EDGE,"E7.10.0"),sQuery(id+"F0.wireOp",EDGE,"E7.10.1"),sQuery(id+"F0.wireOp",EDGE,"E7.10.2"),sQuery(id+"F0.wireOp",EDGE,"E7.10.3"),sQuery(id+"F0.wireOp",EDGE,"E7.10.4"),sQuery(id+"F0.wireOp",EDGE,"E7.10.5"),sQuery(id+"F0.wireOp",EDGE,"E7.11.0"),sQuery(id+"F0.wireOp",EDGE,"E7.11.1"),sQuery(id+"F0.wireOp",EDGE,"E7.11.2"),sQuery(id+"F0.wireOp",EDGE,"E7.11.3"),sQuery(id+"F0.wireOp",EDGE,"E7.11.4"),sQuery(id+"F0.wireOp",EDGE,"E7.11.5"),sQuery(id+"F0.wireOp",EDGE,"E7.12.0"),sQuery(id+"F0.wireOp",EDGE,"E7.12.1"),sQuery(id+"F0.wireOp",EDGE,"E7.12.2"),sQuery(id+"F0.wireOp",EDGE,"E7.12.3"),sQuery(id+"F0.wireOp",EDGE,"E7.12.4"),sQuery(id+"F0.wireOp",EDGE,"E7.12.5"),sQuery(id+"F0.wireOp",EDGE,"E7.13.0"),sQuery(id+"F0.wireOp",EDGE,"E7.13.1"),sQuery(id+"F0.wireOp",EDGE,"E7.13.2"),sQuery(id+"F0.wireOp",EDGE,"E7.13.3"),sQuery(id+"F0.wireOp",EDGE,"E7.13.4"),sQuery(id+"F0.wireOp",EDGE,"E7.13.5"),sQuery(id+"F0.wireOp",EDGE,"E7.14.0"),sQuery(id+"F0.wireOp",EDGE,"E7.14.1"),sQuery(id+"F0.wireOp",EDGE,"E7.14.2"),sQuery(id+"F0.wireOp",EDGE,"E7.14.3"),sQuery(id+"F0.wireOp",EDGE,"E7.14.4"),sQuery(id+"F0.wireOp",EDGE,"E7.14.5"),sQuery(id+"F0.wireOp",EDGE,"E7.15.0"),sQuery(id+"F0.wireOp",EDGE,"E7.15.1"),sQuery(id+"F0.wireOp",EDGE,"E7.15.2"),sQuery(id+"F0.wireOp",EDGE,"E7.15.3"),sQuery(id+"F0.wireOp",EDGE,"E7.15.4"),sQuery(id+"F0.wireOp",EDGE,"E7.15.5"),sQuery(id+"F0.wireOp",EDGE,"E7.16.0"),sQuery(id+"F0.wireOp",EDGE,"E7.16.1"),sQuery(id+"F0.wireOp",EDGE,"E7.16.2"),sQuery(id+"F0.wireOp",EDGE,"E7.16.3"),sQuery(id+"F0.wireOp",EDGE,"E7.16.4"),sQuery(id+"F0.wireOp",EDGE,"E7.16.5"),sQuery(id+"F0.wireOp",EDGE,"E7.17.0"),sQuery(id+"F0.wireOp",EDGE,"E7.17.1"),sQuery(id+"F0.wireOp",EDGE,"E7.17.2"),sQuery(id+"F0.wireOp",EDGE,"E7.17.3"),sQuery(id+"F0.wireOp",EDGE,"E7.17.4"),sQuery(id+"F0.wireOp",EDGE,"E7.17.5"),sQuery(id+"F0.wireOp",EDGE,"E7.18.0"),sQuery(id+"F0.wireOp",EDGE,"E7.18.1"),sQuery(id+"F0.wireOp",EDGE,"E7.18.2"),sQuery(id+"F0.wireOp",EDGE,"E7.18.3"),sQuery(id+"F0.wireOp",EDGE,"E7.18.4"),sQuery(id+"F0.wireOp",EDGE,"E7.18.5"),sQuery(id+"F0.wireOp",EDGE,"E7.19.0"),sQuery(id+"F0.wireOp",EDGE,"E7.19.1"),sQuery(id+"F0.wireOp",EDGE,"E7.19.2"),sQuery(id+"F0.wireOp",EDGE,"E7.19.3"),sQuery(id+"F0.wireOp",EDGE,"E7.19.4"),sQuery(id+"F0.wireOp",EDGE,"E7.19.5"),sQuery(id+"F0.wireOp",EDGE,"E7.20.0"),sQuery(id+"F0.wireOp",EDGE,"E7.20.1"),sQuery(id+"F0.wireOp",EDGE,"E7.20.2"),sQuery(id+"F0.wireOp",EDGE,"E7.20.3"),sQuery(id+"F0.wireOp",EDGE,"E7.20.4"),sQuery(id+"F0.wireOp",EDGE,"E7.20.5"),sQuery(id+"F0.wireOp",EDGE,"E7.21.0"),sQuery(id+"F0.wireOp",EDGE,"E7.21.1"),sQuery(id+"F0.wireOp",EDGE,"E7.21.2"),sQuery(id+"F0.wireOp",EDGE,"E7.21.3"),sQuery(id+"F0.wireOp",EDGE,"E7.21.4"),sQuery(id+"F0.wireOp",EDGE,"E7.21.5"),sQuery(id+"F0.wireOp",EDGE,"E7.22.0"),sQuery(id+"F0.wireOp",EDGE,"E7.22.1"),sQuery(id+"F0.wireOp",EDGE,"E7.22.2"),sQuery(id+"F0.wireOp",EDGE,"E7.22.3"),sQuery(id+"F0.wireOp",EDGE,"E7.22.4"),sQuery(id+"F0.wireOp",EDGE,"E7.22.5"),sQuery(id+"F0.wireOp",EDGE,"E7.23.0"),sQuery(id+"F0.wireOp",EDGE,"E7.23.1"),sQuery(id+"F0.wireOp",EDGE,"E7.23.2"),sQuery(id+"F0.wireOp",EDGE,"E7.23.3"),sQuery(id+"F0.wireOp",EDGE,"E7.23.4"),sQuery(id+"F0.wireOp",EDGE,"E7.23.5"),sQuery(id+"F0.wireOp",EDGE,"E7.24.0"),sQuery(id+"F0.wireOp",EDGE,"E7.24.1"),sQuery(id+"F0.wireOp",EDGE,"E7.24.2"),sQuery(id+"F0.wireOp",EDGE,"E7.24.3"),sQuery(id+"F0.wireOp",EDGE,"E7.24.4"),sQuery(id+"F0.wireOp",EDGE,"E7.24.5"),sQuery(id+"F0.wireOp",EDGE,"E7.25.0"),sQuery(id+"F0.wireOp",EDGE,"E7.25.1"),sQuery(id+"F0.wireOp",EDGE,"E7.25.2"),sQuery(id+"F0.wireOp",EDGE,"E7.25.3"),sQuery(id+"F0.wireOp",EDGE,"E7.25.4"),sQuery(id+"F0.wireOp",EDGE,"E7.25.5"),subQ0,sQuery(id+"F0.wireOp",EDGE,"E7.26.1"),sQuery(id+"F0.wireOp",EDGE,"E7.26.2"),sQuery(id+"F0.wireOp",EDGE,"E7.26.3"),sQuery(id+"F0.wireOp",EDGE,"E7.26.4"),sQuery(id+"F0.wireOp",EDGE,"E7.26.5"),sQuery(id+"F0.wireOp",EDGE,"E7.27.0"),sQuery(id+"F0.wireOp",EDGE,"E7.27.1"),sQuery(id+"F0.wireOp",EDGE,"E7.27.2"),sQuery(id+"F0.wireOp",EDGE,"E7.27.3"),sQuery(id+"F0.wireOp",EDGE,"E7.27.4"),sQuery(id+"F0.wireOp",EDGE,"E7.27.5"),sQuery(id+"F0.wireOp",EDGE,"E7.28.0"),sQuery(id+"F0.wireOp",EDGE,"E7.28.1"),sQuery(id+"F0.wireOp",EDGE,"E7.28.2"),sQuery(id+"F0.wireOp",EDGE,"E7.28.3"),sQuery(id+"F0.wireOp",EDGE,"E7.28.4"),sQuery(id+"F0.wireOp",EDGE,"E7.28.5"),sQuery(id+"F0.wireOp",EDGE,"E7.29.0"),sQuery(id+"F0.wireOp",EDGE,"E7.29.1"),sQuery(id+"F0.wireOp",EDGE,"E7.29.2"),sQuery(id+"F0.wireOp",EDGE,"E7.29.3"),sQuery(id+"F0.wireOp",EDGE,"E7.29.4"),sQuery(id+"F0.wireOp",EDGE,"E7.29.5"),sQuery(id+"F0.wireOp",EDGE,"E7.30.0"),sQuery(id+"F0.wireOp",EDGE,"E7.30.1"),sQuery(id+"F0.wireOp",EDGE,"E7.30.2"),sQuery(id+"F0.wireOp",EDGE,"E7.30.3"),sQuery(id+"F0.wireOp",EDGE,"E7.30.4"),sQuery(id+"F0.wireOp",EDGE,"E7.30.5"),sQuery(id+"F0.wireOp",EDGE,"E7.31.0"),sQuery(id+"F0.wireOp",EDGE,"E7.31.1"),sQuery(id+"F0.wireOp",EDGE,"E7.31.2"),sQuery(id+"F0.wireOp",EDGE,"E7.31.3"),sQuery(id+"F0.wireOp",EDGE,"E7.31.4"),sQuery(id+"F0.wireOp",EDGE,"E7.31.5"),sQuery(id+"F0.wireOp",EDGE,"E7.32.0"),sQuery(id+"F0.wireOp",EDGE,"E7.32.1"),sQuery(id+"F0.wireOp",EDGE,"E7.32.2"),sQuery(id+"F0.wireOp",EDGE,"E7.32.3"),sQuery(id+"F0.wireOp",EDGE,"E7.32.4"),sQuery(id+"F0.wireOp",EDGE,"E7.32.5"),sQuery(id+"F0.wireOp",EDGE,"E7.33.0"),sQuery(id+"F0.wireOp",EDGE,"E7.33.1"),sQuery(id+"F0.wireOp",EDGE,"E7.33.2"),sQuery(id+"F0.wireOp",EDGE,"E7.33.3"),sQuery(id+"F0.wireOp",EDGE,"E7.33.4"),sQuery(id+"F0.wireOp",EDGE,"E7.33.5"),sQuery(id+"F0.wireOp",EDGE,"E7.34.0"),sQuery(id+"F0.wireOp",EDGE,"E7.34.1"),sQuery(id+"F0.wireOp",EDGE,"E7.34.2"),sQuery(id+"F0.wireOp",EDGE,"E7.34.3"),sQuery(id+"F0.wireOp",EDGE,"E7.34.4"),sQuery(id+"F0.wireOp",EDGE,"E7.34.5"),sQuery(id+"F0.wireOp",EDGE,"E7.35.0"),sQuery(id+"F0.wireOp",EDGE,"E7.35.1"),sQuery(id+"F0.wireOp",EDGE,"E7.35.2"),sQuery(id+"F0.wireOp",EDGE,"E7.35.3"),sQuery(id+"F0.wireOp",EDGE,"E7.35.4"),sQuery(id+"F0.wireOp",EDGE,"E7.35.5"),sQuery(id+"F0.wireOp",EDGE,"E7.36.0"),sQuery(id+"F0.wireOp",EDGE,"E7.36.1"),sQuery(id+"F0.wireOp",EDGE,"E7.36.2"),sQuery(id+"F0.wireOp",EDGE,"E7.36.3"),sQuery(id+"F0.wireOp",EDGE,"E7.36.4"),sQuery(id+"F0.wireOp",EDGE,"E7.36.5"),sQuery(id+"F0.wireOp",EDGE,"E7.37.0"),sQuery(id+"F0.wireOp",EDGE,"E7.37.1"),sQuery(id+"F0.wireOp",EDGE,"E7.37.2"),sQuery(id+"F0.wireOp",EDGE,"E7.37.3"),sQuery(id+"F0.wireOp",EDGE,"E7.37.4"),sQuery(id+"F0.wireOp",EDGE,"E7.37.5"),sQuery(id+"F0.wireOp",EDGE,"E7.38.0"),sQuery(id+"F0.wireOp",EDGE,"E7.38.1"),sQuery(id+"F0.wireOp",EDGE,"E7.38.2"),sQuery(id+"F0.wireOp",EDGE,"E7.38.3"),sQuery(id+"F0.wireOp",EDGE,"E7.38.4"),sQuery(id+"F0.wireOp",EDGE,"E7.38.5"),sQuery(id+"F0.wireOp",EDGE,"E7.39.0"),sQuery(id+"F0.wireOp",EDGE,"E7.39.1"),sQuery(id+"F0.wireOp",EDGE,"E7.39.2"),sQuery(id+"F0.wireOp",EDGE,"E7.39.3"),sQuery(id+"F0.wireOp",EDGE,"E7.39.4"),sQuery(id+"F0.wireOp",EDGE,"E7.39.5"),sQuery(id+"F0.wireOp",EDGE,"E7.40.0"),sQuery(id+"F0.wireOp",EDGE,"E7.40.1"),sQuery(id+"F0.wireOp",EDGE,"E7.40.2"),sQuery(id+"F0.wireOp",EDGE,"E7.40.3"),sQuery(id+"F0.wireOp",EDGE,"E7.40.4"),sQuery(id+"F0.wireOp",EDGE,"E7.40.5"),sQuery(id+"F0.wireOp",EDGE,"E7.41.0"),sQuery(id+"F0.wireOp",EDGE,"E7.41.1"),sQuery(id+"F0.wireOp",EDGE,"E7.41.2"),sQuery(id+"F0.wireOp",EDGE,"E7.41.3"),sQuery(id+"F0.wireOp",EDGE,"E7.41.4"),sQuery(id+"F0.wireOp",EDGE,"E7.41.5"),sQuery(id+"F0.wireOp",EDGE,"E7.42.0"),sQuery(id+"F0.wireOp",EDGE,"E7.42.1"),sQuery(id+"F0.wireOp",EDGE,"E7.42.2"),sQuery(id+"F0.wireOp",EDGE,"E7.42.3"),sQuery(id+"F0.wireOp",EDGE,"E7.42.4"),sQuery(id+"F0.wireOp",EDGE,"E7.42.5"),sQuery(id+"F0.wireOp",EDGE,"E7.43.0"),sQuery(id+"F0.wireOp",EDGE,"E7.43.1"),sQuery(id+"F0.wireOp",EDGE,"E7.43.2"),sQuery(id+"F0.wireOp",EDGE,"E7.43.3"),sQuery(id+"F0.wireOp",EDGE,"E7.43.4"),sQuery(id+"F0.wireOp",EDGE,"E7.43.5")])],"isStart":true})],"blendedInto":[makeQuery(id+"F1.opExtrude","CAP_FACE",FACE,{"disambiguationData":[OSD([sQuery(id+"F0.wireOp",EDGE,"E1"),sQuery(id+"F0.wireOp",EDGE,"E2"),sQuery(id+"F0.wireOp",EDGE,"E3"),sQuery(id+"F0.wireOp",EDGE,"E4"),sQuery(id+"F0.wireOp",EDGE,"E5"),sQuery(id+"F0.wireOp",EDGE,"E6"),sQuery(id+"F0.wireOp",EDGE,"E7.1.0"),sQuery(id+"F0.wireOp",EDGE,"E7.1.1"),sQuery(id+"F0.wireOp",EDGE,"E7.1.2"),sQuery(id+"F0.wireOp",EDGE,"E7.1.3"),sQuery(id+"F0.wireOp",EDGE,"E7.1.4"),sQuery(id+"F0.wireOp",EDGE,"E7.1.5"),sQuery(id+"F0.wireOp",EDGE,"E7.2.0"),sQuery(id+"F0.wireOp",EDGE,"E7.2.1"),sQuery(id+"F0.wireOp",EDGE,"E7.2.2"),sQuery(id+"F0.wireOp",EDGE,"E7.2.3"),sQuery(id+"F0.wireOp",EDGE,"E7.2.4"),sQuery(id+"F0.wireOp",EDGE,"E7.2.5"),sQuery(id+"F0.wireOp",EDGE,"E7.3.0"),sQuery(id+"F0.wireOp",EDGE,"E7.3.1"),sQuery(id+"F0.wireOp",EDGE,"E7.3.2"),sQuery(id+"F0.wireOp",EDGE,"E7.3.3"),sQuery(id+"F0.wireOp",EDGE,"E7.3.4"),sQuery(id+"F0.wireOp",EDGE,"E7.3.5"),sQuery(id+"F0.wireOp",EDGE,"E7.4.0"),sQuery(id+"F0.wireOp",EDGE,"E7.4.1"),sQuery(id+"F0.wireOp",EDGE,"E7.4.2"),sQuery(id+"F0.wireOp",EDGE,"E7.4.3"),sQuery(id+"F0.wireOp",EDGE,"E7.4.4"),sQuery(id+"F0.wireOp",EDGE,"E7.4.5"),sQuery(id+"F0.wireOp",EDGE,"E7.5.0"),sQuery(id+"F0.wireOp",EDGE,"E7.5.1"),sQuery(id+"F0.wireOp",EDGE,"E7.5.2"),sQuery(id+"F0.wireOp",EDGE,"E7.5.3"),sQuery(id+"F0.wireOp",EDGE,"E7.5.4"),sQuery(id+"F0.wireOp",EDGE,"E7.5.5"),sQuery(id+"F0.wireOp",EDGE,"E7.6.0"),sQuery(id+"F0.wireOp",EDGE,"E7.6.1"),sQuery(id+"F0.wireOp",EDGE,"E7.6.2"),sQuery(id+"F0.wireOp",EDGE,"E7.6.3"),sQuery(id+"F0.wireOp",EDGE,"E7.6.4"),sQuery(id+"F0.wireOp",EDGE,"E7.6.5"),sQuery(id+"F0.wireOp",EDGE,"E7.7.0"),sQuery(id+"F0.wireOp",EDGE,"E7.7.1"),sQuery(id+"F0.wireOp",EDGE,"E7.7.2"),sQuery(id+"F0.wireOp",EDGE,"E7.7.3"),sQuery(id+"F0.wireOp",EDGE,"E7.7.4"),sQuery(id+"F0.wireOp",EDGE,"E7.7.5"),sQuery(id+"F0.wireOp",EDGE,"E7.8.0"),sQuery(id+"F0.wireOp",EDGE,"E7.8.1"),sQuery(id+"F0.wireOp",EDGE,"E7.8.2"),sQuery(id+"F0.wireOp",EDGE,"E7.8.3"),sQuery(id+"F0.wireOp",EDGE,"E7.8.4"),sQuery(id+"F0.wireOp",EDGE,"E7.8.5"),sQuery(id+"F0.wireOp",EDGE,"E7.9.0"),sQuery(id+"F0.wireOp",EDGE,"E7.9.1"),sQuery(id+"F0.wireOp",EDGE,"E7.9.2"),sQuery(id+"F0.wireOp",EDGE,"E7.9.3"),sQuery(id+"F0.wireOp",EDGE,"E7.9.4"),sQuery(id+"F0.wireOp",EDGE,"E7.9.5"),sQuery(id+"F0.wireOp",EDGE,"E7.10.0"),sQuery(id+"F0.wireOp",EDGE,"E7.10.1"),sQuery(id+"F0.wireOp",EDGE,"E7.10.2"),sQuery(id+"F0.wireOp",EDGE,"E7.10.3"),sQuery(id+"F0.wireOp",EDGE,"E7.10.4"),sQuery(id+"F0.wireOp",EDGE,"E7.10.5"),sQuery(id+"F0.wireOp",EDGE,"E7.11.0"),sQuery(id+"F0.wireOp",EDGE,"E7.11.1"),sQuery(id+"F0.wireOp",EDGE,"E7.11.2"),sQuery(id+"F0.wireOp",EDGE,"E7.11.3"),sQuery(id+"F0.wireOp",EDGE,"E7.11.4"),sQuery(id+"F0.wireOp",EDGE,"E7.11.5"),sQuery(id+"F0.wireOp",EDGE,"E7.12.0"),sQuery(id+"F0.wireOp",EDGE,"E7.12.1"),sQuery(id+"F0.wireOp",EDGE,"E7.12.2"),sQuery(id+"F0.wireOp",EDGE,"E7.12.3"),sQuery(id+"F0.wireOp",EDGE,"E7.12.4"),sQuery(id+"F0.wireOp",EDGE,"E7.12.5"),sQuery(id+"F0.wireOp",EDGE,"E7.13.0"),sQuery(id+"F0.wireOp",EDGE,"E7.13.1"),sQuery(id+"F0.wireOp",EDGE,"E7.13.2"),sQuery(id+"F0.wireOp",EDGE,"E7.13.3"),sQuery(id+"F0.wireOp",EDGE,"E7.13.4"),sQuery(id+"F0.wireOp",EDGE,"E7.13.5"),sQuery(id+"F0.wireOp",EDGE,"E7.14.0"),sQuery(id+"F0.wireOp",EDGE,"E7.14.1"),sQuery(id+"F0.wireOp",EDGE,"E7.14.2"),sQuery(id+"F0.wireOp",EDGE,"E7.14.3"),sQuery(id+"F0.wireOp",EDGE,"E7.14.4"),sQuery(id+"F0.wireOp",EDGE,"E7.14.5"),sQuery(id+"F0.wireOp",EDGE,"E7.15.0"),sQuery(id+"F0.wireOp",EDGE,"E7.15.1"),sQuery(id+"F0.wireOp",EDGE,"E7.15.2"),sQuery(id+"F0.wireOp",EDGE,"E7.15.3"),sQuery(id+"F0.wireOp",EDGE,"E7.15.4"),sQuery(id+"F0.wireOp",EDGE,"E7.15.5"),sQuery(id+"F0.wireOp",EDGE,"E7.16.0"),sQuery(id+"F0.wireOp",EDGE,"E7.16.1"),sQuery(id+"F0.wireOp",EDGE,"E7.16.2"),sQuery(id+"F0.wireOp",EDGE,"E7.16.3"),sQuery(id+"F0.wireOp",EDGE,"E7.16.4"),sQuery(id+"F0.wireOp",EDGE,"E7.16.5"),sQuery(id+"F0.wireOp",EDGE,"E7.17.0"),sQuery(id+"F0.wireOp",EDGE,"E7.17.1"),sQuery(id+"F0.wireOp",EDGE,"E7.17.2"),sQuery(id+"F0.wireOp",EDGE,"E7.17.3"),sQuery(id+"F0.wireOp",EDGE,"E7.17.4"),sQuery(id+"F0.wireOp",EDGE,"E7.17.5"),sQuery(id+"F0.wireOp",EDGE,"E7.18.0"),sQuery(id+"F0.wireOp",EDGE,"E7.18.1"),sQuery(id+"F0.wireOp",EDGE,"E7.18.2"),sQuery(id+"F0.wireOp",EDGE,"E7.18.3"),sQuery(id+"F0.wireOp",EDGE,"E7.18.4"),sQuery(id+"F0.wireOp",EDGE,"E7.18.5"),sQuery(id+"F0.wireOp",EDGE,"E7.19.0"),sQuery(id+"F0.wireOp",EDGE,"E7.19.1"),sQuery(id+"F0.wireOp",EDGE,"E7.19.2"),sQuery(id+"F0.wireOp",EDGE,"E7.19.3"),sQuery(id+"F0.wireOp",EDGE,"E7.19.4"),sQuery(id+"F0.wireOp",EDGE,"E7.19.5"),sQuery(id+"F0.wireOp",EDGE,"E7.20.0"),sQuery(id+"F0.wireOp",EDGE,"E7.20.1"),sQuery(id+"F0.wireOp",EDGE,"E7.20.2"),sQuery(id+"F0.wireOp",EDGE,"E7.20.3"),sQuery(id+"F0.wireOp",EDGE,"E7.20.4"),sQuery(id+"F0.wireOp",EDGE,"E7.20.5"),sQuery(id+"F0.wireOp",EDGE,"E7.21.0"),sQuery(id+"F0.wireOp",EDGE,"E7.21.1"),sQuery(id+"F0.wireOp",EDGE,"E7.21.2"),sQuery(id+"F0.wireOp",EDGE,"E7.21.3"),sQuery(id+"F0.wireOp",EDGE,"E7.21.4"),sQuery(id+"F0.wireOp",EDGE,"E7.21.5"),sQuery(id+"F0.wireOp",EDGE,"E7.22.0"),sQuery(id+"F0.wireOp",EDGE,"E7.22.1"),sQuery(id+"F0.wireOp",EDGE,"E7.22.2"),sQuery(id+"F0.wireOp",EDGE,"E7.22.3"),sQuery(id+"F0.wireOp",EDGE,"E7.22.4"),sQuery(id+"F0.wireOp",EDGE,"E7.22.5"),sQuery(id+"F0.wireOp",EDGE,"E7.23.0"),sQuery(id+"F0.wireOp",EDGE,"E7.23.1"),sQuery(id+"F0.wireOp",EDGE,"E7.23.2"),sQuery(id+"F0.wireOp",EDGE,"E7.23.3"),sQuery(id+"F0.wireOp",EDGE,"E7.23.4"),sQuery(id+"F0.wireOp",EDGE,"E7.23.5"),sQuery(id+"F0.wireOp",EDGE,"E7.24.0"),sQuery(id+"F0.wireOp",EDGE,"E7.24.1"),sQuery(id+"F0.wireOp",EDGE,"E7.24.2"),sQuery(id+"F0.wireOp",EDGE,"E7.24.3"),sQuery(id+"F0.wireOp",EDGE,"E7.24.4"),sQuery(id+"F0.wireOp",EDGE,"E7.24.5"),sQuery(id+"F0.wireOp",EDGE,"E7.25.0"),sQuery(id+"F0.wireOp",EDGE,"E7.25.1"),sQuery(id+"F0.wireOp",EDGE,"E7.25.2"),sQuery(id+"F0.wireOp",EDGE,"E7.25.3"),sQuery(id+"F0.wireOp",EDGE,"E7.25.4"),sQuery(id+"F0.wireOp",EDGE,"E7.25.5"),subQ0,sQuery(id+"F0.wireOp",EDGE,"E7.26.1"),sQuery(id+"F0.wireOp",EDGE,"E7.26.2"),sQuery(id+"F0.wireOp",EDGE,"E7.26.3"),sQuery(id+"F0.wireOp",EDGE,"E7.26.4"),sQuery(id+"F0.wireOp",EDGE,"E7.26.5"),sQuery(id+"F0.wireOp",EDGE,"E7.27.0"),sQuery(id+"F0.wireOp",EDGE,"E7.27.1"),sQuery(id+"F0.wireOp",EDGE,"E7.27.2"),sQuery(id+"F0.wireOp",EDGE,"E7.27.3"),sQuery(id+"F0.wireOp",EDGE,"E7.27.4"),sQuery(id+"F0.wireOp",EDGE,"E7.27.5"),sQuery(id+"F0.wireOp",EDGE,"E7.28.0"),sQuery(id+"F0.wireOp",EDGE,"E7.28.1"),sQuery(id+"F0.wireOp",EDGE,"E7.28.2"),sQuery(id+"F0.wireOp",EDGE,"E7.28.3"),sQuery(id+"F0.wireOp",EDGE,"E7.28.4"),sQuery(id+"F0.wireOp",EDGE,"E7.28.5"),sQuery(id+"F0.wireOp",EDGE,"E7.29.0"),sQuery(id+"F0.wireOp",EDGE,"E7.29.1"),sQuery(id+"F0.wireOp",EDGE,"E7.29.2"),sQuery(id+"F0.wireOp",EDGE,"E7.29.3"),sQuery(id+"F0.wireOp",EDGE,"E7.29.4"),sQuery(id+"F0.wireOp",EDGE,"E7.29.5"),sQuery(id+"F0.wireOp",EDGE,"E7.30.0"),sQuery(id+"F0.wireOp",EDGE,"E7.30.1"),sQuery(id+"F0.wireOp",EDGE,"E7.30.2"),sQuery(id+"F0.wireOp",EDGE,"E7.30.3"),sQuery(id+"F0.wireOp",EDGE,"E7.30.4"),sQuery(id+"F0.wireOp",EDGE,"E7.30.5"),sQuery(id+"F0.wireOp",EDGE,"E7.31.0"),sQuery(id+"F0.wireOp",EDGE,"E7.31.1"),sQuery(id+"F0.wireOp",EDGE,"E7.31.2"),sQuery(id+"F0.wireOp",EDGE,"E7.31.3"),sQuery(id+"F0.wireOp",EDGE,"E7.31.4"),sQuery(id+"F0.wireOp",EDGE,"E7.31.5"),sQuery(id+"F0.wireOp",EDGE,"E7.32.0"),sQuery(id+"F0.wireOp",EDGE,"E7.32.1"),sQuery(id+"F0.wireOp",EDGE,"E7.32.2"),sQuery(id+"F0.wireOp",EDGE,"E7.32.3"),sQuery(id+"F0.wireOp",EDGE,"E7.32.4"),sQuery(id+"F0.wireOp",EDGE,"E7.32.5"),sQuery(id+"F0.wireOp",EDGE,"E7.33.0"),sQuery(id+"F0.wireOp",EDGE,"E7.33.1"),sQuery(id+"F0.wireOp",EDGE,"E7.33.2"),sQuery(id+"F0.wireOp",EDGE,"E7.33.3"),sQuery(id+"F0.wireOp",EDGE,"E7.33.4"),sQuery(id+"F0.wireOp",EDGE,"E7.33.5"),sQuery(id+"F0.wireOp",EDGE,"E7.34.0"),sQuery(id+"F0.wireOp",EDGE,"E7.34.1"),sQuery(id+"F0.wireOp",EDGE,"E7.34.2"),sQuery(id+"F0.wireOp",EDGE,"E7.34.3"),sQuery(id+"F0.wireOp",EDGE,"E7.34.4"),sQuery(id+"F0.wireOp",EDGE,"E7.34.5"),sQuery(id+"F0.wireOp",EDGE,"E7.35.0"),sQuery(id+"F0.wireOp",EDGE,"E7.35.1"),sQuery(id+"F0.wireOp",EDGE,"E7.35.2"),sQuery(id+"F0.wireOp",EDGE,"E7.35.3"),sQuery(id+"F0.wireOp",EDGE,"E7.35.4"),sQuery(id+"F0.wireOp",EDGE,"E7.35.5"),sQuery(id+"F0.wireOp",EDGE,"E7.36.0"),sQuery(id+"F0.wireOp",EDGE,"E7.36.1"),sQuery(id+"F0.wireOp",EDGE,"E7.36.2"),sQuery(id+"F0.wireOp",EDGE,"E7.36.3"),sQuery(id+"F0.wireOp",EDGE,"E7.36.4"),sQuery(id+"F0.wireOp",EDGE,"E7.36.5"),sQuery(id+"F0.wireOp",EDGE,"E7.37.0"),sQuery(id+"F0.wireOp",EDGE,"E7.37.1"),sQuery(id+"F0.wireOp",EDGE,"E7.37.2"),sQuery(id+"F0.wireOp",EDGE,"E7.37.3"),sQuery(id+"F0.wireOp",EDGE,"E7.37.4"),sQuery(id+"F0.wireOp",EDGE,"E7.37.5"),sQuery(id+"F0.wireOp",EDGE,"E7.38.0"),sQuery(id+"F0.wireOp",EDGE,"E7.38.1"),sQuery(id+"F0.wireOp",EDGE,"E7.38.2"),sQuery(id+"F0.wireOp",EDGE,"E7.38.3"),sQuery(id+"F0.wireOp",EDGE,"E7.38.4"),sQuery(id+"F0.wireOp",EDGE,"E7.38.5"),sQuery(id+"F0.wireOp",EDGE,"E7.39.0"),sQuery(id+"F0.wireOp",EDGE,"E7.39.1"),sQuery(id+"F0.wireOp",EDGE,"E7.39.2"),sQuery(id+"F0.wireOp",EDGE,"E7.39.3"),sQuery(id+"F0.wireOp",EDGE,"E7.39.4"),sQuery(id+"F0.wireOp",EDGE,"E7.39.5"),sQuery(id+"F0.wireOp",EDGE,"E7.40.0"),sQuery(id+"F0.wireOp",EDGE,"E7.40.1"),sQuery(id+"F0.wireOp",EDGE,"E7.40.2"),sQuery(id+"F0.wireOp",EDGE,"E7.40.3"),sQuery(id+"F0.wireOp",EDGE,"E7.40.4"),sQuery(id+"F0.wireOp",EDGE,"E7.40.5"),sQuery(id+"F0.wireOp",EDGE,"E7.41.0"),sQuery(id+"F0.wireOp",EDGE,"E7.41.1"),sQuery(id+"F0.wireOp",EDGE,"E7.41.2"),sQuery(id+"F0.wireOp",EDGE,"E7.41.3"),sQuery(id+"F0.wireOp",EDGE,"E7.41.4"),sQuery(id+"F0.wireOp",EDGE,"E7.41.5"),sQuery(id+"F0.wireOp",EDGE,"E7.42.0"),sQuery(id+"F0.wireOp",EDGE,"E7.42.1"),sQuery(id+"F0.wireOp",EDGE,"E7.42.2"),sQuery(id+"F0.wireOp",EDGE,"E7.42.3"),sQuery(id+"F0.wireOp",EDGE,"E7.42.4"),sQuery(id+"F0.wireOp",EDGE,"E7.42.5"),sQuery(id+"F0.wireOp",EDGE,"E7.43.0"),sQuery(id+"F0.wireOp",EDGE,"E7.43.1"),sQuery(id+"F0.wireOp",EDGE,"E7.43.2"),sQuery(id+"F0.wireOp",EDGE,"E7.43.3"),sQuery(id+"F0.wireOp",EDGE,"E7.43.4"),sQuery(id+"F0.wireOp",EDGE,"E7.43.5")])],"isStart":true})]});}
            var Q35;
            {var subQ0=sQuery(id+"F0.wireOp",EDGE,"E7.28.0");Q35=makeQuery(id+"F2.opChamfer","BLEND_EDGE",EDGE,{"blendedFrom":[makeQuery(id+"F1.opExtrude","CAP_EDGE",EDGE,{"disambiguationData":[OSD([subQ0])],"isStart":true}),makeQuery(id+"F1.opExtrude","CAP_FACE",FACE,{"disambiguationData":[OSD([sQuery(id+"F0.wireOp",EDGE,"E1"),sQuery(id+"F0.wireOp",EDGE,"E2"),sQuery(id+"F0.wireOp",EDGE,"E3"),sQuery(id+"F0.wireOp",EDGE,"E4"),sQuery(id+"F0.wireOp",EDGE,"E5"),sQuery(id+"F0.wireOp",EDGE,"E6"),sQuery(id+"F0.wireOp",EDGE,"E7.1.0"),sQuery(id+"F0.wireOp",EDGE,"E7.1.1"),sQuery(id+"F0.wireOp",EDGE,"E7.1.2"),sQuery(id+"F0.wireOp",EDGE,"E7.1.3"),sQuery(id+"F0.wireOp",EDGE,"E7.1.4"),sQuery(id+"F0.wireOp",EDGE,"E7.1.5"),sQuery(id+"F0.wireOp",EDGE,"E7.2.0"),sQuery(id+"F0.wireOp",EDGE,"E7.2.1"),sQuery(id+"F0.wireOp",EDGE,"E7.2.2"),sQuery(id+"F0.wireOp",EDGE,"E7.2.3"),sQuery(id+"F0.wireOp",EDGE,"E7.2.4"),sQuery(id+"F0.wireOp",EDGE,"E7.2.5"),sQuery(id+"F0.wireOp",EDGE,"E7.3.0"),sQuery(id+"F0.wireOp",EDGE,"E7.3.1"),sQuery(id+"F0.wireOp",EDGE,"E7.3.2"),sQuery(id+"F0.wireOp",EDGE,"E7.3.3"),sQuery(id+"F0.wireOp",EDGE,"E7.3.4"),sQuery(id+"F0.wireOp",EDGE,"E7.3.5"),sQuery(id+"F0.wireOp",EDGE,"E7.4.0"),sQuery(id+"F0.wireOp",EDGE,"E7.4.1"),sQuery(id+"F0.wireOp",EDGE,"E7.4.2"),sQuery(id+"F0.wireOp",EDGE,"E7.4.3"),sQuery(id+"F0.wireOp",EDGE,"E7.4.4"),sQuery(id+"F0.wireOp",EDGE,"E7.4.5"),sQuery(id+"F0.wireOp",EDGE,"E7.5.0"),sQuery(id+"F0.wireOp",EDGE,"E7.5.1"),sQuery(id+"F0.wireOp",EDGE,"E7.5.2"),sQuery(id+"F0.wireOp",EDGE,"E7.5.3"),sQuery(id+"F0.wireOp",EDGE,"E7.5.4"),sQuery(id+"F0.wireOp",EDGE,"E7.5.5"),sQuery(id+"F0.wireOp",EDGE,"E7.6.0"),sQuery(id+"F0.wireOp",EDGE,"E7.6.1"),sQuery(id+"F0.wireOp",EDGE,"E7.6.2"),sQuery(id+"F0.wireOp",EDGE,"E7.6.3"),sQuery(id+"F0.wireOp",EDGE,"E7.6.4"),sQuery(id+"F0.wireOp",EDGE,"E7.6.5"),sQuery(id+"F0.wireOp",EDGE,"E7.7.0"),sQuery(id+"F0.wireOp",EDGE,"E7.7.1"),sQuery(id+"F0.wireOp",EDGE,"E7.7.2"),sQuery(id+"F0.wireOp",EDGE,"E7.7.3"),sQuery(id+"F0.wireOp",EDGE,"E7.7.4"),sQuery(id+"F0.wireOp",EDGE,"E7.7.5"),sQuery(id+"F0.wireOp",EDGE,"E7.8.0"),sQuery(id+"F0.wireOp",EDGE,"E7.8.1"),sQuery(id+"F0.wireOp",EDGE,"E7.8.2"),sQuery(id+"F0.wireOp",EDGE,"E7.8.3"),sQuery(id+"F0.wireOp",EDGE,"E7.8.4"),sQuery(id+"F0.wireOp",EDGE,"E7.8.5"),sQuery(id+"F0.wireOp",EDGE,"E7.9.0"),sQuery(id+"F0.wireOp",EDGE,"E7.9.1"),sQuery(id+"F0.wireOp",EDGE,"E7.9.2"),sQuery(id+"F0.wireOp",EDGE,"E7.9.3"),sQuery(id+"F0.wireOp",EDGE,"E7.9.4"),sQuery(id+"F0.wireOp",EDGE,"E7.9.5"),sQuery(id+"F0.wireOp",EDGE,"E7.10.0"),sQuery(id+"F0.wireOp",EDGE,"E7.10.1"),sQuery(id+"F0.wireOp",EDGE,"E7.10.2"),sQuery(id+"F0.wireOp",EDGE,"E7.10.3"),sQuery(id+"F0.wireOp",EDGE,"E7.10.4"),sQuery(id+"F0.wireOp",EDGE,"E7.10.5"),sQuery(id+"F0.wireOp",EDGE,"E7.11.0"),sQuery(id+"F0.wireOp",EDGE,"E7.11.1"),sQuery(id+"F0.wireOp",EDGE,"E7.11.2"),sQuery(id+"F0.wireOp",EDGE,"E7.11.3"),sQuery(id+"F0.wireOp",EDGE,"E7.11.4"),sQuery(id+"F0.wireOp",EDGE,"E7.11.5"),sQuery(id+"F0.wireOp",EDGE,"E7.12.0"),sQuery(id+"F0.wireOp",EDGE,"E7.12.1"),sQuery(id+"F0.wireOp",EDGE,"E7.12.2"),sQuery(id+"F0.wireOp",EDGE,"E7.12.3"),sQuery(id+"F0.wireOp",EDGE,"E7.12.4"),sQuery(id+"F0.wireOp",EDGE,"E7.12.5"),sQuery(id+"F0.wireOp",EDGE,"E7.13.0"),sQuery(id+"F0.wireOp",EDGE,"E7.13.1"),sQuery(id+"F0.wireOp",EDGE,"E7.13.2"),sQuery(id+"F0.wireOp",EDGE,"E7.13.3"),sQuery(id+"F0.wireOp",EDGE,"E7.13.4"),sQuery(id+"F0.wireOp",EDGE,"E7.13.5"),sQuery(id+"F0.wireOp",EDGE,"E7.14.0"),sQuery(id+"F0.wireOp",EDGE,"E7.14.1"),sQuery(id+"F0.wireOp",EDGE,"E7.14.2"),sQuery(id+"F0.wireOp",EDGE,"E7.14.3"),sQuery(id+"F0.wireOp",EDGE,"E7.14.4"),sQuery(id+"F0.wireOp",EDGE,"E7.14.5"),sQuery(id+"F0.wireOp",EDGE,"E7.15.0"),sQuery(id+"F0.wireOp",EDGE,"E7.15.1"),sQuery(id+"F0.wireOp",EDGE,"E7.15.2"),sQuery(id+"F0.wireOp",EDGE,"E7.15.3"),sQuery(id+"F0.wireOp",EDGE,"E7.15.4"),sQuery(id+"F0.wireOp",EDGE,"E7.15.5"),sQuery(id+"F0.wireOp",EDGE,"E7.16.0"),sQuery(id+"F0.wireOp",EDGE,"E7.16.1"),sQuery(id+"F0.wireOp",EDGE,"E7.16.2"),sQuery(id+"F0.wireOp",EDGE,"E7.16.3"),sQuery(id+"F0.wireOp",EDGE,"E7.16.4"),sQuery(id+"F0.wireOp",EDGE,"E7.16.5"),sQuery(id+"F0.wireOp",EDGE,"E7.17.0"),sQuery(id+"F0.wireOp",EDGE,"E7.17.1"),sQuery(id+"F0.wireOp",EDGE,"E7.17.2"),sQuery(id+"F0.wireOp",EDGE,"E7.17.3"),sQuery(id+"F0.wireOp",EDGE,"E7.17.4"),sQuery(id+"F0.wireOp",EDGE,"E7.17.5"),sQuery(id+"F0.wireOp",EDGE,"E7.18.0"),sQuery(id+"F0.wireOp",EDGE,"E7.18.1"),sQuery(id+"F0.wireOp",EDGE,"E7.18.2"),sQuery(id+"F0.wireOp",EDGE,"E7.18.3"),sQuery(id+"F0.wireOp",EDGE,"E7.18.4"),sQuery(id+"F0.wireOp",EDGE,"E7.18.5"),sQuery(id+"F0.wireOp",EDGE,"E7.19.0"),sQuery(id+"F0.wireOp",EDGE,"E7.19.1"),sQuery(id+"F0.wireOp",EDGE,"E7.19.2"),sQuery(id+"F0.wireOp",EDGE,"E7.19.3"),sQuery(id+"F0.wireOp",EDGE,"E7.19.4"),sQuery(id+"F0.wireOp",EDGE,"E7.19.5"),sQuery(id+"F0.wireOp",EDGE,"E7.20.0"),sQuery(id+"F0.wireOp",EDGE,"E7.20.1"),sQuery(id+"F0.wireOp",EDGE,"E7.20.2"),sQuery(id+"F0.wireOp",EDGE,"E7.20.3"),sQuery(id+"F0.wireOp",EDGE,"E7.20.4"),sQuery(id+"F0.wireOp",EDGE,"E7.20.5"),sQuery(id+"F0.wireOp",EDGE,"E7.21.0"),sQuery(id+"F0.wireOp",EDGE,"E7.21.1"),sQuery(id+"F0.wireOp",EDGE,"E7.21.2"),sQuery(id+"F0.wireOp",EDGE,"E7.21.3"),sQuery(id+"F0.wireOp",EDGE,"E7.21.4"),sQuery(id+"F0.wireOp",EDGE,"E7.21.5"),sQuery(id+"F0.wireOp",EDGE,"E7.22.0"),sQuery(id+"F0.wireOp",EDGE,"E7.22.1"),sQuery(id+"F0.wireOp",EDGE,"E7.22.2"),sQuery(id+"F0.wireOp",EDGE,"E7.22.3"),sQuery(id+"F0.wireOp",EDGE,"E7.22.4"),sQuery(id+"F0.wireOp",EDGE,"E7.22.5"),sQuery(id+"F0.wireOp",EDGE,"E7.23.0"),sQuery(id+"F0.wireOp",EDGE,"E7.23.1"),sQuery(id+"F0.wireOp",EDGE,"E7.23.2"),sQuery(id+"F0.wireOp",EDGE,"E7.23.3"),sQuery(id+"F0.wireOp",EDGE,"E7.23.4"),sQuery(id+"F0.wireOp",EDGE,"E7.23.5"),sQuery(id+"F0.wireOp",EDGE,"E7.24.0"),sQuery(id+"F0.wireOp",EDGE,"E7.24.1"),sQuery(id+"F0.wireOp",EDGE,"E7.24.2"),sQuery(id+"F0.wireOp",EDGE,"E7.24.3"),sQuery(id+"F0.wireOp",EDGE,"E7.24.4"),sQuery(id+"F0.wireOp",EDGE,"E7.24.5"),sQuery(id+"F0.wireOp",EDGE,"E7.25.0"),sQuery(id+"F0.wireOp",EDGE,"E7.25.1"),sQuery(id+"F0.wireOp",EDGE,"E7.25.2"),sQuery(id+"F0.wireOp",EDGE,"E7.25.3"),sQuery(id+"F0.wireOp",EDGE,"E7.25.4"),sQuery(id+"F0.wireOp",EDGE,"E7.25.5"),sQuery(id+"F0.wireOp",EDGE,"E7.26.0"),sQuery(id+"F0.wireOp",EDGE,"E7.26.1"),sQuery(id+"F0.wireOp",EDGE,"E7.26.2"),sQuery(id+"F0.wireOp",EDGE,"E7.26.3"),sQuery(id+"F0.wireOp",EDGE,"E7.26.4"),sQuery(id+"F0.wireOp",EDGE,"E7.26.5"),sQuery(id+"F0.wireOp",EDGE,"E7.27.0"),sQuery(id+"F0.wireOp",EDGE,"E7.27.1"),sQuery(id+"F0.wireOp",EDGE,"E7.27.2"),sQuery(id+"F0.wireOp",EDGE,"E7.27.3"),sQuery(id+"F0.wireOp",EDGE,"E7.27.4"),sQuery(id+"F0.wireOp",EDGE,"E7.27.5"),subQ0,sQuery(id+"F0.wireOp",EDGE,"E7.28.1"),sQuery(id+"F0.wireOp",EDGE,"E7.28.2"),sQuery(id+"F0.wireOp",EDGE,"E7.28.3"),sQuery(id+"F0.wireOp",EDGE,"E7.28.4"),sQuery(id+"F0.wireOp",EDGE,"E7.28.5"),sQuery(id+"F0.wireOp",EDGE,"E7.29.0"),sQuery(id+"F0.wireOp",EDGE,"E7.29.1"),sQuery(id+"F0.wireOp",EDGE,"E7.29.2"),sQuery(id+"F0.wireOp",EDGE,"E7.29.3"),sQuery(id+"F0.wireOp",EDGE,"E7.29.4"),sQuery(id+"F0.wireOp",EDGE,"E7.29.5"),sQuery(id+"F0.wireOp",EDGE,"E7.30.0"),sQuery(id+"F0.wireOp",EDGE,"E7.30.1"),sQuery(id+"F0.wireOp",EDGE,"E7.30.2"),sQuery(id+"F0.wireOp",EDGE,"E7.30.3"),sQuery(id+"F0.wireOp",EDGE,"E7.30.4"),sQuery(id+"F0.wireOp",EDGE,"E7.30.5"),sQuery(id+"F0.wireOp",EDGE,"E7.31.0"),sQuery(id+"F0.wireOp",EDGE,"E7.31.1"),sQuery(id+"F0.wireOp",EDGE,"E7.31.2"),sQuery(id+"F0.wireOp",EDGE,"E7.31.3"),sQuery(id+"F0.wireOp",EDGE,"E7.31.4"),sQuery(id+"F0.wireOp",EDGE,"E7.31.5"),sQuery(id+"F0.wireOp",EDGE,"E7.32.0"),sQuery(id+"F0.wireOp",EDGE,"E7.32.1"),sQuery(id+"F0.wireOp",EDGE,"E7.32.2"),sQuery(id+"F0.wireOp",EDGE,"E7.32.3"),sQuery(id+"F0.wireOp",EDGE,"E7.32.4"),sQuery(id+"F0.wireOp",EDGE,"E7.32.5"),sQuery(id+"F0.wireOp",EDGE,"E7.33.0"),sQuery(id+"F0.wireOp",EDGE,"E7.33.1"),sQuery(id+"F0.wireOp",EDGE,"E7.33.2"),sQuery(id+"F0.wireOp",EDGE,"E7.33.3"),sQuery(id+"F0.wireOp",EDGE,"E7.33.4"),sQuery(id+"F0.wireOp",EDGE,"E7.33.5"),sQuery(id+"F0.wireOp",EDGE,"E7.34.0"),sQuery(id+"F0.wireOp",EDGE,"E7.34.1"),sQuery(id+"F0.wireOp",EDGE,"E7.34.2"),sQuery(id+"F0.wireOp",EDGE,"E7.34.3"),sQuery(id+"F0.wireOp",EDGE,"E7.34.4"),sQuery(id+"F0.wireOp",EDGE,"E7.34.5"),sQuery(id+"F0.wireOp",EDGE,"E7.35.0"),sQuery(id+"F0.wireOp",EDGE,"E7.35.1"),sQuery(id+"F0.wireOp",EDGE,"E7.35.2"),sQuery(id+"F0.wireOp",EDGE,"E7.35.3"),sQuery(id+"F0.wireOp",EDGE,"E7.35.4"),sQuery(id+"F0.wireOp",EDGE,"E7.35.5"),sQuery(id+"F0.wireOp",EDGE,"E7.36.0"),sQuery(id+"F0.wireOp",EDGE,"E7.36.1"),sQuery(id+"F0.wireOp",EDGE,"E7.36.2"),sQuery(id+"F0.wireOp",EDGE,"E7.36.3"),sQuery(id+"F0.wireOp",EDGE,"E7.36.4"),sQuery(id+"F0.wireOp",EDGE,"E7.36.5"),sQuery(id+"F0.wireOp",EDGE,"E7.37.0"),sQuery(id+"F0.wireOp",EDGE,"E7.37.1"),sQuery(id+"F0.wireOp",EDGE,"E7.37.2"),sQuery(id+"F0.wireOp",EDGE,"E7.37.3"),sQuery(id+"F0.wireOp",EDGE,"E7.37.4"),sQuery(id+"F0.wireOp",EDGE,"E7.37.5"),sQuery(id+"F0.wireOp",EDGE,"E7.38.0"),sQuery(id+"F0.wireOp",EDGE,"E7.38.1"),sQuery(id+"F0.wireOp",EDGE,"E7.38.2"),sQuery(id+"F0.wireOp",EDGE,"E7.38.3"),sQuery(id+"F0.wireOp",EDGE,"E7.38.4"),sQuery(id+"F0.wireOp",EDGE,"E7.38.5"),sQuery(id+"F0.wireOp",EDGE,"E7.39.0"),sQuery(id+"F0.wireOp",EDGE,"E7.39.1"),sQuery(id+"F0.wireOp",EDGE,"E7.39.2"),sQuery(id+"F0.wireOp",EDGE,"E7.39.3"),sQuery(id+"F0.wireOp",EDGE,"E7.39.4"),sQuery(id+"F0.wireOp",EDGE,"E7.39.5"),sQuery(id+"F0.wireOp",EDGE,"E7.40.0"),sQuery(id+"F0.wireOp",EDGE,"E7.40.1"),sQuery(id+"F0.wireOp",EDGE,"E7.40.2"),sQuery(id+"F0.wireOp",EDGE,"E7.40.3"),sQuery(id+"F0.wireOp",EDGE,"E7.40.4"),sQuery(id+"F0.wireOp",EDGE,"E7.40.5"),sQuery(id+"F0.wireOp",EDGE,"E7.41.0"),sQuery(id+"F0.wireOp",EDGE,"E7.41.1"),sQuery(id+"F0.wireOp",EDGE,"E7.41.2"),sQuery(id+"F0.wireOp",EDGE,"E7.41.3"),sQuery(id+"F0.wireOp",EDGE,"E7.41.4"),sQuery(id+"F0.wireOp",EDGE,"E7.41.5"),sQuery(id+"F0.wireOp",EDGE,"E7.42.0"),sQuery(id+"F0.wireOp",EDGE,"E7.42.1"),sQuery(id+"F0.wireOp",EDGE,"E7.42.2"),sQuery(id+"F0.wireOp",EDGE,"E7.42.3"),sQuery(id+"F0.wireOp",EDGE,"E7.42.4"),sQuery(id+"F0.wireOp",EDGE,"E7.42.5"),sQuery(id+"F0.wireOp",EDGE,"E7.43.0"),sQuery(id+"F0.wireOp",EDGE,"E7.43.1"),sQuery(id+"F0.wireOp",EDGE,"E7.43.2"),sQuery(id+"F0.wireOp",EDGE,"E7.43.3"),sQuery(id+"F0.wireOp",EDGE,"E7.43.4"),sQuery(id+"F0.wireOp",EDGE,"E7.43.5")])],"isStart":true})],"blendedInto":[makeQuery(id+"F1.opExtrude","CAP_FACE",FACE,{"disambiguationData":[OSD([sQuery(id+"F0.wireOp",EDGE,"E1"),sQuery(id+"F0.wireOp",EDGE,"E2"),sQuery(id+"F0.wireOp",EDGE,"E3"),sQuery(id+"F0.wireOp",EDGE,"E4"),sQuery(id+"F0.wireOp",EDGE,"E5"),sQuery(id+"F0.wireOp",EDGE,"E6"),sQuery(id+"F0.wireOp",EDGE,"E7.1.0"),sQuery(id+"F0.wireOp",EDGE,"E7.1.1"),sQuery(id+"F0.wireOp",EDGE,"E7.1.2"),sQuery(id+"F0.wireOp",EDGE,"E7.1.3"),sQuery(id+"F0.wireOp",EDGE,"E7.1.4"),sQuery(id+"F0.wireOp",EDGE,"E7.1.5"),sQuery(id+"F0.wireOp",EDGE,"E7.2.0"),sQuery(id+"F0.wireOp",EDGE,"E7.2.1"),sQuery(id+"F0.wireOp",EDGE,"E7.2.2"),sQuery(id+"F0.wireOp",EDGE,"E7.2.3"),sQuery(id+"F0.wireOp",EDGE,"E7.2.4"),sQuery(id+"F0.wireOp",EDGE,"E7.2.5"),sQuery(id+"F0.wireOp",EDGE,"E7.3.0"),sQuery(id+"F0.wireOp",EDGE,"E7.3.1"),sQuery(id+"F0.wireOp",EDGE,"E7.3.2"),sQuery(id+"F0.wireOp",EDGE,"E7.3.3"),sQuery(id+"F0.wireOp",EDGE,"E7.3.4"),sQuery(id+"F0.wireOp",EDGE,"E7.3.5"),sQuery(id+"F0.wireOp",EDGE,"E7.4.0"),sQuery(id+"F0.wireOp",EDGE,"E7.4.1"),sQuery(id+"F0.wireOp",EDGE,"E7.4.2"),sQuery(id+"F0.wireOp",EDGE,"E7.4.3"),sQuery(id+"F0.wireOp",EDGE,"E7.4.4"),sQuery(id+"F0.wireOp",EDGE,"E7.4.5"),sQuery(id+"F0.wireOp",EDGE,"E7.5.0"),sQuery(id+"F0.wireOp",EDGE,"E7.5.1"),sQuery(id+"F0.wireOp",EDGE,"E7.5.2"),sQuery(id+"F0.wireOp",EDGE,"E7.5.3"),sQuery(id+"F0.wireOp",EDGE,"E7.5.4"),sQuery(id+"F0.wireOp",EDGE,"E7.5.5"),sQuery(id+"F0.wireOp",EDGE,"E7.6.0"),sQuery(id+"F0.wireOp",EDGE,"E7.6.1"),sQuery(id+"F0.wireOp",EDGE,"E7.6.2"),sQuery(id+"F0.wireOp",EDGE,"E7.6.3"),sQuery(id+"F0.wireOp",EDGE,"E7.6.4"),sQuery(id+"F0.wireOp",EDGE,"E7.6.5"),sQuery(id+"F0.wireOp",EDGE,"E7.7.0"),sQuery(id+"F0.wireOp",EDGE,"E7.7.1"),sQuery(id+"F0.wireOp",EDGE,"E7.7.2"),sQuery(id+"F0.wireOp",EDGE,"E7.7.3"),sQuery(id+"F0.wireOp",EDGE,"E7.7.4"),sQuery(id+"F0.wireOp",EDGE,"E7.7.5"),sQuery(id+"F0.wireOp",EDGE,"E7.8.0"),sQuery(id+"F0.wireOp",EDGE,"E7.8.1"),sQuery(id+"F0.wireOp",EDGE,"E7.8.2"),sQuery(id+"F0.wireOp",EDGE,"E7.8.3"),sQuery(id+"F0.wireOp",EDGE,"E7.8.4"),sQuery(id+"F0.wireOp",EDGE,"E7.8.5"),sQuery(id+"F0.wireOp",EDGE,"E7.9.0"),sQuery(id+"F0.wireOp",EDGE,"E7.9.1"),sQuery(id+"F0.wireOp",EDGE,"E7.9.2"),sQuery(id+"F0.wireOp",EDGE,"E7.9.3"),sQuery(id+"F0.wireOp",EDGE,"E7.9.4"),sQuery(id+"F0.wireOp",EDGE,"E7.9.5"),sQuery(id+"F0.wireOp",EDGE,"E7.10.0"),sQuery(id+"F0.wireOp",EDGE,"E7.10.1"),sQuery(id+"F0.wireOp",EDGE,"E7.10.2"),sQuery(id+"F0.wireOp",EDGE,"E7.10.3"),sQuery(id+"F0.wireOp",EDGE,"E7.10.4"),sQuery(id+"F0.wireOp",EDGE,"E7.10.5"),sQuery(id+"F0.wireOp",EDGE,"E7.11.0"),sQuery(id+"F0.wireOp",EDGE,"E7.11.1"),sQuery(id+"F0.wireOp",EDGE,"E7.11.2"),sQuery(id+"F0.wireOp",EDGE,"E7.11.3"),sQuery(id+"F0.wireOp",EDGE,"E7.11.4"),sQuery(id+"F0.wireOp",EDGE,"E7.11.5"),sQuery(id+"F0.wireOp",EDGE,"E7.12.0"),sQuery(id+"F0.wireOp",EDGE,"E7.12.1"),sQuery(id+"F0.wireOp",EDGE,"E7.12.2"),sQuery(id+"F0.wireOp",EDGE,"E7.12.3"),sQuery(id+"F0.wireOp",EDGE,"E7.12.4"),sQuery(id+"F0.wireOp",EDGE,"E7.12.5"),sQuery(id+"F0.wireOp",EDGE,"E7.13.0"),sQuery(id+"F0.wireOp",EDGE,"E7.13.1"),sQuery(id+"F0.wireOp",EDGE,"E7.13.2"),sQuery(id+"F0.wireOp",EDGE,"E7.13.3"),sQuery(id+"F0.wireOp",EDGE,"E7.13.4"),sQuery(id+"F0.wireOp",EDGE,"E7.13.5"),sQuery(id+"F0.wireOp",EDGE,"E7.14.0"),sQuery(id+"F0.wireOp",EDGE,"E7.14.1"),sQuery(id+"F0.wireOp",EDGE,"E7.14.2"),sQuery(id+"F0.wireOp",EDGE,"E7.14.3"),sQuery(id+"F0.wireOp",EDGE,"E7.14.4"),sQuery(id+"F0.wireOp",EDGE,"E7.14.5"),sQuery(id+"F0.wireOp",EDGE,"E7.15.0"),sQuery(id+"F0.wireOp",EDGE,"E7.15.1"),sQuery(id+"F0.wireOp",EDGE,"E7.15.2"),sQuery(id+"F0.wireOp",EDGE,"E7.15.3"),sQuery(id+"F0.wireOp",EDGE,"E7.15.4"),sQuery(id+"F0.wireOp",EDGE,"E7.15.5"),sQuery(id+"F0.wireOp",EDGE,"E7.16.0"),sQuery(id+"F0.wireOp",EDGE,"E7.16.1"),sQuery(id+"F0.wireOp",EDGE,"E7.16.2"),sQuery(id+"F0.wireOp",EDGE,"E7.16.3"),sQuery(id+"F0.wireOp",EDGE,"E7.16.4"),sQuery(id+"F0.wireOp",EDGE,"E7.16.5"),sQuery(id+"F0.wireOp",EDGE,"E7.17.0"),sQuery(id+"F0.wireOp",EDGE,"E7.17.1"),sQuery(id+"F0.wireOp",EDGE,"E7.17.2"),sQuery(id+"F0.wireOp",EDGE,"E7.17.3"),sQuery(id+"F0.wireOp",EDGE,"E7.17.4"),sQuery(id+"F0.wireOp",EDGE,"E7.17.5"),sQuery(id+"F0.wireOp",EDGE,"E7.18.0"),sQuery(id+"F0.wireOp",EDGE,"E7.18.1"),sQuery(id+"F0.wireOp",EDGE,"E7.18.2"),sQuery(id+"F0.wireOp",EDGE,"E7.18.3"),sQuery(id+"F0.wireOp",EDGE,"E7.18.4"),sQuery(id+"F0.wireOp",EDGE,"E7.18.5"),sQuery(id+"F0.wireOp",EDGE,"E7.19.0"),sQuery(id+"F0.wireOp",EDGE,"E7.19.1"),sQuery(id+"F0.wireOp",EDGE,"E7.19.2"),sQuery(id+"F0.wireOp",EDGE,"E7.19.3"),sQuery(id+"F0.wireOp",EDGE,"E7.19.4"),sQuery(id+"F0.wireOp",EDGE,"E7.19.5"),sQuery(id+"F0.wireOp",EDGE,"E7.20.0"),sQuery(id+"F0.wireOp",EDGE,"E7.20.1"),sQuery(id+"F0.wireOp",EDGE,"E7.20.2"),sQuery(id+"F0.wireOp",EDGE,"E7.20.3"),sQuery(id+"F0.wireOp",EDGE,"E7.20.4"),sQuery(id+"F0.wireOp",EDGE,"E7.20.5"),sQuery(id+"F0.wireOp",EDGE,"E7.21.0"),sQuery(id+"F0.wireOp",EDGE,"E7.21.1"),sQuery(id+"F0.wireOp",EDGE,"E7.21.2"),sQuery(id+"F0.wireOp",EDGE,"E7.21.3"),sQuery(id+"F0.wireOp",EDGE,"E7.21.4"),sQuery(id+"F0.wireOp",EDGE,"E7.21.5"),sQuery(id+"F0.wireOp",EDGE,"E7.22.0"),sQuery(id+"F0.wireOp",EDGE,"E7.22.1"),sQuery(id+"F0.wireOp",EDGE,"E7.22.2"),sQuery(id+"F0.wireOp",EDGE,"E7.22.3"),sQuery(id+"F0.wireOp",EDGE,"E7.22.4"),sQuery(id+"F0.wireOp",EDGE,"E7.22.5"),sQuery(id+"F0.wireOp",EDGE,"E7.23.0"),sQuery(id+"F0.wireOp",EDGE,"E7.23.1"),sQuery(id+"F0.wireOp",EDGE,"E7.23.2"),sQuery(id+"F0.wireOp",EDGE,"E7.23.3"),sQuery(id+"F0.wireOp",EDGE,"E7.23.4"),sQuery(id+"F0.wireOp",EDGE,"E7.23.5"),sQuery(id+"F0.wireOp",EDGE,"E7.24.0"),sQuery(id+"F0.wireOp",EDGE,"E7.24.1"),sQuery(id+"F0.wireOp",EDGE,"E7.24.2"),sQuery(id+"F0.wireOp",EDGE,"E7.24.3"),sQuery(id+"F0.wireOp",EDGE,"E7.24.4"),sQuery(id+"F0.wireOp",EDGE,"E7.24.5"),sQuery(id+"F0.wireOp",EDGE,"E7.25.0"),sQuery(id+"F0.wireOp",EDGE,"E7.25.1"),sQuery(id+"F0.wireOp",EDGE,"E7.25.2"),sQuery(id+"F0.wireOp",EDGE,"E7.25.3"),sQuery(id+"F0.wireOp",EDGE,"E7.25.4"),sQuery(id+"F0.wireOp",EDGE,"E7.25.5"),sQuery(id+"F0.wireOp",EDGE,"E7.26.0"),sQuery(id+"F0.wireOp",EDGE,"E7.26.1"),sQuery(id+"F0.wireOp",EDGE,"E7.26.2"),sQuery(id+"F0.wireOp",EDGE,"E7.26.3"),sQuery(id+"F0.wireOp",EDGE,"E7.26.4"),sQuery(id+"F0.wireOp",EDGE,"E7.26.5"),sQuery(id+"F0.wireOp",EDGE,"E7.27.0"),sQuery(id+"F0.wireOp",EDGE,"E7.27.1"),sQuery(id+"F0.wireOp",EDGE,"E7.27.2"),sQuery(id+"F0.wireOp",EDGE,"E7.27.3"),sQuery(id+"F0.wireOp",EDGE,"E7.27.4"),sQuery(id+"F0.wireOp",EDGE,"E7.27.5"),subQ0,sQuery(id+"F0.wireOp",EDGE,"E7.28.1"),sQuery(id+"F0.wireOp",EDGE,"E7.28.2"),sQuery(id+"F0.wireOp",EDGE,"E7.28.3"),sQuery(id+"F0.wireOp",EDGE,"E7.28.4"),sQuery(id+"F0.wireOp",EDGE,"E7.28.5"),sQuery(id+"F0.wireOp",EDGE,"E7.29.0"),sQuery(id+"F0.wireOp",EDGE,"E7.29.1"),sQuery(id+"F0.wireOp",EDGE,"E7.29.2"),sQuery(id+"F0.wireOp",EDGE,"E7.29.3"),sQuery(id+"F0.wireOp",EDGE,"E7.29.4"),sQuery(id+"F0.wireOp",EDGE,"E7.29.5"),sQuery(id+"F0.wireOp",EDGE,"E7.30.0"),sQuery(id+"F0.wireOp",EDGE,"E7.30.1"),sQuery(id+"F0.wireOp",EDGE,"E7.30.2"),sQuery(id+"F0.wireOp",EDGE,"E7.30.3"),sQuery(id+"F0.wireOp",EDGE,"E7.30.4"),sQuery(id+"F0.wireOp",EDGE,"E7.30.5"),sQuery(id+"F0.wireOp",EDGE,"E7.31.0"),sQuery(id+"F0.wireOp",EDGE,"E7.31.1"),sQuery(id+"F0.wireOp",EDGE,"E7.31.2"),sQuery(id+"F0.wireOp",EDGE,"E7.31.3"),sQuery(id+"F0.wireOp",EDGE,"E7.31.4"),sQuery(id+"F0.wireOp",EDGE,"E7.31.5"),sQuery(id+"F0.wireOp",EDGE,"E7.32.0"),sQuery(id+"F0.wireOp",EDGE,"E7.32.1"),sQuery(id+"F0.wireOp",EDGE,"E7.32.2"),sQuery(id+"F0.wireOp",EDGE,"E7.32.3"),sQuery(id+"F0.wireOp",EDGE,"E7.32.4"),sQuery(id+"F0.wireOp",EDGE,"E7.32.5"),sQuery(id+"F0.wireOp",EDGE,"E7.33.0"),sQuery(id+"F0.wireOp",EDGE,"E7.33.1"),sQuery(id+"F0.wireOp",EDGE,"E7.33.2"),sQuery(id+"F0.wireOp",EDGE,"E7.33.3"),sQuery(id+"F0.wireOp",EDGE,"E7.33.4"),sQuery(id+"F0.wireOp",EDGE,"E7.33.5"),sQuery(id+"F0.wireOp",EDGE,"E7.34.0"),sQuery(id+"F0.wireOp",EDGE,"E7.34.1"),sQuery(id+"F0.wireOp",EDGE,"E7.34.2"),sQuery(id+"F0.wireOp",EDGE,"E7.34.3"),sQuery(id+"F0.wireOp",EDGE,"E7.34.4"),sQuery(id+"F0.wireOp",EDGE,"E7.34.5"),sQuery(id+"F0.wireOp",EDGE,"E7.35.0"),sQuery(id+"F0.wireOp",EDGE,"E7.35.1"),sQuery(id+"F0.wireOp",EDGE,"E7.35.2"),sQuery(id+"F0.wireOp",EDGE,"E7.35.3"),sQuery(id+"F0.wireOp",EDGE,"E7.35.4"),sQuery(id+"F0.wireOp",EDGE,"E7.35.5"),sQuery(id+"F0.wireOp",EDGE,"E7.36.0"),sQuery(id+"F0.wireOp",EDGE,"E7.36.1"),sQuery(id+"F0.wireOp",EDGE,"E7.36.2"),sQuery(id+"F0.wireOp",EDGE,"E7.36.3"),sQuery(id+"F0.wireOp",EDGE,"E7.36.4"),sQuery(id+"F0.wireOp",EDGE,"E7.36.5"),sQuery(id+"F0.wireOp",EDGE,"E7.37.0"),sQuery(id+"F0.wireOp",EDGE,"E7.37.1"),sQuery(id+"F0.wireOp",EDGE,"E7.37.2"),sQuery(id+"F0.wireOp",EDGE,"E7.37.3"),sQuery(id+"F0.wireOp",EDGE,"E7.37.4"),sQuery(id+"F0.wireOp",EDGE,"E7.37.5"),sQuery(id+"F0.wireOp",EDGE,"E7.38.0"),sQuery(id+"F0.wireOp",EDGE,"E7.38.1"),sQuery(id+"F0.wireOp",EDGE,"E7.38.2"),sQuery(id+"F0.wireOp",EDGE,"E7.38.3"),sQuery(id+"F0.wireOp",EDGE,"E7.38.4"),sQuery(id+"F0.wireOp",EDGE,"E7.38.5"),sQuery(id+"F0.wireOp",EDGE,"E7.39.0"),sQuery(id+"F0.wireOp",EDGE,"E7.39.1"),sQuery(id+"F0.wireOp",EDGE,"E7.39.2"),sQuery(id+"F0.wireOp",EDGE,"E7.39.3"),sQuery(id+"F0.wireOp",EDGE,"E7.39.4"),sQuery(id+"F0.wireOp",EDGE,"E7.39.5"),sQuery(id+"F0.wireOp",EDGE,"E7.40.0"),sQuery(id+"F0.wireOp",EDGE,"E7.40.1"),sQuery(id+"F0.wireOp",EDGE,"E7.40.2"),sQuery(id+"F0.wireOp",EDGE,"E7.40.3"),sQuery(id+"F0.wireOp",EDGE,"E7.40.4"),sQuery(id+"F0.wireOp",EDGE,"E7.40.5"),sQuery(id+"F0.wireOp",EDGE,"E7.41.0"),sQuery(id+"F0.wireOp",EDGE,"E7.41.1"),sQuery(id+"F0.wireOp",EDGE,"E7.41.2"),sQuery(id+"F0.wireOp",EDGE,"E7.41.3"),sQuery(id+"F0.wireOp",EDGE,"E7.41.4"),sQuery(id+"F0.wireOp",EDGE,"E7.41.5"),sQuery(id+"F0.wireOp",EDGE,"E7.42.0"),sQuery(id+"F0.wireOp",EDGE,"E7.42.1"),sQuery(id+"F0.wireOp",EDGE,"E7.42.2"),sQuery(id+"F0.wireOp",EDGE,"E7.42.3"),sQuery(id+"F0.wireOp",EDGE,"E7.42.4"),sQuery(id+"F0.wireOp",EDGE,"E7.42.5"),sQuery(id+"F0.wireOp",EDGE,"E7.43.0"),sQuery(id+"F0.wireOp",EDGE,"E7.43.1"),sQuery(id+"F0.wireOp",EDGE,"E7.43.2"),sQuery(id+"F0.wireOp",EDGE,"E7.43.3"),sQuery(id+"F0.wireOp",EDGE,"E7.43.4"),sQuery(id+"F0.wireOp",EDGE,"E7.43.5")])],"isStart":true})]});}
            var Q36;
            {var subQ0=sQuery(id+"F0.wireOp",EDGE,"E7.30.0");Q36=makeQuery(id+"F2.opChamfer","BLEND_EDGE",EDGE,{"blendedFrom":[makeQuery(id+"F1.opExtrude","CAP_EDGE",EDGE,{"disambiguationData":[OSD([subQ0])],"isStart":true}),makeQuery(id+"F1.opExtrude","CAP_FACE",FACE,{"disambiguationData":[OSD([sQuery(id+"F0.wireOp",EDGE,"E1"),sQuery(id+"F0.wireOp",EDGE,"E2"),sQuery(id+"F0.wireOp",EDGE,"E3"),sQuery(id+"F0.wireOp",EDGE,"E4"),sQuery(id+"F0.wireOp",EDGE,"E5"),sQuery(id+"F0.wireOp",EDGE,"E6"),sQuery(id+"F0.wireOp",EDGE,"E7.1.0"),sQuery(id+"F0.wireOp",EDGE,"E7.1.1"),sQuery(id+"F0.wireOp",EDGE,"E7.1.2"),sQuery(id+"F0.wireOp",EDGE,"E7.1.3"),sQuery(id+"F0.wireOp",EDGE,"E7.1.4"),sQuery(id+"F0.wireOp",EDGE,"E7.1.5"),sQuery(id+"F0.wireOp",EDGE,"E7.2.0"),sQuery(id+"F0.wireOp",EDGE,"E7.2.1"),sQuery(id+"F0.wireOp",EDGE,"E7.2.2"),sQuery(id+"F0.wireOp",EDGE,"E7.2.3"),sQuery(id+"F0.wireOp",EDGE,"E7.2.4"),sQuery(id+"F0.wireOp",EDGE,"E7.2.5"),sQuery(id+"F0.wireOp",EDGE,"E7.3.0"),sQuery(id+"F0.wireOp",EDGE,"E7.3.1"),sQuery(id+"F0.wireOp",EDGE,"E7.3.2"),sQuery(id+"F0.wireOp",EDGE,"E7.3.3"),sQuery(id+"F0.wireOp",EDGE,"E7.3.4"),sQuery(id+"F0.wireOp",EDGE,"E7.3.5"),sQuery(id+"F0.wireOp",EDGE,"E7.4.0"),sQuery(id+"F0.wireOp",EDGE,"E7.4.1"),sQuery(id+"F0.wireOp",EDGE,"E7.4.2"),sQuery(id+"F0.wireOp",EDGE,"E7.4.3"),sQuery(id+"F0.wireOp",EDGE,"E7.4.4"),sQuery(id+"F0.wireOp",EDGE,"E7.4.5"),sQuery(id+"F0.wireOp",EDGE,"E7.5.0"),sQuery(id+"F0.wireOp",EDGE,"E7.5.1"),sQuery(id+"F0.wireOp",EDGE,"E7.5.2"),sQuery(id+"F0.wireOp",EDGE,"E7.5.3"),sQuery(id+"F0.wireOp",EDGE,"E7.5.4"),sQuery(id+"F0.wireOp",EDGE,"E7.5.5"),sQuery(id+"F0.wireOp",EDGE,"E7.6.0"),sQuery(id+"F0.wireOp",EDGE,"E7.6.1"),sQuery(id+"F0.wireOp",EDGE,"E7.6.2"),sQuery(id+"F0.wireOp",EDGE,"E7.6.3"),sQuery(id+"F0.wireOp",EDGE,"E7.6.4"),sQuery(id+"F0.wireOp",EDGE,"E7.6.5"),sQuery(id+"F0.wireOp",EDGE,"E7.7.0"),sQuery(id+"F0.wireOp",EDGE,"E7.7.1"),sQuery(id+"F0.wireOp",EDGE,"E7.7.2"),sQuery(id+"F0.wireOp",EDGE,"E7.7.3"),sQuery(id+"F0.wireOp",EDGE,"E7.7.4"),sQuery(id+"F0.wireOp",EDGE,"E7.7.5"),sQuery(id+"F0.wireOp",EDGE,"E7.8.0"),sQuery(id+"F0.wireOp",EDGE,"E7.8.1"),sQuery(id+"F0.wireOp",EDGE,"E7.8.2"),sQuery(id+"F0.wireOp",EDGE,"E7.8.3"),sQuery(id+"F0.wireOp",EDGE,"E7.8.4"),sQuery(id+"F0.wireOp",EDGE,"E7.8.5"),sQuery(id+"F0.wireOp",EDGE,"E7.9.0"),sQuery(id+"F0.wireOp",EDGE,"E7.9.1"),sQuery(id+"F0.wireOp",EDGE,"E7.9.2"),sQuery(id+"F0.wireOp",EDGE,"E7.9.3"),sQuery(id+"F0.wireOp",EDGE,"E7.9.4"),sQuery(id+"F0.wireOp",EDGE,"E7.9.5"),sQuery(id+"F0.wireOp",EDGE,"E7.10.0"),sQuery(id+"F0.wireOp",EDGE,"E7.10.1"),sQuery(id+"F0.wireOp",EDGE,"E7.10.2"),sQuery(id+"F0.wireOp",EDGE,"E7.10.3"),sQuery(id+"F0.wireOp",EDGE,"E7.10.4"),sQuery(id+"F0.wireOp",EDGE,"E7.10.5"),sQuery(id+"F0.wireOp",EDGE,"E7.11.0"),sQuery(id+"F0.wireOp",EDGE,"E7.11.1"),sQuery(id+"F0.wireOp",EDGE,"E7.11.2"),sQuery(id+"F0.wireOp",EDGE,"E7.11.3"),sQuery(id+"F0.wireOp",EDGE,"E7.11.4"),sQuery(id+"F0.wireOp",EDGE,"E7.11.5"),sQuery(id+"F0.wireOp",EDGE,"E7.12.0"),sQuery(id+"F0.wireOp",EDGE,"E7.12.1"),sQuery(id+"F0.wireOp",EDGE,"E7.12.2"),sQuery(id+"F0.wireOp",EDGE,"E7.12.3"),sQuery(id+"F0.wireOp",EDGE,"E7.12.4"),sQuery(id+"F0.wireOp",EDGE,"E7.12.5"),sQuery(id+"F0.wireOp",EDGE,"E7.13.0"),sQuery(id+"F0.wireOp",EDGE,"E7.13.1"),sQuery(id+"F0.wireOp",EDGE,"E7.13.2"),sQuery(id+"F0.wireOp",EDGE,"E7.13.3"),sQuery(id+"F0.wireOp",EDGE,"E7.13.4"),sQuery(id+"F0.wireOp",EDGE,"E7.13.5"),sQuery(id+"F0.wireOp",EDGE,"E7.14.0"),sQuery(id+"F0.wireOp",EDGE,"E7.14.1"),sQuery(id+"F0.wireOp",EDGE,"E7.14.2"),sQuery(id+"F0.wireOp",EDGE,"E7.14.3"),sQuery(id+"F0.wireOp",EDGE,"E7.14.4"),sQuery(id+"F0.wireOp",EDGE,"E7.14.5"),sQuery(id+"F0.wireOp",EDGE,"E7.15.0"),sQuery(id+"F0.wireOp",EDGE,"E7.15.1"),sQuery(id+"F0.wireOp",EDGE,"E7.15.2"),sQuery(id+"F0.wireOp",EDGE,"E7.15.3"),sQuery(id+"F0.wireOp",EDGE,"E7.15.4"),sQuery(id+"F0.wireOp",EDGE,"E7.15.5"),sQuery(id+"F0.wireOp",EDGE,"E7.16.0"),sQuery(id+"F0.wireOp",EDGE,"E7.16.1"),sQuery(id+"F0.wireOp",EDGE,"E7.16.2"),sQuery(id+"F0.wireOp",EDGE,"E7.16.3"),sQuery(id+"F0.wireOp",EDGE,"E7.16.4"),sQuery(id+"F0.wireOp",EDGE,"E7.16.5"),sQuery(id+"F0.wireOp",EDGE,"E7.17.0"),sQuery(id+"F0.wireOp",EDGE,"E7.17.1"),sQuery(id+"F0.wireOp",EDGE,"E7.17.2"),sQuery(id+"F0.wireOp",EDGE,"E7.17.3"),sQuery(id+"F0.wireOp",EDGE,"E7.17.4"),sQuery(id+"F0.wireOp",EDGE,"E7.17.5"),sQuery(id+"F0.wireOp",EDGE,"E7.18.0"),sQuery(id+"F0.wireOp",EDGE,"E7.18.1"),sQuery(id+"F0.wireOp",EDGE,"E7.18.2"),sQuery(id+"F0.wireOp",EDGE,"E7.18.3"),sQuery(id+"F0.wireOp",EDGE,"E7.18.4"),sQuery(id+"F0.wireOp",EDGE,"E7.18.5"),sQuery(id+"F0.wireOp",EDGE,"E7.19.0"),sQuery(id+"F0.wireOp",EDGE,"E7.19.1"),sQuery(id+"F0.wireOp",EDGE,"E7.19.2"),sQuery(id+"F0.wireOp",EDGE,"E7.19.3"),sQuery(id+"F0.wireOp",EDGE,"E7.19.4"),sQuery(id+"F0.wireOp",EDGE,"E7.19.5"),sQuery(id+"F0.wireOp",EDGE,"E7.20.0"),sQuery(id+"F0.wireOp",EDGE,"E7.20.1"),sQuery(id+"F0.wireOp",EDGE,"E7.20.2"),sQuery(id+"F0.wireOp",EDGE,"E7.20.3"),sQuery(id+"F0.wireOp",EDGE,"E7.20.4"),sQuery(id+"F0.wireOp",EDGE,"E7.20.5"),sQuery(id+"F0.wireOp",EDGE,"E7.21.0"),sQuery(id+"F0.wireOp",EDGE,"E7.21.1"),sQuery(id+"F0.wireOp",EDGE,"E7.21.2"),sQuery(id+"F0.wireOp",EDGE,"E7.21.3"),sQuery(id+"F0.wireOp",EDGE,"E7.21.4"),sQuery(id+"F0.wireOp",EDGE,"E7.21.5"),sQuery(id+"F0.wireOp",EDGE,"E7.22.0"),sQuery(id+"F0.wireOp",EDGE,"E7.22.1"),sQuery(id+"F0.wireOp",EDGE,"E7.22.2"),sQuery(id+"F0.wireOp",EDGE,"E7.22.3"),sQuery(id+"F0.wireOp",EDGE,"E7.22.4"),sQuery(id+"F0.wireOp",EDGE,"E7.22.5"),sQuery(id+"F0.wireOp",EDGE,"E7.23.0"),sQuery(id+"F0.wireOp",EDGE,"E7.23.1"),sQuery(id+"F0.wireOp",EDGE,"E7.23.2"),sQuery(id+"F0.wireOp",EDGE,"E7.23.3"),sQuery(id+"F0.wireOp",EDGE,"E7.23.4"),sQuery(id+"F0.wireOp",EDGE,"E7.23.5"),sQuery(id+"F0.wireOp",EDGE,"E7.24.0"),sQuery(id+"F0.wireOp",EDGE,"E7.24.1"),sQuery(id+"F0.wireOp",EDGE,"E7.24.2"),sQuery(id+"F0.wireOp",EDGE,"E7.24.3"),sQuery(id+"F0.wireOp",EDGE,"E7.24.4"),sQuery(id+"F0.wireOp",EDGE,"E7.24.5"),sQuery(id+"F0.wireOp",EDGE,"E7.25.0"),sQuery(id+"F0.wireOp",EDGE,"E7.25.1"),sQuery(id+"F0.wireOp",EDGE,"E7.25.2"),sQuery(id+"F0.wireOp",EDGE,"E7.25.3"),sQuery(id+"F0.wireOp",EDGE,"E7.25.4"),sQuery(id+"F0.wireOp",EDGE,"E7.25.5"),sQuery(id+"F0.wireOp",EDGE,"E7.26.0"),sQuery(id+"F0.wireOp",EDGE,"E7.26.1"),sQuery(id+"F0.wireOp",EDGE,"E7.26.2"),sQuery(id+"F0.wireOp",EDGE,"E7.26.3"),sQuery(id+"F0.wireOp",EDGE,"E7.26.4"),sQuery(id+"F0.wireOp",EDGE,"E7.26.5"),sQuery(id+"F0.wireOp",EDGE,"E7.27.0"),sQuery(id+"F0.wireOp",EDGE,"E7.27.1"),sQuery(id+"F0.wireOp",EDGE,"E7.27.2"),sQuery(id+"F0.wireOp",EDGE,"E7.27.3"),sQuery(id+"F0.wireOp",EDGE,"E7.27.4"),sQuery(id+"F0.wireOp",EDGE,"E7.27.5"),sQuery(id+"F0.wireOp",EDGE,"E7.28.0"),sQuery(id+"F0.wireOp",EDGE,"E7.28.1"),sQuery(id+"F0.wireOp",EDGE,"E7.28.2"),sQuery(id+"F0.wireOp",EDGE,"E7.28.3"),sQuery(id+"F0.wireOp",EDGE,"E7.28.4"),sQuery(id+"F0.wireOp",EDGE,"E7.28.5"),sQuery(id+"F0.wireOp",EDGE,"E7.29.0"),sQuery(id+"F0.wireOp",EDGE,"E7.29.1"),sQuery(id+"F0.wireOp",EDGE,"E7.29.2"),sQuery(id+"F0.wireOp",EDGE,"E7.29.3"),sQuery(id+"F0.wireOp",EDGE,"E7.29.4"),sQuery(id+"F0.wireOp",EDGE,"E7.29.5"),subQ0,sQuery(id+"F0.wireOp",EDGE,"E7.30.1"),sQuery(id+"F0.wireOp",EDGE,"E7.30.2"),sQuery(id+"F0.wireOp",EDGE,"E7.30.3"),sQuery(id+"F0.wireOp",EDGE,"E7.30.4"),sQuery(id+"F0.wireOp",EDGE,"E7.30.5"),sQuery(id+"F0.wireOp",EDGE,"E7.31.0"),sQuery(id+"F0.wireOp",EDGE,"E7.31.1"),sQuery(id+"F0.wireOp",EDGE,"E7.31.2"),sQuery(id+"F0.wireOp",EDGE,"E7.31.3"),sQuery(id+"F0.wireOp",EDGE,"E7.31.4"),sQuery(id+"F0.wireOp",EDGE,"E7.31.5"),sQuery(id+"F0.wireOp",EDGE,"E7.32.0"),sQuery(id+"F0.wireOp",EDGE,"E7.32.1"),sQuery(id+"F0.wireOp",EDGE,"E7.32.2"),sQuery(id+"F0.wireOp",EDGE,"E7.32.3"),sQuery(id+"F0.wireOp",EDGE,"E7.32.4"),sQuery(id+"F0.wireOp",EDGE,"E7.32.5"),sQuery(id+"F0.wireOp",EDGE,"E7.33.0"),sQuery(id+"F0.wireOp",EDGE,"E7.33.1"),sQuery(id+"F0.wireOp",EDGE,"E7.33.2"),sQuery(id+"F0.wireOp",EDGE,"E7.33.3"),sQuery(id+"F0.wireOp",EDGE,"E7.33.4"),sQuery(id+"F0.wireOp",EDGE,"E7.33.5"),sQuery(id+"F0.wireOp",EDGE,"E7.34.0"),sQuery(id+"F0.wireOp",EDGE,"E7.34.1"),sQuery(id+"F0.wireOp",EDGE,"E7.34.2"),sQuery(id+"F0.wireOp",EDGE,"E7.34.3"),sQuery(id+"F0.wireOp",EDGE,"E7.34.4"),sQuery(id+"F0.wireOp",EDGE,"E7.34.5"),sQuery(id+"F0.wireOp",EDGE,"E7.35.0"),sQuery(id+"F0.wireOp",EDGE,"E7.35.1"),sQuery(id+"F0.wireOp",EDGE,"E7.35.2"),sQuery(id+"F0.wireOp",EDGE,"E7.35.3"),sQuery(id+"F0.wireOp",EDGE,"E7.35.4"),sQuery(id+"F0.wireOp",EDGE,"E7.35.5"),sQuery(id+"F0.wireOp",EDGE,"E7.36.0"),sQuery(id+"F0.wireOp",EDGE,"E7.36.1"),sQuery(id+"F0.wireOp",EDGE,"E7.36.2"),sQuery(id+"F0.wireOp",EDGE,"E7.36.3"),sQuery(id+"F0.wireOp",EDGE,"E7.36.4"),sQuery(id+"F0.wireOp",EDGE,"E7.36.5"),sQuery(id+"F0.wireOp",EDGE,"E7.37.0"),sQuery(id+"F0.wireOp",EDGE,"E7.37.1"),sQuery(id+"F0.wireOp",EDGE,"E7.37.2"),sQuery(id+"F0.wireOp",EDGE,"E7.37.3"),sQuery(id+"F0.wireOp",EDGE,"E7.37.4"),sQuery(id+"F0.wireOp",EDGE,"E7.37.5"),sQuery(id+"F0.wireOp",EDGE,"E7.38.0"),sQuery(id+"F0.wireOp",EDGE,"E7.38.1"),sQuery(id+"F0.wireOp",EDGE,"E7.38.2"),sQuery(id+"F0.wireOp",EDGE,"E7.38.3"),sQuery(id+"F0.wireOp",EDGE,"E7.38.4"),sQuery(id+"F0.wireOp",EDGE,"E7.38.5"),sQuery(id+"F0.wireOp",EDGE,"E7.39.0"),sQuery(id+"F0.wireOp",EDGE,"E7.39.1"),sQuery(id+"F0.wireOp",EDGE,"E7.39.2"),sQuery(id+"F0.wireOp",EDGE,"E7.39.3"),sQuery(id+"F0.wireOp",EDGE,"E7.39.4"),sQuery(id+"F0.wireOp",EDGE,"E7.39.5"),sQuery(id+"F0.wireOp",EDGE,"E7.40.0"),sQuery(id+"F0.wireOp",EDGE,"E7.40.1"),sQuery(id+"F0.wireOp",EDGE,"E7.40.2"),sQuery(id+"F0.wireOp",EDGE,"E7.40.3"),sQuery(id+"F0.wireOp",EDGE,"E7.40.4"),sQuery(id+"F0.wireOp",EDGE,"E7.40.5"),sQuery(id+"F0.wireOp",EDGE,"E7.41.0"),sQuery(id+"F0.wireOp",EDGE,"E7.41.1"),sQuery(id+"F0.wireOp",EDGE,"E7.41.2"),sQuery(id+"F0.wireOp",EDGE,"E7.41.3"),sQuery(id+"F0.wireOp",EDGE,"E7.41.4"),sQuery(id+"F0.wireOp",EDGE,"E7.41.5"),sQuery(id+"F0.wireOp",EDGE,"E7.42.0"),sQuery(id+"F0.wireOp",EDGE,"E7.42.1"),sQuery(id+"F0.wireOp",EDGE,"E7.42.2"),sQuery(id+"F0.wireOp",EDGE,"E7.42.3"),sQuery(id+"F0.wireOp",EDGE,"E7.42.4"),sQuery(id+"F0.wireOp",EDGE,"E7.42.5"),sQuery(id+"F0.wireOp",EDGE,"E7.43.0"),sQuery(id+"F0.wireOp",EDGE,"E7.43.1"),sQuery(id+"F0.wireOp",EDGE,"E7.43.2"),sQuery(id+"F0.wireOp",EDGE,"E7.43.3"),sQuery(id+"F0.wireOp",EDGE,"E7.43.4"),sQuery(id+"F0.wireOp",EDGE,"E7.43.5")])],"isStart":true})],"blendedInto":[makeQuery(id+"F1.opExtrude","CAP_FACE",FACE,{"disambiguationData":[OSD([sQuery(id+"F0.wireOp",EDGE,"E1"),sQuery(id+"F0.wireOp",EDGE,"E2"),sQuery(id+"F0.wireOp",EDGE,"E3"),sQuery(id+"F0.wireOp",EDGE,"E4"),sQuery(id+"F0.wireOp",EDGE,"E5"),sQuery(id+"F0.wireOp",EDGE,"E6"),sQuery(id+"F0.wireOp",EDGE,"E7.1.0"),sQuery(id+"F0.wireOp",EDGE,"E7.1.1"),sQuery(id+"F0.wireOp",EDGE,"E7.1.2"),sQuery(id+"F0.wireOp",EDGE,"E7.1.3"),sQuery(id+"F0.wireOp",EDGE,"E7.1.4"),sQuery(id+"F0.wireOp",EDGE,"E7.1.5"),sQuery(id+"F0.wireOp",EDGE,"E7.2.0"),sQuery(id+"F0.wireOp",EDGE,"E7.2.1"),sQuery(id+"F0.wireOp",EDGE,"E7.2.2"),sQuery(id+"F0.wireOp",EDGE,"E7.2.3"),sQuery(id+"F0.wireOp",EDGE,"E7.2.4"),sQuery(id+"F0.wireOp",EDGE,"E7.2.5"),sQuery(id+"F0.wireOp",EDGE,"E7.3.0"),sQuery(id+"F0.wireOp",EDGE,"E7.3.1"),sQuery(id+"F0.wireOp",EDGE,"E7.3.2"),sQuery(id+"F0.wireOp",EDGE,"E7.3.3"),sQuery(id+"F0.wireOp",EDGE,"E7.3.4"),sQuery(id+"F0.wireOp",EDGE,"E7.3.5"),sQuery(id+"F0.wireOp",EDGE,"E7.4.0"),sQuery(id+"F0.wireOp",EDGE,"E7.4.1"),sQuery(id+"F0.wireOp",EDGE,"E7.4.2"),sQuery(id+"F0.wireOp",EDGE,"E7.4.3"),sQuery(id+"F0.wireOp",EDGE,"E7.4.4"),sQuery(id+"F0.wireOp",EDGE,"E7.4.5"),sQuery(id+"F0.wireOp",EDGE,"E7.5.0"),sQuery(id+"F0.wireOp",EDGE,"E7.5.1"),sQuery(id+"F0.wireOp",EDGE,"E7.5.2"),sQuery(id+"F0.wireOp",EDGE,"E7.5.3"),sQuery(id+"F0.wireOp",EDGE,"E7.5.4"),sQuery(id+"F0.wireOp",EDGE,"E7.5.5"),sQuery(id+"F0.wireOp",EDGE,"E7.6.0"),sQuery(id+"F0.wireOp",EDGE,"E7.6.1"),sQuery(id+"F0.wireOp",EDGE,"E7.6.2"),sQuery(id+"F0.wireOp",EDGE,"E7.6.3"),sQuery(id+"F0.wireOp",EDGE,"E7.6.4"),sQuery(id+"F0.wireOp",EDGE,"E7.6.5"),sQuery(id+"F0.wireOp",EDGE,"E7.7.0"),sQuery(id+"F0.wireOp",EDGE,"E7.7.1"),sQuery(id+"F0.wireOp",EDGE,"E7.7.2"),sQuery(id+"F0.wireOp",EDGE,"E7.7.3"),sQuery(id+"F0.wireOp",EDGE,"E7.7.4"),sQuery(id+"F0.wireOp",EDGE,"E7.7.5"),sQuery(id+"F0.wireOp",EDGE,"E7.8.0"),sQuery(id+"F0.wireOp",EDGE,"E7.8.1"),sQuery(id+"F0.wireOp",EDGE,"E7.8.2"),sQuery(id+"F0.wireOp",EDGE,"E7.8.3"),sQuery(id+"F0.wireOp",EDGE,"E7.8.4"),sQuery(id+"F0.wireOp",EDGE,"E7.8.5"),sQuery(id+"F0.wireOp",EDGE,"E7.9.0"),sQuery(id+"F0.wireOp",EDGE,"E7.9.1"),sQuery(id+"F0.wireOp",EDGE,"E7.9.2"),sQuery(id+"F0.wireOp",EDGE,"E7.9.3"),sQuery(id+"F0.wireOp",EDGE,"E7.9.4"),sQuery(id+"F0.wireOp",EDGE,"E7.9.5"),sQuery(id+"F0.wireOp",EDGE,"E7.10.0"),sQuery(id+"F0.wireOp",EDGE,"E7.10.1"),sQuery(id+"F0.wireOp",EDGE,"E7.10.2"),sQuery(id+"F0.wireOp",EDGE,"E7.10.3"),sQuery(id+"F0.wireOp",EDGE,"E7.10.4"),sQuery(id+"F0.wireOp",EDGE,"E7.10.5"),sQuery(id+"F0.wireOp",EDGE,"E7.11.0"),sQuery(id+"F0.wireOp",EDGE,"E7.11.1"),sQuery(id+"F0.wireOp",EDGE,"E7.11.2"),sQuery(id+"F0.wireOp",EDGE,"E7.11.3"),sQuery(id+"F0.wireOp",EDGE,"E7.11.4"),sQuery(id+"F0.wireOp",EDGE,"E7.11.5"),sQuery(id+"F0.wireOp",EDGE,"E7.12.0"),sQuery(id+"F0.wireOp",EDGE,"E7.12.1"),sQuery(id+"F0.wireOp",EDGE,"E7.12.2"),sQuery(id+"F0.wireOp",EDGE,"E7.12.3"),sQuery(id+"F0.wireOp",EDGE,"E7.12.4"),sQuery(id+"F0.wireOp",EDGE,"E7.12.5"),sQuery(id+"F0.wireOp",EDGE,"E7.13.0"),sQuery(id+"F0.wireOp",EDGE,"E7.13.1"),sQuery(id+"F0.wireOp",EDGE,"E7.13.2"),sQuery(id+"F0.wireOp",EDGE,"E7.13.3"),sQuery(id+"F0.wireOp",EDGE,"E7.13.4"),sQuery(id+"F0.wireOp",EDGE,"E7.13.5"),sQuery(id+"F0.wireOp",EDGE,"E7.14.0"),sQuery(id+"F0.wireOp",EDGE,"E7.14.1"),sQuery(id+"F0.wireOp",EDGE,"E7.14.2"),sQuery(id+"F0.wireOp",EDGE,"E7.14.3"),sQuery(id+"F0.wireOp",EDGE,"E7.14.4"),sQuery(id+"F0.wireOp",EDGE,"E7.14.5"),sQuery(id+"F0.wireOp",EDGE,"E7.15.0"),sQuery(id+"F0.wireOp",EDGE,"E7.15.1"),sQuery(id+"F0.wireOp",EDGE,"E7.15.2"),sQuery(id+"F0.wireOp",EDGE,"E7.15.3"),sQuery(id+"F0.wireOp",EDGE,"E7.15.4"),sQuery(id+"F0.wireOp",EDGE,"E7.15.5"),sQuery(id+"F0.wireOp",EDGE,"E7.16.0"),sQuery(id+"F0.wireOp",EDGE,"E7.16.1"),sQuery(id+"F0.wireOp",EDGE,"E7.16.2"),sQuery(id+"F0.wireOp",EDGE,"E7.16.3"),sQuery(id+"F0.wireOp",EDGE,"E7.16.4"),sQuery(id+"F0.wireOp",EDGE,"E7.16.5"),sQuery(id+"F0.wireOp",EDGE,"E7.17.0"),sQuery(id+"F0.wireOp",EDGE,"E7.17.1"),sQuery(id+"F0.wireOp",EDGE,"E7.17.2"),sQuery(id+"F0.wireOp",EDGE,"E7.17.3"),sQuery(id+"F0.wireOp",EDGE,"E7.17.4"),sQuery(id+"F0.wireOp",EDGE,"E7.17.5"),sQuery(id+"F0.wireOp",EDGE,"E7.18.0"),sQuery(id+"F0.wireOp",EDGE,"E7.18.1"),sQuery(id+"F0.wireOp",EDGE,"E7.18.2"),sQuery(id+"F0.wireOp",EDGE,"E7.18.3"),sQuery(id+"F0.wireOp",EDGE,"E7.18.4"),sQuery(id+"F0.wireOp",EDGE,"E7.18.5"),sQuery(id+"F0.wireOp",EDGE,"E7.19.0"),sQuery(id+"F0.wireOp",EDGE,"E7.19.1"),sQuery(id+"F0.wireOp",EDGE,"E7.19.2"),sQuery(id+"F0.wireOp",EDGE,"E7.19.3"),sQuery(id+"F0.wireOp",EDGE,"E7.19.4"),sQuery(id+"F0.wireOp",EDGE,"E7.19.5"),sQuery(id+"F0.wireOp",EDGE,"E7.20.0"),sQuery(id+"F0.wireOp",EDGE,"E7.20.1"),sQuery(id+"F0.wireOp",EDGE,"E7.20.2"),sQuery(id+"F0.wireOp",EDGE,"E7.20.3"),sQuery(id+"F0.wireOp",EDGE,"E7.20.4"),sQuery(id+"F0.wireOp",EDGE,"E7.20.5"),sQuery(id+"F0.wireOp",EDGE,"E7.21.0"),sQuery(id+"F0.wireOp",EDGE,"E7.21.1"),sQuery(id+"F0.wireOp",EDGE,"E7.21.2"),sQuery(id+"F0.wireOp",EDGE,"E7.21.3"),sQuery(id+"F0.wireOp",EDGE,"E7.21.4"),sQuery(id+"F0.wireOp",EDGE,"E7.21.5"),sQuery(id+"F0.wireOp",EDGE,"E7.22.0"),sQuery(id+"F0.wireOp",EDGE,"E7.22.1"),sQuery(id+"F0.wireOp",EDGE,"E7.22.2"),sQuery(id+"F0.wireOp",EDGE,"E7.22.3"),sQuery(id+"F0.wireOp",EDGE,"E7.22.4"),sQuery(id+"F0.wireOp",EDGE,"E7.22.5"),sQuery(id+"F0.wireOp",EDGE,"E7.23.0"),sQuery(id+"F0.wireOp",EDGE,"E7.23.1"),sQuery(id+"F0.wireOp",EDGE,"E7.23.2"),sQuery(id+"F0.wireOp",EDGE,"E7.23.3"),sQuery(id+"F0.wireOp",EDGE,"E7.23.4"),sQuery(id+"F0.wireOp",EDGE,"E7.23.5"),sQuery(id+"F0.wireOp",EDGE,"E7.24.0"),sQuery(id+"F0.wireOp",EDGE,"E7.24.1"),sQuery(id+"F0.wireOp",EDGE,"E7.24.2"),sQuery(id+"F0.wireOp",EDGE,"E7.24.3"),sQuery(id+"F0.wireOp",EDGE,"E7.24.4"),sQuery(id+"F0.wireOp",EDGE,"E7.24.5"),sQuery(id+"F0.wireOp",EDGE,"E7.25.0"),sQuery(id+"F0.wireOp",EDGE,"E7.25.1"),sQuery(id+"F0.wireOp",EDGE,"E7.25.2"),sQuery(id+"F0.wireOp",EDGE,"E7.25.3"),sQuery(id+"F0.wireOp",EDGE,"E7.25.4"),sQuery(id+"F0.wireOp",EDGE,"E7.25.5"),sQuery(id+"F0.wireOp",EDGE,"E7.26.0"),sQuery(id+"F0.wireOp",EDGE,"E7.26.1"),sQuery(id+"F0.wireOp",EDGE,"E7.26.2"),sQuery(id+"F0.wireOp",EDGE,"E7.26.3"),sQuery(id+"F0.wireOp",EDGE,"E7.26.4"),sQuery(id+"F0.wireOp",EDGE,"E7.26.5"),sQuery(id+"F0.wireOp",EDGE,"E7.27.0"),sQuery(id+"F0.wireOp",EDGE,"E7.27.1"),sQuery(id+"F0.wireOp",EDGE,"E7.27.2"),sQuery(id+"F0.wireOp",EDGE,"E7.27.3"),sQuery(id+"F0.wireOp",EDGE,"E7.27.4"),sQuery(id+"F0.wireOp",EDGE,"E7.27.5"),sQuery(id+"F0.wireOp",EDGE,"E7.28.0"),sQuery(id+"F0.wireOp",EDGE,"E7.28.1"),sQuery(id+"F0.wireOp",EDGE,"E7.28.2"),sQuery(id+"F0.wireOp",EDGE,"E7.28.3"),sQuery(id+"F0.wireOp",EDGE,"E7.28.4"),sQuery(id+"F0.wireOp",EDGE,"E7.28.5"),sQuery(id+"F0.wireOp",EDGE,"E7.29.0"),sQuery(id+"F0.wireOp",EDGE,"E7.29.1"),sQuery(id+"F0.wireOp",EDGE,"E7.29.2"),sQuery(id+"F0.wireOp",EDGE,"E7.29.3"),sQuery(id+"F0.wireOp",EDGE,"E7.29.4"),sQuery(id+"F0.wireOp",EDGE,"E7.29.5"),subQ0,sQuery(id+"F0.wireOp",EDGE,"E7.30.1"),sQuery(id+"F0.wireOp",EDGE,"E7.30.2"),sQuery(id+"F0.wireOp",EDGE,"E7.30.3"),sQuery(id+"F0.wireOp",EDGE,"E7.30.4"),sQuery(id+"F0.wireOp",EDGE,"E7.30.5"),sQuery(id+"F0.wireOp",EDGE,"E7.31.0"),sQuery(id+"F0.wireOp",EDGE,"E7.31.1"),sQuery(id+"F0.wireOp",EDGE,"E7.31.2"),sQuery(id+"F0.wireOp",EDGE,"E7.31.3"),sQuery(id+"F0.wireOp",EDGE,"E7.31.4"),sQuery(id+"F0.wireOp",EDGE,"E7.31.5"),sQuery(id+"F0.wireOp",EDGE,"E7.32.0"),sQuery(id+"F0.wireOp",EDGE,"E7.32.1"),sQuery(id+"F0.wireOp",EDGE,"E7.32.2"),sQuery(id+"F0.wireOp",EDGE,"E7.32.3"),sQuery(id+"F0.wireOp",EDGE,"E7.32.4"),sQuery(id+"F0.wireOp",EDGE,"E7.32.5"),sQuery(id+"F0.wireOp",EDGE,"E7.33.0"),sQuery(id+"F0.wireOp",EDGE,"E7.33.1"),sQuery(id+"F0.wireOp",EDGE,"E7.33.2"),sQuery(id+"F0.wireOp",EDGE,"E7.33.3"),sQuery(id+"F0.wireOp",EDGE,"E7.33.4"),sQuery(id+"F0.wireOp",EDGE,"E7.33.5"),sQuery(id+"F0.wireOp",EDGE,"E7.34.0"),sQuery(id+"F0.wireOp",EDGE,"E7.34.1"),sQuery(id+"F0.wireOp",EDGE,"E7.34.2"),sQuery(id+"F0.wireOp",EDGE,"E7.34.3"),sQuery(id+"F0.wireOp",EDGE,"E7.34.4"),sQuery(id+"F0.wireOp",EDGE,"E7.34.5"),sQuery(id+"F0.wireOp",EDGE,"E7.35.0"),sQuery(id+"F0.wireOp",EDGE,"E7.35.1"),sQuery(id+"F0.wireOp",EDGE,"E7.35.2"),sQuery(id+"F0.wireOp",EDGE,"E7.35.3"),sQuery(id+"F0.wireOp",EDGE,"E7.35.4"),sQuery(id+"F0.wireOp",EDGE,"E7.35.5"),sQuery(id+"F0.wireOp",EDGE,"E7.36.0"),sQuery(id+"F0.wireOp",EDGE,"E7.36.1"),sQuery(id+"F0.wireOp",EDGE,"E7.36.2"),sQuery(id+"F0.wireOp",EDGE,"E7.36.3"),sQuery(id+"F0.wireOp",EDGE,"E7.36.4"),sQuery(id+"F0.wireOp",EDGE,"E7.36.5"),sQuery(id+"F0.wireOp",EDGE,"E7.37.0"),sQuery(id+"F0.wireOp",EDGE,"E7.37.1"),sQuery(id+"F0.wireOp",EDGE,"E7.37.2"),sQuery(id+"F0.wireOp",EDGE,"E7.37.3"),sQuery(id+"F0.wireOp",EDGE,"E7.37.4"),sQuery(id+"F0.wireOp",EDGE,"E7.37.5"),sQuery(id+"F0.wireOp",EDGE,"E7.38.0"),sQuery(id+"F0.wireOp",EDGE,"E7.38.1"),sQuery(id+"F0.wireOp",EDGE,"E7.38.2"),sQuery(id+"F0.wireOp",EDGE,"E7.38.3"),sQuery(id+"F0.wireOp",EDGE,"E7.38.4"),sQuery(id+"F0.wireOp",EDGE,"E7.38.5"),sQuery(id+"F0.wireOp",EDGE,"E7.39.0"),sQuery(id+"F0.wireOp",EDGE,"E7.39.1"),sQuery(id+"F0.wireOp",EDGE,"E7.39.2"),sQuery(id+"F0.wireOp",EDGE,"E7.39.3"),sQuery(id+"F0.wireOp",EDGE,"E7.39.4"),sQuery(id+"F0.wireOp",EDGE,"E7.39.5"),sQuery(id+"F0.wireOp",EDGE,"E7.40.0"),sQuery(id+"F0.wireOp",EDGE,"E7.40.1"),sQuery(id+"F0.wireOp",EDGE,"E7.40.2"),sQuery(id+"F0.wireOp",EDGE,"E7.40.3"),sQuery(id+"F0.wireOp",EDGE,"E7.40.4"),sQuery(id+"F0.wireOp",EDGE,"E7.40.5"),sQuery(id+"F0.wireOp",EDGE,"E7.41.0"),sQuery(id+"F0.wireOp",EDGE,"E7.41.1"),sQuery(id+"F0.wireOp",EDGE,"E7.41.2"),sQuery(id+"F0.wireOp",EDGE,"E7.41.3"),sQuery(id+"F0.wireOp",EDGE,"E7.41.4"),sQuery(id+"F0.wireOp",EDGE,"E7.41.5"),sQuery(id+"F0.wireOp",EDGE,"E7.42.0"),sQuery(id+"F0.wireOp",EDGE,"E7.42.1"),sQuery(id+"F0.wireOp",EDGE,"E7.42.2"),sQuery(id+"F0.wireOp",EDGE,"E7.42.3"),sQuery(id+"F0.wireOp",EDGE,"E7.42.4"),sQuery(id+"F0.wireOp",EDGE,"E7.42.5"),sQuery(id+"F0.wireOp",EDGE,"E7.43.0"),sQuery(id+"F0.wireOp",EDGE,"E7.43.1"),sQuery(id+"F0.wireOp",EDGE,"E7.43.2"),sQuery(id+"F0.wireOp",EDGE,"E7.43.3"),sQuery(id+"F0.wireOp",EDGE,"E7.43.4"),sQuery(id+"F0.wireOp",EDGE,"E7.43.5")])],"isStart":true})]});}
            var Q37;
            {var subQ0=sQuery(id+"F0.wireOp",EDGE,"E7.32.0");Q37=makeQuery(id+"F2.opChamfer","BLEND_EDGE",EDGE,{"blendedFrom":[makeQuery(id+"F1.opExtrude","CAP_EDGE",EDGE,{"disambiguationData":[OSD([subQ0])],"isStart":true}),makeQuery(id+"F1.opExtrude","CAP_FACE",FACE,{"disambiguationData":[OSD([sQuery(id+"F0.wireOp",EDGE,"E1"),sQuery(id+"F0.wireOp",EDGE,"E2"),sQuery(id+"F0.wireOp",EDGE,"E3"),sQuery(id+"F0.wireOp",EDGE,"E4"),sQuery(id+"F0.wireOp",EDGE,"E5"),sQuery(id+"F0.wireOp",EDGE,"E6"),sQuery(id+"F0.wireOp",EDGE,"E7.1.0"),sQuery(id+"F0.wireOp",EDGE,"E7.1.1"),sQuery(id+"F0.wireOp",EDGE,"E7.1.2"),sQuery(id+"F0.wireOp",EDGE,"E7.1.3"),sQuery(id+"F0.wireOp",EDGE,"E7.1.4"),sQuery(id+"F0.wireOp",EDGE,"E7.1.5"),sQuery(id+"F0.wireOp",EDGE,"E7.2.0"),sQuery(id+"F0.wireOp",EDGE,"E7.2.1"),sQuery(id+"F0.wireOp",EDGE,"E7.2.2"),sQuery(id+"F0.wireOp",EDGE,"E7.2.3"),sQuery(id+"F0.wireOp",EDGE,"E7.2.4"),sQuery(id+"F0.wireOp",EDGE,"E7.2.5"),sQuery(id+"F0.wireOp",EDGE,"E7.3.0"),sQuery(id+"F0.wireOp",EDGE,"E7.3.1"),sQuery(id+"F0.wireOp",EDGE,"E7.3.2"),sQuery(id+"F0.wireOp",EDGE,"E7.3.3"),sQuery(id+"F0.wireOp",EDGE,"E7.3.4"),sQuery(id+"F0.wireOp",EDGE,"E7.3.5"),sQuery(id+"F0.wireOp",EDGE,"E7.4.0"),sQuery(id+"F0.wireOp",EDGE,"E7.4.1"),sQuery(id+"F0.wireOp",EDGE,"E7.4.2"),sQuery(id+"F0.wireOp",EDGE,"E7.4.3"),sQuery(id+"F0.wireOp",EDGE,"E7.4.4"),sQuery(id+"F0.wireOp",EDGE,"E7.4.5"),sQuery(id+"F0.wireOp",EDGE,"E7.5.0"),sQuery(id+"F0.wireOp",EDGE,"E7.5.1"),sQuery(id+"F0.wireOp",EDGE,"E7.5.2"),sQuery(id+"F0.wireOp",EDGE,"E7.5.3"),sQuery(id+"F0.wireOp",EDGE,"E7.5.4"),sQuery(id+"F0.wireOp",EDGE,"E7.5.5"),sQuery(id+"F0.wireOp",EDGE,"E7.6.0"),sQuery(id+"F0.wireOp",EDGE,"E7.6.1"),sQuery(id+"F0.wireOp",EDGE,"E7.6.2"),sQuery(id+"F0.wireOp",EDGE,"E7.6.3"),sQuery(id+"F0.wireOp",EDGE,"E7.6.4"),sQuery(id+"F0.wireOp",EDGE,"E7.6.5"),sQuery(id+"F0.wireOp",EDGE,"E7.7.0"),sQuery(id+"F0.wireOp",EDGE,"E7.7.1"),sQuery(id+"F0.wireOp",EDGE,"E7.7.2"),sQuery(id+"F0.wireOp",EDGE,"E7.7.3"),sQuery(id+"F0.wireOp",EDGE,"E7.7.4"),sQuery(id+"F0.wireOp",EDGE,"E7.7.5"),sQuery(id+"F0.wireOp",EDGE,"E7.8.0"),sQuery(id+"F0.wireOp",EDGE,"E7.8.1"),sQuery(id+"F0.wireOp",EDGE,"E7.8.2"),sQuery(id+"F0.wireOp",EDGE,"E7.8.3"),sQuery(id+"F0.wireOp",EDGE,"E7.8.4"),sQuery(id+"F0.wireOp",EDGE,"E7.8.5"),sQuery(id+"F0.wireOp",EDGE,"E7.9.0"),sQuery(id+"F0.wireOp",EDGE,"E7.9.1"),sQuery(id+"F0.wireOp",EDGE,"E7.9.2"),sQuery(id+"F0.wireOp",EDGE,"E7.9.3"),sQuery(id+"F0.wireOp",EDGE,"E7.9.4"),sQuery(id+"F0.wireOp",EDGE,"E7.9.5"),sQuery(id+"F0.wireOp",EDGE,"E7.10.0"),sQuery(id+"F0.wireOp",EDGE,"E7.10.1"),sQuery(id+"F0.wireOp",EDGE,"E7.10.2"),sQuery(id+"F0.wireOp",EDGE,"E7.10.3"),sQuery(id+"F0.wireOp",EDGE,"E7.10.4"),sQuery(id+"F0.wireOp",EDGE,"E7.10.5"),sQuery(id+"F0.wireOp",EDGE,"E7.11.0"),sQuery(id+"F0.wireOp",EDGE,"E7.11.1"),sQuery(id+"F0.wireOp",EDGE,"E7.11.2"),sQuery(id+"F0.wireOp",EDGE,"E7.11.3"),sQuery(id+"F0.wireOp",EDGE,"E7.11.4"),sQuery(id+"F0.wireOp",EDGE,"E7.11.5"),sQuery(id+"F0.wireOp",EDGE,"E7.12.0"),sQuery(id+"F0.wireOp",EDGE,"E7.12.1"),sQuery(id+"F0.wireOp",EDGE,"E7.12.2"),sQuery(id+"F0.wireOp",EDGE,"E7.12.3"),sQuery(id+"F0.wireOp",EDGE,"E7.12.4"),sQuery(id+"F0.wireOp",EDGE,"E7.12.5"),sQuery(id+"F0.wireOp",EDGE,"E7.13.0"),sQuery(id+"F0.wireOp",EDGE,"E7.13.1"),sQuery(id+"F0.wireOp",EDGE,"E7.13.2"),sQuery(id+"F0.wireOp",EDGE,"E7.13.3"),sQuery(id+"F0.wireOp",EDGE,"E7.13.4"),sQuery(id+"F0.wireOp",EDGE,"E7.13.5"),sQuery(id+"F0.wireOp",EDGE,"E7.14.0"),sQuery(id+"F0.wireOp",EDGE,"E7.14.1"),sQuery(id+"F0.wireOp",EDGE,"E7.14.2"),sQuery(id+"F0.wireOp",EDGE,"E7.14.3"),sQuery(id+"F0.wireOp",EDGE,"E7.14.4"),sQuery(id+"F0.wireOp",EDGE,"E7.14.5"),sQuery(id+"F0.wireOp",EDGE,"E7.15.0"),sQuery(id+"F0.wireOp",EDGE,"E7.15.1"),sQuery(id+"F0.wireOp",EDGE,"E7.15.2"),sQuery(id+"F0.wireOp",EDGE,"E7.15.3"),sQuery(id+"F0.wireOp",EDGE,"E7.15.4"),sQuery(id+"F0.wireOp",EDGE,"E7.15.5"),sQuery(id+"F0.wireOp",EDGE,"E7.16.0"),sQuery(id+"F0.wireOp",EDGE,"E7.16.1"),sQuery(id+"F0.wireOp",EDGE,"E7.16.2"),sQuery(id+"F0.wireOp",EDGE,"E7.16.3"),sQuery(id+"F0.wireOp",EDGE,"E7.16.4"),sQuery(id+"F0.wireOp",EDGE,"E7.16.5"),sQuery(id+"F0.wireOp",EDGE,"E7.17.0"),sQuery(id+"F0.wireOp",EDGE,"E7.17.1"),sQuery(id+"F0.wireOp",EDGE,"E7.17.2"),sQuery(id+"F0.wireOp",EDGE,"E7.17.3"),sQuery(id+"F0.wireOp",EDGE,"E7.17.4"),sQuery(id+"F0.wireOp",EDGE,"E7.17.5"),sQuery(id+"F0.wireOp",EDGE,"E7.18.0"),sQuery(id+"F0.wireOp",EDGE,"E7.18.1"),sQuery(id+"F0.wireOp",EDGE,"E7.18.2"),sQuery(id+"F0.wireOp",EDGE,"E7.18.3"),sQuery(id+"F0.wireOp",EDGE,"E7.18.4"),sQuery(id+"F0.wireOp",EDGE,"E7.18.5"),sQuery(id+"F0.wireOp",EDGE,"E7.19.0"),sQuery(id+"F0.wireOp",EDGE,"E7.19.1"),sQuery(id+"F0.wireOp",EDGE,"E7.19.2"),sQuery(id+"F0.wireOp",EDGE,"E7.19.3"),sQuery(id+"F0.wireOp",EDGE,"E7.19.4"),sQuery(id+"F0.wireOp",EDGE,"E7.19.5"),sQuery(id+"F0.wireOp",EDGE,"E7.20.0"),sQuery(id+"F0.wireOp",EDGE,"E7.20.1"),sQuery(id+"F0.wireOp",EDGE,"E7.20.2"),sQuery(id+"F0.wireOp",EDGE,"E7.20.3"),sQuery(id+"F0.wireOp",EDGE,"E7.20.4"),sQuery(id+"F0.wireOp",EDGE,"E7.20.5"),sQuery(id+"F0.wireOp",EDGE,"E7.21.0"),sQuery(id+"F0.wireOp",EDGE,"E7.21.1"),sQuery(id+"F0.wireOp",EDGE,"E7.21.2"),sQuery(id+"F0.wireOp",EDGE,"E7.21.3"),sQuery(id+"F0.wireOp",EDGE,"E7.21.4"),sQuery(id+"F0.wireOp",EDGE,"E7.21.5"),sQuery(id+"F0.wireOp",EDGE,"E7.22.0"),sQuery(id+"F0.wireOp",EDGE,"E7.22.1"),sQuery(id+"F0.wireOp",EDGE,"E7.22.2"),sQuery(id+"F0.wireOp",EDGE,"E7.22.3"),sQuery(id+"F0.wireOp",EDGE,"E7.22.4"),sQuery(id+"F0.wireOp",EDGE,"E7.22.5"),sQuery(id+"F0.wireOp",EDGE,"E7.23.0"),sQuery(id+"F0.wireOp",EDGE,"E7.23.1"),sQuery(id+"F0.wireOp",EDGE,"E7.23.2"),sQuery(id+"F0.wireOp",EDGE,"E7.23.3"),sQuery(id+"F0.wireOp",EDGE,"E7.23.4"),sQuery(id+"F0.wireOp",EDGE,"E7.23.5"),sQuery(id+"F0.wireOp",EDGE,"E7.24.0"),sQuery(id+"F0.wireOp",EDGE,"E7.24.1"),sQuery(id+"F0.wireOp",EDGE,"E7.24.2"),sQuery(id+"F0.wireOp",EDGE,"E7.24.3"),sQuery(id+"F0.wireOp",EDGE,"E7.24.4"),sQuery(id+"F0.wireOp",EDGE,"E7.24.5"),sQuery(id+"F0.wireOp",EDGE,"E7.25.0"),sQuery(id+"F0.wireOp",EDGE,"E7.25.1"),sQuery(id+"F0.wireOp",EDGE,"E7.25.2"),sQuery(id+"F0.wireOp",EDGE,"E7.25.3"),sQuery(id+"F0.wireOp",EDGE,"E7.25.4"),sQuery(id+"F0.wireOp",EDGE,"E7.25.5"),sQuery(id+"F0.wireOp",EDGE,"E7.26.0"),sQuery(id+"F0.wireOp",EDGE,"E7.26.1"),sQuery(id+"F0.wireOp",EDGE,"E7.26.2"),sQuery(id+"F0.wireOp",EDGE,"E7.26.3"),sQuery(id+"F0.wireOp",EDGE,"E7.26.4"),sQuery(id+"F0.wireOp",EDGE,"E7.26.5"),sQuery(id+"F0.wireOp",EDGE,"E7.27.0"),sQuery(id+"F0.wireOp",EDGE,"E7.27.1"),sQuery(id+"F0.wireOp",EDGE,"E7.27.2"),sQuery(id+"F0.wireOp",EDGE,"E7.27.3"),sQuery(id+"F0.wireOp",EDGE,"E7.27.4"),sQuery(id+"F0.wireOp",EDGE,"E7.27.5"),sQuery(id+"F0.wireOp",EDGE,"E7.28.0"),sQuery(id+"F0.wireOp",EDGE,"E7.28.1"),sQuery(id+"F0.wireOp",EDGE,"E7.28.2"),sQuery(id+"F0.wireOp",EDGE,"E7.28.3"),sQuery(id+"F0.wireOp",EDGE,"E7.28.4"),sQuery(id+"F0.wireOp",EDGE,"E7.28.5"),sQuery(id+"F0.wireOp",EDGE,"E7.29.0"),sQuery(id+"F0.wireOp",EDGE,"E7.29.1"),sQuery(id+"F0.wireOp",EDGE,"E7.29.2"),sQuery(id+"F0.wireOp",EDGE,"E7.29.3"),sQuery(id+"F0.wireOp",EDGE,"E7.29.4"),sQuery(id+"F0.wireOp",EDGE,"E7.29.5"),sQuery(id+"F0.wireOp",EDGE,"E7.30.0"),sQuery(id+"F0.wireOp",EDGE,"E7.30.1"),sQuery(id+"F0.wireOp",EDGE,"E7.30.2"),sQuery(id+"F0.wireOp",EDGE,"E7.30.3"),sQuery(id+"F0.wireOp",EDGE,"E7.30.4"),sQuery(id+"F0.wireOp",EDGE,"E7.30.5"),sQuery(id+"F0.wireOp",EDGE,"E7.31.0"),sQuery(id+"F0.wireOp",EDGE,"E7.31.1"),sQuery(id+"F0.wireOp",EDGE,"E7.31.2"),sQuery(id+"F0.wireOp",EDGE,"E7.31.3"),sQuery(id+"F0.wireOp",EDGE,"E7.31.4"),sQuery(id+"F0.wireOp",EDGE,"E7.31.5"),subQ0,sQuery(id+"F0.wireOp",EDGE,"E7.32.1"),sQuery(id+"F0.wireOp",EDGE,"E7.32.2"),sQuery(id+"F0.wireOp",EDGE,"E7.32.3"),sQuery(id+"F0.wireOp",EDGE,"E7.32.4"),sQuery(id+"F0.wireOp",EDGE,"E7.32.5"),sQuery(id+"F0.wireOp",EDGE,"E7.33.0"),sQuery(id+"F0.wireOp",EDGE,"E7.33.1"),sQuery(id+"F0.wireOp",EDGE,"E7.33.2"),sQuery(id+"F0.wireOp",EDGE,"E7.33.3"),sQuery(id+"F0.wireOp",EDGE,"E7.33.4"),sQuery(id+"F0.wireOp",EDGE,"E7.33.5"),sQuery(id+"F0.wireOp",EDGE,"E7.34.0"),sQuery(id+"F0.wireOp",EDGE,"E7.34.1"),sQuery(id+"F0.wireOp",EDGE,"E7.34.2"),sQuery(id+"F0.wireOp",EDGE,"E7.34.3"),sQuery(id+"F0.wireOp",EDGE,"E7.34.4"),sQuery(id+"F0.wireOp",EDGE,"E7.34.5"),sQuery(id+"F0.wireOp",EDGE,"E7.35.0"),sQuery(id+"F0.wireOp",EDGE,"E7.35.1"),sQuery(id+"F0.wireOp",EDGE,"E7.35.2"),sQuery(id+"F0.wireOp",EDGE,"E7.35.3"),sQuery(id+"F0.wireOp",EDGE,"E7.35.4"),sQuery(id+"F0.wireOp",EDGE,"E7.35.5"),sQuery(id+"F0.wireOp",EDGE,"E7.36.0"),sQuery(id+"F0.wireOp",EDGE,"E7.36.1"),sQuery(id+"F0.wireOp",EDGE,"E7.36.2"),sQuery(id+"F0.wireOp",EDGE,"E7.36.3"),sQuery(id+"F0.wireOp",EDGE,"E7.36.4"),sQuery(id+"F0.wireOp",EDGE,"E7.36.5"),sQuery(id+"F0.wireOp",EDGE,"E7.37.0"),sQuery(id+"F0.wireOp",EDGE,"E7.37.1"),sQuery(id+"F0.wireOp",EDGE,"E7.37.2"),sQuery(id+"F0.wireOp",EDGE,"E7.37.3"),sQuery(id+"F0.wireOp",EDGE,"E7.37.4"),sQuery(id+"F0.wireOp",EDGE,"E7.37.5"),sQuery(id+"F0.wireOp",EDGE,"E7.38.0"),sQuery(id+"F0.wireOp",EDGE,"E7.38.1"),sQuery(id+"F0.wireOp",EDGE,"E7.38.2"),sQuery(id+"F0.wireOp",EDGE,"E7.38.3"),sQuery(id+"F0.wireOp",EDGE,"E7.38.4"),sQuery(id+"F0.wireOp",EDGE,"E7.38.5"),sQuery(id+"F0.wireOp",EDGE,"E7.39.0"),sQuery(id+"F0.wireOp",EDGE,"E7.39.1"),sQuery(id+"F0.wireOp",EDGE,"E7.39.2"),sQuery(id+"F0.wireOp",EDGE,"E7.39.3"),sQuery(id+"F0.wireOp",EDGE,"E7.39.4"),sQuery(id+"F0.wireOp",EDGE,"E7.39.5"),sQuery(id+"F0.wireOp",EDGE,"E7.40.0"),sQuery(id+"F0.wireOp",EDGE,"E7.40.1"),sQuery(id+"F0.wireOp",EDGE,"E7.40.2"),sQuery(id+"F0.wireOp",EDGE,"E7.40.3"),sQuery(id+"F0.wireOp",EDGE,"E7.40.4"),sQuery(id+"F0.wireOp",EDGE,"E7.40.5"),sQuery(id+"F0.wireOp",EDGE,"E7.41.0"),sQuery(id+"F0.wireOp",EDGE,"E7.41.1"),sQuery(id+"F0.wireOp",EDGE,"E7.41.2"),sQuery(id+"F0.wireOp",EDGE,"E7.41.3"),sQuery(id+"F0.wireOp",EDGE,"E7.41.4"),sQuery(id+"F0.wireOp",EDGE,"E7.41.5"),sQuery(id+"F0.wireOp",EDGE,"E7.42.0"),sQuery(id+"F0.wireOp",EDGE,"E7.42.1"),sQuery(id+"F0.wireOp",EDGE,"E7.42.2"),sQuery(id+"F0.wireOp",EDGE,"E7.42.3"),sQuery(id+"F0.wireOp",EDGE,"E7.42.4"),sQuery(id+"F0.wireOp",EDGE,"E7.42.5"),sQuery(id+"F0.wireOp",EDGE,"E7.43.0"),sQuery(id+"F0.wireOp",EDGE,"E7.43.1"),sQuery(id+"F0.wireOp",EDGE,"E7.43.2"),sQuery(id+"F0.wireOp",EDGE,"E7.43.3"),sQuery(id+"F0.wireOp",EDGE,"E7.43.4"),sQuery(id+"F0.wireOp",EDGE,"E7.43.5")])],"isStart":true})],"blendedInto":[makeQuery(id+"F1.opExtrude","CAP_FACE",FACE,{"disambiguationData":[OSD([sQuery(id+"F0.wireOp",EDGE,"E1"),sQuery(id+"F0.wireOp",EDGE,"E2"),sQuery(id+"F0.wireOp",EDGE,"E3"),sQuery(id+"F0.wireOp",EDGE,"E4"),sQuery(id+"F0.wireOp",EDGE,"E5"),sQuery(id+"F0.wireOp",EDGE,"E6"),sQuery(id+"F0.wireOp",EDGE,"E7.1.0"),sQuery(id+"F0.wireOp",EDGE,"E7.1.1"),sQuery(id+"F0.wireOp",EDGE,"E7.1.2"),sQuery(id+"F0.wireOp",EDGE,"E7.1.3"),sQuery(id+"F0.wireOp",EDGE,"E7.1.4"),sQuery(id+"F0.wireOp",EDGE,"E7.1.5"),sQuery(id+"F0.wireOp",EDGE,"E7.2.0"),sQuery(id+"F0.wireOp",EDGE,"E7.2.1"),sQuery(id+"F0.wireOp",EDGE,"E7.2.2"),sQuery(id+"F0.wireOp",EDGE,"E7.2.3"),sQuery(id+"F0.wireOp",EDGE,"E7.2.4"),sQuery(id+"F0.wireOp",EDGE,"E7.2.5"),sQuery(id+"F0.wireOp",EDGE,"E7.3.0"),sQuery(id+"F0.wireOp",EDGE,"E7.3.1"),sQuery(id+"F0.wireOp",EDGE,"E7.3.2"),sQuery(id+"F0.wireOp",EDGE,"E7.3.3"),sQuery(id+"F0.wireOp",EDGE,"E7.3.4"),sQuery(id+"F0.wireOp",EDGE,"E7.3.5"),sQuery(id+"F0.wireOp",EDGE,"E7.4.0"),sQuery(id+"F0.wireOp",EDGE,"E7.4.1"),sQuery(id+"F0.wireOp",EDGE,"E7.4.2"),sQuery(id+"F0.wireOp",EDGE,"E7.4.3"),sQuery(id+"F0.wireOp",EDGE,"E7.4.4"),sQuery(id+"F0.wireOp",EDGE,"E7.4.5"),sQuery(id+"F0.wireOp",EDGE,"E7.5.0"),sQuery(id+"F0.wireOp",EDGE,"E7.5.1"),sQuery(id+"F0.wireOp",EDGE,"E7.5.2"),sQuery(id+"F0.wireOp",EDGE,"E7.5.3"),sQuery(id+"F0.wireOp",EDGE,"E7.5.4"),sQuery(id+"F0.wireOp",EDGE,"E7.5.5"),sQuery(id+"F0.wireOp",EDGE,"E7.6.0"),sQuery(id+"F0.wireOp",EDGE,"E7.6.1"),sQuery(id+"F0.wireOp",EDGE,"E7.6.2"),sQuery(id+"F0.wireOp",EDGE,"E7.6.3"),sQuery(id+"F0.wireOp",EDGE,"E7.6.4"),sQuery(id+"F0.wireOp",EDGE,"E7.6.5"),sQuery(id+"F0.wireOp",EDGE,"E7.7.0"),sQuery(id+"F0.wireOp",EDGE,"E7.7.1"),sQuery(id+"F0.wireOp",EDGE,"E7.7.2"),sQuery(id+"F0.wireOp",EDGE,"E7.7.3"),sQuery(id+"F0.wireOp",EDGE,"E7.7.4"),sQuery(id+"F0.wireOp",EDGE,"E7.7.5"),sQuery(id+"F0.wireOp",EDGE,"E7.8.0"),sQuery(id+"F0.wireOp",EDGE,"E7.8.1"),sQuery(id+"F0.wireOp",EDGE,"E7.8.2"),sQuery(id+"F0.wireOp",EDGE,"E7.8.3"),sQuery(id+"F0.wireOp",EDGE,"E7.8.4"),sQuery(id+"F0.wireOp",EDGE,"E7.8.5"),sQuery(id+"F0.wireOp",EDGE,"E7.9.0"),sQuery(id+"F0.wireOp",EDGE,"E7.9.1"),sQuery(id+"F0.wireOp",EDGE,"E7.9.2"),sQuery(id+"F0.wireOp",EDGE,"E7.9.3"),sQuery(id+"F0.wireOp",EDGE,"E7.9.4"),sQuery(id+"F0.wireOp",EDGE,"E7.9.5"),sQuery(id+"F0.wireOp",EDGE,"E7.10.0"),sQuery(id+"F0.wireOp",EDGE,"E7.10.1"),sQuery(id+"F0.wireOp",EDGE,"E7.10.2"),sQuery(id+"F0.wireOp",EDGE,"E7.10.3"),sQuery(id+"F0.wireOp",EDGE,"E7.10.4"),sQuery(id+"F0.wireOp",EDGE,"E7.10.5"),sQuery(id+"F0.wireOp",EDGE,"E7.11.0"),sQuery(id+"F0.wireOp",EDGE,"E7.11.1"),sQuery(id+"F0.wireOp",EDGE,"E7.11.2"),sQuery(id+"F0.wireOp",EDGE,"E7.11.3"),sQuery(id+"F0.wireOp",EDGE,"E7.11.4"),sQuery(id+"F0.wireOp",EDGE,"E7.11.5"),sQuery(id+"F0.wireOp",EDGE,"E7.12.0"),sQuery(id+"F0.wireOp",EDGE,"E7.12.1"),sQuery(id+"F0.wireOp",EDGE,"E7.12.2"),sQuery(id+"F0.wireOp",EDGE,"E7.12.3"),sQuery(id+"F0.wireOp",EDGE,"E7.12.4"),sQuery(id+"F0.wireOp",EDGE,"E7.12.5"),sQuery(id+"F0.wireOp",EDGE,"E7.13.0"),sQuery(id+"F0.wireOp",EDGE,"E7.13.1"),sQuery(id+"F0.wireOp",EDGE,"E7.13.2"),sQuery(id+"F0.wireOp",EDGE,"E7.13.3"),sQuery(id+"F0.wireOp",EDGE,"E7.13.4"),sQuery(id+"F0.wireOp",EDGE,"E7.13.5"),sQuery(id+"F0.wireOp",EDGE,"E7.14.0"),sQuery(id+"F0.wireOp",EDGE,"E7.14.1"),sQuery(id+"F0.wireOp",EDGE,"E7.14.2"),sQuery(id+"F0.wireOp",EDGE,"E7.14.3"),sQuery(id+"F0.wireOp",EDGE,"E7.14.4"),sQuery(id+"F0.wireOp",EDGE,"E7.14.5"),sQuery(id+"F0.wireOp",EDGE,"E7.15.0"),sQuery(id+"F0.wireOp",EDGE,"E7.15.1"),sQuery(id+"F0.wireOp",EDGE,"E7.15.2"),sQuery(id+"F0.wireOp",EDGE,"E7.15.3"),sQuery(id+"F0.wireOp",EDGE,"E7.15.4"),sQuery(id+"F0.wireOp",EDGE,"E7.15.5"),sQuery(id+"F0.wireOp",EDGE,"E7.16.0"),sQuery(id+"F0.wireOp",EDGE,"E7.16.1"),sQuery(id+"F0.wireOp",EDGE,"E7.16.2"),sQuery(id+"F0.wireOp",EDGE,"E7.16.3"),sQuery(id+"F0.wireOp",EDGE,"E7.16.4"),sQuery(id+"F0.wireOp",EDGE,"E7.16.5"),sQuery(id+"F0.wireOp",EDGE,"E7.17.0"),sQuery(id+"F0.wireOp",EDGE,"E7.17.1"),sQuery(id+"F0.wireOp",EDGE,"E7.17.2"),sQuery(id+"F0.wireOp",EDGE,"E7.17.3"),sQuery(id+"F0.wireOp",EDGE,"E7.17.4"),sQuery(id+"F0.wireOp",EDGE,"E7.17.5"),sQuery(id+"F0.wireOp",EDGE,"E7.18.0"),sQuery(id+"F0.wireOp",EDGE,"E7.18.1"),sQuery(id+"F0.wireOp",EDGE,"E7.18.2"),sQuery(id+"F0.wireOp",EDGE,"E7.18.3"),sQuery(id+"F0.wireOp",EDGE,"E7.18.4"),sQuery(id+"F0.wireOp",EDGE,"E7.18.5"),sQuery(id+"F0.wireOp",EDGE,"E7.19.0"),sQuery(id+"F0.wireOp",EDGE,"E7.19.1"),sQuery(id+"F0.wireOp",EDGE,"E7.19.2"),sQuery(id+"F0.wireOp",EDGE,"E7.19.3"),sQuery(id+"F0.wireOp",EDGE,"E7.19.4"),sQuery(id+"F0.wireOp",EDGE,"E7.19.5"),sQuery(id+"F0.wireOp",EDGE,"E7.20.0"),sQuery(id+"F0.wireOp",EDGE,"E7.20.1"),sQuery(id+"F0.wireOp",EDGE,"E7.20.2"),sQuery(id+"F0.wireOp",EDGE,"E7.20.3"),sQuery(id+"F0.wireOp",EDGE,"E7.20.4"),sQuery(id+"F0.wireOp",EDGE,"E7.20.5"),sQuery(id+"F0.wireOp",EDGE,"E7.21.0"),sQuery(id+"F0.wireOp",EDGE,"E7.21.1"),sQuery(id+"F0.wireOp",EDGE,"E7.21.2"),sQuery(id+"F0.wireOp",EDGE,"E7.21.3"),sQuery(id+"F0.wireOp",EDGE,"E7.21.4"),sQuery(id+"F0.wireOp",EDGE,"E7.21.5"),sQuery(id+"F0.wireOp",EDGE,"E7.22.0"),sQuery(id+"F0.wireOp",EDGE,"E7.22.1"),sQuery(id+"F0.wireOp",EDGE,"E7.22.2"),sQuery(id+"F0.wireOp",EDGE,"E7.22.3"),sQuery(id+"F0.wireOp",EDGE,"E7.22.4"),sQuery(id+"F0.wireOp",EDGE,"E7.22.5"),sQuery(id+"F0.wireOp",EDGE,"E7.23.0"),sQuery(id+"F0.wireOp",EDGE,"E7.23.1"),sQuery(id+"F0.wireOp",EDGE,"E7.23.2"),sQuery(id+"F0.wireOp",EDGE,"E7.23.3"),sQuery(id+"F0.wireOp",EDGE,"E7.23.4"),sQuery(id+"F0.wireOp",EDGE,"E7.23.5"),sQuery(id+"F0.wireOp",EDGE,"E7.24.0"),sQuery(id+"F0.wireOp",EDGE,"E7.24.1"),sQuery(id+"F0.wireOp",EDGE,"E7.24.2"),sQuery(id+"F0.wireOp",EDGE,"E7.24.3"),sQuery(id+"F0.wireOp",EDGE,"E7.24.4"),sQuery(id+"F0.wireOp",EDGE,"E7.24.5"),sQuery(id+"F0.wireOp",EDGE,"E7.25.0"),sQuery(id+"F0.wireOp",EDGE,"E7.25.1"),sQuery(id+"F0.wireOp",EDGE,"E7.25.2"),sQuery(id+"F0.wireOp",EDGE,"E7.25.3"),sQuery(id+"F0.wireOp",EDGE,"E7.25.4"),sQuery(id+"F0.wireOp",EDGE,"E7.25.5"),sQuery(id+"F0.wireOp",EDGE,"E7.26.0"),sQuery(id+"F0.wireOp",EDGE,"E7.26.1"),sQuery(id+"F0.wireOp",EDGE,"E7.26.2"),sQuery(id+"F0.wireOp",EDGE,"E7.26.3"),sQuery(id+"F0.wireOp",EDGE,"E7.26.4"),sQuery(id+"F0.wireOp",EDGE,"E7.26.5"),sQuery(id+"F0.wireOp",EDGE,"E7.27.0"),sQuery(id+"F0.wireOp",EDGE,"E7.27.1"),sQuery(id+"F0.wireOp",EDGE,"E7.27.2"),sQuery(id+"F0.wireOp",EDGE,"E7.27.3"),sQuery(id+"F0.wireOp",EDGE,"E7.27.4"),sQuery(id+"F0.wireOp",EDGE,"E7.27.5"),sQuery(id+"F0.wireOp",EDGE,"E7.28.0"),sQuery(id+"F0.wireOp",EDGE,"E7.28.1"),sQuery(id+"F0.wireOp",EDGE,"E7.28.2"),sQuery(id+"F0.wireOp",EDGE,"E7.28.3"),sQuery(id+"F0.wireOp",EDGE,"E7.28.4"),sQuery(id+"F0.wireOp",EDGE,"E7.28.5"),sQuery(id+"F0.wireOp",EDGE,"E7.29.0"),sQuery(id+"F0.wireOp",EDGE,"E7.29.1"),sQuery(id+"F0.wireOp",EDGE,"E7.29.2"),sQuery(id+"F0.wireOp",EDGE,"E7.29.3"),sQuery(id+"F0.wireOp",EDGE,"E7.29.4"),sQuery(id+"F0.wireOp",EDGE,"E7.29.5"),sQuery(id+"F0.wireOp",EDGE,"E7.30.0"),sQuery(id+"F0.wireOp",EDGE,"E7.30.1"),sQuery(id+"F0.wireOp",EDGE,"E7.30.2"),sQuery(id+"F0.wireOp",EDGE,"E7.30.3"),sQuery(id+"F0.wireOp",EDGE,"E7.30.4"),sQuery(id+"F0.wireOp",EDGE,"E7.30.5"),sQuery(id+"F0.wireOp",EDGE,"E7.31.0"),sQuery(id+"F0.wireOp",EDGE,"E7.31.1"),sQuery(id+"F0.wireOp",EDGE,"E7.31.2"),sQuery(id+"F0.wireOp",EDGE,"E7.31.3"),sQuery(id+"F0.wireOp",EDGE,"E7.31.4"),sQuery(id+"F0.wireOp",EDGE,"E7.31.5"),subQ0,sQuery(id+"F0.wireOp",EDGE,"E7.32.1"),sQuery(id+"F0.wireOp",EDGE,"E7.32.2"),sQuery(id+"F0.wireOp",EDGE,"E7.32.3"),sQuery(id+"F0.wireOp",EDGE,"E7.32.4"),sQuery(id+"F0.wireOp",EDGE,"E7.32.5"),sQuery(id+"F0.wireOp",EDGE,"E7.33.0"),sQuery(id+"F0.wireOp",EDGE,"E7.33.1"),sQuery(id+"F0.wireOp",EDGE,"E7.33.2"),sQuery(id+"F0.wireOp",EDGE,"E7.33.3"),sQuery(id+"F0.wireOp",EDGE,"E7.33.4"),sQuery(id+"F0.wireOp",EDGE,"E7.33.5"),sQuery(id+"F0.wireOp",EDGE,"E7.34.0"),sQuery(id+"F0.wireOp",EDGE,"E7.34.1"),sQuery(id+"F0.wireOp",EDGE,"E7.34.2"),sQuery(id+"F0.wireOp",EDGE,"E7.34.3"),sQuery(id+"F0.wireOp",EDGE,"E7.34.4"),sQuery(id+"F0.wireOp",EDGE,"E7.34.5"),sQuery(id+"F0.wireOp",EDGE,"E7.35.0"),sQuery(id+"F0.wireOp",EDGE,"E7.35.1"),sQuery(id+"F0.wireOp",EDGE,"E7.35.2"),sQuery(id+"F0.wireOp",EDGE,"E7.35.3"),sQuery(id+"F0.wireOp",EDGE,"E7.35.4"),sQuery(id+"F0.wireOp",EDGE,"E7.35.5"),sQuery(id+"F0.wireOp",EDGE,"E7.36.0"),sQuery(id+"F0.wireOp",EDGE,"E7.36.1"),sQuery(id+"F0.wireOp",EDGE,"E7.36.2"),sQuery(id+"F0.wireOp",EDGE,"E7.36.3"),sQuery(id+"F0.wireOp",EDGE,"E7.36.4"),sQuery(id+"F0.wireOp",EDGE,"E7.36.5"),sQuery(id+"F0.wireOp",EDGE,"E7.37.0"),sQuery(id+"F0.wireOp",EDGE,"E7.37.1"),sQuery(id+"F0.wireOp",EDGE,"E7.37.2"),sQuery(id+"F0.wireOp",EDGE,"E7.37.3"),sQuery(id+"F0.wireOp",EDGE,"E7.37.4"),sQuery(id+"F0.wireOp",EDGE,"E7.37.5"),sQuery(id+"F0.wireOp",EDGE,"E7.38.0"),sQuery(id+"F0.wireOp",EDGE,"E7.38.1"),sQuery(id+"F0.wireOp",EDGE,"E7.38.2"),sQuery(id+"F0.wireOp",EDGE,"E7.38.3"),sQuery(id+"F0.wireOp",EDGE,"E7.38.4"),sQuery(id+"F0.wireOp",EDGE,"E7.38.5"),sQuery(id+"F0.wireOp",EDGE,"E7.39.0"),sQuery(id+"F0.wireOp",EDGE,"E7.39.1"),sQuery(id+"F0.wireOp",EDGE,"E7.39.2"),sQuery(id+"F0.wireOp",EDGE,"E7.39.3"),sQuery(id+"F0.wireOp",EDGE,"E7.39.4"),sQuery(id+"F0.wireOp",EDGE,"E7.39.5"),sQuery(id+"F0.wireOp",EDGE,"E7.40.0"),sQuery(id+"F0.wireOp",EDGE,"E7.40.1"),sQuery(id+"F0.wireOp",EDGE,"E7.40.2"),sQuery(id+"F0.wireOp",EDGE,"E7.40.3"),sQuery(id+"F0.wireOp",EDGE,"E7.40.4"),sQuery(id+"F0.wireOp",EDGE,"E7.40.5"),sQuery(id+"F0.wireOp",EDGE,"E7.41.0"),sQuery(id+"F0.wireOp",EDGE,"E7.41.1"),sQuery(id+"F0.wireOp",EDGE,"E7.41.2"),sQuery(id+"F0.wireOp",EDGE,"E7.41.3"),sQuery(id+"F0.wireOp",EDGE,"E7.41.4"),sQuery(id+"F0.wireOp",EDGE,"E7.41.5"),sQuery(id+"F0.wireOp",EDGE,"E7.42.0"),sQuery(id+"F0.wireOp",EDGE,"E7.42.1"),sQuery(id+"F0.wireOp",EDGE,"E7.42.2"),sQuery(id+"F0.wireOp",EDGE,"E7.42.3"),sQuery(id+"F0.wireOp",EDGE,"E7.42.4"),sQuery(id+"F0.wireOp",EDGE,"E7.42.5"),sQuery(id+"F0.wireOp",EDGE,"E7.43.0"),sQuery(id+"F0.wireOp",EDGE,"E7.43.1"),sQuery(id+"F0.wireOp",EDGE,"E7.43.2"),sQuery(id+"F0.wireOp",EDGE,"E7.43.3"),sQuery(id+"F0.wireOp",EDGE,"E7.43.4"),sQuery(id+"F0.wireOp",EDGE,"E7.43.5")])],"isStart":true})]});}
            var Q38;
            {var subQ0=sQuery(id+"F0.wireOp",EDGE,"E7.34.0");Q38=makeQuery(id+"F2.opChamfer","BLEND_EDGE",EDGE,{"blendedFrom":[makeQuery(id+"F1.opExtrude","CAP_EDGE",EDGE,{"disambiguationData":[OSD([subQ0])],"isStart":true}),makeQuery(id+"F1.opExtrude","CAP_FACE",FACE,{"disambiguationData":[OSD([sQuery(id+"F0.wireOp",EDGE,"E1"),sQuery(id+"F0.wireOp",EDGE,"E2"),sQuery(id+"F0.wireOp",EDGE,"E3"),sQuery(id+"F0.wireOp",EDGE,"E4"),sQuery(id+"F0.wireOp",EDGE,"E5"),sQuery(id+"F0.wireOp",EDGE,"E6"),sQuery(id+"F0.wireOp",EDGE,"E7.1.0"),sQuery(id+"F0.wireOp",EDGE,"E7.1.1"),sQuery(id+"F0.wireOp",EDGE,"E7.1.2"),sQuery(id+"F0.wireOp",EDGE,"E7.1.3"),sQuery(id+"F0.wireOp",EDGE,"E7.1.4"),sQuery(id+"F0.wireOp",EDGE,"E7.1.5"),sQuery(id+"F0.wireOp",EDGE,"E7.2.0"),sQuery(id+"F0.wireOp",EDGE,"E7.2.1"),sQuery(id+"F0.wireOp",EDGE,"E7.2.2"),sQuery(id+"F0.wireOp",EDGE,"E7.2.3"),sQuery(id+"F0.wireOp",EDGE,"E7.2.4"),sQuery(id+"F0.wireOp",EDGE,"E7.2.5"),sQuery(id+"F0.wireOp",EDGE,"E7.3.0"),sQuery(id+"F0.wireOp",EDGE,"E7.3.1"),sQuery(id+"F0.wireOp",EDGE,"E7.3.2"),sQuery(id+"F0.wireOp",EDGE,"E7.3.3"),sQuery(id+"F0.wireOp",EDGE,"E7.3.4"),sQuery(id+"F0.wireOp",EDGE,"E7.3.5"),sQuery(id+"F0.wireOp",EDGE,"E7.4.0"),sQuery(id+"F0.wireOp",EDGE,"E7.4.1"),sQuery(id+"F0.wireOp",EDGE,"E7.4.2"),sQuery(id+"F0.wireOp",EDGE,"E7.4.3"),sQuery(id+"F0.wireOp",EDGE,"E7.4.4"),sQuery(id+"F0.wireOp",EDGE,"E7.4.5"),sQuery(id+"F0.wireOp",EDGE,"E7.5.0"),sQuery(id+"F0.wireOp",EDGE,"E7.5.1"),sQuery(id+"F0.wireOp",EDGE,"E7.5.2"),sQuery(id+"F0.wireOp",EDGE,"E7.5.3"),sQuery(id+"F0.wireOp",EDGE,"E7.5.4"),sQuery(id+"F0.wireOp",EDGE,"E7.5.5"),sQuery(id+"F0.wireOp",EDGE,"E7.6.0"),sQuery(id+"F0.wireOp",EDGE,"E7.6.1"),sQuery(id+"F0.wireOp",EDGE,"E7.6.2"),sQuery(id+"F0.wireOp",EDGE,"E7.6.3"),sQuery(id+"F0.wireOp",EDGE,"E7.6.4"),sQuery(id+"F0.wireOp",EDGE,"E7.6.5"),sQuery(id+"F0.wireOp",EDGE,"E7.7.0"),sQuery(id+"F0.wireOp",EDGE,"E7.7.1"),sQuery(id+"F0.wireOp",EDGE,"E7.7.2"),sQuery(id+"F0.wireOp",EDGE,"E7.7.3"),sQuery(id+"F0.wireOp",EDGE,"E7.7.4"),sQuery(id+"F0.wireOp",EDGE,"E7.7.5"),sQuery(id+"F0.wireOp",EDGE,"E7.8.0"),sQuery(id+"F0.wireOp",EDGE,"E7.8.1"),sQuery(id+"F0.wireOp",EDGE,"E7.8.2"),sQuery(id+"F0.wireOp",EDGE,"E7.8.3"),sQuery(id+"F0.wireOp",EDGE,"E7.8.4"),sQuery(id+"F0.wireOp",EDGE,"E7.8.5"),sQuery(id+"F0.wireOp",EDGE,"E7.9.0"),sQuery(id+"F0.wireOp",EDGE,"E7.9.1"),sQuery(id+"F0.wireOp",EDGE,"E7.9.2"),sQuery(id+"F0.wireOp",EDGE,"E7.9.3"),sQuery(id+"F0.wireOp",EDGE,"E7.9.4"),sQuery(id+"F0.wireOp",EDGE,"E7.9.5"),sQuery(id+"F0.wireOp",EDGE,"E7.10.0"),sQuery(id+"F0.wireOp",EDGE,"E7.10.1"),sQuery(id+"F0.wireOp",EDGE,"E7.10.2"),sQuery(id+"F0.wireOp",EDGE,"E7.10.3"),sQuery(id+"F0.wireOp",EDGE,"E7.10.4"),sQuery(id+"F0.wireOp",EDGE,"E7.10.5"),sQuery(id+"F0.wireOp",EDGE,"E7.11.0"),sQuery(id+"F0.wireOp",EDGE,"E7.11.1"),sQuery(id+"F0.wireOp",EDGE,"E7.11.2"),sQuery(id+"F0.wireOp",EDGE,"E7.11.3"),sQuery(id+"F0.wireOp",EDGE,"E7.11.4"),sQuery(id+"F0.wireOp",EDGE,"E7.11.5"),sQuery(id+"F0.wireOp",EDGE,"E7.12.0"),sQuery(id+"F0.wireOp",EDGE,"E7.12.1"),sQuery(id+"F0.wireOp",EDGE,"E7.12.2"),sQuery(id+"F0.wireOp",EDGE,"E7.12.3"),sQuery(id+"F0.wireOp",EDGE,"E7.12.4"),sQuery(id+"F0.wireOp",EDGE,"E7.12.5"),sQuery(id+"F0.wireOp",EDGE,"E7.13.0"),sQuery(id+"F0.wireOp",EDGE,"E7.13.1"),sQuery(id+"F0.wireOp",EDGE,"E7.13.2"),sQuery(id+"F0.wireOp",EDGE,"E7.13.3"),sQuery(id+"F0.wireOp",EDGE,"E7.13.4"),sQuery(id+"F0.wireOp",EDGE,"E7.13.5"),sQuery(id+"F0.wireOp",EDGE,"E7.14.0"),sQuery(id+"F0.wireOp",EDGE,"E7.14.1"),sQuery(id+"F0.wireOp",EDGE,"E7.14.2"),sQuery(id+"F0.wireOp",EDGE,"E7.14.3"),sQuery(id+"F0.wireOp",EDGE,"E7.14.4"),sQuery(id+"F0.wireOp",EDGE,"E7.14.5"),sQuery(id+"F0.wireOp",EDGE,"E7.15.0"),sQuery(id+"F0.wireOp",EDGE,"E7.15.1"),sQuery(id+"F0.wireOp",EDGE,"E7.15.2"),sQuery(id+"F0.wireOp",EDGE,"E7.15.3"),sQuery(id+"F0.wireOp",EDGE,"E7.15.4"),sQuery(id+"F0.wireOp",EDGE,"E7.15.5"),sQuery(id+"F0.wireOp",EDGE,"E7.16.0"),sQuery(id+"F0.wireOp",EDGE,"E7.16.1"),sQuery(id+"F0.wireOp",EDGE,"E7.16.2"),sQuery(id+"F0.wireOp",EDGE,"E7.16.3"),sQuery(id+"F0.wireOp",EDGE,"E7.16.4"),sQuery(id+"F0.wireOp",EDGE,"E7.16.5"),sQuery(id+"F0.wireOp",EDGE,"E7.17.0"),sQuery(id+"F0.wireOp",EDGE,"E7.17.1"),sQuery(id+"F0.wireOp",EDGE,"E7.17.2"),sQuery(id+"F0.wireOp",EDGE,"E7.17.3"),sQuery(id+"F0.wireOp",EDGE,"E7.17.4"),sQuery(id+"F0.wireOp",EDGE,"E7.17.5"),sQuery(id+"F0.wireOp",EDGE,"E7.18.0"),sQuery(id+"F0.wireOp",EDGE,"E7.18.1"),sQuery(id+"F0.wireOp",EDGE,"E7.18.2"),sQuery(id+"F0.wireOp",EDGE,"E7.18.3"),sQuery(id+"F0.wireOp",EDGE,"E7.18.4"),sQuery(id+"F0.wireOp",EDGE,"E7.18.5"),sQuery(id+"F0.wireOp",EDGE,"E7.19.0"),sQuery(id+"F0.wireOp",EDGE,"E7.19.1"),sQuery(id+"F0.wireOp",EDGE,"E7.19.2"),sQuery(id+"F0.wireOp",EDGE,"E7.19.3"),sQuery(id+"F0.wireOp",EDGE,"E7.19.4"),sQuery(id+"F0.wireOp",EDGE,"E7.19.5"),sQuery(id+"F0.wireOp",EDGE,"E7.20.0"),sQuery(id+"F0.wireOp",EDGE,"E7.20.1"),sQuery(id+"F0.wireOp",EDGE,"E7.20.2"),sQuery(id+"F0.wireOp",EDGE,"E7.20.3"),sQuery(id+"F0.wireOp",EDGE,"E7.20.4"),sQuery(id+"F0.wireOp",EDGE,"E7.20.5"),sQuery(id+"F0.wireOp",EDGE,"E7.21.0"),sQuery(id+"F0.wireOp",EDGE,"E7.21.1"),sQuery(id+"F0.wireOp",EDGE,"E7.21.2"),sQuery(id+"F0.wireOp",EDGE,"E7.21.3"),sQuery(id+"F0.wireOp",EDGE,"E7.21.4"),sQuery(id+"F0.wireOp",EDGE,"E7.21.5"),sQuery(id+"F0.wireOp",EDGE,"E7.22.0"),sQuery(id+"F0.wireOp",EDGE,"E7.22.1"),sQuery(id+"F0.wireOp",EDGE,"E7.22.2"),sQuery(id+"F0.wireOp",EDGE,"E7.22.3"),sQuery(id+"F0.wireOp",EDGE,"E7.22.4"),sQuery(id+"F0.wireOp",EDGE,"E7.22.5"),sQuery(id+"F0.wireOp",EDGE,"E7.23.0"),sQuery(id+"F0.wireOp",EDGE,"E7.23.1"),sQuery(id+"F0.wireOp",EDGE,"E7.23.2"),sQuery(id+"F0.wireOp",EDGE,"E7.23.3"),sQuery(id+"F0.wireOp",EDGE,"E7.23.4"),sQuery(id+"F0.wireOp",EDGE,"E7.23.5"),sQuery(id+"F0.wireOp",EDGE,"E7.24.0"),sQuery(id+"F0.wireOp",EDGE,"E7.24.1"),sQuery(id+"F0.wireOp",EDGE,"E7.24.2"),sQuery(id+"F0.wireOp",EDGE,"E7.24.3"),sQuery(id+"F0.wireOp",EDGE,"E7.24.4"),sQuery(id+"F0.wireOp",EDGE,"E7.24.5"),sQuery(id+"F0.wireOp",EDGE,"E7.25.0"),sQuery(id+"F0.wireOp",EDGE,"E7.25.1"),sQuery(id+"F0.wireOp",EDGE,"E7.25.2"),sQuery(id+"F0.wireOp",EDGE,"E7.25.3"),sQuery(id+"F0.wireOp",EDGE,"E7.25.4"),sQuery(id+"F0.wireOp",EDGE,"E7.25.5"),sQuery(id+"F0.wireOp",EDGE,"E7.26.0"),sQuery(id+"F0.wireOp",EDGE,"E7.26.1"),sQuery(id+"F0.wireOp",EDGE,"E7.26.2"),sQuery(id+"F0.wireOp",EDGE,"E7.26.3"),sQuery(id+"F0.wireOp",EDGE,"E7.26.4"),sQuery(id+"F0.wireOp",EDGE,"E7.26.5"),sQuery(id+"F0.wireOp",EDGE,"E7.27.0"),sQuery(id+"F0.wireOp",EDGE,"E7.27.1"),sQuery(id+"F0.wireOp",EDGE,"E7.27.2"),sQuery(id+"F0.wireOp",EDGE,"E7.27.3"),sQuery(id+"F0.wireOp",EDGE,"E7.27.4"),sQuery(id+"F0.wireOp",EDGE,"E7.27.5"),sQuery(id+"F0.wireOp",EDGE,"E7.28.0"),sQuery(id+"F0.wireOp",EDGE,"E7.28.1"),sQuery(id+"F0.wireOp",EDGE,"E7.28.2"),sQuery(id+"F0.wireOp",EDGE,"E7.28.3"),sQuery(id+"F0.wireOp",EDGE,"E7.28.4"),sQuery(id+"F0.wireOp",EDGE,"E7.28.5"),sQuery(id+"F0.wireOp",EDGE,"E7.29.0"),sQuery(id+"F0.wireOp",EDGE,"E7.29.1"),sQuery(id+"F0.wireOp",EDGE,"E7.29.2"),sQuery(id+"F0.wireOp",EDGE,"E7.29.3"),sQuery(id+"F0.wireOp",EDGE,"E7.29.4"),sQuery(id+"F0.wireOp",EDGE,"E7.29.5"),sQuery(id+"F0.wireOp",EDGE,"E7.30.0"),sQuery(id+"F0.wireOp",EDGE,"E7.30.1"),sQuery(id+"F0.wireOp",EDGE,"E7.30.2"),sQuery(id+"F0.wireOp",EDGE,"E7.30.3"),sQuery(id+"F0.wireOp",EDGE,"E7.30.4"),sQuery(id+"F0.wireOp",EDGE,"E7.30.5"),sQuery(id+"F0.wireOp",EDGE,"E7.31.0"),sQuery(id+"F0.wireOp",EDGE,"E7.31.1"),sQuery(id+"F0.wireOp",EDGE,"E7.31.2"),sQuery(id+"F0.wireOp",EDGE,"E7.31.3"),sQuery(id+"F0.wireOp",EDGE,"E7.31.4"),sQuery(id+"F0.wireOp",EDGE,"E7.31.5"),sQuery(id+"F0.wireOp",EDGE,"E7.32.0"),sQuery(id+"F0.wireOp",EDGE,"E7.32.1"),sQuery(id+"F0.wireOp",EDGE,"E7.32.2"),sQuery(id+"F0.wireOp",EDGE,"E7.32.3"),sQuery(id+"F0.wireOp",EDGE,"E7.32.4"),sQuery(id+"F0.wireOp",EDGE,"E7.32.5"),sQuery(id+"F0.wireOp",EDGE,"E7.33.0"),sQuery(id+"F0.wireOp",EDGE,"E7.33.1"),sQuery(id+"F0.wireOp",EDGE,"E7.33.2"),sQuery(id+"F0.wireOp",EDGE,"E7.33.3"),sQuery(id+"F0.wireOp",EDGE,"E7.33.4"),sQuery(id+"F0.wireOp",EDGE,"E7.33.5"),subQ0,sQuery(id+"F0.wireOp",EDGE,"E7.34.1"),sQuery(id+"F0.wireOp",EDGE,"E7.34.2"),sQuery(id+"F0.wireOp",EDGE,"E7.34.3"),sQuery(id+"F0.wireOp",EDGE,"E7.34.4"),sQuery(id+"F0.wireOp",EDGE,"E7.34.5"),sQuery(id+"F0.wireOp",EDGE,"E7.35.0"),sQuery(id+"F0.wireOp",EDGE,"E7.35.1"),sQuery(id+"F0.wireOp",EDGE,"E7.35.2"),sQuery(id+"F0.wireOp",EDGE,"E7.35.3"),sQuery(id+"F0.wireOp",EDGE,"E7.35.4"),sQuery(id+"F0.wireOp",EDGE,"E7.35.5"),sQuery(id+"F0.wireOp",EDGE,"E7.36.0"),sQuery(id+"F0.wireOp",EDGE,"E7.36.1"),sQuery(id+"F0.wireOp",EDGE,"E7.36.2"),sQuery(id+"F0.wireOp",EDGE,"E7.36.3"),sQuery(id+"F0.wireOp",EDGE,"E7.36.4"),sQuery(id+"F0.wireOp",EDGE,"E7.36.5"),sQuery(id+"F0.wireOp",EDGE,"E7.37.0"),sQuery(id+"F0.wireOp",EDGE,"E7.37.1"),sQuery(id+"F0.wireOp",EDGE,"E7.37.2"),sQuery(id+"F0.wireOp",EDGE,"E7.37.3"),sQuery(id+"F0.wireOp",EDGE,"E7.37.4"),sQuery(id+"F0.wireOp",EDGE,"E7.37.5"),sQuery(id+"F0.wireOp",EDGE,"E7.38.0"),sQuery(id+"F0.wireOp",EDGE,"E7.38.1"),sQuery(id+"F0.wireOp",EDGE,"E7.38.2"),sQuery(id+"F0.wireOp",EDGE,"E7.38.3"),sQuery(id+"F0.wireOp",EDGE,"E7.38.4"),sQuery(id+"F0.wireOp",EDGE,"E7.38.5"),sQuery(id+"F0.wireOp",EDGE,"E7.39.0"),sQuery(id+"F0.wireOp",EDGE,"E7.39.1"),sQuery(id+"F0.wireOp",EDGE,"E7.39.2"),sQuery(id+"F0.wireOp",EDGE,"E7.39.3"),sQuery(id+"F0.wireOp",EDGE,"E7.39.4"),sQuery(id+"F0.wireOp",EDGE,"E7.39.5"),sQuery(id+"F0.wireOp",EDGE,"E7.40.0"),sQuery(id+"F0.wireOp",EDGE,"E7.40.1"),sQuery(id+"F0.wireOp",EDGE,"E7.40.2"),sQuery(id+"F0.wireOp",EDGE,"E7.40.3"),sQuery(id+"F0.wireOp",EDGE,"E7.40.4"),sQuery(id+"F0.wireOp",EDGE,"E7.40.5"),sQuery(id+"F0.wireOp",EDGE,"E7.41.0"),sQuery(id+"F0.wireOp",EDGE,"E7.41.1"),sQuery(id+"F0.wireOp",EDGE,"E7.41.2"),sQuery(id+"F0.wireOp",EDGE,"E7.41.3"),sQuery(id+"F0.wireOp",EDGE,"E7.41.4"),sQuery(id+"F0.wireOp",EDGE,"E7.41.5"),sQuery(id+"F0.wireOp",EDGE,"E7.42.0"),sQuery(id+"F0.wireOp",EDGE,"E7.42.1"),sQuery(id+"F0.wireOp",EDGE,"E7.42.2"),sQuery(id+"F0.wireOp",EDGE,"E7.42.3"),sQuery(id+"F0.wireOp",EDGE,"E7.42.4"),sQuery(id+"F0.wireOp",EDGE,"E7.42.5"),sQuery(id+"F0.wireOp",EDGE,"E7.43.0"),sQuery(id+"F0.wireOp",EDGE,"E7.43.1"),sQuery(id+"F0.wireOp",EDGE,"E7.43.2"),sQuery(id+"F0.wireOp",EDGE,"E7.43.3"),sQuery(id+"F0.wireOp",EDGE,"E7.43.4"),sQuery(id+"F0.wireOp",EDGE,"E7.43.5")])],"isStart":true})],"blendedInto":[makeQuery(id+"F1.opExtrude","CAP_FACE",FACE,{"disambiguationData":[OSD([sQuery(id+"F0.wireOp",EDGE,"E1"),sQuery(id+"F0.wireOp",EDGE,"E2"),sQuery(id+"F0.wireOp",EDGE,"E3"),sQuery(id+"F0.wireOp",EDGE,"E4"),sQuery(id+"F0.wireOp",EDGE,"E5"),sQuery(id+"F0.wireOp",EDGE,"E6"),sQuery(id+"F0.wireOp",EDGE,"E7.1.0"),sQuery(id+"F0.wireOp",EDGE,"E7.1.1"),sQuery(id+"F0.wireOp",EDGE,"E7.1.2"),sQuery(id+"F0.wireOp",EDGE,"E7.1.3"),sQuery(id+"F0.wireOp",EDGE,"E7.1.4"),sQuery(id+"F0.wireOp",EDGE,"E7.1.5"),sQuery(id+"F0.wireOp",EDGE,"E7.2.0"),sQuery(id+"F0.wireOp",EDGE,"E7.2.1"),sQuery(id+"F0.wireOp",EDGE,"E7.2.2"),sQuery(id+"F0.wireOp",EDGE,"E7.2.3"),sQuery(id+"F0.wireOp",EDGE,"E7.2.4"),sQuery(id+"F0.wireOp",EDGE,"E7.2.5"),sQuery(id+"F0.wireOp",EDGE,"E7.3.0"),sQuery(id+"F0.wireOp",EDGE,"E7.3.1"),sQuery(id+"F0.wireOp",EDGE,"E7.3.2"),sQuery(id+"F0.wireOp",EDGE,"E7.3.3"),sQuery(id+"F0.wireOp",EDGE,"E7.3.4"),sQuery(id+"F0.wireOp",EDGE,"E7.3.5"),sQuery(id+"F0.wireOp",EDGE,"E7.4.0"),sQuery(id+"F0.wireOp",EDGE,"E7.4.1"),sQuery(id+"F0.wireOp",EDGE,"E7.4.2"),sQuery(id+"F0.wireOp",EDGE,"E7.4.3"),sQuery(id+"F0.wireOp",EDGE,"E7.4.4"),sQuery(id+"F0.wireOp",EDGE,"E7.4.5"),sQuery(id+"F0.wireOp",EDGE,"E7.5.0"),sQuery(id+"F0.wireOp",EDGE,"E7.5.1"),sQuery(id+"F0.wireOp",EDGE,"E7.5.2"),sQuery(id+"F0.wireOp",EDGE,"E7.5.3"),sQuery(id+"F0.wireOp",EDGE,"E7.5.4"),sQuery(id+"F0.wireOp",EDGE,"E7.5.5"),sQuery(id+"F0.wireOp",EDGE,"E7.6.0"),sQuery(id+"F0.wireOp",EDGE,"E7.6.1"),sQuery(id+"F0.wireOp",EDGE,"E7.6.2"),sQuery(id+"F0.wireOp",EDGE,"E7.6.3"),sQuery(id+"F0.wireOp",EDGE,"E7.6.4"),sQuery(id+"F0.wireOp",EDGE,"E7.6.5"),sQuery(id+"F0.wireOp",EDGE,"E7.7.0"),sQuery(id+"F0.wireOp",EDGE,"E7.7.1"),sQuery(id+"F0.wireOp",EDGE,"E7.7.2"),sQuery(id+"F0.wireOp",EDGE,"E7.7.3"),sQuery(id+"F0.wireOp",EDGE,"E7.7.4"),sQuery(id+"F0.wireOp",EDGE,"E7.7.5"),sQuery(id+"F0.wireOp",EDGE,"E7.8.0"),sQuery(id+"F0.wireOp",EDGE,"E7.8.1"),sQuery(id+"F0.wireOp",EDGE,"E7.8.2"),sQuery(id+"F0.wireOp",EDGE,"E7.8.3"),sQuery(id+"F0.wireOp",EDGE,"E7.8.4"),sQuery(id+"F0.wireOp",EDGE,"E7.8.5"),sQuery(id+"F0.wireOp",EDGE,"E7.9.0"),sQuery(id+"F0.wireOp",EDGE,"E7.9.1"),sQuery(id+"F0.wireOp",EDGE,"E7.9.2"),sQuery(id+"F0.wireOp",EDGE,"E7.9.3"),sQuery(id+"F0.wireOp",EDGE,"E7.9.4"),sQuery(id+"F0.wireOp",EDGE,"E7.9.5"),sQuery(id+"F0.wireOp",EDGE,"E7.10.0"),sQuery(id+"F0.wireOp",EDGE,"E7.10.1"),sQuery(id+"F0.wireOp",EDGE,"E7.10.2"),sQuery(id+"F0.wireOp",EDGE,"E7.10.3"),sQuery(id+"F0.wireOp",EDGE,"E7.10.4"),sQuery(id+"F0.wireOp",EDGE,"E7.10.5"),sQuery(id+"F0.wireOp",EDGE,"E7.11.0"),sQuery(id+"F0.wireOp",EDGE,"E7.11.1"),sQuery(id+"F0.wireOp",EDGE,"E7.11.2"),sQuery(id+"F0.wireOp",EDGE,"E7.11.3"),sQuery(id+"F0.wireOp",EDGE,"E7.11.4"),sQuery(id+"F0.wireOp",EDGE,"E7.11.5"),sQuery(id+"F0.wireOp",EDGE,"E7.12.0"),sQuery(id+"F0.wireOp",EDGE,"E7.12.1"),sQuery(id+"F0.wireOp",EDGE,"E7.12.2"),sQuery(id+"F0.wireOp",EDGE,"E7.12.3"),sQuery(id+"F0.wireOp",EDGE,"E7.12.4"),sQuery(id+"F0.wireOp",EDGE,"E7.12.5"),sQuery(id+"F0.wireOp",EDGE,"E7.13.0"),sQuery(id+"F0.wireOp",EDGE,"E7.13.1"),sQuery(id+"F0.wireOp",EDGE,"E7.13.2"),sQuery(id+"F0.wireOp",EDGE,"E7.13.3"),sQuery(id+"F0.wireOp",EDGE,"E7.13.4"),sQuery(id+"F0.wireOp",EDGE,"E7.13.5"),sQuery(id+"F0.wireOp",EDGE,"E7.14.0"),sQuery(id+"F0.wireOp",EDGE,"E7.14.1"),sQuery(id+"F0.wireOp",EDGE,"E7.14.2"),sQuery(id+"F0.wireOp",EDGE,"E7.14.3"),sQuery(id+"F0.wireOp",EDGE,"E7.14.4"),sQuery(id+"F0.wireOp",EDGE,"E7.14.5"),sQuery(id+"F0.wireOp",EDGE,"E7.15.0"),sQuery(id+"F0.wireOp",EDGE,"E7.15.1"),sQuery(id+"F0.wireOp",EDGE,"E7.15.2"),sQuery(id+"F0.wireOp",EDGE,"E7.15.3"),sQuery(id+"F0.wireOp",EDGE,"E7.15.4"),sQuery(id+"F0.wireOp",EDGE,"E7.15.5"),sQuery(id+"F0.wireOp",EDGE,"E7.16.0"),sQuery(id+"F0.wireOp",EDGE,"E7.16.1"),sQuery(id+"F0.wireOp",EDGE,"E7.16.2"),sQuery(id+"F0.wireOp",EDGE,"E7.16.3"),sQuery(id+"F0.wireOp",EDGE,"E7.16.4"),sQuery(id+"F0.wireOp",EDGE,"E7.16.5"),sQuery(id+"F0.wireOp",EDGE,"E7.17.0"),sQuery(id+"F0.wireOp",EDGE,"E7.17.1"),sQuery(id+"F0.wireOp",EDGE,"E7.17.2"),sQuery(id+"F0.wireOp",EDGE,"E7.17.3"),sQuery(id+"F0.wireOp",EDGE,"E7.17.4"),sQuery(id+"F0.wireOp",EDGE,"E7.17.5"),sQuery(id+"F0.wireOp",EDGE,"E7.18.0"),sQuery(id+"F0.wireOp",EDGE,"E7.18.1"),sQuery(id+"F0.wireOp",EDGE,"E7.18.2"),sQuery(id+"F0.wireOp",EDGE,"E7.18.3"),sQuery(id+"F0.wireOp",EDGE,"E7.18.4"),sQuery(id+"F0.wireOp",EDGE,"E7.18.5"),sQuery(id+"F0.wireOp",EDGE,"E7.19.0"),sQuery(id+"F0.wireOp",EDGE,"E7.19.1"),sQuery(id+"F0.wireOp",EDGE,"E7.19.2"),sQuery(id+"F0.wireOp",EDGE,"E7.19.3"),sQuery(id+"F0.wireOp",EDGE,"E7.19.4"),sQuery(id+"F0.wireOp",EDGE,"E7.19.5"),sQuery(id+"F0.wireOp",EDGE,"E7.20.0"),sQuery(id+"F0.wireOp",EDGE,"E7.20.1"),sQuery(id+"F0.wireOp",EDGE,"E7.20.2"),sQuery(id+"F0.wireOp",EDGE,"E7.20.3"),sQuery(id+"F0.wireOp",EDGE,"E7.20.4"),sQuery(id+"F0.wireOp",EDGE,"E7.20.5"),sQuery(id+"F0.wireOp",EDGE,"E7.21.0"),sQuery(id+"F0.wireOp",EDGE,"E7.21.1"),sQuery(id+"F0.wireOp",EDGE,"E7.21.2"),sQuery(id+"F0.wireOp",EDGE,"E7.21.3"),sQuery(id+"F0.wireOp",EDGE,"E7.21.4"),sQuery(id+"F0.wireOp",EDGE,"E7.21.5"),sQuery(id+"F0.wireOp",EDGE,"E7.22.0"),sQuery(id+"F0.wireOp",EDGE,"E7.22.1"),sQuery(id+"F0.wireOp",EDGE,"E7.22.2"),sQuery(id+"F0.wireOp",EDGE,"E7.22.3"),sQuery(id+"F0.wireOp",EDGE,"E7.22.4"),sQuery(id+"F0.wireOp",EDGE,"E7.22.5"),sQuery(id+"F0.wireOp",EDGE,"E7.23.0"),sQuery(id+"F0.wireOp",EDGE,"E7.23.1"),sQuery(id+"F0.wireOp",EDGE,"E7.23.2"),sQuery(id+"F0.wireOp",EDGE,"E7.23.3"),sQuery(id+"F0.wireOp",EDGE,"E7.23.4"),sQuery(id+"F0.wireOp",EDGE,"E7.23.5"),sQuery(id+"F0.wireOp",EDGE,"E7.24.0"),sQuery(id+"F0.wireOp",EDGE,"E7.24.1"),sQuery(id+"F0.wireOp",EDGE,"E7.24.2"),sQuery(id+"F0.wireOp",EDGE,"E7.24.3"),sQuery(id+"F0.wireOp",EDGE,"E7.24.4"),sQuery(id+"F0.wireOp",EDGE,"E7.24.5"),sQuery(id+"F0.wireOp",EDGE,"E7.25.0"),sQuery(id+"F0.wireOp",EDGE,"E7.25.1"),sQuery(id+"F0.wireOp",EDGE,"E7.25.2"),sQuery(id+"F0.wireOp",EDGE,"E7.25.3"),sQuery(id+"F0.wireOp",EDGE,"E7.25.4"),sQuery(id+"F0.wireOp",EDGE,"E7.25.5"),sQuery(id+"F0.wireOp",EDGE,"E7.26.0"),sQuery(id+"F0.wireOp",EDGE,"E7.26.1"),sQuery(id+"F0.wireOp",EDGE,"E7.26.2"),sQuery(id+"F0.wireOp",EDGE,"E7.26.3"),sQuery(id+"F0.wireOp",EDGE,"E7.26.4"),sQuery(id+"F0.wireOp",EDGE,"E7.26.5"),sQuery(id+"F0.wireOp",EDGE,"E7.27.0"),sQuery(id+"F0.wireOp",EDGE,"E7.27.1"),sQuery(id+"F0.wireOp",EDGE,"E7.27.2"),sQuery(id+"F0.wireOp",EDGE,"E7.27.3"),sQuery(id+"F0.wireOp",EDGE,"E7.27.4"),sQuery(id+"F0.wireOp",EDGE,"E7.27.5"),sQuery(id+"F0.wireOp",EDGE,"E7.28.0"),sQuery(id+"F0.wireOp",EDGE,"E7.28.1"),sQuery(id+"F0.wireOp",EDGE,"E7.28.2"),sQuery(id+"F0.wireOp",EDGE,"E7.28.3"),sQuery(id+"F0.wireOp",EDGE,"E7.28.4"),sQuery(id+"F0.wireOp",EDGE,"E7.28.5"),sQuery(id+"F0.wireOp",EDGE,"E7.29.0"),sQuery(id+"F0.wireOp",EDGE,"E7.29.1"),sQuery(id+"F0.wireOp",EDGE,"E7.29.2"),sQuery(id+"F0.wireOp",EDGE,"E7.29.3"),sQuery(id+"F0.wireOp",EDGE,"E7.29.4"),sQuery(id+"F0.wireOp",EDGE,"E7.29.5"),sQuery(id+"F0.wireOp",EDGE,"E7.30.0"),sQuery(id+"F0.wireOp",EDGE,"E7.30.1"),sQuery(id+"F0.wireOp",EDGE,"E7.30.2"),sQuery(id+"F0.wireOp",EDGE,"E7.30.3"),sQuery(id+"F0.wireOp",EDGE,"E7.30.4"),sQuery(id+"F0.wireOp",EDGE,"E7.30.5"),sQuery(id+"F0.wireOp",EDGE,"E7.31.0"),sQuery(id+"F0.wireOp",EDGE,"E7.31.1"),sQuery(id+"F0.wireOp",EDGE,"E7.31.2"),sQuery(id+"F0.wireOp",EDGE,"E7.31.3"),sQuery(id+"F0.wireOp",EDGE,"E7.31.4"),sQuery(id+"F0.wireOp",EDGE,"E7.31.5"),sQuery(id+"F0.wireOp",EDGE,"E7.32.0"),sQuery(id+"F0.wireOp",EDGE,"E7.32.1"),sQuery(id+"F0.wireOp",EDGE,"E7.32.2"),sQuery(id+"F0.wireOp",EDGE,"E7.32.3"),sQuery(id+"F0.wireOp",EDGE,"E7.32.4"),sQuery(id+"F0.wireOp",EDGE,"E7.32.5"),sQuery(id+"F0.wireOp",EDGE,"E7.33.0"),sQuery(id+"F0.wireOp",EDGE,"E7.33.1"),sQuery(id+"F0.wireOp",EDGE,"E7.33.2"),sQuery(id+"F0.wireOp",EDGE,"E7.33.3"),sQuery(id+"F0.wireOp",EDGE,"E7.33.4"),sQuery(id+"F0.wireOp",EDGE,"E7.33.5"),subQ0,sQuery(id+"F0.wireOp",EDGE,"E7.34.1"),sQuery(id+"F0.wireOp",EDGE,"E7.34.2"),sQuery(id+"F0.wireOp",EDGE,"E7.34.3"),sQuery(id+"F0.wireOp",EDGE,"E7.34.4"),sQuery(id+"F0.wireOp",EDGE,"E7.34.5"),sQuery(id+"F0.wireOp",EDGE,"E7.35.0"),sQuery(id+"F0.wireOp",EDGE,"E7.35.1"),sQuery(id+"F0.wireOp",EDGE,"E7.35.2"),sQuery(id+"F0.wireOp",EDGE,"E7.35.3"),sQuery(id+"F0.wireOp",EDGE,"E7.35.4"),sQuery(id+"F0.wireOp",EDGE,"E7.35.5"),sQuery(id+"F0.wireOp",EDGE,"E7.36.0"),sQuery(id+"F0.wireOp",EDGE,"E7.36.1"),sQuery(id+"F0.wireOp",EDGE,"E7.36.2"),sQuery(id+"F0.wireOp",EDGE,"E7.36.3"),sQuery(id+"F0.wireOp",EDGE,"E7.36.4"),sQuery(id+"F0.wireOp",EDGE,"E7.36.5"),sQuery(id+"F0.wireOp",EDGE,"E7.37.0"),sQuery(id+"F0.wireOp",EDGE,"E7.37.1"),sQuery(id+"F0.wireOp",EDGE,"E7.37.2"),sQuery(id+"F0.wireOp",EDGE,"E7.37.3"),sQuery(id+"F0.wireOp",EDGE,"E7.37.4"),sQuery(id+"F0.wireOp",EDGE,"E7.37.5"),sQuery(id+"F0.wireOp",EDGE,"E7.38.0"),sQuery(id+"F0.wireOp",EDGE,"E7.38.1"),sQuery(id+"F0.wireOp",EDGE,"E7.38.2"),sQuery(id+"F0.wireOp",EDGE,"E7.38.3"),sQuery(id+"F0.wireOp",EDGE,"E7.38.4"),sQuery(id+"F0.wireOp",EDGE,"E7.38.5"),sQuery(id+"F0.wireOp",EDGE,"E7.39.0"),sQuery(id+"F0.wireOp",EDGE,"E7.39.1"),sQuery(id+"F0.wireOp",EDGE,"E7.39.2"),sQuery(id+"F0.wireOp",EDGE,"E7.39.3"),sQuery(id+"F0.wireOp",EDGE,"E7.39.4"),sQuery(id+"F0.wireOp",EDGE,"E7.39.5"),sQuery(id+"F0.wireOp",EDGE,"E7.40.0"),sQuery(id+"F0.wireOp",EDGE,"E7.40.1"),sQuery(id+"F0.wireOp",EDGE,"E7.40.2"),sQuery(id+"F0.wireOp",EDGE,"E7.40.3"),sQuery(id+"F0.wireOp",EDGE,"E7.40.4"),sQuery(id+"F0.wireOp",EDGE,"E7.40.5"),sQuery(id+"F0.wireOp",EDGE,"E7.41.0"),sQuery(id+"F0.wireOp",EDGE,"E7.41.1"),sQuery(id+"F0.wireOp",EDGE,"E7.41.2"),sQuery(id+"F0.wireOp",EDGE,"E7.41.3"),sQuery(id+"F0.wireOp",EDGE,"E7.41.4"),sQuery(id+"F0.wireOp",EDGE,"E7.41.5"),sQuery(id+"F0.wireOp",EDGE,"E7.42.0"),sQuery(id+"F0.wireOp",EDGE,"E7.42.1"),sQuery(id+"F0.wireOp",EDGE,"E7.42.2"),sQuery(id+"F0.wireOp",EDGE,"E7.42.3"),sQuery(id+"F0.wireOp",EDGE,"E7.42.4"),sQuery(id+"F0.wireOp",EDGE,"E7.42.5"),sQuery(id+"F0.wireOp",EDGE,"E7.43.0"),sQuery(id+"F0.wireOp",EDGE,"E7.43.1"),sQuery(id+"F0.wireOp",EDGE,"E7.43.2"),sQuery(id+"F0.wireOp",EDGE,"E7.43.3"),sQuery(id+"F0.wireOp",EDGE,"E7.43.4"),sQuery(id+"F0.wireOp",EDGE,"E7.43.5")])],"isStart":true})]});}
            var Q39;
            {var subQ0=sQuery(id+"F0.wireOp",EDGE,"E7.36.0");Q39=makeQuery(id+"F2.opChamfer","BLEND_EDGE",EDGE,{"blendedFrom":[makeQuery(id+"F1.opExtrude","CAP_EDGE",EDGE,{"disambiguationData":[OSD([subQ0])],"isStart":true}),makeQuery(id+"F1.opExtrude","CAP_FACE",FACE,{"disambiguationData":[OSD([sQuery(id+"F0.wireOp",EDGE,"E1"),sQuery(id+"F0.wireOp",EDGE,"E2"),sQuery(id+"F0.wireOp",EDGE,"E3"),sQuery(id+"F0.wireOp",EDGE,"E4"),sQuery(id+"F0.wireOp",EDGE,"E5"),sQuery(id+"F0.wireOp",EDGE,"E6"),sQuery(id+"F0.wireOp",EDGE,"E7.1.0"),sQuery(id+"F0.wireOp",EDGE,"E7.1.1"),sQuery(id+"F0.wireOp",EDGE,"E7.1.2"),sQuery(id+"F0.wireOp",EDGE,"E7.1.3"),sQuery(id+"F0.wireOp",EDGE,"E7.1.4"),sQuery(id+"F0.wireOp",EDGE,"E7.1.5"),sQuery(id+"F0.wireOp",EDGE,"E7.2.0"),sQuery(id+"F0.wireOp",EDGE,"E7.2.1"),sQuery(id+"F0.wireOp",EDGE,"E7.2.2"),sQuery(id+"F0.wireOp",EDGE,"E7.2.3"),sQuery(id+"F0.wireOp",EDGE,"E7.2.4"),sQuery(id+"F0.wireOp",EDGE,"E7.2.5"),sQuery(id+"F0.wireOp",EDGE,"E7.3.0"),sQuery(id+"F0.wireOp",EDGE,"E7.3.1"),sQuery(id+"F0.wireOp",EDGE,"E7.3.2"),sQuery(id+"F0.wireOp",EDGE,"E7.3.3"),sQuery(id+"F0.wireOp",EDGE,"E7.3.4"),sQuery(id+"F0.wireOp",EDGE,"E7.3.5"),sQuery(id+"F0.wireOp",EDGE,"E7.4.0"),sQuery(id+"F0.wireOp",EDGE,"E7.4.1"),sQuery(id+"F0.wireOp",EDGE,"E7.4.2"),sQuery(id+"F0.wireOp",EDGE,"E7.4.3"),sQuery(id+"F0.wireOp",EDGE,"E7.4.4"),sQuery(id+"F0.wireOp",EDGE,"E7.4.5"),sQuery(id+"F0.wireOp",EDGE,"E7.5.0"),sQuery(id+"F0.wireOp",EDGE,"E7.5.1"),sQuery(id+"F0.wireOp",EDGE,"E7.5.2"),sQuery(id+"F0.wireOp",EDGE,"E7.5.3"),sQuery(id+"F0.wireOp",EDGE,"E7.5.4"),sQuery(id+"F0.wireOp",EDGE,"E7.5.5"),sQuery(id+"F0.wireOp",EDGE,"E7.6.0"),sQuery(id+"F0.wireOp",EDGE,"E7.6.1"),sQuery(id+"F0.wireOp",EDGE,"E7.6.2"),sQuery(id+"F0.wireOp",EDGE,"E7.6.3"),sQuery(id+"F0.wireOp",EDGE,"E7.6.4"),sQuery(id+"F0.wireOp",EDGE,"E7.6.5"),sQuery(id+"F0.wireOp",EDGE,"E7.7.0"),sQuery(id+"F0.wireOp",EDGE,"E7.7.1"),sQuery(id+"F0.wireOp",EDGE,"E7.7.2"),sQuery(id+"F0.wireOp",EDGE,"E7.7.3"),sQuery(id+"F0.wireOp",EDGE,"E7.7.4"),sQuery(id+"F0.wireOp",EDGE,"E7.7.5"),sQuery(id+"F0.wireOp",EDGE,"E7.8.0"),sQuery(id+"F0.wireOp",EDGE,"E7.8.1"),sQuery(id+"F0.wireOp",EDGE,"E7.8.2"),sQuery(id+"F0.wireOp",EDGE,"E7.8.3"),sQuery(id+"F0.wireOp",EDGE,"E7.8.4"),sQuery(id+"F0.wireOp",EDGE,"E7.8.5"),sQuery(id+"F0.wireOp",EDGE,"E7.9.0"),sQuery(id+"F0.wireOp",EDGE,"E7.9.1"),sQuery(id+"F0.wireOp",EDGE,"E7.9.2"),sQuery(id+"F0.wireOp",EDGE,"E7.9.3"),sQuery(id+"F0.wireOp",EDGE,"E7.9.4"),sQuery(id+"F0.wireOp",EDGE,"E7.9.5"),sQuery(id+"F0.wireOp",EDGE,"E7.10.0"),sQuery(id+"F0.wireOp",EDGE,"E7.10.1"),sQuery(id+"F0.wireOp",EDGE,"E7.10.2"),sQuery(id+"F0.wireOp",EDGE,"E7.10.3"),sQuery(id+"F0.wireOp",EDGE,"E7.10.4"),sQuery(id+"F0.wireOp",EDGE,"E7.10.5"),sQuery(id+"F0.wireOp",EDGE,"E7.11.0"),sQuery(id+"F0.wireOp",EDGE,"E7.11.1"),sQuery(id+"F0.wireOp",EDGE,"E7.11.2"),sQuery(id+"F0.wireOp",EDGE,"E7.11.3"),sQuery(id+"F0.wireOp",EDGE,"E7.11.4"),sQuery(id+"F0.wireOp",EDGE,"E7.11.5"),sQuery(id+"F0.wireOp",EDGE,"E7.12.0"),sQuery(id+"F0.wireOp",EDGE,"E7.12.1"),sQuery(id+"F0.wireOp",EDGE,"E7.12.2"),sQuery(id+"F0.wireOp",EDGE,"E7.12.3"),sQuery(id+"F0.wireOp",EDGE,"E7.12.4"),sQuery(id+"F0.wireOp",EDGE,"E7.12.5"),sQuery(id+"F0.wireOp",EDGE,"E7.13.0"),sQuery(id+"F0.wireOp",EDGE,"E7.13.1"),sQuery(id+"F0.wireOp",EDGE,"E7.13.2"),sQuery(id+"F0.wireOp",EDGE,"E7.13.3"),sQuery(id+"F0.wireOp",EDGE,"E7.13.4"),sQuery(id+"F0.wireOp",EDGE,"E7.13.5"),sQuery(id+"F0.wireOp",EDGE,"E7.14.0"),sQuery(id+"F0.wireOp",EDGE,"E7.14.1"),sQuery(id+"F0.wireOp",EDGE,"E7.14.2"),sQuery(id+"F0.wireOp",EDGE,"E7.14.3"),sQuery(id+"F0.wireOp",EDGE,"E7.14.4"),sQuery(id+"F0.wireOp",EDGE,"E7.14.5"),sQuery(id+"F0.wireOp",EDGE,"E7.15.0"),sQuery(id+"F0.wireOp",EDGE,"E7.15.1"),sQuery(id+"F0.wireOp",EDGE,"E7.15.2"),sQuery(id+"F0.wireOp",EDGE,"E7.15.3"),sQuery(id+"F0.wireOp",EDGE,"E7.15.4"),sQuery(id+"F0.wireOp",EDGE,"E7.15.5"),sQuery(id+"F0.wireOp",EDGE,"E7.16.0"),sQuery(id+"F0.wireOp",EDGE,"E7.16.1"),sQuery(id+"F0.wireOp",EDGE,"E7.16.2"),sQuery(id+"F0.wireOp",EDGE,"E7.16.3"),sQuery(id+"F0.wireOp",EDGE,"E7.16.4"),sQuery(id+"F0.wireOp",EDGE,"E7.16.5"),sQuery(id+"F0.wireOp",EDGE,"E7.17.0"),sQuery(id+"F0.wireOp",EDGE,"E7.17.1"),sQuery(id+"F0.wireOp",EDGE,"E7.17.2"),sQuery(id+"F0.wireOp",EDGE,"E7.17.3"),sQuery(id+"F0.wireOp",EDGE,"E7.17.4"),sQuery(id+"F0.wireOp",EDGE,"E7.17.5"),sQuery(id+"F0.wireOp",EDGE,"E7.18.0"),sQuery(id+"F0.wireOp",EDGE,"E7.18.1"),sQuery(id+"F0.wireOp",EDGE,"E7.18.2"),sQuery(id+"F0.wireOp",EDGE,"E7.18.3"),sQuery(id+"F0.wireOp",EDGE,"E7.18.4"),sQuery(id+"F0.wireOp",EDGE,"E7.18.5"),sQuery(id+"F0.wireOp",EDGE,"E7.19.0"),sQuery(id+"F0.wireOp",EDGE,"E7.19.1"),sQuery(id+"F0.wireOp",EDGE,"E7.19.2"),sQuery(id+"F0.wireOp",EDGE,"E7.19.3"),sQuery(id+"F0.wireOp",EDGE,"E7.19.4"),sQuery(id+"F0.wireOp",EDGE,"E7.19.5"),sQuery(id+"F0.wireOp",EDGE,"E7.20.0"),sQuery(id+"F0.wireOp",EDGE,"E7.20.1"),sQuery(id+"F0.wireOp",EDGE,"E7.20.2"),sQuery(id+"F0.wireOp",EDGE,"E7.20.3"),sQuery(id+"F0.wireOp",EDGE,"E7.20.4"),sQuery(id+"F0.wireOp",EDGE,"E7.20.5"),sQuery(id+"F0.wireOp",EDGE,"E7.21.0"),sQuery(id+"F0.wireOp",EDGE,"E7.21.1"),sQuery(id+"F0.wireOp",EDGE,"E7.21.2"),sQuery(id+"F0.wireOp",EDGE,"E7.21.3"),sQuery(id+"F0.wireOp",EDGE,"E7.21.4"),sQuery(id+"F0.wireOp",EDGE,"E7.21.5"),sQuery(id+"F0.wireOp",EDGE,"E7.22.0"),sQuery(id+"F0.wireOp",EDGE,"E7.22.1"),sQuery(id+"F0.wireOp",EDGE,"E7.22.2"),sQuery(id+"F0.wireOp",EDGE,"E7.22.3"),sQuery(id+"F0.wireOp",EDGE,"E7.22.4"),sQuery(id+"F0.wireOp",EDGE,"E7.22.5"),sQuery(id+"F0.wireOp",EDGE,"E7.23.0"),sQuery(id+"F0.wireOp",EDGE,"E7.23.1"),sQuery(id+"F0.wireOp",EDGE,"E7.23.2"),sQuery(id+"F0.wireOp",EDGE,"E7.23.3"),sQuery(id+"F0.wireOp",EDGE,"E7.23.4"),sQuery(id+"F0.wireOp",EDGE,"E7.23.5"),sQuery(id+"F0.wireOp",EDGE,"E7.24.0"),sQuery(id+"F0.wireOp",EDGE,"E7.24.1"),sQuery(id+"F0.wireOp",EDGE,"E7.24.2"),sQuery(id+"F0.wireOp",EDGE,"E7.24.3"),sQuery(id+"F0.wireOp",EDGE,"E7.24.4"),sQuery(id+"F0.wireOp",EDGE,"E7.24.5"),sQuery(id+"F0.wireOp",EDGE,"E7.25.0"),sQuery(id+"F0.wireOp",EDGE,"E7.25.1"),sQuery(id+"F0.wireOp",EDGE,"E7.25.2"),sQuery(id+"F0.wireOp",EDGE,"E7.25.3"),sQuery(id+"F0.wireOp",EDGE,"E7.25.4"),sQuery(id+"F0.wireOp",EDGE,"E7.25.5"),sQuery(id+"F0.wireOp",EDGE,"E7.26.0"),sQuery(id+"F0.wireOp",EDGE,"E7.26.1"),sQuery(id+"F0.wireOp",EDGE,"E7.26.2"),sQuery(id+"F0.wireOp",EDGE,"E7.26.3"),sQuery(id+"F0.wireOp",EDGE,"E7.26.4"),sQuery(id+"F0.wireOp",EDGE,"E7.26.5"),sQuery(id+"F0.wireOp",EDGE,"E7.27.0"),sQuery(id+"F0.wireOp",EDGE,"E7.27.1"),sQuery(id+"F0.wireOp",EDGE,"E7.27.2"),sQuery(id+"F0.wireOp",EDGE,"E7.27.3"),sQuery(id+"F0.wireOp",EDGE,"E7.27.4"),sQuery(id+"F0.wireOp",EDGE,"E7.27.5"),sQuery(id+"F0.wireOp",EDGE,"E7.28.0"),sQuery(id+"F0.wireOp",EDGE,"E7.28.1"),sQuery(id+"F0.wireOp",EDGE,"E7.28.2"),sQuery(id+"F0.wireOp",EDGE,"E7.28.3"),sQuery(id+"F0.wireOp",EDGE,"E7.28.4"),sQuery(id+"F0.wireOp",EDGE,"E7.28.5"),sQuery(id+"F0.wireOp",EDGE,"E7.29.0"),sQuery(id+"F0.wireOp",EDGE,"E7.29.1"),sQuery(id+"F0.wireOp",EDGE,"E7.29.2"),sQuery(id+"F0.wireOp",EDGE,"E7.29.3"),sQuery(id+"F0.wireOp",EDGE,"E7.29.4"),sQuery(id+"F0.wireOp",EDGE,"E7.29.5"),sQuery(id+"F0.wireOp",EDGE,"E7.30.0"),sQuery(id+"F0.wireOp",EDGE,"E7.30.1"),sQuery(id+"F0.wireOp",EDGE,"E7.30.2"),sQuery(id+"F0.wireOp",EDGE,"E7.30.3"),sQuery(id+"F0.wireOp",EDGE,"E7.30.4"),sQuery(id+"F0.wireOp",EDGE,"E7.30.5"),sQuery(id+"F0.wireOp",EDGE,"E7.31.0"),sQuery(id+"F0.wireOp",EDGE,"E7.31.1"),sQuery(id+"F0.wireOp",EDGE,"E7.31.2"),sQuery(id+"F0.wireOp",EDGE,"E7.31.3"),sQuery(id+"F0.wireOp",EDGE,"E7.31.4"),sQuery(id+"F0.wireOp",EDGE,"E7.31.5"),sQuery(id+"F0.wireOp",EDGE,"E7.32.0"),sQuery(id+"F0.wireOp",EDGE,"E7.32.1"),sQuery(id+"F0.wireOp",EDGE,"E7.32.2"),sQuery(id+"F0.wireOp",EDGE,"E7.32.3"),sQuery(id+"F0.wireOp",EDGE,"E7.32.4"),sQuery(id+"F0.wireOp",EDGE,"E7.32.5"),sQuery(id+"F0.wireOp",EDGE,"E7.33.0"),sQuery(id+"F0.wireOp",EDGE,"E7.33.1"),sQuery(id+"F0.wireOp",EDGE,"E7.33.2"),sQuery(id+"F0.wireOp",EDGE,"E7.33.3"),sQuery(id+"F0.wireOp",EDGE,"E7.33.4"),sQuery(id+"F0.wireOp",EDGE,"E7.33.5"),sQuery(id+"F0.wireOp",EDGE,"E7.34.0"),sQuery(id+"F0.wireOp",EDGE,"E7.34.1"),sQuery(id+"F0.wireOp",EDGE,"E7.34.2"),sQuery(id+"F0.wireOp",EDGE,"E7.34.3"),sQuery(id+"F0.wireOp",EDGE,"E7.34.4"),sQuery(id+"F0.wireOp",EDGE,"E7.34.5"),sQuery(id+"F0.wireOp",EDGE,"E7.35.0"),sQuery(id+"F0.wireOp",EDGE,"E7.35.1"),sQuery(id+"F0.wireOp",EDGE,"E7.35.2"),sQuery(id+"F0.wireOp",EDGE,"E7.35.3"),sQuery(id+"F0.wireOp",EDGE,"E7.35.4"),sQuery(id+"F0.wireOp",EDGE,"E7.35.5"),subQ0,sQuery(id+"F0.wireOp",EDGE,"E7.36.1"),sQuery(id+"F0.wireOp",EDGE,"E7.36.2"),sQuery(id+"F0.wireOp",EDGE,"E7.36.3"),sQuery(id+"F0.wireOp",EDGE,"E7.36.4"),sQuery(id+"F0.wireOp",EDGE,"E7.36.5"),sQuery(id+"F0.wireOp",EDGE,"E7.37.0"),sQuery(id+"F0.wireOp",EDGE,"E7.37.1"),sQuery(id+"F0.wireOp",EDGE,"E7.37.2"),sQuery(id+"F0.wireOp",EDGE,"E7.37.3"),sQuery(id+"F0.wireOp",EDGE,"E7.37.4"),sQuery(id+"F0.wireOp",EDGE,"E7.37.5"),sQuery(id+"F0.wireOp",EDGE,"E7.38.0"),sQuery(id+"F0.wireOp",EDGE,"E7.38.1"),sQuery(id+"F0.wireOp",EDGE,"E7.38.2"),sQuery(id+"F0.wireOp",EDGE,"E7.38.3"),sQuery(id+"F0.wireOp",EDGE,"E7.38.4"),sQuery(id+"F0.wireOp",EDGE,"E7.38.5"),sQuery(id+"F0.wireOp",EDGE,"E7.39.0"),sQuery(id+"F0.wireOp",EDGE,"E7.39.1"),sQuery(id+"F0.wireOp",EDGE,"E7.39.2"),sQuery(id+"F0.wireOp",EDGE,"E7.39.3"),sQuery(id+"F0.wireOp",EDGE,"E7.39.4"),sQuery(id+"F0.wireOp",EDGE,"E7.39.5"),sQuery(id+"F0.wireOp",EDGE,"E7.40.0"),sQuery(id+"F0.wireOp",EDGE,"E7.40.1"),sQuery(id+"F0.wireOp",EDGE,"E7.40.2"),sQuery(id+"F0.wireOp",EDGE,"E7.40.3"),sQuery(id+"F0.wireOp",EDGE,"E7.40.4"),sQuery(id+"F0.wireOp",EDGE,"E7.40.5"),sQuery(id+"F0.wireOp",EDGE,"E7.41.0"),sQuery(id+"F0.wireOp",EDGE,"E7.41.1"),sQuery(id+"F0.wireOp",EDGE,"E7.41.2"),sQuery(id+"F0.wireOp",EDGE,"E7.41.3"),sQuery(id+"F0.wireOp",EDGE,"E7.41.4"),sQuery(id+"F0.wireOp",EDGE,"E7.41.5"),sQuery(id+"F0.wireOp",EDGE,"E7.42.0"),sQuery(id+"F0.wireOp",EDGE,"E7.42.1"),sQuery(id+"F0.wireOp",EDGE,"E7.42.2"),sQuery(id+"F0.wireOp",EDGE,"E7.42.3"),sQuery(id+"F0.wireOp",EDGE,"E7.42.4"),sQuery(id+"F0.wireOp",EDGE,"E7.42.5"),sQuery(id+"F0.wireOp",EDGE,"E7.43.0"),sQuery(id+"F0.wireOp",EDGE,"E7.43.1"),sQuery(id+"F0.wireOp",EDGE,"E7.43.2"),sQuery(id+"F0.wireOp",EDGE,"E7.43.3"),sQuery(id+"F0.wireOp",EDGE,"E7.43.4"),sQuery(id+"F0.wireOp",EDGE,"E7.43.5")])],"isStart":true})],"blendedInto":[makeQuery(id+"F1.opExtrude","CAP_FACE",FACE,{"disambiguationData":[OSD([sQuery(id+"F0.wireOp",EDGE,"E1"),sQuery(id+"F0.wireOp",EDGE,"E2"),sQuery(id+"F0.wireOp",EDGE,"E3"),sQuery(id+"F0.wireOp",EDGE,"E4"),sQuery(id+"F0.wireOp",EDGE,"E5"),sQuery(id+"F0.wireOp",EDGE,"E6"),sQuery(id+"F0.wireOp",EDGE,"E7.1.0"),sQuery(id+"F0.wireOp",EDGE,"E7.1.1"),sQuery(id+"F0.wireOp",EDGE,"E7.1.2"),sQuery(id+"F0.wireOp",EDGE,"E7.1.3"),sQuery(id+"F0.wireOp",EDGE,"E7.1.4"),sQuery(id+"F0.wireOp",EDGE,"E7.1.5"),sQuery(id+"F0.wireOp",EDGE,"E7.2.0"),sQuery(id+"F0.wireOp",EDGE,"E7.2.1"),sQuery(id+"F0.wireOp",EDGE,"E7.2.2"),sQuery(id+"F0.wireOp",EDGE,"E7.2.3"),sQuery(id+"F0.wireOp",EDGE,"E7.2.4"),sQuery(id+"F0.wireOp",EDGE,"E7.2.5"),sQuery(id+"F0.wireOp",EDGE,"E7.3.0"),sQuery(id+"F0.wireOp",EDGE,"E7.3.1"),sQuery(id+"F0.wireOp",EDGE,"E7.3.2"),sQuery(id+"F0.wireOp",EDGE,"E7.3.3"),sQuery(id+"F0.wireOp",EDGE,"E7.3.4"),sQuery(id+"F0.wireOp",EDGE,"E7.3.5"),sQuery(id+"F0.wireOp",EDGE,"E7.4.0"),sQuery(id+"F0.wireOp",EDGE,"E7.4.1"),sQuery(id+"F0.wireOp",EDGE,"E7.4.2"),sQuery(id+"F0.wireOp",EDGE,"E7.4.3"),sQuery(id+"F0.wireOp",EDGE,"E7.4.4"),sQuery(id+"F0.wireOp",EDGE,"E7.4.5"),sQuery(id+"F0.wireOp",EDGE,"E7.5.0"),sQuery(id+"F0.wireOp",EDGE,"E7.5.1"),sQuery(id+"F0.wireOp",EDGE,"E7.5.2"),sQuery(id+"F0.wireOp",EDGE,"E7.5.3"),sQuery(id+"F0.wireOp",EDGE,"E7.5.4"),sQuery(id+"F0.wireOp",EDGE,"E7.5.5"),sQuery(id+"F0.wireOp",EDGE,"E7.6.0"),sQuery(id+"F0.wireOp",EDGE,"E7.6.1"),sQuery(id+"F0.wireOp",EDGE,"E7.6.2"),sQuery(id+"F0.wireOp",EDGE,"E7.6.3"),sQuery(id+"F0.wireOp",EDGE,"E7.6.4"),sQuery(id+"F0.wireOp",EDGE,"E7.6.5"),sQuery(id+"F0.wireOp",EDGE,"E7.7.0"),sQuery(id+"F0.wireOp",EDGE,"E7.7.1"),sQuery(id+"F0.wireOp",EDGE,"E7.7.2"),sQuery(id+"F0.wireOp",EDGE,"E7.7.3"),sQuery(id+"F0.wireOp",EDGE,"E7.7.4"),sQuery(id+"F0.wireOp",EDGE,"E7.7.5"),sQuery(id+"F0.wireOp",EDGE,"E7.8.0"),sQuery(id+"F0.wireOp",EDGE,"E7.8.1"),sQuery(id+"F0.wireOp",EDGE,"E7.8.2"),sQuery(id+"F0.wireOp",EDGE,"E7.8.3"),sQuery(id+"F0.wireOp",EDGE,"E7.8.4"),sQuery(id+"F0.wireOp",EDGE,"E7.8.5"),sQuery(id+"F0.wireOp",EDGE,"E7.9.0"),sQuery(id+"F0.wireOp",EDGE,"E7.9.1"),sQuery(id+"F0.wireOp",EDGE,"E7.9.2"),sQuery(id+"F0.wireOp",EDGE,"E7.9.3"),sQuery(id+"F0.wireOp",EDGE,"E7.9.4"),sQuery(id+"F0.wireOp",EDGE,"E7.9.5"),sQuery(id+"F0.wireOp",EDGE,"E7.10.0"),sQuery(id+"F0.wireOp",EDGE,"E7.10.1"),sQuery(id+"F0.wireOp",EDGE,"E7.10.2"),sQuery(id+"F0.wireOp",EDGE,"E7.10.3"),sQuery(id+"F0.wireOp",EDGE,"E7.10.4"),sQuery(id+"F0.wireOp",EDGE,"E7.10.5"),sQuery(id+"F0.wireOp",EDGE,"E7.11.0"),sQuery(id+"F0.wireOp",EDGE,"E7.11.1"),sQuery(id+"F0.wireOp",EDGE,"E7.11.2"),sQuery(id+"F0.wireOp",EDGE,"E7.11.3"),sQuery(id+"F0.wireOp",EDGE,"E7.11.4"),sQuery(id+"F0.wireOp",EDGE,"E7.11.5"),sQuery(id+"F0.wireOp",EDGE,"E7.12.0"),sQuery(id+"F0.wireOp",EDGE,"E7.12.1"),sQuery(id+"F0.wireOp",EDGE,"E7.12.2"),sQuery(id+"F0.wireOp",EDGE,"E7.12.3"),sQuery(id+"F0.wireOp",EDGE,"E7.12.4"),sQuery(id+"F0.wireOp",EDGE,"E7.12.5"),sQuery(id+"F0.wireOp",EDGE,"E7.13.0"),sQuery(id+"F0.wireOp",EDGE,"E7.13.1"),sQuery(id+"F0.wireOp",EDGE,"E7.13.2"),sQuery(id+"F0.wireOp",EDGE,"E7.13.3"),sQuery(id+"F0.wireOp",EDGE,"E7.13.4"),sQuery(id+"F0.wireOp",EDGE,"E7.13.5"),sQuery(id+"F0.wireOp",EDGE,"E7.14.0"),sQuery(id+"F0.wireOp",EDGE,"E7.14.1"),sQuery(id+"F0.wireOp",EDGE,"E7.14.2"),sQuery(id+"F0.wireOp",EDGE,"E7.14.3"),sQuery(id+"F0.wireOp",EDGE,"E7.14.4"),sQuery(id+"F0.wireOp",EDGE,"E7.14.5"),sQuery(id+"F0.wireOp",EDGE,"E7.15.0"),sQuery(id+"F0.wireOp",EDGE,"E7.15.1"),sQuery(id+"F0.wireOp",EDGE,"E7.15.2"),sQuery(id+"F0.wireOp",EDGE,"E7.15.3"),sQuery(id+"F0.wireOp",EDGE,"E7.15.4"),sQuery(id+"F0.wireOp",EDGE,"E7.15.5"),sQuery(id+"F0.wireOp",EDGE,"E7.16.0"),sQuery(id+"F0.wireOp",EDGE,"E7.16.1"),sQuery(id+"F0.wireOp",EDGE,"E7.16.2"),sQuery(id+"F0.wireOp",EDGE,"E7.16.3"),sQuery(id+"F0.wireOp",EDGE,"E7.16.4"),sQuery(id+"F0.wireOp",EDGE,"E7.16.5"),sQuery(id+"F0.wireOp",EDGE,"E7.17.0"),sQuery(id+"F0.wireOp",EDGE,"E7.17.1"),sQuery(id+"F0.wireOp",EDGE,"E7.17.2"),sQuery(id+"F0.wireOp",EDGE,"E7.17.3"),sQuery(id+"F0.wireOp",EDGE,"E7.17.4"),sQuery(id+"F0.wireOp",EDGE,"E7.17.5"),sQuery(id+"F0.wireOp",EDGE,"E7.18.0"),sQuery(id+"F0.wireOp",EDGE,"E7.18.1"),sQuery(id+"F0.wireOp",EDGE,"E7.18.2"),sQuery(id+"F0.wireOp",EDGE,"E7.18.3"),sQuery(id+"F0.wireOp",EDGE,"E7.18.4"),sQuery(id+"F0.wireOp",EDGE,"E7.18.5"),sQuery(id+"F0.wireOp",EDGE,"E7.19.0"),sQuery(id+"F0.wireOp",EDGE,"E7.19.1"),sQuery(id+"F0.wireOp",EDGE,"E7.19.2"),sQuery(id+"F0.wireOp",EDGE,"E7.19.3"),sQuery(id+"F0.wireOp",EDGE,"E7.19.4"),sQuery(id+"F0.wireOp",EDGE,"E7.19.5"),sQuery(id+"F0.wireOp",EDGE,"E7.20.0"),sQuery(id+"F0.wireOp",EDGE,"E7.20.1"),sQuery(id+"F0.wireOp",EDGE,"E7.20.2"),sQuery(id+"F0.wireOp",EDGE,"E7.20.3"),sQuery(id+"F0.wireOp",EDGE,"E7.20.4"),sQuery(id+"F0.wireOp",EDGE,"E7.20.5"),sQuery(id+"F0.wireOp",EDGE,"E7.21.0"),sQuery(id+"F0.wireOp",EDGE,"E7.21.1"),sQuery(id+"F0.wireOp",EDGE,"E7.21.2"),sQuery(id+"F0.wireOp",EDGE,"E7.21.3"),sQuery(id+"F0.wireOp",EDGE,"E7.21.4"),sQuery(id+"F0.wireOp",EDGE,"E7.21.5"),sQuery(id+"F0.wireOp",EDGE,"E7.22.0"),sQuery(id+"F0.wireOp",EDGE,"E7.22.1"),sQuery(id+"F0.wireOp",EDGE,"E7.22.2"),sQuery(id+"F0.wireOp",EDGE,"E7.22.3"),sQuery(id+"F0.wireOp",EDGE,"E7.22.4"),sQuery(id+"F0.wireOp",EDGE,"E7.22.5"),sQuery(id+"F0.wireOp",EDGE,"E7.23.0"),sQuery(id+"F0.wireOp",EDGE,"E7.23.1"),sQuery(id+"F0.wireOp",EDGE,"E7.23.2"),sQuery(id+"F0.wireOp",EDGE,"E7.23.3"),sQuery(id+"F0.wireOp",EDGE,"E7.23.4"),sQuery(id+"F0.wireOp",EDGE,"E7.23.5"),sQuery(id+"F0.wireOp",EDGE,"E7.24.0"),sQuery(id+"F0.wireOp",EDGE,"E7.24.1"),sQuery(id+"F0.wireOp",EDGE,"E7.24.2"),sQuery(id+"F0.wireOp",EDGE,"E7.24.3"),sQuery(id+"F0.wireOp",EDGE,"E7.24.4"),sQuery(id+"F0.wireOp",EDGE,"E7.24.5"),sQuery(id+"F0.wireOp",EDGE,"E7.25.0"),sQuery(id+"F0.wireOp",EDGE,"E7.25.1"),sQuery(id+"F0.wireOp",EDGE,"E7.25.2"),sQuery(id+"F0.wireOp",EDGE,"E7.25.3"),sQuery(id+"F0.wireOp",EDGE,"E7.25.4"),sQuery(id+"F0.wireOp",EDGE,"E7.25.5"),sQuery(id+"F0.wireOp",EDGE,"E7.26.0"),sQuery(id+"F0.wireOp",EDGE,"E7.26.1"),sQuery(id+"F0.wireOp",EDGE,"E7.26.2"),sQuery(id+"F0.wireOp",EDGE,"E7.26.3"),sQuery(id+"F0.wireOp",EDGE,"E7.26.4"),sQuery(id+"F0.wireOp",EDGE,"E7.26.5"),sQuery(id+"F0.wireOp",EDGE,"E7.27.0"),sQuery(id+"F0.wireOp",EDGE,"E7.27.1"),sQuery(id+"F0.wireOp",EDGE,"E7.27.2"),sQuery(id+"F0.wireOp",EDGE,"E7.27.3"),sQuery(id+"F0.wireOp",EDGE,"E7.27.4"),sQuery(id+"F0.wireOp",EDGE,"E7.27.5"),sQuery(id+"F0.wireOp",EDGE,"E7.28.0"),sQuery(id+"F0.wireOp",EDGE,"E7.28.1"),sQuery(id+"F0.wireOp",EDGE,"E7.28.2"),sQuery(id+"F0.wireOp",EDGE,"E7.28.3"),sQuery(id+"F0.wireOp",EDGE,"E7.28.4"),sQuery(id+"F0.wireOp",EDGE,"E7.28.5"),sQuery(id+"F0.wireOp",EDGE,"E7.29.0"),sQuery(id+"F0.wireOp",EDGE,"E7.29.1"),sQuery(id+"F0.wireOp",EDGE,"E7.29.2"),sQuery(id+"F0.wireOp",EDGE,"E7.29.3"),sQuery(id+"F0.wireOp",EDGE,"E7.29.4"),sQuery(id+"F0.wireOp",EDGE,"E7.29.5"),sQuery(id+"F0.wireOp",EDGE,"E7.30.0"),sQuery(id+"F0.wireOp",EDGE,"E7.30.1"),sQuery(id+"F0.wireOp",EDGE,"E7.30.2"),sQuery(id+"F0.wireOp",EDGE,"E7.30.3"),sQuery(id+"F0.wireOp",EDGE,"E7.30.4"),sQuery(id+"F0.wireOp",EDGE,"E7.30.5"),sQuery(id+"F0.wireOp",EDGE,"E7.31.0"),sQuery(id+"F0.wireOp",EDGE,"E7.31.1"),sQuery(id+"F0.wireOp",EDGE,"E7.31.2"),sQuery(id+"F0.wireOp",EDGE,"E7.31.3"),sQuery(id+"F0.wireOp",EDGE,"E7.31.4"),sQuery(id+"F0.wireOp",EDGE,"E7.31.5"),sQuery(id+"F0.wireOp",EDGE,"E7.32.0"),sQuery(id+"F0.wireOp",EDGE,"E7.32.1"),sQuery(id+"F0.wireOp",EDGE,"E7.32.2"),sQuery(id+"F0.wireOp",EDGE,"E7.32.3"),sQuery(id+"F0.wireOp",EDGE,"E7.32.4"),sQuery(id+"F0.wireOp",EDGE,"E7.32.5"),sQuery(id+"F0.wireOp",EDGE,"E7.33.0"),sQuery(id+"F0.wireOp",EDGE,"E7.33.1"),sQuery(id+"F0.wireOp",EDGE,"E7.33.2"),sQuery(id+"F0.wireOp",EDGE,"E7.33.3"),sQuery(id+"F0.wireOp",EDGE,"E7.33.4"),sQuery(id+"F0.wireOp",EDGE,"E7.33.5"),sQuery(id+"F0.wireOp",EDGE,"E7.34.0"),sQuery(id+"F0.wireOp",EDGE,"E7.34.1"),sQuery(id+"F0.wireOp",EDGE,"E7.34.2"),sQuery(id+"F0.wireOp",EDGE,"E7.34.3"),sQuery(id+"F0.wireOp",EDGE,"E7.34.4"),sQuery(id+"F0.wireOp",EDGE,"E7.34.5"),sQuery(id+"F0.wireOp",EDGE,"E7.35.0"),sQuery(id+"F0.wireOp",EDGE,"E7.35.1"),sQuery(id+"F0.wireOp",EDGE,"E7.35.2"),sQuery(id+"F0.wireOp",EDGE,"E7.35.3"),sQuery(id+"F0.wireOp",EDGE,"E7.35.4"),sQuery(id+"F0.wireOp",EDGE,"E7.35.5"),subQ0,sQuery(id+"F0.wireOp",EDGE,"E7.36.1"),sQuery(id+"F0.wireOp",EDGE,"E7.36.2"),sQuery(id+"F0.wireOp",EDGE,"E7.36.3"),sQuery(id+"F0.wireOp",EDGE,"E7.36.4"),sQuery(id+"F0.wireOp",EDGE,"E7.36.5"),sQuery(id+"F0.wireOp",EDGE,"E7.37.0"),sQuery(id+"F0.wireOp",EDGE,"E7.37.1"),sQuery(id+"F0.wireOp",EDGE,"E7.37.2"),sQuery(id+"F0.wireOp",EDGE,"E7.37.3"),sQuery(id+"F0.wireOp",EDGE,"E7.37.4"),sQuery(id+"F0.wireOp",EDGE,"E7.37.5"),sQuery(id+"F0.wireOp",EDGE,"E7.38.0"),sQuery(id+"F0.wireOp",EDGE,"E7.38.1"),sQuery(id+"F0.wireOp",EDGE,"E7.38.2"),sQuery(id+"F0.wireOp",EDGE,"E7.38.3"),sQuery(id+"F0.wireOp",EDGE,"E7.38.4"),sQuery(id+"F0.wireOp",EDGE,"E7.38.5"),sQuery(id+"F0.wireOp",EDGE,"E7.39.0"),sQuery(id+"F0.wireOp",EDGE,"E7.39.1"),sQuery(id+"F0.wireOp",EDGE,"E7.39.2"),sQuery(id+"F0.wireOp",EDGE,"E7.39.3"),sQuery(id+"F0.wireOp",EDGE,"E7.39.4"),sQuery(id+"F0.wireOp",EDGE,"E7.39.5"),sQuery(id+"F0.wireOp",EDGE,"E7.40.0"),sQuery(id+"F0.wireOp",EDGE,"E7.40.1"),sQuery(id+"F0.wireOp",EDGE,"E7.40.2"),sQuery(id+"F0.wireOp",EDGE,"E7.40.3"),sQuery(id+"F0.wireOp",EDGE,"E7.40.4"),sQuery(id+"F0.wireOp",EDGE,"E7.40.5"),sQuery(id+"F0.wireOp",EDGE,"E7.41.0"),sQuery(id+"F0.wireOp",EDGE,"E7.41.1"),sQuery(id+"F0.wireOp",EDGE,"E7.41.2"),sQuery(id+"F0.wireOp",EDGE,"E7.41.3"),sQuery(id+"F0.wireOp",EDGE,"E7.41.4"),sQuery(id+"F0.wireOp",EDGE,"E7.41.5"),sQuery(id+"F0.wireOp",EDGE,"E7.42.0"),sQuery(id+"F0.wireOp",EDGE,"E7.42.1"),sQuery(id+"F0.wireOp",EDGE,"E7.42.2"),sQuery(id+"F0.wireOp",EDGE,"E7.42.3"),sQuery(id+"F0.wireOp",EDGE,"E7.42.4"),sQuery(id+"F0.wireOp",EDGE,"E7.42.5"),sQuery(id+"F0.wireOp",EDGE,"E7.43.0"),sQuery(id+"F0.wireOp",EDGE,"E7.43.1"),sQuery(id+"F0.wireOp",EDGE,"E7.43.2"),sQuery(id+"F0.wireOp",EDGE,"E7.43.3"),sQuery(id+"F0.wireOp",EDGE,"E7.43.4"),sQuery(id+"F0.wireOp",EDGE,"E7.43.5")])],"isStart":true})]});}
            var Q40;
            {var subQ0=sQuery(id+"F0.wireOp",EDGE,"E7.38.0");Q40=makeQuery(id+"F2.opChamfer","BLEND_EDGE",EDGE,{"blendedFrom":[makeQuery(id+"F1.opExtrude","CAP_EDGE",EDGE,{"disambiguationData":[OSD([subQ0])],"isStart":true}),makeQuery(id+"F1.opExtrude","CAP_FACE",FACE,{"disambiguationData":[OSD([sQuery(id+"F0.wireOp",EDGE,"E1"),sQuery(id+"F0.wireOp",EDGE,"E2"),sQuery(id+"F0.wireOp",EDGE,"E3"),sQuery(id+"F0.wireOp",EDGE,"E4"),sQuery(id+"F0.wireOp",EDGE,"E5"),sQuery(id+"F0.wireOp",EDGE,"E6"),sQuery(id+"F0.wireOp",EDGE,"E7.1.0"),sQuery(id+"F0.wireOp",EDGE,"E7.1.1"),sQuery(id+"F0.wireOp",EDGE,"E7.1.2"),sQuery(id+"F0.wireOp",EDGE,"E7.1.3"),sQuery(id+"F0.wireOp",EDGE,"E7.1.4"),sQuery(id+"F0.wireOp",EDGE,"E7.1.5"),sQuery(id+"F0.wireOp",EDGE,"E7.2.0"),sQuery(id+"F0.wireOp",EDGE,"E7.2.1"),sQuery(id+"F0.wireOp",EDGE,"E7.2.2"),sQuery(id+"F0.wireOp",EDGE,"E7.2.3"),sQuery(id+"F0.wireOp",EDGE,"E7.2.4"),sQuery(id+"F0.wireOp",EDGE,"E7.2.5"),sQuery(id+"F0.wireOp",EDGE,"E7.3.0"),sQuery(id+"F0.wireOp",EDGE,"E7.3.1"),sQuery(id+"F0.wireOp",EDGE,"E7.3.2"),sQuery(id+"F0.wireOp",EDGE,"E7.3.3"),sQuery(id+"F0.wireOp",EDGE,"E7.3.4"),sQuery(id+"F0.wireOp",EDGE,"E7.3.5"),sQuery(id+"F0.wireOp",EDGE,"E7.4.0"),sQuery(id+"F0.wireOp",EDGE,"E7.4.1"),sQuery(id+"F0.wireOp",EDGE,"E7.4.2"),sQuery(id+"F0.wireOp",EDGE,"E7.4.3"),sQuery(id+"F0.wireOp",EDGE,"E7.4.4"),sQuery(id+"F0.wireOp",EDGE,"E7.4.5"),sQuery(id+"F0.wireOp",EDGE,"E7.5.0"),sQuery(id+"F0.wireOp",EDGE,"E7.5.1"),sQuery(id+"F0.wireOp",EDGE,"E7.5.2"),sQuery(id+"F0.wireOp",EDGE,"E7.5.3"),sQuery(id+"F0.wireOp",EDGE,"E7.5.4"),sQuery(id+"F0.wireOp",EDGE,"E7.5.5"),sQuery(id+"F0.wireOp",EDGE,"E7.6.0"),sQuery(id+"F0.wireOp",EDGE,"E7.6.1"),sQuery(id+"F0.wireOp",EDGE,"E7.6.2"),sQuery(id+"F0.wireOp",EDGE,"E7.6.3"),sQuery(id+"F0.wireOp",EDGE,"E7.6.4"),sQuery(id+"F0.wireOp",EDGE,"E7.6.5"),sQuery(id+"F0.wireOp",EDGE,"E7.7.0"),sQuery(id+"F0.wireOp",EDGE,"E7.7.1"),sQuery(id+"F0.wireOp",EDGE,"E7.7.2"),sQuery(id+"F0.wireOp",EDGE,"E7.7.3"),sQuery(id+"F0.wireOp",EDGE,"E7.7.4"),sQuery(id+"F0.wireOp",EDGE,"E7.7.5"),sQuery(id+"F0.wireOp",EDGE,"E7.8.0"),sQuery(id+"F0.wireOp",EDGE,"E7.8.1"),sQuery(id+"F0.wireOp",EDGE,"E7.8.2"),sQuery(id+"F0.wireOp",EDGE,"E7.8.3"),sQuery(id+"F0.wireOp",EDGE,"E7.8.4"),sQuery(id+"F0.wireOp",EDGE,"E7.8.5"),sQuery(id+"F0.wireOp",EDGE,"E7.9.0"),sQuery(id+"F0.wireOp",EDGE,"E7.9.1"),sQuery(id+"F0.wireOp",EDGE,"E7.9.2"),sQuery(id+"F0.wireOp",EDGE,"E7.9.3"),sQuery(id+"F0.wireOp",EDGE,"E7.9.4"),sQuery(id+"F0.wireOp",EDGE,"E7.9.5"),sQuery(id+"F0.wireOp",EDGE,"E7.10.0"),sQuery(id+"F0.wireOp",EDGE,"E7.10.1"),sQuery(id+"F0.wireOp",EDGE,"E7.10.2"),sQuery(id+"F0.wireOp",EDGE,"E7.10.3"),sQuery(id+"F0.wireOp",EDGE,"E7.10.4"),sQuery(id+"F0.wireOp",EDGE,"E7.10.5"),sQuery(id+"F0.wireOp",EDGE,"E7.11.0"),sQuery(id+"F0.wireOp",EDGE,"E7.11.1"),sQuery(id+"F0.wireOp",EDGE,"E7.11.2"),sQuery(id+"F0.wireOp",EDGE,"E7.11.3"),sQuery(id+"F0.wireOp",EDGE,"E7.11.4"),sQuery(id+"F0.wireOp",EDGE,"E7.11.5"),sQuery(id+"F0.wireOp",EDGE,"E7.12.0"),sQuery(id+"F0.wireOp",EDGE,"E7.12.1"),sQuery(id+"F0.wireOp",EDGE,"E7.12.2"),sQuery(id+"F0.wireOp",EDGE,"E7.12.3"),sQuery(id+"F0.wireOp",EDGE,"E7.12.4"),sQuery(id+"F0.wireOp",EDGE,"E7.12.5"),sQuery(id+"F0.wireOp",EDGE,"E7.13.0"),sQuery(id+"F0.wireOp",EDGE,"E7.13.1"),sQuery(id+"F0.wireOp",EDGE,"E7.13.2"),sQuery(id+"F0.wireOp",EDGE,"E7.13.3"),sQuery(id+"F0.wireOp",EDGE,"E7.13.4"),sQuery(id+"F0.wireOp",EDGE,"E7.13.5"),sQuery(id+"F0.wireOp",EDGE,"E7.14.0"),sQuery(id+"F0.wireOp",EDGE,"E7.14.1"),sQuery(id+"F0.wireOp",EDGE,"E7.14.2"),sQuery(id+"F0.wireOp",EDGE,"E7.14.3"),sQuery(id+"F0.wireOp",EDGE,"E7.14.4"),sQuery(id+"F0.wireOp",EDGE,"E7.14.5"),sQuery(id+"F0.wireOp",EDGE,"E7.15.0"),sQuery(id+"F0.wireOp",EDGE,"E7.15.1"),sQuery(id+"F0.wireOp",EDGE,"E7.15.2"),sQuery(id+"F0.wireOp",EDGE,"E7.15.3"),sQuery(id+"F0.wireOp",EDGE,"E7.15.4"),sQuery(id+"F0.wireOp",EDGE,"E7.15.5"),sQuery(id+"F0.wireOp",EDGE,"E7.16.0"),sQuery(id+"F0.wireOp",EDGE,"E7.16.1"),sQuery(id+"F0.wireOp",EDGE,"E7.16.2"),sQuery(id+"F0.wireOp",EDGE,"E7.16.3"),sQuery(id+"F0.wireOp",EDGE,"E7.16.4"),sQuery(id+"F0.wireOp",EDGE,"E7.16.5"),sQuery(id+"F0.wireOp",EDGE,"E7.17.0"),sQuery(id+"F0.wireOp",EDGE,"E7.17.1"),sQuery(id+"F0.wireOp",EDGE,"E7.17.2"),sQuery(id+"F0.wireOp",EDGE,"E7.17.3"),sQuery(id+"F0.wireOp",EDGE,"E7.17.4"),sQuery(id+"F0.wireOp",EDGE,"E7.17.5"),sQuery(id+"F0.wireOp",EDGE,"E7.18.0"),sQuery(id+"F0.wireOp",EDGE,"E7.18.1"),sQuery(id+"F0.wireOp",EDGE,"E7.18.2"),sQuery(id+"F0.wireOp",EDGE,"E7.18.3"),sQuery(id+"F0.wireOp",EDGE,"E7.18.4"),sQuery(id+"F0.wireOp",EDGE,"E7.18.5"),sQuery(id+"F0.wireOp",EDGE,"E7.19.0"),sQuery(id+"F0.wireOp",EDGE,"E7.19.1"),sQuery(id+"F0.wireOp",EDGE,"E7.19.2"),sQuery(id+"F0.wireOp",EDGE,"E7.19.3"),sQuery(id+"F0.wireOp",EDGE,"E7.19.4"),sQuery(id+"F0.wireOp",EDGE,"E7.19.5"),sQuery(id+"F0.wireOp",EDGE,"E7.20.0"),sQuery(id+"F0.wireOp",EDGE,"E7.20.1"),sQuery(id+"F0.wireOp",EDGE,"E7.20.2"),sQuery(id+"F0.wireOp",EDGE,"E7.20.3"),sQuery(id+"F0.wireOp",EDGE,"E7.20.4"),sQuery(id+"F0.wireOp",EDGE,"E7.20.5"),sQuery(id+"F0.wireOp",EDGE,"E7.21.0"),sQuery(id+"F0.wireOp",EDGE,"E7.21.1"),sQuery(id+"F0.wireOp",EDGE,"E7.21.2"),sQuery(id+"F0.wireOp",EDGE,"E7.21.3"),sQuery(id+"F0.wireOp",EDGE,"E7.21.4"),sQuery(id+"F0.wireOp",EDGE,"E7.21.5"),sQuery(id+"F0.wireOp",EDGE,"E7.22.0"),sQuery(id+"F0.wireOp",EDGE,"E7.22.1"),sQuery(id+"F0.wireOp",EDGE,"E7.22.2"),sQuery(id+"F0.wireOp",EDGE,"E7.22.3"),sQuery(id+"F0.wireOp",EDGE,"E7.22.4"),sQuery(id+"F0.wireOp",EDGE,"E7.22.5"),sQuery(id+"F0.wireOp",EDGE,"E7.23.0"),sQuery(id+"F0.wireOp",EDGE,"E7.23.1"),sQuery(id+"F0.wireOp",EDGE,"E7.23.2"),sQuery(id+"F0.wireOp",EDGE,"E7.23.3"),sQuery(id+"F0.wireOp",EDGE,"E7.23.4"),sQuery(id+"F0.wireOp",EDGE,"E7.23.5"),sQuery(id+"F0.wireOp",EDGE,"E7.24.0"),sQuery(id+"F0.wireOp",EDGE,"E7.24.1"),sQuery(id+"F0.wireOp",EDGE,"E7.24.2"),sQuery(id+"F0.wireOp",EDGE,"E7.24.3"),sQuery(id+"F0.wireOp",EDGE,"E7.24.4"),sQuery(id+"F0.wireOp",EDGE,"E7.24.5"),sQuery(id+"F0.wireOp",EDGE,"E7.25.0"),sQuery(id+"F0.wireOp",EDGE,"E7.25.1"),sQuery(id+"F0.wireOp",EDGE,"E7.25.2"),sQuery(id+"F0.wireOp",EDGE,"E7.25.3"),sQuery(id+"F0.wireOp",EDGE,"E7.25.4"),sQuery(id+"F0.wireOp",EDGE,"E7.25.5"),sQuery(id+"F0.wireOp",EDGE,"E7.26.0"),sQuery(id+"F0.wireOp",EDGE,"E7.26.1"),sQuery(id+"F0.wireOp",EDGE,"E7.26.2"),sQuery(id+"F0.wireOp",EDGE,"E7.26.3"),sQuery(id+"F0.wireOp",EDGE,"E7.26.4"),sQuery(id+"F0.wireOp",EDGE,"E7.26.5"),sQuery(id+"F0.wireOp",EDGE,"E7.27.0"),sQuery(id+"F0.wireOp",EDGE,"E7.27.1"),sQuery(id+"F0.wireOp",EDGE,"E7.27.2"),sQuery(id+"F0.wireOp",EDGE,"E7.27.3"),sQuery(id+"F0.wireOp",EDGE,"E7.27.4"),sQuery(id+"F0.wireOp",EDGE,"E7.27.5"),sQuery(id+"F0.wireOp",EDGE,"E7.28.0"),sQuery(id+"F0.wireOp",EDGE,"E7.28.1"),sQuery(id+"F0.wireOp",EDGE,"E7.28.2"),sQuery(id+"F0.wireOp",EDGE,"E7.28.3"),sQuery(id+"F0.wireOp",EDGE,"E7.28.4"),sQuery(id+"F0.wireOp",EDGE,"E7.28.5"),sQuery(id+"F0.wireOp",EDGE,"E7.29.0"),sQuery(id+"F0.wireOp",EDGE,"E7.29.1"),sQuery(id+"F0.wireOp",EDGE,"E7.29.2"),sQuery(id+"F0.wireOp",EDGE,"E7.29.3"),sQuery(id+"F0.wireOp",EDGE,"E7.29.4"),sQuery(id+"F0.wireOp",EDGE,"E7.29.5"),sQuery(id+"F0.wireOp",EDGE,"E7.30.0"),sQuery(id+"F0.wireOp",EDGE,"E7.30.1"),sQuery(id+"F0.wireOp",EDGE,"E7.30.2"),sQuery(id+"F0.wireOp",EDGE,"E7.30.3"),sQuery(id+"F0.wireOp",EDGE,"E7.30.4"),sQuery(id+"F0.wireOp",EDGE,"E7.30.5"),sQuery(id+"F0.wireOp",EDGE,"E7.31.0"),sQuery(id+"F0.wireOp",EDGE,"E7.31.1"),sQuery(id+"F0.wireOp",EDGE,"E7.31.2"),sQuery(id+"F0.wireOp",EDGE,"E7.31.3"),sQuery(id+"F0.wireOp",EDGE,"E7.31.4"),sQuery(id+"F0.wireOp",EDGE,"E7.31.5"),sQuery(id+"F0.wireOp",EDGE,"E7.32.0"),sQuery(id+"F0.wireOp",EDGE,"E7.32.1"),sQuery(id+"F0.wireOp",EDGE,"E7.32.2"),sQuery(id+"F0.wireOp",EDGE,"E7.32.3"),sQuery(id+"F0.wireOp",EDGE,"E7.32.4"),sQuery(id+"F0.wireOp",EDGE,"E7.32.5"),sQuery(id+"F0.wireOp",EDGE,"E7.33.0"),sQuery(id+"F0.wireOp",EDGE,"E7.33.1"),sQuery(id+"F0.wireOp",EDGE,"E7.33.2"),sQuery(id+"F0.wireOp",EDGE,"E7.33.3"),sQuery(id+"F0.wireOp",EDGE,"E7.33.4"),sQuery(id+"F0.wireOp",EDGE,"E7.33.5"),sQuery(id+"F0.wireOp",EDGE,"E7.34.0"),sQuery(id+"F0.wireOp",EDGE,"E7.34.1"),sQuery(id+"F0.wireOp",EDGE,"E7.34.2"),sQuery(id+"F0.wireOp",EDGE,"E7.34.3"),sQuery(id+"F0.wireOp",EDGE,"E7.34.4"),sQuery(id+"F0.wireOp",EDGE,"E7.34.5"),sQuery(id+"F0.wireOp",EDGE,"E7.35.0"),sQuery(id+"F0.wireOp",EDGE,"E7.35.1"),sQuery(id+"F0.wireOp",EDGE,"E7.35.2"),sQuery(id+"F0.wireOp",EDGE,"E7.35.3"),sQuery(id+"F0.wireOp",EDGE,"E7.35.4"),sQuery(id+"F0.wireOp",EDGE,"E7.35.5"),sQuery(id+"F0.wireOp",EDGE,"E7.36.0"),sQuery(id+"F0.wireOp",EDGE,"E7.36.1"),sQuery(id+"F0.wireOp",EDGE,"E7.36.2"),sQuery(id+"F0.wireOp",EDGE,"E7.36.3"),sQuery(id+"F0.wireOp",EDGE,"E7.36.4"),sQuery(id+"F0.wireOp",EDGE,"E7.36.5"),sQuery(id+"F0.wireOp",EDGE,"E7.37.0"),sQuery(id+"F0.wireOp",EDGE,"E7.37.1"),sQuery(id+"F0.wireOp",EDGE,"E7.37.2"),sQuery(id+"F0.wireOp",EDGE,"E7.37.3"),sQuery(id+"F0.wireOp",EDGE,"E7.37.4"),sQuery(id+"F0.wireOp",EDGE,"E7.37.5"),subQ0,sQuery(id+"F0.wireOp",EDGE,"E7.38.1"),sQuery(id+"F0.wireOp",EDGE,"E7.38.2"),sQuery(id+"F0.wireOp",EDGE,"E7.38.3"),sQuery(id+"F0.wireOp",EDGE,"E7.38.4"),sQuery(id+"F0.wireOp",EDGE,"E7.38.5"),sQuery(id+"F0.wireOp",EDGE,"E7.39.0"),sQuery(id+"F0.wireOp",EDGE,"E7.39.1"),sQuery(id+"F0.wireOp",EDGE,"E7.39.2"),sQuery(id+"F0.wireOp",EDGE,"E7.39.3"),sQuery(id+"F0.wireOp",EDGE,"E7.39.4"),sQuery(id+"F0.wireOp",EDGE,"E7.39.5"),sQuery(id+"F0.wireOp",EDGE,"E7.40.0"),sQuery(id+"F0.wireOp",EDGE,"E7.40.1"),sQuery(id+"F0.wireOp",EDGE,"E7.40.2"),sQuery(id+"F0.wireOp",EDGE,"E7.40.3"),sQuery(id+"F0.wireOp",EDGE,"E7.40.4"),sQuery(id+"F0.wireOp",EDGE,"E7.40.5"),sQuery(id+"F0.wireOp",EDGE,"E7.41.0"),sQuery(id+"F0.wireOp",EDGE,"E7.41.1"),sQuery(id+"F0.wireOp",EDGE,"E7.41.2"),sQuery(id+"F0.wireOp",EDGE,"E7.41.3"),sQuery(id+"F0.wireOp",EDGE,"E7.41.4"),sQuery(id+"F0.wireOp",EDGE,"E7.41.5"),sQuery(id+"F0.wireOp",EDGE,"E7.42.0"),sQuery(id+"F0.wireOp",EDGE,"E7.42.1"),sQuery(id+"F0.wireOp",EDGE,"E7.42.2"),sQuery(id+"F0.wireOp",EDGE,"E7.42.3"),sQuery(id+"F0.wireOp",EDGE,"E7.42.4"),sQuery(id+"F0.wireOp",EDGE,"E7.42.5"),sQuery(id+"F0.wireOp",EDGE,"E7.43.0"),sQuery(id+"F0.wireOp",EDGE,"E7.43.1"),sQuery(id+"F0.wireOp",EDGE,"E7.43.2"),sQuery(id+"F0.wireOp",EDGE,"E7.43.3"),sQuery(id+"F0.wireOp",EDGE,"E7.43.4"),sQuery(id+"F0.wireOp",EDGE,"E7.43.5")])],"isStart":true})],"blendedInto":[makeQuery(id+"F1.opExtrude","CAP_FACE",FACE,{"disambiguationData":[OSD([sQuery(id+"F0.wireOp",EDGE,"E1"),sQuery(id+"F0.wireOp",EDGE,"E2"),sQuery(id+"F0.wireOp",EDGE,"E3"),sQuery(id+"F0.wireOp",EDGE,"E4"),sQuery(id+"F0.wireOp",EDGE,"E5"),sQuery(id+"F0.wireOp",EDGE,"E6"),sQuery(id+"F0.wireOp",EDGE,"E7.1.0"),sQuery(id+"F0.wireOp",EDGE,"E7.1.1"),sQuery(id+"F0.wireOp",EDGE,"E7.1.2"),sQuery(id+"F0.wireOp",EDGE,"E7.1.3"),sQuery(id+"F0.wireOp",EDGE,"E7.1.4"),sQuery(id+"F0.wireOp",EDGE,"E7.1.5"),sQuery(id+"F0.wireOp",EDGE,"E7.2.0"),sQuery(id+"F0.wireOp",EDGE,"E7.2.1"),sQuery(id+"F0.wireOp",EDGE,"E7.2.2"),sQuery(id+"F0.wireOp",EDGE,"E7.2.3"),sQuery(id+"F0.wireOp",EDGE,"E7.2.4"),sQuery(id+"F0.wireOp",EDGE,"E7.2.5"),sQuery(id+"F0.wireOp",EDGE,"E7.3.0"),sQuery(id+"F0.wireOp",EDGE,"E7.3.1"),sQuery(id+"F0.wireOp",EDGE,"E7.3.2"),sQuery(id+"F0.wireOp",EDGE,"E7.3.3"),sQuery(id+"F0.wireOp",EDGE,"E7.3.4"),sQuery(id+"F0.wireOp",EDGE,"E7.3.5"),sQuery(id+"F0.wireOp",EDGE,"E7.4.0"),sQuery(id+"F0.wireOp",EDGE,"E7.4.1"),sQuery(id+"F0.wireOp",EDGE,"E7.4.2"),sQuery(id+"F0.wireOp",EDGE,"E7.4.3"),sQuery(id+"F0.wireOp",EDGE,"E7.4.4"),sQuery(id+"F0.wireOp",EDGE,"E7.4.5"),sQuery(id+"F0.wireOp",EDGE,"E7.5.0"),sQuery(id+"F0.wireOp",EDGE,"E7.5.1"),sQuery(id+"F0.wireOp",EDGE,"E7.5.2"),sQuery(id+"F0.wireOp",EDGE,"E7.5.3"),sQuery(id+"F0.wireOp",EDGE,"E7.5.4"),sQuery(id+"F0.wireOp",EDGE,"E7.5.5"),sQuery(id+"F0.wireOp",EDGE,"E7.6.0"),sQuery(id+"F0.wireOp",EDGE,"E7.6.1"),sQuery(id+"F0.wireOp",EDGE,"E7.6.2"),sQuery(id+"F0.wireOp",EDGE,"E7.6.3"),sQuery(id+"F0.wireOp",EDGE,"E7.6.4"),sQuery(id+"F0.wireOp",EDGE,"E7.6.5"),sQuery(id+"F0.wireOp",EDGE,"E7.7.0"),sQuery(id+"F0.wireOp",EDGE,"E7.7.1"),sQuery(id+"F0.wireOp",EDGE,"E7.7.2"),sQuery(id+"F0.wireOp",EDGE,"E7.7.3"),sQuery(id+"F0.wireOp",EDGE,"E7.7.4"),sQuery(id+"F0.wireOp",EDGE,"E7.7.5"),sQuery(id+"F0.wireOp",EDGE,"E7.8.0"),sQuery(id+"F0.wireOp",EDGE,"E7.8.1"),sQuery(id+"F0.wireOp",EDGE,"E7.8.2"),sQuery(id+"F0.wireOp",EDGE,"E7.8.3"),sQuery(id+"F0.wireOp",EDGE,"E7.8.4"),sQuery(id+"F0.wireOp",EDGE,"E7.8.5"),sQuery(id+"F0.wireOp",EDGE,"E7.9.0"),sQuery(id+"F0.wireOp",EDGE,"E7.9.1"),sQuery(id+"F0.wireOp",EDGE,"E7.9.2"),sQuery(id+"F0.wireOp",EDGE,"E7.9.3"),sQuery(id+"F0.wireOp",EDGE,"E7.9.4"),sQuery(id+"F0.wireOp",EDGE,"E7.9.5"),sQuery(id+"F0.wireOp",EDGE,"E7.10.0"),sQuery(id+"F0.wireOp",EDGE,"E7.10.1"),sQuery(id+"F0.wireOp",EDGE,"E7.10.2"),sQuery(id+"F0.wireOp",EDGE,"E7.10.3"),sQuery(id+"F0.wireOp",EDGE,"E7.10.4"),sQuery(id+"F0.wireOp",EDGE,"E7.10.5"),sQuery(id+"F0.wireOp",EDGE,"E7.11.0"),sQuery(id+"F0.wireOp",EDGE,"E7.11.1"),sQuery(id+"F0.wireOp",EDGE,"E7.11.2"),sQuery(id+"F0.wireOp",EDGE,"E7.11.3"),sQuery(id+"F0.wireOp",EDGE,"E7.11.4"),sQuery(id+"F0.wireOp",EDGE,"E7.11.5"),sQuery(id+"F0.wireOp",EDGE,"E7.12.0"),sQuery(id+"F0.wireOp",EDGE,"E7.12.1"),sQuery(id+"F0.wireOp",EDGE,"E7.12.2"),sQuery(id+"F0.wireOp",EDGE,"E7.12.3"),sQuery(id+"F0.wireOp",EDGE,"E7.12.4"),sQuery(id+"F0.wireOp",EDGE,"E7.12.5"),sQuery(id+"F0.wireOp",EDGE,"E7.13.0"),sQuery(id+"F0.wireOp",EDGE,"E7.13.1"),sQuery(id+"F0.wireOp",EDGE,"E7.13.2"),sQuery(id+"F0.wireOp",EDGE,"E7.13.3"),sQuery(id+"F0.wireOp",EDGE,"E7.13.4"),sQuery(id+"F0.wireOp",EDGE,"E7.13.5"),sQuery(id+"F0.wireOp",EDGE,"E7.14.0"),sQuery(id+"F0.wireOp",EDGE,"E7.14.1"),sQuery(id+"F0.wireOp",EDGE,"E7.14.2"),sQuery(id+"F0.wireOp",EDGE,"E7.14.3"),sQuery(id+"F0.wireOp",EDGE,"E7.14.4"),sQuery(id+"F0.wireOp",EDGE,"E7.14.5"),sQuery(id+"F0.wireOp",EDGE,"E7.15.0"),sQuery(id+"F0.wireOp",EDGE,"E7.15.1"),sQuery(id+"F0.wireOp",EDGE,"E7.15.2"),sQuery(id+"F0.wireOp",EDGE,"E7.15.3"),sQuery(id+"F0.wireOp",EDGE,"E7.15.4"),sQuery(id+"F0.wireOp",EDGE,"E7.15.5"),sQuery(id+"F0.wireOp",EDGE,"E7.16.0"),sQuery(id+"F0.wireOp",EDGE,"E7.16.1"),sQuery(id+"F0.wireOp",EDGE,"E7.16.2"),sQuery(id+"F0.wireOp",EDGE,"E7.16.3"),sQuery(id+"F0.wireOp",EDGE,"E7.16.4"),sQuery(id+"F0.wireOp",EDGE,"E7.16.5"),sQuery(id+"F0.wireOp",EDGE,"E7.17.0"),sQuery(id+"F0.wireOp",EDGE,"E7.17.1"),sQuery(id+"F0.wireOp",EDGE,"E7.17.2"),sQuery(id+"F0.wireOp",EDGE,"E7.17.3"),sQuery(id+"F0.wireOp",EDGE,"E7.17.4"),sQuery(id+"F0.wireOp",EDGE,"E7.17.5"),sQuery(id+"F0.wireOp",EDGE,"E7.18.0"),sQuery(id+"F0.wireOp",EDGE,"E7.18.1"),sQuery(id+"F0.wireOp",EDGE,"E7.18.2"),sQuery(id+"F0.wireOp",EDGE,"E7.18.3"),sQuery(id+"F0.wireOp",EDGE,"E7.18.4"),sQuery(id+"F0.wireOp",EDGE,"E7.18.5"),sQuery(id+"F0.wireOp",EDGE,"E7.19.0"),sQuery(id+"F0.wireOp",EDGE,"E7.19.1"),sQuery(id+"F0.wireOp",EDGE,"E7.19.2"),sQuery(id+"F0.wireOp",EDGE,"E7.19.3"),sQuery(id+"F0.wireOp",EDGE,"E7.19.4"),sQuery(id+"F0.wireOp",EDGE,"E7.19.5"),sQuery(id+"F0.wireOp",EDGE,"E7.20.0"),sQuery(id+"F0.wireOp",EDGE,"E7.20.1"),sQuery(id+"F0.wireOp",EDGE,"E7.20.2"),sQuery(id+"F0.wireOp",EDGE,"E7.20.3"),sQuery(id+"F0.wireOp",EDGE,"E7.20.4"),sQuery(id+"F0.wireOp",EDGE,"E7.20.5"),sQuery(id+"F0.wireOp",EDGE,"E7.21.0"),sQuery(id+"F0.wireOp",EDGE,"E7.21.1"),sQuery(id+"F0.wireOp",EDGE,"E7.21.2"),sQuery(id+"F0.wireOp",EDGE,"E7.21.3"),sQuery(id+"F0.wireOp",EDGE,"E7.21.4"),sQuery(id+"F0.wireOp",EDGE,"E7.21.5"),sQuery(id+"F0.wireOp",EDGE,"E7.22.0"),sQuery(id+"F0.wireOp",EDGE,"E7.22.1"),sQuery(id+"F0.wireOp",EDGE,"E7.22.2"),sQuery(id+"F0.wireOp",EDGE,"E7.22.3"),sQuery(id+"F0.wireOp",EDGE,"E7.22.4"),sQuery(id+"F0.wireOp",EDGE,"E7.22.5"),sQuery(id+"F0.wireOp",EDGE,"E7.23.0"),sQuery(id+"F0.wireOp",EDGE,"E7.23.1"),sQuery(id+"F0.wireOp",EDGE,"E7.23.2"),sQuery(id+"F0.wireOp",EDGE,"E7.23.3"),sQuery(id+"F0.wireOp",EDGE,"E7.23.4"),sQuery(id+"F0.wireOp",EDGE,"E7.23.5"),sQuery(id+"F0.wireOp",EDGE,"E7.24.0"),sQuery(id+"F0.wireOp",EDGE,"E7.24.1"),sQuery(id+"F0.wireOp",EDGE,"E7.24.2"),sQuery(id+"F0.wireOp",EDGE,"E7.24.3"),sQuery(id+"F0.wireOp",EDGE,"E7.24.4"),sQuery(id+"F0.wireOp",EDGE,"E7.24.5"),sQuery(id+"F0.wireOp",EDGE,"E7.25.0"),sQuery(id+"F0.wireOp",EDGE,"E7.25.1"),sQuery(id+"F0.wireOp",EDGE,"E7.25.2"),sQuery(id+"F0.wireOp",EDGE,"E7.25.3"),sQuery(id+"F0.wireOp",EDGE,"E7.25.4"),sQuery(id+"F0.wireOp",EDGE,"E7.25.5"),sQuery(id+"F0.wireOp",EDGE,"E7.26.0"),sQuery(id+"F0.wireOp",EDGE,"E7.26.1"),sQuery(id+"F0.wireOp",EDGE,"E7.26.2"),sQuery(id+"F0.wireOp",EDGE,"E7.26.3"),sQuery(id+"F0.wireOp",EDGE,"E7.26.4"),sQuery(id+"F0.wireOp",EDGE,"E7.26.5"),sQuery(id+"F0.wireOp",EDGE,"E7.27.0"),sQuery(id+"F0.wireOp",EDGE,"E7.27.1"),sQuery(id+"F0.wireOp",EDGE,"E7.27.2"),sQuery(id+"F0.wireOp",EDGE,"E7.27.3"),sQuery(id+"F0.wireOp",EDGE,"E7.27.4"),sQuery(id+"F0.wireOp",EDGE,"E7.27.5"),sQuery(id+"F0.wireOp",EDGE,"E7.28.0"),sQuery(id+"F0.wireOp",EDGE,"E7.28.1"),sQuery(id+"F0.wireOp",EDGE,"E7.28.2"),sQuery(id+"F0.wireOp",EDGE,"E7.28.3"),sQuery(id+"F0.wireOp",EDGE,"E7.28.4"),sQuery(id+"F0.wireOp",EDGE,"E7.28.5"),sQuery(id+"F0.wireOp",EDGE,"E7.29.0"),sQuery(id+"F0.wireOp",EDGE,"E7.29.1"),sQuery(id+"F0.wireOp",EDGE,"E7.29.2"),sQuery(id+"F0.wireOp",EDGE,"E7.29.3"),sQuery(id+"F0.wireOp",EDGE,"E7.29.4"),sQuery(id+"F0.wireOp",EDGE,"E7.29.5"),sQuery(id+"F0.wireOp",EDGE,"E7.30.0"),sQuery(id+"F0.wireOp",EDGE,"E7.30.1"),sQuery(id+"F0.wireOp",EDGE,"E7.30.2"),sQuery(id+"F0.wireOp",EDGE,"E7.30.3"),sQuery(id+"F0.wireOp",EDGE,"E7.30.4"),sQuery(id+"F0.wireOp",EDGE,"E7.30.5"),sQuery(id+"F0.wireOp",EDGE,"E7.31.0"),sQuery(id+"F0.wireOp",EDGE,"E7.31.1"),sQuery(id+"F0.wireOp",EDGE,"E7.31.2"),sQuery(id+"F0.wireOp",EDGE,"E7.31.3"),sQuery(id+"F0.wireOp",EDGE,"E7.31.4"),sQuery(id+"F0.wireOp",EDGE,"E7.31.5"),sQuery(id+"F0.wireOp",EDGE,"E7.32.0"),sQuery(id+"F0.wireOp",EDGE,"E7.32.1"),sQuery(id+"F0.wireOp",EDGE,"E7.32.2"),sQuery(id+"F0.wireOp",EDGE,"E7.32.3"),sQuery(id+"F0.wireOp",EDGE,"E7.32.4"),sQuery(id+"F0.wireOp",EDGE,"E7.32.5"),sQuery(id+"F0.wireOp",EDGE,"E7.33.0"),sQuery(id+"F0.wireOp",EDGE,"E7.33.1"),sQuery(id+"F0.wireOp",EDGE,"E7.33.2"),sQuery(id+"F0.wireOp",EDGE,"E7.33.3"),sQuery(id+"F0.wireOp",EDGE,"E7.33.4"),sQuery(id+"F0.wireOp",EDGE,"E7.33.5"),sQuery(id+"F0.wireOp",EDGE,"E7.34.0"),sQuery(id+"F0.wireOp",EDGE,"E7.34.1"),sQuery(id+"F0.wireOp",EDGE,"E7.34.2"),sQuery(id+"F0.wireOp",EDGE,"E7.34.3"),sQuery(id+"F0.wireOp",EDGE,"E7.34.4"),sQuery(id+"F0.wireOp",EDGE,"E7.34.5"),sQuery(id+"F0.wireOp",EDGE,"E7.35.0"),sQuery(id+"F0.wireOp",EDGE,"E7.35.1"),sQuery(id+"F0.wireOp",EDGE,"E7.35.2"),sQuery(id+"F0.wireOp",EDGE,"E7.35.3"),sQuery(id+"F0.wireOp",EDGE,"E7.35.4"),sQuery(id+"F0.wireOp",EDGE,"E7.35.5"),sQuery(id+"F0.wireOp",EDGE,"E7.36.0"),sQuery(id+"F0.wireOp",EDGE,"E7.36.1"),sQuery(id+"F0.wireOp",EDGE,"E7.36.2"),sQuery(id+"F0.wireOp",EDGE,"E7.36.3"),sQuery(id+"F0.wireOp",EDGE,"E7.36.4"),sQuery(id+"F0.wireOp",EDGE,"E7.36.5"),sQuery(id+"F0.wireOp",EDGE,"E7.37.0"),sQuery(id+"F0.wireOp",EDGE,"E7.37.1"),sQuery(id+"F0.wireOp",EDGE,"E7.37.2"),sQuery(id+"F0.wireOp",EDGE,"E7.37.3"),sQuery(id+"F0.wireOp",EDGE,"E7.37.4"),sQuery(id+"F0.wireOp",EDGE,"E7.37.5"),subQ0,sQuery(id+"F0.wireOp",EDGE,"E7.38.1"),sQuery(id+"F0.wireOp",EDGE,"E7.38.2"),sQuery(id+"F0.wireOp",EDGE,"E7.38.3"),sQuery(id+"F0.wireOp",EDGE,"E7.38.4"),sQuery(id+"F0.wireOp",EDGE,"E7.38.5"),sQuery(id+"F0.wireOp",EDGE,"E7.39.0"),sQuery(id+"F0.wireOp",EDGE,"E7.39.1"),sQuery(id+"F0.wireOp",EDGE,"E7.39.2"),sQuery(id+"F0.wireOp",EDGE,"E7.39.3"),sQuery(id+"F0.wireOp",EDGE,"E7.39.4"),sQuery(id+"F0.wireOp",EDGE,"E7.39.5"),sQuery(id+"F0.wireOp",EDGE,"E7.40.0"),sQuery(id+"F0.wireOp",EDGE,"E7.40.1"),sQuery(id+"F0.wireOp",EDGE,"E7.40.2"),sQuery(id+"F0.wireOp",EDGE,"E7.40.3"),sQuery(id+"F0.wireOp",EDGE,"E7.40.4"),sQuery(id+"F0.wireOp",EDGE,"E7.40.5"),sQuery(id+"F0.wireOp",EDGE,"E7.41.0"),sQuery(id+"F0.wireOp",EDGE,"E7.41.1"),sQuery(id+"F0.wireOp",EDGE,"E7.41.2"),sQuery(id+"F0.wireOp",EDGE,"E7.41.3"),sQuery(id+"F0.wireOp",EDGE,"E7.41.4"),sQuery(id+"F0.wireOp",EDGE,"E7.41.5"),sQuery(id+"F0.wireOp",EDGE,"E7.42.0"),sQuery(id+"F0.wireOp",EDGE,"E7.42.1"),sQuery(id+"F0.wireOp",EDGE,"E7.42.2"),sQuery(id+"F0.wireOp",EDGE,"E7.42.3"),sQuery(id+"F0.wireOp",EDGE,"E7.42.4"),sQuery(id+"F0.wireOp",EDGE,"E7.42.5"),sQuery(id+"F0.wireOp",EDGE,"E7.43.0"),sQuery(id+"F0.wireOp",EDGE,"E7.43.1"),sQuery(id+"F0.wireOp",EDGE,"E7.43.2"),sQuery(id+"F0.wireOp",EDGE,"E7.43.3"),sQuery(id+"F0.wireOp",EDGE,"E7.43.4"),sQuery(id+"F0.wireOp",EDGE,"E7.43.5")])],"isStart":true})]});}
            var Q41;
            {var subQ0=sQuery(id+"F0.wireOp",EDGE,"E7.40.0");Q41=makeQuery(id+"F2.opChamfer","BLEND_EDGE",EDGE,{"blendedFrom":[makeQuery(id+"F1.opExtrude","CAP_EDGE",EDGE,{"disambiguationData":[OSD([subQ0])],"isStart":true}),makeQuery(id+"F1.opExtrude","CAP_FACE",FACE,{"disambiguationData":[OSD([sQuery(id+"F0.wireOp",EDGE,"E1"),sQuery(id+"F0.wireOp",EDGE,"E2"),sQuery(id+"F0.wireOp",EDGE,"E3"),sQuery(id+"F0.wireOp",EDGE,"E4"),sQuery(id+"F0.wireOp",EDGE,"E5"),sQuery(id+"F0.wireOp",EDGE,"E6"),sQuery(id+"F0.wireOp",EDGE,"E7.1.0"),sQuery(id+"F0.wireOp",EDGE,"E7.1.1"),sQuery(id+"F0.wireOp",EDGE,"E7.1.2"),sQuery(id+"F0.wireOp",EDGE,"E7.1.3"),sQuery(id+"F0.wireOp",EDGE,"E7.1.4"),sQuery(id+"F0.wireOp",EDGE,"E7.1.5"),sQuery(id+"F0.wireOp",EDGE,"E7.2.0"),sQuery(id+"F0.wireOp",EDGE,"E7.2.1"),sQuery(id+"F0.wireOp",EDGE,"E7.2.2"),sQuery(id+"F0.wireOp",EDGE,"E7.2.3"),sQuery(id+"F0.wireOp",EDGE,"E7.2.4"),sQuery(id+"F0.wireOp",EDGE,"E7.2.5"),sQuery(id+"F0.wireOp",EDGE,"E7.3.0"),sQuery(id+"F0.wireOp",EDGE,"E7.3.1"),sQuery(id+"F0.wireOp",EDGE,"E7.3.2"),sQuery(id+"F0.wireOp",EDGE,"E7.3.3"),sQuery(id+"F0.wireOp",EDGE,"E7.3.4"),sQuery(id+"F0.wireOp",EDGE,"E7.3.5"),sQuery(id+"F0.wireOp",EDGE,"E7.4.0"),sQuery(id+"F0.wireOp",EDGE,"E7.4.1"),sQuery(id+"F0.wireOp",EDGE,"E7.4.2"),sQuery(id+"F0.wireOp",EDGE,"E7.4.3"),sQuery(id+"F0.wireOp",EDGE,"E7.4.4"),sQuery(id+"F0.wireOp",EDGE,"E7.4.5"),sQuery(id+"F0.wireOp",EDGE,"E7.5.0"),sQuery(id+"F0.wireOp",EDGE,"E7.5.1"),sQuery(id+"F0.wireOp",EDGE,"E7.5.2"),sQuery(id+"F0.wireOp",EDGE,"E7.5.3"),sQuery(id+"F0.wireOp",EDGE,"E7.5.4"),sQuery(id+"F0.wireOp",EDGE,"E7.5.5"),sQuery(id+"F0.wireOp",EDGE,"E7.6.0"),sQuery(id+"F0.wireOp",EDGE,"E7.6.1"),sQuery(id+"F0.wireOp",EDGE,"E7.6.2"),sQuery(id+"F0.wireOp",EDGE,"E7.6.3"),sQuery(id+"F0.wireOp",EDGE,"E7.6.4"),sQuery(id+"F0.wireOp",EDGE,"E7.6.5"),sQuery(id+"F0.wireOp",EDGE,"E7.7.0"),sQuery(id+"F0.wireOp",EDGE,"E7.7.1"),sQuery(id+"F0.wireOp",EDGE,"E7.7.2"),sQuery(id+"F0.wireOp",EDGE,"E7.7.3"),sQuery(id+"F0.wireOp",EDGE,"E7.7.4"),sQuery(id+"F0.wireOp",EDGE,"E7.7.5"),sQuery(id+"F0.wireOp",EDGE,"E7.8.0"),sQuery(id+"F0.wireOp",EDGE,"E7.8.1"),sQuery(id+"F0.wireOp",EDGE,"E7.8.2"),sQuery(id+"F0.wireOp",EDGE,"E7.8.3"),sQuery(id+"F0.wireOp",EDGE,"E7.8.4"),sQuery(id+"F0.wireOp",EDGE,"E7.8.5"),sQuery(id+"F0.wireOp",EDGE,"E7.9.0"),sQuery(id+"F0.wireOp",EDGE,"E7.9.1"),sQuery(id+"F0.wireOp",EDGE,"E7.9.2"),sQuery(id+"F0.wireOp",EDGE,"E7.9.3"),sQuery(id+"F0.wireOp",EDGE,"E7.9.4"),sQuery(id+"F0.wireOp",EDGE,"E7.9.5"),sQuery(id+"F0.wireOp",EDGE,"E7.10.0"),sQuery(id+"F0.wireOp",EDGE,"E7.10.1"),sQuery(id+"F0.wireOp",EDGE,"E7.10.2"),sQuery(id+"F0.wireOp",EDGE,"E7.10.3"),sQuery(id+"F0.wireOp",EDGE,"E7.10.4"),sQuery(id+"F0.wireOp",EDGE,"E7.10.5"),sQuery(id+"F0.wireOp",EDGE,"E7.11.0"),sQuery(id+"F0.wireOp",EDGE,"E7.11.1"),sQuery(id+"F0.wireOp",EDGE,"E7.11.2"),sQuery(id+"F0.wireOp",EDGE,"E7.11.3"),sQuery(id+"F0.wireOp",EDGE,"E7.11.4"),sQuery(id+"F0.wireOp",EDGE,"E7.11.5"),sQuery(id+"F0.wireOp",EDGE,"E7.12.0"),sQuery(id+"F0.wireOp",EDGE,"E7.12.1"),sQuery(id+"F0.wireOp",EDGE,"E7.12.2"),sQuery(id+"F0.wireOp",EDGE,"E7.12.3"),sQuery(id+"F0.wireOp",EDGE,"E7.12.4"),sQuery(id+"F0.wireOp",EDGE,"E7.12.5"),sQuery(id+"F0.wireOp",EDGE,"E7.13.0"),sQuery(id+"F0.wireOp",EDGE,"E7.13.1"),sQuery(id+"F0.wireOp",EDGE,"E7.13.2"),sQuery(id+"F0.wireOp",EDGE,"E7.13.3"),sQuery(id+"F0.wireOp",EDGE,"E7.13.4"),sQuery(id+"F0.wireOp",EDGE,"E7.13.5"),sQuery(id+"F0.wireOp",EDGE,"E7.14.0"),sQuery(id+"F0.wireOp",EDGE,"E7.14.1"),sQuery(id+"F0.wireOp",EDGE,"E7.14.2"),sQuery(id+"F0.wireOp",EDGE,"E7.14.3"),sQuery(id+"F0.wireOp",EDGE,"E7.14.4"),sQuery(id+"F0.wireOp",EDGE,"E7.14.5"),sQuery(id+"F0.wireOp",EDGE,"E7.15.0"),sQuery(id+"F0.wireOp",EDGE,"E7.15.1"),sQuery(id+"F0.wireOp",EDGE,"E7.15.2"),sQuery(id+"F0.wireOp",EDGE,"E7.15.3"),sQuery(id+"F0.wireOp",EDGE,"E7.15.4"),sQuery(id+"F0.wireOp",EDGE,"E7.15.5"),sQuery(id+"F0.wireOp",EDGE,"E7.16.0"),sQuery(id+"F0.wireOp",EDGE,"E7.16.1"),sQuery(id+"F0.wireOp",EDGE,"E7.16.2"),sQuery(id+"F0.wireOp",EDGE,"E7.16.3"),sQuery(id+"F0.wireOp",EDGE,"E7.16.4"),sQuery(id+"F0.wireOp",EDGE,"E7.16.5"),sQuery(id+"F0.wireOp",EDGE,"E7.17.0"),sQuery(id+"F0.wireOp",EDGE,"E7.17.1"),sQuery(id+"F0.wireOp",EDGE,"E7.17.2"),sQuery(id+"F0.wireOp",EDGE,"E7.17.3"),sQuery(id+"F0.wireOp",EDGE,"E7.17.4"),sQuery(id+"F0.wireOp",EDGE,"E7.17.5"),sQuery(id+"F0.wireOp",EDGE,"E7.18.0"),sQuery(id+"F0.wireOp",EDGE,"E7.18.1"),sQuery(id+"F0.wireOp",EDGE,"E7.18.2"),sQuery(id+"F0.wireOp",EDGE,"E7.18.3"),sQuery(id+"F0.wireOp",EDGE,"E7.18.4"),sQuery(id+"F0.wireOp",EDGE,"E7.18.5"),sQuery(id+"F0.wireOp",EDGE,"E7.19.0"),sQuery(id+"F0.wireOp",EDGE,"E7.19.1"),sQuery(id+"F0.wireOp",EDGE,"E7.19.2"),sQuery(id+"F0.wireOp",EDGE,"E7.19.3"),sQuery(id+"F0.wireOp",EDGE,"E7.19.4"),sQuery(id+"F0.wireOp",EDGE,"E7.19.5"),sQuery(id+"F0.wireOp",EDGE,"E7.20.0"),sQuery(id+"F0.wireOp",EDGE,"E7.20.1"),sQuery(id+"F0.wireOp",EDGE,"E7.20.2"),sQuery(id+"F0.wireOp",EDGE,"E7.20.3"),sQuery(id+"F0.wireOp",EDGE,"E7.20.4"),sQuery(id+"F0.wireOp",EDGE,"E7.20.5"),sQuery(id+"F0.wireOp",EDGE,"E7.21.0"),sQuery(id+"F0.wireOp",EDGE,"E7.21.1"),sQuery(id+"F0.wireOp",EDGE,"E7.21.2"),sQuery(id+"F0.wireOp",EDGE,"E7.21.3"),sQuery(id+"F0.wireOp",EDGE,"E7.21.4"),sQuery(id+"F0.wireOp",EDGE,"E7.21.5"),sQuery(id+"F0.wireOp",EDGE,"E7.22.0"),sQuery(id+"F0.wireOp",EDGE,"E7.22.1"),sQuery(id+"F0.wireOp",EDGE,"E7.22.2"),sQuery(id+"F0.wireOp",EDGE,"E7.22.3"),sQuery(id+"F0.wireOp",EDGE,"E7.22.4"),sQuery(id+"F0.wireOp",EDGE,"E7.22.5"),sQuery(id+"F0.wireOp",EDGE,"E7.23.0"),sQuery(id+"F0.wireOp",EDGE,"E7.23.1"),sQuery(id+"F0.wireOp",EDGE,"E7.23.2"),sQuery(id+"F0.wireOp",EDGE,"E7.23.3"),sQuery(id+"F0.wireOp",EDGE,"E7.23.4"),sQuery(id+"F0.wireOp",EDGE,"E7.23.5"),sQuery(id+"F0.wireOp",EDGE,"E7.24.0"),sQuery(id+"F0.wireOp",EDGE,"E7.24.1"),sQuery(id+"F0.wireOp",EDGE,"E7.24.2"),sQuery(id+"F0.wireOp",EDGE,"E7.24.3"),sQuery(id+"F0.wireOp",EDGE,"E7.24.4"),sQuery(id+"F0.wireOp",EDGE,"E7.24.5"),sQuery(id+"F0.wireOp",EDGE,"E7.25.0"),sQuery(id+"F0.wireOp",EDGE,"E7.25.1"),sQuery(id+"F0.wireOp",EDGE,"E7.25.2"),sQuery(id+"F0.wireOp",EDGE,"E7.25.3"),sQuery(id+"F0.wireOp",EDGE,"E7.25.4"),sQuery(id+"F0.wireOp",EDGE,"E7.25.5"),sQuery(id+"F0.wireOp",EDGE,"E7.26.0"),sQuery(id+"F0.wireOp",EDGE,"E7.26.1"),sQuery(id+"F0.wireOp",EDGE,"E7.26.2"),sQuery(id+"F0.wireOp",EDGE,"E7.26.3"),sQuery(id+"F0.wireOp",EDGE,"E7.26.4"),sQuery(id+"F0.wireOp",EDGE,"E7.26.5"),sQuery(id+"F0.wireOp",EDGE,"E7.27.0"),sQuery(id+"F0.wireOp",EDGE,"E7.27.1"),sQuery(id+"F0.wireOp",EDGE,"E7.27.2"),sQuery(id+"F0.wireOp",EDGE,"E7.27.3"),sQuery(id+"F0.wireOp",EDGE,"E7.27.4"),sQuery(id+"F0.wireOp",EDGE,"E7.27.5"),sQuery(id+"F0.wireOp",EDGE,"E7.28.0"),sQuery(id+"F0.wireOp",EDGE,"E7.28.1"),sQuery(id+"F0.wireOp",EDGE,"E7.28.2"),sQuery(id+"F0.wireOp",EDGE,"E7.28.3"),sQuery(id+"F0.wireOp",EDGE,"E7.28.4"),sQuery(id+"F0.wireOp",EDGE,"E7.28.5"),sQuery(id+"F0.wireOp",EDGE,"E7.29.0"),sQuery(id+"F0.wireOp",EDGE,"E7.29.1"),sQuery(id+"F0.wireOp",EDGE,"E7.29.2"),sQuery(id+"F0.wireOp",EDGE,"E7.29.3"),sQuery(id+"F0.wireOp",EDGE,"E7.29.4"),sQuery(id+"F0.wireOp",EDGE,"E7.29.5"),sQuery(id+"F0.wireOp",EDGE,"E7.30.0"),sQuery(id+"F0.wireOp",EDGE,"E7.30.1"),sQuery(id+"F0.wireOp",EDGE,"E7.30.2"),sQuery(id+"F0.wireOp",EDGE,"E7.30.3"),sQuery(id+"F0.wireOp",EDGE,"E7.30.4"),sQuery(id+"F0.wireOp",EDGE,"E7.30.5"),sQuery(id+"F0.wireOp",EDGE,"E7.31.0"),sQuery(id+"F0.wireOp",EDGE,"E7.31.1"),sQuery(id+"F0.wireOp",EDGE,"E7.31.2"),sQuery(id+"F0.wireOp",EDGE,"E7.31.3"),sQuery(id+"F0.wireOp",EDGE,"E7.31.4"),sQuery(id+"F0.wireOp",EDGE,"E7.31.5"),sQuery(id+"F0.wireOp",EDGE,"E7.32.0"),sQuery(id+"F0.wireOp",EDGE,"E7.32.1"),sQuery(id+"F0.wireOp",EDGE,"E7.32.2"),sQuery(id+"F0.wireOp",EDGE,"E7.32.3"),sQuery(id+"F0.wireOp",EDGE,"E7.32.4"),sQuery(id+"F0.wireOp",EDGE,"E7.32.5"),sQuery(id+"F0.wireOp",EDGE,"E7.33.0"),sQuery(id+"F0.wireOp",EDGE,"E7.33.1"),sQuery(id+"F0.wireOp",EDGE,"E7.33.2"),sQuery(id+"F0.wireOp",EDGE,"E7.33.3"),sQuery(id+"F0.wireOp",EDGE,"E7.33.4"),sQuery(id+"F0.wireOp",EDGE,"E7.33.5"),sQuery(id+"F0.wireOp",EDGE,"E7.34.0"),sQuery(id+"F0.wireOp",EDGE,"E7.34.1"),sQuery(id+"F0.wireOp",EDGE,"E7.34.2"),sQuery(id+"F0.wireOp",EDGE,"E7.34.3"),sQuery(id+"F0.wireOp",EDGE,"E7.34.4"),sQuery(id+"F0.wireOp",EDGE,"E7.34.5"),sQuery(id+"F0.wireOp",EDGE,"E7.35.0"),sQuery(id+"F0.wireOp",EDGE,"E7.35.1"),sQuery(id+"F0.wireOp",EDGE,"E7.35.2"),sQuery(id+"F0.wireOp",EDGE,"E7.35.3"),sQuery(id+"F0.wireOp",EDGE,"E7.35.4"),sQuery(id+"F0.wireOp",EDGE,"E7.35.5"),sQuery(id+"F0.wireOp",EDGE,"E7.36.0"),sQuery(id+"F0.wireOp",EDGE,"E7.36.1"),sQuery(id+"F0.wireOp",EDGE,"E7.36.2"),sQuery(id+"F0.wireOp",EDGE,"E7.36.3"),sQuery(id+"F0.wireOp",EDGE,"E7.36.4"),sQuery(id+"F0.wireOp",EDGE,"E7.36.5"),sQuery(id+"F0.wireOp",EDGE,"E7.37.0"),sQuery(id+"F0.wireOp",EDGE,"E7.37.1"),sQuery(id+"F0.wireOp",EDGE,"E7.37.2"),sQuery(id+"F0.wireOp",EDGE,"E7.37.3"),sQuery(id+"F0.wireOp",EDGE,"E7.37.4"),sQuery(id+"F0.wireOp",EDGE,"E7.37.5"),sQuery(id+"F0.wireOp",EDGE,"E7.38.0"),sQuery(id+"F0.wireOp",EDGE,"E7.38.1"),sQuery(id+"F0.wireOp",EDGE,"E7.38.2"),sQuery(id+"F0.wireOp",EDGE,"E7.38.3"),sQuery(id+"F0.wireOp",EDGE,"E7.38.4"),sQuery(id+"F0.wireOp",EDGE,"E7.38.5"),sQuery(id+"F0.wireOp",EDGE,"E7.39.0"),sQuery(id+"F0.wireOp",EDGE,"E7.39.1"),sQuery(id+"F0.wireOp",EDGE,"E7.39.2"),sQuery(id+"F0.wireOp",EDGE,"E7.39.3"),sQuery(id+"F0.wireOp",EDGE,"E7.39.4"),sQuery(id+"F0.wireOp",EDGE,"E7.39.5"),subQ0,sQuery(id+"F0.wireOp",EDGE,"E7.40.1"),sQuery(id+"F0.wireOp",EDGE,"E7.40.2"),sQuery(id+"F0.wireOp",EDGE,"E7.40.3"),sQuery(id+"F0.wireOp",EDGE,"E7.40.4"),sQuery(id+"F0.wireOp",EDGE,"E7.40.5"),sQuery(id+"F0.wireOp",EDGE,"E7.41.0"),sQuery(id+"F0.wireOp",EDGE,"E7.41.1"),sQuery(id+"F0.wireOp",EDGE,"E7.41.2"),sQuery(id+"F0.wireOp",EDGE,"E7.41.3"),sQuery(id+"F0.wireOp",EDGE,"E7.41.4"),sQuery(id+"F0.wireOp",EDGE,"E7.41.5"),sQuery(id+"F0.wireOp",EDGE,"E7.42.0"),sQuery(id+"F0.wireOp",EDGE,"E7.42.1"),sQuery(id+"F0.wireOp",EDGE,"E7.42.2"),sQuery(id+"F0.wireOp",EDGE,"E7.42.3"),sQuery(id+"F0.wireOp",EDGE,"E7.42.4"),sQuery(id+"F0.wireOp",EDGE,"E7.42.5"),sQuery(id+"F0.wireOp",EDGE,"E7.43.0"),sQuery(id+"F0.wireOp",EDGE,"E7.43.1"),sQuery(id+"F0.wireOp",EDGE,"E7.43.2"),sQuery(id+"F0.wireOp",EDGE,"E7.43.3"),sQuery(id+"F0.wireOp",EDGE,"E7.43.4"),sQuery(id+"F0.wireOp",EDGE,"E7.43.5")])],"isStart":true})],"blendedInto":[makeQuery(id+"F1.opExtrude","CAP_FACE",FACE,{"disambiguationData":[OSD([sQuery(id+"F0.wireOp",EDGE,"E1"),sQuery(id+"F0.wireOp",EDGE,"E2"),sQuery(id+"F0.wireOp",EDGE,"E3"),sQuery(id+"F0.wireOp",EDGE,"E4"),sQuery(id+"F0.wireOp",EDGE,"E5"),sQuery(id+"F0.wireOp",EDGE,"E6"),sQuery(id+"F0.wireOp",EDGE,"E7.1.0"),sQuery(id+"F0.wireOp",EDGE,"E7.1.1"),sQuery(id+"F0.wireOp",EDGE,"E7.1.2"),sQuery(id+"F0.wireOp",EDGE,"E7.1.3"),sQuery(id+"F0.wireOp",EDGE,"E7.1.4"),sQuery(id+"F0.wireOp",EDGE,"E7.1.5"),sQuery(id+"F0.wireOp",EDGE,"E7.2.0"),sQuery(id+"F0.wireOp",EDGE,"E7.2.1"),sQuery(id+"F0.wireOp",EDGE,"E7.2.2"),sQuery(id+"F0.wireOp",EDGE,"E7.2.3"),sQuery(id+"F0.wireOp",EDGE,"E7.2.4"),sQuery(id+"F0.wireOp",EDGE,"E7.2.5"),sQuery(id+"F0.wireOp",EDGE,"E7.3.0"),sQuery(id+"F0.wireOp",EDGE,"E7.3.1"),sQuery(id+"F0.wireOp",EDGE,"E7.3.2"),sQuery(id+"F0.wireOp",EDGE,"E7.3.3"),sQuery(id+"F0.wireOp",EDGE,"E7.3.4"),sQuery(id+"F0.wireOp",EDGE,"E7.3.5"),sQuery(id+"F0.wireOp",EDGE,"E7.4.0"),sQuery(id+"F0.wireOp",EDGE,"E7.4.1"),sQuery(id+"F0.wireOp",EDGE,"E7.4.2"),sQuery(id+"F0.wireOp",EDGE,"E7.4.3"),sQuery(id+"F0.wireOp",EDGE,"E7.4.4"),sQuery(id+"F0.wireOp",EDGE,"E7.4.5"),sQuery(id+"F0.wireOp",EDGE,"E7.5.0"),sQuery(id+"F0.wireOp",EDGE,"E7.5.1"),sQuery(id+"F0.wireOp",EDGE,"E7.5.2"),sQuery(id+"F0.wireOp",EDGE,"E7.5.3"),sQuery(id+"F0.wireOp",EDGE,"E7.5.4"),sQuery(id+"F0.wireOp",EDGE,"E7.5.5"),sQuery(id+"F0.wireOp",EDGE,"E7.6.0"),sQuery(id+"F0.wireOp",EDGE,"E7.6.1"),sQuery(id+"F0.wireOp",EDGE,"E7.6.2"),sQuery(id+"F0.wireOp",EDGE,"E7.6.3"),sQuery(id+"F0.wireOp",EDGE,"E7.6.4"),sQuery(id+"F0.wireOp",EDGE,"E7.6.5"),sQuery(id+"F0.wireOp",EDGE,"E7.7.0"),sQuery(id+"F0.wireOp",EDGE,"E7.7.1"),sQuery(id+"F0.wireOp",EDGE,"E7.7.2"),sQuery(id+"F0.wireOp",EDGE,"E7.7.3"),sQuery(id+"F0.wireOp",EDGE,"E7.7.4"),sQuery(id+"F0.wireOp",EDGE,"E7.7.5"),sQuery(id+"F0.wireOp",EDGE,"E7.8.0"),sQuery(id+"F0.wireOp",EDGE,"E7.8.1"),sQuery(id+"F0.wireOp",EDGE,"E7.8.2"),sQuery(id+"F0.wireOp",EDGE,"E7.8.3"),sQuery(id+"F0.wireOp",EDGE,"E7.8.4"),sQuery(id+"F0.wireOp",EDGE,"E7.8.5"),sQuery(id+"F0.wireOp",EDGE,"E7.9.0"),sQuery(id+"F0.wireOp",EDGE,"E7.9.1"),sQuery(id+"F0.wireOp",EDGE,"E7.9.2"),sQuery(id+"F0.wireOp",EDGE,"E7.9.3"),sQuery(id+"F0.wireOp",EDGE,"E7.9.4"),sQuery(id+"F0.wireOp",EDGE,"E7.9.5"),sQuery(id+"F0.wireOp",EDGE,"E7.10.0"),sQuery(id+"F0.wireOp",EDGE,"E7.10.1"),sQuery(id+"F0.wireOp",EDGE,"E7.10.2"),sQuery(id+"F0.wireOp",EDGE,"E7.10.3"),sQuery(id+"F0.wireOp",EDGE,"E7.10.4"),sQuery(id+"F0.wireOp",EDGE,"E7.10.5"),sQuery(id+"F0.wireOp",EDGE,"E7.11.0"),sQuery(id+"F0.wireOp",EDGE,"E7.11.1"),sQuery(id+"F0.wireOp",EDGE,"E7.11.2"),sQuery(id+"F0.wireOp",EDGE,"E7.11.3"),sQuery(id+"F0.wireOp",EDGE,"E7.11.4"),sQuery(id+"F0.wireOp",EDGE,"E7.11.5"),sQuery(id+"F0.wireOp",EDGE,"E7.12.0"),sQuery(id+"F0.wireOp",EDGE,"E7.12.1"),sQuery(id+"F0.wireOp",EDGE,"E7.12.2"),sQuery(id+"F0.wireOp",EDGE,"E7.12.3"),sQuery(id+"F0.wireOp",EDGE,"E7.12.4"),sQuery(id+"F0.wireOp",EDGE,"E7.12.5"),sQuery(id+"F0.wireOp",EDGE,"E7.13.0"),sQuery(id+"F0.wireOp",EDGE,"E7.13.1"),sQuery(id+"F0.wireOp",EDGE,"E7.13.2"),sQuery(id+"F0.wireOp",EDGE,"E7.13.3"),sQuery(id+"F0.wireOp",EDGE,"E7.13.4"),sQuery(id+"F0.wireOp",EDGE,"E7.13.5"),sQuery(id+"F0.wireOp",EDGE,"E7.14.0"),sQuery(id+"F0.wireOp",EDGE,"E7.14.1"),sQuery(id+"F0.wireOp",EDGE,"E7.14.2"),sQuery(id+"F0.wireOp",EDGE,"E7.14.3"),sQuery(id+"F0.wireOp",EDGE,"E7.14.4"),sQuery(id+"F0.wireOp",EDGE,"E7.14.5"),sQuery(id+"F0.wireOp",EDGE,"E7.15.0"),sQuery(id+"F0.wireOp",EDGE,"E7.15.1"),sQuery(id+"F0.wireOp",EDGE,"E7.15.2"),sQuery(id+"F0.wireOp",EDGE,"E7.15.3"),sQuery(id+"F0.wireOp",EDGE,"E7.15.4"),sQuery(id+"F0.wireOp",EDGE,"E7.15.5"),sQuery(id+"F0.wireOp",EDGE,"E7.16.0"),sQuery(id+"F0.wireOp",EDGE,"E7.16.1"),sQuery(id+"F0.wireOp",EDGE,"E7.16.2"),sQuery(id+"F0.wireOp",EDGE,"E7.16.3"),sQuery(id+"F0.wireOp",EDGE,"E7.16.4"),sQuery(id+"F0.wireOp",EDGE,"E7.16.5"),sQuery(id+"F0.wireOp",EDGE,"E7.17.0"),sQuery(id+"F0.wireOp",EDGE,"E7.17.1"),sQuery(id+"F0.wireOp",EDGE,"E7.17.2"),sQuery(id+"F0.wireOp",EDGE,"E7.17.3"),sQuery(id+"F0.wireOp",EDGE,"E7.17.4"),sQuery(id+"F0.wireOp",EDGE,"E7.17.5"),sQuery(id+"F0.wireOp",EDGE,"E7.18.0"),sQuery(id+"F0.wireOp",EDGE,"E7.18.1"),sQuery(id+"F0.wireOp",EDGE,"E7.18.2"),sQuery(id+"F0.wireOp",EDGE,"E7.18.3"),sQuery(id+"F0.wireOp",EDGE,"E7.18.4"),sQuery(id+"F0.wireOp",EDGE,"E7.18.5"),sQuery(id+"F0.wireOp",EDGE,"E7.19.0"),sQuery(id+"F0.wireOp",EDGE,"E7.19.1"),sQuery(id+"F0.wireOp",EDGE,"E7.19.2"),sQuery(id+"F0.wireOp",EDGE,"E7.19.3"),sQuery(id+"F0.wireOp",EDGE,"E7.19.4"),sQuery(id+"F0.wireOp",EDGE,"E7.19.5"),sQuery(id+"F0.wireOp",EDGE,"E7.20.0"),sQuery(id+"F0.wireOp",EDGE,"E7.20.1"),sQuery(id+"F0.wireOp",EDGE,"E7.20.2"),sQuery(id+"F0.wireOp",EDGE,"E7.20.3"),sQuery(id+"F0.wireOp",EDGE,"E7.20.4"),sQuery(id+"F0.wireOp",EDGE,"E7.20.5"),sQuery(id+"F0.wireOp",EDGE,"E7.21.0"),sQuery(id+"F0.wireOp",EDGE,"E7.21.1"),sQuery(id+"F0.wireOp",EDGE,"E7.21.2"),sQuery(id+"F0.wireOp",EDGE,"E7.21.3"),sQuery(id+"F0.wireOp",EDGE,"E7.21.4"),sQuery(id+"F0.wireOp",EDGE,"E7.21.5"),sQuery(id+"F0.wireOp",EDGE,"E7.22.0"),sQuery(id+"F0.wireOp",EDGE,"E7.22.1"),sQuery(id+"F0.wireOp",EDGE,"E7.22.2"),sQuery(id+"F0.wireOp",EDGE,"E7.22.3"),sQuery(id+"F0.wireOp",EDGE,"E7.22.4"),sQuery(id+"F0.wireOp",EDGE,"E7.22.5"),sQuery(id+"F0.wireOp",EDGE,"E7.23.0"),sQuery(id+"F0.wireOp",EDGE,"E7.23.1"),sQuery(id+"F0.wireOp",EDGE,"E7.23.2"),sQuery(id+"F0.wireOp",EDGE,"E7.23.3"),sQuery(id+"F0.wireOp",EDGE,"E7.23.4"),sQuery(id+"F0.wireOp",EDGE,"E7.23.5"),sQuery(id+"F0.wireOp",EDGE,"E7.24.0"),sQuery(id+"F0.wireOp",EDGE,"E7.24.1"),sQuery(id+"F0.wireOp",EDGE,"E7.24.2"),sQuery(id+"F0.wireOp",EDGE,"E7.24.3"),sQuery(id+"F0.wireOp",EDGE,"E7.24.4"),sQuery(id+"F0.wireOp",EDGE,"E7.24.5"),sQuery(id+"F0.wireOp",EDGE,"E7.25.0"),sQuery(id+"F0.wireOp",EDGE,"E7.25.1"),sQuery(id+"F0.wireOp",EDGE,"E7.25.2"),sQuery(id+"F0.wireOp",EDGE,"E7.25.3"),sQuery(id+"F0.wireOp",EDGE,"E7.25.4"),sQuery(id+"F0.wireOp",EDGE,"E7.25.5"),sQuery(id+"F0.wireOp",EDGE,"E7.26.0"),sQuery(id+"F0.wireOp",EDGE,"E7.26.1"),sQuery(id+"F0.wireOp",EDGE,"E7.26.2"),sQuery(id+"F0.wireOp",EDGE,"E7.26.3"),sQuery(id+"F0.wireOp",EDGE,"E7.26.4"),sQuery(id+"F0.wireOp",EDGE,"E7.26.5"),sQuery(id+"F0.wireOp",EDGE,"E7.27.0"),sQuery(id+"F0.wireOp",EDGE,"E7.27.1"),sQuery(id+"F0.wireOp",EDGE,"E7.27.2"),sQuery(id+"F0.wireOp",EDGE,"E7.27.3"),sQuery(id+"F0.wireOp",EDGE,"E7.27.4"),sQuery(id+"F0.wireOp",EDGE,"E7.27.5"),sQuery(id+"F0.wireOp",EDGE,"E7.28.0"),sQuery(id+"F0.wireOp",EDGE,"E7.28.1"),sQuery(id+"F0.wireOp",EDGE,"E7.28.2"),sQuery(id+"F0.wireOp",EDGE,"E7.28.3"),sQuery(id+"F0.wireOp",EDGE,"E7.28.4"),sQuery(id+"F0.wireOp",EDGE,"E7.28.5"),sQuery(id+"F0.wireOp",EDGE,"E7.29.0"),sQuery(id+"F0.wireOp",EDGE,"E7.29.1"),sQuery(id+"F0.wireOp",EDGE,"E7.29.2"),sQuery(id+"F0.wireOp",EDGE,"E7.29.3"),sQuery(id+"F0.wireOp",EDGE,"E7.29.4"),sQuery(id+"F0.wireOp",EDGE,"E7.29.5"),sQuery(id+"F0.wireOp",EDGE,"E7.30.0"),sQuery(id+"F0.wireOp",EDGE,"E7.30.1"),sQuery(id+"F0.wireOp",EDGE,"E7.30.2"),sQuery(id+"F0.wireOp",EDGE,"E7.30.3"),sQuery(id+"F0.wireOp",EDGE,"E7.30.4"),sQuery(id+"F0.wireOp",EDGE,"E7.30.5"),sQuery(id+"F0.wireOp",EDGE,"E7.31.0"),sQuery(id+"F0.wireOp",EDGE,"E7.31.1"),sQuery(id+"F0.wireOp",EDGE,"E7.31.2"),sQuery(id+"F0.wireOp",EDGE,"E7.31.3"),sQuery(id+"F0.wireOp",EDGE,"E7.31.4"),sQuery(id+"F0.wireOp",EDGE,"E7.31.5"),sQuery(id+"F0.wireOp",EDGE,"E7.32.0"),sQuery(id+"F0.wireOp",EDGE,"E7.32.1"),sQuery(id+"F0.wireOp",EDGE,"E7.32.2"),sQuery(id+"F0.wireOp",EDGE,"E7.32.3"),sQuery(id+"F0.wireOp",EDGE,"E7.32.4"),sQuery(id+"F0.wireOp",EDGE,"E7.32.5"),sQuery(id+"F0.wireOp",EDGE,"E7.33.0"),sQuery(id+"F0.wireOp",EDGE,"E7.33.1"),sQuery(id+"F0.wireOp",EDGE,"E7.33.2"),sQuery(id+"F0.wireOp",EDGE,"E7.33.3"),sQuery(id+"F0.wireOp",EDGE,"E7.33.4"),sQuery(id+"F0.wireOp",EDGE,"E7.33.5"),sQuery(id+"F0.wireOp",EDGE,"E7.34.0"),sQuery(id+"F0.wireOp",EDGE,"E7.34.1"),sQuery(id+"F0.wireOp",EDGE,"E7.34.2"),sQuery(id+"F0.wireOp",EDGE,"E7.34.3"),sQuery(id+"F0.wireOp",EDGE,"E7.34.4"),sQuery(id+"F0.wireOp",EDGE,"E7.34.5"),sQuery(id+"F0.wireOp",EDGE,"E7.35.0"),sQuery(id+"F0.wireOp",EDGE,"E7.35.1"),sQuery(id+"F0.wireOp",EDGE,"E7.35.2"),sQuery(id+"F0.wireOp",EDGE,"E7.35.3"),sQuery(id+"F0.wireOp",EDGE,"E7.35.4"),sQuery(id+"F0.wireOp",EDGE,"E7.35.5"),sQuery(id+"F0.wireOp",EDGE,"E7.36.0"),sQuery(id+"F0.wireOp",EDGE,"E7.36.1"),sQuery(id+"F0.wireOp",EDGE,"E7.36.2"),sQuery(id+"F0.wireOp",EDGE,"E7.36.3"),sQuery(id+"F0.wireOp",EDGE,"E7.36.4"),sQuery(id+"F0.wireOp",EDGE,"E7.36.5"),sQuery(id+"F0.wireOp",EDGE,"E7.37.0"),sQuery(id+"F0.wireOp",EDGE,"E7.37.1"),sQuery(id+"F0.wireOp",EDGE,"E7.37.2"),sQuery(id+"F0.wireOp",EDGE,"E7.37.3"),sQuery(id+"F0.wireOp",EDGE,"E7.37.4"),sQuery(id+"F0.wireOp",EDGE,"E7.37.5"),sQuery(id+"F0.wireOp",EDGE,"E7.38.0"),sQuery(id+"F0.wireOp",EDGE,"E7.38.1"),sQuery(id+"F0.wireOp",EDGE,"E7.38.2"),sQuery(id+"F0.wireOp",EDGE,"E7.38.3"),sQuery(id+"F0.wireOp",EDGE,"E7.38.4"),sQuery(id+"F0.wireOp",EDGE,"E7.38.5"),sQuery(id+"F0.wireOp",EDGE,"E7.39.0"),sQuery(id+"F0.wireOp",EDGE,"E7.39.1"),sQuery(id+"F0.wireOp",EDGE,"E7.39.2"),sQuery(id+"F0.wireOp",EDGE,"E7.39.3"),sQuery(id+"F0.wireOp",EDGE,"E7.39.4"),sQuery(id+"F0.wireOp",EDGE,"E7.39.5"),subQ0,sQuery(id+"F0.wireOp",EDGE,"E7.40.1"),sQuery(id+"F0.wireOp",EDGE,"E7.40.2"),sQuery(id+"F0.wireOp",EDGE,"E7.40.3"),sQuery(id+"F0.wireOp",EDGE,"E7.40.4"),sQuery(id+"F0.wireOp",EDGE,"E7.40.5"),sQuery(id+"F0.wireOp",EDGE,"E7.41.0"),sQuery(id+"F0.wireOp",EDGE,"E7.41.1"),sQuery(id+"F0.wireOp",EDGE,"E7.41.2"),sQuery(id+"F0.wireOp",EDGE,"E7.41.3"),sQuery(id+"F0.wireOp",EDGE,"E7.41.4"),sQuery(id+"F0.wireOp",EDGE,"E7.41.5"),sQuery(id+"F0.wireOp",EDGE,"E7.42.0"),sQuery(id+"F0.wireOp",EDGE,"E7.42.1"),sQuery(id+"F0.wireOp",EDGE,"E7.42.2"),sQuery(id+"F0.wireOp",EDGE,"E7.42.3"),sQuery(id+"F0.wireOp",EDGE,"E7.42.4"),sQuery(id+"F0.wireOp",EDGE,"E7.42.5"),sQuery(id+"F0.wireOp",EDGE,"E7.43.0"),sQuery(id+"F0.wireOp",EDGE,"E7.43.1"),sQuery(id+"F0.wireOp",EDGE,"E7.43.2"),sQuery(id+"F0.wireOp",EDGE,"E7.43.3"),sQuery(id+"F0.wireOp",EDGE,"E7.43.4"),sQuery(id+"F0.wireOp",EDGE,"E7.43.5")])],"isStart":true})]});}
            var Q42;
            {var subQ0=sQuery(id+"F0.wireOp",EDGE,"E7.42.0");Q42=makeQuery(id+"F2.opChamfer","BLEND_EDGE",EDGE,{"blendedFrom":[makeQuery(id+"F1.opExtrude","CAP_EDGE",EDGE,{"disambiguationData":[OSD([subQ0])],"isStart":true}),makeQuery(id+"F1.opExtrude","CAP_FACE",FACE,{"disambiguationData":[OSD([sQuery(id+"F0.wireOp",EDGE,"E1"),sQuery(id+"F0.wireOp",EDGE,"E2"),sQuery(id+"F0.wireOp",EDGE,"E3"),sQuery(id+"F0.wireOp",EDGE,"E4"),sQuery(id+"F0.wireOp",EDGE,"E5"),sQuery(id+"F0.wireOp",EDGE,"E6"),sQuery(id+"F0.wireOp",EDGE,"E7.1.0"),sQuery(id+"F0.wireOp",EDGE,"E7.1.1"),sQuery(id+"F0.wireOp",EDGE,"E7.1.2"),sQuery(id+"F0.wireOp",EDGE,"E7.1.3"),sQuery(id+"F0.wireOp",EDGE,"E7.1.4"),sQuery(id+"F0.wireOp",EDGE,"E7.1.5"),sQuery(id+"F0.wireOp",EDGE,"E7.2.0"),sQuery(id+"F0.wireOp",EDGE,"E7.2.1"),sQuery(id+"F0.wireOp",EDGE,"E7.2.2"),sQuery(id+"F0.wireOp",EDGE,"E7.2.3"),sQuery(id+"F0.wireOp",EDGE,"E7.2.4"),sQuery(id+"F0.wireOp",EDGE,"E7.2.5"),sQuery(id+"F0.wireOp",EDGE,"E7.3.0"),sQuery(id+"F0.wireOp",EDGE,"E7.3.1"),sQuery(id+"F0.wireOp",EDGE,"E7.3.2"),sQuery(id+"F0.wireOp",EDGE,"E7.3.3"),sQuery(id+"F0.wireOp",EDGE,"E7.3.4"),sQuery(id+"F0.wireOp",EDGE,"E7.3.5"),sQuery(id+"F0.wireOp",EDGE,"E7.4.0"),sQuery(id+"F0.wireOp",EDGE,"E7.4.1"),sQuery(id+"F0.wireOp",EDGE,"E7.4.2"),sQuery(id+"F0.wireOp",EDGE,"E7.4.3"),sQuery(id+"F0.wireOp",EDGE,"E7.4.4"),sQuery(id+"F0.wireOp",EDGE,"E7.4.5"),sQuery(id+"F0.wireOp",EDGE,"E7.5.0"),sQuery(id+"F0.wireOp",EDGE,"E7.5.1"),sQuery(id+"F0.wireOp",EDGE,"E7.5.2"),sQuery(id+"F0.wireOp",EDGE,"E7.5.3"),sQuery(id+"F0.wireOp",EDGE,"E7.5.4"),sQuery(id+"F0.wireOp",EDGE,"E7.5.5"),sQuery(id+"F0.wireOp",EDGE,"E7.6.0"),sQuery(id+"F0.wireOp",EDGE,"E7.6.1"),sQuery(id+"F0.wireOp",EDGE,"E7.6.2"),sQuery(id+"F0.wireOp",EDGE,"E7.6.3"),sQuery(id+"F0.wireOp",EDGE,"E7.6.4"),sQuery(id+"F0.wireOp",EDGE,"E7.6.5"),sQuery(id+"F0.wireOp",EDGE,"E7.7.0"),sQuery(id+"F0.wireOp",EDGE,"E7.7.1"),sQuery(id+"F0.wireOp",EDGE,"E7.7.2"),sQuery(id+"F0.wireOp",EDGE,"E7.7.3"),sQuery(id+"F0.wireOp",EDGE,"E7.7.4"),sQuery(id+"F0.wireOp",EDGE,"E7.7.5"),sQuery(id+"F0.wireOp",EDGE,"E7.8.0"),sQuery(id+"F0.wireOp",EDGE,"E7.8.1"),sQuery(id+"F0.wireOp",EDGE,"E7.8.2"),sQuery(id+"F0.wireOp",EDGE,"E7.8.3"),sQuery(id+"F0.wireOp",EDGE,"E7.8.4"),sQuery(id+"F0.wireOp",EDGE,"E7.8.5"),sQuery(id+"F0.wireOp",EDGE,"E7.9.0"),sQuery(id+"F0.wireOp",EDGE,"E7.9.1"),sQuery(id+"F0.wireOp",EDGE,"E7.9.2"),sQuery(id+"F0.wireOp",EDGE,"E7.9.3"),sQuery(id+"F0.wireOp",EDGE,"E7.9.4"),sQuery(id+"F0.wireOp",EDGE,"E7.9.5"),sQuery(id+"F0.wireOp",EDGE,"E7.10.0"),sQuery(id+"F0.wireOp",EDGE,"E7.10.1"),sQuery(id+"F0.wireOp",EDGE,"E7.10.2"),sQuery(id+"F0.wireOp",EDGE,"E7.10.3"),sQuery(id+"F0.wireOp",EDGE,"E7.10.4"),sQuery(id+"F0.wireOp",EDGE,"E7.10.5"),sQuery(id+"F0.wireOp",EDGE,"E7.11.0"),sQuery(id+"F0.wireOp",EDGE,"E7.11.1"),sQuery(id+"F0.wireOp",EDGE,"E7.11.2"),sQuery(id+"F0.wireOp",EDGE,"E7.11.3"),sQuery(id+"F0.wireOp",EDGE,"E7.11.4"),sQuery(id+"F0.wireOp",EDGE,"E7.11.5"),sQuery(id+"F0.wireOp",EDGE,"E7.12.0"),sQuery(id+"F0.wireOp",EDGE,"E7.12.1"),sQuery(id+"F0.wireOp",EDGE,"E7.12.2"),sQuery(id+"F0.wireOp",EDGE,"E7.12.3"),sQuery(id+"F0.wireOp",EDGE,"E7.12.4"),sQuery(id+"F0.wireOp",EDGE,"E7.12.5"),sQuery(id+"F0.wireOp",EDGE,"E7.13.0"),sQuery(id+"F0.wireOp",EDGE,"E7.13.1"),sQuery(id+"F0.wireOp",EDGE,"E7.13.2"),sQuery(id+"F0.wireOp",EDGE,"E7.13.3"),sQuery(id+"F0.wireOp",EDGE,"E7.13.4"),sQuery(id+"F0.wireOp",EDGE,"E7.13.5"),sQuery(id+"F0.wireOp",EDGE,"E7.14.0"),sQuery(id+"F0.wireOp",EDGE,"E7.14.1"),sQuery(id+"F0.wireOp",EDGE,"E7.14.2"),sQuery(id+"F0.wireOp",EDGE,"E7.14.3"),sQuery(id+"F0.wireOp",EDGE,"E7.14.4"),sQuery(id+"F0.wireOp",EDGE,"E7.14.5"),sQuery(id+"F0.wireOp",EDGE,"E7.15.0"),sQuery(id+"F0.wireOp",EDGE,"E7.15.1"),sQuery(id+"F0.wireOp",EDGE,"E7.15.2"),sQuery(id+"F0.wireOp",EDGE,"E7.15.3"),sQuery(id+"F0.wireOp",EDGE,"E7.15.4"),sQuery(id+"F0.wireOp",EDGE,"E7.15.5"),sQuery(id+"F0.wireOp",EDGE,"E7.16.0"),sQuery(id+"F0.wireOp",EDGE,"E7.16.1"),sQuery(id+"F0.wireOp",EDGE,"E7.16.2"),sQuery(id+"F0.wireOp",EDGE,"E7.16.3"),sQuery(id+"F0.wireOp",EDGE,"E7.16.4"),sQuery(id+"F0.wireOp",EDGE,"E7.16.5"),sQuery(id+"F0.wireOp",EDGE,"E7.17.0"),sQuery(id+"F0.wireOp",EDGE,"E7.17.1"),sQuery(id+"F0.wireOp",EDGE,"E7.17.2"),sQuery(id+"F0.wireOp",EDGE,"E7.17.3"),sQuery(id+"F0.wireOp",EDGE,"E7.17.4"),sQuery(id+"F0.wireOp",EDGE,"E7.17.5"),sQuery(id+"F0.wireOp",EDGE,"E7.18.0"),sQuery(id+"F0.wireOp",EDGE,"E7.18.1"),sQuery(id+"F0.wireOp",EDGE,"E7.18.2"),sQuery(id+"F0.wireOp",EDGE,"E7.18.3"),sQuery(id+"F0.wireOp",EDGE,"E7.18.4"),sQuery(id+"F0.wireOp",EDGE,"E7.18.5"),sQuery(id+"F0.wireOp",EDGE,"E7.19.0"),sQuery(id+"F0.wireOp",EDGE,"E7.19.1"),sQuery(id+"F0.wireOp",EDGE,"E7.19.2"),sQuery(id+"F0.wireOp",EDGE,"E7.19.3"),sQuery(id+"F0.wireOp",EDGE,"E7.19.4"),sQuery(id+"F0.wireOp",EDGE,"E7.19.5"),sQuery(id+"F0.wireOp",EDGE,"E7.20.0"),sQuery(id+"F0.wireOp",EDGE,"E7.20.1"),sQuery(id+"F0.wireOp",EDGE,"E7.20.2"),sQuery(id+"F0.wireOp",EDGE,"E7.20.3"),sQuery(id+"F0.wireOp",EDGE,"E7.20.4"),sQuery(id+"F0.wireOp",EDGE,"E7.20.5"),sQuery(id+"F0.wireOp",EDGE,"E7.21.0"),sQuery(id+"F0.wireOp",EDGE,"E7.21.1"),sQuery(id+"F0.wireOp",EDGE,"E7.21.2"),sQuery(id+"F0.wireOp",EDGE,"E7.21.3"),sQuery(id+"F0.wireOp",EDGE,"E7.21.4"),sQuery(id+"F0.wireOp",EDGE,"E7.21.5"),sQuery(id+"F0.wireOp",EDGE,"E7.22.0"),sQuery(id+"F0.wireOp",EDGE,"E7.22.1"),sQuery(id+"F0.wireOp",EDGE,"E7.22.2"),sQuery(id+"F0.wireOp",EDGE,"E7.22.3"),sQuery(id+"F0.wireOp",EDGE,"E7.22.4"),sQuery(id+"F0.wireOp",EDGE,"E7.22.5"),sQuery(id+"F0.wireOp",EDGE,"E7.23.0"),sQuery(id+"F0.wireOp",EDGE,"E7.23.1"),sQuery(id+"F0.wireOp",EDGE,"E7.23.2"),sQuery(id+"F0.wireOp",EDGE,"E7.23.3"),sQuery(id+"F0.wireOp",EDGE,"E7.23.4"),sQuery(id+"F0.wireOp",EDGE,"E7.23.5"),sQuery(id+"F0.wireOp",EDGE,"E7.24.0"),sQuery(id+"F0.wireOp",EDGE,"E7.24.1"),sQuery(id+"F0.wireOp",EDGE,"E7.24.2"),sQuery(id+"F0.wireOp",EDGE,"E7.24.3"),sQuery(id+"F0.wireOp",EDGE,"E7.24.4"),sQuery(id+"F0.wireOp",EDGE,"E7.24.5"),sQuery(id+"F0.wireOp",EDGE,"E7.25.0"),sQuery(id+"F0.wireOp",EDGE,"E7.25.1"),sQuery(id+"F0.wireOp",EDGE,"E7.25.2"),sQuery(id+"F0.wireOp",EDGE,"E7.25.3"),sQuery(id+"F0.wireOp",EDGE,"E7.25.4"),sQuery(id+"F0.wireOp",EDGE,"E7.25.5"),sQuery(id+"F0.wireOp",EDGE,"E7.26.0"),sQuery(id+"F0.wireOp",EDGE,"E7.26.1"),sQuery(id+"F0.wireOp",EDGE,"E7.26.2"),sQuery(id+"F0.wireOp",EDGE,"E7.26.3"),sQuery(id+"F0.wireOp",EDGE,"E7.26.4"),sQuery(id+"F0.wireOp",EDGE,"E7.26.5"),sQuery(id+"F0.wireOp",EDGE,"E7.27.0"),sQuery(id+"F0.wireOp",EDGE,"E7.27.1"),sQuery(id+"F0.wireOp",EDGE,"E7.27.2"),sQuery(id+"F0.wireOp",EDGE,"E7.27.3"),sQuery(id+"F0.wireOp",EDGE,"E7.27.4"),sQuery(id+"F0.wireOp",EDGE,"E7.27.5"),sQuery(id+"F0.wireOp",EDGE,"E7.28.0"),sQuery(id+"F0.wireOp",EDGE,"E7.28.1"),sQuery(id+"F0.wireOp",EDGE,"E7.28.2"),sQuery(id+"F0.wireOp",EDGE,"E7.28.3"),sQuery(id+"F0.wireOp",EDGE,"E7.28.4"),sQuery(id+"F0.wireOp",EDGE,"E7.28.5"),sQuery(id+"F0.wireOp",EDGE,"E7.29.0"),sQuery(id+"F0.wireOp",EDGE,"E7.29.1"),sQuery(id+"F0.wireOp",EDGE,"E7.29.2"),sQuery(id+"F0.wireOp",EDGE,"E7.29.3"),sQuery(id+"F0.wireOp",EDGE,"E7.29.4"),sQuery(id+"F0.wireOp",EDGE,"E7.29.5"),sQuery(id+"F0.wireOp",EDGE,"E7.30.0"),sQuery(id+"F0.wireOp",EDGE,"E7.30.1"),sQuery(id+"F0.wireOp",EDGE,"E7.30.2"),sQuery(id+"F0.wireOp",EDGE,"E7.30.3"),sQuery(id+"F0.wireOp",EDGE,"E7.30.4"),sQuery(id+"F0.wireOp",EDGE,"E7.30.5"),sQuery(id+"F0.wireOp",EDGE,"E7.31.0"),sQuery(id+"F0.wireOp",EDGE,"E7.31.1"),sQuery(id+"F0.wireOp",EDGE,"E7.31.2"),sQuery(id+"F0.wireOp",EDGE,"E7.31.3"),sQuery(id+"F0.wireOp",EDGE,"E7.31.4"),sQuery(id+"F0.wireOp",EDGE,"E7.31.5"),sQuery(id+"F0.wireOp",EDGE,"E7.32.0"),sQuery(id+"F0.wireOp",EDGE,"E7.32.1"),sQuery(id+"F0.wireOp",EDGE,"E7.32.2"),sQuery(id+"F0.wireOp",EDGE,"E7.32.3"),sQuery(id+"F0.wireOp",EDGE,"E7.32.4"),sQuery(id+"F0.wireOp",EDGE,"E7.32.5"),sQuery(id+"F0.wireOp",EDGE,"E7.33.0"),sQuery(id+"F0.wireOp",EDGE,"E7.33.1"),sQuery(id+"F0.wireOp",EDGE,"E7.33.2"),sQuery(id+"F0.wireOp",EDGE,"E7.33.3"),sQuery(id+"F0.wireOp",EDGE,"E7.33.4"),sQuery(id+"F0.wireOp",EDGE,"E7.33.5"),sQuery(id+"F0.wireOp",EDGE,"E7.34.0"),sQuery(id+"F0.wireOp",EDGE,"E7.34.1"),sQuery(id+"F0.wireOp",EDGE,"E7.34.2"),sQuery(id+"F0.wireOp",EDGE,"E7.34.3"),sQuery(id+"F0.wireOp",EDGE,"E7.34.4"),sQuery(id+"F0.wireOp",EDGE,"E7.34.5"),sQuery(id+"F0.wireOp",EDGE,"E7.35.0"),sQuery(id+"F0.wireOp",EDGE,"E7.35.1"),sQuery(id+"F0.wireOp",EDGE,"E7.35.2"),sQuery(id+"F0.wireOp",EDGE,"E7.35.3"),sQuery(id+"F0.wireOp",EDGE,"E7.35.4"),sQuery(id+"F0.wireOp",EDGE,"E7.35.5"),sQuery(id+"F0.wireOp",EDGE,"E7.36.0"),sQuery(id+"F0.wireOp",EDGE,"E7.36.1"),sQuery(id+"F0.wireOp",EDGE,"E7.36.2"),sQuery(id+"F0.wireOp",EDGE,"E7.36.3"),sQuery(id+"F0.wireOp",EDGE,"E7.36.4"),sQuery(id+"F0.wireOp",EDGE,"E7.36.5"),sQuery(id+"F0.wireOp",EDGE,"E7.37.0"),sQuery(id+"F0.wireOp",EDGE,"E7.37.1"),sQuery(id+"F0.wireOp",EDGE,"E7.37.2"),sQuery(id+"F0.wireOp",EDGE,"E7.37.3"),sQuery(id+"F0.wireOp",EDGE,"E7.37.4"),sQuery(id+"F0.wireOp",EDGE,"E7.37.5"),sQuery(id+"F0.wireOp",EDGE,"E7.38.0"),sQuery(id+"F0.wireOp",EDGE,"E7.38.1"),sQuery(id+"F0.wireOp",EDGE,"E7.38.2"),sQuery(id+"F0.wireOp",EDGE,"E7.38.3"),sQuery(id+"F0.wireOp",EDGE,"E7.38.4"),sQuery(id+"F0.wireOp",EDGE,"E7.38.5"),sQuery(id+"F0.wireOp",EDGE,"E7.39.0"),sQuery(id+"F0.wireOp",EDGE,"E7.39.1"),sQuery(id+"F0.wireOp",EDGE,"E7.39.2"),sQuery(id+"F0.wireOp",EDGE,"E7.39.3"),sQuery(id+"F0.wireOp",EDGE,"E7.39.4"),sQuery(id+"F0.wireOp",EDGE,"E7.39.5"),sQuery(id+"F0.wireOp",EDGE,"E7.40.0"),sQuery(id+"F0.wireOp",EDGE,"E7.40.1"),sQuery(id+"F0.wireOp",EDGE,"E7.40.2"),sQuery(id+"F0.wireOp",EDGE,"E7.40.3"),sQuery(id+"F0.wireOp",EDGE,"E7.40.4"),sQuery(id+"F0.wireOp",EDGE,"E7.40.5"),sQuery(id+"F0.wireOp",EDGE,"E7.41.0"),sQuery(id+"F0.wireOp",EDGE,"E7.41.1"),sQuery(id+"F0.wireOp",EDGE,"E7.41.2"),sQuery(id+"F0.wireOp",EDGE,"E7.41.3"),sQuery(id+"F0.wireOp",EDGE,"E7.41.4"),sQuery(id+"F0.wireOp",EDGE,"E7.41.5"),subQ0,sQuery(id+"F0.wireOp",EDGE,"E7.42.1"),sQuery(id+"F0.wireOp",EDGE,"E7.42.2"),sQuery(id+"F0.wireOp",EDGE,"E7.42.3"),sQuery(id+"F0.wireOp",EDGE,"E7.42.4"),sQuery(id+"F0.wireOp",EDGE,"E7.42.5"),sQuery(id+"F0.wireOp",EDGE,"E7.43.0"),sQuery(id+"F0.wireOp",EDGE,"E7.43.1"),sQuery(id+"F0.wireOp",EDGE,"E7.43.2"),sQuery(id+"F0.wireOp",EDGE,"E7.43.3"),sQuery(id+"F0.wireOp",EDGE,"E7.43.4"),sQuery(id+"F0.wireOp",EDGE,"E7.43.5")])],"isStart":true})],"blendedInto":[makeQuery(id+"F1.opExtrude","CAP_FACE",FACE,{"disambiguationData":[OSD([sQuery(id+"F0.wireOp",EDGE,"E1"),sQuery(id+"F0.wireOp",EDGE,"E2"),sQuery(id+"F0.wireOp",EDGE,"E3"),sQuery(id+"F0.wireOp",EDGE,"E4"),sQuery(id+"F0.wireOp",EDGE,"E5"),sQuery(id+"F0.wireOp",EDGE,"E6"),sQuery(id+"F0.wireOp",EDGE,"E7.1.0"),sQuery(id+"F0.wireOp",EDGE,"E7.1.1"),sQuery(id+"F0.wireOp",EDGE,"E7.1.2"),sQuery(id+"F0.wireOp",EDGE,"E7.1.3"),sQuery(id+"F0.wireOp",EDGE,"E7.1.4"),sQuery(id+"F0.wireOp",EDGE,"E7.1.5"),sQuery(id+"F0.wireOp",EDGE,"E7.2.0"),sQuery(id+"F0.wireOp",EDGE,"E7.2.1"),sQuery(id+"F0.wireOp",EDGE,"E7.2.2"),sQuery(id+"F0.wireOp",EDGE,"E7.2.3"),sQuery(id+"F0.wireOp",EDGE,"E7.2.4"),sQuery(id+"F0.wireOp",EDGE,"E7.2.5"),sQuery(id+"F0.wireOp",EDGE,"E7.3.0"),sQuery(id+"F0.wireOp",EDGE,"E7.3.1"),sQuery(id+"F0.wireOp",EDGE,"E7.3.2"),sQuery(id+"F0.wireOp",EDGE,"E7.3.3"),sQuery(id+"F0.wireOp",EDGE,"E7.3.4"),sQuery(id+"F0.wireOp",EDGE,"E7.3.5"),sQuery(id+"F0.wireOp",EDGE,"E7.4.0"),sQuery(id+"F0.wireOp",EDGE,"E7.4.1"),sQuery(id+"F0.wireOp",EDGE,"E7.4.2"),sQuery(id+"F0.wireOp",EDGE,"E7.4.3"),sQuery(id+"F0.wireOp",EDGE,"E7.4.4"),sQuery(id+"F0.wireOp",EDGE,"E7.4.5"),sQuery(id+"F0.wireOp",EDGE,"E7.5.0"),sQuery(id+"F0.wireOp",EDGE,"E7.5.1"),sQuery(id+"F0.wireOp",EDGE,"E7.5.2"),sQuery(id+"F0.wireOp",EDGE,"E7.5.3"),sQuery(id+"F0.wireOp",EDGE,"E7.5.4"),sQuery(id+"F0.wireOp",EDGE,"E7.5.5"),sQuery(id+"F0.wireOp",EDGE,"E7.6.0"),sQuery(id+"F0.wireOp",EDGE,"E7.6.1"),sQuery(id+"F0.wireOp",EDGE,"E7.6.2"),sQuery(id+"F0.wireOp",EDGE,"E7.6.3"),sQuery(id+"F0.wireOp",EDGE,"E7.6.4"),sQuery(id+"F0.wireOp",EDGE,"E7.6.5"),sQuery(id+"F0.wireOp",EDGE,"E7.7.0"),sQuery(id+"F0.wireOp",EDGE,"E7.7.1"),sQuery(id+"F0.wireOp",EDGE,"E7.7.2"),sQuery(id+"F0.wireOp",EDGE,"E7.7.3"),sQuery(id+"F0.wireOp",EDGE,"E7.7.4"),sQuery(id+"F0.wireOp",EDGE,"E7.7.5"),sQuery(id+"F0.wireOp",EDGE,"E7.8.0"),sQuery(id+"F0.wireOp",EDGE,"E7.8.1"),sQuery(id+"F0.wireOp",EDGE,"E7.8.2"),sQuery(id+"F0.wireOp",EDGE,"E7.8.3"),sQuery(id+"F0.wireOp",EDGE,"E7.8.4"),sQuery(id+"F0.wireOp",EDGE,"E7.8.5"),sQuery(id+"F0.wireOp",EDGE,"E7.9.0"),sQuery(id+"F0.wireOp",EDGE,"E7.9.1"),sQuery(id+"F0.wireOp",EDGE,"E7.9.2"),sQuery(id+"F0.wireOp",EDGE,"E7.9.3"),sQuery(id+"F0.wireOp",EDGE,"E7.9.4"),sQuery(id+"F0.wireOp",EDGE,"E7.9.5"),sQuery(id+"F0.wireOp",EDGE,"E7.10.0"),sQuery(id+"F0.wireOp",EDGE,"E7.10.1"),sQuery(id+"F0.wireOp",EDGE,"E7.10.2"),sQuery(id+"F0.wireOp",EDGE,"E7.10.3"),sQuery(id+"F0.wireOp",EDGE,"E7.10.4"),sQuery(id+"F0.wireOp",EDGE,"E7.10.5"),sQuery(id+"F0.wireOp",EDGE,"E7.11.0"),sQuery(id+"F0.wireOp",EDGE,"E7.11.1"),sQuery(id+"F0.wireOp",EDGE,"E7.11.2"),sQuery(id+"F0.wireOp",EDGE,"E7.11.3"),sQuery(id+"F0.wireOp",EDGE,"E7.11.4"),sQuery(id+"F0.wireOp",EDGE,"E7.11.5"),sQuery(id+"F0.wireOp",EDGE,"E7.12.0"),sQuery(id+"F0.wireOp",EDGE,"E7.12.1"),sQuery(id+"F0.wireOp",EDGE,"E7.12.2"),sQuery(id+"F0.wireOp",EDGE,"E7.12.3"),sQuery(id+"F0.wireOp",EDGE,"E7.12.4"),sQuery(id+"F0.wireOp",EDGE,"E7.12.5"),sQuery(id+"F0.wireOp",EDGE,"E7.13.0"),sQuery(id+"F0.wireOp",EDGE,"E7.13.1"),sQuery(id+"F0.wireOp",EDGE,"E7.13.2"),sQuery(id+"F0.wireOp",EDGE,"E7.13.3"),sQuery(id+"F0.wireOp",EDGE,"E7.13.4"),sQuery(id+"F0.wireOp",EDGE,"E7.13.5"),sQuery(id+"F0.wireOp",EDGE,"E7.14.0"),sQuery(id+"F0.wireOp",EDGE,"E7.14.1"),sQuery(id+"F0.wireOp",EDGE,"E7.14.2"),sQuery(id+"F0.wireOp",EDGE,"E7.14.3"),sQuery(id+"F0.wireOp",EDGE,"E7.14.4"),sQuery(id+"F0.wireOp",EDGE,"E7.14.5"),sQuery(id+"F0.wireOp",EDGE,"E7.15.0"),sQuery(id+"F0.wireOp",EDGE,"E7.15.1"),sQuery(id+"F0.wireOp",EDGE,"E7.15.2"),sQuery(id+"F0.wireOp",EDGE,"E7.15.3"),sQuery(id+"F0.wireOp",EDGE,"E7.15.4"),sQuery(id+"F0.wireOp",EDGE,"E7.15.5"),sQuery(id+"F0.wireOp",EDGE,"E7.16.0"),sQuery(id+"F0.wireOp",EDGE,"E7.16.1"),sQuery(id+"F0.wireOp",EDGE,"E7.16.2"),sQuery(id+"F0.wireOp",EDGE,"E7.16.3"),sQuery(id+"F0.wireOp",EDGE,"E7.16.4"),sQuery(id+"F0.wireOp",EDGE,"E7.16.5"),sQuery(id+"F0.wireOp",EDGE,"E7.17.0"),sQuery(id+"F0.wireOp",EDGE,"E7.17.1"),sQuery(id+"F0.wireOp",EDGE,"E7.17.2"),sQuery(id+"F0.wireOp",EDGE,"E7.17.3"),sQuery(id+"F0.wireOp",EDGE,"E7.17.4"),sQuery(id+"F0.wireOp",EDGE,"E7.17.5"),sQuery(id+"F0.wireOp",EDGE,"E7.18.0"),sQuery(id+"F0.wireOp",EDGE,"E7.18.1"),sQuery(id+"F0.wireOp",EDGE,"E7.18.2"),sQuery(id+"F0.wireOp",EDGE,"E7.18.3"),sQuery(id+"F0.wireOp",EDGE,"E7.18.4"),sQuery(id+"F0.wireOp",EDGE,"E7.18.5"),sQuery(id+"F0.wireOp",EDGE,"E7.19.0"),sQuery(id+"F0.wireOp",EDGE,"E7.19.1"),sQuery(id+"F0.wireOp",EDGE,"E7.19.2"),sQuery(id+"F0.wireOp",EDGE,"E7.19.3"),sQuery(id+"F0.wireOp",EDGE,"E7.19.4"),sQuery(id+"F0.wireOp",EDGE,"E7.19.5"),sQuery(id+"F0.wireOp",EDGE,"E7.20.0"),sQuery(id+"F0.wireOp",EDGE,"E7.20.1"),sQuery(id+"F0.wireOp",EDGE,"E7.20.2"),sQuery(id+"F0.wireOp",EDGE,"E7.20.3"),sQuery(id+"F0.wireOp",EDGE,"E7.20.4"),sQuery(id+"F0.wireOp",EDGE,"E7.20.5"),sQuery(id+"F0.wireOp",EDGE,"E7.21.0"),sQuery(id+"F0.wireOp",EDGE,"E7.21.1"),sQuery(id+"F0.wireOp",EDGE,"E7.21.2"),sQuery(id+"F0.wireOp",EDGE,"E7.21.3"),sQuery(id+"F0.wireOp",EDGE,"E7.21.4"),sQuery(id+"F0.wireOp",EDGE,"E7.21.5"),sQuery(id+"F0.wireOp",EDGE,"E7.22.0"),sQuery(id+"F0.wireOp",EDGE,"E7.22.1"),sQuery(id+"F0.wireOp",EDGE,"E7.22.2"),sQuery(id+"F0.wireOp",EDGE,"E7.22.3"),sQuery(id+"F0.wireOp",EDGE,"E7.22.4"),sQuery(id+"F0.wireOp",EDGE,"E7.22.5"),sQuery(id+"F0.wireOp",EDGE,"E7.23.0"),sQuery(id+"F0.wireOp",EDGE,"E7.23.1"),sQuery(id+"F0.wireOp",EDGE,"E7.23.2"),sQuery(id+"F0.wireOp",EDGE,"E7.23.3"),sQuery(id+"F0.wireOp",EDGE,"E7.23.4"),sQuery(id+"F0.wireOp",EDGE,"E7.23.5"),sQuery(id+"F0.wireOp",EDGE,"E7.24.0"),sQuery(id+"F0.wireOp",EDGE,"E7.24.1"),sQuery(id+"F0.wireOp",EDGE,"E7.24.2"),sQuery(id+"F0.wireOp",EDGE,"E7.24.3"),sQuery(id+"F0.wireOp",EDGE,"E7.24.4"),sQuery(id+"F0.wireOp",EDGE,"E7.24.5"),sQuery(id+"F0.wireOp",EDGE,"E7.25.0"),sQuery(id+"F0.wireOp",EDGE,"E7.25.1"),sQuery(id+"F0.wireOp",EDGE,"E7.25.2"),sQuery(id+"F0.wireOp",EDGE,"E7.25.3"),sQuery(id+"F0.wireOp",EDGE,"E7.25.4"),sQuery(id+"F0.wireOp",EDGE,"E7.25.5"),sQuery(id+"F0.wireOp",EDGE,"E7.26.0"),sQuery(id+"F0.wireOp",EDGE,"E7.26.1"),sQuery(id+"F0.wireOp",EDGE,"E7.26.2"),sQuery(id+"F0.wireOp",EDGE,"E7.26.3"),sQuery(id+"F0.wireOp",EDGE,"E7.26.4"),sQuery(id+"F0.wireOp",EDGE,"E7.26.5"),sQuery(id+"F0.wireOp",EDGE,"E7.27.0"),sQuery(id+"F0.wireOp",EDGE,"E7.27.1"),sQuery(id+"F0.wireOp",EDGE,"E7.27.2"),sQuery(id+"F0.wireOp",EDGE,"E7.27.3"),sQuery(id+"F0.wireOp",EDGE,"E7.27.4"),sQuery(id+"F0.wireOp",EDGE,"E7.27.5"),sQuery(id+"F0.wireOp",EDGE,"E7.28.0"),sQuery(id+"F0.wireOp",EDGE,"E7.28.1"),sQuery(id+"F0.wireOp",EDGE,"E7.28.2"),sQuery(id+"F0.wireOp",EDGE,"E7.28.3"),sQuery(id+"F0.wireOp",EDGE,"E7.28.4"),sQuery(id+"F0.wireOp",EDGE,"E7.28.5"),sQuery(id+"F0.wireOp",EDGE,"E7.29.0"),sQuery(id+"F0.wireOp",EDGE,"E7.29.1"),sQuery(id+"F0.wireOp",EDGE,"E7.29.2"),sQuery(id+"F0.wireOp",EDGE,"E7.29.3"),sQuery(id+"F0.wireOp",EDGE,"E7.29.4"),sQuery(id+"F0.wireOp",EDGE,"E7.29.5"),sQuery(id+"F0.wireOp",EDGE,"E7.30.0"),sQuery(id+"F0.wireOp",EDGE,"E7.30.1"),sQuery(id+"F0.wireOp",EDGE,"E7.30.2"),sQuery(id+"F0.wireOp",EDGE,"E7.30.3"),sQuery(id+"F0.wireOp",EDGE,"E7.30.4"),sQuery(id+"F0.wireOp",EDGE,"E7.30.5"),sQuery(id+"F0.wireOp",EDGE,"E7.31.0"),sQuery(id+"F0.wireOp",EDGE,"E7.31.1"),sQuery(id+"F0.wireOp",EDGE,"E7.31.2"),sQuery(id+"F0.wireOp",EDGE,"E7.31.3"),sQuery(id+"F0.wireOp",EDGE,"E7.31.4"),sQuery(id+"F0.wireOp",EDGE,"E7.31.5"),sQuery(id+"F0.wireOp",EDGE,"E7.32.0"),sQuery(id+"F0.wireOp",EDGE,"E7.32.1"),sQuery(id+"F0.wireOp",EDGE,"E7.32.2"),sQuery(id+"F0.wireOp",EDGE,"E7.32.3"),sQuery(id+"F0.wireOp",EDGE,"E7.32.4"),sQuery(id+"F0.wireOp",EDGE,"E7.32.5"),sQuery(id+"F0.wireOp",EDGE,"E7.33.0"),sQuery(id+"F0.wireOp",EDGE,"E7.33.1"),sQuery(id+"F0.wireOp",EDGE,"E7.33.2"),sQuery(id+"F0.wireOp",EDGE,"E7.33.3"),sQuery(id+"F0.wireOp",EDGE,"E7.33.4"),sQuery(id+"F0.wireOp",EDGE,"E7.33.5"),sQuery(id+"F0.wireOp",EDGE,"E7.34.0"),sQuery(id+"F0.wireOp",EDGE,"E7.34.1"),sQuery(id+"F0.wireOp",EDGE,"E7.34.2"),sQuery(id+"F0.wireOp",EDGE,"E7.34.3"),sQuery(id+"F0.wireOp",EDGE,"E7.34.4"),sQuery(id+"F0.wireOp",EDGE,"E7.34.5"),sQuery(id+"F0.wireOp",EDGE,"E7.35.0"),sQuery(id+"F0.wireOp",EDGE,"E7.35.1"),sQuery(id+"F0.wireOp",EDGE,"E7.35.2"),sQuery(id+"F0.wireOp",EDGE,"E7.35.3"),sQuery(id+"F0.wireOp",EDGE,"E7.35.4"),sQuery(id+"F0.wireOp",EDGE,"E7.35.5"),sQuery(id+"F0.wireOp",EDGE,"E7.36.0"),sQuery(id+"F0.wireOp",EDGE,"E7.36.1"),sQuery(id+"F0.wireOp",EDGE,"E7.36.2"),sQuery(id+"F0.wireOp",EDGE,"E7.36.3"),sQuery(id+"F0.wireOp",EDGE,"E7.36.4"),sQuery(id+"F0.wireOp",EDGE,"E7.36.5"),sQuery(id+"F0.wireOp",EDGE,"E7.37.0"),sQuery(id+"F0.wireOp",EDGE,"E7.37.1"),sQuery(id+"F0.wireOp",EDGE,"E7.37.2"),sQuery(id+"F0.wireOp",EDGE,"E7.37.3"),sQuery(id+"F0.wireOp",EDGE,"E7.37.4"),sQuery(id+"F0.wireOp",EDGE,"E7.37.5"),sQuery(id+"F0.wireOp",EDGE,"E7.38.0"),sQuery(id+"F0.wireOp",EDGE,"E7.38.1"),sQuery(id+"F0.wireOp",EDGE,"E7.38.2"),sQuery(id+"F0.wireOp",EDGE,"E7.38.3"),sQuery(id+"F0.wireOp",EDGE,"E7.38.4"),sQuery(id+"F0.wireOp",EDGE,"E7.38.5"),sQuery(id+"F0.wireOp",EDGE,"E7.39.0"),sQuery(id+"F0.wireOp",EDGE,"E7.39.1"),sQuery(id+"F0.wireOp",EDGE,"E7.39.2"),sQuery(id+"F0.wireOp",EDGE,"E7.39.3"),sQuery(id+"F0.wireOp",EDGE,"E7.39.4"),sQuery(id+"F0.wireOp",EDGE,"E7.39.5"),sQuery(id+"F0.wireOp",EDGE,"E7.40.0"),sQuery(id+"F0.wireOp",EDGE,"E7.40.1"),sQuery(id+"F0.wireOp",EDGE,"E7.40.2"),sQuery(id+"F0.wireOp",EDGE,"E7.40.3"),sQuery(id+"F0.wireOp",EDGE,"E7.40.4"),sQuery(id+"F0.wireOp",EDGE,"E7.40.5"),sQuery(id+"F0.wireOp",EDGE,"E7.41.0"),sQuery(id+"F0.wireOp",EDGE,"E7.41.1"),sQuery(id+"F0.wireOp",EDGE,"E7.41.2"),sQuery(id+"F0.wireOp",EDGE,"E7.41.3"),sQuery(id+"F0.wireOp",EDGE,"E7.41.4"),sQuery(id+"F0.wireOp",EDGE,"E7.41.5"),subQ0,sQuery(id+"F0.wireOp",EDGE,"E7.42.1"),sQuery(id+"F0.wireOp",EDGE,"E7.42.2"),sQuery(id+"F0.wireOp",EDGE,"E7.42.3"),sQuery(id+"F0.wireOp",EDGE,"E7.42.4"),sQuery(id+"F0.wireOp",EDGE,"E7.42.5"),sQuery(id+"F0.wireOp",EDGE,"E7.43.0"),sQuery(id+"F0.wireOp",EDGE,"E7.43.1"),sQuery(id+"F0.wireOp",EDGE,"E7.43.2"),sQuery(id+"F0.wireOp",EDGE,"E7.43.3"),sQuery(id+"F0.wireOp",EDGE,"E7.43.4"),sQuery(id+"F0.wireOp",EDGE,"E7.43.5")])],"isStart":true})]});}
            var Q43;
            {var subQ0=sQuery(id+"F0.wireOp",EDGE,"E5");Q43=makeQuery(id+"F2.opChamfer","BLEND_EDGE",EDGE,{"blendedFrom":[makeQuery(id+"F1.opExtrude","CAP_EDGE",EDGE,{"disambiguationData":[OSD([subQ0])],"isStart":true}),makeQuery(id+"F1.opExtrude","CAP_FACE",FACE,{"disambiguationData":[OSD([sQuery(id+"F0.wireOp",EDGE,"E1"),sQuery(id+"F0.wireOp",EDGE,"E2"),sQuery(id+"F0.wireOp",EDGE,"E3"),sQuery(id+"F0.wireOp",EDGE,"E4"),subQ0,sQuery(id+"F0.wireOp",EDGE,"E6"),sQuery(id+"F0.wireOp",EDGE,"E7.1.0"),sQuery(id+"F0.wireOp",EDGE,"E7.1.1"),sQuery(id+"F0.wireOp",EDGE,"E7.1.2"),sQuery(id+"F0.wireOp",EDGE,"E7.1.3"),sQuery(id+"F0.wireOp",EDGE,"E7.1.4"),sQuery(id+"F0.wireOp",EDGE,"E7.1.5"),sQuery(id+"F0.wireOp",EDGE,"E7.2.0"),sQuery(id+"F0.wireOp",EDGE,"E7.2.1"),sQuery(id+"F0.wireOp",EDGE,"E7.2.2"),sQuery(id+"F0.wireOp",EDGE,"E7.2.3"),sQuery(id+"F0.wireOp",EDGE,"E7.2.4"),sQuery(id+"F0.wireOp",EDGE,"E7.2.5"),sQuery(id+"F0.wireOp",EDGE,"E7.3.0"),sQuery(id+"F0.wireOp",EDGE,"E7.3.1"),sQuery(id+"F0.wireOp",EDGE,"E7.3.2"),sQuery(id+"F0.wireOp",EDGE,"E7.3.3"),sQuery(id+"F0.wireOp",EDGE,"E7.3.4"),sQuery(id+"F0.wireOp",EDGE,"E7.3.5"),sQuery(id+"F0.wireOp",EDGE,"E7.4.0"),sQuery(id+"F0.wireOp",EDGE,"E7.4.1"),sQuery(id+"F0.wireOp",EDGE,"E7.4.2"),sQuery(id+"F0.wireOp",EDGE,"E7.4.3"),sQuery(id+"F0.wireOp",EDGE,"E7.4.4"),sQuery(id+"F0.wireOp",EDGE,"E7.4.5"),sQuery(id+"F0.wireOp",EDGE,"E7.5.0"),sQuery(id+"F0.wireOp",EDGE,"E7.5.1"),sQuery(id+"F0.wireOp",EDGE,"E7.5.2"),sQuery(id+"F0.wireOp",EDGE,"E7.5.3"),sQuery(id+"F0.wireOp",EDGE,"E7.5.4"),sQuery(id+"F0.wireOp",EDGE,"E7.5.5"),sQuery(id+"F0.wireOp",EDGE,"E7.6.0"),sQuery(id+"F0.wireOp",EDGE,"E7.6.1"),sQuery(id+"F0.wireOp",EDGE,"E7.6.2"),sQuery(id+"F0.wireOp",EDGE,"E7.6.3"),sQuery(id+"F0.wireOp",EDGE,"E7.6.4"),sQuery(id+"F0.wireOp",EDGE,"E7.6.5"),sQuery(id+"F0.wireOp",EDGE,"E7.7.0"),sQuery(id+"F0.wireOp",EDGE,"E7.7.1"),sQuery(id+"F0.wireOp",EDGE,"E7.7.2"),sQuery(id+"F0.wireOp",EDGE,"E7.7.3"),sQuery(id+"F0.wireOp",EDGE,"E7.7.4"),sQuery(id+"F0.wireOp",EDGE,"E7.7.5"),sQuery(id+"F0.wireOp",EDGE,"E7.8.0"),sQuery(id+"F0.wireOp",EDGE,"E7.8.1"),sQuery(id+"F0.wireOp",EDGE,"E7.8.2"),sQuery(id+"F0.wireOp",EDGE,"E7.8.3"),sQuery(id+"F0.wireOp",EDGE,"E7.8.4"),sQuery(id+"F0.wireOp",EDGE,"E7.8.5"),sQuery(id+"F0.wireOp",EDGE,"E7.9.0"),sQuery(id+"F0.wireOp",EDGE,"E7.9.1"),sQuery(id+"F0.wireOp",EDGE,"E7.9.2"),sQuery(id+"F0.wireOp",EDGE,"E7.9.3"),sQuery(id+"F0.wireOp",EDGE,"E7.9.4"),sQuery(id+"F0.wireOp",EDGE,"E7.9.5"),sQuery(id+"F0.wireOp",EDGE,"E7.10.0"),sQuery(id+"F0.wireOp",EDGE,"E7.10.1"),sQuery(id+"F0.wireOp",EDGE,"E7.10.2"),sQuery(id+"F0.wireOp",EDGE,"E7.10.3"),sQuery(id+"F0.wireOp",EDGE,"E7.10.4"),sQuery(id+"F0.wireOp",EDGE,"E7.10.5"),sQuery(id+"F0.wireOp",EDGE,"E7.11.0"),sQuery(id+"F0.wireOp",EDGE,"E7.11.1"),sQuery(id+"F0.wireOp",EDGE,"E7.11.2"),sQuery(id+"F0.wireOp",EDGE,"E7.11.3"),sQuery(id+"F0.wireOp",EDGE,"E7.11.4"),sQuery(id+"F0.wireOp",EDGE,"E7.11.5"),sQuery(id+"F0.wireOp",EDGE,"E7.12.0"),sQuery(id+"F0.wireOp",EDGE,"E7.12.1"),sQuery(id+"F0.wireOp",EDGE,"E7.12.2"),sQuery(id+"F0.wireOp",EDGE,"E7.12.3"),sQuery(id+"F0.wireOp",EDGE,"E7.12.4"),sQuery(id+"F0.wireOp",EDGE,"E7.12.5"),sQuery(id+"F0.wireOp",EDGE,"E7.13.0"),sQuery(id+"F0.wireOp",EDGE,"E7.13.1"),sQuery(id+"F0.wireOp",EDGE,"E7.13.2"),sQuery(id+"F0.wireOp",EDGE,"E7.13.3"),sQuery(id+"F0.wireOp",EDGE,"E7.13.4"),sQuery(id+"F0.wireOp",EDGE,"E7.13.5"),sQuery(id+"F0.wireOp",EDGE,"E7.14.0"),sQuery(id+"F0.wireOp",EDGE,"E7.14.1"),sQuery(id+"F0.wireOp",EDGE,"E7.14.2"),sQuery(id+"F0.wireOp",EDGE,"E7.14.3"),sQuery(id+"F0.wireOp",EDGE,"E7.14.4"),sQuery(id+"F0.wireOp",EDGE,"E7.14.5"),sQuery(id+"F0.wireOp",EDGE,"E7.15.0"),sQuery(id+"F0.wireOp",EDGE,"E7.15.1"),sQuery(id+"F0.wireOp",EDGE,"E7.15.2"),sQuery(id+"F0.wireOp",EDGE,"E7.15.3"),sQuery(id+"F0.wireOp",EDGE,"E7.15.4"),sQuery(id+"F0.wireOp",EDGE,"E7.15.5"),sQuery(id+"F0.wireOp",EDGE,"E7.16.0"),sQuery(id+"F0.wireOp",EDGE,"E7.16.1"),sQuery(id+"F0.wireOp",EDGE,"E7.16.2"),sQuery(id+"F0.wireOp",EDGE,"E7.16.3"),sQuery(id+"F0.wireOp",EDGE,"E7.16.4"),sQuery(id+"F0.wireOp",EDGE,"E7.16.5"),sQuery(id+"F0.wireOp",EDGE,"E7.17.0"),sQuery(id+"F0.wireOp",EDGE,"E7.17.1"),sQuery(id+"F0.wireOp",EDGE,"E7.17.2"),sQuery(id+"F0.wireOp",EDGE,"E7.17.3"),sQuery(id+"F0.wireOp",EDGE,"E7.17.4"),sQuery(id+"F0.wireOp",EDGE,"E7.17.5"),sQuery(id+"F0.wireOp",EDGE,"E7.18.0"),sQuery(id+"F0.wireOp",EDGE,"E7.18.1"),sQuery(id+"F0.wireOp",EDGE,"E7.18.2"),sQuery(id+"F0.wireOp",EDGE,"E7.18.3"),sQuery(id+"F0.wireOp",EDGE,"E7.18.4"),sQuery(id+"F0.wireOp",EDGE,"E7.18.5"),sQuery(id+"F0.wireOp",EDGE,"E7.19.0"),sQuery(id+"F0.wireOp",EDGE,"E7.19.1"),sQuery(id+"F0.wireOp",EDGE,"E7.19.2"),sQuery(id+"F0.wireOp",EDGE,"E7.19.3"),sQuery(id+"F0.wireOp",EDGE,"E7.19.4"),sQuery(id+"F0.wireOp",EDGE,"E7.19.5"),sQuery(id+"F0.wireOp",EDGE,"E7.20.0"),sQuery(id+"F0.wireOp",EDGE,"E7.20.1"),sQuery(id+"F0.wireOp",EDGE,"E7.20.2"),sQuery(id+"F0.wireOp",EDGE,"E7.20.3"),sQuery(id+"F0.wireOp",EDGE,"E7.20.4"),sQuery(id+"F0.wireOp",EDGE,"E7.20.5"),sQuery(id+"F0.wireOp",EDGE,"E7.21.0"),sQuery(id+"F0.wireOp",EDGE,"E7.21.1"),sQuery(id+"F0.wireOp",EDGE,"E7.21.2"),sQuery(id+"F0.wireOp",EDGE,"E7.21.3"),sQuery(id+"F0.wireOp",EDGE,"E7.21.4"),sQuery(id+"F0.wireOp",EDGE,"E7.21.5"),sQuery(id+"F0.wireOp",EDGE,"E7.22.0"),sQuery(id+"F0.wireOp",EDGE,"E7.22.1"),sQuery(id+"F0.wireOp",EDGE,"E7.22.2"),sQuery(id+"F0.wireOp",EDGE,"E7.22.3"),sQuery(id+"F0.wireOp",EDGE,"E7.22.4"),sQuery(id+"F0.wireOp",EDGE,"E7.22.5"),sQuery(id+"F0.wireOp",EDGE,"E7.23.0"),sQuery(id+"F0.wireOp",EDGE,"E7.23.1"),sQuery(id+"F0.wireOp",EDGE,"E7.23.2"),sQuery(id+"F0.wireOp",EDGE,"E7.23.3"),sQuery(id+"F0.wireOp",EDGE,"E7.23.4"),sQuery(id+"F0.wireOp",EDGE,"E7.23.5"),sQuery(id+"F0.wireOp",EDGE,"E7.24.0"),sQuery(id+"F0.wireOp",EDGE,"E7.24.1"),sQuery(id+"F0.wireOp",EDGE,"E7.24.2"),sQuery(id+"F0.wireOp",EDGE,"E7.24.3"),sQuery(id+"F0.wireOp",EDGE,"E7.24.4"),sQuery(id+"F0.wireOp",EDGE,"E7.24.5"),sQuery(id+"F0.wireOp",EDGE,"E7.25.0"),sQuery(id+"F0.wireOp",EDGE,"E7.25.1"),sQuery(id+"F0.wireOp",EDGE,"E7.25.2"),sQuery(id+"F0.wireOp",EDGE,"E7.25.3"),sQuery(id+"F0.wireOp",EDGE,"E7.25.4"),sQuery(id+"F0.wireOp",EDGE,"E7.25.5"),sQuery(id+"F0.wireOp",EDGE,"E7.26.0"),sQuery(id+"F0.wireOp",EDGE,"E7.26.1"),sQuery(id+"F0.wireOp",EDGE,"E7.26.2"),sQuery(id+"F0.wireOp",EDGE,"E7.26.3"),sQuery(id+"F0.wireOp",EDGE,"E7.26.4"),sQuery(id+"F0.wireOp",EDGE,"E7.26.5"),sQuery(id+"F0.wireOp",EDGE,"E7.27.0"),sQuery(id+"F0.wireOp",EDGE,"E7.27.1"),sQuery(id+"F0.wireOp",EDGE,"E7.27.2"),sQuery(id+"F0.wireOp",EDGE,"E7.27.3"),sQuery(id+"F0.wireOp",EDGE,"E7.27.4"),sQuery(id+"F0.wireOp",EDGE,"E7.27.5"),sQuery(id+"F0.wireOp",EDGE,"E7.28.0"),sQuery(id+"F0.wireOp",EDGE,"E7.28.1"),sQuery(id+"F0.wireOp",EDGE,"E7.28.2"),sQuery(id+"F0.wireOp",EDGE,"E7.28.3"),sQuery(id+"F0.wireOp",EDGE,"E7.28.4"),sQuery(id+"F0.wireOp",EDGE,"E7.28.5"),sQuery(id+"F0.wireOp",EDGE,"E7.29.0"),sQuery(id+"F0.wireOp",EDGE,"E7.29.1"),sQuery(id+"F0.wireOp",EDGE,"E7.29.2"),sQuery(id+"F0.wireOp",EDGE,"E7.29.3"),sQuery(id+"F0.wireOp",EDGE,"E7.29.4"),sQuery(id+"F0.wireOp",EDGE,"E7.29.5"),sQuery(id+"F0.wireOp",EDGE,"E7.30.0"),sQuery(id+"F0.wireOp",EDGE,"E7.30.1"),sQuery(id+"F0.wireOp",EDGE,"E7.30.2"),sQuery(id+"F0.wireOp",EDGE,"E7.30.3"),sQuery(id+"F0.wireOp",EDGE,"E7.30.4"),sQuery(id+"F0.wireOp",EDGE,"E7.30.5"),sQuery(id+"F0.wireOp",EDGE,"E7.31.0"),sQuery(id+"F0.wireOp",EDGE,"E7.31.1"),sQuery(id+"F0.wireOp",EDGE,"E7.31.2"),sQuery(id+"F0.wireOp",EDGE,"E7.31.3"),sQuery(id+"F0.wireOp",EDGE,"E7.31.4"),sQuery(id+"F0.wireOp",EDGE,"E7.31.5"),sQuery(id+"F0.wireOp",EDGE,"E7.32.0"),sQuery(id+"F0.wireOp",EDGE,"E7.32.1"),sQuery(id+"F0.wireOp",EDGE,"E7.32.2"),sQuery(id+"F0.wireOp",EDGE,"E7.32.3"),sQuery(id+"F0.wireOp",EDGE,"E7.32.4"),sQuery(id+"F0.wireOp",EDGE,"E7.32.5"),sQuery(id+"F0.wireOp",EDGE,"E7.33.0"),sQuery(id+"F0.wireOp",EDGE,"E7.33.1"),sQuery(id+"F0.wireOp",EDGE,"E7.33.2"),sQuery(id+"F0.wireOp",EDGE,"E7.33.3"),sQuery(id+"F0.wireOp",EDGE,"E7.33.4"),sQuery(id+"F0.wireOp",EDGE,"E7.33.5"),sQuery(id+"F0.wireOp",EDGE,"E7.34.0"),sQuery(id+"F0.wireOp",EDGE,"E7.34.1"),sQuery(id+"F0.wireOp",EDGE,"E7.34.2"),sQuery(id+"F0.wireOp",EDGE,"E7.34.3"),sQuery(id+"F0.wireOp",EDGE,"E7.34.4"),sQuery(id+"F0.wireOp",EDGE,"E7.34.5"),sQuery(id+"F0.wireOp",EDGE,"E7.35.0"),sQuery(id+"F0.wireOp",EDGE,"E7.35.1"),sQuery(id+"F0.wireOp",EDGE,"E7.35.2"),sQuery(id+"F0.wireOp",EDGE,"E7.35.3"),sQuery(id+"F0.wireOp",EDGE,"E7.35.4"),sQuery(id+"F0.wireOp",EDGE,"E7.35.5"),sQuery(id+"F0.wireOp",EDGE,"E7.36.0"),sQuery(id+"F0.wireOp",EDGE,"E7.36.1"),sQuery(id+"F0.wireOp",EDGE,"E7.36.2"),sQuery(id+"F0.wireOp",EDGE,"E7.36.3"),sQuery(id+"F0.wireOp",EDGE,"E7.36.4"),sQuery(id+"F0.wireOp",EDGE,"E7.36.5"),sQuery(id+"F0.wireOp",EDGE,"E7.37.0"),sQuery(id+"F0.wireOp",EDGE,"E7.37.1"),sQuery(id+"F0.wireOp",EDGE,"E7.37.2"),sQuery(id+"F0.wireOp",EDGE,"E7.37.3"),sQuery(id+"F0.wireOp",EDGE,"E7.37.4"),sQuery(id+"F0.wireOp",EDGE,"E7.37.5"),sQuery(id+"F0.wireOp",EDGE,"E7.38.0"),sQuery(id+"F0.wireOp",EDGE,"E7.38.1"),sQuery(id+"F0.wireOp",EDGE,"E7.38.2"),sQuery(id+"F0.wireOp",EDGE,"E7.38.3"),sQuery(id+"F0.wireOp",EDGE,"E7.38.4"),sQuery(id+"F0.wireOp",EDGE,"E7.38.5"),sQuery(id+"F0.wireOp",EDGE,"E7.39.0"),sQuery(id+"F0.wireOp",EDGE,"E7.39.1"),sQuery(id+"F0.wireOp",EDGE,"E7.39.2"),sQuery(id+"F0.wireOp",EDGE,"E7.39.3"),sQuery(id+"F0.wireOp",EDGE,"E7.39.4"),sQuery(id+"F0.wireOp",EDGE,"E7.39.5"),sQuery(id+"F0.wireOp",EDGE,"E7.40.0"),sQuery(id+"F0.wireOp",EDGE,"E7.40.1"),sQuery(id+"F0.wireOp",EDGE,"E7.40.2"),sQuery(id+"F0.wireOp",EDGE,"E7.40.3"),sQuery(id+"F0.wireOp",EDGE,"E7.40.4"),sQuery(id+"F0.wireOp",EDGE,"E7.40.5"),sQuery(id+"F0.wireOp",EDGE,"E7.41.0"),sQuery(id+"F0.wireOp",EDGE,"E7.41.1"),sQuery(id+"F0.wireOp",EDGE,"E7.41.2"),sQuery(id+"F0.wireOp",EDGE,"E7.41.3"),sQuery(id+"F0.wireOp",EDGE,"E7.41.4"),sQuery(id+"F0.wireOp",EDGE,"E7.41.5"),sQuery(id+"F0.wireOp",EDGE,"E7.42.0"),sQuery(id+"F0.wireOp",EDGE,"E7.42.1"),sQuery(id+"F0.wireOp",EDGE,"E7.42.2"),sQuery(id+"F0.wireOp",EDGE,"E7.42.3"),sQuery(id+"F0.wireOp",EDGE,"E7.42.4"),sQuery(id+"F0.wireOp",EDGE,"E7.42.5"),sQuery(id+"F0.wireOp",EDGE,"E7.43.0"),sQuery(id+"F0.wireOp",EDGE,"E7.43.1"),sQuery(id+"F0.wireOp",EDGE,"E7.43.2"),sQuery(id+"F0.wireOp",EDGE,"E7.43.3"),sQuery(id+"F0.wireOp",EDGE,"E7.43.4"),sQuery(id+"F0.wireOp",EDGE,"E7.43.5")])],"isStart":true})],"blendedInto":[makeQuery(id+"F1.opExtrude","CAP_FACE",FACE,{"disambiguationData":[OSD([sQuery(id+"F0.wireOp",EDGE,"E1"),sQuery(id+"F0.wireOp",EDGE,"E2"),sQuery(id+"F0.wireOp",EDGE,"E3"),sQuery(id+"F0.wireOp",EDGE,"E4"),subQ0,sQuery(id+"F0.wireOp",EDGE,"E6"),sQuery(id+"F0.wireOp",EDGE,"E7.1.0"),sQuery(id+"F0.wireOp",EDGE,"E7.1.1"),sQuery(id+"F0.wireOp",EDGE,"E7.1.2"),sQuery(id+"F0.wireOp",EDGE,"E7.1.3"),sQuery(id+"F0.wireOp",EDGE,"E7.1.4"),sQuery(id+"F0.wireOp",EDGE,"E7.1.5"),sQuery(id+"F0.wireOp",EDGE,"E7.2.0"),sQuery(id+"F0.wireOp",EDGE,"E7.2.1"),sQuery(id+"F0.wireOp",EDGE,"E7.2.2"),sQuery(id+"F0.wireOp",EDGE,"E7.2.3"),sQuery(id+"F0.wireOp",EDGE,"E7.2.4"),sQuery(id+"F0.wireOp",EDGE,"E7.2.5"),sQuery(id+"F0.wireOp",EDGE,"E7.3.0"),sQuery(id+"F0.wireOp",EDGE,"E7.3.1"),sQuery(id+"F0.wireOp",EDGE,"E7.3.2"),sQuery(id+"F0.wireOp",EDGE,"E7.3.3"),sQuery(id+"F0.wireOp",EDGE,"E7.3.4"),sQuery(id+"F0.wireOp",EDGE,"E7.3.5"),sQuery(id+"F0.wireOp",EDGE,"E7.4.0"),sQuery(id+"F0.wireOp",EDGE,"E7.4.1"),sQuery(id+"F0.wireOp",EDGE,"E7.4.2"),sQuery(id+"F0.wireOp",EDGE,"E7.4.3"),sQuery(id+"F0.wireOp",EDGE,"E7.4.4"),sQuery(id+"F0.wireOp",EDGE,"E7.4.5"),sQuery(id+"F0.wireOp",EDGE,"E7.5.0"),sQuery(id+"F0.wireOp",EDGE,"E7.5.1"),sQuery(id+"F0.wireOp",EDGE,"E7.5.2"),sQuery(id+"F0.wireOp",EDGE,"E7.5.3"),sQuery(id+"F0.wireOp",EDGE,"E7.5.4"),sQuery(id+"F0.wireOp",EDGE,"E7.5.5"),sQuery(id+"F0.wireOp",EDGE,"E7.6.0"),sQuery(id+"F0.wireOp",EDGE,"E7.6.1"),sQuery(id+"F0.wireOp",EDGE,"E7.6.2"),sQuery(id+"F0.wireOp",EDGE,"E7.6.3"),sQuery(id+"F0.wireOp",EDGE,"E7.6.4"),sQuery(id+"F0.wireOp",EDGE,"E7.6.5"),sQuery(id+"F0.wireOp",EDGE,"E7.7.0"),sQuery(id+"F0.wireOp",EDGE,"E7.7.1"),sQuery(id+"F0.wireOp",EDGE,"E7.7.2"),sQuery(id+"F0.wireOp",EDGE,"E7.7.3"),sQuery(id+"F0.wireOp",EDGE,"E7.7.4"),sQuery(id+"F0.wireOp",EDGE,"E7.7.5"),sQuery(id+"F0.wireOp",EDGE,"E7.8.0"),sQuery(id+"F0.wireOp",EDGE,"E7.8.1"),sQuery(id+"F0.wireOp",EDGE,"E7.8.2"),sQuery(id+"F0.wireOp",EDGE,"E7.8.3"),sQuery(id+"F0.wireOp",EDGE,"E7.8.4"),sQuery(id+"F0.wireOp",EDGE,"E7.8.5"),sQuery(id+"F0.wireOp",EDGE,"E7.9.0"),sQuery(id+"F0.wireOp",EDGE,"E7.9.1"),sQuery(id+"F0.wireOp",EDGE,"E7.9.2"),sQuery(id+"F0.wireOp",EDGE,"E7.9.3"),sQuery(id+"F0.wireOp",EDGE,"E7.9.4"),sQuery(id+"F0.wireOp",EDGE,"E7.9.5"),sQuery(id+"F0.wireOp",EDGE,"E7.10.0"),sQuery(id+"F0.wireOp",EDGE,"E7.10.1"),sQuery(id+"F0.wireOp",EDGE,"E7.10.2"),sQuery(id+"F0.wireOp",EDGE,"E7.10.3"),sQuery(id+"F0.wireOp",EDGE,"E7.10.4"),sQuery(id+"F0.wireOp",EDGE,"E7.10.5"),sQuery(id+"F0.wireOp",EDGE,"E7.11.0"),sQuery(id+"F0.wireOp",EDGE,"E7.11.1"),sQuery(id+"F0.wireOp",EDGE,"E7.11.2"),sQuery(id+"F0.wireOp",EDGE,"E7.11.3"),sQuery(id+"F0.wireOp",EDGE,"E7.11.4"),sQuery(id+"F0.wireOp",EDGE,"E7.11.5"),sQuery(id+"F0.wireOp",EDGE,"E7.12.0"),sQuery(id+"F0.wireOp",EDGE,"E7.12.1"),sQuery(id+"F0.wireOp",EDGE,"E7.12.2"),sQuery(id+"F0.wireOp",EDGE,"E7.12.3"),sQuery(id+"F0.wireOp",EDGE,"E7.12.4"),sQuery(id+"F0.wireOp",EDGE,"E7.12.5"),sQuery(id+"F0.wireOp",EDGE,"E7.13.0"),sQuery(id+"F0.wireOp",EDGE,"E7.13.1"),sQuery(id+"F0.wireOp",EDGE,"E7.13.2"),sQuery(id+"F0.wireOp",EDGE,"E7.13.3"),sQuery(id+"F0.wireOp",EDGE,"E7.13.4"),sQuery(id+"F0.wireOp",EDGE,"E7.13.5"),sQuery(id+"F0.wireOp",EDGE,"E7.14.0"),sQuery(id+"F0.wireOp",EDGE,"E7.14.1"),sQuery(id+"F0.wireOp",EDGE,"E7.14.2"),sQuery(id+"F0.wireOp",EDGE,"E7.14.3"),sQuery(id+"F0.wireOp",EDGE,"E7.14.4"),sQuery(id+"F0.wireOp",EDGE,"E7.14.5"),sQuery(id+"F0.wireOp",EDGE,"E7.15.0"),sQuery(id+"F0.wireOp",EDGE,"E7.15.1"),sQuery(id+"F0.wireOp",EDGE,"E7.15.2"),sQuery(id+"F0.wireOp",EDGE,"E7.15.3"),sQuery(id+"F0.wireOp",EDGE,"E7.15.4"),sQuery(id+"F0.wireOp",EDGE,"E7.15.5"),sQuery(id+"F0.wireOp",EDGE,"E7.16.0"),sQuery(id+"F0.wireOp",EDGE,"E7.16.1"),sQuery(id+"F0.wireOp",EDGE,"E7.16.2"),sQuery(id+"F0.wireOp",EDGE,"E7.16.3"),sQuery(id+"F0.wireOp",EDGE,"E7.16.4"),sQuery(id+"F0.wireOp",EDGE,"E7.16.5"),sQuery(id+"F0.wireOp",EDGE,"E7.17.0"),sQuery(id+"F0.wireOp",EDGE,"E7.17.1"),sQuery(id+"F0.wireOp",EDGE,"E7.17.2"),sQuery(id+"F0.wireOp",EDGE,"E7.17.3"),sQuery(id+"F0.wireOp",EDGE,"E7.17.4"),sQuery(id+"F0.wireOp",EDGE,"E7.17.5"),sQuery(id+"F0.wireOp",EDGE,"E7.18.0"),sQuery(id+"F0.wireOp",EDGE,"E7.18.1"),sQuery(id+"F0.wireOp",EDGE,"E7.18.2"),sQuery(id+"F0.wireOp",EDGE,"E7.18.3"),sQuery(id+"F0.wireOp",EDGE,"E7.18.4"),sQuery(id+"F0.wireOp",EDGE,"E7.18.5"),sQuery(id+"F0.wireOp",EDGE,"E7.19.0"),sQuery(id+"F0.wireOp",EDGE,"E7.19.1"),sQuery(id+"F0.wireOp",EDGE,"E7.19.2"),sQuery(id+"F0.wireOp",EDGE,"E7.19.3"),sQuery(id+"F0.wireOp",EDGE,"E7.19.4"),sQuery(id+"F0.wireOp",EDGE,"E7.19.5"),sQuery(id+"F0.wireOp",EDGE,"E7.20.0"),sQuery(id+"F0.wireOp",EDGE,"E7.20.1"),sQuery(id+"F0.wireOp",EDGE,"E7.20.2"),sQuery(id+"F0.wireOp",EDGE,"E7.20.3"),sQuery(id+"F0.wireOp",EDGE,"E7.20.4"),sQuery(id+"F0.wireOp",EDGE,"E7.20.5"),sQuery(id+"F0.wireOp",EDGE,"E7.21.0"),sQuery(id+"F0.wireOp",EDGE,"E7.21.1"),sQuery(id+"F0.wireOp",EDGE,"E7.21.2"),sQuery(id+"F0.wireOp",EDGE,"E7.21.3"),sQuery(id+"F0.wireOp",EDGE,"E7.21.4"),sQuery(id+"F0.wireOp",EDGE,"E7.21.5"),sQuery(id+"F0.wireOp",EDGE,"E7.22.0"),sQuery(id+"F0.wireOp",EDGE,"E7.22.1"),sQuery(id+"F0.wireOp",EDGE,"E7.22.2"),sQuery(id+"F0.wireOp",EDGE,"E7.22.3"),sQuery(id+"F0.wireOp",EDGE,"E7.22.4"),sQuery(id+"F0.wireOp",EDGE,"E7.22.5"),sQuery(id+"F0.wireOp",EDGE,"E7.23.0"),sQuery(id+"F0.wireOp",EDGE,"E7.23.1"),sQuery(id+"F0.wireOp",EDGE,"E7.23.2"),sQuery(id+"F0.wireOp",EDGE,"E7.23.3"),sQuery(id+"F0.wireOp",EDGE,"E7.23.4"),sQuery(id+"F0.wireOp",EDGE,"E7.23.5"),sQuery(id+"F0.wireOp",EDGE,"E7.24.0"),sQuery(id+"F0.wireOp",EDGE,"E7.24.1"),sQuery(id+"F0.wireOp",EDGE,"E7.24.2"),sQuery(id+"F0.wireOp",EDGE,"E7.24.3"),sQuery(id+"F0.wireOp",EDGE,"E7.24.4"),sQuery(id+"F0.wireOp",EDGE,"E7.24.5"),sQuery(id+"F0.wireOp",EDGE,"E7.25.0"),sQuery(id+"F0.wireOp",EDGE,"E7.25.1"),sQuery(id+"F0.wireOp",EDGE,"E7.25.2"),sQuery(id+"F0.wireOp",EDGE,"E7.25.3"),sQuery(id+"F0.wireOp",EDGE,"E7.25.4"),sQuery(id+"F0.wireOp",EDGE,"E7.25.5"),sQuery(id+"F0.wireOp",EDGE,"E7.26.0"),sQuery(id+"F0.wireOp",EDGE,"E7.26.1"),sQuery(id+"F0.wireOp",EDGE,"E7.26.2"),sQuery(id+"F0.wireOp",EDGE,"E7.26.3"),sQuery(id+"F0.wireOp",EDGE,"E7.26.4"),sQuery(id+"F0.wireOp",EDGE,"E7.26.5"),sQuery(id+"F0.wireOp",EDGE,"E7.27.0"),sQuery(id+"F0.wireOp",EDGE,"E7.27.1"),sQuery(id+"F0.wireOp",EDGE,"E7.27.2"),sQuery(id+"F0.wireOp",EDGE,"E7.27.3"),sQuery(id+"F0.wireOp",EDGE,"E7.27.4"),sQuery(id+"F0.wireOp",EDGE,"E7.27.5"),sQuery(id+"F0.wireOp",EDGE,"E7.28.0"),sQuery(id+"F0.wireOp",EDGE,"E7.28.1"),sQuery(id+"F0.wireOp",EDGE,"E7.28.2"),sQuery(id+"F0.wireOp",EDGE,"E7.28.3"),sQuery(id+"F0.wireOp",EDGE,"E7.28.4"),sQuery(id+"F0.wireOp",EDGE,"E7.28.5"),sQuery(id+"F0.wireOp",EDGE,"E7.29.0"),sQuery(id+"F0.wireOp",EDGE,"E7.29.1"),sQuery(id+"F0.wireOp",EDGE,"E7.29.2"),sQuery(id+"F0.wireOp",EDGE,"E7.29.3"),sQuery(id+"F0.wireOp",EDGE,"E7.29.4"),sQuery(id+"F0.wireOp",EDGE,"E7.29.5"),sQuery(id+"F0.wireOp",EDGE,"E7.30.0"),sQuery(id+"F0.wireOp",EDGE,"E7.30.1"),sQuery(id+"F0.wireOp",EDGE,"E7.30.2"),sQuery(id+"F0.wireOp",EDGE,"E7.30.3"),sQuery(id+"F0.wireOp",EDGE,"E7.30.4"),sQuery(id+"F0.wireOp",EDGE,"E7.30.5"),sQuery(id+"F0.wireOp",EDGE,"E7.31.0"),sQuery(id+"F0.wireOp",EDGE,"E7.31.1"),sQuery(id+"F0.wireOp",EDGE,"E7.31.2"),sQuery(id+"F0.wireOp",EDGE,"E7.31.3"),sQuery(id+"F0.wireOp",EDGE,"E7.31.4"),sQuery(id+"F0.wireOp",EDGE,"E7.31.5"),sQuery(id+"F0.wireOp",EDGE,"E7.32.0"),sQuery(id+"F0.wireOp",EDGE,"E7.32.1"),sQuery(id+"F0.wireOp",EDGE,"E7.32.2"),sQuery(id+"F0.wireOp",EDGE,"E7.32.3"),sQuery(id+"F0.wireOp",EDGE,"E7.32.4"),sQuery(id+"F0.wireOp",EDGE,"E7.32.5"),sQuery(id+"F0.wireOp",EDGE,"E7.33.0"),sQuery(id+"F0.wireOp",EDGE,"E7.33.1"),sQuery(id+"F0.wireOp",EDGE,"E7.33.2"),sQuery(id+"F0.wireOp",EDGE,"E7.33.3"),sQuery(id+"F0.wireOp",EDGE,"E7.33.4"),sQuery(id+"F0.wireOp",EDGE,"E7.33.5"),sQuery(id+"F0.wireOp",EDGE,"E7.34.0"),sQuery(id+"F0.wireOp",EDGE,"E7.34.1"),sQuery(id+"F0.wireOp",EDGE,"E7.34.2"),sQuery(id+"F0.wireOp",EDGE,"E7.34.3"),sQuery(id+"F0.wireOp",EDGE,"E7.34.4"),sQuery(id+"F0.wireOp",EDGE,"E7.34.5"),sQuery(id+"F0.wireOp",EDGE,"E7.35.0"),sQuery(id+"F0.wireOp",EDGE,"E7.35.1"),sQuery(id+"F0.wireOp",EDGE,"E7.35.2"),sQuery(id+"F0.wireOp",EDGE,"E7.35.3"),sQuery(id+"F0.wireOp",EDGE,"E7.35.4"),sQuery(id+"F0.wireOp",EDGE,"E7.35.5"),sQuery(id+"F0.wireOp",EDGE,"E7.36.0"),sQuery(id+"F0.wireOp",EDGE,"E7.36.1"),sQuery(id+"F0.wireOp",EDGE,"E7.36.2"),sQuery(id+"F0.wireOp",EDGE,"E7.36.3"),sQuery(id+"F0.wireOp",EDGE,"E7.36.4"),sQuery(id+"F0.wireOp",EDGE,"E7.36.5"),sQuery(id+"F0.wireOp",EDGE,"E7.37.0"),sQuery(id+"F0.wireOp",EDGE,"E7.37.1"),sQuery(id+"F0.wireOp",EDGE,"E7.37.2"),sQuery(id+"F0.wireOp",EDGE,"E7.37.3"),sQuery(id+"F0.wireOp",EDGE,"E7.37.4"),sQuery(id+"F0.wireOp",EDGE,"E7.37.5"),sQuery(id+"F0.wireOp",EDGE,"E7.38.0"),sQuery(id+"F0.wireOp",EDGE,"E7.38.1"),sQuery(id+"F0.wireOp",EDGE,"E7.38.2"),sQuery(id+"F0.wireOp",EDGE,"E7.38.3"),sQuery(id+"F0.wireOp",EDGE,"E7.38.4"),sQuery(id+"F0.wireOp",EDGE,"E7.38.5"),sQuery(id+"F0.wireOp",EDGE,"E7.39.0"),sQuery(id+"F0.wireOp",EDGE,"E7.39.1"),sQuery(id+"F0.wireOp",EDGE,"E7.39.2"),sQuery(id+"F0.wireOp",EDGE,"E7.39.3"),sQuery(id+"F0.wireOp",EDGE,"E7.39.4"),sQuery(id+"F0.wireOp",EDGE,"E7.39.5"),sQuery(id+"F0.wireOp",EDGE,"E7.40.0"),sQuery(id+"F0.wireOp",EDGE,"E7.40.1"),sQuery(id+"F0.wireOp",EDGE,"E7.40.2"),sQuery(id+"F0.wireOp",EDGE,"E7.40.3"),sQuery(id+"F0.wireOp",EDGE,"E7.40.4"),sQuery(id+"F0.wireOp",EDGE,"E7.40.5"),sQuery(id+"F0.wireOp",EDGE,"E7.41.0"),sQuery(id+"F0.wireOp",EDGE,"E7.41.1"),sQuery(id+"F0.wireOp",EDGE,"E7.41.2"),sQuery(id+"F0.wireOp",EDGE,"E7.41.3"),sQuery(id+"F0.wireOp",EDGE,"E7.41.4"),sQuery(id+"F0.wireOp",EDGE,"E7.41.5"),sQuery(id+"F0.wireOp",EDGE,"E7.42.0"),sQuery(id+"F0.wireOp",EDGE,"E7.42.1"),sQuery(id+"F0.wireOp",EDGE,"E7.42.2"),sQuery(id+"F0.wireOp",EDGE,"E7.42.3"),sQuery(id+"F0.wireOp",EDGE,"E7.42.4"),sQuery(id+"F0.wireOp",EDGE,"E7.42.5"),sQuery(id+"F0.wireOp",EDGE,"E7.43.0"),sQuery(id+"F0.wireOp",EDGE,"E7.43.1"),sQuery(id+"F0.wireOp",EDGE,"E7.43.2"),sQuery(id+"F0.wireOp",EDGE,"E7.43.3"),sQuery(id+"F0.wireOp",EDGE,"E7.43.4"),sQuery(id+"F0.wireOp",EDGE,"E7.43.5")])],"isStart":true})]});}
            chamfer(context, id + "F8", {"entities" : qUnion([Q0, Q1, Q2, Q3, Q4, Q5, Q6, Q7, Q8, Q9, Q10, Q11, Q12, Q13, Q14, Q15, Q16, Q17, Q18, Q19, Q20, Q21, Q22, Q23, Q24, Q25, Q26, Q27, Q28, Q29, Q30, Q31, Q32, Q33, Q34, Q35, Q36, Q37, Q38, Q39, Q40, Q41, Q42, Q43]), "width" : 2.54 * mm, "tangentPropagation" : true});
        }
        {
            var Q0;
            {var subQ0=sQuery(id+"F0.wireOp",EDGE,"E7.1.0");Q0=makeQuery(id+"F8.opChamfer","BLEND_EDGE",EDGE,{"blendedFrom":[makeQuery(id+"F2.opChamfer","BLEND_EDGE",EDGE,{"blendedFrom":[makeQuery(id+"F1.opExtrude","CAP_EDGE",EDGE,{"disambiguationData":[OSD([subQ0])],"isStart":false}),makeQuery(id+"F1.opExtrude","CAP_FACE",FACE,{"disambiguationData":[OSD([sQuery(id+"F0.wireOp",EDGE,"E1"),sQuery(id+"F0.wireOp",EDGE,"E2"),sQuery(id+"F0.wireOp",EDGE,"E3"),sQuery(id+"F0.wireOp",EDGE,"E4"),sQuery(id+"F0.wireOp",EDGE,"E5"),sQuery(id+"F0.wireOp",EDGE,"E6"),subQ0,sQuery(id+"F0.wireOp",EDGE,"E7.1.1"),sQuery(id+"F0.wireOp",EDGE,"E7.1.2"),sQuery(id+"F0.wireOp",EDGE,"E7.1.3"),sQuery(id+"F0.wireOp",EDGE,"E7.1.4"),sQuery(id+"F0.wireOp",EDGE,"E7.1.5"),sQuery(id+"F0.wireOp",EDGE,"E7.2.0"),sQuery(id+"F0.wireOp",EDGE,"E7.2.1"),sQuery(id+"F0.wireOp",EDGE,"E7.2.2"),sQuery(id+"F0.wireOp",EDGE,"E7.2.3"),sQuery(id+"F0.wireOp",EDGE,"E7.2.4"),sQuery(id+"F0.wireOp",EDGE,"E7.2.5"),sQuery(id+"F0.wireOp",EDGE,"E7.3.0"),sQuery(id+"F0.wireOp",EDGE,"E7.3.1"),sQuery(id+"F0.wireOp",EDGE,"E7.3.2"),sQuery(id+"F0.wireOp",EDGE,"E7.3.3"),sQuery(id+"F0.wireOp",EDGE,"E7.3.4"),sQuery(id+"F0.wireOp",EDGE,"E7.3.5"),sQuery(id+"F0.wireOp",EDGE,"E7.4.0"),sQuery(id+"F0.wireOp",EDGE,"E7.4.1"),sQuery(id+"F0.wireOp",EDGE,"E7.4.2"),sQuery(id+"F0.wireOp",EDGE,"E7.4.3"),sQuery(id+"F0.wireOp",EDGE,"E7.4.4"),sQuery(id+"F0.wireOp",EDGE,"E7.4.5"),sQuery(id+"F0.wireOp",EDGE,"E7.5.0"),sQuery(id+"F0.wireOp",EDGE,"E7.5.1"),sQuery(id+"F0.wireOp",EDGE,"E7.5.2"),sQuery(id+"F0.wireOp",EDGE,"E7.5.3"),sQuery(id+"F0.wireOp",EDGE,"E7.5.4"),sQuery(id+"F0.wireOp",EDGE,"E7.5.5"),sQuery(id+"F0.wireOp",EDGE,"E7.6.0"),sQuery(id+"F0.wireOp",EDGE,"E7.6.1"),sQuery(id+"F0.wireOp",EDGE,"E7.6.2"),sQuery(id+"F0.wireOp",EDGE,"E7.6.3"),sQuery(id+"F0.wireOp",EDGE,"E7.6.4"),sQuery(id+"F0.wireOp",EDGE,"E7.6.5"),sQuery(id+"F0.wireOp",EDGE,"E7.7.0"),sQuery(id+"F0.wireOp",EDGE,"E7.7.1"),sQuery(id+"F0.wireOp",EDGE,"E7.7.2"),sQuery(id+"F0.wireOp",EDGE,"E7.7.3"),sQuery(id+"F0.wireOp",EDGE,"E7.7.4"),sQuery(id+"F0.wireOp",EDGE,"E7.7.5"),sQuery(id+"F0.wireOp",EDGE,"E7.8.0"),sQuery(id+"F0.wireOp",EDGE,"E7.8.1"),sQuery(id+"F0.wireOp",EDGE,"E7.8.2"),sQuery(id+"F0.wireOp",EDGE,"E7.8.3"),sQuery(id+"F0.wireOp",EDGE,"E7.8.4"),sQuery(id+"F0.wireOp",EDGE,"E7.8.5"),sQuery(id+"F0.wireOp",EDGE,"E7.9.0"),sQuery(id+"F0.wireOp",EDGE,"E7.9.1"),sQuery(id+"F0.wireOp",EDGE,"E7.9.2"),sQuery(id+"F0.wireOp",EDGE,"E7.9.3"),sQuery(id+"F0.wireOp",EDGE,"E7.9.4"),sQuery(id+"F0.wireOp",EDGE,"E7.9.5"),sQuery(id+"F0.wireOp",EDGE,"E7.10.0"),sQuery(id+"F0.wireOp",EDGE,"E7.10.1"),sQuery(id+"F0.wireOp",EDGE,"E7.10.2"),sQuery(id+"F0.wireOp",EDGE,"E7.10.3"),sQuery(id+"F0.wireOp",EDGE,"E7.10.4"),sQuery(id+"F0.wireOp",EDGE,"E7.10.5"),sQuery(id+"F0.wireOp",EDGE,"E7.11.0"),sQuery(id+"F0.wireOp",EDGE,"E7.11.1"),sQuery(id+"F0.wireOp",EDGE,"E7.11.2"),sQuery(id+"F0.wireOp",EDGE,"E7.11.3"),sQuery(id+"F0.wireOp",EDGE,"E7.11.4"),sQuery(id+"F0.wireOp",EDGE,"E7.11.5"),sQuery(id+"F0.wireOp",EDGE,"E7.12.0"),sQuery(id+"F0.wireOp",EDGE,"E7.12.1"),sQuery(id+"F0.wireOp",EDGE,"E7.12.2"),sQuery(id+"F0.wireOp",EDGE,"E7.12.3"),sQuery(id+"F0.wireOp",EDGE,"E7.12.4"),sQuery(id+"F0.wireOp",EDGE,"E7.12.5"),sQuery(id+"F0.wireOp",EDGE,"E7.13.0"),sQuery(id+"F0.wireOp",EDGE,"E7.13.1"),sQuery(id+"F0.wireOp",EDGE,"E7.13.2"),sQuery(id+"F0.wireOp",EDGE,"E7.13.3"),sQuery(id+"F0.wireOp",EDGE,"E7.13.4"),sQuery(id+"F0.wireOp",EDGE,"E7.13.5"),sQuery(id+"F0.wireOp",EDGE,"E7.14.0"),sQuery(id+"F0.wireOp",EDGE,"E7.14.1"),sQuery(id+"F0.wireOp",EDGE,"E7.14.2"),sQuery(id+"F0.wireOp",EDGE,"E7.14.3"),sQuery(id+"F0.wireOp",EDGE,"E7.14.4"),sQuery(id+"F0.wireOp",EDGE,"E7.14.5"),sQuery(id+"F0.wireOp",EDGE,"E7.15.0"),sQuery(id+"F0.wireOp",EDGE,"E7.15.1"),sQuery(id+"F0.wireOp",EDGE,"E7.15.2"),sQuery(id+"F0.wireOp",EDGE,"E7.15.3"),sQuery(id+"F0.wireOp",EDGE,"E7.15.4"),sQuery(id+"F0.wireOp",EDGE,"E7.15.5"),sQuery(id+"F0.wireOp",EDGE,"E7.16.0"),sQuery(id+"F0.wireOp",EDGE,"E7.16.1"),sQuery(id+"F0.wireOp",EDGE,"E7.16.2"),sQuery(id+"F0.wireOp",EDGE,"E7.16.3"),sQuery(id+"F0.wireOp",EDGE,"E7.16.4"),sQuery(id+"F0.wireOp",EDGE,"E7.16.5"),sQuery(id+"F0.wireOp",EDGE,"E7.17.0"),sQuery(id+"F0.wireOp",EDGE,"E7.17.1"),sQuery(id+"F0.wireOp",EDGE,"E7.17.2"),sQuery(id+"F0.wireOp",EDGE,"E7.17.3"),sQuery(id+"F0.wireOp",EDGE,"E7.17.4"),sQuery(id+"F0.wireOp",EDGE,"E7.17.5"),sQuery(id+"F0.wireOp",EDGE,"E7.18.0"),sQuery(id+"F0.wireOp",EDGE,"E7.18.1"),sQuery(id+"F0.wireOp",EDGE,"E7.18.2"),sQuery(id+"F0.wireOp",EDGE,"E7.18.3"),sQuery(id+"F0.wireOp",EDGE,"E7.18.4"),sQuery(id+"F0.wireOp",EDGE,"E7.18.5"),sQuery(id+"F0.wireOp",EDGE,"E7.19.0"),sQuery(id+"F0.wireOp",EDGE,"E7.19.1"),sQuery(id+"F0.wireOp",EDGE,"E7.19.2"),sQuery(id+"F0.wireOp",EDGE,"E7.19.3"),sQuery(id+"F0.wireOp",EDGE,"E7.19.4"),sQuery(id+"F0.wireOp",EDGE,"E7.19.5"),sQuery(id+"F0.wireOp",EDGE,"E7.20.0"),sQuery(id+"F0.wireOp",EDGE,"E7.20.1"),sQuery(id+"F0.wireOp",EDGE,"E7.20.2"),sQuery(id+"F0.wireOp",EDGE,"E7.20.3"),sQuery(id+"F0.wireOp",EDGE,"E7.20.4"),sQuery(id+"F0.wireOp",EDGE,"E7.20.5"),sQuery(id+"F0.wireOp",EDGE,"E7.21.0"),sQuery(id+"F0.wireOp",EDGE,"E7.21.1"),sQuery(id+"F0.wireOp",EDGE,"E7.21.2"),sQuery(id+"F0.wireOp",EDGE,"E7.21.3"),sQuery(id+"F0.wireOp",EDGE,"E7.21.4"),sQuery(id+"F0.wireOp",EDGE,"E7.21.5"),sQuery(id+"F0.wireOp",EDGE,"E7.22.0"),sQuery(id+"F0.wireOp",EDGE,"E7.22.1"),sQuery(id+"F0.wireOp",EDGE,"E7.22.2"),sQuery(id+"F0.wireOp",EDGE,"E7.22.3"),sQuery(id+"F0.wireOp",EDGE,"E7.22.4"),sQuery(id+"F0.wireOp",EDGE,"E7.22.5"),sQuery(id+"F0.wireOp",EDGE,"E7.23.0"),sQuery(id+"F0.wireOp",EDGE,"E7.23.1"),sQuery(id+"F0.wireOp",EDGE,"E7.23.2"),sQuery(id+"F0.wireOp",EDGE,"E7.23.3"),sQuery(id+"F0.wireOp",EDGE,"E7.23.4"),sQuery(id+"F0.wireOp",EDGE,"E7.23.5"),sQuery(id+"F0.wireOp",EDGE,"E7.24.0"),sQuery(id+"F0.wireOp",EDGE,"E7.24.1"),sQuery(id+"F0.wireOp",EDGE,"E7.24.2"),sQuery(id+"F0.wireOp",EDGE,"E7.24.3"),sQuery(id+"F0.wireOp",EDGE,"E7.24.4"),sQuery(id+"F0.wireOp",EDGE,"E7.24.5"),sQuery(id+"F0.wireOp",EDGE,"E7.25.0"),sQuery(id+"F0.wireOp",EDGE,"E7.25.1"),sQuery(id+"F0.wireOp",EDGE,"E7.25.2"),sQuery(id+"F0.wireOp",EDGE,"E7.25.3"),sQuery(id+"F0.wireOp",EDGE,"E7.25.4"),sQuery(id+"F0.wireOp",EDGE,"E7.25.5"),sQuery(id+"F0.wireOp",EDGE,"E7.26.0"),sQuery(id+"F0.wireOp",EDGE,"E7.26.1"),sQuery(id+"F0.wireOp",EDGE,"E7.26.2"),sQuery(id+"F0.wireOp",EDGE,"E7.26.3"),sQuery(id+"F0.wireOp",EDGE,"E7.26.4"),sQuery(id+"F0.wireOp",EDGE,"E7.26.5"),sQuery(id+"F0.wireOp",EDGE,"E7.27.0"),sQuery(id+"F0.wireOp",EDGE,"E7.27.1"),sQuery(id+"F0.wireOp",EDGE,"E7.27.2"),sQuery(id+"F0.wireOp",EDGE,"E7.27.3"),sQuery(id+"F0.wireOp",EDGE,"E7.27.4"),sQuery(id+"F0.wireOp",EDGE,"E7.27.5"),sQuery(id+"F0.wireOp",EDGE,"E7.28.0"),sQuery(id+"F0.wireOp",EDGE,"E7.28.1"),sQuery(id+"F0.wireOp",EDGE,"E7.28.2"),sQuery(id+"F0.wireOp",EDGE,"E7.28.3"),sQuery(id+"F0.wireOp",EDGE,"E7.28.4"),sQuery(id+"F0.wireOp",EDGE,"E7.28.5"),sQuery(id+"F0.wireOp",EDGE,"E7.29.0"),sQuery(id+"F0.wireOp",EDGE,"E7.29.1"),sQuery(id+"F0.wireOp",EDGE,"E7.29.2"),sQuery(id+"F0.wireOp",EDGE,"E7.29.3"),sQuery(id+"F0.wireOp",EDGE,"E7.29.4"),sQuery(id+"F0.wireOp",EDGE,"E7.29.5"),sQuery(id+"F0.wireOp",EDGE,"E7.30.0"),sQuery(id+"F0.wireOp",EDGE,"E7.30.1"),sQuery(id+"F0.wireOp",EDGE,"E7.30.2"),sQuery(id+"F0.wireOp",EDGE,"E7.30.3"),sQuery(id+"F0.wireOp",EDGE,"E7.30.4"),sQuery(id+"F0.wireOp",EDGE,"E7.30.5"),sQuery(id+"F0.wireOp",EDGE,"E7.31.0"),sQuery(id+"F0.wireOp",EDGE,"E7.31.1"),sQuery(id+"F0.wireOp",EDGE,"E7.31.2"),sQuery(id+"F0.wireOp",EDGE,"E7.31.3"),sQuery(id+"F0.wireOp",EDGE,"E7.31.4"),sQuery(id+"F0.wireOp",EDGE,"E7.31.5"),sQuery(id+"F0.wireOp",EDGE,"E7.32.0"),sQuery(id+"F0.wireOp",EDGE,"E7.32.1"),sQuery(id+"F0.wireOp",EDGE,"E7.32.2"),sQuery(id+"F0.wireOp",EDGE,"E7.32.3"),sQuery(id+"F0.wireOp",EDGE,"E7.32.4"),sQuery(id+"F0.wireOp",EDGE,"E7.32.5"),sQuery(id+"F0.wireOp",EDGE,"E7.33.0"),sQuery(id+"F0.wireOp",EDGE,"E7.33.1"),sQuery(id+"F0.wireOp",EDGE,"E7.33.2"),sQuery(id+"F0.wireOp",EDGE,"E7.33.3"),sQuery(id+"F0.wireOp",EDGE,"E7.33.4"),sQuery(id+"F0.wireOp",EDGE,"E7.33.5"),sQuery(id+"F0.wireOp",EDGE,"E7.34.0"),sQuery(id+"F0.wireOp",EDGE,"E7.34.1"),sQuery(id+"F0.wireOp",EDGE,"E7.34.2"),sQuery(id+"F0.wireOp",EDGE,"E7.34.3"),sQuery(id+"F0.wireOp",EDGE,"E7.34.4"),sQuery(id+"F0.wireOp",EDGE,"E7.34.5"),sQuery(id+"F0.wireOp",EDGE,"E7.35.0"),sQuery(id+"F0.wireOp",EDGE,"E7.35.1"),sQuery(id+"F0.wireOp",EDGE,"E7.35.2"),sQuery(id+"F0.wireOp",EDGE,"E7.35.3"),sQuery(id+"F0.wireOp",EDGE,"E7.35.4"),sQuery(id+"F0.wireOp",EDGE,"E7.35.5"),sQuery(id+"F0.wireOp",EDGE,"E7.36.0"),sQuery(id+"F0.wireOp",EDGE,"E7.36.1"),sQuery(id+"F0.wireOp",EDGE,"E7.36.2"),sQuery(id+"F0.wireOp",EDGE,"E7.36.3"),sQuery(id+"F0.wireOp",EDGE,"E7.36.4"),sQuery(id+"F0.wireOp",EDGE,"E7.36.5"),sQuery(id+"F0.wireOp",EDGE,"E7.37.0"),sQuery(id+"F0.wireOp",EDGE,"E7.37.1"),sQuery(id+"F0.wireOp",EDGE,"E7.37.2"),sQuery(id+"F0.wireOp",EDGE,"E7.37.3"),sQuery(id+"F0.wireOp",EDGE,"E7.37.4"),sQuery(id+"F0.wireOp",EDGE,"E7.37.5"),sQuery(id+"F0.wireOp",EDGE,"E7.38.0"),sQuery(id+"F0.wireOp",EDGE,"E7.38.1"),sQuery(id+"F0.wireOp",EDGE,"E7.38.2"),sQuery(id+"F0.wireOp",EDGE,"E7.38.3"),sQuery(id+"F0.wireOp",EDGE,"E7.38.4"),sQuery(id+"F0.wireOp",EDGE,"E7.38.5"),sQuery(id+"F0.wireOp",EDGE,"E7.39.0"),sQuery(id+"F0.wireOp",EDGE,"E7.39.1"),sQuery(id+"F0.wireOp",EDGE,"E7.39.2"),sQuery(id+"F0.wireOp",EDGE,"E7.39.3"),sQuery(id+"F0.wireOp",EDGE,"E7.39.4"),sQuery(id+"F0.wireOp",EDGE,"E7.39.5"),sQuery(id+"F0.wireOp",EDGE,"E7.40.0"),sQuery(id+"F0.wireOp",EDGE,"E7.40.1"),sQuery(id+"F0.wireOp",EDGE,"E7.40.2"),sQuery(id+"F0.wireOp",EDGE,"E7.40.3"),sQuery(id+"F0.wireOp",EDGE,"E7.40.4"),sQuery(id+"F0.wireOp",EDGE,"E7.40.5"),sQuery(id+"F0.wireOp",EDGE,"E7.41.0"),sQuery(id+"F0.wireOp",EDGE,"E7.41.1"),sQuery(id+"F0.wireOp",EDGE,"E7.41.2"),sQuery(id+"F0.wireOp",EDGE,"E7.41.3"),sQuery(id+"F0.wireOp",EDGE,"E7.41.4"),sQuery(id+"F0.wireOp",EDGE,"E7.41.5"),sQuery(id+"F0.wireOp",EDGE,"E7.42.0"),sQuery(id+"F0.wireOp",EDGE,"E7.42.1"),sQuery(id+"F0.wireOp",EDGE,"E7.42.2"),sQuery(id+"F0.wireOp",EDGE,"E7.42.3"),sQuery(id+"F0.wireOp",EDGE,"E7.42.4"),sQuery(id+"F0.wireOp",EDGE,"E7.42.5"),sQuery(id+"F0.wireOp",EDGE,"E7.43.0"),sQuery(id+"F0.wireOp",EDGE,"E7.43.1"),sQuery(id+"F0.wireOp",EDGE,"E7.43.2"),sQuery(id+"F0.wireOp",EDGE,"E7.43.3"),sQuery(id+"F0.wireOp",EDGE,"E7.43.4"),sQuery(id+"F0.wireOp",EDGE,"E7.43.5")])],"isStart":false})],"blendedInto":[makeQuery(id+"F1.opExtrude","CAP_FACE",FACE,{"disambiguationData":[OSD([sQuery(id+"F0.wireOp",EDGE,"E1"),sQuery(id+"F0.wireOp",EDGE,"E2"),sQuery(id+"F0.wireOp",EDGE,"E3"),sQuery(id+"F0.wireOp",EDGE,"E4"),sQuery(id+"F0.wireOp",EDGE,"E5"),sQuery(id+"F0.wireOp",EDGE,"E6"),subQ0,sQuery(id+"F0.wireOp",EDGE,"E7.1.1"),sQuery(id+"F0.wireOp",EDGE,"E7.1.2"),sQuery(id+"F0.wireOp",EDGE,"E7.1.3"),sQuery(id+"F0.wireOp",EDGE,"E7.1.4"),sQuery(id+"F0.wireOp",EDGE,"E7.1.5"),sQuery(id+"F0.wireOp",EDGE,"E7.2.0"),sQuery(id+"F0.wireOp",EDGE,"E7.2.1"),sQuery(id+"F0.wireOp",EDGE,"E7.2.2"),sQuery(id+"F0.wireOp",EDGE,"E7.2.3"),sQuery(id+"F0.wireOp",EDGE,"E7.2.4"),sQuery(id+"F0.wireOp",EDGE,"E7.2.5"),sQuery(id+"F0.wireOp",EDGE,"E7.3.0"),sQuery(id+"F0.wireOp",EDGE,"E7.3.1"),sQuery(id+"F0.wireOp",EDGE,"E7.3.2"),sQuery(id+"F0.wireOp",EDGE,"E7.3.3"),sQuery(id+"F0.wireOp",EDGE,"E7.3.4"),sQuery(id+"F0.wireOp",EDGE,"E7.3.5"),sQuery(id+"F0.wireOp",EDGE,"E7.4.0"),sQuery(id+"F0.wireOp",EDGE,"E7.4.1"),sQuery(id+"F0.wireOp",EDGE,"E7.4.2"),sQuery(id+"F0.wireOp",EDGE,"E7.4.3"),sQuery(id+"F0.wireOp",EDGE,"E7.4.4"),sQuery(id+"F0.wireOp",EDGE,"E7.4.5"),sQuery(id+"F0.wireOp",EDGE,"E7.5.0"),sQuery(id+"F0.wireOp",EDGE,"E7.5.1"),sQuery(id+"F0.wireOp",EDGE,"E7.5.2"),sQuery(id+"F0.wireOp",EDGE,"E7.5.3"),sQuery(id+"F0.wireOp",EDGE,"E7.5.4"),sQuery(id+"F0.wireOp",EDGE,"E7.5.5"),sQuery(id+"F0.wireOp",EDGE,"E7.6.0"),sQuery(id+"F0.wireOp",EDGE,"E7.6.1"),sQuery(id+"F0.wireOp",EDGE,"E7.6.2"),sQuery(id+"F0.wireOp",EDGE,"E7.6.3"),sQuery(id+"F0.wireOp",EDGE,"E7.6.4"),sQuery(id+"F0.wireOp",EDGE,"E7.6.5"),sQuery(id+"F0.wireOp",EDGE,"E7.7.0"),sQuery(id+"F0.wireOp",EDGE,"E7.7.1"),sQuery(id+"F0.wireOp",EDGE,"E7.7.2"),sQuery(id+"F0.wireOp",EDGE,"E7.7.3"),sQuery(id+"F0.wireOp",EDGE,"E7.7.4"),sQuery(id+"F0.wireOp",EDGE,"E7.7.5"),sQuery(id+"F0.wireOp",EDGE,"E7.8.0"),sQuery(id+"F0.wireOp",EDGE,"E7.8.1"),sQuery(id+"F0.wireOp",EDGE,"E7.8.2"),sQuery(id+"F0.wireOp",EDGE,"E7.8.3"),sQuery(id+"F0.wireOp",EDGE,"E7.8.4"),sQuery(id+"F0.wireOp",EDGE,"E7.8.5"),sQuery(id+"F0.wireOp",EDGE,"E7.9.0"),sQuery(id+"F0.wireOp",EDGE,"E7.9.1"),sQuery(id+"F0.wireOp",EDGE,"E7.9.2"),sQuery(id+"F0.wireOp",EDGE,"E7.9.3"),sQuery(id+"F0.wireOp",EDGE,"E7.9.4"),sQuery(id+"F0.wireOp",EDGE,"E7.9.5"),sQuery(id+"F0.wireOp",EDGE,"E7.10.0"),sQuery(id+"F0.wireOp",EDGE,"E7.10.1"),sQuery(id+"F0.wireOp",EDGE,"E7.10.2"),sQuery(id+"F0.wireOp",EDGE,"E7.10.3"),sQuery(id+"F0.wireOp",EDGE,"E7.10.4"),sQuery(id+"F0.wireOp",EDGE,"E7.10.5"),sQuery(id+"F0.wireOp",EDGE,"E7.11.0"),sQuery(id+"F0.wireOp",EDGE,"E7.11.1"),sQuery(id+"F0.wireOp",EDGE,"E7.11.2"),sQuery(id+"F0.wireOp",EDGE,"E7.11.3"),sQuery(id+"F0.wireOp",EDGE,"E7.11.4"),sQuery(id+"F0.wireOp",EDGE,"E7.11.5"),sQuery(id+"F0.wireOp",EDGE,"E7.12.0"),sQuery(id+"F0.wireOp",EDGE,"E7.12.1"),sQuery(id+"F0.wireOp",EDGE,"E7.12.2"),sQuery(id+"F0.wireOp",EDGE,"E7.12.3"),sQuery(id+"F0.wireOp",EDGE,"E7.12.4"),sQuery(id+"F0.wireOp",EDGE,"E7.12.5"),sQuery(id+"F0.wireOp",EDGE,"E7.13.0"),sQuery(id+"F0.wireOp",EDGE,"E7.13.1"),sQuery(id+"F0.wireOp",EDGE,"E7.13.2"),sQuery(id+"F0.wireOp",EDGE,"E7.13.3"),sQuery(id+"F0.wireOp",EDGE,"E7.13.4"),sQuery(id+"F0.wireOp",EDGE,"E7.13.5"),sQuery(id+"F0.wireOp",EDGE,"E7.14.0"),sQuery(id+"F0.wireOp",EDGE,"E7.14.1"),sQuery(id+"F0.wireOp",EDGE,"E7.14.2"),sQuery(id+"F0.wireOp",EDGE,"E7.14.3"),sQuery(id+"F0.wireOp",EDGE,"E7.14.4"),sQuery(id+"F0.wireOp",EDGE,"E7.14.5"),sQuery(id+"F0.wireOp",EDGE,"E7.15.0"),sQuery(id+"F0.wireOp",EDGE,"E7.15.1"),sQuery(id+"F0.wireOp",EDGE,"E7.15.2"),sQuery(id+"F0.wireOp",EDGE,"E7.15.3"),sQuery(id+"F0.wireOp",EDGE,"E7.15.4"),sQuery(id+"F0.wireOp",EDGE,"E7.15.5"),sQuery(id+"F0.wireOp",EDGE,"E7.16.0"),sQuery(id+"F0.wireOp",EDGE,"E7.16.1"),sQuery(id+"F0.wireOp",EDGE,"E7.16.2"),sQuery(id+"F0.wireOp",EDGE,"E7.16.3"),sQuery(id+"F0.wireOp",EDGE,"E7.16.4"),sQuery(id+"F0.wireOp",EDGE,"E7.16.5"),sQuery(id+"F0.wireOp",EDGE,"E7.17.0"),sQuery(id+"F0.wireOp",EDGE,"E7.17.1"),sQuery(id+"F0.wireOp",EDGE,"E7.17.2"),sQuery(id+"F0.wireOp",EDGE,"E7.17.3"),sQuery(id+"F0.wireOp",EDGE,"E7.17.4"),sQuery(id+"F0.wireOp",EDGE,"E7.17.5"),sQuery(id+"F0.wireOp",EDGE,"E7.18.0"),sQuery(id+"F0.wireOp",EDGE,"E7.18.1"),sQuery(id+"F0.wireOp",EDGE,"E7.18.2"),sQuery(id+"F0.wireOp",EDGE,"E7.18.3"),sQuery(id+"F0.wireOp",EDGE,"E7.18.4"),sQuery(id+"F0.wireOp",EDGE,"E7.18.5"),sQuery(id+"F0.wireOp",EDGE,"E7.19.0"),sQuery(id+"F0.wireOp",EDGE,"E7.19.1"),sQuery(id+"F0.wireOp",EDGE,"E7.19.2"),sQuery(id+"F0.wireOp",EDGE,"E7.19.3"),sQuery(id+"F0.wireOp",EDGE,"E7.19.4"),sQuery(id+"F0.wireOp",EDGE,"E7.19.5"),sQuery(id+"F0.wireOp",EDGE,"E7.20.0"),sQuery(id+"F0.wireOp",EDGE,"E7.20.1"),sQuery(id+"F0.wireOp",EDGE,"E7.20.2"),sQuery(id+"F0.wireOp",EDGE,"E7.20.3"),sQuery(id+"F0.wireOp",EDGE,"E7.20.4"),sQuery(id+"F0.wireOp",EDGE,"E7.20.5"),sQuery(id+"F0.wireOp",EDGE,"E7.21.0"),sQuery(id+"F0.wireOp",EDGE,"E7.21.1"),sQuery(id+"F0.wireOp",EDGE,"E7.21.2"),sQuery(id+"F0.wireOp",EDGE,"E7.21.3"),sQuery(id+"F0.wireOp",EDGE,"E7.21.4"),sQuery(id+"F0.wireOp",EDGE,"E7.21.5"),sQuery(id+"F0.wireOp",EDGE,"E7.22.0"),sQuery(id+"F0.wireOp",EDGE,"E7.22.1"),sQuery(id+"F0.wireOp",EDGE,"E7.22.2"),sQuery(id+"F0.wireOp",EDGE,"E7.22.3"),sQuery(id+"F0.wireOp",EDGE,"E7.22.4"),sQuery(id+"F0.wireOp",EDGE,"E7.22.5"),sQuery(id+"F0.wireOp",EDGE,"E7.23.0"),sQuery(id+"F0.wireOp",EDGE,"E7.23.1"),sQuery(id+"F0.wireOp",EDGE,"E7.23.2"),sQuery(id+"F0.wireOp",EDGE,"E7.23.3"),sQuery(id+"F0.wireOp",EDGE,"E7.23.4"),sQuery(id+"F0.wireOp",EDGE,"E7.23.5"),sQuery(id+"F0.wireOp",EDGE,"E7.24.0"),sQuery(id+"F0.wireOp",EDGE,"E7.24.1"),sQuery(id+"F0.wireOp",EDGE,"E7.24.2"),sQuery(id+"F0.wireOp",EDGE,"E7.24.3"),sQuery(id+"F0.wireOp",EDGE,"E7.24.4"),sQuery(id+"F0.wireOp",EDGE,"E7.24.5"),sQuery(id+"F0.wireOp",EDGE,"E7.25.0"),sQuery(id+"F0.wireOp",EDGE,"E7.25.1"),sQuery(id+"F0.wireOp",EDGE,"E7.25.2"),sQuery(id+"F0.wireOp",EDGE,"E7.25.3"),sQuery(id+"F0.wireOp",EDGE,"E7.25.4"),sQuery(id+"F0.wireOp",EDGE,"E7.25.5"),sQuery(id+"F0.wireOp",EDGE,"E7.26.0"),sQuery(id+"F0.wireOp",EDGE,"E7.26.1"),sQuery(id+"F0.wireOp",EDGE,"E7.26.2"),sQuery(id+"F0.wireOp",EDGE,"E7.26.3"),sQuery(id+"F0.wireOp",EDGE,"E7.26.4"),sQuery(id+"F0.wireOp",EDGE,"E7.26.5"),sQuery(id+"F0.wireOp",EDGE,"E7.27.0"),sQuery(id+"F0.wireOp",EDGE,"E7.27.1"),sQuery(id+"F0.wireOp",EDGE,"E7.27.2"),sQuery(id+"F0.wireOp",EDGE,"E7.27.3"),sQuery(id+"F0.wireOp",EDGE,"E7.27.4"),sQuery(id+"F0.wireOp",EDGE,"E7.27.5"),sQuery(id+"F0.wireOp",EDGE,"E7.28.0"),sQuery(id+"F0.wireOp",EDGE,"E7.28.1"),sQuery(id+"F0.wireOp",EDGE,"E7.28.2"),sQuery(id+"F0.wireOp",EDGE,"E7.28.3"),sQuery(id+"F0.wireOp",EDGE,"E7.28.4"),sQuery(id+"F0.wireOp",EDGE,"E7.28.5"),sQuery(id+"F0.wireOp",EDGE,"E7.29.0"),sQuery(id+"F0.wireOp",EDGE,"E7.29.1"),sQuery(id+"F0.wireOp",EDGE,"E7.29.2"),sQuery(id+"F0.wireOp",EDGE,"E7.29.3"),sQuery(id+"F0.wireOp",EDGE,"E7.29.4"),sQuery(id+"F0.wireOp",EDGE,"E7.29.5"),sQuery(id+"F0.wireOp",EDGE,"E7.30.0"),sQuery(id+"F0.wireOp",EDGE,"E7.30.1"),sQuery(id+"F0.wireOp",EDGE,"E7.30.2"),sQuery(id+"F0.wireOp",EDGE,"E7.30.3"),sQuery(id+"F0.wireOp",EDGE,"E7.30.4"),sQuery(id+"F0.wireOp",EDGE,"E7.30.5"),sQuery(id+"F0.wireOp",EDGE,"E7.31.0"),sQuery(id+"F0.wireOp",EDGE,"E7.31.1"),sQuery(id+"F0.wireOp",EDGE,"E7.31.2"),sQuery(id+"F0.wireOp",EDGE,"E7.31.3"),sQuery(id+"F0.wireOp",EDGE,"E7.31.4"),sQuery(id+"F0.wireOp",EDGE,"E7.31.5"),sQuery(id+"F0.wireOp",EDGE,"E7.32.0"),sQuery(id+"F0.wireOp",EDGE,"E7.32.1"),sQuery(id+"F0.wireOp",EDGE,"E7.32.2"),sQuery(id+"F0.wireOp",EDGE,"E7.32.3"),sQuery(id+"F0.wireOp",EDGE,"E7.32.4"),sQuery(id+"F0.wireOp",EDGE,"E7.32.5"),sQuery(id+"F0.wireOp",EDGE,"E7.33.0"),sQuery(id+"F0.wireOp",EDGE,"E7.33.1"),sQuery(id+"F0.wireOp",EDGE,"E7.33.2"),sQuery(id+"F0.wireOp",EDGE,"E7.33.3"),sQuery(id+"F0.wireOp",EDGE,"E7.33.4"),sQuery(id+"F0.wireOp",EDGE,"E7.33.5"),sQuery(id+"F0.wireOp",EDGE,"E7.34.0"),sQuery(id+"F0.wireOp",EDGE,"E7.34.1"),sQuery(id+"F0.wireOp",EDGE,"E7.34.2"),sQuery(id+"F0.wireOp",EDGE,"E7.34.3"),sQuery(id+"F0.wireOp",EDGE,"E7.34.4"),sQuery(id+"F0.wireOp",EDGE,"E7.34.5"),sQuery(id+"F0.wireOp",EDGE,"E7.35.0"),sQuery(id+"F0.wireOp",EDGE,"E7.35.1"),sQuery(id+"F0.wireOp",EDGE,"E7.35.2"),sQuery(id+"F0.wireOp",EDGE,"E7.35.3"),sQuery(id+"F0.wireOp",EDGE,"E7.35.4"),sQuery(id+"F0.wireOp",EDGE,"E7.35.5"),sQuery(id+"F0.wireOp",EDGE,"E7.36.0"),sQuery(id+"F0.wireOp",EDGE,"E7.36.1"),sQuery(id+"F0.wireOp",EDGE,"E7.36.2"),sQuery(id+"F0.wireOp",EDGE,"E7.36.3"),sQuery(id+"F0.wireOp",EDGE,"E7.36.4"),sQuery(id+"F0.wireOp",EDGE,"E7.36.5"),sQuery(id+"F0.wireOp",EDGE,"E7.37.0"),sQuery(id+"F0.wireOp",EDGE,"E7.37.1"),sQuery(id+"F0.wireOp",EDGE,"E7.37.2"),sQuery(id+"F0.wireOp",EDGE,"E7.37.3"),sQuery(id+"F0.wireOp",EDGE,"E7.37.4"),sQuery(id+"F0.wireOp",EDGE,"E7.37.5"),sQuery(id+"F0.wireOp",EDGE,"E7.38.0"),sQuery(id+"F0.wireOp",EDGE,"E7.38.1"),sQuery(id+"F0.wireOp",EDGE,"E7.38.2"),sQuery(id+"F0.wireOp",EDGE,"E7.38.3"),sQuery(id+"F0.wireOp",EDGE,"E7.38.4"),sQuery(id+"F0.wireOp",EDGE,"E7.38.5"),sQuery(id+"F0.wireOp",EDGE,"E7.39.0"),sQuery(id+"F0.wireOp",EDGE,"E7.39.1"),sQuery(id+"F0.wireOp",EDGE,"E7.39.2"),sQuery(id+"F0.wireOp",EDGE,"E7.39.3"),sQuery(id+"F0.wireOp",EDGE,"E7.39.4"),sQuery(id+"F0.wireOp",EDGE,"E7.39.5"),sQuery(id+"F0.wireOp",EDGE,"E7.40.0"),sQuery(id+"F0.wireOp",EDGE,"E7.40.1"),sQuery(id+"F0.wireOp",EDGE,"E7.40.2"),sQuery(id+"F0.wireOp",EDGE,"E7.40.3"),sQuery(id+"F0.wireOp",EDGE,"E7.40.4"),sQuery(id+"F0.wireOp",EDGE,"E7.40.5"),sQuery(id+"F0.wireOp",EDGE,"E7.41.0"),sQuery(id+"F0.wireOp",EDGE,"E7.41.1"),sQuery(id+"F0.wireOp",EDGE,"E7.41.2"),sQuery(id+"F0.wireOp",EDGE,"E7.41.3"),sQuery(id+"F0.wireOp",EDGE,"E7.41.4"),sQuery(id+"F0.wireOp",EDGE,"E7.41.5"),sQuery(id+"F0.wireOp",EDGE,"E7.42.0"),sQuery(id+"F0.wireOp",EDGE,"E7.42.1"),sQuery(id+"F0.wireOp",EDGE,"E7.42.2"),sQuery(id+"F0.wireOp",EDGE,"E7.42.3"),sQuery(id+"F0.wireOp",EDGE,"E7.42.4"),sQuery(id+"F0.wireOp",EDGE,"E7.42.5"),sQuery(id+"F0.wireOp",EDGE,"E7.43.0"),sQuery(id+"F0.wireOp",EDGE,"E7.43.1"),sQuery(id+"F0.wireOp",EDGE,"E7.43.2"),sQuery(id+"F0.wireOp",EDGE,"E7.43.3"),sQuery(id+"F0.wireOp",EDGE,"E7.43.4"),sQuery(id+"F0.wireOp",EDGE,"E7.43.5")])],"isStart":false})]}),makeQuery(id+"F2.opChamfer","BLEND_FACE",FACE,{"disambiguationData":[OSD([subQ0])]})],"blendedInto":[makeQuery(id+"F2.opChamfer","BLEND_FACE",FACE,{"disambiguationData":[OSD([subQ0])]})]});}
            var Q1;
            {var subQ0=sQuery(id+"F0.wireOp",EDGE,"E7.43.0");Q1=makeQuery(id+"F8.opChamfer","BLEND_EDGE",EDGE,{"blendedFrom":[makeQuery(id+"F2.opChamfer","BLEND_EDGE",EDGE,{"blendedFrom":[makeQuery(id+"F1.opExtrude","CAP_EDGE",EDGE,{"disambiguationData":[OSD([subQ0])],"isStart":false}),makeQuery(id+"F1.opExtrude","CAP_FACE",FACE,{"disambiguationData":[OSD([sQuery(id+"F0.wireOp",EDGE,"E1"),sQuery(id+"F0.wireOp",EDGE,"E2"),sQuery(id+"F0.wireOp",EDGE,"E3"),sQuery(id+"F0.wireOp",EDGE,"E4"),sQuery(id+"F0.wireOp",EDGE,"E5"),sQuery(id+"F0.wireOp",EDGE,"E6"),sQuery(id+"F0.wireOp",EDGE,"E7.1.0"),sQuery(id+"F0.wireOp",EDGE,"E7.1.1"),sQuery(id+"F0.wireOp",EDGE,"E7.1.2"),sQuery(id+"F0.wireOp",EDGE,"E7.1.3"),sQuery(id+"F0.wireOp",EDGE,"E7.1.4"),sQuery(id+"F0.wireOp",EDGE,"E7.1.5"),sQuery(id+"F0.wireOp",EDGE,"E7.2.0"),sQuery(id+"F0.wireOp",EDGE,"E7.2.1"),sQuery(id+"F0.wireOp",EDGE,"E7.2.2"),sQuery(id+"F0.wireOp",EDGE,"E7.2.3"),sQuery(id+"F0.wireOp",EDGE,"E7.2.4"),sQuery(id+"F0.wireOp",EDGE,"E7.2.5"),sQuery(id+"F0.wireOp",EDGE,"E7.3.0"),sQuery(id+"F0.wireOp",EDGE,"E7.3.1"),sQuery(id+"F0.wireOp",EDGE,"E7.3.2"),sQuery(id+"F0.wireOp",EDGE,"E7.3.3"),sQuery(id+"F0.wireOp",EDGE,"E7.3.4"),sQuery(id+"F0.wireOp",EDGE,"E7.3.5"),sQuery(id+"F0.wireOp",EDGE,"E7.4.0"),sQuery(id+"F0.wireOp",EDGE,"E7.4.1"),sQuery(id+"F0.wireOp",EDGE,"E7.4.2"),sQuery(id+"F0.wireOp",EDGE,"E7.4.3"),sQuery(id+"F0.wireOp",EDGE,"E7.4.4"),sQuery(id+"F0.wireOp",EDGE,"E7.4.5"),sQuery(id+"F0.wireOp",EDGE,"E7.5.0"),sQuery(id+"F0.wireOp",EDGE,"E7.5.1"),sQuery(id+"F0.wireOp",EDGE,"E7.5.2"),sQuery(id+"F0.wireOp",EDGE,"E7.5.3"),sQuery(id+"F0.wireOp",EDGE,"E7.5.4"),sQuery(id+"F0.wireOp",EDGE,"E7.5.5"),sQuery(id+"F0.wireOp",EDGE,"E7.6.0"),sQuery(id+"F0.wireOp",EDGE,"E7.6.1"),sQuery(id+"F0.wireOp",EDGE,"E7.6.2"),sQuery(id+"F0.wireOp",EDGE,"E7.6.3"),sQuery(id+"F0.wireOp",EDGE,"E7.6.4"),sQuery(id+"F0.wireOp",EDGE,"E7.6.5"),sQuery(id+"F0.wireOp",EDGE,"E7.7.0"),sQuery(id+"F0.wireOp",EDGE,"E7.7.1"),sQuery(id+"F0.wireOp",EDGE,"E7.7.2"),sQuery(id+"F0.wireOp",EDGE,"E7.7.3"),sQuery(id+"F0.wireOp",EDGE,"E7.7.4"),sQuery(id+"F0.wireOp",EDGE,"E7.7.5"),sQuery(id+"F0.wireOp",EDGE,"E7.8.0"),sQuery(id+"F0.wireOp",EDGE,"E7.8.1"),sQuery(id+"F0.wireOp",EDGE,"E7.8.2"),sQuery(id+"F0.wireOp",EDGE,"E7.8.3"),sQuery(id+"F0.wireOp",EDGE,"E7.8.4"),sQuery(id+"F0.wireOp",EDGE,"E7.8.5"),sQuery(id+"F0.wireOp",EDGE,"E7.9.0"),sQuery(id+"F0.wireOp",EDGE,"E7.9.1"),sQuery(id+"F0.wireOp",EDGE,"E7.9.2"),sQuery(id+"F0.wireOp",EDGE,"E7.9.3"),sQuery(id+"F0.wireOp",EDGE,"E7.9.4"),sQuery(id+"F0.wireOp",EDGE,"E7.9.5"),sQuery(id+"F0.wireOp",EDGE,"E7.10.0"),sQuery(id+"F0.wireOp",EDGE,"E7.10.1"),sQuery(id+"F0.wireOp",EDGE,"E7.10.2"),sQuery(id+"F0.wireOp",EDGE,"E7.10.3"),sQuery(id+"F0.wireOp",EDGE,"E7.10.4"),sQuery(id+"F0.wireOp",EDGE,"E7.10.5"),sQuery(id+"F0.wireOp",EDGE,"E7.11.0"),sQuery(id+"F0.wireOp",EDGE,"E7.11.1"),sQuery(id+"F0.wireOp",EDGE,"E7.11.2"),sQuery(id+"F0.wireOp",EDGE,"E7.11.3"),sQuery(id+"F0.wireOp",EDGE,"E7.11.4"),sQuery(id+"F0.wireOp",EDGE,"E7.11.5"),sQuery(id+"F0.wireOp",EDGE,"E7.12.0"),sQuery(id+"F0.wireOp",EDGE,"E7.12.1"),sQuery(id+"F0.wireOp",EDGE,"E7.12.2"),sQuery(id+"F0.wireOp",EDGE,"E7.12.3"),sQuery(id+"F0.wireOp",EDGE,"E7.12.4"),sQuery(id+"F0.wireOp",EDGE,"E7.12.5"),sQuery(id+"F0.wireOp",EDGE,"E7.13.0"),sQuery(id+"F0.wireOp",EDGE,"E7.13.1"),sQuery(id+"F0.wireOp",EDGE,"E7.13.2"),sQuery(id+"F0.wireOp",EDGE,"E7.13.3"),sQuery(id+"F0.wireOp",EDGE,"E7.13.4"),sQuery(id+"F0.wireOp",EDGE,"E7.13.5"),sQuery(id+"F0.wireOp",EDGE,"E7.14.0"),sQuery(id+"F0.wireOp",EDGE,"E7.14.1"),sQuery(id+"F0.wireOp",EDGE,"E7.14.2"),sQuery(id+"F0.wireOp",EDGE,"E7.14.3"),sQuery(id+"F0.wireOp",EDGE,"E7.14.4"),sQuery(id+"F0.wireOp",EDGE,"E7.14.5"),sQuery(id+"F0.wireOp",EDGE,"E7.15.0"),sQuery(id+"F0.wireOp",EDGE,"E7.15.1"),sQuery(id+"F0.wireOp",EDGE,"E7.15.2"),sQuery(id+"F0.wireOp",EDGE,"E7.15.3"),sQuery(id+"F0.wireOp",EDGE,"E7.15.4"),sQuery(id+"F0.wireOp",EDGE,"E7.15.5"),sQuery(id+"F0.wireOp",EDGE,"E7.16.0"),sQuery(id+"F0.wireOp",EDGE,"E7.16.1"),sQuery(id+"F0.wireOp",EDGE,"E7.16.2"),sQuery(id+"F0.wireOp",EDGE,"E7.16.3"),sQuery(id+"F0.wireOp",EDGE,"E7.16.4"),sQuery(id+"F0.wireOp",EDGE,"E7.16.5"),sQuery(id+"F0.wireOp",EDGE,"E7.17.0"),sQuery(id+"F0.wireOp",EDGE,"E7.17.1"),sQuery(id+"F0.wireOp",EDGE,"E7.17.2"),sQuery(id+"F0.wireOp",EDGE,"E7.17.3"),sQuery(id+"F0.wireOp",EDGE,"E7.17.4"),sQuery(id+"F0.wireOp",EDGE,"E7.17.5"),sQuery(id+"F0.wireOp",EDGE,"E7.18.0"),sQuery(id+"F0.wireOp",EDGE,"E7.18.1"),sQuery(id+"F0.wireOp",EDGE,"E7.18.2"),sQuery(id+"F0.wireOp",EDGE,"E7.18.3"),sQuery(id+"F0.wireOp",EDGE,"E7.18.4"),sQuery(id+"F0.wireOp",EDGE,"E7.18.5"),sQuery(id+"F0.wireOp",EDGE,"E7.19.0"),sQuery(id+"F0.wireOp",EDGE,"E7.19.1"),sQuery(id+"F0.wireOp",EDGE,"E7.19.2"),sQuery(id+"F0.wireOp",EDGE,"E7.19.3"),sQuery(id+"F0.wireOp",EDGE,"E7.19.4"),sQuery(id+"F0.wireOp",EDGE,"E7.19.5"),sQuery(id+"F0.wireOp",EDGE,"E7.20.0"),sQuery(id+"F0.wireOp",EDGE,"E7.20.1"),sQuery(id+"F0.wireOp",EDGE,"E7.20.2"),sQuery(id+"F0.wireOp",EDGE,"E7.20.3"),sQuery(id+"F0.wireOp",EDGE,"E7.20.4"),sQuery(id+"F0.wireOp",EDGE,"E7.20.5"),sQuery(id+"F0.wireOp",EDGE,"E7.21.0"),sQuery(id+"F0.wireOp",EDGE,"E7.21.1"),sQuery(id+"F0.wireOp",EDGE,"E7.21.2"),sQuery(id+"F0.wireOp",EDGE,"E7.21.3"),sQuery(id+"F0.wireOp",EDGE,"E7.21.4"),sQuery(id+"F0.wireOp",EDGE,"E7.21.5"),sQuery(id+"F0.wireOp",EDGE,"E7.22.0"),sQuery(id+"F0.wireOp",EDGE,"E7.22.1"),sQuery(id+"F0.wireOp",EDGE,"E7.22.2"),sQuery(id+"F0.wireOp",EDGE,"E7.22.3"),sQuery(id+"F0.wireOp",EDGE,"E7.22.4"),sQuery(id+"F0.wireOp",EDGE,"E7.22.5"),sQuery(id+"F0.wireOp",EDGE,"E7.23.0"),sQuery(id+"F0.wireOp",EDGE,"E7.23.1"),sQuery(id+"F0.wireOp",EDGE,"E7.23.2"),sQuery(id+"F0.wireOp",EDGE,"E7.23.3"),sQuery(id+"F0.wireOp",EDGE,"E7.23.4"),sQuery(id+"F0.wireOp",EDGE,"E7.23.5"),sQuery(id+"F0.wireOp",EDGE,"E7.24.0"),sQuery(id+"F0.wireOp",EDGE,"E7.24.1"),sQuery(id+"F0.wireOp",EDGE,"E7.24.2"),sQuery(id+"F0.wireOp",EDGE,"E7.24.3"),sQuery(id+"F0.wireOp",EDGE,"E7.24.4"),sQuery(id+"F0.wireOp",EDGE,"E7.24.5"),sQuery(id+"F0.wireOp",EDGE,"E7.25.0"),sQuery(id+"F0.wireOp",EDGE,"E7.25.1"),sQuery(id+"F0.wireOp",EDGE,"E7.25.2"),sQuery(id+"F0.wireOp",EDGE,"E7.25.3"),sQuery(id+"F0.wireOp",EDGE,"E7.25.4"),sQuery(id+"F0.wireOp",EDGE,"E7.25.5"),sQuery(id+"F0.wireOp",EDGE,"E7.26.0"),sQuery(id+"F0.wireOp",EDGE,"E7.26.1"),sQuery(id+"F0.wireOp",EDGE,"E7.26.2"),sQuery(id+"F0.wireOp",EDGE,"E7.26.3"),sQuery(id+"F0.wireOp",EDGE,"E7.26.4"),sQuery(id+"F0.wireOp",EDGE,"E7.26.5"),sQuery(id+"F0.wireOp",EDGE,"E7.27.0"),sQuery(id+"F0.wireOp",EDGE,"E7.27.1"),sQuery(id+"F0.wireOp",EDGE,"E7.27.2"),sQuery(id+"F0.wireOp",EDGE,"E7.27.3"),sQuery(id+"F0.wireOp",EDGE,"E7.27.4"),sQuery(id+"F0.wireOp",EDGE,"E7.27.5"),sQuery(id+"F0.wireOp",EDGE,"E7.28.0"),sQuery(id+"F0.wireOp",EDGE,"E7.28.1"),sQuery(id+"F0.wireOp",EDGE,"E7.28.2"),sQuery(id+"F0.wireOp",EDGE,"E7.28.3"),sQuery(id+"F0.wireOp",EDGE,"E7.28.4"),sQuery(id+"F0.wireOp",EDGE,"E7.28.5"),sQuery(id+"F0.wireOp",EDGE,"E7.29.0"),sQuery(id+"F0.wireOp",EDGE,"E7.29.1"),sQuery(id+"F0.wireOp",EDGE,"E7.29.2"),sQuery(id+"F0.wireOp",EDGE,"E7.29.3"),sQuery(id+"F0.wireOp",EDGE,"E7.29.4"),sQuery(id+"F0.wireOp",EDGE,"E7.29.5"),sQuery(id+"F0.wireOp",EDGE,"E7.30.0"),sQuery(id+"F0.wireOp",EDGE,"E7.30.1"),sQuery(id+"F0.wireOp",EDGE,"E7.30.2"),sQuery(id+"F0.wireOp",EDGE,"E7.30.3"),sQuery(id+"F0.wireOp",EDGE,"E7.30.4"),sQuery(id+"F0.wireOp",EDGE,"E7.30.5"),sQuery(id+"F0.wireOp",EDGE,"E7.31.0"),sQuery(id+"F0.wireOp",EDGE,"E7.31.1"),sQuery(id+"F0.wireOp",EDGE,"E7.31.2"),sQuery(id+"F0.wireOp",EDGE,"E7.31.3"),sQuery(id+"F0.wireOp",EDGE,"E7.31.4"),sQuery(id+"F0.wireOp",EDGE,"E7.31.5"),sQuery(id+"F0.wireOp",EDGE,"E7.32.0"),sQuery(id+"F0.wireOp",EDGE,"E7.32.1"),sQuery(id+"F0.wireOp",EDGE,"E7.32.2"),sQuery(id+"F0.wireOp",EDGE,"E7.32.3"),sQuery(id+"F0.wireOp",EDGE,"E7.32.4"),sQuery(id+"F0.wireOp",EDGE,"E7.32.5"),sQuery(id+"F0.wireOp",EDGE,"E7.33.0"),sQuery(id+"F0.wireOp",EDGE,"E7.33.1"),sQuery(id+"F0.wireOp",EDGE,"E7.33.2"),sQuery(id+"F0.wireOp",EDGE,"E7.33.3"),sQuery(id+"F0.wireOp",EDGE,"E7.33.4"),sQuery(id+"F0.wireOp",EDGE,"E7.33.5"),sQuery(id+"F0.wireOp",EDGE,"E7.34.0"),sQuery(id+"F0.wireOp",EDGE,"E7.34.1"),sQuery(id+"F0.wireOp",EDGE,"E7.34.2"),sQuery(id+"F0.wireOp",EDGE,"E7.34.3"),sQuery(id+"F0.wireOp",EDGE,"E7.34.4"),sQuery(id+"F0.wireOp",EDGE,"E7.34.5"),sQuery(id+"F0.wireOp",EDGE,"E7.35.0"),sQuery(id+"F0.wireOp",EDGE,"E7.35.1"),sQuery(id+"F0.wireOp",EDGE,"E7.35.2"),sQuery(id+"F0.wireOp",EDGE,"E7.35.3"),sQuery(id+"F0.wireOp",EDGE,"E7.35.4"),sQuery(id+"F0.wireOp",EDGE,"E7.35.5"),sQuery(id+"F0.wireOp",EDGE,"E7.36.0"),sQuery(id+"F0.wireOp",EDGE,"E7.36.1"),sQuery(id+"F0.wireOp",EDGE,"E7.36.2"),sQuery(id+"F0.wireOp",EDGE,"E7.36.3"),sQuery(id+"F0.wireOp",EDGE,"E7.36.4"),sQuery(id+"F0.wireOp",EDGE,"E7.36.5"),sQuery(id+"F0.wireOp",EDGE,"E7.37.0"),sQuery(id+"F0.wireOp",EDGE,"E7.37.1"),sQuery(id+"F0.wireOp",EDGE,"E7.37.2"),sQuery(id+"F0.wireOp",EDGE,"E7.37.3"),sQuery(id+"F0.wireOp",EDGE,"E7.37.4"),sQuery(id+"F0.wireOp",EDGE,"E7.37.5"),sQuery(id+"F0.wireOp",EDGE,"E7.38.0"),sQuery(id+"F0.wireOp",EDGE,"E7.38.1"),sQuery(id+"F0.wireOp",EDGE,"E7.38.2"),sQuery(id+"F0.wireOp",EDGE,"E7.38.3"),sQuery(id+"F0.wireOp",EDGE,"E7.38.4"),sQuery(id+"F0.wireOp",EDGE,"E7.38.5"),sQuery(id+"F0.wireOp",EDGE,"E7.39.0"),sQuery(id+"F0.wireOp",EDGE,"E7.39.1"),sQuery(id+"F0.wireOp",EDGE,"E7.39.2"),sQuery(id+"F0.wireOp",EDGE,"E7.39.3"),sQuery(id+"F0.wireOp",EDGE,"E7.39.4"),sQuery(id+"F0.wireOp",EDGE,"E7.39.5"),sQuery(id+"F0.wireOp",EDGE,"E7.40.0"),sQuery(id+"F0.wireOp",EDGE,"E7.40.1"),sQuery(id+"F0.wireOp",EDGE,"E7.40.2"),sQuery(id+"F0.wireOp",EDGE,"E7.40.3"),sQuery(id+"F0.wireOp",EDGE,"E7.40.4"),sQuery(id+"F0.wireOp",EDGE,"E7.40.5"),sQuery(id+"F0.wireOp",EDGE,"E7.41.0"),sQuery(id+"F0.wireOp",EDGE,"E7.41.1"),sQuery(id+"F0.wireOp",EDGE,"E7.41.2"),sQuery(id+"F0.wireOp",EDGE,"E7.41.3"),sQuery(id+"F0.wireOp",EDGE,"E7.41.4"),sQuery(id+"F0.wireOp",EDGE,"E7.41.5"),sQuery(id+"F0.wireOp",EDGE,"E7.42.0"),sQuery(id+"F0.wireOp",EDGE,"E7.42.1"),sQuery(id+"F0.wireOp",EDGE,"E7.42.2"),sQuery(id+"F0.wireOp",EDGE,"E7.42.3"),sQuery(id+"F0.wireOp",EDGE,"E7.42.4"),sQuery(id+"F0.wireOp",EDGE,"E7.42.5"),subQ0,sQuery(id+"F0.wireOp",EDGE,"E7.43.1"),sQuery(id+"F0.wireOp",EDGE,"E7.43.2"),sQuery(id+"F0.wireOp",EDGE,"E7.43.3"),sQuery(id+"F0.wireOp",EDGE,"E7.43.4"),sQuery(id+"F0.wireOp",EDGE,"E7.43.5")])],"isStart":false})],"blendedInto":[makeQuery(id+"F1.opExtrude","CAP_FACE",FACE,{"disambiguationData":[OSD([sQuery(id+"F0.wireOp",EDGE,"E1"),sQuery(id+"F0.wireOp",EDGE,"E2"),sQuery(id+"F0.wireOp",EDGE,"E3"),sQuery(id+"F0.wireOp",EDGE,"E4"),sQuery(id+"F0.wireOp",EDGE,"E5"),sQuery(id+"F0.wireOp",EDGE,"E6"),sQuery(id+"F0.wireOp",EDGE,"E7.1.0"),sQuery(id+"F0.wireOp",EDGE,"E7.1.1"),sQuery(id+"F0.wireOp",EDGE,"E7.1.2"),sQuery(id+"F0.wireOp",EDGE,"E7.1.3"),sQuery(id+"F0.wireOp",EDGE,"E7.1.4"),sQuery(id+"F0.wireOp",EDGE,"E7.1.5"),sQuery(id+"F0.wireOp",EDGE,"E7.2.0"),sQuery(id+"F0.wireOp",EDGE,"E7.2.1"),sQuery(id+"F0.wireOp",EDGE,"E7.2.2"),sQuery(id+"F0.wireOp",EDGE,"E7.2.3"),sQuery(id+"F0.wireOp",EDGE,"E7.2.4"),sQuery(id+"F0.wireOp",EDGE,"E7.2.5"),sQuery(id+"F0.wireOp",EDGE,"E7.3.0"),sQuery(id+"F0.wireOp",EDGE,"E7.3.1"),sQuery(id+"F0.wireOp",EDGE,"E7.3.2"),sQuery(id+"F0.wireOp",EDGE,"E7.3.3"),sQuery(id+"F0.wireOp",EDGE,"E7.3.4"),sQuery(id+"F0.wireOp",EDGE,"E7.3.5"),sQuery(id+"F0.wireOp",EDGE,"E7.4.0"),sQuery(id+"F0.wireOp",EDGE,"E7.4.1"),sQuery(id+"F0.wireOp",EDGE,"E7.4.2"),sQuery(id+"F0.wireOp",EDGE,"E7.4.3"),sQuery(id+"F0.wireOp",EDGE,"E7.4.4"),sQuery(id+"F0.wireOp",EDGE,"E7.4.5"),sQuery(id+"F0.wireOp",EDGE,"E7.5.0"),sQuery(id+"F0.wireOp",EDGE,"E7.5.1"),sQuery(id+"F0.wireOp",EDGE,"E7.5.2"),sQuery(id+"F0.wireOp",EDGE,"E7.5.3"),sQuery(id+"F0.wireOp",EDGE,"E7.5.4"),sQuery(id+"F0.wireOp",EDGE,"E7.5.5"),sQuery(id+"F0.wireOp",EDGE,"E7.6.0"),sQuery(id+"F0.wireOp",EDGE,"E7.6.1"),sQuery(id+"F0.wireOp",EDGE,"E7.6.2"),sQuery(id+"F0.wireOp",EDGE,"E7.6.3"),sQuery(id+"F0.wireOp",EDGE,"E7.6.4"),sQuery(id+"F0.wireOp",EDGE,"E7.6.5"),sQuery(id+"F0.wireOp",EDGE,"E7.7.0"),sQuery(id+"F0.wireOp",EDGE,"E7.7.1"),sQuery(id+"F0.wireOp",EDGE,"E7.7.2"),sQuery(id+"F0.wireOp",EDGE,"E7.7.3"),sQuery(id+"F0.wireOp",EDGE,"E7.7.4"),sQuery(id+"F0.wireOp",EDGE,"E7.7.5"),sQuery(id+"F0.wireOp",EDGE,"E7.8.0"),sQuery(id+"F0.wireOp",EDGE,"E7.8.1"),sQuery(id+"F0.wireOp",EDGE,"E7.8.2"),sQuery(id+"F0.wireOp",EDGE,"E7.8.3"),sQuery(id+"F0.wireOp",EDGE,"E7.8.4"),sQuery(id+"F0.wireOp",EDGE,"E7.8.5"),sQuery(id+"F0.wireOp",EDGE,"E7.9.0"),sQuery(id+"F0.wireOp",EDGE,"E7.9.1"),sQuery(id+"F0.wireOp",EDGE,"E7.9.2"),sQuery(id+"F0.wireOp",EDGE,"E7.9.3"),sQuery(id+"F0.wireOp",EDGE,"E7.9.4"),sQuery(id+"F0.wireOp",EDGE,"E7.9.5"),sQuery(id+"F0.wireOp",EDGE,"E7.10.0"),sQuery(id+"F0.wireOp",EDGE,"E7.10.1"),sQuery(id+"F0.wireOp",EDGE,"E7.10.2"),sQuery(id+"F0.wireOp",EDGE,"E7.10.3"),sQuery(id+"F0.wireOp",EDGE,"E7.10.4"),sQuery(id+"F0.wireOp",EDGE,"E7.10.5"),sQuery(id+"F0.wireOp",EDGE,"E7.11.0"),sQuery(id+"F0.wireOp",EDGE,"E7.11.1"),sQuery(id+"F0.wireOp",EDGE,"E7.11.2"),sQuery(id+"F0.wireOp",EDGE,"E7.11.3"),sQuery(id+"F0.wireOp",EDGE,"E7.11.4"),sQuery(id+"F0.wireOp",EDGE,"E7.11.5"),sQuery(id+"F0.wireOp",EDGE,"E7.12.0"),sQuery(id+"F0.wireOp",EDGE,"E7.12.1"),sQuery(id+"F0.wireOp",EDGE,"E7.12.2"),sQuery(id+"F0.wireOp",EDGE,"E7.12.3"),sQuery(id+"F0.wireOp",EDGE,"E7.12.4"),sQuery(id+"F0.wireOp",EDGE,"E7.12.5"),sQuery(id+"F0.wireOp",EDGE,"E7.13.0"),sQuery(id+"F0.wireOp",EDGE,"E7.13.1"),sQuery(id+"F0.wireOp",EDGE,"E7.13.2"),sQuery(id+"F0.wireOp",EDGE,"E7.13.3"),sQuery(id+"F0.wireOp",EDGE,"E7.13.4"),sQuery(id+"F0.wireOp",EDGE,"E7.13.5"),sQuery(id+"F0.wireOp",EDGE,"E7.14.0"),sQuery(id+"F0.wireOp",EDGE,"E7.14.1"),sQuery(id+"F0.wireOp",EDGE,"E7.14.2"),sQuery(id+"F0.wireOp",EDGE,"E7.14.3"),sQuery(id+"F0.wireOp",EDGE,"E7.14.4"),sQuery(id+"F0.wireOp",EDGE,"E7.14.5"),sQuery(id+"F0.wireOp",EDGE,"E7.15.0"),sQuery(id+"F0.wireOp",EDGE,"E7.15.1"),sQuery(id+"F0.wireOp",EDGE,"E7.15.2"),sQuery(id+"F0.wireOp",EDGE,"E7.15.3"),sQuery(id+"F0.wireOp",EDGE,"E7.15.4"),sQuery(id+"F0.wireOp",EDGE,"E7.15.5"),sQuery(id+"F0.wireOp",EDGE,"E7.16.0"),sQuery(id+"F0.wireOp",EDGE,"E7.16.1"),sQuery(id+"F0.wireOp",EDGE,"E7.16.2"),sQuery(id+"F0.wireOp",EDGE,"E7.16.3"),sQuery(id+"F0.wireOp",EDGE,"E7.16.4"),sQuery(id+"F0.wireOp",EDGE,"E7.16.5"),sQuery(id+"F0.wireOp",EDGE,"E7.17.0"),sQuery(id+"F0.wireOp",EDGE,"E7.17.1"),sQuery(id+"F0.wireOp",EDGE,"E7.17.2"),sQuery(id+"F0.wireOp",EDGE,"E7.17.3"),sQuery(id+"F0.wireOp",EDGE,"E7.17.4"),sQuery(id+"F0.wireOp",EDGE,"E7.17.5"),sQuery(id+"F0.wireOp",EDGE,"E7.18.0"),sQuery(id+"F0.wireOp",EDGE,"E7.18.1"),sQuery(id+"F0.wireOp",EDGE,"E7.18.2"),sQuery(id+"F0.wireOp",EDGE,"E7.18.3"),sQuery(id+"F0.wireOp",EDGE,"E7.18.4"),sQuery(id+"F0.wireOp",EDGE,"E7.18.5"),sQuery(id+"F0.wireOp",EDGE,"E7.19.0"),sQuery(id+"F0.wireOp",EDGE,"E7.19.1"),sQuery(id+"F0.wireOp",EDGE,"E7.19.2"),sQuery(id+"F0.wireOp",EDGE,"E7.19.3"),sQuery(id+"F0.wireOp",EDGE,"E7.19.4"),sQuery(id+"F0.wireOp",EDGE,"E7.19.5"),sQuery(id+"F0.wireOp",EDGE,"E7.20.0"),sQuery(id+"F0.wireOp",EDGE,"E7.20.1"),sQuery(id+"F0.wireOp",EDGE,"E7.20.2"),sQuery(id+"F0.wireOp",EDGE,"E7.20.3"),sQuery(id+"F0.wireOp",EDGE,"E7.20.4"),sQuery(id+"F0.wireOp",EDGE,"E7.20.5"),sQuery(id+"F0.wireOp",EDGE,"E7.21.0"),sQuery(id+"F0.wireOp",EDGE,"E7.21.1"),sQuery(id+"F0.wireOp",EDGE,"E7.21.2"),sQuery(id+"F0.wireOp",EDGE,"E7.21.3"),sQuery(id+"F0.wireOp",EDGE,"E7.21.4"),sQuery(id+"F0.wireOp",EDGE,"E7.21.5"),sQuery(id+"F0.wireOp",EDGE,"E7.22.0"),sQuery(id+"F0.wireOp",EDGE,"E7.22.1"),sQuery(id+"F0.wireOp",EDGE,"E7.22.2"),sQuery(id+"F0.wireOp",EDGE,"E7.22.3"),sQuery(id+"F0.wireOp",EDGE,"E7.22.4"),sQuery(id+"F0.wireOp",EDGE,"E7.22.5"),sQuery(id+"F0.wireOp",EDGE,"E7.23.0"),sQuery(id+"F0.wireOp",EDGE,"E7.23.1"),sQuery(id+"F0.wireOp",EDGE,"E7.23.2"),sQuery(id+"F0.wireOp",EDGE,"E7.23.3"),sQuery(id+"F0.wireOp",EDGE,"E7.23.4"),sQuery(id+"F0.wireOp",EDGE,"E7.23.5"),sQuery(id+"F0.wireOp",EDGE,"E7.24.0"),sQuery(id+"F0.wireOp",EDGE,"E7.24.1"),sQuery(id+"F0.wireOp",EDGE,"E7.24.2"),sQuery(id+"F0.wireOp",EDGE,"E7.24.3"),sQuery(id+"F0.wireOp",EDGE,"E7.24.4"),sQuery(id+"F0.wireOp",EDGE,"E7.24.5"),sQuery(id+"F0.wireOp",EDGE,"E7.25.0"),sQuery(id+"F0.wireOp",EDGE,"E7.25.1"),sQuery(id+"F0.wireOp",EDGE,"E7.25.2"),sQuery(id+"F0.wireOp",EDGE,"E7.25.3"),sQuery(id+"F0.wireOp",EDGE,"E7.25.4"),sQuery(id+"F0.wireOp",EDGE,"E7.25.5"),sQuery(id+"F0.wireOp",EDGE,"E7.26.0"),sQuery(id+"F0.wireOp",EDGE,"E7.26.1"),sQuery(id+"F0.wireOp",EDGE,"E7.26.2"),sQuery(id+"F0.wireOp",EDGE,"E7.26.3"),sQuery(id+"F0.wireOp",EDGE,"E7.26.4"),sQuery(id+"F0.wireOp",EDGE,"E7.26.5"),sQuery(id+"F0.wireOp",EDGE,"E7.27.0"),sQuery(id+"F0.wireOp",EDGE,"E7.27.1"),sQuery(id+"F0.wireOp",EDGE,"E7.27.2"),sQuery(id+"F0.wireOp",EDGE,"E7.27.3"),sQuery(id+"F0.wireOp",EDGE,"E7.27.4"),sQuery(id+"F0.wireOp",EDGE,"E7.27.5"),sQuery(id+"F0.wireOp",EDGE,"E7.28.0"),sQuery(id+"F0.wireOp",EDGE,"E7.28.1"),sQuery(id+"F0.wireOp",EDGE,"E7.28.2"),sQuery(id+"F0.wireOp",EDGE,"E7.28.3"),sQuery(id+"F0.wireOp",EDGE,"E7.28.4"),sQuery(id+"F0.wireOp",EDGE,"E7.28.5"),sQuery(id+"F0.wireOp",EDGE,"E7.29.0"),sQuery(id+"F0.wireOp",EDGE,"E7.29.1"),sQuery(id+"F0.wireOp",EDGE,"E7.29.2"),sQuery(id+"F0.wireOp",EDGE,"E7.29.3"),sQuery(id+"F0.wireOp",EDGE,"E7.29.4"),sQuery(id+"F0.wireOp",EDGE,"E7.29.5"),sQuery(id+"F0.wireOp",EDGE,"E7.30.0"),sQuery(id+"F0.wireOp",EDGE,"E7.30.1"),sQuery(id+"F0.wireOp",EDGE,"E7.30.2"),sQuery(id+"F0.wireOp",EDGE,"E7.30.3"),sQuery(id+"F0.wireOp",EDGE,"E7.30.4"),sQuery(id+"F0.wireOp",EDGE,"E7.30.5"),sQuery(id+"F0.wireOp",EDGE,"E7.31.0"),sQuery(id+"F0.wireOp",EDGE,"E7.31.1"),sQuery(id+"F0.wireOp",EDGE,"E7.31.2"),sQuery(id+"F0.wireOp",EDGE,"E7.31.3"),sQuery(id+"F0.wireOp",EDGE,"E7.31.4"),sQuery(id+"F0.wireOp",EDGE,"E7.31.5"),sQuery(id+"F0.wireOp",EDGE,"E7.32.0"),sQuery(id+"F0.wireOp",EDGE,"E7.32.1"),sQuery(id+"F0.wireOp",EDGE,"E7.32.2"),sQuery(id+"F0.wireOp",EDGE,"E7.32.3"),sQuery(id+"F0.wireOp",EDGE,"E7.32.4"),sQuery(id+"F0.wireOp",EDGE,"E7.32.5"),sQuery(id+"F0.wireOp",EDGE,"E7.33.0"),sQuery(id+"F0.wireOp",EDGE,"E7.33.1"),sQuery(id+"F0.wireOp",EDGE,"E7.33.2"),sQuery(id+"F0.wireOp",EDGE,"E7.33.3"),sQuery(id+"F0.wireOp",EDGE,"E7.33.4"),sQuery(id+"F0.wireOp",EDGE,"E7.33.5"),sQuery(id+"F0.wireOp",EDGE,"E7.34.0"),sQuery(id+"F0.wireOp",EDGE,"E7.34.1"),sQuery(id+"F0.wireOp",EDGE,"E7.34.2"),sQuery(id+"F0.wireOp",EDGE,"E7.34.3"),sQuery(id+"F0.wireOp",EDGE,"E7.34.4"),sQuery(id+"F0.wireOp",EDGE,"E7.34.5"),sQuery(id+"F0.wireOp",EDGE,"E7.35.0"),sQuery(id+"F0.wireOp",EDGE,"E7.35.1"),sQuery(id+"F0.wireOp",EDGE,"E7.35.2"),sQuery(id+"F0.wireOp",EDGE,"E7.35.3"),sQuery(id+"F0.wireOp",EDGE,"E7.35.4"),sQuery(id+"F0.wireOp",EDGE,"E7.35.5"),sQuery(id+"F0.wireOp",EDGE,"E7.36.0"),sQuery(id+"F0.wireOp",EDGE,"E7.36.1"),sQuery(id+"F0.wireOp",EDGE,"E7.36.2"),sQuery(id+"F0.wireOp",EDGE,"E7.36.3"),sQuery(id+"F0.wireOp",EDGE,"E7.36.4"),sQuery(id+"F0.wireOp",EDGE,"E7.36.5"),sQuery(id+"F0.wireOp",EDGE,"E7.37.0"),sQuery(id+"F0.wireOp",EDGE,"E7.37.1"),sQuery(id+"F0.wireOp",EDGE,"E7.37.2"),sQuery(id+"F0.wireOp",EDGE,"E7.37.3"),sQuery(id+"F0.wireOp",EDGE,"E7.37.4"),sQuery(id+"F0.wireOp",EDGE,"E7.37.5"),sQuery(id+"F0.wireOp",EDGE,"E7.38.0"),sQuery(id+"F0.wireOp",EDGE,"E7.38.1"),sQuery(id+"F0.wireOp",EDGE,"E7.38.2"),sQuery(id+"F0.wireOp",EDGE,"E7.38.3"),sQuery(id+"F0.wireOp",EDGE,"E7.38.4"),sQuery(id+"F0.wireOp",EDGE,"E7.38.5"),sQuery(id+"F0.wireOp",EDGE,"E7.39.0"),sQuery(id+"F0.wireOp",EDGE,"E7.39.1"),sQuery(id+"F0.wireOp",EDGE,"E7.39.2"),sQuery(id+"F0.wireOp",EDGE,"E7.39.3"),sQuery(id+"F0.wireOp",EDGE,"E7.39.4"),sQuery(id+"F0.wireOp",EDGE,"E7.39.5"),sQuery(id+"F0.wireOp",EDGE,"E7.40.0"),sQuery(id+"F0.wireOp",EDGE,"E7.40.1"),sQuery(id+"F0.wireOp",EDGE,"E7.40.2"),sQuery(id+"F0.wireOp",EDGE,"E7.40.3"),sQuery(id+"F0.wireOp",EDGE,"E7.40.4"),sQuery(id+"F0.wireOp",EDGE,"E7.40.5"),sQuery(id+"F0.wireOp",EDGE,"E7.41.0"),sQuery(id+"F0.wireOp",EDGE,"E7.41.1"),sQuery(id+"F0.wireOp",EDGE,"E7.41.2"),sQuery(id+"F0.wireOp",EDGE,"E7.41.3"),sQuery(id+"F0.wireOp",EDGE,"E7.41.4"),sQuery(id+"F0.wireOp",EDGE,"E7.41.5"),sQuery(id+"F0.wireOp",EDGE,"E7.42.0"),sQuery(id+"F0.wireOp",EDGE,"E7.42.1"),sQuery(id+"F0.wireOp",EDGE,"E7.42.2"),sQuery(id+"F0.wireOp",EDGE,"E7.42.3"),sQuery(id+"F0.wireOp",EDGE,"E7.42.4"),sQuery(id+"F0.wireOp",EDGE,"E7.42.5"),subQ0,sQuery(id+"F0.wireOp",EDGE,"E7.43.1"),sQuery(id+"F0.wireOp",EDGE,"E7.43.2"),sQuery(id+"F0.wireOp",EDGE,"E7.43.3"),sQuery(id+"F0.wireOp",EDGE,"E7.43.4"),sQuery(id+"F0.wireOp",EDGE,"E7.43.5")])],"isStart":false})]}),makeQuery(id+"F2.opChamfer","BLEND_FACE",FACE,{"disambiguationData":[OSD([subQ0])]})],"blendedInto":[makeQuery(id+"F2.opChamfer","BLEND_FACE",FACE,{"disambiguationData":[OSD([subQ0])]})]});}
            var Q2;
            {var subQ0=sQuery(id+"F0.wireOp",EDGE,"E7.41.0");Q2=makeQuery(id+"F8.opChamfer","BLEND_EDGE",EDGE,{"blendedFrom":[makeQuery(id+"F2.opChamfer","BLEND_EDGE",EDGE,{"blendedFrom":[makeQuery(id+"F1.opExtrude","CAP_EDGE",EDGE,{"disambiguationData":[OSD([subQ0])],"isStart":false}),makeQuery(id+"F1.opExtrude","CAP_FACE",FACE,{"disambiguationData":[OSD([sQuery(id+"F0.wireOp",EDGE,"E1"),sQuery(id+"F0.wireOp",EDGE,"E2"),sQuery(id+"F0.wireOp",EDGE,"E3"),sQuery(id+"F0.wireOp",EDGE,"E4"),sQuery(id+"F0.wireOp",EDGE,"E5"),sQuery(id+"F0.wireOp",EDGE,"E6"),sQuery(id+"F0.wireOp",EDGE,"E7.1.0"),sQuery(id+"F0.wireOp",EDGE,"E7.1.1"),sQuery(id+"F0.wireOp",EDGE,"E7.1.2"),sQuery(id+"F0.wireOp",EDGE,"E7.1.3"),sQuery(id+"F0.wireOp",EDGE,"E7.1.4"),sQuery(id+"F0.wireOp",EDGE,"E7.1.5"),sQuery(id+"F0.wireOp",EDGE,"E7.2.0"),sQuery(id+"F0.wireOp",EDGE,"E7.2.1"),sQuery(id+"F0.wireOp",EDGE,"E7.2.2"),sQuery(id+"F0.wireOp",EDGE,"E7.2.3"),sQuery(id+"F0.wireOp",EDGE,"E7.2.4"),sQuery(id+"F0.wireOp",EDGE,"E7.2.5"),sQuery(id+"F0.wireOp",EDGE,"E7.3.0"),sQuery(id+"F0.wireOp",EDGE,"E7.3.1"),sQuery(id+"F0.wireOp",EDGE,"E7.3.2"),sQuery(id+"F0.wireOp",EDGE,"E7.3.3"),sQuery(id+"F0.wireOp",EDGE,"E7.3.4"),sQuery(id+"F0.wireOp",EDGE,"E7.3.5"),sQuery(id+"F0.wireOp",EDGE,"E7.4.0"),sQuery(id+"F0.wireOp",EDGE,"E7.4.1"),sQuery(id+"F0.wireOp",EDGE,"E7.4.2"),sQuery(id+"F0.wireOp",EDGE,"E7.4.3"),sQuery(id+"F0.wireOp",EDGE,"E7.4.4"),sQuery(id+"F0.wireOp",EDGE,"E7.4.5"),sQuery(id+"F0.wireOp",EDGE,"E7.5.0"),sQuery(id+"F0.wireOp",EDGE,"E7.5.1"),sQuery(id+"F0.wireOp",EDGE,"E7.5.2"),sQuery(id+"F0.wireOp",EDGE,"E7.5.3"),sQuery(id+"F0.wireOp",EDGE,"E7.5.4"),sQuery(id+"F0.wireOp",EDGE,"E7.5.5"),sQuery(id+"F0.wireOp",EDGE,"E7.6.0"),sQuery(id+"F0.wireOp",EDGE,"E7.6.1"),sQuery(id+"F0.wireOp",EDGE,"E7.6.2"),sQuery(id+"F0.wireOp",EDGE,"E7.6.3"),sQuery(id+"F0.wireOp",EDGE,"E7.6.4"),sQuery(id+"F0.wireOp",EDGE,"E7.6.5"),sQuery(id+"F0.wireOp",EDGE,"E7.7.0"),sQuery(id+"F0.wireOp",EDGE,"E7.7.1"),sQuery(id+"F0.wireOp",EDGE,"E7.7.2"),sQuery(id+"F0.wireOp",EDGE,"E7.7.3"),sQuery(id+"F0.wireOp",EDGE,"E7.7.4"),sQuery(id+"F0.wireOp",EDGE,"E7.7.5"),sQuery(id+"F0.wireOp",EDGE,"E7.8.0"),sQuery(id+"F0.wireOp",EDGE,"E7.8.1"),sQuery(id+"F0.wireOp",EDGE,"E7.8.2"),sQuery(id+"F0.wireOp",EDGE,"E7.8.3"),sQuery(id+"F0.wireOp",EDGE,"E7.8.4"),sQuery(id+"F0.wireOp",EDGE,"E7.8.5"),sQuery(id+"F0.wireOp",EDGE,"E7.9.0"),sQuery(id+"F0.wireOp",EDGE,"E7.9.1"),sQuery(id+"F0.wireOp",EDGE,"E7.9.2"),sQuery(id+"F0.wireOp",EDGE,"E7.9.3"),sQuery(id+"F0.wireOp",EDGE,"E7.9.4"),sQuery(id+"F0.wireOp",EDGE,"E7.9.5"),sQuery(id+"F0.wireOp",EDGE,"E7.10.0"),sQuery(id+"F0.wireOp",EDGE,"E7.10.1"),sQuery(id+"F0.wireOp",EDGE,"E7.10.2"),sQuery(id+"F0.wireOp",EDGE,"E7.10.3"),sQuery(id+"F0.wireOp",EDGE,"E7.10.4"),sQuery(id+"F0.wireOp",EDGE,"E7.10.5"),sQuery(id+"F0.wireOp",EDGE,"E7.11.0"),sQuery(id+"F0.wireOp",EDGE,"E7.11.1"),sQuery(id+"F0.wireOp",EDGE,"E7.11.2"),sQuery(id+"F0.wireOp",EDGE,"E7.11.3"),sQuery(id+"F0.wireOp",EDGE,"E7.11.4"),sQuery(id+"F0.wireOp",EDGE,"E7.11.5"),sQuery(id+"F0.wireOp",EDGE,"E7.12.0"),sQuery(id+"F0.wireOp",EDGE,"E7.12.1"),sQuery(id+"F0.wireOp",EDGE,"E7.12.2"),sQuery(id+"F0.wireOp",EDGE,"E7.12.3"),sQuery(id+"F0.wireOp",EDGE,"E7.12.4"),sQuery(id+"F0.wireOp",EDGE,"E7.12.5"),sQuery(id+"F0.wireOp",EDGE,"E7.13.0"),sQuery(id+"F0.wireOp",EDGE,"E7.13.1"),sQuery(id+"F0.wireOp",EDGE,"E7.13.2"),sQuery(id+"F0.wireOp",EDGE,"E7.13.3"),sQuery(id+"F0.wireOp",EDGE,"E7.13.4"),sQuery(id+"F0.wireOp",EDGE,"E7.13.5"),sQuery(id+"F0.wireOp",EDGE,"E7.14.0"),sQuery(id+"F0.wireOp",EDGE,"E7.14.1"),sQuery(id+"F0.wireOp",EDGE,"E7.14.2"),sQuery(id+"F0.wireOp",EDGE,"E7.14.3"),sQuery(id+"F0.wireOp",EDGE,"E7.14.4"),sQuery(id+"F0.wireOp",EDGE,"E7.14.5"),sQuery(id+"F0.wireOp",EDGE,"E7.15.0"),sQuery(id+"F0.wireOp",EDGE,"E7.15.1"),sQuery(id+"F0.wireOp",EDGE,"E7.15.2"),sQuery(id+"F0.wireOp",EDGE,"E7.15.3"),sQuery(id+"F0.wireOp",EDGE,"E7.15.4"),sQuery(id+"F0.wireOp",EDGE,"E7.15.5"),sQuery(id+"F0.wireOp",EDGE,"E7.16.0"),sQuery(id+"F0.wireOp",EDGE,"E7.16.1"),sQuery(id+"F0.wireOp",EDGE,"E7.16.2"),sQuery(id+"F0.wireOp",EDGE,"E7.16.3"),sQuery(id+"F0.wireOp",EDGE,"E7.16.4"),sQuery(id+"F0.wireOp",EDGE,"E7.16.5"),sQuery(id+"F0.wireOp",EDGE,"E7.17.0"),sQuery(id+"F0.wireOp",EDGE,"E7.17.1"),sQuery(id+"F0.wireOp",EDGE,"E7.17.2"),sQuery(id+"F0.wireOp",EDGE,"E7.17.3"),sQuery(id+"F0.wireOp",EDGE,"E7.17.4"),sQuery(id+"F0.wireOp",EDGE,"E7.17.5"),sQuery(id+"F0.wireOp",EDGE,"E7.18.0"),sQuery(id+"F0.wireOp",EDGE,"E7.18.1"),sQuery(id+"F0.wireOp",EDGE,"E7.18.2"),sQuery(id+"F0.wireOp",EDGE,"E7.18.3"),sQuery(id+"F0.wireOp",EDGE,"E7.18.4"),sQuery(id+"F0.wireOp",EDGE,"E7.18.5"),sQuery(id+"F0.wireOp",EDGE,"E7.19.0"),sQuery(id+"F0.wireOp",EDGE,"E7.19.1"),sQuery(id+"F0.wireOp",EDGE,"E7.19.2"),sQuery(id+"F0.wireOp",EDGE,"E7.19.3"),sQuery(id+"F0.wireOp",EDGE,"E7.19.4"),sQuery(id+"F0.wireOp",EDGE,"E7.19.5"),sQuery(id+"F0.wireOp",EDGE,"E7.20.0"),sQuery(id+"F0.wireOp",EDGE,"E7.20.1"),sQuery(id+"F0.wireOp",EDGE,"E7.20.2"),sQuery(id+"F0.wireOp",EDGE,"E7.20.3"),sQuery(id+"F0.wireOp",EDGE,"E7.20.4"),sQuery(id+"F0.wireOp",EDGE,"E7.20.5"),sQuery(id+"F0.wireOp",EDGE,"E7.21.0"),sQuery(id+"F0.wireOp",EDGE,"E7.21.1"),sQuery(id+"F0.wireOp",EDGE,"E7.21.2"),sQuery(id+"F0.wireOp",EDGE,"E7.21.3"),sQuery(id+"F0.wireOp",EDGE,"E7.21.4"),sQuery(id+"F0.wireOp",EDGE,"E7.21.5"),sQuery(id+"F0.wireOp",EDGE,"E7.22.0"),sQuery(id+"F0.wireOp",EDGE,"E7.22.1"),sQuery(id+"F0.wireOp",EDGE,"E7.22.2"),sQuery(id+"F0.wireOp",EDGE,"E7.22.3"),sQuery(id+"F0.wireOp",EDGE,"E7.22.4"),sQuery(id+"F0.wireOp",EDGE,"E7.22.5"),sQuery(id+"F0.wireOp",EDGE,"E7.23.0"),sQuery(id+"F0.wireOp",EDGE,"E7.23.1"),sQuery(id+"F0.wireOp",EDGE,"E7.23.2"),sQuery(id+"F0.wireOp",EDGE,"E7.23.3"),sQuery(id+"F0.wireOp",EDGE,"E7.23.4"),sQuery(id+"F0.wireOp",EDGE,"E7.23.5"),sQuery(id+"F0.wireOp",EDGE,"E7.24.0"),sQuery(id+"F0.wireOp",EDGE,"E7.24.1"),sQuery(id+"F0.wireOp",EDGE,"E7.24.2"),sQuery(id+"F0.wireOp",EDGE,"E7.24.3"),sQuery(id+"F0.wireOp",EDGE,"E7.24.4"),sQuery(id+"F0.wireOp",EDGE,"E7.24.5"),sQuery(id+"F0.wireOp",EDGE,"E7.25.0"),sQuery(id+"F0.wireOp",EDGE,"E7.25.1"),sQuery(id+"F0.wireOp",EDGE,"E7.25.2"),sQuery(id+"F0.wireOp",EDGE,"E7.25.3"),sQuery(id+"F0.wireOp",EDGE,"E7.25.4"),sQuery(id+"F0.wireOp",EDGE,"E7.25.5"),sQuery(id+"F0.wireOp",EDGE,"E7.26.0"),sQuery(id+"F0.wireOp",EDGE,"E7.26.1"),sQuery(id+"F0.wireOp",EDGE,"E7.26.2"),sQuery(id+"F0.wireOp",EDGE,"E7.26.3"),sQuery(id+"F0.wireOp",EDGE,"E7.26.4"),sQuery(id+"F0.wireOp",EDGE,"E7.26.5"),sQuery(id+"F0.wireOp",EDGE,"E7.27.0"),sQuery(id+"F0.wireOp",EDGE,"E7.27.1"),sQuery(id+"F0.wireOp",EDGE,"E7.27.2"),sQuery(id+"F0.wireOp",EDGE,"E7.27.3"),sQuery(id+"F0.wireOp",EDGE,"E7.27.4"),sQuery(id+"F0.wireOp",EDGE,"E7.27.5"),sQuery(id+"F0.wireOp",EDGE,"E7.28.0"),sQuery(id+"F0.wireOp",EDGE,"E7.28.1"),sQuery(id+"F0.wireOp",EDGE,"E7.28.2"),sQuery(id+"F0.wireOp",EDGE,"E7.28.3"),sQuery(id+"F0.wireOp",EDGE,"E7.28.4"),sQuery(id+"F0.wireOp",EDGE,"E7.28.5"),sQuery(id+"F0.wireOp",EDGE,"E7.29.0"),sQuery(id+"F0.wireOp",EDGE,"E7.29.1"),sQuery(id+"F0.wireOp",EDGE,"E7.29.2"),sQuery(id+"F0.wireOp",EDGE,"E7.29.3"),sQuery(id+"F0.wireOp",EDGE,"E7.29.4"),sQuery(id+"F0.wireOp",EDGE,"E7.29.5"),sQuery(id+"F0.wireOp",EDGE,"E7.30.0"),sQuery(id+"F0.wireOp",EDGE,"E7.30.1"),sQuery(id+"F0.wireOp",EDGE,"E7.30.2"),sQuery(id+"F0.wireOp",EDGE,"E7.30.3"),sQuery(id+"F0.wireOp",EDGE,"E7.30.4"),sQuery(id+"F0.wireOp",EDGE,"E7.30.5"),sQuery(id+"F0.wireOp",EDGE,"E7.31.0"),sQuery(id+"F0.wireOp",EDGE,"E7.31.1"),sQuery(id+"F0.wireOp",EDGE,"E7.31.2"),sQuery(id+"F0.wireOp",EDGE,"E7.31.3"),sQuery(id+"F0.wireOp",EDGE,"E7.31.4"),sQuery(id+"F0.wireOp",EDGE,"E7.31.5"),sQuery(id+"F0.wireOp",EDGE,"E7.32.0"),sQuery(id+"F0.wireOp",EDGE,"E7.32.1"),sQuery(id+"F0.wireOp",EDGE,"E7.32.2"),sQuery(id+"F0.wireOp",EDGE,"E7.32.3"),sQuery(id+"F0.wireOp",EDGE,"E7.32.4"),sQuery(id+"F0.wireOp",EDGE,"E7.32.5"),sQuery(id+"F0.wireOp",EDGE,"E7.33.0"),sQuery(id+"F0.wireOp",EDGE,"E7.33.1"),sQuery(id+"F0.wireOp",EDGE,"E7.33.2"),sQuery(id+"F0.wireOp",EDGE,"E7.33.3"),sQuery(id+"F0.wireOp",EDGE,"E7.33.4"),sQuery(id+"F0.wireOp",EDGE,"E7.33.5"),sQuery(id+"F0.wireOp",EDGE,"E7.34.0"),sQuery(id+"F0.wireOp",EDGE,"E7.34.1"),sQuery(id+"F0.wireOp",EDGE,"E7.34.2"),sQuery(id+"F0.wireOp",EDGE,"E7.34.3"),sQuery(id+"F0.wireOp",EDGE,"E7.34.4"),sQuery(id+"F0.wireOp",EDGE,"E7.34.5"),sQuery(id+"F0.wireOp",EDGE,"E7.35.0"),sQuery(id+"F0.wireOp",EDGE,"E7.35.1"),sQuery(id+"F0.wireOp",EDGE,"E7.35.2"),sQuery(id+"F0.wireOp",EDGE,"E7.35.3"),sQuery(id+"F0.wireOp",EDGE,"E7.35.4"),sQuery(id+"F0.wireOp",EDGE,"E7.35.5"),sQuery(id+"F0.wireOp",EDGE,"E7.36.0"),sQuery(id+"F0.wireOp",EDGE,"E7.36.1"),sQuery(id+"F0.wireOp",EDGE,"E7.36.2"),sQuery(id+"F0.wireOp",EDGE,"E7.36.3"),sQuery(id+"F0.wireOp",EDGE,"E7.36.4"),sQuery(id+"F0.wireOp",EDGE,"E7.36.5"),sQuery(id+"F0.wireOp",EDGE,"E7.37.0"),sQuery(id+"F0.wireOp",EDGE,"E7.37.1"),sQuery(id+"F0.wireOp",EDGE,"E7.37.2"),sQuery(id+"F0.wireOp",EDGE,"E7.37.3"),sQuery(id+"F0.wireOp",EDGE,"E7.37.4"),sQuery(id+"F0.wireOp",EDGE,"E7.37.5"),sQuery(id+"F0.wireOp",EDGE,"E7.38.0"),sQuery(id+"F0.wireOp",EDGE,"E7.38.1"),sQuery(id+"F0.wireOp",EDGE,"E7.38.2"),sQuery(id+"F0.wireOp",EDGE,"E7.38.3"),sQuery(id+"F0.wireOp",EDGE,"E7.38.4"),sQuery(id+"F0.wireOp",EDGE,"E7.38.5"),sQuery(id+"F0.wireOp",EDGE,"E7.39.0"),sQuery(id+"F0.wireOp",EDGE,"E7.39.1"),sQuery(id+"F0.wireOp",EDGE,"E7.39.2"),sQuery(id+"F0.wireOp",EDGE,"E7.39.3"),sQuery(id+"F0.wireOp",EDGE,"E7.39.4"),sQuery(id+"F0.wireOp",EDGE,"E7.39.5"),sQuery(id+"F0.wireOp",EDGE,"E7.40.0"),sQuery(id+"F0.wireOp",EDGE,"E7.40.1"),sQuery(id+"F0.wireOp",EDGE,"E7.40.2"),sQuery(id+"F0.wireOp",EDGE,"E7.40.3"),sQuery(id+"F0.wireOp",EDGE,"E7.40.4"),sQuery(id+"F0.wireOp",EDGE,"E7.40.5"),subQ0,sQuery(id+"F0.wireOp",EDGE,"E7.41.1"),sQuery(id+"F0.wireOp",EDGE,"E7.41.2"),sQuery(id+"F0.wireOp",EDGE,"E7.41.3"),sQuery(id+"F0.wireOp",EDGE,"E7.41.4"),sQuery(id+"F0.wireOp",EDGE,"E7.41.5"),sQuery(id+"F0.wireOp",EDGE,"E7.42.0"),sQuery(id+"F0.wireOp",EDGE,"E7.42.1"),sQuery(id+"F0.wireOp",EDGE,"E7.42.2"),sQuery(id+"F0.wireOp",EDGE,"E7.42.3"),sQuery(id+"F0.wireOp",EDGE,"E7.42.4"),sQuery(id+"F0.wireOp",EDGE,"E7.42.5"),sQuery(id+"F0.wireOp",EDGE,"E7.43.0"),sQuery(id+"F0.wireOp",EDGE,"E7.43.1"),sQuery(id+"F0.wireOp",EDGE,"E7.43.2"),sQuery(id+"F0.wireOp",EDGE,"E7.43.3"),sQuery(id+"F0.wireOp",EDGE,"E7.43.4"),sQuery(id+"F0.wireOp",EDGE,"E7.43.5")])],"isStart":false})],"blendedInto":[makeQuery(id+"F1.opExtrude","CAP_FACE",FACE,{"disambiguationData":[OSD([sQuery(id+"F0.wireOp",EDGE,"E1"),sQuery(id+"F0.wireOp",EDGE,"E2"),sQuery(id+"F0.wireOp",EDGE,"E3"),sQuery(id+"F0.wireOp",EDGE,"E4"),sQuery(id+"F0.wireOp",EDGE,"E5"),sQuery(id+"F0.wireOp",EDGE,"E6"),sQuery(id+"F0.wireOp",EDGE,"E7.1.0"),sQuery(id+"F0.wireOp",EDGE,"E7.1.1"),sQuery(id+"F0.wireOp",EDGE,"E7.1.2"),sQuery(id+"F0.wireOp",EDGE,"E7.1.3"),sQuery(id+"F0.wireOp",EDGE,"E7.1.4"),sQuery(id+"F0.wireOp",EDGE,"E7.1.5"),sQuery(id+"F0.wireOp",EDGE,"E7.2.0"),sQuery(id+"F0.wireOp",EDGE,"E7.2.1"),sQuery(id+"F0.wireOp",EDGE,"E7.2.2"),sQuery(id+"F0.wireOp",EDGE,"E7.2.3"),sQuery(id+"F0.wireOp",EDGE,"E7.2.4"),sQuery(id+"F0.wireOp",EDGE,"E7.2.5"),sQuery(id+"F0.wireOp",EDGE,"E7.3.0"),sQuery(id+"F0.wireOp",EDGE,"E7.3.1"),sQuery(id+"F0.wireOp",EDGE,"E7.3.2"),sQuery(id+"F0.wireOp",EDGE,"E7.3.3"),sQuery(id+"F0.wireOp",EDGE,"E7.3.4"),sQuery(id+"F0.wireOp",EDGE,"E7.3.5"),sQuery(id+"F0.wireOp",EDGE,"E7.4.0"),sQuery(id+"F0.wireOp",EDGE,"E7.4.1"),sQuery(id+"F0.wireOp",EDGE,"E7.4.2"),sQuery(id+"F0.wireOp",EDGE,"E7.4.3"),sQuery(id+"F0.wireOp",EDGE,"E7.4.4"),sQuery(id+"F0.wireOp",EDGE,"E7.4.5"),sQuery(id+"F0.wireOp",EDGE,"E7.5.0"),sQuery(id+"F0.wireOp",EDGE,"E7.5.1"),sQuery(id+"F0.wireOp",EDGE,"E7.5.2"),sQuery(id+"F0.wireOp",EDGE,"E7.5.3"),sQuery(id+"F0.wireOp",EDGE,"E7.5.4"),sQuery(id+"F0.wireOp",EDGE,"E7.5.5"),sQuery(id+"F0.wireOp",EDGE,"E7.6.0"),sQuery(id+"F0.wireOp",EDGE,"E7.6.1"),sQuery(id+"F0.wireOp",EDGE,"E7.6.2"),sQuery(id+"F0.wireOp",EDGE,"E7.6.3"),sQuery(id+"F0.wireOp",EDGE,"E7.6.4"),sQuery(id+"F0.wireOp",EDGE,"E7.6.5"),sQuery(id+"F0.wireOp",EDGE,"E7.7.0"),sQuery(id+"F0.wireOp",EDGE,"E7.7.1"),sQuery(id+"F0.wireOp",EDGE,"E7.7.2"),sQuery(id+"F0.wireOp",EDGE,"E7.7.3"),sQuery(id+"F0.wireOp",EDGE,"E7.7.4"),sQuery(id+"F0.wireOp",EDGE,"E7.7.5"),sQuery(id+"F0.wireOp",EDGE,"E7.8.0"),sQuery(id+"F0.wireOp",EDGE,"E7.8.1"),sQuery(id+"F0.wireOp",EDGE,"E7.8.2"),sQuery(id+"F0.wireOp",EDGE,"E7.8.3"),sQuery(id+"F0.wireOp",EDGE,"E7.8.4"),sQuery(id+"F0.wireOp",EDGE,"E7.8.5"),sQuery(id+"F0.wireOp",EDGE,"E7.9.0"),sQuery(id+"F0.wireOp",EDGE,"E7.9.1"),sQuery(id+"F0.wireOp",EDGE,"E7.9.2"),sQuery(id+"F0.wireOp",EDGE,"E7.9.3"),sQuery(id+"F0.wireOp",EDGE,"E7.9.4"),sQuery(id+"F0.wireOp",EDGE,"E7.9.5"),sQuery(id+"F0.wireOp",EDGE,"E7.10.0"),sQuery(id+"F0.wireOp",EDGE,"E7.10.1"),sQuery(id+"F0.wireOp",EDGE,"E7.10.2"),sQuery(id+"F0.wireOp",EDGE,"E7.10.3"),sQuery(id+"F0.wireOp",EDGE,"E7.10.4"),sQuery(id+"F0.wireOp",EDGE,"E7.10.5"),sQuery(id+"F0.wireOp",EDGE,"E7.11.0"),sQuery(id+"F0.wireOp",EDGE,"E7.11.1"),sQuery(id+"F0.wireOp",EDGE,"E7.11.2"),sQuery(id+"F0.wireOp",EDGE,"E7.11.3"),sQuery(id+"F0.wireOp",EDGE,"E7.11.4"),sQuery(id+"F0.wireOp",EDGE,"E7.11.5"),sQuery(id+"F0.wireOp",EDGE,"E7.12.0"),sQuery(id+"F0.wireOp",EDGE,"E7.12.1"),sQuery(id+"F0.wireOp",EDGE,"E7.12.2"),sQuery(id+"F0.wireOp",EDGE,"E7.12.3"),sQuery(id+"F0.wireOp",EDGE,"E7.12.4"),sQuery(id+"F0.wireOp",EDGE,"E7.12.5"),sQuery(id+"F0.wireOp",EDGE,"E7.13.0"),sQuery(id+"F0.wireOp",EDGE,"E7.13.1"),sQuery(id+"F0.wireOp",EDGE,"E7.13.2"),sQuery(id+"F0.wireOp",EDGE,"E7.13.3"),sQuery(id+"F0.wireOp",EDGE,"E7.13.4"),sQuery(id+"F0.wireOp",EDGE,"E7.13.5"),sQuery(id+"F0.wireOp",EDGE,"E7.14.0"),sQuery(id+"F0.wireOp",EDGE,"E7.14.1"),sQuery(id+"F0.wireOp",EDGE,"E7.14.2"),sQuery(id+"F0.wireOp",EDGE,"E7.14.3"),sQuery(id+"F0.wireOp",EDGE,"E7.14.4"),sQuery(id+"F0.wireOp",EDGE,"E7.14.5"),sQuery(id+"F0.wireOp",EDGE,"E7.15.0"),sQuery(id+"F0.wireOp",EDGE,"E7.15.1"),sQuery(id+"F0.wireOp",EDGE,"E7.15.2"),sQuery(id+"F0.wireOp",EDGE,"E7.15.3"),sQuery(id+"F0.wireOp",EDGE,"E7.15.4"),sQuery(id+"F0.wireOp",EDGE,"E7.15.5"),sQuery(id+"F0.wireOp",EDGE,"E7.16.0"),sQuery(id+"F0.wireOp",EDGE,"E7.16.1"),sQuery(id+"F0.wireOp",EDGE,"E7.16.2"),sQuery(id+"F0.wireOp",EDGE,"E7.16.3"),sQuery(id+"F0.wireOp",EDGE,"E7.16.4"),sQuery(id+"F0.wireOp",EDGE,"E7.16.5"),sQuery(id+"F0.wireOp",EDGE,"E7.17.0"),sQuery(id+"F0.wireOp",EDGE,"E7.17.1"),sQuery(id+"F0.wireOp",EDGE,"E7.17.2"),sQuery(id+"F0.wireOp",EDGE,"E7.17.3"),sQuery(id+"F0.wireOp",EDGE,"E7.17.4"),sQuery(id+"F0.wireOp",EDGE,"E7.17.5"),sQuery(id+"F0.wireOp",EDGE,"E7.18.0"),sQuery(id+"F0.wireOp",EDGE,"E7.18.1"),sQuery(id+"F0.wireOp",EDGE,"E7.18.2"),sQuery(id+"F0.wireOp",EDGE,"E7.18.3"),sQuery(id+"F0.wireOp",EDGE,"E7.18.4"),sQuery(id+"F0.wireOp",EDGE,"E7.18.5"),sQuery(id+"F0.wireOp",EDGE,"E7.19.0"),sQuery(id+"F0.wireOp",EDGE,"E7.19.1"),sQuery(id+"F0.wireOp",EDGE,"E7.19.2"),sQuery(id+"F0.wireOp",EDGE,"E7.19.3"),sQuery(id+"F0.wireOp",EDGE,"E7.19.4"),sQuery(id+"F0.wireOp",EDGE,"E7.19.5"),sQuery(id+"F0.wireOp",EDGE,"E7.20.0"),sQuery(id+"F0.wireOp",EDGE,"E7.20.1"),sQuery(id+"F0.wireOp",EDGE,"E7.20.2"),sQuery(id+"F0.wireOp",EDGE,"E7.20.3"),sQuery(id+"F0.wireOp",EDGE,"E7.20.4"),sQuery(id+"F0.wireOp",EDGE,"E7.20.5"),sQuery(id+"F0.wireOp",EDGE,"E7.21.0"),sQuery(id+"F0.wireOp",EDGE,"E7.21.1"),sQuery(id+"F0.wireOp",EDGE,"E7.21.2"),sQuery(id+"F0.wireOp",EDGE,"E7.21.3"),sQuery(id+"F0.wireOp",EDGE,"E7.21.4"),sQuery(id+"F0.wireOp",EDGE,"E7.21.5"),sQuery(id+"F0.wireOp",EDGE,"E7.22.0"),sQuery(id+"F0.wireOp",EDGE,"E7.22.1"),sQuery(id+"F0.wireOp",EDGE,"E7.22.2"),sQuery(id+"F0.wireOp",EDGE,"E7.22.3"),sQuery(id+"F0.wireOp",EDGE,"E7.22.4"),sQuery(id+"F0.wireOp",EDGE,"E7.22.5"),sQuery(id+"F0.wireOp",EDGE,"E7.23.0"),sQuery(id+"F0.wireOp",EDGE,"E7.23.1"),sQuery(id+"F0.wireOp",EDGE,"E7.23.2"),sQuery(id+"F0.wireOp",EDGE,"E7.23.3"),sQuery(id+"F0.wireOp",EDGE,"E7.23.4"),sQuery(id+"F0.wireOp",EDGE,"E7.23.5"),sQuery(id+"F0.wireOp",EDGE,"E7.24.0"),sQuery(id+"F0.wireOp",EDGE,"E7.24.1"),sQuery(id+"F0.wireOp",EDGE,"E7.24.2"),sQuery(id+"F0.wireOp",EDGE,"E7.24.3"),sQuery(id+"F0.wireOp",EDGE,"E7.24.4"),sQuery(id+"F0.wireOp",EDGE,"E7.24.5"),sQuery(id+"F0.wireOp",EDGE,"E7.25.0"),sQuery(id+"F0.wireOp",EDGE,"E7.25.1"),sQuery(id+"F0.wireOp",EDGE,"E7.25.2"),sQuery(id+"F0.wireOp",EDGE,"E7.25.3"),sQuery(id+"F0.wireOp",EDGE,"E7.25.4"),sQuery(id+"F0.wireOp",EDGE,"E7.25.5"),sQuery(id+"F0.wireOp",EDGE,"E7.26.0"),sQuery(id+"F0.wireOp",EDGE,"E7.26.1"),sQuery(id+"F0.wireOp",EDGE,"E7.26.2"),sQuery(id+"F0.wireOp",EDGE,"E7.26.3"),sQuery(id+"F0.wireOp",EDGE,"E7.26.4"),sQuery(id+"F0.wireOp",EDGE,"E7.26.5"),sQuery(id+"F0.wireOp",EDGE,"E7.27.0"),sQuery(id+"F0.wireOp",EDGE,"E7.27.1"),sQuery(id+"F0.wireOp",EDGE,"E7.27.2"),sQuery(id+"F0.wireOp",EDGE,"E7.27.3"),sQuery(id+"F0.wireOp",EDGE,"E7.27.4"),sQuery(id+"F0.wireOp",EDGE,"E7.27.5"),sQuery(id+"F0.wireOp",EDGE,"E7.28.0"),sQuery(id+"F0.wireOp",EDGE,"E7.28.1"),sQuery(id+"F0.wireOp",EDGE,"E7.28.2"),sQuery(id+"F0.wireOp",EDGE,"E7.28.3"),sQuery(id+"F0.wireOp",EDGE,"E7.28.4"),sQuery(id+"F0.wireOp",EDGE,"E7.28.5"),sQuery(id+"F0.wireOp",EDGE,"E7.29.0"),sQuery(id+"F0.wireOp",EDGE,"E7.29.1"),sQuery(id+"F0.wireOp",EDGE,"E7.29.2"),sQuery(id+"F0.wireOp",EDGE,"E7.29.3"),sQuery(id+"F0.wireOp",EDGE,"E7.29.4"),sQuery(id+"F0.wireOp",EDGE,"E7.29.5"),sQuery(id+"F0.wireOp",EDGE,"E7.30.0"),sQuery(id+"F0.wireOp",EDGE,"E7.30.1"),sQuery(id+"F0.wireOp",EDGE,"E7.30.2"),sQuery(id+"F0.wireOp",EDGE,"E7.30.3"),sQuery(id+"F0.wireOp",EDGE,"E7.30.4"),sQuery(id+"F0.wireOp",EDGE,"E7.30.5"),sQuery(id+"F0.wireOp",EDGE,"E7.31.0"),sQuery(id+"F0.wireOp",EDGE,"E7.31.1"),sQuery(id+"F0.wireOp",EDGE,"E7.31.2"),sQuery(id+"F0.wireOp",EDGE,"E7.31.3"),sQuery(id+"F0.wireOp",EDGE,"E7.31.4"),sQuery(id+"F0.wireOp",EDGE,"E7.31.5"),sQuery(id+"F0.wireOp",EDGE,"E7.32.0"),sQuery(id+"F0.wireOp",EDGE,"E7.32.1"),sQuery(id+"F0.wireOp",EDGE,"E7.32.2"),sQuery(id+"F0.wireOp",EDGE,"E7.32.3"),sQuery(id+"F0.wireOp",EDGE,"E7.32.4"),sQuery(id+"F0.wireOp",EDGE,"E7.32.5"),sQuery(id+"F0.wireOp",EDGE,"E7.33.0"),sQuery(id+"F0.wireOp",EDGE,"E7.33.1"),sQuery(id+"F0.wireOp",EDGE,"E7.33.2"),sQuery(id+"F0.wireOp",EDGE,"E7.33.3"),sQuery(id+"F0.wireOp",EDGE,"E7.33.4"),sQuery(id+"F0.wireOp",EDGE,"E7.33.5"),sQuery(id+"F0.wireOp",EDGE,"E7.34.0"),sQuery(id+"F0.wireOp",EDGE,"E7.34.1"),sQuery(id+"F0.wireOp",EDGE,"E7.34.2"),sQuery(id+"F0.wireOp",EDGE,"E7.34.3"),sQuery(id+"F0.wireOp",EDGE,"E7.34.4"),sQuery(id+"F0.wireOp",EDGE,"E7.34.5"),sQuery(id+"F0.wireOp",EDGE,"E7.35.0"),sQuery(id+"F0.wireOp",EDGE,"E7.35.1"),sQuery(id+"F0.wireOp",EDGE,"E7.35.2"),sQuery(id+"F0.wireOp",EDGE,"E7.35.3"),sQuery(id+"F0.wireOp",EDGE,"E7.35.4"),sQuery(id+"F0.wireOp",EDGE,"E7.35.5"),sQuery(id+"F0.wireOp",EDGE,"E7.36.0"),sQuery(id+"F0.wireOp",EDGE,"E7.36.1"),sQuery(id+"F0.wireOp",EDGE,"E7.36.2"),sQuery(id+"F0.wireOp",EDGE,"E7.36.3"),sQuery(id+"F0.wireOp",EDGE,"E7.36.4"),sQuery(id+"F0.wireOp",EDGE,"E7.36.5"),sQuery(id+"F0.wireOp",EDGE,"E7.37.0"),sQuery(id+"F0.wireOp",EDGE,"E7.37.1"),sQuery(id+"F0.wireOp",EDGE,"E7.37.2"),sQuery(id+"F0.wireOp",EDGE,"E7.37.3"),sQuery(id+"F0.wireOp",EDGE,"E7.37.4"),sQuery(id+"F0.wireOp",EDGE,"E7.37.5"),sQuery(id+"F0.wireOp",EDGE,"E7.38.0"),sQuery(id+"F0.wireOp",EDGE,"E7.38.1"),sQuery(id+"F0.wireOp",EDGE,"E7.38.2"),sQuery(id+"F0.wireOp",EDGE,"E7.38.3"),sQuery(id+"F0.wireOp",EDGE,"E7.38.4"),sQuery(id+"F0.wireOp",EDGE,"E7.38.5"),sQuery(id+"F0.wireOp",EDGE,"E7.39.0"),sQuery(id+"F0.wireOp",EDGE,"E7.39.1"),sQuery(id+"F0.wireOp",EDGE,"E7.39.2"),sQuery(id+"F0.wireOp",EDGE,"E7.39.3"),sQuery(id+"F0.wireOp",EDGE,"E7.39.4"),sQuery(id+"F0.wireOp",EDGE,"E7.39.5"),sQuery(id+"F0.wireOp",EDGE,"E7.40.0"),sQuery(id+"F0.wireOp",EDGE,"E7.40.1"),sQuery(id+"F0.wireOp",EDGE,"E7.40.2"),sQuery(id+"F0.wireOp",EDGE,"E7.40.3"),sQuery(id+"F0.wireOp",EDGE,"E7.40.4"),sQuery(id+"F0.wireOp",EDGE,"E7.40.5"),subQ0,sQuery(id+"F0.wireOp",EDGE,"E7.41.1"),sQuery(id+"F0.wireOp",EDGE,"E7.41.2"),sQuery(id+"F0.wireOp",EDGE,"E7.41.3"),sQuery(id+"F0.wireOp",EDGE,"E7.41.4"),sQuery(id+"F0.wireOp",EDGE,"E7.41.5"),sQuery(id+"F0.wireOp",EDGE,"E7.42.0"),sQuery(id+"F0.wireOp",EDGE,"E7.42.1"),sQuery(id+"F0.wireOp",EDGE,"E7.42.2"),sQuery(id+"F0.wireOp",EDGE,"E7.42.3"),sQuery(id+"F0.wireOp",EDGE,"E7.42.4"),sQuery(id+"F0.wireOp",EDGE,"E7.42.5"),sQuery(id+"F0.wireOp",EDGE,"E7.43.0"),sQuery(id+"F0.wireOp",EDGE,"E7.43.1"),sQuery(id+"F0.wireOp",EDGE,"E7.43.2"),sQuery(id+"F0.wireOp",EDGE,"E7.43.3"),sQuery(id+"F0.wireOp",EDGE,"E7.43.4"),sQuery(id+"F0.wireOp",EDGE,"E7.43.5")])],"isStart":false})]}),makeQuery(id+"F2.opChamfer","BLEND_FACE",FACE,{"disambiguationData":[OSD([subQ0])]})],"blendedInto":[makeQuery(id+"F2.opChamfer","BLEND_FACE",FACE,{"disambiguationData":[OSD([subQ0])]})]});}
            var Q3;
            {var subQ0=sQuery(id+"F0.wireOp",EDGE,"E7.39.0");Q3=makeQuery(id+"F8.opChamfer","BLEND_EDGE",EDGE,{"blendedFrom":[makeQuery(id+"F2.opChamfer","BLEND_EDGE",EDGE,{"blendedFrom":[makeQuery(id+"F1.opExtrude","CAP_EDGE",EDGE,{"disambiguationData":[OSD([subQ0])],"isStart":false}),makeQuery(id+"F1.opExtrude","CAP_FACE",FACE,{"disambiguationData":[OSD([sQuery(id+"F0.wireOp",EDGE,"E1"),sQuery(id+"F0.wireOp",EDGE,"E2"),sQuery(id+"F0.wireOp",EDGE,"E3"),sQuery(id+"F0.wireOp",EDGE,"E4"),sQuery(id+"F0.wireOp",EDGE,"E5"),sQuery(id+"F0.wireOp",EDGE,"E6"),sQuery(id+"F0.wireOp",EDGE,"E7.1.0"),sQuery(id+"F0.wireOp",EDGE,"E7.1.1"),sQuery(id+"F0.wireOp",EDGE,"E7.1.2"),sQuery(id+"F0.wireOp",EDGE,"E7.1.3"),sQuery(id+"F0.wireOp",EDGE,"E7.1.4"),sQuery(id+"F0.wireOp",EDGE,"E7.1.5"),sQuery(id+"F0.wireOp",EDGE,"E7.2.0"),sQuery(id+"F0.wireOp",EDGE,"E7.2.1"),sQuery(id+"F0.wireOp",EDGE,"E7.2.2"),sQuery(id+"F0.wireOp",EDGE,"E7.2.3"),sQuery(id+"F0.wireOp",EDGE,"E7.2.4"),sQuery(id+"F0.wireOp",EDGE,"E7.2.5"),sQuery(id+"F0.wireOp",EDGE,"E7.3.0"),sQuery(id+"F0.wireOp",EDGE,"E7.3.1"),sQuery(id+"F0.wireOp",EDGE,"E7.3.2"),sQuery(id+"F0.wireOp",EDGE,"E7.3.3"),sQuery(id+"F0.wireOp",EDGE,"E7.3.4"),sQuery(id+"F0.wireOp",EDGE,"E7.3.5"),sQuery(id+"F0.wireOp",EDGE,"E7.4.0"),sQuery(id+"F0.wireOp",EDGE,"E7.4.1"),sQuery(id+"F0.wireOp",EDGE,"E7.4.2"),sQuery(id+"F0.wireOp",EDGE,"E7.4.3"),sQuery(id+"F0.wireOp",EDGE,"E7.4.4"),sQuery(id+"F0.wireOp",EDGE,"E7.4.5"),sQuery(id+"F0.wireOp",EDGE,"E7.5.0"),sQuery(id+"F0.wireOp",EDGE,"E7.5.1"),sQuery(id+"F0.wireOp",EDGE,"E7.5.2"),sQuery(id+"F0.wireOp",EDGE,"E7.5.3"),sQuery(id+"F0.wireOp",EDGE,"E7.5.4"),sQuery(id+"F0.wireOp",EDGE,"E7.5.5"),sQuery(id+"F0.wireOp",EDGE,"E7.6.0"),sQuery(id+"F0.wireOp",EDGE,"E7.6.1"),sQuery(id+"F0.wireOp",EDGE,"E7.6.2"),sQuery(id+"F0.wireOp",EDGE,"E7.6.3"),sQuery(id+"F0.wireOp",EDGE,"E7.6.4"),sQuery(id+"F0.wireOp",EDGE,"E7.6.5"),sQuery(id+"F0.wireOp",EDGE,"E7.7.0"),sQuery(id+"F0.wireOp",EDGE,"E7.7.1"),sQuery(id+"F0.wireOp",EDGE,"E7.7.2"),sQuery(id+"F0.wireOp",EDGE,"E7.7.3"),sQuery(id+"F0.wireOp",EDGE,"E7.7.4"),sQuery(id+"F0.wireOp",EDGE,"E7.7.5"),sQuery(id+"F0.wireOp",EDGE,"E7.8.0"),sQuery(id+"F0.wireOp",EDGE,"E7.8.1"),sQuery(id+"F0.wireOp",EDGE,"E7.8.2"),sQuery(id+"F0.wireOp",EDGE,"E7.8.3"),sQuery(id+"F0.wireOp",EDGE,"E7.8.4"),sQuery(id+"F0.wireOp",EDGE,"E7.8.5"),sQuery(id+"F0.wireOp",EDGE,"E7.9.0"),sQuery(id+"F0.wireOp",EDGE,"E7.9.1"),sQuery(id+"F0.wireOp",EDGE,"E7.9.2"),sQuery(id+"F0.wireOp",EDGE,"E7.9.3"),sQuery(id+"F0.wireOp",EDGE,"E7.9.4"),sQuery(id+"F0.wireOp",EDGE,"E7.9.5"),sQuery(id+"F0.wireOp",EDGE,"E7.10.0"),sQuery(id+"F0.wireOp",EDGE,"E7.10.1"),sQuery(id+"F0.wireOp",EDGE,"E7.10.2"),sQuery(id+"F0.wireOp",EDGE,"E7.10.3"),sQuery(id+"F0.wireOp",EDGE,"E7.10.4"),sQuery(id+"F0.wireOp",EDGE,"E7.10.5"),sQuery(id+"F0.wireOp",EDGE,"E7.11.0"),sQuery(id+"F0.wireOp",EDGE,"E7.11.1"),sQuery(id+"F0.wireOp",EDGE,"E7.11.2"),sQuery(id+"F0.wireOp",EDGE,"E7.11.3"),sQuery(id+"F0.wireOp",EDGE,"E7.11.4"),sQuery(id+"F0.wireOp",EDGE,"E7.11.5"),sQuery(id+"F0.wireOp",EDGE,"E7.12.0"),sQuery(id+"F0.wireOp",EDGE,"E7.12.1"),sQuery(id+"F0.wireOp",EDGE,"E7.12.2"),sQuery(id+"F0.wireOp",EDGE,"E7.12.3"),sQuery(id+"F0.wireOp",EDGE,"E7.12.4"),sQuery(id+"F0.wireOp",EDGE,"E7.12.5"),sQuery(id+"F0.wireOp",EDGE,"E7.13.0"),sQuery(id+"F0.wireOp",EDGE,"E7.13.1"),sQuery(id+"F0.wireOp",EDGE,"E7.13.2"),sQuery(id+"F0.wireOp",EDGE,"E7.13.3"),sQuery(id+"F0.wireOp",EDGE,"E7.13.4"),sQuery(id+"F0.wireOp",EDGE,"E7.13.5"),sQuery(id+"F0.wireOp",EDGE,"E7.14.0"),sQuery(id+"F0.wireOp",EDGE,"E7.14.1"),sQuery(id+"F0.wireOp",EDGE,"E7.14.2"),sQuery(id+"F0.wireOp",EDGE,"E7.14.3"),sQuery(id+"F0.wireOp",EDGE,"E7.14.4"),sQuery(id+"F0.wireOp",EDGE,"E7.14.5"),sQuery(id+"F0.wireOp",EDGE,"E7.15.0"),sQuery(id+"F0.wireOp",EDGE,"E7.15.1"),sQuery(id+"F0.wireOp",EDGE,"E7.15.2"),sQuery(id+"F0.wireOp",EDGE,"E7.15.3"),sQuery(id+"F0.wireOp",EDGE,"E7.15.4"),sQuery(id+"F0.wireOp",EDGE,"E7.15.5"),sQuery(id+"F0.wireOp",EDGE,"E7.16.0"),sQuery(id+"F0.wireOp",EDGE,"E7.16.1"),sQuery(id+"F0.wireOp",EDGE,"E7.16.2"),sQuery(id+"F0.wireOp",EDGE,"E7.16.3"),sQuery(id+"F0.wireOp",EDGE,"E7.16.4"),sQuery(id+"F0.wireOp",EDGE,"E7.16.5"),sQuery(id+"F0.wireOp",EDGE,"E7.17.0"),sQuery(id+"F0.wireOp",EDGE,"E7.17.1"),sQuery(id+"F0.wireOp",EDGE,"E7.17.2"),sQuery(id+"F0.wireOp",EDGE,"E7.17.3"),sQuery(id+"F0.wireOp",EDGE,"E7.17.4"),sQuery(id+"F0.wireOp",EDGE,"E7.17.5"),sQuery(id+"F0.wireOp",EDGE,"E7.18.0"),sQuery(id+"F0.wireOp",EDGE,"E7.18.1"),sQuery(id+"F0.wireOp",EDGE,"E7.18.2"),sQuery(id+"F0.wireOp",EDGE,"E7.18.3"),sQuery(id+"F0.wireOp",EDGE,"E7.18.4"),sQuery(id+"F0.wireOp",EDGE,"E7.18.5"),sQuery(id+"F0.wireOp",EDGE,"E7.19.0"),sQuery(id+"F0.wireOp",EDGE,"E7.19.1"),sQuery(id+"F0.wireOp",EDGE,"E7.19.2"),sQuery(id+"F0.wireOp",EDGE,"E7.19.3"),sQuery(id+"F0.wireOp",EDGE,"E7.19.4"),sQuery(id+"F0.wireOp",EDGE,"E7.19.5"),sQuery(id+"F0.wireOp",EDGE,"E7.20.0"),sQuery(id+"F0.wireOp",EDGE,"E7.20.1"),sQuery(id+"F0.wireOp",EDGE,"E7.20.2"),sQuery(id+"F0.wireOp",EDGE,"E7.20.3"),sQuery(id+"F0.wireOp",EDGE,"E7.20.4"),sQuery(id+"F0.wireOp",EDGE,"E7.20.5"),sQuery(id+"F0.wireOp",EDGE,"E7.21.0"),sQuery(id+"F0.wireOp",EDGE,"E7.21.1"),sQuery(id+"F0.wireOp",EDGE,"E7.21.2"),sQuery(id+"F0.wireOp",EDGE,"E7.21.3"),sQuery(id+"F0.wireOp",EDGE,"E7.21.4"),sQuery(id+"F0.wireOp",EDGE,"E7.21.5"),sQuery(id+"F0.wireOp",EDGE,"E7.22.0"),sQuery(id+"F0.wireOp",EDGE,"E7.22.1"),sQuery(id+"F0.wireOp",EDGE,"E7.22.2"),sQuery(id+"F0.wireOp",EDGE,"E7.22.3"),sQuery(id+"F0.wireOp",EDGE,"E7.22.4"),sQuery(id+"F0.wireOp",EDGE,"E7.22.5"),sQuery(id+"F0.wireOp",EDGE,"E7.23.0"),sQuery(id+"F0.wireOp",EDGE,"E7.23.1"),sQuery(id+"F0.wireOp",EDGE,"E7.23.2"),sQuery(id+"F0.wireOp",EDGE,"E7.23.3"),sQuery(id+"F0.wireOp",EDGE,"E7.23.4"),sQuery(id+"F0.wireOp",EDGE,"E7.23.5"),sQuery(id+"F0.wireOp",EDGE,"E7.24.0"),sQuery(id+"F0.wireOp",EDGE,"E7.24.1"),sQuery(id+"F0.wireOp",EDGE,"E7.24.2"),sQuery(id+"F0.wireOp",EDGE,"E7.24.3"),sQuery(id+"F0.wireOp",EDGE,"E7.24.4"),sQuery(id+"F0.wireOp",EDGE,"E7.24.5"),sQuery(id+"F0.wireOp",EDGE,"E7.25.0"),sQuery(id+"F0.wireOp",EDGE,"E7.25.1"),sQuery(id+"F0.wireOp",EDGE,"E7.25.2"),sQuery(id+"F0.wireOp",EDGE,"E7.25.3"),sQuery(id+"F0.wireOp",EDGE,"E7.25.4"),sQuery(id+"F0.wireOp",EDGE,"E7.25.5"),sQuery(id+"F0.wireOp",EDGE,"E7.26.0"),sQuery(id+"F0.wireOp",EDGE,"E7.26.1"),sQuery(id+"F0.wireOp",EDGE,"E7.26.2"),sQuery(id+"F0.wireOp",EDGE,"E7.26.3"),sQuery(id+"F0.wireOp",EDGE,"E7.26.4"),sQuery(id+"F0.wireOp",EDGE,"E7.26.5"),sQuery(id+"F0.wireOp",EDGE,"E7.27.0"),sQuery(id+"F0.wireOp",EDGE,"E7.27.1"),sQuery(id+"F0.wireOp",EDGE,"E7.27.2"),sQuery(id+"F0.wireOp",EDGE,"E7.27.3"),sQuery(id+"F0.wireOp",EDGE,"E7.27.4"),sQuery(id+"F0.wireOp",EDGE,"E7.27.5"),sQuery(id+"F0.wireOp",EDGE,"E7.28.0"),sQuery(id+"F0.wireOp",EDGE,"E7.28.1"),sQuery(id+"F0.wireOp",EDGE,"E7.28.2"),sQuery(id+"F0.wireOp",EDGE,"E7.28.3"),sQuery(id+"F0.wireOp",EDGE,"E7.28.4"),sQuery(id+"F0.wireOp",EDGE,"E7.28.5"),sQuery(id+"F0.wireOp",EDGE,"E7.29.0"),sQuery(id+"F0.wireOp",EDGE,"E7.29.1"),sQuery(id+"F0.wireOp",EDGE,"E7.29.2"),sQuery(id+"F0.wireOp",EDGE,"E7.29.3"),sQuery(id+"F0.wireOp",EDGE,"E7.29.4"),sQuery(id+"F0.wireOp",EDGE,"E7.29.5"),sQuery(id+"F0.wireOp",EDGE,"E7.30.0"),sQuery(id+"F0.wireOp",EDGE,"E7.30.1"),sQuery(id+"F0.wireOp",EDGE,"E7.30.2"),sQuery(id+"F0.wireOp",EDGE,"E7.30.3"),sQuery(id+"F0.wireOp",EDGE,"E7.30.4"),sQuery(id+"F0.wireOp",EDGE,"E7.30.5"),sQuery(id+"F0.wireOp",EDGE,"E7.31.0"),sQuery(id+"F0.wireOp",EDGE,"E7.31.1"),sQuery(id+"F0.wireOp",EDGE,"E7.31.2"),sQuery(id+"F0.wireOp",EDGE,"E7.31.3"),sQuery(id+"F0.wireOp",EDGE,"E7.31.4"),sQuery(id+"F0.wireOp",EDGE,"E7.31.5"),sQuery(id+"F0.wireOp",EDGE,"E7.32.0"),sQuery(id+"F0.wireOp",EDGE,"E7.32.1"),sQuery(id+"F0.wireOp",EDGE,"E7.32.2"),sQuery(id+"F0.wireOp",EDGE,"E7.32.3"),sQuery(id+"F0.wireOp",EDGE,"E7.32.4"),sQuery(id+"F0.wireOp",EDGE,"E7.32.5"),sQuery(id+"F0.wireOp",EDGE,"E7.33.0"),sQuery(id+"F0.wireOp",EDGE,"E7.33.1"),sQuery(id+"F0.wireOp",EDGE,"E7.33.2"),sQuery(id+"F0.wireOp",EDGE,"E7.33.3"),sQuery(id+"F0.wireOp",EDGE,"E7.33.4"),sQuery(id+"F0.wireOp",EDGE,"E7.33.5"),sQuery(id+"F0.wireOp",EDGE,"E7.34.0"),sQuery(id+"F0.wireOp",EDGE,"E7.34.1"),sQuery(id+"F0.wireOp",EDGE,"E7.34.2"),sQuery(id+"F0.wireOp",EDGE,"E7.34.3"),sQuery(id+"F0.wireOp",EDGE,"E7.34.4"),sQuery(id+"F0.wireOp",EDGE,"E7.34.5"),sQuery(id+"F0.wireOp",EDGE,"E7.35.0"),sQuery(id+"F0.wireOp",EDGE,"E7.35.1"),sQuery(id+"F0.wireOp",EDGE,"E7.35.2"),sQuery(id+"F0.wireOp",EDGE,"E7.35.3"),sQuery(id+"F0.wireOp",EDGE,"E7.35.4"),sQuery(id+"F0.wireOp",EDGE,"E7.35.5"),sQuery(id+"F0.wireOp",EDGE,"E7.36.0"),sQuery(id+"F0.wireOp",EDGE,"E7.36.1"),sQuery(id+"F0.wireOp",EDGE,"E7.36.2"),sQuery(id+"F0.wireOp",EDGE,"E7.36.3"),sQuery(id+"F0.wireOp",EDGE,"E7.36.4"),sQuery(id+"F0.wireOp",EDGE,"E7.36.5"),sQuery(id+"F0.wireOp",EDGE,"E7.37.0"),sQuery(id+"F0.wireOp",EDGE,"E7.37.1"),sQuery(id+"F0.wireOp",EDGE,"E7.37.2"),sQuery(id+"F0.wireOp",EDGE,"E7.37.3"),sQuery(id+"F0.wireOp",EDGE,"E7.37.4"),sQuery(id+"F0.wireOp",EDGE,"E7.37.5"),sQuery(id+"F0.wireOp",EDGE,"E7.38.0"),sQuery(id+"F0.wireOp",EDGE,"E7.38.1"),sQuery(id+"F0.wireOp",EDGE,"E7.38.2"),sQuery(id+"F0.wireOp",EDGE,"E7.38.3"),sQuery(id+"F0.wireOp",EDGE,"E7.38.4"),sQuery(id+"F0.wireOp",EDGE,"E7.38.5"),subQ0,sQuery(id+"F0.wireOp",EDGE,"E7.39.1"),sQuery(id+"F0.wireOp",EDGE,"E7.39.2"),sQuery(id+"F0.wireOp",EDGE,"E7.39.3"),sQuery(id+"F0.wireOp",EDGE,"E7.39.4"),sQuery(id+"F0.wireOp",EDGE,"E7.39.5"),sQuery(id+"F0.wireOp",EDGE,"E7.40.0"),sQuery(id+"F0.wireOp",EDGE,"E7.40.1"),sQuery(id+"F0.wireOp",EDGE,"E7.40.2"),sQuery(id+"F0.wireOp",EDGE,"E7.40.3"),sQuery(id+"F0.wireOp",EDGE,"E7.40.4"),sQuery(id+"F0.wireOp",EDGE,"E7.40.5"),sQuery(id+"F0.wireOp",EDGE,"E7.41.0"),sQuery(id+"F0.wireOp",EDGE,"E7.41.1"),sQuery(id+"F0.wireOp",EDGE,"E7.41.2"),sQuery(id+"F0.wireOp",EDGE,"E7.41.3"),sQuery(id+"F0.wireOp",EDGE,"E7.41.4"),sQuery(id+"F0.wireOp",EDGE,"E7.41.5"),sQuery(id+"F0.wireOp",EDGE,"E7.42.0"),sQuery(id+"F0.wireOp",EDGE,"E7.42.1"),sQuery(id+"F0.wireOp",EDGE,"E7.42.2"),sQuery(id+"F0.wireOp",EDGE,"E7.42.3"),sQuery(id+"F0.wireOp",EDGE,"E7.42.4"),sQuery(id+"F0.wireOp",EDGE,"E7.42.5"),sQuery(id+"F0.wireOp",EDGE,"E7.43.0"),sQuery(id+"F0.wireOp",EDGE,"E7.43.1"),sQuery(id+"F0.wireOp",EDGE,"E7.43.2"),sQuery(id+"F0.wireOp",EDGE,"E7.43.3"),sQuery(id+"F0.wireOp",EDGE,"E7.43.4"),sQuery(id+"F0.wireOp",EDGE,"E7.43.5")])],"isStart":false})],"blendedInto":[makeQuery(id+"F1.opExtrude","CAP_FACE",FACE,{"disambiguationData":[OSD([sQuery(id+"F0.wireOp",EDGE,"E1"),sQuery(id+"F0.wireOp",EDGE,"E2"),sQuery(id+"F0.wireOp",EDGE,"E3"),sQuery(id+"F0.wireOp",EDGE,"E4"),sQuery(id+"F0.wireOp",EDGE,"E5"),sQuery(id+"F0.wireOp",EDGE,"E6"),sQuery(id+"F0.wireOp",EDGE,"E7.1.0"),sQuery(id+"F0.wireOp",EDGE,"E7.1.1"),sQuery(id+"F0.wireOp",EDGE,"E7.1.2"),sQuery(id+"F0.wireOp",EDGE,"E7.1.3"),sQuery(id+"F0.wireOp",EDGE,"E7.1.4"),sQuery(id+"F0.wireOp",EDGE,"E7.1.5"),sQuery(id+"F0.wireOp",EDGE,"E7.2.0"),sQuery(id+"F0.wireOp",EDGE,"E7.2.1"),sQuery(id+"F0.wireOp",EDGE,"E7.2.2"),sQuery(id+"F0.wireOp",EDGE,"E7.2.3"),sQuery(id+"F0.wireOp",EDGE,"E7.2.4"),sQuery(id+"F0.wireOp",EDGE,"E7.2.5"),sQuery(id+"F0.wireOp",EDGE,"E7.3.0"),sQuery(id+"F0.wireOp",EDGE,"E7.3.1"),sQuery(id+"F0.wireOp",EDGE,"E7.3.2"),sQuery(id+"F0.wireOp",EDGE,"E7.3.3"),sQuery(id+"F0.wireOp",EDGE,"E7.3.4"),sQuery(id+"F0.wireOp",EDGE,"E7.3.5"),sQuery(id+"F0.wireOp",EDGE,"E7.4.0"),sQuery(id+"F0.wireOp",EDGE,"E7.4.1"),sQuery(id+"F0.wireOp",EDGE,"E7.4.2"),sQuery(id+"F0.wireOp",EDGE,"E7.4.3"),sQuery(id+"F0.wireOp",EDGE,"E7.4.4"),sQuery(id+"F0.wireOp",EDGE,"E7.4.5"),sQuery(id+"F0.wireOp",EDGE,"E7.5.0"),sQuery(id+"F0.wireOp",EDGE,"E7.5.1"),sQuery(id+"F0.wireOp",EDGE,"E7.5.2"),sQuery(id+"F0.wireOp",EDGE,"E7.5.3"),sQuery(id+"F0.wireOp",EDGE,"E7.5.4"),sQuery(id+"F0.wireOp",EDGE,"E7.5.5"),sQuery(id+"F0.wireOp",EDGE,"E7.6.0"),sQuery(id+"F0.wireOp",EDGE,"E7.6.1"),sQuery(id+"F0.wireOp",EDGE,"E7.6.2"),sQuery(id+"F0.wireOp",EDGE,"E7.6.3"),sQuery(id+"F0.wireOp",EDGE,"E7.6.4"),sQuery(id+"F0.wireOp",EDGE,"E7.6.5"),sQuery(id+"F0.wireOp",EDGE,"E7.7.0"),sQuery(id+"F0.wireOp",EDGE,"E7.7.1"),sQuery(id+"F0.wireOp",EDGE,"E7.7.2"),sQuery(id+"F0.wireOp",EDGE,"E7.7.3"),sQuery(id+"F0.wireOp",EDGE,"E7.7.4"),sQuery(id+"F0.wireOp",EDGE,"E7.7.5"),sQuery(id+"F0.wireOp",EDGE,"E7.8.0"),sQuery(id+"F0.wireOp",EDGE,"E7.8.1"),sQuery(id+"F0.wireOp",EDGE,"E7.8.2"),sQuery(id+"F0.wireOp",EDGE,"E7.8.3"),sQuery(id+"F0.wireOp",EDGE,"E7.8.4"),sQuery(id+"F0.wireOp",EDGE,"E7.8.5"),sQuery(id+"F0.wireOp",EDGE,"E7.9.0"),sQuery(id+"F0.wireOp",EDGE,"E7.9.1"),sQuery(id+"F0.wireOp",EDGE,"E7.9.2"),sQuery(id+"F0.wireOp",EDGE,"E7.9.3"),sQuery(id+"F0.wireOp",EDGE,"E7.9.4"),sQuery(id+"F0.wireOp",EDGE,"E7.9.5"),sQuery(id+"F0.wireOp",EDGE,"E7.10.0"),sQuery(id+"F0.wireOp",EDGE,"E7.10.1"),sQuery(id+"F0.wireOp",EDGE,"E7.10.2"),sQuery(id+"F0.wireOp",EDGE,"E7.10.3"),sQuery(id+"F0.wireOp",EDGE,"E7.10.4"),sQuery(id+"F0.wireOp",EDGE,"E7.10.5"),sQuery(id+"F0.wireOp",EDGE,"E7.11.0"),sQuery(id+"F0.wireOp",EDGE,"E7.11.1"),sQuery(id+"F0.wireOp",EDGE,"E7.11.2"),sQuery(id+"F0.wireOp",EDGE,"E7.11.3"),sQuery(id+"F0.wireOp",EDGE,"E7.11.4"),sQuery(id+"F0.wireOp",EDGE,"E7.11.5"),sQuery(id+"F0.wireOp",EDGE,"E7.12.0"),sQuery(id+"F0.wireOp",EDGE,"E7.12.1"),sQuery(id+"F0.wireOp",EDGE,"E7.12.2"),sQuery(id+"F0.wireOp",EDGE,"E7.12.3"),sQuery(id+"F0.wireOp",EDGE,"E7.12.4"),sQuery(id+"F0.wireOp",EDGE,"E7.12.5"),sQuery(id+"F0.wireOp",EDGE,"E7.13.0"),sQuery(id+"F0.wireOp",EDGE,"E7.13.1"),sQuery(id+"F0.wireOp",EDGE,"E7.13.2"),sQuery(id+"F0.wireOp",EDGE,"E7.13.3"),sQuery(id+"F0.wireOp",EDGE,"E7.13.4"),sQuery(id+"F0.wireOp",EDGE,"E7.13.5"),sQuery(id+"F0.wireOp",EDGE,"E7.14.0"),sQuery(id+"F0.wireOp",EDGE,"E7.14.1"),sQuery(id+"F0.wireOp",EDGE,"E7.14.2"),sQuery(id+"F0.wireOp",EDGE,"E7.14.3"),sQuery(id+"F0.wireOp",EDGE,"E7.14.4"),sQuery(id+"F0.wireOp",EDGE,"E7.14.5"),sQuery(id+"F0.wireOp",EDGE,"E7.15.0"),sQuery(id+"F0.wireOp",EDGE,"E7.15.1"),sQuery(id+"F0.wireOp",EDGE,"E7.15.2"),sQuery(id+"F0.wireOp",EDGE,"E7.15.3"),sQuery(id+"F0.wireOp",EDGE,"E7.15.4"),sQuery(id+"F0.wireOp",EDGE,"E7.15.5"),sQuery(id+"F0.wireOp",EDGE,"E7.16.0"),sQuery(id+"F0.wireOp",EDGE,"E7.16.1"),sQuery(id+"F0.wireOp",EDGE,"E7.16.2"),sQuery(id+"F0.wireOp",EDGE,"E7.16.3"),sQuery(id+"F0.wireOp",EDGE,"E7.16.4"),sQuery(id+"F0.wireOp",EDGE,"E7.16.5"),sQuery(id+"F0.wireOp",EDGE,"E7.17.0"),sQuery(id+"F0.wireOp",EDGE,"E7.17.1"),sQuery(id+"F0.wireOp",EDGE,"E7.17.2"),sQuery(id+"F0.wireOp",EDGE,"E7.17.3"),sQuery(id+"F0.wireOp",EDGE,"E7.17.4"),sQuery(id+"F0.wireOp",EDGE,"E7.17.5"),sQuery(id+"F0.wireOp",EDGE,"E7.18.0"),sQuery(id+"F0.wireOp",EDGE,"E7.18.1"),sQuery(id+"F0.wireOp",EDGE,"E7.18.2"),sQuery(id+"F0.wireOp",EDGE,"E7.18.3"),sQuery(id+"F0.wireOp",EDGE,"E7.18.4"),sQuery(id+"F0.wireOp",EDGE,"E7.18.5"),sQuery(id+"F0.wireOp",EDGE,"E7.19.0"),sQuery(id+"F0.wireOp",EDGE,"E7.19.1"),sQuery(id+"F0.wireOp",EDGE,"E7.19.2"),sQuery(id+"F0.wireOp",EDGE,"E7.19.3"),sQuery(id+"F0.wireOp",EDGE,"E7.19.4"),sQuery(id+"F0.wireOp",EDGE,"E7.19.5"),sQuery(id+"F0.wireOp",EDGE,"E7.20.0"),sQuery(id+"F0.wireOp",EDGE,"E7.20.1"),sQuery(id+"F0.wireOp",EDGE,"E7.20.2"),sQuery(id+"F0.wireOp",EDGE,"E7.20.3"),sQuery(id+"F0.wireOp",EDGE,"E7.20.4"),sQuery(id+"F0.wireOp",EDGE,"E7.20.5"),sQuery(id+"F0.wireOp",EDGE,"E7.21.0"),sQuery(id+"F0.wireOp",EDGE,"E7.21.1"),sQuery(id+"F0.wireOp",EDGE,"E7.21.2"),sQuery(id+"F0.wireOp",EDGE,"E7.21.3"),sQuery(id+"F0.wireOp",EDGE,"E7.21.4"),sQuery(id+"F0.wireOp",EDGE,"E7.21.5"),sQuery(id+"F0.wireOp",EDGE,"E7.22.0"),sQuery(id+"F0.wireOp",EDGE,"E7.22.1"),sQuery(id+"F0.wireOp",EDGE,"E7.22.2"),sQuery(id+"F0.wireOp",EDGE,"E7.22.3"),sQuery(id+"F0.wireOp",EDGE,"E7.22.4"),sQuery(id+"F0.wireOp",EDGE,"E7.22.5"),sQuery(id+"F0.wireOp",EDGE,"E7.23.0"),sQuery(id+"F0.wireOp",EDGE,"E7.23.1"),sQuery(id+"F0.wireOp",EDGE,"E7.23.2"),sQuery(id+"F0.wireOp",EDGE,"E7.23.3"),sQuery(id+"F0.wireOp",EDGE,"E7.23.4"),sQuery(id+"F0.wireOp",EDGE,"E7.23.5"),sQuery(id+"F0.wireOp",EDGE,"E7.24.0"),sQuery(id+"F0.wireOp",EDGE,"E7.24.1"),sQuery(id+"F0.wireOp",EDGE,"E7.24.2"),sQuery(id+"F0.wireOp",EDGE,"E7.24.3"),sQuery(id+"F0.wireOp",EDGE,"E7.24.4"),sQuery(id+"F0.wireOp",EDGE,"E7.24.5"),sQuery(id+"F0.wireOp",EDGE,"E7.25.0"),sQuery(id+"F0.wireOp",EDGE,"E7.25.1"),sQuery(id+"F0.wireOp",EDGE,"E7.25.2"),sQuery(id+"F0.wireOp",EDGE,"E7.25.3"),sQuery(id+"F0.wireOp",EDGE,"E7.25.4"),sQuery(id+"F0.wireOp",EDGE,"E7.25.5"),sQuery(id+"F0.wireOp",EDGE,"E7.26.0"),sQuery(id+"F0.wireOp",EDGE,"E7.26.1"),sQuery(id+"F0.wireOp",EDGE,"E7.26.2"),sQuery(id+"F0.wireOp",EDGE,"E7.26.3"),sQuery(id+"F0.wireOp",EDGE,"E7.26.4"),sQuery(id+"F0.wireOp",EDGE,"E7.26.5"),sQuery(id+"F0.wireOp",EDGE,"E7.27.0"),sQuery(id+"F0.wireOp",EDGE,"E7.27.1"),sQuery(id+"F0.wireOp",EDGE,"E7.27.2"),sQuery(id+"F0.wireOp",EDGE,"E7.27.3"),sQuery(id+"F0.wireOp",EDGE,"E7.27.4"),sQuery(id+"F0.wireOp",EDGE,"E7.27.5"),sQuery(id+"F0.wireOp",EDGE,"E7.28.0"),sQuery(id+"F0.wireOp",EDGE,"E7.28.1"),sQuery(id+"F0.wireOp",EDGE,"E7.28.2"),sQuery(id+"F0.wireOp",EDGE,"E7.28.3"),sQuery(id+"F0.wireOp",EDGE,"E7.28.4"),sQuery(id+"F0.wireOp",EDGE,"E7.28.5"),sQuery(id+"F0.wireOp",EDGE,"E7.29.0"),sQuery(id+"F0.wireOp",EDGE,"E7.29.1"),sQuery(id+"F0.wireOp",EDGE,"E7.29.2"),sQuery(id+"F0.wireOp",EDGE,"E7.29.3"),sQuery(id+"F0.wireOp",EDGE,"E7.29.4"),sQuery(id+"F0.wireOp",EDGE,"E7.29.5"),sQuery(id+"F0.wireOp",EDGE,"E7.30.0"),sQuery(id+"F0.wireOp",EDGE,"E7.30.1"),sQuery(id+"F0.wireOp",EDGE,"E7.30.2"),sQuery(id+"F0.wireOp",EDGE,"E7.30.3"),sQuery(id+"F0.wireOp",EDGE,"E7.30.4"),sQuery(id+"F0.wireOp",EDGE,"E7.30.5"),sQuery(id+"F0.wireOp",EDGE,"E7.31.0"),sQuery(id+"F0.wireOp",EDGE,"E7.31.1"),sQuery(id+"F0.wireOp",EDGE,"E7.31.2"),sQuery(id+"F0.wireOp",EDGE,"E7.31.3"),sQuery(id+"F0.wireOp",EDGE,"E7.31.4"),sQuery(id+"F0.wireOp",EDGE,"E7.31.5"),sQuery(id+"F0.wireOp",EDGE,"E7.32.0"),sQuery(id+"F0.wireOp",EDGE,"E7.32.1"),sQuery(id+"F0.wireOp",EDGE,"E7.32.2"),sQuery(id+"F0.wireOp",EDGE,"E7.32.3"),sQuery(id+"F0.wireOp",EDGE,"E7.32.4"),sQuery(id+"F0.wireOp",EDGE,"E7.32.5"),sQuery(id+"F0.wireOp",EDGE,"E7.33.0"),sQuery(id+"F0.wireOp",EDGE,"E7.33.1"),sQuery(id+"F0.wireOp",EDGE,"E7.33.2"),sQuery(id+"F0.wireOp",EDGE,"E7.33.3"),sQuery(id+"F0.wireOp",EDGE,"E7.33.4"),sQuery(id+"F0.wireOp",EDGE,"E7.33.5"),sQuery(id+"F0.wireOp",EDGE,"E7.34.0"),sQuery(id+"F0.wireOp",EDGE,"E7.34.1"),sQuery(id+"F0.wireOp",EDGE,"E7.34.2"),sQuery(id+"F0.wireOp",EDGE,"E7.34.3"),sQuery(id+"F0.wireOp",EDGE,"E7.34.4"),sQuery(id+"F0.wireOp",EDGE,"E7.34.5"),sQuery(id+"F0.wireOp",EDGE,"E7.35.0"),sQuery(id+"F0.wireOp",EDGE,"E7.35.1"),sQuery(id+"F0.wireOp",EDGE,"E7.35.2"),sQuery(id+"F0.wireOp",EDGE,"E7.35.3"),sQuery(id+"F0.wireOp",EDGE,"E7.35.4"),sQuery(id+"F0.wireOp",EDGE,"E7.35.5"),sQuery(id+"F0.wireOp",EDGE,"E7.36.0"),sQuery(id+"F0.wireOp",EDGE,"E7.36.1"),sQuery(id+"F0.wireOp",EDGE,"E7.36.2"),sQuery(id+"F0.wireOp",EDGE,"E7.36.3"),sQuery(id+"F0.wireOp",EDGE,"E7.36.4"),sQuery(id+"F0.wireOp",EDGE,"E7.36.5"),sQuery(id+"F0.wireOp",EDGE,"E7.37.0"),sQuery(id+"F0.wireOp",EDGE,"E7.37.1"),sQuery(id+"F0.wireOp",EDGE,"E7.37.2"),sQuery(id+"F0.wireOp",EDGE,"E7.37.3"),sQuery(id+"F0.wireOp",EDGE,"E7.37.4"),sQuery(id+"F0.wireOp",EDGE,"E7.37.5"),sQuery(id+"F0.wireOp",EDGE,"E7.38.0"),sQuery(id+"F0.wireOp",EDGE,"E7.38.1"),sQuery(id+"F0.wireOp",EDGE,"E7.38.2"),sQuery(id+"F0.wireOp",EDGE,"E7.38.3"),sQuery(id+"F0.wireOp",EDGE,"E7.38.4"),sQuery(id+"F0.wireOp",EDGE,"E7.38.5"),subQ0,sQuery(id+"F0.wireOp",EDGE,"E7.39.1"),sQuery(id+"F0.wireOp",EDGE,"E7.39.2"),sQuery(id+"F0.wireOp",EDGE,"E7.39.3"),sQuery(id+"F0.wireOp",EDGE,"E7.39.4"),sQuery(id+"F0.wireOp",EDGE,"E7.39.5"),sQuery(id+"F0.wireOp",EDGE,"E7.40.0"),sQuery(id+"F0.wireOp",EDGE,"E7.40.1"),sQuery(id+"F0.wireOp",EDGE,"E7.40.2"),sQuery(id+"F0.wireOp",EDGE,"E7.40.3"),sQuery(id+"F0.wireOp",EDGE,"E7.40.4"),sQuery(id+"F0.wireOp",EDGE,"E7.40.5"),sQuery(id+"F0.wireOp",EDGE,"E7.41.0"),sQuery(id+"F0.wireOp",EDGE,"E7.41.1"),sQuery(id+"F0.wireOp",EDGE,"E7.41.2"),sQuery(id+"F0.wireOp",EDGE,"E7.41.3"),sQuery(id+"F0.wireOp",EDGE,"E7.41.4"),sQuery(id+"F0.wireOp",EDGE,"E7.41.5"),sQuery(id+"F0.wireOp",EDGE,"E7.42.0"),sQuery(id+"F0.wireOp",EDGE,"E7.42.1"),sQuery(id+"F0.wireOp",EDGE,"E7.42.2"),sQuery(id+"F0.wireOp",EDGE,"E7.42.3"),sQuery(id+"F0.wireOp",EDGE,"E7.42.4"),sQuery(id+"F0.wireOp",EDGE,"E7.42.5"),sQuery(id+"F0.wireOp",EDGE,"E7.43.0"),sQuery(id+"F0.wireOp",EDGE,"E7.43.1"),sQuery(id+"F0.wireOp",EDGE,"E7.43.2"),sQuery(id+"F0.wireOp",EDGE,"E7.43.3"),sQuery(id+"F0.wireOp",EDGE,"E7.43.4"),sQuery(id+"F0.wireOp",EDGE,"E7.43.5")])],"isStart":false})]}),makeQuery(id+"F2.opChamfer","BLEND_FACE",FACE,{"disambiguationData":[OSD([subQ0])]})],"blendedInto":[makeQuery(id+"F2.opChamfer","BLEND_FACE",FACE,{"disambiguationData":[OSD([subQ0])]})]});}
            var Q4;
            {var subQ0=sQuery(id+"F0.wireOp",EDGE,"E7.37.0");Q4=makeQuery(id+"F8.opChamfer","BLEND_EDGE",EDGE,{"blendedFrom":[makeQuery(id+"F2.opChamfer","BLEND_EDGE",EDGE,{"blendedFrom":[makeQuery(id+"F1.opExtrude","CAP_EDGE",EDGE,{"disambiguationData":[OSD([subQ0])],"isStart":false}),makeQuery(id+"F1.opExtrude","CAP_FACE",FACE,{"disambiguationData":[OSD([sQuery(id+"F0.wireOp",EDGE,"E1"),sQuery(id+"F0.wireOp",EDGE,"E2"),sQuery(id+"F0.wireOp",EDGE,"E3"),sQuery(id+"F0.wireOp",EDGE,"E4"),sQuery(id+"F0.wireOp",EDGE,"E5"),sQuery(id+"F0.wireOp",EDGE,"E6"),sQuery(id+"F0.wireOp",EDGE,"E7.1.0"),sQuery(id+"F0.wireOp",EDGE,"E7.1.1"),sQuery(id+"F0.wireOp",EDGE,"E7.1.2"),sQuery(id+"F0.wireOp",EDGE,"E7.1.3"),sQuery(id+"F0.wireOp",EDGE,"E7.1.4"),sQuery(id+"F0.wireOp",EDGE,"E7.1.5"),sQuery(id+"F0.wireOp",EDGE,"E7.2.0"),sQuery(id+"F0.wireOp",EDGE,"E7.2.1"),sQuery(id+"F0.wireOp",EDGE,"E7.2.2"),sQuery(id+"F0.wireOp",EDGE,"E7.2.3"),sQuery(id+"F0.wireOp",EDGE,"E7.2.4"),sQuery(id+"F0.wireOp",EDGE,"E7.2.5"),sQuery(id+"F0.wireOp",EDGE,"E7.3.0"),sQuery(id+"F0.wireOp",EDGE,"E7.3.1"),sQuery(id+"F0.wireOp",EDGE,"E7.3.2"),sQuery(id+"F0.wireOp",EDGE,"E7.3.3"),sQuery(id+"F0.wireOp",EDGE,"E7.3.4"),sQuery(id+"F0.wireOp",EDGE,"E7.3.5"),sQuery(id+"F0.wireOp",EDGE,"E7.4.0"),sQuery(id+"F0.wireOp",EDGE,"E7.4.1"),sQuery(id+"F0.wireOp",EDGE,"E7.4.2"),sQuery(id+"F0.wireOp",EDGE,"E7.4.3"),sQuery(id+"F0.wireOp",EDGE,"E7.4.4"),sQuery(id+"F0.wireOp",EDGE,"E7.4.5"),sQuery(id+"F0.wireOp",EDGE,"E7.5.0"),sQuery(id+"F0.wireOp",EDGE,"E7.5.1"),sQuery(id+"F0.wireOp",EDGE,"E7.5.2"),sQuery(id+"F0.wireOp",EDGE,"E7.5.3"),sQuery(id+"F0.wireOp",EDGE,"E7.5.4"),sQuery(id+"F0.wireOp",EDGE,"E7.5.5"),sQuery(id+"F0.wireOp",EDGE,"E7.6.0"),sQuery(id+"F0.wireOp",EDGE,"E7.6.1"),sQuery(id+"F0.wireOp",EDGE,"E7.6.2"),sQuery(id+"F0.wireOp",EDGE,"E7.6.3"),sQuery(id+"F0.wireOp",EDGE,"E7.6.4"),sQuery(id+"F0.wireOp",EDGE,"E7.6.5"),sQuery(id+"F0.wireOp",EDGE,"E7.7.0"),sQuery(id+"F0.wireOp",EDGE,"E7.7.1"),sQuery(id+"F0.wireOp",EDGE,"E7.7.2"),sQuery(id+"F0.wireOp",EDGE,"E7.7.3"),sQuery(id+"F0.wireOp",EDGE,"E7.7.4"),sQuery(id+"F0.wireOp",EDGE,"E7.7.5"),sQuery(id+"F0.wireOp",EDGE,"E7.8.0"),sQuery(id+"F0.wireOp",EDGE,"E7.8.1"),sQuery(id+"F0.wireOp",EDGE,"E7.8.2"),sQuery(id+"F0.wireOp",EDGE,"E7.8.3"),sQuery(id+"F0.wireOp",EDGE,"E7.8.4"),sQuery(id+"F0.wireOp",EDGE,"E7.8.5"),sQuery(id+"F0.wireOp",EDGE,"E7.9.0"),sQuery(id+"F0.wireOp",EDGE,"E7.9.1"),sQuery(id+"F0.wireOp",EDGE,"E7.9.2"),sQuery(id+"F0.wireOp",EDGE,"E7.9.3"),sQuery(id+"F0.wireOp",EDGE,"E7.9.4"),sQuery(id+"F0.wireOp",EDGE,"E7.9.5"),sQuery(id+"F0.wireOp",EDGE,"E7.10.0"),sQuery(id+"F0.wireOp",EDGE,"E7.10.1"),sQuery(id+"F0.wireOp",EDGE,"E7.10.2"),sQuery(id+"F0.wireOp",EDGE,"E7.10.3"),sQuery(id+"F0.wireOp",EDGE,"E7.10.4"),sQuery(id+"F0.wireOp",EDGE,"E7.10.5"),sQuery(id+"F0.wireOp",EDGE,"E7.11.0"),sQuery(id+"F0.wireOp",EDGE,"E7.11.1"),sQuery(id+"F0.wireOp",EDGE,"E7.11.2"),sQuery(id+"F0.wireOp",EDGE,"E7.11.3"),sQuery(id+"F0.wireOp",EDGE,"E7.11.4"),sQuery(id+"F0.wireOp",EDGE,"E7.11.5"),sQuery(id+"F0.wireOp",EDGE,"E7.12.0"),sQuery(id+"F0.wireOp",EDGE,"E7.12.1"),sQuery(id+"F0.wireOp",EDGE,"E7.12.2"),sQuery(id+"F0.wireOp",EDGE,"E7.12.3"),sQuery(id+"F0.wireOp",EDGE,"E7.12.4"),sQuery(id+"F0.wireOp",EDGE,"E7.12.5"),sQuery(id+"F0.wireOp",EDGE,"E7.13.0"),sQuery(id+"F0.wireOp",EDGE,"E7.13.1"),sQuery(id+"F0.wireOp",EDGE,"E7.13.2"),sQuery(id+"F0.wireOp",EDGE,"E7.13.3"),sQuery(id+"F0.wireOp",EDGE,"E7.13.4"),sQuery(id+"F0.wireOp",EDGE,"E7.13.5"),sQuery(id+"F0.wireOp",EDGE,"E7.14.0"),sQuery(id+"F0.wireOp",EDGE,"E7.14.1"),sQuery(id+"F0.wireOp",EDGE,"E7.14.2"),sQuery(id+"F0.wireOp",EDGE,"E7.14.3"),sQuery(id+"F0.wireOp",EDGE,"E7.14.4"),sQuery(id+"F0.wireOp",EDGE,"E7.14.5"),sQuery(id+"F0.wireOp",EDGE,"E7.15.0"),sQuery(id+"F0.wireOp",EDGE,"E7.15.1"),sQuery(id+"F0.wireOp",EDGE,"E7.15.2"),sQuery(id+"F0.wireOp",EDGE,"E7.15.3"),sQuery(id+"F0.wireOp",EDGE,"E7.15.4"),sQuery(id+"F0.wireOp",EDGE,"E7.15.5"),sQuery(id+"F0.wireOp",EDGE,"E7.16.0"),sQuery(id+"F0.wireOp",EDGE,"E7.16.1"),sQuery(id+"F0.wireOp",EDGE,"E7.16.2"),sQuery(id+"F0.wireOp",EDGE,"E7.16.3"),sQuery(id+"F0.wireOp",EDGE,"E7.16.4"),sQuery(id+"F0.wireOp",EDGE,"E7.16.5"),sQuery(id+"F0.wireOp",EDGE,"E7.17.0"),sQuery(id+"F0.wireOp",EDGE,"E7.17.1"),sQuery(id+"F0.wireOp",EDGE,"E7.17.2"),sQuery(id+"F0.wireOp",EDGE,"E7.17.3"),sQuery(id+"F0.wireOp",EDGE,"E7.17.4"),sQuery(id+"F0.wireOp",EDGE,"E7.17.5"),sQuery(id+"F0.wireOp",EDGE,"E7.18.0"),sQuery(id+"F0.wireOp",EDGE,"E7.18.1"),sQuery(id+"F0.wireOp",EDGE,"E7.18.2"),sQuery(id+"F0.wireOp",EDGE,"E7.18.3"),sQuery(id+"F0.wireOp",EDGE,"E7.18.4"),sQuery(id+"F0.wireOp",EDGE,"E7.18.5"),sQuery(id+"F0.wireOp",EDGE,"E7.19.0"),sQuery(id+"F0.wireOp",EDGE,"E7.19.1"),sQuery(id+"F0.wireOp",EDGE,"E7.19.2"),sQuery(id+"F0.wireOp",EDGE,"E7.19.3"),sQuery(id+"F0.wireOp",EDGE,"E7.19.4"),sQuery(id+"F0.wireOp",EDGE,"E7.19.5"),sQuery(id+"F0.wireOp",EDGE,"E7.20.0"),sQuery(id+"F0.wireOp",EDGE,"E7.20.1"),sQuery(id+"F0.wireOp",EDGE,"E7.20.2"),sQuery(id+"F0.wireOp",EDGE,"E7.20.3"),sQuery(id+"F0.wireOp",EDGE,"E7.20.4"),sQuery(id+"F0.wireOp",EDGE,"E7.20.5"),sQuery(id+"F0.wireOp",EDGE,"E7.21.0"),sQuery(id+"F0.wireOp",EDGE,"E7.21.1"),sQuery(id+"F0.wireOp",EDGE,"E7.21.2"),sQuery(id+"F0.wireOp",EDGE,"E7.21.3"),sQuery(id+"F0.wireOp",EDGE,"E7.21.4"),sQuery(id+"F0.wireOp",EDGE,"E7.21.5"),sQuery(id+"F0.wireOp",EDGE,"E7.22.0"),sQuery(id+"F0.wireOp",EDGE,"E7.22.1"),sQuery(id+"F0.wireOp",EDGE,"E7.22.2"),sQuery(id+"F0.wireOp",EDGE,"E7.22.3"),sQuery(id+"F0.wireOp",EDGE,"E7.22.4"),sQuery(id+"F0.wireOp",EDGE,"E7.22.5"),sQuery(id+"F0.wireOp",EDGE,"E7.23.0"),sQuery(id+"F0.wireOp",EDGE,"E7.23.1"),sQuery(id+"F0.wireOp",EDGE,"E7.23.2"),sQuery(id+"F0.wireOp",EDGE,"E7.23.3"),sQuery(id+"F0.wireOp",EDGE,"E7.23.4"),sQuery(id+"F0.wireOp",EDGE,"E7.23.5"),sQuery(id+"F0.wireOp",EDGE,"E7.24.0"),sQuery(id+"F0.wireOp",EDGE,"E7.24.1"),sQuery(id+"F0.wireOp",EDGE,"E7.24.2"),sQuery(id+"F0.wireOp",EDGE,"E7.24.3"),sQuery(id+"F0.wireOp",EDGE,"E7.24.4"),sQuery(id+"F0.wireOp",EDGE,"E7.24.5"),sQuery(id+"F0.wireOp",EDGE,"E7.25.0"),sQuery(id+"F0.wireOp",EDGE,"E7.25.1"),sQuery(id+"F0.wireOp",EDGE,"E7.25.2"),sQuery(id+"F0.wireOp",EDGE,"E7.25.3"),sQuery(id+"F0.wireOp",EDGE,"E7.25.4"),sQuery(id+"F0.wireOp",EDGE,"E7.25.5"),sQuery(id+"F0.wireOp",EDGE,"E7.26.0"),sQuery(id+"F0.wireOp",EDGE,"E7.26.1"),sQuery(id+"F0.wireOp",EDGE,"E7.26.2"),sQuery(id+"F0.wireOp",EDGE,"E7.26.3"),sQuery(id+"F0.wireOp",EDGE,"E7.26.4"),sQuery(id+"F0.wireOp",EDGE,"E7.26.5"),sQuery(id+"F0.wireOp",EDGE,"E7.27.0"),sQuery(id+"F0.wireOp",EDGE,"E7.27.1"),sQuery(id+"F0.wireOp",EDGE,"E7.27.2"),sQuery(id+"F0.wireOp",EDGE,"E7.27.3"),sQuery(id+"F0.wireOp",EDGE,"E7.27.4"),sQuery(id+"F0.wireOp",EDGE,"E7.27.5"),sQuery(id+"F0.wireOp",EDGE,"E7.28.0"),sQuery(id+"F0.wireOp",EDGE,"E7.28.1"),sQuery(id+"F0.wireOp",EDGE,"E7.28.2"),sQuery(id+"F0.wireOp",EDGE,"E7.28.3"),sQuery(id+"F0.wireOp",EDGE,"E7.28.4"),sQuery(id+"F0.wireOp",EDGE,"E7.28.5"),sQuery(id+"F0.wireOp",EDGE,"E7.29.0"),sQuery(id+"F0.wireOp",EDGE,"E7.29.1"),sQuery(id+"F0.wireOp",EDGE,"E7.29.2"),sQuery(id+"F0.wireOp",EDGE,"E7.29.3"),sQuery(id+"F0.wireOp",EDGE,"E7.29.4"),sQuery(id+"F0.wireOp",EDGE,"E7.29.5"),sQuery(id+"F0.wireOp",EDGE,"E7.30.0"),sQuery(id+"F0.wireOp",EDGE,"E7.30.1"),sQuery(id+"F0.wireOp",EDGE,"E7.30.2"),sQuery(id+"F0.wireOp",EDGE,"E7.30.3"),sQuery(id+"F0.wireOp",EDGE,"E7.30.4"),sQuery(id+"F0.wireOp",EDGE,"E7.30.5"),sQuery(id+"F0.wireOp",EDGE,"E7.31.0"),sQuery(id+"F0.wireOp",EDGE,"E7.31.1"),sQuery(id+"F0.wireOp",EDGE,"E7.31.2"),sQuery(id+"F0.wireOp",EDGE,"E7.31.3"),sQuery(id+"F0.wireOp",EDGE,"E7.31.4"),sQuery(id+"F0.wireOp",EDGE,"E7.31.5"),sQuery(id+"F0.wireOp",EDGE,"E7.32.0"),sQuery(id+"F0.wireOp",EDGE,"E7.32.1"),sQuery(id+"F0.wireOp",EDGE,"E7.32.2"),sQuery(id+"F0.wireOp",EDGE,"E7.32.3"),sQuery(id+"F0.wireOp",EDGE,"E7.32.4"),sQuery(id+"F0.wireOp",EDGE,"E7.32.5"),sQuery(id+"F0.wireOp",EDGE,"E7.33.0"),sQuery(id+"F0.wireOp",EDGE,"E7.33.1"),sQuery(id+"F0.wireOp",EDGE,"E7.33.2"),sQuery(id+"F0.wireOp",EDGE,"E7.33.3"),sQuery(id+"F0.wireOp",EDGE,"E7.33.4"),sQuery(id+"F0.wireOp",EDGE,"E7.33.5"),sQuery(id+"F0.wireOp",EDGE,"E7.34.0"),sQuery(id+"F0.wireOp",EDGE,"E7.34.1"),sQuery(id+"F0.wireOp",EDGE,"E7.34.2"),sQuery(id+"F0.wireOp",EDGE,"E7.34.3"),sQuery(id+"F0.wireOp",EDGE,"E7.34.4"),sQuery(id+"F0.wireOp",EDGE,"E7.34.5"),sQuery(id+"F0.wireOp",EDGE,"E7.35.0"),sQuery(id+"F0.wireOp",EDGE,"E7.35.1"),sQuery(id+"F0.wireOp",EDGE,"E7.35.2"),sQuery(id+"F0.wireOp",EDGE,"E7.35.3"),sQuery(id+"F0.wireOp",EDGE,"E7.35.4"),sQuery(id+"F0.wireOp",EDGE,"E7.35.5"),sQuery(id+"F0.wireOp",EDGE,"E7.36.0"),sQuery(id+"F0.wireOp",EDGE,"E7.36.1"),sQuery(id+"F0.wireOp",EDGE,"E7.36.2"),sQuery(id+"F0.wireOp",EDGE,"E7.36.3"),sQuery(id+"F0.wireOp",EDGE,"E7.36.4"),sQuery(id+"F0.wireOp",EDGE,"E7.36.5"),subQ0,sQuery(id+"F0.wireOp",EDGE,"E7.37.1"),sQuery(id+"F0.wireOp",EDGE,"E7.37.2"),sQuery(id+"F0.wireOp",EDGE,"E7.37.3"),sQuery(id+"F0.wireOp",EDGE,"E7.37.4"),sQuery(id+"F0.wireOp",EDGE,"E7.37.5"),sQuery(id+"F0.wireOp",EDGE,"E7.38.0"),sQuery(id+"F0.wireOp",EDGE,"E7.38.1"),sQuery(id+"F0.wireOp",EDGE,"E7.38.2"),sQuery(id+"F0.wireOp",EDGE,"E7.38.3"),sQuery(id+"F0.wireOp",EDGE,"E7.38.4"),sQuery(id+"F0.wireOp",EDGE,"E7.38.5"),sQuery(id+"F0.wireOp",EDGE,"E7.39.0"),sQuery(id+"F0.wireOp",EDGE,"E7.39.1"),sQuery(id+"F0.wireOp",EDGE,"E7.39.2"),sQuery(id+"F0.wireOp",EDGE,"E7.39.3"),sQuery(id+"F0.wireOp",EDGE,"E7.39.4"),sQuery(id+"F0.wireOp",EDGE,"E7.39.5"),sQuery(id+"F0.wireOp",EDGE,"E7.40.0"),sQuery(id+"F0.wireOp",EDGE,"E7.40.1"),sQuery(id+"F0.wireOp",EDGE,"E7.40.2"),sQuery(id+"F0.wireOp",EDGE,"E7.40.3"),sQuery(id+"F0.wireOp",EDGE,"E7.40.4"),sQuery(id+"F0.wireOp",EDGE,"E7.40.5"),sQuery(id+"F0.wireOp",EDGE,"E7.41.0"),sQuery(id+"F0.wireOp",EDGE,"E7.41.1"),sQuery(id+"F0.wireOp",EDGE,"E7.41.2"),sQuery(id+"F0.wireOp",EDGE,"E7.41.3"),sQuery(id+"F0.wireOp",EDGE,"E7.41.4"),sQuery(id+"F0.wireOp",EDGE,"E7.41.5"),sQuery(id+"F0.wireOp",EDGE,"E7.42.0"),sQuery(id+"F0.wireOp",EDGE,"E7.42.1"),sQuery(id+"F0.wireOp",EDGE,"E7.42.2"),sQuery(id+"F0.wireOp",EDGE,"E7.42.3"),sQuery(id+"F0.wireOp",EDGE,"E7.42.4"),sQuery(id+"F0.wireOp",EDGE,"E7.42.5"),sQuery(id+"F0.wireOp",EDGE,"E7.43.0"),sQuery(id+"F0.wireOp",EDGE,"E7.43.1"),sQuery(id+"F0.wireOp",EDGE,"E7.43.2"),sQuery(id+"F0.wireOp",EDGE,"E7.43.3"),sQuery(id+"F0.wireOp",EDGE,"E7.43.4"),sQuery(id+"F0.wireOp",EDGE,"E7.43.5")])],"isStart":false})],"blendedInto":[makeQuery(id+"F1.opExtrude","CAP_FACE",FACE,{"disambiguationData":[OSD([sQuery(id+"F0.wireOp",EDGE,"E1"),sQuery(id+"F0.wireOp",EDGE,"E2"),sQuery(id+"F0.wireOp",EDGE,"E3"),sQuery(id+"F0.wireOp",EDGE,"E4"),sQuery(id+"F0.wireOp",EDGE,"E5"),sQuery(id+"F0.wireOp",EDGE,"E6"),sQuery(id+"F0.wireOp",EDGE,"E7.1.0"),sQuery(id+"F0.wireOp",EDGE,"E7.1.1"),sQuery(id+"F0.wireOp",EDGE,"E7.1.2"),sQuery(id+"F0.wireOp",EDGE,"E7.1.3"),sQuery(id+"F0.wireOp",EDGE,"E7.1.4"),sQuery(id+"F0.wireOp",EDGE,"E7.1.5"),sQuery(id+"F0.wireOp",EDGE,"E7.2.0"),sQuery(id+"F0.wireOp",EDGE,"E7.2.1"),sQuery(id+"F0.wireOp",EDGE,"E7.2.2"),sQuery(id+"F0.wireOp",EDGE,"E7.2.3"),sQuery(id+"F0.wireOp",EDGE,"E7.2.4"),sQuery(id+"F0.wireOp",EDGE,"E7.2.5"),sQuery(id+"F0.wireOp",EDGE,"E7.3.0"),sQuery(id+"F0.wireOp",EDGE,"E7.3.1"),sQuery(id+"F0.wireOp",EDGE,"E7.3.2"),sQuery(id+"F0.wireOp",EDGE,"E7.3.3"),sQuery(id+"F0.wireOp",EDGE,"E7.3.4"),sQuery(id+"F0.wireOp",EDGE,"E7.3.5"),sQuery(id+"F0.wireOp",EDGE,"E7.4.0"),sQuery(id+"F0.wireOp",EDGE,"E7.4.1"),sQuery(id+"F0.wireOp",EDGE,"E7.4.2"),sQuery(id+"F0.wireOp",EDGE,"E7.4.3"),sQuery(id+"F0.wireOp",EDGE,"E7.4.4"),sQuery(id+"F0.wireOp",EDGE,"E7.4.5"),sQuery(id+"F0.wireOp",EDGE,"E7.5.0"),sQuery(id+"F0.wireOp",EDGE,"E7.5.1"),sQuery(id+"F0.wireOp",EDGE,"E7.5.2"),sQuery(id+"F0.wireOp",EDGE,"E7.5.3"),sQuery(id+"F0.wireOp",EDGE,"E7.5.4"),sQuery(id+"F0.wireOp",EDGE,"E7.5.5"),sQuery(id+"F0.wireOp",EDGE,"E7.6.0"),sQuery(id+"F0.wireOp",EDGE,"E7.6.1"),sQuery(id+"F0.wireOp",EDGE,"E7.6.2"),sQuery(id+"F0.wireOp",EDGE,"E7.6.3"),sQuery(id+"F0.wireOp",EDGE,"E7.6.4"),sQuery(id+"F0.wireOp",EDGE,"E7.6.5"),sQuery(id+"F0.wireOp",EDGE,"E7.7.0"),sQuery(id+"F0.wireOp",EDGE,"E7.7.1"),sQuery(id+"F0.wireOp",EDGE,"E7.7.2"),sQuery(id+"F0.wireOp",EDGE,"E7.7.3"),sQuery(id+"F0.wireOp",EDGE,"E7.7.4"),sQuery(id+"F0.wireOp",EDGE,"E7.7.5"),sQuery(id+"F0.wireOp",EDGE,"E7.8.0"),sQuery(id+"F0.wireOp",EDGE,"E7.8.1"),sQuery(id+"F0.wireOp",EDGE,"E7.8.2"),sQuery(id+"F0.wireOp",EDGE,"E7.8.3"),sQuery(id+"F0.wireOp",EDGE,"E7.8.4"),sQuery(id+"F0.wireOp",EDGE,"E7.8.5"),sQuery(id+"F0.wireOp",EDGE,"E7.9.0"),sQuery(id+"F0.wireOp",EDGE,"E7.9.1"),sQuery(id+"F0.wireOp",EDGE,"E7.9.2"),sQuery(id+"F0.wireOp",EDGE,"E7.9.3"),sQuery(id+"F0.wireOp",EDGE,"E7.9.4"),sQuery(id+"F0.wireOp",EDGE,"E7.9.5"),sQuery(id+"F0.wireOp",EDGE,"E7.10.0"),sQuery(id+"F0.wireOp",EDGE,"E7.10.1"),sQuery(id+"F0.wireOp",EDGE,"E7.10.2"),sQuery(id+"F0.wireOp",EDGE,"E7.10.3"),sQuery(id+"F0.wireOp",EDGE,"E7.10.4"),sQuery(id+"F0.wireOp",EDGE,"E7.10.5"),sQuery(id+"F0.wireOp",EDGE,"E7.11.0"),sQuery(id+"F0.wireOp",EDGE,"E7.11.1"),sQuery(id+"F0.wireOp",EDGE,"E7.11.2"),sQuery(id+"F0.wireOp",EDGE,"E7.11.3"),sQuery(id+"F0.wireOp",EDGE,"E7.11.4"),sQuery(id+"F0.wireOp",EDGE,"E7.11.5"),sQuery(id+"F0.wireOp",EDGE,"E7.12.0"),sQuery(id+"F0.wireOp",EDGE,"E7.12.1"),sQuery(id+"F0.wireOp",EDGE,"E7.12.2"),sQuery(id+"F0.wireOp",EDGE,"E7.12.3"),sQuery(id+"F0.wireOp",EDGE,"E7.12.4"),sQuery(id+"F0.wireOp",EDGE,"E7.12.5"),sQuery(id+"F0.wireOp",EDGE,"E7.13.0"),sQuery(id+"F0.wireOp",EDGE,"E7.13.1"),sQuery(id+"F0.wireOp",EDGE,"E7.13.2"),sQuery(id+"F0.wireOp",EDGE,"E7.13.3"),sQuery(id+"F0.wireOp",EDGE,"E7.13.4"),sQuery(id+"F0.wireOp",EDGE,"E7.13.5"),sQuery(id+"F0.wireOp",EDGE,"E7.14.0"),sQuery(id+"F0.wireOp",EDGE,"E7.14.1"),sQuery(id+"F0.wireOp",EDGE,"E7.14.2"),sQuery(id+"F0.wireOp",EDGE,"E7.14.3"),sQuery(id+"F0.wireOp",EDGE,"E7.14.4"),sQuery(id+"F0.wireOp",EDGE,"E7.14.5"),sQuery(id+"F0.wireOp",EDGE,"E7.15.0"),sQuery(id+"F0.wireOp",EDGE,"E7.15.1"),sQuery(id+"F0.wireOp",EDGE,"E7.15.2"),sQuery(id+"F0.wireOp",EDGE,"E7.15.3"),sQuery(id+"F0.wireOp",EDGE,"E7.15.4"),sQuery(id+"F0.wireOp",EDGE,"E7.15.5"),sQuery(id+"F0.wireOp",EDGE,"E7.16.0"),sQuery(id+"F0.wireOp",EDGE,"E7.16.1"),sQuery(id+"F0.wireOp",EDGE,"E7.16.2"),sQuery(id+"F0.wireOp",EDGE,"E7.16.3"),sQuery(id+"F0.wireOp",EDGE,"E7.16.4"),sQuery(id+"F0.wireOp",EDGE,"E7.16.5"),sQuery(id+"F0.wireOp",EDGE,"E7.17.0"),sQuery(id+"F0.wireOp",EDGE,"E7.17.1"),sQuery(id+"F0.wireOp",EDGE,"E7.17.2"),sQuery(id+"F0.wireOp",EDGE,"E7.17.3"),sQuery(id+"F0.wireOp",EDGE,"E7.17.4"),sQuery(id+"F0.wireOp",EDGE,"E7.17.5"),sQuery(id+"F0.wireOp",EDGE,"E7.18.0"),sQuery(id+"F0.wireOp",EDGE,"E7.18.1"),sQuery(id+"F0.wireOp",EDGE,"E7.18.2"),sQuery(id+"F0.wireOp",EDGE,"E7.18.3"),sQuery(id+"F0.wireOp",EDGE,"E7.18.4"),sQuery(id+"F0.wireOp",EDGE,"E7.18.5"),sQuery(id+"F0.wireOp",EDGE,"E7.19.0"),sQuery(id+"F0.wireOp",EDGE,"E7.19.1"),sQuery(id+"F0.wireOp",EDGE,"E7.19.2"),sQuery(id+"F0.wireOp",EDGE,"E7.19.3"),sQuery(id+"F0.wireOp",EDGE,"E7.19.4"),sQuery(id+"F0.wireOp",EDGE,"E7.19.5"),sQuery(id+"F0.wireOp",EDGE,"E7.20.0"),sQuery(id+"F0.wireOp",EDGE,"E7.20.1"),sQuery(id+"F0.wireOp",EDGE,"E7.20.2"),sQuery(id+"F0.wireOp",EDGE,"E7.20.3"),sQuery(id+"F0.wireOp",EDGE,"E7.20.4"),sQuery(id+"F0.wireOp",EDGE,"E7.20.5"),sQuery(id+"F0.wireOp",EDGE,"E7.21.0"),sQuery(id+"F0.wireOp",EDGE,"E7.21.1"),sQuery(id+"F0.wireOp",EDGE,"E7.21.2"),sQuery(id+"F0.wireOp",EDGE,"E7.21.3"),sQuery(id+"F0.wireOp",EDGE,"E7.21.4"),sQuery(id+"F0.wireOp",EDGE,"E7.21.5"),sQuery(id+"F0.wireOp",EDGE,"E7.22.0"),sQuery(id+"F0.wireOp",EDGE,"E7.22.1"),sQuery(id+"F0.wireOp",EDGE,"E7.22.2"),sQuery(id+"F0.wireOp",EDGE,"E7.22.3"),sQuery(id+"F0.wireOp",EDGE,"E7.22.4"),sQuery(id+"F0.wireOp",EDGE,"E7.22.5"),sQuery(id+"F0.wireOp",EDGE,"E7.23.0"),sQuery(id+"F0.wireOp",EDGE,"E7.23.1"),sQuery(id+"F0.wireOp",EDGE,"E7.23.2"),sQuery(id+"F0.wireOp",EDGE,"E7.23.3"),sQuery(id+"F0.wireOp",EDGE,"E7.23.4"),sQuery(id+"F0.wireOp",EDGE,"E7.23.5"),sQuery(id+"F0.wireOp",EDGE,"E7.24.0"),sQuery(id+"F0.wireOp",EDGE,"E7.24.1"),sQuery(id+"F0.wireOp",EDGE,"E7.24.2"),sQuery(id+"F0.wireOp",EDGE,"E7.24.3"),sQuery(id+"F0.wireOp",EDGE,"E7.24.4"),sQuery(id+"F0.wireOp",EDGE,"E7.24.5"),sQuery(id+"F0.wireOp",EDGE,"E7.25.0"),sQuery(id+"F0.wireOp",EDGE,"E7.25.1"),sQuery(id+"F0.wireOp",EDGE,"E7.25.2"),sQuery(id+"F0.wireOp",EDGE,"E7.25.3"),sQuery(id+"F0.wireOp",EDGE,"E7.25.4"),sQuery(id+"F0.wireOp",EDGE,"E7.25.5"),sQuery(id+"F0.wireOp",EDGE,"E7.26.0"),sQuery(id+"F0.wireOp",EDGE,"E7.26.1"),sQuery(id+"F0.wireOp",EDGE,"E7.26.2"),sQuery(id+"F0.wireOp",EDGE,"E7.26.3"),sQuery(id+"F0.wireOp",EDGE,"E7.26.4"),sQuery(id+"F0.wireOp",EDGE,"E7.26.5"),sQuery(id+"F0.wireOp",EDGE,"E7.27.0"),sQuery(id+"F0.wireOp",EDGE,"E7.27.1"),sQuery(id+"F0.wireOp",EDGE,"E7.27.2"),sQuery(id+"F0.wireOp",EDGE,"E7.27.3"),sQuery(id+"F0.wireOp",EDGE,"E7.27.4"),sQuery(id+"F0.wireOp",EDGE,"E7.27.5"),sQuery(id+"F0.wireOp",EDGE,"E7.28.0"),sQuery(id+"F0.wireOp",EDGE,"E7.28.1"),sQuery(id+"F0.wireOp",EDGE,"E7.28.2"),sQuery(id+"F0.wireOp",EDGE,"E7.28.3"),sQuery(id+"F0.wireOp",EDGE,"E7.28.4"),sQuery(id+"F0.wireOp",EDGE,"E7.28.5"),sQuery(id+"F0.wireOp",EDGE,"E7.29.0"),sQuery(id+"F0.wireOp",EDGE,"E7.29.1"),sQuery(id+"F0.wireOp",EDGE,"E7.29.2"),sQuery(id+"F0.wireOp",EDGE,"E7.29.3"),sQuery(id+"F0.wireOp",EDGE,"E7.29.4"),sQuery(id+"F0.wireOp",EDGE,"E7.29.5"),sQuery(id+"F0.wireOp",EDGE,"E7.30.0"),sQuery(id+"F0.wireOp",EDGE,"E7.30.1"),sQuery(id+"F0.wireOp",EDGE,"E7.30.2"),sQuery(id+"F0.wireOp",EDGE,"E7.30.3"),sQuery(id+"F0.wireOp",EDGE,"E7.30.4"),sQuery(id+"F0.wireOp",EDGE,"E7.30.5"),sQuery(id+"F0.wireOp",EDGE,"E7.31.0"),sQuery(id+"F0.wireOp",EDGE,"E7.31.1"),sQuery(id+"F0.wireOp",EDGE,"E7.31.2"),sQuery(id+"F0.wireOp",EDGE,"E7.31.3"),sQuery(id+"F0.wireOp",EDGE,"E7.31.4"),sQuery(id+"F0.wireOp",EDGE,"E7.31.5"),sQuery(id+"F0.wireOp",EDGE,"E7.32.0"),sQuery(id+"F0.wireOp",EDGE,"E7.32.1"),sQuery(id+"F0.wireOp",EDGE,"E7.32.2"),sQuery(id+"F0.wireOp",EDGE,"E7.32.3"),sQuery(id+"F0.wireOp",EDGE,"E7.32.4"),sQuery(id+"F0.wireOp",EDGE,"E7.32.5"),sQuery(id+"F0.wireOp",EDGE,"E7.33.0"),sQuery(id+"F0.wireOp",EDGE,"E7.33.1"),sQuery(id+"F0.wireOp",EDGE,"E7.33.2"),sQuery(id+"F0.wireOp",EDGE,"E7.33.3"),sQuery(id+"F0.wireOp",EDGE,"E7.33.4"),sQuery(id+"F0.wireOp",EDGE,"E7.33.5"),sQuery(id+"F0.wireOp",EDGE,"E7.34.0"),sQuery(id+"F0.wireOp",EDGE,"E7.34.1"),sQuery(id+"F0.wireOp",EDGE,"E7.34.2"),sQuery(id+"F0.wireOp",EDGE,"E7.34.3"),sQuery(id+"F0.wireOp",EDGE,"E7.34.4"),sQuery(id+"F0.wireOp",EDGE,"E7.34.5"),sQuery(id+"F0.wireOp",EDGE,"E7.35.0"),sQuery(id+"F0.wireOp",EDGE,"E7.35.1"),sQuery(id+"F0.wireOp",EDGE,"E7.35.2"),sQuery(id+"F0.wireOp",EDGE,"E7.35.3"),sQuery(id+"F0.wireOp",EDGE,"E7.35.4"),sQuery(id+"F0.wireOp",EDGE,"E7.35.5"),sQuery(id+"F0.wireOp",EDGE,"E7.36.0"),sQuery(id+"F0.wireOp",EDGE,"E7.36.1"),sQuery(id+"F0.wireOp",EDGE,"E7.36.2"),sQuery(id+"F0.wireOp",EDGE,"E7.36.3"),sQuery(id+"F0.wireOp",EDGE,"E7.36.4"),sQuery(id+"F0.wireOp",EDGE,"E7.36.5"),subQ0,sQuery(id+"F0.wireOp",EDGE,"E7.37.1"),sQuery(id+"F0.wireOp",EDGE,"E7.37.2"),sQuery(id+"F0.wireOp",EDGE,"E7.37.3"),sQuery(id+"F0.wireOp",EDGE,"E7.37.4"),sQuery(id+"F0.wireOp",EDGE,"E7.37.5"),sQuery(id+"F0.wireOp",EDGE,"E7.38.0"),sQuery(id+"F0.wireOp",EDGE,"E7.38.1"),sQuery(id+"F0.wireOp",EDGE,"E7.38.2"),sQuery(id+"F0.wireOp",EDGE,"E7.38.3"),sQuery(id+"F0.wireOp",EDGE,"E7.38.4"),sQuery(id+"F0.wireOp",EDGE,"E7.38.5"),sQuery(id+"F0.wireOp",EDGE,"E7.39.0"),sQuery(id+"F0.wireOp",EDGE,"E7.39.1"),sQuery(id+"F0.wireOp",EDGE,"E7.39.2"),sQuery(id+"F0.wireOp",EDGE,"E7.39.3"),sQuery(id+"F0.wireOp",EDGE,"E7.39.4"),sQuery(id+"F0.wireOp",EDGE,"E7.39.5"),sQuery(id+"F0.wireOp",EDGE,"E7.40.0"),sQuery(id+"F0.wireOp",EDGE,"E7.40.1"),sQuery(id+"F0.wireOp",EDGE,"E7.40.2"),sQuery(id+"F0.wireOp",EDGE,"E7.40.3"),sQuery(id+"F0.wireOp",EDGE,"E7.40.4"),sQuery(id+"F0.wireOp",EDGE,"E7.40.5"),sQuery(id+"F0.wireOp",EDGE,"E7.41.0"),sQuery(id+"F0.wireOp",EDGE,"E7.41.1"),sQuery(id+"F0.wireOp",EDGE,"E7.41.2"),sQuery(id+"F0.wireOp",EDGE,"E7.41.3"),sQuery(id+"F0.wireOp",EDGE,"E7.41.4"),sQuery(id+"F0.wireOp",EDGE,"E7.41.5"),sQuery(id+"F0.wireOp",EDGE,"E7.42.0"),sQuery(id+"F0.wireOp",EDGE,"E7.42.1"),sQuery(id+"F0.wireOp",EDGE,"E7.42.2"),sQuery(id+"F0.wireOp",EDGE,"E7.42.3"),sQuery(id+"F0.wireOp",EDGE,"E7.42.4"),sQuery(id+"F0.wireOp",EDGE,"E7.42.5"),sQuery(id+"F0.wireOp",EDGE,"E7.43.0"),sQuery(id+"F0.wireOp",EDGE,"E7.43.1"),sQuery(id+"F0.wireOp",EDGE,"E7.43.2"),sQuery(id+"F0.wireOp",EDGE,"E7.43.3"),sQuery(id+"F0.wireOp",EDGE,"E7.43.4"),sQuery(id+"F0.wireOp",EDGE,"E7.43.5")])],"isStart":false})]}),makeQuery(id+"F2.opChamfer","BLEND_FACE",FACE,{"disambiguationData":[OSD([subQ0])]})],"blendedInto":[makeQuery(id+"F2.opChamfer","BLEND_FACE",FACE,{"disambiguationData":[OSD([subQ0])]})]});}
            var Q5;
            {var subQ0=sQuery(id+"F0.wireOp",EDGE,"E7.35.0");Q5=makeQuery(id+"F8.opChamfer","BLEND_EDGE",EDGE,{"blendedFrom":[makeQuery(id+"F2.opChamfer","BLEND_EDGE",EDGE,{"blendedFrom":[makeQuery(id+"F1.opExtrude","CAP_EDGE",EDGE,{"disambiguationData":[OSD([subQ0])],"isStart":false}),makeQuery(id+"F1.opExtrude","CAP_FACE",FACE,{"disambiguationData":[OSD([sQuery(id+"F0.wireOp",EDGE,"E1"),sQuery(id+"F0.wireOp",EDGE,"E2"),sQuery(id+"F0.wireOp",EDGE,"E3"),sQuery(id+"F0.wireOp",EDGE,"E4"),sQuery(id+"F0.wireOp",EDGE,"E5"),sQuery(id+"F0.wireOp",EDGE,"E6"),sQuery(id+"F0.wireOp",EDGE,"E7.1.0"),sQuery(id+"F0.wireOp",EDGE,"E7.1.1"),sQuery(id+"F0.wireOp",EDGE,"E7.1.2"),sQuery(id+"F0.wireOp",EDGE,"E7.1.3"),sQuery(id+"F0.wireOp",EDGE,"E7.1.4"),sQuery(id+"F0.wireOp",EDGE,"E7.1.5"),sQuery(id+"F0.wireOp",EDGE,"E7.2.0"),sQuery(id+"F0.wireOp",EDGE,"E7.2.1"),sQuery(id+"F0.wireOp",EDGE,"E7.2.2"),sQuery(id+"F0.wireOp",EDGE,"E7.2.3"),sQuery(id+"F0.wireOp",EDGE,"E7.2.4"),sQuery(id+"F0.wireOp",EDGE,"E7.2.5"),sQuery(id+"F0.wireOp",EDGE,"E7.3.0"),sQuery(id+"F0.wireOp",EDGE,"E7.3.1"),sQuery(id+"F0.wireOp",EDGE,"E7.3.2"),sQuery(id+"F0.wireOp",EDGE,"E7.3.3"),sQuery(id+"F0.wireOp",EDGE,"E7.3.4"),sQuery(id+"F0.wireOp",EDGE,"E7.3.5"),sQuery(id+"F0.wireOp",EDGE,"E7.4.0"),sQuery(id+"F0.wireOp",EDGE,"E7.4.1"),sQuery(id+"F0.wireOp",EDGE,"E7.4.2"),sQuery(id+"F0.wireOp",EDGE,"E7.4.3"),sQuery(id+"F0.wireOp",EDGE,"E7.4.4"),sQuery(id+"F0.wireOp",EDGE,"E7.4.5"),sQuery(id+"F0.wireOp",EDGE,"E7.5.0"),sQuery(id+"F0.wireOp",EDGE,"E7.5.1"),sQuery(id+"F0.wireOp",EDGE,"E7.5.2"),sQuery(id+"F0.wireOp",EDGE,"E7.5.3"),sQuery(id+"F0.wireOp",EDGE,"E7.5.4"),sQuery(id+"F0.wireOp",EDGE,"E7.5.5"),sQuery(id+"F0.wireOp",EDGE,"E7.6.0"),sQuery(id+"F0.wireOp",EDGE,"E7.6.1"),sQuery(id+"F0.wireOp",EDGE,"E7.6.2"),sQuery(id+"F0.wireOp",EDGE,"E7.6.3"),sQuery(id+"F0.wireOp",EDGE,"E7.6.4"),sQuery(id+"F0.wireOp",EDGE,"E7.6.5"),sQuery(id+"F0.wireOp",EDGE,"E7.7.0"),sQuery(id+"F0.wireOp",EDGE,"E7.7.1"),sQuery(id+"F0.wireOp",EDGE,"E7.7.2"),sQuery(id+"F0.wireOp",EDGE,"E7.7.3"),sQuery(id+"F0.wireOp",EDGE,"E7.7.4"),sQuery(id+"F0.wireOp",EDGE,"E7.7.5"),sQuery(id+"F0.wireOp",EDGE,"E7.8.0"),sQuery(id+"F0.wireOp",EDGE,"E7.8.1"),sQuery(id+"F0.wireOp",EDGE,"E7.8.2"),sQuery(id+"F0.wireOp",EDGE,"E7.8.3"),sQuery(id+"F0.wireOp",EDGE,"E7.8.4"),sQuery(id+"F0.wireOp",EDGE,"E7.8.5"),sQuery(id+"F0.wireOp",EDGE,"E7.9.0"),sQuery(id+"F0.wireOp",EDGE,"E7.9.1"),sQuery(id+"F0.wireOp",EDGE,"E7.9.2"),sQuery(id+"F0.wireOp",EDGE,"E7.9.3"),sQuery(id+"F0.wireOp",EDGE,"E7.9.4"),sQuery(id+"F0.wireOp",EDGE,"E7.9.5"),sQuery(id+"F0.wireOp",EDGE,"E7.10.0"),sQuery(id+"F0.wireOp",EDGE,"E7.10.1"),sQuery(id+"F0.wireOp",EDGE,"E7.10.2"),sQuery(id+"F0.wireOp",EDGE,"E7.10.3"),sQuery(id+"F0.wireOp",EDGE,"E7.10.4"),sQuery(id+"F0.wireOp",EDGE,"E7.10.5"),sQuery(id+"F0.wireOp",EDGE,"E7.11.0"),sQuery(id+"F0.wireOp",EDGE,"E7.11.1"),sQuery(id+"F0.wireOp",EDGE,"E7.11.2"),sQuery(id+"F0.wireOp",EDGE,"E7.11.3"),sQuery(id+"F0.wireOp",EDGE,"E7.11.4"),sQuery(id+"F0.wireOp",EDGE,"E7.11.5"),sQuery(id+"F0.wireOp",EDGE,"E7.12.0"),sQuery(id+"F0.wireOp",EDGE,"E7.12.1"),sQuery(id+"F0.wireOp",EDGE,"E7.12.2"),sQuery(id+"F0.wireOp",EDGE,"E7.12.3"),sQuery(id+"F0.wireOp",EDGE,"E7.12.4"),sQuery(id+"F0.wireOp",EDGE,"E7.12.5"),sQuery(id+"F0.wireOp",EDGE,"E7.13.0"),sQuery(id+"F0.wireOp",EDGE,"E7.13.1"),sQuery(id+"F0.wireOp",EDGE,"E7.13.2"),sQuery(id+"F0.wireOp",EDGE,"E7.13.3"),sQuery(id+"F0.wireOp",EDGE,"E7.13.4"),sQuery(id+"F0.wireOp",EDGE,"E7.13.5"),sQuery(id+"F0.wireOp",EDGE,"E7.14.0"),sQuery(id+"F0.wireOp",EDGE,"E7.14.1"),sQuery(id+"F0.wireOp",EDGE,"E7.14.2"),sQuery(id+"F0.wireOp",EDGE,"E7.14.3"),sQuery(id+"F0.wireOp",EDGE,"E7.14.4"),sQuery(id+"F0.wireOp",EDGE,"E7.14.5"),sQuery(id+"F0.wireOp",EDGE,"E7.15.0"),sQuery(id+"F0.wireOp",EDGE,"E7.15.1"),sQuery(id+"F0.wireOp",EDGE,"E7.15.2"),sQuery(id+"F0.wireOp",EDGE,"E7.15.3"),sQuery(id+"F0.wireOp",EDGE,"E7.15.4"),sQuery(id+"F0.wireOp",EDGE,"E7.15.5"),sQuery(id+"F0.wireOp",EDGE,"E7.16.0"),sQuery(id+"F0.wireOp",EDGE,"E7.16.1"),sQuery(id+"F0.wireOp",EDGE,"E7.16.2"),sQuery(id+"F0.wireOp",EDGE,"E7.16.3"),sQuery(id+"F0.wireOp",EDGE,"E7.16.4"),sQuery(id+"F0.wireOp",EDGE,"E7.16.5"),sQuery(id+"F0.wireOp",EDGE,"E7.17.0"),sQuery(id+"F0.wireOp",EDGE,"E7.17.1"),sQuery(id+"F0.wireOp",EDGE,"E7.17.2"),sQuery(id+"F0.wireOp",EDGE,"E7.17.3"),sQuery(id+"F0.wireOp",EDGE,"E7.17.4"),sQuery(id+"F0.wireOp",EDGE,"E7.17.5"),sQuery(id+"F0.wireOp",EDGE,"E7.18.0"),sQuery(id+"F0.wireOp",EDGE,"E7.18.1"),sQuery(id+"F0.wireOp",EDGE,"E7.18.2"),sQuery(id+"F0.wireOp",EDGE,"E7.18.3"),sQuery(id+"F0.wireOp",EDGE,"E7.18.4"),sQuery(id+"F0.wireOp",EDGE,"E7.18.5"),sQuery(id+"F0.wireOp",EDGE,"E7.19.0"),sQuery(id+"F0.wireOp",EDGE,"E7.19.1"),sQuery(id+"F0.wireOp",EDGE,"E7.19.2"),sQuery(id+"F0.wireOp",EDGE,"E7.19.3"),sQuery(id+"F0.wireOp",EDGE,"E7.19.4"),sQuery(id+"F0.wireOp",EDGE,"E7.19.5"),sQuery(id+"F0.wireOp",EDGE,"E7.20.0"),sQuery(id+"F0.wireOp",EDGE,"E7.20.1"),sQuery(id+"F0.wireOp",EDGE,"E7.20.2"),sQuery(id+"F0.wireOp",EDGE,"E7.20.3"),sQuery(id+"F0.wireOp",EDGE,"E7.20.4"),sQuery(id+"F0.wireOp",EDGE,"E7.20.5"),sQuery(id+"F0.wireOp",EDGE,"E7.21.0"),sQuery(id+"F0.wireOp",EDGE,"E7.21.1"),sQuery(id+"F0.wireOp",EDGE,"E7.21.2"),sQuery(id+"F0.wireOp",EDGE,"E7.21.3"),sQuery(id+"F0.wireOp",EDGE,"E7.21.4"),sQuery(id+"F0.wireOp",EDGE,"E7.21.5"),sQuery(id+"F0.wireOp",EDGE,"E7.22.0"),sQuery(id+"F0.wireOp",EDGE,"E7.22.1"),sQuery(id+"F0.wireOp",EDGE,"E7.22.2"),sQuery(id+"F0.wireOp",EDGE,"E7.22.3"),sQuery(id+"F0.wireOp",EDGE,"E7.22.4"),sQuery(id+"F0.wireOp",EDGE,"E7.22.5"),sQuery(id+"F0.wireOp",EDGE,"E7.23.0"),sQuery(id+"F0.wireOp",EDGE,"E7.23.1"),sQuery(id+"F0.wireOp",EDGE,"E7.23.2"),sQuery(id+"F0.wireOp",EDGE,"E7.23.3"),sQuery(id+"F0.wireOp",EDGE,"E7.23.4"),sQuery(id+"F0.wireOp",EDGE,"E7.23.5"),sQuery(id+"F0.wireOp",EDGE,"E7.24.0"),sQuery(id+"F0.wireOp",EDGE,"E7.24.1"),sQuery(id+"F0.wireOp",EDGE,"E7.24.2"),sQuery(id+"F0.wireOp",EDGE,"E7.24.3"),sQuery(id+"F0.wireOp",EDGE,"E7.24.4"),sQuery(id+"F0.wireOp",EDGE,"E7.24.5"),sQuery(id+"F0.wireOp",EDGE,"E7.25.0"),sQuery(id+"F0.wireOp",EDGE,"E7.25.1"),sQuery(id+"F0.wireOp",EDGE,"E7.25.2"),sQuery(id+"F0.wireOp",EDGE,"E7.25.3"),sQuery(id+"F0.wireOp",EDGE,"E7.25.4"),sQuery(id+"F0.wireOp",EDGE,"E7.25.5"),sQuery(id+"F0.wireOp",EDGE,"E7.26.0"),sQuery(id+"F0.wireOp",EDGE,"E7.26.1"),sQuery(id+"F0.wireOp",EDGE,"E7.26.2"),sQuery(id+"F0.wireOp",EDGE,"E7.26.3"),sQuery(id+"F0.wireOp",EDGE,"E7.26.4"),sQuery(id+"F0.wireOp",EDGE,"E7.26.5"),sQuery(id+"F0.wireOp",EDGE,"E7.27.0"),sQuery(id+"F0.wireOp",EDGE,"E7.27.1"),sQuery(id+"F0.wireOp",EDGE,"E7.27.2"),sQuery(id+"F0.wireOp",EDGE,"E7.27.3"),sQuery(id+"F0.wireOp",EDGE,"E7.27.4"),sQuery(id+"F0.wireOp",EDGE,"E7.27.5"),sQuery(id+"F0.wireOp",EDGE,"E7.28.0"),sQuery(id+"F0.wireOp",EDGE,"E7.28.1"),sQuery(id+"F0.wireOp",EDGE,"E7.28.2"),sQuery(id+"F0.wireOp",EDGE,"E7.28.3"),sQuery(id+"F0.wireOp",EDGE,"E7.28.4"),sQuery(id+"F0.wireOp",EDGE,"E7.28.5"),sQuery(id+"F0.wireOp",EDGE,"E7.29.0"),sQuery(id+"F0.wireOp",EDGE,"E7.29.1"),sQuery(id+"F0.wireOp",EDGE,"E7.29.2"),sQuery(id+"F0.wireOp",EDGE,"E7.29.3"),sQuery(id+"F0.wireOp",EDGE,"E7.29.4"),sQuery(id+"F0.wireOp",EDGE,"E7.29.5"),sQuery(id+"F0.wireOp",EDGE,"E7.30.0"),sQuery(id+"F0.wireOp",EDGE,"E7.30.1"),sQuery(id+"F0.wireOp",EDGE,"E7.30.2"),sQuery(id+"F0.wireOp",EDGE,"E7.30.3"),sQuery(id+"F0.wireOp",EDGE,"E7.30.4"),sQuery(id+"F0.wireOp",EDGE,"E7.30.5"),sQuery(id+"F0.wireOp",EDGE,"E7.31.0"),sQuery(id+"F0.wireOp",EDGE,"E7.31.1"),sQuery(id+"F0.wireOp",EDGE,"E7.31.2"),sQuery(id+"F0.wireOp",EDGE,"E7.31.3"),sQuery(id+"F0.wireOp",EDGE,"E7.31.4"),sQuery(id+"F0.wireOp",EDGE,"E7.31.5"),sQuery(id+"F0.wireOp",EDGE,"E7.32.0"),sQuery(id+"F0.wireOp",EDGE,"E7.32.1"),sQuery(id+"F0.wireOp",EDGE,"E7.32.2"),sQuery(id+"F0.wireOp",EDGE,"E7.32.3"),sQuery(id+"F0.wireOp",EDGE,"E7.32.4"),sQuery(id+"F0.wireOp",EDGE,"E7.32.5"),sQuery(id+"F0.wireOp",EDGE,"E7.33.0"),sQuery(id+"F0.wireOp",EDGE,"E7.33.1"),sQuery(id+"F0.wireOp",EDGE,"E7.33.2"),sQuery(id+"F0.wireOp",EDGE,"E7.33.3"),sQuery(id+"F0.wireOp",EDGE,"E7.33.4"),sQuery(id+"F0.wireOp",EDGE,"E7.33.5"),sQuery(id+"F0.wireOp",EDGE,"E7.34.0"),sQuery(id+"F0.wireOp",EDGE,"E7.34.1"),sQuery(id+"F0.wireOp",EDGE,"E7.34.2"),sQuery(id+"F0.wireOp",EDGE,"E7.34.3"),sQuery(id+"F0.wireOp",EDGE,"E7.34.4"),sQuery(id+"F0.wireOp",EDGE,"E7.34.5"),subQ0,sQuery(id+"F0.wireOp",EDGE,"E7.35.1"),sQuery(id+"F0.wireOp",EDGE,"E7.35.2"),sQuery(id+"F0.wireOp",EDGE,"E7.35.3"),sQuery(id+"F0.wireOp",EDGE,"E7.35.4"),sQuery(id+"F0.wireOp",EDGE,"E7.35.5"),sQuery(id+"F0.wireOp",EDGE,"E7.36.0"),sQuery(id+"F0.wireOp",EDGE,"E7.36.1"),sQuery(id+"F0.wireOp",EDGE,"E7.36.2"),sQuery(id+"F0.wireOp",EDGE,"E7.36.3"),sQuery(id+"F0.wireOp",EDGE,"E7.36.4"),sQuery(id+"F0.wireOp",EDGE,"E7.36.5"),sQuery(id+"F0.wireOp",EDGE,"E7.37.0"),sQuery(id+"F0.wireOp",EDGE,"E7.37.1"),sQuery(id+"F0.wireOp",EDGE,"E7.37.2"),sQuery(id+"F0.wireOp",EDGE,"E7.37.3"),sQuery(id+"F0.wireOp",EDGE,"E7.37.4"),sQuery(id+"F0.wireOp",EDGE,"E7.37.5"),sQuery(id+"F0.wireOp",EDGE,"E7.38.0"),sQuery(id+"F0.wireOp",EDGE,"E7.38.1"),sQuery(id+"F0.wireOp",EDGE,"E7.38.2"),sQuery(id+"F0.wireOp",EDGE,"E7.38.3"),sQuery(id+"F0.wireOp",EDGE,"E7.38.4"),sQuery(id+"F0.wireOp",EDGE,"E7.38.5"),sQuery(id+"F0.wireOp",EDGE,"E7.39.0"),sQuery(id+"F0.wireOp",EDGE,"E7.39.1"),sQuery(id+"F0.wireOp",EDGE,"E7.39.2"),sQuery(id+"F0.wireOp",EDGE,"E7.39.3"),sQuery(id+"F0.wireOp",EDGE,"E7.39.4"),sQuery(id+"F0.wireOp",EDGE,"E7.39.5"),sQuery(id+"F0.wireOp",EDGE,"E7.40.0"),sQuery(id+"F0.wireOp",EDGE,"E7.40.1"),sQuery(id+"F0.wireOp",EDGE,"E7.40.2"),sQuery(id+"F0.wireOp",EDGE,"E7.40.3"),sQuery(id+"F0.wireOp",EDGE,"E7.40.4"),sQuery(id+"F0.wireOp",EDGE,"E7.40.5"),sQuery(id+"F0.wireOp",EDGE,"E7.41.0"),sQuery(id+"F0.wireOp",EDGE,"E7.41.1"),sQuery(id+"F0.wireOp",EDGE,"E7.41.2"),sQuery(id+"F0.wireOp",EDGE,"E7.41.3"),sQuery(id+"F0.wireOp",EDGE,"E7.41.4"),sQuery(id+"F0.wireOp",EDGE,"E7.41.5"),sQuery(id+"F0.wireOp",EDGE,"E7.42.0"),sQuery(id+"F0.wireOp",EDGE,"E7.42.1"),sQuery(id+"F0.wireOp",EDGE,"E7.42.2"),sQuery(id+"F0.wireOp",EDGE,"E7.42.3"),sQuery(id+"F0.wireOp",EDGE,"E7.42.4"),sQuery(id+"F0.wireOp",EDGE,"E7.42.5"),sQuery(id+"F0.wireOp",EDGE,"E7.43.0"),sQuery(id+"F0.wireOp",EDGE,"E7.43.1"),sQuery(id+"F0.wireOp",EDGE,"E7.43.2"),sQuery(id+"F0.wireOp",EDGE,"E7.43.3"),sQuery(id+"F0.wireOp",EDGE,"E7.43.4"),sQuery(id+"F0.wireOp",EDGE,"E7.43.5")])],"isStart":false})],"blendedInto":[makeQuery(id+"F1.opExtrude","CAP_FACE",FACE,{"disambiguationData":[OSD([sQuery(id+"F0.wireOp",EDGE,"E1"),sQuery(id+"F0.wireOp",EDGE,"E2"),sQuery(id+"F0.wireOp",EDGE,"E3"),sQuery(id+"F0.wireOp",EDGE,"E4"),sQuery(id+"F0.wireOp",EDGE,"E5"),sQuery(id+"F0.wireOp",EDGE,"E6"),sQuery(id+"F0.wireOp",EDGE,"E7.1.0"),sQuery(id+"F0.wireOp",EDGE,"E7.1.1"),sQuery(id+"F0.wireOp",EDGE,"E7.1.2"),sQuery(id+"F0.wireOp",EDGE,"E7.1.3"),sQuery(id+"F0.wireOp",EDGE,"E7.1.4"),sQuery(id+"F0.wireOp",EDGE,"E7.1.5"),sQuery(id+"F0.wireOp",EDGE,"E7.2.0"),sQuery(id+"F0.wireOp",EDGE,"E7.2.1"),sQuery(id+"F0.wireOp",EDGE,"E7.2.2"),sQuery(id+"F0.wireOp",EDGE,"E7.2.3"),sQuery(id+"F0.wireOp",EDGE,"E7.2.4"),sQuery(id+"F0.wireOp",EDGE,"E7.2.5"),sQuery(id+"F0.wireOp",EDGE,"E7.3.0"),sQuery(id+"F0.wireOp",EDGE,"E7.3.1"),sQuery(id+"F0.wireOp",EDGE,"E7.3.2"),sQuery(id+"F0.wireOp",EDGE,"E7.3.3"),sQuery(id+"F0.wireOp",EDGE,"E7.3.4"),sQuery(id+"F0.wireOp",EDGE,"E7.3.5"),sQuery(id+"F0.wireOp",EDGE,"E7.4.0"),sQuery(id+"F0.wireOp",EDGE,"E7.4.1"),sQuery(id+"F0.wireOp",EDGE,"E7.4.2"),sQuery(id+"F0.wireOp",EDGE,"E7.4.3"),sQuery(id+"F0.wireOp",EDGE,"E7.4.4"),sQuery(id+"F0.wireOp",EDGE,"E7.4.5"),sQuery(id+"F0.wireOp",EDGE,"E7.5.0"),sQuery(id+"F0.wireOp",EDGE,"E7.5.1"),sQuery(id+"F0.wireOp",EDGE,"E7.5.2"),sQuery(id+"F0.wireOp",EDGE,"E7.5.3"),sQuery(id+"F0.wireOp",EDGE,"E7.5.4"),sQuery(id+"F0.wireOp",EDGE,"E7.5.5"),sQuery(id+"F0.wireOp",EDGE,"E7.6.0"),sQuery(id+"F0.wireOp",EDGE,"E7.6.1"),sQuery(id+"F0.wireOp",EDGE,"E7.6.2"),sQuery(id+"F0.wireOp",EDGE,"E7.6.3"),sQuery(id+"F0.wireOp",EDGE,"E7.6.4"),sQuery(id+"F0.wireOp",EDGE,"E7.6.5"),sQuery(id+"F0.wireOp",EDGE,"E7.7.0"),sQuery(id+"F0.wireOp",EDGE,"E7.7.1"),sQuery(id+"F0.wireOp",EDGE,"E7.7.2"),sQuery(id+"F0.wireOp",EDGE,"E7.7.3"),sQuery(id+"F0.wireOp",EDGE,"E7.7.4"),sQuery(id+"F0.wireOp",EDGE,"E7.7.5"),sQuery(id+"F0.wireOp",EDGE,"E7.8.0"),sQuery(id+"F0.wireOp",EDGE,"E7.8.1"),sQuery(id+"F0.wireOp",EDGE,"E7.8.2"),sQuery(id+"F0.wireOp",EDGE,"E7.8.3"),sQuery(id+"F0.wireOp",EDGE,"E7.8.4"),sQuery(id+"F0.wireOp",EDGE,"E7.8.5"),sQuery(id+"F0.wireOp",EDGE,"E7.9.0"),sQuery(id+"F0.wireOp",EDGE,"E7.9.1"),sQuery(id+"F0.wireOp",EDGE,"E7.9.2"),sQuery(id+"F0.wireOp",EDGE,"E7.9.3"),sQuery(id+"F0.wireOp",EDGE,"E7.9.4"),sQuery(id+"F0.wireOp",EDGE,"E7.9.5"),sQuery(id+"F0.wireOp",EDGE,"E7.10.0"),sQuery(id+"F0.wireOp",EDGE,"E7.10.1"),sQuery(id+"F0.wireOp",EDGE,"E7.10.2"),sQuery(id+"F0.wireOp",EDGE,"E7.10.3"),sQuery(id+"F0.wireOp",EDGE,"E7.10.4"),sQuery(id+"F0.wireOp",EDGE,"E7.10.5"),sQuery(id+"F0.wireOp",EDGE,"E7.11.0"),sQuery(id+"F0.wireOp",EDGE,"E7.11.1"),sQuery(id+"F0.wireOp",EDGE,"E7.11.2"),sQuery(id+"F0.wireOp",EDGE,"E7.11.3"),sQuery(id+"F0.wireOp",EDGE,"E7.11.4"),sQuery(id+"F0.wireOp",EDGE,"E7.11.5"),sQuery(id+"F0.wireOp",EDGE,"E7.12.0"),sQuery(id+"F0.wireOp",EDGE,"E7.12.1"),sQuery(id+"F0.wireOp",EDGE,"E7.12.2"),sQuery(id+"F0.wireOp",EDGE,"E7.12.3"),sQuery(id+"F0.wireOp",EDGE,"E7.12.4"),sQuery(id+"F0.wireOp",EDGE,"E7.12.5"),sQuery(id+"F0.wireOp",EDGE,"E7.13.0"),sQuery(id+"F0.wireOp",EDGE,"E7.13.1"),sQuery(id+"F0.wireOp",EDGE,"E7.13.2"),sQuery(id+"F0.wireOp",EDGE,"E7.13.3"),sQuery(id+"F0.wireOp",EDGE,"E7.13.4"),sQuery(id+"F0.wireOp",EDGE,"E7.13.5"),sQuery(id+"F0.wireOp",EDGE,"E7.14.0"),sQuery(id+"F0.wireOp",EDGE,"E7.14.1"),sQuery(id+"F0.wireOp",EDGE,"E7.14.2"),sQuery(id+"F0.wireOp",EDGE,"E7.14.3"),sQuery(id+"F0.wireOp",EDGE,"E7.14.4"),sQuery(id+"F0.wireOp",EDGE,"E7.14.5"),sQuery(id+"F0.wireOp",EDGE,"E7.15.0"),sQuery(id+"F0.wireOp",EDGE,"E7.15.1"),sQuery(id+"F0.wireOp",EDGE,"E7.15.2"),sQuery(id+"F0.wireOp",EDGE,"E7.15.3"),sQuery(id+"F0.wireOp",EDGE,"E7.15.4"),sQuery(id+"F0.wireOp",EDGE,"E7.15.5"),sQuery(id+"F0.wireOp",EDGE,"E7.16.0"),sQuery(id+"F0.wireOp",EDGE,"E7.16.1"),sQuery(id+"F0.wireOp",EDGE,"E7.16.2"),sQuery(id+"F0.wireOp",EDGE,"E7.16.3"),sQuery(id+"F0.wireOp",EDGE,"E7.16.4"),sQuery(id+"F0.wireOp",EDGE,"E7.16.5"),sQuery(id+"F0.wireOp",EDGE,"E7.17.0"),sQuery(id+"F0.wireOp",EDGE,"E7.17.1"),sQuery(id+"F0.wireOp",EDGE,"E7.17.2"),sQuery(id+"F0.wireOp",EDGE,"E7.17.3"),sQuery(id+"F0.wireOp",EDGE,"E7.17.4"),sQuery(id+"F0.wireOp",EDGE,"E7.17.5"),sQuery(id+"F0.wireOp",EDGE,"E7.18.0"),sQuery(id+"F0.wireOp",EDGE,"E7.18.1"),sQuery(id+"F0.wireOp",EDGE,"E7.18.2"),sQuery(id+"F0.wireOp",EDGE,"E7.18.3"),sQuery(id+"F0.wireOp",EDGE,"E7.18.4"),sQuery(id+"F0.wireOp",EDGE,"E7.18.5"),sQuery(id+"F0.wireOp",EDGE,"E7.19.0"),sQuery(id+"F0.wireOp",EDGE,"E7.19.1"),sQuery(id+"F0.wireOp",EDGE,"E7.19.2"),sQuery(id+"F0.wireOp",EDGE,"E7.19.3"),sQuery(id+"F0.wireOp",EDGE,"E7.19.4"),sQuery(id+"F0.wireOp",EDGE,"E7.19.5"),sQuery(id+"F0.wireOp",EDGE,"E7.20.0"),sQuery(id+"F0.wireOp",EDGE,"E7.20.1"),sQuery(id+"F0.wireOp",EDGE,"E7.20.2"),sQuery(id+"F0.wireOp",EDGE,"E7.20.3"),sQuery(id+"F0.wireOp",EDGE,"E7.20.4"),sQuery(id+"F0.wireOp",EDGE,"E7.20.5"),sQuery(id+"F0.wireOp",EDGE,"E7.21.0"),sQuery(id+"F0.wireOp",EDGE,"E7.21.1"),sQuery(id+"F0.wireOp",EDGE,"E7.21.2"),sQuery(id+"F0.wireOp",EDGE,"E7.21.3"),sQuery(id+"F0.wireOp",EDGE,"E7.21.4"),sQuery(id+"F0.wireOp",EDGE,"E7.21.5"),sQuery(id+"F0.wireOp",EDGE,"E7.22.0"),sQuery(id+"F0.wireOp",EDGE,"E7.22.1"),sQuery(id+"F0.wireOp",EDGE,"E7.22.2"),sQuery(id+"F0.wireOp",EDGE,"E7.22.3"),sQuery(id+"F0.wireOp",EDGE,"E7.22.4"),sQuery(id+"F0.wireOp",EDGE,"E7.22.5"),sQuery(id+"F0.wireOp",EDGE,"E7.23.0"),sQuery(id+"F0.wireOp",EDGE,"E7.23.1"),sQuery(id+"F0.wireOp",EDGE,"E7.23.2"),sQuery(id+"F0.wireOp",EDGE,"E7.23.3"),sQuery(id+"F0.wireOp",EDGE,"E7.23.4"),sQuery(id+"F0.wireOp",EDGE,"E7.23.5"),sQuery(id+"F0.wireOp",EDGE,"E7.24.0"),sQuery(id+"F0.wireOp",EDGE,"E7.24.1"),sQuery(id+"F0.wireOp",EDGE,"E7.24.2"),sQuery(id+"F0.wireOp",EDGE,"E7.24.3"),sQuery(id+"F0.wireOp",EDGE,"E7.24.4"),sQuery(id+"F0.wireOp",EDGE,"E7.24.5"),sQuery(id+"F0.wireOp",EDGE,"E7.25.0"),sQuery(id+"F0.wireOp",EDGE,"E7.25.1"),sQuery(id+"F0.wireOp",EDGE,"E7.25.2"),sQuery(id+"F0.wireOp",EDGE,"E7.25.3"),sQuery(id+"F0.wireOp",EDGE,"E7.25.4"),sQuery(id+"F0.wireOp",EDGE,"E7.25.5"),sQuery(id+"F0.wireOp",EDGE,"E7.26.0"),sQuery(id+"F0.wireOp",EDGE,"E7.26.1"),sQuery(id+"F0.wireOp",EDGE,"E7.26.2"),sQuery(id+"F0.wireOp",EDGE,"E7.26.3"),sQuery(id+"F0.wireOp",EDGE,"E7.26.4"),sQuery(id+"F0.wireOp",EDGE,"E7.26.5"),sQuery(id+"F0.wireOp",EDGE,"E7.27.0"),sQuery(id+"F0.wireOp",EDGE,"E7.27.1"),sQuery(id+"F0.wireOp",EDGE,"E7.27.2"),sQuery(id+"F0.wireOp",EDGE,"E7.27.3"),sQuery(id+"F0.wireOp",EDGE,"E7.27.4"),sQuery(id+"F0.wireOp",EDGE,"E7.27.5"),sQuery(id+"F0.wireOp",EDGE,"E7.28.0"),sQuery(id+"F0.wireOp",EDGE,"E7.28.1"),sQuery(id+"F0.wireOp",EDGE,"E7.28.2"),sQuery(id+"F0.wireOp",EDGE,"E7.28.3"),sQuery(id+"F0.wireOp",EDGE,"E7.28.4"),sQuery(id+"F0.wireOp",EDGE,"E7.28.5"),sQuery(id+"F0.wireOp",EDGE,"E7.29.0"),sQuery(id+"F0.wireOp",EDGE,"E7.29.1"),sQuery(id+"F0.wireOp",EDGE,"E7.29.2"),sQuery(id+"F0.wireOp",EDGE,"E7.29.3"),sQuery(id+"F0.wireOp",EDGE,"E7.29.4"),sQuery(id+"F0.wireOp",EDGE,"E7.29.5"),sQuery(id+"F0.wireOp",EDGE,"E7.30.0"),sQuery(id+"F0.wireOp",EDGE,"E7.30.1"),sQuery(id+"F0.wireOp",EDGE,"E7.30.2"),sQuery(id+"F0.wireOp",EDGE,"E7.30.3"),sQuery(id+"F0.wireOp",EDGE,"E7.30.4"),sQuery(id+"F0.wireOp",EDGE,"E7.30.5"),sQuery(id+"F0.wireOp",EDGE,"E7.31.0"),sQuery(id+"F0.wireOp",EDGE,"E7.31.1"),sQuery(id+"F0.wireOp",EDGE,"E7.31.2"),sQuery(id+"F0.wireOp",EDGE,"E7.31.3"),sQuery(id+"F0.wireOp",EDGE,"E7.31.4"),sQuery(id+"F0.wireOp",EDGE,"E7.31.5"),sQuery(id+"F0.wireOp",EDGE,"E7.32.0"),sQuery(id+"F0.wireOp",EDGE,"E7.32.1"),sQuery(id+"F0.wireOp",EDGE,"E7.32.2"),sQuery(id+"F0.wireOp",EDGE,"E7.32.3"),sQuery(id+"F0.wireOp",EDGE,"E7.32.4"),sQuery(id+"F0.wireOp",EDGE,"E7.32.5"),sQuery(id+"F0.wireOp",EDGE,"E7.33.0"),sQuery(id+"F0.wireOp",EDGE,"E7.33.1"),sQuery(id+"F0.wireOp",EDGE,"E7.33.2"),sQuery(id+"F0.wireOp",EDGE,"E7.33.3"),sQuery(id+"F0.wireOp",EDGE,"E7.33.4"),sQuery(id+"F0.wireOp",EDGE,"E7.33.5"),sQuery(id+"F0.wireOp",EDGE,"E7.34.0"),sQuery(id+"F0.wireOp",EDGE,"E7.34.1"),sQuery(id+"F0.wireOp",EDGE,"E7.34.2"),sQuery(id+"F0.wireOp",EDGE,"E7.34.3"),sQuery(id+"F0.wireOp",EDGE,"E7.34.4"),sQuery(id+"F0.wireOp",EDGE,"E7.34.5"),subQ0,sQuery(id+"F0.wireOp",EDGE,"E7.35.1"),sQuery(id+"F0.wireOp",EDGE,"E7.35.2"),sQuery(id+"F0.wireOp",EDGE,"E7.35.3"),sQuery(id+"F0.wireOp",EDGE,"E7.35.4"),sQuery(id+"F0.wireOp",EDGE,"E7.35.5"),sQuery(id+"F0.wireOp",EDGE,"E7.36.0"),sQuery(id+"F0.wireOp",EDGE,"E7.36.1"),sQuery(id+"F0.wireOp",EDGE,"E7.36.2"),sQuery(id+"F0.wireOp",EDGE,"E7.36.3"),sQuery(id+"F0.wireOp",EDGE,"E7.36.4"),sQuery(id+"F0.wireOp",EDGE,"E7.36.5"),sQuery(id+"F0.wireOp",EDGE,"E7.37.0"),sQuery(id+"F0.wireOp",EDGE,"E7.37.1"),sQuery(id+"F0.wireOp",EDGE,"E7.37.2"),sQuery(id+"F0.wireOp",EDGE,"E7.37.3"),sQuery(id+"F0.wireOp",EDGE,"E7.37.4"),sQuery(id+"F0.wireOp",EDGE,"E7.37.5"),sQuery(id+"F0.wireOp",EDGE,"E7.38.0"),sQuery(id+"F0.wireOp",EDGE,"E7.38.1"),sQuery(id+"F0.wireOp",EDGE,"E7.38.2"),sQuery(id+"F0.wireOp",EDGE,"E7.38.3"),sQuery(id+"F0.wireOp",EDGE,"E7.38.4"),sQuery(id+"F0.wireOp",EDGE,"E7.38.5"),sQuery(id+"F0.wireOp",EDGE,"E7.39.0"),sQuery(id+"F0.wireOp",EDGE,"E7.39.1"),sQuery(id+"F0.wireOp",EDGE,"E7.39.2"),sQuery(id+"F0.wireOp",EDGE,"E7.39.3"),sQuery(id+"F0.wireOp",EDGE,"E7.39.4"),sQuery(id+"F0.wireOp",EDGE,"E7.39.5"),sQuery(id+"F0.wireOp",EDGE,"E7.40.0"),sQuery(id+"F0.wireOp",EDGE,"E7.40.1"),sQuery(id+"F0.wireOp",EDGE,"E7.40.2"),sQuery(id+"F0.wireOp",EDGE,"E7.40.3"),sQuery(id+"F0.wireOp",EDGE,"E7.40.4"),sQuery(id+"F0.wireOp",EDGE,"E7.40.5"),sQuery(id+"F0.wireOp",EDGE,"E7.41.0"),sQuery(id+"F0.wireOp",EDGE,"E7.41.1"),sQuery(id+"F0.wireOp",EDGE,"E7.41.2"),sQuery(id+"F0.wireOp",EDGE,"E7.41.3"),sQuery(id+"F0.wireOp",EDGE,"E7.41.4"),sQuery(id+"F0.wireOp",EDGE,"E7.41.5"),sQuery(id+"F0.wireOp",EDGE,"E7.42.0"),sQuery(id+"F0.wireOp",EDGE,"E7.42.1"),sQuery(id+"F0.wireOp",EDGE,"E7.42.2"),sQuery(id+"F0.wireOp",EDGE,"E7.42.3"),sQuery(id+"F0.wireOp",EDGE,"E7.42.4"),sQuery(id+"F0.wireOp",EDGE,"E7.42.5"),sQuery(id+"F0.wireOp",EDGE,"E7.43.0"),sQuery(id+"F0.wireOp",EDGE,"E7.43.1"),sQuery(id+"F0.wireOp",EDGE,"E7.43.2"),sQuery(id+"F0.wireOp",EDGE,"E7.43.3"),sQuery(id+"F0.wireOp",EDGE,"E7.43.4"),sQuery(id+"F0.wireOp",EDGE,"E7.43.5")])],"isStart":false})]}),makeQuery(id+"F2.opChamfer","BLEND_FACE",FACE,{"disambiguationData":[OSD([subQ0])]})],"blendedInto":[makeQuery(id+"F2.opChamfer","BLEND_FACE",FACE,{"disambiguationData":[OSD([subQ0])]})]});}
            var Q6;
            {var subQ0=sQuery(id+"F0.wireOp",EDGE,"E7.33.0");Q6=makeQuery(id+"F8.opChamfer","BLEND_EDGE",EDGE,{"blendedFrom":[makeQuery(id+"F2.opChamfer","BLEND_EDGE",EDGE,{"blendedFrom":[makeQuery(id+"F1.opExtrude","CAP_EDGE",EDGE,{"disambiguationData":[OSD([subQ0])],"isStart":false}),makeQuery(id+"F1.opExtrude","CAP_FACE",FACE,{"disambiguationData":[OSD([sQuery(id+"F0.wireOp",EDGE,"E1"),sQuery(id+"F0.wireOp",EDGE,"E2"),sQuery(id+"F0.wireOp",EDGE,"E3"),sQuery(id+"F0.wireOp",EDGE,"E4"),sQuery(id+"F0.wireOp",EDGE,"E5"),sQuery(id+"F0.wireOp",EDGE,"E6"),sQuery(id+"F0.wireOp",EDGE,"E7.1.0"),sQuery(id+"F0.wireOp",EDGE,"E7.1.1"),sQuery(id+"F0.wireOp",EDGE,"E7.1.2"),sQuery(id+"F0.wireOp",EDGE,"E7.1.3"),sQuery(id+"F0.wireOp",EDGE,"E7.1.4"),sQuery(id+"F0.wireOp",EDGE,"E7.1.5"),sQuery(id+"F0.wireOp",EDGE,"E7.2.0"),sQuery(id+"F0.wireOp",EDGE,"E7.2.1"),sQuery(id+"F0.wireOp",EDGE,"E7.2.2"),sQuery(id+"F0.wireOp",EDGE,"E7.2.3"),sQuery(id+"F0.wireOp",EDGE,"E7.2.4"),sQuery(id+"F0.wireOp",EDGE,"E7.2.5"),sQuery(id+"F0.wireOp",EDGE,"E7.3.0"),sQuery(id+"F0.wireOp",EDGE,"E7.3.1"),sQuery(id+"F0.wireOp",EDGE,"E7.3.2"),sQuery(id+"F0.wireOp",EDGE,"E7.3.3"),sQuery(id+"F0.wireOp",EDGE,"E7.3.4"),sQuery(id+"F0.wireOp",EDGE,"E7.3.5"),sQuery(id+"F0.wireOp",EDGE,"E7.4.0"),sQuery(id+"F0.wireOp",EDGE,"E7.4.1"),sQuery(id+"F0.wireOp",EDGE,"E7.4.2"),sQuery(id+"F0.wireOp",EDGE,"E7.4.3"),sQuery(id+"F0.wireOp",EDGE,"E7.4.4"),sQuery(id+"F0.wireOp",EDGE,"E7.4.5"),sQuery(id+"F0.wireOp",EDGE,"E7.5.0"),sQuery(id+"F0.wireOp",EDGE,"E7.5.1"),sQuery(id+"F0.wireOp",EDGE,"E7.5.2"),sQuery(id+"F0.wireOp",EDGE,"E7.5.3"),sQuery(id+"F0.wireOp",EDGE,"E7.5.4"),sQuery(id+"F0.wireOp",EDGE,"E7.5.5"),sQuery(id+"F0.wireOp",EDGE,"E7.6.0"),sQuery(id+"F0.wireOp",EDGE,"E7.6.1"),sQuery(id+"F0.wireOp",EDGE,"E7.6.2"),sQuery(id+"F0.wireOp",EDGE,"E7.6.3"),sQuery(id+"F0.wireOp",EDGE,"E7.6.4"),sQuery(id+"F0.wireOp",EDGE,"E7.6.5"),sQuery(id+"F0.wireOp",EDGE,"E7.7.0"),sQuery(id+"F0.wireOp",EDGE,"E7.7.1"),sQuery(id+"F0.wireOp",EDGE,"E7.7.2"),sQuery(id+"F0.wireOp",EDGE,"E7.7.3"),sQuery(id+"F0.wireOp",EDGE,"E7.7.4"),sQuery(id+"F0.wireOp",EDGE,"E7.7.5"),sQuery(id+"F0.wireOp",EDGE,"E7.8.0"),sQuery(id+"F0.wireOp",EDGE,"E7.8.1"),sQuery(id+"F0.wireOp",EDGE,"E7.8.2"),sQuery(id+"F0.wireOp",EDGE,"E7.8.3"),sQuery(id+"F0.wireOp",EDGE,"E7.8.4"),sQuery(id+"F0.wireOp",EDGE,"E7.8.5"),sQuery(id+"F0.wireOp",EDGE,"E7.9.0"),sQuery(id+"F0.wireOp",EDGE,"E7.9.1"),sQuery(id+"F0.wireOp",EDGE,"E7.9.2"),sQuery(id+"F0.wireOp",EDGE,"E7.9.3"),sQuery(id+"F0.wireOp",EDGE,"E7.9.4"),sQuery(id+"F0.wireOp",EDGE,"E7.9.5"),sQuery(id+"F0.wireOp",EDGE,"E7.10.0"),sQuery(id+"F0.wireOp",EDGE,"E7.10.1"),sQuery(id+"F0.wireOp",EDGE,"E7.10.2"),sQuery(id+"F0.wireOp",EDGE,"E7.10.3"),sQuery(id+"F0.wireOp",EDGE,"E7.10.4"),sQuery(id+"F0.wireOp",EDGE,"E7.10.5"),sQuery(id+"F0.wireOp",EDGE,"E7.11.0"),sQuery(id+"F0.wireOp",EDGE,"E7.11.1"),sQuery(id+"F0.wireOp",EDGE,"E7.11.2"),sQuery(id+"F0.wireOp",EDGE,"E7.11.3"),sQuery(id+"F0.wireOp",EDGE,"E7.11.4"),sQuery(id+"F0.wireOp",EDGE,"E7.11.5"),sQuery(id+"F0.wireOp",EDGE,"E7.12.0"),sQuery(id+"F0.wireOp",EDGE,"E7.12.1"),sQuery(id+"F0.wireOp",EDGE,"E7.12.2"),sQuery(id+"F0.wireOp",EDGE,"E7.12.3"),sQuery(id+"F0.wireOp",EDGE,"E7.12.4"),sQuery(id+"F0.wireOp",EDGE,"E7.12.5"),sQuery(id+"F0.wireOp",EDGE,"E7.13.0"),sQuery(id+"F0.wireOp",EDGE,"E7.13.1"),sQuery(id+"F0.wireOp",EDGE,"E7.13.2"),sQuery(id+"F0.wireOp",EDGE,"E7.13.3"),sQuery(id+"F0.wireOp",EDGE,"E7.13.4"),sQuery(id+"F0.wireOp",EDGE,"E7.13.5"),sQuery(id+"F0.wireOp",EDGE,"E7.14.0"),sQuery(id+"F0.wireOp",EDGE,"E7.14.1"),sQuery(id+"F0.wireOp",EDGE,"E7.14.2"),sQuery(id+"F0.wireOp",EDGE,"E7.14.3"),sQuery(id+"F0.wireOp",EDGE,"E7.14.4"),sQuery(id+"F0.wireOp",EDGE,"E7.14.5"),sQuery(id+"F0.wireOp",EDGE,"E7.15.0"),sQuery(id+"F0.wireOp",EDGE,"E7.15.1"),sQuery(id+"F0.wireOp",EDGE,"E7.15.2"),sQuery(id+"F0.wireOp",EDGE,"E7.15.3"),sQuery(id+"F0.wireOp",EDGE,"E7.15.4"),sQuery(id+"F0.wireOp",EDGE,"E7.15.5"),sQuery(id+"F0.wireOp",EDGE,"E7.16.0"),sQuery(id+"F0.wireOp",EDGE,"E7.16.1"),sQuery(id+"F0.wireOp",EDGE,"E7.16.2"),sQuery(id+"F0.wireOp",EDGE,"E7.16.3"),sQuery(id+"F0.wireOp",EDGE,"E7.16.4"),sQuery(id+"F0.wireOp",EDGE,"E7.16.5"),sQuery(id+"F0.wireOp",EDGE,"E7.17.0"),sQuery(id+"F0.wireOp",EDGE,"E7.17.1"),sQuery(id+"F0.wireOp",EDGE,"E7.17.2"),sQuery(id+"F0.wireOp",EDGE,"E7.17.3"),sQuery(id+"F0.wireOp",EDGE,"E7.17.4"),sQuery(id+"F0.wireOp",EDGE,"E7.17.5"),sQuery(id+"F0.wireOp",EDGE,"E7.18.0"),sQuery(id+"F0.wireOp",EDGE,"E7.18.1"),sQuery(id+"F0.wireOp",EDGE,"E7.18.2"),sQuery(id+"F0.wireOp",EDGE,"E7.18.3"),sQuery(id+"F0.wireOp",EDGE,"E7.18.4"),sQuery(id+"F0.wireOp",EDGE,"E7.18.5"),sQuery(id+"F0.wireOp",EDGE,"E7.19.0"),sQuery(id+"F0.wireOp",EDGE,"E7.19.1"),sQuery(id+"F0.wireOp",EDGE,"E7.19.2"),sQuery(id+"F0.wireOp",EDGE,"E7.19.3"),sQuery(id+"F0.wireOp",EDGE,"E7.19.4"),sQuery(id+"F0.wireOp",EDGE,"E7.19.5"),sQuery(id+"F0.wireOp",EDGE,"E7.20.0"),sQuery(id+"F0.wireOp",EDGE,"E7.20.1"),sQuery(id+"F0.wireOp",EDGE,"E7.20.2"),sQuery(id+"F0.wireOp",EDGE,"E7.20.3"),sQuery(id+"F0.wireOp",EDGE,"E7.20.4"),sQuery(id+"F0.wireOp",EDGE,"E7.20.5"),sQuery(id+"F0.wireOp",EDGE,"E7.21.0"),sQuery(id+"F0.wireOp",EDGE,"E7.21.1"),sQuery(id+"F0.wireOp",EDGE,"E7.21.2"),sQuery(id+"F0.wireOp",EDGE,"E7.21.3"),sQuery(id+"F0.wireOp",EDGE,"E7.21.4"),sQuery(id+"F0.wireOp",EDGE,"E7.21.5"),sQuery(id+"F0.wireOp",EDGE,"E7.22.0"),sQuery(id+"F0.wireOp",EDGE,"E7.22.1"),sQuery(id+"F0.wireOp",EDGE,"E7.22.2"),sQuery(id+"F0.wireOp",EDGE,"E7.22.3"),sQuery(id+"F0.wireOp",EDGE,"E7.22.4"),sQuery(id+"F0.wireOp",EDGE,"E7.22.5"),sQuery(id+"F0.wireOp",EDGE,"E7.23.0"),sQuery(id+"F0.wireOp",EDGE,"E7.23.1"),sQuery(id+"F0.wireOp",EDGE,"E7.23.2"),sQuery(id+"F0.wireOp",EDGE,"E7.23.3"),sQuery(id+"F0.wireOp",EDGE,"E7.23.4"),sQuery(id+"F0.wireOp",EDGE,"E7.23.5"),sQuery(id+"F0.wireOp",EDGE,"E7.24.0"),sQuery(id+"F0.wireOp",EDGE,"E7.24.1"),sQuery(id+"F0.wireOp",EDGE,"E7.24.2"),sQuery(id+"F0.wireOp",EDGE,"E7.24.3"),sQuery(id+"F0.wireOp",EDGE,"E7.24.4"),sQuery(id+"F0.wireOp",EDGE,"E7.24.5"),sQuery(id+"F0.wireOp",EDGE,"E7.25.0"),sQuery(id+"F0.wireOp",EDGE,"E7.25.1"),sQuery(id+"F0.wireOp",EDGE,"E7.25.2"),sQuery(id+"F0.wireOp",EDGE,"E7.25.3"),sQuery(id+"F0.wireOp",EDGE,"E7.25.4"),sQuery(id+"F0.wireOp",EDGE,"E7.25.5"),sQuery(id+"F0.wireOp",EDGE,"E7.26.0"),sQuery(id+"F0.wireOp",EDGE,"E7.26.1"),sQuery(id+"F0.wireOp",EDGE,"E7.26.2"),sQuery(id+"F0.wireOp",EDGE,"E7.26.3"),sQuery(id+"F0.wireOp",EDGE,"E7.26.4"),sQuery(id+"F0.wireOp",EDGE,"E7.26.5"),sQuery(id+"F0.wireOp",EDGE,"E7.27.0"),sQuery(id+"F0.wireOp",EDGE,"E7.27.1"),sQuery(id+"F0.wireOp",EDGE,"E7.27.2"),sQuery(id+"F0.wireOp",EDGE,"E7.27.3"),sQuery(id+"F0.wireOp",EDGE,"E7.27.4"),sQuery(id+"F0.wireOp",EDGE,"E7.27.5"),sQuery(id+"F0.wireOp",EDGE,"E7.28.0"),sQuery(id+"F0.wireOp",EDGE,"E7.28.1"),sQuery(id+"F0.wireOp",EDGE,"E7.28.2"),sQuery(id+"F0.wireOp",EDGE,"E7.28.3"),sQuery(id+"F0.wireOp",EDGE,"E7.28.4"),sQuery(id+"F0.wireOp",EDGE,"E7.28.5"),sQuery(id+"F0.wireOp",EDGE,"E7.29.0"),sQuery(id+"F0.wireOp",EDGE,"E7.29.1"),sQuery(id+"F0.wireOp",EDGE,"E7.29.2"),sQuery(id+"F0.wireOp",EDGE,"E7.29.3"),sQuery(id+"F0.wireOp",EDGE,"E7.29.4"),sQuery(id+"F0.wireOp",EDGE,"E7.29.5"),sQuery(id+"F0.wireOp",EDGE,"E7.30.0"),sQuery(id+"F0.wireOp",EDGE,"E7.30.1"),sQuery(id+"F0.wireOp",EDGE,"E7.30.2"),sQuery(id+"F0.wireOp",EDGE,"E7.30.3"),sQuery(id+"F0.wireOp",EDGE,"E7.30.4"),sQuery(id+"F0.wireOp",EDGE,"E7.30.5"),sQuery(id+"F0.wireOp",EDGE,"E7.31.0"),sQuery(id+"F0.wireOp",EDGE,"E7.31.1"),sQuery(id+"F0.wireOp",EDGE,"E7.31.2"),sQuery(id+"F0.wireOp",EDGE,"E7.31.3"),sQuery(id+"F0.wireOp",EDGE,"E7.31.4"),sQuery(id+"F0.wireOp",EDGE,"E7.31.5"),sQuery(id+"F0.wireOp",EDGE,"E7.32.0"),sQuery(id+"F0.wireOp",EDGE,"E7.32.1"),sQuery(id+"F0.wireOp",EDGE,"E7.32.2"),sQuery(id+"F0.wireOp",EDGE,"E7.32.3"),sQuery(id+"F0.wireOp",EDGE,"E7.32.4"),sQuery(id+"F0.wireOp",EDGE,"E7.32.5"),subQ0,sQuery(id+"F0.wireOp",EDGE,"E7.33.1"),sQuery(id+"F0.wireOp",EDGE,"E7.33.2"),sQuery(id+"F0.wireOp",EDGE,"E7.33.3"),sQuery(id+"F0.wireOp",EDGE,"E7.33.4"),sQuery(id+"F0.wireOp",EDGE,"E7.33.5"),sQuery(id+"F0.wireOp",EDGE,"E7.34.0"),sQuery(id+"F0.wireOp",EDGE,"E7.34.1"),sQuery(id+"F0.wireOp",EDGE,"E7.34.2"),sQuery(id+"F0.wireOp",EDGE,"E7.34.3"),sQuery(id+"F0.wireOp",EDGE,"E7.34.4"),sQuery(id+"F0.wireOp",EDGE,"E7.34.5"),sQuery(id+"F0.wireOp",EDGE,"E7.35.0"),sQuery(id+"F0.wireOp",EDGE,"E7.35.1"),sQuery(id+"F0.wireOp",EDGE,"E7.35.2"),sQuery(id+"F0.wireOp",EDGE,"E7.35.3"),sQuery(id+"F0.wireOp",EDGE,"E7.35.4"),sQuery(id+"F0.wireOp",EDGE,"E7.35.5"),sQuery(id+"F0.wireOp",EDGE,"E7.36.0"),sQuery(id+"F0.wireOp",EDGE,"E7.36.1"),sQuery(id+"F0.wireOp",EDGE,"E7.36.2"),sQuery(id+"F0.wireOp",EDGE,"E7.36.3"),sQuery(id+"F0.wireOp",EDGE,"E7.36.4"),sQuery(id+"F0.wireOp",EDGE,"E7.36.5"),sQuery(id+"F0.wireOp",EDGE,"E7.37.0"),sQuery(id+"F0.wireOp",EDGE,"E7.37.1"),sQuery(id+"F0.wireOp",EDGE,"E7.37.2"),sQuery(id+"F0.wireOp",EDGE,"E7.37.3"),sQuery(id+"F0.wireOp",EDGE,"E7.37.4"),sQuery(id+"F0.wireOp",EDGE,"E7.37.5"),sQuery(id+"F0.wireOp",EDGE,"E7.38.0"),sQuery(id+"F0.wireOp",EDGE,"E7.38.1"),sQuery(id+"F0.wireOp",EDGE,"E7.38.2"),sQuery(id+"F0.wireOp",EDGE,"E7.38.3"),sQuery(id+"F0.wireOp",EDGE,"E7.38.4"),sQuery(id+"F0.wireOp",EDGE,"E7.38.5"),sQuery(id+"F0.wireOp",EDGE,"E7.39.0"),sQuery(id+"F0.wireOp",EDGE,"E7.39.1"),sQuery(id+"F0.wireOp",EDGE,"E7.39.2"),sQuery(id+"F0.wireOp",EDGE,"E7.39.3"),sQuery(id+"F0.wireOp",EDGE,"E7.39.4"),sQuery(id+"F0.wireOp",EDGE,"E7.39.5"),sQuery(id+"F0.wireOp",EDGE,"E7.40.0"),sQuery(id+"F0.wireOp",EDGE,"E7.40.1"),sQuery(id+"F0.wireOp",EDGE,"E7.40.2"),sQuery(id+"F0.wireOp",EDGE,"E7.40.3"),sQuery(id+"F0.wireOp",EDGE,"E7.40.4"),sQuery(id+"F0.wireOp",EDGE,"E7.40.5"),sQuery(id+"F0.wireOp",EDGE,"E7.41.0"),sQuery(id+"F0.wireOp",EDGE,"E7.41.1"),sQuery(id+"F0.wireOp",EDGE,"E7.41.2"),sQuery(id+"F0.wireOp",EDGE,"E7.41.3"),sQuery(id+"F0.wireOp",EDGE,"E7.41.4"),sQuery(id+"F0.wireOp",EDGE,"E7.41.5"),sQuery(id+"F0.wireOp",EDGE,"E7.42.0"),sQuery(id+"F0.wireOp",EDGE,"E7.42.1"),sQuery(id+"F0.wireOp",EDGE,"E7.42.2"),sQuery(id+"F0.wireOp",EDGE,"E7.42.3"),sQuery(id+"F0.wireOp",EDGE,"E7.42.4"),sQuery(id+"F0.wireOp",EDGE,"E7.42.5"),sQuery(id+"F0.wireOp",EDGE,"E7.43.0"),sQuery(id+"F0.wireOp",EDGE,"E7.43.1"),sQuery(id+"F0.wireOp",EDGE,"E7.43.2"),sQuery(id+"F0.wireOp",EDGE,"E7.43.3"),sQuery(id+"F0.wireOp",EDGE,"E7.43.4"),sQuery(id+"F0.wireOp",EDGE,"E7.43.5")])],"isStart":false})],"blendedInto":[makeQuery(id+"F1.opExtrude","CAP_FACE",FACE,{"disambiguationData":[OSD([sQuery(id+"F0.wireOp",EDGE,"E1"),sQuery(id+"F0.wireOp",EDGE,"E2"),sQuery(id+"F0.wireOp",EDGE,"E3"),sQuery(id+"F0.wireOp",EDGE,"E4"),sQuery(id+"F0.wireOp",EDGE,"E5"),sQuery(id+"F0.wireOp",EDGE,"E6"),sQuery(id+"F0.wireOp",EDGE,"E7.1.0"),sQuery(id+"F0.wireOp",EDGE,"E7.1.1"),sQuery(id+"F0.wireOp",EDGE,"E7.1.2"),sQuery(id+"F0.wireOp",EDGE,"E7.1.3"),sQuery(id+"F0.wireOp",EDGE,"E7.1.4"),sQuery(id+"F0.wireOp",EDGE,"E7.1.5"),sQuery(id+"F0.wireOp",EDGE,"E7.2.0"),sQuery(id+"F0.wireOp",EDGE,"E7.2.1"),sQuery(id+"F0.wireOp",EDGE,"E7.2.2"),sQuery(id+"F0.wireOp",EDGE,"E7.2.3"),sQuery(id+"F0.wireOp",EDGE,"E7.2.4"),sQuery(id+"F0.wireOp",EDGE,"E7.2.5"),sQuery(id+"F0.wireOp",EDGE,"E7.3.0"),sQuery(id+"F0.wireOp",EDGE,"E7.3.1"),sQuery(id+"F0.wireOp",EDGE,"E7.3.2"),sQuery(id+"F0.wireOp",EDGE,"E7.3.3"),sQuery(id+"F0.wireOp",EDGE,"E7.3.4"),sQuery(id+"F0.wireOp",EDGE,"E7.3.5"),sQuery(id+"F0.wireOp",EDGE,"E7.4.0"),sQuery(id+"F0.wireOp",EDGE,"E7.4.1"),sQuery(id+"F0.wireOp",EDGE,"E7.4.2"),sQuery(id+"F0.wireOp",EDGE,"E7.4.3"),sQuery(id+"F0.wireOp",EDGE,"E7.4.4"),sQuery(id+"F0.wireOp",EDGE,"E7.4.5"),sQuery(id+"F0.wireOp",EDGE,"E7.5.0"),sQuery(id+"F0.wireOp",EDGE,"E7.5.1"),sQuery(id+"F0.wireOp",EDGE,"E7.5.2"),sQuery(id+"F0.wireOp",EDGE,"E7.5.3"),sQuery(id+"F0.wireOp",EDGE,"E7.5.4"),sQuery(id+"F0.wireOp",EDGE,"E7.5.5"),sQuery(id+"F0.wireOp",EDGE,"E7.6.0"),sQuery(id+"F0.wireOp",EDGE,"E7.6.1"),sQuery(id+"F0.wireOp",EDGE,"E7.6.2"),sQuery(id+"F0.wireOp",EDGE,"E7.6.3"),sQuery(id+"F0.wireOp",EDGE,"E7.6.4"),sQuery(id+"F0.wireOp",EDGE,"E7.6.5"),sQuery(id+"F0.wireOp",EDGE,"E7.7.0"),sQuery(id+"F0.wireOp",EDGE,"E7.7.1"),sQuery(id+"F0.wireOp",EDGE,"E7.7.2"),sQuery(id+"F0.wireOp",EDGE,"E7.7.3"),sQuery(id+"F0.wireOp",EDGE,"E7.7.4"),sQuery(id+"F0.wireOp",EDGE,"E7.7.5"),sQuery(id+"F0.wireOp",EDGE,"E7.8.0"),sQuery(id+"F0.wireOp",EDGE,"E7.8.1"),sQuery(id+"F0.wireOp",EDGE,"E7.8.2"),sQuery(id+"F0.wireOp",EDGE,"E7.8.3"),sQuery(id+"F0.wireOp",EDGE,"E7.8.4"),sQuery(id+"F0.wireOp",EDGE,"E7.8.5"),sQuery(id+"F0.wireOp",EDGE,"E7.9.0"),sQuery(id+"F0.wireOp",EDGE,"E7.9.1"),sQuery(id+"F0.wireOp",EDGE,"E7.9.2"),sQuery(id+"F0.wireOp",EDGE,"E7.9.3"),sQuery(id+"F0.wireOp",EDGE,"E7.9.4"),sQuery(id+"F0.wireOp",EDGE,"E7.9.5"),sQuery(id+"F0.wireOp",EDGE,"E7.10.0"),sQuery(id+"F0.wireOp",EDGE,"E7.10.1"),sQuery(id+"F0.wireOp",EDGE,"E7.10.2"),sQuery(id+"F0.wireOp",EDGE,"E7.10.3"),sQuery(id+"F0.wireOp",EDGE,"E7.10.4"),sQuery(id+"F0.wireOp",EDGE,"E7.10.5"),sQuery(id+"F0.wireOp",EDGE,"E7.11.0"),sQuery(id+"F0.wireOp",EDGE,"E7.11.1"),sQuery(id+"F0.wireOp",EDGE,"E7.11.2"),sQuery(id+"F0.wireOp",EDGE,"E7.11.3"),sQuery(id+"F0.wireOp",EDGE,"E7.11.4"),sQuery(id+"F0.wireOp",EDGE,"E7.11.5"),sQuery(id+"F0.wireOp",EDGE,"E7.12.0"),sQuery(id+"F0.wireOp",EDGE,"E7.12.1"),sQuery(id+"F0.wireOp",EDGE,"E7.12.2"),sQuery(id+"F0.wireOp",EDGE,"E7.12.3"),sQuery(id+"F0.wireOp",EDGE,"E7.12.4"),sQuery(id+"F0.wireOp",EDGE,"E7.12.5"),sQuery(id+"F0.wireOp",EDGE,"E7.13.0"),sQuery(id+"F0.wireOp",EDGE,"E7.13.1"),sQuery(id+"F0.wireOp",EDGE,"E7.13.2"),sQuery(id+"F0.wireOp",EDGE,"E7.13.3"),sQuery(id+"F0.wireOp",EDGE,"E7.13.4"),sQuery(id+"F0.wireOp",EDGE,"E7.13.5"),sQuery(id+"F0.wireOp",EDGE,"E7.14.0"),sQuery(id+"F0.wireOp",EDGE,"E7.14.1"),sQuery(id+"F0.wireOp",EDGE,"E7.14.2"),sQuery(id+"F0.wireOp",EDGE,"E7.14.3"),sQuery(id+"F0.wireOp",EDGE,"E7.14.4"),sQuery(id+"F0.wireOp",EDGE,"E7.14.5"),sQuery(id+"F0.wireOp",EDGE,"E7.15.0"),sQuery(id+"F0.wireOp",EDGE,"E7.15.1"),sQuery(id+"F0.wireOp",EDGE,"E7.15.2"),sQuery(id+"F0.wireOp",EDGE,"E7.15.3"),sQuery(id+"F0.wireOp",EDGE,"E7.15.4"),sQuery(id+"F0.wireOp",EDGE,"E7.15.5"),sQuery(id+"F0.wireOp",EDGE,"E7.16.0"),sQuery(id+"F0.wireOp",EDGE,"E7.16.1"),sQuery(id+"F0.wireOp",EDGE,"E7.16.2"),sQuery(id+"F0.wireOp",EDGE,"E7.16.3"),sQuery(id+"F0.wireOp",EDGE,"E7.16.4"),sQuery(id+"F0.wireOp",EDGE,"E7.16.5"),sQuery(id+"F0.wireOp",EDGE,"E7.17.0"),sQuery(id+"F0.wireOp",EDGE,"E7.17.1"),sQuery(id+"F0.wireOp",EDGE,"E7.17.2"),sQuery(id+"F0.wireOp",EDGE,"E7.17.3"),sQuery(id+"F0.wireOp",EDGE,"E7.17.4"),sQuery(id+"F0.wireOp",EDGE,"E7.17.5"),sQuery(id+"F0.wireOp",EDGE,"E7.18.0"),sQuery(id+"F0.wireOp",EDGE,"E7.18.1"),sQuery(id+"F0.wireOp",EDGE,"E7.18.2"),sQuery(id+"F0.wireOp",EDGE,"E7.18.3"),sQuery(id+"F0.wireOp",EDGE,"E7.18.4"),sQuery(id+"F0.wireOp",EDGE,"E7.18.5"),sQuery(id+"F0.wireOp",EDGE,"E7.19.0"),sQuery(id+"F0.wireOp",EDGE,"E7.19.1"),sQuery(id+"F0.wireOp",EDGE,"E7.19.2"),sQuery(id+"F0.wireOp",EDGE,"E7.19.3"),sQuery(id+"F0.wireOp",EDGE,"E7.19.4"),sQuery(id+"F0.wireOp",EDGE,"E7.19.5"),sQuery(id+"F0.wireOp",EDGE,"E7.20.0"),sQuery(id+"F0.wireOp",EDGE,"E7.20.1"),sQuery(id+"F0.wireOp",EDGE,"E7.20.2"),sQuery(id+"F0.wireOp",EDGE,"E7.20.3"),sQuery(id+"F0.wireOp",EDGE,"E7.20.4"),sQuery(id+"F0.wireOp",EDGE,"E7.20.5"),sQuery(id+"F0.wireOp",EDGE,"E7.21.0"),sQuery(id+"F0.wireOp",EDGE,"E7.21.1"),sQuery(id+"F0.wireOp",EDGE,"E7.21.2"),sQuery(id+"F0.wireOp",EDGE,"E7.21.3"),sQuery(id+"F0.wireOp",EDGE,"E7.21.4"),sQuery(id+"F0.wireOp",EDGE,"E7.21.5"),sQuery(id+"F0.wireOp",EDGE,"E7.22.0"),sQuery(id+"F0.wireOp",EDGE,"E7.22.1"),sQuery(id+"F0.wireOp",EDGE,"E7.22.2"),sQuery(id+"F0.wireOp",EDGE,"E7.22.3"),sQuery(id+"F0.wireOp",EDGE,"E7.22.4"),sQuery(id+"F0.wireOp",EDGE,"E7.22.5"),sQuery(id+"F0.wireOp",EDGE,"E7.23.0"),sQuery(id+"F0.wireOp",EDGE,"E7.23.1"),sQuery(id+"F0.wireOp",EDGE,"E7.23.2"),sQuery(id+"F0.wireOp",EDGE,"E7.23.3"),sQuery(id+"F0.wireOp",EDGE,"E7.23.4"),sQuery(id+"F0.wireOp",EDGE,"E7.23.5"),sQuery(id+"F0.wireOp",EDGE,"E7.24.0"),sQuery(id+"F0.wireOp",EDGE,"E7.24.1"),sQuery(id+"F0.wireOp",EDGE,"E7.24.2"),sQuery(id+"F0.wireOp",EDGE,"E7.24.3"),sQuery(id+"F0.wireOp",EDGE,"E7.24.4"),sQuery(id+"F0.wireOp",EDGE,"E7.24.5"),sQuery(id+"F0.wireOp",EDGE,"E7.25.0"),sQuery(id+"F0.wireOp",EDGE,"E7.25.1"),sQuery(id+"F0.wireOp",EDGE,"E7.25.2"),sQuery(id+"F0.wireOp",EDGE,"E7.25.3"),sQuery(id+"F0.wireOp",EDGE,"E7.25.4"),sQuery(id+"F0.wireOp",EDGE,"E7.25.5"),sQuery(id+"F0.wireOp",EDGE,"E7.26.0"),sQuery(id+"F0.wireOp",EDGE,"E7.26.1"),sQuery(id+"F0.wireOp",EDGE,"E7.26.2"),sQuery(id+"F0.wireOp",EDGE,"E7.26.3"),sQuery(id+"F0.wireOp",EDGE,"E7.26.4"),sQuery(id+"F0.wireOp",EDGE,"E7.26.5"),sQuery(id+"F0.wireOp",EDGE,"E7.27.0"),sQuery(id+"F0.wireOp",EDGE,"E7.27.1"),sQuery(id+"F0.wireOp",EDGE,"E7.27.2"),sQuery(id+"F0.wireOp",EDGE,"E7.27.3"),sQuery(id+"F0.wireOp",EDGE,"E7.27.4"),sQuery(id+"F0.wireOp",EDGE,"E7.27.5"),sQuery(id+"F0.wireOp",EDGE,"E7.28.0"),sQuery(id+"F0.wireOp",EDGE,"E7.28.1"),sQuery(id+"F0.wireOp",EDGE,"E7.28.2"),sQuery(id+"F0.wireOp",EDGE,"E7.28.3"),sQuery(id+"F0.wireOp",EDGE,"E7.28.4"),sQuery(id+"F0.wireOp",EDGE,"E7.28.5"),sQuery(id+"F0.wireOp",EDGE,"E7.29.0"),sQuery(id+"F0.wireOp",EDGE,"E7.29.1"),sQuery(id+"F0.wireOp",EDGE,"E7.29.2"),sQuery(id+"F0.wireOp",EDGE,"E7.29.3"),sQuery(id+"F0.wireOp",EDGE,"E7.29.4"),sQuery(id+"F0.wireOp",EDGE,"E7.29.5"),sQuery(id+"F0.wireOp",EDGE,"E7.30.0"),sQuery(id+"F0.wireOp",EDGE,"E7.30.1"),sQuery(id+"F0.wireOp",EDGE,"E7.30.2"),sQuery(id+"F0.wireOp",EDGE,"E7.30.3"),sQuery(id+"F0.wireOp",EDGE,"E7.30.4"),sQuery(id+"F0.wireOp",EDGE,"E7.30.5"),sQuery(id+"F0.wireOp",EDGE,"E7.31.0"),sQuery(id+"F0.wireOp",EDGE,"E7.31.1"),sQuery(id+"F0.wireOp",EDGE,"E7.31.2"),sQuery(id+"F0.wireOp",EDGE,"E7.31.3"),sQuery(id+"F0.wireOp",EDGE,"E7.31.4"),sQuery(id+"F0.wireOp",EDGE,"E7.31.5"),sQuery(id+"F0.wireOp",EDGE,"E7.32.0"),sQuery(id+"F0.wireOp",EDGE,"E7.32.1"),sQuery(id+"F0.wireOp",EDGE,"E7.32.2"),sQuery(id+"F0.wireOp",EDGE,"E7.32.3"),sQuery(id+"F0.wireOp",EDGE,"E7.32.4"),sQuery(id+"F0.wireOp",EDGE,"E7.32.5"),subQ0,sQuery(id+"F0.wireOp",EDGE,"E7.33.1"),sQuery(id+"F0.wireOp",EDGE,"E7.33.2"),sQuery(id+"F0.wireOp",EDGE,"E7.33.3"),sQuery(id+"F0.wireOp",EDGE,"E7.33.4"),sQuery(id+"F0.wireOp",EDGE,"E7.33.5"),sQuery(id+"F0.wireOp",EDGE,"E7.34.0"),sQuery(id+"F0.wireOp",EDGE,"E7.34.1"),sQuery(id+"F0.wireOp",EDGE,"E7.34.2"),sQuery(id+"F0.wireOp",EDGE,"E7.34.3"),sQuery(id+"F0.wireOp",EDGE,"E7.34.4"),sQuery(id+"F0.wireOp",EDGE,"E7.34.5"),sQuery(id+"F0.wireOp",EDGE,"E7.35.0"),sQuery(id+"F0.wireOp",EDGE,"E7.35.1"),sQuery(id+"F0.wireOp",EDGE,"E7.35.2"),sQuery(id+"F0.wireOp",EDGE,"E7.35.3"),sQuery(id+"F0.wireOp",EDGE,"E7.35.4"),sQuery(id+"F0.wireOp",EDGE,"E7.35.5"),sQuery(id+"F0.wireOp",EDGE,"E7.36.0"),sQuery(id+"F0.wireOp",EDGE,"E7.36.1"),sQuery(id+"F0.wireOp",EDGE,"E7.36.2"),sQuery(id+"F0.wireOp",EDGE,"E7.36.3"),sQuery(id+"F0.wireOp",EDGE,"E7.36.4"),sQuery(id+"F0.wireOp",EDGE,"E7.36.5"),sQuery(id+"F0.wireOp",EDGE,"E7.37.0"),sQuery(id+"F0.wireOp",EDGE,"E7.37.1"),sQuery(id+"F0.wireOp",EDGE,"E7.37.2"),sQuery(id+"F0.wireOp",EDGE,"E7.37.3"),sQuery(id+"F0.wireOp",EDGE,"E7.37.4"),sQuery(id+"F0.wireOp",EDGE,"E7.37.5"),sQuery(id+"F0.wireOp",EDGE,"E7.38.0"),sQuery(id+"F0.wireOp",EDGE,"E7.38.1"),sQuery(id+"F0.wireOp",EDGE,"E7.38.2"),sQuery(id+"F0.wireOp",EDGE,"E7.38.3"),sQuery(id+"F0.wireOp",EDGE,"E7.38.4"),sQuery(id+"F0.wireOp",EDGE,"E7.38.5"),sQuery(id+"F0.wireOp",EDGE,"E7.39.0"),sQuery(id+"F0.wireOp",EDGE,"E7.39.1"),sQuery(id+"F0.wireOp",EDGE,"E7.39.2"),sQuery(id+"F0.wireOp",EDGE,"E7.39.3"),sQuery(id+"F0.wireOp",EDGE,"E7.39.4"),sQuery(id+"F0.wireOp",EDGE,"E7.39.5"),sQuery(id+"F0.wireOp",EDGE,"E7.40.0"),sQuery(id+"F0.wireOp",EDGE,"E7.40.1"),sQuery(id+"F0.wireOp",EDGE,"E7.40.2"),sQuery(id+"F0.wireOp",EDGE,"E7.40.3"),sQuery(id+"F0.wireOp",EDGE,"E7.40.4"),sQuery(id+"F0.wireOp",EDGE,"E7.40.5"),sQuery(id+"F0.wireOp",EDGE,"E7.41.0"),sQuery(id+"F0.wireOp",EDGE,"E7.41.1"),sQuery(id+"F0.wireOp",EDGE,"E7.41.2"),sQuery(id+"F0.wireOp",EDGE,"E7.41.3"),sQuery(id+"F0.wireOp",EDGE,"E7.41.4"),sQuery(id+"F0.wireOp",EDGE,"E7.41.5"),sQuery(id+"F0.wireOp",EDGE,"E7.42.0"),sQuery(id+"F0.wireOp",EDGE,"E7.42.1"),sQuery(id+"F0.wireOp",EDGE,"E7.42.2"),sQuery(id+"F0.wireOp",EDGE,"E7.42.3"),sQuery(id+"F0.wireOp",EDGE,"E7.42.4"),sQuery(id+"F0.wireOp",EDGE,"E7.42.5"),sQuery(id+"F0.wireOp",EDGE,"E7.43.0"),sQuery(id+"F0.wireOp",EDGE,"E7.43.1"),sQuery(id+"F0.wireOp",EDGE,"E7.43.2"),sQuery(id+"F0.wireOp",EDGE,"E7.43.3"),sQuery(id+"F0.wireOp",EDGE,"E7.43.4"),sQuery(id+"F0.wireOp",EDGE,"E7.43.5")])],"isStart":false})]}),makeQuery(id+"F2.opChamfer","BLEND_FACE",FACE,{"disambiguationData":[OSD([subQ0])]})],"blendedInto":[makeQuery(id+"F2.opChamfer","BLEND_FACE",FACE,{"disambiguationData":[OSD([subQ0])]})]});}
            var Q7;
            {var subQ0=sQuery(id+"F0.wireOp",EDGE,"E7.31.0");Q7=makeQuery(id+"F8.opChamfer","BLEND_EDGE",EDGE,{"blendedFrom":[makeQuery(id+"F2.opChamfer","BLEND_EDGE",EDGE,{"blendedFrom":[makeQuery(id+"F1.opExtrude","CAP_EDGE",EDGE,{"disambiguationData":[OSD([subQ0])],"isStart":false}),makeQuery(id+"F1.opExtrude","CAP_FACE",FACE,{"disambiguationData":[OSD([sQuery(id+"F0.wireOp",EDGE,"E1"),sQuery(id+"F0.wireOp",EDGE,"E2"),sQuery(id+"F0.wireOp",EDGE,"E3"),sQuery(id+"F0.wireOp",EDGE,"E4"),sQuery(id+"F0.wireOp",EDGE,"E5"),sQuery(id+"F0.wireOp",EDGE,"E6"),sQuery(id+"F0.wireOp",EDGE,"E7.1.0"),sQuery(id+"F0.wireOp",EDGE,"E7.1.1"),sQuery(id+"F0.wireOp",EDGE,"E7.1.2"),sQuery(id+"F0.wireOp",EDGE,"E7.1.3"),sQuery(id+"F0.wireOp",EDGE,"E7.1.4"),sQuery(id+"F0.wireOp",EDGE,"E7.1.5"),sQuery(id+"F0.wireOp",EDGE,"E7.2.0"),sQuery(id+"F0.wireOp",EDGE,"E7.2.1"),sQuery(id+"F0.wireOp",EDGE,"E7.2.2"),sQuery(id+"F0.wireOp",EDGE,"E7.2.3"),sQuery(id+"F0.wireOp",EDGE,"E7.2.4"),sQuery(id+"F0.wireOp",EDGE,"E7.2.5"),sQuery(id+"F0.wireOp",EDGE,"E7.3.0"),sQuery(id+"F0.wireOp",EDGE,"E7.3.1"),sQuery(id+"F0.wireOp",EDGE,"E7.3.2"),sQuery(id+"F0.wireOp",EDGE,"E7.3.3"),sQuery(id+"F0.wireOp",EDGE,"E7.3.4"),sQuery(id+"F0.wireOp",EDGE,"E7.3.5"),sQuery(id+"F0.wireOp",EDGE,"E7.4.0"),sQuery(id+"F0.wireOp",EDGE,"E7.4.1"),sQuery(id+"F0.wireOp",EDGE,"E7.4.2"),sQuery(id+"F0.wireOp",EDGE,"E7.4.3"),sQuery(id+"F0.wireOp",EDGE,"E7.4.4"),sQuery(id+"F0.wireOp",EDGE,"E7.4.5"),sQuery(id+"F0.wireOp",EDGE,"E7.5.0"),sQuery(id+"F0.wireOp",EDGE,"E7.5.1"),sQuery(id+"F0.wireOp",EDGE,"E7.5.2"),sQuery(id+"F0.wireOp",EDGE,"E7.5.3"),sQuery(id+"F0.wireOp",EDGE,"E7.5.4"),sQuery(id+"F0.wireOp",EDGE,"E7.5.5"),sQuery(id+"F0.wireOp",EDGE,"E7.6.0"),sQuery(id+"F0.wireOp",EDGE,"E7.6.1"),sQuery(id+"F0.wireOp",EDGE,"E7.6.2"),sQuery(id+"F0.wireOp",EDGE,"E7.6.3"),sQuery(id+"F0.wireOp",EDGE,"E7.6.4"),sQuery(id+"F0.wireOp",EDGE,"E7.6.5"),sQuery(id+"F0.wireOp",EDGE,"E7.7.0"),sQuery(id+"F0.wireOp",EDGE,"E7.7.1"),sQuery(id+"F0.wireOp",EDGE,"E7.7.2"),sQuery(id+"F0.wireOp",EDGE,"E7.7.3"),sQuery(id+"F0.wireOp",EDGE,"E7.7.4"),sQuery(id+"F0.wireOp",EDGE,"E7.7.5"),sQuery(id+"F0.wireOp",EDGE,"E7.8.0"),sQuery(id+"F0.wireOp",EDGE,"E7.8.1"),sQuery(id+"F0.wireOp",EDGE,"E7.8.2"),sQuery(id+"F0.wireOp",EDGE,"E7.8.3"),sQuery(id+"F0.wireOp",EDGE,"E7.8.4"),sQuery(id+"F0.wireOp",EDGE,"E7.8.5"),sQuery(id+"F0.wireOp",EDGE,"E7.9.0"),sQuery(id+"F0.wireOp",EDGE,"E7.9.1"),sQuery(id+"F0.wireOp",EDGE,"E7.9.2"),sQuery(id+"F0.wireOp",EDGE,"E7.9.3"),sQuery(id+"F0.wireOp",EDGE,"E7.9.4"),sQuery(id+"F0.wireOp",EDGE,"E7.9.5"),sQuery(id+"F0.wireOp",EDGE,"E7.10.0"),sQuery(id+"F0.wireOp",EDGE,"E7.10.1"),sQuery(id+"F0.wireOp",EDGE,"E7.10.2"),sQuery(id+"F0.wireOp",EDGE,"E7.10.3"),sQuery(id+"F0.wireOp",EDGE,"E7.10.4"),sQuery(id+"F0.wireOp",EDGE,"E7.10.5"),sQuery(id+"F0.wireOp",EDGE,"E7.11.0"),sQuery(id+"F0.wireOp",EDGE,"E7.11.1"),sQuery(id+"F0.wireOp",EDGE,"E7.11.2"),sQuery(id+"F0.wireOp",EDGE,"E7.11.3"),sQuery(id+"F0.wireOp",EDGE,"E7.11.4"),sQuery(id+"F0.wireOp",EDGE,"E7.11.5"),sQuery(id+"F0.wireOp",EDGE,"E7.12.0"),sQuery(id+"F0.wireOp",EDGE,"E7.12.1"),sQuery(id+"F0.wireOp",EDGE,"E7.12.2"),sQuery(id+"F0.wireOp",EDGE,"E7.12.3"),sQuery(id+"F0.wireOp",EDGE,"E7.12.4"),sQuery(id+"F0.wireOp",EDGE,"E7.12.5"),sQuery(id+"F0.wireOp",EDGE,"E7.13.0"),sQuery(id+"F0.wireOp",EDGE,"E7.13.1"),sQuery(id+"F0.wireOp",EDGE,"E7.13.2"),sQuery(id+"F0.wireOp",EDGE,"E7.13.3"),sQuery(id+"F0.wireOp",EDGE,"E7.13.4"),sQuery(id+"F0.wireOp",EDGE,"E7.13.5"),sQuery(id+"F0.wireOp",EDGE,"E7.14.0"),sQuery(id+"F0.wireOp",EDGE,"E7.14.1"),sQuery(id+"F0.wireOp",EDGE,"E7.14.2"),sQuery(id+"F0.wireOp",EDGE,"E7.14.3"),sQuery(id+"F0.wireOp",EDGE,"E7.14.4"),sQuery(id+"F0.wireOp",EDGE,"E7.14.5"),sQuery(id+"F0.wireOp",EDGE,"E7.15.0"),sQuery(id+"F0.wireOp",EDGE,"E7.15.1"),sQuery(id+"F0.wireOp",EDGE,"E7.15.2"),sQuery(id+"F0.wireOp",EDGE,"E7.15.3"),sQuery(id+"F0.wireOp",EDGE,"E7.15.4"),sQuery(id+"F0.wireOp",EDGE,"E7.15.5"),sQuery(id+"F0.wireOp",EDGE,"E7.16.0"),sQuery(id+"F0.wireOp",EDGE,"E7.16.1"),sQuery(id+"F0.wireOp",EDGE,"E7.16.2"),sQuery(id+"F0.wireOp",EDGE,"E7.16.3"),sQuery(id+"F0.wireOp",EDGE,"E7.16.4"),sQuery(id+"F0.wireOp",EDGE,"E7.16.5"),sQuery(id+"F0.wireOp",EDGE,"E7.17.0"),sQuery(id+"F0.wireOp",EDGE,"E7.17.1"),sQuery(id+"F0.wireOp",EDGE,"E7.17.2"),sQuery(id+"F0.wireOp",EDGE,"E7.17.3"),sQuery(id+"F0.wireOp",EDGE,"E7.17.4"),sQuery(id+"F0.wireOp",EDGE,"E7.17.5"),sQuery(id+"F0.wireOp",EDGE,"E7.18.0"),sQuery(id+"F0.wireOp",EDGE,"E7.18.1"),sQuery(id+"F0.wireOp",EDGE,"E7.18.2"),sQuery(id+"F0.wireOp",EDGE,"E7.18.3"),sQuery(id+"F0.wireOp",EDGE,"E7.18.4"),sQuery(id+"F0.wireOp",EDGE,"E7.18.5"),sQuery(id+"F0.wireOp",EDGE,"E7.19.0"),sQuery(id+"F0.wireOp",EDGE,"E7.19.1"),sQuery(id+"F0.wireOp",EDGE,"E7.19.2"),sQuery(id+"F0.wireOp",EDGE,"E7.19.3"),sQuery(id+"F0.wireOp",EDGE,"E7.19.4"),sQuery(id+"F0.wireOp",EDGE,"E7.19.5"),sQuery(id+"F0.wireOp",EDGE,"E7.20.0"),sQuery(id+"F0.wireOp",EDGE,"E7.20.1"),sQuery(id+"F0.wireOp",EDGE,"E7.20.2"),sQuery(id+"F0.wireOp",EDGE,"E7.20.3"),sQuery(id+"F0.wireOp",EDGE,"E7.20.4"),sQuery(id+"F0.wireOp",EDGE,"E7.20.5"),sQuery(id+"F0.wireOp",EDGE,"E7.21.0"),sQuery(id+"F0.wireOp",EDGE,"E7.21.1"),sQuery(id+"F0.wireOp",EDGE,"E7.21.2"),sQuery(id+"F0.wireOp",EDGE,"E7.21.3"),sQuery(id+"F0.wireOp",EDGE,"E7.21.4"),sQuery(id+"F0.wireOp",EDGE,"E7.21.5"),sQuery(id+"F0.wireOp",EDGE,"E7.22.0"),sQuery(id+"F0.wireOp",EDGE,"E7.22.1"),sQuery(id+"F0.wireOp",EDGE,"E7.22.2"),sQuery(id+"F0.wireOp",EDGE,"E7.22.3"),sQuery(id+"F0.wireOp",EDGE,"E7.22.4"),sQuery(id+"F0.wireOp",EDGE,"E7.22.5"),sQuery(id+"F0.wireOp",EDGE,"E7.23.0"),sQuery(id+"F0.wireOp",EDGE,"E7.23.1"),sQuery(id+"F0.wireOp",EDGE,"E7.23.2"),sQuery(id+"F0.wireOp",EDGE,"E7.23.3"),sQuery(id+"F0.wireOp",EDGE,"E7.23.4"),sQuery(id+"F0.wireOp",EDGE,"E7.23.5"),sQuery(id+"F0.wireOp",EDGE,"E7.24.0"),sQuery(id+"F0.wireOp",EDGE,"E7.24.1"),sQuery(id+"F0.wireOp",EDGE,"E7.24.2"),sQuery(id+"F0.wireOp",EDGE,"E7.24.3"),sQuery(id+"F0.wireOp",EDGE,"E7.24.4"),sQuery(id+"F0.wireOp",EDGE,"E7.24.5"),sQuery(id+"F0.wireOp",EDGE,"E7.25.0"),sQuery(id+"F0.wireOp",EDGE,"E7.25.1"),sQuery(id+"F0.wireOp",EDGE,"E7.25.2"),sQuery(id+"F0.wireOp",EDGE,"E7.25.3"),sQuery(id+"F0.wireOp",EDGE,"E7.25.4"),sQuery(id+"F0.wireOp",EDGE,"E7.25.5"),sQuery(id+"F0.wireOp",EDGE,"E7.26.0"),sQuery(id+"F0.wireOp",EDGE,"E7.26.1"),sQuery(id+"F0.wireOp",EDGE,"E7.26.2"),sQuery(id+"F0.wireOp",EDGE,"E7.26.3"),sQuery(id+"F0.wireOp",EDGE,"E7.26.4"),sQuery(id+"F0.wireOp",EDGE,"E7.26.5"),sQuery(id+"F0.wireOp",EDGE,"E7.27.0"),sQuery(id+"F0.wireOp",EDGE,"E7.27.1"),sQuery(id+"F0.wireOp",EDGE,"E7.27.2"),sQuery(id+"F0.wireOp",EDGE,"E7.27.3"),sQuery(id+"F0.wireOp",EDGE,"E7.27.4"),sQuery(id+"F0.wireOp",EDGE,"E7.27.5"),sQuery(id+"F0.wireOp",EDGE,"E7.28.0"),sQuery(id+"F0.wireOp",EDGE,"E7.28.1"),sQuery(id+"F0.wireOp",EDGE,"E7.28.2"),sQuery(id+"F0.wireOp",EDGE,"E7.28.3"),sQuery(id+"F0.wireOp",EDGE,"E7.28.4"),sQuery(id+"F0.wireOp",EDGE,"E7.28.5"),sQuery(id+"F0.wireOp",EDGE,"E7.29.0"),sQuery(id+"F0.wireOp",EDGE,"E7.29.1"),sQuery(id+"F0.wireOp",EDGE,"E7.29.2"),sQuery(id+"F0.wireOp",EDGE,"E7.29.3"),sQuery(id+"F0.wireOp",EDGE,"E7.29.4"),sQuery(id+"F0.wireOp",EDGE,"E7.29.5"),sQuery(id+"F0.wireOp",EDGE,"E7.30.0"),sQuery(id+"F0.wireOp",EDGE,"E7.30.1"),sQuery(id+"F0.wireOp",EDGE,"E7.30.2"),sQuery(id+"F0.wireOp",EDGE,"E7.30.3"),sQuery(id+"F0.wireOp",EDGE,"E7.30.4"),sQuery(id+"F0.wireOp",EDGE,"E7.30.5"),subQ0,sQuery(id+"F0.wireOp",EDGE,"E7.31.1"),sQuery(id+"F0.wireOp",EDGE,"E7.31.2"),sQuery(id+"F0.wireOp",EDGE,"E7.31.3"),sQuery(id+"F0.wireOp",EDGE,"E7.31.4"),sQuery(id+"F0.wireOp",EDGE,"E7.31.5"),sQuery(id+"F0.wireOp",EDGE,"E7.32.0"),sQuery(id+"F0.wireOp",EDGE,"E7.32.1"),sQuery(id+"F0.wireOp",EDGE,"E7.32.2"),sQuery(id+"F0.wireOp",EDGE,"E7.32.3"),sQuery(id+"F0.wireOp",EDGE,"E7.32.4"),sQuery(id+"F0.wireOp",EDGE,"E7.32.5"),sQuery(id+"F0.wireOp",EDGE,"E7.33.0"),sQuery(id+"F0.wireOp",EDGE,"E7.33.1"),sQuery(id+"F0.wireOp",EDGE,"E7.33.2"),sQuery(id+"F0.wireOp",EDGE,"E7.33.3"),sQuery(id+"F0.wireOp",EDGE,"E7.33.4"),sQuery(id+"F0.wireOp",EDGE,"E7.33.5"),sQuery(id+"F0.wireOp",EDGE,"E7.34.0"),sQuery(id+"F0.wireOp",EDGE,"E7.34.1"),sQuery(id+"F0.wireOp",EDGE,"E7.34.2"),sQuery(id+"F0.wireOp",EDGE,"E7.34.3"),sQuery(id+"F0.wireOp",EDGE,"E7.34.4"),sQuery(id+"F0.wireOp",EDGE,"E7.34.5"),sQuery(id+"F0.wireOp",EDGE,"E7.35.0"),sQuery(id+"F0.wireOp",EDGE,"E7.35.1"),sQuery(id+"F0.wireOp",EDGE,"E7.35.2"),sQuery(id+"F0.wireOp",EDGE,"E7.35.3"),sQuery(id+"F0.wireOp",EDGE,"E7.35.4"),sQuery(id+"F0.wireOp",EDGE,"E7.35.5"),sQuery(id+"F0.wireOp",EDGE,"E7.36.0"),sQuery(id+"F0.wireOp",EDGE,"E7.36.1"),sQuery(id+"F0.wireOp",EDGE,"E7.36.2"),sQuery(id+"F0.wireOp",EDGE,"E7.36.3"),sQuery(id+"F0.wireOp",EDGE,"E7.36.4"),sQuery(id+"F0.wireOp",EDGE,"E7.36.5"),sQuery(id+"F0.wireOp",EDGE,"E7.37.0"),sQuery(id+"F0.wireOp",EDGE,"E7.37.1"),sQuery(id+"F0.wireOp",EDGE,"E7.37.2"),sQuery(id+"F0.wireOp",EDGE,"E7.37.3"),sQuery(id+"F0.wireOp",EDGE,"E7.37.4"),sQuery(id+"F0.wireOp",EDGE,"E7.37.5"),sQuery(id+"F0.wireOp",EDGE,"E7.38.0"),sQuery(id+"F0.wireOp",EDGE,"E7.38.1"),sQuery(id+"F0.wireOp",EDGE,"E7.38.2"),sQuery(id+"F0.wireOp",EDGE,"E7.38.3"),sQuery(id+"F0.wireOp",EDGE,"E7.38.4"),sQuery(id+"F0.wireOp",EDGE,"E7.38.5"),sQuery(id+"F0.wireOp",EDGE,"E7.39.0"),sQuery(id+"F0.wireOp",EDGE,"E7.39.1"),sQuery(id+"F0.wireOp",EDGE,"E7.39.2"),sQuery(id+"F0.wireOp",EDGE,"E7.39.3"),sQuery(id+"F0.wireOp",EDGE,"E7.39.4"),sQuery(id+"F0.wireOp",EDGE,"E7.39.5"),sQuery(id+"F0.wireOp",EDGE,"E7.40.0"),sQuery(id+"F0.wireOp",EDGE,"E7.40.1"),sQuery(id+"F0.wireOp",EDGE,"E7.40.2"),sQuery(id+"F0.wireOp",EDGE,"E7.40.3"),sQuery(id+"F0.wireOp",EDGE,"E7.40.4"),sQuery(id+"F0.wireOp",EDGE,"E7.40.5"),sQuery(id+"F0.wireOp",EDGE,"E7.41.0"),sQuery(id+"F0.wireOp",EDGE,"E7.41.1"),sQuery(id+"F0.wireOp",EDGE,"E7.41.2"),sQuery(id+"F0.wireOp",EDGE,"E7.41.3"),sQuery(id+"F0.wireOp",EDGE,"E7.41.4"),sQuery(id+"F0.wireOp",EDGE,"E7.41.5"),sQuery(id+"F0.wireOp",EDGE,"E7.42.0"),sQuery(id+"F0.wireOp",EDGE,"E7.42.1"),sQuery(id+"F0.wireOp",EDGE,"E7.42.2"),sQuery(id+"F0.wireOp",EDGE,"E7.42.3"),sQuery(id+"F0.wireOp",EDGE,"E7.42.4"),sQuery(id+"F0.wireOp",EDGE,"E7.42.5"),sQuery(id+"F0.wireOp",EDGE,"E7.43.0"),sQuery(id+"F0.wireOp",EDGE,"E7.43.1"),sQuery(id+"F0.wireOp",EDGE,"E7.43.2"),sQuery(id+"F0.wireOp",EDGE,"E7.43.3"),sQuery(id+"F0.wireOp",EDGE,"E7.43.4"),sQuery(id+"F0.wireOp",EDGE,"E7.43.5")])],"isStart":false})],"blendedInto":[makeQuery(id+"F1.opExtrude","CAP_FACE",FACE,{"disambiguationData":[OSD([sQuery(id+"F0.wireOp",EDGE,"E1"),sQuery(id+"F0.wireOp",EDGE,"E2"),sQuery(id+"F0.wireOp",EDGE,"E3"),sQuery(id+"F0.wireOp",EDGE,"E4"),sQuery(id+"F0.wireOp",EDGE,"E5"),sQuery(id+"F0.wireOp",EDGE,"E6"),sQuery(id+"F0.wireOp",EDGE,"E7.1.0"),sQuery(id+"F0.wireOp",EDGE,"E7.1.1"),sQuery(id+"F0.wireOp",EDGE,"E7.1.2"),sQuery(id+"F0.wireOp",EDGE,"E7.1.3"),sQuery(id+"F0.wireOp",EDGE,"E7.1.4"),sQuery(id+"F0.wireOp",EDGE,"E7.1.5"),sQuery(id+"F0.wireOp",EDGE,"E7.2.0"),sQuery(id+"F0.wireOp",EDGE,"E7.2.1"),sQuery(id+"F0.wireOp",EDGE,"E7.2.2"),sQuery(id+"F0.wireOp",EDGE,"E7.2.3"),sQuery(id+"F0.wireOp",EDGE,"E7.2.4"),sQuery(id+"F0.wireOp",EDGE,"E7.2.5"),sQuery(id+"F0.wireOp",EDGE,"E7.3.0"),sQuery(id+"F0.wireOp",EDGE,"E7.3.1"),sQuery(id+"F0.wireOp",EDGE,"E7.3.2"),sQuery(id+"F0.wireOp",EDGE,"E7.3.3"),sQuery(id+"F0.wireOp",EDGE,"E7.3.4"),sQuery(id+"F0.wireOp",EDGE,"E7.3.5"),sQuery(id+"F0.wireOp",EDGE,"E7.4.0"),sQuery(id+"F0.wireOp",EDGE,"E7.4.1"),sQuery(id+"F0.wireOp",EDGE,"E7.4.2"),sQuery(id+"F0.wireOp",EDGE,"E7.4.3"),sQuery(id+"F0.wireOp",EDGE,"E7.4.4"),sQuery(id+"F0.wireOp",EDGE,"E7.4.5"),sQuery(id+"F0.wireOp",EDGE,"E7.5.0"),sQuery(id+"F0.wireOp",EDGE,"E7.5.1"),sQuery(id+"F0.wireOp",EDGE,"E7.5.2"),sQuery(id+"F0.wireOp",EDGE,"E7.5.3"),sQuery(id+"F0.wireOp",EDGE,"E7.5.4"),sQuery(id+"F0.wireOp",EDGE,"E7.5.5"),sQuery(id+"F0.wireOp",EDGE,"E7.6.0"),sQuery(id+"F0.wireOp",EDGE,"E7.6.1"),sQuery(id+"F0.wireOp",EDGE,"E7.6.2"),sQuery(id+"F0.wireOp",EDGE,"E7.6.3"),sQuery(id+"F0.wireOp",EDGE,"E7.6.4"),sQuery(id+"F0.wireOp",EDGE,"E7.6.5"),sQuery(id+"F0.wireOp",EDGE,"E7.7.0"),sQuery(id+"F0.wireOp",EDGE,"E7.7.1"),sQuery(id+"F0.wireOp",EDGE,"E7.7.2"),sQuery(id+"F0.wireOp",EDGE,"E7.7.3"),sQuery(id+"F0.wireOp",EDGE,"E7.7.4"),sQuery(id+"F0.wireOp",EDGE,"E7.7.5"),sQuery(id+"F0.wireOp",EDGE,"E7.8.0"),sQuery(id+"F0.wireOp",EDGE,"E7.8.1"),sQuery(id+"F0.wireOp",EDGE,"E7.8.2"),sQuery(id+"F0.wireOp",EDGE,"E7.8.3"),sQuery(id+"F0.wireOp",EDGE,"E7.8.4"),sQuery(id+"F0.wireOp",EDGE,"E7.8.5"),sQuery(id+"F0.wireOp",EDGE,"E7.9.0"),sQuery(id+"F0.wireOp",EDGE,"E7.9.1"),sQuery(id+"F0.wireOp",EDGE,"E7.9.2"),sQuery(id+"F0.wireOp",EDGE,"E7.9.3"),sQuery(id+"F0.wireOp",EDGE,"E7.9.4"),sQuery(id+"F0.wireOp",EDGE,"E7.9.5"),sQuery(id+"F0.wireOp",EDGE,"E7.10.0"),sQuery(id+"F0.wireOp",EDGE,"E7.10.1"),sQuery(id+"F0.wireOp",EDGE,"E7.10.2"),sQuery(id+"F0.wireOp",EDGE,"E7.10.3"),sQuery(id+"F0.wireOp",EDGE,"E7.10.4"),sQuery(id+"F0.wireOp",EDGE,"E7.10.5"),sQuery(id+"F0.wireOp",EDGE,"E7.11.0"),sQuery(id+"F0.wireOp",EDGE,"E7.11.1"),sQuery(id+"F0.wireOp",EDGE,"E7.11.2"),sQuery(id+"F0.wireOp",EDGE,"E7.11.3"),sQuery(id+"F0.wireOp",EDGE,"E7.11.4"),sQuery(id+"F0.wireOp",EDGE,"E7.11.5"),sQuery(id+"F0.wireOp",EDGE,"E7.12.0"),sQuery(id+"F0.wireOp",EDGE,"E7.12.1"),sQuery(id+"F0.wireOp",EDGE,"E7.12.2"),sQuery(id+"F0.wireOp",EDGE,"E7.12.3"),sQuery(id+"F0.wireOp",EDGE,"E7.12.4"),sQuery(id+"F0.wireOp",EDGE,"E7.12.5"),sQuery(id+"F0.wireOp",EDGE,"E7.13.0"),sQuery(id+"F0.wireOp",EDGE,"E7.13.1"),sQuery(id+"F0.wireOp",EDGE,"E7.13.2"),sQuery(id+"F0.wireOp",EDGE,"E7.13.3"),sQuery(id+"F0.wireOp",EDGE,"E7.13.4"),sQuery(id+"F0.wireOp",EDGE,"E7.13.5"),sQuery(id+"F0.wireOp",EDGE,"E7.14.0"),sQuery(id+"F0.wireOp",EDGE,"E7.14.1"),sQuery(id+"F0.wireOp",EDGE,"E7.14.2"),sQuery(id+"F0.wireOp",EDGE,"E7.14.3"),sQuery(id+"F0.wireOp",EDGE,"E7.14.4"),sQuery(id+"F0.wireOp",EDGE,"E7.14.5"),sQuery(id+"F0.wireOp",EDGE,"E7.15.0"),sQuery(id+"F0.wireOp",EDGE,"E7.15.1"),sQuery(id+"F0.wireOp",EDGE,"E7.15.2"),sQuery(id+"F0.wireOp",EDGE,"E7.15.3"),sQuery(id+"F0.wireOp",EDGE,"E7.15.4"),sQuery(id+"F0.wireOp",EDGE,"E7.15.5"),sQuery(id+"F0.wireOp",EDGE,"E7.16.0"),sQuery(id+"F0.wireOp",EDGE,"E7.16.1"),sQuery(id+"F0.wireOp",EDGE,"E7.16.2"),sQuery(id+"F0.wireOp",EDGE,"E7.16.3"),sQuery(id+"F0.wireOp",EDGE,"E7.16.4"),sQuery(id+"F0.wireOp",EDGE,"E7.16.5"),sQuery(id+"F0.wireOp",EDGE,"E7.17.0"),sQuery(id+"F0.wireOp",EDGE,"E7.17.1"),sQuery(id+"F0.wireOp",EDGE,"E7.17.2"),sQuery(id+"F0.wireOp",EDGE,"E7.17.3"),sQuery(id+"F0.wireOp",EDGE,"E7.17.4"),sQuery(id+"F0.wireOp",EDGE,"E7.17.5"),sQuery(id+"F0.wireOp",EDGE,"E7.18.0"),sQuery(id+"F0.wireOp",EDGE,"E7.18.1"),sQuery(id+"F0.wireOp",EDGE,"E7.18.2"),sQuery(id+"F0.wireOp",EDGE,"E7.18.3"),sQuery(id+"F0.wireOp",EDGE,"E7.18.4"),sQuery(id+"F0.wireOp",EDGE,"E7.18.5"),sQuery(id+"F0.wireOp",EDGE,"E7.19.0"),sQuery(id+"F0.wireOp",EDGE,"E7.19.1"),sQuery(id+"F0.wireOp",EDGE,"E7.19.2"),sQuery(id+"F0.wireOp",EDGE,"E7.19.3"),sQuery(id+"F0.wireOp",EDGE,"E7.19.4"),sQuery(id+"F0.wireOp",EDGE,"E7.19.5"),sQuery(id+"F0.wireOp",EDGE,"E7.20.0"),sQuery(id+"F0.wireOp",EDGE,"E7.20.1"),sQuery(id+"F0.wireOp",EDGE,"E7.20.2"),sQuery(id+"F0.wireOp",EDGE,"E7.20.3"),sQuery(id+"F0.wireOp",EDGE,"E7.20.4"),sQuery(id+"F0.wireOp",EDGE,"E7.20.5"),sQuery(id+"F0.wireOp",EDGE,"E7.21.0"),sQuery(id+"F0.wireOp",EDGE,"E7.21.1"),sQuery(id+"F0.wireOp",EDGE,"E7.21.2"),sQuery(id+"F0.wireOp",EDGE,"E7.21.3"),sQuery(id+"F0.wireOp",EDGE,"E7.21.4"),sQuery(id+"F0.wireOp",EDGE,"E7.21.5"),sQuery(id+"F0.wireOp",EDGE,"E7.22.0"),sQuery(id+"F0.wireOp",EDGE,"E7.22.1"),sQuery(id+"F0.wireOp",EDGE,"E7.22.2"),sQuery(id+"F0.wireOp",EDGE,"E7.22.3"),sQuery(id+"F0.wireOp",EDGE,"E7.22.4"),sQuery(id+"F0.wireOp",EDGE,"E7.22.5"),sQuery(id+"F0.wireOp",EDGE,"E7.23.0"),sQuery(id+"F0.wireOp",EDGE,"E7.23.1"),sQuery(id+"F0.wireOp",EDGE,"E7.23.2"),sQuery(id+"F0.wireOp",EDGE,"E7.23.3"),sQuery(id+"F0.wireOp",EDGE,"E7.23.4"),sQuery(id+"F0.wireOp",EDGE,"E7.23.5"),sQuery(id+"F0.wireOp",EDGE,"E7.24.0"),sQuery(id+"F0.wireOp",EDGE,"E7.24.1"),sQuery(id+"F0.wireOp",EDGE,"E7.24.2"),sQuery(id+"F0.wireOp",EDGE,"E7.24.3"),sQuery(id+"F0.wireOp",EDGE,"E7.24.4"),sQuery(id+"F0.wireOp",EDGE,"E7.24.5"),sQuery(id+"F0.wireOp",EDGE,"E7.25.0"),sQuery(id+"F0.wireOp",EDGE,"E7.25.1"),sQuery(id+"F0.wireOp",EDGE,"E7.25.2"),sQuery(id+"F0.wireOp",EDGE,"E7.25.3"),sQuery(id+"F0.wireOp",EDGE,"E7.25.4"),sQuery(id+"F0.wireOp",EDGE,"E7.25.5"),sQuery(id+"F0.wireOp",EDGE,"E7.26.0"),sQuery(id+"F0.wireOp",EDGE,"E7.26.1"),sQuery(id+"F0.wireOp",EDGE,"E7.26.2"),sQuery(id+"F0.wireOp",EDGE,"E7.26.3"),sQuery(id+"F0.wireOp",EDGE,"E7.26.4"),sQuery(id+"F0.wireOp",EDGE,"E7.26.5"),sQuery(id+"F0.wireOp",EDGE,"E7.27.0"),sQuery(id+"F0.wireOp",EDGE,"E7.27.1"),sQuery(id+"F0.wireOp",EDGE,"E7.27.2"),sQuery(id+"F0.wireOp",EDGE,"E7.27.3"),sQuery(id+"F0.wireOp",EDGE,"E7.27.4"),sQuery(id+"F0.wireOp",EDGE,"E7.27.5"),sQuery(id+"F0.wireOp",EDGE,"E7.28.0"),sQuery(id+"F0.wireOp",EDGE,"E7.28.1"),sQuery(id+"F0.wireOp",EDGE,"E7.28.2"),sQuery(id+"F0.wireOp",EDGE,"E7.28.3"),sQuery(id+"F0.wireOp",EDGE,"E7.28.4"),sQuery(id+"F0.wireOp",EDGE,"E7.28.5"),sQuery(id+"F0.wireOp",EDGE,"E7.29.0"),sQuery(id+"F0.wireOp",EDGE,"E7.29.1"),sQuery(id+"F0.wireOp",EDGE,"E7.29.2"),sQuery(id+"F0.wireOp",EDGE,"E7.29.3"),sQuery(id+"F0.wireOp",EDGE,"E7.29.4"),sQuery(id+"F0.wireOp",EDGE,"E7.29.5"),sQuery(id+"F0.wireOp",EDGE,"E7.30.0"),sQuery(id+"F0.wireOp",EDGE,"E7.30.1"),sQuery(id+"F0.wireOp",EDGE,"E7.30.2"),sQuery(id+"F0.wireOp",EDGE,"E7.30.3"),sQuery(id+"F0.wireOp",EDGE,"E7.30.4"),sQuery(id+"F0.wireOp",EDGE,"E7.30.5"),subQ0,sQuery(id+"F0.wireOp",EDGE,"E7.31.1"),sQuery(id+"F0.wireOp",EDGE,"E7.31.2"),sQuery(id+"F0.wireOp",EDGE,"E7.31.3"),sQuery(id+"F0.wireOp",EDGE,"E7.31.4"),sQuery(id+"F0.wireOp",EDGE,"E7.31.5"),sQuery(id+"F0.wireOp",EDGE,"E7.32.0"),sQuery(id+"F0.wireOp",EDGE,"E7.32.1"),sQuery(id+"F0.wireOp",EDGE,"E7.32.2"),sQuery(id+"F0.wireOp",EDGE,"E7.32.3"),sQuery(id+"F0.wireOp",EDGE,"E7.32.4"),sQuery(id+"F0.wireOp",EDGE,"E7.32.5"),sQuery(id+"F0.wireOp",EDGE,"E7.33.0"),sQuery(id+"F0.wireOp",EDGE,"E7.33.1"),sQuery(id+"F0.wireOp",EDGE,"E7.33.2"),sQuery(id+"F0.wireOp",EDGE,"E7.33.3"),sQuery(id+"F0.wireOp",EDGE,"E7.33.4"),sQuery(id+"F0.wireOp",EDGE,"E7.33.5"),sQuery(id+"F0.wireOp",EDGE,"E7.34.0"),sQuery(id+"F0.wireOp",EDGE,"E7.34.1"),sQuery(id+"F0.wireOp",EDGE,"E7.34.2"),sQuery(id+"F0.wireOp",EDGE,"E7.34.3"),sQuery(id+"F0.wireOp",EDGE,"E7.34.4"),sQuery(id+"F0.wireOp",EDGE,"E7.34.5"),sQuery(id+"F0.wireOp",EDGE,"E7.35.0"),sQuery(id+"F0.wireOp",EDGE,"E7.35.1"),sQuery(id+"F0.wireOp",EDGE,"E7.35.2"),sQuery(id+"F0.wireOp",EDGE,"E7.35.3"),sQuery(id+"F0.wireOp",EDGE,"E7.35.4"),sQuery(id+"F0.wireOp",EDGE,"E7.35.5"),sQuery(id+"F0.wireOp",EDGE,"E7.36.0"),sQuery(id+"F0.wireOp",EDGE,"E7.36.1"),sQuery(id+"F0.wireOp",EDGE,"E7.36.2"),sQuery(id+"F0.wireOp",EDGE,"E7.36.3"),sQuery(id+"F0.wireOp",EDGE,"E7.36.4"),sQuery(id+"F0.wireOp",EDGE,"E7.36.5"),sQuery(id+"F0.wireOp",EDGE,"E7.37.0"),sQuery(id+"F0.wireOp",EDGE,"E7.37.1"),sQuery(id+"F0.wireOp",EDGE,"E7.37.2"),sQuery(id+"F0.wireOp",EDGE,"E7.37.3"),sQuery(id+"F0.wireOp",EDGE,"E7.37.4"),sQuery(id+"F0.wireOp",EDGE,"E7.37.5"),sQuery(id+"F0.wireOp",EDGE,"E7.38.0"),sQuery(id+"F0.wireOp",EDGE,"E7.38.1"),sQuery(id+"F0.wireOp",EDGE,"E7.38.2"),sQuery(id+"F0.wireOp",EDGE,"E7.38.3"),sQuery(id+"F0.wireOp",EDGE,"E7.38.4"),sQuery(id+"F0.wireOp",EDGE,"E7.38.5"),sQuery(id+"F0.wireOp",EDGE,"E7.39.0"),sQuery(id+"F0.wireOp",EDGE,"E7.39.1"),sQuery(id+"F0.wireOp",EDGE,"E7.39.2"),sQuery(id+"F0.wireOp",EDGE,"E7.39.3"),sQuery(id+"F0.wireOp",EDGE,"E7.39.4"),sQuery(id+"F0.wireOp",EDGE,"E7.39.5"),sQuery(id+"F0.wireOp",EDGE,"E7.40.0"),sQuery(id+"F0.wireOp",EDGE,"E7.40.1"),sQuery(id+"F0.wireOp",EDGE,"E7.40.2"),sQuery(id+"F0.wireOp",EDGE,"E7.40.3"),sQuery(id+"F0.wireOp",EDGE,"E7.40.4"),sQuery(id+"F0.wireOp",EDGE,"E7.40.5"),sQuery(id+"F0.wireOp",EDGE,"E7.41.0"),sQuery(id+"F0.wireOp",EDGE,"E7.41.1"),sQuery(id+"F0.wireOp",EDGE,"E7.41.2"),sQuery(id+"F0.wireOp",EDGE,"E7.41.3"),sQuery(id+"F0.wireOp",EDGE,"E7.41.4"),sQuery(id+"F0.wireOp",EDGE,"E7.41.5"),sQuery(id+"F0.wireOp",EDGE,"E7.42.0"),sQuery(id+"F0.wireOp",EDGE,"E7.42.1"),sQuery(id+"F0.wireOp",EDGE,"E7.42.2"),sQuery(id+"F0.wireOp",EDGE,"E7.42.3"),sQuery(id+"F0.wireOp",EDGE,"E7.42.4"),sQuery(id+"F0.wireOp",EDGE,"E7.42.5"),sQuery(id+"F0.wireOp",EDGE,"E7.43.0"),sQuery(id+"F0.wireOp",EDGE,"E7.43.1"),sQuery(id+"F0.wireOp",EDGE,"E7.43.2"),sQuery(id+"F0.wireOp",EDGE,"E7.43.3"),sQuery(id+"F0.wireOp",EDGE,"E7.43.4"),sQuery(id+"F0.wireOp",EDGE,"E7.43.5")])],"isStart":false})]}),makeQuery(id+"F2.opChamfer","BLEND_FACE",FACE,{"disambiguationData":[OSD([subQ0])]})],"blendedInto":[makeQuery(id+"F2.opChamfer","BLEND_FACE",FACE,{"disambiguationData":[OSD([subQ0])]})]});}
            var Q8;
            {var subQ0=sQuery(id+"F0.wireOp",EDGE,"E7.29.0");Q8=makeQuery(id+"F8.opChamfer","BLEND_EDGE",EDGE,{"blendedFrom":[makeQuery(id+"F2.opChamfer","BLEND_EDGE",EDGE,{"blendedFrom":[makeQuery(id+"F1.opExtrude","CAP_EDGE",EDGE,{"disambiguationData":[OSD([subQ0])],"isStart":false}),makeQuery(id+"F1.opExtrude","CAP_FACE",FACE,{"disambiguationData":[OSD([sQuery(id+"F0.wireOp",EDGE,"E1"),sQuery(id+"F0.wireOp",EDGE,"E2"),sQuery(id+"F0.wireOp",EDGE,"E3"),sQuery(id+"F0.wireOp",EDGE,"E4"),sQuery(id+"F0.wireOp",EDGE,"E5"),sQuery(id+"F0.wireOp",EDGE,"E6"),sQuery(id+"F0.wireOp",EDGE,"E7.1.0"),sQuery(id+"F0.wireOp",EDGE,"E7.1.1"),sQuery(id+"F0.wireOp",EDGE,"E7.1.2"),sQuery(id+"F0.wireOp",EDGE,"E7.1.3"),sQuery(id+"F0.wireOp",EDGE,"E7.1.4"),sQuery(id+"F0.wireOp",EDGE,"E7.1.5"),sQuery(id+"F0.wireOp",EDGE,"E7.2.0"),sQuery(id+"F0.wireOp",EDGE,"E7.2.1"),sQuery(id+"F0.wireOp",EDGE,"E7.2.2"),sQuery(id+"F0.wireOp",EDGE,"E7.2.3"),sQuery(id+"F0.wireOp",EDGE,"E7.2.4"),sQuery(id+"F0.wireOp",EDGE,"E7.2.5"),sQuery(id+"F0.wireOp",EDGE,"E7.3.0"),sQuery(id+"F0.wireOp",EDGE,"E7.3.1"),sQuery(id+"F0.wireOp",EDGE,"E7.3.2"),sQuery(id+"F0.wireOp",EDGE,"E7.3.3"),sQuery(id+"F0.wireOp",EDGE,"E7.3.4"),sQuery(id+"F0.wireOp",EDGE,"E7.3.5"),sQuery(id+"F0.wireOp",EDGE,"E7.4.0"),sQuery(id+"F0.wireOp",EDGE,"E7.4.1"),sQuery(id+"F0.wireOp",EDGE,"E7.4.2"),sQuery(id+"F0.wireOp",EDGE,"E7.4.3"),sQuery(id+"F0.wireOp",EDGE,"E7.4.4"),sQuery(id+"F0.wireOp",EDGE,"E7.4.5"),sQuery(id+"F0.wireOp",EDGE,"E7.5.0"),sQuery(id+"F0.wireOp",EDGE,"E7.5.1"),sQuery(id+"F0.wireOp",EDGE,"E7.5.2"),sQuery(id+"F0.wireOp",EDGE,"E7.5.3"),sQuery(id+"F0.wireOp",EDGE,"E7.5.4"),sQuery(id+"F0.wireOp",EDGE,"E7.5.5"),sQuery(id+"F0.wireOp",EDGE,"E7.6.0"),sQuery(id+"F0.wireOp",EDGE,"E7.6.1"),sQuery(id+"F0.wireOp",EDGE,"E7.6.2"),sQuery(id+"F0.wireOp",EDGE,"E7.6.3"),sQuery(id+"F0.wireOp",EDGE,"E7.6.4"),sQuery(id+"F0.wireOp",EDGE,"E7.6.5"),sQuery(id+"F0.wireOp",EDGE,"E7.7.0"),sQuery(id+"F0.wireOp",EDGE,"E7.7.1"),sQuery(id+"F0.wireOp",EDGE,"E7.7.2"),sQuery(id+"F0.wireOp",EDGE,"E7.7.3"),sQuery(id+"F0.wireOp",EDGE,"E7.7.4"),sQuery(id+"F0.wireOp",EDGE,"E7.7.5"),sQuery(id+"F0.wireOp",EDGE,"E7.8.0"),sQuery(id+"F0.wireOp",EDGE,"E7.8.1"),sQuery(id+"F0.wireOp",EDGE,"E7.8.2"),sQuery(id+"F0.wireOp",EDGE,"E7.8.3"),sQuery(id+"F0.wireOp",EDGE,"E7.8.4"),sQuery(id+"F0.wireOp",EDGE,"E7.8.5"),sQuery(id+"F0.wireOp",EDGE,"E7.9.0"),sQuery(id+"F0.wireOp",EDGE,"E7.9.1"),sQuery(id+"F0.wireOp",EDGE,"E7.9.2"),sQuery(id+"F0.wireOp",EDGE,"E7.9.3"),sQuery(id+"F0.wireOp",EDGE,"E7.9.4"),sQuery(id+"F0.wireOp",EDGE,"E7.9.5"),sQuery(id+"F0.wireOp",EDGE,"E7.10.0"),sQuery(id+"F0.wireOp",EDGE,"E7.10.1"),sQuery(id+"F0.wireOp",EDGE,"E7.10.2"),sQuery(id+"F0.wireOp",EDGE,"E7.10.3"),sQuery(id+"F0.wireOp",EDGE,"E7.10.4"),sQuery(id+"F0.wireOp",EDGE,"E7.10.5"),sQuery(id+"F0.wireOp",EDGE,"E7.11.0"),sQuery(id+"F0.wireOp",EDGE,"E7.11.1"),sQuery(id+"F0.wireOp",EDGE,"E7.11.2"),sQuery(id+"F0.wireOp",EDGE,"E7.11.3"),sQuery(id+"F0.wireOp",EDGE,"E7.11.4"),sQuery(id+"F0.wireOp",EDGE,"E7.11.5"),sQuery(id+"F0.wireOp",EDGE,"E7.12.0"),sQuery(id+"F0.wireOp",EDGE,"E7.12.1"),sQuery(id+"F0.wireOp",EDGE,"E7.12.2"),sQuery(id+"F0.wireOp",EDGE,"E7.12.3"),sQuery(id+"F0.wireOp",EDGE,"E7.12.4"),sQuery(id+"F0.wireOp",EDGE,"E7.12.5"),sQuery(id+"F0.wireOp",EDGE,"E7.13.0"),sQuery(id+"F0.wireOp",EDGE,"E7.13.1"),sQuery(id+"F0.wireOp",EDGE,"E7.13.2"),sQuery(id+"F0.wireOp",EDGE,"E7.13.3"),sQuery(id+"F0.wireOp",EDGE,"E7.13.4"),sQuery(id+"F0.wireOp",EDGE,"E7.13.5"),sQuery(id+"F0.wireOp",EDGE,"E7.14.0"),sQuery(id+"F0.wireOp",EDGE,"E7.14.1"),sQuery(id+"F0.wireOp",EDGE,"E7.14.2"),sQuery(id+"F0.wireOp",EDGE,"E7.14.3"),sQuery(id+"F0.wireOp",EDGE,"E7.14.4"),sQuery(id+"F0.wireOp",EDGE,"E7.14.5"),sQuery(id+"F0.wireOp",EDGE,"E7.15.0"),sQuery(id+"F0.wireOp",EDGE,"E7.15.1"),sQuery(id+"F0.wireOp",EDGE,"E7.15.2"),sQuery(id+"F0.wireOp",EDGE,"E7.15.3"),sQuery(id+"F0.wireOp",EDGE,"E7.15.4"),sQuery(id+"F0.wireOp",EDGE,"E7.15.5"),sQuery(id+"F0.wireOp",EDGE,"E7.16.0"),sQuery(id+"F0.wireOp",EDGE,"E7.16.1"),sQuery(id+"F0.wireOp",EDGE,"E7.16.2"),sQuery(id+"F0.wireOp",EDGE,"E7.16.3"),sQuery(id+"F0.wireOp",EDGE,"E7.16.4"),sQuery(id+"F0.wireOp",EDGE,"E7.16.5"),sQuery(id+"F0.wireOp",EDGE,"E7.17.0"),sQuery(id+"F0.wireOp",EDGE,"E7.17.1"),sQuery(id+"F0.wireOp",EDGE,"E7.17.2"),sQuery(id+"F0.wireOp",EDGE,"E7.17.3"),sQuery(id+"F0.wireOp",EDGE,"E7.17.4"),sQuery(id+"F0.wireOp",EDGE,"E7.17.5"),sQuery(id+"F0.wireOp",EDGE,"E7.18.0"),sQuery(id+"F0.wireOp",EDGE,"E7.18.1"),sQuery(id+"F0.wireOp",EDGE,"E7.18.2"),sQuery(id+"F0.wireOp",EDGE,"E7.18.3"),sQuery(id+"F0.wireOp",EDGE,"E7.18.4"),sQuery(id+"F0.wireOp",EDGE,"E7.18.5"),sQuery(id+"F0.wireOp",EDGE,"E7.19.0"),sQuery(id+"F0.wireOp",EDGE,"E7.19.1"),sQuery(id+"F0.wireOp",EDGE,"E7.19.2"),sQuery(id+"F0.wireOp",EDGE,"E7.19.3"),sQuery(id+"F0.wireOp",EDGE,"E7.19.4"),sQuery(id+"F0.wireOp",EDGE,"E7.19.5"),sQuery(id+"F0.wireOp",EDGE,"E7.20.0"),sQuery(id+"F0.wireOp",EDGE,"E7.20.1"),sQuery(id+"F0.wireOp",EDGE,"E7.20.2"),sQuery(id+"F0.wireOp",EDGE,"E7.20.3"),sQuery(id+"F0.wireOp",EDGE,"E7.20.4"),sQuery(id+"F0.wireOp",EDGE,"E7.20.5"),sQuery(id+"F0.wireOp",EDGE,"E7.21.0"),sQuery(id+"F0.wireOp",EDGE,"E7.21.1"),sQuery(id+"F0.wireOp",EDGE,"E7.21.2"),sQuery(id+"F0.wireOp",EDGE,"E7.21.3"),sQuery(id+"F0.wireOp",EDGE,"E7.21.4"),sQuery(id+"F0.wireOp",EDGE,"E7.21.5"),sQuery(id+"F0.wireOp",EDGE,"E7.22.0"),sQuery(id+"F0.wireOp",EDGE,"E7.22.1"),sQuery(id+"F0.wireOp",EDGE,"E7.22.2"),sQuery(id+"F0.wireOp",EDGE,"E7.22.3"),sQuery(id+"F0.wireOp",EDGE,"E7.22.4"),sQuery(id+"F0.wireOp",EDGE,"E7.22.5"),sQuery(id+"F0.wireOp",EDGE,"E7.23.0"),sQuery(id+"F0.wireOp",EDGE,"E7.23.1"),sQuery(id+"F0.wireOp",EDGE,"E7.23.2"),sQuery(id+"F0.wireOp",EDGE,"E7.23.3"),sQuery(id+"F0.wireOp",EDGE,"E7.23.4"),sQuery(id+"F0.wireOp",EDGE,"E7.23.5"),sQuery(id+"F0.wireOp",EDGE,"E7.24.0"),sQuery(id+"F0.wireOp",EDGE,"E7.24.1"),sQuery(id+"F0.wireOp",EDGE,"E7.24.2"),sQuery(id+"F0.wireOp",EDGE,"E7.24.3"),sQuery(id+"F0.wireOp",EDGE,"E7.24.4"),sQuery(id+"F0.wireOp",EDGE,"E7.24.5"),sQuery(id+"F0.wireOp",EDGE,"E7.25.0"),sQuery(id+"F0.wireOp",EDGE,"E7.25.1"),sQuery(id+"F0.wireOp",EDGE,"E7.25.2"),sQuery(id+"F0.wireOp",EDGE,"E7.25.3"),sQuery(id+"F0.wireOp",EDGE,"E7.25.4"),sQuery(id+"F0.wireOp",EDGE,"E7.25.5"),sQuery(id+"F0.wireOp",EDGE,"E7.26.0"),sQuery(id+"F0.wireOp",EDGE,"E7.26.1"),sQuery(id+"F0.wireOp",EDGE,"E7.26.2"),sQuery(id+"F0.wireOp",EDGE,"E7.26.3"),sQuery(id+"F0.wireOp",EDGE,"E7.26.4"),sQuery(id+"F0.wireOp",EDGE,"E7.26.5"),sQuery(id+"F0.wireOp",EDGE,"E7.27.0"),sQuery(id+"F0.wireOp",EDGE,"E7.27.1"),sQuery(id+"F0.wireOp",EDGE,"E7.27.2"),sQuery(id+"F0.wireOp",EDGE,"E7.27.3"),sQuery(id+"F0.wireOp",EDGE,"E7.27.4"),sQuery(id+"F0.wireOp",EDGE,"E7.27.5"),sQuery(id+"F0.wireOp",EDGE,"E7.28.0"),sQuery(id+"F0.wireOp",EDGE,"E7.28.1"),sQuery(id+"F0.wireOp",EDGE,"E7.28.2"),sQuery(id+"F0.wireOp",EDGE,"E7.28.3"),sQuery(id+"F0.wireOp",EDGE,"E7.28.4"),sQuery(id+"F0.wireOp",EDGE,"E7.28.5"),subQ0,sQuery(id+"F0.wireOp",EDGE,"E7.29.1"),sQuery(id+"F0.wireOp",EDGE,"E7.29.2"),sQuery(id+"F0.wireOp",EDGE,"E7.29.3"),sQuery(id+"F0.wireOp",EDGE,"E7.29.4"),sQuery(id+"F0.wireOp",EDGE,"E7.29.5"),sQuery(id+"F0.wireOp",EDGE,"E7.30.0"),sQuery(id+"F0.wireOp",EDGE,"E7.30.1"),sQuery(id+"F0.wireOp",EDGE,"E7.30.2"),sQuery(id+"F0.wireOp",EDGE,"E7.30.3"),sQuery(id+"F0.wireOp",EDGE,"E7.30.4"),sQuery(id+"F0.wireOp",EDGE,"E7.30.5"),sQuery(id+"F0.wireOp",EDGE,"E7.31.0"),sQuery(id+"F0.wireOp",EDGE,"E7.31.1"),sQuery(id+"F0.wireOp",EDGE,"E7.31.2"),sQuery(id+"F0.wireOp",EDGE,"E7.31.3"),sQuery(id+"F0.wireOp",EDGE,"E7.31.4"),sQuery(id+"F0.wireOp",EDGE,"E7.31.5"),sQuery(id+"F0.wireOp",EDGE,"E7.32.0"),sQuery(id+"F0.wireOp",EDGE,"E7.32.1"),sQuery(id+"F0.wireOp",EDGE,"E7.32.2"),sQuery(id+"F0.wireOp",EDGE,"E7.32.3"),sQuery(id+"F0.wireOp",EDGE,"E7.32.4"),sQuery(id+"F0.wireOp",EDGE,"E7.32.5"),sQuery(id+"F0.wireOp",EDGE,"E7.33.0"),sQuery(id+"F0.wireOp",EDGE,"E7.33.1"),sQuery(id+"F0.wireOp",EDGE,"E7.33.2"),sQuery(id+"F0.wireOp",EDGE,"E7.33.3"),sQuery(id+"F0.wireOp",EDGE,"E7.33.4"),sQuery(id+"F0.wireOp",EDGE,"E7.33.5"),sQuery(id+"F0.wireOp",EDGE,"E7.34.0"),sQuery(id+"F0.wireOp",EDGE,"E7.34.1"),sQuery(id+"F0.wireOp",EDGE,"E7.34.2"),sQuery(id+"F0.wireOp",EDGE,"E7.34.3"),sQuery(id+"F0.wireOp",EDGE,"E7.34.4"),sQuery(id+"F0.wireOp",EDGE,"E7.34.5"),sQuery(id+"F0.wireOp",EDGE,"E7.35.0"),sQuery(id+"F0.wireOp",EDGE,"E7.35.1"),sQuery(id+"F0.wireOp",EDGE,"E7.35.2"),sQuery(id+"F0.wireOp",EDGE,"E7.35.3"),sQuery(id+"F0.wireOp",EDGE,"E7.35.4"),sQuery(id+"F0.wireOp",EDGE,"E7.35.5"),sQuery(id+"F0.wireOp",EDGE,"E7.36.0"),sQuery(id+"F0.wireOp",EDGE,"E7.36.1"),sQuery(id+"F0.wireOp",EDGE,"E7.36.2"),sQuery(id+"F0.wireOp",EDGE,"E7.36.3"),sQuery(id+"F0.wireOp",EDGE,"E7.36.4"),sQuery(id+"F0.wireOp",EDGE,"E7.36.5"),sQuery(id+"F0.wireOp",EDGE,"E7.37.0"),sQuery(id+"F0.wireOp",EDGE,"E7.37.1"),sQuery(id+"F0.wireOp",EDGE,"E7.37.2"),sQuery(id+"F0.wireOp",EDGE,"E7.37.3"),sQuery(id+"F0.wireOp",EDGE,"E7.37.4"),sQuery(id+"F0.wireOp",EDGE,"E7.37.5"),sQuery(id+"F0.wireOp",EDGE,"E7.38.0"),sQuery(id+"F0.wireOp",EDGE,"E7.38.1"),sQuery(id+"F0.wireOp",EDGE,"E7.38.2"),sQuery(id+"F0.wireOp",EDGE,"E7.38.3"),sQuery(id+"F0.wireOp",EDGE,"E7.38.4"),sQuery(id+"F0.wireOp",EDGE,"E7.38.5"),sQuery(id+"F0.wireOp",EDGE,"E7.39.0"),sQuery(id+"F0.wireOp",EDGE,"E7.39.1"),sQuery(id+"F0.wireOp",EDGE,"E7.39.2"),sQuery(id+"F0.wireOp",EDGE,"E7.39.3"),sQuery(id+"F0.wireOp",EDGE,"E7.39.4"),sQuery(id+"F0.wireOp",EDGE,"E7.39.5"),sQuery(id+"F0.wireOp",EDGE,"E7.40.0"),sQuery(id+"F0.wireOp",EDGE,"E7.40.1"),sQuery(id+"F0.wireOp",EDGE,"E7.40.2"),sQuery(id+"F0.wireOp",EDGE,"E7.40.3"),sQuery(id+"F0.wireOp",EDGE,"E7.40.4"),sQuery(id+"F0.wireOp",EDGE,"E7.40.5"),sQuery(id+"F0.wireOp",EDGE,"E7.41.0"),sQuery(id+"F0.wireOp",EDGE,"E7.41.1"),sQuery(id+"F0.wireOp",EDGE,"E7.41.2"),sQuery(id+"F0.wireOp",EDGE,"E7.41.3"),sQuery(id+"F0.wireOp",EDGE,"E7.41.4"),sQuery(id+"F0.wireOp",EDGE,"E7.41.5"),sQuery(id+"F0.wireOp",EDGE,"E7.42.0"),sQuery(id+"F0.wireOp",EDGE,"E7.42.1"),sQuery(id+"F0.wireOp",EDGE,"E7.42.2"),sQuery(id+"F0.wireOp",EDGE,"E7.42.3"),sQuery(id+"F0.wireOp",EDGE,"E7.42.4"),sQuery(id+"F0.wireOp",EDGE,"E7.42.5"),sQuery(id+"F0.wireOp",EDGE,"E7.43.0"),sQuery(id+"F0.wireOp",EDGE,"E7.43.1"),sQuery(id+"F0.wireOp",EDGE,"E7.43.2"),sQuery(id+"F0.wireOp",EDGE,"E7.43.3"),sQuery(id+"F0.wireOp",EDGE,"E7.43.4"),sQuery(id+"F0.wireOp",EDGE,"E7.43.5")])],"isStart":false})],"blendedInto":[makeQuery(id+"F1.opExtrude","CAP_FACE",FACE,{"disambiguationData":[OSD([sQuery(id+"F0.wireOp",EDGE,"E1"),sQuery(id+"F0.wireOp",EDGE,"E2"),sQuery(id+"F0.wireOp",EDGE,"E3"),sQuery(id+"F0.wireOp",EDGE,"E4"),sQuery(id+"F0.wireOp",EDGE,"E5"),sQuery(id+"F0.wireOp",EDGE,"E6"),sQuery(id+"F0.wireOp",EDGE,"E7.1.0"),sQuery(id+"F0.wireOp",EDGE,"E7.1.1"),sQuery(id+"F0.wireOp",EDGE,"E7.1.2"),sQuery(id+"F0.wireOp",EDGE,"E7.1.3"),sQuery(id+"F0.wireOp",EDGE,"E7.1.4"),sQuery(id+"F0.wireOp",EDGE,"E7.1.5"),sQuery(id+"F0.wireOp",EDGE,"E7.2.0"),sQuery(id+"F0.wireOp",EDGE,"E7.2.1"),sQuery(id+"F0.wireOp",EDGE,"E7.2.2"),sQuery(id+"F0.wireOp",EDGE,"E7.2.3"),sQuery(id+"F0.wireOp",EDGE,"E7.2.4"),sQuery(id+"F0.wireOp",EDGE,"E7.2.5"),sQuery(id+"F0.wireOp",EDGE,"E7.3.0"),sQuery(id+"F0.wireOp",EDGE,"E7.3.1"),sQuery(id+"F0.wireOp",EDGE,"E7.3.2"),sQuery(id+"F0.wireOp",EDGE,"E7.3.3"),sQuery(id+"F0.wireOp",EDGE,"E7.3.4"),sQuery(id+"F0.wireOp",EDGE,"E7.3.5"),sQuery(id+"F0.wireOp",EDGE,"E7.4.0"),sQuery(id+"F0.wireOp",EDGE,"E7.4.1"),sQuery(id+"F0.wireOp",EDGE,"E7.4.2"),sQuery(id+"F0.wireOp",EDGE,"E7.4.3"),sQuery(id+"F0.wireOp",EDGE,"E7.4.4"),sQuery(id+"F0.wireOp",EDGE,"E7.4.5"),sQuery(id+"F0.wireOp",EDGE,"E7.5.0"),sQuery(id+"F0.wireOp",EDGE,"E7.5.1"),sQuery(id+"F0.wireOp",EDGE,"E7.5.2"),sQuery(id+"F0.wireOp",EDGE,"E7.5.3"),sQuery(id+"F0.wireOp",EDGE,"E7.5.4"),sQuery(id+"F0.wireOp",EDGE,"E7.5.5"),sQuery(id+"F0.wireOp",EDGE,"E7.6.0"),sQuery(id+"F0.wireOp",EDGE,"E7.6.1"),sQuery(id+"F0.wireOp",EDGE,"E7.6.2"),sQuery(id+"F0.wireOp",EDGE,"E7.6.3"),sQuery(id+"F0.wireOp",EDGE,"E7.6.4"),sQuery(id+"F0.wireOp",EDGE,"E7.6.5"),sQuery(id+"F0.wireOp",EDGE,"E7.7.0"),sQuery(id+"F0.wireOp",EDGE,"E7.7.1"),sQuery(id+"F0.wireOp",EDGE,"E7.7.2"),sQuery(id+"F0.wireOp",EDGE,"E7.7.3"),sQuery(id+"F0.wireOp",EDGE,"E7.7.4"),sQuery(id+"F0.wireOp",EDGE,"E7.7.5"),sQuery(id+"F0.wireOp",EDGE,"E7.8.0"),sQuery(id+"F0.wireOp",EDGE,"E7.8.1"),sQuery(id+"F0.wireOp",EDGE,"E7.8.2"),sQuery(id+"F0.wireOp",EDGE,"E7.8.3"),sQuery(id+"F0.wireOp",EDGE,"E7.8.4"),sQuery(id+"F0.wireOp",EDGE,"E7.8.5"),sQuery(id+"F0.wireOp",EDGE,"E7.9.0"),sQuery(id+"F0.wireOp",EDGE,"E7.9.1"),sQuery(id+"F0.wireOp",EDGE,"E7.9.2"),sQuery(id+"F0.wireOp",EDGE,"E7.9.3"),sQuery(id+"F0.wireOp",EDGE,"E7.9.4"),sQuery(id+"F0.wireOp",EDGE,"E7.9.5"),sQuery(id+"F0.wireOp",EDGE,"E7.10.0"),sQuery(id+"F0.wireOp",EDGE,"E7.10.1"),sQuery(id+"F0.wireOp",EDGE,"E7.10.2"),sQuery(id+"F0.wireOp",EDGE,"E7.10.3"),sQuery(id+"F0.wireOp",EDGE,"E7.10.4"),sQuery(id+"F0.wireOp",EDGE,"E7.10.5"),sQuery(id+"F0.wireOp",EDGE,"E7.11.0"),sQuery(id+"F0.wireOp",EDGE,"E7.11.1"),sQuery(id+"F0.wireOp",EDGE,"E7.11.2"),sQuery(id+"F0.wireOp",EDGE,"E7.11.3"),sQuery(id+"F0.wireOp",EDGE,"E7.11.4"),sQuery(id+"F0.wireOp",EDGE,"E7.11.5"),sQuery(id+"F0.wireOp",EDGE,"E7.12.0"),sQuery(id+"F0.wireOp",EDGE,"E7.12.1"),sQuery(id+"F0.wireOp",EDGE,"E7.12.2"),sQuery(id+"F0.wireOp",EDGE,"E7.12.3"),sQuery(id+"F0.wireOp",EDGE,"E7.12.4"),sQuery(id+"F0.wireOp",EDGE,"E7.12.5"),sQuery(id+"F0.wireOp",EDGE,"E7.13.0"),sQuery(id+"F0.wireOp",EDGE,"E7.13.1"),sQuery(id+"F0.wireOp",EDGE,"E7.13.2"),sQuery(id+"F0.wireOp",EDGE,"E7.13.3"),sQuery(id+"F0.wireOp",EDGE,"E7.13.4"),sQuery(id+"F0.wireOp",EDGE,"E7.13.5"),sQuery(id+"F0.wireOp",EDGE,"E7.14.0"),sQuery(id+"F0.wireOp",EDGE,"E7.14.1"),sQuery(id+"F0.wireOp",EDGE,"E7.14.2"),sQuery(id+"F0.wireOp",EDGE,"E7.14.3"),sQuery(id+"F0.wireOp",EDGE,"E7.14.4"),sQuery(id+"F0.wireOp",EDGE,"E7.14.5"),sQuery(id+"F0.wireOp",EDGE,"E7.15.0"),sQuery(id+"F0.wireOp",EDGE,"E7.15.1"),sQuery(id+"F0.wireOp",EDGE,"E7.15.2"),sQuery(id+"F0.wireOp",EDGE,"E7.15.3"),sQuery(id+"F0.wireOp",EDGE,"E7.15.4"),sQuery(id+"F0.wireOp",EDGE,"E7.15.5"),sQuery(id+"F0.wireOp",EDGE,"E7.16.0"),sQuery(id+"F0.wireOp",EDGE,"E7.16.1"),sQuery(id+"F0.wireOp",EDGE,"E7.16.2"),sQuery(id+"F0.wireOp",EDGE,"E7.16.3"),sQuery(id+"F0.wireOp",EDGE,"E7.16.4"),sQuery(id+"F0.wireOp",EDGE,"E7.16.5"),sQuery(id+"F0.wireOp",EDGE,"E7.17.0"),sQuery(id+"F0.wireOp",EDGE,"E7.17.1"),sQuery(id+"F0.wireOp",EDGE,"E7.17.2"),sQuery(id+"F0.wireOp",EDGE,"E7.17.3"),sQuery(id+"F0.wireOp",EDGE,"E7.17.4"),sQuery(id+"F0.wireOp",EDGE,"E7.17.5"),sQuery(id+"F0.wireOp",EDGE,"E7.18.0"),sQuery(id+"F0.wireOp",EDGE,"E7.18.1"),sQuery(id+"F0.wireOp",EDGE,"E7.18.2"),sQuery(id+"F0.wireOp",EDGE,"E7.18.3"),sQuery(id+"F0.wireOp",EDGE,"E7.18.4"),sQuery(id+"F0.wireOp",EDGE,"E7.18.5"),sQuery(id+"F0.wireOp",EDGE,"E7.19.0"),sQuery(id+"F0.wireOp",EDGE,"E7.19.1"),sQuery(id+"F0.wireOp",EDGE,"E7.19.2"),sQuery(id+"F0.wireOp",EDGE,"E7.19.3"),sQuery(id+"F0.wireOp",EDGE,"E7.19.4"),sQuery(id+"F0.wireOp",EDGE,"E7.19.5"),sQuery(id+"F0.wireOp",EDGE,"E7.20.0"),sQuery(id+"F0.wireOp",EDGE,"E7.20.1"),sQuery(id+"F0.wireOp",EDGE,"E7.20.2"),sQuery(id+"F0.wireOp",EDGE,"E7.20.3"),sQuery(id+"F0.wireOp",EDGE,"E7.20.4"),sQuery(id+"F0.wireOp",EDGE,"E7.20.5"),sQuery(id+"F0.wireOp",EDGE,"E7.21.0"),sQuery(id+"F0.wireOp",EDGE,"E7.21.1"),sQuery(id+"F0.wireOp",EDGE,"E7.21.2"),sQuery(id+"F0.wireOp",EDGE,"E7.21.3"),sQuery(id+"F0.wireOp",EDGE,"E7.21.4"),sQuery(id+"F0.wireOp",EDGE,"E7.21.5"),sQuery(id+"F0.wireOp",EDGE,"E7.22.0"),sQuery(id+"F0.wireOp",EDGE,"E7.22.1"),sQuery(id+"F0.wireOp",EDGE,"E7.22.2"),sQuery(id+"F0.wireOp",EDGE,"E7.22.3"),sQuery(id+"F0.wireOp",EDGE,"E7.22.4"),sQuery(id+"F0.wireOp",EDGE,"E7.22.5"),sQuery(id+"F0.wireOp",EDGE,"E7.23.0"),sQuery(id+"F0.wireOp",EDGE,"E7.23.1"),sQuery(id+"F0.wireOp",EDGE,"E7.23.2"),sQuery(id+"F0.wireOp",EDGE,"E7.23.3"),sQuery(id+"F0.wireOp",EDGE,"E7.23.4"),sQuery(id+"F0.wireOp",EDGE,"E7.23.5"),sQuery(id+"F0.wireOp",EDGE,"E7.24.0"),sQuery(id+"F0.wireOp",EDGE,"E7.24.1"),sQuery(id+"F0.wireOp",EDGE,"E7.24.2"),sQuery(id+"F0.wireOp",EDGE,"E7.24.3"),sQuery(id+"F0.wireOp",EDGE,"E7.24.4"),sQuery(id+"F0.wireOp",EDGE,"E7.24.5"),sQuery(id+"F0.wireOp",EDGE,"E7.25.0"),sQuery(id+"F0.wireOp",EDGE,"E7.25.1"),sQuery(id+"F0.wireOp",EDGE,"E7.25.2"),sQuery(id+"F0.wireOp",EDGE,"E7.25.3"),sQuery(id+"F0.wireOp",EDGE,"E7.25.4"),sQuery(id+"F0.wireOp",EDGE,"E7.25.5"),sQuery(id+"F0.wireOp",EDGE,"E7.26.0"),sQuery(id+"F0.wireOp",EDGE,"E7.26.1"),sQuery(id+"F0.wireOp",EDGE,"E7.26.2"),sQuery(id+"F0.wireOp",EDGE,"E7.26.3"),sQuery(id+"F0.wireOp",EDGE,"E7.26.4"),sQuery(id+"F0.wireOp",EDGE,"E7.26.5"),sQuery(id+"F0.wireOp",EDGE,"E7.27.0"),sQuery(id+"F0.wireOp",EDGE,"E7.27.1"),sQuery(id+"F0.wireOp",EDGE,"E7.27.2"),sQuery(id+"F0.wireOp",EDGE,"E7.27.3"),sQuery(id+"F0.wireOp",EDGE,"E7.27.4"),sQuery(id+"F0.wireOp",EDGE,"E7.27.5"),sQuery(id+"F0.wireOp",EDGE,"E7.28.0"),sQuery(id+"F0.wireOp",EDGE,"E7.28.1"),sQuery(id+"F0.wireOp",EDGE,"E7.28.2"),sQuery(id+"F0.wireOp",EDGE,"E7.28.3"),sQuery(id+"F0.wireOp",EDGE,"E7.28.4"),sQuery(id+"F0.wireOp",EDGE,"E7.28.5"),subQ0,sQuery(id+"F0.wireOp",EDGE,"E7.29.1"),sQuery(id+"F0.wireOp",EDGE,"E7.29.2"),sQuery(id+"F0.wireOp",EDGE,"E7.29.3"),sQuery(id+"F0.wireOp",EDGE,"E7.29.4"),sQuery(id+"F0.wireOp",EDGE,"E7.29.5"),sQuery(id+"F0.wireOp",EDGE,"E7.30.0"),sQuery(id+"F0.wireOp",EDGE,"E7.30.1"),sQuery(id+"F0.wireOp",EDGE,"E7.30.2"),sQuery(id+"F0.wireOp",EDGE,"E7.30.3"),sQuery(id+"F0.wireOp",EDGE,"E7.30.4"),sQuery(id+"F0.wireOp",EDGE,"E7.30.5"),sQuery(id+"F0.wireOp",EDGE,"E7.31.0"),sQuery(id+"F0.wireOp",EDGE,"E7.31.1"),sQuery(id+"F0.wireOp",EDGE,"E7.31.2"),sQuery(id+"F0.wireOp",EDGE,"E7.31.3"),sQuery(id+"F0.wireOp",EDGE,"E7.31.4"),sQuery(id+"F0.wireOp",EDGE,"E7.31.5"),sQuery(id+"F0.wireOp",EDGE,"E7.32.0"),sQuery(id+"F0.wireOp",EDGE,"E7.32.1"),sQuery(id+"F0.wireOp",EDGE,"E7.32.2"),sQuery(id+"F0.wireOp",EDGE,"E7.32.3"),sQuery(id+"F0.wireOp",EDGE,"E7.32.4"),sQuery(id+"F0.wireOp",EDGE,"E7.32.5"),sQuery(id+"F0.wireOp",EDGE,"E7.33.0"),sQuery(id+"F0.wireOp",EDGE,"E7.33.1"),sQuery(id+"F0.wireOp",EDGE,"E7.33.2"),sQuery(id+"F0.wireOp",EDGE,"E7.33.3"),sQuery(id+"F0.wireOp",EDGE,"E7.33.4"),sQuery(id+"F0.wireOp",EDGE,"E7.33.5"),sQuery(id+"F0.wireOp",EDGE,"E7.34.0"),sQuery(id+"F0.wireOp",EDGE,"E7.34.1"),sQuery(id+"F0.wireOp",EDGE,"E7.34.2"),sQuery(id+"F0.wireOp",EDGE,"E7.34.3"),sQuery(id+"F0.wireOp",EDGE,"E7.34.4"),sQuery(id+"F0.wireOp",EDGE,"E7.34.5"),sQuery(id+"F0.wireOp",EDGE,"E7.35.0"),sQuery(id+"F0.wireOp",EDGE,"E7.35.1"),sQuery(id+"F0.wireOp",EDGE,"E7.35.2"),sQuery(id+"F0.wireOp",EDGE,"E7.35.3"),sQuery(id+"F0.wireOp",EDGE,"E7.35.4"),sQuery(id+"F0.wireOp",EDGE,"E7.35.5"),sQuery(id+"F0.wireOp",EDGE,"E7.36.0"),sQuery(id+"F0.wireOp",EDGE,"E7.36.1"),sQuery(id+"F0.wireOp",EDGE,"E7.36.2"),sQuery(id+"F0.wireOp",EDGE,"E7.36.3"),sQuery(id+"F0.wireOp",EDGE,"E7.36.4"),sQuery(id+"F0.wireOp",EDGE,"E7.36.5"),sQuery(id+"F0.wireOp",EDGE,"E7.37.0"),sQuery(id+"F0.wireOp",EDGE,"E7.37.1"),sQuery(id+"F0.wireOp",EDGE,"E7.37.2"),sQuery(id+"F0.wireOp",EDGE,"E7.37.3"),sQuery(id+"F0.wireOp",EDGE,"E7.37.4"),sQuery(id+"F0.wireOp",EDGE,"E7.37.5"),sQuery(id+"F0.wireOp",EDGE,"E7.38.0"),sQuery(id+"F0.wireOp",EDGE,"E7.38.1"),sQuery(id+"F0.wireOp",EDGE,"E7.38.2"),sQuery(id+"F0.wireOp",EDGE,"E7.38.3"),sQuery(id+"F0.wireOp",EDGE,"E7.38.4"),sQuery(id+"F0.wireOp",EDGE,"E7.38.5"),sQuery(id+"F0.wireOp",EDGE,"E7.39.0"),sQuery(id+"F0.wireOp",EDGE,"E7.39.1"),sQuery(id+"F0.wireOp",EDGE,"E7.39.2"),sQuery(id+"F0.wireOp",EDGE,"E7.39.3"),sQuery(id+"F0.wireOp",EDGE,"E7.39.4"),sQuery(id+"F0.wireOp",EDGE,"E7.39.5"),sQuery(id+"F0.wireOp",EDGE,"E7.40.0"),sQuery(id+"F0.wireOp",EDGE,"E7.40.1"),sQuery(id+"F0.wireOp",EDGE,"E7.40.2"),sQuery(id+"F0.wireOp",EDGE,"E7.40.3"),sQuery(id+"F0.wireOp",EDGE,"E7.40.4"),sQuery(id+"F0.wireOp",EDGE,"E7.40.5"),sQuery(id+"F0.wireOp",EDGE,"E7.41.0"),sQuery(id+"F0.wireOp",EDGE,"E7.41.1"),sQuery(id+"F0.wireOp",EDGE,"E7.41.2"),sQuery(id+"F0.wireOp",EDGE,"E7.41.3"),sQuery(id+"F0.wireOp",EDGE,"E7.41.4"),sQuery(id+"F0.wireOp",EDGE,"E7.41.5"),sQuery(id+"F0.wireOp",EDGE,"E7.42.0"),sQuery(id+"F0.wireOp",EDGE,"E7.42.1"),sQuery(id+"F0.wireOp",EDGE,"E7.42.2"),sQuery(id+"F0.wireOp",EDGE,"E7.42.3"),sQuery(id+"F0.wireOp",EDGE,"E7.42.4"),sQuery(id+"F0.wireOp",EDGE,"E7.42.5"),sQuery(id+"F0.wireOp",EDGE,"E7.43.0"),sQuery(id+"F0.wireOp",EDGE,"E7.43.1"),sQuery(id+"F0.wireOp",EDGE,"E7.43.2"),sQuery(id+"F0.wireOp",EDGE,"E7.43.3"),sQuery(id+"F0.wireOp",EDGE,"E7.43.4"),sQuery(id+"F0.wireOp",EDGE,"E7.43.5")])],"isStart":false})]}),makeQuery(id+"F2.opChamfer","BLEND_FACE",FACE,{"disambiguationData":[OSD([subQ0])]})],"blendedInto":[makeQuery(id+"F2.opChamfer","BLEND_FACE",FACE,{"disambiguationData":[OSD([subQ0])]})]});}
            var Q9;
            {var subQ0=sQuery(id+"F0.wireOp",EDGE,"E7.27.0");Q9=makeQuery(id+"F8.opChamfer","BLEND_EDGE",EDGE,{"blendedFrom":[makeQuery(id+"F2.opChamfer","BLEND_EDGE",EDGE,{"blendedFrom":[makeQuery(id+"F1.opExtrude","CAP_EDGE",EDGE,{"disambiguationData":[OSD([subQ0])],"isStart":false}),makeQuery(id+"F1.opExtrude","CAP_FACE",FACE,{"disambiguationData":[OSD([sQuery(id+"F0.wireOp",EDGE,"E1"),sQuery(id+"F0.wireOp",EDGE,"E2"),sQuery(id+"F0.wireOp",EDGE,"E3"),sQuery(id+"F0.wireOp",EDGE,"E4"),sQuery(id+"F0.wireOp",EDGE,"E5"),sQuery(id+"F0.wireOp",EDGE,"E6"),sQuery(id+"F0.wireOp",EDGE,"E7.1.0"),sQuery(id+"F0.wireOp",EDGE,"E7.1.1"),sQuery(id+"F0.wireOp",EDGE,"E7.1.2"),sQuery(id+"F0.wireOp",EDGE,"E7.1.3"),sQuery(id+"F0.wireOp",EDGE,"E7.1.4"),sQuery(id+"F0.wireOp",EDGE,"E7.1.5"),sQuery(id+"F0.wireOp",EDGE,"E7.2.0"),sQuery(id+"F0.wireOp",EDGE,"E7.2.1"),sQuery(id+"F0.wireOp",EDGE,"E7.2.2"),sQuery(id+"F0.wireOp",EDGE,"E7.2.3"),sQuery(id+"F0.wireOp",EDGE,"E7.2.4"),sQuery(id+"F0.wireOp",EDGE,"E7.2.5"),sQuery(id+"F0.wireOp",EDGE,"E7.3.0"),sQuery(id+"F0.wireOp",EDGE,"E7.3.1"),sQuery(id+"F0.wireOp",EDGE,"E7.3.2"),sQuery(id+"F0.wireOp",EDGE,"E7.3.3"),sQuery(id+"F0.wireOp",EDGE,"E7.3.4"),sQuery(id+"F0.wireOp",EDGE,"E7.3.5"),sQuery(id+"F0.wireOp",EDGE,"E7.4.0"),sQuery(id+"F0.wireOp",EDGE,"E7.4.1"),sQuery(id+"F0.wireOp",EDGE,"E7.4.2"),sQuery(id+"F0.wireOp",EDGE,"E7.4.3"),sQuery(id+"F0.wireOp",EDGE,"E7.4.4"),sQuery(id+"F0.wireOp",EDGE,"E7.4.5"),sQuery(id+"F0.wireOp",EDGE,"E7.5.0"),sQuery(id+"F0.wireOp",EDGE,"E7.5.1"),sQuery(id+"F0.wireOp",EDGE,"E7.5.2"),sQuery(id+"F0.wireOp",EDGE,"E7.5.3"),sQuery(id+"F0.wireOp",EDGE,"E7.5.4"),sQuery(id+"F0.wireOp",EDGE,"E7.5.5"),sQuery(id+"F0.wireOp",EDGE,"E7.6.0"),sQuery(id+"F0.wireOp",EDGE,"E7.6.1"),sQuery(id+"F0.wireOp",EDGE,"E7.6.2"),sQuery(id+"F0.wireOp",EDGE,"E7.6.3"),sQuery(id+"F0.wireOp",EDGE,"E7.6.4"),sQuery(id+"F0.wireOp",EDGE,"E7.6.5"),sQuery(id+"F0.wireOp",EDGE,"E7.7.0"),sQuery(id+"F0.wireOp",EDGE,"E7.7.1"),sQuery(id+"F0.wireOp",EDGE,"E7.7.2"),sQuery(id+"F0.wireOp",EDGE,"E7.7.3"),sQuery(id+"F0.wireOp",EDGE,"E7.7.4"),sQuery(id+"F0.wireOp",EDGE,"E7.7.5"),sQuery(id+"F0.wireOp",EDGE,"E7.8.0"),sQuery(id+"F0.wireOp",EDGE,"E7.8.1"),sQuery(id+"F0.wireOp",EDGE,"E7.8.2"),sQuery(id+"F0.wireOp",EDGE,"E7.8.3"),sQuery(id+"F0.wireOp",EDGE,"E7.8.4"),sQuery(id+"F0.wireOp",EDGE,"E7.8.5"),sQuery(id+"F0.wireOp",EDGE,"E7.9.0"),sQuery(id+"F0.wireOp",EDGE,"E7.9.1"),sQuery(id+"F0.wireOp",EDGE,"E7.9.2"),sQuery(id+"F0.wireOp",EDGE,"E7.9.3"),sQuery(id+"F0.wireOp",EDGE,"E7.9.4"),sQuery(id+"F0.wireOp",EDGE,"E7.9.5"),sQuery(id+"F0.wireOp",EDGE,"E7.10.0"),sQuery(id+"F0.wireOp",EDGE,"E7.10.1"),sQuery(id+"F0.wireOp",EDGE,"E7.10.2"),sQuery(id+"F0.wireOp",EDGE,"E7.10.3"),sQuery(id+"F0.wireOp",EDGE,"E7.10.4"),sQuery(id+"F0.wireOp",EDGE,"E7.10.5"),sQuery(id+"F0.wireOp",EDGE,"E7.11.0"),sQuery(id+"F0.wireOp",EDGE,"E7.11.1"),sQuery(id+"F0.wireOp",EDGE,"E7.11.2"),sQuery(id+"F0.wireOp",EDGE,"E7.11.3"),sQuery(id+"F0.wireOp",EDGE,"E7.11.4"),sQuery(id+"F0.wireOp",EDGE,"E7.11.5"),sQuery(id+"F0.wireOp",EDGE,"E7.12.0"),sQuery(id+"F0.wireOp",EDGE,"E7.12.1"),sQuery(id+"F0.wireOp",EDGE,"E7.12.2"),sQuery(id+"F0.wireOp",EDGE,"E7.12.3"),sQuery(id+"F0.wireOp",EDGE,"E7.12.4"),sQuery(id+"F0.wireOp",EDGE,"E7.12.5"),sQuery(id+"F0.wireOp",EDGE,"E7.13.0"),sQuery(id+"F0.wireOp",EDGE,"E7.13.1"),sQuery(id+"F0.wireOp",EDGE,"E7.13.2"),sQuery(id+"F0.wireOp",EDGE,"E7.13.3"),sQuery(id+"F0.wireOp",EDGE,"E7.13.4"),sQuery(id+"F0.wireOp",EDGE,"E7.13.5"),sQuery(id+"F0.wireOp",EDGE,"E7.14.0"),sQuery(id+"F0.wireOp",EDGE,"E7.14.1"),sQuery(id+"F0.wireOp",EDGE,"E7.14.2"),sQuery(id+"F0.wireOp",EDGE,"E7.14.3"),sQuery(id+"F0.wireOp",EDGE,"E7.14.4"),sQuery(id+"F0.wireOp",EDGE,"E7.14.5"),sQuery(id+"F0.wireOp",EDGE,"E7.15.0"),sQuery(id+"F0.wireOp",EDGE,"E7.15.1"),sQuery(id+"F0.wireOp",EDGE,"E7.15.2"),sQuery(id+"F0.wireOp",EDGE,"E7.15.3"),sQuery(id+"F0.wireOp",EDGE,"E7.15.4"),sQuery(id+"F0.wireOp",EDGE,"E7.15.5"),sQuery(id+"F0.wireOp",EDGE,"E7.16.0"),sQuery(id+"F0.wireOp",EDGE,"E7.16.1"),sQuery(id+"F0.wireOp",EDGE,"E7.16.2"),sQuery(id+"F0.wireOp",EDGE,"E7.16.3"),sQuery(id+"F0.wireOp",EDGE,"E7.16.4"),sQuery(id+"F0.wireOp",EDGE,"E7.16.5"),sQuery(id+"F0.wireOp",EDGE,"E7.17.0"),sQuery(id+"F0.wireOp",EDGE,"E7.17.1"),sQuery(id+"F0.wireOp",EDGE,"E7.17.2"),sQuery(id+"F0.wireOp",EDGE,"E7.17.3"),sQuery(id+"F0.wireOp",EDGE,"E7.17.4"),sQuery(id+"F0.wireOp",EDGE,"E7.17.5"),sQuery(id+"F0.wireOp",EDGE,"E7.18.0"),sQuery(id+"F0.wireOp",EDGE,"E7.18.1"),sQuery(id+"F0.wireOp",EDGE,"E7.18.2"),sQuery(id+"F0.wireOp",EDGE,"E7.18.3"),sQuery(id+"F0.wireOp",EDGE,"E7.18.4"),sQuery(id+"F0.wireOp",EDGE,"E7.18.5"),sQuery(id+"F0.wireOp",EDGE,"E7.19.0"),sQuery(id+"F0.wireOp",EDGE,"E7.19.1"),sQuery(id+"F0.wireOp",EDGE,"E7.19.2"),sQuery(id+"F0.wireOp",EDGE,"E7.19.3"),sQuery(id+"F0.wireOp",EDGE,"E7.19.4"),sQuery(id+"F0.wireOp",EDGE,"E7.19.5"),sQuery(id+"F0.wireOp",EDGE,"E7.20.0"),sQuery(id+"F0.wireOp",EDGE,"E7.20.1"),sQuery(id+"F0.wireOp",EDGE,"E7.20.2"),sQuery(id+"F0.wireOp",EDGE,"E7.20.3"),sQuery(id+"F0.wireOp",EDGE,"E7.20.4"),sQuery(id+"F0.wireOp",EDGE,"E7.20.5"),sQuery(id+"F0.wireOp",EDGE,"E7.21.0"),sQuery(id+"F0.wireOp",EDGE,"E7.21.1"),sQuery(id+"F0.wireOp",EDGE,"E7.21.2"),sQuery(id+"F0.wireOp",EDGE,"E7.21.3"),sQuery(id+"F0.wireOp",EDGE,"E7.21.4"),sQuery(id+"F0.wireOp",EDGE,"E7.21.5"),sQuery(id+"F0.wireOp",EDGE,"E7.22.0"),sQuery(id+"F0.wireOp",EDGE,"E7.22.1"),sQuery(id+"F0.wireOp",EDGE,"E7.22.2"),sQuery(id+"F0.wireOp",EDGE,"E7.22.3"),sQuery(id+"F0.wireOp",EDGE,"E7.22.4"),sQuery(id+"F0.wireOp",EDGE,"E7.22.5"),sQuery(id+"F0.wireOp",EDGE,"E7.23.0"),sQuery(id+"F0.wireOp",EDGE,"E7.23.1"),sQuery(id+"F0.wireOp",EDGE,"E7.23.2"),sQuery(id+"F0.wireOp",EDGE,"E7.23.3"),sQuery(id+"F0.wireOp",EDGE,"E7.23.4"),sQuery(id+"F0.wireOp",EDGE,"E7.23.5"),sQuery(id+"F0.wireOp",EDGE,"E7.24.0"),sQuery(id+"F0.wireOp",EDGE,"E7.24.1"),sQuery(id+"F0.wireOp",EDGE,"E7.24.2"),sQuery(id+"F0.wireOp",EDGE,"E7.24.3"),sQuery(id+"F0.wireOp",EDGE,"E7.24.4"),sQuery(id+"F0.wireOp",EDGE,"E7.24.5"),sQuery(id+"F0.wireOp",EDGE,"E7.25.0"),sQuery(id+"F0.wireOp",EDGE,"E7.25.1"),sQuery(id+"F0.wireOp",EDGE,"E7.25.2"),sQuery(id+"F0.wireOp",EDGE,"E7.25.3"),sQuery(id+"F0.wireOp",EDGE,"E7.25.4"),sQuery(id+"F0.wireOp",EDGE,"E7.25.5"),sQuery(id+"F0.wireOp",EDGE,"E7.26.0"),sQuery(id+"F0.wireOp",EDGE,"E7.26.1"),sQuery(id+"F0.wireOp",EDGE,"E7.26.2"),sQuery(id+"F0.wireOp",EDGE,"E7.26.3"),sQuery(id+"F0.wireOp",EDGE,"E7.26.4"),sQuery(id+"F0.wireOp",EDGE,"E7.26.5"),subQ0,sQuery(id+"F0.wireOp",EDGE,"E7.27.1"),sQuery(id+"F0.wireOp",EDGE,"E7.27.2"),sQuery(id+"F0.wireOp",EDGE,"E7.27.3"),sQuery(id+"F0.wireOp",EDGE,"E7.27.4"),sQuery(id+"F0.wireOp",EDGE,"E7.27.5"),sQuery(id+"F0.wireOp",EDGE,"E7.28.0"),sQuery(id+"F0.wireOp",EDGE,"E7.28.1"),sQuery(id+"F0.wireOp",EDGE,"E7.28.2"),sQuery(id+"F0.wireOp",EDGE,"E7.28.3"),sQuery(id+"F0.wireOp",EDGE,"E7.28.4"),sQuery(id+"F0.wireOp",EDGE,"E7.28.5"),sQuery(id+"F0.wireOp",EDGE,"E7.29.0"),sQuery(id+"F0.wireOp",EDGE,"E7.29.1"),sQuery(id+"F0.wireOp",EDGE,"E7.29.2"),sQuery(id+"F0.wireOp",EDGE,"E7.29.3"),sQuery(id+"F0.wireOp",EDGE,"E7.29.4"),sQuery(id+"F0.wireOp",EDGE,"E7.29.5"),sQuery(id+"F0.wireOp",EDGE,"E7.30.0"),sQuery(id+"F0.wireOp",EDGE,"E7.30.1"),sQuery(id+"F0.wireOp",EDGE,"E7.30.2"),sQuery(id+"F0.wireOp",EDGE,"E7.30.3"),sQuery(id+"F0.wireOp",EDGE,"E7.30.4"),sQuery(id+"F0.wireOp",EDGE,"E7.30.5"),sQuery(id+"F0.wireOp",EDGE,"E7.31.0"),sQuery(id+"F0.wireOp",EDGE,"E7.31.1"),sQuery(id+"F0.wireOp",EDGE,"E7.31.2"),sQuery(id+"F0.wireOp",EDGE,"E7.31.3"),sQuery(id+"F0.wireOp",EDGE,"E7.31.4"),sQuery(id+"F0.wireOp",EDGE,"E7.31.5"),sQuery(id+"F0.wireOp",EDGE,"E7.32.0"),sQuery(id+"F0.wireOp",EDGE,"E7.32.1"),sQuery(id+"F0.wireOp",EDGE,"E7.32.2"),sQuery(id+"F0.wireOp",EDGE,"E7.32.3"),sQuery(id+"F0.wireOp",EDGE,"E7.32.4"),sQuery(id+"F0.wireOp",EDGE,"E7.32.5"),sQuery(id+"F0.wireOp",EDGE,"E7.33.0"),sQuery(id+"F0.wireOp",EDGE,"E7.33.1"),sQuery(id+"F0.wireOp",EDGE,"E7.33.2"),sQuery(id+"F0.wireOp",EDGE,"E7.33.3"),sQuery(id+"F0.wireOp",EDGE,"E7.33.4"),sQuery(id+"F0.wireOp",EDGE,"E7.33.5"),sQuery(id+"F0.wireOp",EDGE,"E7.34.0"),sQuery(id+"F0.wireOp",EDGE,"E7.34.1"),sQuery(id+"F0.wireOp",EDGE,"E7.34.2"),sQuery(id+"F0.wireOp",EDGE,"E7.34.3"),sQuery(id+"F0.wireOp",EDGE,"E7.34.4"),sQuery(id+"F0.wireOp",EDGE,"E7.34.5"),sQuery(id+"F0.wireOp",EDGE,"E7.35.0"),sQuery(id+"F0.wireOp",EDGE,"E7.35.1"),sQuery(id+"F0.wireOp",EDGE,"E7.35.2"),sQuery(id+"F0.wireOp",EDGE,"E7.35.3"),sQuery(id+"F0.wireOp",EDGE,"E7.35.4"),sQuery(id+"F0.wireOp",EDGE,"E7.35.5"),sQuery(id+"F0.wireOp",EDGE,"E7.36.0"),sQuery(id+"F0.wireOp",EDGE,"E7.36.1"),sQuery(id+"F0.wireOp",EDGE,"E7.36.2"),sQuery(id+"F0.wireOp",EDGE,"E7.36.3"),sQuery(id+"F0.wireOp",EDGE,"E7.36.4"),sQuery(id+"F0.wireOp",EDGE,"E7.36.5"),sQuery(id+"F0.wireOp",EDGE,"E7.37.0"),sQuery(id+"F0.wireOp",EDGE,"E7.37.1"),sQuery(id+"F0.wireOp",EDGE,"E7.37.2"),sQuery(id+"F0.wireOp",EDGE,"E7.37.3"),sQuery(id+"F0.wireOp",EDGE,"E7.37.4"),sQuery(id+"F0.wireOp",EDGE,"E7.37.5"),sQuery(id+"F0.wireOp",EDGE,"E7.38.0"),sQuery(id+"F0.wireOp",EDGE,"E7.38.1"),sQuery(id+"F0.wireOp",EDGE,"E7.38.2"),sQuery(id+"F0.wireOp",EDGE,"E7.38.3"),sQuery(id+"F0.wireOp",EDGE,"E7.38.4"),sQuery(id+"F0.wireOp",EDGE,"E7.38.5"),sQuery(id+"F0.wireOp",EDGE,"E7.39.0"),sQuery(id+"F0.wireOp",EDGE,"E7.39.1"),sQuery(id+"F0.wireOp",EDGE,"E7.39.2"),sQuery(id+"F0.wireOp",EDGE,"E7.39.3"),sQuery(id+"F0.wireOp",EDGE,"E7.39.4"),sQuery(id+"F0.wireOp",EDGE,"E7.39.5"),sQuery(id+"F0.wireOp",EDGE,"E7.40.0"),sQuery(id+"F0.wireOp",EDGE,"E7.40.1"),sQuery(id+"F0.wireOp",EDGE,"E7.40.2"),sQuery(id+"F0.wireOp",EDGE,"E7.40.3"),sQuery(id+"F0.wireOp",EDGE,"E7.40.4"),sQuery(id+"F0.wireOp",EDGE,"E7.40.5"),sQuery(id+"F0.wireOp",EDGE,"E7.41.0"),sQuery(id+"F0.wireOp",EDGE,"E7.41.1"),sQuery(id+"F0.wireOp",EDGE,"E7.41.2"),sQuery(id+"F0.wireOp",EDGE,"E7.41.3"),sQuery(id+"F0.wireOp",EDGE,"E7.41.4"),sQuery(id+"F0.wireOp",EDGE,"E7.41.5"),sQuery(id+"F0.wireOp",EDGE,"E7.42.0"),sQuery(id+"F0.wireOp",EDGE,"E7.42.1"),sQuery(id+"F0.wireOp",EDGE,"E7.42.2"),sQuery(id+"F0.wireOp",EDGE,"E7.42.3"),sQuery(id+"F0.wireOp",EDGE,"E7.42.4"),sQuery(id+"F0.wireOp",EDGE,"E7.42.5"),sQuery(id+"F0.wireOp",EDGE,"E7.43.0"),sQuery(id+"F0.wireOp",EDGE,"E7.43.1"),sQuery(id+"F0.wireOp",EDGE,"E7.43.2"),sQuery(id+"F0.wireOp",EDGE,"E7.43.3"),sQuery(id+"F0.wireOp",EDGE,"E7.43.4"),sQuery(id+"F0.wireOp",EDGE,"E7.43.5")])],"isStart":false})],"blendedInto":[makeQuery(id+"F1.opExtrude","CAP_FACE",FACE,{"disambiguationData":[OSD([sQuery(id+"F0.wireOp",EDGE,"E1"),sQuery(id+"F0.wireOp",EDGE,"E2"),sQuery(id+"F0.wireOp",EDGE,"E3"),sQuery(id+"F0.wireOp",EDGE,"E4"),sQuery(id+"F0.wireOp",EDGE,"E5"),sQuery(id+"F0.wireOp",EDGE,"E6"),sQuery(id+"F0.wireOp",EDGE,"E7.1.0"),sQuery(id+"F0.wireOp",EDGE,"E7.1.1"),sQuery(id+"F0.wireOp",EDGE,"E7.1.2"),sQuery(id+"F0.wireOp",EDGE,"E7.1.3"),sQuery(id+"F0.wireOp",EDGE,"E7.1.4"),sQuery(id+"F0.wireOp",EDGE,"E7.1.5"),sQuery(id+"F0.wireOp",EDGE,"E7.2.0"),sQuery(id+"F0.wireOp",EDGE,"E7.2.1"),sQuery(id+"F0.wireOp",EDGE,"E7.2.2"),sQuery(id+"F0.wireOp",EDGE,"E7.2.3"),sQuery(id+"F0.wireOp",EDGE,"E7.2.4"),sQuery(id+"F0.wireOp",EDGE,"E7.2.5"),sQuery(id+"F0.wireOp",EDGE,"E7.3.0"),sQuery(id+"F0.wireOp",EDGE,"E7.3.1"),sQuery(id+"F0.wireOp",EDGE,"E7.3.2"),sQuery(id+"F0.wireOp",EDGE,"E7.3.3"),sQuery(id+"F0.wireOp",EDGE,"E7.3.4"),sQuery(id+"F0.wireOp",EDGE,"E7.3.5"),sQuery(id+"F0.wireOp",EDGE,"E7.4.0"),sQuery(id+"F0.wireOp",EDGE,"E7.4.1"),sQuery(id+"F0.wireOp",EDGE,"E7.4.2"),sQuery(id+"F0.wireOp",EDGE,"E7.4.3"),sQuery(id+"F0.wireOp",EDGE,"E7.4.4"),sQuery(id+"F0.wireOp",EDGE,"E7.4.5"),sQuery(id+"F0.wireOp",EDGE,"E7.5.0"),sQuery(id+"F0.wireOp",EDGE,"E7.5.1"),sQuery(id+"F0.wireOp",EDGE,"E7.5.2"),sQuery(id+"F0.wireOp",EDGE,"E7.5.3"),sQuery(id+"F0.wireOp",EDGE,"E7.5.4"),sQuery(id+"F0.wireOp",EDGE,"E7.5.5"),sQuery(id+"F0.wireOp",EDGE,"E7.6.0"),sQuery(id+"F0.wireOp",EDGE,"E7.6.1"),sQuery(id+"F0.wireOp",EDGE,"E7.6.2"),sQuery(id+"F0.wireOp",EDGE,"E7.6.3"),sQuery(id+"F0.wireOp",EDGE,"E7.6.4"),sQuery(id+"F0.wireOp",EDGE,"E7.6.5"),sQuery(id+"F0.wireOp",EDGE,"E7.7.0"),sQuery(id+"F0.wireOp",EDGE,"E7.7.1"),sQuery(id+"F0.wireOp",EDGE,"E7.7.2"),sQuery(id+"F0.wireOp",EDGE,"E7.7.3"),sQuery(id+"F0.wireOp",EDGE,"E7.7.4"),sQuery(id+"F0.wireOp",EDGE,"E7.7.5"),sQuery(id+"F0.wireOp",EDGE,"E7.8.0"),sQuery(id+"F0.wireOp",EDGE,"E7.8.1"),sQuery(id+"F0.wireOp",EDGE,"E7.8.2"),sQuery(id+"F0.wireOp",EDGE,"E7.8.3"),sQuery(id+"F0.wireOp",EDGE,"E7.8.4"),sQuery(id+"F0.wireOp",EDGE,"E7.8.5"),sQuery(id+"F0.wireOp",EDGE,"E7.9.0"),sQuery(id+"F0.wireOp",EDGE,"E7.9.1"),sQuery(id+"F0.wireOp",EDGE,"E7.9.2"),sQuery(id+"F0.wireOp",EDGE,"E7.9.3"),sQuery(id+"F0.wireOp",EDGE,"E7.9.4"),sQuery(id+"F0.wireOp",EDGE,"E7.9.5"),sQuery(id+"F0.wireOp",EDGE,"E7.10.0"),sQuery(id+"F0.wireOp",EDGE,"E7.10.1"),sQuery(id+"F0.wireOp",EDGE,"E7.10.2"),sQuery(id+"F0.wireOp",EDGE,"E7.10.3"),sQuery(id+"F0.wireOp",EDGE,"E7.10.4"),sQuery(id+"F0.wireOp",EDGE,"E7.10.5"),sQuery(id+"F0.wireOp",EDGE,"E7.11.0"),sQuery(id+"F0.wireOp",EDGE,"E7.11.1"),sQuery(id+"F0.wireOp",EDGE,"E7.11.2"),sQuery(id+"F0.wireOp",EDGE,"E7.11.3"),sQuery(id+"F0.wireOp",EDGE,"E7.11.4"),sQuery(id+"F0.wireOp",EDGE,"E7.11.5"),sQuery(id+"F0.wireOp",EDGE,"E7.12.0"),sQuery(id+"F0.wireOp",EDGE,"E7.12.1"),sQuery(id+"F0.wireOp",EDGE,"E7.12.2"),sQuery(id+"F0.wireOp",EDGE,"E7.12.3"),sQuery(id+"F0.wireOp",EDGE,"E7.12.4"),sQuery(id+"F0.wireOp",EDGE,"E7.12.5"),sQuery(id+"F0.wireOp",EDGE,"E7.13.0"),sQuery(id+"F0.wireOp",EDGE,"E7.13.1"),sQuery(id+"F0.wireOp",EDGE,"E7.13.2"),sQuery(id+"F0.wireOp",EDGE,"E7.13.3"),sQuery(id+"F0.wireOp",EDGE,"E7.13.4"),sQuery(id+"F0.wireOp",EDGE,"E7.13.5"),sQuery(id+"F0.wireOp",EDGE,"E7.14.0"),sQuery(id+"F0.wireOp",EDGE,"E7.14.1"),sQuery(id+"F0.wireOp",EDGE,"E7.14.2"),sQuery(id+"F0.wireOp",EDGE,"E7.14.3"),sQuery(id+"F0.wireOp",EDGE,"E7.14.4"),sQuery(id+"F0.wireOp",EDGE,"E7.14.5"),sQuery(id+"F0.wireOp",EDGE,"E7.15.0"),sQuery(id+"F0.wireOp",EDGE,"E7.15.1"),sQuery(id+"F0.wireOp",EDGE,"E7.15.2"),sQuery(id+"F0.wireOp",EDGE,"E7.15.3"),sQuery(id+"F0.wireOp",EDGE,"E7.15.4"),sQuery(id+"F0.wireOp",EDGE,"E7.15.5"),sQuery(id+"F0.wireOp",EDGE,"E7.16.0"),sQuery(id+"F0.wireOp",EDGE,"E7.16.1"),sQuery(id+"F0.wireOp",EDGE,"E7.16.2"),sQuery(id+"F0.wireOp",EDGE,"E7.16.3"),sQuery(id+"F0.wireOp",EDGE,"E7.16.4"),sQuery(id+"F0.wireOp",EDGE,"E7.16.5"),sQuery(id+"F0.wireOp",EDGE,"E7.17.0"),sQuery(id+"F0.wireOp",EDGE,"E7.17.1"),sQuery(id+"F0.wireOp",EDGE,"E7.17.2"),sQuery(id+"F0.wireOp",EDGE,"E7.17.3"),sQuery(id+"F0.wireOp",EDGE,"E7.17.4"),sQuery(id+"F0.wireOp",EDGE,"E7.17.5"),sQuery(id+"F0.wireOp",EDGE,"E7.18.0"),sQuery(id+"F0.wireOp",EDGE,"E7.18.1"),sQuery(id+"F0.wireOp",EDGE,"E7.18.2"),sQuery(id+"F0.wireOp",EDGE,"E7.18.3"),sQuery(id+"F0.wireOp",EDGE,"E7.18.4"),sQuery(id+"F0.wireOp",EDGE,"E7.18.5"),sQuery(id+"F0.wireOp",EDGE,"E7.19.0"),sQuery(id+"F0.wireOp",EDGE,"E7.19.1"),sQuery(id+"F0.wireOp",EDGE,"E7.19.2"),sQuery(id+"F0.wireOp",EDGE,"E7.19.3"),sQuery(id+"F0.wireOp",EDGE,"E7.19.4"),sQuery(id+"F0.wireOp",EDGE,"E7.19.5"),sQuery(id+"F0.wireOp",EDGE,"E7.20.0"),sQuery(id+"F0.wireOp",EDGE,"E7.20.1"),sQuery(id+"F0.wireOp",EDGE,"E7.20.2"),sQuery(id+"F0.wireOp",EDGE,"E7.20.3"),sQuery(id+"F0.wireOp",EDGE,"E7.20.4"),sQuery(id+"F0.wireOp",EDGE,"E7.20.5"),sQuery(id+"F0.wireOp",EDGE,"E7.21.0"),sQuery(id+"F0.wireOp",EDGE,"E7.21.1"),sQuery(id+"F0.wireOp",EDGE,"E7.21.2"),sQuery(id+"F0.wireOp",EDGE,"E7.21.3"),sQuery(id+"F0.wireOp",EDGE,"E7.21.4"),sQuery(id+"F0.wireOp",EDGE,"E7.21.5"),sQuery(id+"F0.wireOp",EDGE,"E7.22.0"),sQuery(id+"F0.wireOp",EDGE,"E7.22.1"),sQuery(id+"F0.wireOp",EDGE,"E7.22.2"),sQuery(id+"F0.wireOp",EDGE,"E7.22.3"),sQuery(id+"F0.wireOp",EDGE,"E7.22.4"),sQuery(id+"F0.wireOp",EDGE,"E7.22.5"),sQuery(id+"F0.wireOp",EDGE,"E7.23.0"),sQuery(id+"F0.wireOp",EDGE,"E7.23.1"),sQuery(id+"F0.wireOp",EDGE,"E7.23.2"),sQuery(id+"F0.wireOp",EDGE,"E7.23.3"),sQuery(id+"F0.wireOp",EDGE,"E7.23.4"),sQuery(id+"F0.wireOp",EDGE,"E7.23.5"),sQuery(id+"F0.wireOp",EDGE,"E7.24.0"),sQuery(id+"F0.wireOp",EDGE,"E7.24.1"),sQuery(id+"F0.wireOp",EDGE,"E7.24.2"),sQuery(id+"F0.wireOp",EDGE,"E7.24.3"),sQuery(id+"F0.wireOp",EDGE,"E7.24.4"),sQuery(id+"F0.wireOp",EDGE,"E7.24.5"),sQuery(id+"F0.wireOp",EDGE,"E7.25.0"),sQuery(id+"F0.wireOp",EDGE,"E7.25.1"),sQuery(id+"F0.wireOp",EDGE,"E7.25.2"),sQuery(id+"F0.wireOp",EDGE,"E7.25.3"),sQuery(id+"F0.wireOp",EDGE,"E7.25.4"),sQuery(id+"F0.wireOp",EDGE,"E7.25.5"),sQuery(id+"F0.wireOp",EDGE,"E7.26.0"),sQuery(id+"F0.wireOp",EDGE,"E7.26.1"),sQuery(id+"F0.wireOp",EDGE,"E7.26.2"),sQuery(id+"F0.wireOp",EDGE,"E7.26.3"),sQuery(id+"F0.wireOp",EDGE,"E7.26.4"),sQuery(id+"F0.wireOp",EDGE,"E7.26.5"),subQ0,sQuery(id+"F0.wireOp",EDGE,"E7.27.1"),sQuery(id+"F0.wireOp",EDGE,"E7.27.2"),sQuery(id+"F0.wireOp",EDGE,"E7.27.3"),sQuery(id+"F0.wireOp",EDGE,"E7.27.4"),sQuery(id+"F0.wireOp",EDGE,"E7.27.5"),sQuery(id+"F0.wireOp",EDGE,"E7.28.0"),sQuery(id+"F0.wireOp",EDGE,"E7.28.1"),sQuery(id+"F0.wireOp",EDGE,"E7.28.2"),sQuery(id+"F0.wireOp",EDGE,"E7.28.3"),sQuery(id+"F0.wireOp",EDGE,"E7.28.4"),sQuery(id+"F0.wireOp",EDGE,"E7.28.5"),sQuery(id+"F0.wireOp",EDGE,"E7.29.0"),sQuery(id+"F0.wireOp",EDGE,"E7.29.1"),sQuery(id+"F0.wireOp",EDGE,"E7.29.2"),sQuery(id+"F0.wireOp",EDGE,"E7.29.3"),sQuery(id+"F0.wireOp",EDGE,"E7.29.4"),sQuery(id+"F0.wireOp",EDGE,"E7.29.5"),sQuery(id+"F0.wireOp",EDGE,"E7.30.0"),sQuery(id+"F0.wireOp",EDGE,"E7.30.1"),sQuery(id+"F0.wireOp",EDGE,"E7.30.2"),sQuery(id+"F0.wireOp",EDGE,"E7.30.3"),sQuery(id+"F0.wireOp",EDGE,"E7.30.4"),sQuery(id+"F0.wireOp",EDGE,"E7.30.5"),sQuery(id+"F0.wireOp",EDGE,"E7.31.0"),sQuery(id+"F0.wireOp",EDGE,"E7.31.1"),sQuery(id+"F0.wireOp",EDGE,"E7.31.2"),sQuery(id+"F0.wireOp",EDGE,"E7.31.3"),sQuery(id+"F0.wireOp",EDGE,"E7.31.4"),sQuery(id+"F0.wireOp",EDGE,"E7.31.5"),sQuery(id+"F0.wireOp",EDGE,"E7.32.0"),sQuery(id+"F0.wireOp",EDGE,"E7.32.1"),sQuery(id+"F0.wireOp",EDGE,"E7.32.2"),sQuery(id+"F0.wireOp",EDGE,"E7.32.3"),sQuery(id+"F0.wireOp",EDGE,"E7.32.4"),sQuery(id+"F0.wireOp",EDGE,"E7.32.5"),sQuery(id+"F0.wireOp",EDGE,"E7.33.0"),sQuery(id+"F0.wireOp",EDGE,"E7.33.1"),sQuery(id+"F0.wireOp",EDGE,"E7.33.2"),sQuery(id+"F0.wireOp",EDGE,"E7.33.3"),sQuery(id+"F0.wireOp",EDGE,"E7.33.4"),sQuery(id+"F0.wireOp",EDGE,"E7.33.5"),sQuery(id+"F0.wireOp",EDGE,"E7.34.0"),sQuery(id+"F0.wireOp",EDGE,"E7.34.1"),sQuery(id+"F0.wireOp",EDGE,"E7.34.2"),sQuery(id+"F0.wireOp",EDGE,"E7.34.3"),sQuery(id+"F0.wireOp",EDGE,"E7.34.4"),sQuery(id+"F0.wireOp",EDGE,"E7.34.5"),sQuery(id+"F0.wireOp",EDGE,"E7.35.0"),sQuery(id+"F0.wireOp",EDGE,"E7.35.1"),sQuery(id+"F0.wireOp",EDGE,"E7.35.2"),sQuery(id+"F0.wireOp",EDGE,"E7.35.3"),sQuery(id+"F0.wireOp",EDGE,"E7.35.4"),sQuery(id+"F0.wireOp",EDGE,"E7.35.5"),sQuery(id+"F0.wireOp",EDGE,"E7.36.0"),sQuery(id+"F0.wireOp",EDGE,"E7.36.1"),sQuery(id+"F0.wireOp",EDGE,"E7.36.2"),sQuery(id+"F0.wireOp",EDGE,"E7.36.3"),sQuery(id+"F0.wireOp",EDGE,"E7.36.4"),sQuery(id+"F0.wireOp",EDGE,"E7.36.5"),sQuery(id+"F0.wireOp",EDGE,"E7.37.0"),sQuery(id+"F0.wireOp",EDGE,"E7.37.1"),sQuery(id+"F0.wireOp",EDGE,"E7.37.2"),sQuery(id+"F0.wireOp",EDGE,"E7.37.3"),sQuery(id+"F0.wireOp",EDGE,"E7.37.4"),sQuery(id+"F0.wireOp",EDGE,"E7.37.5"),sQuery(id+"F0.wireOp",EDGE,"E7.38.0"),sQuery(id+"F0.wireOp",EDGE,"E7.38.1"),sQuery(id+"F0.wireOp",EDGE,"E7.38.2"),sQuery(id+"F0.wireOp",EDGE,"E7.38.3"),sQuery(id+"F0.wireOp",EDGE,"E7.38.4"),sQuery(id+"F0.wireOp",EDGE,"E7.38.5"),sQuery(id+"F0.wireOp",EDGE,"E7.39.0"),sQuery(id+"F0.wireOp",EDGE,"E7.39.1"),sQuery(id+"F0.wireOp",EDGE,"E7.39.2"),sQuery(id+"F0.wireOp",EDGE,"E7.39.3"),sQuery(id+"F0.wireOp",EDGE,"E7.39.4"),sQuery(id+"F0.wireOp",EDGE,"E7.39.5"),sQuery(id+"F0.wireOp",EDGE,"E7.40.0"),sQuery(id+"F0.wireOp",EDGE,"E7.40.1"),sQuery(id+"F0.wireOp",EDGE,"E7.40.2"),sQuery(id+"F0.wireOp",EDGE,"E7.40.3"),sQuery(id+"F0.wireOp",EDGE,"E7.40.4"),sQuery(id+"F0.wireOp",EDGE,"E7.40.5"),sQuery(id+"F0.wireOp",EDGE,"E7.41.0"),sQuery(id+"F0.wireOp",EDGE,"E7.41.1"),sQuery(id+"F0.wireOp",EDGE,"E7.41.2"),sQuery(id+"F0.wireOp",EDGE,"E7.41.3"),sQuery(id+"F0.wireOp",EDGE,"E7.41.4"),sQuery(id+"F0.wireOp",EDGE,"E7.41.5"),sQuery(id+"F0.wireOp",EDGE,"E7.42.0"),sQuery(id+"F0.wireOp",EDGE,"E7.42.1"),sQuery(id+"F0.wireOp",EDGE,"E7.42.2"),sQuery(id+"F0.wireOp",EDGE,"E7.42.3"),sQuery(id+"F0.wireOp",EDGE,"E7.42.4"),sQuery(id+"F0.wireOp",EDGE,"E7.42.5"),sQuery(id+"F0.wireOp",EDGE,"E7.43.0"),sQuery(id+"F0.wireOp",EDGE,"E7.43.1"),sQuery(id+"F0.wireOp",EDGE,"E7.43.2"),sQuery(id+"F0.wireOp",EDGE,"E7.43.3"),sQuery(id+"F0.wireOp",EDGE,"E7.43.4"),sQuery(id+"F0.wireOp",EDGE,"E7.43.5")])],"isStart":false})]}),makeQuery(id+"F2.opChamfer","BLEND_FACE",FACE,{"disambiguationData":[OSD([subQ0])]})],"blendedInto":[makeQuery(id+"F2.opChamfer","BLEND_FACE",FACE,{"disambiguationData":[OSD([subQ0])]})]});}
            var Q10;
            {var subQ0=sQuery(id+"F0.wireOp",EDGE,"E7.25.0");Q10=makeQuery(id+"F8.opChamfer","BLEND_EDGE",EDGE,{"blendedFrom":[makeQuery(id+"F2.opChamfer","BLEND_EDGE",EDGE,{"blendedFrom":[makeQuery(id+"F1.opExtrude","CAP_EDGE",EDGE,{"disambiguationData":[OSD([subQ0])],"isStart":false}),makeQuery(id+"F1.opExtrude","CAP_FACE",FACE,{"disambiguationData":[OSD([sQuery(id+"F0.wireOp",EDGE,"E1"),sQuery(id+"F0.wireOp",EDGE,"E2"),sQuery(id+"F0.wireOp",EDGE,"E3"),sQuery(id+"F0.wireOp",EDGE,"E4"),sQuery(id+"F0.wireOp",EDGE,"E5"),sQuery(id+"F0.wireOp",EDGE,"E6"),sQuery(id+"F0.wireOp",EDGE,"E7.1.0"),sQuery(id+"F0.wireOp",EDGE,"E7.1.1"),sQuery(id+"F0.wireOp",EDGE,"E7.1.2"),sQuery(id+"F0.wireOp",EDGE,"E7.1.3"),sQuery(id+"F0.wireOp",EDGE,"E7.1.4"),sQuery(id+"F0.wireOp",EDGE,"E7.1.5"),sQuery(id+"F0.wireOp",EDGE,"E7.2.0"),sQuery(id+"F0.wireOp",EDGE,"E7.2.1"),sQuery(id+"F0.wireOp",EDGE,"E7.2.2"),sQuery(id+"F0.wireOp",EDGE,"E7.2.3"),sQuery(id+"F0.wireOp",EDGE,"E7.2.4"),sQuery(id+"F0.wireOp",EDGE,"E7.2.5"),sQuery(id+"F0.wireOp",EDGE,"E7.3.0"),sQuery(id+"F0.wireOp",EDGE,"E7.3.1"),sQuery(id+"F0.wireOp",EDGE,"E7.3.2"),sQuery(id+"F0.wireOp",EDGE,"E7.3.3"),sQuery(id+"F0.wireOp",EDGE,"E7.3.4"),sQuery(id+"F0.wireOp",EDGE,"E7.3.5"),sQuery(id+"F0.wireOp",EDGE,"E7.4.0"),sQuery(id+"F0.wireOp",EDGE,"E7.4.1"),sQuery(id+"F0.wireOp",EDGE,"E7.4.2"),sQuery(id+"F0.wireOp",EDGE,"E7.4.3"),sQuery(id+"F0.wireOp",EDGE,"E7.4.4"),sQuery(id+"F0.wireOp",EDGE,"E7.4.5"),sQuery(id+"F0.wireOp",EDGE,"E7.5.0"),sQuery(id+"F0.wireOp",EDGE,"E7.5.1"),sQuery(id+"F0.wireOp",EDGE,"E7.5.2"),sQuery(id+"F0.wireOp",EDGE,"E7.5.3"),sQuery(id+"F0.wireOp",EDGE,"E7.5.4"),sQuery(id+"F0.wireOp",EDGE,"E7.5.5"),sQuery(id+"F0.wireOp",EDGE,"E7.6.0"),sQuery(id+"F0.wireOp",EDGE,"E7.6.1"),sQuery(id+"F0.wireOp",EDGE,"E7.6.2"),sQuery(id+"F0.wireOp",EDGE,"E7.6.3"),sQuery(id+"F0.wireOp",EDGE,"E7.6.4"),sQuery(id+"F0.wireOp",EDGE,"E7.6.5"),sQuery(id+"F0.wireOp",EDGE,"E7.7.0"),sQuery(id+"F0.wireOp",EDGE,"E7.7.1"),sQuery(id+"F0.wireOp",EDGE,"E7.7.2"),sQuery(id+"F0.wireOp",EDGE,"E7.7.3"),sQuery(id+"F0.wireOp",EDGE,"E7.7.4"),sQuery(id+"F0.wireOp",EDGE,"E7.7.5"),sQuery(id+"F0.wireOp",EDGE,"E7.8.0"),sQuery(id+"F0.wireOp",EDGE,"E7.8.1"),sQuery(id+"F0.wireOp",EDGE,"E7.8.2"),sQuery(id+"F0.wireOp",EDGE,"E7.8.3"),sQuery(id+"F0.wireOp",EDGE,"E7.8.4"),sQuery(id+"F0.wireOp",EDGE,"E7.8.5"),sQuery(id+"F0.wireOp",EDGE,"E7.9.0"),sQuery(id+"F0.wireOp",EDGE,"E7.9.1"),sQuery(id+"F0.wireOp",EDGE,"E7.9.2"),sQuery(id+"F0.wireOp",EDGE,"E7.9.3"),sQuery(id+"F0.wireOp",EDGE,"E7.9.4"),sQuery(id+"F0.wireOp",EDGE,"E7.9.5"),sQuery(id+"F0.wireOp",EDGE,"E7.10.0"),sQuery(id+"F0.wireOp",EDGE,"E7.10.1"),sQuery(id+"F0.wireOp",EDGE,"E7.10.2"),sQuery(id+"F0.wireOp",EDGE,"E7.10.3"),sQuery(id+"F0.wireOp",EDGE,"E7.10.4"),sQuery(id+"F0.wireOp",EDGE,"E7.10.5"),sQuery(id+"F0.wireOp",EDGE,"E7.11.0"),sQuery(id+"F0.wireOp",EDGE,"E7.11.1"),sQuery(id+"F0.wireOp",EDGE,"E7.11.2"),sQuery(id+"F0.wireOp",EDGE,"E7.11.3"),sQuery(id+"F0.wireOp",EDGE,"E7.11.4"),sQuery(id+"F0.wireOp",EDGE,"E7.11.5"),sQuery(id+"F0.wireOp",EDGE,"E7.12.0"),sQuery(id+"F0.wireOp",EDGE,"E7.12.1"),sQuery(id+"F0.wireOp",EDGE,"E7.12.2"),sQuery(id+"F0.wireOp",EDGE,"E7.12.3"),sQuery(id+"F0.wireOp",EDGE,"E7.12.4"),sQuery(id+"F0.wireOp",EDGE,"E7.12.5"),sQuery(id+"F0.wireOp",EDGE,"E7.13.0"),sQuery(id+"F0.wireOp",EDGE,"E7.13.1"),sQuery(id+"F0.wireOp",EDGE,"E7.13.2"),sQuery(id+"F0.wireOp",EDGE,"E7.13.3"),sQuery(id+"F0.wireOp",EDGE,"E7.13.4"),sQuery(id+"F0.wireOp",EDGE,"E7.13.5"),sQuery(id+"F0.wireOp",EDGE,"E7.14.0"),sQuery(id+"F0.wireOp",EDGE,"E7.14.1"),sQuery(id+"F0.wireOp",EDGE,"E7.14.2"),sQuery(id+"F0.wireOp",EDGE,"E7.14.3"),sQuery(id+"F0.wireOp",EDGE,"E7.14.4"),sQuery(id+"F0.wireOp",EDGE,"E7.14.5"),sQuery(id+"F0.wireOp",EDGE,"E7.15.0"),sQuery(id+"F0.wireOp",EDGE,"E7.15.1"),sQuery(id+"F0.wireOp",EDGE,"E7.15.2"),sQuery(id+"F0.wireOp",EDGE,"E7.15.3"),sQuery(id+"F0.wireOp",EDGE,"E7.15.4"),sQuery(id+"F0.wireOp",EDGE,"E7.15.5"),sQuery(id+"F0.wireOp",EDGE,"E7.16.0"),sQuery(id+"F0.wireOp",EDGE,"E7.16.1"),sQuery(id+"F0.wireOp",EDGE,"E7.16.2"),sQuery(id+"F0.wireOp",EDGE,"E7.16.3"),sQuery(id+"F0.wireOp",EDGE,"E7.16.4"),sQuery(id+"F0.wireOp",EDGE,"E7.16.5"),sQuery(id+"F0.wireOp",EDGE,"E7.17.0"),sQuery(id+"F0.wireOp",EDGE,"E7.17.1"),sQuery(id+"F0.wireOp",EDGE,"E7.17.2"),sQuery(id+"F0.wireOp",EDGE,"E7.17.3"),sQuery(id+"F0.wireOp",EDGE,"E7.17.4"),sQuery(id+"F0.wireOp",EDGE,"E7.17.5"),sQuery(id+"F0.wireOp",EDGE,"E7.18.0"),sQuery(id+"F0.wireOp",EDGE,"E7.18.1"),sQuery(id+"F0.wireOp",EDGE,"E7.18.2"),sQuery(id+"F0.wireOp",EDGE,"E7.18.3"),sQuery(id+"F0.wireOp",EDGE,"E7.18.4"),sQuery(id+"F0.wireOp",EDGE,"E7.18.5"),sQuery(id+"F0.wireOp",EDGE,"E7.19.0"),sQuery(id+"F0.wireOp",EDGE,"E7.19.1"),sQuery(id+"F0.wireOp",EDGE,"E7.19.2"),sQuery(id+"F0.wireOp",EDGE,"E7.19.3"),sQuery(id+"F0.wireOp",EDGE,"E7.19.4"),sQuery(id+"F0.wireOp",EDGE,"E7.19.5"),sQuery(id+"F0.wireOp",EDGE,"E7.20.0"),sQuery(id+"F0.wireOp",EDGE,"E7.20.1"),sQuery(id+"F0.wireOp",EDGE,"E7.20.2"),sQuery(id+"F0.wireOp",EDGE,"E7.20.3"),sQuery(id+"F0.wireOp",EDGE,"E7.20.4"),sQuery(id+"F0.wireOp",EDGE,"E7.20.5"),sQuery(id+"F0.wireOp",EDGE,"E7.21.0"),sQuery(id+"F0.wireOp",EDGE,"E7.21.1"),sQuery(id+"F0.wireOp",EDGE,"E7.21.2"),sQuery(id+"F0.wireOp",EDGE,"E7.21.3"),sQuery(id+"F0.wireOp",EDGE,"E7.21.4"),sQuery(id+"F0.wireOp",EDGE,"E7.21.5"),sQuery(id+"F0.wireOp",EDGE,"E7.22.0"),sQuery(id+"F0.wireOp",EDGE,"E7.22.1"),sQuery(id+"F0.wireOp",EDGE,"E7.22.2"),sQuery(id+"F0.wireOp",EDGE,"E7.22.3"),sQuery(id+"F0.wireOp",EDGE,"E7.22.4"),sQuery(id+"F0.wireOp",EDGE,"E7.22.5"),sQuery(id+"F0.wireOp",EDGE,"E7.23.0"),sQuery(id+"F0.wireOp",EDGE,"E7.23.1"),sQuery(id+"F0.wireOp",EDGE,"E7.23.2"),sQuery(id+"F0.wireOp",EDGE,"E7.23.3"),sQuery(id+"F0.wireOp",EDGE,"E7.23.4"),sQuery(id+"F0.wireOp",EDGE,"E7.23.5"),sQuery(id+"F0.wireOp",EDGE,"E7.24.0"),sQuery(id+"F0.wireOp",EDGE,"E7.24.1"),sQuery(id+"F0.wireOp",EDGE,"E7.24.2"),sQuery(id+"F0.wireOp",EDGE,"E7.24.3"),sQuery(id+"F0.wireOp",EDGE,"E7.24.4"),sQuery(id+"F0.wireOp",EDGE,"E7.24.5"),subQ0,sQuery(id+"F0.wireOp",EDGE,"E7.25.1"),sQuery(id+"F0.wireOp",EDGE,"E7.25.2"),sQuery(id+"F0.wireOp",EDGE,"E7.25.3"),sQuery(id+"F0.wireOp",EDGE,"E7.25.4"),sQuery(id+"F0.wireOp",EDGE,"E7.25.5"),sQuery(id+"F0.wireOp",EDGE,"E7.26.0"),sQuery(id+"F0.wireOp",EDGE,"E7.26.1"),sQuery(id+"F0.wireOp",EDGE,"E7.26.2"),sQuery(id+"F0.wireOp",EDGE,"E7.26.3"),sQuery(id+"F0.wireOp",EDGE,"E7.26.4"),sQuery(id+"F0.wireOp",EDGE,"E7.26.5"),sQuery(id+"F0.wireOp",EDGE,"E7.27.0"),sQuery(id+"F0.wireOp",EDGE,"E7.27.1"),sQuery(id+"F0.wireOp",EDGE,"E7.27.2"),sQuery(id+"F0.wireOp",EDGE,"E7.27.3"),sQuery(id+"F0.wireOp",EDGE,"E7.27.4"),sQuery(id+"F0.wireOp",EDGE,"E7.27.5"),sQuery(id+"F0.wireOp",EDGE,"E7.28.0"),sQuery(id+"F0.wireOp",EDGE,"E7.28.1"),sQuery(id+"F0.wireOp",EDGE,"E7.28.2"),sQuery(id+"F0.wireOp",EDGE,"E7.28.3"),sQuery(id+"F0.wireOp",EDGE,"E7.28.4"),sQuery(id+"F0.wireOp",EDGE,"E7.28.5"),sQuery(id+"F0.wireOp",EDGE,"E7.29.0"),sQuery(id+"F0.wireOp",EDGE,"E7.29.1"),sQuery(id+"F0.wireOp",EDGE,"E7.29.2"),sQuery(id+"F0.wireOp",EDGE,"E7.29.3"),sQuery(id+"F0.wireOp",EDGE,"E7.29.4"),sQuery(id+"F0.wireOp",EDGE,"E7.29.5"),sQuery(id+"F0.wireOp",EDGE,"E7.30.0"),sQuery(id+"F0.wireOp",EDGE,"E7.30.1"),sQuery(id+"F0.wireOp",EDGE,"E7.30.2"),sQuery(id+"F0.wireOp",EDGE,"E7.30.3"),sQuery(id+"F0.wireOp",EDGE,"E7.30.4"),sQuery(id+"F0.wireOp",EDGE,"E7.30.5"),sQuery(id+"F0.wireOp",EDGE,"E7.31.0"),sQuery(id+"F0.wireOp",EDGE,"E7.31.1"),sQuery(id+"F0.wireOp",EDGE,"E7.31.2"),sQuery(id+"F0.wireOp",EDGE,"E7.31.3"),sQuery(id+"F0.wireOp",EDGE,"E7.31.4"),sQuery(id+"F0.wireOp",EDGE,"E7.31.5"),sQuery(id+"F0.wireOp",EDGE,"E7.32.0"),sQuery(id+"F0.wireOp",EDGE,"E7.32.1"),sQuery(id+"F0.wireOp",EDGE,"E7.32.2"),sQuery(id+"F0.wireOp",EDGE,"E7.32.3"),sQuery(id+"F0.wireOp",EDGE,"E7.32.4"),sQuery(id+"F0.wireOp",EDGE,"E7.32.5"),sQuery(id+"F0.wireOp",EDGE,"E7.33.0"),sQuery(id+"F0.wireOp",EDGE,"E7.33.1"),sQuery(id+"F0.wireOp",EDGE,"E7.33.2"),sQuery(id+"F0.wireOp",EDGE,"E7.33.3"),sQuery(id+"F0.wireOp",EDGE,"E7.33.4"),sQuery(id+"F0.wireOp",EDGE,"E7.33.5"),sQuery(id+"F0.wireOp",EDGE,"E7.34.0"),sQuery(id+"F0.wireOp",EDGE,"E7.34.1"),sQuery(id+"F0.wireOp",EDGE,"E7.34.2"),sQuery(id+"F0.wireOp",EDGE,"E7.34.3"),sQuery(id+"F0.wireOp",EDGE,"E7.34.4"),sQuery(id+"F0.wireOp",EDGE,"E7.34.5"),sQuery(id+"F0.wireOp",EDGE,"E7.35.0"),sQuery(id+"F0.wireOp",EDGE,"E7.35.1"),sQuery(id+"F0.wireOp",EDGE,"E7.35.2"),sQuery(id+"F0.wireOp",EDGE,"E7.35.3"),sQuery(id+"F0.wireOp",EDGE,"E7.35.4"),sQuery(id+"F0.wireOp",EDGE,"E7.35.5"),sQuery(id+"F0.wireOp",EDGE,"E7.36.0"),sQuery(id+"F0.wireOp",EDGE,"E7.36.1"),sQuery(id+"F0.wireOp",EDGE,"E7.36.2"),sQuery(id+"F0.wireOp",EDGE,"E7.36.3"),sQuery(id+"F0.wireOp",EDGE,"E7.36.4"),sQuery(id+"F0.wireOp",EDGE,"E7.36.5"),sQuery(id+"F0.wireOp",EDGE,"E7.37.0"),sQuery(id+"F0.wireOp",EDGE,"E7.37.1"),sQuery(id+"F0.wireOp",EDGE,"E7.37.2"),sQuery(id+"F0.wireOp",EDGE,"E7.37.3"),sQuery(id+"F0.wireOp",EDGE,"E7.37.4"),sQuery(id+"F0.wireOp",EDGE,"E7.37.5"),sQuery(id+"F0.wireOp",EDGE,"E7.38.0"),sQuery(id+"F0.wireOp",EDGE,"E7.38.1"),sQuery(id+"F0.wireOp",EDGE,"E7.38.2"),sQuery(id+"F0.wireOp",EDGE,"E7.38.3"),sQuery(id+"F0.wireOp",EDGE,"E7.38.4"),sQuery(id+"F0.wireOp",EDGE,"E7.38.5"),sQuery(id+"F0.wireOp",EDGE,"E7.39.0"),sQuery(id+"F0.wireOp",EDGE,"E7.39.1"),sQuery(id+"F0.wireOp",EDGE,"E7.39.2"),sQuery(id+"F0.wireOp",EDGE,"E7.39.3"),sQuery(id+"F0.wireOp",EDGE,"E7.39.4"),sQuery(id+"F0.wireOp",EDGE,"E7.39.5"),sQuery(id+"F0.wireOp",EDGE,"E7.40.0"),sQuery(id+"F0.wireOp",EDGE,"E7.40.1"),sQuery(id+"F0.wireOp",EDGE,"E7.40.2"),sQuery(id+"F0.wireOp",EDGE,"E7.40.3"),sQuery(id+"F0.wireOp",EDGE,"E7.40.4"),sQuery(id+"F0.wireOp",EDGE,"E7.40.5"),sQuery(id+"F0.wireOp",EDGE,"E7.41.0"),sQuery(id+"F0.wireOp",EDGE,"E7.41.1"),sQuery(id+"F0.wireOp",EDGE,"E7.41.2"),sQuery(id+"F0.wireOp",EDGE,"E7.41.3"),sQuery(id+"F0.wireOp",EDGE,"E7.41.4"),sQuery(id+"F0.wireOp",EDGE,"E7.41.5"),sQuery(id+"F0.wireOp",EDGE,"E7.42.0"),sQuery(id+"F0.wireOp",EDGE,"E7.42.1"),sQuery(id+"F0.wireOp",EDGE,"E7.42.2"),sQuery(id+"F0.wireOp",EDGE,"E7.42.3"),sQuery(id+"F0.wireOp",EDGE,"E7.42.4"),sQuery(id+"F0.wireOp",EDGE,"E7.42.5"),sQuery(id+"F0.wireOp",EDGE,"E7.43.0"),sQuery(id+"F0.wireOp",EDGE,"E7.43.1"),sQuery(id+"F0.wireOp",EDGE,"E7.43.2"),sQuery(id+"F0.wireOp",EDGE,"E7.43.3"),sQuery(id+"F0.wireOp",EDGE,"E7.43.4"),sQuery(id+"F0.wireOp",EDGE,"E7.43.5")])],"isStart":false})],"blendedInto":[makeQuery(id+"F1.opExtrude","CAP_FACE",FACE,{"disambiguationData":[OSD([sQuery(id+"F0.wireOp",EDGE,"E1"),sQuery(id+"F0.wireOp",EDGE,"E2"),sQuery(id+"F0.wireOp",EDGE,"E3"),sQuery(id+"F0.wireOp",EDGE,"E4"),sQuery(id+"F0.wireOp",EDGE,"E5"),sQuery(id+"F0.wireOp",EDGE,"E6"),sQuery(id+"F0.wireOp",EDGE,"E7.1.0"),sQuery(id+"F0.wireOp",EDGE,"E7.1.1"),sQuery(id+"F0.wireOp",EDGE,"E7.1.2"),sQuery(id+"F0.wireOp",EDGE,"E7.1.3"),sQuery(id+"F0.wireOp",EDGE,"E7.1.4"),sQuery(id+"F0.wireOp",EDGE,"E7.1.5"),sQuery(id+"F0.wireOp",EDGE,"E7.2.0"),sQuery(id+"F0.wireOp",EDGE,"E7.2.1"),sQuery(id+"F0.wireOp",EDGE,"E7.2.2"),sQuery(id+"F0.wireOp",EDGE,"E7.2.3"),sQuery(id+"F0.wireOp",EDGE,"E7.2.4"),sQuery(id+"F0.wireOp",EDGE,"E7.2.5"),sQuery(id+"F0.wireOp",EDGE,"E7.3.0"),sQuery(id+"F0.wireOp",EDGE,"E7.3.1"),sQuery(id+"F0.wireOp",EDGE,"E7.3.2"),sQuery(id+"F0.wireOp",EDGE,"E7.3.3"),sQuery(id+"F0.wireOp",EDGE,"E7.3.4"),sQuery(id+"F0.wireOp",EDGE,"E7.3.5"),sQuery(id+"F0.wireOp",EDGE,"E7.4.0"),sQuery(id+"F0.wireOp",EDGE,"E7.4.1"),sQuery(id+"F0.wireOp",EDGE,"E7.4.2"),sQuery(id+"F0.wireOp",EDGE,"E7.4.3"),sQuery(id+"F0.wireOp",EDGE,"E7.4.4"),sQuery(id+"F0.wireOp",EDGE,"E7.4.5"),sQuery(id+"F0.wireOp",EDGE,"E7.5.0"),sQuery(id+"F0.wireOp",EDGE,"E7.5.1"),sQuery(id+"F0.wireOp",EDGE,"E7.5.2"),sQuery(id+"F0.wireOp",EDGE,"E7.5.3"),sQuery(id+"F0.wireOp",EDGE,"E7.5.4"),sQuery(id+"F0.wireOp",EDGE,"E7.5.5"),sQuery(id+"F0.wireOp",EDGE,"E7.6.0"),sQuery(id+"F0.wireOp",EDGE,"E7.6.1"),sQuery(id+"F0.wireOp",EDGE,"E7.6.2"),sQuery(id+"F0.wireOp",EDGE,"E7.6.3"),sQuery(id+"F0.wireOp",EDGE,"E7.6.4"),sQuery(id+"F0.wireOp",EDGE,"E7.6.5"),sQuery(id+"F0.wireOp",EDGE,"E7.7.0"),sQuery(id+"F0.wireOp",EDGE,"E7.7.1"),sQuery(id+"F0.wireOp",EDGE,"E7.7.2"),sQuery(id+"F0.wireOp",EDGE,"E7.7.3"),sQuery(id+"F0.wireOp",EDGE,"E7.7.4"),sQuery(id+"F0.wireOp",EDGE,"E7.7.5"),sQuery(id+"F0.wireOp",EDGE,"E7.8.0"),sQuery(id+"F0.wireOp",EDGE,"E7.8.1"),sQuery(id+"F0.wireOp",EDGE,"E7.8.2"),sQuery(id+"F0.wireOp",EDGE,"E7.8.3"),sQuery(id+"F0.wireOp",EDGE,"E7.8.4"),sQuery(id+"F0.wireOp",EDGE,"E7.8.5"),sQuery(id+"F0.wireOp",EDGE,"E7.9.0"),sQuery(id+"F0.wireOp",EDGE,"E7.9.1"),sQuery(id+"F0.wireOp",EDGE,"E7.9.2"),sQuery(id+"F0.wireOp",EDGE,"E7.9.3"),sQuery(id+"F0.wireOp",EDGE,"E7.9.4"),sQuery(id+"F0.wireOp",EDGE,"E7.9.5"),sQuery(id+"F0.wireOp",EDGE,"E7.10.0"),sQuery(id+"F0.wireOp",EDGE,"E7.10.1"),sQuery(id+"F0.wireOp",EDGE,"E7.10.2"),sQuery(id+"F0.wireOp",EDGE,"E7.10.3"),sQuery(id+"F0.wireOp",EDGE,"E7.10.4"),sQuery(id+"F0.wireOp",EDGE,"E7.10.5"),sQuery(id+"F0.wireOp",EDGE,"E7.11.0"),sQuery(id+"F0.wireOp",EDGE,"E7.11.1"),sQuery(id+"F0.wireOp",EDGE,"E7.11.2"),sQuery(id+"F0.wireOp",EDGE,"E7.11.3"),sQuery(id+"F0.wireOp",EDGE,"E7.11.4"),sQuery(id+"F0.wireOp",EDGE,"E7.11.5"),sQuery(id+"F0.wireOp",EDGE,"E7.12.0"),sQuery(id+"F0.wireOp",EDGE,"E7.12.1"),sQuery(id+"F0.wireOp",EDGE,"E7.12.2"),sQuery(id+"F0.wireOp",EDGE,"E7.12.3"),sQuery(id+"F0.wireOp",EDGE,"E7.12.4"),sQuery(id+"F0.wireOp",EDGE,"E7.12.5"),sQuery(id+"F0.wireOp",EDGE,"E7.13.0"),sQuery(id+"F0.wireOp",EDGE,"E7.13.1"),sQuery(id+"F0.wireOp",EDGE,"E7.13.2"),sQuery(id+"F0.wireOp",EDGE,"E7.13.3"),sQuery(id+"F0.wireOp",EDGE,"E7.13.4"),sQuery(id+"F0.wireOp",EDGE,"E7.13.5"),sQuery(id+"F0.wireOp",EDGE,"E7.14.0"),sQuery(id+"F0.wireOp",EDGE,"E7.14.1"),sQuery(id+"F0.wireOp",EDGE,"E7.14.2"),sQuery(id+"F0.wireOp",EDGE,"E7.14.3"),sQuery(id+"F0.wireOp",EDGE,"E7.14.4"),sQuery(id+"F0.wireOp",EDGE,"E7.14.5"),sQuery(id+"F0.wireOp",EDGE,"E7.15.0"),sQuery(id+"F0.wireOp",EDGE,"E7.15.1"),sQuery(id+"F0.wireOp",EDGE,"E7.15.2"),sQuery(id+"F0.wireOp",EDGE,"E7.15.3"),sQuery(id+"F0.wireOp",EDGE,"E7.15.4"),sQuery(id+"F0.wireOp",EDGE,"E7.15.5"),sQuery(id+"F0.wireOp",EDGE,"E7.16.0"),sQuery(id+"F0.wireOp",EDGE,"E7.16.1"),sQuery(id+"F0.wireOp",EDGE,"E7.16.2"),sQuery(id+"F0.wireOp",EDGE,"E7.16.3"),sQuery(id+"F0.wireOp",EDGE,"E7.16.4"),sQuery(id+"F0.wireOp",EDGE,"E7.16.5"),sQuery(id+"F0.wireOp",EDGE,"E7.17.0"),sQuery(id+"F0.wireOp",EDGE,"E7.17.1"),sQuery(id+"F0.wireOp",EDGE,"E7.17.2"),sQuery(id+"F0.wireOp",EDGE,"E7.17.3"),sQuery(id+"F0.wireOp",EDGE,"E7.17.4"),sQuery(id+"F0.wireOp",EDGE,"E7.17.5"),sQuery(id+"F0.wireOp",EDGE,"E7.18.0"),sQuery(id+"F0.wireOp",EDGE,"E7.18.1"),sQuery(id+"F0.wireOp",EDGE,"E7.18.2"),sQuery(id+"F0.wireOp",EDGE,"E7.18.3"),sQuery(id+"F0.wireOp",EDGE,"E7.18.4"),sQuery(id+"F0.wireOp",EDGE,"E7.18.5"),sQuery(id+"F0.wireOp",EDGE,"E7.19.0"),sQuery(id+"F0.wireOp",EDGE,"E7.19.1"),sQuery(id+"F0.wireOp",EDGE,"E7.19.2"),sQuery(id+"F0.wireOp",EDGE,"E7.19.3"),sQuery(id+"F0.wireOp",EDGE,"E7.19.4"),sQuery(id+"F0.wireOp",EDGE,"E7.19.5"),sQuery(id+"F0.wireOp",EDGE,"E7.20.0"),sQuery(id+"F0.wireOp",EDGE,"E7.20.1"),sQuery(id+"F0.wireOp",EDGE,"E7.20.2"),sQuery(id+"F0.wireOp",EDGE,"E7.20.3"),sQuery(id+"F0.wireOp",EDGE,"E7.20.4"),sQuery(id+"F0.wireOp",EDGE,"E7.20.5"),sQuery(id+"F0.wireOp",EDGE,"E7.21.0"),sQuery(id+"F0.wireOp",EDGE,"E7.21.1"),sQuery(id+"F0.wireOp",EDGE,"E7.21.2"),sQuery(id+"F0.wireOp",EDGE,"E7.21.3"),sQuery(id+"F0.wireOp",EDGE,"E7.21.4"),sQuery(id+"F0.wireOp",EDGE,"E7.21.5"),sQuery(id+"F0.wireOp",EDGE,"E7.22.0"),sQuery(id+"F0.wireOp",EDGE,"E7.22.1"),sQuery(id+"F0.wireOp",EDGE,"E7.22.2"),sQuery(id+"F0.wireOp",EDGE,"E7.22.3"),sQuery(id+"F0.wireOp",EDGE,"E7.22.4"),sQuery(id+"F0.wireOp",EDGE,"E7.22.5"),sQuery(id+"F0.wireOp",EDGE,"E7.23.0"),sQuery(id+"F0.wireOp",EDGE,"E7.23.1"),sQuery(id+"F0.wireOp",EDGE,"E7.23.2"),sQuery(id+"F0.wireOp",EDGE,"E7.23.3"),sQuery(id+"F0.wireOp",EDGE,"E7.23.4"),sQuery(id+"F0.wireOp",EDGE,"E7.23.5"),sQuery(id+"F0.wireOp",EDGE,"E7.24.0"),sQuery(id+"F0.wireOp",EDGE,"E7.24.1"),sQuery(id+"F0.wireOp",EDGE,"E7.24.2"),sQuery(id+"F0.wireOp",EDGE,"E7.24.3"),sQuery(id+"F0.wireOp",EDGE,"E7.24.4"),sQuery(id+"F0.wireOp",EDGE,"E7.24.5"),subQ0,sQuery(id+"F0.wireOp",EDGE,"E7.25.1"),sQuery(id+"F0.wireOp",EDGE,"E7.25.2"),sQuery(id+"F0.wireOp",EDGE,"E7.25.3"),sQuery(id+"F0.wireOp",EDGE,"E7.25.4"),sQuery(id+"F0.wireOp",EDGE,"E7.25.5"),sQuery(id+"F0.wireOp",EDGE,"E7.26.0"),sQuery(id+"F0.wireOp",EDGE,"E7.26.1"),sQuery(id+"F0.wireOp",EDGE,"E7.26.2"),sQuery(id+"F0.wireOp",EDGE,"E7.26.3"),sQuery(id+"F0.wireOp",EDGE,"E7.26.4"),sQuery(id+"F0.wireOp",EDGE,"E7.26.5"),sQuery(id+"F0.wireOp",EDGE,"E7.27.0"),sQuery(id+"F0.wireOp",EDGE,"E7.27.1"),sQuery(id+"F0.wireOp",EDGE,"E7.27.2"),sQuery(id+"F0.wireOp",EDGE,"E7.27.3"),sQuery(id+"F0.wireOp",EDGE,"E7.27.4"),sQuery(id+"F0.wireOp",EDGE,"E7.27.5"),sQuery(id+"F0.wireOp",EDGE,"E7.28.0"),sQuery(id+"F0.wireOp",EDGE,"E7.28.1"),sQuery(id+"F0.wireOp",EDGE,"E7.28.2"),sQuery(id+"F0.wireOp",EDGE,"E7.28.3"),sQuery(id+"F0.wireOp",EDGE,"E7.28.4"),sQuery(id+"F0.wireOp",EDGE,"E7.28.5"),sQuery(id+"F0.wireOp",EDGE,"E7.29.0"),sQuery(id+"F0.wireOp",EDGE,"E7.29.1"),sQuery(id+"F0.wireOp",EDGE,"E7.29.2"),sQuery(id+"F0.wireOp",EDGE,"E7.29.3"),sQuery(id+"F0.wireOp",EDGE,"E7.29.4"),sQuery(id+"F0.wireOp",EDGE,"E7.29.5"),sQuery(id+"F0.wireOp",EDGE,"E7.30.0"),sQuery(id+"F0.wireOp",EDGE,"E7.30.1"),sQuery(id+"F0.wireOp",EDGE,"E7.30.2"),sQuery(id+"F0.wireOp",EDGE,"E7.30.3"),sQuery(id+"F0.wireOp",EDGE,"E7.30.4"),sQuery(id+"F0.wireOp",EDGE,"E7.30.5"),sQuery(id+"F0.wireOp",EDGE,"E7.31.0"),sQuery(id+"F0.wireOp",EDGE,"E7.31.1"),sQuery(id+"F0.wireOp",EDGE,"E7.31.2"),sQuery(id+"F0.wireOp",EDGE,"E7.31.3"),sQuery(id+"F0.wireOp",EDGE,"E7.31.4"),sQuery(id+"F0.wireOp",EDGE,"E7.31.5"),sQuery(id+"F0.wireOp",EDGE,"E7.32.0"),sQuery(id+"F0.wireOp",EDGE,"E7.32.1"),sQuery(id+"F0.wireOp",EDGE,"E7.32.2"),sQuery(id+"F0.wireOp",EDGE,"E7.32.3"),sQuery(id+"F0.wireOp",EDGE,"E7.32.4"),sQuery(id+"F0.wireOp",EDGE,"E7.32.5"),sQuery(id+"F0.wireOp",EDGE,"E7.33.0"),sQuery(id+"F0.wireOp",EDGE,"E7.33.1"),sQuery(id+"F0.wireOp",EDGE,"E7.33.2"),sQuery(id+"F0.wireOp",EDGE,"E7.33.3"),sQuery(id+"F0.wireOp",EDGE,"E7.33.4"),sQuery(id+"F0.wireOp",EDGE,"E7.33.5"),sQuery(id+"F0.wireOp",EDGE,"E7.34.0"),sQuery(id+"F0.wireOp",EDGE,"E7.34.1"),sQuery(id+"F0.wireOp",EDGE,"E7.34.2"),sQuery(id+"F0.wireOp",EDGE,"E7.34.3"),sQuery(id+"F0.wireOp",EDGE,"E7.34.4"),sQuery(id+"F0.wireOp",EDGE,"E7.34.5"),sQuery(id+"F0.wireOp",EDGE,"E7.35.0"),sQuery(id+"F0.wireOp",EDGE,"E7.35.1"),sQuery(id+"F0.wireOp",EDGE,"E7.35.2"),sQuery(id+"F0.wireOp",EDGE,"E7.35.3"),sQuery(id+"F0.wireOp",EDGE,"E7.35.4"),sQuery(id+"F0.wireOp",EDGE,"E7.35.5"),sQuery(id+"F0.wireOp",EDGE,"E7.36.0"),sQuery(id+"F0.wireOp",EDGE,"E7.36.1"),sQuery(id+"F0.wireOp",EDGE,"E7.36.2"),sQuery(id+"F0.wireOp",EDGE,"E7.36.3"),sQuery(id+"F0.wireOp",EDGE,"E7.36.4"),sQuery(id+"F0.wireOp",EDGE,"E7.36.5"),sQuery(id+"F0.wireOp",EDGE,"E7.37.0"),sQuery(id+"F0.wireOp",EDGE,"E7.37.1"),sQuery(id+"F0.wireOp",EDGE,"E7.37.2"),sQuery(id+"F0.wireOp",EDGE,"E7.37.3"),sQuery(id+"F0.wireOp",EDGE,"E7.37.4"),sQuery(id+"F0.wireOp",EDGE,"E7.37.5"),sQuery(id+"F0.wireOp",EDGE,"E7.38.0"),sQuery(id+"F0.wireOp",EDGE,"E7.38.1"),sQuery(id+"F0.wireOp",EDGE,"E7.38.2"),sQuery(id+"F0.wireOp",EDGE,"E7.38.3"),sQuery(id+"F0.wireOp",EDGE,"E7.38.4"),sQuery(id+"F0.wireOp",EDGE,"E7.38.5"),sQuery(id+"F0.wireOp",EDGE,"E7.39.0"),sQuery(id+"F0.wireOp",EDGE,"E7.39.1"),sQuery(id+"F0.wireOp",EDGE,"E7.39.2"),sQuery(id+"F0.wireOp",EDGE,"E7.39.3"),sQuery(id+"F0.wireOp",EDGE,"E7.39.4"),sQuery(id+"F0.wireOp",EDGE,"E7.39.5"),sQuery(id+"F0.wireOp",EDGE,"E7.40.0"),sQuery(id+"F0.wireOp",EDGE,"E7.40.1"),sQuery(id+"F0.wireOp",EDGE,"E7.40.2"),sQuery(id+"F0.wireOp",EDGE,"E7.40.3"),sQuery(id+"F0.wireOp",EDGE,"E7.40.4"),sQuery(id+"F0.wireOp",EDGE,"E7.40.5"),sQuery(id+"F0.wireOp",EDGE,"E7.41.0"),sQuery(id+"F0.wireOp",EDGE,"E7.41.1"),sQuery(id+"F0.wireOp",EDGE,"E7.41.2"),sQuery(id+"F0.wireOp",EDGE,"E7.41.3"),sQuery(id+"F0.wireOp",EDGE,"E7.41.4"),sQuery(id+"F0.wireOp",EDGE,"E7.41.5"),sQuery(id+"F0.wireOp",EDGE,"E7.42.0"),sQuery(id+"F0.wireOp",EDGE,"E7.42.1"),sQuery(id+"F0.wireOp",EDGE,"E7.42.2"),sQuery(id+"F0.wireOp",EDGE,"E7.42.3"),sQuery(id+"F0.wireOp",EDGE,"E7.42.4"),sQuery(id+"F0.wireOp",EDGE,"E7.42.5"),sQuery(id+"F0.wireOp",EDGE,"E7.43.0"),sQuery(id+"F0.wireOp",EDGE,"E7.43.1"),sQuery(id+"F0.wireOp",EDGE,"E7.43.2"),sQuery(id+"F0.wireOp",EDGE,"E7.43.3"),sQuery(id+"F0.wireOp",EDGE,"E7.43.4"),sQuery(id+"F0.wireOp",EDGE,"E7.43.5")])],"isStart":false})]}),makeQuery(id+"F2.opChamfer","BLEND_FACE",FACE,{"disambiguationData":[OSD([subQ0])]})],"blendedInto":[makeQuery(id+"F2.opChamfer","BLEND_FACE",FACE,{"disambiguationData":[OSD([subQ0])]})]});}
            var Q11;
            {var subQ0=sQuery(id+"F0.wireOp",EDGE,"E7.23.0");Q11=makeQuery(id+"F8.opChamfer","BLEND_EDGE",EDGE,{"blendedFrom":[makeQuery(id+"F2.opChamfer","BLEND_EDGE",EDGE,{"blendedFrom":[makeQuery(id+"F1.opExtrude","CAP_EDGE",EDGE,{"disambiguationData":[OSD([subQ0])],"isStart":false}),makeQuery(id+"F1.opExtrude","CAP_FACE",FACE,{"disambiguationData":[OSD([sQuery(id+"F0.wireOp",EDGE,"E1"),sQuery(id+"F0.wireOp",EDGE,"E2"),sQuery(id+"F0.wireOp",EDGE,"E3"),sQuery(id+"F0.wireOp",EDGE,"E4"),sQuery(id+"F0.wireOp",EDGE,"E5"),sQuery(id+"F0.wireOp",EDGE,"E6"),sQuery(id+"F0.wireOp",EDGE,"E7.1.0"),sQuery(id+"F0.wireOp",EDGE,"E7.1.1"),sQuery(id+"F0.wireOp",EDGE,"E7.1.2"),sQuery(id+"F0.wireOp",EDGE,"E7.1.3"),sQuery(id+"F0.wireOp",EDGE,"E7.1.4"),sQuery(id+"F0.wireOp",EDGE,"E7.1.5"),sQuery(id+"F0.wireOp",EDGE,"E7.2.0"),sQuery(id+"F0.wireOp",EDGE,"E7.2.1"),sQuery(id+"F0.wireOp",EDGE,"E7.2.2"),sQuery(id+"F0.wireOp",EDGE,"E7.2.3"),sQuery(id+"F0.wireOp",EDGE,"E7.2.4"),sQuery(id+"F0.wireOp",EDGE,"E7.2.5"),sQuery(id+"F0.wireOp",EDGE,"E7.3.0"),sQuery(id+"F0.wireOp",EDGE,"E7.3.1"),sQuery(id+"F0.wireOp",EDGE,"E7.3.2"),sQuery(id+"F0.wireOp",EDGE,"E7.3.3"),sQuery(id+"F0.wireOp",EDGE,"E7.3.4"),sQuery(id+"F0.wireOp",EDGE,"E7.3.5"),sQuery(id+"F0.wireOp",EDGE,"E7.4.0"),sQuery(id+"F0.wireOp",EDGE,"E7.4.1"),sQuery(id+"F0.wireOp",EDGE,"E7.4.2"),sQuery(id+"F0.wireOp",EDGE,"E7.4.3"),sQuery(id+"F0.wireOp",EDGE,"E7.4.4"),sQuery(id+"F0.wireOp",EDGE,"E7.4.5"),sQuery(id+"F0.wireOp",EDGE,"E7.5.0"),sQuery(id+"F0.wireOp",EDGE,"E7.5.1"),sQuery(id+"F0.wireOp",EDGE,"E7.5.2"),sQuery(id+"F0.wireOp",EDGE,"E7.5.3"),sQuery(id+"F0.wireOp",EDGE,"E7.5.4"),sQuery(id+"F0.wireOp",EDGE,"E7.5.5"),sQuery(id+"F0.wireOp",EDGE,"E7.6.0"),sQuery(id+"F0.wireOp",EDGE,"E7.6.1"),sQuery(id+"F0.wireOp",EDGE,"E7.6.2"),sQuery(id+"F0.wireOp",EDGE,"E7.6.3"),sQuery(id+"F0.wireOp",EDGE,"E7.6.4"),sQuery(id+"F0.wireOp",EDGE,"E7.6.5"),sQuery(id+"F0.wireOp",EDGE,"E7.7.0"),sQuery(id+"F0.wireOp",EDGE,"E7.7.1"),sQuery(id+"F0.wireOp",EDGE,"E7.7.2"),sQuery(id+"F0.wireOp",EDGE,"E7.7.3"),sQuery(id+"F0.wireOp",EDGE,"E7.7.4"),sQuery(id+"F0.wireOp",EDGE,"E7.7.5"),sQuery(id+"F0.wireOp",EDGE,"E7.8.0"),sQuery(id+"F0.wireOp",EDGE,"E7.8.1"),sQuery(id+"F0.wireOp",EDGE,"E7.8.2"),sQuery(id+"F0.wireOp",EDGE,"E7.8.3"),sQuery(id+"F0.wireOp",EDGE,"E7.8.4"),sQuery(id+"F0.wireOp",EDGE,"E7.8.5"),sQuery(id+"F0.wireOp",EDGE,"E7.9.0"),sQuery(id+"F0.wireOp",EDGE,"E7.9.1"),sQuery(id+"F0.wireOp",EDGE,"E7.9.2"),sQuery(id+"F0.wireOp",EDGE,"E7.9.3"),sQuery(id+"F0.wireOp",EDGE,"E7.9.4"),sQuery(id+"F0.wireOp",EDGE,"E7.9.5"),sQuery(id+"F0.wireOp",EDGE,"E7.10.0"),sQuery(id+"F0.wireOp",EDGE,"E7.10.1"),sQuery(id+"F0.wireOp",EDGE,"E7.10.2"),sQuery(id+"F0.wireOp",EDGE,"E7.10.3"),sQuery(id+"F0.wireOp",EDGE,"E7.10.4"),sQuery(id+"F0.wireOp",EDGE,"E7.10.5"),sQuery(id+"F0.wireOp",EDGE,"E7.11.0"),sQuery(id+"F0.wireOp",EDGE,"E7.11.1"),sQuery(id+"F0.wireOp",EDGE,"E7.11.2"),sQuery(id+"F0.wireOp",EDGE,"E7.11.3"),sQuery(id+"F0.wireOp",EDGE,"E7.11.4"),sQuery(id+"F0.wireOp",EDGE,"E7.11.5"),sQuery(id+"F0.wireOp",EDGE,"E7.12.0"),sQuery(id+"F0.wireOp",EDGE,"E7.12.1"),sQuery(id+"F0.wireOp",EDGE,"E7.12.2"),sQuery(id+"F0.wireOp",EDGE,"E7.12.3"),sQuery(id+"F0.wireOp",EDGE,"E7.12.4"),sQuery(id+"F0.wireOp",EDGE,"E7.12.5"),sQuery(id+"F0.wireOp",EDGE,"E7.13.0"),sQuery(id+"F0.wireOp",EDGE,"E7.13.1"),sQuery(id+"F0.wireOp",EDGE,"E7.13.2"),sQuery(id+"F0.wireOp",EDGE,"E7.13.3"),sQuery(id+"F0.wireOp",EDGE,"E7.13.4"),sQuery(id+"F0.wireOp",EDGE,"E7.13.5"),sQuery(id+"F0.wireOp",EDGE,"E7.14.0"),sQuery(id+"F0.wireOp",EDGE,"E7.14.1"),sQuery(id+"F0.wireOp",EDGE,"E7.14.2"),sQuery(id+"F0.wireOp",EDGE,"E7.14.3"),sQuery(id+"F0.wireOp",EDGE,"E7.14.4"),sQuery(id+"F0.wireOp",EDGE,"E7.14.5"),sQuery(id+"F0.wireOp",EDGE,"E7.15.0"),sQuery(id+"F0.wireOp",EDGE,"E7.15.1"),sQuery(id+"F0.wireOp",EDGE,"E7.15.2"),sQuery(id+"F0.wireOp",EDGE,"E7.15.3"),sQuery(id+"F0.wireOp",EDGE,"E7.15.4"),sQuery(id+"F0.wireOp",EDGE,"E7.15.5"),sQuery(id+"F0.wireOp",EDGE,"E7.16.0"),sQuery(id+"F0.wireOp",EDGE,"E7.16.1"),sQuery(id+"F0.wireOp",EDGE,"E7.16.2"),sQuery(id+"F0.wireOp",EDGE,"E7.16.3"),sQuery(id+"F0.wireOp",EDGE,"E7.16.4"),sQuery(id+"F0.wireOp",EDGE,"E7.16.5"),sQuery(id+"F0.wireOp",EDGE,"E7.17.0"),sQuery(id+"F0.wireOp",EDGE,"E7.17.1"),sQuery(id+"F0.wireOp",EDGE,"E7.17.2"),sQuery(id+"F0.wireOp",EDGE,"E7.17.3"),sQuery(id+"F0.wireOp",EDGE,"E7.17.4"),sQuery(id+"F0.wireOp",EDGE,"E7.17.5"),sQuery(id+"F0.wireOp",EDGE,"E7.18.0"),sQuery(id+"F0.wireOp",EDGE,"E7.18.1"),sQuery(id+"F0.wireOp",EDGE,"E7.18.2"),sQuery(id+"F0.wireOp",EDGE,"E7.18.3"),sQuery(id+"F0.wireOp",EDGE,"E7.18.4"),sQuery(id+"F0.wireOp",EDGE,"E7.18.5"),sQuery(id+"F0.wireOp",EDGE,"E7.19.0"),sQuery(id+"F0.wireOp",EDGE,"E7.19.1"),sQuery(id+"F0.wireOp",EDGE,"E7.19.2"),sQuery(id+"F0.wireOp",EDGE,"E7.19.3"),sQuery(id+"F0.wireOp",EDGE,"E7.19.4"),sQuery(id+"F0.wireOp",EDGE,"E7.19.5"),sQuery(id+"F0.wireOp",EDGE,"E7.20.0"),sQuery(id+"F0.wireOp",EDGE,"E7.20.1"),sQuery(id+"F0.wireOp",EDGE,"E7.20.2"),sQuery(id+"F0.wireOp",EDGE,"E7.20.3"),sQuery(id+"F0.wireOp",EDGE,"E7.20.4"),sQuery(id+"F0.wireOp",EDGE,"E7.20.5"),sQuery(id+"F0.wireOp",EDGE,"E7.21.0"),sQuery(id+"F0.wireOp",EDGE,"E7.21.1"),sQuery(id+"F0.wireOp",EDGE,"E7.21.2"),sQuery(id+"F0.wireOp",EDGE,"E7.21.3"),sQuery(id+"F0.wireOp",EDGE,"E7.21.4"),sQuery(id+"F0.wireOp",EDGE,"E7.21.5"),sQuery(id+"F0.wireOp",EDGE,"E7.22.0"),sQuery(id+"F0.wireOp",EDGE,"E7.22.1"),sQuery(id+"F0.wireOp",EDGE,"E7.22.2"),sQuery(id+"F0.wireOp",EDGE,"E7.22.3"),sQuery(id+"F0.wireOp",EDGE,"E7.22.4"),sQuery(id+"F0.wireOp",EDGE,"E7.22.5"),subQ0,sQuery(id+"F0.wireOp",EDGE,"E7.23.1"),sQuery(id+"F0.wireOp",EDGE,"E7.23.2"),sQuery(id+"F0.wireOp",EDGE,"E7.23.3"),sQuery(id+"F0.wireOp",EDGE,"E7.23.4"),sQuery(id+"F0.wireOp",EDGE,"E7.23.5"),sQuery(id+"F0.wireOp",EDGE,"E7.24.0"),sQuery(id+"F0.wireOp",EDGE,"E7.24.1"),sQuery(id+"F0.wireOp",EDGE,"E7.24.2"),sQuery(id+"F0.wireOp",EDGE,"E7.24.3"),sQuery(id+"F0.wireOp",EDGE,"E7.24.4"),sQuery(id+"F0.wireOp",EDGE,"E7.24.5"),sQuery(id+"F0.wireOp",EDGE,"E7.25.0"),sQuery(id+"F0.wireOp",EDGE,"E7.25.1"),sQuery(id+"F0.wireOp",EDGE,"E7.25.2"),sQuery(id+"F0.wireOp",EDGE,"E7.25.3"),sQuery(id+"F0.wireOp",EDGE,"E7.25.4"),sQuery(id+"F0.wireOp",EDGE,"E7.25.5"),sQuery(id+"F0.wireOp",EDGE,"E7.26.0"),sQuery(id+"F0.wireOp",EDGE,"E7.26.1"),sQuery(id+"F0.wireOp",EDGE,"E7.26.2"),sQuery(id+"F0.wireOp",EDGE,"E7.26.3"),sQuery(id+"F0.wireOp",EDGE,"E7.26.4"),sQuery(id+"F0.wireOp",EDGE,"E7.26.5"),sQuery(id+"F0.wireOp",EDGE,"E7.27.0"),sQuery(id+"F0.wireOp",EDGE,"E7.27.1"),sQuery(id+"F0.wireOp",EDGE,"E7.27.2"),sQuery(id+"F0.wireOp",EDGE,"E7.27.3"),sQuery(id+"F0.wireOp",EDGE,"E7.27.4"),sQuery(id+"F0.wireOp",EDGE,"E7.27.5"),sQuery(id+"F0.wireOp",EDGE,"E7.28.0"),sQuery(id+"F0.wireOp",EDGE,"E7.28.1"),sQuery(id+"F0.wireOp",EDGE,"E7.28.2"),sQuery(id+"F0.wireOp",EDGE,"E7.28.3"),sQuery(id+"F0.wireOp",EDGE,"E7.28.4"),sQuery(id+"F0.wireOp",EDGE,"E7.28.5"),sQuery(id+"F0.wireOp",EDGE,"E7.29.0"),sQuery(id+"F0.wireOp",EDGE,"E7.29.1"),sQuery(id+"F0.wireOp",EDGE,"E7.29.2"),sQuery(id+"F0.wireOp",EDGE,"E7.29.3"),sQuery(id+"F0.wireOp",EDGE,"E7.29.4"),sQuery(id+"F0.wireOp",EDGE,"E7.29.5"),sQuery(id+"F0.wireOp",EDGE,"E7.30.0"),sQuery(id+"F0.wireOp",EDGE,"E7.30.1"),sQuery(id+"F0.wireOp",EDGE,"E7.30.2"),sQuery(id+"F0.wireOp",EDGE,"E7.30.3"),sQuery(id+"F0.wireOp",EDGE,"E7.30.4"),sQuery(id+"F0.wireOp",EDGE,"E7.30.5"),sQuery(id+"F0.wireOp",EDGE,"E7.31.0"),sQuery(id+"F0.wireOp",EDGE,"E7.31.1"),sQuery(id+"F0.wireOp",EDGE,"E7.31.2"),sQuery(id+"F0.wireOp",EDGE,"E7.31.3"),sQuery(id+"F0.wireOp",EDGE,"E7.31.4"),sQuery(id+"F0.wireOp",EDGE,"E7.31.5"),sQuery(id+"F0.wireOp",EDGE,"E7.32.0"),sQuery(id+"F0.wireOp",EDGE,"E7.32.1"),sQuery(id+"F0.wireOp",EDGE,"E7.32.2"),sQuery(id+"F0.wireOp",EDGE,"E7.32.3"),sQuery(id+"F0.wireOp",EDGE,"E7.32.4"),sQuery(id+"F0.wireOp",EDGE,"E7.32.5"),sQuery(id+"F0.wireOp",EDGE,"E7.33.0"),sQuery(id+"F0.wireOp",EDGE,"E7.33.1"),sQuery(id+"F0.wireOp",EDGE,"E7.33.2"),sQuery(id+"F0.wireOp",EDGE,"E7.33.3"),sQuery(id+"F0.wireOp",EDGE,"E7.33.4"),sQuery(id+"F0.wireOp",EDGE,"E7.33.5"),sQuery(id+"F0.wireOp",EDGE,"E7.34.0"),sQuery(id+"F0.wireOp",EDGE,"E7.34.1"),sQuery(id+"F0.wireOp",EDGE,"E7.34.2"),sQuery(id+"F0.wireOp",EDGE,"E7.34.3"),sQuery(id+"F0.wireOp",EDGE,"E7.34.4"),sQuery(id+"F0.wireOp",EDGE,"E7.34.5"),sQuery(id+"F0.wireOp",EDGE,"E7.35.0"),sQuery(id+"F0.wireOp",EDGE,"E7.35.1"),sQuery(id+"F0.wireOp",EDGE,"E7.35.2"),sQuery(id+"F0.wireOp",EDGE,"E7.35.3"),sQuery(id+"F0.wireOp",EDGE,"E7.35.4"),sQuery(id+"F0.wireOp",EDGE,"E7.35.5"),sQuery(id+"F0.wireOp",EDGE,"E7.36.0"),sQuery(id+"F0.wireOp",EDGE,"E7.36.1"),sQuery(id+"F0.wireOp",EDGE,"E7.36.2"),sQuery(id+"F0.wireOp",EDGE,"E7.36.3"),sQuery(id+"F0.wireOp",EDGE,"E7.36.4"),sQuery(id+"F0.wireOp",EDGE,"E7.36.5"),sQuery(id+"F0.wireOp",EDGE,"E7.37.0"),sQuery(id+"F0.wireOp",EDGE,"E7.37.1"),sQuery(id+"F0.wireOp",EDGE,"E7.37.2"),sQuery(id+"F0.wireOp",EDGE,"E7.37.3"),sQuery(id+"F0.wireOp",EDGE,"E7.37.4"),sQuery(id+"F0.wireOp",EDGE,"E7.37.5"),sQuery(id+"F0.wireOp",EDGE,"E7.38.0"),sQuery(id+"F0.wireOp",EDGE,"E7.38.1"),sQuery(id+"F0.wireOp",EDGE,"E7.38.2"),sQuery(id+"F0.wireOp",EDGE,"E7.38.3"),sQuery(id+"F0.wireOp",EDGE,"E7.38.4"),sQuery(id+"F0.wireOp",EDGE,"E7.38.5"),sQuery(id+"F0.wireOp",EDGE,"E7.39.0"),sQuery(id+"F0.wireOp",EDGE,"E7.39.1"),sQuery(id+"F0.wireOp",EDGE,"E7.39.2"),sQuery(id+"F0.wireOp",EDGE,"E7.39.3"),sQuery(id+"F0.wireOp",EDGE,"E7.39.4"),sQuery(id+"F0.wireOp",EDGE,"E7.39.5"),sQuery(id+"F0.wireOp",EDGE,"E7.40.0"),sQuery(id+"F0.wireOp",EDGE,"E7.40.1"),sQuery(id+"F0.wireOp",EDGE,"E7.40.2"),sQuery(id+"F0.wireOp",EDGE,"E7.40.3"),sQuery(id+"F0.wireOp",EDGE,"E7.40.4"),sQuery(id+"F0.wireOp",EDGE,"E7.40.5"),sQuery(id+"F0.wireOp",EDGE,"E7.41.0"),sQuery(id+"F0.wireOp",EDGE,"E7.41.1"),sQuery(id+"F0.wireOp",EDGE,"E7.41.2"),sQuery(id+"F0.wireOp",EDGE,"E7.41.3"),sQuery(id+"F0.wireOp",EDGE,"E7.41.4"),sQuery(id+"F0.wireOp",EDGE,"E7.41.5"),sQuery(id+"F0.wireOp",EDGE,"E7.42.0"),sQuery(id+"F0.wireOp",EDGE,"E7.42.1"),sQuery(id+"F0.wireOp",EDGE,"E7.42.2"),sQuery(id+"F0.wireOp",EDGE,"E7.42.3"),sQuery(id+"F0.wireOp",EDGE,"E7.42.4"),sQuery(id+"F0.wireOp",EDGE,"E7.42.5"),sQuery(id+"F0.wireOp",EDGE,"E7.43.0"),sQuery(id+"F0.wireOp",EDGE,"E7.43.1"),sQuery(id+"F0.wireOp",EDGE,"E7.43.2"),sQuery(id+"F0.wireOp",EDGE,"E7.43.3"),sQuery(id+"F0.wireOp",EDGE,"E7.43.4"),sQuery(id+"F0.wireOp",EDGE,"E7.43.5")])],"isStart":false})],"blendedInto":[makeQuery(id+"F1.opExtrude","CAP_FACE",FACE,{"disambiguationData":[OSD([sQuery(id+"F0.wireOp",EDGE,"E1"),sQuery(id+"F0.wireOp",EDGE,"E2"),sQuery(id+"F0.wireOp",EDGE,"E3"),sQuery(id+"F0.wireOp",EDGE,"E4"),sQuery(id+"F0.wireOp",EDGE,"E5"),sQuery(id+"F0.wireOp",EDGE,"E6"),sQuery(id+"F0.wireOp",EDGE,"E7.1.0"),sQuery(id+"F0.wireOp",EDGE,"E7.1.1"),sQuery(id+"F0.wireOp",EDGE,"E7.1.2"),sQuery(id+"F0.wireOp",EDGE,"E7.1.3"),sQuery(id+"F0.wireOp",EDGE,"E7.1.4"),sQuery(id+"F0.wireOp",EDGE,"E7.1.5"),sQuery(id+"F0.wireOp",EDGE,"E7.2.0"),sQuery(id+"F0.wireOp",EDGE,"E7.2.1"),sQuery(id+"F0.wireOp",EDGE,"E7.2.2"),sQuery(id+"F0.wireOp",EDGE,"E7.2.3"),sQuery(id+"F0.wireOp",EDGE,"E7.2.4"),sQuery(id+"F0.wireOp",EDGE,"E7.2.5"),sQuery(id+"F0.wireOp",EDGE,"E7.3.0"),sQuery(id+"F0.wireOp",EDGE,"E7.3.1"),sQuery(id+"F0.wireOp",EDGE,"E7.3.2"),sQuery(id+"F0.wireOp",EDGE,"E7.3.3"),sQuery(id+"F0.wireOp",EDGE,"E7.3.4"),sQuery(id+"F0.wireOp",EDGE,"E7.3.5"),sQuery(id+"F0.wireOp",EDGE,"E7.4.0"),sQuery(id+"F0.wireOp",EDGE,"E7.4.1"),sQuery(id+"F0.wireOp",EDGE,"E7.4.2"),sQuery(id+"F0.wireOp",EDGE,"E7.4.3"),sQuery(id+"F0.wireOp",EDGE,"E7.4.4"),sQuery(id+"F0.wireOp",EDGE,"E7.4.5"),sQuery(id+"F0.wireOp",EDGE,"E7.5.0"),sQuery(id+"F0.wireOp",EDGE,"E7.5.1"),sQuery(id+"F0.wireOp",EDGE,"E7.5.2"),sQuery(id+"F0.wireOp",EDGE,"E7.5.3"),sQuery(id+"F0.wireOp",EDGE,"E7.5.4"),sQuery(id+"F0.wireOp",EDGE,"E7.5.5"),sQuery(id+"F0.wireOp",EDGE,"E7.6.0"),sQuery(id+"F0.wireOp",EDGE,"E7.6.1"),sQuery(id+"F0.wireOp",EDGE,"E7.6.2"),sQuery(id+"F0.wireOp",EDGE,"E7.6.3"),sQuery(id+"F0.wireOp",EDGE,"E7.6.4"),sQuery(id+"F0.wireOp",EDGE,"E7.6.5"),sQuery(id+"F0.wireOp",EDGE,"E7.7.0"),sQuery(id+"F0.wireOp",EDGE,"E7.7.1"),sQuery(id+"F0.wireOp",EDGE,"E7.7.2"),sQuery(id+"F0.wireOp",EDGE,"E7.7.3"),sQuery(id+"F0.wireOp",EDGE,"E7.7.4"),sQuery(id+"F0.wireOp",EDGE,"E7.7.5"),sQuery(id+"F0.wireOp",EDGE,"E7.8.0"),sQuery(id+"F0.wireOp",EDGE,"E7.8.1"),sQuery(id+"F0.wireOp",EDGE,"E7.8.2"),sQuery(id+"F0.wireOp",EDGE,"E7.8.3"),sQuery(id+"F0.wireOp",EDGE,"E7.8.4"),sQuery(id+"F0.wireOp",EDGE,"E7.8.5"),sQuery(id+"F0.wireOp",EDGE,"E7.9.0"),sQuery(id+"F0.wireOp",EDGE,"E7.9.1"),sQuery(id+"F0.wireOp",EDGE,"E7.9.2"),sQuery(id+"F0.wireOp",EDGE,"E7.9.3"),sQuery(id+"F0.wireOp",EDGE,"E7.9.4"),sQuery(id+"F0.wireOp",EDGE,"E7.9.5"),sQuery(id+"F0.wireOp",EDGE,"E7.10.0"),sQuery(id+"F0.wireOp",EDGE,"E7.10.1"),sQuery(id+"F0.wireOp",EDGE,"E7.10.2"),sQuery(id+"F0.wireOp",EDGE,"E7.10.3"),sQuery(id+"F0.wireOp",EDGE,"E7.10.4"),sQuery(id+"F0.wireOp",EDGE,"E7.10.5"),sQuery(id+"F0.wireOp",EDGE,"E7.11.0"),sQuery(id+"F0.wireOp",EDGE,"E7.11.1"),sQuery(id+"F0.wireOp",EDGE,"E7.11.2"),sQuery(id+"F0.wireOp",EDGE,"E7.11.3"),sQuery(id+"F0.wireOp",EDGE,"E7.11.4"),sQuery(id+"F0.wireOp",EDGE,"E7.11.5"),sQuery(id+"F0.wireOp",EDGE,"E7.12.0"),sQuery(id+"F0.wireOp",EDGE,"E7.12.1"),sQuery(id+"F0.wireOp",EDGE,"E7.12.2"),sQuery(id+"F0.wireOp",EDGE,"E7.12.3"),sQuery(id+"F0.wireOp",EDGE,"E7.12.4"),sQuery(id+"F0.wireOp",EDGE,"E7.12.5"),sQuery(id+"F0.wireOp",EDGE,"E7.13.0"),sQuery(id+"F0.wireOp",EDGE,"E7.13.1"),sQuery(id+"F0.wireOp",EDGE,"E7.13.2"),sQuery(id+"F0.wireOp",EDGE,"E7.13.3"),sQuery(id+"F0.wireOp",EDGE,"E7.13.4"),sQuery(id+"F0.wireOp",EDGE,"E7.13.5"),sQuery(id+"F0.wireOp",EDGE,"E7.14.0"),sQuery(id+"F0.wireOp",EDGE,"E7.14.1"),sQuery(id+"F0.wireOp",EDGE,"E7.14.2"),sQuery(id+"F0.wireOp",EDGE,"E7.14.3"),sQuery(id+"F0.wireOp",EDGE,"E7.14.4"),sQuery(id+"F0.wireOp",EDGE,"E7.14.5"),sQuery(id+"F0.wireOp",EDGE,"E7.15.0"),sQuery(id+"F0.wireOp",EDGE,"E7.15.1"),sQuery(id+"F0.wireOp",EDGE,"E7.15.2"),sQuery(id+"F0.wireOp",EDGE,"E7.15.3"),sQuery(id+"F0.wireOp",EDGE,"E7.15.4"),sQuery(id+"F0.wireOp",EDGE,"E7.15.5"),sQuery(id+"F0.wireOp",EDGE,"E7.16.0"),sQuery(id+"F0.wireOp",EDGE,"E7.16.1"),sQuery(id+"F0.wireOp",EDGE,"E7.16.2"),sQuery(id+"F0.wireOp",EDGE,"E7.16.3"),sQuery(id+"F0.wireOp",EDGE,"E7.16.4"),sQuery(id+"F0.wireOp",EDGE,"E7.16.5"),sQuery(id+"F0.wireOp",EDGE,"E7.17.0"),sQuery(id+"F0.wireOp",EDGE,"E7.17.1"),sQuery(id+"F0.wireOp",EDGE,"E7.17.2"),sQuery(id+"F0.wireOp",EDGE,"E7.17.3"),sQuery(id+"F0.wireOp",EDGE,"E7.17.4"),sQuery(id+"F0.wireOp",EDGE,"E7.17.5"),sQuery(id+"F0.wireOp",EDGE,"E7.18.0"),sQuery(id+"F0.wireOp",EDGE,"E7.18.1"),sQuery(id+"F0.wireOp",EDGE,"E7.18.2"),sQuery(id+"F0.wireOp",EDGE,"E7.18.3"),sQuery(id+"F0.wireOp",EDGE,"E7.18.4"),sQuery(id+"F0.wireOp",EDGE,"E7.18.5"),sQuery(id+"F0.wireOp",EDGE,"E7.19.0"),sQuery(id+"F0.wireOp",EDGE,"E7.19.1"),sQuery(id+"F0.wireOp",EDGE,"E7.19.2"),sQuery(id+"F0.wireOp",EDGE,"E7.19.3"),sQuery(id+"F0.wireOp",EDGE,"E7.19.4"),sQuery(id+"F0.wireOp",EDGE,"E7.19.5"),sQuery(id+"F0.wireOp",EDGE,"E7.20.0"),sQuery(id+"F0.wireOp",EDGE,"E7.20.1"),sQuery(id+"F0.wireOp",EDGE,"E7.20.2"),sQuery(id+"F0.wireOp",EDGE,"E7.20.3"),sQuery(id+"F0.wireOp",EDGE,"E7.20.4"),sQuery(id+"F0.wireOp",EDGE,"E7.20.5"),sQuery(id+"F0.wireOp",EDGE,"E7.21.0"),sQuery(id+"F0.wireOp",EDGE,"E7.21.1"),sQuery(id+"F0.wireOp",EDGE,"E7.21.2"),sQuery(id+"F0.wireOp",EDGE,"E7.21.3"),sQuery(id+"F0.wireOp",EDGE,"E7.21.4"),sQuery(id+"F0.wireOp",EDGE,"E7.21.5"),sQuery(id+"F0.wireOp",EDGE,"E7.22.0"),sQuery(id+"F0.wireOp",EDGE,"E7.22.1"),sQuery(id+"F0.wireOp",EDGE,"E7.22.2"),sQuery(id+"F0.wireOp",EDGE,"E7.22.3"),sQuery(id+"F0.wireOp",EDGE,"E7.22.4"),sQuery(id+"F0.wireOp",EDGE,"E7.22.5"),subQ0,sQuery(id+"F0.wireOp",EDGE,"E7.23.1"),sQuery(id+"F0.wireOp",EDGE,"E7.23.2"),sQuery(id+"F0.wireOp",EDGE,"E7.23.3"),sQuery(id+"F0.wireOp",EDGE,"E7.23.4"),sQuery(id+"F0.wireOp",EDGE,"E7.23.5"),sQuery(id+"F0.wireOp",EDGE,"E7.24.0"),sQuery(id+"F0.wireOp",EDGE,"E7.24.1"),sQuery(id+"F0.wireOp",EDGE,"E7.24.2"),sQuery(id+"F0.wireOp",EDGE,"E7.24.3"),sQuery(id+"F0.wireOp",EDGE,"E7.24.4"),sQuery(id+"F0.wireOp",EDGE,"E7.24.5"),sQuery(id+"F0.wireOp",EDGE,"E7.25.0"),sQuery(id+"F0.wireOp",EDGE,"E7.25.1"),sQuery(id+"F0.wireOp",EDGE,"E7.25.2"),sQuery(id+"F0.wireOp",EDGE,"E7.25.3"),sQuery(id+"F0.wireOp",EDGE,"E7.25.4"),sQuery(id+"F0.wireOp",EDGE,"E7.25.5"),sQuery(id+"F0.wireOp",EDGE,"E7.26.0"),sQuery(id+"F0.wireOp",EDGE,"E7.26.1"),sQuery(id+"F0.wireOp",EDGE,"E7.26.2"),sQuery(id+"F0.wireOp",EDGE,"E7.26.3"),sQuery(id+"F0.wireOp",EDGE,"E7.26.4"),sQuery(id+"F0.wireOp",EDGE,"E7.26.5"),sQuery(id+"F0.wireOp",EDGE,"E7.27.0"),sQuery(id+"F0.wireOp",EDGE,"E7.27.1"),sQuery(id+"F0.wireOp",EDGE,"E7.27.2"),sQuery(id+"F0.wireOp",EDGE,"E7.27.3"),sQuery(id+"F0.wireOp",EDGE,"E7.27.4"),sQuery(id+"F0.wireOp",EDGE,"E7.27.5"),sQuery(id+"F0.wireOp",EDGE,"E7.28.0"),sQuery(id+"F0.wireOp",EDGE,"E7.28.1"),sQuery(id+"F0.wireOp",EDGE,"E7.28.2"),sQuery(id+"F0.wireOp",EDGE,"E7.28.3"),sQuery(id+"F0.wireOp",EDGE,"E7.28.4"),sQuery(id+"F0.wireOp",EDGE,"E7.28.5"),sQuery(id+"F0.wireOp",EDGE,"E7.29.0"),sQuery(id+"F0.wireOp",EDGE,"E7.29.1"),sQuery(id+"F0.wireOp",EDGE,"E7.29.2"),sQuery(id+"F0.wireOp",EDGE,"E7.29.3"),sQuery(id+"F0.wireOp",EDGE,"E7.29.4"),sQuery(id+"F0.wireOp",EDGE,"E7.29.5"),sQuery(id+"F0.wireOp",EDGE,"E7.30.0"),sQuery(id+"F0.wireOp",EDGE,"E7.30.1"),sQuery(id+"F0.wireOp",EDGE,"E7.30.2"),sQuery(id+"F0.wireOp",EDGE,"E7.30.3"),sQuery(id+"F0.wireOp",EDGE,"E7.30.4"),sQuery(id+"F0.wireOp",EDGE,"E7.30.5"),sQuery(id+"F0.wireOp",EDGE,"E7.31.0"),sQuery(id+"F0.wireOp",EDGE,"E7.31.1"),sQuery(id+"F0.wireOp",EDGE,"E7.31.2"),sQuery(id+"F0.wireOp",EDGE,"E7.31.3"),sQuery(id+"F0.wireOp",EDGE,"E7.31.4"),sQuery(id+"F0.wireOp",EDGE,"E7.31.5"),sQuery(id+"F0.wireOp",EDGE,"E7.32.0"),sQuery(id+"F0.wireOp",EDGE,"E7.32.1"),sQuery(id+"F0.wireOp",EDGE,"E7.32.2"),sQuery(id+"F0.wireOp",EDGE,"E7.32.3"),sQuery(id+"F0.wireOp",EDGE,"E7.32.4"),sQuery(id+"F0.wireOp",EDGE,"E7.32.5"),sQuery(id+"F0.wireOp",EDGE,"E7.33.0"),sQuery(id+"F0.wireOp",EDGE,"E7.33.1"),sQuery(id+"F0.wireOp",EDGE,"E7.33.2"),sQuery(id+"F0.wireOp",EDGE,"E7.33.3"),sQuery(id+"F0.wireOp",EDGE,"E7.33.4"),sQuery(id+"F0.wireOp",EDGE,"E7.33.5"),sQuery(id+"F0.wireOp",EDGE,"E7.34.0"),sQuery(id+"F0.wireOp",EDGE,"E7.34.1"),sQuery(id+"F0.wireOp",EDGE,"E7.34.2"),sQuery(id+"F0.wireOp",EDGE,"E7.34.3"),sQuery(id+"F0.wireOp",EDGE,"E7.34.4"),sQuery(id+"F0.wireOp",EDGE,"E7.34.5"),sQuery(id+"F0.wireOp",EDGE,"E7.35.0"),sQuery(id+"F0.wireOp",EDGE,"E7.35.1"),sQuery(id+"F0.wireOp",EDGE,"E7.35.2"),sQuery(id+"F0.wireOp",EDGE,"E7.35.3"),sQuery(id+"F0.wireOp",EDGE,"E7.35.4"),sQuery(id+"F0.wireOp",EDGE,"E7.35.5"),sQuery(id+"F0.wireOp",EDGE,"E7.36.0"),sQuery(id+"F0.wireOp",EDGE,"E7.36.1"),sQuery(id+"F0.wireOp",EDGE,"E7.36.2"),sQuery(id+"F0.wireOp",EDGE,"E7.36.3"),sQuery(id+"F0.wireOp",EDGE,"E7.36.4"),sQuery(id+"F0.wireOp",EDGE,"E7.36.5"),sQuery(id+"F0.wireOp",EDGE,"E7.37.0"),sQuery(id+"F0.wireOp",EDGE,"E7.37.1"),sQuery(id+"F0.wireOp",EDGE,"E7.37.2"),sQuery(id+"F0.wireOp",EDGE,"E7.37.3"),sQuery(id+"F0.wireOp",EDGE,"E7.37.4"),sQuery(id+"F0.wireOp",EDGE,"E7.37.5"),sQuery(id+"F0.wireOp",EDGE,"E7.38.0"),sQuery(id+"F0.wireOp",EDGE,"E7.38.1"),sQuery(id+"F0.wireOp",EDGE,"E7.38.2"),sQuery(id+"F0.wireOp",EDGE,"E7.38.3"),sQuery(id+"F0.wireOp",EDGE,"E7.38.4"),sQuery(id+"F0.wireOp",EDGE,"E7.38.5"),sQuery(id+"F0.wireOp",EDGE,"E7.39.0"),sQuery(id+"F0.wireOp",EDGE,"E7.39.1"),sQuery(id+"F0.wireOp",EDGE,"E7.39.2"),sQuery(id+"F0.wireOp",EDGE,"E7.39.3"),sQuery(id+"F0.wireOp",EDGE,"E7.39.4"),sQuery(id+"F0.wireOp",EDGE,"E7.39.5"),sQuery(id+"F0.wireOp",EDGE,"E7.40.0"),sQuery(id+"F0.wireOp",EDGE,"E7.40.1"),sQuery(id+"F0.wireOp",EDGE,"E7.40.2"),sQuery(id+"F0.wireOp",EDGE,"E7.40.3"),sQuery(id+"F0.wireOp",EDGE,"E7.40.4"),sQuery(id+"F0.wireOp",EDGE,"E7.40.5"),sQuery(id+"F0.wireOp",EDGE,"E7.41.0"),sQuery(id+"F0.wireOp",EDGE,"E7.41.1"),sQuery(id+"F0.wireOp",EDGE,"E7.41.2"),sQuery(id+"F0.wireOp",EDGE,"E7.41.3"),sQuery(id+"F0.wireOp",EDGE,"E7.41.4"),sQuery(id+"F0.wireOp",EDGE,"E7.41.5"),sQuery(id+"F0.wireOp",EDGE,"E7.42.0"),sQuery(id+"F0.wireOp",EDGE,"E7.42.1"),sQuery(id+"F0.wireOp",EDGE,"E7.42.2"),sQuery(id+"F0.wireOp",EDGE,"E7.42.3"),sQuery(id+"F0.wireOp",EDGE,"E7.42.4"),sQuery(id+"F0.wireOp",EDGE,"E7.42.5"),sQuery(id+"F0.wireOp",EDGE,"E7.43.0"),sQuery(id+"F0.wireOp",EDGE,"E7.43.1"),sQuery(id+"F0.wireOp",EDGE,"E7.43.2"),sQuery(id+"F0.wireOp",EDGE,"E7.43.3"),sQuery(id+"F0.wireOp",EDGE,"E7.43.4"),sQuery(id+"F0.wireOp",EDGE,"E7.43.5")])],"isStart":false})]}),makeQuery(id+"F2.opChamfer","BLEND_FACE",FACE,{"disambiguationData":[OSD([subQ0])]})],"blendedInto":[makeQuery(id+"F2.opChamfer","BLEND_FACE",FACE,{"disambiguationData":[OSD([subQ0])]})]});}
            var Q12;
            {var subQ0=sQuery(id+"F0.wireOp",EDGE,"E7.21.0");Q12=makeQuery(id+"F8.opChamfer","BLEND_EDGE",EDGE,{"blendedFrom":[makeQuery(id+"F2.opChamfer","BLEND_EDGE",EDGE,{"blendedFrom":[makeQuery(id+"F1.opExtrude","CAP_EDGE",EDGE,{"disambiguationData":[OSD([subQ0])],"isStart":false}),makeQuery(id+"F1.opExtrude","CAP_FACE",FACE,{"disambiguationData":[OSD([sQuery(id+"F0.wireOp",EDGE,"E1"),sQuery(id+"F0.wireOp",EDGE,"E2"),sQuery(id+"F0.wireOp",EDGE,"E3"),sQuery(id+"F0.wireOp",EDGE,"E4"),sQuery(id+"F0.wireOp",EDGE,"E5"),sQuery(id+"F0.wireOp",EDGE,"E6"),sQuery(id+"F0.wireOp",EDGE,"E7.1.0"),sQuery(id+"F0.wireOp",EDGE,"E7.1.1"),sQuery(id+"F0.wireOp",EDGE,"E7.1.2"),sQuery(id+"F0.wireOp",EDGE,"E7.1.3"),sQuery(id+"F0.wireOp",EDGE,"E7.1.4"),sQuery(id+"F0.wireOp",EDGE,"E7.1.5"),sQuery(id+"F0.wireOp",EDGE,"E7.2.0"),sQuery(id+"F0.wireOp",EDGE,"E7.2.1"),sQuery(id+"F0.wireOp",EDGE,"E7.2.2"),sQuery(id+"F0.wireOp",EDGE,"E7.2.3"),sQuery(id+"F0.wireOp",EDGE,"E7.2.4"),sQuery(id+"F0.wireOp",EDGE,"E7.2.5"),sQuery(id+"F0.wireOp",EDGE,"E7.3.0"),sQuery(id+"F0.wireOp",EDGE,"E7.3.1"),sQuery(id+"F0.wireOp",EDGE,"E7.3.2"),sQuery(id+"F0.wireOp",EDGE,"E7.3.3"),sQuery(id+"F0.wireOp",EDGE,"E7.3.4"),sQuery(id+"F0.wireOp",EDGE,"E7.3.5"),sQuery(id+"F0.wireOp",EDGE,"E7.4.0"),sQuery(id+"F0.wireOp",EDGE,"E7.4.1"),sQuery(id+"F0.wireOp",EDGE,"E7.4.2"),sQuery(id+"F0.wireOp",EDGE,"E7.4.3"),sQuery(id+"F0.wireOp",EDGE,"E7.4.4"),sQuery(id+"F0.wireOp",EDGE,"E7.4.5"),sQuery(id+"F0.wireOp",EDGE,"E7.5.0"),sQuery(id+"F0.wireOp",EDGE,"E7.5.1"),sQuery(id+"F0.wireOp",EDGE,"E7.5.2"),sQuery(id+"F0.wireOp",EDGE,"E7.5.3"),sQuery(id+"F0.wireOp",EDGE,"E7.5.4"),sQuery(id+"F0.wireOp",EDGE,"E7.5.5"),sQuery(id+"F0.wireOp",EDGE,"E7.6.0"),sQuery(id+"F0.wireOp",EDGE,"E7.6.1"),sQuery(id+"F0.wireOp",EDGE,"E7.6.2"),sQuery(id+"F0.wireOp",EDGE,"E7.6.3"),sQuery(id+"F0.wireOp",EDGE,"E7.6.4"),sQuery(id+"F0.wireOp",EDGE,"E7.6.5"),sQuery(id+"F0.wireOp",EDGE,"E7.7.0"),sQuery(id+"F0.wireOp",EDGE,"E7.7.1"),sQuery(id+"F0.wireOp",EDGE,"E7.7.2"),sQuery(id+"F0.wireOp",EDGE,"E7.7.3"),sQuery(id+"F0.wireOp",EDGE,"E7.7.4"),sQuery(id+"F0.wireOp",EDGE,"E7.7.5"),sQuery(id+"F0.wireOp",EDGE,"E7.8.0"),sQuery(id+"F0.wireOp",EDGE,"E7.8.1"),sQuery(id+"F0.wireOp",EDGE,"E7.8.2"),sQuery(id+"F0.wireOp",EDGE,"E7.8.3"),sQuery(id+"F0.wireOp",EDGE,"E7.8.4"),sQuery(id+"F0.wireOp",EDGE,"E7.8.5"),sQuery(id+"F0.wireOp",EDGE,"E7.9.0"),sQuery(id+"F0.wireOp",EDGE,"E7.9.1"),sQuery(id+"F0.wireOp",EDGE,"E7.9.2"),sQuery(id+"F0.wireOp",EDGE,"E7.9.3"),sQuery(id+"F0.wireOp",EDGE,"E7.9.4"),sQuery(id+"F0.wireOp",EDGE,"E7.9.5"),sQuery(id+"F0.wireOp",EDGE,"E7.10.0"),sQuery(id+"F0.wireOp",EDGE,"E7.10.1"),sQuery(id+"F0.wireOp",EDGE,"E7.10.2"),sQuery(id+"F0.wireOp",EDGE,"E7.10.3"),sQuery(id+"F0.wireOp",EDGE,"E7.10.4"),sQuery(id+"F0.wireOp",EDGE,"E7.10.5"),sQuery(id+"F0.wireOp",EDGE,"E7.11.0"),sQuery(id+"F0.wireOp",EDGE,"E7.11.1"),sQuery(id+"F0.wireOp",EDGE,"E7.11.2"),sQuery(id+"F0.wireOp",EDGE,"E7.11.3"),sQuery(id+"F0.wireOp",EDGE,"E7.11.4"),sQuery(id+"F0.wireOp",EDGE,"E7.11.5"),sQuery(id+"F0.wireOp",EDGE,"E7.12.0"),sQuery(id+"F0.wireOp",EDGE,"E7.12.1"),sQuery(id+"F0.wireOp",EDGE,"E7.12.2"),sQuery(id+"F0.wireOp",EDGE,"E7.12.3"),sQuery(id+"F0.wireOp",EDGE,"E7.12.4"),sQuery(id+"F0.wireOp",EDGE,"E7.12.5"),sQuery(id+"F0.wireOp",EDGE,"E7.13.0"),sQuery(id+"F0.wireOp",EDGE,"E7.13.1"),sQuery(id+"F0.wireOp",EDGE,"E7.13.2"),sQuery(id+"F0.wireOp",EDGE,"E7.13.3"),sQuery(id+"F0.wireOp",EDGE,"E7.13.4"),sQuery(id+"F0.wireOp",EDGE,"E7.13.5"),sQuery(id+"F0.wireOp",EDGE,"E7.14.0"),sQuery(id+"F0.wireOp",EDGE,"E7.14.1"),sQuery(id+"F0.wireOp",EDGE,"E7.14.2"),sQuery(id+"F0.wireOp",EDGE,"E7.14.3"),sQuery(id+"F0.wireOp",EDGE,"E7.14.4"),sQuery(id+"F0.wireOp",EDGE,"E7.14.5"),sQuery(id+"F0.wireOp",EDGE,"E7.15.0"),sQuery(id+"F0.wireOp",EDGE,"E7.15.1"),sQuery(id+"F0.wireOp",EDGE,"E7.15.2"),sQuery(id+"F0.wireOp",EDGE,"E7.15.3"),sQuery(id+"F0.wireOp",EDGE,"E7.15.4"),sQuery(id+"F0.wireOp",EDGE,"E7.15.5"),sQuery(id+"F0.wireOp",EDGE,"E7.16.0"),sQuery(id+"F0.wireOp",EDGE,"E7.16.1"),sQuery(id+"F0.wireOp",EDGE,"E7.16.2"),sQuery(id+"F0.wireOp",EDGE,"E7.16.3"),sQuery(id+"F0.wireOp",EDGE,"E7.16.4"),sQuery(id+"F0.wireOp",EDGE,"E7.16.5"),sQuery(id+"F0.wireOp",EDGE,"E7.17.0"),sQuery(id+"F0.wireOp",EDGE,"E7.17.1"),sQuery(id+"F0.wireOp",EDGE,"E7.17.2"),sQuery(id+"F0.wireOp",EDGE,"E7.17.3"),sQuery(id+"F0.wireOp",EDGE,"E7.17.4"),sQuery(id+"F0.wireOp",EDGE,"E7.17.5"),sQuery(id+"F0.wireOp",EDGE,"E7.18.0"),sQuery(id+"F0.wireOp",EDGE,"E7.18.1"),sQuery(id+"F0.wireOp",EDGE,"E7.18.2"),sQuery(id+"F0.wireOp",EDGE,"E7.18.3"),sQuery(id+"F0.wireOp",EDGE,"E7.18.4"),sQuery(id+"F0.wireOp",EDGE,"E7.18.5"),sQuery(id+"F0.wireOp",EDGE,"E7.19.0"),sQuery(id+"F0.wireOp",EDGE,"E7.19.1"),sQuery(id+"F0.wireOp",EDGE,"E7.19.2"),sQuery(id+"F0.wireOp",EDGE,"E7.19.3"),sQuery(id+"F0.wireOp",EDGE,"E7.19.4"),sQuery(id+"F0.wireOp",EDGE,"E7.19.5"),sQuery(id+"F0.wireOp",EDGE,"E7.20.0"),sQuery(id+"F0.wireOp",EDGE,"E7.20.1"),sQuery(id+"F0.wireOp",EDGE,"E7.20.2"),sQuery(id+"F0.wireOp",EDGE,"E7.20.3"),sQuery(id+"F0.wireOp",EDGE,"E7.20.4"),sQuery(id+"F0.wireOp",EDGE,"E7.20.5"),subQ0,sQuery(id+"F0.wireOp",EDGE,"E7.21.1"),sQuery(id+"F0.wireOp",EDGE,"E7.21.2"),sQuery(id+"F0.wireOp",EDGE,"E7.21.3"),sQuery(id+"F0.wireOp",EDGE,"E7.21.4"),sQuery(id+"F0.wireOp",EDGE,"E7.21.5"),sQuery(id+"F0.wireOp",EDGE,"E7.22.0"),sQuery(id+"F0.wireOp",EDGE,"E7.22.1"),sQuery(id+"F0.wireOp",EDGE,"E7.22.2"),sQuery(id+"F0.wireOp",EDGE,"E7.22.3"),sQuery(id+"F0.wireOp",EDGE,"E7.22.4"),sQuery(id+"F0.wireOp",EDGE,"E7.22.5"),sQuery(id+"F0.wireOp",EDGE,"E7.23.0"),sQuery(id+"F0.wireOp",EDGE,"E7.23.1"),sQuery(id+"F0.wireOp",EDGE,"E7.23.2"),sQuery(id+"F0.wireOp",EDGE,"E7.23.3"),sQuery(id+"F0.wireOp",EDGE,"E7.23.4"),sQuery(id+"F0.wireOp",EDGE,"E7.23.5"),sQuery(id+"F0.wireOp",EDGE,"E7.24.0"),sQuery(id+"F0.wireOp",EDGE,"E7.24.1"),sQuery(id+"F0.wireOp",EDGE,"E7.24.2"),sQuery(id+"F0.wireOp",EDGE,"E7.24.3"),sQuery(id+"F0.wireOp",EDGE,"E7.24.4"),sQuery(id+"F0.wireOp",EDGE,"E7.24.5"),sQuery(id+"F0.wireOp",EDGE,"E7.25.0"),sQuery(id+"F0.wireOp",EDGE,"E7.25.1"),sQuery(id+"F0.wireOp",EDGE,"E7.25.2"),sQuery(id+"F0.wireOp",EDGE,"E7.25.3"),sQuery(id+"F0.wireOp",EDGE,"E7.25.4"),sQuery(id+"F0.wireOp",EDGE,"E7.25.5"),sQuery(id+"F0.wireOp",EDGE,"E7.26.0"),sQuery(id+"F0.wireOp",EDGE,"E7.26.1"),sQuery(id+"F0.wireOp",EDGE,"E7.26.2"),sQuery(id+"F0.wireOp",EDGE,"E7.26.3"),sQuery(id+"F0.wireOp",EDGE,"E7.26.4"),sQuery(id+"F0.wireOp",EDGE,"E7.26.5"),sQuery(id+"F0.wireOp",EDGE,"E7.27.0"),sQuery(id+"F0.wireOp",EDGE,"E7.27.1"),sQuery(id+"F0.wireOp",EDGE,"E7.27.2"),sQuery(id+"F0.wireOp",EDGE,"E7.27.3"),sQuery(id+"F0.wireOp",EDGE,"E7.27.4"),sQuery(id+"F0.wireOp",EDGE,"E7.27.5"),sQuery(id+"F0.wireOp",EDGE,"E7.28.0"),sQuery(id+"F0.wireOp",EDGE,"E7.28.1"),sQuery(id+"F0.wireOp",EDGE,"E7.28.2"),sQuery(id+"F0.wireOp",EDGE,"E7.28.3"),sQuery(id+"F0.wireOp",EDGE,"E7.28.4"),sQuery(id+"F0.wireOp",EDGE,"E7.28.5"),sQuery(id+"F0.wireOp",EDGE,"E7.29.0"),sQuery(id+"F0.wireOp",EDGE,"E7.29.1"),sQuery(id+"F0.wireOp",EDGE,"E7.29.2"),sQuery(id+"F0.wireOp",EDGE,"E7.29.3"),sQuery(id+"F0.wireOp",EDGE,"E7.29.4"),sQuery(id+"F0.wireOp",EDGE,"E7.29.5"),sQuery(id+"F0.wireOp",EDGE,"E7.30.0"),sQuery(id+"F0.wireOp",EDGE,"E7.30.1"),sQuery(id+"F0.wireOp",EDGE,"E7.30.2"),sQuery(id+"F0.wireOp",EDGE,"E7.30.3"),sQuery(id+"F0.wireOp",EDGE,"E7.30.4"),sQuery(id+"F0.wireOp",EDGE,"E7.30.5"),sQuery(id+"F0.wireOp",EDGE,"E7.31.0"),sQuery(id+"F0.wireOp",EDGE,"E7.31.1"),sQuery(id+"F0.wireOp",EDGE,"E7.31.2"),sQuery(id+"F0.wireOp",EDGE,"E7.31.3"),sQuery(id+"F0.wireOp",EDGE,"E7.31.4"),sQuery(id+"F0.wireOp",EDGE,"E7.31.5"),sQuery(id+"F0.wireOp",EDGE,"E7.32.0"),sQuery(id+"F0.wireOp",EDGE,"E7.32.1"),sQuery(id+"F0.wireOp",EDGE,"E7.32.2"),sQuery(id+"F0.wireOp",EDGE,"E7.32.3"),sQuery(id+"F0.wireOp",EDGE,"E7.32.4"),sQuery(id+"F0.wireOp",EDGE,"E7.32.5"),sQuery(id+"F0.wireOp",EDGE,"E7.33.0"),sQuery(id+"F0.wireOp",EDGE,"E7.33.1"),sQuery(id+"F0.wireOp",EDGE,"E7.33.2"),sQuery(id+"F0.wireOp",EDGE,"E7.33.3"),sQuery(id+"F0.wireOp",EDGE,"E7.33.4"),sQuery(id+"F0.wireOp",EDGE,"E7.33.5"),sQuery(id+"F0.wireOp",EDGE,"E7.34.0"),sQuery(id+"F0.wireOp",EDGE,"E7.34.1"),sQuery(id+"F0.wireOp",EDGE,"E7.34.2"),sQuery(id+"F0.wireOp",EDGE,"E7.34.3"),sQuery(id+"F0.wireOp",EDGE,"E7.34.4"),sQuery(id+"F0.wireOp",EDGE,"E7.34.5"),sQuery(id+"F0.wireOp",EDGE,"E7.35.0"),sQuery(id+"F0.wireOp",EDGE,"E7.35.1"),sQuery(id+"F0.wireOp",EDGE,"E7.35.2"),sQuery(id+"F0.wireOp",EDGE,"E7.35.3"),sQuery(id+"F0.wireOp",EDGE,"E7.35.4"),sQuery(id+"F0.wireOp",EDGE,"E7.35.5"),sQuery(id+"F0.wireOp",EDGE,"E7.36.0"),sQuery(id+"F0.wireOp",EDGE,"E7.36.1"),sQuery(id+"F0.wireOp",EDGE,"E7.36.2"),sQuery(id+"F0.wireOp",EDGE,"E7.36.3"),sQuery(id+"F0.wireOp",EDGE,"E7.36.4"),sQuery(id+"F0.wireOp",EDGE,"E7.36.5"),sQuery(id+"F0.wireOp",EDGE,"E7.37.0"),sQuery(id+"F0.wireOp",EDGE,"E7.37.1"),sQuery(id+"F0.wireOp",EDGE,"E7.37.2"),sQuery(id+"F0.wireOp",EDGE,"E7.37.3"),sQuery(id+"F0.wireOp",EDGE,"E7.37.4"),sQuery(id+"F0.wireOp",EDGE,"E7.37.5"),sQuery(id+"F0.wireOp",EDGE,"E7.38.0"),sQuery(id+"F0.wireOp",EDGE,"E7.38.1"),sQuery(id+"F0.wireOp",EDGE,"E7.38.2"),sQuery(id+"F0.wireOp",EDGE,"E7.38.3"),sQuery(id+"F0.wireOp",EDGE,"E7.38.4"),sQuery(id+"F0.wireOp",EDGE,"E7.38.5"),sQuery(id+"F0.wireOp",EDGE,"E7.39.0"),sQuery(id+"F0.wireOp",EDGE,"E7.39.1"),sQuery(id+"F0.wireOp",EDGE,"E7.39.2"),sQuery(id+"F0.wireOp",EDGE,"E7.39.3"),sQuery(id+"F0.wireOp",EDGE,"E7.39.4"),sQuery(id+"F0.wireOp",EDGE,"E7.39.5"),sQuery(id+"F0.wireOp",EDGE,"E7.40.0"),sQuery(id+"F0.wireOp",EDGE,"E7.40.1"),sQuery(id+"F0.wireOp",EDGE,"E7.40.2"),sQuery(id+"F0.wireOp",EDGE,"E7.40.3"),sQuery(id+"F0.wireOp",EDGE,"E7.40.4"),sQuery(id+"F0.wireOp",EDGE,"E7.40.5"),sQuery(id+"F0.wireOp",EDGE,"E7.41.0"),sQuery(id+"F0.wireOp",EDGE,"E7.41.1"),sQuery(id+"F0.wireOp",EDGE,"E7.41.2"),sQuery(id+"F0.wireOp",EDGE,"E7.41.3"),sQuery(id+"F0.wireOp",EDGE,"E7.41.4"),sQuery(id+"F0.wireOp",EDGE,"E7.41.5"),sQuery(id+"F0.wireOp",EDGE,"E7.42.0"),sQuery(id+"F0.wireOp",EDGE,"E7.42.1"),sQuery(id+"F0.wireOp",EDGE,"E7.42.2"),sQuery(id+"F0.wireOp",EDGE,"E7.42.3"),sQuery(id+"F0.wireOp",EDGE,"E7.42.4"),sQuery(id+"F0.wireOp",EDGE,"E7.42.5"),sQuery(id+"F0.wireOp",EDGE,"E7.43.0"),sQuery(id+"F0.wireOp",EDGE,"E7.43.1"),sQuery(id+"F0.wireOp",EDGE,"E7.43.2"),sQuery(id+"F0.wireOp",EDGE,"E7.43.3"),sQuery(id+"F0.wireOp",EDGE,"E7.43.4"),sQuery(id+"F0.wireOp",EDGE,"E7.43.5")])],"isStart":false})],"blendedInto":[makeQuery(id+"F1.opExtrude","CAP_FACE",FACE,{"disambiguationData":[OSD([sQuery(id+"F0.wireOp",EDGE,"E1"),sQuery(id+"F0.wireOp",EDGE,"E2"),sQuery(id+"F0.wireOp",EDGE,"E3"),sQuery(id+"F0.wireOp",EDGE,"E4"),sQuery(id+"F0.wireOp",EDGE,"E5"),sQuery(id+"F0.wireOp",EDGE,"E6"),sQuery(id+"F0.wireOp",EDGE,"E7.1.0"),sQuery(id+"F0.wireOp",EDGE,"E7.1.1"),sQuery(id+"F0.wireOp",EDGE,"E7.1.2"),sQuery(id+"F0.wireOp",EDGE,"E7.1.3"),sQuery(id+"F0.wireOp",EDGE,"E7.1.4"),sQuery(id+"F0.wireOp",EDGE,"E7.1.5"),sQuery(id+"F0.wireOp",EDGE,"E7.2.0"),sQuery(id+"F0.wireOp",EDGE,"E7.2.1"),sQuery(id+"F0.wireOp",EDGE,"E7.2.2"),sQuery(id+"F0.wireOp",EDGE,"E7.2.3"),sQuery(id+"F0.wireOp",EDGE,"E7.2.4"),sQuery(id+"F0.wireOp",EDGE,"E7.2.5"),sQuery(id+"F0.wireOp",EDGE,"E7.3.0"),sQuery(id+"F0.wireOp",EDGE,"E7.3.1"),sQuery(id+"F0.wireOp",EDGE,"E7.3.2"),sQuery(id+"F0.wireOp",EDGE,"E7.3.3"),sQuery(id+"F0.wireOp",EDGE,"E7.3.4"),sQuery(id+"F0.wireOp",EDGE,"E7.3.5"),sQuery(id+"F0.wireOp",EDGE,"E7.4.0"),sQuery(id+"F0.wireOp",EDGE,"E7.4.1"),sQuery(id+"F0.wireOp",EDGE,"E7.4.2"),sQuery(id+"F0.wireOp",EDGE,"E7.4.3"),sQuery(id+"F0.wireOp",EDGE,"E7.4.4"),sQuery(id+"F0.wireOp",EDGE,"E7.4.5"),sQuery(id+"F0.wireOp",EDGE,"E7.5.0"),sQuery(id+"F0.wireOp",EDGE,"E7.5.1"),sQuery(id+"F0.wireOp",EDGE,"E7.5.2"),sQuery(id+"F0.wireOp",EDGE,"E7.5.3"),sQuery(id+"F0.wireOp",EDGE,"E7.5.4"),sQuery(id+"F0.wireOp",EDGE,"E7.5.5"),sQuery(id+"F0.wireOp",EDGE,"E7.6.0"),sQuery(id+"F0.wireOp",EDGE,"E7.6.1"),sQuery(id+"F0.wireOp",EDGE,"E7.6.2"),sQuery(id+"F0.wireOp",EDGE,"E7.6.3"),sQuery(id+"F0.wireOp",EDGE,"E7.6.4"),sQuery(id+"F0.wireOp",EDGE,"E7.6.5"),sQuery(id+"F0.wireOp",EDGE,"E7.7.0"),sQuery(id+"F0.wireOp",EDGE,"E7.7.1"),sQuery(id+"F0.wireOp",EDGE,"E7.7.2"),sQuery(id+"F0.wireOp",EDGE,"E7.7.3"),sQuery(id+"F0.wireOp",EDGE,"E7.7.4"),sQuery(id+"F0.wireOp",EDGE,"E7.7.5"),sQuery(id+"F0.wireOp",EDGE,"E7.8.0"),sQuery(id+"F0.wireOp",EDGE,"E7.8.1"),sQuery(id+"F0.wireOp",EDGE,"E7.8.2"),sQuery(id+"F0.wireOp",EDGE,"E7.8.3"),sQuery(id+"F0.wireOp",EDGE,"E7.8.4"),sQuery(id+"F0.wireOp",EDGE,"E7.8.5"),sQuery(id+"F0.wireOp",EDGE,"E7.9.0"),sQuery(id+"F0.wireOp",EDGE,"E7.9.1"),sQuery(id+"F0.wireOp",EDGE,"E7.9.2"),sQuery(id+"F0.wireOp",EDGE,"E7.9.3"),sQuery(id+"F0.wireOp",EDGE,"E7.9.4"),sQuery(id+"F0.wireOp",EDGE,"E7.9.5"),sQuery(id+"F0.wireOp",EDGE,"E7.10.0"),sQuery(id+"F0.wireOp",EDGE,"E7.10.1"),sQuery(id+"F0.wireOp",EDGE,"E7.10.2"),sQuery(id+"F0.wireOp",EDGE,"E7.10.3"),sQuery(id+"F0.wireOp",EDGE,"E7.10.4"),sQuery(id+"F0.wireOp",EDGE,"E7.10.5"),sQuery(id+"F0.wireOp",EDGE,"E7.11.0"),sQuery(id+"F0.wireOp",EDGE,"E7.11.1"),sQuery(id+"F0.wireOp",EDGE,"E7.11.2"),sQuery(id+"F0.wireOp",EDGE,"E7.11.3"),sQuery(id+"F0.wireOp",EDGE,"E7.11.4"),sQuery(id+"F0.wireOp",EDGE,"E7.11.5"),sQuery(id+"F0.wireOp",EDGE,"E7.12.0"),sQuery(id+"F0.wireOp",EDGE,"E7.12.1"),sQuery(id+"F0.wireOp",EDGE,"E7.12.2"),sQuery(id+"F0.wireOp",EDGE,"E7.12.3"),sQuery(id+"F0.wireOp",EDGE,"E7.12.4"),sQuery(id+"F0.wireOp",EDGE,"E7.12.5"),sQuery(id+"F0.wireOp",EDGE,"E7.13.0"),sQuery(id+"F0.wireOp",EDGE,"E7.13.1"),sQuery(id+"F0.wireOp",EDGE,"E7.13.2"),sQuery(id+"F0.wireOp",EDGE,"E7.13.3"),sQuery(id+"F0.wireOp",EDGE,"E7.13.4"),sQuery(id+"F0.wireOp",EDGE,"E7.13.5"),sQuery(id+"F0.wireOp",EDGE,"E7.14.0"),sQuery(id+"F0.wireOp",EDGE,"E7.14.1"),sQuery(id+"F0.wireOp",EDGE,"E7.14.2"),sQuery(id+"F0.wireOp",EDGE,"E7.14.3"),sQuery(id+"F0.wireOp",EDGE,"E7.14.4"),sQuery(id+"F0.wireOp",EDGE,"E7.14.5"),sQuery(id+"F0.wireOp",EDGE,"E7.15.0"),sQuery(id+"F0.wireOp",EDGE,"E7.15.1"),sQuery(id+"F0.wireOp",EDGE,"E7.15.2"),sQuery(id+"F0.wireOp",EDGE,"E7.15.3"),sQuery(id+"F0.wireOp",EDGE,"E7.15.4"),sQuery(id+"F0.wireOp",EDGE,"E7.15.5"),sQuery(id+"F0.wireOp",EDGE,"E7.16.0"),sQuery(id+"F0.wireOp",EDGE,"E7.16.1"),sQuery(id+"F0.wireOp",EDGE,"E7.16.2"),sQuery(id+"F0.wireOp",EDGE,"E7.16.3"),sQuery(id+"F0.wireOp",EDGE,"E7.16.4"),sQuery(id+"F0.wireOp",EDGE,"E7.16.5"),sQuery(id+"F0.wireOp",EDGE,"E7.17.0"),sQuery(id+"F0.wireOp",EDGE,"E7.17.1"),sQuery(id+"F0.wireOp",EDGE,"E7.17.2"),sQuery(id+"F0.wireOp",EDGE,"E7.17.3"),sQuery(id+"F0.wireOp",EDGE,"E7.17.4"),sQuery(id+"F0.wireOp",EDGE,"E7.17.5"),sQuery(id+"F0.wireOp",EDGE,"E7.18.0"),sQuery(id+"F0.wireOp",EDGE,"E7.18.1"),sQuery(id+"F0.wireOp",EDGE,"E7.18.2"),sQuery(id+"F0.wireOp",EDGE,"E7.18.3"),sQuery(id+"F0.wireOp",EDGE,"E7.18.4"),sQuery(id+"F0.wireOp",EDGE,"E7.18.5"),sQuery(id+"F0.wireOp",EDGE,"E7.19.0"),sQuery(id+"F0.wireOp",EDGE,"E7.19.1"),sQuery(id+"F0.wireOp",EDGE,"E7.19.2"),sQuery(id+"F0.wireOp",EDGE,"E7.19.3"),sQuery(id+"F0.wireOp",EDGE,"E7.19.4"),sQuery(id+"F0.wireOp",EDGE,"E7.19.5"),sQuery(id+"F0.wireOp",EDGE,"E7.20.0"),sQuery(id+"F0.wireOp",EDGE,"E7.20.1"),sQuery(id+"F0.wireOp",EDGE,"E7.20.2"),sQuery(id+"F0.wireOp",EDGE,"E7.20.3"),sQuery(id+"F0.wireOp",EDGE,"E7.20.4"),sQuery(id+"F0.wireOp",EDGE,"E7.20.5"),subQ0,sQuery(id+"F0.wireOp",EDGE,"E7.21.1"),sQuery(id+"F0.wireOp",EDGE,"E7.21.2"),sQuery(id+"F0.wireOp",EDGE,"E7.21.3"),sQuery(id+"F0.wireOp",EDGE,"E7.21.4"),sQuery(id+"F0.wireOp",EDGE,"E7.21.5"),sQuery(id+"F0.wireOp",EDGE,"E7.22.0"),sQuery(id+"F0.wireOp",EDGE,"E7.22.1"),sQuery(id+"F0.wireOp",EDGE,"E7.22.2"),sQuery(id+"F0.wireOp",EDGE,"E7.22.3"),sQuery(id+"F0.wireOp",EDGE,"E7.22.4"),sQuery(id+"F0.wireOp",EDGE,"E7.22.5"),sQuery(id+"F0.wireOp",EDGE,"E7.23.0"),sQuery(id+"F0.wireOp",EDGE,"E7.23.1"),sQuery(id+"F0.wireOp",EDGE,"E7.23.2"),sQuery(id+"F0.wireOp",EDGE,"E7.23.3"),sQuery(id+"F0.wireOp",EDGE,"E7.23.4"),sQuery(id+"F0.wireOp",EDGE,"E7.23.5"),sQuery(id+"F0.wireOp",EDGE,"E7.24.0"),sQuery(id+"F0.wireOp",EDGE,"E7.24.1"),sQuery(id+"F0.wireOp",EDGE,"E7.24.2"),sQuery(id+"F0.wireOp",EDGE,"E7.24.3"),sQuery(id+"F0.wireOp",EDGE,"E7.24.4"),sQuery(id+"F0.wireOp",EDGE,"E7.24.5"),sQuery(id+"F0.wireOp",EDGE,"E7.25.0"),sQuery(id+"F0.wireOp",EDGE,"E7.25.1"),sQuery(id+"F0.wireOp",EDGE,"E7.25.2"),sQuery(id+"F0.wireOp",EDGE,"E7.25.3"),sQuery(id+"F0.wireOp",EDGE,"E7.25.4"),sQuery(id+"F0.wireOp",EDGE,"E7.25.5"),sQuery(id+"F0.wireOp",EDGE,"E7.26.0"),sQuery(id+"F0.wireOp",EDGE,"E7.26.1"),sQuery(id+"F0.wireOp",EDGE,"E7.26.2"),sQuery(id+"F0.wireOp",EDGE,"E7.26.3"),sQuery(id+"F0.wireOp",EDGE,"E7.26.4"),sQuery(id+"F0.wireOp",EDGE,"E7.26.5"),sQuery(id+"F0.wireOp",EDGE,"E7.27.0"),sQuery(id+"F0.wireOp",EDGE,"E7.27.1"),sQuery(id+"F0.wireOp",EDGE,"E7.27.2"),sQuery(id+"F0.wireOp",EDGE,"E7.27.3"),sQuery(id+"F0.wireOp",EDGE,"E7.27.4"),sQuery(id+"F0.wireOp",EDGE,"E7.27.5"),sQuery(id+"F0.wireOp",EDGE,"E7.28.0"),sQuery(id+"F0.wireOp",EDGE,"E7.28.1"),sQuery(id+"F0.wireOp",EDGE,"E7.28.2"),sQuery(id+"F0.wireOp",EDGE,"E7.28.3"),sQuery(id+"F0.wireOp",EDGE,"E7.28.4"),sQuery(id+"F0.wireOp",EDGE,"E7.28.5"),sQuery(id+"F0.wireOp",EDGE,"E7.29.0"),sQuery(id+"F0.wireOp",EDGE,"E7.29.1"),sQuery(id+"F0.wireOp",EDGE,"E7.29.2"),sQuery(id+"F0.wireOp",EDGE,"E7.29.3"),sQuery(id+"F0.wireOp",EDGE,"E7.29.4"),sQuery(id+"F0.wireOp",EDGE,"E7.29.5"),sQuery(id+"F0.wireOp",EDGE,"E7.30.0"),sQuery(id+"F0.wireOp",EDGE,"E7.30.1"),sQuery(id+"F0.wireOp",EDGE,"E7.30.2"),sQuery(id+"F0.wireOp",EDGE,"E7.30.3"),sQuery(id+"F0.wireOp",EDGE,"E7.30.4"),sQuery(id+"F0.wireOp",EDGE,"E7.30.5"),sQuery(id+"F0.wireOp",EDGE,"E7.31.0"),sQuery(id+"F0.wireOp",EDGE,"E7.31.1"),sQuery(id+"F0.wireOp",EDGE,"E7.31.2"),sQuery(id+"F0.wireOp",EDGE,"E7.31.3"),sQuery(id+"F0.wireOp",EDGE,"E7.31.4"),sQuery(id+"F0.wireOp",EDGE,"E7.31.5"),sQuery(id+"F0.wireOp",EDGE,"E7.32.0"),sQuery(id+"F0.wireOp",EDGE,"E7.32.1"),sQuery(id+"F0.wireOp",EDGE,"E7.32.2"),sQuery(id+"F0.wireOp",EDGE,"E7.32.3"),sQuery(id+"F0.wireOp",EDGE,"E7.32.4"),sQuery(id+"F0.wireOp",EDGE,"E7.32.5"),sQuery(id+"F0.wireOp",EDGE,"E7.33.0"),sQuery(id+"F0.wireOp",EDGE,"E7.33.1"),sQuery(id+"F0.wireOp",EDGE,"E7.33.2"),sQuery(id+"F0.wireOp",EDGE,"E7.33.3"),sQuery(id+"F0.wireOp",EDGE,"E7.33.4"),sQuery(id+"F0.wireOp",EDGE,"E7.33.5"),sQuery(id+"F0.wireOp",EDGE,"E7.34.0"),sQuery(id+"F0.wireOp",EDGE,"E7.34.1"),sQuery(id+"F0.wireOp",EDGE,"E7.34.2"),sQuery(id+"F0.wireOp",EDGE,"E7.34.3"),sQuery(id+"F0.wireOp",EDGE,"E7.34.4"),sQuery(id+"F0.wireOp",EDGE,"E7.34.5"),sQuery(id+"F0.wireOp",EDGE,"E7.35.0"),sQuery(id+"F0.wireOp",EDGE,"E7.35.1"),sQuery(id+"F0.wireOp",EDGE,"E7.35.2"),sQuery(id+"F0.wireOp",EDGE,"E7.35.3"),sQuery(id+"F0.wireOp",EDGE,"E7.35.4"),sQuery(id+"F0.wireOp",EDGE,"E7.35.5"),sQuery(id+"F0.wireOp",EDGE,"E7.36.0"),sQuery(id+"F0.wireOp",EDGE,"E7.36.1"),sQuery(id+"F0.wireOp",EDGE,"E7.36.2"),sQuery(id+"F0.wireOp",EDGE,"E7.36.3"),sQuery(id+"F0.wireOp",EDGE,"E7.36.4"),sQuery(id+"F0.wireOp",EDGE,"E7.36.5"),sQuery(id+"F0.wireOp",EDGE,"E7.37.0"),sQuery(id+"F0.wireOp",EDGE,"E7.37.1"),sQuery(id+"F0.wireOp",EDGE,"E7.37.2"),sQuery(id+"F0.wireOp",EDGE,"E7.37.3"),sQuery(id+"F0.wireOp",EDGE,"E7.37.4"),sQuery(id+"F0.wireOp",EDGE,"E7.37.5"),sQuery(id+"F0.wireOp",EDGE,"E7.38.0"),sQuery(id+"F0.wireOp",EDGE,"E7.38.1"),sQuery(id+"F0.wireOp",EDGE,"E7.38.2"),sQuery(id+"F0.wireOp",EDGE,"E7.38.3"),sQuery(id+"F0.wireOp",EDGE,"E7.38.4"),sQuery(id+"F0.wireOp",EDGE,"E7.38.5"),sQuery(id+"F0.wireOp",EDGE,"E7.39.0"),sQuery(id+"F0.wireOp",EDGE,"E7.39.1"),sQuery(id+"F0.wireOp",EDGE,"E7.39.2"),sQuery(id+"F0.wireOp",EDGE,"E7.39.3"),sQuery(id+"F0.wireOp",EDGE,"E7.39.4"),sQuery(id+"F0.wireOp",EDGE,"E7.39.5"),sQuery(id+"F0.wireOp",EDGE,"E7.40.0"),sQuery(id+"F0.wireOp",EDGE,"E7.40.1"),sQuery(id+"F0.wireOp",EDGE,"E7.40.2"),sQuery(id+"F0.wireOp",EDGE,"E7.40.3"),sQuery(id+"F0.wireOp",EDGE,"E7.40.4"),sQuery(id+"F0.wireOp",EDGE,"E7.40.5"),sQuery(id+"F0.wireOp",EDGE,"E7.41.0"),sQuery(id+"F0.wireOp",EDGE,"E7.41.1"),sQuery(id+"F0.wireOp",EDGE,"E7.41.2"),sQuery(id+"F0.wireOp",EDGE,"E7.41.3"),sQuery(id+"F0.wireOp",EDGE,"E7.41.4"),sQuery(id+"F0.wireOp",EDGE,"E7.41.5"),sQuery(id+"F0.wireOp",EDGE,"E7.42.0"),sQuery(id+"F0.wireOp",EDGE,"E7.42.1"),sQuery(id+"F0.wireOp",EDGE,"E7.42.2"),sQuery(id+"F0.wireOp",EDGE,"E7.42.3"),sQuery(id+"F0.wireOp",EDGE,"E7.42.4"),sQuery(id+"F0.wireOp",EDGE,"E7.42.5"),sQuery(id+"F0.wireOp",EDGE,"E7.43.0"),sQuery(id+"F0.wireOp",EDGE,"E7.43.1"),sQuery(id+"F0.wireOp",EDGE,"E7.43.2"),sQuery(id+"F0.wireOp",EDGE,"E7.43.3"),sQuery(id+"F0.wireOp",EDGE,"E7.43.4"),sQuery(id+"F0.wireOp",EDGE,"E7.43.5")])],"isStart":false})]}),makeQuery(id+"F2.opChamfer","BLEND_FACE",FACE,{"disambiguationData":[OSD([subQ0])]})],"blendedInto":[makeQuery(id+"F2.opChamfer","BLEND_FACE",FACE,{"disambiguationData":[OSD([subQ0])]})]});}
            var Q13;
            {var subQ0=sQuery(id+"F0.wireOp",EDGE,"E7.19.0");Q13=makeQuery(id+"F8.opChamfer","BLEND_EDGE",EDGE,{"blendedFrom":[makeQuery(id+"F2.opChamfer","BLEND_EDGE",EDGE,{"blendedFrom":[makeQuery(id+"F1.opExtrude","CAP_EDGE",EDGE,{"disambiguationData":[OSD([subQ0])],"isStart":false}),makeQuery(id+"F1.opExtrude","CAP_FACE",FACE,{"disambiguationData":[OSD([sQuery(id+"F0.wireOp",EDGE,"E1"),sQuery(id+"F0.wireOp",EDGE,"E2"),sQuery(id+"F0.wireOp",EDGE,"E3"),sQuery(id+"F0.wireOp",EDGE,"E4"),sQuery(id+"F0.wireOp",EDGE,"E5"),sQuery(id+"F0.wireOp",EDGE,"E6"),sQuery(id+"F0.wireOp",EDGE,"E7.1.0"),sQuery(id+"F0.wireOp",EDGE,"E7.1.1"),sQuery(id+"F0.wireOp",EDGE,"E7.1.2"),sQuery(id+"F0.wireOp",EDGE,"E7.1.3"),sQuery(id+"F0.wireOp",EDGE,"E7.1.4"),sQuery(id+"F0.wireOp",EDGE,"E7.1.5"),sQuery(id+"F0.wireOp",EDGE,"E7.2.0"),sQuery(id+"F0.wireOp",EDGE,"E7.2.1"),sQuery(id+"F0.wireOp",EDGE,"E7.2.2"),sQuery(id+"F0.wireOp",EDGE,"E7.2.3"),sQuery(id+"F0.wireOp",EDGE,"E7.2.4"),sQuery(id+"F0.wireOp",EDGE,"E7.2.5"),sQuery(id+"F0.wireOp",EDGE,"E7.3.0"),sQuery(id+"F0.wireOp",EDGE,"E7.3.1"),sQuery(id+"F0.wireOp",EDGE,"E7.3.2"),sQuery(id+"F0.wireOp",EDGE,"E7.3.3"),sQuery(id+"F0.wireOp",EDGE,"E7.3.4"),sQuery(id+"F0.wireOp",EDGE,"E7.3.5"),sQuery(id+"F0.wireOp",EDGE,"E7.4.0"),sQuery(id+"F0.wireOp",EDGE,"E7.4.1"),sQuery(id+"F0.wireOp",EDGE,"E7.4.2"),sQuery(id+"F0.wireOp",EDGE,"E7.4.3"),sQuery(id+"F0.wireOp",EDGE,"E7.4.4"),sQuery(id+"F0.wireOp",EDGE,"E7.4.5"),sQuery(id+"F0.wireOp",EDGE,"E7.5.0"),sQuery(id+"F0.wireOp",EDGE,"E7.5.1"),sQuery(id+"F0.wireOp",EDGE,"E7.5.2"),sQuery(id+"F0.wireOp",EDGE,"E7.5.3"),sQuery(id+"F0.wireOp",EDGE,"E7.5.4"),sQuery(id+"F0.wireOp",EDGE,"E7.5.5"),sQuery(id+"F0.wireOp",EDGE,"E7.6.0"),sQuery(id+"F0.wireOp",EDGE,"E7.6.1"),sQuery(id+"F0.wireOp",EDGE,"E7.6.2"),sQuery(id+"F0.wireOp",EDGE,"E7.6.3"),sQuery(id+"F0.wireOp",EDGE,"E7.6.4"),sQuery(id+"F0.wireOp",EDGE,"E7.6.5"),sQuery(id+"F0.wireOp",EDGE,"E7.7.0"),sQuery(id+"F0.wireOp",EDGE,"E7.7.1"),sQuery(id+"F0.wireOp",EDGE,"E7.7.2"),sQuery(id+"F0.wireOp",EDGE,"E7.7.3"),sQuery(id+"F0.wireOp",EDGE,"E7.7.4"),sQuery(id+"F0.wireOp",EDGE,"E7.7.5"),sQuery(id+"F0.wireOp",EDGE,"E7.8.0"),sQuery(id+"F0.wireOp",EDGE,"E7.8.1"),sQuery(id+"F0.wireOp",EDGE,"E7.8.2"),sQuery(id+"F0.wireOp",EDGE,"E7.8.3"),sQuery(id+"F0.wireOp",EDGE,"E7.8.4"),sQuery(id+"F0.wireOp",EDGE,"E7.8.5"),sQuery(id+"F0.wireOp",EDGE,"E7.9.0"),sQuery(id+"F0.wireOp",EDGE,"E7.9.1"),sQuery(id+"F0.wireOp",EDGE,"E7.9.2"),sQuery(id+"F0.wireOp",EDGE,"E7.9.3"),sQuery(id+"F0.wireOp",EDGE,"E7.9.4"),sQuery(id+"F0.wireOp",EDGE,"E7.9.5"),sQuery(id+"F0.wireOp",EDGE,"E7.10.0"),sQuery(id+"F0.wireOp",EDGE,"E7.10.1"),sQuery(id+"F0.wireOp",EDGE,"E7.10.2"),sQuery(id+"F0.wireOp",EDGE,"E7.10.3"),sQuery(id+"F0.wireOp",EDGE,"E7.10.4"),sQuery(id+"F0.wireOp",EDGE,"E7.10.5"),sQuery(id+"F0.wireOp",EDGE,"E7.11.0"),sQuery(id+"F0.wireOp",EDGE,"E7.11.1"),sQuery(id+"F0.wireOp",EDGE,"E7.11.2"),sQuery(id+"F0.wireOp",EDGE,"E7.11.3"),sQuery(id+"F0.wireOp",EDGE,"E7.11.4"),sQuery(id+"F0.wireOp",EDGE,"E7.11.5"),sQuery(id+"F0.wireOp",EDGE,"E7.12.0"),sQuery(id+"F0.wireOp",EDGE,"E7.12.1"),sQuery(id+"F0.wireOp",EDGE,"E7.12.2"),sQuery(id+"F0.wireOp",EDGE,"E7.12.3"),sQuery(id+"F0.wireOp",EDGE,"E7.12.4"),sQuery(id+"F0.wireOp",EDGE,"E7.12.5"),sQuery(id+"F0.wireOp",EDGE,"E7.13.0"),sQuery(id+"F0.wireOp",EDGE,"E7.13.1"),sQuery(id+"F0.wireOp",EDGE,"E7.13.2"),sQuery(id+"F0.wireOp",EDGE,"E7.13.3"),sQuery(id+"F0.wireOp",EDGE,"E7.13.4"),sQuery(id+"F0.wireOp",EDGE,"E7.13.5"),sQuery(id+"F0.wireOp",EDGE,"E7.14.0"),sQuery(id+"F0.wireOp",EDGE,"E7.14.1"),sQuery(id+"F0.wireOp",EDGE,"E7.14.2"),sQuery(id+"F0.wireOp",EDGE,"E7.14.3"),sQuery(id+"F0.wireOp",EDGE,"E7.14.4"),sQuery(id+"F0.wireOp",EDGE,"E7.14.5"),sQuery(id+"F0.wireOp",EDGE,"E7.15.0"),sQuery(id+"F0.wireOp",EDGE,"E7.15.1"),sQuery(id+"F0.wireOp",EDGE,"E7.15.2"),sQuery(id+"F0.wireOp",EDGE,"E7.15.3"),sQuery(id+"F0.wireOp",EDGE,"E7.15.4"),sQuery(id+"F0.wireOp",EDGE,"E7.15.5"),sQuery(id+"F0.wireOp",EDGE,"E7.16.0"),sQuery(id+"F0.wireOp",EDGE,"E7.16.1"),sQuery(id+"F0.wireOp",EDGE,"E7.16.2"),sQuery(id+"F0.wireOp",EDGE,"E7.16.3"),sQuery(id+"F0.wireOp",EDGE,"E7.16.4"),sQuery(id+"F0.wireOp",EDGE,"E7.16.5"),sQuery(id+"F0.wireOp",EDGE,"E7.17.0"),sQuery(id+"F0.wireOp",EDGE,"E7.17.1"),sQuery(id+"F0.wireOp",EDGE,"E7.17.2"),sQuery(id+"F0.wireOp",EDGE,"E7.17.3"),sQuery(id+"F0.wireOp",EDGE,"E7.17.4"),sQuery(id+"F0.wireOp",EDGE,"E7.17.5"),sQuery(id+"F0.wireOp",EDGE,"E7.18.0"),sQuery(id+"F0.wireOp",EDGE,"E7.18.1"),sQuery(id+"F0.wireOp",EDGE,"E7.18.2"),sQuery(id+"F0.wireOp",EDGE,"E7.18.3"),sQuery(id+"F0.wireOp",EDGE,"E7.18.4"),sQuery(id+"F0.wireOp",EDGE,"E7.18.5"),subQ0,sQuery(id+"F0.wireOp",EDGE,"E7.19.1"),sQuery(id+"F0.wireOp",EDGE,"E7.19.2"),sQuery(id+"F0.wireOp",EDGE,"E7.19.3"),sQuery(id+"F0.wireOp",EDGE,"E7.19.4"),sQuery(id+"F0.wireOp",EDGE,"E7.19.5"),sQuery(id+"F0.wireOp",EDGE,"E7.20.0"),sQuery(id+"F0.wireOp",EDGE,"E7.20.1"),sQuery(id+"F0.wireOp",EDGE,"E7.20.2"),sQuery(id+"F0.wireOp",EDGE,"E7.20.3"),sQuery(id+"F0.wireOp",EDGE,"E7.20.4"),sQuery(id+"F0.wireOp",EDGE,"E7.20.5"),sQuery(id+"F0.wireOp",EDGE,"E7.21.0"),sQuery(id+"F0.wireOp",EDGE,"E7.21.1"),sQuery(id+"F0.wireOp",EDGE,"E7.21.2"),sQuery(id+"F0.wireOp",EDGE,"E7.21.3"),sQuery(id+"F0.wireOp",EDGE,"E7.21.4"),sQuery(id+"F0.wireOp",EDGE,"E7.21.5"),sQuery(id+"F0.wireOp",EDGE,"E7.22.0"),sQuery(id+"F0.wireOp",EDGE,"E7.22.1"),sQuery(id+"F0.wireOp",EDGE,"E7.22.2"),sQuery(id+"F0.wireOp",EDGE,"E7.22.3"),sQuery(id+"F0.wireOp",EDGE,"E7.22.4"),sQuery(id+"F0.wireOp",EDGE,"E7.22.5"),sQuery(id+"F0.wireOp",EDGE,"E7.23.0"),sQuery(id+"F0.wireOp",EDGE,"E7.23.1"),sQuery(id+"F0.wireOp",EDGE,"E7.23.2"),sQuery(id+"F0.wireOp",EDGE,"E7.23.3"),sQuery(id+"F0.wireOp",EDGE,"E7.23.4"),sQuery(id+"F0.wireOp",EDGE,"E7.23.5"),sQuery(id+"F0.wireOp",EDGE,"E7.24.0"),sQuery(id+"F0.wireOp",EDGE,"E7.24.1"),sQuery(id+"F0.wireOp",EDGE,"E7.24.2"),sQuery(id+"F0.wireOp",EDGE,"E7.24.3"),sQuery(id+"F0.wireOp",EDGE,"E7.24.4"),sQuery(id+"F0.wireOp",EDGE,"E7.24.5"),sQuery(id+"F0.wireOp",EDGE,"E7.25.0"),sQuery(id+"F0.wireOp",EDGE,"E7.25.1"),sQuery(id+"F0.wireOp",EDGE,"E7.25.2"),sQuery(id+"F0.wireOp",EDGE,"E7.25.3"),sQuery(id+"F0.wireOp",EDGE,"E7.25.4"),sQuery(id+"F0.wireOp",EDGE,"E7.25.5"),sQuery(id+"F0.wireOp",EDGE,"E7.26.0"),sQuery(id+"F0.wireOp",EDGE,"E7.26.1"),sQuery(id+"F0.wireOp",EDGE,"E7.26.2"),sQuery(id+"F0.wireOp",EDGE,"E7.26.3"),sQuery(id+"F0.wireOp",EDGE,"E7.26.4"),sQuery(id+"F0.wireOp",EDGE,"E7.26.5"),sQuery(id+"F0.wireOp",EDGE,"E7.27.0"),sQuery(id+"F0.wireOp",EDGE,"E7.27.1"),sQuery(id+"F0.wireOp",EDGE,"E7.27.2"),sQuery(id+"F0.wireOp",EDGE,"E7.27.3"),sQuery(id+"F0.wireOp",EDGE,"E7.27.4"),sQuery(id+"F0.wireOp",EDGE,"E7.27.5"),sQuery(id+"F0.wireOp",EDGE,"E7.28.0"),sQuery(id+"F0.wireOp",EDGE,"E7.28.1"),sQuery(id+"F0.wireOp",EDGE,"E7.28.2"),sQuery(id+"F0.wireOp",EDGE,"E7.28.3"),sQuery(id+"F0.wireOp",EDGE,"E7.28.4"),sQuery(id+"F0.wireOp",EDGE,"E7.28.5"),sQuery(id+"F0.wireOp",EDGE,"E7.29.0"),sQuery(id+"F0.wireOp",EDGE,"E7.29.1"),sQuery(id+"F0.wireOp",EDGE,"E7.29.2"),sQuery(id+"F0.wireOp",EDGE,"E7.29.3"),sQuery(id+"F0.wireOp",EDGE,"E7.29.4"),sQuery(id+"F0.wireOp",EDGE,"E7.29.5"),sQuery(id+"F0.wireOp",EDGE,"E7.30.0"),sQuery(id+"F0.wireOp",EDGE,"E7.30.1"),sQuery(id+"F0.wireOp",EDGE,"E7.30.2"),sQuery(id+"F0.wireOp",EDGE,"E7.30.3"),sQuery(id+"F0.wireOp",EDGE,"E7.30.4"),sQuery(id+"F0.wireOp",EDGE,"E7.30.5"),sQuery(id+"F0.wireOp",EDGE,"E7.31.0"),sQuery(id+"F0.wireOp",EDGE,"E7.31.1"),sQuery(id+"F0.wireOp",EDGE,"E7.31.2"),sQuery(id+"F0.wireOp",EDGE,"E7.31.3"),sQuery(id+"F0.wireOp",EDGE,"E7.31.4"),sQuery(id+"F0.wireOp",EDGE,"E7.31.5"),sQuery(id+"F0.wireOp",EDGE,"E7.32.0"),sQuery(id+"F0.wireOp",EDGE,"E7.32.1"),sQuery(id+"F0.wireOp",EDGE,"E7.32.2"),sQuery(id+"F0.wireOp",EDGE,"E7.32.3"),sQuery(id+"F0.wireOp",EDGE,"E7.32.4"),sQuery(id+"F0.wireOp",EDGE,"E7.32.5"),sQuery(id+"F0.wireOp",EDGE,"E7.33.0"),sQuery(id+"F0.wireOp",EDGE,"E7.33.1"),sQuery(id+"F0.wireOp",EDGE,"E7.33.2"),sQuery(id+"F0.wireOp",EDGE,"E7.33.3"),sQuery(id+"F0.wireOp",EDGE,"E7.33.4"),sQuery(id+"F0.wireOp",EDGE,"E7.33.5"),sQuery(id+"F0.wireOp",EDGE,"E7.34.0"),sQuery(id+"F0.wireOp",EDGE,"E7.34.1"),sQuery(id+"F0.wireOp",EDGE,"E7.34.2"),sQuery(id+"F0.wireOp",EDGE,"E7.34.3"),sQuery(id+"F0.wireOp",EDGE,"E7.34.4"),sQuery(id+"F0.wireOp",EDGE,"E7.34.5"),sQuery(id+"F0.wireOp",EDGE,"E7.35.0"),sQuery(id+"F0.wireOp",EDGE,"E7.35.1"),sQuery(id+"F0.wireOp",EDGE,"E7.35.2"),sQuery(id+"F0.wireOp",EDGE,"E7.35.3"),sQuery(id+"F0.wireOp",EDGE,"E7.35.4"),sQuery(id+"F0.wireOp",EDGE,"E7.35.5"),sQuery(id+"F0.wireOp",EDGE,"E7.36.0"),sQuery(id+"F0.wireOp",EDGE,"E7.36.1"),sQuery(id+"F0.wireOp",EDGE,"E7.36.2"),sQuery(id+"F0.wireOp",EDGE,"E7.36.3"),sQuery(id+"F0.wireOp",EDGE,"E7.36.4"),sQuery(id+"F0.wireOp",EDGE,"E7.36.5"),sQuery(id+"F0.wireOp",EDGE,"E7.37.0"),sQuery(id+"F0.wireOp",EDGE,"E7.37.1"),sQuery(id+"F0.wireOp",EDGE,"E7.37.2"),sQuery(id+"F0.wireOp",EDGE,"E7.37.3"),sQuery(id+"F0.wireOp",EDGE,"E7.37.4"),sQuery(id+"F0.wireOp",EDGE,"E7.37.5"),sQuery(id+"F0.wireOp",EDGE,"E7.38.0"),sQuery(id+"F0.wireOp",EDGE,"E7.38.1"),sQuery(id+"F0.wireOp",EDGE,"E7.38.2"),sQuery(id+"F0.wireOp",EDGE,"E7.38.3"),sQuery(id+"F0.wireOp",EDGE,"E7.38.4"),sQuery(id+"F0.wireOp",EDGE,"E7.38.5"),sQuery(id+"F0.wireOp",EDGE,"E7.39.0"),sQuery(id+"F0.wireOp",EDGE,"E7.39.1"),sQuery(id+"F0.wireOp",EDGE,"E7.39.2"),sQuery(id+"F0.wireOp",EDGE,"E7.39.3"),sQuery(id+"F0.wireOp",EDGE,"E7.39.4"),sQuery(id+"F0.wireOp",EDGE,"E7.39.5"),sQuery(id+"F0.wireOp",EDGE,"E7.40.0"),sQuery(id+"F0.wireOp",EDGE,"E7.40.1"),sQuery(id+"F0.wireOp",EDGE,"E7.40.2"),sQuery(id+"F0.wireOp",EDGE,"E7.40.3"),sQuery(id+"F0.wireOp",EDGE,"E7.40.4"),sQuery(id+"F0.wireOp",EDGE,"E7.40.5"),sQuery(id+"F0.wireOp",EDGE,"E7.41.0"),sQuery(id+"F0.wireOp",EDGE,"E7.41.1"),sQuery(id+"F0.wireOp",EDGE,"E7.41.2"),sQuery(id+"F0.wireOp",EDGE,"E7.41.3"),sQuery(id+"F0.wireOp",EDGE,"E7.41.4"),sQuery(id+"F0.wireOp",EDGE,"E7.41.5"),sQuery(id+"F0.wireOp",EDGE,"E7.42.0"),sQuery(id+"F0.wireOp",EDGE,"E7.42.1"),sQuery(id+"F0.wireOp",EDGE,"E7.42.2"),sQuery(id+"F0.wireOp",EDGE,"E7.42.3"),sQuery(id+"F0.wireOp",EDGE,"E7.42.4"),sQuery(id+"F0.wireOp",EDGE,"E7.42.5"),sQuery(id+"F0.wireOp",EDGE,"E7.43.0"),sQuery(id+"F0.wireOp",EDGE,"E7.43.1"),sQuery(id+"F0.wireOp",EDGE,"E7.43.2"),sQuery(id+"F0.wireOp",EDGE,"E7.43.3"),sQuery(id+"F0.wireOp",EDGE,"E7.43.4"),sQuery(id+"F0.wireOp",EDGE,"E7.43.5")])],"isStart":false})],"blendedInto":[makeQuery(id+"F1.opExtrude","CAP_FACE",FACE,{"disambiguationData":[OSD([sQuery(id+"F0.wireOp",EDGE,"E1"),sQuery(id+"F0.wireOp",EDGE,"E2"),sQuery(id+"F0.wireOp",EDGE,"E3"),sQuery(id+"F0.wireOp",EDGE,"E4"),sQuery(id+"F0.wireOp",EDGE,"E5"),sQuery(id+"F0.wireOp",EDGE,"E6"),sQuery(id+"F0.wireOp",EDGE,"E7.1.0"),sQuery(id+"F0.wireOp",EDGE,"E7.1.1"),sQuery(id+"F0.wireOp",EDGE,"E7.1.2"),sQuery(id+"F0.wireOp",EDGE,"E7.1.3"),sQuery(id+"F0.wireOp",EDGE,"E7.1.4"),sQuery(id+"F0.wireOp",EDGE,"E7.1.5"),sQuery(id+"F0.wireOp",EDGE,"E7.2.0"),sQuery(id+"F0.wireOp",EDGE,"E7.2.1"),sQuery(id+"F0.wireOp",EDGE,"E7.2.2"),sQuery(id+"F0.wireOp",EDGE,"E7.2.3"),sQuery(id+"F0.wireOp",EDGE,"E7.2.4"),sQuery(id+"F0.wireOp",EDGE,"E7.2.5"),sQuery(id+"F0.wireOp",EDGE,"E7.3.0"),sQuery(id+"F0.wireOp",EDGE,"E7.3.1"),sQuery(id+"F0.wireOp",EDGE,"E7.3.2"),sQuery(id+"F0.wireOp",EDGE,"E7.3.3"),sQuery(id+"F0.wireOp",EDGE,"E7.3.4"),sQuery(id+"F0.wireOp",EDGE,"E7.3.5"),sQuery(id+"F0.wireOp",EDGE,"E7.4.0"),sQuery(id+"F0.wireOp",EDGE,"E7.4.1"),sQuery(id+"F0.wireOp",EDGE,"E7.4.2"),sQuery(id+"F0.wireOp",EDGE,"E7.4.3"),sQuery(id+"F0.wireOp",EDGE,"E7.4.4"),sQuery(id+"F0.wireOp",EDGE,"E7.4.5"),sQuery(id+"F0.wireOp",EDGE,"E7.5.0"),sQuery(id+"F0.wireOp",EDGE,"E7.5.1"),sQuery(id+"F0.wireOp",EDGE,"E7.5.2"),sQuery(id+"F0.wireOp",EDGE,"E7.5.3"),sQuery(id+"F0.wireOp",EDGE,"E7.5.4"),sQuery(id+"F0.wireOp",EDGE,"E7.5.5"),sQuery(id+"F0.wireOp",EDGE,"E7.6.0"),sQuery(id+"F0.wireOp",EDGE,"E7.6.1"),sQuery(id+"F0.wireOp",EDGE,"E7.6.2"),sQuery(id+"F0.wireOp",EDGE,"E7.6.3"),sQuery(id+"F0.wireOp",EDGE,"E7.6.4"),sQuery(id+"F0.wireOp",EDGE,"E7.6.5"),sQuery(id+"F0.wireOp",EDGE,"E7.7.0"),sQuery(id+"F0.wireOp",EDGE,"E7.7.1"),sQuery(id+"F0.wireOp",EDGE,"E7.7.2"),sQuery(id+"F0.wireOp",EDGE,"E7.7.3"),sQuery(id+"F0.wireOp",EDGE,"E7.7.4"),sQuery(id+"F0.wireOp",EDGE,"E7.7.5"),sQuery(id+"F0.wireOp",EDGE,"E7.8.0"),sQuery(id+"F0.wireOp",EDGE,"E7.8.1"),sQuery(id+"F0.wireOp",EDGE,"E7.8.2"),sQuery(id+"F0.wireOp",EDGE,"E7.8.3"),sQuery(id+"F0.wireOp",EDGE,"E7.8.4"),sQuery(id+"F0.wireOp",EDGE,"E7.8.5"),sQuery(id+"F0.wireOp",EDGE,"E7.9.0"),sQuery(id+"F0.wireOp",EDGE,"E7.9.1"),sQuery(id+"F0.wireOp",EDGE,"E7.9.2"),sQuery(id+"F0.wireOp",EDGE,"E7.9.3"),sQuery(id+"F0.wireOp",EDGE,"E7.9.4"),sQuery(id+"F0.wireOp",EDGE,"E7.9.5"),sQuery(id+"F0.wireOp",EDGE,"E7.10.0"),sQuery(id+"F0.wireOp",EDGE,"E7.10.1"),sQuery(id+"F0.wireOp",EDGE,"E7.10.2"),sQuery(id+"F0.wireOp",EDGE,"E7.10.3"),sQuery(id+"F0.wireOp",EDGE,"E7.10.4"),sQuery(id+"F0.wireOp",EDGE,"E7.10.5"),sQuery(id+"F0.wireOp",EDGE,"E7.11.0"),sQuery(id+"F0.wireOp",EDGE,"E7.11.1"),sQuery(id+"F0.wireOp",EDGE,"E7.11.2"),sQuery(id+"F0.wireOp",EDGE,"E7.11.3"),sQuery(id+"F0.wireOp",EDGE,"E7.11.4"),sQuery(id+"F0.wireOp",EDGE,"E7.11.5"),sQuery(id+"F0.wireOp",EDGE,"E7.12.0"),sQuery(id+"F0.wireOp",EDGE,"E7.12.1"),sQuery(id+"F0.wireOp",EDGE,"E7.12.2"),sQuery(id+"F0.wireOp",EDGE,"E7.12.3"),sQuery(id+"F0.wireOp",EDGE,"E7.12.4"),sQuery(id+"F0.wireOp",EDGE,"E7.12.5"),sQuery(id+"F0.wireOp",EDGE,"E7.13.0"),sQuery(id+"F0.wireOp",EDGE,"E7.13.1"),sQuery(id+"F0.wireOp",EDGE,"E7.13.2"),sQuery(id+"F0.wireOp",EDGE,"E7.13.3"),sQuery(id+"F0.wireOp",EDGE,"E7.13.4"),sQuery(id+"F0.wireOp",EDGE,"E7.13.5"),sQuery(id+"F0.wireOp",EDGE,"E7.14.0"),sQuery(id+"F0.wireOp",EDGE,"E7.14.1"),sQuery(id+"F0.wireOp",EDGE,"E7.14.2"),sQuery(id+"F0.wireOp",EDGE,"E7.14.3"),sQuery(id+"F0.wireOp",EDGE,"E7.14.4"),sQuery(id+"F0.wireOp",EDGE,"E7.14.5"),sQuery(id+"F0.wireOp",EDGE,"E7.15.0"),sQuery(id+"F0.wireOp",EDGE,"E7.15.1"),sQuery(id+"F0.wireOp",EDGE,"E7.15.2"),sQuery(id+"F0.wireOp",EDGE,"E7.15.3"),sQuery(id+"F0.wireOp",EDGE,"E7.15.4"),sQuery(id+"F0.wireOp",EDGE,"E7.15.5"),sQuery(id+"F0.wireOp",EDGE,"E7.16.0"),sQuery(id+"F0.wireOp",EDGE,"E7.16.1"),sQuery(id+"F0.wireOp",EDGE,"E7.16.2"),sQuery(id+"F0.wireOp",EDGE,"E7.16.3"),sQuery(id+"F0.wireOp",EDGE,"E7.16.4"),sQuery(id+"F0.wireOp",EDGE,"E7.16.5"),sQuery(id+"F0.wireOp",EDGE,"E7.17.0"),sQuery(id+"F0.wireOp",EDGE,"E7.17.1"),sQuery(id+"F0.wireOp",EDGE,"E7.17.2"),sQuery(id+"F0.wireOp",EDGE,"E7.17.3"),sQuery(id+"F0.wireOp",EDGE,"E7.17.4"),sQuery(id+"F0.wireOp",EDGE,"E7.17.5"),sQuery(id+"F0.wireOp",EDGE,"E7.18.0"),sQuery(id+"F0.wireOp",EDGE,"E7.18.1"),sQuery(id+"F0.wireOp",EDGE,"E7.18.2"),sQuery(id+"F0.wireOp",EDGE,"E7.18.3"),sQuery(id+"F0.wireOp",EDGE,"E7.18.4"),sQuery(id+"F0.wireOp",EDGE,"E7.18.5"),subQ0,sQuery(id+"F0.wireOp",EDGE,"E7.19.1"),sQuery(id+"F0.wireOp",EDGE,"E7.19.2"),sQuery(id+"F0.wireOp",EDGE,"E7.19.3"),sQuery(id+"F0.wireOp",EDGE,"E7.19.4"),sQuery(id+"F0.wireOp",EDGE,"E7.19.5"),sQuery(id+"F0.wireOp",EDGE,"E7.20.0"),sQuery(id+"F0.wireOp",EDGE,"E7.20.1"),sQuery(id+"F0.wireOp",EDGE,"E7.20.2"),sQuery(id+"F0.wireOp",EDGE,"E7.20.3"),sQuery(id+"F0.wireOp",EDGE,"E7.20.4"),sQuery(id+"F0.wireOp",EDGE,"E7.20.5"),sQuery(id+"F0.wireOp",EDGE,"E7.21.0"),sQuery(id+"F0.wireOp",EDGE,"E7.21.1"),sQuery(id+"F0.wireOp",EDGE,"E7.21.2"),sQuery(id+"F0.wireOp",EDGE,"E7.21.3"),sQuery(id+"F0.wireOp",EDGE,"E7.21.4"),sQuery(id+"F0.wireOp",EDGE,"E7.21.5"),sQuery(id+"F0.wireOp",EDGE,"E7.22.0"),sQuery(id+"F0.wireOp",EDGE,"E7.22.1"),sQuery(id+"F0.wireOp",EDGE,"E7.22.2"),sQuery(id+"F0.wireOp",EDGE,"E7.22.3"),sQuery(id+"F0.wireOp",EDGE,"E7.22.4"),sQuery(id+"F0.wireOp",EDGE,"E7.22.5"),sQuery(id+"F0.wireOp",EDGE,"E7.23.0"),sQuery(id+"F0.wireOp",EDGE,"E7.23.1"),sQuery(id+"F0.wireOp",EDGE,"E7.23.2"),sQuery(id+"F0.wireOp",EDGE,"E7.23.3"),sQuery(id+"F0.wireOp",EDGE,"E7.23.4"),sQuery(id+"F0.wireOp",EDGE,"E7.23.5"),sQuery(id+"F0.wireOp",EDGE,"E7.24.0"),sQuery(id+"F0.wireOp",EDGE,"E7.24.1"),sQuery(id+"F0.wireOp",EDGE,"E7.24.2"),sQuery(id+"F0.wireOp",EDGE,"E7.24.3"),sQuery(id+"F0.wireOp",EDGE,"E7.24.4"),sQuery(id+"F0.wireOp",EDGE,"E7.24.5"),sQuery(id+"F0.wireOp",EDGE,"E7.25.0"),sQuery(id+"F0.wireOp",EDGE,"E7.25.1"),sQuery(id+"F0.wireOp",EDGE,"E7.25.2"),sQuery(id+"F0.wireOp",EDGE,"E7.25.3"),sQuery(id+"F0.wireOp",EDGE,"E7.25.4"),sQuery(id+"F0.wireOp",EDGE,"E7.25.5"),sQuery(id+"F0.wireOp",EDGE,"E7.26.0"),sQuery(id+"F0.wireOp",EDGE,"E7.26.1"),sQuery(id+"F0.wireOp",EDGE,"E7.26.2"),sQuery(id+"F0.wireOp",EDGE,"E7.26.3"),sQuery(id+"F0.wireOp",EDGE,"E7.26.4"),sQuery(id+"F0.wireOp",EDGE,"E7.26.5"),sQuery(id+"F0.wireOp",EDGE,"E7.27.0"),sQuery(id+"F0.wireOp",EDGE,"E7.27.1"),sQuery(id+"F0.wireOp",EDGE,"E7.27.2"),sQuery(id+"F0.wireOp",EDGE,"E7.27.3"),sQuery(id+"F0.wireOp",EDGE,"E7.27.4"),sQuery(id+"F0.wireOp",EDGE,"E7.27.5"),sQuery(id+"F0.wireOp",EDGE,"E7.28.0"),sQuery(id+"F0.wireOp",EDGE,"E7.28.1"),sQuery(id+"F0.wireOp",EDGE,"E7.28.2"),sQuery(id+"F0.wireOp",EDGE,"E7.28.3"),sQuery(id+"F0.wireOp",EDGE,"E7.28.4"),sQuery(id+"F0.wireOp",EDGE,"E7.28.5"),sQuery(id+"F0.wireOp",EDGE,"E7.29.0"),sQuery(id+"F0.wireOp",EDGE,"E7.29.1"),sQuery(id+"F0.wireOp",EDGE,"E7.29.2"),sQuery(id+"F0.wireOp",EDGE,"E7.29.3"),sQuery(id+"F0.wireOp",EDGE,"E7.29.4"),sQuery(id+"F0.wireOp",EDGE,"E7.29.5"),sQuery(id+"F0.wireOp",EDGE,"E7.30.0"),sQuery(id+"F0.wireOp",EDGE,"E7.30.1"),sQuery(id+"F0.wireOp",EDGE,"E7.30.2"),sQuery(id+"F0.wireOp",EDGE,"E7.30.3"),sQuery(id+"F0.wireOp",EDGE,"E7.30.4"),sQuery(id+"F0.wireOp",EDGE,"E7.30.5"),sQuery(id+"F0.wireOp",EDGE,"E7.31.0"),sQuery(id+"F0.wireOp",EDGE,"E7.31.1"),sQuery(id+"F0.wireOp",EDGE,"E7.31.2"),sQuery(id+"F0.wireOp",EDGE,"E7.31.3"),sQuery(id+"F0.wireOp",EDGE,"E7.31.4"),sQuery(id+"F0.wireOp",EDGE,"E7.31.5"),sQuery(id+"F0.wireOp",EDGE,"E7.32.0"),sQuery(id+"F0.wireOp",EDGE,"E7.32.1"),sQuery(id+"F0.wireOp",EDGE,"E7.32.2"),sQuery(id+"F0.wireOp",EDGE,"E7.32.3"),sQuery(id+"F0.wireOp",EDGE,"E7.32.4"),sQuery(id+"F0.wireOp",EDGE,"E7.32.5"),sQuery(id+"F0.wireOp",EDGE,"E7.33.0"),sQuery(id+"F0.wireOp",EDGE,"E7.33.1"),sQuery(id+"F0.wireOp",EDGE,"E7.33.2"),sQuery(id+"F0.wireOp",EDGE,"E7.33.3"),sQuery(id+"F0.wireOp",EDGE,"E7.33.4"),sQuery(id+"F0.wireOp",EDGE,"E7.33.5"),sQuery(id+"F0.wireOp",EDGE,"E7.34.0"),sQuery(id+"F0.wireOp",EDGE,"E7.34.1"),sQuery(id+"F0.wireOp",EDGE,"E7.34.2"),sQuery(id+"F0.wireOp",EDGE,"E7.34.3"),sQuery(id+"F0.wireOp",EDGE,"E7.34.4"),sQuery(id+"F0.wireOp",EDGE,"E7.34.5"),sQuery(id+"F0.wireOp",EDGE,"E7.35.0"),sQuery(id+"F0.wireOp",EDGE,"E7.35.1"),sQuery(id+"F0.wireOp",EDGE,"E7.35.2"),sQuery(id+"F0.wireOp",EDGE,"E7.35.3"),sQuery(id+"F0.wireOp",EDGE,"E7.35.4"),sQuery(id+"F0.wireOp",EDGE,"E7.35.5"),sQuery(id+"F0.wireOp",EDGE,"E7.36.0"),sQuery(id+"F0.wireOp",EDGE,"E7.36.1"),sQuery(id+"F0.wireOp",EDGE,"E7.36.2"),sQuery(id+"F0.wireOp",EDGE,"E7.36.3"),sQuery(id+"F0.wireOp",EDGE,"E7.36.4"),sQuery(id+"F0.wireOp",EDGE,"E7.36.5"),sQuery(id+"F0.wireOp",EDGE,"E7.37.0"),sQuery(id+"F0.wireOp",EDGE,"E7.37.1"),sQuery(id+"F0.wireOp",EDGE,"E7.37.2"),sQuery(id+"F0.wireOp",EDGE,"E7.37.3"),sQuery(id+"F0.wireOp",EDGE,"E7.37.4"),sQuery(id+"F0.wireOp",EDGE,"E7.37.5"),sQuery(id+"F0.wireOp",EDGE,"E7.38.0"),sQuery(id+"F0.wireOp",EDGE,"E7.38.1"),sQuery(id+"F0.wireOp",EDGE,"E7.38.2"),sQuery(id+"F0.wireOp",EDGE,"E7.38.3"),sQuery(id+"F0.wireOp",EDGE,"E7.38.4"),sQuery(id+"F0.wireOp",EDGE,"E7.38.5"),sQuery(id+"F0.wireOp",EDGE,"E7.39.0"),sQuery(id+"F0.wireOp",EDGE,"E7.39.1"),sQuery(id+"F0.wireOp",EDGE,"E7.39.2"),sQuery(id+"F0.wireOp",EDGE,"E7.39.3"),sQuery(id+"F0.wireOp",EDGE,"E7.39.4"),sQuery(id+"F0.wireOp",EDGE,"E7.39.5"),sQuery(id+"F0.wireOp",EDGE,"E7.40.0"),sQuery(id+"F0.wireOp",EDGE,"E7.40.1"),sQuery(id+"F0.wireOp",EDGE,"E7.40.2"),sQuery(id+"F0.wireOp",EDGE,"E7.40.3"),sQuery(id+"F0.wireOp",EDGE,"E7.40.4"),sQuery(id+"F0.wireOp",EDGE,"E7.40.5"),sQuery(id+"F0.wireOp",EDGE,"E7.41.0"),sQuery(id+"F0.wireOp",EDGE,"E7.41.1"),sQuery(id+"F0.wireOp",EDGE,"E7.41.2"),sQuery(id+"F0.wireOp",EDGE,"E7.41.3"),sQuery(id+"F0.wireOp",EDGE,"E7.41.4"),sQuery(id+"F0.wireOp",EDGE,"E7.41.5"),sQuery(id+"F0.wireOp",EDGE,"E7.42.0"),sQuery(id+"F0.wireOp",EDGE,"E7.42.1"),sQuery(id+"F0.wireOp",EDGE,"E7.42.2"),sQuery(id+"F0.wireOp",EDGE,"E7.42.3"),sQuery(id+"F0.wireOp",EDGE,"E7.42.4"),sQuery(id+"F0.wireOp",EDGE,"E7.42.5"),sQuery(id+"F0.wireOp",EDGE,"E7.43.0"),sQuery(id+"F0.wireOp",EDGE,"E7.43.1"),sQuery(id+"F0.wireOp",EDGE,"E7.43.2"),sQuery(id+"F0.wireOp",EDGE,"E7.43.3"),sQuery(id+"F0.wireOp",EDGE,"E7.43.4"),sQuery(id+"F0.wireOp",EDGE,"E7.43.5")])],"isStart":false})]}),makeQuery(id+"F2.opChamfer","BLEND_FACE",FACE,{"disambiguationData":[OSD([subQ0])]})],"blendedInto":[makeQuery(id+"F2.opChamfer","BLEND_FACE",FACE,{"disambiguationData":[OSD([subQ0])]})]});}
            var Q14;
            {var subQ0=sQuery(id+"F0.wireOp",EDGE,"E7.17.0");Q14=makeQuery(id+"F8.opChamfer","BLEND_EDGE",EDGE,{"blendedFrom":[makeQuery(id+"F2.opChamfer","BLEND_EDGE",EDGE,{"blendedFrom":[makeQuery(id+"F1.opExtrude","CAP_EDGE",EDGE,{"disambiguationData":[OSD([subQ0])],"isStart":false}),makeQuery(id+"F1.opExtrude","CAP_FACE",FACE,{"disambiguationData":[OSD([sQuery(id+"F0.wireOp",EDGE,"E1"),sQuery(id+"F0.wireOp",EDGE,"E2"),sQuery(id+"F0.wireOp",EDGE,"E3"),sQuery(id+"F0.wireOp",EDGE,"E4"),sQuery(id+"F0.wireOp",EDGE,"E5"),sQuery(id+"F0.wireOp",EDGE,"E6"),sQuery(id+"F0.wireOp",EDGE,"E7.1.0"),sQuery(id+"F0.wireOp",EDGE,"E7.1.1"),sQuery(id+"F0.wireOp",EDGE,"E7.1.2"),sQuery(id+"F0.wireOp",EDGE,"E7.1.3"),sQuery(id+"F0.wireOp",EDGE,"E7.1.4"),sQuery(id+"F0.wireOp",EDGE,"E7.1.5"),sQuery(id+"F0.wireOp",EDGE,"E7.2.0"),sQuery(id+"F0.wireOp",EDGE,"E7.2.1"),sQuery(id+"F0.wireOp",EDGE,"E7.2.2"),sQuery(id+"F0.wireOp",EDGE,"E7.2.3"),sQuery(id+"F0.wireOp",EDGE,"E7.2.4"),sQuery(id+"F0.wireOp",EDGE,"E7.2.5"),sQuery(id+"F0.wireOp",EDGE,"E7.3.0"),sQuery(id+"F0.wireOp",EDGE,"E7.3.1"),sQuery(id+"F0.wireOp",EDGE,"E7.3.2"),sQuery(id+"F0.wireOp",EDGE,"E7.3.3"),sQuery(id+"F0.wireOp",EDGE,"E7.3.4"),sQuery(id+"F0.wireOp",EDGE,"E7.3.5"),sQuery(id+"F0.wireOp",EDGE,"E7.4.0"),sQuery(id+"F0.wireOp",EDGE,"E7.4.1"),sQuery(id+"F0.wireOp",EDGE,"E7.4.2"),sQuery(id+"F0.wireOp",EDGE,"E7.4.3"),sQuery(id+"F0.wireOp",EDGE,"E7.4.4"),sQuery(id+"F0.wireOp",EDGE,"E7.4.5"),sQuery(id+"F0.wireOp",EDGE,"E7.5.0"),sQuery(id+"F0.wireOp",EDGE,"E7.5.1"),sQuery(id+"F0.wireOp",EDGE,"E7.5.2"),sQuery(id+"F0.wireOp",EDGE,"E7.5.3"),sQuery(id+"F0.wireOp",EDGE,"E7.5.4"),sQuery(id+"F0.wireOp",EDGE,"E7.5.5"),sQuery(id+"F0.wireOp",EDGE,"E7.6.0"),sQuery(id+"F0.wireOp",EDGE,"E7.6.1"),sQuery(id+"F0.wireOp",EDGE,"E7.6.2"),sQuery(id+"F0.wireOp",EDGE,"E7.6.3"),sQuery(id+"F0.wireOp",EDGE,"E7.6.4"),sQuery(id+"F0.wireOp",EDGE,"E7.6.5"),sQuery(id+"F0.wireOp",EDGE,"E7.7.0"),sQuery(id+"F0.wireOp",EDGE,"E7.7.1"),sQuery(id+"F0.wireOp",EDGE,"E7.7.2"),sQuery(id+"F0.wireOp",EDGE,"E7.7.3"),sQuery(id+"F0.wireOp",EDGE,"E7.7.4"),sQuery(id+"F0.wireOp",EDGE,"E7.7.5"),sQuery(id+"F0.wireOp",EDGE,"E7.8.0"),sQuery(id+"F0.wireOp",EDGE,"E7.8.1"),sQuery(id+"F0.wireOp",EDGE,"E7.8.2"),sQuery(id+"F0.wireOp",EDGE,"E7.8.3"),sQuery(id+"F0.wireOp",EDGE,"E7.8.4"),sQuery(id+"F0.wireOp",EDGE,"E7.8.5"),sQuery(id+"F0.wireOp",EDGE,"E7.9.0"),sQuery(id+"F0.wireOp",EDGE,"E7.9.1"),sQuery(id+"F0.wireOp",EDGE,"E7.9.2"),sQuery(id+"F0.wireOp",EDGE,"E7.9.3"),sQuery(id+"F0.wireOp",EDGE,"E7.9.4"),sQuery(id+"F0.wireOp",EDGE,"E7.9.5"),sQuery(id+"F0.wireOp",EDGE,"E7.10.0"),sQuery(id+"F0.wireOp",EDGE,"E7.10.1"),sQuery(id+"F0.wireOp",EDGE,"E7.10.2"),sQuery(id+"F0.wireOp",EDGE,"E7.10.3"),sQuery(id+"F0.wireOp",EDGE,"E7.10.4"),sQuery(id+"F0.wireOp",EDGE,"E7.10.5"),sQuery(id+"F0.wireOp",EDGE,"E7.11.0"),sQuery(id+"F0.wireOp",EDGE,"E7.11.1"),sQuery(id+"F0.wireOp",EDGE,"E7.11.2"),sQuery(id+"F0.wireOp",EDGE,"E7.11.3"),sQuery(id+"F0.wireOp",EDGE,"E7.11.4"),sQuery(id+"F0.wireOp",EDGE,"E7.11.5"),sQuery(id+"F0.wireOp",EDGE,"E7.12.0"),sQuery(id+"F0.wireOp",EDGE,"E7.12.1"),sQuery(id+"F0.wireOp",EDGE,"E7.12.2"),sQuery(id+"F0.wireOp",EDGE,"E7.12.3"),sQuery(id+"F0.wireOp",EDGE,"E7.12.4"),sQuery(id+"F0.wireOp",EDGE,"E7.12.5"),sQuery(id+"F0.wireOp",EDGE,"E7.13.0"),sQuery(id+"F0.wireOp",EDGE,"E7.13.1"),sQuery(id+"F0.wireOp",EDGE,"E7.13.2"),sQuery(id+"F0.wireOp",EDGE,"E7.13.3"),sQuery(id+"F0.wireOp",EDGE,"E7.13.4"),sQuery(id+"F0.wireOp",EDGE,"E7.13.5"),sQuery(id+"F0.wireOp",EDGE,"E7.14.0"),sQuery(id+"F0.wireOp",EDGE,"E7.14.1"),sQuery(id+"F0.wireOp",EDGE,"E7.14.2"),sQuery(id+"F0.wireOp",EDGE,"E7.14.3"),sQuery(id+"F0.wireOp",EDGE,"E7.14.4"),sQuery(id+"F0.wireOp",EDGE,"E7.14.5"),sQuery(id+"F0.wireOp",EDGE,"E7.15.0"),sQuery(id+"F0.wireOp",EDGE,"E7.15.1"),sQuery(id+"F0.wireOp",EDGE,"E7.15.2"),sQuery(id+"F0.wireOp",EDGE,"E7.15.3"),sQuery(id+"F0.wireOp",EDGE,"E7.15.4"),sQuery(id+"F0.wireOp",EDGE,"E7.15.5"),sQuery(id+"F0.wireOp",EDGE,"E7.16.0"),sQuery(id+"F0.wireOp",EDGE,"E7.16.1"),sQuery(id+"F0.wireOp",EDGE,"E7.16.2"),sQuery(id+"F0.wireOp",EDGE,"E7.16.3"),sQuery(id+"F0.wireOp",EDGE,"E7.16.4"),sQuery(id+"F0.wireOp",EDGE,"E7.16.5"),subQ0,sQuery(id+"F0.wireOp",EDGE,"E7.17.1"),sQuery(id+"F0.wireOp",EDGE,"E7.17.2"),sQuery(id+"F0.wireOp",EDGE,"E7.17.3"),sQuery(id+"F0.wireOp",EDGE,"E7.17.4"),sQuery(id+"F0.wireOp",EDGE,"E7.17.5"),sQuery(id+"F0.wireOp",EDGE,"E7.18.0"),sQuery(id+"F0.wireOp",EDGE,"E7.18.1"),sQuery(id+"F0.wireOp",EDGE,"E7.18.2"),sQuery(id+"F0.wireOp",EDGE,"E7.18.3"),sQuery(id+"F0.wireOp",EDGE,"E7.18.4"),sQuery(id+"F0.wireOp",EDGE,"E7.18.5"),sQuery(id+"F0.wireOp",EDGE,"E7.19.0"),sQuery(id+"F0.wireOp",EDGE,"E7.19.1"),sQuery(id+"F0.wireOp",EDGE,"E7.19.2"),sQuery(id+"F0.wireOp",EDGE,"E7.19.3"),sQuery(id+"F0.wireOp",EDGE,"E7.19.4"),sQuery(id+"F0.wireOp",EDGE,"E7.19.5"),sQuery(id+"F0.wireOp",EDGE,"E7.20.0"),sQuery(id+"F0.wireOp",EDGE,"E7.20.1"),sQuery(id+"F0.wireOp",EDGE,"E7.20.2"),sQuery(id+"F0.wireOp",EDGE,"E7.20.3"),sQuery(id+"F0.wireOp",EDGE,"E7.20.4"),sQuery(id+"F0.wireOp",EDGE,"E7.20.5"),sQuery(id+"F0.wireOp",EDGE,"E7.21.0"),sQuery(id+"F0.wireOp",EDGE,"E7.21.1"),sQuery(id+"F0.wireOp",EDGE,"E7.21.2"),sQuery(id+"F0.wireOp",EDGE,"E7.21.3"),sQuery(id+"F0.wireOp",EDGE,"E7.21.4"),sQuery(id+"F0.wireOp",EDGE,"E7.21.5"),sQuery(id+"F0.wireOp",EDGE,"E7.22.0"),sQuery(id+"F0.wireOp",EDGE,"E7.22.1"),sQuery(id+"F0.wireOp",EDGE,"E7.22.2"),sQuery(id+"F0.wireOp",EDGE,"E7.22.3"),sQuery(id+"F0.wireOp",EDGE,"E7.22.4"),sQuery(id+"F0.wireOp",EDGE,"E7.22.5"),sQuery(id+"F0.wireOp",EDGE,"E7.23.0"),sQuery(id+"F0.wireOp",EDGE,"E7.23.1"),sQuery(id+"F0.wireOp",EDGE,"E7.23.2"),sQuery(id+"F0.wireOp",EDGE,"E7.23.3"),sQuery(id+"F0.wireOp",EDGE,"E7.23.4"),sQuery(id+"F0.wireOp",EDGE,"E7.23.5"),sQuery(id+"F0.wireOp",EDGE,"E7.24.0"),sQuery(id+"F0.wireOp",EDGE,"E7.24.1"),sQuery(id+"F0.wireOp",EDGE,"E7.24.2"),sQuery(id+"F0.wireOp",EDGE,"E7.24.3"),sQuery(id+"F0.wireOp",EDGE,"E7.24.4"),sQuery(id+"F0.wireOp",EDGE,"E7.24.5"),sQuery(id+"F0.wireOp",EDGE,"E7.25.0"),sQuery(id+"F0.wireOp",EDGE,"E7.25.1"),sQuery(id+"F0.wireOp",EDGE,"E7.25.2"),sQuery(id+"F0.wireOp",EDGE,"E7.25.3"),sQuery(id+"F0.wireOp",EDGE,"E7.25.4"),sQuery(id+"F0.wireOp",EDGE,"E7.25.5"),sQuery(id+"F0.wireOp",EDGE,"E7.26.0"),sQuery(id+"F0.wireOp",EDGE,"E7.26.1"),sQuery(id+"F0.wireOp",EDGE,"E7.26.2"),sQuery(id+"F0.wireOp",EDGE,"E7.26.3"),sQuery(id+"F0.wireOp",EDGE,"E7.26.4"),sQuery(id+"F0.wireOp",EDGE,"E7.26.5"),sQuery(id+"F0.wireOp",EDGE,"E7.27.0"),sQuery(id+"F0.wireOp",EDGE,"E7.27.1"),sQuery(id+"F0.wireOp",EDGE,"E7.27.2"),sQuery(id+"F0.wireOp",EDGE,"E7.27.3"),sQuery(id+"F0.wireOp",EDGE,"E7.27.4"),sQuery(id+"F0.wireOp",EDGE,"E7.27.5"),sQuery(id+"F0.wireOp",EDGE,"E7.28.0"),sQuery(id+"F0.wireOp",EDGE,"E7.28.1"),sQuery(id+"F0.wireOp",EDGE,"E7.28.2"),sQuery(id+"F0.wireOp",EDGE,"E7.28.3"),sQuery(id+"F0.wireOp",EDGE,"E7.28.4"),sQuery(id+"F0.wireOp",EDGE,"E7.28.5"),sQuery(id+"F0.wireOp",EDGE,"E7.29.0"),sQuery(id+"F0.wireOp",EDGE,"E7.29.1"),sQuery(id+"F0.wireOp",EDGE,"E7.29.2"),sQuery(id+"F0.wireOp",EDGE,"E7.29.3"),sQuery(id+"F0.wireOp",EDGE,"E7.29.4"),sQuery(id+"F0.wireOp",EDGE,"E7.29.5"),sQuery(id+"F0.wireOp",EDGE,"E7.30.0"),sQuery(id+"F0.wireOp",EDGE,"E7.30.1"),sQuery(id+"F0.wireOp",EDGE,"E7.30.2"),sQuery(id+"F0.wireOp",EDGE,"E7.30.3"),sQuery(id+"F0.wireOp",EDGE,"E7.30.4"),sQuery(id+"F0.wireOp",EDGE,"E7.30.5"),sQuery(id+"F0.wireOp",EDGE,"E7.31.0"),sQuery(id+"F0.wireOp",EDGE,"E7.31.1"),sQuery(id+"F0.wireOp",EDGE,"E7.31.2"),sQuery(id+"F0.wireOp",EDGE,"E7.31.3"),sQuery(id+"F0.wireOp",EDGE,"E7.31.4"),sQuery(id+"F0.wireOp",EDGE,"E7.31.5"),sQuery(id+"F0.wireOp",EDGE,"E7.32.0"),sQuery(id+"F0.wireOp",EDGE,"E7.32.1"),sQuery(id+"F0.wireOp",EDGE,"E7.32.2"),sQuery(id+"F0.wireOp",EDGE,"E7.32.3"),sQuery(id+"F0.wireOp",EDGE,"E7.32.4"),sQuery(id+"F0.wireOp",EDGE,"E7.32.5"),sQuery(id+"F0.wireOp",EDGE,"E7.33.0"),sQuery(id+"F0.wireOp",EDGE,"E7.33.1"),sQuery(id+"F0.wireOp",EDGE,"E7.33.2"),sQuery(id+"F0.wireOp",EDGE,"E7.33.3"),sQuery(id+"F0.wireOp",EDGE,"E7.33.4"),sQuery(id+"F0.wireOp",EDGE,"E7.33.5"),sQuery(id+"F0.wireOp",EDGE,"E7.34.0"),sQuery(id+"F0.wireOp",EDGE,"E7.34.1"),sQuery(id+"F0.wireOp",EDGE,"E7.34.2"),sQuery(id+"F0.wireOp",EDGE,"E7.34.3"),sQuery(id+"F0.wireOp",EDGE,"E7.34.4"),sQuery(id+"F0.wireOp",EDGE,"E7.34.5"),sQuery(id+"F0.wireOp",EDGE,"E7.35.0"),sQuery(id+"F0.wireOp",EDGE,"E7.35.1"),sQuery(id+"F0.wireOp",EDGE,"E7.35.2"),sQuery(id+"F0.wireOp",EDGE,"E7.35.3"),sQuery(id+"F0.wireOp",EDGE,"E7.35.4"),sQuery(id+"F0.wireOp",EDGE,"E7.35.5"),sQuery(id+"F0.wireOp",EDGE,"E7.36.0"),sQuery(id+"F0.wireOp",EDGE,"E7.36.1"),sQuery(id+"F0.wireOp",EDGE,"E7.36.2"),sQuery(id+"F0.wireOp",EDGE,"E7.36.3"),sQuery(id+"F0.wireOp",EDGE,"E7.36.4"),sQuery(id+"F0.wireOp",EDGE,"E7.36.5"),sQuery(id+"F0.wireOp",EDGE,"E7.37.0"),sQuery(id+"F0.wireOp",EDGE,"E7.37.1"),sQuery(id+"F0.wireOp",EDGE,"E7.37.2"),sQuery(id+"F0.wireOp",EDGE,"E7.37.3"),sQuery(id+"F0.wireOp",EDGE,"E7.37.4"),sQuery(id+"F0.wireOp",EDGE,"E7.37.5"),sQuery(id+"F0.wireOp",EDGE,"E7.38.0"),sQuery(id+"F0.wireOp",EDGE,"E7.38.1"),sQuery(id+"F0.wireOp",EDGE,"E7.38.2"),sQuery(id+"F0.wireOp",EDGE,"E7.38.3"),sQuery(id+"F0.wireOp",EDGE,"E7.38.4"),sQuery(id+"F0.wireOp",EDGE,"E7.38.5"),sQuery(id+"F0.wireOp",EDGE,"E7.39.0"),sQuery(id+"F0.wireOp",EDGE,"E7.39.1"),sQuery(id+"F0.wireOp",EDGE,"E7.39.2"),sQuery(id+"F0.wireOp",EDGE,"E7.39.3"),sQuery(id+"F0.wireOp",EDGE,"E7.39.4"),sQuery(id+"F0.wireOp",EDGE,"E7.39.5"),sQuery(id+"F0.wireOp",EDGE,"E7.40.0"),sQuery(id+"F0.wireOp",EDGE,"E7.40.1"),sQuery(id+"F0.wireOp",EDGE,"E7.40.2"),sQuery(id+"F0.wireOp",EDGE,"E7.40.3"),sQuery(id+"F0.wireOp",EDGE,"E7.40.4"),sQuery(id+"F0.wireOp",EDGE,"E7.40.5"),sQuery(id+"F0.wireOp",EDGE,"E7.41.0"),sQuery(id+"F0.wireOp",EDGE,"E7.41.1"),sQuery(id+"F0.wireOp",EDGE,"E7.41.2"),sQuery(id+"F0.wireOp",EDGE,"E7.41.3"),sQuery(id+"F0.wireOp",EDGE,"E7.41.4"),sQuery(id+"F0.wireOp",EDGE,"E7.41.5"),sQuery(id+"F0.wireOp",EDGE,"E7.42.0"),sQuery(id+"F0.wireOp",EDGE,"E7.42.1"),sQuery(id+"F0.wireOp",EDGE,"E7.42.2"),sQuery(id+"F0.wireOp",EDGE,"E7.42.3"),sQuery(id+"F0.wireOp",EDGE,"E7.42.4"),sQuery(id+"F0.wireOp",EDGE,"E7.42.5"),sQuery(id+"F0.wireOp",EDGE,"E7.43.0"),sQuery(id+"F0.wireOp",EDGE,"E7.43.1"),sQuery(id+"F0.wireOp",EDGE,"E7.43.2"),sQuery(id+"F0.wireOp",EDGE,"E7.43.3"),sQuery(id+"F0.wireOp",EDGE,"E7.43.4"),sQuery(id+"F0.wireOp",EDGE,"E7.43.5")])],"isStart":false})],"blendedInto":[makeQuery(id+"F1.opExtrude","CAP_FACE",FACE,{"disambiguationData":[OSD([sQuery(id+"F0.wireOp",EDGE,"E1"),sQuery(id+"F0.wireOp",EDGE,"E2"),sQuery(id+"F0.wireOp",EDGE,"E3"),sQuery(id+"F0.wireOp",EDGE,"E4"),sQuery(id+"F0.wireOp",EDGE,"E5"),sQuery(id+"F0.wireOp",EDGE,"E6"),sQuery(id+"F0.wireOp",EDGE,"E7.1.0"),sQuery(id+"F0.wireOp",EDGE,"E7.1.1"),sQuery(id+"F0.wireOp",EDGE,"E7.1.2"),sQuery(id+"F0.wireOp",EDGE,"E7.1.3"),sQuery(id+"F0.wireOp",EDGE,"E7.1.4"),sQuery(id+"F0.wireOp",EDGE,"E7.1.5"),sQuery(id+"F0.wireOp",EDGE,"E7.2.0"),sQuery(id+"F0.wireOp",EDGE,"E7.2.1"),sQuery(id+"F0.wireOp",EDGE,"E7.2.2"),sQuery(id+"F0.wireOp",EDGE,"E7.2.3"),sQuery(id+"F0.wireOp",EDGE,"E7.2.4"),sQuery(id+"F0.wireOp",EDGE,"E7.2.5"),sQuery(id+"F0.wireOp",EDGE,"E7.3.0"),sQuery(id+"F0.wireOp",EDGE,"E7.3.1"),sQuery(id+"F0.wireOp",EDGE,"E7.3.2"),sQuery(id+"F0.wireOp",EDGE,"E7.3.3"),sQuery(id+"F0.wireOp",EDGE,"E7.3.4"),sQuery(id+"F0.wireOp",EDGE,"E7.3.5"),sQuery(id+"F0.wireOp",EDGE,"E7.4.0"),sQuery(id+"F0.wireOp",EDGE,"E7.4.1"),sQuery(id+"F0.wireOp",EDGE,"E7.4.2"),sQuery(id+"F0.wireOp",EDGE,"E7.4.3"),sQuery(id+"F0.wireOp",EDGE,"E7.4.4"),sQuery(id+"F0.wireOp",EDGE,"E7.4.5"),sQuery(id+"F0.wireOp",EDGE,"E7.5.0"),sQuery(id+"F0.wireOp",EDGE,"E7.5.1"),sQuery(id+"F0.wireOp",EDGE,"E7.5.2"),sQuery(id+"F0.wireOp",EDGE,"E7.5.3"),sQuery(id+"F0.wireOp",EDGE,"E7.5.4"),sQuery(id+"F0.wireOp",EDGE,"E7.5.5"),sQuery(id+"F0.wireOp",EDGE,"E7.6.0"),sQuery(id+"F0.wireOp",EDGE,"E7.6.1"),sQuery(id+"F0.wireOp",EDGE,"E7.6.2"),sQuery(id+"F0.wireOp",EDGE,"E7.6.3"),sQuery(id+"F0.wireOp",EDGE,"E7.6.4"),sQuery(id+"F0.wireOp",EDGE,"E7.6.5"),sQuery(id+"F0.wireOp",EDGE,"E7.7.0"),sQuery(id+"F0.wireOp",EDGE,"E7.7.1"),sQuery(id+"F0.wireOp",EDGE,"E7.7.2"),sQuery(id+"F0.wireOp",EDGE,"E7.7.3"),sQuery(id+"F0.wireOp",EDGE,"E7.7.4"),sQuery(id+"F0.wireOp",EDGE,"E7.7.5"),sQuery(id+"F0.wireOp",EDGE,"E7.8.0"),sQuery(id+"F0.wireOp",EDGE,"E7.8.1"),sQuery(id+"F0.wireOp",EDGE,"E7.8.2"),sQuery(id+"F0.wireOp",EDGE,"E7.8.3"),sQuery(id+"F0.wireOp",EDGE,"E7.8.4"),sQuery(id+"F0.wireOp",EDGE,"E7.8.5"),sQuery(id+"F0.wireOp",EDGE,"E7.9.0"),sQuery(id+"F0.wireOp",EDGE,"E7.9.1"),sQuery(id+"F0.wireOp",EDGE,"E7.9.2"),sQuery(id+"F0.wireOp",EDGE,"E7.9.3"),sQuery(id+"F0.wireOp",EDGE,"E7.9.4"),sQuery(id+"F0.wireOp",EDGE,"E7.9.5"),sQuery(id+"F0.wireOp",EDGE,"E7.10.0"),sQuery(id+"F0.wireOp",EDGE,"E7.10.1"),sQuery(id+"F0.wireOp",EDGE,"E7.10.2"),sQuery(id+"F0.wireOp",EDGE,"E7.10.3"),sQuery(id+"F0.wireOp",EDGE,"E7.10.4"),sQuery(id+"F0.wireOp",EDGE,"E7.10.5"),sQuery(id+"F0.wireOp",EDGE,"E7.11.0"),sQuery(id+"F0.wireOp",EDGE,"E7.11.1"),sQuery(id+"F0.wireOp",EDGE,"E7.11.2"),sQuery(id+"F0.wireOp",EDGE,"E7.11.3"),sQuery(id+"F0.wireOp",EDGE,"E7.11.4"),sQuery(id+"F0.wireOp",EDGE,"E7.11.5"),sQuery(id+"F0.wireOp",EDGE,"E7.12.0"),sQuery(id+"F0.wireOp",EDGE,"E7.12.1"),sQuery(id+"F0.wireOp",EDGE,"E7.12.2"),sQuery(id+"F0.wireOp",EDGE,"E7.12.3"),sQuery(id+"F0.wireOp",EDGE,"E7.12.4"),sQuery(id+"F0.wireOp",EDGE,"E7.12.5"),sQuery(id+"F0.wireOp",EDGE,"E7.13.0"),sQuery(id+"F0.wireOp",EDGE,"E7.13.1"),sQuery(id+"F0.wireOp",EDGE,"E7.13.2"),sQuery(id+"F0.wireOp",EDGE,"E7.13.3"),sQuery(id+"F0.wireOp",EDGE,"E7.13.4"),sQuery(id+"F0.wireOp",EDGE,"E7.13.5"),sQuery(id+"F0.wireOp",EDGE,"E7.14.0"),sQuery(id+"F0.wireOp",EDGE,"E7.14.1"),sQuery(id+"F0.wireOp",EDGE,"E7.14.2"),sQuery(id+"F0.wireOp",EDGE,"E7.14.3"),sQuery(id+"F0.wireOp",EDGE,"E7.14.4"),sQuery(id+"F0.wireOp",EDGE,"E7.14.5"),sQuery(id+"F0.wireOp",EDGE,"E7.15.0"),sQuery(id+"F0.wireOp",EDGE,"E7.15.1"),sQuery(id+"F0.wireOp",EDGE,"E7.15.2"),sQuery(id+"F0.wireOp",EDGE,"E7.15.3"),sQuery(id+"F0.wireOp",EDGE,"E7.15.4"),sQuery(id+"F0.wireOp",EDGE,"E7.15.5"),sQuery(id+"F0.wireOp",EDGE,"E7.16.0"),sQuery(id+"F0.wireOp",EDGE,"E7.16.1"),sQuery(id+"F0.wireOp",EDGE,"E7.16.2"),sQuery(id+"F0.wireOp",EDGE,"E7.16.3"),sQuery(id+"F0.wireOp",EDGE,"E7.16.4"),sQuery(id+"F0.wireOp",EDGE,"E7.16.5"),subQ0,sQuery(id+"F0.wireOp",EDGE,"E7.17.1"),sQuery(id+"F0.wireOp",EDGE,"E7.17.2"),sQuery(id+"F0.wireOp",EDGE,"E7.17.3"),sQuery(id+"F0.wireOp",EDGE,"E7.17.4"),sQuery(id+"F0.wireOp",EDGE,"E7.17.5"),sQuery(id+"F0.wireOp",EDGE,"E7.18.0"),sQuery(id+"F0.wireOp",EDGE,"E7.18.1"),sQuery(id+"F0.wireOp",EDGE,"E7.18.2"),sQuery(id+"F0.wireOp",EDGE,"E7.18.3"),sQuery(id+"F0.wireOp",EDGE,"E7.18.4"),sQuery(id+"F0.wireOp",EDGE,"E7.18.5"),sQuery(id+"F0.wireOp",EDGE,"E7.19.0"),sQuery(id+"F0.wireOp",EDGE,"E7.19.1"),sQuery(id+"F0.wireOp",EDGE,"E7.19.2"),sQuery(id+"F0.wireOp",EDGE,"E7.19.3"),sQuery(id+"F0.wireOp",EDGE,"E7.19.4"),sQuery(id+"F0.wireOp",EDGE,"E7.19.5"),sQuery(id+"F0.wireOp",EDGE,"E7.20.0"),sQuery(id+"F0.wireOp",EDGE,"E7.20.1"),sQuery(id+"F0.wireOp",EDGE,"E7.20.2"),sQuery(id+"F0.wireOp",EDGE,"E7.20.3"),sQuery(id+"F0.wireOp",EDGE,"E7.20.4"),sQuery(id+"F0.wireOp",EDGE,"E7.20.5"),sQuery(id+"F0.wireOp",EDGE,"E7.21.0"),sQuery(id+"F0.wireOp",EDGE,"E7.21.1"),sQuery(id+"F0.wireOp",EDGE,"E7.21.2"),sQuery(id+"F0.wireOp",EDGE,"E7.21.3"),sQuery(id+"F0.wireOp",EDGE,"E7.21.4"),sQuery(id+"F0.wireOp",EDGE,"E7.21.5"),sQuery(id+"F0.wireOp",EDGE,"E7.22.0"),sQuery(id+"F0.wireOp",EDGE,"E7.22.1"),sQuery(id+"F0.wireOp",EDGE,"E7.22.2"),sQuery(id+"F0.wireOp",EDGE,"E7.22.3"),sQuery(id+"F0.wireOp",EDGE,"E7.22.4"),sQuery(id+"F0.wireOp",EDGE,"E7.22.5"),sQuery(id+"F0.wireOp",EDGE,"E7.23.0"),sQuery(id+"F0.wireOp",EDGE,"E7.23.1"),sQuery(id+"F0.wireOp",EDGE,"E7.23.2"),sQuery(id+"F0.wireOp",EDGE,"E7.23.3"),sQuery(id+"F0.wireOp",EDGE,"E7.23.4"),sQuery(id+"F0.wireOp",EDGE,"E7.23.5"),sQuery(id+"F0.wireOp",EDGE,"E7.24.0"),sQuery(id+"F0.wireOp",EDGE,"E7.24.1"),sQuery(id+"F0.wireOp",EDGE,"E7.24.2"),sQuery(id+"F0.wireOp",EDGE,"E7.24.3"),sQuery(id+"F0.wireOp",EDGE,"E7.24.4"),sQuery(id+"F0.wireOp",EDGE,"E7.24.5"),sQuery(id+"F0.wireOp",EDGE,"E7.25.0"),sQuery(id+"F0.wireOp",EDGE,"E7.25.1"),sQuery(id+"F0.wireOp",EDGE,"E7.25.2"),sQuery(id+"F0.wireOp",EDGE,"E7.25.3"),sQuery(id+"F0.wireOp",EDGE,"E7.25.4"),sQuery(id+"F0.wireOp",EDGE,"E7.25.5"),sQuery(id+"F0.wireOp",EDGE,"E7.26.0"),sQuery(id+"F0.wireOp",EDGE,"E7.26.1"),sQuery(id+"F0.wireOp",EDGE,"E7.26.2"),sQuery(id+"F0.wireOp",EDGE,"E7.26.3"),sQuery(id+"F0.wireOp",EDGE,"E7.26.4"),sQuery(id+"F0.wireOp",EDGE,"E7.26.5"),sQuery(id+"F0.wireOp",EDGE,"E7.27.0"),sQuery(id+"F0.wireOp",EDGE,"E7.27.1"),sQuery(id+"F0.wireOp",EDGE,"E7.27.2"),sQuery(id+"F0.wireOp",EDGE,"E7.27.3"),sQuery(id+"F0.wireOp",EDGE,"E7.27.4"),sQuery(id+"F0.wireOp",EDGE,"E7.27.5"),sQuery(id+"F0.wireOp",EDGE,"E7.28.0"),sQuery(id+"F0.wireOp",EDGE,"E7.28.1"),sQuery(id+"F0.wireOp",EDGE,"E7.28.2"),sQuery(id+"F0.wireOp",EDGE,"E7.28.3"),sQuery(id+"F0.wireOp",EDGE,"E7.28.4"),sQuery(id+"F0.wireOp",EDGE,"E7.28.5"),sQuery(id+"F0.wireOp",EDGE,"E7.29.0"),sQuery(id+"F0.wireOp",EDGE,"E7.29.1"),sQuery(id+"F0.wireOp",EDGE,"E7.29.2"),sQuery(id+"F0.wireOp",EDGE,"E7.29.3"),sQuery(id+"F0.wireOp",EDGE,"E7.29.4"),sQuery(id+"F0.wireOp",EDGE,"E7.29.5"),sQuery(id+"F0.wireOp",EDGE,"E7.30.0"),sQuery(id+"F0.wireOp",EDGE,"E7.30.1"),sQuery(id+"F0.wireOp",EDGE,"E7.30.2"),sQuery(id+"F0.wireOp",EDGE,"E7.30.3"),sQuery(id+"F0.wireOp",EDGE,"E7.30.4"),sQuery(id+"F0.wireOp",EDGE,"E7.30.5"),sQuery(id+"F0.wireOp",EDGE,"E7.31.0"),sQuery(id+"F0.wireOp",EDGE,"E7.31.1"),sQuery(id+"F0.wireOp",EDGE,"E7.31.2"),sQuery(id+"F0.wireOp",EDGE,"E7.31.3"),sQuery(id+"F0.wireOp",EDGE,"E7.31.4"),sQuery(id+"F0.wireOp",EDGE,"E7.31.5"),sQuery(id+"F0.wireOp",EDGE,"E7.32.0"),sQuery(id+"F0.wireOp",EDGE,"E7.32.1"),sQuery(id+"F0.wireOp",EDGE,"E7.32.2"),sQuery(id+"F0.wireOp",EDGE,"E7.32.3"),sQuery(id+"F0.wireOp",EDGE,"E7.32.4"),sQuery(id+"F0.wireOp",EDGE,"E7.32.5"),sQuery(id+"F0.wireOp",EDGE,"E7.33.0"),sQuery(id+"F0.wireOp",EDGE,"E7.33.1"),sQuery(id+"F0.wireOp",EDGE,"E7.33.2"),sQuery(id+"F0.wireOp",EDGE,"E7.33.3"),sQuery(id+"F0.wireOp",EDGE,"E7.33.4"),sQuery(id+"F0.wireOp",EDGE,"E7.33.5"),sQuery(id+"F0.wireOp",EDGE,"E7.34.0"),sQuery(id+"F0.wireOp",EDGE,"E7.34.1"),sQuery(id+"F0.wireOp",EDGE,"E7.34.2"),sQuery(id+"F0.wireOp",EDGE,"E7.34.3"),sQuery(id+"F0.wireOp",EDGE,"E7.34.4"),sQuery(id+"F0.wireOp",EDGE,"E7.34.5"),sQuery(id+"F0.wireOp",EDGE,"E7.35.0"),sQuery(id+"F0.wireOp",EDGE,"E7.35.1"),sQuery(id+"F0.wireOp",EDGE,"E7.35.2"),sQuery(id+"F0.wireOp",EDGE,"E7.35.3"),sQuery(id+"F0.wireOp",EDGE,"E7.35.4"),sQuery(id+"F0.wireOp",EDGE,"E7.35.5"),sQuery(id+"F0.wireOp",EDGE,"E7.36.0"),sQuery(id+"F0.wireOp",EDGE,"E7.36.1"),sQuery(id+"F0.wireOp",EDGE,"E7.36.2"),sQuery(id+"F0.wireOp",EDGE,"E7.36.3"),sQuery(id+"F0.wireOp",EDGE,"E7.36.4"),sQuery(id+"F0.wireOp",EDGE,"E7.36.5"),sQuery(id+"F0.wireOp",EDGE,"E7.37.0"),sQuery(id+"F0.wireOp",EDGE,"E7.37.1"),sQuery(id+"F0.wireOp",EDGE,"E7.37.2"),sQuery(id+"F0.wireOp",EDGE,"E7.37.3"),sQuery(id+"F0.wireOp",EDGE,"E7.37.4"),sQuery(id+"F0.wireOp",EDGE,"E7.37.5"),sQuery(id+"F0.wireOp",EDGE,"E7.38.0"),sQuery(id+"F0.wireOp",EDGE,"E7.38.1"),sQuery(id+"F0.wireOp",EDGE,"E7.38.2"),sQuery(id+"F0.wireOp",EDGE,"E7.38.3"),sQuery(id+"F0.wireOp",EDGE,"E7.38.4"),sQuery(id+"F0.wireOp",EDGE,"E7.38.5"),sQuery(id+"F0.wireOp",EDGE,"E7.39.0"),sQuery(id+"F0.wireOp",EDGE,"E7.39.1"),sQuery(id+"F0.wireOp",EDGE,"E7.39.2"),sQuery(id+"F0.wireOp",EDGE,"E7.39.3"),sQuery(id+"F0.wireOp",EDGE,"E7.39.4"),sQuery(id+"F0.wireOp",EDGE,"E7.39.5"),sQuery(id+"F0.wireOp",EDGE,"E7.40.0"),sQuery(id+"F0.wireOp",EDGE,"E7.40.1"),sQuery(id+"F0.wireOp",EDGE,"E7.40.2"),sQuery(id+"F0.wireOp",EDGE,"E7.40.3"),sQuery(id+"F0.wireOp",EDGE,"E7.40.4"),sQuery(id+"F0.wireOp",EDGE,"E7.40.5"),sQuery(id+"F0.wireOp",EDGE,"E7.41.0"),sQuery(id+"F0.wireOp",EDGE,"E7.41.1"),sQuery(id+"F0.wireOp",EDGE,"E7.41.2"),sQuery(id+"F0.wireOp",EDGE,"E7.41.3"),sQuery(id+"F0.wireOp",EDGE,"E7.41.4"),sQuery(id+"F0.wireOp",EDGE,"E7.41.5"),sQuery(id+"F0.wireOp",EDGE,"E7.42.0"),sQuery(id+"F0.wireOp",EDGE,"E7.42.1"),sQuery(id+"F0.wireOp",EDGE,"E7.42.2"),sQuery(id+"F0.wireOp",EDGE,"E7.42.3"),sQuery(id+"F0.wireOp",EDGE,"E7.42.4"),sQuery(id+"F0.wireOp",EDGE,"E7.42.5"),sQuery(id+"F0.wireOp",EDGE,"E7.43.0"),sQuery(id+"F0.wireOp",EDGE,"E7.43.1"),sQuery(id+"F0.wireOp",EDGE,"E7.43.2"),sQuery(id+"F0.wireOp",EDGE,"E7.43.3"),sQuery(id+"F0.wireOp",EDGE,"E7.43.4"),sQuery(id+"F0.wireOp",EDGE,"E7.43.5")])],"isStart":false})]}),makeQuery(id+"F2.opChamfer","BLEND_FACE",FACE,{"disambiguationData":[OSD([subQ0])]})],"blendedInto":[makeQuery(id+"F2.opChamfer","BLEND_FACE",FACE,{"disambiguationData":[OSD([subQ0])]})]});}
            var Q15;
            {var subQ0=sQuery(id+"F0.wireOp",EDGE,"E7.15.0");Q15=makeQuery(id+"F8.opChamfer","BLEND_EDGE",EDGE,{"blendedFrom":[makeQuery(id+"F2.opChamfer","BLEND_EDGE",EDGE,{"blendedFrom":[makeQuery(id+"F1.opExtrude","CAP_EDGE",EDGE,{"disambiguationData":[OSD([subQ0])],"isStart":false}),makeQuery(id+"F1.opExtrude","CAP_FACE",FACE,{"disambiguationData":[OSD([sQuery(id+"F0.wireOp",EDGE,"E1"),sQuery(id+"F0.wireOp",EDGE,"E2"),sQuery(id+"F0.wireOp",EDGE,"E3"),sQuery(id+"F0.wireOp",EDGE,"E4"),sQuery(id+"F0.wireOp",EDGE,"E5"),sQuery(id+"F0.wireOp",EDGE,"E6"),sQuery(id+"F0.wireOp",EDGE,"E7.1.0"),sQuery(id+"F0.wireOp",EDGE,"E7.1.1"),sQuery(id+"F0.wireOp",EDGE,"E7.1.2"),sQuery(id+"F0.wireOp",EDGE,"E7.1.3"),sQuery(id+"F0.wireOp",EDGE,"E7.1.4"),sQuery(id+"F0.wireOp",EDGE,"E7.1.5"),sQuery(id+"F0.wireOp",EDGE,"E7.2.0"),sQuery(id+"F0.wireOp",EDGE,"E7.2.1"),sQuery(id+"F0.wireOp",EDGE,"E7.2.2"),sQuery(id+"F0.wireOp",EDGE,"E7.2.3"),sQuery(id+"F0.wireOp",EDGE,"E7.2.4"),sQuery(id+"F0.wireOp",EDGE,"E7.2.5"),sQuery(id+"F0.wireOp",EDGE,"E7.3.0"),sQuery(id+"F0.wireOp",EDGE,"E7.3.1"),sQuery(id+"F0.wireOp",EDGE,"E7.3.2"),sQuery(id+"F0.wireOp",EDGE,"E7.3.3"),sQuery(id+"F0.wireOp",EDGE,"E7.3.4"),sQuery(id+"F0.wireOp",EDGE,"E7.3.5"),sQuery(id+"F0.wireOp",EDGE,"E7.4.0"),sQuery(id+"F0.wireOp",EDGE,"E7.4.1"),sQuery(id+"F0.wireOp",EDGE,"E7.4.2"),sQuery(id+"F0.wireOp",EDGE,"E7.4.3"),sQuery(id+"F0.wireOp",EDGE,"E7.4.4"),sQuery(id+"F0.wireOp",EDGE,"E7.4.5"),sQuery(id+"F0.wireOp",EDGE,"E7.5.0"),sQuery(id+"F0.wireOp",EDGE,"E7.5.1"),sQuery(id+"F0.wireOp",EDGE,"E7.5.2"),sQuery(id+"F0.wireOp",EDGE,"E7.5.3"),sQuery(id+"F0.wireOp",EDGE,"E7.5.4"),sQuery(id+"F0.wireOp",EDGE,"E7.5.5"),sQuery(id+"F0.wireOp",EDGE,"E7.6.0"),sQuery(id+"F0.wireOp",EDGE,"E7.6.1"),sQuery(id+"F0.wireOp",EDGE,"E7.6.2"),sQuery(id+"F0.wireOp",EDGE,"E7.6.3"),sQuery(id+"F0.wireOp",EDGE,"E7.6.4"),sQuery(id+"F0.wireOp",EDGE,"E7.6.5"),sQuery(id+"F0.wireOp",EDGE,"E7.7.0"),sQuery(id+"F0.wireOp",EDGE,"E7.7.1"),sQuery(id+"F0.wireOp",EDGE,"E7.7.2"),sQuery(id+"F0.wireOp",EDGE,"E7.7.3"),sQuery(id+"F0.wireOp",EDGE,"E7.7.4"),sQuery(id+"F0.wireOp",EDGE,"E7.7.5"),sQuery(id+"F0.wireOp",EDGE,"E7.8.0"),sQuery(id+"F0.wireOp",EDGE,"E7.8.1"),sQuery(id+"F0.wireOp",EDGE,"E7.8.2"),sQuery(id+"F0.wireOp",EDGE,"E7.8.3"),sQuery(id+"F0.wireOp",EDGE,"E7.8.4"),sQuery(id+"F0.wireOp",EDGE,"E7.8.5"),sQuery(id+"F0.wireOp",EDGE,"E7.9.0"),sQuery(id+"F0.wireOp",EDGE,"E7.9.1"),sQuery(id+"F0.wireOp",EDGE,"E7.9.2"),sQuery(id+"F0.wireOp",EDGE,"E7.9.3"),sQuery(id+"F0.wireOp",EDGE,"E7.9.4"),sQuery(id+"F0.wireOp",EDGE,"E7.9.5"),sQuery(id+"F0.wireOp",EDGE,"E7.10.0"),sQuery(id+"F0.wireOp",EDGE,"E7.10.1"),sQuery(id+"F0.wireOp",EDGE,"E7.10.2"),sQuery(id+"F0.wireOp",EDGE,"E7.10.3"),sQuery(id+"F0.wireOp",EDGE,"E7.10.4"),sQuery(id+"F0.wireOp",EDGE,"E7.10.5"),sQuery(id+"F0.wireOp",EDGE,"E7.11.0"),sQuery(id+"F0.wireOp",EDGE,"E7.11.1"),sQuery(id+"F0.wireOp",EDGE,"E7.11.2"),sQuery(id+"F0.wireOp",EDGE,"E7.11.3"),sQuery(id+"F0.wireOp",EDGE,"E7.11.4"),sQuery(id+"F0.wireOp",EDGE,"E7.11.5"),sQuery(id+"F0.wireOp",EDGE,"E7.12.0"),sQuery(id+"F0.wireOp",EDGE,"E7.12.1"),sQuery(id+"F0.wireOp",EDGE,"E7.12.2"),sQuery(id+"F0.wireOp",EDGE,"E7.12.3"),sQuery(id+"F0.wireOp",EDGE,"E7.12.4"),sQuery(id+"F0.wireOp",EDGE,"E7.12.5"),sQuery(id+"F0.wireOp",EDGE,"E7.13.0"),sQuery(id+"F0.wireOp",EDGE,"E7.13.1"),sQuery(id+"F0.wireOp",EDGE,"E7.13.2"),sQuery(id+"F0.wireOp",EDGE,"E7.13.3"),sQuery(id+"F0.wireOp",EDGE,"E7.13.4"),sQuery(id+"F0.wireOp",EDGE,"E7.13.5"),sQuery(id+"F0.wireOp",EDGE,"E7.14.0"),sQuery(id+"F0.wireOp",EDGE,"E7.14.1"),sQuery(id+"F0.wireOp",EDGE,"E7.14.2"),sQuery(id+"F0.wireOp",EDGE,"E7.14.3"),sQuery(id+"F0.wireOp",EDGE,"E7.14.4"),sQuery(id+"F0.wireOp",EDGE,"E7.14.5"),subQ0,sQuery(id+"F0.wireOp",EDGE,"E7.15.1"),sQuery(id+"F0.wireOp",EDGE,"E7.15.2"),sQuery(id+"F0.wireOp",EDGE,"E7.15.3"),sQuery(id+"F0.wireOp",EDGE,"E7.15.4"),sQuery(id+"F0.wireOp",EDGE,"E7.15.5"),sQuery(id+"F0.wireOp",EDGE,"E7.16.0"),sQuery(id+"F0.wireOp",EDGE,"E7.16.1"),sQuery(id+"F0.wireOp",EDGE,"E7.16.2"),sQuery(id+"F0.wireOp",EDGE,"E7.16.3"),sQuery(id+"F0.wireOp",EDGE,"E7.16.4"),sQuery(id+"F0.wireOp",EDGE,"E7.16.5"),sQuery(id+"F0.wireOp",EDGE,"E7.17.0"),sQuery(id+"F0.wireOp",EDGE,"E7.17.1"),sQuery(id+"F0.wireOp",EDGE,"E7.17.2"),sQuery(id+"F0.wireOp",EDGE,"E7.17.3"),sQuery(id+"F0.wireOp",EDGE,"E7.17.4"),sQuery(id+"F0.wireOp",EDGE,"E7.17.5"),sQuery(id+"F0.wireOp",EDGE,"E7.18.0"),sQuery(id+"F0.wireOp",EDGE,"E7.18.1"),sQuery(id+"F0.wireOp",EDGE,"E7.18.2"),sQuery(id+"F0.wireOp",EDGE,"E7.18.3"),sQuery(id+"F0.wireOp",EDGE,"E7.18.4"),sQuery(id+"F0.wireOp",EDGE,"E7.18.5"),sQuery(id+"F0.wireOp",EDGE,"E7.19.0"),sQuery(id+"F0.wireOp",EDGE,"E7.19.1"),sQuery(id+"F0.wireOp",EDGE,"E7.19.2"),sQuery(id+"F0.wireOp",EDGE,"E7.19.3"),sQuery(id+"F0.wireOp",EDGE,"E7.19.4"),sQuery(id+"F0.wireOp",EDGE,"E7.19.5"),sQuery(id+"F0.wireOp",EDGE,"E7.20.0"),sQuery(id+"F0.wireOp",EDGE,"E7.20.1"),sQuery(id+"F0.wireOp",EDGE,"E7.20.2"),sQuery(id+"F0.wireOp",EDGE,"E7.20.3"),sQuery(id+"F0.wireOp",EDGE,"E7.20.4"),sQuery(id+"F0.wireOp",EDGE,"E7.20.5"),sQuery(id+"F0.wireOp",EDGE,"E7.21.0"),sQuery(id+"F0.wireOp",EDGE,"E7.21.1"),sQuery(id+"F0.wireOp",EDGE,"E7.21.2"),sQuery(id+"F0.wireOp",EDGE,"E7.21.3"),sQuery(id+"F0.wireOp",EDGE,"E7.21.4"),sQuery(id+"F0.wireOp",EDGE,"E7.21.5"),sQuery(id+"F0.wireOp",EDGE,"E7.22.0"),sQuery(id+"F0.wireOp",EDGE,"E7.22.1"),sQuery(id+"F0.wireOp",EDGE,"E7.22.2"),sQuery(id+"F0.wireOp",EDGE,"E7.22.3"),sQuery(id+"F0.wireOp",EDGE,"E7.22.4"),sQuery(id+"F0.wireOp",EDGE,"E7.22.5"),sQuery(id+"F0.wireOp",EDGE,"E7.23.0"),sQuery(id+"F0.wireOp",EDGE,"E7.23.1"),sQuery(id+"F0.wireOp",EDGE,"E7.23.2"),sQuery(id+"F0.wireOp",EDGE,"E7.23.3"),sQuery(id+"F0.wireOp",EDGE,"E7.23.4"),sQuery(id+"F0.wireOp",EDGE,"E7.23.5"),sQuery(id+"F0.wireOp",EDGE,"E7.24.0"),sQuery(id+"F0.wireOp",EDGE,"E7.24.1"),sQuery(id+"F0.wireOp",EDGE,"E7.24.2"),sQuery(id+"F0.wireOp",EDGE,"E7.24.3"),sQuery(id+"F0.wireOp",EDGE,"E7.24.4"),sQuery(id+"F0.wireOp",EDGE,"E7.24.5"),sQuery(id+"F0.wireOp",EDGE,"E7.25.0"),sQuery(id+"F0.wireOp",EDGE,"E7.25.1"),sQuery(id+"F0.wireOp",EDGE,"E7.25.2"),sQuery(id+"F0.wireOp",EDGE,"E7.25.3"),sQuery(id+"F0.wireOp",EDGE,"E7.25.4"),sQuery(id+"F0.wireOp",EDGE,"E7.25.5"),sQuery(id+"F0.wireOp",EDGE,"E7.26.0"),sQuery(id+"F0.wireOp",EDGE,"E7.26.1"),sQuery(id+"F0.wireOp",EDGE,"E7.26.2"),sQuery(id+"F0.wireOp",EDGE,"E7.26.3"),sQuery(id+"F0.wireOp",EDGE,"E7.26.4"),sQuery(id+"F0.wireOp",EDGE,"E7.26.5"),sQuery(id+"F0.wireOp",EDGE,"E7.27.0"),sQuery(id+"F0.wireOp",EDGE,"E7.27.1"),sQuery(id+"F0.wireOp",EDGE,"E7.27.2"),sQuery(id+"F0.wireOp",EDGE,"E7.27.3"),sQuery(id+"F0.wireOp",EDGE,"E7.27.4"),sQuery(id+"F0.wireOp",EDGE,"E7.27.5"),sQuery(id+"F0.wireOp",EDGE,"E7.28.0"),sQuery(id+"F0.wireOp",EDGE,"E7.28.1"),sQuery(id+"F0.wireOp",EDGE,"E7.28.2"),sQuery(id+"F0.wireOp",EDGE,"E7.28.3"),sQuery(id+"F0.wireOp",EDGE,"E7.28.4"),sQuery(id+"F0.wireOp",EDGE,"E7.28.5"),sQuery(id+"F0.wireOp",EDGE,"E7.29.0"),sQuery(id+"F0.wireOp",EDGE,"E7.29.1"),sQuery(id+"F0.wireOp",EDGE,"E7.29.2"),sQuery(id+"F0.wireOp",EDGE,"E7.29.3"),sQuery(id+"F0.wireOp",EDGE,"E7.29.4"),sQuery(id+"F0.wireOp",EDGE,"E7.29.5"),sQuery(id+"F0.wireOp",EDGE,"E7.30.0"),sQuery(id+"F0.wireOp",EDGE,"E7.30.1"),sQuery(id+"F0.wireOp",EDGE,"E7.30.2"),sQuery(id+"F0.wireOp",EDGE,"E7.30.3"),sQuery(id+"F0.wireOp",EDGE,"E7.30.4"),sQuery(id+"F0.wireOp",EDGE,"E7.30.5"),sQuery(id+"F0.wireOp",EDGE,"E7.31.0"),sQuery(id+"F0.wireOp",EDGE,"E7.31.1"),sQuery(id+"F0.wireOp",EDGE,"E7.31.2"),sQuery(id+"F0.wireOp",EDGE,"E7.31.3"),sQuery(id+"F0.wireOp",EDGE,"E7.31.4"),sQuery(id+"F0.wireOp",EDGE,"E7.31.5"),sQuery(id+"F0.wireOp",EDGE,"E7.32.0"),sQuery(id+"F0.wireOp",EDGE,"E7.32.1"),sQuery(id+"F0.wireOp",EDGE,"E7.32.2"),sQuery(id+"F0.wireOp",EDGE,"E7.32.3"),sQuery(id+"F0.wireOp",EDGE,"E7.32.4"),sQuery(id+"F0.wireOp",EDGE,"E7.32.5"),sQuery(id+"F0.wireOp",EDGE,"E7.33.0"),sQuery(id+"F0.wireOp",EDGE,"E7.33.1"),sQuery(id+"F0.wireOp",EDGE,"E7.33.2"),sQuery(id+"F0.wireOp",EDGE,"E7.33.3"),sQuery(id+"F0.wireOp",EDGE,"E7.33.4"),sQuery(id+"F0.wireOp",EDGE,"E7.33.5"),sQuery(id+"F0.wireOp",EDGE,"E7.34.0"),sQuery(id+"F0.wireOp",EDGE,"E7.34.1"),sQuery(id+"F0.wireOp",EDGE,"E7.34.2"),sQuery(id+"F0.wireOp",EDGE,"E7.34.3"),sQuery(id+"F0.wireOp",EDGE,"E7.34.4"),sQuery(id+"F0.wireOp",EDGE,"E7.34.5"),sQuery(id+"F0.wireOp",EDGE,"E7.35.0"),sQuery(id+"F0.wireOp",EDGE,"E7.35.1"),sQuery(id+"F0.wireOp",EDGE,"E7.35.2"),sQuery(id+"F0.wireOp",EDGE,"E7.35.3"),sQuery(id+"F0.wireOp",EDGE,"E7.35.4"),sQuery(id+"F0.wireOp",EDGE,"E7.35.5"),sQuery(id+"F0.wireOp",EDGE,"E7.36.0"),sQuery(id+"F0.wireOp",EDGE,"E7.36.1"),sQuery(id+"F0.wireOp",EDGE,"E7.36.2"),sQuery(id+"F0.wireOp",EDGE,"E7.36.3"),sQuery(id+"F0.wireOp",EDGE,"E7.36.4"),sQuery(id+"F0.wireOp",EDGE,"E7.36.5"),sQuery(id+"F0.wireOp",EDGE,"E7.37.0"),sQuery(id+"F0.wireOp",EDGE,"E7.37.1"),sQuery(id+"F0.wireOp",EDGE,"E7.37.2"),sQuery(id+"F0.wireOp",EDGE,"E7.37.3"),sQuery(id+"F0.wireOp",EDGE,"E7.37.4"),sQuery(id+"F0.wireOp",EDGE,"E7.37.5"),sQuery(id+"F0.wireOp",EDGE,"E7.38.0"),sQuery(id+"F0.wireOp",EDGE,"E7.38.1"),sQuery(id+"F0.wireOp",EDGE,"E7.38.2"),sQuery(id+"F0.wireOp",EDGE,"E7.38.3"),sQuery(id+"F0.wireOp",EDGE,"E7.38.4"),sQuery(id+"F0.wireOp",EDGE,"E7.38.5"),sQuery(id+"F0.wireOp",EDGE,"E7.39.0"),sQuery(id+"F0.wireOp",EDGE,"E7.39.1"),sQuery(id+"F0.wireOp",EDGE,"E7.39.2"),sQuery(id+"F0.wireOp",EDGE,"E7.39.3"),sQuery(id+"F0.wireOp",EDGE,"E7.39.4"),sQuery(id+"F0.wireOp",EDGE,"E7.39.5"),sQuery(id+"F0.wireOp",EDGE,"E7.40.0"),sQuery(id+"F0.wireOp",EDGE,"E7.40.1"),sQuery(id+"F0.wireOp",EDGE,"E7.40.2"),sQuery(id+"F0.wireOp",EDGE,"E7.40.3"),sQuery(id+"F0.wireOp",EDGE,"E7.40.4"),sQuery(id+"F0.wireOp",EDGE,"E7.40.5"),sQuery(id+"F0.wireOp",EDGE,"E7.41.0"),sQuery(id+"F0.wireOp",EDGE,"E7.41.1"),sQuery(id+"F0.wireOp",EDGE,"E7.41.2"),sQuery(id+"F0.wireOp",EDGE,"E7.41.3"),sQuery(id+"F0.wireOp",EDGE,"E7.41.4"),sQuery(id+"F0.wireOp",EDGE,"E7.41.5"),sQuery(id+"F0.wireOp",EDGE,"E7.42.0"),sQuery(id+"F0.wireOp",EDGE,"E7.42.1"),sQuery(id+"F0.wireOp",EDGE,"E7.42.2"),sQuery(id+"F0.wireOp",EDGE,"E7.42.3"),sQuery(id+"F0.wireOp",EDGE,"E7.42.4"),sQuery(id+"F0.wireOp",EDGE,"E7.42.5"),sQuery(id+"F0.wireOp",EDGE,"E7.43.0"),sQuery(id+"F0.wireOp",EDGE,"E7.43.1"),sQuery(id+"F0.wireOp",EDGE,"E7.43.2"),sQuery(id+"F0.wireOp",EDGE,"E7.43.3"),sQuery(id+"F0.wireOp",EDGE,"E7.43.4"),sQuery(id+"F0.wireOp",EDGE,"E7.43.5")])],"isStart":false})],"blendedInto":[makeQuery(id+"F1.opExtrude","CAP_FACE",FACE,{"disambiguationData":[OSD([sQuery(id+"F0.wireOp",EDGE,"E1"),sQuery(id+"F0.wireOp",EDGE,"E2"),sQuery(id+"F0.wireOp",EDGE,"E3"),sQuery(id+"F0.wireOp",EDGE,"E4"),sQuery(id+"F0.wireOp",EDGE,"E5"),sQuery(id+"F0.wireOp",EDGE,"E6"),sQuery(id+"F0.wireOp",EDGE,"E7.1.0"),sQuery(id+"F0.wireOp",EDGE,"E7.1.1"),sQuery(id+"F0.wireOp",EDGE,"E7.1.2"),sQuery(id+"F0.wireOp",EDGE,"E7.1.3"),sQuery(id+"F0.wireOp",EDGE,"E7.1.4"),sQuery(id+"F0.wireOp",EDGE,"E7.1.5"),sQuery(id+"F0.wireOp",EDGE,"E7.2.0"),sQuery(id+"F0.wireOp",EDGE,"E7.2.1"),sQuery(id+"F0.wireOp",EDGE,"E7.2.2"),sQuery(id+"F0.wireOp",EDGE,"E7.2.3"),sQuery(id+"F0.wireOp",EDGE,"E7.2.4"),sQuery(id+"F0.wireOp",EDGE,"E7.2.5"),sQuery(id+"F0.wireOp",EDGE,"E7.3.0"),sQuery(id+"F0.wireOp",EDGE,"E7.3.1"),sQuery(id+"F0.wireOp",EDGE,"E7.3.2"),sQuery(id+"F0.wireOp",EDGE,"E7.3.3"),sQuery(id+"F0.wireOp",EDGE,"E7.3.4"),sQuery(id+"F0.wireOp",EDGE,"E7.3.5"),sQuery(id+"F0.wireOp",EDGE,"E7.4.0"),sQuery(id+"F0.wireOp",EDGE,"E7.4.1"),sQuery(id+"F0.wireOp",EDGE,"E7.4.2"),sQuery(id+"F0.wireOp",EDGE,"E7.4.3"),sQuery(id+"F0.wireOp",EDGE,"E7.4.4"),sQuery(id+"F0.wireOp",EDGE,"E7.4.5"),sQuery(id+"F0.wireOp",EDGE,"E7.5.0"),sQuery(id+"F0.wireOp",EDGE,"E7.5.1"),sQuery(id+"F0.wireOp",EDGE,"E7.5.2"),sQuery(id+"F0.wireOp",EDGE,"E7.5.3"),sQuery(id+"F0.wireOp",EDGE,"E7.5.4"),sQuery(id+"F0.wireOp",EDGE,"E7.5.5"),sQuery(id+"F0.wireOp",EDGE,"E7.6.0"),sQuery(id+"F0.wireOp",EDGE,"E7.6.1"),sQuery(id+"F0.wireOp",EDGE,"E7.6.2"),sQuery(id+"F0.wireOp",EDGE,"E7.6.3"),sQuery(id+"F0.wireOp",EDGE,"E7.6.4"),sQuery(id+"F0.wireOp",EDGE,"E7.6.5"),sQuery(id+"F0.wireOp",EDGE,"E7.7.0"),sQuery(id+"F0.wireOp",EDGE,"E7.7.1"),sQuery(id+"F0.wireOp",EDGE,"E7.7.2"),sQuery(id+"F0.wireOp",EDGE,"E7.7.3"),sQuery(id+"F0.wireOp",EDGE,"E7.7.4"),sQuery(id+"F0.wireOp",EDGE,"E7.7.5"),sQuery(id+"F0.wireOp",EDGE,"E7.8.0"),sQuery(id+"F0.wireOp",EDGE,"E7.8.1"),sQuery(id+"F0.wireOp",EDGE,"E7.8.2"),sQuery(id+"F0.wireOp",EDGE,"E7.8.3"),sQuery(id+"F0.wireOp",EDGE,"E7.8.4"),sQuery(id+"F0.wireOp",EDGE,"E7.8.5"),sQuery(id+"F0.wireOp",EDGE,"E7.9.0"),sQuery(id+"F0.wireOp",EDGE,"E7.9.1"),sQuery(id+"F0.wireOp",EDGE,"E7.9.2"),sQuery(id+"F0.wireOp",EDGE,"E7.9.3"),sQuery(id+"F0.wireOp",EDGE,"E7.9.4"),sQuery(id+"F0.wireOp",EDGE,"E7.9.5"),sQuery(id+"F0.wireOp",EDGE,"E7.10.0"),sQuery(id+"F0.wireOp",EDGE,"E7.10.1"),sQuery(id+"F0.wireOp",EDGE,"E7.10.2"),sQuery(id+"F0.wireOp",EDGE,"E7.10.3"),sQuery(id+"F0.wireOp",EDGE,"E7.10.4"),sQuery(id+"F0.wireOp",EDGE,"E7.10.5"),sQuery(id+"F0.wireOp",EDGE,"E7.11.0"),sQuery(id+"F0.wireOp",EDGE,"E7.11.1"),sQuery(id+"F0.wireOp",EDGE,"E7.11.2"),sQuery(id+"F0.wireOp",EDGE,"E7.11.3"),sQuery(id+"F0.wireOp",EDGE,"E7.11.4"),sQuery(id+"F0.wireOp",EDGE,"E7.11.5"),sQuery(id+"F0.wireOp",EDGE,"E7.12.0"),sQuery(id+"F0.wireOp",EDGE,"E7.12.1"),sQuery(id+"F0.wireOp",EDGE,"E7.12.2"),sQuery(id+"F0.wireOp",EDGE,"E7.12.3"),sQuery(id+"F0.wireOp",EDGE,"E7.12.4"),sQuery(id+"F0.wireOp",EDGE,"E7.12.5"),sQuery(id+"F0.wireOp",EDGE,"E7.13.0"),sQuery(id+"F0.wireOp",EDGE,"E7.13.1"),sQuery(id+"F0.wireOp",EDGE,"E7.13.2"),sQuery(id+"F0.wireOp",EDGE,"E7.13.3"),sQuery(id+"F0.wireOp",EDGE,"E7.13.4"),sQuery(id+"F0.wireOp",EDGE,"E7.13.5"),sQuery(id+"F0.wireOp",EDGE,"E7.14.0"),sQuery(id+"F0.wireOp",EDGE,"E7.14.1"),sQuery(id+"F0.wireOp",EDGE,"E7.14.2"),sQuery(id+"F0.wireOp",EDGE,"E7.14.3"),sQuery(id+"F0.wireOp",EDGE,"E7.14.4"),sQuery(id+"F0.wireOp",EDGE,"E7.14.5"),subQ0,sQuery(id+"F0.wireOp",EDGE,"E7.15.1"),sQuery(id+"F0.wireOp",EDGE,"E7.15.2"),sQuery(id+"F0.wireOp",EDGE,"E7.15.3"),sQuery(id+"F0.wireOp",EDGE,"E7.15.4"),sQuery(id+"F0.wireOp",EDGE,"E7.15.5"),sQuery(id+"F0.wireOp",EDGE,"E7.16.0"),sQuery(id+"F0.wireOp",EDGE,"E7.16.1"),sQuery(id+"F0.wireOp",EDGE,"E7.16.2"),sQuery(id+"F0.wireOp",EDGE,"E7.16.3"),sQuery(id+"F0.wireOp",EDGE,"E7.16.4"),sQuery(id+"F0.wireOp",EDGE,"E7.16.5"),sQuery(id+"F0.wireOp",EDGE,"E7.17.0"),sQuery(id+"F0.wireOp",EDGE,"E7.17.1"),sQuery(id+"F0.wireOp",EDGE,"E7.17.2"),sQuery(id+"F0.wireOp",EDGE,"E7.17.3"),sQuery(id+"F0.wireOp",EDGE,"E7.17.4"),sQuery(id+"F0.wireOp",EDGE,"E7.17.5"),sQuery(id+"F0.wireOp",EDGE,"E7.18.0"),sQuery(id+"F0.wireOp",EDGE,"E7.18.1"),sQuery(id+"F0.wireOp",EDGE,"E7.18.2"),sQuery(id+"F0.wireOp",EDGE,"E7.18.3"),sQuery(id+"F0.wireOp",EDGE,"E7.18.4"),sQuery(id+"F0.wireOp",EDGE,"E7.18.5"),sQuery(id+"F0.wireOp",EDGE,"E7.19.0"),sQuery(id+"F0.wireOp",EDGE,"E7.19.1"),sQuery(id+"F0.wireOp",EDGE,"E7.19.2"),sQuery(id+"F0.wireOp",EDGE,"E7.19.3"),sQuery(id+"F0.wireOp",EDGE,"E7.19.4"),sQuery(id+"F0.wireOp",EDGE,"E7.19.5"),sQuery(id+"F0.wireOp",EDGE,"E7.20.0"),sQuery(id+"F0.wireOp",EDGE,"E7.20.1"),sQuery(id+"F0.wireOp",EDGE,"E7.20.2"),sQuery(id+"F0.wireOp",EDGE,"E7.20.3"),sQuery(id+"F0.wireOp",EDGE,"E7.20.4"),sQuery(id+"F0.wireOp",EDGE,"E7.20.5"),sQuery(id+"F0.wireOp",EDGE,"E7.21.0"),sQuery(id+"F0.wireOp",EDGE,"E7.21.1"),sQuery(id+"F0.wireOp",EDGE,"E7.21.2"),sQuery(id+"F0.wireOp",EDGE,"E7.21.3"),sQuery(id+"F0.wireOp",EDGE,"E7.21.4"),sQuery(id+"F0.wireOp",EDGE,"E7.21.5"),sQuery(id+"F0.wireOp",EDGE,"E7.22.0"),sQuery(id+"F0.wireOp",EDGE,"E7.22.1"),sQuery(id+"F0.wireOp",EDGE,"E7.22.2"),sQuery(id+"F0.wireOp",EDGE,"E7.22.3"),sQuery(id+"F0.wireOp",EDGE,"E7.22.4"),sQuery(id+"F0.wireOp",EDGE,"E7.22.5"),sQuery(id+"F0.wireOp",EDGE,"E7.23.0"),sQuery(id+"F0.wireOp",EDGE,"E7.23.1"),sQuery(id+"F0.wireOp",EDGE,"E7.23.2"),sQuery(id+"F0.wireOp",EDGE,"E7.23.3"),sQuery(id+"F0.wireOp",EDGE,"E7.23.4"),sQuery(id+"F0.wireOp",EDGE,"E7.23.5"),sQuery(id+"F0.wireOp",EDGE,"E7.24.0"),sQuery(id+"F0.wireOp",EDGE,"E7.24.1"),sQuery(id+"F0.wireOp",EDGE,"E7.24.2"),sQuery(id+"F0.wireOp",EDGE,"E7.24.3"),sQuery(id+"F0.wireOp",EDGE,"E7.24.4"),sQuery(id+"F0.wireOp",EDGE,"E7.24.5"),sQuery(id+"F0.wireOp",EDGE,"E7.25.0"),sQuery(id+"F0.wireOp",EDGE,"E7.25.1"),sQuery(id+"F0.wireOp",EDGE,"E7.25.2"),sQuery(id+"F0.wireOp",EDGE,"E7.25.3"),sQuery(id+"F0.wireOp",EDGE,"E7.25.4"),sQuery(id+"F0.wireOp",EDGE,"E7.25.5"),sQuery(id+"F0.wireOp",EDGE,"E7.26.0"),sQuery(id+"F0.wireOp",EDGE,"E7.26.1"),sQuery(id+"F0.wireOp",EDGE,"E7.26.2"),sQuery(id+"F0.wireOp",EDGE,"E7.26.3"),sQuery(id+"F0.wireOp",EDGE,"E7.26.4"),sQuery(id+"F0.wireOp",EDGE,"E7.26.5"),sQuery(id+"F0.wireOp",EDGE,"E7.27.0"),sQuery(id+"F0.wireOp",EDGE,"E7.27.1"),sQuery(id+"F0.wireOp",EDGE,"E7.27.2"),sQuery(id+"F0.wireOp",EDGE,"E7.27.3"),sQuery(id+"F0.wireOp",EDGE,"E7.27.4"),sQuery(id+"F0.wireOp",EDGE,"E7.27.5"),sQuery(id+"F0.wireOp",EDGE,"E7.28.0"),sQuery(id+"F0.wireOp",EDGE,"E7.28.1"),sQuery(id+"F0.wireOp",EDGE,"E7.28.2"),sQuery(id+"F0.wireOp",EDGE,"E7.28.3"),sQuery(id+"F0.wireOp",EDGE,"E7.28.4"),sQuery(id+"F0.wireOp",EDGE,"E7.28.5"),sQuery(id+"F0.wireOp",EDGE,"E7.29.0"),sQuery(id+"F0.wireOp",EDGE,"E7.29.1"),sQuery(id+"F0.wireOp",EDGE,"E7.29.2"),sQuery(id+"F0.wireOp",EDGE,"E7.29.3"),sQuery(id+"F0.wireOp",EDGE,"E7.29.4"),sQuery(id+"F0.wireOp",EDGE,"E7.29.5"),sQuery(id+"F0.wireOp",EDGE,"E7.30.0"),sQuery(id+"F0.wireOp",EDGE,"E7.30.1"),sQuery(id+"F0.wireOp",EDGE,"E7.30.2"),sQuery(id+"F0.wireOp",EDGE,"E7.30.3"),sQuery(id+"F0.wireOp",EDGE,"E7.30.4"),sQuery(id+"F0.wireOp",EDGE,"E7.30.5"),sQuery(id+"F0.wireOp",EDGE,"E7.31.0"),sQuery(id+"F0.wireOp",EDGE,"E7.31.1"),sQuery(id+"F0.wireOp",EDGE,"E7.31.2"),sQuery(id+"F0.wireOp",EDGE,"E7.31.3"),sQuery(id+"F0.wireOp",EDGE,"E7.31.4"),sQuery(id+"F0.wireOp",EDGE,"E7.31.5"),sQuery(id+"F0.wireOp",EDGE,"E7.32.0"),sQuery(id+"F0.wireOp",EDGE,"E7.32.1"),sQuery(id+"F0.wireOp",EDGE,"E7.32.2"),sQuery(id+"F0.wireOp",EDGE,"E7.32.3"),sQuery(id+"F0.wireOp",EDGE,"E7.32.4"),sQuery(id+"F0.wireOp",EDGE,"E7.32.5"),sQuery(id+"F0.wireOp",EDGE,"E7.33.0"),sQuery(id+"F0.wireOp",EDGE,"E7.33.1"),sQuery(id+"F0.wireOp",EDGE,"E7.33.2"),sQuery(id+"F0.wireOp",EDGE,"E7.33.3"),sQuery(id+"F0.wireOp",EDGE,"E7.33.4"),sQuery(id+"F0.wireOp",EDGE,"E7.33.5"),sQuery(id+"F0.wireOp",EDGE,"E7.34.0"),sQuery(id+"F0.wireOp",EDGE,"E7.34.1"),sQuery(id+"F0.wireOp",EDGE,"E7.34.2"),sQuery(id+"F0.wireOp",EDGE,"E7.34.3"),sQuery(id+"F0.wireOp",EDGE,"E7.34.4"),sQuery(id+"F0.wireOp",EDGE,"E7.34.5"),sQuery(id+"F0.wireOp",EDGE,"E7.35.0"),sQuery(id+"F0.wireOp",EDGE,"E7.35.1"),sQuery(id+"F0.wireOp",EDGE,"E7.35.2"),sQuery(id+"F0.wireOp",EDGE,"E7.35.3"),sQuery(id+"F0.wireOp",EDGE,"E7.35.4"),sQuery(id+"F0.wireOp",EDGE,"E7.35.5"),sQuery(id+"F0.wireOp",EDGE,"E7.36.0"),sQuery(id+"F0.wireOp",EDGE,"E7.36.1"),sQuery(id+"F0.wireOp",EDGE,"E7.36.2"),sQuery(id+"F0.wireOp",EDGE,"E7.36.3"),sQuery(id+"F0.wireOp",EDGE,"E7.36.4"),sQuery(id+"F0.wireOp",EDGE,"E7.36.5"),sQuery(id+"F0.wireOp",EDGE,"E7.37.0"),sQuery(id+"F0.wireOp",EDGE,"E7.37.1"),sQuery(id+"F0.wireOp",EDGE,"E7.37.2"),sQuery(id+"F0.wireOp",EDGE,"E7.37.3"),sQuery(id+"F0.wireOp",EDGE,"E7.37.4"),sQuery(id+"F0.wireOp",EDGE,"E7.37.5"),sQuery(id+"F0.wireOp",EDGE,"E7.38.0"),sQuery(id+"F0.wireOp",EDGE,"E7.38.1"),sQuery(id+"F0.wireOp",EDGE,"E7.38.2"),sQuery(id+"F0.wireOp",EDGE,"E7.38.3"),sQuery(id+"F0.wireOp",EDGE,"E7.38.4"),sQuery(id+"F0.wireOp",EDGE,"E7.38.5"),sQuery(id+"F0.wireOp",EDGE,"E7.39.0"),sQuery(id+"F0.wireOp",EDGE,"E7.39.1"),sQuery(id+"F0.wireOp",EDGE,"E7.39.2"),sQuery(id+"F0.wireOp",EDGE,"E7.39.3"),sQuery(id+"F0.wireOp",EDGE,"E7.39.4"),sQuery(id+"F0.wireOp",EDGE,"E7.39.5"),sQuery(id+"F0.wireOp",EDGE,"E7.40.0"),sQuery(id+"F0.wireOp",EDGE,"E7.40.1"),sQuery(id+"F0.wireOp",EDGE,"E7.40.2"),sQuery(id+"F0.wireOp",EDGE,"E7.40.3"),sQuery(id+"F0.wireOp",EDGE,"E7.40.4"),sQuery(id+"F0.wireOp",EDGE,"E7.40.5"),sQuery(id+"F0.wireOp",EDGE,"E7.41.0"),sQuery(id+"F0.wireOp",EDGE,"E7.41.1"),sQuery(id+"F0.wireOp",EDGE,"E7.41.2"),sQuery(id+"F0.wireOp",EDGE,"E7.41.3"),sQuery(id+"F0.wireOp",EDGE,"E7.41.4"),sQuery(id+"F0.wireOp",EDGE,"E7.41.5"),sQuery(id+"F0.wireOp",EDGE,"E7.42.0"),sQuery(id+"F0.wireOp",EDGE,"E7.42.1"),sQuery(id+"F0.wireOp",EDGE,"E7.42.2"),sQuery(id+"F0.wireOp",EDGE,"E7.42.3"),sQuery(id+"F0.wireOp",EDGE,"E7.42.4"),sQuery(id+"F0.wireOp",EDGE,"E7.42.5"),sQuery(id+"F0.wireOp",EDGE,"E7.43.0"),sQuery(id+"F0.wireOp",EDGE,"E7.43.1"),sQuery(id+"F0.wireOp",EDGE,"E7.43.2"),sQuery(id+"F0.wireOp",EDGE,"E7.43.3"),sQuery(id+"F0.wireOp",EDGE,"E7.43.4"),sQuery(id+"F0.wireOp",EDGE,"E7.43.5")])],"isStart":false})]}),makeQuery(id+"F2.opChamfer","BLEND_FACE",FACE,{"disambiguationData":[OSD([subQ0])]})],"blendedInto":[makeQuery(id+"F2.opChamfer","BLEND_FACE",FACE,{"disambiguationData":[OSD([subQ0])]})]});}
            var Q16;
            {var subQ0=sQuery(id+"F0.wireOp",EDGE,"E7.13.0");Q16=makeQuery(id+"F8.opChamfer","BLEND_EDGE",EDGE,{"blendedFrom":[makeQuery(id+"F2.opChamfer","BLEND_EDGE",EDGE,{"blendedFrom":[makeQuery(id+"F1.opExtrude","CAP_EDGE",EDGE,{"disambiguationData":[OSD([subQ0])],"isStart":false}),makeQuery(id+"F1.opExtrude","CAP_FACE",FACE,{"disambiguationData":[OSD([sQuery(id+"F0.wireOp",EDGE,"E1"),sQuery(id+"F0.wireOp",EDGE,"E2"),sQuery(id+"F0.wireOp",EDGE,"E3"),sQuery(id+"F0.wireOp",EDGE,"E4"),sQuery(id+"F0.wireOp",EDGE,"E5"),sQuery(id+"F0.wireOp",EDGE,"E6"),sQuery(id+"F0.wireOp",EDGE,"E7.1.0"),sQuery(id+"F0.wireOp",EDGE,"E7.1.1"),sQuery(id+"F0.wireOp",EDGE,"E7.1.2"),sQuery(id+"F0.wireOp",EDGE,"E7.1.3"),sQuery(id+"F0.wireOp",EDGE,"E7.1.4"),sQuery(id+"F0.wireOp",EDGE,"E7.1.5"),sQuery(id+"F0.wireOp",EDGE,"E7.2.0"),sQuery(id+"F0.wireOp",EDGE,"E7.2.1"),sQuery(id+"F0.wireOp",EDGE,"E7.2.2"),sQuery(id+"F0.wireOp",EDGE,"E7.2.3"),sQuery(id+"F0.wireOp",EDGE,"E7.2.4"),sQuery(id+"F0.wireOp",EDGE,"E7.2.5"),sQuery(id+"F0.wireOp",EDGE,"E7.3.0"),sQuery(id+"F0.wireOp",EDGE,"E7.3.1"),sQuery(id+"F0.wireOp",EDGE,"E7.3.2"),sQuery(id+"F0.wireOp",EDGE,"E7.3.3"),sQuery(id+"F0.wireOp",EDGE,"E7.3.4"),sQuery(id+"F0.wireOp",EDGE,"E7.3.5"),sQuery(id+"F0.wireOp",EDGE,"E7.4.0"),sQuery(id+"F0.wireOp",EDGE,"E7.4.1"),sQuery(id+"F0.wireOp",EDGE,"E7.4.2"),sQuery(id+"F0.wireOp",EDGE,"E7.4.3"),sQuery(id+"F0.wireOp",EDGE,"E7.4.4"),sQuery(id+"F0.wireOp",EDGE,"E7.4.5"),sQuery(id+"F0.wireOp",EDGE,"E7.5.0"),sQuery(id+"F0.wireOp",EDGE,"E7.5.1"),sQuery(id+"F0.wireOp",EDGE,"E7.5.2"),sQuery(id+"F0.wireOp",EDGE,"E7.5.3"),sQuery(id+"F0.wireOp",EDGE,"E7.5.4"),sQuery(id+"F0.wireOp",EDGE,"E7.5.5"),sQuery(id+"F0.wireOp",EDGE,"E7.6.0"),sQuery(id+"F0.wireOp",EDGE,"E7.6.1"),sQuery(id+"F0.wireOp",EDGE,"E7.6.2"),sQuery(id+"F0.wireOp",EDGE,"E7.6.3"),sQuery(id+"F0.wireOp",EDGE,"E7.6.4"),sQuery(id+"F0.wireOp",EDGE,"E7.6.5"),sQuery(id+"F0.wireOp",EDGE,"E7.7.0"),sQuery(id+"F0.wireOp",EDGE,"E7.7.1"),sQuery(id+"F0.wireOp",EDGE,"E7.7.2"),sQuery(id+"F0.wireOp",EDGE,"E7.7.3"),sQuery(id+"F0.wireOp",EDGE,"E7.7.4"),sQuery(id+"F0.wireOp",EDGE,"E7.7.5"),sQuery(id+"F0.wireOp",EDGE,"E7.8.0"),sQuery(id+"F0.wireOp",EDGE,"E7.8.1"),sQuery(id+"F0.wireOp",EDGE,"E7.8.2"),sQuery(id+"F0.wireOp",EDGE,"E7.8.3"),sQuery(id+"F0.wireOp",EDGE,"E7.8.4"),sQuery(id+"F0.wireOp",EDGE,"E7.8.5"),sQuery(id+"F0.wireOp",EDGE,"E7.9.0"),sQuery(id+"F0.wireOp",EDGE,"E7.9.1"),sQuery(id+"F0.wireOp",EDGE,"E7.9.2"),sQuery(id+"F0.wireOp",EDGE,"E7.9.3"),sQuery(id+"F0.wireOp",EDGE,"E7.9.4"),sQuery(id+"F0.wireOp",EDGE,"E7.9.5"),sQuery(id+"F0.wireOp",EDGE,"E7.10.0"),sQuery(id+"F0.wireOp",EDGE,"E7.10.1"),sQuery(id+"F0.wireOp",EDGE,"E7.10.2"),sQuery(id+"F0.wireOp",EDGE,"E7.10.3"),sQuery(id+"F0.wireOp",EDGE,"E7.10.4"),sQuery(id+"F0.wireOp",EDGE,"E7.10.5"),sQuery(id+"F0.wireOp",EDGE,"E7.11.0"),sQuery(id+"F0.wireOp",EDGE,"E7.11.1"),sQuery(id+"F0.wireOp",EDGE,"E7.11.2"),sQuery(id+"F0.wireOp",EDGE,"E7.11.3"),sQuery(id+"F0.wireOp",EDGE,"E7.11.4"),sQuery(id+"F0.wireOp",EDGE,"E7.11.5"),sQuery(id+"F0.wireOp",EDGE,"E7.12.0"),sQuery(id+"F0.wireOp",EDGE,"E7.12.1"),sQuery(id+"F0.wireOp",EDGE,"E7.12.2"),sQuery(id+"F0.wireOp",EDGE,"E7.12.3"),sQuery(id+"F0.wireOp",EDGE,"E7.12.4"),sQuery(id+"F0.wireOp",EDGE,"E7.12.5"),subQ0,sQuery(id+"F0.wireOp",EDGE,"E7.13.1"),sQuery(id+"F0.wireOp",EDGE,"E7.13.2"),sQuery(id+"F0.wireOp",EDGE,"E7.13.3"),sQuery(id+"F0.wireOp",EDGE,"E7.13.4"),sQuery(id+"F0.wireOp",EDGE,"E7.13.5"),sQuery(id+"F0.wireOp",EDGE,"E7.14.0"),sQuery(id+"F0.wireOp",EDGE,"E7.14.1"),sQuery(id+"F0.wireOp",EDGE,"E7.14.2"),sQuery(id+"F0.wireOp",EDGE,"E7.14.3"),sQuery(id+"F0.wireOp",EDGE,"E7.14.4"),sQuery(id+"F0.wireOp",EDGE,"E7.14.5"),sQuery(id+"F0.wireOp",EDGE,"E7.15.0"),sQuery(id+"F0.wireOp",EDGE,"E7.15.1"),sQuery(id+"F0.wireOp",EDGE,"E7.15.2"),sQuery(id+"F0.wireOp",EDGE,"E7.15.3"),sQuery(id+"F0.wireOp",EDGE,"E7.15.4"),sQuery(id+"F0.wireOp",EDGE,"E7.15.5"),sQuery(id+"F0.wireOp",EDGE,"E7.16.0"),sQuery(id+"F0.wireOp",EDGE,"E7.16.1"),sQuery(id+"F0.wireOp",EDGE,"E7.16.2"),sQuery(id+"F0.wireOp",EDGE,"E7.16.3"),sQuery(id+"F0.wireOp",EDGE,"E7.16.4"),sQuery(id+"F0.wireOp",EDGE,"E7.16.5"),sQuery(id+"F0.wireOp",EDGE,"E7.17.0"),sQuery(id+"F0.wireOp",EDGE,"E7.17.1"),sQuery(id+"F0.wireOp",EDGE,"E7.17.2"),sQuery(id+"F0.wireOp",EDGE,"E7.17.3"),sQuery(id+"F0.wireOp",EDGE,"E7.17.4"),sQuery(id+"F0.wireOp",EDGE,"E7.17.5"),sQuery(id+"F0.wireOp",EDGE,"E7.18.0"),sQuery(id+"F0.wireOp",EDGE,"E7.18.1"),sQuery(id+"F0.wireOp",EDGE,"E7.18.2"),sQuery(id+"F0.wireOp",EDGE,"E7.18.3"),sQuery(id+"F0.wireOp",EDGE,"E7.18.4"),sQuery(id+"F0.wireOp",EDGE,"E7.18.5"),sQuery(id+"F0.wireOp",EDGE,"E7.19.0"),sQuery(id+"F0.wireOp",EDGE,"E7.19.1"),sQuery(id+"F0.wireOp",EDGE,"E7.19.2"),sQuery(id+"F0.wireOp",EDGE,"E7.19.3"),sQuery(id+"F0.wireOp",EDGE,"E7.19.4"),sQuery(id+"F0.wireOp",EDGE,"E7.19.5"),sQuery(id+"F0.wireOp",EDGE,"E7.20.0"),sQuery(id+"F0.wireOp",EDGE,"E7.20.1"),sQuery(id+"F0.wireOp",EDGE,"E7.20.2"),sQuery(id+"F0.wireOp",EDGE,"E7.20.3"),sQuery(id+"F0.wireOp",EDGE,"E7.20.4"),sQuery(id+"F0.wireOp",EDGE,"E7.20.5"),sQuery(id+"F0.wireOp",EDGE,"E7.21.0"),sQuery(id+"F0.wireOp",EDGE,"E7.21.1"),sQuery(id+"F0.wireOp",EDGE,"E7.21.2"),sQuery(id+"F0.wireOp",EDGE,"E7.21.3"),sQuery(id+"F0.wireOp",EDGE,"E7.21.4"),sQuery(id+"F0.wireOp",EDGE,"E7.21.5"),sQuery(id+"F0.wireOp",EDGE,"E7.22.0"),sQuery(id+"F0.wireOp",EDGE,"E7.22.1"),sQuery(id+"F0.wireOp",EDGE,"E7.22.2"),sQuery(id+"F0.wireOp",EDGE,"E7.22.3"),sQuery(id+"F0.wireOp",EDGE,"E7.22.4"),sQuery(id+"F0.wireOp",EDGE,"E7.22.5"),sQuery(id+"F0.wireOp",EDGE,"E7.23.0"),sQuery(id+"F0.wireOp",EDGE,"E7.23.1"),sQuery(id+"F0.wireOp",EDGE,"E7.23.2"),sQuery(id+"F0.wireOp",EDGE,"E7.23.3"),sQuery(id+"F0.wireOp",EDGE,"E7.23.4"),sQuery(id+"F0.wireOp",EDGE,"E7.23.5"),sQuery(id+"F0.wireOp",EDGE,"E7.24.0"),sQuery(id+"F0.wireOp",EDGE,"E7.24.1"),sQuery(id+"F0.wireOp",EDGE,"E7.24.2"),sQuery(id+"F0.wireOp",EDGE,"E7.24.3"),sQuery(id+"F0.wireOp",EDGE,"E7.24.4"),sQuery(id+"F0.wireOp",EDGE,"E7.24.5"),sQuery(id+"F0.wireOp",EDGE,"E7.25.0"),sQuery(id+"F0.wireOp",EDGE,"E7.25.1"),sQuery(id+"F0.wireOp",EDGE,"E7.25.2"),sQuery(id+"F0.wireOp",EDGE,"E7.25.3"),sQuery(id+"F0.wireOp",EDGE,"E7.25.4"),sQuery(id+"F0.wireOp",EDGE,"E7.25.5"),sQuery(id+"F0.wireOp",EDGE,"E7.26.0"),sQuery(id+"F0.wireOp",EDGE,"E7.26.1"),sQuery(id+"F0.wireOp",EDGE,"E7.26.2"),sQuery(id+"F0.wireOp",EDGE,"E7.26.3"),sQuery(id+"F0.wireOp",EDGE,"E7.26.4"),sQuery(id+"F0.wireOp",EDGE,"E7.26.5"),sQuery(id+"F0.wireOp",EDGE,"E7.27.0"),sQuery(id+"F0.wireOp",EDGE,"E7.27.1"),sQuery(id+"F0.wireOp",EDGE,"E7.27.2"),sQuery(id+"F0.wireOp",EDGE,"E7.27.3"),sQuery(id+"F0.wireOp",EDGE,"E7.27.4"),sQuery(id+"F0.wireOp",EDGE,"E7.27.5"),sQuery(id+"F0.wireOp",EDGE,"E7.28.0"),sQuery(id+"F0.wireOp",EDGE,"E7.28.1"),sQuery(id+"F0.wireOp",EDGE,"E7.28.2"),sQuery(id+"F0.wireOp",EDGE,"E7.28.3"),sQuery(id+"F0.wireOp",EDGE,"E7.28.4"),sQuery(id+"F0.wireOp",EDGE,"E7.28.5"),sQuery(id+"F0.wireOp",EDGE,"E7.29.0"),sQuery(id+"F0.wireOp",EDGE,"E7.29.1"),sQuery(id+"F0.wireOp",EDGE,"E7.29.2"),sQuery(id+"F0.wireOp",EDGE,"E7.29.3"),sQuery(id+"F0.wireOp",EDGE,"E7.29.4"),sQuery(id+"F0.wireOp",EDGE,"E7.29.5"),sQuery(id+"F0.wireOp",EDGE,"E7.30.0"),sQuery(id+"F0.wireOp",EDGE,"E7.30.1"),sQuery(id+"F0.wireOp",EDGE,"E7.30.2"),sQuery(id+"F0.wireOp",EDGE,"E7.30.3"),sQuery(id+"F0.wireOp",EDGE,"E7.30.4"),sQuery(id+"F0.wireOp",EDGE,"E7.30.5"),sQuery(id+"F0.wireOp",EDGE,"E7.31.0"),sQuery(id+"F0.wireOp",EDGE,"E7.31.1"),sQuery(id+"F0.wireOp",EDGE,"E7.31.2"),sQuery(id+"F0.wireOp",EDGE,"E7.31.3"),sQuery(id+"F0.wireOp",EDGE,"E7.31.4"),sQuery(id+"F0.wireOp",EDGE,"E7.31.5"),sQuery(id+"F0.wireOp",EDGE,"E7.32.0"),sQuery(id+"F0.wireOp",EDGE,"E7.32.1"),sQuery(id+"F0.wireOp",EDGE,"E7.32.2"),sQuery(id+"F0.wireOp",EDGE,"E7.32.3"),sQuery(id+"F0.wireOp",EDGE,"E7.32.4"),sQuery(id+"F0.wireOp",EDGE,"E7.32.5"),sQuery(id+"F0.wireOp",EDGE,"E7.33.0"),sQuery(id+"F0.wireOp",EDGE,"E7.33.1"),sQuery(id+"F0.wireOp",EDGE,"E7.33.2"),sQuery(id+"F0.wireOp",EDGE,"E7.33.3"),sQuery(id+"F0.wireOp",EDGE,"E7.33.4"),sQuery(id+"F0.wireOp",EDGE,"E7.33.5"),sQuery(id+"F0.wireOp",EDGE,"E7.34.0"),sQuery(id+"F0.wireOp",EDGE,"E7.34.1"),sQuery(id+"F0.wireOp",EDGE,"E7.34.2"),sQuery(id+"F0.wireOp",EDGE,"E7.34.3"),sQuery(id+"F0.wireOp",EDGE,"E7.34.4"),sQuery(id+"F0.wireOp",EDGE,"E7.34.5"),sQuery(id+"F0.wireOp",EDGE,"E7.35.0"),sQuery(id+"F0.wireOp",EDGE,"E7.35.1"),sQuery(id+"F0.wireOp",EDGE,"E7.35.2"),sQuery(id+"F0.wireOp",EDGE,"E7.35.3"),sQuery(id+"F0.wireOp",EDGE,"E7.35.4"),sQuery(id+"F0.wireOp",EDGE,"E7.35.5"),sQuery(id+"F0.wireOp",EDGE,"E7.36.0"),sQuery(id+"F0.wireOp",EDGE,"E7.36.1"),sQuery(id+"F0.wireOp",EDGE,"E7.36.2"),sQuery(id+"F0.wireOp",EDGE,"E7.36.3"),sQuery(id+"F0.wireOp",EDGE,"E7.36.4"),sQuery(id+"F0.wireOp",EDGE,"E7.36.5"),sQuery(id+"F0.wireOp",EDGE,"E7.37.0"),sQuery(id+"F0.wireOp",EDGE,"E7.37.1"),sQuery(id+"F0.wireOp",EDGE,"E7.37.2"),sQuery(id+"F0.wireOp",EDGE,"E7.37.3"),sQuery(id+"F0.wireOp",EDGE,"E7.37.4"),sQuery(id+"F0.wireOp",EDGE,"E7.37.5"),sQuery(id+"F0.wireOp",EDGE,"E7.38.0"),sQuery(id+"F0.wireOp",EDGE,"E7.38.1"),sQuery(id+"F0.wireOp",EDGE,"E7.38.2"),sQuery(id+"F0.wireOp",EDGE,"E7.38.3"),sQuery(id+"F0.wireOp",EDGE,"E7.38.4"),sQuery(id+"F0.wireOp",EDGE,"E7.38.5"),sQuery(id+"F0.wireOp",EDGE,"E7.39.0"),sQuery(id+"F0.wireOp",EDGE,"E7.39.1"),sQuery(id+"F0.wireOp",EDGE,"E7.39.2"),sQuery(id+"F0.wireOp",EDGE,"E7.39.3"),sQuery(id+"F0.wireOp",EDGE,"E7.39.4"),sQuery(id+"F0.wireOp",EDGE,"E7.39.5"),sQuery(id+"F0.wireOp",EDGE,"E7.40.0"),sQuery(id+"F0.wireOp",EDGE,"E7.40.1"),sQuery(id+"F0.wireOp",EDGE,"E7.40.2"),sQuery(id+"F0.wireOp",EDGE,"E7.40.3"),sQuery(id+"F0.wireOp",EDGE,"E7.40.4"),sQuery(id+"F0.wireOp",EDGE,"E7.40.5"),sQuery(id+"F0.wireOp",EDGE,"E7.41.0"),sQuery(id+"F0.wireOp",EDGE,"E7.41.1"),sQuery(id+"F0.wireOp",EDGE,"E7.41.2"),sQuery(id+"F0.wireOp",EDGE,"E7.41.3"),sQuery(id+"F0.wireOp",EDGE,"E7.41.4"),sQuery(id+"F0.wireOp",EDGE,"E7.41.5"),sQuery(id+"F0.wireOp",EDGE,"E7.42.0"),sQuery(id+"F0.wireOp",EDGE,"E7.42.1"),sQuery(id+"F0.wireOp",EDGE,"E7.42.2"),sQuery(id+"F0.wireOp",EDGE,"E7.42.3"),sQuery(id+"F0.wireOp",EDGE,"E7.42.4"),sQuery(id+"F0.wireOp",EDGE,"E7.42.5"),sQuery(id+"F0.wireOp",EDGE,"E7.43.0"),sQuery(id+"F0.wireOp",EDGE,"E7.43.1"),sQuery(id+"F0.wireOp",EDGE,"E7.43.2"),sQuery(id+"F0.wireOp",EDGE,"E7.43.3"),sQuery(id+"F0.wireOp",EDGE,"E7.43.4"),sQuery(id+"F0.wireOp",EDGE,"E7.43.5")])],"isStart":false})],"blendedInto":[makeQuery(id+"F1.opExtrude","CAP_FACE",FACE,{"disambiguationData":[OSD([sQuery(id+"F0.wireOp",EDGE,"E1"),sQuery(id+"F0.wireOp",EDGE,"E2"),sQuery(id+"F0.wireOp",EDGE,"E3"),sQuery(id+"F0.wireOp",EDGE,"E4"),sQuery(id+"F0.wireOp",EDGE,"E5"),sQuery(id+"F0.wireOp",EDGE,"E6"),sQuery(id+"F0.wireOp",EDGE,"E7.1.0"),sQuery(id+"F0.wireOp",EDGE,"E7.1.1"),sQuery(id+"F0.wireOp",EDGE,"E7.1.2"),sQuery(id+"F0.wireOp",EDGE,"E7.1.3"),sQuery(id+"F0.wireOp",EDGE,"E7.1.4"),sQuery(id+"F0.wireOp",EDGE,"E7.1.5"),sQuery(id+"F0.wireOp",EDGE,"E7.2.0"),sQuery(id+"F0.wireOp",EDGE,"E7.2.1"),sQuery(id+"F0.wireOp",EDGE,"E7.2.2"),sQuery(id+"F0.wireOp",EDGE,"E7.2.3"),sQuery(id+"F0.wireOp",EDGE,"E7.2.4"),sQuery(id+"F0.wireOp",EDGE,"E7.2.5"),sQuery(id+"F0.wireOp",EDGE,"E7.3.0"),sQuery(id+"F0.wireOp",EDGE,"E7.3.1"),sQuery(id+"F0.wireOp",EDGE,"E7.3.2"),sQuery(id+"F0.wireOp",EDGE,"E7.3.3"),sQuery(id+"F0.wireOp",EDGE,"E7.3.4"),sQuery(id+"F0.wireOp",EDGE,"E7.3.5"),sQuery(id+"F0.wireOp",EDGE,"E7.4.0"),sQuery(id+"F0.wireOp",EDGE,"E7.4.1"),sQuery(id+"F0.wireOp",EDGE,"E7.4.2"),sQuery(id+"F0.wireOp",EDGE,"E7.4.3"),sQuery(id+"F0.wireOp",EDGE,"E7.4.4"),sQuery(id+"F0.wireOp",EDGE,"E7.4.5"),sQuery(id+"F0.wireOp",EDGE,"E7.5.0"),sQuery(id+"F0.wireOp",EDGE,"E7.5.1"),sQuery(id+"F0.wireOp",EDGE,"E7.5.2"),sQuery(id+"F0.wireOp",EDGE,"E7.5.3"),sQuery(id+"F0.wireOp",EDGE,"E7.5.4"),sQuery(id+"F0.wireOp",EDGE,"E7.5.5"),sQuery(id+"F0.wireOp",EDGE,"E7.6.0"),sQuery(id+"F0.wireOp",EDGE,"E7.6.1"),sQuery(id+"F0.wireOp",EDGE,"E7.6.2"),sQuery(id+"F0.wireOp",EDGE,"E7.6.3"),sQuery(id+"F0.wireOp",EDGE,"E7.6.4"),sQuery(id+"F0.wireOp",EDGE,"E7.6.5"),sQuery(id+"F0.wireOp",EDGE,"E7.7.0"),sQuery(id+"F0.wireOp",EDGE,"E7.7.1"),sQuery(id+"F0.wireOp",EDGE,"E7.7.2"),sQuery(id+"F0.wireOp",EDGE,"E7.7.3"),sQuery(id+"F0.wireOp",EDGE,"E7.7.4"),sQuery(id+"F0.wireOp",EDGE,"E7.7.5"),sQuery(id+"F0.wireOp",EDGE,"E7.8.0"),sQuery(id+"F0.wireOp",EDGE,"E7.8.1"),sQuery(id+"F0.wireOp",EDGE,"E7.8.2"),sQuery(id+"F0.wireOp",EDGE,"E7.8.3"),sQuery(id+"F0.wireOp",EDGE,"E7.8.4"),sQuery(id+"F0.wireOp",EDGE,"E7.8.5"),sQuery(id+"F0.wireOp",EDGE,"E7.9.0"),sQuery(id+"F0.wireOp",EDGE,"E7.9.1"),sQuery(id+"F0.wireOp",EDGE,"E7.9.2"),sQuery(id+"F0.wireOp",EDGE,"E7.9.3"),sQuery(id+"F0.wireOp",EDGE,"E7.9.4"),sQuery(id+"F0.wireOp",EDGE,"E7.9.5"),sQuery(id+"F0.wireOp",EDGE,"E7.10.0"),sQuery(id+"F0.wireOp",EDGE,"E7.10.1"),sQuery(id+"F0.wireOp",EDGE,"E7.10.2"),sQuery(id+"F0.wireOp",EDGE,"E7.10.3"),sQuery(id+"F0.wireOp",EDGE,"E7.10.4"),sQuery(id+"F0.wireOp",EDGE,"E7.10.5"),sQuery(id+"F0.wireOp",EDGE,"E7.11.0"),sQuery(id+"F0.wireOp",EDGE,"E7.11.1"),sQuery(id+"F0.wireOp",EDGE,"E7.11.2"),sQuery(id+"F0.wireOp",EDGE,"E7.11.3"),sQuery(id+"F0.wireOp",EDGE,"E7.11.4"),sQuery(id+"F0.wireOp",EDGE,"E7.11.5"),sQuery(id+"F0.wireOp",EDGE,"E7.12.0"),sQuery(id+"F0.wireOp",EDGE,"E7.12.1"),sQuery(id+"F0.wireOp",EDGE,"E7.12.2"),sQuery(id+"F0.wireOp",EDGE,"E7.12.3"),sQuery(id+"F0.wireOp",EDGE,"E7.12.4"),sQuery(id+"F0.wireOp",EDGE,"E7.12.5"),subQ0,sQuery(id+"F0.wireOp",EDGE,"E7.13.1"),sQuery(id+"F0.wireOp",EDGE,"E7.13.2"),sQuery(id+"F0.wireOp",EDGE,"E7.13.3"),sQuery(id+"F0.wireOp",EDGE,"E7.13.4"),sQuery(id+"F0.wireOp",EDGE,"E7.13.5"),sQuery(id+"F0.wireOp",EDGE,"E7.14.0"),sQuery(id+"F0.wireOp",EDGE,"E7.14.1"),sQuery(id+"F0.wireOp",EDGE,"E7.14.2"),sQuery(id+"F0.wireOp",EDGE,"E7.14.3"),sQuery(id+"F0.wireOp",EDGE,"E7.14.4"),sQuery(id+"F0.wireOp",EDGE,"E7.14.5"),sQuery(id+"F0.wireOp",EDGE,"E7.15.0"),sQuery(id+"F0.wireOp",EDGE,"E7.15.1"),sQuery(id+"F0.wireOp",EDGE,"E7.15.2"),sQuery(id+"F0.wireOp",EDGE,"E7.15.3"),sQuery(id+"F0.wireOp",EDGE,"E7.15.4"),sQuery(id+"F0.wireOp",EDGE,"E7.15.5"),sQuery(id+"F0.wireOp",EDGE,"E7.16.0"),sQuery(id+"F0.wireOp",EDGE,"E7.16.1"),sQuery(id+"F0.wireOp",EDGE,"E7.16.2"),sQuery(id+"F0.wireOp",EDGE,"E7.16.3"),sQuery(id+"F0.wireOp",EDGE,"E7.16.4"),sQuery(id+"F0.wireOp",EDGE,"E7.16.5"),sQuery(id+"F0.wireOp",EDGE,"E7.17.0"),sQuery(id+"F0.wireOp",EDGE,"E7.17.1"),sQuery(id+"F0.wireOp",EDGE,"E7.17.2"),sQuery(id+"F0.wireOp",EDGE,"E7.17.3"),sQuery(id+"F0.wireOp",EDGE,"E7.17.4"),sQuery(id+"F0.wireOp",EDGE,"E7.17.5"),sQuery(id+"F0.wireOp",EDGE,"E7.18.0"),sQuery(id+"F0.wireOp",EDGE,"E7.18.1"),sQuery(id+"F0.wireOp",EDGE,"E7.18.2"),sQuery(id+"F0.wireOp",EDGE,"E7.18.3"),sQuery(id+"F0.wireOp",EDGE,"E7.18.4"),sQuery(id+"F0.wireOp",EDGE,"E7.18.5"),sQuery(id+"F0.wireOp",EDGE,"E7.19.0"),sQuery(id+"F0.wireOp",EDGE,"E7.19.1"),sQuery(id+"F0.wireOp",EDGE,"E7.19.2"),sQuery(id+"F0.wireOp",EDGE,"E7.19.3"),sQuery(id+"F0.wireOp",EDGE,"E7.19.4"),sQuery(id+"F0.wireOp",EDGE,"E7.19.5"),sQuery(id+"F0.wireOp",EDGE,"E7.20.0"),sQuery(id+"F0.wireOp",EDGE,"E7.20.1"),sQuery(id+"F0.wireOp",EDGE,"E7.20.2"),sQuery(id+"F0.wireOp",EDGE,"E7.20.3"),sQuery(id+"F0.wireOp",EDGE,"E7.20.4"),sQuery(id+"F0.wireOp",EDGE,"E7.20.5"),sQuery(id+"F0.wireOp",EDGE,"E7.21.0"),sQuery(id+"F0.wireOp",EDGE,"E7.21.1"),sQuery(id+"F0.wireOp",EDGE,"E7.21.2"),sQuery(id+"F0.wireOp",EDGE,"E7.21.3"),sQuery(id+"F0.wireOp",EDGE,"E7.21.4"),sQuery(id+"F0.wireOp",EDGE,"E7.21.5"),sQuery(id+"F0.wireOp",EDGE,"E7.22.0"),sQuery(id+"F0.wireOp",EDGE,"E7.22.1"),sQuery(id+"F0.wireOp",EDGE,"E7.22.2"),sQuery(id+"F0.wireOp",EDGE,"E7.22.3"),sQuery(id+"F0.wireOp",EDGE,"E7.22.4"),sQuery(id+"F0.wireOp",EDGE,"E7.22.5"),sQuery(id+"F0.wireOp",EDGE,"E7.23.0"),sQuery(id+"F0.wireOp",EDGE,"E7.23.1"),sQuery(id+"F0.wireOp",EDGE,"E7.23.2"),sQuery(id+"F0.wireOp",EDGE,"E7.23.3"),sQuery(id+"F0.wireOp",EDGE,"E7.23.4"),sQuery(id+"F0.wireOp",EDGE,"E7.23.5"),sQuery(id+"F0.wireOp",EDGE,"E7.24.0"),sQuery(id+"F0.wireOp",EDGE,"E7.24.1"),sQuery(id+"F0.wireOp",EDGE,"E7.24.2"),sQuery(id+"F0.wireOp",EDGE,"E7.24.3"),sQuery(id+"F0.wireOp",EDGE,"E7.24.4"),sQuery(id+"F0.wireOp",EDGE,"E7.24.5"),sQuery(id+"F0.wireOp",EDGE,"E7.25.0"),sQuery(id+"F0.wireOp",EDGE,"E7.25.1"),sQuery(id+"F0.wireOp",EDGE,"E7.25.2"),sQuery(id+"F0.wireOp",EDGE,"E7.25.3"),sQuery(id+"F0.wireOp",EDGE,"E7.25.4"),sQuery(id+"F0.wireOp",EDGE,"E7.25.5"),sQuery(id+"F0.wireOp",EDGE,"E7.26.0"),sQuery(id+"F0.wireOp",EDGE,"E7.26.1"),sQuery(id+"F0.wireOp",EDGE,"E7.26.2"),sQuery(id+"F0.wireOp",EDGE,"E7.26.3"),sQuery(id+"F0.wireOp",EDGE,"E7.26.4"),sQuery(id+"F0.wireOp",EDGE,"E7.26.5"),sQuery(id+"F0.wireOp",EDGE,"E7.27.0"),sQuery(id+"F0.wireOp",EDGE,"E7.27.1"),sQuery(id+"F0.wireOp",EDGE,"E7.27.2"),sQuery(id+"F0.wireOp",EDGE,"E7.27.3"),sQuery(id+"F0.wireOp",EDGE,"E7.27.4"),sQuery(id+"F0.wireOp",EDGE,"E7.27.5"),sQuery(id+"F0.wireOp",EDGE,"E7.28.0"),sQuery(id+"F0.wireOp",EDGE,"E7.28.1"),sQuery(id+"F0.wireOp",EDGE,"E7.28.2"),sQuery(id+"F0.wireOp",EDGE,"E7.28.3"),sQuery(id+"F0.wireOp",EDGE,"E7.28.4"),sQuery(id+"F0.wireOp",EDGE,"E7.28.5"),sQuery(id+"F0.wireOp",EDGE,"E7.29.0"),sQuery(id+"F0.wireOp",EDGE,"E7.29.1"),sQuery(id+"F0.wireOp",EDGE,"E7.29.2"),sQuery(id+"F0.wireOp",EDGE,"E7.29.3"),sQuery(id+"F0.wireOp",EDGE,"E7.29.4"),sQuery(id+"F0.wireOp",EDGE,"E7.29.5"),sQuery(id+"F0.wireOp",EDGE,"E7.30.0"),sQuery(id+"F0.wireOp",EDGE,"E7.30.1"),sQuery(id+"F0.wireOp",EDGE,"E7.30.2"),sQuery(id+"F0.wireOp",EDGE,"E7.30.3"),sQuery(id+"F0.wireOp",EDGE,"E7.30.4"),sQuery(id+"F0.wireOp",EDGE,"E7.30.5"),sQuery(id+"F0.wireOp",EDGE,"E7.31.0"),sQuery(id+"F0.wireOp",EDGE,"E7.31.1"),sQuery(id+"F0.wireOp",EDGE,"E7.31.2"),sQuery(id+"F0.wireOp",EDGE,"E7.31.3"),sQuery(id+"F0.wireOp",EDGE,"E7.31.4"),sQuery(id+"F0.wireOp",EDGE,"E7.31.5"),sQuery(id+"F0.wireOp",EDGE,"E7.32.0"),sQuery(id+"F0.wireOp",EDGE,"E7.32.1"),sQuery(id+"F0.wireOp",EDGE,"E7.32.2"),sQuery(id+"F0.wireOp",EDGE,"E7.32.3"),sQuery(id+"F0.wireOp",EDGE,"E7.32.4"),sQuery(id+"F0.wireOp",EDGE,"E7.32.5"),sQuery(id+"F0.wireOp",EDGE,"E7.33.0"),sQuery(id+"F0.wireOp",EDGE,"E7.33.1"),sQuery(id+"F0.wireOp",EDGE,"E7.33.2"),sQuery(id+"F0.wireOp",EDGE,"E7.33.3"),sQuery(id+"F0.wireOp",EDGE,"E7.33.4"),sQuery(id+"F0.wireOp",EDGE,"E7.33.5"),sQuery(id+"F0.wireOp",EDGE,"E7.34.0"),sQuery(id+"F0.wireOp",EDGE,"E7.34.1"),sQuery(id+"F0.wireOp",EDGE,"E7.34.2"),sQuery(id+"F0.wireOp",EDGE,"E7.34.3"),sQuery(id+"F0.wireOp",EDGE,"E7.34.4"),sQuery(id+"F0.wireOp",EDGE,"E7.34.5"),sQuery(id+"F0.wireOp",EDGE,"E7.35.0"),sQuery(id+"F0.wireOp",EDGE,"E7.35.1"),sQuery(id+"F0.wireOp",EDGE,"E7.35.2"),sQuery(id+"F0.wireOp",EDGE,"E7.35.3"),sQuery(id+"F0.wireOp",EDGE,"E7.35.4"),sQuery(id+"F0.wireOp",EDGE,"E7.35.5"),sQuery(id+"F0.wireOp",EDGE,"E7.36.0"),sQuery(id+"F0.wireOp",EDGE,"E7.36.1"),sQuery(id+"F0.wireOp",EDGE,"E7.36.2"),sQuery(id+"F0.wireOp",EDGE,"E7.36.3"),sQuery(id+"F0.wireOp",EDGE,"E7.36.4"),sQuery(id+"F0.wireOp",EDGE,"E7.36.5"),sQuery(id+"F0.wireOp",EDGE,"E7.37.0"),sQuery(id+"F0.wireOp",EDGE,"E7.37.1"),sQuery(id+"F0.wireOp",EDGE,"E7.37.2"),sQuery(id+"F0.wireOp",EDGE,"E7.37.3"),sQuery(id+"F0.wireOp",EDGE,"E7.37.4"),sQuery(id+"F0.wireOp",EDGE,"E7.37.5"),sQuery(id+"F0.wireOp",EDGE,"E7.38.0"),sQuery(id+"F0.wireOp",EDGE,"E7.38.1"),sQuery(id+"F0.wireOp",EDGE,"E7.38.2"),sQuery(id+"F0.wireOp",EDGE,"E7.38.3"),sQuery(id+"F0.wireOp",EDGE,"E7.38.4"),sQuery(id+"F0.wireOp",EDGE,"E7.38.5"),sQuery(id+"F0.wireOp",EDGE,"E7.39.0"),sQuery(id+"F0.wireOp",EDGE,"E7.39.1"),sQuery(id+"F0.wireOp",EDGE,"E7.39.2"),sQuery(id+"F0.wireOp",EDGE,"E7.39.3"),sQuery(id+"F0.wireOp",EDGE,"E7.39.4"),sQuery(id+"F0.wireOp",EDGE,"E7.39.5"),sQuery(id+"F0.wireOp",EDGE,"E7.40.0"),sQuery(id+"F0.wireOp",EDGE,"E7.40.1"),sQuery(id+"F0.wireOp",EDGE,"E7.40.2"),sQuery(id+"F0.wireOp",EDGE,"E7.40.3"),sQuery(id+"F0.wireOp",EDGE,"E7.40.4"),sQuery(id+"F0.wireOp",EDGE,"E7.40.5"),sQuery(id+"F0.wireOp",EDGE,"E7.41.0"),sQuery(id+"F0.wireOp",EDGE,"E7.41.1"),sQuery(id+"F0.wireOp",EDGE,"E7.41.2"),sQuery(id+"F0.wireOp",EDGE,"E7.41.3"),sQuery(id+"F0.wireOp",EDGE,"E7.41.4"),sQuery(id+"F0.wireOp",EDGE,"E7.41.5"),sQuery(id+"F0.wireOp",EDGE,"E7.42.0"),sQuery(id+"F0.wireOp",EDGE,"E7.42.1"),sQuery(id+"F0.wireOp",EDGE,"E7.42.2"),sQuery(id+"F0.wireOp",EDGE,"E7.42.3"),sQuery(id+"F0.wireOp",EDGE,"E7.42.4"),sQuery(id+"F0.wireOp",EDGE,"E7.42.5"),sQuery(id+"F0.wireOp",EDGE,"E7.43.0"),sQuery(id+"F0.wireOp",EDGE,"E7.43.1"),sQuery(id+"F0.wireOp",EDGE,"E7.43.2"),sQuery(id+"F0.wireOp",EDGE,"E7.43.3"),sQuery(id+"F0.wireOp",EDGE,"E7.43.4"),sQuery(id+"F0.wireOp",EDGE,"E7.43.5")])],"isStart":false})]}),makeQuery(id+"F2.opChamfer","BLEND_FACE",FACE,{"disambiguationData":[OSD([subQ0])]})],"blendedInto":[makeQuery(id+"F2.opChamfer","BLEND_FACE",FACE,{"disambiguationData":[OSD([subQ0])]})]});}
            var Q17;
            {var subQ0=sQuery(id+"F0.wireOp",EDGE,"E7.11.0");Q17=makeQuery(id+"F8.opChamfer","BLEND_EDGE",EDGE,{"blendedFrom":[makeQuery(id+"F2.opChamfer","BLEND_EDGE",EDGE,{"blendedFrom":[makeQuery(id+"F1.opExtrude","CAP_EDGE",EDGE,{"disambiguationData":[OSD([subQ0])],"isStart":false}),makeQuery(id+"F1.opExtrude","CAP_FACE",FACE,{"disambiguationData":[OSD([sQuery(id+"F0.wireOp",EDGE,"E1"),sQuery(id+"F0.wireOp",EDGE,"E2"),sQuery(id+"F0.wireOp",EDGE,"E3"),sQuery(id+"F0.wireOp",EDGE,"E4"),sQuery(id+"F0.wireOp",EDGE,"E5"),sQuery(id+"F0.wireOp",EDGE,"E6"),sQuery(id+"F0.wireOp",EDGE,"E7.1.0"),sQuery(id+"F0.wireOp",EDGE,"E7.1.1"),sQuery(id+"F0.wireOp",EDGE,"E7.1.2"),sQuery(id+"F0.wireOp",EDGE,"E7.1.3"),sQuery(id+"F0.wireOp",EDGE,"E7.1.4"),sQuery(id+"F0.wireOp",EDGE,"E7.1.5"),sQuery(id+"F0.wireOp",EDGE,"E7.2.0"),sQuery(id+"F0.wireOp",EDGE,"E7.2.1"),sQuery(id+"F0.wireOp",EDGE,"E7.2.2"),sQuery(id+"F0.wireOp",EDGE,"E7.2.3"),sQuery(id+"F0.wireOp",EDGE,"E7.2.4"),sQuery(id+"F0.wireOp",EDGE,"E7.2.5"),sQuery(id+"F0.wireOp",EDGE,"E7.3.0"),sQuery(id+"F0.wireOp",EDGE,"E7.3.1"),sQuery(id+"F0.wireOp",EDGE,"E7.3.2"),sQuery(id+"F0.wireOp",EDGE,"E7.3.3"),sQuery(id+"F0.wireOp",EDGE,"E7.3.4"),sQuery(id+"F0.wireOp",EDGE,"E7.3.5"),sQuery(id+"F0.wireOp",EDGE,"E7.4.0"),sQuery(id+"F0.wireOp",EDGE,"E7.4.1"),sQuery(id+"F0.wireOp",EDGE,"E7.4.2"),sQuery(id+"F0.wireOp",EDGE,"E7.4.3"),sQuery(id+"F0.wireOp",EDGE,"E7.4.4"),sQuery(id+"F0.wireOp",EDGE,"E7.4.5"),sQuery(id+"F0.wireOp",EDGE,"E7.5.0"),sQuery(id+"F0.wireOp",EDGE,"E7.5.1"),sQuery(id+"F0.wireOp",EDGE,"E7.5.2"),sQuery(id+"F0.wireOp",EDGE,"E7.5.3"),sQuery(id+"F0.wireOp",EDGE,"E7.5.4"),sQuery(id+"F0.wireOp",EDGE,"E7.5.5"),sQuery(id+"F0.wireOp",EDGE,"E7.6.0"),sQuery(id+"F0.wireOp",EDGE,"E7.6.1"),sQuery(id+"F0.wireOp",EDGE,"E7.6.2"),sQuery(id+"F0.wireOp",EDGE,"E7.6.3"),sQuery(id+"F0.wireOp",EDGE,"E7.6.4"),sQuery(id+"F0.wireOp",EDGE,"E7.6.5"),sQuery(id+"F0.wireOp",EDGE,"E7.7.0"),sQuery(id+"F0.wireOp",EDGE,"E7.7.1"),sQuery(id+"F0.wireOp",EDGE,"E7.7.2"),sQuery(id+"F0.wireOp",EDGE,"E7.7.3"),sQuery(id+"F0.wireOp",EDGE,"E7.7.4"),sQuery(id+"F0.wireOp",EDGE,"E7.7.5"),sQuery(id+"F0.wireOp",EDGE,"E7.8.0"),sQuery(id+"F0.wireOp",EDGE,"E7.8.1"),sQuery(id+"F0.wireOp",EDGE,"E7.8.2"),sQuery(id+"F0.wireOp",EDGE,"E7.8.3"),sQuery(id+"F0.wireOp",EDGE,"E7.8.4"),sQuery(id+"F0.wireOp",EDGE,"E7.8.5"),sQuery(id+"F0.wireOp",EDGE,"E7.9.0"),sQuery(id+"F0.wireOp",EDGE,"E7.9.1"),sQuery(id+"F0.wireOp",EDGE,"E7.9.2"),sQuery(id+"F0.wireOp",EDGE,"E7.9.3"),sQuery(id+"F0.wireOp",EDGE,"E7.9.4"),sQuery(id+"F0.wireOp",EDGE,"E7.9.5"),sQuery(id+"F0.wireOp",EDGE,"E7.10.0"),sQuery(id+"F0.wireOp",EDGE,"E7.10.1"),sQuery(id+"F0.wireOp",EDGE,"E7.10.2"),sQuery(id+"F0.wireOp",EDGE,"E7.10.3"),sQuery(id+"F0.wireOp",EDGE,"E7.10.4"),sQuery(id+"F0.wireOp",EDGE,"E7.10.5"),subQ0,sQuery(id+"F0.wireOp",EDGE,"E7.11.1"),sQuery(id+"F0.wireOp",EDGE,"E7.11.2"),sQuery(id+"F0.wireOp",EDGE,"E7.11.3"),sQuery(id+"F0.wireOp",EDGE,"E7.11.4"),sQuery(id+"F0.wireOp",EDGE,"E7.11.5"),sQuery(id+"F0.wireOp",EDGE,"E7.12.0"),sQuery(id+"F0.wireOp",EDGE,"E7.12.1"),sQuery(id+"F0.wireOp",EDGE,"E7.12.2"),sQuery(id+"F0.wireOp",EDGE,"E7.12.3"),sQuery(id+"F0.wireOp",EDGE,"E7.12.4"),sQuery(id+"F0.wireOp",EDGE,"E7.12.5"),sQuery(id+"F0.wireOp",EDGE,"E7.13.0"),sQuery(id+"F0.wireOp",EDGE,"E7.13.1"),sQuery(id+"F0.wireOp",EDGE,"E7.13.2"),sQuery(id+"F0.wireOp",EDGE,"E7.13.3"),sQuery(id+"F0.wireOp",EDGE,"E7.13.4"),sQuery(id+"F0.wireOp",EDGE,"E7.13.5"),sQuery(id+"F0.wireOp",EDGE,"E7.14.0"),sQuery(id+"F0.wireOp",EDGE,"E7.14.1"),sQuery(id+"F0.wireOp",EDGE,"E7.14.2"),sQuery(id+"F0.wireOp",EDGE,"E7.14.3"),sQuery(id+"F0.wireOp",EDGE,"E7.14.4"),sQuery(id+"F0.wireOp",EDGE,"E7.14.5"),sQuery(id+"F0.wireOp",EDGE,"E7.15.0"),sQuery(id+"F0.wireOp",EDGE,"E7.15.1"),sQuery(id+"F0.wireOp",EDGE,"E7.15.2"),sQuery(id+"F0.wireOp",EDGE,"E7.15.3"),sQuery(id+"F0.wireOp",EDGE,"E7.15.4"),sQuery(id+"F0.wireOp",EDGE,"E7.15.5"),sQuery(id+"F0.wireOp",EDGE,"E7.16.0"),sQuery(id+"F0.wireOp",EDGE,"E7.16.1"),sQuery(id+"F0.wireOp",EDGE,"E7.16.2"),sQuery(id+"F0.wireOp",EDGE,"E7.16.3"),sQuery(id+"F0.wireOp",EDGE,"E7.16.4"),sQuery(id+"F0.wireOp",EDGE,"E7.16.5"),sQuery(id+"F0.wireOp",EDGE,"E7.17.0"),sQuery(id+"F0.wireOp",EDGE,"E7.17.1"),sQuery(id+"F0.wireOp",EDGE,"E7.17.2"),sQuery(id+"F0.wireOp",EDGE,"E7.17.3"),sQuery(id+"F0.wireOp",EDGE,"E7.17.4"),sQuery(id+"F0.wireOp",EDGE,"E7.17.5"),sQuery(id+"F0.wireOp",EDGE,"E7.18.0"),sQuery(id+"F0.wireOp",EDGE,"E7.18.1"),sQuery(id+"F0.wireOp",EDGE,"E7.18.2"),sQuery(id+"F0.wireOp",EDGE,"E7.18.3"),sQuery(id+"F0.wireOp",EDGE,"E7.18.4"),sQuery(id+"F0.wireOp",EDGE,"E7.18.5"),sQuery(id+"F0.wireOp",EDGE,"E7.19.0"),sQuery(id+"F0.wireOp",EDGE,"E7.19.1"),sQuery(id+"F0.wireOp",EDGE,"E7.19.2"),sQuery(id+"F0.wireOp",EDGE,"E7.19.3"),sQuery(id+"F0.wireOp",EDGE,"E7.19.4"),sQuery(id+"F0.wireOp",EDGE,"E7.19.5"),sQuery(id+"F0.wireOp",EDGE,"E7.20.0"),sQuery(id+"F0.wireOp",EDGE,"E7.20.1"),sQuery(id+"F0.wireOp",EDGE,"E7.20.2"),sQuery(id+"F0.wireOp",EDGE,"E7.20.3"),sQuery(id+"F0.wireOp",EDGE,"E7.20.4"),sQuery(id+"F0.wireOp",EDGE,"E7.20.5"),sQuery(id+"F0.wireOp",EDGE,"E7.21.0"),sQuery(id+"F0.wireOp",EDGE,"E7.21.1"),sQuery(id+"F0.wireOp",EDGE,"E7.21.2"),sQuery(id+"F0.wireOp",EDGE,"E7.21.3"),sQuery(id+"F0.wireOp",EDGE,"E7.21.4"),sQuery(id+"F0.wireOp",EDGE,"E7.21.5"),sQuery(id+"F0.wireOp",EDGE,"E7.22.0"),sQuery(id+"F0.wireOp",EDGE,"E7.22.1"),sQuery(id+"F0.wireOp",EDGE,"E7.22.2"),sQuery(id+"F0.wireOp",EDGE,"E7.22.3"),sQuery(id+"F0.wireOp",EDGE,"E7.22.4"),sQuery(id+"F0.wireOp",EDGE,"E7.22.5"),sQuery(id+"F0.wireOp",EDGE,"E7.23.0"),sQuery(id+"F0.wireOp",EDGE,"E7.23.1"),sQuery(id+"F0.wireOp",EDGE,"E7.23.2"),sQuery(id+"F0.wireOp",EDGE,"E7.23.3"),sQuery(id+"F0.wireOp",EDGE,"E7.23.4"),sQuery(id+"F0.wireOp",EDGE,"E7.23.5"),sQuery(id+"F0.wireOp",EDGE,"E7.24.0"),sQuery(id+"F0.wireOp",EDGE,"E7.24.1"),sQuery(id+"F0.wireOp",EDGE,"E7.24.2"),sQuery(id+"F0.wireOp",EDGE,"E7.24.3"),sQuery(id+"F0.wireOp",EDGE,"E7.24.4"),sQuery(id+"F0.wireOp",EDGE,"E7.24.5"),sQuery(id+"F0.wireOp",EDGE,"E7.25.0"),sQuery(id+"F0.wireOp",EDGE,"E7.25.1"),sQuery(id+"F0.wireOp",EDGE,"E7.25.2"),sQuery(id+"F0.wireOp",EDGE,"E7.25.3"),sQuery(id+"F0.wireOp",EDGE,"E7.25.4"),sQuery(id+"F0.wireOp",EDGE,"E7.25.5"),sQuery(id+"F0.wireOp",EDGE,"E7.26.0"),sQuery(id+"F0.wireOp",EDGE,"E7.26.1"),sQuery(id+"F0.wireOp",EDGE,"E7.26.2"),sQuery(id+"F0.wireOp",EDGE,"E7.26.3"),sQuery(id+"F0.wireOp",EDGE,"E7.26.4"),sQuery(id+"F0.wireOp",EDGE,"E7.26.5"),sQuery(id+"F0.wireOp",EDGE,"E7.27.0"),sQuery(id+"F0.wireOp",EDGE,"E7.27.1"),sQuery(id+"F0.wireOp",EDGE,"E7.27.2"),sQuery(id+"F0.wireOp",EDGE,"E7.27.3"),sQuery(id+"F0.wireOp",EDGE,"E7.27.4"),sQuery(id+"F0.wireOp",EDGE,"E7.27.5"),sQuery(id+"F0.wireOp",EDGE,"E7.28.0"),sQuery(id+"F0.wireOp",EDGE,"E7.28.1"),sQuery(id+"F0.wireOp",EDGE,"E7.28.2"),sQuery(id+"F0.wireOp",EDGE,"E7.28.3"),sQuery(id+"F0.wireOp",EDGE,"E7.28.4"),sQuery(id+"F0.wireOp",EDGE,"E7.28.5"),sQuery(id+"F0.wireOp",EDGE,"E7.29.0"),sQuery(id+"F0.wireOp",EDGE,"E7.29.1"),sQuery(id+"F0.wireOp",EDGE,"E7.29.2"),sQuery(id+"F0.wireOp",EDGE,"E7.29.3"),sQuery(id+"F0.wireOp",EDGE,"E7.29.4"),sQuery(id+"F0.wireOp",EDGE,"E7.29.5"),sQuery(id+"F0.wireOp",EDGE,"E7.30.0"),sQuery(id+"F0.wireOp",EDGE,"E7.30.1"),sQuery(id+"F0.wireOp",EDGE,"E7.30.2"),sQuery(id+"F0.wireOp",EDGE,"E7.30.3"),sQuery(id+"F0.wireOp",EDGE,"E7.30.4"),sQuery(id+"F0.wireOp",EDGE,"E7.30.5"),sQuery(id+"F0.wireOp",EDGE,"E7.31.0"),sQuery(id+"F0.wireOp",EDGE,"E7.31.1"),sQuery(id+"F0.wireOp",EDGE,"E7.31.2"),sQuery(id+"F0.wireOp",EDGE,"E7.31.3"),sQuery(id+"F0.wireOp",EDGE,"E7.31.4"),sQuery(id+"F0.wireOp",EDGE,"E7.31.5"),sQuery(id+"F0.wireOp",EDGE,"E7.32.0"),sQuery(id+"F0.wireOp",EDGE,"E7.32.1"),sQuery(id+"F0.wireOp",EDGE,"E7.32.2"),sQuery(id+"F0.wireOp",EDGE,"E7.32.3"),sQuery(id+"F0.wireOp",EDGE,"E7.32.4"),sQuery(id+"F0.wireOp",EDGE,"E7.32.5"),sQuery(id+"F0.wireOp",EDGE,"E7.33.0"),sQuery(id+"F0.wireOp",EDGE,"E7.33.1"),sQuery(id+"F0.wireOp",EDGE,"E7.33.2"),sQuery(id+"F0.wireOp",EDGE,"E7.33.3"),sQuery(id+"F0.wireOp",EDGE,"E7.33.4"),sQuery(id+"F0.wireOp",EDGE,"E7.33.5"),sQuery(id+"F0.wireOp",EDGE,"E7.34.0"),sQuery(id+"F0.wireOp",EDGE,"E7.34.1"),sQuery(id+"F0.wireOp",EDGE,"E7.34.2"),sQuery(id+"F0.wireOp",EDGE,"E7.34.3"),sQuery(id+"F0.wireOp",EDGE,"E7.34.4"),sQuery(id+"F0.wireOp",EDGE,"E7.34.5"),sQuery(id+"F0.wireOp",EDGE,"E7.35.0"),sQuery(id+"F0.wireOp",EDGE,"E7.35.1"),sQuery(id+"F0.wireOp",EDGE,"E7.35.2"),sQuery(id+"F0.wireOp",EDGE,"E7.35.3"),sQuery(id+"F0.wireOp",EDGE,"E7.35.4"),sQuery(id+"F0.wireOp",EDGE,"E7.35.5"),sQuery(id+"F0.wireOp",EDGE,"E7.36.0"),sQuery(id+"F0.wireOp",EDGE,"E7.36.1"),sQuery(id+"F0.wireOp",EDGE,"E7.36.2"),sQuery(id+"F0.wireOp",EDGE,"E7.36.3"),sQuery(id+"F0.wireOp",EDGE,"E7.36.4"),sQuery(id+"F0.wireOp",EDGE,"E7.36.5"),sQuery(id+"F0.wireOp",EDGE,"E7.37.0"),sQuery(id+"F0.wireOp",EDGE,"E7.37.1"),sQuery(id+"F0.wireOp",EDGE,"E7.37.2"),sQuery(id+"F0.wireOp",EDGE,"E7.37.3"),sQuery(id+"F0.wireOp",EDGE,"E7.37.4"),sQuery(id+"F0.wireOp",EDGE,"E7.37.5"),sQuery(id+"F0.wireOp",EDGE,"E7.38.0"),sQuery(id+"F0.wireOp",EDGE,"E7.38.1"),sQuery(id+"F0.wireOp",EDGE,"E7.38.2"),sQuery(id+"F0.wireOp",EDGE,"E7.38.3"),sQuery(id+"F0.wireOp",EDGE,"E7.38.4"),sQuery(id+"F0.wireOp",EDGE,"E7.38.5"),sQuery(id+"F0.wireOp",EDGE,"E7.39.0"),sQuery(id+"F0.wireOp",EDGE,"E7.39.1"),sQuery(id+"F0.wireOp",EDGE,"E7.39.2"),sQuery(id+"F0.wireOp",EDGE,"E7.39.3"),sQuery(id+"F0.wireOp",EDGE,"E7.39.4"),sQuery(id+"F0.wireOp",EDGE,"E7.39.5"),sQuery(id+"F0.wireOp",EDGE,"E7.40.0"),sQuery(id+"F0.wireOp",EDGE,"E7.40.1"),sQuery(id+"F0.wireOp",EDGE,"E7.40.2"),sQuery(id+"F0.wireOp",EDGE,"E7.40.3"),sQuery(id+"F0.wireOp",EDGE,"E7.40.4"),sQuery(id+"F0.wireOp",EDGE,"E7.40.5"),sQuery(id+"F0.wireOp",EDGE,"E7.41.0"),sQuery(id+"F0.wireOp",EDGE,"E7.41.1"),sQuery(id+"F0.wireOp",EDGE,"E7.41.2"),sQuery(id+"F0.wireOp",EDGE,"E7.41.3"),sQuery(id+"F0.wireOp",EDGE,"E7.41.4"),sQuery(id+"F0.wireOp",EDGE,"E7.41.5"),sQuery(id+"F0.wireOp",EDGE,"E7.42.0"),sQuery(id+"F0.wireOp",EDGE,"E7.42.1"),sQuery(id+"F0.wireOp",EDGE,"E7.42.2"),sQuery(id+"F0.wireOp",EDGE,"E7.42.3"),sQuery(id+"F0.wireOp",EDGE,"E7.42.4"),sQuery(id+"F0.wireOp",EDGE,"E7.42.5"),sQuery(id+"F0.wireOp",EDGE,"E7.43.0"),sQuery(id+"F0.wireOp",EDGE,"E7.43.1"),sQuery(id+"F0.wireOp",EDGE,"E7.43.2"),sQuery(id+"F0.wireOp",EDGE,"E7.43.3"),sQuery(id+"F0.wireOp",EDGE,"E7.43.4"),sQuery(id+"F0.wireOp",EDGE,"E7.43.5")])],"isStart":false})],"blendedInto":[makeQuery(id+"F1.opExtrude","CAP_FACE",FACE,{"disambiguationData":[OSD([sQuery(id+"F0.wireOp",EDGE,"E1"),sQuery(id+"F0.wireOp",EDGE,"E2"),sQuery(id+"F0.wireOp",EDGE,"E3"),sQuery(id+"F0.wireOp",EDGE,"E4"),sQuery(id+"F0.wireOp",EDGE,"E5"),sQuery(id+"F0.wireOp",EDGE,"E6"),sQuery(id+"F0.wireOp",EDGE,"E7.1.0"),sQuery(id+"F0.wireOp",EDGE,"E7.1.1"),sQuery(id+"F0.wireOp",EDGE,"E7.1.2"),sQuery(id+"F0.wireOp",EDGE,"E7.1.3"),sQuery(id+"F0.wireOp",EDGE,"E7.1.4"),sQuery(id+"F0.wireOp",EDGE,"E7.1.5"),sQuery(id+"F0.wireOp",EDGE,"E7.2.0"),sQuery(id+"F0.wireOp",EDGE,"E7.2.1"),sQuery(id+"F0.wireOp",EDGE,"E7.2.2"),sQuery(id+"F0.wireOp",EDGE,"E7.2.3"),sQuery(id+"F0.wireOp",EDGE,"E7.2.4"),sQuery(id+"F0.wireOp",EDGE,"E7.2.5"),sQuery(id+"F0.wireOp",EDGE,"E7.3.0"),sQuery(id+"F0.wireOp",EDGE,"E7.3.1"),sQuery(id+"F0.wireOp",EDGE,"E7.3.2"),sQuery(id+"F0.wireOp",EDGE,"E7.3.3"),sQuery(id+"F0.wireOp",EDGE,"E7.3.4"),sQuery(id+"F0.wireOp",EDGE,"E7.3.5"),sQuery(id+"F0.wireOp",EDGE,"E7.4.0"),sQuery(id+"F0.wireOp",EDGE,"E7.4.1"),sQuery(id+"F0.wireOp",EDGE,"E7.4.2"),sQuery(id+"F0.wireOp",EDGE,"E7.4.3"),sQuery(id+"F0.wireOp",EDGE,"E7.4.4"),sQuery(id+"F0.wireOp",EDGE,"E7.4.5"),sQuery(id+"F0.wireOp",EDGE,"E7.5.0"),sQuery(id+"F0.wireOp",EDGE,"E7.5.1"),sQuery(id+"F0.wireOp",EDGE,"E7.5.2"),sQuery(id+"F0.wireOp",EDGE,"E7.5.3"),sQuery(id+"F0.wireOp",EDGE,"E7.5.4"),sQuery(id+"F0.wireOp",EDGE,"E7.5.5"),sQuery(id+"F0.wireOp",EDGE,"E7.6.0"),sQuery(id+"F0.wireOp",EDGE,"E7.6.1"),sQuery(id+"F0.wireOp",EDGE,"E7.6.2"),sQuery(id+"F0.wireOp",EDGE,"E7.6.3"),sQuery(id+"F0.wireOp",EDGE,"E7.6.4"),sQuery(id+"F0.wireOp",EDGE,"E7.6.5"),sQuery(id+"F0.wireOp",EDGE,"E7.7.0"),sQuery(id+"F0.wireOp",EDGE,"E7.7.1"),sQuery(id+"F0.wireOp",EDGE,"E7.7.2"),sQuery(id+"F0.wireOp",EDGE,"E7.7.3"),sQuery(id+"F0.wireOp",EDGE,"E7.7.4"),sQuery(id+"F0.wireOp",EDGE,"E7.7.5"),sQuery(id+"F0.wireOp",EDGE,"E7.8.0"),sQuery(id+"F0.wireOp",EDGE,"E7.8.1"),sQuery(id+"F0.wireOp",EDGE,"E7.8.2"),sQuery(id+"F0.wireOp",EDGE,"E7.8.3"),sQuery(id+"F0.wireOp",EDGE,"E7.8.4"),sQuery(id+"F0.wireOp",EDGE,"E7.8.5"),sQuery(id+"F0.wireOp",EDGE,"E7.9.0"),sQuery(id+"F0.wireOp",EDGE,"E7.9.1"),sQuery(id+"F0.wireOp",EDGE,"E7.9.2"),sQuery(id+"F0.wireOp",EDGE,"E7.9.3"),sQuery(id+"F0.wireOp",EDGE,"E7.9.4"),sQuery(id+"F0.wireOp",EDGE,"E7.9.5"),sQuery(id+"F0.wireOp",EDGE,"E7.10.0"),sQuery(id+"F0.wireOp",EDGE,"E7.10.1"),sQuery(id+"F0.wireOp",EDGE,"E7.10.2"),sQuery(id+"F0.wireOp",EDGE,"E7.10.3"),sQuery(id+"F0.wireOp",EDGE,"E7.10.4"),sQuery(id+"F0.wireOp",EDGE,"E7.10.5"),subQ0,sQuery(id+"F0.wireOp",EDGE,"E7.11.1"),sQuery(id+"F0.wireOp",EDGE,"E7.11.2"),sQuery(id+"F0.wireOp",EDGE,"E7.11.3"),sQuery(id+"F0.wireOp",EDGE,"E7.11.4"),sQuery(id+"F0.wireOp",EDGE,"E7.11.5"),sQuery(id+"F0.wireOp",EDGE,"E7.12.0"),sQuery(id+"F0.wireOp",EDGE,"E7.12.1"),sQuery(id+"F0.wireOp",EDGE,"E7.12.2"),sQuery(id+"F0.wireOp",EDGE,"E7.12.3"),sQuery(id+"F0.wireOp",EDGE,"E7.12.4"),sQuery(id+"F0.wireOp",EDGE,"E7.12.5"),sQuery(id+"F0.wireOp",EDGE,"E7.13.0"),sQuery(id+"F0.wireOp",EDGE,"E7.13.1"),sQuery(id+"F0.wireOp",EDGE,"E7.13.2"),sQuery(id+"F0.wireOp",EDGE,"E7.13.3"),sQuery(id+"F0.wireOp",EDGE,"E7.13.4"),sQuery(id+"F0.wireOp",EDGE,"E7.13.5"),sQuery(id+"F0.wireOp",EDGE,"E7.14.0"),sQuery(id+"F0.wireOp",EDGE,"E7.14.1"),sQuery(id+"F0.wireOp",EDGE,"E7.14.2"),sQuery(id+"F0.wireOp",EDGE,"E7.14.3"),sQuery(id+"F0.wireOp",EDGE,"E7.14.4"),sQuery(id+"F0.wireOp",EDGE,"E7.14.5"),sQuery(id+"F0.wireOp",EDGE,"E7.15.0"),sQuery(id+"F0.wireOp",EDGE,"E7.15.1"),sQuery(id+"F0.wireOp",EDGE,"E7.15.2"),sQuery(id+"F0.wireOp",EDGE,"E7.15.3"),sQuery(id+"F0.wireOp",EDGE,"E7.15.4"),sQuery(id+"F0.wireOp",EDGE,"E7.15.5"),sQuery(id+"F0.wireOp",EDGE,"E7.16.0"),sQuery(id+"F0.wireOp",EDGE,"E7.16.1"),sQuery(id+"F0.wireOp",EDGE,"E7.16.2"),sQuery(id+"F0.wireOp",EDGE,"E7.16.3"),sQuery(id+"F0.wireOp",EDGE,"E7.16.4"),sQuery(id+"F0.wireOp",EDGE,"E7.16.5"),sQuery(id+"F0.wireOp",EDGE,"E7.17.0"),sQuery(id+"F0.wireOp",EDGE,"E7.17.1"),sQuery(id+"F0.wireOp",EDGE,"E7.17.2"),sQuery(id+"F0.wireOp",EDGE,"E7.17.3"),sQuery(id+"F0.wireOp",EDGE,"E7.17.4"),sQuery(id+"F0.wireOp",EDGE,"E7.17.5"),sQuery(id+"F0.wireOp",EDGE,"E7.18.0"),sQuery(id+"F0.wireOp",EDGE,"E7.18.1"),sQuery(id+"F0.wireOp",EDGE,"E7.18.2"),sQuery(id+"F0.wireOp",EDGE,"E7.18.3"),sQuery(id+"F0.wireOp",EDGE,"E7.18.4"),sQuery(id+"F0.wireOp",EDGE,"E7.18.5"),sQuery(id+"F0.wireOp",EDGE,"E7.19.0"),sQuery(id+"F0.wireOp",EDGE,"E7.19.1"),sQuery(id+"F0.wireOp",EDGE,"E7.19.2"),sQuery(id+"F0.wireOp",EDGE,"E7.19.3"),sQuery(id+"F0.wireOp",EDGE,"E7.19.4"),sQuery(id+"F0.wireOp",EDGE,"E7.19.5"),sQuery(id+"F0.wireOp",EDGE,"E7.20.0"),sQuery(id+"F0.wireOp",EDGE,"E7.20.1"),sQuery(id+"F0.wireOp",EDGE,"E7.20.2"),sQuery(id+"F0.wireOp",EDGE,"E7.20.3"),sQuery(id+"F0.wireOp",EDGE,"E7.20.4"),sQuery(id+"F0.wireOp",EDGE,"E7.20.5"),sQuery(id+"F0.wireOp",EDGE,"E7.21.0"),sQuery(id+"F0.wireOp",EDGE,"E7.21.1"),sQuery(id+"F0.wireOp",EDGE,"E7.21.2"),sQuery(id+"F0.wireOp",EDGE,"E7.21.3"),sQuery(id+"F0.wireOp",EDGE,"E7.21.4"),sQuery(id+"F0.wireOp",EDGE,"E7.21.5"),sQuery(id+"F0.wireOp",EDGE,"E7.22.0"),sQuery(id+"F0.wireOp",EDGE,"E7.22.1"),sQuery(id+"F0.wireOp",EDGE,"E7.22.2"),sQuery(id+"F0.wireOp",EDGE,"E7.22.3"),sQuery(id+"F0.wireOp",EDGE,"E7.22.4"),sQuery(id+"F0.wireOp",EDGE,"E7.22.5"),sQuery(id+"F0.wireOp",EDGE,"E7.23.0"),sQuery(id+"F0.wireOp",EDGE,"E7.23.1"),sQuery(id+"F0.wireOp",EDGE,"E7.23.2"),sQuery(id+"F0.wireOp",EDGE,"E7.23.3"),sQuery(id+"F0.wireOp",EDGE,"E7.23.4"),sQuery(id+"F0.wireOp",EDGE,"E7.23.5"),sQuery(id+"F0.wireOp",EDGE,"E7.24.0"),sQuery(id+"F0.wireOp",EDGE,"E7.24.1"),sQuery(id+"F0.wireOp",EDGE,"E7.24.2"),sQuery(id+"F0.wireOp",EDGE,"E7.24.3"),sQuery(id+"F0.wireOp",EDGE,"E7.24.4"),sQuery(id+"F0.wireOp",EDGE,"E7.24.5"),sQuery(id+"F0.wireOp",EDGE,"E7.25.0"),sQuery(id+"F0.wireOp",EDGE,"E7.25.1"),sQuery(id+"F0.wireOp",EDGE,"E7.25.2"),sQuery(id+"F0.wireOp",EDGE,"E7.25.3"),sQuery(id+"F0.wireOp",EDGE,"E7.25.4"),sQuery(id+"F0.wireOp",EDGE,"E7.25.5"),sQuery(id+"F0.wireOp",EDGE,"E7.26.0"),sQuery(id+"F0.wireOp",EDGE,"E7.26.1"),sQuery(id+"F0.wireOp",EDGE,"E7.26.2"),sQuery(id+"F0.wireOp",EDGE,"E7.26.3"),sQuery(id+"F0.wireOp",EDGE,"E7.26.4"),sQuery(id+"F0.wireOp",EDGE,"E7.26.5"),sQuery(id+"F0.wireOp",EDGE,"E7.27.0"),sQuery(id+"F0.wireOp",EDGE,"E7.27.1"),sQuery(id+"F0.wireOp",EDGE,"E7.27.2"),sQuery(id+"F0.wireOp",EDGE,"E7.27.3"),sQuery(id+"F0.wireOp",EDGE,"E7.27.4"),sQuery(id+"F0.wireOp",EDGE,"E7.27.5"),sQuery(id+"F0.wireOp",EDGE,"E7.28.0"),sQuery(id+"F0.wireOp",EDGE,"E7.28.1"),sQuery(id+"F0.wireOp",EDGE,"E7.28.2"),sQuery(id+"F0.wireOp",EDGE,"E7.28.3"),sQuery(id+"F0.wireOp",EDGE,"E7.28.4"),sQuery(id+"F0.wireOp",EDGE,"E7.28.5"),sQuery(id+"F0.wireOp",EDGE,"E7.29.0"),sQuery(id+"F0.wireOp",EDGE,"E7.29.1"),sQuery(id+"F0.wireOp",EDGE,"E7.29.2"),sQuery(id+"F0.wireOp",EDGE,"E7.29.3"),sQuery(id+"F0.wireOp",EDGE,"E7.29.4"),sQuery(id+"F0.wireOp",EDGE,"E7.29.5"),sQuery(id+"F0.wireOp",EDGE,"E7.30.0"),sQuery(id+"F0.wireOp",EDGE,"E7.30.1"),sQuery(id+"F0.wireOp",EDGE,"E7.30.2"),sQuery(id+"F0.wireOp",EDGE,"E7.30.3"),sQuery(id+"F0.wireOp",EDGE,"E7.30.4"),sQuery(id+"F0.wireOp",EDGE,"E7.30.5"),sQuery(id+"F0.wireOp",EDGE,"E7.31.0"),sQuery(id+"F0.wireOp",EDGE,"E7.31.1"),sQuery(id+"F0.wireOp",EDGE,"E7.31.2"),sQuery(id+"F0.wireOp",EDGE,"E7.31.3"),sQuery(id+"F0.wireOp",EDGE,"E7.31.4"),sQuery(id+"F0.wireOp",EDGE,"E7.31.5"),sQuery(id+"F0.wireOp",EDGE,"E7.32.0"),sQuery(id+"F0.wireOp",EDGE,"E7.32.1"),sQuery(id+"F0.wireOp",EDGE,"E7.32.2"),sQuery(id+"F0.wireOp",EDGE,"E7.32.3"),sQuery(id+"F0.wireOp",EDGE,"E7.32.4"),sQuery(id+"F0.wireOp",EDGE,"E7.32.5"),sQuery(id+"F0.wireOp",EDGE,"E7.33.0"),sQuery(id+"F0.wireOp",EDGE,"E7.33.1"),sQuery(id+"F0.wireOp",EDGE,"E7.33.2"),sQuery(id+"F0.wireOp",EDGE,"E7.33.3"),sQuery(id+"F0.wireOp",EDGE,"E7.33.4"),sQuery(id+"F0.wireOp",EDGE,"E7.33.5"),sQuery(id+"F0.wireOp",EDGE,"E7.34.0"),sQuery(id+"F0.wireOp",EDGE,"E7.34.1"),sQuery(id+"F0.wireOp",EDGE,"E7.34.2"),sQuery(id+"F0.wireOp",EDGE,"E7.34.3"),sQuery(id+"F0.wireOp",EDGE,"E7.34.4"),sQuery(id+"F0.wireOp",EDGE,"E7.34.5"),sQuery(id+"F0.wireOp",EDGE,"E7.35.0"),sQuery(id+"F0.wireOp",EDGE,"E7.35.1"),sQuery(id+"F0.wireOp",EDGE,"E7.35.2"),sQuery(id+"F0.wireOp",EDGE,"E7.35.3"),sQuery(id+"F0.wireOp",EDGE,"E7.35.4"),sQuery(id+"F0.wireOp",EDGE,"E7.35.5"),sQuery(id+"F0.wireOp",EDGE,"E7.36.0"),sQuery(id+"F0.wireOp",EDGE,"E7.36.1"),sQuery(id+"F0.wireOp",EDGE,"E7.36.2"),sQuery(id+"F0.wireOp",EDGE,"E7.36.3"),sQuery(id+"F0.wireOp",EDGE,"E7.36.4"),sQuery(id+"F0.wireOp",EDGE,"E7.36.5"),sQuery(id+"F0.wireOp",EDGE,"E7.37.0"),sQuery(id+"F0.wireOp",EDGE,"E7.37.1"),sQuery(id+"F0.wireOp",EDGE,"E7.37.2"),sQuery(id+"F0.wireOp",EDGE,"E7.37.3"),sQuery(id+"F0.wireOp",EDGE,"E7.37.4"),sQuery(id+"F0.wireOp",EDGE,"E7.37.5"),sQuery(id+"F0.wireOp",EDGE,"E7.38.0"),sQuery(id+"F0.wireOp",EDGE,"E7.38.1"),sQuery(id+"F0.wireOp",EDGE,"E7.38.2"),sQuery(id+"F0.wireOp",EDGE,"E7.38.3"),sQuery(id+"F0.wireOp",EDGE,"E7.38.4"),sQuery(id+"F0.wireOp",EDGE,"E7.38.5"),sQuery(id+"F0.wireOp",EDGE,"E7.39.0"),sQuery(id+"F0.wireOp",EDGE,"E7.39.1"),sQuery(id+"F0.wireOp",EDGE,"E7.39.2"),sQuery(id+"F0.wireOp",EDGE,"E7.39.3"),sQuery(id+"F0.wireOp",EDGE,"E7.39.4"),sQuery(id+"F0.wireOp",EDGE,"E7.39.5"),sQuery(id+"F0.wireOp",EDGE,"E7.40.0"),sQuery(id+"F0.wireOp",EDGE,"E7.40.1"),sQuery(id+"F0.wireOp",EDGE,"E7.40.2"),sQuery(id+"F0.wireOp",EDGE,"E7.40.3"),sQuery(id+"F0.wireOp",EDGE,"E7.40.4"),sQuery(id+"F0.wireOp",EDGE,"E7.40.5"),sQuery(id+"F0.wireOp",EDGE,"E7.41.0"),sQuery(id+"F0.wireOp",EDGE,"E7.41.1"),sQuery(id+"F0.wireOp",EDGE,"E7.41.2"),sQuery(id+"F0.wireOp",EDGE,"E7.41.3"),sQuery(id+"F0.wireOp",EDGE,"E7.41.4"),sQuery(id+"F0.wireOp",EDGE,"E7.41.5"),sQuery(id+"F0.wireOp",EDGE,"E7.42.0"),sQuery(id+"F0.wireOp",EDGE,"E7.42.1"),sQuery(id+"F0.wireOp",EDGE,"E7.42.2"),sQuery(id+"F0.wireOp",EDGE,"E7.42.3"),sQuery(id+"F0.wireOp",EDGE,"E7.42.4"),sQuery(id+"F0.wireOp",EDGE,"E7.42.5"),sQuery(id+"F0.wireOp",EDGE,"E7.43.0"),sQuery(id+"F0.wireOp",EDGE,"E7.43.1"),sQuery(id+"F0.wireOp",EDGE,"E7.43.2"),sQuery(id+"F0.wireOp",EDGE,"E7.43.3"),sQuery(id+"F0.wireOp",EDGE,"E7.43.4"),sQuery(id+"F0.wireOp",EDGE,"E7.43.5")])],"isStart":false})]}),makeQuery(id+"F2.opChamfer","BLEND_FACE",FACE,{"disambiguationData":[OSD([subQ0])]})],"blendedInto":[makeQuery(id+"F2.opChamfer","BLEND_FACE",FACE,{"disambiguationData":[OSD([subQ0])]})]});}
            var Q18;
            {var subQ0=sQuery(id+"F0.wireOp",EDGE,"E7.9.0");Q18=makeQuery(id+"F8.opChamfer","BLEND_EDGE",EDGE,{"blendedFrom":[makeQuery(id+"F2.opChamfer","BLEND_EDGE",EDGE,{"blendedFrom":[makeQuery(id+"F1.opExtrude","CAP_EDGE",EDGE,{"disambiguationData":[OSD([subQ0])],"isStart":false}),makeQuery(id+"F1.opExtrude","CAP_FACE",FACE,{"disambiguationData":[OSD([sQuery(id+"F0.wireOp",EDGE,"E1"),sQuery(id+"F0.wireOp",EDGE,"E2"),sQuery(id+"F0.wireOp",EDGE,"E3"),sQuery(id+"F0.wireOp",EDGE,"E4"),sQuery(id+"F0.wireOp",EDGE,"E5"),sQuery(id+"F0.wireOp",EDGE,"E6"),sQuery(id+"F0.wireOp",EDGE,"E7.1.0"),sQuery(id+"F0.wireOp",EDGE,"E7.1.1"),sQuery(id+"F0.wireOp",EDGE,"E7.1.2"),sQuery(id+"F0.wireOp",EDGE,"E7.1.3"),sQuery(id+"F0.wireOp",EDGE,"E7.1.4"),sQuery(id+"F0.wireOp",EDGE,"E7.1.5"),sQuery(id+"F0.wireOp",EDGE,"E7.2.0"),sQuery(id+"F0.wireOp",EDGE,"E7.2.1"),sQuery(id+"F0.wireOp",EDGE,"E7.2.2"),sQuery(id+"F0.wireOp",EDGE,"E7.2.3"),sQuery(id+"F0.wireOp",EDGE,"E7.2.4"),sQuery(id+"F0.wireOp",EDGE,"E7.2.5"),sQuery(id+"F0.wireOp",EDGE,"E7.3.0"),sQuery(id+"F0.wireOp",EDGE,"E7.3.1"),sQuery(id+"F0.wireOp",EDGE,"E7.3.2"),sQuery(id+"F0.wireOp",EDGE,"E7.3.3"),sQuery(id+"F0.wireOp",EDGE,"E7.3.4"),sQuery(id+"F0.wireOp",EDGE,"E7.3.5"),sQuery(id+"F0.wireOp",EDGE,"E7.4.0"),sQuery(id+"F0.wireOp",EDGE,"E7.4.1"),sQuery(id+"F0.wireOp",EDGE,"E7.4.2"),sQuery(id+"F0.wireOp",EDGE,"E7.4.3"),sQuery(id+"F0.wireOp",EDGE,"E7.4.4"),sQuery(id+"F0.wireOp",EDGE,"E7.4.5"),sQuery(id+"F0.wireOp",EDGE,"E7.5.0"),sQuery(id+"F0.wireOp",EDGE,"E7.5.1"),sQuery(id+"F0.wireOp",EDGE,"E7.5.2"),sQuery(id+"F0.wireOp",EDGE,"E7.5.3"),sQuery(id+"F0.wireOp",EDGE,"E7.5.4"),sQuery(id+"F0.wireOp",EDGE,"E7.5.5"),sQuery(id+"F0.wireOp",EDGE,"E7.6.0"),sQuery(id+"F0.wireOp",EDGE,"E7.6.1"),sQuery(id+"F0.wireOp",EDGE,"E7.6.2"),sQuery(id+"F0.wireOp",EDGE,"E7.6.3"),sQuery(id+"F0.wireOp",EDGE,"E7.6.4"),sQuery(id+"F0.wireOp",EDGE,"E7.6.5"),sQuery(id+"F0.wireOp",EDGE,"E7.7.0"),sQuery(id+"F0.wireOp",EDGE,"E7.7.1"),sQuery(id+"F0.wireOp",EDGE,"E7.7.2"),sQuery(id+"F0.wireOp",EDGE,"E7.7.3"),sQuery(id+"F0.wireOp",EDGE,"E7.7.4"),sQuery(id+"F0.wireOp",EDGE,"E7.7.5"),sQuery(id+"F0.wireOp",EDGE,"E7.8.0"),sQuery(id+"F0.wireOp",EDGE,"E7.8.1"),sQuery(id+"F0.wireOp",EDGE,"E7.8.2"),sQuery(id+"F0.wireOp",EDGE,"E7.8.3"),sQuery(id+"F0.wireOp",EDGE,"E7.8.4"),sQuery(id+"F0.wireOp",EDGE,"E7.8.5"),subQ0,sQuery(id+"F0.wireOp",EDGE,"E7.9.1"),sQuery(id+"F0.wireOp",EDGE,"E7.9.2"),sQuery(id+"F0.wireOp",EDGE,"E7.9.3"),sQuery(id+"F0.wireOp",EDGE,"E7.9.4"),sQuery(id+"F0.wireOp",EDGE,"E7.9.5"),sQuery(id+"F0.wireOp",EDGE,"E7.10.0"),sQuery(id+"F0.wireOp",EDGE,"E7.10.1"),sQuery(id+"F0.wireOp",EDGE,"E7.10.2"),sQuery(id+"F0.wireOp",EDGE,"E7.10.3"),sQuery(id+"F0.wireOp",EDGE,"E7.10.4"),sQuery(id+"F0.wireOp",EDGE,"E7.10.5"),sQuery(id+"F0.wireOp",EDGE,"E7.11.0"),sQuery(id+"F0.wireOp",EDGE,"E7.11.1"),sQuery(id+"F0.wireOp",EDGE,"E7.11.2"),sQuery(id+"F0.wireOp",EDGE,"E7.11.3"),sQuery(id+"F0.wireOp",EDGE,"E7.11.4"),sQuery(id+"F0.wireOp",EDGE,"E7.11.5"),sQuery(id+"F0.wireOp",EDGE,"E7.12.0"),sQuery(id+"F0.wireOp",EDGE,"E7.12.1"),sQuery(id+"F0.wireOp",EDGE,"E7.12.2"),sQuery(id+"F0.wireOp",EDGE,"E7.12.3"),sQuery(id+"F0.wireOp",EDGE,"E7.12.4"),sQuery(id+"F0.wireOp",EDGE,"E7.12.5"),sQuery(id+"F0.wireOp",EDGE,"E7.13.0"),sQuery(id+"F0.wireOp",EDGE,"E7.13.1"),sQuery(id+"F0.wireOp",EDGE,"E7.13.2"),sQuery(id+"F0.wireOp",EDGE,"E7.13.3"),sQuery(id+"F0.wireOp",EDGE,"E7.13.4"),sQuery(id+"F0.wireOp",EDGE,"E7.13.5"),sQuery(id+"F0.wireOp",EDGE,"E7.14.0"),sQuery(id+"F0.wireOp",EDGE,"E7.14.1"),sQuery(id+"F0.wireOp",EDGE,"E7.14.2"),sQuery(id+"F0.wireOp",EDGE,"E7.14.3"),sQuery(id+"F0.wireOp",EDGE,"E7.14.4"),sQuery(id+"F0.wireOp",EDGE,"E7.14.5"),sQuery(id+"F0.wireOp",EDGE,"E7.15.0"),sQuery(id+"F0.wireOp",EDGE,"E7.15.1"),sQuery(id+"F0.wireOp",EDGE,"E7.15.2"),sQuery(id+"F0.wireOp",EDGE,"E7.15.3"),sQuery(id+"F0.wireOp",EDGE,"E7.15.4"),sQuery(id+"F0.wireOp",EDGE,"E7.15.5"),sQuery(id+"F0.wireOp",EDGE,"E7.16.0"),sQuery(id+"F0.wireOp",EDGE,"E7.16.1"),sQuery(id+"F0.wireOp",EDGE,"E7.16.2"),sQuery(id+"F0.wireOp",EDGE,"E7.16.3"),sQuery(id+"F0.wireOp",EDGE,"E7.16.4"),sQuery(id+"F0.wireOp",EDGE,"E7.16.5"),sQuery(id+"F0.wireOp",EDGE,"E7.17.0"),sQuery(id+"F0.wireOp",EDGE,"E7.17.1"),sQuery(id+"F0.wireOp",EDGE,"E7.17.2"),sQuery(id+"F0.wireOp",EDGE,"E7.17.3"),sQuery(id+"F0.wireOp",EDGE,"E7.17.4"),sQuery(id+"F0.wireOp",EDGE,"E7.17.5"),sQuery(id+"F0.wireOp",EDGE,"E7.18.0"),sQuery(id+"F0.wireOp",EDGE,"E7.18.1"),sQuery(id+"F0.wireOp",EDGE,"E7.18.2"),sQuery(id+"F0.wireOp",EDGE,"E7.18.3"),sQuery(id+"F0.wireOp",EDGE,"E7.18.4"),sQuery(id+"F0.wireOp",EDGE,"E7.18.5"),sQuery(id+"F0.wireOp",EDGE,"E7.19.0"),sQuery(id+"F0.wireOp",EDGE,"E7.19.1"),sQuery(id+"F0.wireOp",EDGE,"E7.19.2"),sQuery(id+"F0.wireOp",EDGE,"E7.19.3"),sQuery(id+"F0.wireOp",EDGE,"E7.19.4"),sQuery(id+"F0.wireOp",EDGE,"E7.19.5"),sQuery(id+"F0.wireOp",EDGE,"E7.20.0"),sQuery(id+"F0.wireOp",EDGE,"E7.20.1"),sQuery(id+"F0.wireOp",EDGE,"E7.20.2"),sQuery(id+"F0.wireOp",EDGE,"E7.20.3"),sQuery(id+"F0.wireOp",EDGE,"E7.20.4"),sQuery(id+"F0.wireOp",EDGE,"E7.20.5"),sQuery(id+"F0.wireOp",EDGE,"E7.21.0"),sQuery(id+"F0.wireOp",EDGE,"E7.21.1"),sQuery(id+"F0.wireOp",EDGE,"E7.21.2"),sQuery(id+"F0.wireOp",EDGE,"E7.21.3"),sQuery(id+"F0.wireOp",EDGE,"E7.21.4"),sQuery(id+"F0.wireOp",EDGE,"E7.21.5"),sQuery(id+"F0.wireOp",EDGE,"E7.22.0"),sQuery(id+"F0.wireOp",EDGE,"E7.22.1"),sQuery(id+"F0.wireOp",EDGE,"E7.22.2"),sQuery(id+"F0.wireOp",EDGE,"E7.22.3"),sQuery(id+"F0.wireOp",EDGE,"E7.22.4"),sQuery(id+"F0.wireOp",EDGE,"E7.22.5"),sQuery(id+"F0.wireOp",EDGE,"E7.23.0"),sQuery(id+"F0.wireOp",EDGE,"E7.23.1"),sQuery(id+"F0.wireOp",EDGE,"E7.23.2"),sQuery(id+"F0.wireOp",EDGE,"E7.23.3"),sQuery(id+"F0.wireOp",EDGE,"E7.23.4"),sQuery(id+"F0.wireOp",EDGE,"E7.23.5"),sQuery(id+"F0.wireOp",EDGE,"E7.24.0"),sQuery(id+"F0.wireOp",EDGE,"E7.24.1"),sQuery(id+"F0.wireOp",EDGE,"E7.24.2"),sQuery(id+"F0.wireOp",EDGE,"E7.24.3"),sQuery(id+"F0.wireOp",EDGE,"E7.24.4"),sQuery(id+"F0.wireOp",EDGE,"E7.24.5"),sQuery(id+"F0.wireOp",EDGE,"E7.25.0"),sQuery(id+"F0.wireOp",EDGE,"E7.25.1"),sQuery(id+"F0.wireOp",EDGE,"E7.25.2"),sQuery(id+"F0.wireOp",EDGE,"E7.25.3"),sQuery(id+"F0.wireOp",EDGE,"E7.25.4"),sQuery(id+"F0.wireOp",EDGE,"E7.25.5"),sQuery(id+"F0.wireOp",EDGE,"E7.26.0"),sQuery(id+"F0.wireOp",EDGE,"E7.26.1"),sQuery(id+"F0.wireOp",EDGE,"E7.26.2"),sQuery(id+"F0.wireOp",EDGE,"E7.26.3"),sQuery(id+"F0.wireOp",EDGE,"E7.26.4"),sQuery(id+"F0.wireOp",EDGE,"E7.26.5"),sQuery(id+"F0.wireOp",EDGE,"E7.27.0"),sQuery(id+"F0.wireOp",EDGE,"E7.27.1"),sQuery(id+"F0.wireOp",EDGE,"E7.27.2"),sQuery(id+"F0.wireOp",EDGE,"E7.27.3"),sQuery(id+"F0.wireOp",EDGE,"E7.27.4"),sQuery(id+"F0.wireOp",EDGE,"E7.27.5"),sQuery(id+"F0.wireOp",EDGE,"E7.28.0"),sQuery(id+"F0.wireOp",EDGE,"E7.28.1"),sQuery(id+"F0.wireOp",EDGE,"E7.28.2"),sQuery(id+"F0.wireOp",EDGE,"E7.28.3"),sQuery(id+"F0.wireOp",EDGE,"E7.28.4"),sQuery(id+"F0.wireOp",EDGE,"E7.28.5"),sQuery(id+"F0.wireOp",EDGE,"E7.29.0"),sQuery(id+"F0.wireOp",EDGE,"E7.29.1"),sQuery(id+"F0.wireOp",EDGE,"E7.29.2"),sQuery(id+"F0.wireOp",EDGE,"E7.29.3"),sQuery(id+"F0.wireOp",EDGE,"E7.29.4"),sQuery(id+"F0.wireOp",EDGE,"E7.29.5"),sQuery(id+"F0.wireOp",EDGE,"E7.30.0"),sQuery(id+"F0.wireOp",EDGE,"E7.30.1"),sQuery(id+"F0.wireOp",EDGE,"E7.30.2"),sQuery(id+"F0.wireOp",EDGE,"E7.30.3"),sQuery(id+"F0.wireOp",EDGE,"E7.30.4"),sQuery(id+"F0.wireOp",EDGE,"E7.30.5"),sQuery(id+"F0.wireOp",EDGE,"E7.31.0"),sQuery(id+"F0.wireOp",EDGE,"E7.31.1"),sQuery(id+"F0.wireOp",EDGE,"E7.31.2"),sQuery(id+"F0.wireOp",EDGE,"E7.31.3"),sQuery(id+"F0.wireOp",EDGE,"E7.31.4"),sQuery(id+"F0.wireOp",EDGE,"E7.31.5"),sQuery(id+"F0.wireOp",EDGE,"E7.32.0"),sQuery(id+"F0.wireOp",EDGE,"E7.32.1"),sQuery(id+"F0.wireOp",EDGE,"E7.32.2"),sQuery(id+"F0.wireOp",EDGE,"E7.32.3"),sQuery(id+"F0.wireOp",EDGE,"E7.32.4"),sQuery(id+"F0.wireOp",EDGE,"E7.32.5"),sQuery(id+"F0.wireOp",EDGE,"E7.33.0"),sQuery(id+"F0.wireOp",EDGE,"E7.33.1"),sQuery(id+"F0.wireOp",EDGE,"E7.33.2"),sQuery(id+"F0.wireOp",EDGE,"E7.33.3"),sQuery(id+"F0.wireOp",EDGE,"E7.33.4"),sQuery(id+"F0.wireOp",EDGE,"E7.33.5"),sQuery(id+"F0.wireOp",EDGE,"E7.34.0"),sQuery(id+"F0.wireOp",EDGE,"E7.34.1"),sQuery(id+"F0.wireOp",EDGE,"E7.34.2"),sQuery(id+"F0.wireOp",EDGE,"E7.34.3"),sQuery(id+"F0.wireOp",EDGE,"E7.34.4"),sQuery(id+"F0.wireOp",EDGE,"E7.34.5"),sQuery(id+"F0.wireOp",EDGE,"E7.35.0"),sQuery(id+"F0.wireOp",EDGE,"E7.35.1"),sQuery(id+"F0.wireOp",EDGE,"E7.35.2"),sQuery(id+"F0.wireOp",EDGE,"E7.35.3"),sQuery(id+"F0.wireOp",EDGE,"E7.35.4"),sQuery(id+"F0.wireOp",EDGE,"E7.35.5"),sQuery(id+"F0.wireOp",EDGE,"E7.36.0"),sQuery(id+"F0.wireOp",EDGE,"E7.36.1"),sQuery(id+"F0.wireOp",EDGE,"E7.36.2"),sQuery(id+"F0.wireOp",EDGE,"E7.36.3"),sQuery(id+"F0.wireOp",EDGE,"E7.36.4"),sQuery(id+"F0.wireOp",EDGE,"E7.36.5"),sQuery(id+"F0.wireOp",EDGE,"E7.37.0"),sQuery(id+"F0.wireOp",EDGE,"E7.37.1"),sQuery(id+"F0.wireOp",EDGE,"E7.37.2"),sQuery(id+"F0.wireOp",EDGE,"E7.37.3"),sQuery(id+"F0.wireOp",EDGE,"E7.37.4"),sQuery(id+"F0.wireOp",EDGE,"E7.37.5"),sQuery(id+"F0.wireOp",EDGE,"E7.38.0"),sQuery(id+"F0.wireOp",EDGE,"E7.38.1"),sQuery(id+"F0.wireOp",EDGE,"E7.38.2"),sQuery(id+"F0.wireOp",EDGE,"E7.38.3"),sQuery(id+"F0.wireOp",EDGE,"E7.38.4"),sQuery(id+"F0.wireOp",EDGE,"E7.38.5"),sQuery(id+"F0.wireOp",EDGE,"E7.39.0"),sQuery(id+"F0.wireOp",EDGE,"E7.39.1"),sQuery(id+"F0.wireOp",EDGE,"E7.39.2"),sQuery(id+"F0.wireOp",EDGE,"E7.39.3"),sQuery(id+"F0.wireOp",EDGE,"E7.39.4"),sQuery(id+"F0.wireOp",EDGE,"E7.39.5"),sQuery(id+"F0.wireOp",EDGE,"E7.40.0"),sQuery(id+"F0.wireOp",EDGE,"E7.40.1"),sQuery(id+"F0.wireOp",EDGE,"E7.40.2"),sQuery(id+"F0.wireOp",EDGE,"E7.40.3"),sQuery(id+"F0.wireOp",EDGE,"E7.40.4"),sQuery(id+"F0.wireOp",EDGE,"E7.40.5"),sQuery(id+"F0.wireOp",EDGE,"E7.41.0"),sQuery(id+"F0.wireOp",EDGE,"E7.41.1"),sQuery(id+"F0.wireOp",EDGE,"E7.41.2"),sQuery(id+"F0.wireOp",EDGE,"E7.41.3"),sQuery(id+"F0.wireOp",EDGE,"E7.41.4"),sQuery(id+"F0.wireOp",EDGE,"E7.41.5"),sQuery(id+"F0.wireOp",EDGE,"E7.42.0"),sQuery(id+"F0.wireOp",EDGE,"E7.42.1"),sQuery(id+"F0.wireOp",EDGE,"E7.42.2"),sQuery(id+"F0.wireOp",EDGE,"E7.42.3"),sQuery(id+"F0.wireOp",EDGE,"E7.42.4"),sQuery(id+"F0.wireOp",EDGE,"E7.42.5"),sQuery(id+"F0.wireOp",EDGE,"E7.43.0"),sQuery(id+"F0.wireOp",EDGE,"E7.43.1"),sQuery(id+"F0.wireOp",EDGE,"E7.43.2"),sQuery(id+"F0.wireOp",EDGE,"E7.43.3"),sQuery(id+"F0.wireOp",EDGE,"E7.43.4"),sQuery(id+"F0.wireOp",EDGE,"E7.43.5")])],"isStart":false})],"blendedInto":[makeQuery(id+"F1.opExtrude","CAP_FACE",FACE,{"disambiguationData":[OSD([sQuery(id+"F0.wireOp",EDGE,"E1"),sQuery(id+"F0.wireOp",EDGE,"E2"),sQuery(id+"F0.wireOp",EDGE,"E3"),sQuery(id+"F0.wireOp",EDGE,"E4"),sQuery(id+"F0.wireOp",EDGE,"E5"),sQuery(id+"F0.wireOp",EDGE,"E6"),sQuery(id+"F0.wireOp",EDGE,"E7.1.0"),sQuery(id+"F0.wireOp",EDGE,"E7.1.1"),sQuery(id+"F0.wireOp",EDGE,"E7.1.2"),sQuery(id+"F0.wireOp",EDGE,"E7.1.3"),sQuery(id+"F0.wireOp",EDGE,"E7.1.4"),sQuery(id+"F0.wireOp",EDGE,"E7.1.5"),sQuery(id+"F0.wireOp",EDGE,"E7.2.0"),sQuery(id+"F0.wireOp",EDGE,"E7.2.1"),sQuery(id+"F0.wireOp",EDGE,"E7.2.2"),sQuery(id+"F0.wireOp",EDGE,"E7.2.3"),sQuery(id+"F0.wireOp",EDGE,"E7.2.4"),sQuery(id+"F0.wireOp",EDGE,"E7.2.5"),sQuery(id+"F0.wireOp",EDGE,"E7.3.0"),sQuery(id+"F0.wireOp",EDGE,"E7.3.1"),sQuery(id+"F0.wireOp",EDGE,"E7.3.2"),sQuery(id+"F0.wireOp",EDGE,"E7.3.3"),sQuery(id+"F0.wireOp",EDGE,"E7.3.4"),sQuery(id+"F0.wireOp",EDGE,"E7.3.5"),sQuery(id+"F0.wireOp",EDGE,"E7.4.0"),sQuery(id+"F0.wireOp",EDGE,"E7.4.1"),sQuery(id+"F0.wireOp",EDGE,"E7.4.2"),sQuery(id+"F0.wireOp",EDGE,"E7.4.3"),sQuery(id+"F0.wireOp",EDGE,"E7.4.4"),sQuery(id+"F0.wireOp",EDGE,"E7.4.5"),sQuery(id+"F0.wireOp",EDGE,"E7.5.0"),sQuery(id+"F0.wireOp",EDGE,"E7.5.1"),sQuery(id+"F0.wireOp",EDGE,"E7.5.2"),sQuery(id+"F0.wireOp",EDGE,"E7.5.3"),sQuery(id+"F0.wireOp",EDGE,"E7.5.4"),sQuery(id+"F0.wireOp",EDGE,"E7.5.5"),sQuery(id+"F0.wireOp",EDGE,"E7.6.0"),sQuery(id+"F0.wireOp",EDGE,"E7.6.1"),sQuery(id+"F0.wireOp",EDGE,"E7.6.2"),sQuery(id+"F0.wireOp",EDGE,"E7.6.3"),sQuery(id+"F0.wireOp",EDGE,"E7.6.4"),sQuery(id+"F0.wireOp",EDGE,"E7.6.5"),sQuery(id+"F0.wireOp",EDGE,"E7.7.0"),sQuery(id+"F0.wireOp",EDGE,"E7.7.1"),sQuery(id+"F0.wireOp",EDGE,"E7.7.2"),sQuery(id+"F0.wireOp",EDGE,"E7.7.3"),sQuery(id+"F0.wireOp",EDGE,"E7.7.4"),sQuery(id+"F0.wireOp",EDGE,"E7.7.5"),sQuery(id+"F0.wireOp",EDGE,"E7.8.0"),sQuery(id+"F0.wireOp",EDGE,"E7.8.1"),sQuery(id+"F0.wireOp",EDGE,"E7.8.2"),sQuery(id+"F0.wireOp",EDGE,"E7.8.3"),sQuery(id+"F0.wireOp",EDGE,"E7.8.4"),sQuery(id+"F0.wireOp",EDGE,"E7.8.5"),subQ0,sQuery(id+"F0.wireOp",EDGE,"E7.9.1"),sQuery(id+"F0.wireOp",EDGE,"E7.9.2"),sQuery(id+"F0.wireOp",EDGE,"E7.9.3"),sQuery(id+"F0.wireOp",EDGE,"E7.9.4"),sQuery(id+"F0.wireOp",EDGE,"E7.9.5"),sQuery(id+"F0.wireOp",EDGE,"E7.10.0"),sQuery(id+"F0.wireOp",EDGE,"E7.10.1"),sQuery(id+"F0.wireOp",EDGE,"E7.10.2"),sQuery(id+"F0.wireOp",EDGE,"E7.10.3"),sQuery(id+"F0.wireOp",EDGE,"E7.10.4"),sQuery(id+"F0.wireOp",EDGE,"E7.10.5"),sQuery(id+"F0.wireOp",EDGE,"E7.11.0"),sQuery(id+"F0.wireOp",EDGE,"E7.11.1"),sQuery(id+"F0.wireOp",EDGE,"E7.11.2"),sQuery(id+"F0.wireOp",EDGE,"E7.11.3"),sQuery(id+"F0.wireOp",EDGE,"E7.11.4"),sQuery(id+"F0.wireOp",EDGE,"E7.11.5"),sQuery(id+"F0.wireOp",EDGE,"E7.12.0"),sQuery(id+"F0.wireOp",EDGE,"E7.12.1"),sQuery(id+"F0.wireOp",EDGE,"E7.12.2"),sQuery(id+"F0.wireOp",EDGE,"E7.12.3"),sQuery(id+"F0.wireOp",EDGE,"E7.12.4"),sQuery(id+"F0.wireOp",EDGE,"E7.12.5"),sQuery(id+"F0.wireOp",EDGE,"E7.13.0"),sQuery(id+"F0.wireOp",EDGE,"E7.13.1"),sQuery(id+"F0.wireOp",EDGE,"E7.13.2"),sQuery(id+"F0.wireOp",EDGE,"E7.13.3"),sQuery(id+"F0.wireOp",EDGE,"E7.13.4"),sQuery(id+"F0.wireOp",EDGE,"E7.13.5"),sQuery(id+"F0.wireOp",EDGE,"E7.14.0"),sQuery(id+"F0.wireOp",EDGE,"E7.14.1"),sQuery(id+"F0.wireOp",EDGE,"E7.14.2"),sQuery(id+"F0.wireOp",EDGE,"E7.14.3"),sQuery(id+"F0.wireOp",EDGE,"E7.14.4"),sQuery(id+"F0.wireOp",EDGE,"E7.14.5"),sQuery(id+"F0.wireOp",EDGE,"E7.15.0"),sQuery(id+"F0.wireOp",EDGE,"E7.15.1"),sQuery(id+"F0.wireOp",EDGE,"E7.15.2"),sQuery(id+"F0.wireOp",EDGE,"E7.15.3"),sQuery(id+"F0.wireOp",EDGE,"E7.15.4"),sQuery(id+"F0.wireOp",EDGE,"E7.15.5"),sQuery(id+"F0.wireOp",EDGE,"E7.16.0"),sQuery(id+"F0.wireOp",EDGE,"E7.16.1"),sQuery(id+"F0.wireOp",EDGE,"E7.16.2"),sQuery(id+"F0.wireOp",EDGE,"E7.16.3"),sQuery(id+"F0.wireOp",EDGE,"E7.16.4"),sQuery(id+"F0.wireOp",EDGE,"E7.16.5"),sQuery(id+"F0.wireOp",EDGE,"E7.17.0"),sQuery(id+"F0.wireOp",EDGE,"E7.17.1"),sQuery(id+"F0.wireOp",EDGE,"E7.17.2"),sQuery(id+"F0.wireOp",EDGE,"E7.17.3"),sQuery(id+"F0.wireOp",EDGE,"E7.17.4"),sQuery(id+"F0.wireOp",EDGE,"E7.17.5"),sQuery(id+"F0.wireOp",EDGE,"E7.18.0"),sQuery(id+"F0.wireOp",EDGE,"E7.18.1"),sQuery(id+"F0.wireOp",EDGE,"E7.18.2"),sQuery(id+"F0.wireOp",EDGE,"E7.18.3"),sQuery(id+"F0.wireOp",EDGE,"E7.18.4"),sQuery(id+"F0.wireOp",EDGE,"E7.18.5"),sQuery(id+"F0.wireOp",EDGE,"E7.19.0"),sQuery(id+"F0.wireOp",EDGE,"E7.19.1"),sQuery(id+"F0.wireOp",EDGE,"E7.19.2"),sQuery(id+"F0.wireOp",EDGE,"E7.19.3"),sQuery(id+"F0.wireOp",EDGE,"E7.19.4"),sQuery(id+"F0.wireOp",EDGE,"E7.19.5"),sQuery(id+"F0.wireOp",EDGE,"E7.20.0"),sQuery(id+"F0.wireOp",EDGE,"E7.20.1"),sQuery(id+"F0.wireOp",EDGE,"E7.20.2"),sQuery(id+"F0.wireOp",EDGE,"E7.20.3"),sQuery(id+"F0.wireOp",EDGE,"E7.20.4"),sQuery(id+"F0.wireOp",EDGE,"E7.20.5"),sQuery(id+"F0.wireOp",EDGE,"E7.21.0"),sQuery(id+"F0.wireOp",EDGE,"E7.21.1"),sQuery(id+"F0.wireOp",EDGE,"E7.21.2"),sQuery(id+"F0.wireOp",EDGE,"E7.21.3"),sQuery(id+"F0.wireOp",EDGE,"E7.21.4"),sQuery(id+"F0.wireOp",EDGE,"E7.21.5"),sQuery(id+"F0.wireOp",EDGE,"E7.22.0"),sQuery(id+"F0.wireOp",EDGE,"E7.22.1"),sQuery(id+"F0.wireOp",EDGE,"E7.22.2"),sQuery(id+"F0.wireOp",EDGE,"E7.22.3"),sQuery(id+"F0.wireOp",EDGE,"E7.22.4"),sQuery(id+"F0.wireOp",EDGE,"E7.22.5"),sQuery(id+"F0.wireOp",EDGE,"E7.23.0"),sQuery(id+"F0.wireOp",EDGE,"E7.23.1"),sQuery(id+"F0.wireOp",EDGE,"E7.23.2"),sQuery(id+"F0.wireOp",EDGE,"E7.23.3"),sQuery(id+"F0.wireOp",EDGE,"E7.23.4"),sQuery(id+"F0.wireOp",EDGE,"E7.23.5"),sQuery(id+"F0.wireOp",EDGE,"E7.24.0"),sQuery(id+"F0.wireOp",EDGE,"E7.24.1"),sQuery(id+"F0.wireOp",EDGE,"E7.24.2"),sQuery(id+"F0.wireOp",EDGE,"E7.24.3"),sQuery(id+"F0.wireOp",EDGE,"E7.24.4"),sQuery(id+"F0.wireOp",EDGE,"E7.24.5"),sQuery(id+"F0.wireOp",EDGE,"E7.25.0"),sQuery(id+"F0.wireOp",EDGE,"E7.25.1"),sQuery(id+"F0.wireOp",EDGE,"E7.25.2"),sQuery(id+"F0.wireOp",EDGE,"E7.25.3"),sQuery(id+"F0.wireOp",EDGE,"E7.25.4"),sQuery(id+"F0.wireOp",EDGE,"E7.25.5"),sQuery(id+"F0.wireOp",EDGE,"E7.26.0"),sQuery(id+"F0.wireOp",EDGE,"E7.26.1"),sQuery(id+"F0.wireOp",EDGE,"E7.26.2"),sQuery(id+"F0.wireOp",EDGE,"E7.26.3"),sQuery(id+"F0.wireOp",EDGE,"E7.26.4"),sQuery(id+"F0.wireOp",EDGE,"E7.26.5"),sQuery(id+"F0.wireOp",EDGE,"E7.27.0"),sQuery(id+"F0.wireOp",EDGE,"E7.27.1"),sQuery(id+"F0.wireOp",EDGE,"E7.27.2"),sQuery(id+"F0.wireOp",EDGE,"E7.27.3"),sQuery(id+"F0.wireOp",EDGE,"E7.27.4"),sQuery(id+"F0.wireOp",EDGE,"E7.27.5"),sQuery(id+"F0.wireOp",EDGE,"E7.28.0"),sQuery(id+"F0.wireOp",EDGE,"E7.28.1"),sQuery(id+"F0.wireOp",EDGE,"E7.28.2"),sQuery(id+"F0.wireOp",EDGE,"E7.28.3"),sQuery(id+"F0.wireOp",EDGE,"E7.28.4"),sQuery(id+"F0.wireOp",EDGE,"E7.28.5"),sQuery(id+"F0.wireOp",EDGE,"E7.29.0"),sQuery(id+"F0.wireOp",EDGE,"E7.29.1"),sQuery(id+"F0.wireOp",EDGE,"E7.29.2"),sQuery(id+"F0.wireOp",EDGE,"E7.29.3"),sQuery(id+"F0.wireOp",EDGE,"E7.29.4"),sQuery(id+"F0.wireOp",EDGE,"E7.29.5"),sQuery(id+"F0.wireOp",EDGE,"E7.30.0"),sQuery(id+"F0.wireOp",EDGE,"E7.30.1"),sQuery(id+"F0.wireOp",EDGE,"E7.30.2"),sQuery(id+"F0.wireOp",EDGE,"E7.30.3"),sQuery(id+"F0.wireOp",EDGE,"E7.30.4"),sQuery(id+"F0.wireOp",EDGE,"E7.30.5"),sQuery(id+"F0.wireOp",EDGE,"E7.31.0"),sQuery(id+"F0.wireOp",EDGE,"E7.31.1"),sQuery(id+"F0.wireOp",EDGE,"E7.31.2"),sQuery(id+"F0.wireOp",EDGE,"E7.31.3"),sQuery(id+"F0.wireOp",EDGE,"E7.31.4"),sQuery(id+"F0.wireOp",EDGE,"E7.31.5"),sQuery(id+"F0.wireOp",EDGE,"E7.32.0"),sQuery(id+"F0.wireOp",EDGE,"E7.32.1"),sQuery(id+"F0.wireOp",EDGE,"E7.32.2"),sQuery(id+"F0.wireOp",EDGE,"E7.32.3"),sQuery(id+"F0.wireOp",EDGE,"E7.32.4"),sQuery(id+"F0.wireOp",EDGE,"E7.32.5"),sQuery(id+"F0.wireOp",EDGE,"E7.33.0"),sQuery(id+"F0.wireOp",EDGE,"E7.33.1"),sQuery(id+"F0.wireOp",EDGE,"E7.33.2"),sQuery(id+"F0.wireOp",EDGE,"E7.33.3"),sQuery(id+"F0.wireOp",EDGE,"E7.33.4"),sQuery(id+"F0.wireOp",EDGE,"E7.33.5"),sQuery(id+"F0.wireOp",EDGE,"E7.34.0"),sQuery(id+"F0.wireOp",EDGE,"E7.34.1"),sQuery(id+"F0.wireOp",EDGE,"E7.34.2"),sQuery(id+"F0.wireOp",EDGE,"E7.34.3"),sQuery(id+"F0.wireOp",EDGE,"E7.34.4"),sQuery(id+"F0.wireOp",EDGE,"E7.34.5"),sQuery(id+"F0.wireOp",EDGE,"E7.35.0"),sQuery(id+"F0.wireOp",EDGE,"E7.35.1"),sQuery(id+"F0.wireOp",EDGE,"E7.35.2"),sQuery(id+"F0.wireOp",EDGE,"E7.35.3"),sQuery(id+"F0.wireOp",EDGE,"E7.35.4"),sQuery(id+"F0.wireOp",EDGE,"E7.35.5"),sQuery(id+"F0.wireOp",EDGE,"E7.36.0"),sQuery(id+"F0.wireOp",EDGE,"E7.36.1"),sQuery(id+"F0.wireOp",EDGE,"E7.36.2"),sQuery(id+"F0.wireOp",EDGE,"E7.36.3"),sQuery(id+"F0.wireOp",EDGE,"E7.36.4"),sQuery(id+"F0.wireOp",EDGE,"E7.36.5"),sQuery(id+"F0.wireOp",EDGE,"E7.37.0"),sQuery(id+"F0.wireOp",EDGE,"E7.37.1"),sQuery(id+"F0.wireOp",EDGE,"E7.37.2"),sQuery(id+"F0.wireOp",EDGE,"E7.37.3"),sQuery(id+"F0.wireOp",EDGE,"E7.37.4"),sQuery(id+"F0.wireOp",EDGE,"E7.37.5"),sQuery(id+"F0.wireOp",EDGE,"E7.38.0"),sQuery(id+"F0.wireOp",EDGE,"E7.38.1"),sQuery(id+"F0.wireOp",EDGE,"E7.38.2"),sQuery(id+"F0.wireOp",EDGE,"E7.38.3"),sQuery(id+"F0.wireOp",EDGE,"E7.38.4"),sQuery(id+"F0.wireOp",EDGE,"E7.38.5"),sQuery(id+"F0.wireOp",EDGE,"E7.39.0"),sQuery(id+"F0.wireOp",EDGE,"E7.39.1"),sQuery(id+"F0.wireOp",EDGE,"E7.39.2"),sQuery(id+"F0.wireOp",EDGE,"E7.39.3"),sQuery(id+"F0.wireOp",EDGE,"E7.39.4"),sQuery(id+"F0.wireOp",EDGE,"E7.39.5"),sQuery(id+"F0.wireOp",EDGE,"E7.40.0"),sQuery(id+"F0.wireOp",EDGE,"E7.40.1"),sQuery(id+"F0.wireOp",EDGE,"E7.40.2"),sQuery(id+"F0.wireOp",EDGE,"E7.40.3"),sQuery(id+"F0.wireOp",EDGE,"E7.40.4"),sQuery(id+"F0.wireOp",EDGE,"E7.40.5"),sQuery(id+"F0.wireOp",EDGE,"E7.41.0"),sQuery(id+"F0.wireOp",EDGE,"E7.41.1"),sQuery(id+"F0.wireOp",EDGE,"E7.41.2"),sQuery(id+"F0.wireOp",EDGE,"E7.41.3"),sQuery(id+"F0.wireOp",EDGE,"E7.41.4"),sQuery(id+"F0.wireOp",EDGE,"E7.41.5"),sQuery(id+"F0.wireOp",EDGE,"E7.42.0"),sQuery(id+"F0.wireOp",EDGE,"E7.42.1"),sQuery(id+"F0.wireOp",EDGE,"E7.42.2"),sQuery(id+"F0.wireOp",EDGE,"E7.42.3"),sQuery(id+"F0.wireOp",EDGE,"E7.42.4"),sQuery(id+"F0.wireOp",EDGE,"E7.42.5"),sQuery(id+"F0.wireOp",EDGE,"E7.43.0"),sQuery(id+"F0.wireOp",EDGE,"E7.43.1"),sQuery(id+"F0.wireOp",EDGE,"E7.43.2"),sQuery(id+"F0.wireOp",EDGE,"E7.43.3"),sQuery(id+"F0.wireOp",EDGE,"E7.43.4"),sQuery(id+"F0.wireOp",EDGE,"E7.43.5")])],"isStart":false})]}),makeQuery(id+"F2.opChamfer","BLEND_FACE",FACE,{"disambiguationData":[OSD([subQ0])]})],"blendedInto":[makeQuery(id+"F2.opChamfer","BLEND_FACE",FACE,{"disambiguationData":[OSD([subQ0])]})]});}
            var Q19;
            {var subQ0=sQuery(id+"F0.wireOp",EDGE,"E7.7.0");Q19=makeQuery(id+"F8.opChamfer","BLEND_EDGE",EDGE,{"blendedFrom":[makeQuery(id+"F2.opChamfer","BLEND_EDGE",EDGE,{"blendedFrom":[makeQuery(id+"F1.opExtrude","CAP_EDGE",EDGE,{"disambiguationData":[OSD([subQ0])],"isStart":false}),makeQuery(id+"F1.opExtrude","CAP_FACE",FACE,{"disambiguationData":[OSD([sQuery(id+"F0.wireOp",EDGE,"E1"),sQuery(id+"F0.wireOp",EDGE,"E2"),sQuery(id+"F0.wireOp",EDGE,"E3"),sQuery(id+"F0.wireOp",EDGE,"E4"),sQuery(id+"F0.wireOp",EDGE,"E5"),sQuery(id+"F0.wireOp",EDGE,"E6"),sQuery(id+"F0.wireOp",EDGE,"E7.1.0"),sQuery(id+"F0.wireOp",EDGE,"E7.1.1"),sQuery(id+"F0.wireOp",EDGE,"E7.1.2"),sQuery(id+"F0.wireOp",EDGE,"E7.1.3"),sQuery(id+"F0.wireOp",EDGE,"E7.1.4"),sQuery(id+"F0.wireOp",EDGE,"E7.1.5"),sQuery(id+"F0.wireOp",EDGE,"E7.2.0"),sQuery(id+"F0.wireOp",EDGE,"E7.2.1"),sQuery(id+"F0.wireOp",EDGE,"E7.2.2"),sQuery(id+"F0.wireOp",EDGE,"E7.2.3"),sQuery(id+"F0.wireOp",EDGE,"E7.2.4"),sQuery(id+"F0.wireOp",EDGE,"E7.2.5"),sQuery(id+"F0.wireOp",EDGE,"E7.3.0"),sQuery(id+"F0.wireOp",EDGE,"E7.3.1"),sQuery(id+"F0.wireOp",EDGE,"E7.3.2"),sQuery(id+"F0.wireOp",EDGE,"E7.3.3"),sQuery(id+"F0.wireOp",EDGE,"E7.3.4"),sQuery(id+"F0.wireOp",EDGE,"E7.3.5"),sQuery(id+"F0.wireOp",EDGE,"E7.4.0"),sQuery(id+"F0.wireOp",EDGE,"E7.4.1"),sQuery(id+"F0.wireOp",EDGE,"E7.4.2"),sQuery(id+"F0.wireOp",EDGE,"E7.4.3"),sQuery(id+"F0.wireOp",EDGE,"E7.4.4"),sQuery(id+"F0.wireOp",EDGE,"E7.4.5"),sQuery(id+"F0.wireOp",EDGE,"E7.5.0"),sQuery(id+"F0.wireOp",EDGE,"E7.5.1"),sQuery(id+"F0.wireOp",EDGE,"E7.5.2"),sQuery(id+"F0.wireOp",EDGE,"E7.5.3"),sQuery(id+"F0.wireOp",EDGE,"E7.5.4"),sQuery(id+"F0.wireOp",EDGE,"E7.5.5"),sQuery(id+"F0.wireOp",EDGE,"E7.6.0"),sQuery(id+"F0.wireOp",EDGE,"E7.6.1"),sQuery(id+"F0.wireOp",EDGE,"E7.6.2"),sQuery(id+"F0.wireOp",EDGE,"E7.6.3"),sQuery(id+"F0.wireOp",EDGE,"E7.6.4"),sQuery(id+"F0.wireOp",EDGE,"E7.6.5"),subQ0,sQuery(id+"F0.wireOp",EDGE,"E7.7.1"),sQuery(id+"F0.wireOp",EDGE,"E7.7.2"),sQuery(id+"F0.wireOp",EDGE,"E7.7.3"),sQuery(id+"F0.wireOp",EDGE,"E7.7.4"),sQuery(id+"F0.wireOp",EDGE,"E7.7.5"),sQuery(id+"F0.wireOp",EDGE,"E7.8.0"),sQuery(id+"F0.wireOp",EDGE,"E7.8.1"),sQuery(id+"F0.wireOp",EDGE,"E7.8.2"),sQuery(id+"F0.wireOp",EDGE,"E7.8.3"),sQuery(id+"F0.wireOp",EDGE,"E7.8.4"),sQuery(id+"F0.wireOp",EDGE,"E7.8.5"),sQuery(id+"F0.wireOp",EDGE,"E7.9.0"),sQuery(id+"F0.wireOp",EDGE,"E7.9.1"),sQuery(id+"F0.wireOp",EDGE,"E7.9.2"),sQuery(id+"F0.wireOp",EDGE,"E7.9.3"),sQuery(id+"F0.wireOp",EDGE,"E7.9.4"),sQuery(id+"F0.wireOp",EDGE,"E7.9.5"),sQuery(id+"F0.wireOp",EDGE,"E7.10.0"),sQuery(id+"F0.wireOp",EDGE,"E7.10.1"),sQuery(id+"F0.wireOp",EDGE,"E7.10.2"),sQuery(id+"F0.wireOp",EDGE,"E7.10.3"),sQuery(id+"F0.wireOp",EDGE,"E7.10.4"),sQuery(id+"F0.wireOp",EDGE,"E7.10.5"),sQuery(id+"F0.wireOp",EDGE,"E7.11.0"),sQuery(id+"F0.wireOp",EDGE,"E7.11.1"),sQuery(id+"F0.wireOp",EDGE,"E7.11.2"),sQuery(id+"F0.wireOp",EDGE,"E7.11.3"),sQuery(id+"F0.wireOp",EDGE,"E7.11.4"),sQuery(id+"F0.wireOp",EDGE,"E7.11.5"),sQuery(id+"F0.wireOp",EDGE,"E7.12.0"),sQuery(id+"F0.wireOp",EDGE,"E7.12.1"),sQuery(id+"F0.wireOp",EDGE,"E7.12.2"),sQuery(id+"F0.wireOp",EDGE,"E7.12.3"),sQuery(id+"F0.wireOp",EDGE,"E7.12.4"),sQuery(id+"F0.wireOp",EDGE,"E7.12.5"),sQuery(id+"F0.wireOp",EDGE,"E7.13.0"),sQuery(id+"F0.wireOp",EDGE,"E7.13.1"),sQuery(id+"F0.wireOp",EDGE,"E7.13.2"),sQuery(id+"F0.wireOp",EDGE,"E7.13.3"),sQuery(id+"F0.wireOp",EDGE,"E7.13.4"),sQuery(id+"F0.wireOp",EDGE,"E7.13.5"),sQuery(id+"F0.wireOp",EDGE,"E7.14.0"),sQuery(id+"F0.wireOp",EDGE,"E7.14.1"),sQuery(id+"F0.wireOp",EDGE,"E7.14.2"),sQuery(id+"F0.wireOp",EDGE,"E7.14.3"),sQuery(id+"F0.wireOp",EDGE,"E7.14.4"),sQuery(id+"F0.wireOp",EDGE,"E7.14.5"),sQuery(id+"F0.wireOp",EDGE,"E7.15.0"),sQuery(id+"F0.wireOp",EDGE,"E7.15.1"),sQuery(id+"F0.wireOp",EDGE,"E7.15.2"),sQuery(id+"F0.wireOp",EDGE,"E7.15.3"),sQuery(id+"F0.wireOp",EDGE,"E7.15.4"),sQuery(id+"F0.wireOp",EDGE,"E7.15.5"),sQuery(id+"F0.wireOp",EDGE,"E7.16.0"),sQuery(id+"F0.wireOp",EDGE,"E7.16.1"),sQuery(id+"F0.wireOp",EDGE,"E7.16.2"),sQuery(id+"F0.wireOp",EDGE,"E7.16.3"),sQuery(id+"F0.wireOp",EDGE,"E7.16.4"),sQuery(id+"F0.wireOp",EDGE,"E7.16.5"),sQuery(id+"F0.wireOp",EDGE,"E7.17.0"),sQuery(id+"F0.wireOp",EDGE,"E7.17.1"),sQuery(id+"F0.wireOp",EDGE,"E7.17.2"),sQuery(id+"F0.wireOp",EDGE,"E7.17.3"),sQuery(id+"F0.wireOp",EDGE,"E7.17.4"),sQuery(id+"F0.wireOp",EDGE,"E7.17.5"),sQuery(id+"F0.wireOp",EDGE,"E7.18.0"),sQuery(id+"F0.wireOp",EDGE,"E7.18.1"),sQuery(id+"F0.wireOp",EDGE,"E7.18.2"),sQuery(id+"F0.wireOp",EDGE,"E7.18.3"),sQuery(id+"F0.wireOp",EDGE,"E7.18.4"),sQuery(id+"F0.wireOp",EDGE,"E7.18.5"),sQuery(id+"F0.wireOp",EDGE,"E7.19.0"),sQuery(id+"F0.wireOp",EDGE,"E7.19.1"),sQuery(id+"F0.wireOp",EDGE,"E7.19.2"),sQuery(id+"F0.wireOp",EDGE,"E7.19.3"),sQuery(id+"F0.wireOp",EDGE,"E7.19.4"),sQuery(id+"F0.wireOp",EDGE,"E7.19.5"),sQuery(id+"F0.wireOp",EDGE,"E7.20.0"),sQuery(id+"F0.wireOp",EDGE,"E7.20.1"),sQuery(id+"F0.wireOp",EDGE,"E7.20.2"),sQuery(id+"F0.wireOp",EDGE,"E7.20.3"),sQuery(id+"F0.wireOp",EDGE,"E7.20.4"),sQuery(id+"F0.wireOp",EDGE,"E7.20.5"),sQuery(id+"F0.wireOp",EDGE,"E7.21.0"),sQuery(id+"F0.wireOp",EDGE,"E7.21.1"),sQuery(id+"F0.wireOp",EDGE,"E7.21.2"),sQuery(id+"F0.wireOp",EDGE,"E7.21.3"),sQuery(id+"F0.wireOp",EDGE,"E7.21.4"),sQuery(id+"F0.wireOp",EDGE,"E7.21.5"),sQuery(id+"F0.wireOp",EDGE,"E7.22.0"),sQuery(id+"F0.wireOp",EDGE,"E7.22.1"),sQuery(id+"F0.wireOp",EDGE,"E7.22.2"),sQuery(id+"F0.wireOp",EDGE,"E7.22.3"),sQuery(id+"F0.wireOp",EDGE,"E7.22.4"),sQuery(id+"F0.wireOp",EDGE,"E7.22.5"),sQuery(id+"F0.wireOp",EDGE,"E7.23.0"),sQuery(id+"F0.wireOp",EDGE,"E7.23.1"),sQuery(id+"F0.wireOp",EDGE,"E7.23.2"),sQuery(id+"F0.wireOp",EDGE,"E7.23.3"),sQuery(id+"F0.wireOp",EDGE,"E7.23.4"),sQuery(id+"F0.wireOp",EDGE,"E7.23.5"),sQuery(id+"F0.wireOp",EDGE,"E7.24.0"),sQuery(id+"F0.wireOp",EDGE,"E7.24.1"),sQuery(id+"F0.wireOp",EDGE,"E7.24.2"),sQuery(id+"F0.wireOp",EDGE,"E7.24.3"),sQuery(id+"F0.wireOp",EDGE,"E7.24.4"),sQuery(id+"F0.wireOp",EDGE,"E7.24.5"),sQuery(id+"F0.wireOp",EDGE,"E7.25.0"),sQuery(id+"F0.wireOp",EDGE,"E7.25.1"),sQuery(id+"F0.wireOp",EDGE,"E7.25.2"),sQuery(id+"F0.wireOp",EDGE,"E7.25.3"),sQuery(id+"F0.wireOp",EDGE,"E7.25.4"),sQuery(id+"F0.wireOp",EDGE,"E7.25.5"),sQuery(id+"F0.wireOp",EDGE,"E7.26.0"),sQuery(id+"F0.wireOp",EDGE,"E7.26.1"),sQuery(id+"F0.wireOp",EDGE,"E7.26.2"),sQuery(id+"F0.wireOp",EDGE,"E7.26.3"),sQuery(id+"F0.wireOp",EDGE,"E7.26.4"),sQuery(id+"F0.wireOp",EDGE,"E7.26.5"),sQuery(id+"F0.wireOp",EDGE,"E7.27.0"),sQuery(id+"F0.wireOp",EDGE,"E7.27.1"),sQuery(id+"F0.wireOp",EDGE,"E7.27.2"),sQuery(id+"F0.wireOp",EDGE,"E7.27.3"),sQuery(id+"F0.wireOp",EDGE,"E7.27.4"),sQuery(id+"F0.wireOp",EDGE,"E7.27.5"),sQuery(id+"F0.wireOp",EDGE,"E7.28.0"),sQuery(id+"F0.wireOp",EDGE,"E7.28.1"),sQuery(id+"F0.wireOp",EDGE,"E7.28.2"),sQuery(id+"F0.wireOp",EDGE,"E7.28.3"),sQuery(id+"F0.wireOp",EDGE,"E7.28.4"),sQuery(id+"F0.wireOp",EDGE,"E7.28.5"),sQuery(id+"F0.wireOp",EDGE,"E7.29.0"),sQuery(id+"F0.wireOp",EDGE,"E7.29.1"),sQuery(id+"F0.wireOp",EDGE,"E7.29.2"),sQuery(id+"F0.wireOp",EDGE,"E7.29.3"),sQuery(id+"F0.wireOp",EDGE,"E7.29.4"),sQuery(id+"F0.wireOp",EDGE,"E7.29.5"),sQuery(id+"F0.wireOp",EDGE,"E7.30.0"),sQuery(id+"F0.wireOp",EDGE,"E7.30.1"),sQuery(id+"F0.wireOp",EDGE,"E7.30.2"),sQuery(id+"F0.wireOp",EDGE,"E7.30.3"),sQuery(id+"F0.wireOp",EDGE,"E7.30.4"),sQuery(id+"F0.wireOp",EDGE,"E7.30.5"),sQuery(id+"F0.wireOp",EDGE,"E7.31.0"),sQuery(id+"F0.wireOp",EDGE,"E7.31.1"),sQuery(id+"F0.wireOp",EDGE,"E7.31.2"),sQuery(id+"F0.wireOp",EDGE,"E7.31.3"),sQuery(id+"F0.wireOp",EDGE,"E7.31.4"),sQuery(id+"F0.wireOp",EDGE,"E7.31.5"),sQuery(id+"F0.wireOp",EDGE,"E7.32.0"),sQuery(id+"F0.wireOp",EDGE,"E7.32.1"),sQuery(id+"F0.wireOp",EDGE,"E7.32.2"),sQuery(id+"F0.wireOp",EDGE,"E7.32.3"),sQuery(id+"F0.wireOp",EDGE,"E7.32.4"),sQuery(id+"F0.wireOp",EDGE,"E7.32.5"),sQuery(id+"F0.wireOp",EDGE,"E7.33.0"),sQuery(id+"F0.wireOp",EDGE,"E7.33.1"),sQuery(id+"F0.wireOp",EDGE,"E7.33.2"),sQuery(id+"F0.wireOp",EDGE,"E7.33.3"),sQuery(id+"F0.wireOp",EDGE,"E7.33.4"),sQuery(id+"F0.wireOp",EDGE,"E7.33.5"),sQuery(id+"F0.wireOp",EDGE,"E7.34.0"),sQuery(id+"F0.wireOp",EDGE,"E7.34.1"),sQuery(id+"F0.wireOp",EDGE,"E7.34.2"),sQuery(id+"F0.wireOp",EDGE,"E7.34.3"),sQuery(id+"F0.wireOp",EDGE,"E7.34.4"),sQuery(id+"F0.wireOp",EDGE,"E7.34.5"),sQuery(id+"F0.wireOp",EDGE,"E7.35.0"),sQuery(id+"F0.wireOp",EDGE,"E7.35.1"),sQuery(id+"F0.wireOp",EDGE,"E7.35.2"),sQuery(id+"F0.wireOp",EDGE,"E7.35.3"),sQuery(id+"F0.wireOp",EDGE,"E7.35.4"),sQuery(id+"F0.wireOp",EDGE,"E7.35.5"),sQuery(id+"F0.wireOp",EDGE,"E7.36.0"),sQuery(id+"F0.wireOp",EDGE,"E7.36.1"),sQuery(id+"F0.wireOp",EDGE,"E7.36.2"),sQuery(id+"F0.wireOp",EDGE,"E7.36.3"),sQuery(id+"F0.wireOp",EDGE,"E7.36.4"),sQuery(id+"F0.wireOp",EDGE,"E7.36.5"),sQuery(id+"F0.wireOp",EDGE,"E7.37.0"),sQuery(id+"F0.wireOp",EDGE,"E7.37.1"),sQuery(id+"F0.wireOp",EDGE,"E7.37.2"),sQuery(id+"F0.wireOp",EDGE,"E7.37.3"),sQuery(id+"F0.wireOp",EDGE,"E7.37.4"),sQuery(id+"F0.wireOp",EDGE,"E7.37.5"),sQuery(id+"F0.wireOp",EDGE,"E7.38.0"),sQuery(id+"F0.wireOp",EDGE,"E7.38.1"),sQuery(id+"F0.wireOp",EDGE,"E7.38.2"),sQuery(id+"F0.wireOp",EDGE,"E7.38.3"),sQuery(id+"F0.wireOp",EDGE,"E7.38.4"),sQuery(id+"F0.wireOp",EDGE,"E7.38.5"),sQuery(id+"F0.wireOp",EDGE,"E7.39.0"),sQuery(id+"F0.wireOp",EDGE,"E7.39.1"),sQuery(id+"F0.wireOp",EDGE,"E7.39.2"),sQuery(id+"F0.wireOp",EDGE,"E7.39.3"),sQuery(id+"F0.wireOp",EDGE,"E7.39.4"),sQuery(id+"F0.wireOp",EDGE,"E7.39.5"),sQuery(id+"F0.wireOp",EDGE,"E7.40.0"),sQuery(id+"F0.wireOp",EDGE,"E7.40.1"),sQuery(id+"F0.wireOp",EDGE,"E7.40.2"),sQuery(id+"F0.wireOp",EDGE,"E7.40.3"),sQuery(id+"F0.wireOp",EDGE,"E7.40.4"),sQuery(id+"F0.wireOp",EDGE,"E7.40.5"),sQuery(id+"F0.wireOp",EDGE,"E7.41.0"),sQuery(id+"F0.wireOp",EDGE,"E7.41.1"),sQuery(id+"F0.wireOp",EDGE,"E7.41.2"),sQuery(id+"F0.wireOp",EDGE,"E7.41.3"),sQuery(id+"F0.wireOp",EDGE,"E7.41.4"),sQuery(id+"F0.wireOp",EDGE,"E7.41.5"),sQuery(id+"F0.wireOp",EDGE,"E7.42.0"),sQuery(id+"F0.wireOp",EDGE,"E7.42.1"),sQuery(id+"F0.wireOp",EDGE,"E7.42.2"),sQuery(id+"F0.wireOp",EDGE,"E7.42.3"),sQuery(id+"F0.wireOp",EDGE,"E7.42.4"),sQuery(id+"F0.wireOp",EDGE,"E7.42.5"),sQuery(id+"F0.wireOp",EDGE,"E7.43.0"),sQuery(id+"F0.wireOp",EDGE,"E7.43.1"),sQuery(id+"F0.wireOp",EDGE,"E7.43.2"),sQuery(id+"F0.wireOp",EDGE,"E7.43.3"),sQuery(id+"F0.wireOp",EDGE,"E7.43.4"),sQuery(id+"F0.wireOp",EDGE,"E7.43.5")])],"isStart":false})],"blendedInto":[makeQuery(id+"F1.opExtrude","CAP_FACE",FACE,{"disambiguationData":[OSD([sQuery(id+"F0.wireOp",EDGE,"E1"),sQuery(id+"F0.wireOp",EDGE,"E2"),sQuery(id+"F0.wireOp",EDGE,"E3"),sQuery(id+"F0.wireOp",EDGE,"E4"),sQuery(id+"F0.wireOp",EDGE,"E5"),sQuery(id+"F0.wireOp",EDGE,"E6"),sQuery(id+"F0.wireOp",EDGE,"E7.1.0"),sQuery(id+"F0.wireOp",EDGE,"E7.1.1"),sQuery(id+"F0.wireOp",EDGE,"E7.1.2"),sQuery(id+"F0.wireOp",EDGE,"E7.1.3"),sQuery(id+"F0.wireOp",EDGE,"E7.1.4"),sQuery(id+"F0.wireOp",EDGE,"E7.1.5"),sQuery(id+"F0.wireOp",EDGE,"E7.2.0"),sQuery(id+"F0.wireOp",EDGE,"E7.2.1"),sQuery(id+"F0.wireOp",EDGE,"E7.2.2"),sQuery(id+"F0.wireOp",EDGE,"E7.2.3"),sQuery(id+"F0.wireOp",EDGE,"E7.2.4"),sQuery(id+"F0.wireOp",EDGE,"E7.2.5"),sQuery(id+"F0.wireOp",EDGE,"E7.3.0"),sQuery(id+"F0.wireOp",EDGE,"E7.3.1"),sQuery(id+"F0.wireOp",EDGE,"E7.3.2"),sQuery(id+"F0.wireOp",EDGE,"E7.3.3"),sQuery(id+"F0.wireOp",EDGE,"E7.3.4"),sQuery(id+"F0.wireOp",EDGE,"E7.3.5"),sQuery(id+"F0.wireOp",EDGE,"E7.4.0"),sQuery(id+"F0.wireOp",EDGE,"E7.4.1"),sQuery(id+"F0.wireOp",EDGE,"E7.4.2"),sQuery(id+"F0.wireOp",EDGE,"E7.4.3"),sQuery(id+"F0.wireOp",EDGE,"E7.4.4"),sQuery(id+"F0.wireOp",EDGE,"E7.4.5"),sQuery(id+"F0.wireOp",EDGE,"E7.5.0"),sQuery(id+"F0.wireOp",EDGE,"E7.5.1"),sQuery(id+"F0.wireOp",EDGE,"E7.5.2"),sQuery(id+"F0.wireOp",EDGE,"E7.5.3"),sQuery(id+"F0.wireOp",EDGE,"E7.5.4"),sQuery(id+"F0.wireOp",EDGE,"E7.5.5"),sQuery(id+"F0.wireOp",EDGE,"E7.6.0"),sQuery(id+"F0.wireOp",EDGE,"E7.6.1"),sQuery(id+"F0.wireOp",EDGE,"E7.6.2"),sQuery(id+"F0.wireOp",EDGE,"E7.6.3"),sQuery(id+"F0.wireOp",EDGE,"E7.6.4"),sQuery(id+"F0.wireOp",EDGE,"E7.6.5"),subQ0,sQuery(id+"F0.wireOp",EDGE,"E7.7.1"),sQuery(id+"F0.wireOp",EDGE,"E7.7.2"),sQuery(id+"F0.wireOp",EDGE,"E7.7.3"),sQuery(id+"F0.wireOp",EDGE,"E7.7.4"),sQuery(id+"F0.wireOp",EDGE,"E7.7.5"),sQuery(id+"F0.wireOp",EDGE,"E7.8.0"),sQuery(id+"F0.wireOp",EDGE,"E7.8.1"),sQuery(id+"F0.wireOp",EDGE,"E7.8.2"),sQuery(id+"F0.wireOp",EDGE,"E7.8.3"),sQuery(id+"F0.wireOp",EDGE,"E7.8.4"),sQuery(id+"F0.wireOp",EDGE,"E7.8.5"),sQuery(id+"F0.wireOp",EDGE,"E7.9.0"),sQuery(id+"F0.wireOp",EDGE,"E7.9.1"),sQuery(id+"F0.wireOp",EDGE,"E7.9.2"),sQuery(id+"F0.wireOp",EDGE,"E7.9.3"),sQuery(id+"F0.wireOp",EDGE,"E7.9.4"),sQuery(id+"F0.wireOp",EDGE,"E7.9.5"),sQuery(id+"F0.wireOp",EDGE,"E7.10.0"),sQuery(id+"F0.wireOp",EDGE,"E7.10.1"),sQuery(id+"F0.wireOp",EDGE,"E7.10.2"),sQuery(id+"F0.wireOp",EDGE,"E7.10.3"),sQuery(id+"F0.wireOp",EDGE,"E7.10.4"),sQuery(id+"F0.wireOp",EDGE,"E7.10.5"),sQuery(id+"F0.wireOp",EDGE,"E7.11.0"),sQuery(id+"F0.wireOp",EDGE,"E7.11.1"),sQuery(id+"F0.wireOp",EDGE,"E7.11.2"),sQuery(id+"F0.wireOp",EDGE,"E7.11.3"),sQuery(id+"F0.wireOp",EDGE,"E7.11.4"),sQuery(id+"F0.wireOp",EDGE,"E7.11.5"),sQuery(id+"F0.wireOp",EDGE,"E7.12.0"),sQuery(id+"F0.wireOp",EDGE,"E7.12.1"),sQuery(id+"F0.wireOp",EDGE,"E7.12.2"),sQuery(id+"F0.wireOp",EDGE,"E7.12.3"),sQuery(id+"F0.wireOp",EDGE,"E7.12.4"),sQuery(id+"F0.wireOp",EDGE,"E7.12.5"),sQuery(id+"F0.wireOp",EDGE,"E7.13.0"),sQuery(id+"F0.wireOp",EDGE,"E7.13.1"),sQuery(id+"F0.wireOp",EDGE,"E7.13.2"),sQuery(id+"F0.wireOp",EDGE,"E7.13.3"),sQuery(id+"F0.wireOp",EDGE,"E7.13.4"),sQuery(id+"F0.wireOp",EDGE,"E7.13.5"),sQuery(id+"F0.wireOp",EDGE,"E7.14.0"),sQuery(id+"F0.wireOp",EDGE,"E7.14.1"),sQuery(id+"F0.wireOp",EDGE,"E7.14.2"),sQuery(id+"F0.wireOp",EDGE,"E7.14.3"),sQuery(id+"F0.wireOp",EDGE,"E7.14.4"),sQuery(id+"F0.wireOp",EDGE,"E7.14.5"),sQuery(id+"F0.wireOp",EDGE,"E7.15.0"),sQuery(id+"F0.wireOp",EDGE,"E7.15.1"),sQuery(id+"F0.wireOp",EDGE,"E7.15.2"),sQuery(id+"F0.wireOp",EDGE,"E7.15.3"),sQuery(id+"F0.wireOp",EDGE,"E7.15.4"),sQuery(id+"F0.wireOp",EDGE,"E7.15.5"),sQuery(id+"F0.wireOp",EDGE,"E7.16.0"),sQuery(id+"F0.wireOp",EDGE,"E7.16.1"),sQuery(id+"F0.wireOp",EDGE,"E7.16.2"),sQuery(id+"F0.wireOp",EDGE,"E7.16.3"),sQuery(id+"F0.wireOp",EDGE,"E7.16.4"),sQuery(id+"F0.wireOp",EDGE,"E7.16.5"),sQuery(id+"F0.wireOp",EDGE,"E7.17.0"),sQuery(id+"F0.wireOp",EDGE,"E7.17.1"),sQuery(id+"F0.wireOp",EDGE,"E7.17.2"),sQuery(id+"F0.wireOp",EDGE,"E7.17.3"),sQuery(id+"F0.wireOp",EDGE,"E7.17.4"),sQuery(id+"F0.wireOp",EDGE,"E7.17.5"),sQuery(id+"F0.wireOp",EDGE,"E7.18.0"),sQuery(id+"F0.wireOp",EDGE,"E7.18.1"),sQuery(id+"F0.wireOp",EDGE,"E7.18.2"),sQuery(id+"F0.wireOp",EDGE,"E7.18.3"),sQuery(id+"F0.wireOp",EDGE,"E7.18.4"),sQuery(id+"F0.wireOp",EDGE,"E7.18.5"),sQuery(id+"F0.wireOp",EDGE,"E7.19.0"),sQuery(id+"F0.wireOp",EDGE,"E7.19.1"),sQuery(id+"F0.wireOp",EDGE,"E7.19.2"),sQuery(id+"F0.wireOp",EDGE,"E7.19.3"),sQuery(id+"F0.wireOp",EDGE,"E7.19.4"),sQuery(id+"F0.wireOp",EDGE,"E7.19.5"),sQuery(id+"F0.wireOp",EDGE,"E7.20.0"),sQuery(id+"F0.wireOp",EDGE,"E7.20.1"),sQuery(id+"F0.wireOp",EDGE,"E7.20.2"),sQuery(id+"F0.wireOp",EDGE,"E7.20.3"),sQuery(id+"F0.wireOp",EDGE,"E7.20.4"),sQuery(id+"F0.wireOp",EDGE,"E7.20.5"),sQuery(id+"F0.wireOp",EDGE,"E7.21.0"),sQuery(id+"F0.wireOp",EDGE,"E7.21.1"),sQuery(id+"F0.wireOp",EDGE,"E7.21.2"),sQuery(id+"F0.wireOp",EDGE,"E7.21.3"),sQuery(id+"F0.wireOp",EDGE,"E7.21.4"),sQuery(id+"F0.wireOp",EDGE,"E7.21.5"),sQuery(id+"F0.wireOp",EDGE,"E7.22.0"),sQuery(id+"F0.wireOp",EDGE,"E7.22.1"),sQuery(id+"F0.wireOp",EDGE,"E7.22.2"),sQuery(id+"F0.wireOp",EDGE,"E7.22.3"),sQuery(id+"F0.wireOp",EDGE,"E7.22.4"),sQuery(id+"F0.wireOp",EDGE,"E7.22.5"),sQuery(id+"F0.wireOp",EDGE,"E7.23.0"),sQuery(id+"F0.wireOp",EDGE,"E7.23.1"),sQuery(id+"F0.wireOp",EDGE,"E7.23.2"),sQuery(id+"F0.wireOp",EDGE,"E7.23.3"),sQuery(id+"F0.wireOp",EDGE,"E7.23.4"),sQuery(id+"F0.wireOp",EDGE,"E7.23.5"),sQuery(id+"F0.wireOp",EDGE,"E7.24.0"),sQuery(id+"F0.wireOp",EDGE,"E7.24.1"),sQuery(id+"F0.wireOp",EDGE,"E7.24.2"),sQuery(id+"F0.wireOp",EDGE,"E7.24.3"),sQuery(id+"F0.wireOp",EDGE,"E7.24.4"),sQuery(id+"F0.wireOp",EDGE,"E7.24.5"),sQuery(id+"F0.wireOp",EDGE,"E7.25.0"),sQuery(id+"F0.wireOp",EDGE,"E7.25.1"),sQuery(id+"F0.wireOp",EDGE,"E7.25.2"),sQuery(id+"F0.wireOp",EDGE,"E7.25.3"),sQuery(id+"F0.wireOp",EDGE,"E7.25.4"),sQuery(id+"F0.wireOp",EDGE,"E7.25.5"),sQuery(id+"F0.wireOp",EDGE,"E7.26.0"),sQuery(id+"F0.wireOp",EDGE,"E7.26.1"),sQuery(id+"F0.wireOp",EDGE,"E7.26.2"),sQuery(id+"F0.wireOp",EDGE,"E7.26.3"),sQuery(id+"F0.wireOp",EDGE,"E7.26.4"),sQuery(id+"F0.wireOp",EDGE,"E7.26.5"),sQuery(id+"F0.wireOp",EDGE,"E7.27.0"),sQuery(id+"F0.wireOp",EDGE,"E7.27.1"),sQuery(id+"F0.wireOp",EDGE,"E7.27.2"),sQuery(id+"F0.wireOp",EDGE,"E7.27.3"),sQuery(id+"F0.wireOp",EDGE,"E7.27.4"),sQuery(id+"F0.wireOp",EDGE,"E7.27.5"),sQuery(id+"F0.wireOp",EDGE,"E7.28.0"),sQuery(id+"F0.wireOp",EDGE,"E7.28.1"),sQuery(id+"F0.wireOp",EDGE,"E7.28.2"),sQuery(id+"F0.wireOp",EDGE,"E7.28.3"),sQuery(id+"F0.wireOp",EDGE,"E7.28.4"),sQuery(id+"F0.wireOp",EDGE,"E7.28.5"),sQuery(id+"F0.wireOp",EDGE,"E7.29.0"),sQuery(id+"F0.wireOp",EDGE,"E7.29.1"),sQuery(id+"F0.wireOp",EDGE,"E7.29.2"),sQuery(id+"F0.wireOp",EDGE,"E7.29.3"),sQuery(id+"F0.wireOp",EDGE,"E7.29.4"),sQuery(id+"F0.wireOp",EDGE,"E7.29.5"),sQuery(id+"F0.wireOp",EDGE,"E7.30.0"),sQuery(id+"F0.wireOp",EDGE,"E7.30.1"),sQuery(id+"F0.wireOp",EDGE,"E7.30.2"),sQuery(id+"F0.wireOp",EDGE,"E7.30.3"),sQuery(id+"F0.wireOp",EDGE,"E7.30.4"),sQuery(id+"F0.wireOp",EDGE,"E7.30.5"),sQuery(id+"F0.wireOp",EDGE,"E7.31.0"),sQuery(id+"F0.wireOp",EDGE,"E7.31.1"),sQuery(id+"F0.wireOp",EDGE,"E7.31.2"),sQuery(id+"F0.wireOp",EDGE,"E7.31.3"),sQuery(id+"F0.wireOp",EDGE,"E7.31.4"),sQuery(id+"F0.wireOp",EDGE,"E7.31.5"),sQuery(id+"F0.wireOp",EDGE,"E7.32.0"),sQuery(id+"F0.wireOp",EDGE,"E7.32.1"),sQuery(id+"F0.wireOp",EDGE,"E7.32.2"),sQuery(id+"F0.wireOp",EDGE,"E7.32.3"),sQuery(id+"F0.wireOp",EDGE,"E7.32.4"),sQuery(id+"F0.wireOp",EDGE,"E7.32.5"),sQuery(id+"F0.wireOp",EDGE,"E7.33.0"),sQuery(id+"F0.wireOp",EDGE,"E7.33.1"),sQuery(id+"F0.wireOp",EDGE,"E7.33.2"),sQuery(id+"F0.wireOp",EDGE,"E7.33.3"),sQuery(id+"F0.wireOp",EDGE,"E7.33.4"),sQuery(id+"F0.wireOp",EDGE,"E7.33.5"),sQuery(id+"F0.wireOp",EDGE,"E7.34.0"),sQuery(id+"F0.wireOp",EDGE,"E7.34.1"),sQuery(id+"F0.wireOp",EDGE,"E7.34.2"),sQuery(id+"F0.wireOp",EDGE,"E7.34.3"),sQuery(id+"F0.wireOp",EDGE,"E7.34.4"),sQuery(id+"F0.wireOp",EDGE,"E7.34.5"),sQuery(id+"F0.wireOp",EDGE,"E7.35.0"),sQuery(id+"F0.wireOp",EDGE,"E7.35.1"),sQuery(id+"F0.wireOp",EDGE,"E7.35.2"),sQuery(id+"F0.wireOp",EDGE,"E7.35.3"),sQuery(id+"F0.wireOp",EDGE,"E7.35.4"),sQuery(id+"F0.wireOp",EDGE,"E7.35.5"),sQuery(id+"F0.wireOp",EDGE,"E7.36.0"),sQuery(id+"F0.wireOp",EDGE,"E7.36.1"),sQuery(id+"F0.wireOp",EDGE,"E7.36.2"),sQuery(id+"F0.wireOp",EDGE,"E7.36.3"),sQuery(id+"F0.wireOp",EDGE,"E7.36.4"),sQuery(id+"F0.wireOp",EDGE,"E7.36.5"),sQuery(id+"F0.wireOp",EDGE,"E7.37.0"),sQuery(id+"F0.wireOp",EDGE,"E7.37.1"),sQuery(id+"F0.wireOp",EDGE,"E7.37.2"),sQuery(id+"F0.wireOp",EDGE,"E7.37.3"),sQuery(id+"F0.wireOp",EDGE,"E7.37.4"),sQuery(id+"F0.wireOp",EDGE,"E7.37.5"),sQuery(id+"F0.wireOp",EDGE,"E7.38.0"),sQuery(id+"F0.wireOp",EDGE,"E7.38.1"),sQuery(id+"F0.wireOp",EDGE,"E7.38.2"),sQuery(id+"F0.wireOp",EDGE,"E7.38.3"),sQuery(id+"F0.wireOp",EDGE,"E7.38.4"),sQuery(id+"F0.wireOp",EDGE,"E7.38.5"),sQuery(id+"F0.wireOp",EDGE,"E7.39.0"),sQuery(id+"F0.wireOp",EDGE,"E7.39.1"),sQuery(id+"F0.wireOp",EDGE,"E7.39.2"),sQuery(id+"F0.wireOp",EDGE,"E7.39.3"),sQuery(id+"F0.wireOp",EDGE,"E7.39.4"),sQuery(id+"F0.wireOp",EDGE,"E7.39.5"),sQuery(id+"F0.wireOp",EDGE,"E7.40.0"),sQuery(id+"F0.wireOp",EDGE,"E7.40.1"),sQuery(id+"F0.wireOp",EDGE,"E7.40.2"),sQuery(id+"F0.wireOp",EDGE,"E7.40.3"),sQuery(id+"F0.wireOp",EDGE,"E7.40.4"),sQuery(id+"F0.wireOp",EDGE,"E7.40.5"),sQuery(id+"F0.wireOp",EDGE,"E7.41.0"),sQuery(id+"F0.wireOp",EDGE,"E7.41.1"),sQuery(id+"F0.wireOp",EDGE,"E7.41.2"),sQuery(id+"F0.wireOp",EDGE,"E7.41.3"),sQuery(id+"F0.wireOp",EDGE,"E7.41.4"),sQuery(id+"F0.wireOp",EDGE,"E7.41.5"),sQuery(id+"F0.wireOp",EDGE,"E7.42.0"),sQuery(id+"F0.wireOp",EDGE,"E7.42.1"),sQuery(id+"F0.wireOp",EDGE,"E7.42.2"),sQuery(id+"F0.wireOp",EDGE,"E7.42.3"),sQuery(id+"F0.wireOp",EDGE,"E7.42.4"),sQuery(id+"F0.wireOp",EDGE,"E7.42.5"),sQuery(id+"F0.wireOp",EDGE,"E7.43.0"),sQuery(id+"F0.wireOp",EDGE,"E7.43.1"),sQuery(id+"F0.wireOp",EDGE,"E7.43.2"),sQuery(id+"F0.wireOp",EDGE,"E7.43.3"),sQuery(id+"F0.wireOp",EDGE,"E7.43.4"),sQuery(id+"F0.wireOp",EDGE,"E7.43.5")])],"isStart":false})]}),makeQuery(id+"F2.opChamfer","BLEND_FACE",FACE,{"disambiguationData":[OSD([subQ0])]})],"blendedInto":[makeQuery(id+"F2.opChamfer","BLEND_FACE",FACE,{"disambiguationData":[OSD([subQ0])]})]});}
            var Q20;
            {var subQ0=sQuery(id+"F0.wireOp",EDGE,"E7.5.0");Q20=makeQuery(id+"F8.opChamfer","BLEND_EDGE",EDGE,{"blendedFrom":[makeQuery(id+"F2.opChamfer","BLEND_EDGE",EDGE,{"blendedFrom":[makeQuery(id+"F1.opExtrude","CAP_EDGE",EDGE,{"disambiguationData":[OSD([subQ0])],"isStart":false}),makeQuery(id+"F1.opExtrude","CAP_FACE",FACE,{"disambiguationData":[OSD([sQuery(id+"F0.wireOp",EDGE,"E1"),sQuery(id+"F0.wireOp",EDGE,"E2"),sQuery(id+"F0.wireOp",EDGE,"E3"),sQuery(id+"F0.wireOp",EDGE,"E4"),sQuery(id+"F0.wireOp",EDGE,"E5"),sQuery(id+"F0.wireOp",EDGE,"E6"),sQuery(id+"F0.wireOp",EDGE,"E7.1.0"),sQuery(id+"F0.wireOp",EDGE,"E7.1.1"),sQuery(id+"F0.wireOp",EDGE,"E7.1.2"),sQuery(id+"F0.wireOp",EDGE,"E7.1.3"),sQuery(id+"F0.wireOp",EDGE,"E7.1.4"),sQuery(id+"F0.wireOp",EDGE,"E7.1.5"),sQuery(id+"F0.wireOp",EDGE,"E7.2.0"),sQuery(id+"F0.wireOp",EDGE,"E7.2.1"),sQuery(id+"F0.wireOp",EDGE,"E7.2.2"),sQuery(id+"F0.wireOp",EDGE,"E7.2.3"),sQuery(id+"F0.wireOp",EDGE,"E7.2.4"),sQuery(id+"F0.wireOp",EDGE,"E7.2.5"),sQuery(id+"F0.wireOp",EDGE,"E7.3.0"),sQuery(id+"F0.wireOp",EDGE,"E7.3.1"),sQuery(id+"F0.wireOp",EDGE,"E7.3.2"),sQuery(id+"F0.wireOp",EDGE,"E7.3.3"),sQuery(id+"F0.wireOp",EDGE,"E7.3.4"),sQuery(id+"F0.wireOp",EDGE,"E7.3.5"),sQuery(id+"F0.wireOp",EDGE,"E7.4.0"),sQuery(id+"F0.wireOp",EDGE,"E7.4.1"),sQuery(id+"F0.wireOp",EDGE,"E7.4.2"),sQuery(id+"F0.wireOp",EDGE,"E7.4.3"),sQuery(id+"F0.wireOp",EDGE,"E7.4.4"),sQuery(id+"F0.wireOp",EDGE,"E7.4.5"),subQ0,sQuery(id+"F0.wireOp",EDGE,"E7.5.1"),sQuery(id+"F0.wireOp",EDGE,"E7.5.2"),sQuery(id+"F0.wireOp",EDGE,"E7.5.3"),sQuery(id+"F0.wireOp",EDGE,"E7.5.4"),sQuery(id+"F0.wireOp",EDGE,"E7.5.5"),sQuery(id+"F0.wireOp",EDGE,"E7.6.0"),sQuery(id+"F0.wireOp",EDGE,"E7.6.1"),sQuery(id+"F0.wireOp",EDGE,"E7.6.2"),sQuery(id+"F0.wireOp",EDGE,"E7.6.3"),sQuery(id+"F0.wireOp",EDGE,"E7.6.4"),sQuery(id+"F0.wireOp",EDGE,"E7.6.5"),sQuery(id+"F0.wireOp",EDGE,"E7.7.0"),sQuery(id+"F0.wireOp",EDGE,"E7.7.1"),sQuery(id+"F0.wireOp",EDGE,"E7.7.2"),sQuery(id+"F0.wireOp",EDGE,"E7.7.3"),sQuery(id+"F0.wireOp",EDGE,"E7.7.4"),sQuery(id+"F0.wireOp",EDGE,"E7.7.5"),sQuery(id+"F0.wireOp",EDGE,"E7.8.0"),sQuery(id+"F0.wireOp",EDGE,"E7.8.1"),sQuery(id+"F0.wireOp",EDGE,"E7.8.2"),sQuery(id+"F0.wireOp",EDGE,"E7.8.3"),sQuery(id+"F0.wireOp",EDGE,"E7.8.4"),sQuery(id+"F0.wireOp",EDGE,"E7.8.5"),sQuery(id+"F0.wireOp",EDGE,"E7.9.0"),sQuery(id+"F0.wireOp",EDGE,"E7.9.1"),sQuery(id+"F0.wireOp",EDGE,"E7.9.2"),sQuery(id+"F0.wireOp",EDGE,"E7.9.3"),sQuery(id+"F0.wireOp",EDGE,"E7.9.4"),sQuery(id+"F0.wireOp",EDGE,"E7.9.5"),sQuery(id+"F0.wireOp",EDGE,"E7.10.0"),sQuery(id+"F0.wireOp",EDGE,"E7.10.1"),sQuery(id+"F0.wireOp",EDGE,"E7.10.2"),sQuery(id+"F0.wireOp",EDGE,"E7.10.3"),sQuery(id+"F0.wireOp",EDGE,"E7.10.4"),sQuery(id+"F0.wireOp",EDGE,"E7.10.5"),sQuery(id+"F0.wireOp",EDGE,"E7.11.0"),sQuery(id+"F0.wireOp",EDGE,"E7.11.1"),sQuery(id+"F0.wireOp",EDGE,"E7.11.2"),sQuery(id+"F0.wireOp",EDGE,"E7.11.3"),sQuery(id+"F0.wireOp",EDGE,"E7.11.4"),sQuery(id+"F0.wireOp",EDGE,"E7.11.5"),sQuery(id+"F0.wireOp",EDGE,"E7.12.0"),sQuery(id+"F0.wireOp",EDGE,"E7.12.1"),sQuery(id+"F0.wireOp",EDGE,"E7.12.2"),sQuery(id+"F0.wireOp",EDGE,"E7.12.3"),sQuery(id+"F0.wireOp",EDGE,"E7.12.4"),sQuery(id+"F0.wireOp",EDGE,"E7.12.5"),sQuery(id+"F0.wireOp",EDGE,"E7.13.0"),sQuery(id+"F0.wireOp",EDGE,"E7.13.1"),sQuery(id+"F0.wireOp",EDGE,"E7.13.2"),sQuery(id+"F0.wireOp",EDGE,"E7.13.3"),sQuery(id+"F0.wireOp",EDGE,"E7.13.4"),sQuery(id+"F0.wireOp",EDGE,"E7.13.5"),sQuery(id+"F0.wireOp",EDGE,"E7.14.0"),sQuery(id+"F0.wireOp",EDGE,"E7.14.1"),sQuery(id+"F0.wireOp",EDGE,"E7.14.2"),sQuery(id+"F0.wireOp",EDGE,"E7.14.3"),sQuery(id+"F0.wireOp",EDGE,"E7.14.4"),sQuery(id+"F0.wireOp",EDGE,"E7.14.5"),sQuery(id+"F0.wireOp",EDGE,"E7.15.0"),sQuery(id+"F0.wireOp",EDGE,"E7.15.1"),sQuery(id+"F0.wireOp",EDGE,"E7.15.2"),sQuery(id+"F0.wireOp",EDGE,"E7.15.3"),sQuery(id+"F0.wireOp",EDGE,"E7.15.4"),sQuery(id+"F0.wireOp",EDGE,"E7.15.5"),sQuery(id+"F0.wireOp",EDGE,"E7.16.0"),sQuery(id+"F0.wireOp",EDGE,"E7.16.1"),sQuery(id+"F0.wireOp",EDGE,"E7.16.2"),sQuery(id+"F0.wireOp",EDGE,"E7.16.3"),sQuery(id+"F0.wireOp",EDGE,"E7.16.4"),sQuery(id+"F0.wireOp",EDGE,"E7.16.5"),sQuery(id+"F0.wireOp",EDGE,"E7.17.0"),sQuery(id+"F0.wireOp",EDGE,"E7.17.1"),sQuery(id+"F0.wireOp",EDGE,"E7.17.2"),sQuery(id+"F0.wireOp",EDGE,"E7.17.3"),sQuery(id+"F0.wireOp",EDGE,"E7.17.4"),sQuery(id+"F0.wireOp",EDGE,"E7.17.5"),sQuery(id+"F0.wireOp",EDGE,"E7.18.0"),sQuery(id+"F0.wireOp",EDGE,"E7.18.1"),sQuery(id+"F0.wireOp",EDGE,"E7.18.2"),sQuery(id+"F0.wireOp",EDGE,"E7.18.3"),sQuery(id+"F0.wireOp",EDGE,"E7.18.4"),sQuery(id+"F0.wireOp",EDGE,"E7.18.5"),sQuery(id+"F0.wireOp",EDGE,"E7.19.0"),sQuery(id+"F0.wireOp",EDGE,"E7.19.1"),sQuery(id+"F0.wireOp",EDGE,"E7.19.2"),sQuery(id+"F0.wireOp",EDGE,"E7.19.3"),sQuery(id+"F0.wireOp",EDGE,"E7.19.4"),sQuery(id+"F0.wireOp",EDGE,"E7.19.5"),sQuery(id+"F0.wireOp",EDGE,"E7.20.0"),sQuery(id+"F0.wireOp",EDGE,"E7.20.1"),sQuery(id+"F0.wireOp",EDGE,"E7.20.2"),sQuery(id+"F0.wireOp",EDGE,"E7.20.3"),sQuery(id+"F0.wireOp",EDGE,"E7.20.4"),sQuery(id+"F0.wireOp",EDGE,"E7.20.5"),sQuery(id+"F0.wireOp",EDGE,"E7.21.0"),sQuery(id+"F0.wireOp",EDGE,"E7.21.1"),sQuery(id+"F0.wireOp",EDGE,"E7.21.2"),sQuery(id+"F0.wireOp",EDGE,"E7.21.3"),sQuery(id+"F0.wireOp",EDGE,"E7.21.4"),sQuery(id+"F0.wireOp",EDGE,"E7.21.5"),sQuery(id+"F0.wireOp",EDGE,"E7.22.0"),sQuery(id+"F0.wireOp",EDGE,"E7.22.1"),sQuery(id+"F0.wireOp",EDGE,"E7.22.2"),sQuery(id+"F0.wireOp",EDGE,"E7.22.3"),sQuery(id+"F0.wireOp",EDGE,"E7.22.4"),sQuery(id+"F0.wireOp",EDGE,"E7.22.5"),sQuery(id+"F0.wireOp",EDGE,"E7.23.0"),sQuery(id+"F0.wireOp",EDGE,"E7.23.1"),sQuery(id+"F0.wireOp",EDGE,"E7.23.2"),sQuery(id+"F0.wireOp",EDGE,"E7.23.3"),sQuery(id+"F0.wireOp",EDGE,"E7.23.4"),sQuery(id+"F0.wireOp",EDGE,"E7.23.5"),sQuery(id+"F0.wireOp",EDGE,"E7.24.0"),sQuery(id+"F0.wireOp",EDGE,"E7.24.1"),sQuery(id+"F0.wireOp",EDGE,"E7.24.2"),sQuery(id+"F0.wireOp",EDGE,"E7.24.3"),sQuery(id+"F0.wireOp",EDGE,"E7.24.4"),sQuery(id+"F0.wireOp",EDGE,"E7.24.5"),sQuery(id+"F0.wireOp",EDGE,"E7.25.0"),sQuery(id+"F0.wireOp",EDGE,"E7.25.1"),sQuery(id+"F0.wireOp",EDGE,"E7.25.2"),sQuery(id+"F0.wireOp",EDGE,"E7.25.3"),sQuery(id+"F0.wireOp",EDGE,"E7.25.4"),sQuery(id+"F0.wireOp",EDGE,"E7.25.5"),sQuery(id+"F0.wireOp",EDGE,"E7.26.0"),sQuery(id+"F0.wireOp",EDGE,"E7.26.1"),sQuery(id+"F0.wireOp",EDGE,"E7.26.2"),sQuery(id+"F0.wireOp",EDGE,"E7.26.3"),sQuery(id+"F0.wireOp",EDGE,"E7.26.4"),sQuery(id+"F0.wireOp",EDGE,"E7.26.5"),sQuery(id+"F0.wireOp",EDGE,"E7.27.0"),sQuery(id+"F0.wireOp",EDGE,"E7.27.1"),sQuery(id+"F0.wireOp",EDGE,"E7.27.2"),sQuery(id+"F0.wireOp",EDGE,"E7.27.3"),sQuery(id+"F0.wireOp",EDGE,"E7.27.4"),sQuery(id+"F0.wireOp",EDGE,"E7.27.5"),sQuery(id+"F0.wireOp",EDGE,"E7.28.0"),sQuery(id+"F0.wireOp",EDGE,"E7.28.1"),sQuery(id+"F0.wireOp",EDGE,"E7.28.2"),sQuery(id+"F0.wireOp",EDGE,"E7.28.3"),sQuery(id+"F0.wireOp",EDGE,"E7.28.4"),sQuery(id+"F0.wireOp",EDGE,"E7.28.5"),sQuery(id+"F0.wireOp",EDGE,"E7.29.0"),sQuery(id+"F0.wireOp",EDGE,"E7.29.1"),sQuery(id+"F0.wireOp",EDGE,"E7.29.2"),sQuery(id+"F0.wireOp",EDGE,"E7.29.3"),sQuery(id+"F0.wireOp",EDGE,"E7.29.4"),sQuery(id+"F0.wireOp",EDGE,"E7.29.5"),sQuery(id+"F0.wireOp",EDGE,"E7.30.0"),sQuery(id+"F0.wireOp",EDGE,"E7.30.1"),sQuery(id+"F0.wireOp",EDGE,"E7.30.2"),sQuery(id+"F0.wireOp",EDGE,"E7.30.3"),sQuery(id+"F0.wireOp",EDGE,"E7.30.4"),sQuery(id+"F0.wireOp",EDGE,"E7.30.5"),sQuery(id+"F0.wireOp",EDGE,"E7.31.0"),sQuery(id+"F0.wireOp",EDGE,"E7.31.1"),sQuery(id+"F0.wireOp",EDGE,"E7.31.2"),sQuery(id+"F0.wireOp",EDGE,"E7.31.3"),sQuery(id+"F0.wireOp",EDGE,"E7.31.4"),sQuery(id+"F0.wireOp",EDGE,"E7.31.5"),sQuery(id+"F0.wireOp",EDGE,"E7.32.0"),sQuery(id+"F0.wireOp",EDGE,"E7.32.1"),sQuery(id+"F0.wireOp",EDGE,"E7.32.2"),sQuery(id+"F0.wireOp",EDGE,"E7.32.3"),sQuery(id+"F0.wireOp",EDGE,"E7.32.4"),sQuery(id+"F0.wireOp",EDGE,"E7.32.5"),sQuery(id+"F0.wireOp",EDGE,"E7.33.0"),sQuery(id+"F0.wireOp",EDGE,"E7.33.1"),sQuery(id+"F0.wireOp",EDGE,"E7.33.2"),sQuery(id+"F0.wireOp",EDGE,"E7.33.3"),sQuery(id+"F0.wireOp",EDGE,"E7.33.4"),sQuery(id+"F0.wireOp",EDGE,"E7.33.5"),sQuery(id+"F0.wireOp",EDGE,"E7.34.0"),sQuery(id+"F0.wireOp",EDGE,"E7.34.1"),sQuery(id+"F0.wireOp",EDGE,"E7.34.2"),sQuery(id+"F0.wireOp",EDGE,"E7.34.3"),sQuery(id+"F0.wireOp",EDGE,"E7.34.4"),sQuery(id+"F0.wireOp",EDGE,"E7.34.5"),sQuery(id+"F0.wireOp",EDGE,"E7.35.0"),sQuery(id+"F0.wireOp",EDGE,"E7.35.1"),sQuery(id+"F0.wireOp",EDGE,"E7.35.2"),sQuery(id+"F0.wireOp",EDGE,"E7.35.3"),sQuery(id+"F0.wireOp",EDGE,"E7.35.4"),sQuery(id+"F0.wireOp",EDGE,"E7.35.5"),sQuery(id+"F0.wireOp",EDGE,"E7.36.0"),sQuery(id+"F0.wireOp",EDGE,"E7.36.1"),sQuery(id+"F0.wireOp",EDGE,"E7.36.2"),sQuery(id+"F0.wireOp",EDGE,"E7.36.3"),sQuery(id+"F0.wireOp",EDGE,"E7.36.4"),sQuery(id+"F0.wireOp",EDGE,"E7.36.5"),sQuery(id+"F0.wireOp",EDGE,"E7.37.0"),sQuery(id+"F0.wireOp",EDGE,"E7.37.1"),sQuery(id+"F0.wireOp",EDGE,"E7.37.2"),sQuery(id+"F0.wireOp",EDGE,"E7.37.3"),sQuery(id+"F0.wireOp",EDGE,"E7.37.4"),sQuery(id+"F0.wireOp",EDGE,"E7.37.5"),sQuery(id+"F0.wireOp",EDGE,"E7.38.0"),sQuery(id+"F0.wireOp",EDGE,"E7.38.1"),sQuery(id+"F0.wireOp",EDGE,"E7.38.2"),sQuery(id+"F0.wireOp",EDGE,"E7.38.3"),sQuery(id+"F0.wireOp",EDGE,"E7.38.4"),sQuery(id+"F0.wireOp",EDGE,"E7.38.5"),sQuery(id+"F0.wireOp",EDGE,"E7.39.0"),sQuery(id+"F0.wireOp",EDGE,"E7.39.1"),sQuery(id+"F0.wireOp",EDGE,"E7.39.2"),sQuery(id+"F0.wireOp",EDGE,"E7.39.3"),sQuery(id+"F0.wireOp",EDGE,"E7.39.4"),sQuery(id+"F0.wireOp",EDGE,"E7.39.5"),sQuery(id+"F0.wireOp",EDGE,"E7.40.0"),sQuery(id+"F0.wireOp",EDGE,"E7.40.1"),sQuery(id+"F0.wireOp",EDGE,"E7.40.2"),sQuery(id+"F0.wireOp",EDGE,"E7.40.3"),sQuery(id+"F0.wireOp",EDGE,"E7.40.4"),sQuery(id+"F0.wireOp",EDGE,"E7.40.5"),sQuery(id+"F0.wireOp",EDGE,"E7.41.0"),sQuery(id+"F0.wireOp",EDGE,"E7.41.1"),sQuery(id+"F0.wireOp",EDGE,"E7.41.2"),sQuery(id+"F0.wireOp",EDGE,"E7.41.3"),sQuery(id+"F0.wireOp",EDGE,"E7.41.4"),sQuery(id+"F0.wireOp",EDGE,"E7.41.5"),sQuery(id+"F0.wireOp",EDGE,"E7.42.0"),sQuery(id+"F0.wireOp",EDGE,"E7.42.1"),sQuery(id+"F0.wireOp",EDGE,"E7.42.2"),sQuery(id+"F0.wireOp",EDGE,"E7.42.3"),sQuery(id+"F0.wireOp",EDGE,"E7.42.4"),sQuery(id+"F0.wireOp",EDGE,"E7.42.5"),sQuery(id+"F0.wireOp",EDGE,"E7.43.0"),sQuery(id+"F0.wireOp",EDGE,"E7.43.1"),sQuery(id+"F0.wireOp",EDGE,"E7.43.2"),sQuery(id+"F0.wireOp",EDGE,"E7.43.3"),sQuery(id+"F0.wireOp",EDGE,"E7.43.4"),sQuery(id+"F0.wireOp",EDGE,"E7.43.5")])],"isStart":false})],"blendedInto":[makeQuery(id+"F1.opExtrude","CAP_FACE",FACE,{"disambiguationData":[OSD([sQuery(id+"F0.wireOp",EDGE,"E1"),sQuery(id+"F0.wireOp",EDGE,"E2"),sQuery(id+"F0.wireOp",EDGE,"E3"),sQuery(id+"F0.wireOp",EDGE,"E4"),sQuery(id+"F0.wireOp",EDGE,"E5"),sQuery(id+"F0.wireOp",EDGE,"E6"),sQuery(id+"F0.wireOp",EDGE,"E7.1.0"),sQuery(id+"F0.wireOp",EDGE,"E7.1.1"),sQuery(id+"F0.wireOp",EDGE,"E7.1.2"),sQuery(id+"F0.wireOp",EDGE,"E7.1.3"),sQuery(id+"F0.wireOp",EDGE,"E7.1.4"),sQuery(id+"F0.wireOp",EDGE,"E7.1.5"),sQuery(id+"F0.wireOp",EDGE,"E7.2.0"),sQuery(id+"F0.wireOp",EDGE,"E7.2.1"),sQuery(id+"F0.wireOp",EDGE,"E7.2.2"),sQuery(id+"F0.wireOp",EDGE,"E7.2.3"),sQuery(id+"F0.wireOp",EDGE,"E7.2.4"),sQuery(id+"F0.wireOp",EDGE,"E7.2.5"),sQuery(id+"F0.wireOp",EDGE,"E7.3.0"),sQuery(id+"F0.wireOp",EDGE,"E7.3.1"),sQuery(id+"F0.wireOp",EDGE,"E7.3.2"),sQuery(id+"F0.wireOp",EDGE,"E7.3.3"),sQuery(id+"F0.wireOp",EDGE,"E7.3.4"),sQuery(id+"F0.wireOp",EDGE,"E7.3.5"),sQuery(id+"F0.wireOp",EDGE,"E7.4.0"),sQuery(id+"F0.wireOp",EDGE,"E7.4.1"),sQuery(id+"F0.wireOp",EDGE,"E7.4.2"),sQuery(id+"F0.wireOp",EDGE,"E7.4.3"),sQuery(id+"F0.wireOp",EDGE,"E7.4.4"),sQuery(id+"F0.wireOp",EDGE,"E7.4.5"),subQ0,sQuery(id+"F0.wireOp",EDGE,"E7.5.1"),sQuery(id+"F0.wireOp",EDGE,"E7.5.2"),sQuery(id+"F0.wireOp",EDGE,"E7.5.3"),sQuery(id+"F0.wireOp",EDGE,"E7.5.4"),sQuery(id+"F0.wireOp",EDGE,"E7.5.5"),sQuery(id+"F0.wireOp",EDGE,"E7.6.0"),sQuery(id+"F0.wireOp",EDGE,"E7.6.1"),sQuery(id+"F0.wireOp",EDGE,"E7.6.2"),sQuery(id+"F0.wireOp",EDGE,"E7.6.3"),sQuery(id+"F0.wireOp",EDGE,"E7.6.4"),sQuery(id+"F0.wireOp",EDGE,"E7.6.5"),sQuery(id+"F0.wireOp",EDGE,"E7.7.0"),sQuery(id+"F0.wireOp",EDGE,"E7.7.1"),sQuery(id+"F0.wireOp",EDGE,"E7.7.2"),sQuery(id+"F0.wireOp",EDGE,"E7.7.3"),sQuery(id+"F0.wireOp",EDGE,"E7.7.4"),sQuery(id+"F0.wireOp",EDGE,"E7.7.5"),sQuery(id+"F0.wireOp",EDGE,"E7.8.0"),sQuery(id+"F0.wireOp",EDGE,"E7.8.1"),sQuery(id+"F0.wireOp",EDGE,"E7.8.2"),sQuery(id+"F0.wireOp",EDGE,"E7.8.3"),sQuery(id+"F0.wireOp",EDGE,"E7.8.4"),sQuery(id+"F0.wireOp",EDGE,"E7.8.5"),sQuery(id+"F0.wireOp",EDGE,"E7.9.0"),sQuery(id+"F0.wireOp",EDGE,"E7.9.1"),sQuery(id+"F0.wireOp",EDGE,"E7.9.2"),sQuery(id+"F0.wireOp",EDGE,"E7.9.3"),sQuery(id+"F0.wireOp",EDGE,"E7.9.4"),sQuery(id+"F0.wireOp",EDGE,"E7.9.5"),sQuery(id+"F0.wireOp",EDGE,"E7.10.0"),sQuery(id+"F0.wireOp",EDGE,"E7.10.1"),sQuery(id+"F0.wireOp",EDGE,"E7.10.2"),sQuery(id+"F0.wireOp",EDGE,"E7.10.3"),sQuery(id+"F0.wireOp",EDGE,"E7.10.4"),sQuery(id+"F0.wireOp",EDGE,"E7.10.5"),sQuery(id+"F0.wireOp",EDGE,"E7.11.0"),sQuery(id+"F0.wireOp",EDGE,"E7.11.1"),sQuery(id+"F0.wireOp",EDGE,"E7.11.2"),sQuery(id+"F0.wireOp",EDGE,"E7.11.3"),sQuery(id+"F0.wireOp",EDGE,"E7.11.4"),sQuery(id+"F0.wireOp",EDGE,"E7.11.5"),sQuery(id+"F0.wireOp",EDGE,"E7.12.0"),sQuery(id+"F0.wireOp",EDGE,"E7.12.1"),sQuery(id+"F0.wireOp",EDGE,"E7.12.2"),sQuery(id+"F0.wireOp",EDGE,"E7.12.3"),sQuery(id+"F0.wireOp",EDGE,"E7.12.4"),sQuery(id+"F0.wireOp",EDGE,"E7.12.5"),sQuery(id+"F0.wireOp",EDGE,"E7.13.0"),sQuery(id+"F0.wireOp",EDGE,"E7.13.1"),sQuery(id+"F0.wireOp",EDGE,"E7.13.2"),sQuery(id+"F0.wireOp",EDGE,"E7.13.3"),sQuery(id+"F0.wireOp",EDGE,"E7.13.4"),sQuery(id+"F0.wireOp",EDGE,"E7.13.5"),sQuery(id+"F0.wireOp",EDGE,"E7.14.0"),sQuery(id+"F0.wireOp",EDGE,"E7.14.1"),sQuery(id+"F0.wireOp",EDGE,"E7.14.2"),sQuery(id+"F0.wireOp",EDGE,"E7.14.3"),sQuery(id+"F0.wireOp",EDGE,"E7.14.4"),sQuery(id+"F0.wireOp",EDGE,"E7.14.5"),sQuery(id+"F0.wireOp",EDGE,"E7.15.0"),sQuery(id+"F0.wireOp",EDGE,"E7.15.1"),sQuery(id+"F0.wireOp",EDGE,"E7.15.2"),sQuery(id+"F0.wireOp",EDGE,"E7.15.3"),sQuery(id+"F0.wireOp",EDGE,"E7.15.4"),sQuery(id+"F0.wireOp",EDGE,"E7.15.5"),sQuery(id+"F0.wireOp",EDGE,"E7.16.0"),sQuery(id+"F0.wireOp",EDGE,"E7.16.1"),sQuery(id+"F0.wireOp",EDGE,"E7.16.2"),sQuery(id+"F0.wireOp",EDGE,"E7.16.3"),sQuery(id+"F0.wireOp",EDGE,"E7.16.4"),sQuery(id+"F0.wireOp",EDGE,"E7.16.5"),sQuery(id+"F0.wireOp",EDGE,"E7.17.0"),sQuery(id+"F0.wireOp",EDGE,"E7.17.1"),sQuery(id+"F0.wireOp",EDGE,"E7.17.2"),sQuery(id+"F0.wireOp",EDGE,"E7.17.3"),sQuery(id+"F0.wireOp",EDGE,"E7.17.4"),sQuery(id+"F0.wireOp",EDGE,"E7.17.5"),sQuery(id+"F0.wireOp",EDGE,"E7.18.0"),sQuery(id+"F0.wireOp",EDGE,"E7.18.1"),sQuery(id+"F0.wireOp",EDGE,"E7.18.2"),sQuery(id+"F0.wireOp",EDGE,"E7.18.3"),sQuery(id+"F0.wireOp",EDGE,"E7.18.4"),sQuery(id+"F0.wireOp",EDGE,"E7.18.5"),sQuery(id+"F0.wireOp",EDGE,"E7.19.0"),sQuery(id+"F0.wireOp",EDGE,"E7.19.1"),sQuery(id+"F0.wireOp",EDGE,"E7.19.2"),sQuery(id+"F0.wireOp",EDGE,"E7.19.3"),sQuery(id+"F0.wireOp",EDGE,"E7.19.4"),sQuery(id+"F0.wireOp",EDGE,"E7.19.5"),sQuery(id+"F0.wireOp",EDGE,"E7.20.0"),sQuery(id+"F0.wireOp",EDGE,"E7.20.1"),sQuery(id+"F0.wireOp",EDGE,"E7.20.2"),sQuery(id+"F0.wireOp",EDGE,"E7.20.3"),sQuery(id+"F0.wireOp",EDGE,"E7.20.4"),sQuery(id+"F0.wireOp",EDGE,"E7.20.5"),sQuery(id+"F0.wireOp",EDGE,"E7.21.0"),sQuery(id+"F0.wireOp",EDGE,"E7.21.1"),sQuery(id+"F0.wireOp",EDGE,"E7.21.2"),sQuery(id+"F0.wireOp",EDGE,"E7.21.3"),sQuery(id+"F0.wireOp",EDGE,"E7.21.4"),sQuery(id+"F0.wireOp",EDGE,"E7.21.5"),sQuery(id+"F0.wireOp",EDGE,"E7.22.0"),sQuery(id+"F0.wireOp",EDGE,"E7.22.1"),sQuery(id+"F0.wireOp",EDGE,"E7.22.2"),sQuery(id+"F0.wireOp",EDGE,"E7.22.3"),sQuery(id+"F0.wireOp",EDGE,"E7.22.4"),sQuery(id+"F0.wireOp",EDGE,"E7.22.5"),sQuery(id+"F0.wireOp",EDGE,"E7.23.0"),sQuery(id+"F0.wireOp",EDGE,"E7.23.1"),sQuery(id+"F0.wireOp",EDGE,"E7.23.2"),sQuery(id+"F0.wireOp",EDGE,"E7.23.3"),sQuery(id+"F0.wireOp",EDGE,"E7.23.4"),sQuery(id+"F0.wireOp",EDGE,"E7.23.5"),sQuery(id+"F0.wireOp",EDGE,"E7.24.0"),sQuery(id+"F0.wireOp",EDGE,"E7.24.1"),sQuery(id+"F0.wireOp",EDGE,"E7.24.2"),sQuery(id+"F0.wireOp",EDGE,"E7.24.3"),sQuery(id+"F0.wireOp",EDGE,"E7.24.4"),sQuery(id+"F0.wireOp",EDGE,"E7.24.5"),sQuery(id+"F0.wireOp",EDGE,"E7.25.0"),sQuery(id+"F0.wireOp",EDGE,"E7.25.1"),sQuery(id+"F0.wireOp",EDGE,"E7.25.2"),sQuery(id+"F0.wireOp",EDGE,"E7.25.3"),sQuery(id+"F0.wireOp",EDGE,"E7.25.4"),sQuery(id+"F0.wireOp",EDGE,"E7.25.5"),sQuery(id+"F0.wireOp",EDGE,"E7.26.0"),sQuery(id+"F0.wireOp",EDGE,"E7.26.1"),sQuery(id+"F0.wireOp",EDGE,"E7.26.2"),sQuery(id+"F0.wireOp",EDGE,"E7.26.3"),sQuery(id+"F0.wireOp",EDGE,"E7.26.4"),sQuery(id+"F0.wireOp",EDGE,"E7.26.5"),sQuery(id+"F0.wireOp",EDGE,"E7.27.0"),sQuery(id+"F0.wireOp",EDGE,"E7.27.1"),sQuery(id+"F0.wireOp",EDGE,"E7.27.2"),sQuery(id+"F0.wireOp",EDGE,"E7.27.3"),sQuery(id+"F0.wireOp",EDGE,"E7.27.4"),sQuery(id+"F0.wireOp",EDGE,"E7.27.5"),sQuery(id+"F0.wireOp",EDGE,"E7.28.0"),sQuery(id+"F0.wireOp",EDGE,"E7.28.1"),sQuery(id+"F0.wireOp",EDGE,"E7.28.2"),sQuery(id+"F0.wireOp",EDGE,"E7.28.3"),sQuery(id+"F0.wireOp",EDGE,"E7.28.4"),sQuery(id+"F0.wireOp",EDGE,"E7.28.5"),sQuery(id+"F0.wireOp",EDGE,"E7.29.0"),sQuery(id+"F0.wireOp",EDGE,"E7.29.1"),sQuery(id+"F0.wireOp",EDGE,"E7.29.2"),sQuery(id+"F0.wireOp",EDGE,"E7.29.3"),sQuery(id+"F0.wireOp",EDGE,"E7.29.4"),sQuery(id+"F0.wireOp",EDGE,"E7.29.5"),sQuery(id+"F0.wireOp",EDGE,"E7.30.0"),sQuery(id+"F0.wireOp",EDGE,"E7.30.1"),sQuery(id+"F0.wireOp",EDGE,"E7.30.2"),sQuery(id+"F0.wireOp",EDGE,"E7.30.3"),sQuery(id+"F0.wireOp",EDGE,"E7.30.4"),sQuery(id+"F0.wireOp",EDGE,"E7.30.5"),sQuery(id+"F0.wireOp",EDGE,"E7.31.0"),sQuery(id+"F0.wireOp",EDGE,"E7.31.1"),sQuery(id+"F0.wireOp",EDGE,"E7.31.2"),sQuery(id+"F0.wireOp",EDGE,"E7.31.3"),sQuery(id+"F0.wireOp",EDGE,"E7.31.4"),sQuery(id+"F0.wireOp",EDGE,"E7.31.5"),sQuery(id+"F0.wireOp",EDGE,"E7.32.0"),sQuery(id+"F0.wireOp",EDGE,"E7.32.1"),sQuery(id+"F0.wireOp",EDGE,"E7.32.2"),sQuery(id+"F0.wireOp",EDGE,"E7.32.3"),sQuery(id+"F0.wireOp",EDGE,"E7.32.4"),sQuery(id+"F0.wireOp",EDGE,"E7.32.5"),sQuery(id+"F0.wireOp",EDGE,"E7.33.0"),sQuery(id+"F0.wireOp",EDGE,"E7.33.1"),sQuery(id+"F0.wireOp",EDGE,"E7.33.2"),sQuery(id+"F0.wireOp",EDGE,"E7.33.3"),sQuery(id+"F0.wireOp",EDGE,"E7.33.4"),sQuery(id+"F0.wireOp",EDGE,"E7.33.5"),sQuery(id+"F0.wireOp",EDGE,"E7.34.0"),sQuery(id+"F0.wireOp",EDGE,"E7.34.1"),sQuery(id+"F0.wireOp",EDGE,"E7.34.2"),sQuery(id+"F0.wireOp",EDGE,"E7.34.3"),sQuery(id+"F0.wireOp",EDGE,"E7.34.4"),sQuery(id+"F0.wireOp",EDGE,"E7.34.5"),sQuery(id+"F0.wireOp",EDGE,"E7.35.0"),sQuery(id+"F0.wireOp",EDGE,"E7.35.1"),sQuery(id+"F0.wireOp",EDGE,"E7.35.2"),sQuery(id+"F0.wireOp",EDGE,"E7.35.3"),sQuery(id+"F0.wireOp",EDGE,"E7.35.4"),sQuery(id+"F0.wireOp",EDGE,"E7.35.5"),sQuery(id+"F0.wireOp",EDGE,"E7.36.0"),sQuery(id+"F0.wireOp",EDGE,"E7.36.1"),sQuery(id+"F0.wireOp",EDGE,"E7.36.2"),sQuery(id+"F0.wireOp",EDGE,"E7.36.3"),sQuery(id+"F0.wireOp",EDGE,"E7.36.4"),sQuery(id+"F0.wireOp",EDGE,"E7.36.5"),sQuery(id+"F0.wireOp",EDGE,"E7.37.0"),sQuery(id+"F0.wireOp",EDGE,"E7.37.1"),sQuery(id+"F0.wireOp",EDGE,"E7.37.2"),sQuery(id+"F0.wireOp",EDGE,"E7.37.3"),sQuery(id+"F0.wireOp",EDGE,"E7.37.4"),sQuery(id+"F0.wireOp",EDGE,"E7.37.5"),sQuery(id+"F0.wireOp",EDGE,"E7.38.0"),sQuery(id+"F0.wireOp",EDGE,"E7.38.1"),sQuery(id+"F0.wireOp",EDGE,"E7.38.2"),sQuery(id+"F0.wireOp",EDGE,"E7.38.3"),sQuery(id+"F0.wireOp",EDGE,"E7.38.4"),sQuery(id+"F0.wireOp",EDGE,"E7.38.5"),sQuery(id+"F0.wireOp",EDGE,"E7.39.0"),sQuery(id+"F0.wireOp",EDGE,"E7.39.1"),sQuery(id+"F0.wireOp",EDGE,"E7.39.2"),sQuery(id+"F0.wireOp",EDGE,"E7.39.3"),sQuery(id+"F0.wireOp",EDGE,"E7.39.4"),sQuery(id+"F0.wireOp",EDGE,"E7.39.5"),sQuery(id+"F0.wireOp",EDGE,"E7.40.0"),sQuery(id+"F0.wireOp",EDGE,"E7.40.1"),sQuery(id+"F0.wireOp",EDGE,"E7.40.2"),sQuery(id+"F0.wireOp",EDGE,"E7.40.3"),sQuery(id+"F0.wireOp",EDGE,"E7.40.4"),sQuery(id+"F0.wireOp",EDGE,"E7.40.5"),sQuery(id+"F0.wireOp",EDGE,"E7.41.0"),sQuery(id+"F0.wireOp",EDGE,"E7.41.1"),sQuery(id+"F0.wireOp",EDGE,"E7.41.2"),sQuery(id+"F0.wireOp",EDGE,"E7.41.3"),sQuery(id+"F0.wireOp",EDGE,"E7.41.4"),sQuery(id+"F0.wireOp",EDGE,"E7.41.5"),sQuery(id+"F0.wireOp",EDGE,"E7.42.0"),sQuery(id+"F0.wireOp",EDGE,"E7.42.1"),sQuery(id+"F0.wireOp",EDGE,"E7.42.2"),sQuery(id+"F0.wireOp",EDGE,"E7.42.3"),sQuery(id+"F0.wireOp",EDGE,"E7.42.4"),sQuery(id+"F0.wireOp",EDGE,"E7.42.5"),sQuery(id+"F0.wireOp",EDGE,"E7.43.0"),sQuery(id+"F0.wireOp",EDGE,"E7.43.1"),sQuery(id+"F0.wireOp",EDGE,"E7.43.2"),sQuery(id+"F0.wireOp",EDGE,"E7.43.3"),sQuery(id+"F0.wireOp",EDGE,"E7.43.4"),sQuery(id+"F0.wireOp",EDGE,"E7.43.5")])],"isStart":false})]}),makeQuery(id+"F2.opChamfer","BLEND_FACE",FACE,{"disambiguationData":[OSD([subQ0])]})],"blendedInto":[makeQuery(id+"F2.opChamfer","BLEND_FACE",FACE,{"disambiguationData":[OSD([subQ0])]})]});}
            var Q21;
            {var subQ0=sQuery(id+"F0.wireOp",EDGE,"E7.3.0");Q21=makeQuery(id+"F8.opChamfer","BLEND_EDGE",EDGE,{"blendedFrom":[makeQuery(id+"F2.opChamfer","BLEND_EDGE",EDGE,{"blendedFrom":[makeQuery(id+"F1.opExtrude","CAP_EDGE",EDGE,{"disambiguationData":[OSD([subQ0])],"isStart":false}),makeQuery(id+"F1.opExtrude","CAP_FACE",FACE,{"disambiguationData":[OSD([sQuery(id+"F0.wireOp",EDGE,"E1"),sQuery(id+"F0.wireOp",EDGE,"E2"),sQuery(id+"F0.wireOp",EDGE,"E3"),sQuery(id+"F0.wireOp",EDGE,"E4"),sQuery(id+"F0.wireOp",EDGE,"E5"),sQuery(id+"F0.wireOp",EDGE,"E6"),sQuery(id+"F0.wireOp",EDGE,"E7.1.0"),sQuery(id+"F0.wireOp",EDGE,"E7.1.1"),sQuery(id+"F0.wireOp",EDGE,"E7.1.2"),sQuery(id+"F0.wireOp",EDGE,"E7.1.3"),sQuery(id+"F0.wireOp",EDGE,"E7.1.4"),sQuery(id+"F0.wireOp",EDGE,"E7.1.5"),sQuery(id+"F0.wireOp",EDGE,"E7.2.0"),sQuery(id+"F0.wireOp",EDGE,"E7.2.1"),sQuery(id+"F0.wireOp",EDGE,"E7.2.2"),sQuery(id+"F0.wireOp",EDGE,"E7.2.3"),sQuery(id+"F0.wireOp",EDGE,"E7.2.4"),sQuery(id+"F0.wireOp",EDGE,"E7.2.5"),subQ0,sQuery(id+"F0.wireOp",EDGE,"E7.3.1"),sQuery(id+"F0.wireOp",EDGE,"E7.3.2"),sQuery(id+"F0.wireOp",EDGE,"E7.3.3"),sQuery(id+"F0.wireOp",EDGE,"E7.3.4"),sQuery(id+"F0.wireOp",EDGE,"E7.3.5"),sQuery(id+"F0.wireOp",EDGE,"E7.4.0"),sQuery(id+"F0.wireOp",EDGE,"E7.4.1"),sQuery(id+"F0.wireOp",EDGE,"E7.4.2"),sQuery(id+"F0.wireOp",EDGE,"E7.4.3"),sQuery(id+"F0.wireOp",EDGE,"E7.4.4"),sQuery(id+"F0.wireOp",EDGE,"E7.4.5"),sQuery(id+"F0.wireOp",EDGE,"E7.5.0"),sQuery(id+"F0.wireOp",EDGE,"E7.5.1"),sQuery(id+"F0.wireOp",EDGE,"E7.5.2"),sQuery(id+"F0.wireOp",EDGE,"E7.5.3"),sQuery(id+"F0.wireOp",EDGE,"E7.5.4"),sQuery(id+"F0.wireOp",EDGE,"E7.5.5"),sQuery(id+"F0.wireOp",EDGE,"E7.6.0"),sQuery(id+"F0.wireOp",EDGE,"E7.6.1"),sQuery(id+"F0.wireOp",EDGE,"E7.6.2"),sQuery(id+"F0.wireOp",EDGE,"E7.6.3"),sQuery(id+"F0.wireOp",EDGE,"E7.6.4"),sQuery(id+"F0.wireOp",EDGE,"E7.6.5"),sQuery(id+"F0.wireOp",EDGE,"E7.7.0"),sQuery(id+"F0.wireOp",EDGE,"E7.7.1"),sQuery(id+"F0.wireOp",EDGE,"E7.7.2"),sQuery(id+"F0.wireOp",EDGE,"E7.7.3"),sQuery(id+"F0.wireOp",EDGE,"E7.7.4"),sQuery(id+"F0.wireOp",EDGE,"E7.7.5"),sQuery(id+"F0.wireOp",EDGE,"E7.8.0"),sQuery(id+"F0.wireOp",EDGE,"E7.8.1"),sQuery(id+"F0.wireOp",EDGE,"E7.8.2"),sQuery(id+"F0.wireOp",EDGE,"E7.8.3"),sQuery(id+"F0.wireOp",EDGE,"E7.8.4"),sQuery(id+"F0.wireOp",EDGE,"E7.8.5"),sQuery(id+"F0.wireOp",EDGE,"E7.9.0"),sQuery(id+"F0.wireOp",EDGE,"E7.9.1"),sQuery(id+"F0.wireOp",EDGE,"E7.9.2"),sQuery(id+"F0.wireOp",EDGE,"E7.9.3"),sQuery(id+"F0.wireOp",EDGE,"E7.9.4"),sQuery(id+"F0.wireOp",EDGE,"E7.9.5"),sQuery(id+"F0.wireOp",EDGE,"E7.10.0"),sQuery(id+"F0.wireOp",EDGE,"E7.10.1"),sQuery(id+"F0.wireOp",EDGE,"E7.10.2"),sQuery(id+"F0.wireOp",EDGE,"E7.10.3"),sQuery(id+"F0.wireOp",EDGE,"E7.10.4"),sQuery(id+"F0.wireOp",EDGE,"E7.10.5"),sQuery(id+"F0.wireOp",EDGE,"E7.11.0"),sQuery(id+"F0.wireOp",EDGE,"E7.11.1"),sQuery(id+"F0.wireOp",EDGE,"E7.11.2"),sQuery(id+"F0.wireOp",EDGE,"E7.11.3"),sQuery(id+"F0.wireOp",EDGE,"E7.11.4"),sQuery(id+"F0.wireOp",EDGE,"E7.11.5"),sQuery(id+"F0.wireOp",EDGE,"E7.12.0"),sQuery(id+"F0.wireOp",EDGE,"E7.12.1"),sQuery(id+"F0.wireOp",EDGE,"E7.12.2"),sQuery(id+"F0.wireOp",EDGE,"E7.12.3"),sQuery(id+"F0.wireOp",EDGE,"E7.12.4"),sQuery(id+"F0.wireOp",EDGE,"E7.12.5"),sQuery(id+"F0.wireOp",EDGE,"E7.13.0"),sQuery(id+"F0.wireOp",EDGE,"E7.13.1"),sQuery(id+"F0.wireOp",EDGE,"E7.13.2"),sQuery(id+"F0.wireOp",EDGE,"E7.13.3"),sQuery(id+"F0.wireOp",EDGE,"E7.13.4"),sQuery(id+"F0.wireOp",EDGE,"E7.13.5"),sQuery(id+"F0.wireOp",EDGE,"E7.14.0"),sQuery(id+"F0.wireOp",EDGE,"E7.14.1"),sQuery(id+"F0.wireOp",EDGE,"E7.14.2"),sQuery(id+"F0.wireOp",EDGE,"E7.14.3"),sQuery(id+"F0.wireOp",EDGE,"E7.14.4"),sQuery(id+"F0.wireOp",EDGE,"E7.14.5"),sQuery(id+"F0.wireOp",EDGE,"E7.15.0"),sQuery(id+"F0.wireOp",EDGE,"E7.15.1"),sQuery(id+"F0.wireOp",EDGE,"E7.15.2"),sQuery(id+"F0.wireOp",EDGE,"E7.15.3"),sQuery(id+"F0.wireOp",EDGE,"E7.15.4"),sQuery(id+"F0.wireOp",EDGE,"E7.15.5"),sQuery(id+"F0.wireOp",EDGE,"E7.16.0"),sQuery(id+"F0.wireOp",EDGE,"E7.16.1"),sQuery(id+"F0.wireOp",EDGE,"E7.16.2"),sQuery(id+"F0.wireOp",EDGE,"E7.16.3"),sQuery(id+"F0.wireOp",EDGE,"E7.16.4"),sQuery(id+"F0.wireOp",EDGE,"E7.16.5"),sQuery(id+"F0.wireOp",EDGE,"E7.17.0"),sQuery(id+"F0.wireOp",EDGE,"E7.17.1"),sQuery(id+"F0.wireOp",EDGE,"E7.17.2"),sQuery(id+"F0.wireOp",EDGE,"E7.17.3"),sQuery(id+"F0.wireOp",EDGE,"E7.17.4"),sQuery(id+"F0.wireOp",EDGE,"E7.17.5"),sQuery(id+"F0.wireOp",EDGE,"E7.18.0"),sQuery(id+"F0.wireOp",EDGE,"E7.18.1"),sQuery(id+"F0.wireOp",EDGE,"E7.18.2"),sQuery(id+"F0.wireOp",EDGE,"E7.18.3"),sQuery(id+"F0.wireOp",EDGE,"E7.18.4"),sQuery(id+"F0.wireOp",EDGE,"E7.18.5"),sQuery(id+"F0.wireOp",EDGE,"E7.19.0"),sQuery(id+"F0.wireOp",EDGE,"E7.19.1"),sQuery(id+"F0.wireOp",EDGE,"E7.19.2"),sQuery(id+"F0.wireOp",EDGE,"E7.19.3"),sQuery(id+"F0.wireOp",EDGE,"E7.19.4"),sQuery(id+"F0.wireOp",EDGE,"E7.19.5"),sQuery(id+"F0.wireOp",EDGE,"E7.20.0"),sQuery(id+"F0.wireOp",EDGE,"E7.20.1"),sQuery(id+"F0.wireOp",EDGE,"E7.20.2"),sQuery(id+"F0.wireOp",EDGE,"E7.20.3"),sQuery(id+"F0.wireOp",EDGE,"E7.20.4"),sQuery(id+"F0.wireOp",EDGE,"E7.20.5"),sQuery(id+"F0.wireOp",EDGE,"E7.21.0"),sQuery(id+"F0.wireOp",EDGE,"E7.21.1"),sQuery(id+"F0.wireOp",EDGE,"E7.21.2"),sQuery(id+"F0.wireOp",EDGE,"E7.21.3"),sQuery(id+"F0.wireOp",EDGE,"E7.21.4"),sQuery(id+"F0.wireOp",EDGE,"E7.21.5"),sQuery(id+"F0.wireOp",EDGE,"E7.22.0"),sQuery(id+"F0.wireOp",EDGE,"E7.22.1"),sQuery(id+"F0.wireOp",EDGE,"E7.22.2"),sQuery(id+"F0.wireOp",EDGE,"E7.22.3"),sQuery(id+"F0.wireOp",EDGE,"E7.22.4"),sQuery(id+"F0.wireOp",EDGE,"E7.22.5"),sQuery(id+"F0.wireOp",EDGE,"E7.23.0"),sQuery(id+"F0.wireOp",EDGE,"E7.23.1"),sQuery(id+"F0.wireOp",EDGE,"E7.23.2"),sQuery(id+"F0.wireOp",EDGE,"E7.23.3"),sQuery(id+"F0.wireOp",EDGE,"E7.23.4"),sQuery(id+"F0.wireOp",EDGE,"E7.23.5"),sQuery(id+"F0.wireOp",EDGE,"E7.24.0"),sQuery(id+"F0.wireOp",EDGE,"E7.24.1"),sQuery(id+"F0.wireOp",EDGE,"E7.24.2"),sQuery(id+"F0.wireOp",EDGE,"E7.24.3"),sQuery(id+"F0.wireOp",EDGE,"E7.24.4"),sQuery(id+"F0.wireOp",EDGE,"E7.24.5"),sQuery(id+"F0.wireOp",EDGE,"E7.25.0"),sQuery(id+"F0.wireOp",EDGE,"E7.25.1"),sQuery(id+"F0.wireOp",EDGE,"E7.25.2"),sQuery(id+"F0.wireOp",EDGE,"E7.25.3"),sQuery(id+"F0.wireOp",EDGE,"E7.25.4"),sQuery(id+"F0.wireOp",EDGE,"E7.25.5"),sQuery(id+"F0.wireOp",EDGE,"E7.26.0"),sQuery(id+"F0.wireOp",EDGE,"E7.26.1"),sQuery(id+"F0.wireOp",EDGE,"E7.26.2"),sQuery(id+"F0.wireOp",EDGE,"E7.26.3"),sQuery(id+"F0.wireOp",EDGE,"E7.26.4"),sQuery(id+"F0.wireOp",EDGE,"E7.26.5"),sQuery(id+"F0.wireOp",EDGE,"E7.27.0"),sQuery(id+"F0.wireOp",EDGE,"E7.27.1"),sQuery(id+"F0.wireOp",EDGE,"E7.27.2"),sQuery(id+"F0.wireOp",EDGE,"E7.27.3"),sQuery(id+"F0.wireOp",EDGE,"E7.27.4"),sQuery(id+"F0.wireOp",EDGE,"E7.27.5"),sQuery(id+"F0.wireOp",EDGE,"E7.28.0"),sQuery(id+"F0.wireOp",EDGE,"E7.28.1"),sQuery(id+"F0.wireOp",EDGE,"E7.28.2"),sQuery(id+"F0.wireOp",EDGE,"E7.28.3"),sQuery(id+"F0.wireOp",EDGE,"E7.28.4"),sQuery(id+"F0.wireOp",EDGE,"E7.28.5"),sQuery(id+"F0.wireOp",EDGE,"E7.29.0"),sQuery(id+"F0.wireOp",EDGE,"E7.29.1"),sQuery(id+"F0.wireOp",EDGE,"E7.29.2"),sQuery(id+"F0.wireOp",EDGE,"E7.29.3"),sQuery(id+"F0.wireOp",EDGE,"E7.29.4"),sQuery(id+"F0.wireOp",EDGE,"E7.29.5"),sQuery(id+"F0.wireOp",EDGE,"E7.30.0"),sQuery(id+"F0.wireOp",EDGE,"E7.30.1"),sQuery(id+"F0.wireOp",EDGE,"E7.30.2"),sQuery(id+"F0.wireOp",EDGE,"E7.30.3"),sQuery(id+"F0.wireOp",EDGE,"E7.30.4"),sQuery(id+"F0.wireOp",EDGE,"E7.30.5"),sQuery(id+"F0.wireOp",EDGE,"E7.31.0"),sQuery(id+"F0.wireOp",EDGE,"E7.31.1"),sQuery(id+"F0.wireOp",EDGE,"E7.31.2"),sQuery(id+"F0.wireOp",EDGE,"E7.31.3"),sQuery(id+"F0.wireOp",EDGE,"E7.31.4"),sQuery(id+"F0.wireOp",EDGE,"E7.31.5"),sQuery(id+"F0.wireOp",EDGE,"E7.32.0"),sQuery(id+"F0.wireOp",EDGE,"E7.32.1"),sQuery(id+"F0.wireOp",EDGE,"E7.32.2"),sQuery(id+"F0.wireOp",EDGE,"E7.32.3"),sQuery(id+"F0.wireOp",EDGE,"E7.32.4"),sQuery(id+"F0.wireOp",EDGE,"E7.32.5"),sQuery(id+"F0.wireOp",EDGE,"E7.33.0"),sQuery(id+"F0.wireOp",EDGE,"E7.33.1"),sQuery(id+"F0.wireOp",EDGE,"E7.33.2"),sQuery(id+"F0.wireOp",EDGE,"E7.33.3"),sQuery(id+"F0.wireOp",EDGE,"E7.33.4"),sQuery(id+"F0.wireOp",EDGE,"E7.33.5"),sQuery(id+"F0.wireOp",EDGE,"E7.34.0"),sQuery(id+"F0.wireOp",EDGE,"E7.34.1"),sQuery(id+"F0.wireOp",EDGE,"E7.34.2"),sQuery(id+"F0.wireOp",EDGE,"E7.34.3"),sQuery(id+"F0.wireOp",EDGE,"E7.34.4"),sQuery(id+"F0.wireOp",EDGE,"E7.34.5"),sQuery(id+"F0.wireOp",EDGE,"E7.35.0"),sQuery(id+"F0.wireOp",EDGE,"E7.35.1"),sQuery(id+"F0.wireOp",EDGE,"E7.35.2"),sQuery(id+"F0.wireOp",EDGE,"E7.35.3"),sQuery(id+"F0.wireOp",EDGE,"E7.35.4"),sQuery(id+"F0.wireOp",EDGE,"E7.35.5"),sQuery(id+"F0.wireOp",EDGE,"E7.36.0"),sQuery(id+"F0.wireOp",EDGE,"E7.36.1"),sQuery(id+"F0.wireOp",EDGE,"E7.36.2"),sQuery(id+"F0.wireOp",EDGE,"E7.36.3"),sQuery(id+"F0.wireOp",EDGE,"E7.36.4"),sQuery(id+"F0.wireOp",EDGE,"E7.36.5"),sQuery(id+"F0.wireOp",EDGE,"E7.37.0"),sQuery(id+"F0.wireOp",EDGE,"E7.37.1"),sQuery(id+"F0.wireOp",EDGE,"E7.37.2"),sQuery(id+"F0.wireOp",EDGE,"E7.37.3"),sQuery(id+"F0.wireOp",EDGE,"E7.37.4"),sQuery(id+"F0.wireOp",EDGE,"E7.37.5"),sQuery(id+"F0.wireOp",EDGE,"E7.38.0"),sQuery(id+"F0.wireOp",EDGE,"E7.38.1"),sQuery(id+"F0.wireOp",EDGE,"E7.38.2"),sQuery(id+"F0.wireOp",EDGE,"E7.38.3"),sQuery(id+"F0.wireOp",EDGE,"E7.38.4"),sQuery(id+"F0.wireOp",EDGE,"E7.38.5"),sQuery(id+"F0.wireOp",EDGE,"E7.39.0"),sQuery(id+"F0.wireOp",EDGE,"E7.39.1"),sQuery(id+"F0.wireOp",EDGE,"E7.39.2"),sQuery(id+"F0.wireOp",EDGE,"E7.39.3"),sQuery(id+"F0.wireOp",EDGE,"E7.39.4"),sQuery(id+"F0.wireOp",EDGE,"E7.39.5"),sQuery(id+"F0.wireOp",EDGE,"E7.40.0"),sQuery(id+"F0.wireOp",EDGE,"E7.40.1"),sQuery(id+"F0.wireOp",EDGE,"E7.40.2"),sQuery(id+"F0.wireOp",EDGE,"E7.40.3"),sQuery(id+"F0.wireOp",EDGE,"E7.40.4"),sQuery(id+"F0.wireOp",EDGE,"E7.40.5"),sQuery(id+"F0.wireOp",EDGE,"E7.41.0"),sQuery(id+"F0.wireOp",EDGE,"E7.41.1"),sQuery(id+"F0.wireOp",EDGE,"E7.41.2"),sQuery(id+"F0.wireOp",EDGE,"E7.41.3"),sQuery(id+"F0.wireOp",EDGE,"E7.41.4"),sQuery(id+"F0.wireOp",EDGE,"E7.41.5"),sQuery(id+"F0.wireOp",EDGE,"E7.42.0"),sQuery(id+"F0.wireOp",EDGE,"E7.42.1"),sQuery(id+"F0.wireOp",EDGE,"E7.42.2"),sQuery(id+"F0.wireOp",EDGE,"E7.42.3"),sQuery(id+"F0.wireOp",EDGE,"E7.42.4"),sQuery(id+"F0.wireOp",EDGE,"E7.42.5"),sQuery(id+"F0.wireOp",EDGE,"E7.43.0"),sQuery(id+"F0.wireOp",EDGE,"E7.43.1"),sQuery(id+"F0.wireOp",EDGE,"E7.43.2"),sQuery(id+"F0.wireOp",EDGE,"E7.43.3"),sQuery(id+"F0.wireOp",EDGE,"E7.43.4"),sQuery(id+"F0.wireOp",EDGE,"E7.43.5")])],"isStart":false})],"blendedInto":[makeQuery(id+"F1.opExtrude","CAP_FACE",FACE,{"disambiguationData":[OSD([sQuery(id+"F0.wireOp",EDGE,"E1"),sQuery(id+"F0.wireOp",EDGE,"E2"),sQuery(id+"F0.wireOp",EDGE,"E3"),sQuery(id+"F0.wireOp",EDGE,"E4"),sQuery(id+"F0.wireOp",EDGE,"E5"),sQuery(id+"F0.wireOp",EDGE,"E6"),sQuery(id+"F0.wireOp",EDGE,"E7.1.0"),sQuery(id+"F0.wireOp",EDGE,"E7.1.1"),sQuery(id+"F0.wireOp",EDGE,"E7.1.2"),sQuery(id+"F0.wireOp",EDGE,"E7.1.3"),sQuery(id+"F0.wireOp",EDGE,"E7.1.4"),sQuery(id+"F0.wireOp",EDGE,"E7.1.5"),sQuery(id+"F0.wireOp",EDGE,"E7.2.0"),sQuery(id+"F0.wireOp",EDGE,"E7.2.1"),sQuery(id+"F0.wireOp",EDGE,"E7.2.2"),sQuery(id+"F0.wireOp",EDGE,"E7.2.3"),sQuery(id+"F0.wireOp",EDGE,"E7.2.4"),sQuery(id+"F0.wireOp",EDGE,"E7.2.5"),subQ0,sQuery(id+"F0.wireOp",EDGE,"E7.3.1"),sQuery(id+"F0.wireOp",EDGE,"E7.3.2"),sQuery(id+"F0.wireOp",EDGE,"E7.3.3"),sQuery(id+"F0.wireOp",EDGE,"E7.3.4"),sQuery(id+"F0.wireOp",EDGE,"E7.3.5"),sQuery(id+"F0.wireOp",EDGE,"E7.4.0"),sQuery(id+"F0.wireOp",EDGE,"E7.4.1"),sQuery(id+"F0.wireOp",EDGE,"E7.4.2"),sQuery(id+"F0.wireOp",EDGE,"E7.4.3"),sQuery(id+"F0.wireOp",EDGE,"E7.4.4"),sQuery(id+"F0.wireOp",EDGE,"E7.4.5"),sQuery(id+"F0.wireOp",EDGE,"E7.5.0"),sQuery(id+"F0.wireOp",EDGE,"E7.5.1"),sQuery(id+"F0.wireOp",EDGE,"E7.5.2"),sQuery(id+"F0.wireOp",EDGE,"E7.5.3"),sQuery(id+"F0.wireOp",EDGE,"E7.5.4"),sQuery(id+"F0.wireOp",EDGE,"E7.5.5"),sQuery(id+"F0.wireOp",EDGE,"E7.6.0"),sQuery(id+"F0.wireOp",EDGE,"E7.6.1"),sQuery(id+"F0.wireOp",EDGE,"E7.6.2"),sQuery(id+"F0.wireOp",EDGE,"E7.6.3"),sQuery(id+"F0.wireOp",EDGE,"E7.6.4"),sQuery(id+"F0.wireOp",EDGE,"E7.6.5"),sQuery(id+"F0.wireOp",EDGE,"E7.7.0"),sQuery(id+"F0.wireOp",EDGE,"E7.7.1"),sQuery(id+"F0.wireOp",EDGE,"E7.7.2"),sQuery(id+"F0.wireOp",EDGE,"E7.7.3"),sQuery(id+"F0.wireOp",EDGE,"E7.7.4"),sQuery(id+"F0.wireOp",EDGE,"E7.7.5"),sQuery(id+"F0.wireOp",EDGE,"E7.8.0"),sQuery(id+"F0.wireOp",EDGE,"E7.8.1"),sQuery(id+"F0.wireOp",EDGE,"E7.8.2"),sQuery(id+"F0.wireOp",EDGE,"E7.8.3"),sQuery(id+"F0.wireOp",EDGE,"E7.8.4"),sQuery(id+"F0.wireOp",EDGE,"E7.8.5"),sQuery(id+"F0.wireOp",EDGE,"E7.9.0"),sQuery(id+"F0.wireOp",EDGE,"E7.9.1"),sQuery(id+"F0.wireOp",EDGE,"E7.9.2"),sQuery(id+"F0.wireOp",EDGE,"E7.9.3"),sQuery(id+"F0.wireOp",EDGE,"E7.9.4"),sQuery(id+"F0.wireOp",EDGE,"E7.9.5"),sQuery(id+"F0.wireOp",EDGE,"E7.10.0"),sQuery(id+"F0.wireOp",EDGE,"E7.10.1"),sQuery(id+"F0.wireOp",EDGE,"E7.10.2"),sQuery(id+"F0.wireOp",EDGE,"E7.10.3"),sQuery(id+"F0.wireOp",EDGE,"E7.10.4"),sQuery(id+"F0.wireOp",EDGE,"E7.10.5"),sQuery(id+"F0.wireOp",EDGE,"E7.11.0"),sQuery(id+"F0.wireOp",EDGE,"E7.11.1"),sQuery(id+"F0.wireOp",EDGE,"E7.11.2"),sQuery(id+"F0.wireOp",EDGE,"E7.11.3"),sQuery(id+"F0.wireOp",EDGE,"E7.11.4"),sQuery(id+"F0.wireOp",EDGE,"E7.11.5"),sQuery(id+"F0.wireOp",EDGE,"E7.12.0"),sQuery(id+"F0.wireOp",EDGE,"E7.12.1"),sQuery(id+"F0.wireOp",EDGE,"E7.12.2"),sQuery(id+"F0.wireOp",EDGE,"E7.12.3"),sQuery(id+"F0.wireOp",EDGE,"E7.12.4"),sQuery(id+"F0.wireOp",EDGE,"E7.12.5"),sQuery(id+"F0.wireOp",EDGE,"E7.13.0"),sQuery(id+"F0.wireOp",EDGE,"E7.13.1"),sQuery(id+"F0.wireOp",EDGE,"E7.13.2"),sQuery(id+"F0.wireOp",EDGE,"E7.13.3"),sQuery(id+"F0.wireOp",EDGE,"E7.13.4"),sQuery(id+"F0.wireOp",EDGE,"E7.13.5"),sQuery(id+"F0.wireOp",EDGE,"E7.14.0"),sQuery(id+"F0.wireOp",EDGE,"E7.14.1"),sQuery(id+"F0.wireOp",EDGE,"E7.14.2"),sQuery(id+"F0.wireOp",EDGE,"E7.14.3"),sQuery(id+"F0.wireOp",EDGE,"E7.14.4"),sQuery(id+"F0.wireOp",EDGE,"E7.14.5"),sQuery(id+"F0.wireOp",EDGE,"E7.15.0"),sQuery(id+"F0.wireOp",EDGE,"E7.15.1"),sQuery(id+"F0.wireOp",EDGE,"E7.15.2"),sQuery(id+"F0.wireOp",EDGE,"E7.15.3"),sQuery(id+"F0.wireOp",EDGE,"E7.15.4"),sQuery(id+"F0.wireOp",EDGE,"E7.15.5"),sQuery(id+"F0.wireOp",EDGE,"E7.16.0"),sQuery(id+"F0.wireOp",EDGE,"E7.16.1"),sQuery(id+"F0.wireOp",EDGE,"E7.16.2"),sQuery(id+"F0.wireOp",EDGE,"E7.16.3"),sQuery(id+"F0.wireOp",EDGE,"E7.16.4"),sQuery(id+"F0.wireOp",EDGE,"E7.16.5"),sQuery(id+"F0.wireOp",EDGE,"E7.17.0"),sQuery(id+"F0.wireOp",EDGE,"E7.17.1"),sQuery(id+"F0.wireOp",EDGE,"E7.17.2"),sQuery(id+"F0.wireOp",EDGE,"E7.17.3"),sQuery(id+"F0.wireOp",EDGE,"E7.17.4"),sQuery(id+"F0.wireOp",EDGE,"E7.17.5"),sQuery(id+"F0.wireOp",EDGE,"E7.18.0"),sQuery(id+"F0.wireOp",EDGE,"E7.18.1"),sQuery(id+"F0.wireOp",EDGE,"E7.18.2"),sQuery(id+"F0.wireOp",EDGE,"E7.18.3"),sQuery(id+"F0.wireOp",EDGE,"E7.18.4"),sQuery(id+"F0.wireOp",EDGE,"E7.18.5"),sQuery(id+"F0.wireOp",EDGE,"E7.19.0"),sQuery(id+"F0.wireOp",EDGE,"E7.19.1"),sQuery(id+"F0.wireOp",EDGE,"E7.19.2"),sQuery(id+"F0.wireOp",EDGE,"E7.19.3"),sQuery(id+"F0.wireOp",EDGE,"E7.19.4"),sQuery(id+"F0.wireOp",EDGE,"E7.19.5"),sQuery(id+"F0.wireOp",EDGE,"E7.20.0"),sQuery(id+"F0.wireOp",EDGE,"E7.20.1"),sQuery(id+"F0.wireOp",EDGE,"E7.20.2"),sQuery(id+"F0.wireOp",EDGE,"E7.20.3"),sQuery(id+"F0.wireOp",EDGE,"E7.20.4"),sQuery(id+"F0.wireOp",EDGE,"E7.20.5"),sQuery(id+"F0.wireOp",EDGE,"E7.21.0"),sQuery(id+"F0.wireOp",EDGE,"E7.21.1"),sQuery(id+"F0.wireOp",EDGE,"E7.21.2"),sQuery(id+"F0.wireOp",EDGE,"E7.21.3"),sQuery(id+"F0.wireOp",EDGE,"E7.21.4"),sQuery(id+"F0.wireOp",EDGE,"E7.21.5"),sQuery(id+"F0.wireOp",EDGE,"E7.22.0"),sQuery(id+"F0.wireOp",EDGE,"E7.22.1"),sQuery(id+"F0.wireOp",EDGE,"E7.22.2"),sQuery(id+"F0.wireOp",EDGE,"E7.22.3"),sQuery(id+"F0.wireOp",EDGE,"E7.22.4"),sQuery(id+"F0.wireOp",EDGE,"E7.22.5"),sQuery(id+"F0.wireOp",EDGE,"E7.23.0"),sQuery(id+"F0.wireOp",EDGE,"E7.23.1"),sQuery(id+"F0.wireOp",EDGE,"E7.23.2"),sQuery(id+"F0.wireOp",EDGE,"E7.23.3"),sQuery(id+"F0.wireOp",EDGE,"E7.23.4"),sQuery(id+"F0.wireOp",EDGE,"E7.23.5"),sQuery(id+"F0.wireOp",EDGE,"E7.24.0"),sQuery(id+"F0.wireOp",EDGE,"E7.24.1"),sQuery(id+"F0.wireOp",EDGE,"E7.24.2"),sQuery(id+"F0.wireOp",EDGE,"E7.24.3"),sQuery(id+"F0.wireOp",EDGE,"E7.24.4"),sQuery(id+"F0.wireOp",EDGE,"E7.24.5"),sQuery(id+"F0.wireOp",EDGE,"E7.25.0"),sQuery(id+"F0.wireOp",EDGE,"E7.25.1"),sQuery(id+"F0.wireOp",EDGE,"E7.25.2"),sQuery(id+"F0.wireOp",EDGE,"E7.25.3"),sQuery(id+"F0.wireOp",EDGE,"E7.25.4"),sQuery(id+"F0.wireOp",EDGE,"E7.25.5"),sQuery(id+"F0.wireOp",EDGE,"E7.26.0"),sQuery(id+"F0.wireOp",EDGE,"E7.26.1"),sQuery(id+"F0.wireOp",EDGE,"E7.26.2"),sQuery(id+"F0.wireOp",EDGE,"E7.26.3"),sQuery(id+"F0.wireOp",EDGE,"E7.26.4"),sQuery(id+"F0.wireOp",EDGE,"E7.26.5"),sQuery(id+"F0.wireOp",EDGE,"E7.27.0"),sQuery(id+"F0.wireOp",EDGE,"E7.27.1"),sQuery(id+"F0.wireOp",EDGE,"E7.27.2"),sQuery(id+"F0.wireOp",EDGE,"E7.27.3"),sQuery(id+"F0.wireOp",EDGE,"E7.27.4"),sQuery(id+"F0.wireOp",EDGE,"E7.27.5"),sQuery(id+"F0.wireOp",EDGE,"E7.28.0"),sQuery(id+"F0.wireOp",EDGE,"E7.28.1"),sQuery(id+"F0.wireOp",EDGE,"E7.28.2"),sQuery(id+"F0.wireOp",EDGE,"E7.28.3"),sQuery(id+"F0.wireOp",EDGE,"E7.28.4"),sQuery(id+"F0.wireOp",EDGE,"E7.28.5"),sQuery(id+"F0.wireOp",EDGE,"E7.29.0"),sQuery(id+"F0.wireOp",EDGE,"E7.29.1"),sQuery(id+"F0.wireOp",EDGE,"E7.29.2"),sQuery(id+"F0.wireOp",EDGE,"E7.29.3"),sQuery(id+"F0.wireOp",EDGE,"E7.29.4"),sQuery(id+"F0.wireOp",EDGE,"E7.29.5"),sQuery(id+"F0.wireOp",EDGE,"E7.30.0"),sQuery(id+"F0.wireOp",EDGE,"E7.30.1"),sQuery(id+"F0.wireOp",EDGE,"E7.30.2"),sQuery(id+"F0.wireOp",EDGE,"E7.30.3"),sQuery(id+"F0.wireOp",EDGE,"E7.30.4"),sQuery(id+"F0.wireOp",EDGE,"E7.30.5"),sQuery(id+"F0.wireOp",EDGE,"E7.31.0"),sQuery(id+"F0.wireOp",EDGE,"E7.31.1"),sQuery(id+"F0.wireOp",EDGE,"E7.31.2"),sQuery(id+"F0.wireOp",EDGE,"E7.31.3"),sQuery(id+"F0.wireOp",EDGE,"E7.31.4"),sQuery(id+"F0.wireOp",EDGE,"E7.31.5"),sQuery(id+"F0.wireOp",EDGE,"E7.32.0"),sQuery(id+"F0.wireOp",EDGE,"E7.32.1"),sQuery(id+"F0.wireOp",EDGE,"E7.32.2"),sQuery(id+"F0.wireOp",EDGE,"E7.32.3"),sQuery(id+"F0.wireOp",EDGE,"E7.32.4"),sQuery(id+"F0.wireOp",EDGE,"E7.32.5"),sQuery(id+"F0.wireOp",EDGE,"E7.33.0"),sQuery(id+"F0.wireOp",EDGE,"E7.33.1"),sQuery(id+"F0.wireOp",EDGE,"E7.33.2"),sQuery(id+"F0.wireOp",EDGE,"E7.33.3"),sQuery(id+"F0.wireOp",EDGE,"E7.33.4"),sQuery(id+"F0.wireOp",EDGE,"E7.33.5"),sQuery(id+"F0.wireOp",EDGE,"E7.34.0"),sQuery(id+"F0.wireOp",EDGE,"E7.34.1"),sQuery(id+"F0.wireOp",EDGE,"E7.34.2"),sQuery(id+"F0.wireOp",EDGE,"E7.34.3"),sQuery(id+"F0.wireOp",EDGE,"E7.34.4"),sQuery(id+"F0.wireOp",EDGE,"E7.34.5"),sQuery(id+"F0.wireOp",EDGE,"E7.35.0"),sQuery(id+"F0.wireOp",EDGE,"E7.35.1"),sQuery(id+"F0.wireOp",EDGE,"E7.35.2"),sQuery(id+"F0.wireOp",EDGE,"E7.35.3"),sQuery(id+"F0.wireOp",EDGE,"E7.35.4"),sQuery(id+"F0.wireOp",EDGE,"E7.35.5"),sQuery(id+"F0.wireOp",EDGE,"E7.36.0"),sQuery(id+"F0.wireOp",EDGE,"E7.36.1"),sQuery(id+"F0.wireOp",EDGE,"E7.36.2"),sQuery(id+"F0.wireOp",EDGE,"E7.36.3"),sQuery(id+"F0.wireOp",EDGE,"E7.36.4"),sQuery(id+"F0.wireOp",EDGE,"E7.36.5"),sQuery(id+"F0.wireOp",EDGE,"E7.37.0"),sQuery(id+"F0.wireOp",EDGE,"E7.37.1"),sQuery(id+"F0.wireOp",EDGE,"E7.37.2"),sQuery(id+"F0.wireOp",EDGE,"E7.37.3"),sQuery(id+"F0.wireOp",EDGE,"E7.37.4"),sQuery(id+"F0.wireOp",EDGE,"E7.37.5"),sQuery(id+"F0.wireOp",EDGE,"E7.38.0"),sQuery(id+"F0.wireOp",EDGE,"E7.38.1"),sQuery(id+"F0.wireOp",EDGE,"E7.38.2"),sQuery(id+"F0.wireOp",EDGE,"E7.38.3"),sQuery(id+"F0.wireOp",EDGE,"E7.38.4"),sQuery(id+"F0.wireOp",EDGE,"E7.38.5"),sQuery(id+"F0.wireOp",EDGE,"E7.39.0"),sQuery(id+"F0.wireOp",EDGE,"E7.39.1"),sQuery(id+"F0.wireOp",EDGE,"E7.39.2"),sQuery(id+"F0.wireOp",EDGE,"E7.39.3"),sQuery(id+"F0.wireOp",EDGE,"E7.39.4"),sQuery(id+"F0.wireOp",EDGE,"E7.39.5"),sQuery(id+"F0.wireOp",EDGE,"E7.40.0"),sQuery(id+"F0.wireOp",EDGE,"E7.40.1"),sQuery(id+"F0.wireOp",EDGE,"E7.40.2"),sQuery(id+"F0.wireOp",EDGE,"E7.40.3"),sQuery(id+"F0.wireOp",EDGE,"E7.40.4"),sQuery(id+"F0.wireOp",EDGE,"E7.40.5"),sQuery(id+"F0.wireOp",EDGE,"E7.41.0"),sQuery(id+"F0.wireOp",EDGE,"E7.41.1"),sQuery(id+"F0.wireOp",EDGE,"E7.41.2"),sQuery(id+"F0.wireOp",EDGE,"E7.41.3"),sQuery(id+"F0.wireOp",EDGE,"E7.41.4"),sQuery(id+"F0.wireOp",EDGE,"E7.41.5"),sQuery(id+"F0.wireOp",EDGE,"E7.42.0"),sQuery(id+"F0.wireOp",EDGE,"E7.42.1"),sQuery(id+"F0.wireOp",EDGE,"E7.42.2"),sQuery(id+"F0.wireOp",EDGE,"E7.42.3"),sQuery(id+"F0.wireOp",EDGE,"E7.42.4"),sQuery(id+"F0.wireOp",EDGE,"E7.42.5"),sQuery(id+"F0.wireOp",EDGE,"E7.43.0"),sQuery(id+"F0.wireOp",EDGE,"E7.43.1"),sQuery(id+"F0.wireOp",EDGE,"E7.43.2"),sQuery(id+"F0.wireOp",EDGE,"E7.43.3"),sQuery(id+"F0.wireOp",EDGE,"E7.43.4"),sQuery(id+"F0.wireOp",EDGE,"E7.43.5")])],"isStart":false})]}),makeQuery(id+"F2.opChamfer","BLEND_FACE",FACE,{"disambiguationData":[OSD([subQ0])]})],"blendedInto":[makeQuery(id+"F2.opChamfer","BLEND_FACE",FACE,{"disambiguationData":[OSD([subQ0])]})]});}
            fillet(context, id + "F9", {"entities" : qUnion([Q0, Q1, Q2, Q3, Q4, Q5, Q6, Q7, Q8, Q9, Q10, Q11, Q12, Q13, Q14, Q15, Q16, Q17, Q18, Q19, Q20, Q21]), "radius" : 0.51 * mm, "allowEdgeOverflow" : false});
        }
    });
